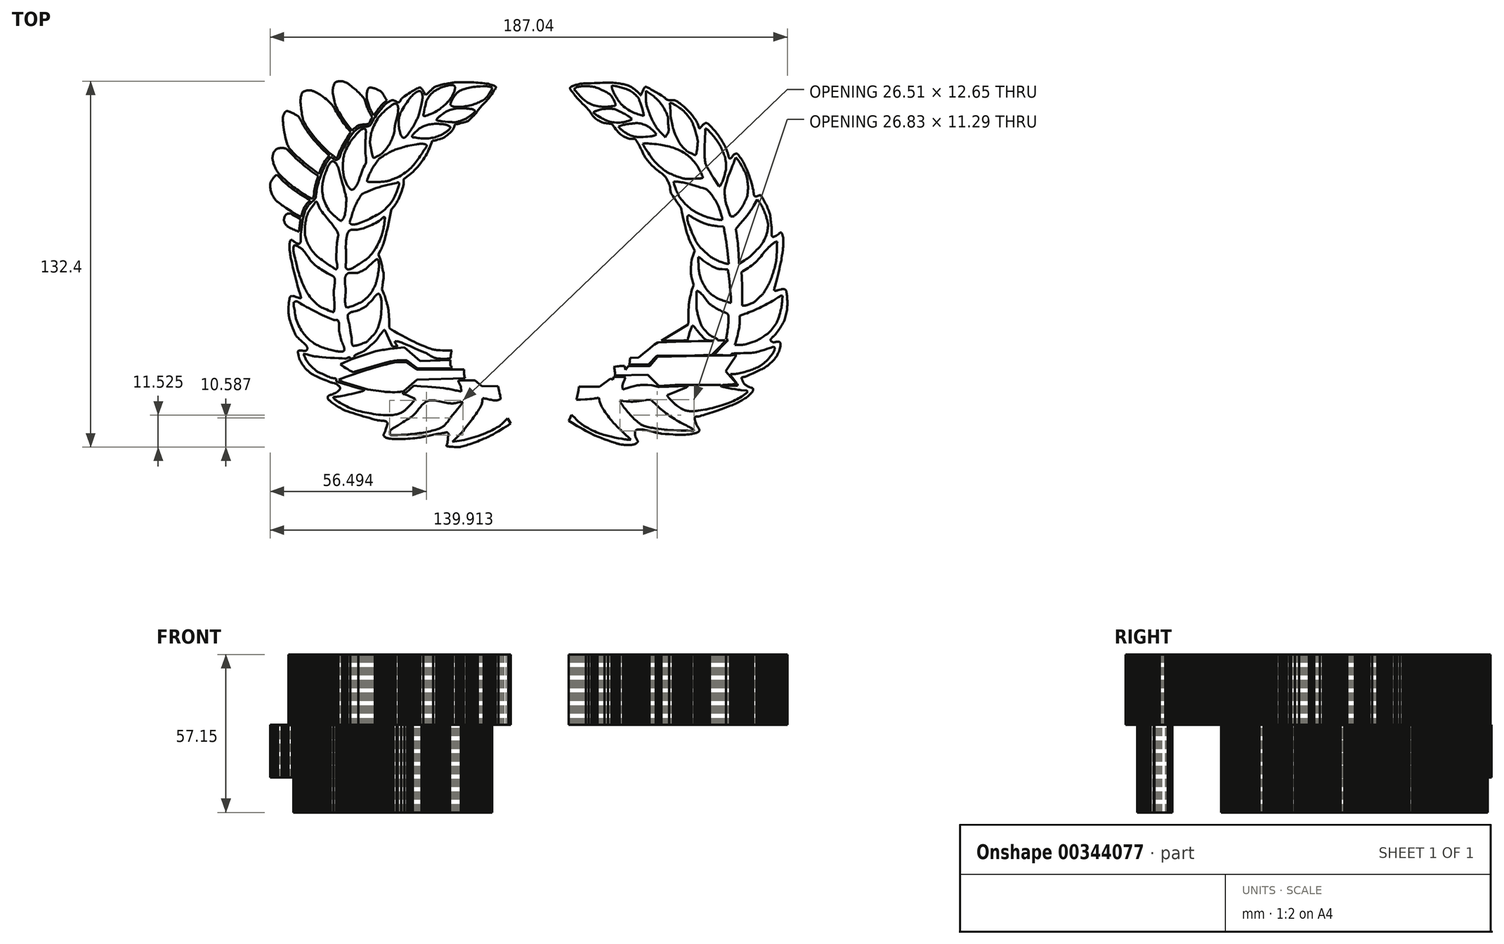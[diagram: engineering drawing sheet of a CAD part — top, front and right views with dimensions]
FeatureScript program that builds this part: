
annotation { "Feature Type Name" : "Feature", "Feature Type Description" : "" }
export const myFeature = defineFeature(function(context is Context, id is Id, definition is map)
    precondition{}
    {
        {
            var Q0;
            Q0=qCreatedBy(makeId("Top.planeOp"),FACE);
            var sketch = newSketch(context, id + "F0", { "sketchPlane" : qUnion([Q0])});
            skLineSegment(sketch, "E0", {"start": v(-39.54, -60.82) * mm, "end": v(-38.96, -60.7) * mm});
            skLineSegment(sketch, "E1", {"start": v(-38.96, -60.7) * mm, "end": v(-38.35, -60.57) * mm});
            skLineSegment(sketch, "E2", {"start": v(-38.35, -60.57) * mm, "end": v(-37.71, -60.43) * mm});
            skLineSegment(sketch, "E3", {"start": v(-37.71, -60.43) * mm, "end": v(-37.06, -60.27) * mm});
            skLineSegment(sketch, "E4", {"start": v(-37.06, -60.27) * mm, "end": v(-36.42, -60.1) * mm});
            skLineSegment(sketch, "E5", {"start": v(-36.42, -60.1) * mm, "end": v(-35.8, -59.92) * mm});
            skLineSegment(sketch, "E6", {"start": v(-35.8, -59.92) * mm, "end": v(-35.2, -59.73) * mm});
            skLineSegment(sketch, "E7", {"start": v(-35.2, -59.73) * mm, "end": v(-34.64, -59.53) * mm});
            skLineSegment(sketch, "E8", {"start": v(-34.64, -59.53) * mm, "end": v(-34.4, -59.43) * mm});
            skLineSegment(sketch, "E9", {"start": v(-34.4, -59.43) * mm, "end": v(-34.14, -59.32) * mm});
            skLineSegment(sketch, "E10", {"start": v(-34.14, -59.32) * mm, "end": v(-33.87, -59.18) * mm});
            skLineSegment(sketch, "E11", {"start": v(-33.87, -59.18) * mm, "end": v(-33.6, -59.04) * mm});
            skLineSegment(sketch, "E12", {"start": v(-33.6, -59.04) * mm, "end": v(-33.35, -58.88) * mm});
            skLineSegment(sketch, "E13", {"start": v(-33.35, -58.88) * mm, "end": v(-33.1, -58.72) * mm});
            skLineSegment(sketch, "E14", {"start": v(-33.1, -58.72) * mm, "end": v(-32.87, -58.56) * mm});
            skLineSegment(sketch, "E15", {"start": v(-32.87, -58.56) * mm, "end": v(-32.66, -58.39) * mm});
            skLineSegment(sketch, "E16", {"start": v(-32.66, -58.39) * mm, "end": v(-32.52, -58.26) * mm});
            skLineSegment(sketch, "E17", {"start": v(-32.52, -58.26) * mm, "end": v(-32.38, -58.12) * mm});
            skLineSegment(sketch, "E18", {"start": v(-32.38, -58.12) * mm, "end": v(-32.1, -57.81) * mm});
            skLineSegment(sketch, "E19", {"start": v(-32.1, -57.81) * mm, "end": v(-31.84, -57.48) * mm});
            skLineSegment(sketch, "E20", {"start": v(-31.84, -57.48) * mm, "end": v(-31.57, -57.13) * mm});
            skLineSegment(sketch, "E21", {"start": v(-31.57, -57.13) * mm, "end": v(-31.07, -56.41) * mm});
            skLineSegment(sketch, "E22", {"start": v(-31.07, -56.41) * mm, "end": v(-30.82, -56.08) * mm});
            skLineSegment(sketch, "E23", {"start": v(-30.82, -56.08) * mm, "end": v(-30.59, -55.76) * mm});
            skLineSegment(sketch, "E24", {"start": v(-30.59, -55.76) * mm, "end": v(-29.68, -54.62) * mm});
            skLineSegment(sketch, "E25", {"start": v(-29.68, -54.62) * mm, "end": v(-28.74, -53.46) * mm});
            skLineSegment(sketch, "E26", {"start": v(-28.74, -53.46) * mm, "end": v(-27.87, -52.4) * mm});
            skLineSegment(sketch, "E27", {"start": v(-27.87, -52.4) * mm, "end": v(-27.2, -51.6) * mm});
            skLineSegment(sketch, "E28", {"start": v(-27.2, -51.6) * mm, "end": v(-26.7, -50.98) * mm});
            skLineSegment(sketch, "E29", {"start": v(-26.7, -50.98) * mm, "end": v(-26.28, -50.46) * mm});
            skLineSegment(sketch, "E30", {"start": v(-26.28, -50.46) * mm, "end": v(-26, -50.09) * mm});
            skLineSegment(sketch, "E31", {"start": v(-26, -50.09) * mm, "end": v(-25.93, -49.97) * mm});
            skLineSegment(sketch, "E32", {"start": v(-25.93, -49.97) * mm, "end": v(-25.9, -49.91) * mm});
            skLineSegment(sketch, "E33", {"start": v(-25.9, -49.91) * mm, "end": v(-25.9, -49.9) * mm});
            skLineSegment(sketch, "E34", {"start": v(-25.9, -49.9) * mm, "end": v(-25.94, -49.9) * mm});
            skLineSegment(sketch, "E35", {"start": v(-25.94, -49.9) * mm, "end": v(-26.05, -49.88) * mm});
            skLineSegment(sketch, "E36", {"start": v(-26.05, -49.88) * mm, "end": v(-26.22, -49.89) * mm});
            skLineSegment(sketch, "E37", {"start": v(-26.22, -49.89) * mm, "end": v(-26.46, -49.9) * mm});
            skLineSegment(sketch, "E38", {"start": v(-26.46, -49.9) * mm, "end": v(-27.06, -49.98) * mm});
            skLineSegment(sketch, "E39", {"start": v(-27.06, -49.98) * mm, "end": v(-27.8, -50.09) * mm});
            skLineSegment(sketch, "E40", {"start": v(-27.8, -50.09) * mm, "end": v(-28.25, -50.17) * mm});
            skLineSegment(sketch, "E41", {"start": v(-28.25, -50.17) * mm, "end": v(-28.74, -50.27) * mm});
            skLineSegment(sketch, "E42", {"start": v(-28.74, -50.27) * mm, "end": v(-29.23, -50.36) * mm});
            skLineSegment(sketch, "E43", {"start": v(-29.23, -50.36) * mm, "end": v(-29.47, -50.38) * mm});
            skLineSegment(sketch, "E44", {"start": v(-29.47, -50.38) * mm, "end": v(-29.7, -50.4) * mm});
            skLineSegment(sketch, "E45", {"start": v(-29.7, -50.4) * mm, "end": v(-29.95, -50.4) * mm});
            skLineSegment(sketch, "E46", {"start": v(-29.95, -50.4) * mm, "end": v(-30.22, -50.4) * mm});
            skLineSegment(sketch, "E47", {"start": v(-30.22, -50.4) * mm, "end": v(-30.5, -50.38) * mm});
            skLineSegment(sketch, "E48", {"start": v(-30.5, -50.38) * mm, "end": v(-30.77, -50.35) * mm});
            skLineSegment(sketch, "E49", {"start": v(-30.77, -50.35) * mm, "end": v(-31.33, -50.28) * mm});
            skLineSegment(sketch, "E50", {"start": v(-31.33, -50.28) * mm, "end": v(-31.92, -50.18) * mm});
            skLineSegment(sketch, "E51", {"start": v(-31.92, -50.18) * mm, "end": v(-33.1, -49.92) * mm});
            skLineSegment(sketch, "E52", {"start": v(-33.1, -49.92) * mm, "end": v(-34.32, -49.66) * mm});
            skLineSegment(sketch, "E53", {"start": v(-34.32, -49.66) * mm, "end": v(-34.92, -49.53) * mm});
            skLineSegment(sketch, "E54", {"start": v(-34.92, -49.53) * mm, "end": v(-35.52, -49.43) * mm});
            skLineSegment(sketch, "E55", {"start": v(-35.52, -49.43) * mm, "end": v(-36.11, -49.35) * mm});
            skLineSegment(sketch, "E56", {"start": v(-36.11, -49.35) * mm, "end": v(-36.4, -49.32) * mm});
            skLineSegment(sketch, "E57", {"start": v(-36.4, -49.32) * mm, "end": v(-36.7, -49.3) * mm});
            skLineSegment(sketch, "E58", {"start": v(-36.7, -49.3) * mm, "end": v(-36.97, -49.3) * mm});
            skLineSegment(sketch, "E59", {"start": v(-36.97, -49.3) * mm, "end": v(-37.25, -49.3) * mm});
            skLineSegment(sketch, "E60", {"start": v(-37.25, -49.3) * mm, "end": v(-37.53, -49.3) * mm});
            skLineSegment(sketch, "E61", {"start": v(-37.53, -49.3) * mm, "end": v(-37.8, -49.33) * mm});
            skLineSegment(sketch, "E62", {"start": v(-37.8, -49.33) * mm, "end": v(-38.06, -49.36) * mm});
            skLineSegment(sketch, "E63", {"start": v(-38.06, -49.36) * mm, "end": v(-38.32, -49.42) * mm});
            skLineSegment(sketch, "E64", {"start": v(-38.32, -49.42) * mm, "end": v(-38.57, -49.48) * mm});
            skLineSegment(sketch, "E65", {"start": v(-38.57, -49.48) * mm, "end": v(-38.81, -49.56) * mm});
            skLineSegment(sketch, "E66", {"start": v(-38.81, -49.56) * mm, "end": v(-38.99, -49.64) * mm});
            skLineSegment(sketch, "E67", {"start": v(-38.99, -49.64) * mm, "end": v(-39.16, -49.72) * mm});
            skLineSegment(sketch, "E68", {"start": v(-39.16, -49.72) * mm, "end": v(-39.33, -49.81) * mm});
            skLineSegment(sketch, "E69", {"start": v(-39.33, -49.81) * mm, "end": v(-39.5, -49.91) * mm});
            skLineSegment(sketch, "E70", {"start": v(-39.5, -49.91) * mm, "end": v(-39.66, -50.03) * mm});
            skLineSegment(sketch, "E71", {"start": v(-39.66, -50.03) * mm, "end": v(-39.82, -50.15) * mm});
            skLineSegment(sketch, "E72", {"start": v(-39.82, -50.15) * mm, "end": v(-40.14, -50.4) * mm});
            skLineSegment(sketch, "E73", {"start": v(-40.14, -50.4) * mm, "end": v(-40.44, -50.7) * mm});
            skLineSegment(sketch, "E74", {"start": v(-40.44, -50.7) * mm, "end": v(-40.74, -51) * mm});
            skLineSegment(sketch, "E75", {"start": v(-40.74, -51) * mm, "end": v(-41.03, -51.34) * mm});
            skLineSegment(sketch, "E76", {"start": v(-41.03, -51.34) * mm, "end": v(-41.32, -51.68) * mm});
            skLineSegment(sketch, "E77", {"start": v(-41.32, -51.68) * mm, "end": v(-41.88, -52.38) * mm});
            skLineSegment(sketch, "E78", {"start": v(-41.88, -52.38) * mm, "end": v(-42.42, -53.08) * mm});
            skLineSegment(sketch, "E79", {"start": v(-42.42, -53.08) * mm, "end": v(-42.7, -53.41) * mm});
            skLineSegment(sketch, "E80", {"start": v(-42.7, -53.41) * mm, "end": v(-42.96, -53.73) * mm});
            skLineSegment(sketch, "E81", {"start": v(-42.96, -53.73) * mm, "end": v(-43.23, -54.03) * mm});
            skLineSegment(sketch, "E82", {"start": v(-43.23, -54.03) * mm, "end": v(-43.5, -54.3) * mm});
            skLineSegment(sketch, "E83", {"start": v(-43.5, -54.3) * mm, "end": v(-43.82, -54.6) * mm});
            skLineSegment(sketch, "E84", {"start": v(-43.82, -54.6) * mm, "end": v(-44.15, -54.87) * mm});
            skLineSegment(sketch, "E85", {"start": v(-44.15, -54.87) * mm, "end": v(-44.48, -55.13) * mm});
            skLineSegment(sketch, "E86", {"start": v(-44.48, -55.13) * mm, "end": v(-44.82, -55.39) * mm});
            skLineSegment(sketch, "E87", {"start": v(-44.82, -55.39) * mm, "end": v(-45.17, -55.63) * mm});
            skLineSegment(sketch, "E88", {"start": v(-45.17, -55.63) * mm, "end": v(-45.52, -55.87) * mm});
            skLineSegment(sketch, "E89", {"start": v(-45.52, -55.87) * mm, "end": v(-46.24, -56.34) * mm});
            skLineSegment(sketch, "E90", {"start": v(-46.24, -56.34) * mm, "end": v(-46.97, -56.78) * mm});
            skLineSegment(sketch, "E91", {"start": v(-46.97, -56.78) * mm, "end": v(-47.7, -57.23) * mm});
            skLineSegment(sketch, "E92", {"start": v(-47.7, -57.23) * mm, "end": v(-48.44, -57.68) * mm});
            skLineSegment(sketch, "E93", {"start": v(-48.44, -57.68) * mm, "end": v(-49.16, -58.15) * mm});
            skLineSegment(sketch, "E94", {"start": v(-49.16, -58.15) * mm, "end": v(-49.56, -58.4) * mm});
            skLineSegment(sketch, "E95", {"start": v(-49.56, -58.4) * mm, "end": v(-50.01, -58.68) * mm});
            skLineSegment(sketch, "E96", {"start": v(-50.01, -58.68) * mm, "end": v(-50.47, -58.95) * mm});
            skLineSegment(sketch, "E97", {"start": v(-50.47, -58.95) * mm, "end": v(-50.9, -59.18) * mm});
            skLineSegment(sketch, "E98", {"start": v(-50.9, -59.18) * mm, "end": v(-51.23, -59.37) * mm});
            skLineSegment(sketch, "E99", {"start": v(-51.23, -59.37) * mm, "end": v(-51.52, -59.55) * mm});
            skLineSegment(sketch, "E100", {"start": v(-51.52, -59.55) * mm, "end": v(-51.76, -59.74) * mm});
            skLineSegment(sketch, "E101", {"start": v(-51.76, -59.74) * mm, "end": v(-51.96, -59.9) * mm});
            skLineSegment(sketch, "E102", {"start": v(-51.96, -59.9) * mm, "end": v(-52.12, -60.07) * mm});
            skLineSegment(sketch, "E103", {"start": v(-52.12, -60.07) * mm, "end": v(-52.23, -60.2) * mm});
            skLineSegment(sketch, "E104", {"start": v(-52.23, -60.2) * mm, "end": v(-52.3, -60.3) * mm});
            skLineSegment(sketch, "E105", {"start": v(-52.3, -60.3) * mm, "end": v(-52.32, -60.35) * mm});
            skLineSegment(sketch, "E106", {"start": v(-52.32, -60.35) * mm, "end": v(-52.32, -60.38) * mm});
            skLineSegment(sketch, "E107", {"start": v(-52.32, -60.38) * mm, "end": v(-52.35, -60.64) * mm});
            skLineSegment(sketch, "E108", {"start": v(-52.35, -60.64) * mm, "end": v(-52.38, -60.82) * mm});
            skLineSegment(sketch, "E109", {"start": v(-52.38, -60.82) * mm, "end": v(-52.4, -61.03) * mm});
            skLineSegment(sketch, "E110", {"start": v(-52.4, -61.03) * mm, "end": v(-52.41, -61.23) * mm});
            skLineSegment(sketch, "E111", {"start": v(-52.41, -61.23) * mm, "end": v(-52.4, -61.42) * mm});
            skLineSegment(sketch, "E112", {"start": v(-52.4, -61.42) * mm, "end": v(-52.39, -61.5) * mm});
            skLineSegment(sketch, "E113", {"start": v(-52.39, -61.5) * mm, "end": v(-52.37, -61.58) * mm});
            skLineSegment(sketch, "E114", {"start": v(-52.37, -61.58) * mm, "end": v(-52.33, -61.64) * mm});
            skLineSegment(sketch, "E115", {"start": v(-52.33, -61.64) * mm, "end": v(-52.3, -61.7) * mm});
            skLineSegment(sketch, "E116", {"start": v(-52.3, -61.7) * mm, "end": v(-52.19, -61.77) * mm});
            skLineSegment(sketch, "E117", {"start": v(-52.19, -61.77) * mm, "end": v(-52.07, -61.83) * mm});
            skLineSegment(sketch, "E118", {"start": v(-52.07, -61.83) * mm, "end": v(-51.93, -61.87) * mm});
            skLineSegment(sketch, "E119", {"start": v(-51.93, -61.87) * mm, "end": v(-51.78, -61.9) * mm});
            skLineSegment(sketch, "E120", {"start": v(-51.78, -61.9) * mm, "end": v(-51.62, -61.92) * mm});
            skLineSegment(sketch, "E121", {"start": v(-51.62, -61.92) * mm, "end": v(-51.45, -61.94) * mm});
            skLineSegment(sketch, "E122", {"start": v(-51.45, -61.94) * mm, "end": v(-51.09, -61.94) * mm});
            skLineSegment(sketch, "E123", {"start": v(-51.09, -61.94) * mm, "end": v(-50.31, -61.88) * mm});
            skLineSegment(sketch, "E124", {"start": v(-50.31, -61.88) * mm, "end": v(-49.93, -61.85) * mm});
            skLineSegment(sketch, "E125", {"start": v(-49.93, -61.85) * mm, "end": v(-49.57, -61.84) * mm});
            skLineSegment(sketch, "E126", {"start": v(-49.57, -61.84) * mm, "end": v(-48.31, -61.8) * mm});
            skLineSegment(sketch, "E127", {"start": v(-48.31, -61.8) * mm, "end": v(-47.13, -61.77) * mm});
            skLineSegment(sketch, "E128", {"start": v(-47.13, -61.77) * mm, "end": v(-46.16, -61.71) * mm});
            skLineSegment(sketch, "E129", {"start": v(-46.16, -61.71) * mm, "end": v(-45.8, -61.68) * mm});
            skLineSegment(sketch, "E130", {"start": v(-45.8, -61.68) * mm, "end": v(-45.53, -61.65) * mm});
            skLineSegment(sketch, "E131", {"start": v(-45.53, -61.65) * mm, "end": v(-44.83, -61.55) * mm});
            skLineSegment(sketch, "E132", {"start": v(-44.83, -61.55) * mm, "end": v(-44.1, -61.45) * mm});
            skLineSegment(sketch, "E133", {"start": v(-44.1, -61.45) * mm, "end": v(-42.53, -61.26) * mm});
            skLineSegment(sketch, "E134", {"start": v(-42.53, -61.26) * mm, "end": v(-41.75, -61.16) * mm});
            skLineSegment(sketch, "E135", {"start": v(-41.75, -61.16) * mm, "end": v(-40.97, -61.05) * mm});
            skLineSegment(sketch, "E136", {"start": v(-40.97, -61.05) * mm, "end": v(-40.23, -60.94) * mm});
            skLineSegment(sketch, "E137", {"start": v(-40.23, -60.94) * mm, "end": v(-39.54, -60.82) * mm});
            skLineSegment(sketch, "E138", {"start": v(54.2, -58.06) * mm, "end": v(53.44, -57.67) * mm});
            skLineSegment(sketch, "E139", {"start": v(53.44, -57.67) * mm, "end": v(52.71, -57.28) * mm});
            skLineSegment(sketch, "E140", {"start": v(52.71, -57.28) * mm, "end": v(52, -56.89) * mm});
            skLineSegment(sketch, "E141", {"start": v(52, -56.89) * mm, "end": v(51.31, -56.49) * mm});
            skLineSegment(sketch, "E142", {"start": v(51.31, -56.49) * mm, "end": v(50.64, -56.09) * mm});
            skLineSegment(sketch, "E143", {"start": v(50.64, -56.09) * mm, "end": v(49.99, -55.68) * mm});
            skLineSegment(sketch, "E144", {"start": v(49.99, -55.68) * mm, "end": v(49.35, -55.27) * mm});
            skLineSegment(sketch, "E145", {"start": v(49.35, -55.27) * mm, "end": v(48.73, -54.85) * mm});
            skLineSegment(sketch, "E146", {"start": v(48.73, -54.85) * mm, "end": v(48.13, -54.42) * mm});
            skLineSegment(sketch, "E147", {"start": v(48.13, -54.42) * mm, "end": v(47.54, -54) * mm});
            skLineSegment(sketch, "E148", {"start": v(47.54, -54) * mm, "end": v(46.96, -53.55) * mm});
            skLineSegment(sketch, "E149", {"start": v(46.96, -53.55) * mm, "end": v(46.4, -53.1) * mm});
            skLineSegment(sketch, "E150", {"start": v(46.4, -53.1) * mm, "end": v(45.84, -52.64) * mm});
            skLineSegment(sketch, "E151", {"start": v(45.84, -52.64) * mm, "end": v(45.3, -52.18) * mm});
            skLineSegment(sketch, "E152", {"start": v(45.3, -52.18) * mm, "end": v(44.77, -51.7) * mm});
            skLineSegment(sketch, "E153", {"start": v(44.77, -51.7) * mm, "end": v(44.25, -51.2) * mm});
            skLineSegment(sketch, "E154", {"start": v(44.25, -51.2) * mm, "end": v(41.97, -49.03) * mm});
            skLineSegment(sketch, "E155", {"start": v(41.97, -49.03) * mm, "end": v(40.39, -49.23) * mm});
            skLineSegment(sketch, "E156", {"start": v(40.39, -49.23) * mm, "end": v(38.69, -49.45) * mm});
            skLineSegment(sketch, "E157", {"start": v(38.69, -49.45) * mm, "end": v(37.83, -49.55) * mm});
            skLineSegment(sketch, "E158", {"start": v(37.83, -49.55) * mm, "end": v(36.98, -49.64) * mm});
            skLineSegment(sketch, "E159", {"start": v(36.98, -49.64) * mm, "end": v(36.17, -49.7) * mm});
            skLineSegment(sketch, "E160", {"start": v(36.17, -49.7) * mm, "end": v(35.77, -49.73) * mm});
            skLineSegment(sketch, "E161", {"start": v(35.77, -49.73) * mm, "end": v(35.4, -49.75) * mm});
            skLineSegment(sketch, "E162", {"start": v(35.4, -49.75) * mm, "end": v(34.86, -49.75) * mm});
            skLineSegment(sketch, "E163", {"start": v(34.86, -49.75) * mm, "end": v(34.3, -49.73) * mm});
            skLineSegment(sketch, "E164", {"start": v(34.3, -49.73) * mm, "end": v(33.72, -49.7) * mm});
            skLineSegment(sketch, "E165", {"start": v(33.72, -49.7) * mm, "end": v(33.12, -49.66) * mm});
            skLineSegment(sketch, "E166", {"start": v(33.12, -49.66) * mm, "end": v(31.94, -49.57) * mm});
            skLineSegment(sketch, "E167", {"start": v(31.94, -49.57) * mm, "end": v(30.85, -49.49) * mm});
            skLineSegment(sketch, "E168", {"start": v(30.85, -49.49) * mm, "end": v(30.93, -49.72) * mm});
            skLineSegment(sketch, "E169", {"start": v(30.93, -49.72) * mm, "end": v(30.97, -49.84) * mm});
            skLineSegment(sketch, "E170", {"start": v(30.97, -49.84) * mm, "end": v(31.02, -49.95) * mm});
            skLineSegment(sketch, "E171", {"start": v(31.02, -49.95) * mm, "end": v(31.33, -50.45) * mm});
            skLineSegment(sketch, "E172", {"start": v(31.33, -50.45) * mm, "end": v(31.67, -50.95) * mm});
            skLineSegment(sketch, "E173", {"start": v(31.67, -50.95) * mm, "end": v(32.03, -51.47) * mm});
            skLineSegment(sketch, "E174", {"start": v(32.03, -51.47) * mm, "end": v(32.42, -51.99) * mm});
            skLineSegment(sketch, "E175", {"start": v(32.42, -51.99) * mm, "end": v(32.82, -52.5) * mm});
            skLineSegment(sketch, "E176", {"start": v(32.82, -52.5) * mm, "end": v(33.24, -53.03) * mm});
            skLineSegment(sketch, "E177", {"start": v(33.24, -53.03) * mm, "end": v(33.67, -53.54) * mm});
            skLineSegment(sketch, "E178", {"start": v(33.67, -53.54) * mm, "end": v(34.12, -54.05) * mm});
            skLineSegment(sketch, "E179", {"start": v(34.12, -54.05) * mm, "end": v(34.57, -54.56) * mm});
            skLineSegment(sketch, "E180", {"start": v(34.57, -54.56) * mm, "end": v(35.03, -55.05) * mm});
            skLineSegment(sketch, "E181", {"start": v(35.03, -55.05) * mm, "end": v(35.5, -55.52) * mm});
            skLineSegment(sketch, "E182", {"start": v(35.5, -55.52) * mm, "end": v(35.97, -55.98) * mm});
            skLineSegment(sketch, "E183", {"start": v(35.97, -55.98) * mm, "end": v(36.44, -56.42) * mm});
            skLineSegment(sketch, "E184", {"start": v(36.44, -56.42) * mm, "end": v(36.91, -56.84) * mm});
            skLineSegment(sketch, "E185", {"start": v(36.91, -56.84) * mm, "end": v(37.38, -57.24) * mm});
            skLineSegment(sketch, "E186", {"start": v(37.38, -57.24) * mm, "end": v(37.84, -57.6) * mm});
            skLineSegment(sketch, "E187", {"start": v(37.84, -57.6) * mm, "end": v(38.03, -57.74) * mm});
            skLineSegment(sketch, "E188", {"start": v(38.03, -57.74) * mm, "end": v(38.23, -57.88) * mm});
            skLineSegment(sketch, "E189", {"start": v(38.23, -57.88) * mm, "end": v(38.45, -58) * mm});
            skLineSegment(sketch, "E190", {"start": v(38.45, -58) * mm, "end": v(38.69, -58.13) * mm});
            skLineSegment(sketch, "E191", {"start": v(38.69, -58.13) * mm, "end": v(38.92, -58.24) * mm});
            skLineSegment(sketch, "E192", {"start": v(38.92, -58.24) * mm, "end": v(39.16, -58.35) * mm});
            skLineSegment(sketch, "E193", {"start": v(39.16, -58.35) * mm, "end": v(39.39, -58.44) * mm});
            skLineSegment(sketch, "E194", {"start": v(39.39, -58.44) * mm, "end": v(39.6, -58.52) * mm});
            skLineSegment(sketch, "E195", {"start": v(39.6, -58.52) * mm, "end": v(40.06, -58.67) * mm});
            skLineSegment(sketch, "E196", {"start": v(40.06, -58.67) * mm, "end": v(40.54, -58.8) * mm});
            skLineSegment(sketch, "E197", {"start": v(40.54, -58.8) * mm, "end": v(41.04, -58.93) * mm});
            skLineSegment(sketch, "E198", {"start": v(41.04, -58.93) * mm, "end": v(41.55, -59.05) * mm});
            skLineSegment(sketch, "E199", {"start": v(41.55, -59.05) * mm, "end": v(42.07, -59.16) * mm});
            skLineSegment(sketch, "E200", {"start": v(42.07, -59.16) * mm, "end": v(42.6, -59.27) * mm});
            skLineSegment(sketch, "E201", {"start": v(42.6, -59.27) * mm, "end": v(43.68, -59.45) * mm});
            skLineSegment(sketch, "E202", {"start": v(43.68, -59.45) * mm, "end": v(44.77, -59.62) * mm});
            skLineSegment(sketch, "E203", {"start": v(44.77, -59.62) * mm, "end": v(45.84, -59.75) * mm});
            skLineSegment(sketch, "E204", {"start": v(45.84, -59.75) * mm, "end": v(47.85, -59.98) * mm});
            skLineSegment(sketch, "E205", {"start": v(47.85, -59.98) * mm, "end": v(48.41, -60.03) * mm});
            skLineSegment(sketch, "E206", {"start": v(48.41, -60.03) * mm, "end": v(49, -60.08) * mm});
            skLineSegment(sketch, "E207", {"start": v(49, -60.08) * mm, "end": v(50.2, -60.15) * mm});
            skLineSegment(sketch, "E208", {"start": v(50.2, -60.15) * mm, "end": v(51.47, -60.2) * mm});
            skLineSegment(sketch, "E209", {"start": v(51.47, -60.2) * mm, "end": v(52.76, -60.23) * mm});
            skLineSegment(sketch, "E210", {"start": v(52.76, -60.23) * mm, "end": v(55.3, -60.27) * mm});
            skLineSegment(sketch, "E211", {"start": v(55.3, -60.27) * mm, "end": v(56.53, -60.29) * mm});
            skLineSegment(sketch, "E212", {"start": v(56.53, -60.29) * mm, "end": v(57.68, -60.32) * mm});
            skLineSegment(sketch, "E213", {"start": v(57.68, -60.32) * mm, "end": v(57.46, -59.97) * mm});
            skLineSegment(sketch, "E214", {"start": v(57.46, -59.97) * mm, "end": v(57.42, -59.92) * mm});
            skLineSegment(sketch, "E215", {"start": v(57.42, -59.92) * mm, "end": v(57.35, -59.86) * mm});
            skLineSegment(sketch, "E216", {"start": v(57.35, -59.86) * mm, "end": v(57.13, -59.7) * mm});
            skLineSegment(sketch, "E217", {"start": v(57.13, -59.7) * mm, "end": v(56.81, -59.5) * mm});
            skLineSegment(sketch, "E218", {"start": v(56.81, -59.5) * mm, "end": v(56.4, -59.26) * mm});
            skLineSegment(sketch, "E219", {"start": v(56.4, -59.26) * mm, "end": v(55.93, -58.99) * mm});
            skLineSegment(sketch, "E220", {"start": v(55.93, -58.99) * mm, "end": v(55.4, -58.7) * mm});
            skLineSegment(sketch, "E221", {"start": v(55.4, -58.7) * mm, "end": v(54.81, -58.38) * mm});
            skLineSegment(sketch, "E222", {"start": v(54.81, -58.38) * mm, "end": v(54.2, -58.06) * mm});
            skLineSegment(sketch, "E223", {"start": v(1.8, -52.65) * mm, "end": v(2.73, -52.65) * mm});
            skLineSegment(sketch, "E224", {"start": v(2.73, -52.65) * mm, "end": v(3.04, -52.23) * mm});
            skLineSegment(sketch, "E225", {"start": v(3.04, -52.23) * mm, "end": v(3.11, -52.12) * mm});
            skLineSegment(sketch, "E226", {"start": v(3.11, -52.12) * mm, "end": v(3.2, -51.94) * mm});
            skLineSegment(sketch, "E227", {"start": v(3.2, -51.94) * mm, "end": v(3.46, -51.43) * mm});
            skLineSegment(sketch, "E228", {"start": v(3.46, -51.43) * mm, "end": v(3.77, -50.72) * mm});
            skLineSegment(sketch, "E229", {"start": v(3.77, -50.72) * mm, "end": v(4.14, -49.85) * mm});
            skLineSegment(sketch, "E230", {"start": v(4.14, -49.85) * mm, "end": v(4.55, -48.84) * mm});
            skLineSegment(sketch, "E231", {"start": v(4.55, -48.84) * mm, "end": v(5, -47.72) * mm});
            skLineSegment(sketch, "E232", {"start": v(5, -47.72) * mm, "end": v(5.46, -46.51) * mm});
            skLineSegment(sketch, "E233", {"start": v(5.46, -46.51) * mm, "end": v(5.94, -45.24) * mm});
            skLineSegment(sketch, "E234", {"start": v(5.94, -45.24) * mm, "end": v(6.16, -44.62) * mm});
            skLineSegment(sketch, "E235", {"start": v(6.16, -44.62) * mm, "end": v(6.4, -43.96) * mm});
            skLineSegment(sketch, "E236", {"start": v(6.4, -43.96) * mm, "end": v(6.86, -42.53) * mm});
            skLineSegment(sketch, "E237", {"start": v(6.86, -42.53) * mm, "end": v(7.34, -41) * mm});
            skLineSegment(sketch, "E238", {"start": v(7.34, -41) * mm, "end": v(7.8, -39.43) * mm});
            skLineSegment(sketch, "E239", {"start": v(7.8, -39.43) * mm, "end": v(8.23, -37.85) * mm});
            skLineSegment(sketch, "E240", {"start": v(8.23, -37.85) * mm, "end": v(8.63, -36.31) * mm});
            skLineSegment(sketch, "E241", {"start": v(8.63, -36.31) * mm, "end": v(8.98, -34.86) * mm});
            skLineSegment(sketch, "E242", {"start": v(8.98, -34.86) * mm, "end": v(9.13, -34.19) * mm});
            skLineSegment(sketch, "E243", {"start": v(9.13, -34.19) * mm, "end": v(9.26, -33.56) * mm});
            skLineSegment(sketch, "E244", {"start": v(9.26, -33.56) * mm, "end": v(9.81, -30.8) * mm});
            skLineSegment(sketch, "E245", {"start": v(9.81, -30.8) * mm, "end": v(9.13, -29.31) * mm});
            skLineSegment(sketch, "E246", {"start": v(9.13, -29.31) * mm, "end": v(6.15, -28.56) * mm});
            skLineSegment(sketch, "E247", {"start": v(6.15, -28.56) * mm, "end": v(-2.3, -28.59) * mm});
            skLineSegment(sketch, "E248", {"start": v(-2.3, -28.59) * mm, "end": v(-3.72, -28.86) * mm});
            skLineSegment(sketch, "E249", {"start": v(-3.72, -28.86) * mm, "end": v(-4.29, -28.98) * mm});
            skLineSegment(sketch, "E250", {"start": v(-4.29, -28.98) * mm, "end": v(-4.78, -29.11) * mm});
            skLineSegment(sketch, "E251", {"start": v(-4.78, -29.11) * mm, "end": v(-4.98, -29.18) * mm});
            skLineSegment(sketch, "E252", {"start": v(-4.98, -29.18) * mm, "end": v(-5.15, -29.24) * mm});
            skLineSegment(sketch, "E253", {"start": v(-5.15, -29.24) * mm, "end": v(-5.27, -29.3) * mm});
            skLineSegment(sketch, "E254", {"start": v(-5.27, -29.3) * mm, "end": v(-5.34, -29.34) * mm});
            skLineSegment(sketch, "E255", {"start": v(-5.34, -29.34) * mm, "end": v(-5.54, -29.54) * mm});
            skLineSegment(sketch, "E256", {"start": v(-5.54, -29.54) * mm, "end": v(-5.46, -36.42) * mm});
            skLineSegment(sketch, "E257", {"start": v(-5.46, -36.42) * mm, "end": v(-5.12, -38.56) * mm});
            skLineSegment(sketch, "E258", {"start": v(-5.12, -38.56) * mm, "end": v(-4.98, -39.33) * mm});
            skLineSegment(sketch, "E259", {"start": v(-4.98, -39.33) * mm, "end": v(-4.81, -40.13) * mm});
            skLineSegment(sketch, "E260", {"start": v(-4.81, -40.13) * mm, "end": v(-4.61, -40.95) * mm});
            skLineSegment(sketch, "E261", {"start": v(-4.61, -40.95) * mm, "end": v(-4.38, -41.78) * mm});
            skLineSegment(sketch, "E262", {"start": v(-4.38, -41.78) * mm, "end": v(-4.12, -42.63) * mm});
            skLineSegment(sketch, "E263", {"start": v(-4.12, -42.63) * mm, "end": v(-3.84, -43.48) * mm});
            skLineSegment(sketch, "E264", {"start": v(-3.84, -43.48) * mm, "end": v(-3.54, -44.33) * mm});
            skLineSegment(sketch, "E265", {"start": v(-3.54, -44.33) * mm, "end": v(-3.21, -45.18) * mm});
            skLineSegment(sketch, "E266", {"start": v(-3.21, -45.18) * mm, "end": v(-2.87, -46.03) * mm});
            skLineSegment(sketch, "E267", {"start": v(-2.87, -46.03) * mm, "end": v(-2.5, -46.85) * mm});
            skLineSegment(sketch, "E268", {"start": v(-2.5, -46.85) * mm, "end": v(-2.13, -47.66) * mm});
            skLineSegment(sketch, "E269", {"start": v(-2.13, -47.66) * mm, "end": v(-1.74, -48.45) * mm});
            skLineSegment(sketch, "E270", {"start": v(-1.74, -48.45) * mm, "end": v(-1.34, -49.2) * mm});
            skLineSegment(sketch, "E271", {"start": v(-1.34, -49.2) * mm, "end": v(-0.94, -49.92) * mm});
            skLineSegment(sketch, "E272", {"start": v(-0.94, -49.92) * mm, "end": v(-0.52, -50.6) * mm});
            skLineSegment(sketch, "E273", {"start": v(-0.52, -50.6) * mm, "end": v(-0.1, -51.24) * mm});
            skLineSegment(sketch, "E274", {"start": v(-0.1, -51.24) * mm, "end": v(0.86, -52.65) * mm});
            skLineSegment(sketch, "E275", {"start": v(0.86, -52.65) * mm, "end": v(1.8, -52.65) * mm});
            skLineSegment(sketch, "E276", {"start": v(-51.43, -46.34) * mm, "end": v(-51, -46.34) * mm});
            skLineSegment(sketch, "E277", {"start": v(-51, -46.34) * mm, "end": v(-50.56, -46.34) * mm});
            skLineSegment(sketch, "E278", {"start": v(-50.56, -46.34) * mm, "end": v(-49.7, -46.3) * mm});
            skLineSegment(sketch, "E279", {"start": v(-49.7, -46.3) * mm, "end": v(-49.3, -46.28) * mm});
            skLineSegment(sketch, "E280", {"start": v(-49.3, -46.28) * mm, "end": v(-48.94, -46.25) * mm});
            skLineSegment(sketch, "E281", {"start": v(-48.94, -46.25) * mm, "end": v(-48.63, -46.21) * mm});
            skLineSegment(sketch, "E282", {"start": v(-48.63, -46.21) * mm, "end": v(-48.38, -46.17) * mm});
            skLineSegment(sketch, "E283", {"start": v(-48.38, -46.17) * mm, "end": v(-47.35, -45.97) * mm});
            skLineSegment(sketch, "E284", {"start": v(-47.35, -45.97) * mm, "end": v(-42.5, -41.83) * mm});
            skLineSegment(sketch, "E285", {"start": v(-42.5, -41.83) * mm, "end": v(-25.18, -41.34) * mm});
            skLineSegment(sketch, "E286", {"start": v(-25.18, -41.34) * mm, "end": v(-25.37, -40.64) * mm});
            skLineSegment(sketch, "E287", {"start": v(-25.37, -40.64) * mm, "end": v(-25.45, -40.3) * mm});
            skLineSegment(sketch, "E288", {"start": v(-25.45, -40.3) * mm, "end": v(-25.5, -39.88) * mm});
            skLineSegment(sketch, "E289", {"start": v(-25.5, -39.88) * mm, "end": v(-25.55, -39.44) * mm});
            skLineSegment(sketch, "E290", {"start": v(-25.55, -39.44) * mm, "end": v(-25.56, -39.03) * mm});
            skLineSegment(sketch, "E291", {"start": v(-25.56, -39.03) * mm, "end": v(-25.57, -38.1) * mm});
            skLineSegment(sketch, "E292", {"start": v(-25.57, -38.1) * mm, "end": v(-42.72, -38.17) * mm});
            skLineSegment(sketch, "E293", {"start": v(-42.72, -38.17) * mm, "end": v(-46.46, -35.49) * mm});
            skLineSegment(sketch, "E294", {"start": v(-46.46, -35.49) * mm, "end": v(-50.3, -35.49) * mm});
            skLineSegment(sketch, "E295", {"start": v(-50.3, -35.49) * mm, "end": v(-53.04, -36.13) * mm});
            skLineSegment(sketch, "E296", {"start": v(-53.04, -36.13) * mm, "end": v(-53.7, -36.29) * mm});
            skLineSegment(sketch, "E297", {"start": v(-53.7, -36.29) * mm, "end": v(-54.5, -36.5) * mm});
            skLineSegment(sketch, "E298", {"start": v(-54.5, -36.5) * mm, "end": v(-56.43, -37.03) * mm});
            skLineSegment(sketch, "E299", {"start": v(-56.43, -37.03) * mm, "end": v(-58.59, -37.66) * mm});
            skLineSegment(sketch, "E300", {"start": v(-58.59, -37.66) * mm, "end": v(-59.67, -37.98) * mm});
            skLineSegment(sketch, "E301", {"start": v(-59.67, -37.98) * mm, "end": v(-60.72, -38.3) * mm});
            skLineSegment(sketch, "E302", {"start": v(-60.72, -38.3) * mm, "end": v(-68.27, -40.84) * mm});
            skLineSegment(sketch, "E303", {"start": v(-68.27, -40.84) * mm, "end": v(-70.88, -41.85) * mm});
            skLineSegment(sketch, "E304", {"start": v(-70.88, -41.85) * mm, "end": v(-69.3, -42.68) * mm});
            skLineSegment(sketch, "E305", {"start": v(-69.3, -42.68) * mm, "end": v(-60.38, -45.3) * mm});
            skLineSegment(sketch, "E306", {"start": v(-60.38, -45.3) * mm, "end": v(-54.44, -46.1) * mm});
            skLineSegment(sketch, "E307", {"start": v(-54.44, -46.1) * mm, "end": v(-53.95, -46.2) * mm});
            skLineSegment(sketch, "E308", {"start": v(-53.95, -46.2) * mm, "end": v(-53.8, -46.22) * mm});
            skLineSegment(sketch, "E309", {"start": v(-53.8, -46.22) * mm, "end": v(-53.6, -46.24) * mm});
            skLineSegment(sketch, "E310", {"start": v(-53.6, -46.24) * mm, "end": v(-53, -46.28) * mm});
            skLineSegment(sketch, "E311", {"start": v(-53, -46.28) * mm, "end": v(-52.25, -46.32) * mm});
            skLineSegment(sketch, "E312", {"start": v(-52.25, -46.32) * mm, "end": v(-51.43, -46.34) * mm});
            skLineSegment(sketch, "E313", {"start": v(73.42, -43.73) * mm, "end": v(73.42, -43.38) * mm});
            skLineSegment(sketch, "E314", {"start": v(73.42, -43.38) * mm, "end": v(68.07, -43.7) * mm});
            skLineSegment(sketch, "E315", {"start": v(68.07, -43.7) * mm, "end": v(67.7, -44.07) * mm});
            skLineSegment(sketch, "E316", {"start": v(67.7, -44.07) * mm, "end": v(72.93, -43.99) * mm});
            skLineSegment(sketch, "E317", {"start": v(72.93, -43.99) * mm, "end": v(73.18, -44.03) * mm});
            skLineSegment(sketch, "E318", {"start": v(73.18, -44.03) * mm, "end": v(73.23, -44.03) * mm});
            skLineSegment(sketch, "E319", {"start": v(73.23, -44.03) * mm, "end": v(73.27, -44.02) * mm});
            skLineSegment(sketch, "E320", {"start": v(73.27, -44.02) * mm, "end": v(73.31, -44) * mm});
            skLineSegment(sketch, "E321", {"start": v(73.31, -44) * mm, "end": v(73.35, -43.95) * mm});
            skLineSegment(sketch, "E322", {"start": v(73.35, -43.95) * mm, "end": v(73.38, -43.9) * mm});
            skLineSegment(sketch, "E323", {"start": v(73.38, -43.9) * mm, "end": v(73.4, -43.85) * mm});
            skLineSegment(sketch, "E324", {"start": v(73.4, -43.85) * mm, "end": v(73.42, -43.8) * mm});
            skLineSegment(sketch, "E325", {"start": v(73.42, -43.8) * mm, "end": v(73.42, -43.73) * mm});
            skLineSegment(sketch, "E326", {"start": v(70.78, -40) * mm, "end": v(70.78, -39.78) * mm});
            skLineSegment(sketch, "E327", {"start": v(70.78, -39.78) * mm, "end": v(71.89, -39.78) * mm});
            skLineSegment(sketch, "E328", {"start": v(71.89, -39.78) * mm, "end": v(72.2, -39.76) * mm});
            skLineSegment(sketch, "E329", {"start": v(72.2, -39.76) * mm, "end": v(72.57, -39.73) * mm});
            skLineSegment(sketch, "E330", {"start": v(72.57, -39.73) * mm, "end": v(72.98, -39.67) * mm});
            skLineSegment(sketch, "E331", {"start": v(72.98, -39.67) * mm, "end": v(73.43, -39.6) * mm});
            skLineSegment(sketch, "E332", {"start": v(73.43, -39.6) * mm, "end": v(73.92, -39.5) * mm});
            skLineSegment(sketch, "E333", {"start": v(73.92, -39.5) * mm, "end": v(74.44, -39.38) * mm});
            skLineSegment(sketch, "E334", {"start": v(74.44, -39.38) * mm, "end": v(74.98, -39.25) * mm});
            skLineSegment(sketch, "E335", {"start": v(74.98, -39.25) * mm, "end": v(75.53, -39.11) * mm});
            skLineSegment(sketch, "E336", {"start": v(75.53, -39.11) * mm, "end": v(76.1, -38.96) * mm});
            skLineSegment(sketch, "E337", {"start": v(76.1, -38.96) * mm, "end": v(76.66, -38.8) * mm});
            skLineSegment(sketch, "E338", {"start": v(76.66, -38.8) * mm, "end": v(77.21, -38.63) * mm});
            skLineSegment(sketch, "E339", {"start": v(77.21, -38.63) * mm, "end": v(77.76, -38.45) * mm});
            skLineSegment(sketch, "E340", {"start": v(77.76, -38.45) * mm, "end": v(78.29, -38.27) * mm});
            skLineSegment(sketch, "E341", {"start": v(78.29, -38.27) * mm, "end": v(78.79, -38.09) * mm});
            skLineSegment(sketch, "E342", {"start": v(78.79, -38.09) * mm, "end": v(79.26, -37.9) * mm});
            skLineSegment(sketch, "E343", {"start": v(79.26, -37.9) * mm, "end": v(79.7, -37.72) * mm});
            skLineSegment(sketch, "E344", {"start": v(79.7, -37.72) * mm, "end": v(80.14, -37.53) * mm});
            skLineSegment(sketch, "E345", {"start": v(80.14, -37.53) * mm, "end": v(80.62, -37.34) * mm});
            skLineSegment(sketch, "E346", {"start": v(80.62, -37.34) * mm, "end": v(80.86, -37.24) * mm});
            skLineSegment(sketch, "E347", {"start": v(80.86, -37.24) * mm, "end": v(81.1, -37.14) * mm});
            skLineSegment(sketch, "E348", {"start": v(81.1, -37.14) * mm, "end": v(81.3, -37.02) * mm});
            skLineSegment(sketch, "E349", {"start": v(81.3, -37.02) * mm, "end": v(81.5, -36.9) * mm});
            skLineSegment(sketch, "E350", {"start": v(81.5, -36.9) * mm, "end": v(81.95, -36.6) * mm});
            skLineSegment(sketch, "E351", {"start": v(81.95, -36.6) * mm, "end": v(82.4, -36.27) * mm});
            skLineSegment(sketch, "E352", {"start": v(82.4, -36.27) * mm, "end": v(82.86, -35.9) * mm});
            skLineSegment(sketch, "E353", {"start": v(82.86, -35.9) * mm, "end": v(83.3, -35.5) * mm});
            skLineSegment(sketch, "E354", {"start": v(83.3, -35.5) * mm, "end": v(83.75, -35.1) * mm});
            skLineSegment(sketch, "E355", {"start": v(83.75, -35.1) * mm, "end": v(84.16, -34.69) * mm});
            skLineSegment(sketch, "E356", {"start": v(84.16, -34.69) * mm, "end": v(84.54, -34.27) * mm});
            skLineSegment(sketch, "E357", {"start": v(84.54, -34.27) * mm, "end": v(84.72, -34.06) * mm});
            skLineSegment(sketch, "E358", {"start": v(84.72, -34.06) * mm, "end": v(84.88, -33.86) * mm});
            skLineSegment(sketch, "E359", {"start": v(84.88, -33.86) * mm, "end": v(85.18, -33.48) * mm});
            skLineSegment(sketch, "E360", {"start": v(85.18, -33.48) * mm, "end": v(85.52, -33.06) * mm});
            skLineSegment(sketch, "E361", {"start": v(85.52, -33.06) * mm, "end": v(85.86, -32.61) * mm});
            skLineSegment(sketch, "E362", {"start": v(85.86, -32.61) * mm, "end": v(86.02, -32.38) * mm});
            skLineSegment(sketch, "E363", {"start": v(86.02, -32.38) * mm, "end": v(86.18, -32.14) * mm});
            skLineSegment(sketch, "E364", {"start": v(86.18, -32.14) * mm, "end": v(86.32, -31.9) * mm});
            skLineSegment(sketch, "E365", {"start": v(86.32, -31.9) * mm, "end": v(86.45, -31.67) * mm});
            skLineSegment(sketch, "E366", {"start": v(86.45, -31.67) * mm, "end": v(86.57, -31.43) * mm});
            skLineSegment(sketch, "E367", {"start": v(86.57, -31.43) * mm, "end": v(86.66, -31.19) * mm});
            skLineSegment(sketch, "E368", {"start": v(86.66, -31.19) * mm, "end": v(86.73, -30.95) * mm});
            skLineSegment(sketch, "E369", {"start": v(86.73, -30.95) * mm, "end": v(86.77, -30.7) * mm});
            skLineSegment(sketch, "E370", {"start": v(86.77, -30.7) * mm, "end": v(86.79, -30.6) * mm});
            skLineSegment(sketch, "E371", {"start": v(86.79, -30.6) * mm, "end": v(86.79, -30.48) * mm});
            skLineSegment(sketch, "E372", {"start": v(86.79, -30.48) * mm, "end": v(86.78, -30.36) * mm});
            skLineSegment(sketch, "E373", {"start": v(86.78, -30.36) * mm, "end": v(86.77, -30.25) * mm});
            skLineSegment(sketch, "E374", {"start": v(86.77, -30.25) * mm, "end": v(86.75, -30.19) * mm});
            skLineSegment(sketch, "E375", {"start": v(86.75, -30.19) * mm, "end": v(86.72, -30.13) * mm});
            skLineSegment(sketch, "E376", {"start": v(86.72, -30.13) * mm, "end": v(86.61, -30.04) * mm});
            skLineSegment(sketch, "E377", {"start": v(86.61, -30.04) * mm, "end": v(86.5, -29.95) * mm});
            skLineSegment(sketch, "E378", {"start": v(86.5, -29.95) * mm, "end": v(86.38, -29.86) * mm});
            skLineSegment(sketch, "E379", {"start": v(86.38, -29.86) * mm, "end": v(85.43, -30.23) * mm});
            skLineSegment(sketch, "E380", {"start": v(85.43, -30.23) * mm, "end": v(84.88, -30.43) * mm});
            skLineSegment(sketch, "E381", {"start": v(84.88, -30.43) * mm, "end": v(84.08, -30.69) * mm});
            skLineSegment(sketch, "E382", {"start": v(84.08, -30.69) * mm, "end": v(83.14, -30.98) * mm});
            skLineSegment(sketch, "E383", {"start": v(83.14, -30.98) * mm, "end": v(82.17, -31.27) * mm});
            skLineSegment(sketch, "E384", {"start": v(82.17, -31.27) * mm, "end": v(81.61, -31.44) * mm});
            skLineSegment(sketch, "E385", {"start": v(81.61, -31.44) * mm, "end": v(81.02, -31.62) * mm});
            skLineSegment(sketch, "E386", {"start": v(81.02, -31.62) * mm, "end": v(80.42, -31.8) * mm});
            skLineSegment(sketch, "E387", {"start": v(80.42, -31.8) * mm, "end": v(80.13, -31.87) * mm});
            skLineSegment(sketch, "E388", {"start": v(80.13, -31.87) * mm, "end": v(79.86, -31.93) * mm});
            skLineSegment(sketch, "E389", {"start": v(79.86, -31.93) * mm, "end": v(79.37, -32) * mm});
            skLineSegment(sketch, "E390", {"start": v(79.37, -32) * mm, "end": v(78.86, -32.06) * mm});
            skLineSegment(sketch, "E391", {"start": v(78.86, -32.06) * mm, "end": v(78.34, -32.1) * mm});
            skLineSegment(sketch, "E392", {"start": v(78.34, -32.1) * mm, "end": v(77.8, -32.14) * mm});
            skLineSegment(sketch, "E393", {"start": v(77.8, -32.14) * mm, "end": v(76.7, -32.18) * mm});
            skLineSegment(sketch, "E394", {"start": v(76.7, -32.18) * mm, "end": v(75.57, -32.2) * mm});
            skLineSegment(sketch, "E395", {"start": v(75.57, -32.2) * mm, "end": v(74.44, -32.22) * mm});
            skLineSegment(sketch, "E396", {"start": v(74.44, -32.22) * mm, "end": v(73.88, -32.24) * mm});
            skLineSegment(sketch, "E397", {"start": v(73.88, -32.24) * mm, "end": v(73.33, -32.26) * mm});
            skLineSegment(sketch, "E398", {"start": v(73.33, -32.26) * mm, "end": v(72.8, -32.3) * mm});
            skLineSegment(sketch, "E399", {"start": v(72.8, -32.3) * mm, "end": v(72.27, -32.34) * mm});
            skLineSegment(sketch, "E400", {"start": v(72.27, -32.34) * mm, "end": v(71.77, -32.4) * mm});
            skLineSegment(sketch, "E401", {"start": v(71.77, -32.4) * mm, "end": v(71.28, -32.47) * mm});
            skLineSegment(sketch, "E402", {"start": v(71.28, -32.47) * mm, "end": v(71.2, -32.5) * mm});
            skLineSegment(sketch, "E403", {"start": v(71.2, -32.5) * mm, "end": v(71.18, -32.5) * mm});
            skLineSegment(sketch, "E404", {"start": v(71.18, -32.5) * mm, "end": v(71.16, -32.53) * mm});
            skLineSegment(sketch, "E405", {"start": v(71.16, -32.53) * mm, "end": v(71.14, -32.6) * mm});
            skLineSegment(sketch, "E406", {"start": v(71.14, -32.6) * mm, "end": v(71.12, -32.69) * mm});
            skLineSegment(sketch, "E407", {"start": v(71.12, -32.69) * mm, "end": v(71.11, -32.8) * mm});
            skLineSegment(sketch, "E408", {"start": v(71.11, -32.8) * mm, "end": v(71.11, -33.09) * mm});
            skLineSegment(sketch, "E409", {"start": v(71.11, -33.09) * mm, "end": v(72.76, -32.77) * mm});
            skLineSegment(sketch, "E410", {"start": v(72.76, -32.77) * mm, "end": v(72.76, -33.05) * mm});
            skLineSegment(sketch, "E411", {"start": v(72.76, -33.05) * mm, "end": v(72.75, -33.09) * mm});
            skLineSegment(sketch, "E412", {"start": v(72.75, -33.09) * mm, "end": v(72.73, -33.16) * mm});
            skLineSegment(sketch, "E413", {"start": v(72.73, -33.16) * mm, "end": v(72.62, -33.37) * mm});
            skLineSegment(sketch, "E414", {"start": v(72.62, -33.37) * mm, "end": v(72.45, -33.67) * mm});
            skLineSegment(sketch, "E415", {"start": v(72.45, -33.67) * mm, "end": v(72.22, -34.04) * mm});
            skLineSegment(sketch, "E416", {"start": v(72.22, -34.04) * mm, "end": v(71.63, -34.96) * mm});
            skLineSegment(sketch, "E417", {"start": v(71.63, -34.96) * mm, "end": v(70.9, -36.03) * mm});
            skLineSegment(sketch, "E418", {"start": v(70.9, -36.03) * mm, "end": v(69.05, -38.74) * mm});
            skLineSegment(sketch, "E419", {"start": v(69.05, -38.74) * mm, "end": v(72.88, -43.08) * mm});
            skLineSegment(sketch, "E420", {"start": v(72.88, -43.08) * mm, "end": v(73, -43.08) * mm});
            skLineSegment(sketch, "E421", {"start": v(73, -43.08) * mm, "end": v(73.02, -43.07) * mm});
            skLineSegment(sketch, "E422", {"start": v(73.02, -43.07) * mm, "end": v(73.01, -43.05) * mm});
            skLineSegment(sketch, "E423", {"start": v(73.01, -43.05) * mm, "end": v(72.97, -42.96) * mm});
            skLineSegment(sketch, "E424", {"start": v(72.97, -42.96) * mm, "end": v(72.75, -42.65) * mm});
            skLineSegment(sketch, "E425", {"start": v(72.75, -42.65) * mm, "end": v(72.4, -42.2) * mm});
            skLineSegment(sketch, "E426", {"start": v(72.4, -42.2) * mm, "end": v(71.96, -41.64) * mm});
            skLineSegment(sketch, "E427", {"start": v(71.96, -41.64) * mm, "end": v(71.5, -41.07) * mm});
            skLineSegment(sketch, "E428", {"start": v(71.5, -41.07) * mm, "end": v(71.13, -40.56) * mm});
            skLineSegment(sketch, "E429", {"start": v(71.13, -40.56) * mm, "end": v(70.99, -40.36) * mm});
            skLineSegment(sketch, "E430", {"start": v(70.99, -40.36) * mm, "end": v(70.88, -40.19) * mm});
            skLineSegment(sketch, "E431", {"start": v(70.88, -40.19) * mm, "end": v(70.8, -40.06) * mm});
            skLineSegment(sketch, "E432", {"start": v(70.8, -40.06) * mm, "end": v(70.78, -40) * mm});
            skLineSegment(sketch, "E433", {"start": v(-20.24, -41.31) * mm, "end": v(-14.96, -41.1) * mm});
            skLineSegment(sketch, "E434", {"start": v(-14.96, -41.1) * mm, "end": v(-13.69, -41.1) * mm});
            skLineSegment(sketch, "E435", {"start": v(-13.69, -41.1) * mm, "end": v(-13.69, -38.59) * mm});
            skLineSegment(sketch, "E436", {"start": v(-13.69, -38.59) * mm, "end": v(-14.48, -37.8) * mm});
            skLineSegment(sketch, "E437", {"start": v(-14.48, -37.8) * mm, "end": v(-19.5, -37.8) * mm});
            skLineSegment(sketch, "E438", {"start": v(-19.5, -37.8) * mm, "end": v(-19.81, -38.07) * mm});
            skLineSegment(sketch, "E439", {"start": v(-19.81, -38.07) * mm, "end": v(-19.9, -38.13) * mm});
            skLineSegment(sketch, "E440", {"start": v(-19.9, -38.13) * mm, "end": v(-20.04, -38.2) * mm});
            skLineSegment(sketch, "E441", {"start": v(-20.04, -38.2) * mm, "end": v(-20.22, -38.3) * mm});
            skLineSegment(sketch, "E442", {"start": v(-20.22, -38.3) * mm, "end": v(-20.44, -38.38) * mm});
            skLineSegment(sketch, "E443", {"start": v(-20.44, -38.38) * mm, "end": v(-20.95, -38.57) * mm});
            skLineSegment(sketch, "E444", {"start": v(-20.95, -38.57) * mm, "end": v(-21.5, -38.74) * mm});
            skLineSegment(sketch, "E445", {"start": v(-21.5, -38.74) * mm, "end": v(-22.74, -39.28) * mm});
            skLineSegment(sketch, "E446", {"start": v(-22.74, -39.28) * mm, "end": v(-23.57, -40) * mm});
            skLineSegment(sketch, "E447", {"start": v(-23.57, -40) * mm, "end": v(-23.7, -40.17) * mm});
            skLineSegment(sketch, "E448", {"start": v(-23.7, -40.17) * mm, "end": v(-23.83, -40.36) * mm});
            skLineSegment(sketch, "E449", {"start": v(-23.83, -40.36) * mm, "end": v(-23.95, -40.53) * mm});
            skLineSegment(sketch, "E450", {"start": v(-23.95, -40.53) * mm, "end": v(-24.05, -40.7) * mm});
            skLineSegment(sketch, "E451", {"start": v(-24.05, -40.7) * mm, "end": v(-24.13, -40.86) * mm});
            skLineSegment(sketch, "E452", {"start": v(-24.13, -40.86) * mm, "end": v(-24.2, -41) * mm});
            skLineSegment(sketch, "E453", {"start": v(-24.2, -41) * mm, "end": v(-24.24, -41.1) * mm});
            skLineSegment(sketch, "E454", {"start": v(-24.24, -41.1) * mm, "end": v(-24.25, -41.2) * mm});
            skLineSegment(sketch, "E455", {"start": v(-24.25, -41.2) * mm, "end": v(-24.25, -41.53) * mm});
            skLineSegment(sketch, "E456", {"start": v(-24.25, -41.53) * mm, "end": v(-20.24, -41.31) * mm});
            skLineSegment(sketch, "E457", {"start": v(28.33, -39.92) * mm, "end": v(28.62, -39.07) * mm});
            skLineSegment(sketch, "E458", {"start": v(28.62, -39.07) * mm, "end": v(27.5, -36.15) * mm});
            skLineSegment(sketch, "E459", {"start": v(27.5, -36.15) * mm, "end": v(27.19, -36.13) * mm});
            skLineSegment(sketch, "E460", {"start": v(27.19, -36.13) * mm, "end": v(26.84, -36.1) * mm});
            skLineSegment(sketch, "E461", {"start": v(26.84, -36.1) * mm, "end": v(26.67, -36.08) * mm});
            skLineSegment(sketch, "E462", {"start": v(26.67, -36.08) * mm, "end": v(26.5, -36.08) * mm});
            skLineSegment(sketch, "E463", {"start": v(26.5, -36.08) * mm, "end": v(26.35, -36.1) * mm});
            skLineSegment(sketch, "E464", {"start": v(26.35, -36.1) * mm, "end": v(26.2, -36.15) * mm});
            skLineSegment(sketch, "E465", {"start": v(26.2, -36.15) * mm, "end": v(26.08, -36.21) * mm});
            skLineSegment(sketch, "E466", {"start": v(26.08, -36.21) * mm, "end": v(25.94, -36.3) * mm});
            skLineSegment(sketch, "E467", {"start": v(25.94, -36.3) * mm, "end": v(25.65, -36.51) * mm});
            skLineSegment(sketch, "E468", {"start": v(25.65, -36.51) * mm, "end": v(25.37, -36.75) * mm});
            skLineSegment(sketch, "E469", {"start": v(25.37, -36.75) * mm, "end": v(25.15, -36.96) * mm});
            skLineSegment(sketch, "E470", {"start": v(25.15, -36.96) * mm, "end": v(25, -37.13) * mm});
            skLineSegment(sketch, "E471", {"start": v(25, -37.13) * mm, "end": v(24.87, -37.3) * mm});
            skLineSegment(sketch, "E472", {"start": v(24.87, -37.3) * mm, "end": v(24.77, -37.47) * mm});
            skLineSegment(sketch, "E473", {"start": v(24.77, -37.47) * mm, "end": v(24.7, -37.62) * mm});
            skLineSegment(sketch, "E474", {"start": v(24.7, -37.62) * mm, "end": v(24.65, -37.77) * mm});
            skLineSegment(sketch, "E475", {"start": v(24.65, -37.77) * mm, "end": v(24.61, -37.9) * mm});
            skLineSegment(sketch, "E476", {"start": v(24.61, -37.9) * mm, "end": v(24.6, -38) * mm});
            skLineSegment(sketch, "E477", {"start": v(24.6, -38) * mm, "end": v(24.59, -38.08) * mm});
            skLineSegment(sketch, "E478", {"start": v(24.59, -38.08) * mm, "end": v(24.59, -38.39) * mm});
            skLineSegment(sketch, "E479", {"start": v(24.59, -38.39) * mm, "end": v(26.18, -38.79) * mm});
            skLineSegment(sketch, "E480", {"start": v(26.18, -38.79) * mm, "end": v(28.05, -40.77) * mm});
            skLineSegment(sketch, "E481", {"start": v(28.05, -40.77) * mm, "end": v(28.33, -39.92) * mm});
            skLineSegment(sketch, "E482", {"start": v(21.78, -40.44) * mm, "end": v(26.9, -40.44) * mm});
            skLineSegment(sketch, "E483", {"start": v(26.9, -40.44) * mm, "end": v(26.9, -40.13) * mm});
            skLineSegment(sketch, "E484", {"start": v(26.9, -40.13) * mm, "end": v(26.9, -40.09) * mm});
            skLineSegment(sketch, "E485", {"start": v(26.9, -40.09) * mm, "end": v(26.87, -40.05) * mm});
            skLineSegment(sketch, "E486", {"start": v(26.87, -40.05) * mm, "end": v(26.81, -39.94) * mm});
            skLineSegment(sketch, "E487", {"start": v(26.81, -39.94) * mm, "end": v(26.72, -39.82) * mm});
            skLineSegment(sketch, "E488", {"start": v(26.72, -39.82) * mm, "end": v(26.6, -39.68) * mm});
            skLineSegment(sketch, "E489", {"start": v(26.6, -39.68) * mm, "end": v(26.45, -39.54) * mm});
            skLineSegment(sketch, "E490", {"start": v(26.45, -39.54) * mm, "end": v(26.3, -39.4) * mm});
            skLineSegment(sketch, "E491", {"start": v(26.3, -39.4) * mm, "end": v(26.14, -39.27) * mm});
            skLineSegment(sketch, "E492", {"start": v(26.14, -39.27) * mm, "end": v(25.99, -39.15) * mm});
            skLineSegment(sketch, "E493", {"start": v(25.99, -39.15) * mm, "end": v(25.12, -38.77) * mm});
            skLineSegment(sketch, "E494", {"start": v(25.12, -38.77) * mm, "end": v(23.38, -38.82) * mm});
            skLineSegment(sketch, "E495", {"start": v(23.38, -38.82) * mm, "end": v(22.02, -37.14) * mm});
            skLineSegment(sketch, "E496", {"start": v(22.02, -37.14) * mm, "end": v(18.46, -37.14) * mm});
            skLineSegment(sketch, "E497", {"start": v(18.46, -37.14) * mm, "end": v(16.67, -39.19) * mm});
            skLineSegment(sketch, "E498", {"start": v(16.67, -39.19) * mm, "end": v(16.67, -40.44) * mm});
            skLineSegment(sketch, "E499", {"start": v(16.67, -40.44) * mm, "end": v(21.78, -40.44) * mm});
            skLineSegment(sketch, "E500", {"start": v(-65.54, -39.1) * mm, "end": v(-65.1, -38.93) * mm});
            skLineSegment(sketch, "E501", {"start": v(-65.1, -38.93) * mm, "end": v(-54.18, -35.69) * mm});
            skLineSegment(sketch, "E502", {"start": v(-54.18, -35.69) * mm, "end": v(-52.6, -35.32) * mm});
            skLineSegment(sketch, "E503", {"start": v(-52.6, -35.32) * mm, "end": v(-52.21, -35.24) * mm});
            skLineSegment(sketch, "E504", {"start": v(-52.21, -35.24) * mm, "end": v(-51.76, -35.16) * mm});
            skLineSegment(sketch, "E505", {"start": v(-51.76, -35.16) * mm, "end": v(-51.26, -35.07) * mm});
            skLineSegment(sketch, "E506", {"start": v(-51.26, -35.07) * mm, "end": v(-50.73, -35) * mm});
            skLineSegment(sketch, "E507", {"start": v(-50.73, -35) * mm, "end": v(-50.19, -34.92) * mm});
            skLineSegment(sketch, "E508", {"start": v(-50.19, -34.92) * mm, "end": v(-49.65, -34.86) * mm});
            skLineSegment(sketch, "E509", {"start": v(-49.65, -34.86) * mm, "end": v(-49.13, -34.82) * mm});
            skLineSegment(sketch, "E510", {"start": v(-49.13, -34.82) * mm, "end": v(-48.66, -34.8) * mm});
            skLineSegment(sketch, "E511", {"start": v(-48.66, -34.8) * mm, "end": v(-46.22, -34.88) * mm});
            skLineSegment(sketch, "E512", {"start": v(-46.22, -34.88) * mm, "end": v(-42.58, -37.65) * mm});
            skLineSegment(sketch, "E513", {"start": v(-42.58, -37.65) * mm, "end": v(-30.24, -37.7) * mm});
            skLineSegment(sketch, "E514", {"start": v(-30.24, -37.7) * mm, "end": v(-29.85, -37.18) * mm});
            skLineSegment(sketch, "E515", {"start": v(-29.85, -37.18) * mm, "end": v(-30.52, -36.77) * mm});
            skLineSegment(sketch, "E516", {"start": v(-30.52, -36.77) * mm, "end": v(-30.52, -34.72) * mm});
            skLineSegment(sketch, "E517", {"start": v(-30.52, -34.72) * mm, "end": v(-41.49, -35.14) * mm});
            skLineSegment(sketch, "E518", {"start": v(-41.49, -35.14) * mm, "end": v(-47.12, -30.12) * mm});
            skLineSegment(sketch, "E519", {"start": v(-47.12, -30.12) * mm, "end": v(-49.72, -30.34) * mm});
            skLineSegment(sketch, "E520", {"start": v(-49.72, -30.34) * mm, "end": v(-50.3, -30.4) * mm});
            skLineSegment(sketch, "E521", {"start": v(-50.3, -30.4) * mm, "end": v(-50.93, -30.46) * mm});
            skLineSegment(sketch, "E522", {"start": v(-50.93, -30.46) * mm, "end": v(-52.33, -30.64) * mm});
            skLineSegment(sketch, "E523", {"start": v(-52.33, -30.64) * mm, "end": v(-53.73, -30.84) * mm});
            skLineSegment(sketch, "E524", {"start": v(-53.73, -30.84) * mm, "end": v(-54.38, -30.95) * mm});
            skLineSegment(sketch, "E525", {"start": v(-54.38, -30.95) * mm, "end": v(-54.96, -31.06) * mm});
            skLineSegment(sketch, "E526", {"start": v(-54.96, -31.06) * mm, "end": v(-57.61, -31.56) * mm});
            skLineSegment(sketch, "E527", {"start": v(-57.61, -31.56) * mm, "end": v(-66.32, -34.44) * mm});
            skLineSegment(sketch, "E528", {"start": v(-66.32, -34.44) * mm, "end": v(-70.21, -36.18) * mm});
            skLineSegment(sketch, "E529", {"start": v(-70.21, -36.18) * mm, "end": v(-69.82, -36.58) * mm});
            skLineSegment(sketch, "E530", {"start": v(-69.82, -36.58) * mm, "end": v(-69.68, -36.7) * mm});
            skLineSegment(sketch, "E531", {"start": v(-69.68, -36.7) * mm, "end": v(-69.48, -36.86) * mm});
            skLineSegment(sketch, "E532", {"start": v(-69.48, -36.86) * mm, "end": v(-69.24, -37.04) * mm});
            skLineSegment(sketch, "E533", {"start": v(-69.24, -37.04) * mm, "end": v(-68.96, -37.23) * mm});
            skLineSegment(sketch, "E534", {"start": v(-68.96, -37.23) * mm, "end": v(-68.32, -37.64) * mm});
            skLineSegment(sketch, "E535", {"start": v(-68.32, -37.64) * mm, "end": v(-67.63, -38.06) * mm});
            skLineSegment(sketch, "E536", {"start": v(-67.63, -38.06) * mm, "end": v(-66.95, -38.45) * mm});
            skLineSegment(sketch, "E537", {"start": v(-66.95, -38.45) * mm, "end": v(-66.33, -38.78) * mm});
            skLineSegment(sketch, "E538", {"start": v(-66.33, -38.78) * mm, "end": v(-66.07, -38.9) * mm});
            skLineSegment(sketch, "E539", {"start": v(-66.07, -38.9) * mm, "end": v(-65.84, -39) * mm});
            skLineSegment(sketch, "E540", {"start": v(-65.84, -39) * mm, "end": v(-65.66, -39.07) * mm});
            skLineSegment(sketch, "E541", {"start": v(-65.66, -39.07) * mm, "end": v(-65.54, -39.1) * mm});
            skLineSegment(sketch, "E542", {"start": v(-9.36, -33.84) * mm, "end": v(-9.3, -33.83) * mm});
            skLineSegment(sketch, "E543", {"start": v(-9.3, -33.83) * mm, "end": v(-9.26, -33.8) * mm});
            skLineSegment(sketch, "E544", {"start": v(-9.26, -33.8) * mm, "end": v(-9.2, -33.77) * mm});
            skLineSegment(sketch, "E545", {"start": v(-9.2, -33.77) * mm, "end": v(-9.16, -33.71) * mm});
            skLineSegment(sketch, "E546", {"start": v(-9.16, -33.71) * mm, "end": v(-9.11, -33.64) * mm});
            skLineSegment(sketch, "E547", {"start": v(-9.11, -33.64) * mm, "end": v(-9.07, -33.55) * mm});
            skLineSegment(sketch, "E548", {"start": v(-9.07, -33.55) * mm, "end": v(-8.97, -33.3) * mm});
            skLineSegment(sketch, "E549", {"start": v(-8.97, -33.3) * mm, "end": v(-8.87, -32.98) * mm});
            skLineSegment(sketch, "E550", {"start": v(-8.87, -32.98) * mm, "end": v(-8.77, -32.57) * mm});
            skLineSegment(sketch, "E551", {"start": v(-8.77, -32.57) * mm, "end": v(-8.67, -32.06) * mm});
            skLineSegment(sketch, "E552", {"start": v(-8.67, -32.06) * mm, "end": v(-8.56, -31.45) * mm});
            skLineSegment(sketch, "E553", {"start": v(-8.56, -31.45) * mm, "end": v(-8.34, -30.2) * mm});
            skLineSegment(sketch, "E554", {"start": v(-8.34, -30.2) * mm, "end": v(-8.72, -30.2) * mm});
            skLineSegment(sketch, "E555", {"start": v(-8.72, -30.2) * mm, "end": v(-8.82, -30.22) * mm});
            skLineSegment(sketch, "E556", {"start": v(-8.82, -30.22) * mm, "end": v(-8.97, -30.26) * mm});
            skLineSegment(sketch, "E557", {"start": v(-8.97, -30.26) * mm, "end": v(-9.15, -30.32) * mm});
            skLineSegment(sketch, "E558", {"start": v(-9.15, -30.32) * mm, "end": v(-9.36, -30.4) * mm});
            skLineSegment(sketch, "E559", {"start": v(-9.36, -30.4) * mm, "end": v(-9.85, -30.6) * mm});
            skLineSegment(sketch, "E560", {"start": v(-9.85, -30.6) * mm, "end": v(-10.38, -30.86) * mm});
            skLineSegment(sketch, "E561", {"start": v(-10.38, -30.86) * mm, "end": v(-11.66, -31.52) * mm});
            skLineSegment(sketch, "E562", {"start": v(-11.66, -31.52) * mm, "end": v(-10.64, -32.68) * mm});
            skLineSegment(sketch, "E563", {"start": v(-10.64, -32.68) * mm, "end": v(-10.22, -33.13) * mm});
            skLineSegment(sketch, "E564", {"start": v(-10.22, -33.13) * mm, "end": v(-9.84, -33.5) * mm});
            skLineSegment(sketch, "E565", {"start": v(-9.84, -33.5) * mm, "end": v(-9.68, -33.64) * mm});
            skLineSegment(sketch, "E566", {"start": v(-9.68, -33.64) * mm, "end": v(-9.54, -33.75) * mm});
            skLineSegment(sketch, "E567", {"start": v(-9.54, -33.75) * mm, "end": v(-9.43, -33.81) * mm});
            skLineSegment(sketch, "E568", {"start": v(-9.43, -33.81) * mm, "end": v(-9.4, -33.83) * mm});
            skLineSegment(sketch, "E569", {"start": v(-9.4, -33.83) * mm, "end": v(-9.36, -33.84) * mm});
            skLineSegment(sketch, "E570", {"start": v(-69.85, -27.8) * mm, "end": v(-70.07, -27) * mm});
            skLineSegment(sketch, "E571", {"start": v(-70.07, -27) * mm, "end": v(-70.29, -26.15) * mm});
            skLineSegment(sketch, "E572", {"start": v(-70.29, -26.15) * mm, "end": v(-70.49, -25.3) * mm});
            skLineSegment(sketch, "E573", {"start": v(-70.49, -25.3) * mm, "end": v(-70.66, -24.48) * mm});
            skLineSegment(sketch, "E574", {"start": v(-70.66, -24.48) * mm, "end": v(-70.7, -24.24) * mm});
            skLineSegment(sketch, "E575", {"start": v(-70.7, -24.24) * mm, "end": v(-70.71, -23.99) * mm});
            skLineSegment(sketch, "E576", {"start": v(-70.71, -23.99) * mm, "end": v(-70.73, -23.45) * mm});
            skLineSegment(sketch, "E577", {"start": v(-70.73, -23.45) * mm, "end": v(-70.73, -22.88) * mm});
            skLineSegment(sketch, "E578", {"start": v(-70.73, -22.88) * mm, "end": v(-70.72, -22.3) * mm});
            skLineSegment(sketch, "E579", {"start": v(-70.72, -22.3) * mm, "end": v(-70.73, -22.01) * mm});
            skLineSegment(sketch, "E580", {"start": v(-70.73, -22.01) * mm, "end": v(-70.75, -21.73) * mm});
            skLineSegment(sketch, "E581", {"start": v(-70.75, -21.73) * mm, "end": v(-70.78, -21.46) * mm});
            skLineSegment(sketch, "E582", {"start": v(-70.78, -21.46) * mm, "end": v(-70.82, -21.2) * mm});
            skLineSegment(sketch, "E583", {"start": v(-70.82, -21.2) * mm, "end": v(-70.88, -20.95) * mm});
            skLineSegment(sketch, "E584", {"start": v(-70.88, -20.95) * mm, "end": v(-70.96, -20.72) * mm});
            skLineSegment(sketch, "E585", {"start": v(-70.96, -20.72) * mm, "end": v(-71.01, -20.6) * mm});
            skLineSegment(sketch, "E586", {"start": v(-71.01, -20.6) * mm, "end": v(-71.07, -20.5) * mm});
            skLineSegment(sketch, "E587", {"start": v(-71.07, -20.5) * mm, "end": v(-71.13, -20.4) * mm});
            skLineSegment(sketch, "E588", {"start": v(-71.13, -20.4) * mm, "end": v(-71.2, -20.3) * mm});
            skLineSegment(sketch, "E589", {"start": v(-71.2, -20.3) * mm, "end": v(-71.22, -20.29) * mm});
            skLineSegment(sketch, "E590", {"start": v(-71.22, -20.29) * mm, "end": v(-71.26, -20.28) * mm});
            skLineSegment(sketch, "E591", {"start": v(-71.26, -20.28) * mm, "end": v(-71.35, -20.26) * mm});
            skLineSegment(sketch, "E592", {"start": v(-71.35, -20.26) * mm, "end": v(-71.6, -20.26) * mm});
            skLineSegment(sketch, "E593", {"start": v(-71.6, -20.26) * mm, "end": v(-71.87, -20.27) * mm});
            skLineSegment(sketch, "E594", {"start": v(-71.87, -20.27) * mm, "end": v(-72.07, -20.28) * mm});
            skLineSegment(sketch, "E595", {"start": v(-72.07, -20.28) * mm, "end": v(-72.23, -20.27) * mm});
            skLineSegment(sketch, "E596", {"start": v(-72.23, -20.27) * mm, "end": v(-72.42, -20.23) * mm});
            skLineSegment(sketch, "E597", {"start": v(-72.42, -20.23) * mm, "end": v(-72.65, -20.16) * mm});
            skLineSegment(sketch, "E598", {"start": v(-72.65, -20.16) * mm, "end": v(-72.91, -20.08) * mm});
            skLineSegment(sketch, "E599", {"start": v(-72.91, -20.08) * mm, "end": v(-73.53, -19.86) * mm});
            skLineSegment(sketch, "E600", {"start": v(-73.53, -19.86) * mm, "end": v(-74.25, -19.57) * mm});
            skLineSegment(sketch, "E601", {"start": v(-74.25, -19.57) * mm, "end": v(-75.05, -19.23) * mm});
            skLineSegment(sketch, "E602", {"start": v(-75.05, -19.23) * mm, "end": v(-75.93, -18.83) * mm});
            skLineSegment(sketch, "E603", {"start": v(-75.93, -18.83) * mm, "end": v(-76.86, -18.4) * mm});
            skLineSegment(sketch, "E604", {"start": v(-76.86, -18.4) * mm, "end": v(-77.83, -17.93) * mm});
            skLineSegment(sketch, "E605", {"start": v(-77.83, -17.93) * mm, "end": v(-78.81, -17.44) * mm});
            skLineSegment(sketch, "E606", {"start": v(-78.81, -17.44) * mm, "end": v(-79.8, -16.94) * mm});
            skLineSegment(sketch, "E607", {"start": v(-79.8, -16.94) * mm, "end": v(-80.76, -16.44) * mm});
            skLineSegment(sketch, "E608", {"start": v(-80.76, -16.44) * mm, "end": v(-81.69, -15.94) * mm});
            skLineSegment(sketch, "E609", {"start": v(-81.69, -15.94) * mm, "end": v(-82.57, -15.46) * mm});
            skLineSegment(sketch, "E610", {"start": v(-82.57, -15.46) * mm, "end": v(-83.37, -15) * mm});
            skLineSegment(sketch, "E611", {"start": v(-83.37, -15) * mm, "end": v(-84.09, -14.58) * mm});
            skLineSegment(sketch, "E612", {"start": v(-84.09, -14.58) * mm, "end": v(-84.7, -14.2) * mm});
            skLineSegment(sketch, "E613", {"start": v(-84.7, -14.2) * mm, "end": v(-85.01, -14) * mm});
            skLineSegment(sketch, "E614", {"start": v(-85.01, -14) * mm, "end": v(-85.3, -13.81) * mm});
            skLineSegment(sketch, "E615", {"start": v(-85.3, -13.81) * mm, "end": v(-85.45, -13.73) * mm});
            skLineSegment(sketch, "E616", {"start": v(-85.45, -13.73) * mm, "end": v(-85.59, -13.65) * mm});
            skLineSegment(sketch, "E617", {"start": v(-85.59, -13.65) * mm, "end": v(-85.73, -13.6) * mm});
            skLineSegment(sketch, "E618", {"start": v(-85.73, -13.6) * mm, "end": v(-85.87, -13.54) * mm});
            skLineSegment(sketch, "E619", {"start": v(-85.87, -13.54) * mm, "end": v(-86.01, -13.5) * mm});
            skLineSegment(sketch, "E620", {"start": v(-86.01, -13.5) * mm, "end": v(-86.15, -13.49) * mm});
            skLineSegment(sketch, "E621", {"start": v(-86.15, -13.49) * mm, "end": v(-86.3, -13.49) * mm});
            skLineSegment(sketch, "E622", {"start": v(-86.3, -13.49) * mm, "end": v(-86.46, -13.5) * mm});
            skLineSegment(sketch, "E623", {"start": v(-86.46, -13.5) * mm, "end": v(-86.62, -13.54) * mm});
            skLineSegment(sketch, "E624", {"start": v(-86.62, -13.54) * mm, "end": v(-86.78, -13.6) * mm});
            skLineSegment(sketch, "E625", {"start": v(-86.78, -13.6) * mm, "end": v(-86.96, -13.69) * mm});
            skLineSegment(sketch, "E626", {"start": v(-86.96, -13.69) * mm, "end": v(-87.14, -13.8) * mm});
            skLineSegment(sketch, "E627", {"start": v(-87.14, -13.8) * mm, "end": v(-87.16, -13.83) * mm});
            skLineSegment(sketch, "E628", {"start": v(-87.16, -13.83) * mm, "end": v(-87.18, -13.89) * mm});
            skLineSegment(sketch, "E629", {"start": v(-87.18, -13.89) * mm, "end": v(-87.18, -14.08) * mm});
            skLineSegment(sketch, "E630", {"start": v(-87.18, -14.08) * mm, "end": v(-87.17, -14.38) * mm});
            skLineSegment(sketch, "E631", {"start": v(-87.17, -14.38) * mm, "end": v(-87.13, -14.76) * mm});
            skLineSegment(sketch, "E632", {"start": v(-87.13, -14.76) * mm, "end": v(-87.08, -15.2) * mm});
            skLineSegment(sketch, "E633", {"start": v(-87.08, -15.2) * mm, "end": v(-87, -15.7) * mm});
            skLineSegment(sketch, "E634", {"start": v(-87, -15.7) * mm, "end": v(-86.83, -16.84) * mm});
            skLineSegment(sketch, "E635", {"start": v(-86.83, -16.84) * mm, "end": v(-86.72, -17.53) * mm});
            skLineSegment(sketch, "E636", {"start": v(-86.72, -17.53) * mm, "end": v(-86.62, -18.28) * mm});
            skLineSegment(sketch, "E637", {"start": v(-86.62, -18.28) * mm, "end": v(-86.57, -18.66) * mm});
            skLineSegment(sketch, "E638", {"start": v(-86.57, -18.66) * mm, "end": v(-86.5, -19.03) * mm});
            skLineSegment(sketch, "E639", {"start": v(-86.5, -19.03) * mm, "end": v(-86.42, -19.38) * mm});
            skLineSegment(sketch, "E640", {"start": v(-86.42, -19.38) * mm, "end": v(-86.33, -19.7) * mm});
            skLineSegment(sketch, "E641", {"start": v(-86.33, -19.7) * mm, "end": v(-86.13, -20.3) * mm});
            skLineSegment(sketch, "E642", {"start": v(-86.13, -20.3) * mm, "end": v(-85.9, -20.92) * mm});
            skLineSegment(sketch, "E643", {"start": v(-85.9, -20.92) * mm, "end": v(-85.63, -21.56) * mm});
            skLineSegment(sketch, "E644", {"start": v(-85.63, -21.56) * mm, "end": v(-85.34, -22.2) * mm});
            skLineSegment(sketch, "E645", {"start": v(-85.34, -22.2) * mm, "end": v(-85.02, -22.84) * mm});
            skLineSegment(sketch, "E646", {"start": v(-85.02, -22.84) * mm, "end": v(-84.7, -23.45) * mm});
            skLineSegment(sketch, "E647", {"start": v(-84.7, -23.45) * mm, "end": v(-84.37, -24.03) * mm});
            skLineSegment(sketch, "E648", {"start": v(-84.37, -24.03) * mm, "end": v(-84.2, -24.3) * mm});
            skLineSegment(sketch, "E649", {"start": v(-84.2, -24.3) * mm, "end": v(-84.03, -24.56) * mm});
            skLineSegment(sketch, "E650", {"start": v(-84.03, -24.56) * mm, "end": v(-83.75, -24.94) * mm});
            skLineSegment(sketch, "E651", {"start": v(-83.75, -24.94) * mm, "end": v(-83.44, -25.34) * mm});
            skLineSegment(sketch, "E652", {"start": v(-83.44, -25.34) * mm, "end": v(-83.1, -25.73) * mm});
            skLineSegment(sketch, "E653", {"start": v(-83.1, -25.73) * mm, "end": v(-82.75, -26.13) * mm});
            skLineSegment(sketch, "E654", {"start": v(-82.75, -26.13) * mm, "end": v(-82.38, -26.51) * mm});
            skLineSegment(sketch, "E655", {"start": v(-82.38, -26.51) * mm, "end": v(-82, -26.88) * mm});
            skLineSegment(sketch, "E656", {"start": v(-82, -26.88) * mm, "end": v(-81.64, -27.22) * mm});
            skLineSegment(sketch, "E657", {"start": v(-81.64, -27.22) * mm, "end": v(-81.28, -27.53) * mm});
            skLineSegment(sketch, "E658", {"start": v(-81.28, -27.53) * mm, "end": v(-80.93, -27.82) * mm});
            skLineSegment(sketch, "E659", {"start": v(-80.93, -27.82) * mm, "end": v(-80.55, -28.1) * mm});
            skLineSegment(sketch, "E660", {"start": v(-80.55, -28.1) * mm, "end": v(-80.14, -28.4) * mm});
            skLineSegment(sketch, "E661", {"start": v(-80.14, -28.4) * mm, "end": v(-79.72, -28.67) * mm});
            skLineSegment(sketch, "E662", {"start": v(-79.72, -28.67) * mm, "end": v(-79.29, -28.94) * mm});
            skLineSegment(sketch, "E663", {"start": v(-79.29, -28.94) * mm, "end": v(-78.86, -29.2) * mm});
            skLineSegment(sketch, "E664", {"start": v(-78.86, -29.2) * mm, "end": v(-78.44, -29.42) * mm});
            skLineSegment(sketch, "E665", {"start": v(-78.44, -29.42) * mm, "end": v(-78.03, -29.62) * mm});
            skLineSegment(sketch, "E666", {"start": v(-78.03, -29.62) * mm, "end": v(-77.5, -29.85) * mm});
            skLineSegment(sketch, "E667", {"start": v(-77.5, -29.85) * mm, "end": v(-76.92, -30.08) * mm});
            skLineSegment(sketch, "E668", {"start": v(-76.92, -30.08) * mm, "end": v(-76.3, -30.3) * mm});
            skLineSegment(sketch, "E669", {"start": v(-76.3, -30.3) * mm, "end": v(-75.68, -30.5) * mm});
            skLineSegment(sketch, "E670", {"start": v(-75.68, -30.5) * mm, "end": v(-75.05, -30.67) * mm});
            skLineSegment(sketch, "E671", {"start": v(-75.05, -30.67) * mm, "end": v(-74.43, -30.84) * mm});
            skLineSegment(sketch, "E672", {"start": v(-74.43, -30.84) * mm, "end": v(-73.82, -30.99) * mm});
            skLineSegment(sketch, "E673", {"start": v(-73.82, -30.99) * mm, "end": v(-73.25, -31.11) * mm});
            skLineSegment(sketch, "E674", {"start": v(-73.25, -31.11) * mm, "end": v(-72.79, -31.22) * mm});
            skLineSegment(sketch, "E675", {"start": v(-72.79, -31.22) * mm, "end": v(-72.29, -31.34) * mm});
            skLineSegment(sketch, "E676", {"start": v(-72.29, -31.34) * mm, "end": v(-71.77, -31.46) * mm});
            skLineSegment(sketch, "E677", {"start": v(-71.77, -31.46) * mm, "end": v(-71.24, -31.57) * mm});
            skLineSegment(sketch, "E678", {"start": v(-71.24, -31.57) * mm, "end": v(-70.97, -31.62) * mm});
            skLineSegment(sketch, "E679", {"start": v(-70.97, -31.62) * mm, "end": v(-70.7, -31.65) * mm});
            skLineSegment(sketch, "E680", {"start": v(-70.7, -31.65) * mm, "end": v(-70.45, -31.67) * mm});
            skLineSegment(sketch, "E681", {"start": v(-70.45, -31.67) * mm, "end": v(-70.2, -31.68) * mm});
            skLineSegment(sketch, "E682", {"start": v(-70.2, -31.68) * mm, "end": v(-69.94, -31.68) * mm});
            skLineSegment(sketch, "E683", {"start": v(-69.94, -31.68) * mm, "end": v(-69.7, -31.65) * mm});
            skLineSegment(sketch, "E684", {"start": v(-69.7, -31.65) * mm, "end": v(-69.47, -31.6) * mm});
            skLineSegment(sketch, "E685", {"start": v(-69.47, -31.6) * mm, "end": v(-69.25, -31.55) * mm});
            skLineSegment(sketch, "E686", {"start": v(-69.25, -31.55) * mm, "end": v(-69.14, -31.49) * mm});
            skLineSegment(sketch, "E687", {"start": v(-69.14, -31.49) * mm, "end": v(-69.03, -31.4) * mm});
            skLineSegment(sketch, "E688", {"start": v(-69.03, -31.4) * mm, "end": v(-68.95, -31.3) * mm});
            skLineSegment(sketch, "E689", {"start": v(-68.95, -31.3) * mm, "end": v(-68.91, -31.24) * mm});
            skLineSegment(sketch, "E690", {"start": v(-68.91, -31.24) * mm, "end": v(-68.9, -31.19) * mm});
            skLineSegment(sketch, "E691", {"start": v(-68.9, -31.19) * mm, "end": v(-68.86, -31) * mm});
            skLineSegment(sketch, "E692", {"start": v(-68.86, -31) * mm, "end": v(-68.85, -30.79) * mm});
            skLineSegment(sketch, "E693", {"start": v(-68.85, -30.79) * mm, "end": v(-68.86, -30.58) * mm});
            skLineSegment(sketch, "E694", {"start": v(-68.86, -30.58) * mm, "end": v(-68.9, -30.37) * mm});
            skLineSegment(sketch, "E695", {"start": v(-68.9, -30.37) * mm, "end": v(-68.94, -30.16) * mm});
            skLineSegment(sketch, "E696", {"start": v(-68.94, -30.16) * mm, "end": v(-69, -29.94) * mm});
            skLineSegment(sketch, "E697", {"start": v(-69, -29.94) * mm, "end": v(-69.16, -29.5) * mm});
            skLineSegment(sketch, "E698", {"start": v(-69.16, -29.5) * mm, "end": v(-69.35, -29.05) * mm});
            skLineSegment(sketch, "E699", {"start": v(-69.35, -29.05) * mm, "end": v(-69.54, -28.62) * mm});
            skLineSegment(sketch, "E700", {"start": v(-69.54, -28.62) * mm, "end": v(-69.71, -28.2) * mm});
            skLineSegment(sketch, "E701", {"start": v(-69.71, -28.2) * mm, "end": v(-69.79, -28) * mm});
            skLineSegment(sketch, "E702", {"start": v(-69.79, -28) * mm, "end": v(-69.85, -27.8) * mm});
            skLineSegment(sketch, "E703", {"start": v(11, -30.85) * mm, "end": v(11.03, -30.84) * mm});
            skLineSegment(sketch, "E704", {"start": v(11.03, -30.84) * mm, "end": v(11.07, -30.8) * mm});
            skLineSegment(sketch, "E705", {"start": v(11.07, -30.8) * mm, "end": v(11.19, -30.63) * mm});
            skLineSegment(sketch, "E706", {"start": v(11.19, -30.63) * mm, "end": v(11.34, -30.37) * mm});
            skLineSegment(sketch, "E707", {"start": v(11.34, -30.37) * mm, "end": v(11.53, -30.03) * mm});
            skLineSegment(sketch, "E708", {"start": v(11.53, -30.03) * mm, "end": v(11.75, -29.62) * mm});
            skLineSegment(sketch, "E709", {"start": v(11.75, -29.62) * mm, "end": v(12, -29.15) * mm});
            skLineSegment(sketch, "E710", {"start": v(12, -29.15) * mm, "end": v(12.24, -28.63) * mm});
            skLineSegment(sketch, "E711", {"start": v(12.24, -28.63) * mm, "end": v(12.5, -28.07) * mm});
            skLineSegment(sketch, "E712", {"start": v(12.5, -28.07) * mm, "end": v(12.81, -27.4) * mm});
            skLineSegment(sketch, "E713", {"start": v(12.81, -27.4) * mm, "end": v(13.15, -26.67) * mm});
            skLineSegment(sketch, "E714", {"start": v(13.15, -26.67) * mm, "end": v(13.33, -26.3) * mm});
            skLineSegment(sketch, "E715", {"start": v(13.33, -26.3) * mm, "end": v(13.5, -25.95) * mm});
            skLineSegment(sketch, "E716", {"start": v(13.5, -25.95) * mm, "end": v(13.7, -25.62) * mm});
            skLineSegment(sketch, "E717", {"start": v(13.7, -25.62) * mm, "end": v(13.88, -25.3) * mm});
            skLineSegment(sketch, "E718", {"start": v(13.88, -25.3) * mm, "end": v(14.28, -24.65) * mm});
            skLineSegment(sketch, "E719", {"start": v(14.28, -24.65) * mm, "end": v(14.5, -24.3) * mm});
            skLineSegment(sketch, "E720", {"start": v(14.5, -24.3) * mm, "end": v(14.74, -23.95) * mm});
            skLineSegment(sketch, "E721", {"start": v(14.74, -23.95) * mm, "end": v(14.99, -23.62) * mm});
            skLineSegment(sketch, "E722", {"start": v(14.99, -23.62) * mm, "end": v(15.11, -23.47) * mm});
            skLineSegment(sketch, "E723", {"start": v(15.11, -23.47) * mm, "end": v(15.23, -23.33) * mm});
            skLineSegment(sketch, "E724", {"start": v(15.23, -23.33) * mm, "end": v(15.36, -23.21) * mm});
            skLineSegment(sketch, "E725", {"start": v(15.36, -23.21) * mm, "end": v(15.48, -23.1) * mm});
            skLineSegment(sketch, "E726", {"start": v(15.48, -23.1) * mm, "end": v(15.6, -23.02) * mm});
            skLineSegment(sketch, "E727", {"start": v(15.6, -23.02) * mm, "end": v(15.73, -22.95) * mm});
            skLineSegment(sketch, "E728", {"start": v(15.73, -22.95) * mm, "end": v(15.83, -22.9) * mm});
            skLineSegment(sketch, "E729", {"start": v(15.83, -22.9) * mm, "end": v(15.94, -22.87) * mm});
            skLineSegment(sketch, "E730", {"start": v(15.94, -22.87) * mm, "end": v(16.17, -22.81) * mm});
            skLineSegment(sketch, "E731", {"start": v(16.17, -22.81) * mm, "end": v(16.43, -22.78) * mm});
            skLineSegment(sketch, "E732", {"start": v(16.43, -22.78) * mm, "end": v(16.7, -22.76) * mm});
            skLineSegment(sketch, "E733", {"start": v(16.7, -22.76) * mm, "end": v(16.97, -22.75) * mm});
            skLineSegment(sketch, "E734", {"start": v(16.97, -22.75) * mm, "end": v(17.24, -22.76) * mm});
            skLineSegment(sketch, "E735", {"start": v(17.24, -22.76) * mm, "end": v(17.49, -22.79) * mm});
            skLineSegment(sketch, "E736", {"start": v(17.49, -22.79) * mm, "end": v(17.7, -22.83) * mm});
            skLineSegment(sketch, "E737", {"start": v(17.7, -22.83) * mm, "end": v(17.89, -22.87) * mm});
            skLineSegment(sketch, "E738", {"start": v(17.89, -22.87) * mm, "end": v(18.07, -22.94) * mm});
            skLineSegment(sketch, "E739", {"start": v(18.07, -22.94) * mm, "end": v(18.46, -23.1) * mm});
            skLineSegment(sketch, "E740", {"start": v(18.46, -23.1) * mm, "end": v(18.85, -23.27) * mm});
            skLineSegment(sketch, "E741", {"start": v(18.85, -23.27) * mm, "end": v(19.2, -23.43) * mm});
            skLineSegment(sketch, "E742", {"start": v(19.2, -23.43) * mm, "end": v(19.53, -23.6) * mm});
            skLineSegment(sketch, "E743", {"start": v(19.53, -23.6) * mm, "end": v(19.94, -23.83) * mm});
            skLineSegment(sketch, "E744", {"start": v(19.94, -23.83) * mm, "end": v(20.42, -24.11) * mm});
            skLineSegment(sketch, "E745", {"start": v(20.42, -24.11) * mm, "end": v(20.94, -24.44) * mm});
            skLineSegment(sketch, "E746", {"start": v(20.94, -24.44) * mm, "end": v(22.07, -25.16) * mm});
            skLineSegment(sketch, "E747", {"start": v(22.07, -25.16) * mm, "end": v(22.66, -25.53) * mm});
            skLineSegment(sketch, "E748", {"start": v(22.66, -25.53) * mm, "end": v(23.24, -25.89) * mm});
            skLineSegment(sketch, "E749", {"start": v(23.24, -25.89) * mm, "end": v(23.56, -26.1) * mm});
            skLineSegment(sketch, "E750", {"start": v(23.56, -26.1) * mm, "end": v(23.88, -26.33) * mm});
            skLineSegment(sketch, "E751", {"start": v(23.88, -26.33) * mm, "end": v(24.55, -26.86) * mm});
            skLineSegment(sketch, "E752", {"start": v(24.55, -26.86) * mm, "end": v(24.89, -27.13) * mm});
            skLineSegment(sketch, "E753", {"start": v(24.89, -27.13) * mm, "end": v(25.22, -27.4) * mm});
            skLineSegment(sketch, "E754", {"start": v(25.22, -27.4) * mm, "end": v(25.54, -27.63) * mm});
            skLineSegment(sketch, "E755", {"start": v(25.54, -27.63) * mm, "end": v(25.86, -27.84) * mm});
            skLineSegment(sketch, "E756", {"start": v(25.86, -27.84) * mm, "end": v(26.2, -27.62) * mm});
            skLineSegment(sketch, "E757", {"start": v(26.2, -27.62) * mm, "end": v(26.21, -27.59) * mm});
            skLineSegment(sketch, "E758", {"start": v(26.21, -27.59) * mm, "end": v(26.22, -27.54) * mm});
            skLineSegment(sketch, "E759", {"start": v(26.22, -27.54) * mm, "end": v(26.23, -27.38) * mm});
            skLineSegment(sketch, "E760", {"start": v(26.23, -27.38) * mm, "end": v(26.21, -27.15) * mm});
            skLineSegment(sketch, "E761", {"start": v(26.21, -27.15) * mm, "end": v(26.19, -26.86) * mm});
            skLineSegment(sketch, "E762", {"start": v(26.19, -26.86) * mm, "end": v(26.14, -26.54) * mm});
            skLineSegment(sketch, "E763", {"start": v(26.14, -26.54) * mm, "end": v(26.09, -26.18) * mm});
            skLineSegment(sketch, "E764", {"start": v(26.09, -26.18) * mm, "end": v(26.02, -25.8) * mm});
            skLineSegment(sketch, "E765", {"start": v(26.02, -25.8) * mm, "end": v(25.94, -25.43) * mm});
            skLineSegment(sketch, "E766", {"start": v(25.94, -25.43) * mm, "end": v(25.83, -25) * mm});
            skLineSegment(sketch, "E767", {"start": v(25.83, -25) * mm, "end": v(25.7, -24.54) * mm});
            skLineSegment(sketch, "E768", {"start": v(25.7, -24.54) * mm, "end": v(25.54, -24.1) * mm});
            skLineSegment(sketch, "E769", {"start": v(25.54, -24.1) * mm, "end": v(25.37, -23.68) * mm});
            skLineSegment(sketch, "E770", {"start": v(25.37, -23.68) * mm, "end": v(25.15, -23.2) * mm});
            skLineSegment(sketch, "E771", {"start": v(25.15, -23.2) * mm, "end": v(24.9, -22.68) * mm});
            skLineSegment(sketch, "E772", {"start": v(24.9, -22.68) * mm, "end": v(24.62, -22.16) * mm});
            skLineSegment(sketch, "E773", {"start": v(24.62, -22.16) * mm, "end": v(24.32, -21.64) * mm});
            skLineSegment(sketch, "E774", {"start": v(24.32, -21.64) * mm, "end": v(24, -21.14) * mm});
            skLineSegment(sketch, "E775", {"start": v(24, -21.14) * mm, "end": v(23.67, -20.65) * mm});
            skLineSegment(sketch, "E776", {"start": v(23.67, -20.65) * mm, "end": v(23.33, -20.2) * mm});
            skLineSegment(sketch, "E777", {"start": v(23.33, -20.2) * mm, "end": v(23.15, -19.99) * mm});
            skLineSegment(sketch, "E778", {"start": v(23.15, -19.99) * mm, "end": v(22.98, -19.8) * mm});
            skLineSegment(sketch, "E779", {"start": v(22.98, -19.8) * mm, "end": v(22.7, -19.5) * mm});
            skLineSegment(sketch, "E780", {"start": v(22.7, -19.5) * mm, "end": v(22.37, -19.2) * mm});
            skLineSegment(sketch, "E781", {"start": v(22.37, -19.2) * mm, "end": v(22.02, -18.92) * mm});
            skLineSegment(sketch, "E782", {"start": v(22.02, -18.92) * mm, "end": v(21.66, -18.64) * mm});
            skLineSegment(sketch, "E783", {"start": v(21.66, -18.64) * mm, "end": v(21.29, -18.37) * mm});
            skLineSegment(sketch, "E784", {"start": v(21.29, -18.37) * mm, "end": v(20.91, -18.12) * mm});
            skLineSegment(sketch, "E785", {"start": v(20.91, -18.12) * mm, "end": v(20.54, -17.88) * mm});
            skLineSegment(sketch, "E786", {"start": v(20.54, -17.88) * mm, "end": v(20.19, -17.67) * mm});
            skLineSegment(sketch, "E787", {"start": v(20.19, -17.67) * mm, "end": v(19.84, -17.49) * mm});
            skLineSegment(sketch, "E788", {"start": v(19.84, -17.49) * mm, "end": v(19.45, -17.3) * mm});
            skLineSegment(sketch, "E789", {"start": v(19.45, -17.3) * mm, "end": v(19.06, -17.14) * mm});
            skLineSegment(sketch, "E790", {"start": v(19.06, -17.14) * mm, "end": v(18.7, -17) * mm});
            skLineSegment(sketch, "E791", {"start": v(18.7, -17) * mm, "end": v(18.35, -16.87) * mm});
            skLineSegment(sketch, "E792", {"start": v(18.35, -16.87) * mm, "end": v(17.97, -16.75) * mm});
            skLineSegment(sketch, "E793", {"start": v(17.97, -16.75) * mm, "end": v(17.57, -16.63) * mm});
            skLineSegment(sketch, "E794", {"start": v(17.57, -16.63) * mm, "end": v(17.15, -16.52) * mm});
            skLineSegment(sketch, "E795", {"start": v(17.15, -16.52) * mm, "end": v(16.73, -16.4) * mm});
            skLineSegment(sketch, "E796", {"start": v(16.73, -16.4) * mm, "end": v(16.32, -16.32) * mm});
            skLineSegment(sketch, "E797", {"start": v(16.32, -16.32) * mm, "end": v(15.94, -16.24) * mm});
            skLineSegment(sketch, "E798", {"start": v(15.94, -16.24) * mm, "end": v(15.6, -16.18) * mm});
            skLineSegment(sketch, "E799", {"start": v(15.6, -16.18) * mm, "end": v(15.22, -16.1) * mm});
            skLineSegment(sketch, "E800", {"start": v(15.22, -16.1) * mm, "end": v(14.8, -16) * mm});
            skLineSegment(sketch, "E801", {"start": v(14.8, -16) * mm, "end": v(14.6, -15.95) * mm});
            skLineSegment(sketch, "E802", {"start": v(14.6, -15.95) * mm, "end": v(14.4, -15.93) * mm});
            skLineSegment(sketch, "E803", {"start": v(14.4, -15.93) * mm, "end": v(14.2, -15.92) * mm});
            skLineSegment(sketch, "E804", {"start": v(14.2, -15.92) * mm, "end": v(14.12, -15.93) * mm});
            skLineSegment(sketch, "E805", {"start": v(14.12, -15.93) * mm, "end": v(14.03, -15.94) * mm});
            skLineSegment(sketch, "E806", {"start": v(14.03, -15.94) * mm, "end": v(13.81, -16) * mm});
            skLineSegment(sketch, "E807", {"start": v(13.81, -16) * mm, "end": v(13.6, -16.1) * mm});
            skLineSegment(sketch, "E808", {"start": v(13.6, -16.1) * mm, "end": v(13.37, -16.22) * mm});
            skLineSegment(sketch, "E809", {"start": v(13.37, -16.22) * mm, "end": v(13.16, -16.35) * mm});
            skLineSegment(sketch, "E810", {"start": v(13.16, -16.35) * mm, "end": v(12.95, -16.5) * mm});
            skLineSegment(sketch, "E811", {"start": v(12.95, -16.5) * mm, "end": v(12.76, -16.67) * mm});
            skLineSegment(sketch, "E812", {"start": v(12.76, -16.67) * mm, "end": v(12.58, -16.83) * mm});
            skLineSegment(sketch, "E813", {"start": v(12.58, -16.83) * mm, "end": v(12.42, -17) * mm});
            skLineSegment(sketch, "E814", {"start": v(12.42, -17) * mm, "end": v(12.12, -17.35) * mm});
            skLineSegment(sketch, "E815", {"start": v(12.12, -17.35) * mm, "end": v(11.82, -17.74) * mm});
            skLineSegment(sketch, "E816", {"start": v(11.82, -17.74) * mm, "end": v(11.53, -18.14) * mm});
            skLineSegment(sketch, "E817", {"start": v(11.53, -18.14) * mm, "end": v(11.24, -18.57) * mm});
            skLineSegment(sketch, "E818", {"start": v(11.24, -18.57) * mm, "end": v(10.96, -19.02) * mm});
            skLineSegment(sketch, "E819", {"start": v(10.96, -19.02) * mm, "end": v(10.7, -19.48) * mm});
            skLineSegment(sketch, "E820", {"start": v(10.7, -19.48) * mm, "end": v(10.43, -19.96) * mm});
            skLineSegment(sketch, "E821", {"start": v(10.43, -19.96) * mm, "end": v(10.19, -20.44) * mm});
            skLineSegment(sketch, "E822", {"start": v(10.19, -20.44) * mm, "end": v(9.95, -20.93) * mm});
            skLineSegment(sketch, "E823", {"start": v(9.95, -20.93) * mm, "end": v(9.73, -21.43) * mm});
            skLineSegment(sketch, "E824", {"start": v(9.73, -21.43) * mm, "end": v(9.52, -21.92) * mm});
            skLineSegment(sketch, "E825", {"start": v(9.52, -21.92) * mm, "end": v(9.33, -22.41) * mm});
            skLineSegment(sketch, "E826", {"start": v(9.33, -22.41) * mm, "end": v(9.16, -22.9) * mm});
            skLineSegment(sketch, "E827", {"start": v(9.16, -22.9) * mm, "end": v(9, -23.38) * mm});
            skLineSegment(sketch, "E828", {"start": v(9, -23.38) * mm, "end": v(8.87, -23.85) * mm});
            skLineSegment(sketch, "E829", {"start": v(8.87, -23.85) * mm, "end": v(8.75, -24.3) * mm});
            skLineSegment(sketch, "E830", {"start": v(8.75, -24.3) * mm, "end": v(8.72, -24.45) * mm});
            skLineSegment(sketch, "E831", {"start": v(8.72, -24.45) * mm, "end": v(8.71, -24.6) * mm});
            skLineSegment(sketch, "E832", {"start": v(8.71, -24.6) * mm, "end": v(8.72, -24.93) * mm});
            skLineSegment(sketch, "E833", {"start": v(8.72, -24.93) * mm, "end": v(8.74, -25.26) * mm});
            skLineSegment(sketch, "E834", {"start": v(8.74, -25.26) * mm, "end": v(8.75, -25.56) * mm});
            skLineSegment(sketch, "E835", {"start": v(8.75, -25.56) * mm, "end": v(8.76, -25.83) * mm});
            skLineSegment(sketch, "E836", {"start": v(8.76, -25.83) * mm, "end": v(8.78, -26.13) * mm});
            skLineSegment(sketch, "E837", {"start": v(8.78, -26.13) * mm, "end": v(8.81, -26.45) * mm});
            skLineSegment(sketch, "E838", {"start": v(8.81, -26.45) * mm, "end": v(8.86, -26.77) * mm});
            skLineSegment(sketch, "E839", {"start": v(8.86, -26.77) * mm, "end": v(8.92, -27.1) * mm});
            skLineSegment(sketch, "E840", {"start": v(8.92, -27.1) * mm, "end": v(8.98, -27.4) * mm});
            skLineSegment(sketch, "E841", {"start": v(8.98, -27.4) * mm, "end": v(9.05, -27.68) * mm});
            skLineSegment(sketch, "E842", {"start": v(9.05, -27.68) * mm, "end": v(9.13, -27.93) * mm});
            skLineSegment(sketch, "E843", {"start": v(9.13, -27.93) * mm, "end": v(9.21, -28.17) * mm});
            skLineSegment(sketch, "E844", {"start": v(9.21, -28.17) * mm, "end": v(9.31, -28.41) * mm});
            skLineSegment(sketch, "E845", {"start": v(9.31, -28.41) * mm, "end": v(9.43, -28.66) * mm});
            skLineSegment(sketch, "E846", {"start": v(9.43, -28.66) * mm, "end": v(9.55, -28.9) * mm});
            skLineSegment(sketch, "E847", {"start": v(9.55, -28.9) * mm, "end": v(9.81, -29.4) * mm});
            skLineSegment(sketch, "E848", {"start": v(9.81, -29.4) * mm, "end": v(10.09, -29.86) * mm});
            skLineSegment(sketch, "E849", {"start": v(10.09, -29.86) * mm, "end": v(10.23, -30.07) * mm});
            skLineSegment(sketch, "E850", {"start": v(10.23, -30.07) * mm, "end": v(10.36, -30.26) * mm});
            skLineSegment(sketch, "E851", {"start": v(10.36, -30.26) * mm, "end": v(10.5, -30.43) * mm});
            skLineSegment(sketch, "E852", {"start": v(10.5, -30.43) * mm, "end": v(10.61, -30.58) * mm});
            skLineSegment(sketch, "E853", {"start": v(10.61, -30.58) * mm, "end": v(10.73, -30.7) * mm});
            skLineSegment(sketch, "E854", {"start": v(10.73, -30.7) * mm, "end": v(10.83, -30.79) * mm});
            skLineSegment(sketch, "E855", {"start": v(10.83, -30.79) * mm, "end": v(10.92, -30.84) * mm});
            skLineSegment(sketch, "E856", {"start": v(10.92, -30.84) * mm, "end": v(10.96, -30.85) * mm});
            skLineSegment(sketch, "E857", {"start": v(10.96, -30.85) * mm, "end": v(11, -30.85) * mm});
            skLineSegment(sketch, "E858", {"start": v(-59.25, -26.59) * mm, "end": v(-58.9, -26.24) * mm});
            skLineSegment(sketch, "E859", {"start": v(-58.9, -26.24) * mm, "end": v(-58.5, -25.87) * mm});
            skLineSegment(sketch, "E860", {"start": v(-58.5, -25.87) * mm, "end": v(-58.3, -25.67) * mm});
            skLineSegment(sketch, "E861", {"start": v(-58.3, -25.67) * mm, "end": v(-58.11, -25.48) * mm});
            skLineSegment(sketch, "E862", {"start": v(-58.11, -25.48) * mm, "end": v(-57.94, -25.29) * mm});
            skLineSegment(sketch, "E863", {"start": v(-57.94, -25.29) * mm, "end": v(-57.8, -25.1) * mm});
            skLineSegment(sketch, "E864", {"start": v(-57.8, -25.1) * mm, "end": v(-57.56, -24.73) * mm});
            skLineSegment(sketch, "E865", {"start": v(-57.56, -24.73) * mm, "end": v(-57.34, -24.33) * mm});
            skLineSegment(sketch, "E866", {"start": v(-57.34, -24.33) * mm, "end": v(-57.12, -23.9) * mm});
            skLineSegment(sketch, "E867", {"start": v(-57.12, -23.9) * mm, "end": v(-56.92, -23.46) * mm});
            skLineSegment(sketch, "E868", {"start": v(-56.92, -23.46) * mm, "end": v(-56.72, -23.01) * mm});
            skLineSegment(sketch, "E869", {"start": v(-56.72, -23.01) * mm, "end": v(-56.55, -22.57) * mm});
            skLineSegment(sketch, "E870", {"start": v(-56.55, -22.57) * mm, "end": v(-56.39, -22.14) * mm});
            skLineSegment(sketch, "E871", {"start": v(-56.39, -22.14) * mm, "end": v(-56.25, -21.72) * mm});
            skLineSegment(sketch, "E872", {"start": v(-56.25, -21.72) * mm, "end": v(-56.12, -21.28) * mm});
            skLineSegment(sketch, "E873", {"start": v(-56.12, -21.28) * mm, "end": v(-56, -20.8) * mm});
            skLineSegment(sketch, "E874", {"start": v(-56, -20.8) * mm, "end": v(-55.88, -20.3) * mm});
            skLineSegment(sketch, "E875", {"start": v(-55.88, -20.3) * mm, "end": v(-55.78, -19.8) * mm});
            skLineSegment(sketch, "E876", {"start": v(-55.78, -19.8) * mm, "end": v(-55.7, -19.29) * mm});
            skLineSegment(sketch, "E877", {"start": v(-55.7, -19.29) * mm, "end": v(-55.62, -18.78) * mm});
            skLineSegment(sketch, "E878", {"start": v(-55.62, -18.78) * mm, "end": v(-55.56, -18.3) * mm});
            skLineSegment(sketch, "E879", {"start": v(-55.56, -18.3) * mm, "end": v(-55.52, -17.83) * mm});
            skLineSegment(sketch, "E880", {"start": v(-55.52, -17.83) * mm, "end": v(-55.47, -17.07) * mm});
            skLineSegment(sketch, "E881", {"start": v(-55.47, -17.07) * mm, "end": v(-55.4, -16.24) * mm});
            skLineSegment(sketch, "E882", {"start": v(-55.4, -16.24) * mm, "end": v(-55.36, -15.39) * mm});
            skLineSegment(sketch, "E883", {"start": v(-55.36, -15.39) * mm, "end": v(-55.35, -14.95) * mm});
            skLineSegment(sketch, "E884", {"start": v(-55.35, -14.95) * mm, "end": v(-55.35, -14.52) * mm});
            skLineSegment(sketch, "E885", {"start": v(-55.35, -14.52) * mm, "end": v(-55.35, -14.08) * mm});
            skLineSegment(sketch, "E886", {"start": v(-55.35, -14.08) * mm, "end": v(-55.37, -13.66) * mm});
            skLineSegment(sketch, "E887", {"start": v(-55.37, -13.66) * mm, "end": v(-55.4, -13.23) * mm});
            skLineSegment(sketch, "E888", {"start": v(-55.4, -13.23) * mm, "end": v(-55.46, -12.82) * mm});
            skLineSegment(sketch, "E889", {"start": v(-55.46, -12.82) * mm, "end": v(-55.53, -12.42) * mm});
            skLineSegment(sketch, "E890", {"start": v(-55.53, -12.42) * mm, "end": v(-55.62, -12.04) * mm});
            skLineSegment(sketch, "E891", {"start": v(-55.62, -12.04) * mm, "end": v(-55.73, -11.67) * mm});
            skLineSegment(sketch, "E892", {"start": v(-55.73, -11.67) * mm, "end": v(-55.8, -11.5) * mm});
            skLineSegment(sketch, "E893", {"start": v(-55.8, -11.5) * mm, "end": v(-55.87, -11.33) * mm});
            skLineSegment(sketch, "E894", {"start": v(-55.87, -11.33) * mm, "end": v(-55.97, -11.13) * mm});
            skLineSegment(sketch, "E895", {"start": v(-55.97, -11.13) * mm, "end": v(-56.04, -11.03) * mm});
            skLineSegment(sketch, "E896", {"start": v(-56.04, -11.03) * mm, "end": v(-56.11, -10.93) * mm});
            skLineSegment(sketch, "E897", {"start": v(-56.11, -10.93) * mm, "end": v(-56.2, -10.85) * mm});
            skLineSegment(sketch, "E898", {"start": v(-56.2, -10.85) * mm, "end": v(-56.28, -10.78) * mm});
            skLineSegment(sketch, "E899", {"start": v(-56.28, -10.78) * mm, "end": v(-56.37, -10.74) * mm});
            skLineSegment(sketch, "E900", {"start": v(-56.37, -10.74) * mm, "end": v(-56.42, -10.73) * mm});
            skLineSegment(sketch, "E901", {"start": v(-56.42, -10.73) * mm, "end": v(-56.47, -10.73) * mm});
            skLineSegment(sketch, "E902", {"start": v(-56.47, -10.73) * mm, "end": v(-56.57, -10.74) * mm});
            skLineSegment(sketch, "E903", {"start": v(-56.57, -10.74) * mm, "end": v(-56.67, -10.77) * mm});
            skLineSegment(sketch, "E904", {"start": v(-56.67, -10.77) * mm, "end": v(-56.77, -10.81) * mm});
            skLineSegment(sketch, "E905", {"start": v(-56.77, -10.81) * mm, "end": v(-56.87, -10.86) * mm});
            skLineSegment(sketch, "E906", {"start": v(-56.87, -10.86) * mm, "end": v(-57.07, -11) * mm});
            skLineSegment(sketch, "E907", {"start": v(-57.07, -11) * mm, "end": v(-57.26, -11.16) * mm});
            skLineSegment(sketch, "E908", {"start": v(-57.26, -11.16) * mm, "end": v(-57.44, -11.34) * mm});
            skLineSegment(sketch, "E909", {"start": v(-57.44, -11.34) * mm, "end": v(-57.6, -11.52) * mm});
            skLineSegment(sketch, "E910", {"start": v(-57.6, -11.52) * mm, "end": v(-57.76, -11.7) * mm});
            skLineSegment(sketch, "E911", {"start": v(-57.76, -11.7) * mm, "end": v(-57.89, -11.88) * mm});
            skLineSegment(sketch, "E912", {"start": v(-57.89, -11.88) * mm, "end": v(-58.13, -12.2) * mm});
            skLineSegment(sketch, "E913", {"start": v(-58.13, -12.2) * mm, "end": v(-58.42, -12.55) * mm});
            skLineSegment(sketch, "E914", {"start": v(-58.42, -12.55) * mm, "end": v(-58.75, -12.93) * mm});
            skLineSegment(sketch, "E915", {"start": v(-58.75, -12.93) * mm, "end": v(-59.1, -13.33) * mm});
            skLineSegment(sketch, "E916", {"start": v(-59.1, -13.33) * mm, "end": v(-59.9, -14.17) * mm});
            skLineSegment(sketch, "E917", {"start": v(-59.9, -14.17) * mm, "end": v(-60.75, -15.02) * mm});
            skLineSegment(sketch, "E918", {"start": v(-60.75, -15.02) * mm, "end": v(-60.87, -15.13) * mm});
            skLineSegment(sketch, "E919", {"start": v(-60.87, -15.13) * mm, "end": v(-61, -15.24) * mm});
            skLineSegment(sketch, "E920", {"start": v(-61, -15.24) * mm, "end": v(-61.29, -15.45) * mm});
            skLineSegment(sketch, "E921", {"start": v(-61.29, -15.45) * mm, "end": v(-61.6, -15.64) * mm});
            skLineSegment(sketch, "E922", {"start": v(-61.6, -15.64) * mm, "end": v(-61.93, -15.83) * mm});
            skLineSegment(sketch, "E923", {"start": v(-61.93, -15.83) * mm, "end": v(-62.6, -16.17) * mm});
            skLineSegment(sketch, "E924", {"start": v(-62.6, -16.17) * mm, "end": v(-62.91, -16.34) * mm});
            skLineSegment(sketch, "E925", {"start": v(-62.91, -16.34) * mm, "end": v(-63.21, -16.5) * mm});
            skLineSegment(sketch, "E926", {"start": v(-63.21, -16.5) * mm, "end": v(-63.44, -16.62) * mm});
            skLineSegment(sketch, "E927", {"start": v(-63.44, -16.62) * mm, "end": v(-63.7, -16.72) * mm});
            skLineSegment(sketch, "E928", {"start": v(-63.7, -16.72) * mm, "end": v(-63.97, -16.8) * mm});
            skLineSegment(sketch, "E929", {"start": v(-63.97, -16.8) * mm, "end": v(-64.27, -16.88) * mm});
            skLineSegment(sketch, "E930", {"start": v(-64.27, -16.88) * mm, "end": v(-64.9, -17.03) * mm});
            skLineSegment(sketch, "E931", {"start": v(-64.9, -17.03) * mm, "end": v(-65.54, -17.18) * mm});
            skLineSegment(sketch, "E932", {"start": v(-65.54, -17.18) * mm, "end": v(-65.86, -17.26) * mm});
            skLineSegment(sketch, "E933", {"start": v(-65.86, -17.26) * mm, "end": v(-66.17, -17.36) * mm});
            skLineSegment(sketch, "E934", {"start": v(-66.17, -17.36) * mm, "end": v(-66.47, -17.47) * mm});
            skLineSegment(sketch, "E935", {"start": v(-66.47, -17.47) * mm, "end": v(-66.75, -17.6) * mm});
            skLineSegment(sketch, "E936", {"start": v(-66.75, -17.6) * mm, "end": v(-66.88, -17.67) * mm});
            skLineSegment(sketch, "E937", {"start": v(-66.88, -17.67) * mm, "end": v(-67, -17.74) * mm});
            skLineSegment(sketch, "E938", {"start": v(-67, -17.74) * mm, "end": v(-67.12, -17.82) * mm});
            skLineSegment(sketch, "E939", {"start": v(-67.12, -17.82) * mm, "end": v(-67.23, -17.91) * mm});
            skLineSegment(sketch, "E940", {"start": v(-67.23, -17.91) * mm, "end": v(-67.33, -18) * mm});
            skLineSegment(sketch, "E941", {"start": v(-67.33, -18) * mm, "end": v(-67.42, -18.11) * mm});
            skLineSegment(sketch, "E942", {"start": v(-67.42, -18.11) * mm, "end": v(-67.5, -18.22) * mm});
            skLineSegment(sketch, "E943", {"start": v(-67.5, -18.22) * mm, "end": v(-67.58, -18.34) * mm});
            skLineSegment(sketch, "E944", {"start": v(-67.58, -18.34) * mm, "end": v(-67.6, -18.4) * mm});
            skLineSegment(sketch, "E945", {"start": v(-67.6, -18.4) * mm, "end": v(-67.63, -18.45) * mm});
            skLineSegment(sketch, "E946", {"start": v(-67.63, -18.45) * mm, "end": v(-67.64, -18.6) * mm});
            skLineSegment(sketch, "E947", {"start": v(-67.64, -18.6) * mm, "end": v(-67.64, -18.8) * mm});
            skLineSegment(sketch, "E948", {"start": v(-67.64, -18.8) * mm, "end": v(-67.62, -19) * mm});
            skLineSegment(sketch, "E949", {"start": v(-67.62, -19) * mm, "end": v(-67.6, -19.24) * mm});
            skLineSegment(sketch, "E950", {"start": v(-67.6, -19.24) * mm, "end": v(-67.54, -19.5) * mm});
            skLineSegment(sketch, "E951", {"start": v(-67.54, -19.5) * mm, "end": v(-67.43, -20.03) * mm});
            skLineSegment(sketch, "E952", {"start": v(-67.43, -20.03) * mm, "end": v(-67.16, -21.07) * mm});
            skLineSegment(sketch, "E953", {"start": v(-67.16, -21.07) * mm, "end": v(-67.06, -21.48) * mm});
            skLineSegment(sketch, "E954", {"start": v(-67.06, -21.48) * mm, "end": v(-67.02, -21.65) * mm});
            skLineSegment(sketch, "E955", {"start": v(-67.02, -21.65) * mm, "end": v(-67, -21.78) * mm});
            skLineSegment(sketch, "E956", {"start": v(-67, -21.78) * mm, "end": v(-66.95, -22.23) * mm});
            skLineSegment(sketch, "E957", {"start": v(-66.95, -22.23) * mm, "end": v(-66.88, -22.77) * mm});
            skLineSegment(sketch, "E958", {"start": v(-66.88, -22.77) * mm, "end": v(-66.7, -24.02) * mm});
            skLineSegment(sketch, "E959", {"start": v(-66.7, -24.02) * mm, "end": v(-66.47, -25.37) * mm});
            skLineSegment(sketch, "E960", {"start": v(-66.47, -25.37) * mm, "end": v(-66.24, -26.65) * mm});
            skLineSegment(sketch, "E961", {"start": v(-66.24, -26.65) * mm, "end": v(-66.2, -26.82) * mm});
            skLineSegment(sketch, "E962", {"start": v(-66.2, -26.82) * mm, "end": v(-66.2, -27) * mm});
            skLineSegment(sketch, "E963", {"start": v(-66.2, -27) * mm, "end": v(-66.17, -27.39) * mm});
            skLineSegment(sketch, "E964", {"start": v(-66.17, -27.39) * mm, "end": v(-66.16, -27.8) * mm});
            skLineSegment(sketch, "E965", {"start": v(-66.16, -27.8) * mm, "end": v(-66.14, -28.22) * mm});
            skLineSegment(sketch, "E966", {"start": v(-66.14, -28.22) * mm, "end": v(-66.13, -28.42) * mm});
            skLineSegment(sketch, "E967", {"start": v(-66.13, -28.42) * mm, "end": v(-66.1, -28.62) * mm});
            skLineSegment(sketch, "E968", {"start": v(-66.1, -28.62) * mm, "end": v(-66.07, -28.8) * mm});
            skLineSegment(sketch, "E969", {"start": v(-66.07, -28.8) * mm, "end": v(-66.02, -28.98) * mm});
            skLineSegment(sketch, "E970", {"start": v(-66.02, -28.98) * mm, "end": v(-65.96, -29.15) * mm});
            skLineSegment(sketch, "E971", {"start": v(-65.96, -29.15) * mm, "end": v(-65.88, -29.3) * mm});
            skLineSegment(sketch, "E972", {"start": v(-65.88, -29.3) * mm, "end": v(-65.78, -29.43) * mm});
            skLineSegment(sketch, "E973", {"start": v(-65.78, -29.43) * mm, "end": v(-65.72, -29.5) * mm});
            skLineSegment(sketch, "E974", {"start": v(-65.72, -29.5) * mm, "end": v(-65.66, -29.55) * mm});
            skLineSegment(sketch, "E975", {"start": v(-65.66, -29.55) * mm, "end": v(-65.6, -29.58) * mm});
            skLineSegment(sketch, "E976", {"start": v(-65.6, -29.58) * mm, "end": v(-65.52, -29.6) * mm});
            skLineSegment(sketch, "E977", {"start": v(-65.52, -29.6) * mm, "end": v(-65.44, -29.6) * mm});
            skLineSegment(sketch, "E978", {"start": v(-65.44, -29.6) * mm, "end": v(-65.35, -29.59) * mm});
            skLineSegment(sketch, "E979", {"start": v(-65.35, -29.59) * mm, "end": v(-65.17, -29.55) * mm});
            skLineSegment(sketch, "E980", {"start": v(-65.17, -29.55) * mm, "end": v(-65.08, -29.53) * mm});
            skLineSegment(sketch, "E981", {"start": v(-65.08, -29.53) * mm, "end": v(-65, -29.53) * mm});
            skLineSegment(sketch, "E982", {"start": v(-65, -29.53) * mm, "end": v(-64.83, -29.5) * mm});
            skLineSegment(sketch, "E983", {"start": v(-64.83, -29.5) * mm, "end": v(-64.6, -29.46) * mm});
            skLineSegment(sketch, "E984", {"start": v(-64.6, -29.46) * mm, "end": v(-64.32, -29.4) * mm});
            skLineSegment(sketch, "E985", {"start": v(-64.32, -29.4) * mm, "end": v(-64, -29.3) * mm});
            skLineSegment(sketch, "E986", {"start": v(-64, -29.3) * mm, "end": v(-63.65, -29.2) * mm});
            skLineSegment(sketch, "E987", {"start": v(-63.65, -29.2) * mm, "end": v(-63.28, -29.07) * mm});
            skLineSegment(sketch, "E988", {"start": v(-63.28, -29.07) * mm, "end": v(-62.9, -28.94) * mm});
            skLineSegment(sketch, "E989", {"start": v(-62.9, -28.94) * mm, "end": v(-62.53, -28.8) * mm});
            skLineSegment(sketch, "E990", {"start": v(-62.53, -28.8) * mm, "end": v(-62.08, -28.64) * mm});
            skLineSegment(sketch, "E991", {"start": v(-62.08, -28.64) * mm, "end": v(-61.6, -28.48) * mm});
            skLineSegment(sketch, "E992", {"start": v(-61.6, -28.48) * mm, "end": v(-61.36, -28.4) * mm});
            skLineSegment(sketch, "E993", {"start": v(-61.36, -28.4) * mm, "end": v(-61.12, -28.3) * mm});
            skLineSegment(sketch, "E994", {"start": v(-61.12, -28.3) * mm, "end": v(-60.9, -28.2) * mm});
            skLineSegment(sketch, "E995", {"start": v(-60.9, -28.2) * mm, "end": v(-60.71, -28.08) * mm});
            skLineSegment(sketch, "E996", {"start": v(-60.71, -28.08) * mm, "end": v(-60.52, -27.93) * mm});
            skLineSegment(sketch, "E997", {"start": v(-60.52, -27.93) * mm, "end": v(-60.33, -27.76) * mm});
            skLineSegment(sketch, "E998", {"start": v(-60.33, -27.76) * mm, "end": v(-60.14, -27.57) * mm});
            skLineSegment(sketch, "E999", {"start": v(-60.14, -27.57) * mm, "end": v(-59.95, -27.37) * mm});
            skLineSegment(sketch, "E1000", {"start": v(-59.95, -27.37) * mm, "end": v(-59.6, -26.96) * mm});
            skLineSegment(sketch, "E1001", {"start": v(-59.6, -26.96) * mm, "end": v(-59.42, -26.76) * mm});
            skLineSegment(sketch, "E1002", {"start": v(-59.42, -26.76) * mm, "end": v(-59.25, -26.59) * mm});
            skLineSegment(sketch, "E1003", {"start": v(80.19, -27.67) * mm, "end": v(80.48, -27.53) * mm});
            skLineSegment(sketch, "E1004", {"start": v(80.48, -27.53) * mm, "end": v(80.82, -27.36) * mm});
            skLineSegment(sketch, "E1005", {"start": v(80.82, -27.36) * mm, "end": v(81.2, -27.16) * mm});
            skLineSegment(sketch, "E1006", {"start": v(81.2, -27.16) * mm, "end": v(81.58, -26.94) * mm});
            skLineSegment(sketch, "E1007", {"start": v(81.58, -26.94) * mm, "end": v(81.97, -26.7) * mm});
            skLineSegment(sketch, "E1008", {"start": v(81.97, -26.7) * mm, "end": v(82.36, -26.46) * mm});
            skLineSegment(sketch, "E1009", {"start": v(82.36, -26.46) * mm, "end": v(82.73, -26.22) * mm});
            skLineSegment(sketch, "E1010", {"start": v(82.73, -26.22) * mm, "end": v(83.07, -25.98) * mm});
            skLineSegment(sketch, "E1011", {"start": v(83.07, -25.98) * mm, "end": v(83.45, -25.73) * mm});
            skLineSegment(sketch, "E1012", {"start": v(83.45, -25.73) * mm, "end": v(83.87, -25.46) * mm});
            skLineSegment(sketch, "E1013", {"start": v(83.87, -25.46) * mm, "end": v(84.07, -25.32) * mm});
            skLineSegment(sketch, "E1014", {"start": v(84.07, -25.32) * mm, "end": v(84.27, -25.18) * mm});
            skLineSegment(sketch, "E1015", {"start": v(84.27, -25.18) * mm, "end": v(84.46, -25.03) * mm});
            skLineSegment(sketch, "E1016", {"start": v(84.46, -25.03) * mm, "end": v(84.62, -24.88) * mm});
            skLineSegment(sketch, "E1017", {"start": v(84.62, -24.88) * mm, "end": v(85.03, -24.47) * mm});
            skLineSegment(sketch, "E1018", {"start": v(85.03, -24.47) * mm, "end": v(85.44, -24.01) * mm});
            skLineSegment(sketch, "E1019", {"start": v(85.44, -24.01) * mm, "end": v(85.85, -23.52) * mm});
            skLineSegment(sketch, "E1020", {"start": v(85.85, -23.52) * mm, "end": v(86.26, -23) * mm});
            skLineSegment(sketch, "E1021", {"start": v(86.26, -23) * mm, "end": v(86.64, -22.48) * mm});
            skLineSegment(sketch, "E1022", {"start": v(86.64, -22.48) * mm, "end": v(87, -21.95) * mm});
            skLineSegment(sketch, "E1023", {"start": v(87, -21.95) * mm, "end": v(87.32, -21.43) * mm});
            skLineSegment(sketch, "E1024", {"start": v(87.32, -21.43) * mm, "end": v(87.47, -21.17) * mm});
            skLineSegment(sketch, "E1025", {"start": v(87.47, -21.17) * mm, "end": v(87.6, -20.92) * mm});
            skLineSegment(sketch, "E1026", {"start": v(87.6, -20.92) * mm, "end": v(87.73, -20.65) * mm});
            skLineSegment(sketch, "E1027", {"start": v(87.73, -20.65) * mm, "end": v(87.86, -20.36) * mm});
            skLineSegment(sketch, "E1028", {"start": v(87.86, -20.36) * mm, "end": v(87.99, -20.06) * mm});
            skLineSegment(sketch, "E1029", {"start": v(87.99, -20.06) * mm, "end": v(88.11, -19.75) * mm});
            skLineSegment(sketch, "E1030", {"start": v(88.11, -19.75) * mm, "end": v(88.34, -19.1) * mm});
            skLineSegment(sketch, "E1031", {"start": v(88.34, -19.1) * mm, "end": v(88.55, -18.44) * mm});
            skLineSegment(sketch, "E1032", {"start": v(88.55, -18.44) * mm, "end": v(88.74, -17.77) * mm});
            skLineSegment(sketch, "E1033", {"start": v(88.74, -17.77) * mm, "end": v(88.91, -17.1) * mm});
            skLineSegment(sketch, "E1034", {"start": v(88.91, -17.1) * mm, "end": v(89.06, -16.46) * mm});
            skLineSegment(sketch, "E1035", {"start": v(89.06, -16.46) * mm, "end": v(89.2, -15.85) * mm});
            skLineSegment(sketch, "E1036", {"start": v(89.2, -15.85) * mm, "end": v(89.29, -15.34) * mm});
            skLineSegment(sketch, "E1037", {"start": v(89.29, -15.34) * mm, "end": v(89.37, -14.8) * mm});
            skLineSegment(sketch, "E1038", {"start": v(89.37, -14.8) * mm, "end": v(89.43, -14.22) * mm});
            skLineSegment(sketch, "E1039", {"start": v(89.43, -14.22) * mm, "end": v(89.48, -13.63) * mm});
            skLineSegment(sketch, "E1040", {"start": v(89.48, -13.63) * mm, "end": v(89.57, -12.47) * mm});
            skLineSegment(sketch, "E1041", {"start": v(89.57, -12.47) * mm, "end": v(89.62, -11.92) * mm});
            skLineSegment(sketch, "E1042", {"start": v(89.62, -11.92) * mm, "end": v(89.67, -11.4) * mm});
            skLineSegment(sketch, "E1043", {"start": v(89.67, -11.4) * mm, "end": v(89.32, -11.4) * mm});
            skLineSegment(sketch, "E1044", {"start": v(89.32, -11.4) * mm, "end": v(89.28, -11.4) * mm});
            skLineSegment(sketch, "E1045", {"start": v(89.28, -11.4) * mm, "end": v(89.21, -11.43) * mm});
            skLineSegment(sketch, "E1046", {"start": v(89.21, -11.43) * mm, "end": v(89.03, -11.5) * mm});
            skLineSegment(sketch, "E1047", {"start": v(89.03, -11.5) * mm, "end": v(88.78, -11.63) * mm});
            skLineSegment(sketch, "E1048", {"start": v(88.78, -11.63) * mm, "end": v(88.47, -11.8) * mm});
            skLineSegment(sketch, "E1049", {"start": v(88.47, -11.8) * mm, "end": v(88.12, -12) * mm});
            skLineSegment(sketch, "E1050", {"start": v(88.12, -12) * mm, "end": v(87.74, -12.24) * mm});
            skLineSegment(sketch, "E1051", {"start": v(87.74, -12.24) * mm, "end": v(87.33, -12.5) * mm});
            skLineSegment(sketch, "E1052", {"start": v(87.33, -12.5) * mm, "end": v(86.91, -12.77) * mm});
            skLineSegment(sketch, "E1053", {"start": v(86.91, -12.77) * mm, "end": v(86.46, -13.06) * mm});
            skLineSegment(sketch, "E1054", {"start": v(86.46, -13.06) * mm, "end": v(85.95, -13.37) * mm});
            skLineSegment(sketch, "E1055", {"start": v(85.95, -13.37) * mm, "end": v(85.38, -13.7) * mm});
            skLineSegment(sketch, "E1056", {"start": v(85.38, -13.7) * mm, "end": v(84.76, -14.04) * mm});
            skLineSegment(sketch, "E1057", {"start": v(84.76, -14.04) * mm, "end": v(84.1, -14.4) * mm});
            skLineSegment(sketch, "E1058", {"start": v(84.1, -14.4) * mm, "end": v(83.4, -14.75) * mm});
            skLineSegment(sketch, "E1059", {"start": v(83.4, -14.75) * mm, "end": v(82.69, -15.11) * mm});
            skLineSegment(sketch, "E1060", {"start": v(82.69, -15.11) * mm, "end": v(81.95, -15.48) * mm});
            skLineSegment(sketch, "E1061", {"start": v(81.95, -15.48) * mm, "end": v(81.2, -15.84) * mm});
            skLineSegment(sketch, "E1062", {"start": v(81.2, -15.84) * mm, "end": v(80.43, -16.2) * mm});
            skLineSegment(sketch, "E1063", {"start": v(80.43, -16.2) * mm, "end": v(79.68, -16.53) * mm});
            skLineSegment(sketch, "E1064", {"start": v(79.68, -16.53) * mm, "end": v(78.93, -16.87) * mm});
            skLineSegment(sketch, "E1065", {"start": v(78.93, -16.87) * mm, "end": v(78.2, -17.18) * mm});
            skLineSegment(sketch, "E1066", {"start": v(78.2, -17.18) * mm, "end": v(77.48, -17.47) * mm});
            skLineSegment(sketch, "E1067", {"start": v(77.48, -17.47) * mm, "end": v(76.8, -17.74) * mm});
            skLineSegment(sketch, "E1068", {"start": v(76.8, -17.74) * mm, "end": v(76.15, -17.99) * mm});
            skLineSegment(sketch, "E1069", {"start": v(76.15, -17.99) * mm, "end": v(74.08, -18.74) * mm});
            skLineSegment(sketch, "E1070", {"start": v(74.08, -18.74) * mm, "end": v(74.1, -19.55) * mm});
            skLineSegment(sketch, "E1071", {"start": v(74.1, -19.55) * mm, "end": v(74.12, -20.43) * mm});
            skLineSegment(sketch, "E1072", {"start": v(74.12, -20.43) * mm, "end": v(74.12, -20.88) * mm});
            skLineSegment(sketch, "E1073", {"start": v(74.12, -20.88) * mm, "end": v(74.12, -21.31) * mm});
            skLineSegment(sketch, "E1074", {"start": v(74.12, -21.31) * mm, "end": v(74.1, -21.73) * mm});
            skLineSegment(sketch, "E1075", {"start": v(74.1, -21.73) * mm, "end": v(74.07, -22.12) * mm});
            skLineSegment(sketch, "E1076", {"start": v(74.07, -22.12) * mm, "end": v(73.97, -22.83) * mm});
            skLineSegment(sketch, "E1077", {"start": v(73.97, -22.83) * mm, "end": v(73.85, -23.57) * mm});
            skLineSegment(sketch, "E1078", {"start": v(73.85, -23.57) * mm, "end": v(73.7, -24.33) * mm});
            skLineSegment(sketch, "E1079", {"start": v(73.7, -24.33) * mm, "end": v(73.52, -25.1) * mm});
            skLineSegment(sketch, "E1080", {"start": v(73.52, -25.1) * mm, "end": v(73.33, -25.88) * mm});
            skLineSegment(sketch, "E1081", {"start": v(73.33, -25.88) * mm, "end": v(73.13, -26.64) * mm});
            skLineSegment(sketch, "E1082", {"start": v(73.13, -26.64) * mm, "end": v(72.76, -28.06) * mm});
            skLineSegment(sketch, "E1083", {"start": v(72.76, -28.06) * mm, "end": v(72.58, -28.64) * mm});
            skLineSegment(sketch, "E1084", {"start": v(72.58, -28.64) * mm, "end": v(72.39, -29.22) * mm});
            skLineSegment(sketch, "E1085", {"start": v(72.39, -29.22) * mm, "end": v(73.16, -29.22) * mm});
            skLineSegment(sketch, "E1086", {"start": v(73.16, -29.22) * mm, "end": v(73.98, -29.23) * mm});
            skLineSegment(sketch, "E1087", {"start": v(73.98, -29.23) * mm, "end": v(74.4, -29.23) * mm});
            skLineSegment(sketch, "E1088", {"start": v(74.4, -29.23) * mm, "end": v(74.8, -29.22) * mm});
            skLineSegment(sketch, "E1089", {"start": v(74.8, -29.22) * mm, "end": v(75.2, -29.2) * mm});
            skLineSegment(sketch, "E1090", {"start": v(75.2, -29.2) * mm, "end": v(75.57, -29.16) * mm});
            skLineSegment(sketch, "E1091", {"start": v(75.57, -29.16) * mm, "end": v(75.76, -29.12) * mm});
            skLineSegment(sketch, "E1092", {"start": v(75.76, -29.12) * mm, "end": v(75.97, -29.08) * mm});
            skLineSegment(sketch, "E1093", {"start": v(75.97, -29.08) * mm, "end": v(76.4, -28.96) * mm});
            skLineSegment(sketch, "E1094", {"start": v(76.4, -28.96) * mm, "end": v(76.82, -28.82) * mm});
            skLineSegment(sketch, "E1095", {"start": v(76.82, -28.82) * mm, "end": v(77.22, -28.7) * mm});
            skLineSegment(sketch, "E1096", {"start": v(77.22, -28.7) * mm, "end": v(77.96, -28.49) * mm});
            skLineSegment(sketch, "E1097", {"start": v(77.96, -28.49) * mm, "end": v(78.77, -28.22) * mm});
            skLineSegment(sketch, "E1098", {"start": v(78.77, -28.22) * mm, "end": v(79.54, -27.93) * mm});
            skLineSegment(sketch, "E1099", {"start": v(79.54, -27.93) * mm, "end": v(79.89, -27.8) * mm});
            skLineSegment(sketch, "E1100", {"start": v(79.89, -27.8) * mm, "end": v(80.19, -27.67) * mm});
            skLineSegment(sketch, "E1101", {"start": v(-37.94, -24.55) * mm, "end": v(-37.7, -24.55) * mm});
            skLineSegment(sketch, "E1102", {"start": v(-37.7, -24.55) * mm, "end": v(-37.39, -24.53) * mm});
            skLineSegment(sketch, "E1103", {"start": v(-37.39, -24.53) * mm, "end": v(-37.02, -24.5) * mm});
            skLineSegment(sketch, "E1104", {"start": v(-37.02, -24.5) * mm, "end": v(-36.6, -24.44) * mm});
            skLineSegment(sketch, "E1105", {"start": v(-36.6, -24.44) * mm, "end": v(-36.16, -24.38) * mm});
            skLineSegment(sketch, "E1106", {"start": v(-36.16, -24.38) * mm, "end": v(-35.7, -24.3) * mm});
            skLineSegment(sketch, "E1107", {"start": v(-35.7, -24.3) * mm, "end": v(-35.23, -24.22) * mm});
            skLineSegment(sketch, "E1108", {"start": v(-35.23, -24.22) * mm, "end": v(-34.77, -24.12) * mm});
            skLineSegment(sketch, "E1109", {"start": v(-34.77, -24.12) * mm, "end": v(-34.24, -24.02) * mm});
            skLineSegment(sketch, "E1110", {"start": v(-34.24, -24.02) * mm, "end": v(-33.67, -23.92) * mm});
            skLineSegment(sketch, "E1111", {"start": v(-33.67, -23.92) * mm, "end": v(-33.38, -23.87) * mm});
            skLineSegment(sketch, "E1112", {"start": v(-33.38, -23.87) * mm, "end": v(-33.1, -23.8) * mm});
            skLineSegment(sketch, "E1113", {"start": v(-33.1, -23.8) * mm, "end": v(-32.83, -23.74) * mm});
            skLineSegment(sketch, "E1114", {"start": v(-32.83, -23.74) * mm, "end": v(-32.58, -23.66) * mm});
            skLineSegment(sketch, "E1115", {"start": v(-32.58, -23.66) * mm, "end": v(-32.1, -23.48) * mm});
            skLineSegment(sketch, "E1116", {"start": v(-32.1, -23.48) * mm, "end": v(-31.58, -23.28) * mm});
            skLineSegment(sketch, "E1117", {"start": v(-31.58, -23.28) * mm, "end": v(-31.06, -23.05) * mm});
            skLineSegment(sketch, "E1118", {"start": v(-31.06, -23.05) * mm, "end": v(-30.53, -22.8) * mm});
            skLineSegment(sketch, "E1119", {"start": v(-30.53, -22.8) * mm, "end": v(-30, -22.54) * mm});
            skLineSegment(sketch, "E1120", {"start": v(-30, -22.54) * mm, "end": v(-29.51, -22.26) * mm});
            skLineSegment(sketch, "E1121", {"start": v(-29.51, -22.26) * mm, "end": v(-29.05, -21.96) * mm});
            skLineSegment(sketch, "E1122", {"start": v(-29.05, -21.96) * mm, "end": v(-28.83, -21.81) * mm});
            skLineSegment(sketch, "E1123", {"start": v(-28.83, -21.81) * mm, "end": v(-28.62, -21.66) * mm});
            skLineSegment(sketch, "E1124", {"start": v(-28.62, -21.66) * mm, "end": v(-28.26, -21.36) * mm});
            skLineSegment(sketch, "E1125", {"start": v(-28.26, -21.36) * mm, "end": v(-27.89, -21.02) * mm});
            skLineSegment(sketch, "E1126", {"start": v(-27.89, -21.02) * mm, "end": v(-27.52, -20.65) * mm});
            skLineSegment(sketch, "E1127", {"start": v(-27.52, -20.65) * mm, "end": v(-27.15, -20.26) * mm});
            skLineSegment(sketch, "E1128", {"start": v(-27.15, -20.26) * mm, "end": v(-26.8, -19.85) * mm});
            skLineSegment(sketch, "E1129", {"start": v(-26.8, -19.85) * mm, "end": v(-26.49, -19.44) * mm});
            skLineSegment(sketch, "E1130", {"start": v(-26.49, -19.44) * mm, "end": v(-26.2, -19.02) * mm});
            skLineSegment(sketch, "E1131", {"start": v(-26.2, -19.02) * mm, "end": v(-25.95, -18.62) * mm});
            skLineSegment(sketch, "E1132", {"start": v(-25.95, -18.62) * mm, "end": v(-25.86, -18.46) * mm});
            skLineSegment(sketch, "E1133", {"start": v(-25.86, -18.46) * mm, "end": v(-25.79, -18.27) * mm});
            skLineSegment(sketch, "E1134", {"start": v(-25.79, -18.27) * mm, "end": v(-25.66, -17.87) * mm});
            skLineSegment(sketch, "E1135", {"start": v(-25.66, -17.87) * mm, "end": v(-25.54, -17.47) * mm});
            skLineSegment(sketch, "E1136", {"start": v(-25.54, -17.47) * mm, "end": v(-25.43, -17.1) * mm});
            skLineSegment(sketch, "E1137", {"start": v(-25.43, -17.1) * mm, "end": v(-25.23, -16.46) * mm});
            skLineSegment(sketch, "E1138", {"start": v(-25.23, -16.46) * mm, "end": v(-25.06, -15.86) * mm});
            skLineSegment(sketch, "E1139", {"start": v(-25.06, -15.86) * mm, "end": v(-25, -15.6) * mm});
            skLineSegment(sketch, "E1140", {"start": v(-25, -15.6) * mm, "end": v(-24.95, -15.37) * mm});
            skLineSegment(sketch, "E1141", {"start": v(-24.95, -15.37) * mm, "end": v(-24.92, -15.18) * mm});
            skLineSegment(sketch, "E1142", {"start": v(-24.92, -15.18) * mm, "end": v(-24.9, -15.04) * mm});
            skLineSegment(sketch, "E1143", {"start": v(-24.9, -15.04) * mm, "end": v(-24.9, -14.51) * mm});
            skLineSegment(sketch, "E1144", {"start": v(-24.9, -14.51) * mm, "end": v(-25.14, -14.39) * mm});
            skLineSegment(sketch, "E1145", {"start": v(-25.14, -14.39) * mm, "end": v(-25.4, -14.26) * mm});
            skLineSegment(sketch, "E1146", {"start": v(-25.4, -14.26) * mm, "end": v(-25.94, -14) * mm});
            skLineSegment(sketch, "E1147", {"start": v(-25.94, -14) * mm, "end": v(-26.2, -13.87) * mm});
            skLineSegment(sketch, "E1148", {"start": v(-26.2, -13.87) * mm, "end": v(-26.45, -13.72) * mm});
            skLineSegment(sketch, "E1149", {"start": v(-26.45, -13.72) * mm, "end": v(-26.56, -13.64) * mm});
            skLineSegment(sketch, "E1150", {"start": v(-26.56, -13.64) * mm, "end": v(-26.67, -13.55) * mm});
            skLineSegment(sketch, "E1151", {"start": v(-26.67, -13.55) * mm, "end": v(-26.76, -13.46) * mm});
            skLineSegment(sketch, "E1152", {"start": v(-26.76, -13.46) * mm, "end": v(-26.85, -13.37) * mm});
            skLineSegment(sketch, "E1153", {"start": v(-26.85, -13.37) * mm, "end": v(-26.94, -13.23) * mm});
            skLineSegment(sketch, "E1154", {"start": v(-26.94, -13.23) * mm, "end": v(-27.01, -13.06) * mm});
            skLineSegment(sketch, "E1155", {"start": v(-27.01, -13.06) * mm, "end": v(-27.07, -12.89) * mm});
            skLineSegment(sketch, "E1156", {"start": v(-27.07, -12.89) * mm, "end": v(-27.12, -12.7) * mm});
            skLineSegment(sketch, "E1157", {"start": v(-27.12, -12.7) * mm, "end": v(-27.2, -12.33) * mm});
            skLineSegment(sketch, "E1158", {"start": v(-27.2, -12.33) * mm, "end": v(-27.24, -12.15) * mm});
            skLineSegment(sketch, "E1159", {"start": v(-27.24, -12.15) * mm, "end": v(-27.29, -11.98) * mm});
            skLineSegment(sketch, "E1160", {"start": v(-27.29, -11.98) * mm, "end": v(-27.64, -12.61) * mm});
            skLineSegment(sketch, "E1161", {"start": v(-27.64, -12.61) * mm, "end": v(-28, -13.3) * mm});
            skLineSegment(sketch, "E1162", {"start": v(-28, -13.3) * mm, "end": v(-28.2, -13.63) * mm});
            skLineSegment(sketch, "E1163", {"start": v(-28.2, -13.63) * mm, "end": v(-28.4, -13.96) * mm});
            skLineSegment(sketch, "E1164", {"start": v(-28.4, -13.96) * mm, "end": v(-28.6, -14.26) * mm});
            skLineSegment(sketch, "E1165", {"start": v(-28.6, -14.26) * mm, "end": v(-28.82, -14.53) * mm});
            skLineSegment(sketch, "E1166", {"start": v(-28.82, -14.53) * mm, "end": v(-29.13, -14.88) * mm});
            skLineSegment(sketch, "E1167", {"start": v(-29.13, -14.88) * mm, "end": v(-29.48, -15.22) * mm});
            skLineSegment(sketch, "E1168", {"start": v(-29.48, -15.22) * mm, "end": v(-29.86, -15.56) * mm});
            skLineSegment(sketch, "E1169", {"start": v(-29.86, -15.56) * mm, "end": v(-30.25, -15.9) * mm});
            skLineSegment(sketch, "E1170", {"start": v(-30.25, -15.9) * mm, "end": v(-30.66, -16.22) * mm});
            skLineSegment(sketch, "E1171", {"start": v(-30.66, -16.22) * mm, "end": v(-31.07, -16.53) * mm});
            skLineSegment(sketch, "E1172", {"start": v(-31.07, -16.53) * mm, "end": v(-31.48, -16.8) * mm});
            skLineSegment(sketch, "E1173", {"start": v(-31.48, -16.8) * mm, "end": v(-31.86, -17.06) * mm});
            skLineSegment(sketch, "E1174", {"start": v(-31.86, -17.06) * mm, "end": v(-32.17, -17.24) * mm});
            skLineSegment(sketch, "E1175", {"start": v(-32.17, -17.24) * mm, "end": v(-32.51, -17.42) * mm});
            skLineSegment(sketch, "E1176", {"start": v(-32.51, -17.42) * mm, "end": v(-32.87, -17.59) * mm});
            skLineSegment(sketch, "E1177", {"start": v(-32.87, -17.59) * mm, "end": v(-33.24, -17.75) * mm});
            skLineSegment(sketch, "E1178", {"start": v(-33.24, -17.75) * mm, "end": v(-33.98, -18.06) * mm});
            skLineSegment(sketch, "E1179", {"start": v(-33.98, -18.06) * mm, "end": v(-34.33, -18.21) * mm});
            skLineSegment(sketch, "E1180", {"start": v(-34.33, -18.21) * mm, "end": v(-34.66, -18.36) * mm});
            skLineSegment(sketch, "E1181", {"start": v(-34.66, -18.36) * mm, "end": v(-35.27, -18.63) * mm});
            skLineSegment(sketch, "E1182", {"start": v(-35.27, -18.63) * mm, "end": v(-35.9, -18.9) * mm});
            skLineSegment(sketch, "E1183", {"start": v(-35.9, -18.9) * mm, "end": v(-36.56, -19.17) * mm});
            skLineSegment(sketch, "E1184", {"start": v(-36.56, -19.17) * mm, "end": v(-37.22, -19.43) * mm});
            skLineSegment(sketch, "E1185", {"start": v(-37.22, -19.43) * mm, "end": v(-37.85, -19.67) * mm});
            skLineSegment(sketch, "E1186", {"start": v(-37.85, -19.67) * mm, "end": v(-38.45, -19.88) * mm});
            skLineSegment(sketch, "E1187", {"start": v(-38.45, -19.88) * mm, "end": v(-38.98, -20.06) * mm});
            skLineSegment(sketch, "E1188", {"start": v(-38.98, -20.06) * mm, "end": v(-39.44, -20.2) * mm});
            skLineSegment(sketch, "E1189", {"start": v(-39.44, -20.2) * mm, "end": v(-39.97, -20.34) * mm});
            skLineSegment(sketch, "E1190", {"start": v(-39.97, -20.34) * mm, "end": v(-40.6, -20.5) * mm});
            skLineSegment(sketch, "E1191", {"start": v(-40.6, -20.5) * mm, "end": v(-41.12, -20.64) * mm});
            skLineSegment(sketch, "E1192", {"start": v(-41.12, -20.64) * mm, "end": v(-41.3, -20.7) * mm});
            skLineSegment(sketch, "E1193", {"start": v(-41.3, -20.7) * mm, "end": v(-41.4, -20.75) * mm});
            skLineSegment(sketch, "E1194", {"start": v(-41.4, -20.75) * mm, "end": v(-41.42, -20.99) * mm});
            skLineSegment(sketch, "E1195", {"start": v(-41.42, -20.99) * mm, "end": v(-41.43, -21.25) * mm});
            skLineSegment(sketch, "E1196", {"start": v(-41.43, -21.25) * mm, "end": v(-41.48, -21.78) * mm});
            skLineSegment(sketch, "E1197", {"start": v(-41.48, -21.78) * mm, "end": v(-41.49, -22.06) * mm});
            skLineSegment(sketch, "E1198", {"start": v(-41.49, -22.06) * mm, "end": v(-41.49, -22.32) * mm});
            skLineSegment(sketch, "E1199", {"start": v(-41.49, -22.32) * mm, "end": v(-41.46, -22.57) * mm});
            skLineSegment(sketch, "E1200", {"start": v(-41.46, -22.57) * mm, "end": v(-41.44, -22.69) * mm});
            skLineSegment(sketch, "E1201", {"start": v(-41.44, -22.69) * mm, "end": v(-41.4, -22.8) * mm});
            skLineSegment(sketch, "E1202", {"start": v(-41.4, -22.8) * mm, "end": v(-41.34, -23) * mm});
            skLineSegment(sketch, "E1203", {"start": v(-41.34, -23) * mm, "end": v(-41.25, -23.2) * mm});
            skLineSegment(sketch, "E1204", {"start": v(-41.25, -23.2) * mm, "end": v(-41.14, -23.4) * mm});
            skLineSegment(sketch, "E1205", {"start": v(-41.14, -23.4) * mm, "end": v(-41.01, -23.6) * mm});
            skLineSegment(sketch, "E1206", {"start": v(-41.01, -23.6) * mm, "end": v(-40.88, -23.78) * mm});
            skLineSegment(sketch, "E1207", {"start": v(-40.88, -23.78) * mm, "end": v(-40.73, -23.95) * mm});
            skLineSegment(sketch, "E1208", {"start": v(-40.73, -23.95) * mm, "end": v(-40.57, -24.1) * mm});
            skLineSegment(sketch, "E1209", {"start": v(-40.57, -24.1) * mm, "end": v(-40.41, -24.22) * mm});
            skLineSegment(sketch, "E1210", {"start": v(-40.41, -24.22) * mm, "end": v(-40.33, -24.26) * mm});
            skLineSegment(sketch, "E1211", {"start": v(-40.33, -24.26) * mm, "end": v(-40.25, -24.3) * mm});
            skLineSegment(sketch, "E1212", {"start": v(-40.25, -24.3) * mm, "end": v(-40.05, -24.32) * mm});
            skLineSegment(sketch, "E1213", {"start": v(-40.05, -24.32) * mm, "end": v(-39.85, -24.34) * mm});
            skLineSegment(sketch, "E1214", {"start": v(-39.85, -24.34) * mm, "end": v(-39.67, -24.37) * mm});
            skLineSegment(sketch, "E1215", {"start": v(-39.67, -24.37) * mm, "end": v(-39.3, -24.42) * mm});
            skLineSegment(sketch, "E1216", {"start": v(-39.3, -24.42) * mm, "end": v(-38.86, -24.48) * mm});
            skLineSegment(sketch, "E1217", {"start": v(-38.86, -24.48) * mm, "end": v(-38.39, -24.52) * mm});
            skLineSegment(sketch, "E1218", {"start": v(-38.39, -24.52) * mm, "end": v(-37.94, -24.55) * mm});
            skLineSegment(sketch, "E1219", {"start": v(-42.1, -20.3) * mm, "end": v(-41.2, -20.3) * mm});
            skLineSegment(sketch, "E1220", {"start": v(-41.2, -20.3) * mm, "end": v(-38.42, -19.37) * mm});
            skLineSegment(sketch, "E1221", {"start": v(-38.42, -19.37) * mm, "end": v(-37.76, -19.14) * mm});
            skLineSegment(sketch, "E1222", {"start": v(-37.76, -19.14) * mm, "end": v(-37.12, -18.9) * mm});
            skLineSegment(sketch, "E1223", {"start": v(-37.12, -18.9) * mm, "end": v(-36.5, -18.67) * mm});
            skLineSegment(sketch, "E1224", {"start": v(-36.5, -18.67) * mm, "end": v(-35.9, -18.43) * mm});
            skLineSegment(sketch, "E1225", {"start": v(-35.9, -18.43) * mm, "end": v(-35.32, -18.18) * mm});
            skLineSegment(sketch, "E1226", {"start": v(-35.32, -18.18) * mm, "end": v(-34.76, -17.93) * mm});
            skLineSegment(sketch, "E1227", {"start": v(-34.76, -17.93) * mm, "end": v(-34.21, -17.67) * mm});
            skLineSegment(sketch, "E1228", {"start": v(-34.21, -17.67) * mm, "end": v(-33.69, -17.41) * mm});
            skLineSegment(sketch, "E1229", {"start": v(-33.69, -17.41) * mm, "end": v(-33.19, -17.15) * mm});
            skLineSegment(sketch, "E1230", {"start": v(-33.19, -17.15) * mm, "end": v(-32.71, -16.89) * mm});
            skLineSegment(sketch, "E1231", {"start": v(-32.71, -16.89) * mm, "end": v(-32.25, -16.62) * mm});
            skLineSegment(sketch, "E1232", {"start": v(-32.25, -16.62) * mm, "end": v(-31.82, -16.35) * mm});
            skLineSegment(sketch, "E1233", {"start": v(-31.82, -16.35) * mm, "end": v(-31.41, -16.08) * mm});
            skLineSegment(sketch, "E1234", {"start": v(-31.41, -16.08) * mm, "end": v(-31.03, -15.8) * mm});
            skLineSegment(sketch, "E1235", {"start": v(-31.03, -15.8) * mm, "end": v(-30.67, -15.53) * mm});
            skLineSegment(sketch, "E1236", {"start": v(-30.67, -15.53) * mm, "end": v(-30.34, -15.26) * mm});
            skLineSegment(sketch, "E1237", {"start": v(-30.34, -15.26) * mm, "end": v(-29, -14.1) * mm});
            skLineSegment(sketch, "E1238", {"start": v(-29, -14.1) * mm, "end": v(-27.8, -11.85) * mm});
            skLineSegment(sketch, "E1239", {"start": v(-27.8, -11.85) * mm, "end": v(-28.66, -10.92) * mm});
            skLineSegment(sketch, "E1240", {"start": v(-28.66, -10.92) * mm, "end": v(-28.84, -10.72) * mm});
            skLineSegment(sketch, "E1241", {"start": v(-28.84, -10.72) * mm, "end": v(-29, -10.53) * mm});
            skLineSegment(sketch, "E1242", {"start": v(-29, -10.53) * mm, "end": v(-29.15, -10.33) * mm});
            skLineSegment(sketch, "E1243", {"start": v(-29.15, -10.33) * mm, "end": v(-29.27, -10.15) * mm});
            skLineSegment(sketch, "E1244", {"start": v(-29.27, -10.15) * mm, "end": v(-29.38, -9.98) * mm});
            skLineSegment(sketch, "E1245", {"start": v(-29.38, -9.98) * mm, "end": v(-29.46, -9.84) * mm});
            skLineSegment(sketch, "E1246", {"start": v(-29.46, -9.84) * mm, "end": v(-29.51, -9.72) * mm});
            skLineSegment(sketch, "E1247", {"start": v(-29.51, -9.72) * mm, "end": v(-29.53, -9.62) * mm});
            skLineSegment(sketch, "E1248", {"start": v(-29.53, -9.62) * mm, "end": v(-29.53, -9.27) * mm});
            skLineSegment(sketch, "E1249", {"start": v(-29.53, -9.27) * mm, "end": v(-32.44, -12.6) * mm});
            skLineSegment(sketch, "E1250", {"start": v(-32.44, -12.6) * mm, "end": v(-37.15, -14.77) * mm});
            skLineSegment(sketch, "E1251", {"start": v(-37.15, -14.77) * mm, "end": v(-44.21, -15.86) * mm});
            skLineSegment(sketch, "E1252", {"start": v(-44.21, -15.86) * mm, "end": v(-44.32, -16.8) * mm});
            skLineSegment(sketch, "E1253", {"start": v(-44.32, -16.8) * mm, "end": v(-44.34, -17.04) * mm});
            skLineSegment(sketch, "E1254", {"start": v(-44.34, -17.04) * mm, "end": v(-44.35, -17.26) * mm});
            skLineSegment(sketch, "E1255", {"start": v(-44.35, -17.26) * mm, "end": v(-44.36, -17.49) * mm});
            skLineSegment(sketch, "E1256", {"start": v(-44.36, -17.49) * mm, "end": v(-44.35, -17.7) * mm});
            skLineSegment(sketch, "E1257", {"start": v(-44.35, -17.7) * mm, "end": v(-44.33, -17.92) * mm});
            skLineSegment(sketch, "E1258", {"start": v(-44.33, -17.92) * mm, "end": v(-44.3, -18.13) * mm});
            skLineSegment(sketch, "E1259", {"start": v(-44.3, -18.13) * mm, "end": v(-44.26, -18.33) * mm});
            skLineSegment(sketch, "E1260", {"start": v(-44.26, -18.33) * mm, "end": v(-44.22, -18.52) * mm});
            skLineSegment(sketch, "E1261", {"start": v(-44.22, -18.52) * mm, "end": v(-44.16, -18.71) * mm});
            skLineSegment(sketch, "E1262", {"start": v(-44.16, -18.71) * mm, "end": v(-44.1, -18.9) * mm});
            skLineSegment(sketch, "E1263", {"start": v(-44.1, -18.9) * mm, "end": v(-44.02, -19.06) * mm});
            skLineSegment(sketch, "E1264", {"start": v(-44.02, -19.06) * mm, "end": v(-43.94, -19.23) * mm});
            skLineSegment(sketch, "E1265", {"start": v(-43.94, -19.23) * mm, "end": v(-43.85, -19.38) * mm});
            skLineSegment(sketch, "E1266", {"start": v(-43.85, -19.38) * mm, "end": v(-43.75, -19.53) * mm});
            skLineSegment(sketch, "E1267", {"start": v(-43.75, -19.53) * mm, "end": v(-43.64, -19.66) * mm});
            skLineSegment(sketch, "E1268", {"start": v(-43.64, -19.66) * mm, "end": v(-43.53, -19.8) * mm});
            skLineSegment(sketch, "E1269", {"start": v(-43.53, -19.8) * mm, "end": v(-43.01, -20.3) * mm});
            skLineSegment(sketch, "E1270", {"start": v(-43.01, -20.3) * mm, "end": v(-42.1, -20.3) * mm});
            skLineSegment(sketch, "E1271", {"start": v(-64.01, -14.34) * mm, "end": v(-63.6, -14.17) * mm});
            skLineSegment(sketch, "E1272", {"start": v(-63.6, -14.17) * mm, "end": v(-63.17, -13.98) * mm});
            skLineSegment(sketch, "E1273", {"start": v(-63.17, -13.98) * mm, "end": v(-62.95, -13.89) * mm});
            skLineSegment(sketch, "E1274", {"start": v(-62.95, -13.89) * mm, "end": v(-62.74, -13.79) * mm});
            skLineSegment(sketch, "E1275", {"start": v(-62.74, -13.79) * mm, "end": v(-62.54, -13.68) * mm});
            skLineSegment(sketch, "E1276", {"start": v(-62.54, -13.68) * mm, "end": v(-62.36, -13.57) * mm});
            skLineSegment(sketch, "E1277", {"start": v(-62.36, -13.57) * mm, "end": v(-61.94, -13.25) * mm});
            skLineSegment(sketch, "E1278", {"start": v(-61.94, -13.25) * mm, "end": v(-61.5, -12.9) * mm});
            skLineSegment(sketch, "E1279", {"start": v(-61.5, -12.9) * mm, "end": v(-61.07, -12.51) * mm});
            skLineSegment(sketch, "E1280", {"start": v(-61.07, -12.51) * mm, "end": v(-60.64, -12.1) * mm});
            skLineSegment(sketch, "E1281", {"start": v(-60.64, -12.1) * mm, "end": v(-60.23, -11.68) * mm});
            skLineSegment(sketch, "E1282", {"start": v(-60.23, -11.68) * mm, "end": v(-59.84, -11.24) * mm});
            skLineSegment(sketch, "E1283", {"start": v(-59.84, -11.24) * mm, "end": v(-59.49, -10.81) * mm});
            skLineSegment(sketch, "E1284", {"start": v(-59.49, -10.81) * mm, "end": v(-59.18, -10.4) * mm});
            skLineSegment(sketch, "E1285", {"start": v(-59.18, -10.4) * mm, "end": v(-58.86, -9.91) * mm});
            skLineSegment(sketch, "E1286", {"start": v(-58.86, -9.91) * mm, "end": v(-58.55, -9.4) * mm});
            skLineSegment(sketch, "E1287", {"start": v(-58.55, -9.4) * mm, "end": v(-58.25, -8.84) * mm});
            skLineSegment(sketch, "E1288", {"start": v(-58.25, -8.84) * mm, "end": v(-57.97, -8.26) * mm});
            skLineSegment(sketch, "E1289", {"start": v(-57.97, -8.26) * mm, "end": v(-57.71, -7.67) * mm});
            skLineSegment(sketch, "E1290", {"start": v(-57.71, -7.67) * mm, "end": v(-57.48, -7.08) * mm});
            skLineSegment(sketch, "E1291", {"start": v(-57.48, -7.08) * mm, "end": v(-57.38, -6.8) * mm});
            skLineSegment(sketch, "E1292", {"start": v(-57.38, -6.8) * mm, "end": v(-57.29, -6.5) * mm});
            skLineSegment(sketch, "E1293", {"start": v(-57.29, -6.5) * mm, "end": v(-57.2, -6.23) * mm});
            skLineSegment(sketch, "E1294", {"start": v(-57.2, -6.23) * mm, "end": v(-57.14, -5.95) * mm});
            skLineSegment(sketch, "E1295", {"start": v(-57.14, -5.95) * mm, "end": v(-56.92, -5.03) * mm});
            skLineSegment(sketch, "E1296", {"start": v(-56.92, -5.03) * mm, "end": v(-56.81, -4.51) * mm});
            skLineSegment(sketch, "E1297", {"start": v(-56.81, -4.51) * mm, "end": v(-56.7, -3.98) * mm});
            skLineSegment(sketch, "E1298", {"start": v(-56.7, -3.98) * mm, "end": v(-56.6, -3.42) * mm});
            skLineSegment(sketch, "E1299", {"start": v(-56.6, -3.42) * mm, "end": v(-56.52, -2.86) * mm});
            skLineSegment(sketch, "E1300", {"start": v(-56.52, -2.86) * mm, "end": v(-56.44, -2.3) * mm});
            skLineSegment(sketch, "E1301", {"start": v(-56.44, -2.3) * mm, "end": v(-56.38, -1.73) * mm});
            skLineSegment(sketch, "E1302", {"start": v(-56.38, -1.73) * mm, "end": v(-56.33, -1.18) * mm});
            skLineSegment(sketch, "E1303", {"start": v(-56.33, -1.18) * mm, "end": v(-56.31, -0.65) * mm});
            skLineSegment(sketch, "E1304", {"start": v(-56.31, -0.65) * mm, "end": v(-56.32, -0.14) * mm});
            skLineSegment(sketch, "E1305", {"start": v(-56.32, -0.14) * mm, "end": v(-56.33, 0.1) * mm});
            skLineSegment(sketch, "E1306", {"start": v(-56.33, 0.1) * mm, "end": v(-56.35, 0.34) * mm});
            skLineSegment(sketch, "E1307", {"start": v(-56.35, 0.34) * mm, "end": v(-56.38, 0.57) * mm});
            skLineSegment(sketch, "E1308", {"start": v(-56.38, 0.57) * mm, "end": v(-56.42, 0.78) * mm});
            skLineSegment(sketch, "E1309", {"start": v(-56.42, 0.78) * mm, "end": v(-56.46, 0.98) * mm});
            skLineSegment(sketch, "E1310", {"start": v(-56.46, 0.98) * mm, "end": v(-56.52, 1.17) * mm});
            skLineSegment(sketch, "E1311", {"start": v(-56.52, 1.17) * mm, "end": v(-56.58, 1.35) * mm});
            skLineSegment(sketch, "E1312", {"start": v(-56.58, 1.35) * mm, "end": v(-56.65, 1.52) * mm});
            skLineSegment(sketch, "E1313", {"start": v(-56.65, 1.52) * mm, "end": v(-56.74, 1.67) * mm});
            skLineSegment(sketch, "E1314", {"start": v(-56.74, 1.67) * mm, "end": v(-56.84, 1.8) * mm});
            skLineSegment(sketch, "E1315", {"start": v(-56.84, 1.8) * mm, "end": v(-56.86, 1.82) * mm});
            skLineSegment(sketch, "E1316", {"start": v(-56.86, 1.82) * mm, "end": v(-56.88, 1.82) * mm});
            skLineSegment(sketch, "E1317", {"start": v(-56.88, 1.82) * mm, "end": v(-56.95, 1.82) * mm});
            skLineSegment(sketch, "E1318", {"start": v(-56.95, 1.82) * mm, "end": v(-57.02, 1.8) * mm});
            skLineSegment(sketch, "E1319", {"start": v(-57.02, 1.8) * mm, "end": v(-57.08, 1.8) * mm});
            skLineSegment(sketch, "E1320", {"start": v(-57.08, 1.8) * mm, "end": v(-57.11, 1.8) * mm});
            skLineSegment(sketch, "E1321", {"start": v(-57.11, 1.8) * mm, "end": v(-57.17, 1.76) * mm});
            skLineSegment(sketch, "E1322", {"start": v(-57.17, 1.76) * mm, "end": v(-57.32, 1.66) * mm});
            skLineSegment(sketch, "E1323", {"start": v(-57.32, 1.66) * mm, "end": v(-57.54, 1.5) * mm});
            skLineSegment(sketch, "E1324", {"start": v(-57.54, 1.5) * mm, "end": v(-57.81, 1.28) * mm});
            skLineSegment(sketch, "E1325", {"start": v(-57.81, 1.28) * mm, "end": v(-58.47, 0.72) * mm});
            skLineSegment(sketch, "E1326", {"start": v(-58.47, 0.72) * mm, "end": v(-59.24, 0.03) * mm});
            skLineSegment(sketch, "E1327", {"start": v(-59.24, 0.03) * mm, "end": v(-59.69, -0.41) * mm});
            skLineSegment(sketch, "E1328", {"start": v(-59.69, -0.41) * mm, "end": v(-60.17, -0.9) * mm});
            skLineSegment(sketch, "E1329", {"start": v(-60.17, -0.9) * mm, "end": v(-60.41, -1.13) * mm});
            skLineSegment(sketch, "E1330", {"start": v(-60.41, -1.13) * mm, "end": v(-60.66, -1.36) * mm});
            skLineSegment(sketch, "E1331", {"start": v(-60.66, -1.36) * mm, "end": v(-60.9, -1.56) * mm});
            skLineSegment(sketch, "E1332", {"start": v(-60.9, -1.56) * mm, "end": v(-61.15, -1.74) * mm});
            skLineSegment(sketch, "E1333", {"start": v(-61.15, -1.74) * mm, "end": v(-61.47, -1.95) * mm});
            skLineSegment(sketch, "E1334", {"start": v(-61.47, -1.95) * mm, "end": v(-61.82, -2.16) * mm});
            skLineSegment(sketch, "E1335", {"start": v(-61.82, -2.16) * mm, "end": v(-62.18, -2.36) * mm});
            skLineSegment(sketch, "E1336", {"start": v(-62.18, -2.36) * mm, "end": v(-62.57, -2.56) * mm});
            skLineSegment(sketch, "E1337", {"start": v(-62.57, -2.56) * mm, "end": v(-62.95, -2.74) * mm});
            skLineSegment(sketch, "E1338", {"start": v(-62.95, -2.74) * mm, "end": v(-63.34, -2.9) * mm});
            skLineSegment(sketch, "E1339", {"start": v(-63.34, -2.9) * mm, "end": v(-63.72, -3.04) * mm});
            skLineSegment(sketch, "E1340", {"start": v(-63.72, -3.04) * mm, "end": v(-64.08, -3.16) * mm});
            skLineSegment(sketch, "E1341", {"start": v(-64.08, -3.16) * mm, "end": v(-64.3, -3.21) * mm});
            skLineSegment(sketch, "E1342", {"start": v(-64.3, -3.21) * mm, "end": v(-64.54, -3.24) * mm});
            skLineSegment(sketch, "E1343", {"start": v(-64.54, -3.24) * mm, "end": v(-64.79, -3.26) * mm});
            skLineSegment(sketch, "E1344", {"start": v(-64.79, -3.26) * mm, "end": v(-65.05, -3.26) * mm});
            skLineSegment(sketch, "E1345", {"start": v(-65.05, -3.26) * mm, "end": v(-65.6, -3.24) * mm});
            skLineSegment(sketch, "E1346", {"start": v(-65.6, -3.24) * mm, "end": v(-66.14, -3.2) * mm});
            skLineSegment(sketch, "E1347", {"start": v(-66.14, -3.2) * mm, "end": v(-66.42, -3.2) * mm});
            skLineSegment(sketch, "E1348", {"start": v(-66.42, -3.2) * mm, "end": v(-66.68, -3.2) * mm});
            skLineSegment(sketch, "E1349", {"start": v(-66.68, -3.2) * mm, "end": v(-66.94, -3.22) * mm});
            skLineSegment(sketch, "E1350", {"start": v(-66.94, -3.22) * mm, "end": v(-67.18, -3.26) * mm});
            skLineSegment(sketch, "E1351", {"start": v(-67.18, -3.26) * mm, "end": v(-67.4, -3.31) * mm});
            skLineSegment(sketch, "E1352", {"start": v(-67.4, -3.31) * mm, "end": v(-67.51, -3.35) * mm});
            skLineSegment(sketch, "E1353", {"start": v(-67.51, -3.35) * mm, "end": v(-67.62, -3.4) * mm});
            skLineSegment(sketch, "E1354", {"start": v(-67.62, -3.4) * mm, "end": v(-67.71, -3.44) * mm});
            skLineSegment(sketch, "E1355", {"start": v(-67.71, -3.44) * mm, "end": v(-67.8, -3.5) * mm});
            skLineSegment(sketch, "E1356", {"start": v(-67.8, -3.5) * mm, "end": v(-67.9, -3.57) * mm});
            skLineSegment(sketch, "E1357", {"start": v(-67.9, -3.57) * mm, "end": v(-67.97, -3.65) * mm});
            skLineSegment(sketch, "E1358", {"start": v(-67.97, -3.65) * mm, "end": v(-68.08, -3.77) * mm});
            skLineSegment(sketch, "E1359", {"start": v(-68.08, -3.77) * mm, "end": v(-68.18, -3.9) * mm});
            skLineSegment(sketch, "E1360", {"start": v(-68.18, -3.9) * mm, "end": v(-68.26, -4.05) * mm});
            skLineSegment(sketch, "E1361", {"start": v(-68.26, -4.05) * mm, "end": v(-68.34, -4.2) * mm});
            skLineSegment(sketch, "E1362", {"start": v(-68.34, -4.2) * mm, "end": v(-68.4, -4.36) * mm});
            skLineSegment(sketch, "E1363", {"start": v(-68.4, -4.36) * mm, "end": v(-68.46, -4.52) * mm});
            skLineSegment(sketch, "E1364", {"start": v(-68.46, -4.52) * mm, "end": v(-68.51, -4.7) * mm});
            skLineSegment(sketch, "E1365", {"start": v(-68.51, -4.7) * mm, "end": v(-68.55, -4.87) * mm});
            skLineSegment(sketch, "E1366", {"start": v(-68.55, -4.87) * mm, "end": v(-68.58, -5.05) * mm});
            skLineSegment(sketch, "E1367", {"start": v(-68.58, -5.05) * mm, "end": v(-68.6, -5.24) * mm});
            skLineSegment(sketch, "E1368", {"start": v(-68.6, -5.24) * mm, "end": v(-68.64, -5.62) * mm});
            skLineSegment(sketch, "E1369", {"start": v(-68.64, -5.62) * mm, "end": v(-68.64, -6.02) * mm});
            skLineSegment(sketch, "E1370", {"start": v(-68.64, -6.02) * mm, "end": v(-68.63, -6.43) * mm});
            skLineSegment(sketch, "E1371", {"start": v(-68.63, -6.43) * mm, "end": v(-68.6, -6.85) * mm});
            skLineSegment(sketch, "E1372", {"start": v(-68.6, -6.85) * mm, "end": v(-68.57, -7.26) * mm});
            skLineSegment(sketch, "E1373", {"start": v(-68.57, -7.26) * mm, "end": v(-68.49, -8.09) * mm});
            skLineSegment(sketch, "E1374", {"start": v(-68.49, -8.09) * mm, "end": v(-68.41, -8.87) * mm});
            skLineSegment(sketch, "E1375", {"start": v(-68.41, -8.87) * mm, "end": v(-68.39, -9.24) * mm});
            skLineSegment(sketch, "E1376", {"start": v(-68.39, -9.24) * mm, "end": v(-68.38, -9.58) * mm});
            skLineSegment(sketch, "E1377", {"start": v(-68.38, -9.58) * mm, "end": v(-68.39, -9.94) * mm});
            skLineSegment(sketch, "E1378", {"start": v(-68.39, -9.94) * mm, "end": v(-68.4, -10.33) * mm});
            skLineSegment(sketch, "E1379", {"start": v(-68.4, -10.33) * mm, "end": v(-68.46, -11.17) * mm});
            skLineSegment(sketch, "E1380", {"start": v(-68.46, -11.17) * mm, "end": v(-68.52, -12.05) * mm});
            skLineSegment(sketch, "E1381", {"start": v(-68.52, -12.05) * mm, "end": v(-68.54, -12.5) * mm});
            skLineSegment(sketch, "E1382", {"start": v(-68.54, -12.5) * mm, "end": v(-68.56, -12.94) * mm});
            skLineSegment(sketch, "E1383", {"start": v(-68.56, -12.94) * mm, "end": v(-68.56, -13.37) * mm});
            skLineSegment(sketch, "E1384", {"start": v(-68.56, -13.37) * mm, "end": v(-68.55, -13.79) * mm});
            skLineSegment(sketch, "E1385", {"start": v(-68.55, -13.79) * mm, "end": v(-68.53, -14.18) * mm});
            skLineSegment(sketch, "E1386", {"start": v(-68.53, -14.18) * mm, "end": v(-68.48, -14.56) * mm});
            skLineSegment(sketch, "E1387", {"start": v(-68.48, -14.56) * mm, "end": v(-68.45, -14.73) * mm});
            skLineSegment(sketch, "E1388", {"start": v(-68.45, -14.73) * mm, "end": v(-68.41, -14.9) * mm});
            skLineSegment(sketch, "E1389", {"start": v(-68.41, -14.9) * mm, "end": v(-68.37, -15.06) * mm});
            skLineSegment(sketch, "E1390", {"start": v(-68.37, -15.06) * mm, "end": v(-68.32, -15.2) * mm});
            skLineSegment(sketch, "E1391", {"start": v(-68.32, -15.2) * mm, "end": v(-68.26, -15.34) * mm});
            skLineSegment(sketch, "E1392", {"start": v(-68.26, -15.34) * mm, "end": v(-68.2, -15.47) * mm});
            skLineSegment(sketch, "E1393", {"start": v(-68.2, -15.47) * mm, "end": v(-68.12, -15.59) * mm});
            skLineSegment(sketch, "E1394", {"start": v(-68.12, -15.59) * mm, "end": v(-68.04, -15.69) * mm});
            skLineSegment(sketch, "E1395", {"start": v(-68.04, -15.69) * mm, "end": v(-68, -15.71) * mm});
            skLineSegment(sketch, "E1396", {"start": v(-68, -15.71) * mm, "end": v(-67.96, -15.72) * mm});
            skLineSegment(sketch, "E1397", {"start": v(-67.96, -15.72) * mm, "end": v(-67.87, -15.7) * mm});
            skLineSegment(sketch, "E1398", {"start": v(-67.87, -15.7) * mm, "end": v(-67.77, -15.68) * mm});
            skLineSegment(sketch, "E1399", {"start": v(-67.77, -15.68) * mm, "end": v(-67.67, -15.66) * mm});
            skLineSegment(sketch, "E1400", {"start": v(-67.67, -15.66) * mm, "end": v(-67.4, -15.62) * mm});
            skLineSegment(sketch, "E1401", {"start": v(-67.4, -15.62) * mm, "end": v(-67.06, -15.54) * mm});
            skLineSegment(sketch, "E1402", {"start": v(-67.06, -15.54) * mm, "end": v(-66.66, -15.43) * mm});
            skLineSegment(sketch, "E1403", {"start": v(-66.66, -15.43) * mm, "end": v(-66.22, -15.28) * mm});
            skLineSegment(sketch, "E1404", {"start": v(-66.22, -15.28) * mm, "end": v(-65.73, -15.1) * mm});
            skLineSegment(sketch, "E1405", {"start": v(-65.73, -15.1) * mm, "end": v(-65.2, -14.87) * mm});
            skLineSegment(sketch, "E1406", {"start": v(-65.2, -14.87) * mm, "end": v(-64.62, -14.62) * mm});
            skLineSegment(sketch, "E1407", {"start": v(-64.62, -14.62) * mm, "end": v(-64.01, -14.34) * mm});
            skLineSegment(sketch, "E1408", {"start": v(-44.21, -15.36) * mm, "end": v(-43.83, -15.32) * mm});
            skLineSegment(sketch, "E1409", {"start": v(-43.83, -15.32) * mm, "end": v(-43.04, -15.21) * mm});
            skLineSegment(sketch, "E1410", {"start": v(-43.04, -15.21) * mm, "end": v(-41.95, -15.06) * mm});
            skLineSegment(sketch, "E1411", {"start": v(-41.95, -15.06) * mm, "end": v(-40.68, -14.87) * mm});
            skLineSegment(sketch, "E1412", {"start": v(-40.68, -14.87) * mm, "end": v(-37.48, -14.39) * mm});
            skLineSegment(sketch, "E1413", {"start": v(-37.48, -14.39) * mm, "end": v(-33, -12.36) * mm});
            skLineSegment(sketch, "E1414", {"start": v(-33, -12.36) * mm, "end": v(-31.9, -11.3) * mm});
            skLineSegment(sketch, "E1415", {"start": v(-31.9, -11.3) * mm, "end": v(-31.66, -11.07) * mm});
            skLineSegment(sketch, "E1416", {"start": v(-31.66, -11.07) * mm, "end": v(-31.43, -10.82) * mm});
            skLineSegment(sketch, "E1417", {"start": v(-31.43, -10.82) * mm, "end": v(-31.2, -10.55) * mm});
            skLineSegment(sketch, "E1418", {"start": v(-31.2, -10.55) * mm, "end": v(-30.97, -10.28) * mm});
            skLineSegment(sketch, "E1419", {"start": v(-30.97, -10.28) * mm, "end": v(-30.76, -10.01) * mm});
            skLineSegment(sketch, "E1420", {"start": v(-30.76, -10.01) * mm, "end": v(-30.58, -9.76) * mm});
            skLineSegment(sketch, "E1421", {"start": v(-30.58, -9.76) * mm, "end": v(-30.42, -9.52) * mm});
            skLineSegment(sketch, "E1422", {"start": v(-30.42, -9.52) * mm, "end": v(-30.3, -9.31) * mm});
            skLineSegment(sketch, "E1423", {"start": v(-30.3, -9.31) * mm, "end": v(-29.82, -8.38) * mm});
            skLineSegment(sketch, "E1424", {"start": v(-29.82, -8.38) * mm, "end": v(-31.5, -6.81) * mm});
            skLineSegment(sketch, "E1425", {"start": v(-31.5, -6.81) * mm, "end": v(-31.5, -5.79) * mm});
            skLineSegment(sketch, "E1426", {"start": v(-31.5, -5.79) * mm, "end": v(-31.85, -5.79) * mm});
            skLineSegment(sketch, "E1427", {"start": v(-31.85, -5.79) * mm, "end": v(-31.94, -5.8) * mm});
            skLineSegment(sketch, "E1428", {"start": v(-31.94, -5.8) * mm, "end": v(-32.06, -5.83) * mm});
            skLineSegment(sketch, "E1429", {"start": v(-32.06, -5.83) * mm, "end": v(-32.36, -5.92) * mm});
            skLineSegment(sketch, "E1430", {"start": v(-32.36, -5.92) * mm, "end": v(-32.72, -6.07) * mm});
            skLineSegment(sketch, "E1431", {"start": v(-32.72, -6.07) * mm, "end": v(-33.1, -6.24) * mm});
            skLineSegment(sketch, "E1432", {"start": v(-33.1, -6.24) * mm, "end": v(-33.32, -6.35) * mm});
            skLineSegment(sketch, "E1433", {"start": v(-33.32, -6.35) * mm, "end": v(-33.62, -6.46) * mm});
            skLineSegment(sketch, "E1434", {"start": v(-33.62, -6.46) * mm, "end": v(-33.99, -6.59) * mm});
            skLineSegment(sketch, "E1435", {"start": v(-33.99, -6.59) * mm, "end": v(-34.4, -6.72) * mm});
            skLineSegment(sketch, "E1436", {"start": v(-34.4, -6.72) * mm, "end": v(-34.86, -6.85) * mm});
            skLineSegment(sketch, "E1437", {"start": v(-34.86, -6.85) * mm, "end": v(-35.34, -6.99) * mm});
            skLineSegment(sketch, "E1438", {"start": v(-35.34, -6.99) * mm, "end": v(-35.83, -7.11) * mm});
            skLineSegment(sketch, "E1439", {"start": v(-35.83, -7.11) * mm, "end": v(-36.32, -7.23) * mm});
            skLineSegment(sketch, "E1440", {"start": v(-36.32, -7.23) * mm, "end": v(-38.66, -7.75) * mm});
            skLineSegment(sketch, "E1441", {"start": v(-38.66, -7.75) * mm, "end": v(-47.96, -8.55) * mm});
            skLineSegment(sketch, "E1442", {"start": v(-47.96, -8.55) * mm, "end": v(-48.14, -9.23) * mm});
            skLineSegment(sketch, "E1443", {"start": v(-48.14, -9.23) * mm, "end": v(-48.18, -9.4) * mm});
            skLineSegment(sketch, "E1444", {"start": v(-48.18, -9.4) * mm, "end": v(-48.22, -9.58) * mm});
            skLineSegment(sketch, "E1445", {"start": v(-48.22, -9.58) * mm, "end": v(-48.28, -10.02) * mm});
            skLineSegment(sketch, "E1446", {"start": v(-48.28, -10.02) * mm, "end": v(-48.32, -10.5) * mm});
            skLineSegment(sketch, "E1447", {"start": v(-48.32, -10.5) * mm, "end": v(-48.33, -10.96) * mm});
            skLineSegment(sketch, "E1448", {"start": v(-48.33, -10.96) * mm, "end": v(-48.34, -12) * mm});
            skLineSegment(sketch, "E1449", {"start": v(-48.34, -12) * mm, "end": v(-47.44, -13.07) * mm});
            skLineSegment(sketch, "E1450", {"start": v(-47.44, -13.07) * mm, "end": v(-47.27, -13.27) * mm});
            skLineSegment(sketch, "E1451", {"start": v(-47.27, -13.27) * mm, "end": v(-47.07, -13.48) * mm});
            skLineSegment(sketch, "E1452", {"start": v(-47.07, -13.48) * mm, "end": v(-46.86, -13.68) * mm});
            skLineSegment(sketch, "E1453", {"start": v(-46.86, -13.68) * mm, "end": v(-46.64, -13.88) * mm});
            skLineSegment(sketch, "E1454", {"start": v(-46.64, -13.88) * mm, "end": v(-46.42, -14.07) * mm});
            skLineSegment(sketch, "E1455", {"start": v(-46.42, -14.07) * mm, "end": v(-46.19, -14.26) * mm});
            skLineSegment(sketch, "E1456", {"start": v(-46.19, -14.26) * mm, "end": v(-45.95, -14.44) * mm});
            skLineSegment(sketch, "E1457", {"start": v(-45.95, -14.44) * mm, "end": v(-45.72, -14.61) * mm});
            skLineSegment(sketch, "E1458", {"start": v(-45.72, -14.61) * mm, "end": v(-45.49, -14.77) * mm});
            skLineSegment(sketch, "E1459", {"start": v(-45.49, -14.77) * mm, "end": v(-45.27, -14.92) * mm});
            skLineSegment(sketch, "E1460", {"start": v(-45.27, -14.92) * mm, "end": v(-45.05, -15.04) * mm});
            skLineSegment(sketch, "E1461", {"start": v(-45.05, -15.04) * mm, "end": v(-44.85, -15.15) * mm});
            skLineSegment(sketch, "E1462", {"start": v(-44.85, -15.15) * mm, "end": v(-44.66, -15.24) * mm});
            skLineSegment(sketch, "E1463", {"start": v(-44.66, -15.24) * mm, "end": v(-44.49, -15.3) * mm});
            skLineSegment(sketch, "E1464", {"start": v(-44.49, -15.3) * mm, "end": v(-44.34, -15.34) * mm});
            skLineSegment(sketch, "E1465", {"start": v(-44.34, -15.34) * mm, "end": v(-44.21, -15.36) * mm});
            skLineSegment(sketch, "E1466", {"start": v(80.88, -12.33) * mm, "end": v(81.26, -12) * mm});
            skLineSegment(sketch, "E1467", {"start": v(81.26, -12) * mm, "end": v(81.68, -11.64) * mm});
            skLineSegment(sketch, "E1468", {"start": v(81.68, -11.64) * mm, "end": v(82.09, -11.27) * mm});
            skLineSegment(sketch, "E1469", {"start": v(82.09, -11.27) * mm, "end": v(82.27, -11.09) * mm});
            skLineSegment(sketch, "E1470", {"start": v(82.27, -11.09) * mm, "end": v(82.44, -10.9) * mm});
            skLineSegment(sketch, "E1471", {"start": v(82.44, -10.9) * mm, "end": v(82.58, -10.72) * mm});
            skLineSegment(sketch, "E1472", {"start": v(82.58, -10.72) * mm, "end": v(82.73, -10.51) * mm});
            skLineSegment(sketch, "E1473", {"start": v(82.73, -10.51) * mm, "end": v(83.01, -10.07) * mm});
            skLineSegment(sketch, "E1474", {"start": v(83.01, -10.07) * mm, "end": v(83.28, -9.61) * mm});
            skLineSegment(sketch, "E1475", {"start": v(83.28, -9.61) * mm, "end": v(83.54, -9.2) * mm});
            skLineSegment(sketch, "E1476", {"start": v(83.54, -9.2) * mm, "end": v(83.78, -8.8) * mm});
            skLineSegment(sketch, "E1477", {"start": v(83.78, -8.8) * mm, "end": v(84.01, -8.41) * mm});
            skLineSegment(sketch, "E1478", {"start": v(84.01, -8.41) * mm, "end": v(84.24, -8) * mm});
            skLineSegment(sketch, "E1479", {"start": v(84.24, -8) * mm, "end": v(84.46, -7.6) * mm});
            skLineSegment(sketch, "E1480", {"start": v(84.46, -7.6) * mm, "end": v(84.68, -7.17) * mm});
            skLineSegment(sketch, "E1481", {"start": v(84.68, -7.17) * mm, "end": v(84.88, -6.74) * mm});
            skLineSegment(sketch, "E1482", {"start": v(84.88, -6.74) * mm, "end": v(85.08, -6.3) * mm});
            skLineSegment(sketch, "E1483", {"start": v(85.08, -6.3) * mm, "end": v(85.28, -5.84) * mm});
            skLineSegment(sketch, "E1484", {"start": v(85.28, -5.84) * mm, "end": v(85.47, -5.37) * mm});
            skLineSegment(sketch, "E1485", {"start": v(85.47, -5.37) * mm, "end": v(85.65, -4.88) * mm});
            skLineSegment(sketch, "E1486", {"start": v(85.65, -4.88) * mm, "end": v(85.83, -4.39) * mm});
            skLineSegment(sketch, "E1487", {"start": v(85.83, -4.39) * mm, "end": v(86, -3.87) * mm});
            skLineSegment(sketch, "E1488", {"start": v(86, -3.87) * mm, "end": v(86.18, -3.35) * mm});
            skLineSegment(sketch, "E1489", {"start": v(86.18, -3.35) * mm, "end": v(86.34, -2.8) * mm});
            skLineSegment(sketch, "E1490", {"start": v(86.34, -2.8) * mm, "end": v(86.5, -2.24) * mm});
            skLineSegment(sketch, "E1491", {"start": v(86.5, -2.24) * mm, "end": v(86.66, -1.66) * mm});
            skLineSegment(sketch, "E1492", {"start": v(86.66, -1.66) * mm, "end": v(86.82, -1.11) * mm});
            skLineSegment(sketch, "E1493", {"start": v(86.82, -1.11) * mm, "end": v(87, -0.52) * mm});
            skLineSegment(sketch, "E1494", {"start": v(87, -0.52) * mm, "end": v(87.16, 0.08) * mm});
            skLineSegment(sketch, "E1495", {"start": v(87.16, 0.08) * mm, "end": v(87.22, 0.37) * mm});
            skLineSegment(sketch, "E1496", {"start": v(87.22, 0.37) * mm, "end": v(87.27, 0.64) * mm});
            skLineSegment(sketch, "E1497", {"start": v(87.27, 0.64) * mm, "end": v(87.34, 1.07) * mm});
            skLineSegment(sketch, "E1498", {"start": v(87.34, 1.07) * mm, "end": v(87.39, 1.5) * mm});
            skLineSegment(sketch, "E1499", {"start": v(87.39, 1.5) * mm, "end": v(87.47, 2.42) * mm});
            skLineSegment(sketch, "E1500", {"start": v(87.47, 2.42) * mm, "end": v(87.53, 3.37) * mm});
            skLineSegment(sketch, "E1501", {"start": v(87.53, 3.37) * mm, "end": v(87.58, 4.35) * mm});
            skLineSegment(sketch, "E1502", {"start": v(87.58, 4.35) * mm, "end": v(87.64, 6.28) * mm});
            skLineSegment(sketch, "E1503", {"start": v(87.64, 6.28) * mm, "end": v(87.67, 7.2) * mm});
            skLineSegment(sketch, "E1504", {"start": v(87.67, 7.2) * mm, "end": v(87.71, 8.07) * mm});
            skLineSegment(sketch, "E1505", {"start": v(87.71, 8.07) * mm, "end": v(87.61, 8.08) * mm});
            skLineSegment(sketch, "E1506", {"start": v(87.61, 8.08) * mm, "end": v(87.5, 8.09) * mm});
            skLineSegment(sketch, "E1507", {"start": v(87.5, 8.09) * mm, "end": v(87.4, 8.09) * mm});
            skLineSegment(sketch, "E1508", {"start": v(87.4, 8.09) * mm, "end": v(87.34, 8.08) * mm});
            skLineSegment(sketch, "E1509", {"start": v(87.34, 8.08) * mm, "end": v(87.3, 8.07) * mm});
            skLineSegment(sketch, "E1510", {"start": v(87.3, 8.07) * mm, "end": v(87.02, 7.94) * mm});
            skLineSegment(sketch, "E1511", {"start": v(87.02, 7.94) * mm, "end": v(86.74, 7.8) * mm});
            skLineSegment(sketch, "E1512", {"start": v(86.74, 7.8) * mm, "end": v(86.46, 7.64) * mm});
            skLineSegment(sketch, "E1513", {"start": v(86.46, 7.64) * mm, "end": v(86.2, 7.46) * mm});
            skLineSegment(sketch, "E1514", {"start": v(86.2, 7.46) * mm, "end": v(85.93, 7.27) * mm});
            skLineSegment(sketch, "E1515", {"start": v(85.93, 7.27) * mm, "end": v(85.67, 7.07) * mm});
            skLineSegment(sketch, "E1516", {"start": v(85.67, 7.07) * mm, "end": v(85.41, 6.85) * mm});
            skLineSegment(sketch, "E1517", {"start": v(85.41, 6.85) * mm, "end": v(85.16, 6.62) * mm});
            skLineSegment(sketch, "E1518", {"start": v(85.16, 6.62) * mm, "end": v(84.9, 6.38) * mm});
            skLineSegment(sketch, "E1519", {"start": v(84.9, 6.38) * mm, "end": v(84.66, 6.14) * mm});
            skLineSegment(sketch, "E1520", {"start": v(84.66, 6.14) * mm, "end": v(84.17, 5.62) * mm});
            skLineSegment(sketch, "E1521", {"start": v(84.17, 5.62) * mm, "end": v(83.7, 5.07) * mm});
            skLineSegment(sketch, "E1522", {"start": v(83.7, 5.07) * mm, "end": v(83.22, 4.5) * mm});
            skLineSegment(sketch, "E1523", {"start": v(83.22, 4.5) * mm, "end": v(82.3, 3.36) * mm});
            skLineSegment(sketch, "E1524", {"start": v(82.3, 3.36) * mm, "end": v(81.84, 2.8) * mm});
            skLineSegment(sketch, "E1525", {"start": v(81.84, 2.8) * mm, "end": v(81.38, 2.24) * mm});
            skLineSegment(sketch, "E1526", {"start": v(81.38, 2.24) * mm, "end": v(80.93, 1.7) * mm});
            skLineSegment(sketch, "E1527", {"start": v(80.93, 1.7) * mm, "end": v(80.46, 1.2) * mm});
            skLineSegment(sketch, "E1528", {"start": v(80.46, 1.2) * mm, "end": v(80.23, 0.96) * mm});
            skLineSegment(sketch, "E1529", {"start": v(80.23, 0.96) * mm, "end": v(80, 0.73) * mm});
            skLineSegment(sketch, "E1530", {"start": v(80, 0.73) * mm, "end": v(79.76, 0.52) * mm});
            skLineSegment(sketch, "E1531", {"start": v(79.76, 0.52) * mm, "end": v(79.53, 0.31) * mm});
            skLineSegment(sketch, "E1532", {"start": v(79.53, 0.31) * mm, "end": v(79, -0.1) * mm});
            skLineSegment(sketch, "E1533", {"start": v(79, -0.1) * mm, "end": v(78.41, -0.53) * mm});
            skLineSegment(sketch, "E1534", {"start": v(78.41, -0.53) * mm, "end": v(77.8, -0.96) * mm});
            skLineSegment(sketch, "E1535", {"start": v(77.8, -0.96) * mm, "end": v(77.16, -1.38) * mm});
            skLineSegment(sketch, "E1536", {"start": v(77.16, -1.38) * mm, "end": v(75.89, -2.2) * mm});
            skLineSegment(sketch, "E1537", {"start": v(75.89, -2.2) * mm, "end": v(75.28, -2.6) * mm});
            skLineSegment(sketch, "E1538", {"start": v(75.28, -2.6) * mm, "end": v(74.72, -2.98) * mm});
            skLineSegment(sketch, "E1539", {"start": v(74.72, -2.98) * mm, "end": v(74.9, -4.63) * mm});
            skLineSegment(sketch, "E1540", {"start": v(74.9, -4.63) * mm, "end": v(74.93, -5.06) * mm});
            skLineSegment(sketch, "E1541", {"start": v(74.93, -5.06) * mm, "end": v(74.96, -5.62) * mm});
            skLineSegment(sketch, "E1542", {"start": v(74.96, -5.62) * mm, "end": v(75.02, -7.08) * mm});
            skLineSegment(sketch, "E1543", {"start": v(75.02, -7.08) * mm, "end": v(75.06, -8.83) * mm});
            skLineSegment(sketch, "E1544", {"start": v(75.06, -8.83) * mm, "end": v(75.07, -10.66) * mm});
            skLineSegment(sketch, "E1545", {"start": v(75.07, -10.66) * mm, "end": v(75.07, -15.03) * mm});
            skLineSegment(sketch, "E1546", {"start": v(75.07, -15.03) * mm, "end": v(75.82, -15.02) * mm});
            skLineSegment(sketch, "E1547", {"start": v(75.82, -15.02) * mm, "end": v(76, -15) * mm});
            skLineSegment(sketch, "E1548", {"start": v(76, -15) * mm, "end": v(76.21, -14.97) * mm});
            skLineSegment(sketch, "E1549", {"start": v(76.21, -14.97) * mm, "end": v(76.47, -14.91) * mm});
            skLineSegment(sketch, "E1550", {"start": v(76.47, -14.91) * mm, "end": v(76.75, -14.83) * mm});
            skLineSegment(sketch, "E1551", {"start": v(76.75, -14.83) * mm, "end": v(77.04, -14.74) * mm});
            skLineSegment(sketch, "E1552", {"start": v(77.04, -14.74) * mm, "end": v(77.35, -14.63) * mm});
            skLineSegment(sketch, "E1553", {"start": v(77.35, -14.63) * mm, "end": v(77.65, -14.51) * mm});
            skLineSegment(sketch, "E1554", {"start": v(77.65, -14.51) * mm, "end": v(77.94, -14.39) * mm});
            skLineSegment(sketch, "E1555", {"start": v(77.94, -14.39) * mm, "end": v(78.28, -14.24) * mm});
            skLineSegment(sketch, "E1556", {"start": v(78.28, -14.24) * mm, "end": v(78.65, -14.1) * mm});
            skLineSegment(sketch, "E1557", {"start": v(78.65, -14.1) * mm, "end": v(79, -13.94) * mm});
            skLineSegment(sketch, "E1558", {"start": v(79, -13.94) * mm, "end": v(79.17, -13.85) * mm});
            skLineSegment(sketch, "E1559", {"start": v(79.17, -13.85) * mm, "end": v(79.32, -13.76) * mm});
            skLineSegment(sketch, "E1560", {"start": v(79.32, -13.76) * mm, "end": v(79.52, -13.61) * mm});
            skLineSegment(sketch, "E1561", {"start": v(79.52, -13.61) * mm, "end": v(79.72, -13.45) * mm});
            skLineSegment(sketch, "E1562", {"start": v(79.72, -13.45) * mm, "end": v(80.13, -13.07) * mm});
            skLineSegment(sketch, "E1563", {"start": v(80.13, -13.07) * mm, "end": v(80.51, -12.69) * mm});
            skLineSegment(sketch, "E1564", {"start": v(80.51, -12.69) * mm, "end": v(80.88, -12.33) * mm});
            skLineSegment(sketch, "E1565", {"start": v(70.43, -6.28) * mm, "end": v(70.32, -5.36) * mm});
            skLineSegment(sketch, "E1566", {"start": v(70.32, -5.36) * mm, "end": v(70.21, -4.36) * mm});
            skLineSegment(sketch, "E1567", {"start": v(70.21, -4.36) * mm, "end": v(70.15, -3.86) * mm});
            skLineSegment(sketch, "E1568", {"start": v(70.15, -3.86) * mm, "end": v(70.09, -3.36) * mm});
            skLineSegment(sketch, "E1569", {"start": v(70.09, -3.36) * mm, "end": v(70.02, -2.9) * mm});
            skLineSegment(sketch, "E1570", {"start": v(70.02, -2.9) * mm, "end": v(69.93, -2.45) * mm});
            skLineSegment(sketch, "E1571", {"start": v(69.93, -2.45) * mm, "end": v(69.86, -2.18) * mm});
            skLineSegment(sketch, "E1572", {"start": v(69.86, -2.18) * mm, "end": v(69.77, -1.9) * mm});
            skLineSegment(sketch, "E1573", {"start": v(69.77, -1.9) * mm, "end": v(69.33, -1.88) * mm});
            skLineSegment(sketch, "E1574", {"start": v(69.33, -1.88) * mm, "end": v(68.85, -1.87) * mm});
            skLineSegment(sketch, "E1575", {"start": v(68.85, -1.87) * mm, "end": v(67.85, -1.85) * mm});
            skLineSegment(sketch, "E1576", {"start": v(67.85, -1.85) * mm, "end": v(67.34, -1.83) * mm});
            skLineSegment(sketch, "E1577", {"start": v(67.34, -1.83) * mm, "end": v(66.85, -1.79) * mm});
            skLineSegment(sketch, "E1578", {"start": v(66.85, -1.79) * mm, "end": v(66.61, -1.76) * mm});
            skLineSegment(sketch, "E1579", {"start": v(66.61, -1.76) * mm, "end": v(66.38, -1.73) * mm});
            skLineSegment(sketch, "E1580", {"start": v(66.38, -1.73) * mm, "end": v(66.16, -1.68) * mm});
            skLineSegment(sketch, "E1581", {"start": v(66.16, -1.68) * mm, "end": v(65.94, -1.63) * mm});
            skLineSegment(sketch, "E1582", {"start": v(65.94, -1.63) * mm, "end": v(65.72, -1.56) * mm});
            skLineSegment(sketch, "E1583", {"start": v(65.72, -1.56) * mm, "end": v(65.5, -1.46) * mm});
            skLineSegment(sketch, "E1584", {"start": v(65.5, -1.46) * mm, "end": v(65.26, -1.35) * mm});
            skLineSegment(sketch, "E1585", {"start": v(65.26, -1.35) * mm, "end": v(65.03, -1.23) * mm});
            skLineSegment(sketch, "E1586", {"start": v(65.03, -1.23) * mm, "end": v(64.57, -0.98) * mm});
            skLineSegment(sketch, "E1587", {"start": v(64.57, -0.98) * mm, "end": v(64.15, -0.75) * mm});
            skLineSegment(sketch, "E1588", {"start": v(64.15, -0.75) * mm, "end": v(63.76, -0.55) * mm});
            skLineSegment(sketch, "E1589", {"start": v(63.76, -0.55) * mm, "end": v(63.34, -0.32) * mm});
            skLineSegment(sketch, "E1590", {"start": v(63.34, -0.32) * mm, "end": v(62.91, -0.06) * mm});
            skLineSegment(sketch, "E1591", {"start": v(62.91, -0.06) * mm, "end": v(62.48, 0.21) * mm});
            skLineSegment(sketch, "E1592", {"start": v(62.48, 0.21) * mm, "end": v(62.06, 0.5) * mm});
            skLineSegment(sketch, "E1593", {"start": v(62.06, 0.5) * mm, "end": v(61.66, 0.77) * mm});
            skLineSegment(sketch, "E1594", {"start": v(61.66, 0.77) * mm, "end": v(61.3, 1.04) * mm});
            skLineSegment(sketch, "E1595", {"start": v(61.3, 1.04) * mm, "end": v(60.99, 1.3) * mm});
            skLineSegment(sketch, "E1596", {"start": v(60.99, 1.3) * mm, "end": v(60.44, 1.75) * mm});
            skLineSegment(sketch, "E1597", {"start": v(60.44, 1.75) * mm, "end": v(59.95, 2.12) * mm});
            skLineSegment(sketch, "E1598", {"start": v(59.95, 2.12) * mm, "end": v(59.75, 2.26) * mm});
            skLineSegment(sketch, "E1599", {"start": v(59.75, 2.26) * mm, "end": v(59.58, 2.37) * mm});
            skLineSegment(sketch, "E1600", {"start": v(59.58, 2.37) * mm, "end": v(59.46, 2.44) * mm});
            skLineSegment(sketch, "E1601", {"start": v(59.46, 2.44) * mm, "end": v(59.38, 2.46) * mm});
            skLineSegment(sketch, "E1602", {"start": v(59.38, 2.46) * mm, "end": v(59.14, 2.46) * mm});
            skLineSegment(sketch, "E1603", {"start": v(59.14, 2.46) * mm, "end": v(59.18, 1.82) * mm});
            skLineSegment(sketch, "E1604", {"start": v(59.18, 1.82) * mm, "end": v(59.2, 1.15) * mm});
            skLineSegment(sketch, "E1605", {"start": v(59.2, 1.15) * mm, "end": v(59.26, -0.27) * mm});
            skLineSegment(sketch, "E1606", {"start": v(59.26, -0.27) * mm, "end": v(59.3, -0.99) * mm});
            skLineSegment(sketch, "E1607", {"start": v(59.3, -0.99) * mm, "end": v(59.35, -1.68) * mm});
            skLineSegment(sketch, "E1608", {"start": v(59.35, -1.68) * mm, "end": v(59.42, -2.36) * mm});
            skLineSegment(sketch, "E1609", {"start": v(59.42, -2.36) * mm, "end": v(59.46, -2.68) * mm});
            skLineSegment(sketch, "E1610", {"start": v(59.46, -2.68) * mm, "end": v(59.52, -2.98) * mm});
            skLineSegment(sketch, "E1611", {"start": v(59.52, -2.98) * mm, "end": v(59.6, -3.4) * mm});
            skLineSegment(sketch, "E1612", {"start": v(59.6, -3.4) * mm, "end": v(59.7, -3.82) * mm});
            skLineSegment(sketch, "E1613", {"start": v(59.7, -3.82) * mm, "end": v(59.81, -4.27) * mm});
            skLineSegment(sketch, "E1614", {"start": v(59.81, -4.27) * mm, "end": v(59.94, -4.72) * mm});
            skLineSegment(sketch, "E1615", {"start": v(59.94, -4.72) * mm, "end": v(60.08, -5.16) * mm});
            skLineSegment(sketch, "E1616", {"start": v(60.08, -5.16) * mm, "end": v(60.23, -5.6) * mm});
            skLineSegment(sketch, "E1617", {"start": v(60.23, -5.6) * mm, "end": v(60.4, -6) * mm});
            skLineSegment(sketch, "E1618", {"start": v(60.4, -6) * mm, "end": v(60.56, -6.38) * mm});
            skLineSegment(sketch, "E1619", {"start": v(60.56, -6.38) * mm, "end": v(60.8, -6.88) * mm});
            skLineSegment(sketch, "E1620", {"start": v(60.8, -6.88) * mm, "end": v(61.1, -7.4) * mm});
            skLineSegment(sketch, "E1621", {"start": v(61.1, -7.4) * mm, "end": v(61.4, -7.94) * mm});
            skLineSegment(sketch, "E1622", {"start": v(61.4, -7.94) * mm, "end": v(61.74, -8.48) * mm});
            skLineSegment(sketch, "E1623", {"start": v(61.74, -8.48) * mm, "end": v(62.1, -9) * mm});
            skLineSegment(sketch, "E1624", {"start": v(62.1, -9) * mm, "end": v(62.46, -9.5) * mm});
            skLineSegment(sketch, "E1625", {"start": v(62.46, -9.5) * mm, "end": v(62.65, -9.73) * mm});
            skLineSegment(sketch, "E1626", {"start": v(62.65, -9.73) * mm, "end": v(62.84, -9.95) * mm});
            skLineSegment(sketch, "E1627", {"start": v(62.84, -9.95) * mm, "end": v(63.03, -10.16) * mm});
            skLineSegment(sketch, "E1628", {"start": v(63.03, -10.16) * mm, "end": v(63.22, -10.36) * mm});
            skLineSegment(sketch, "E1629", {"start": v(63.22, -10.36) * mm, "end": v(63.39, -10.52) * mm});
            skLineSegment(sketch, "E1630", {"start": v(63.39, -10.52) * mm, "end": v(63.57, -10.69) * mm});
            skLineSegment(sketch, "E1631", {"start": v(63.57, -10.69) * mm, "end": v(63.98, -11.02) * mm});
            skLineSegment(sketch, "E1632", {"start": v(63.98, -11.02) * mm, "end": v(64.4, -11.33) * mm});
            skLineSegment(sketch, "E1633", {"start": v(64.4, -11.33) * mm, "end": v(64.87, -11.64) * mm});
            skLineSegment(sketch, "E1634", {"start": v(64.87, -11.64) * mm, "end": v(65.33, -11.93) * mm});
            skLineSegment(sketch, "E1635", {"start": v(65.33, -11.93) * mm, "end": v(65.8, -12.2) * mm});
            skLineSegment(sketch, "E1636", {"start": v(65.8, -12.2) * mm, "end": v(66.26, -12.45) * mm});
            skLineSegment(sketch, "E1637", {"start": v(66.26, -12.45) * mm, "end": v(66.7, -12.67) * mm});
            skLineSegment(sketch, "E1638", {"start": v(66.7, -12.67) * mm, "end": v(66.92, -12.77) * mm});
            skLineSegment(sketch, "E1639", {"start": v(66.92, -12.77) * mm, "end": v(67.17, -12.87) * mm});
            skLineSegment(sketch, "E1640", {"start": v(67.17, -12.87) * mm, "end": v(67.7, -13.04) * mm});
            skLineSegment(sketch, "E1641", {"start": v(67.7, -13.04) * mm, "end": v(68.24, -13.2) * mm});
            skLineSegment(sketch, "E1642", {"start": v(68.24, -13.2) * mm, "end": v(68.73, -13.35) * mm});
            skLineSegment(sketch, "E1643", {"start": v(68.73, -13.35) * mm, "end": v(69.53, -13.62) * mm});
            skLineSegment(sketch, "E1644", {"start": v(69.53, -13.62) * mm, "end": v(70.21, -13.84) * mm});
            skLineSegment(sketch, "E1645", {"start": v(70.21, -13.84) * mm, "end": v(70.7, -13.98) * mm});
            skLineSegment(sketch, "E1646", {"start": v(70.7, -13.98) * mm, "end": v(70.85, -14.03) * mm});
            skLineSegment(sketch, "E1647", {"start": v(70.85, -14.03) * mm, "end": v(70.92, -14.04) * mm});
            skLineSegment(sketch, "E1648", {"start": v(70.92, -14.04) * mm, "end": v(70.94, -14.03) * mm});
            skLineSegment(sketch, "E1649", {"start": v(70.94, -14.03) * mm, "end": v(70.95, -14) * mm});
            skLineSegment(sketch, "E1650", {"start": v(70.95, -14) * mm, "end": v(70.97, -13.9) * mm});
            skLineSegment(sketch, "E1651", {"start": v(70.97, -13.9) * mm, "end": v(70.98, -13.73) * mm});
            skLineSegment(sketch, "E1652", {"start": v(70.98, -13.73) * mm, "end": v(70.99, -13.5) * mm});
            skLineSegment(sketch, "E1653", {"start": v(70.99, -13.5) * mm, "end": v(70.97, -12.85) * mm});
            skLineSegment(sketch, "E1654", {"start": v(70.97, -12.85) * mm, "end": v(70.92, -11.95) * mm});
            skLineSegment(sketch, "E1655", {"start": v(70.92, -11.95) * mm, "end": v(70.84, -10.84) * mm});
            skLineSegment(sketch, "E1656", {"start": v(70.84, -10.84) * mm, "end": v(70.73, -9.51) * mm});
            skLineSegment(sketch, "E1657", {"start": v(70.73, -9.51) * mm, "end": v(70.6, -7.99) * mm});
            skLineSegment(sketch, "E1658", {"start": v(70.6, -7.99) * mm, "end": v(70.43, -6.28) * mm});
            skLineSegment(sketch, "E1659", {"start": v(46.8, -8.4) * mm, "end": v(49.06, -8.43) * mm});
            skLineSegment(sketch, "E1660", {"start": v(49.06, -8.43) * mm, "end": v(50.95, -6.53) * mm});
            skLineSegment(sketch, "E1661", {"start": v(50.95, -6.53) * mm, "end": v(51.39, -4.8) * mm});
            skLineSegment(sketch, "E1662", {"start": v(51.39, -4.8) * mm, "end": v(51.19, -4) * mm});
            skLineSegment(sketch, "E1663", {"start": v(51.19, -4) * mm, "end": v(51.13, -3.83) * mm});
            skLineSegment(sketch, "E1664", {"start": v(51.13, -3.83) * mm, "end": v(51.04, -3.66) * mm});
            skLineSegment(sketch, "E1665", {"start": v(51.04, -3.66) * mm, "end": v(50.93, -3.5) * mm});
            skLineSegment(sketch, "E1666", {"start": v(50.93, -3.5) * mm, "end": v(50.8, -3.34) * mm});
            skLineSegment(sketch, "E1667", {"start": v(50.8, -3.34) * mm, "end": v(50.54, -3.05) * mm});
            skLineSegment(sketch, "E1668", {"start": v(50.54, -3.05) * mm, "end": v(50.31, -2.82) * mm});
            skLineSegment(sketch, "E1669", {"start": v(50.31, -2.82) * mm, "end": v(49.5, -2.55) * mm});
            skLineSegment(sketch, "E1670", {"start": v(49.5, -2.55) * mm, "end": v(44.55, -1.85) * mm});
            skLineSegment(sketch, "E1671", {"start": v(44.55, -1.85) * mm, "end": v(43.03, -1.37) * mm});
            skLineSegment(sketch, "E1672", {"start": v(43.03, -1.37) * mm, "end": v(42.7, -1.27) * mm});
            skLineSegment(sketch, "E1673", {"start": v(42.7, -1.27) * mm, "end": v(42.36, -1.15) * mm});
            skLineSegment(sketch, "E1674", {"start": v(42.36, -1.15) * mm, "end": v(41.67, -0.88) * mm});
            skLineSegment(sketch, "E1675", {"start": v(41.67, -0.88) * mm, "end": v(40.95, -0.58) * mm});
            skLineSegment(sketch, "E1676", {"start": v(40.95, -0.58) * mm, "end": v(40.24, -0.25) * mm});
            skLineSegment(sketch, "E1677", {"start": v(40.24, -0.25) * mm, "end": v(39.54, 0.1) * mm});
            skLineSegment(sketch, "E1678", {"start": v(39.54, 0.1) * mm, "end": v(38.88, 0.46) * mm});
            skLineSegment(sketch, "E1679", {"start": v(38.88, 0.46) * mm, "end": v(38.28, 0.83) * mm});
            skLineSegment(sketch, "E1680", {"start": v(38.28, 0.83) * mm, "end": v(38, 1) * mm});
            skLineSegment(sketch, "E1681", {"start": v(38, 1) * mm, "end": v(37.74, 1.18) * mm});
            skLineSegment(sketch, "E1682", {"start": v(37.74, 1.18) * mm, "end": v(36.87, 1.8) * mm});
            skLineSegment(sketch, "E1683", {"start": v(36.87, 1.8) * mm, "end": v(36.46, 0.16) * mm});
            skLineSegment(sketch, "E1684", {"start": v(36.46, 0.16) * mm, "end": v(34.82, -0.92) * mm});
            skLineSegment(sketch, "E1685", {"start": v(34.82, -0.92) * mm, "end": v(34.82, -4.17) * mm});
            skLineSegment(sketch, "E1686", {"start": v(34.82, -4.17) * mm, "end": v(33.12, -5.74) * mm});
            skLineSegment(sketch, "E1687", {"start": v(33.12, -5.74) * mm, "end": v(33.72, -6.06) * mm});
            skLineSegment(sketch, "E1688", {"start": v(33.72, -6.06) * mm, "end": v(33.92, -6.16) * mm});
            skLineSegment(sketch, "E1689", {"start": v(33.92, -6.16) * mm, "end": v(34.14, -6.26) * mm});
            skLineSegment(sketch, "E1690", {"start": v(34.14, -6.26) * mm, "end": v(34.4, -6.36) * mm});
            skLineSegment(sketch, "E1691", {"start": v(34.4, -6.36) * mm, "end": v(34.67, -6.46) * mm});
            skLineSegment(sketch, "E1692", {"start": v(34.67, -6.46) * mm, "end": v(35.28, -6.66) * mm});
            skLineSegment(sketch, "E1693", {"start": v(35.28, -6.66) * mm, "end": v(35.98, -6.86) * mm});
            skLineSegment(sketch, "E1694", {"start": v(35.98, -6.86) * mm, "end": v(36.75, -7.05) * mm});
            skLineSegment(sketch, "E1695", {"start": v(36.75, -7.05) * mm, "end": v(37.57, -7.24) * mm});
            skLineSegment(sketch, "E1696", {"start": v(37.57, -7.24) * mm, "end": v(38.45, -7.42) * mm});
            skLineSegment(sketch, "E1697", {"start": v(38.45, -7.42) * mm, "end": v(39.36, -7.6) * mm});
            skLineSegment(sketch, "E1698", {"start": v(39.36, -7.6) * mm, "end": v(40.3, -7.75) * mm});
            skLineSegment(sketch, "E1699", {"start": v(40.3, -7.75) * mm, "end": v(41.27, -7.9) * mm});
            skLineSegment(sketch, "E1700", {"start": v(41.27, -7.9) * mm, "end": v(42.23, -8.03) * mm});
            skLineSegment(sketch, "E1701", {"start": v(42.23, -8.03) * mm, "end": v(43.2, -8.14) * mm});
            skLineSegment(sketch, "E1702", {"start": v(43.2, -8.14) * mm, "end": v(44.15, -8.24) * mm});
            skLineSegment(sketch, "E1703", {"start": v(44.15, -8.24) * mm, "end": v(45.07, -8.31) * mm});
            skLineSegment(sketch, "E1704", {"start": v(45.07, -8.31) * mm, "end": v(45.96, -8.36) * mm});
            skLineSegment(sketch, "E1705", {"start": v(45.96, -8.36) * mm, "end": v(46.8, -8.4) * mm});
            skLineSegment(sketch, "E1706", {"start": v(-46.4, -7.95) * mm, "end": v(-45.59, -7.87) * mm});
            skLineSegment(sketch, "E1707", {"start": v(-45.59, -7.87) * mm, "end": v(-44.5, -7.78) * mm});
            skLineSegment(sketch, "E1708", {"start": v(-44.5, -7.78) * mm, "end": v(-42.07, -7.59) * mm});
            skLineSegment(sketch, "E1709", {"start": v(-42.07, -7.59) * mm, "end": v(-41.16, -7.51) * mm});
            skLineSegment(sketch, "E1710", {"start": v(-41.16, -7.51) * mm, "end": v(-40.26, -7.42) * mm});
            skLineSegment(sketch, "E1711", {"start": v(-40.26, -7.42) * mm, "end": v(-39.37, -7.31) * mm});
            skLineSegment(sketch, "E1712", {"start": v(-39.37, -7.31) * mm, "end": v(-38.5, -7.19) * mm});
            skLineSegment(sketch, "E1713", {"start": v(-38.5, -7.19) * mm, "end": v(-37.64, -7.05) * mm});
            skLineSegment(sketch, "E1714", {"start": v(-37.64, -7.05) * mm, "end": v(-36.82, -6.9) * mm});
            skLineSegment(sketch, "E1715", {"start": v(-36.82, -6.9) * mm, "end": v(-36.04, -6.74) * mm});
            skLineSegment(sketch, "E1716", {"start": v(-36.04, -6.74) * mm, "end": v(-35.31, -6.58) * mm});
            skLineSegment(sketch, "E1717", {"start": v(-35.31, -6.58) * mm, "end": v(-34.64, -6.4) * mm});
            skLineSegment(sketch, "E1718", {"start": v(-34.64, -6.4) * mm, "end": v(-34.03, -6.23) * mm});
            skLineSegment(sketch, "E1719", {"start": v(-34.03, -6.23) * mm, "end": v(-33.5, -6.06) * mm});
            skLineSegment(sketch, "E1720", {"start": v(-33.5, -6.06) * mm, "end": v(-33.04, -5.88) * mm});
            skLineSegment(sketch, "E1721", {"start": v(-33.04, -5.88) * mm, "end": v(-32.84, -5.8) * mm});
            skLineSegment(sketch, "E1722", {"start": v(-32.84, -5.8) * mm, "end": v(-32.67, -5.7) * mm});
            skLineSegment(sketch, "E1723", {"start": v(-32.67, -5.7) * mm, "end": v(-32.52, -5.62) * mm});
            skLineSegment(sketch, "E1724", {"start": v(-32.52, -5.62) * mm, "end": v(-32.4, -5.54) * mm});
            skLineSegment(sketch, "E1725", {"start": v(-32.4, -5.54) * mm, "end": v(-32.3, -5.46) * mm});
            skLineSegment(sketch, "E1726", {"start": v(-32.3, -5.46) * mm, "end": v(-32.23, -5.38) * mm});
            skLineSegment(sketch, "E1727", {"start": v(-32.23, -5.38) * mm, "end": v(-32.18, -5.3) * mm});
            skLineSegment(sketch, "E1728", {"start": v(-32.18, -5.3) * mm, "end": v(-32.17, -5.22) * mm});
            skLineSegment(sketch, "E1729", {"start": v(-32.17, -5.22) * mm, "end": v(-32.18, -5.15) * mm});
            skLineSegment(sketch, "E1730", {"start": v(-32.18, -5.15) * mm, "end": v(-32.22, -5.07) * mm});
            skLineSegment(sketch, "E1731", {"start": v(-32.22, -5.07) * mm, "end": v(-32.28, -4.97) * mm});
            skLineSegment(sketch, "E1732", {"start": v(-32.28, -4.97) * mm, "end": v(-32.36, -4.86) * mm});
            skLineSegment(sketch, "E1733", {"start": v(-32.36, -4.86) * mm, "end": v(-32.46, -4.74) * mm});
            skLineSegment(sketch, "E1734", {"start": v(-32.46, -4.74) * mm, "end": v(-32.57, -4.62) * mm});
            skLineSegment(sketch, "E1735", {"start": v(-32.57, -4.62) * mm, "end": v(-32.7, -4.5) * mm});
            skLineSegment(sketch, "E1736", {"start": v(-32.7, -4.5) * mm, "end": v(-32.83, -4.38) * mm});
            skLineSegment(sketch, "E1737", {"start": v(-32.83, -4.38) * mm, "end": v(-33.49, -3.82) * mm});
            skLineSegment(sketch, "E1738", {"start": v(-33.49, -3.82) * mm, "end": v(-33.49, -0.34) * mm});
            skLineSegment(sketch, "E1739", {"start": v(-33.49, -0.34) * mm, "end": v(-34.96, 0.31) * mm});
            skLineSegment(sketch, "E1740", {"start": v(-34.96, 0.31) * mm, "end": v(-35.56, 2.44) * mm});
            skLineSegment(sketch, "E1741", {"start": v(-35.56, 2.44) * mm, "end": v(-36.75, 1.5) * mm});
            skLineSegment(sketch, "E1742", {"start": v(-36.75, 1.5) * mm, "end": v(-37.33, 1.07) * mm});
            skLineSegment(sketch, "E1743", {"start": v(-37.33, 1.07) * mm, "end": v(-37.6, 0.87) * mm});
            skLineSegment(sketch, "E1744", {"start": v(-37.6, 0.87) * mm, "end": v(-37.86, 0.7) * mm});
            skLineSegment(sketch, "E1745", {"start": v(-37.86, 0.7) * mm, "end": v(-38.12, 0.53) * mm});
            skLineSegment(sketch, "E1746", {"start": v(-38.12, 0.53) * mm, "end": v(-38.37, 0.38) * mm});
            skLineSegment(sketch, "E1747", {"start": v(-38.37, 0.38) * mm, "end": v(-38.63, 0.24) * mm});
            skLineSegment(sketch, "E1748", {"start": v(-38.63, 0.24) * mm, "end": v(-38.9, 0.1) * mm});
            skLineSegment(sketch, "E1749", {"start": v(-38.9, 0.1) * mm, "end": v(-39.17, -0.02) * mm});
            skLineSegment(sketch, "E1750", {"start": v(-39.17, -0.02) * mm, "end": v(-39.46, -0.14) * mm});
            skLineSegment(sketch, "E1751", {"start": v(-39.46, -0.14) * mm, "end": v(-39.77, -0.26) * mm});
            skLineSegment(sketch, "E1752", {"start": v(-39.77, -0.26) * mm, "end": v(-40.1, -0.38) * mm});
            skLineSegment(sketch, "E1753", {"start": v(-40.1, -0.38) * mm, "end": v(-40.83, -0.62) * mm});
            skLineSegment(sketch, "E1754", {"start": v(-40.83, -0.62) * mm, "end": v(-41.7, -0.88) * mm});
            skLineSegment(sketch, "E1755", {"start": v(-41.7, -0.88) * mm, "end": v(-43.88, -1.5) * mm});
            skLineSegment(sketch, "E1756", {"start": v(-43.88, -1.5) * mm, "end": v(-49.39, -1.93) * mm});
            skLineSegment(sketch, "E1757", {"start": v(-49.39, -1.93) * mm, "end": v(-50.4, -4.07) * mm});
            skLineSegment(sketch, "E1758", {"start": v(-50.4, -4.07) * mm, "end": v(-49.96, -6.4) * mm});
            skLineSegment(sketch, "E1759", {"start": v(-49.96, -6.4) * mm, "end": v(-47.94, -8.11) * mm});
            skLineSegment(sketch, "E1760", {"start": v(-47.94, -8.11) * mm, "end": v(-46.4, -7.95) * mm});
            skLineSegment(sketch, "E1761", {"start": v(-71.45, 8.32) * mm, "end": v(-71.4, 8.63) * mm});
            skLineSegment(sketch, "E1762", {"start": v(-71.4, 8.63) * mm, "end": v(-71.32, 8.98) * mm});
            skLineSegment(sketch, "E1763", {"start": v(-71.32, 8.98) * mm, "end": v(-71.24, 9.33) * mm});
            skLineSegment(sketch, "E1764", {"start": v(-71.24, 9.33) * mm, "end": v(-71.15, 9.7) * mm});
            skLineSegment(sketch, "E1765", {"start": v(-71.15, 9.7) * mm, "end": v(-71.1, 10.05) * mm});
            skLineSegment(sketch, "E1766", {"start": v(-71.1, 10.05) * mm, "end": v(-71.07, 10.23) * mm});
            skLineSegment(sketch, "E1767", {"start": v(-71.07, 10.23) * mm, "end": v(-71.06, 10.4) * mm});
            skLineSegment(sketch, "E1768", {"start": v(-71.06, 10.4) * mm, "end": v(-71.06, 10.57) * mm});
            skLineSegment(sketch, "E1769", {"start": v(-71.06, 10.57) * mm, "end": v(-71.07, 10.73) * mm});
            skLineSegment(sketch, "E1770", {"start": v(-71.07, 10.73) * mm, "end": v(-71.1, 10.89) * mm});
            skLineSegment(sketch, "E1771", {"start": v(-71.1, 10.89) * mm, "end": v(-71.13, 11.04) * mm});
            skLineSegment(sketch, "E1772", {"start": v(-71.13, 11.04) * mm, "end": v(-71.28, 11.4) * mm});
            skLineSegment(sketch, "E1773", {"start": v(-71.28, 11.4) * mm, "end": v(-71.44, 11.76) * mm});
            skLineSegment(sketch, "E1774", {"start": v(-71.44, 11.76) * mm, "end": v(-71.64, 12.13) * mm});
            skLineSegment(sketch, "E1775", {"start": v(-71.64, 12.13) * mm, "end": v(-71.86, 12.5) * mm});
            skLineSegment(sketch, "E1776", {"start": v(-71.86, 12.5) * mm, "end": v(-72.1, 12.87) * mm});
            skLineSegment(sketch, "E1777", {"start": v(-72.1, 12.87) * mm, "end": v(-72.35, 13.23) * mm});
            skLineSegment(sketch, "E1778", {"start": v(-72.35, 13.23) * mm, "end": v(-72.62, 13.6) * mm});
            skLineSegment(sketch, "E1779", {"start": v(-72.62, 13.6) * mm, "end": v(-72.9, 13.96) * mm});
            skLineSegment(sketch, "E1780", {"start": v(-72.9, 13.96) * mm, "end": v(-73.48, 14.68) * mm});
            skLineSegment(sketch, "E1781", {"start": v(-73.48, 14.68) * mm, "end": v(-74.06, 15.36) * mm});
            skLineSegment(sketch, "E1782", {"start": v(-74.06, 15.36) * mm, "end": v(-74.62, 16.02) * mm});
            skLineSegment(sketch, "E1783", {"start": v(-74.62, 16.02) * mm, "end": v(-75.13, 16.63) * mm});
            skLineSegment(sketch, "E1784", {"start": v(-75.13, 16.63) * mm, "end": v(-76.02, 17.72) * mm});
            skLineSegment(sketch, "E1785", {"start": v(-76.02, 17.72) * mm, "end": v(-76.47, 18.3) * mm});
            skLineSegment(sketch, "E1786", {"start": v(-76.47, 18.3) * mm, "end": v(-76.91, 18.87) * mm});
            skLineSegment(sketch, "E1787", {"start": v(-76.91, 18.87) * mm, "end": v(-77.12, 19.17) * mm});
            skLineSegment(sketch, "E1788", {"start": v(-77.12, 19.17) * mm, "end": v(-77.32, 19.47) * mm});
            skLineSegment(sketch, "E1789", {"start": v(-77.32, 19.47) * mm, "end": v(-77.52, 19.78) * mm});
            skLineSegment(sketch, "E1790", {"start": v(-77.52, 19.78) * mm, "end": v(-77.7, 20.08) * mm});
            skLineSegment(sketch, "E1791", {"start": v(-77.7, 20.08) * mm, "end": v(-77.87, 20.4) * mm});
            skLineSegment(sketch, "E1792", {"start": v(-77.87, 20.4) * mm, "end": v(-78.03, 20.7) * mm});
            skLineSegment(sketch, "E1793", {"start": v(-78.03, 20.7) * mm, "end": v(-78.17, 21.02) * mm});
            skLineSegment(sketch, "E1794", {"start": v(-78.17, 21.02) * mm, "end": v(-78.3, 21.34) * mm});
            skLineSegment(sketch, "E1795", {"start": v(-78.3, 21.34) * mm, "end": v(-78.52, 21.9) * mm});
            skLineSegment(sketch, "E1796", {"start": v(-78.52, 21.9) * mm, "end": v(-78.6, 22.12) * mm});
            skLineSegment(sketch, "E1797", {"start": v(-78.6, 22.12) * mm, "end": v(-78.7, 22.3) * mm});
            skLineSegment(sketch, "E1798", {"start": v(-78.7, 22.3) * mm, "end": v(-78.77, 22.43) * mm});
            skLineSegment(sketch, "E1799", {"start": v(-78.77, 22.43) * mm, "end": v(-78.84, 22.52) * mm});
            skLineSegment(sketch, "E1800", {"start": v(-78.84, 22.52) * mm, "end": v(-78.88, 22.55) * mm});
            skLineSegment(sketch, "E1801", {"start": v(-78.88, 22.55) * mm, "end": v(-78.92, 22.57) * mm});
            skLineSegment(sketch, "E1802", {"start": v(-78.92, 22.57) * mm, "end": v(-78.95, 22.58) * mm});
            skLineSegment(sketch, "E1803", {"start": v(-78.95, 22.58) * mm, "end": v(-79, 22.58) * mm});
            skLineSegment(sketch, "E1804", {"start": v(-79, 22.58) * mm, "end": v(-79.03, 22.57) * mm});
            skLineSegment(sketch, "E1805", {"start": v(-79.03, 22.57) * mm, "end": v(-79.07, 22.56) * mm});
            skLineSegment(sketch, "E1806", {"start": v(-79.07, 22.56) * mm, "end": v(-79.15, 22.5) * mm});
            skLineSegment(sketch, "E1807", {"start": v(-79.15, 22.5) * mm, "end": v(-79.25, 22.4) * mm});
            skLineSegment(sketch, "E1808", {"start": v(-79.25, 22.4) * mm, "end": v(-79.36, 22.28) * mm});
            skLineSegment(sketch, "E1809", {"start": v(-79.36, 22.28) * mm, "end": v(-79.61, 21.94) * mm});
            skLineSegment(sketch, "E1810", {"start": v(-79.61, 21.94) * mm, "end": v(-79.95, 21.47) * mm});
            skLineSegment(sketch, "E1811", {"start": v(-79.95, 21.47) * mm, "end": v(-80.14, 21.23) * mm});
            skLineSegment(sketch, "E1812", {"start": v(-80.14, 21.23) * mm, "end": v(-80.46, 20.84) * mm});
            skLineSegment(sketch, "E1813", {"start": v(-80.46, 20.84) * mm, "end": v(-80.64, 20.6) * mm});
            skLineSegment(sketch, "E1814", {"start": v(-80.64, 20.6) * mm, "end": v(-80.84, 20.32) * mm});
            skLineSegment(sketch, "E1815", {"start": v(-80.84, 20.32) * mm, "end": v(-81.03, 20.04) * mm});
            skLineSegment(sketch, "E1816", {"start": v(-81.03, 20.04) * mm, "end": v(-81.22, 19.73) * mm});
            skLineSegment(sketch, "E1817", {"start": v(-81.22, 19.73) * mm, "end": v(-81.44, 19.38) * mm});
            skLineSegment(sketch, "E1818", {"start": v(-81.44, 19.38) * mm, "end": v(-81.68, 19) * mm});
            skLineSegment(sketch, "E1819", {"start": v(-81.68, 19) * mm, "end": v(-81.91, 18.6) * mm});
            skLineSegment(sketch, "E1820", {"start": v(-81.91, 18.6) * mm, "end": v(-82.01, 18.42) * mm});
            skLineSegment(sketch, "E1821", {"start": v(-82.01, 18.42) * mm, "end": v(-82.1, 18.23) * mm});
            skLineSegment(sketch, "E1822", {"start": v(-82.1, 18.23) * mm, "end": v(-82.25, 17.81) * mm});
            skLineSegment(sketch, "E1823", {"start": v(-82.25, 17.81) * mm, "end": v(-82.4, 17.36) * mm});
            skLineSegment(sketch, "E1824", {"start": v(-82.4, 17.36) * mm, "end": v(-82.53, 16.88) * mm});
            skLineSegment(sketch, "E1825", {"start": v(-82.53, 16.88) * mm, "end": v(-82.65, 16.4) * mm});
            skLineSegment(sketch, "E1826", {"start": v(-82.65, 16.4) * mm, "end": v(-82.75, 15.9) * mm});
            skLineSegment(sketch, "E1827", {"start": v(-82.75, 15.9) * mm, "end": v(-82.84, 15.42) * mm});
            skLineSegment(sketch, "E1828", {"start": v(-82.84, 15.42) * mm, "end": v(-82.92, 14.95) * mm});
            skLineSegment(sketch, "E1829", {"start": v(-82.92, 14.95) * mm, "end": v(-82.97, 14.5) * mm});
            skLineSegment(sketch, "E1830", {"start": v(-82.97, 14.5) * mm, "end": v(-83.03, 14) * mm});
            skLineSegment(sketch, "E1831", {"start": v(-83.03, 14) * mm, "end": v(-83.07, 13.45) * mm});
            skLineSegment(sketch, "E1832", {"start": v(-83.07, 13.45) * mm, "end": v(-83.1, 12.88) * mm});
            skLineSegment(sketch, "E1833", {"start": v(-83.1, 12.88) * mm, "end": v(-83.13, 12.3) * mm});
            skLineSegment(sketch, "E1834", {"start": v(-83.13, 12.3) * mm, "end": v(-83.13, 11.72) * mm});
            skLineSegment(sketch, "E1835", {"start": v(-83.13, 11.72) * mm, "end": v(-83.1, 11.16) * mm});
            skLineSegment(sketch, "E1836", {"start": v(-83.1, 11.16) * mm, "end": v(-83.06, 10.62) * mm});
            skLineSegment(sketch, "E1837", {"start": v(-83.06, 10.62) * mm, "end": v(-83.03, 10.36) * mm});
            skLineSegment(sketch, "E1838", {"start": v(-83.03, 10.36) * mm, "end": v(-82.98, 10.1) * mm});
            skLineSegment(sketch, "E1839", {"start": v(-82.98, 10.1) * mm, "end": v(-82.89, 9.67) * mm});
            skLineSegment(sketch, "E1840", {"start": v(-82.89, 9.67) * mm, "end": v(-82.76, 9.2) * mm});
            skLineSegment(sketch, "E1841", {"start": v(-82.76, 9.2) * mm, "end": v(-82.6, 8.74) * mm});
            skLineSegment(sketch, "E1842", {"start": v(-82.6, 8.74) * mm, "end": v(-82.43, 8.26) * mm});
            skLineSegment(sketch, "E1843", {"start": v(-82.43, 8.26) * mm, "end": v(-82.24, 7.8) * mm});
            skLineSegment(sketch, "E1844", {"start": v(-82.24, 7.8) * mm, "end": v(-82.04, 7.34) * mm});
            skLineSegment(sketch, "E1845", {"start": v(-82.04, 7.34) * mm, "end": v(-81.82, 6.91) * mm});
            skLineSegment(sketch, "E1846", {"start": v(-81.82, 6.91) * mm, "end": v(-81.61, 6.52) * mm});
            skLineSegment(sketch, "E1847", {"start": v(-81.61, 6.52) * mm, "end": v(-81.33, 6.05) * mm});
            skLineSegment(sketch, "E1848", {"start": v(-81.33, 6.05) * mm, "end": v(-81, 5.56) * mm});
            skLineSegment(sketch, "E1849", {"start": v(-81, 5.56) * mm, "end": v(-80.66, 5.07) * mm});
            skLineSegment(sketch, "E1850", {"start": v(-80.66, 5.07) * mm, "end": v(-80.28, 4.58) * mm});
            skLineSegment(sketch, "E1851", {"start": v(-80.28, 4.58) * mm, "end": v(-79.9, 4.1) * mm});
            skLineSegment(sketch, "E1852", {"start": v(-79.9, 4.1) * mm, "end": v(-79.5, 3.65) * mm});
            skLineSegment(sketch, "E1853", {"start": v(-79.5, 3.65) * mm, "end": v(-79.1, 3.22) * mm});
            skLineSegment(sketch, "E1854", {"start": v(-79.1, 3.22) * mm, "end": v(-78.72, 2.83) * mm});
            skLineSegment(sketch, "E1855", {"start": v(-78.72, 2.83) * mm, "end": v(-78.46, 2.6) * mm});
            skLineSegment(sketch, "E1856", {"start": v(-78.46, 2.6) * mm, "end": v(-78.17, 2.36) * mm});
            skLineSegment(sketch, "E1857", {"start": v(-78.17, 2.36) * mm, "end": v(-77.85, 2.13) * mm});
            skLineSegment(sketch, "E1858", {"start": v(-77.85, 2.13) * mm, "end": v(-77.53, 1.9) * mm});
            skLineSegment(sketch, "E1859", {"start": v(-77.53, 1.9) * mm, "end": v(-76.88, 1.45) * mm});
            skLineSegment(sketch, "E1860", {"start": v(-76.88, 1.45) * mm, "end": v(-76.57, 1.24) * mm});
            skLineSegment(sketch, "E1861", {"start": v(-76.57, 1.24) * mm, "end": v(-76.28, 1.03) * mm});
            skLineSegment(sketch, "E1862", {"start": v(-76.28, 1.03) * mm, "end": v(-75.25, 0.29) * mm});
            skLineSegment(sketch, "E1863", {"start": v(-75.25, 0.29) * mm, "end": v(-74.25, -0.4) * mm});
            skLineSegment(sketch, "E1864", {"start": v(-74.25, -0.4) * mm, "end": v(-73.8, -0.7) * mm});
            skLineSegment(sketch, "E1865", {"start": v(-73.8, -0.7) * mm, "end": v(-73.4, -0.96) * mm});
            skLineSegment(sketch, "E1866", {"start": v(-73.4, -0.96) * mm, "end": v(-73.06, -1.17) * mm});
            skLineSegment(sketch, "E1867", {"start": v(-73.06, -1.17) * mm, "end": v(-72.8, -1.3) * mm});
            skLineSegment(sketch, "E1868", {"start": v(-72.8, -1.3) * mm, "end": v(-72.68, -1.39) * mm});
            skLineSegment(sketch, "E1869", {"start": v(-72.68, -1.39) * mm, "end": v(-72.55, -1.49) * mm});
            skLineSegment(sketch, "E1870", {"start": v(-72.55, -1.49) * mm, "end": v(-72.28, -1.7) * mm});
            skLineSegment(sketch, "E1871", {"start": v(-72.28, -1.7) * mm, "end": v(-72.14, -1.8) * mm});
            skLineSegment(sketch, "E1872", {"start": v(-72.14, -1.8) * mm, "end": v(-72.08, -1.84) * mm});
            skLineSegment(sketch, "E1873", {"start": v(-72.08, -1.84) * mm, "end": v(-72.01, -1.86) * mm});
            skLineSegment(sketch, "E1874", {"start": v(-72.01, -1.86) * mm, "end": v(-71.95, -1.88) * mm});
            skLineSegment(sketch, "E1875", {"start": v(-71.95, -1.88) * mm, "end": v(-71.88, -1.88) * mm});
            skLineSegment(sketch, "E1876", {"start": v(-71.88, -1.88) * mm, "end": v(-71.82, -1.87) * mm});
            skLineSegment(sketch, "E1877", {"start": v(-71.82, -1.87) * mm, "end": v(-71.77, -1.85) * mm});
            skLineSegment(sketch, "E1878", {"start": v(-71.77, -1.85) * mm, "end": v(-71.68, -1.79) * mm});
            skLineSegment(sketch, "E1879", {"start": v(-71.68, -1.79) * mm, "end": v(-71.6, -1.72) * mm});
            skLineSegment(sketch, "E1880", {"start": v(-71.6, -1.72) * mm, "end": v(-71.54, -1.65) * mm});
            skLineSegment(sketch, "E1881", {"start": v(-71.54, -1.65) * mm, "end": v(-71.5, -1.57) * mm});
            skLineSegment(sketch, "E1882", {"start": v(-71.5, -1.57) * mm, "end": v(-71.45, -1.48) * mm});
            skLineSegment(sketch, "E1883", {"start": v(-71.45, -1.48) * mm, "end": v(-71.41, -1.38) * mm});
            skLineSegment(sketch, "E1884", {"start": v(-71.41, -1.38) * mm, "end": v(-71.38, -1.28) * mm});
            skLineSegment(sketch, "E1885", {"start": v(-71.38, -1.28) * mm, "end": v(-71.36, -1.18) * mm});
            skLineSegment(sketch, "E1886", {"start": v(-71.36, -1.18) * mm, "end": v(-71.34, -0.95) * mm});
            skLineSegment(sketch, "E1887", {"start": v(-71.34, -0.95) * mm, "end": v(-71.35, -0.7) * mm});
            skLineSegment(sketch, "E1888", {"start": v(-71.35, -0.7) * mm, "end": v(-71.37, -0.45) * mm});
            skLineSegment(sketch, "E1889", {"start": v(-71.37, -0.45) * mm, "end": v(-71.4, -0.19) * mm});
            skLineSegment(sketch, "E1890", {"start": v(-71.4, -0.19) * mm, "end": v(-71.51, 0.36) * mm});
            skLineSegment(sketch, "E1891", {"start": v(-71.51, 0.36) * mm, "end": v(-71.63, 0.9) * mm});
            skLineSegment(sketch, "E1892", {"start": v(-71.63, 0.9) * mm, "end": v(-71.68, 1.17) * mm});
            skLineSegment(sketch, "E1893", {"start": v(-71.68, 1.17) * mm, "end": v(-71.72, 1.42) * mm});
            skLineSegment(sketch, "E1894", {"start": v(-71.72, 1.42) * mm, "end": v(-71.75, 1.65) * mm});
            skLineSegment(sketch, "E1895", {"start": v(-71.75, 1.65) * mm, "end": v(-71.76, 1.87) * mm});
            skLineSegment(sketch, "E1896", {"start": v(-71.76, 1.87) * mm, "end": v(-71.76, 2.68) * mm});
            skLineSegment(sketch, "E1897", {"start": v(-71.76, 2.68) * mm, "end": v(-71.74, 3.53) * mm});
            skLineSegment(sketch, "E1898", {"start": v(-71.74, 3.53) * mm, "end": v(-71.7, 4.42) * mm});
            skLineSegment(sketch, "E1899", {"start": v(-71.7, 4.42) * mm, "end": v(-71.67, 5.3) * mm});
            skLineSegment(sketch, "E1900", {"start": v(-71.67, 5.3) * mm, "end": v(-71.62, 6.16) * mm});
            skLineSegment(sketch, "E1901", {"start": v(-71.62, 6.16) * mm, "end": v(-71.57, 6.97) * mm});
            skLineSegment(sketch, "E1902", {"start": v(-71.57, 6.97) * mm, "end": v(-71.51, 7.7) * mm});
            skLineSegment(sketch, "E1903", {"start": v(-71.51, 7.7) * mm, "end": v(-71.45, 8.32) * mm});
            skLineSegment(sketch, "E1904", {"start": v(-62.3, 0.83) * mm, "end": v(-61.9, 1.1) * mm});
            skLineSegment(sketch, "E1905", {"start": v(-61.9, 1.1) * mm, "end": v(-61.45, 1.37) * mm});
            skLineSegment(sketch, "E1906", {"start": v(-61.45, 1.37) * mm, "end": v(-61.01, 1.66) * mm});
            skLineSegment(sketch, "E1907", {"start": v(-61.01, 1.66) * mm, "end": v(-60.81, 1.81) * mm});
            skLineSegment(sketch, "E1908", {"start": v(-60.81, 1.81) * mm, "end": v(-60.63, 1.96) * mm});
            skLineSegment(sketch, "E1909", {"start": v(-60.63, 1.96) * mm, "end": v(-60.26, 2.31) * mm});
            skLineSegment(sketch, "E1910", {"start": v(-60.26, 2.31) * mm, "end": v(-59.88, 2.7) * mm});
            skLineSegment(sketch, "E1911", {"start": v(-59.88, 2.7) * mm, "end": v(-59.5, 3.1) * mm});
            skLineSegment(sketch, "E1912", {"start": v(-59.5, 3.1) * mm, "end": v(-59.12, 3.53) * mm});
            skLineSegment(sketch, "E1913", {"start": v(-59.12, 3.53) * mm, "end": v(-58.75, 3.97) * mm});
            skLineSegment(sketch, "E1914", {"start": v(-58.75, 3.97) * mm, "end": v(-58.4, 4.4) * mm});
            skLineSegment(sketch, "E1915", {"start": v(-58.4, 4.4) * mm, "end": v(-58.08, 4.84) * mm});
            skLineSegment(sketch, "E1916", {"start": v(-58.08, 4.84) * mm, "end": v(-57.8, 5.26) * mm});
            skLineSegment(sketch, "E1917", {"start": v(-57.8, 5.26) * mm, "end": v(-57.62, 5.55) * mm});
            skLineSegment(sketch, "E1918", {"start": v(-57.62, 5.55) * mm, "end": v(-57.44, 5.85) * mm});
            skLineSegment(sketch, "E1919", {"start": v(-57.44, 5.85) * mm, "end": v(-57.09, 6.48) * mm});
            skLineSegment(sketch, "E1920", {"start": v(-57.09, 6.48) * mm, "end": v(-56.74, 7.15) * mm});
            skLineSegment(sketch, "E1921", {"start": v(-56.74, 7.15) * mm, "end": v(-56.4, 7.84) * mm});
            skLineSegment(sketch, "E1922", {"start": v(-56.4, 7.84) * mm, "end": v(-56.09, 8.54) * mm});
            skLineSegment(sketch, "E1923", {"start": v(-56.09, 8.54) * mm, "end": v(-55.8, 9.23) * mm});
            skLineSegment(sketch, "E1924", {"start": v(-55.8, 9.23) * mm, "end": v(-55.52, 9.9) * mm});
            skLineSegment(sketch, "E1925", {"start": v(-55.52, 9.9) * mm, "end": v(-55.28, 10.54) * mm});
            skLineSegment(sketch, "E1926", {"start": v(-55.28, 10.54) * mm, "end": v(-55.2, 10.77) * mm});
            skLineSegment(sketch, "E1927", {"start": v(-55.2, 10.77) * mm, "end": v(-55.14, 11) * mm});
            skLineSegment(sketch, "E1928", {"start": v(-55.14, 11) * mm, "end": v(-55.01, 11.52) * mm});
            skLineSegment(sketch, "E1929", {"start": v(-55.01, 11.52) * mm, "end": v(-54.9, 12.04) * mm});
            skLineSegment(sketch, "E1930", {"start": v(-54.9, 12.04) * mm, "end": v(-54.78, 12.51) * mm});
            skLineSegment(sketch, "E1931", {"start": v(-54.78, 12.51) * mm, "end": v(-54.68, 12.93) * mm});
            skLineSegment(sketch, "E1932", {"start": v(-54.68, 12.93) * mm, "end": v(-54.58, 13.37) * mm});
            skLineSegment(sketch, "E1933", {"start": v(-54.58, 13.37) * mm, "end": v(-54.5, 13.83) * mm});
            skLineSegment(sketch, "E1934", {"start": v(-54.5, 13.83) * mm, "end": v(-54.42, 14.27) * mm});
            skLineSegment(sketch, "E1935", {"start": v(-54.42, 14.27) * mm, "end": v(-54.36, 14.7) * mm});
            skLineSegment(sketch, "E1936", {"start": v(-54.36, 14.7) * mm, "end": v(-54.32, 15.1) * mm});
            skLineSegment(sketch, "E1937", {"start": v(-54.32, 15.1) * mm, "end": v(-54.29, 15.45) * mm});
            skLineSegment(sketch, "E1938", {"start": v(-54.29, 15.45) * mm, "end": v(-54.28, 15.74) * mm});
            skLineSegment(sketch, "E1939", {"start": v(-54.28, 15.74) * mm, "end": v(-54.26, 15.9) * mm});
            skLineSegment(sketch, "E1940", {"start": v(-54.26, 15.9) * mm, "end": v(-54.23, 16.08) * mm});
            skLineSegment(sketch, "E1941", {"start": v(-54.23, 16.08) * mm, "end": v(-54.15, 16.45) * mm});
            skLineSegment(sketch, "E1942", {"start": v(-54.15, 16.45) * mm, "end": v(-54.13, 16.63) * mm});
            skLineSegment(sketch, "E1943", {"start": v(-54.13, 16.63) * mm, "end": v(-54.13, 16.71) * mm});
            skLineSegment(sketch, "E1944", {"start": v(-54.13, 16.71) * mm, "end": v(-54.13, 16.8) * mm});
            skLineSegment(sketch, "E1945", {"start": v(-54.13, 16.8) * mm, "end": v(-54.15, 16.86) * mm});
            skLineSegment(sketch, "E1946", {"start": v(-54.15, 16.86) * mm, "end": v(-54.18, 16.92) * mm});
            skLineSegment(sketch, "E1947", {"start": v(-54.18, 16.92) * mm, "end": v(-54.22, 16.97) * mm});
            skLineSegment(sketch, "E1948", {"start": v(-54.22, 16.97) * mm, "end": v(-54.28, 17.01) * mm});
            skLineSegment(sketch, "E1949", {"start": v(-54.28, 17.01) * mm, "end": v(-54.36, 17.04) * mm});
            skLineSegment(sketch, "E1950", {"start": v(-54.36, 17.04) * mm, "end": v(-54.45, 17.05) * mm});
            skLineSegment(sketch, "E1951", {"start": v(-54.45, 17.05) * mm, "end": v(-54.54, 17.03) * mm});
            skLineSegment(sketch, "E1952", {"start": v(-54.54, 17.03) * mm, "end": v(-54.63, 17) * mm});
            skLineSegment(sketch, "E1953", {"start": v(-54.63, 17) * mm, "end": v(-54.72, 16.95) * mm});
            skLineSegment(sketch, "E1954", {"start": v(-54.72, 16.95) * mm, "end": v(-54.8, 16.89) * mm});
            skLineSegment(sketch, "E1955", {"start": v(-54.8, 16.89) * mm, "end": v(-54.99, 16.73) * mm});
            skLineSegment(sketch, "E1956", {"start": v(-54.99, 16.73) * mm, "end": v(-55.17, 16.54) * mm});
            skLineSegment(sketch, "E1957", {"start": v(-55.17, 16.54) * mm, "end": v(-55.35, 16.35) * mm});
            skLineSegment(sketch, "E1958", {"start": v(-55.35, 16.35) * mm, "end": v(-55.52, 16.18) * mm});
            skLineSegment(sketch, "E1959", {"start": v(-55.52, 16.18) * mm, "end": v(-55.6, 16.1) * mm});
            skLineSegment(sketch, "E1960", {"start": v(-55.6, 16.1) * mm, "end": v(-55.68, 16.05) * mm});
            skLineSegment(sketch, "E1961", {"start": v(-55.68, 16.05) * mm, "end": v(-56.29, 15.64) * mm});
            skLineSegment(sketch, "E1962", {"start": v(-56.29, 15.64) * mm, "end": v(-56.9, 15.26) * mm});
            skLineSegment(sketch, "E1963", {"start": v(-56.9, 15.26) * mm, "end": v(-57.54, 14.9) * mm});
            skLineSegment(sketch, "E1964", {"start": v(-57.54, 14.9) * mm, "end": v(-58.17, 14.55) * mm});
            skLineSegment(sketch, "E1965", {"start": v(-58.17, 14.55) * mm, "end": v(-58.8, 14.22) * mm});
            skLineSegment(sketch, "E1966", {"start": v(-58.8, 14.22) * mm, "end": v(-59.44, 13.92) * mm});
            skLineSegment(sketch, "E1967", {"start": v(-59.44, 13.92) * mm, "end": v(-60.08, 13.64) * mm});
            skLineSegment(sketch, "E1968", {"start": v(-60.08, 13.64) * mm, "end": v(-60.7, 13.38) * mm});
            skLineSegment(sketch, "E1969", {"start": v(-60.7, 13.38) * mm, "end": v(-61.32, 13.15) * mm});
            skLineSegment(sketch, "E1970", {"start": v(-61.32, 13.15) * mm, "end": v(-61.93, 12.95) * mm});
            skLineSegment(sketch, "E1971", {"start": v(-61.93, 12.95) * mm, "end": v(-62.52, 12.78) * mm});
            skLineSegment(sketch, "E1972", {"start": v(-62.52, 12.78) * mm, "end": v(-63.1, 12.63) * mm});
            skLineSegment(sketch, "E1973", {"start": v(-63.1, 12.63) * mm, "end": v(-63.66, 12.52) * mm});
            skLineSegment(sketch, "E1974", {"start": v(-63.66, 12.52) * mm, "end": v(-64.2, 12.43) * mm});
            skLineSegment(sketch, "E1975", {"start": v(-64.2, 12.43) * mm, "end": v(-64.7, 12.38) * mm});
            skLineSegment(sketch, "E1976", {"start": v(-64.7, 12.38) * mm, "end": v(-64.95, 12.37) * mm});
            skLineSegment(sketch, "E1977", {"start": v(-64.95, 12.37) * mm, "end": v(-65.19, 12.36) * mm});
            skLineSegment(sketch, "E1978", {"start": v(-65.19, 12.36) * mm, "end": v(-65.47, 12.38) * mm});
            skLineSegment(sketch, "E1979", {"start": v(-65.47, 12.38) * mm, "end": v(-65.78, 12.4) * mm});
            skLineSegment(sketch, "E1980", {"start": v(-65.78, 12.4) * mm, "end": v(-65.93, 12.4) * mm});
            skLineSegment(sketch, "E1981", {"start": v(-65.93, 12.4) * mm, "end": v(-66.08, 12.4) * mm});
            skLineSegment(sketch, "E1982", {"start": v(-66.08, 12.4) * mm, "end": v(-66.23, 12.4) * mm});
            skLineSegment(sketch, "E1983", {"start": v(-66.23, 12.4) * mm, "end": v(-66.36, 12.36) * mm});
            skLineSegment(sketch, "E1984", {"start": v(-66.36, 12.36) * mm, "end": v(-66.52, 12.3) * mm});
            skLineSegment(sketch, "E1985", {"start": v(-66.52, 12.3) * mm, "end": v(-66.68, 12.23) * mm});
            skLineSegment(sketch, "E1986", {"start": v(-66.68, 12.23) * mm, "end": v(-66.85, 12.14) * mm});
            skLineSegment(sketch, "E1987", {"start": v(-66.85, 12.14) * mm, "end": v(-67.02, 12.04) * mm});
            skLineSegment(sketch, "E1988", {"start": v(-67.02, 12.04) * mm, "end": v(-67.17, 11.92) * mm});
            skLineSegment(sketch, "E1989", {"start": v(-67.17, 11.92) * mm, "end": v(-67.3, 11.8) * mm});
            skLineSegment(sketch, "E1990", {"start": v(-67.3, 11.8) * mm, "end": v(-67.42, 11.67) * mm});
            skLineSegment(sketch, "E1991", {"start": v(-67.42, 11.67) * mm, "end": v(-67.47, 11.6) * mm});
            skLineSegment(sketch, "E1992", {"start": v(-67.47, 11.6) * mm, "end": v(-67.5, 11.52) * mm});
            skLineSegment(sketch, "E1993", {"start": v(-67.5, 11.52) * mm, "end": v(-67.6, 11.26) * mm});
            skLineSegment(sketch, "E1994", {"start": v(-67.6, 11.26) * mm, "end": v(-67.7, 10.99) * mm});
            skLineSegment(sketch, "E1995", {"start": v(-67.7, 10.99) * mm, "end": v(-67.8, 10.7) * mm});
            skLineSegment(sketch, "E1996", {"start": v(-67.8, 10.7) * mm, "end": v(-67.88, 10.41) * mm});
            skLineSegment(sketch, "E1997", {"start": v(-67.88, 10.41) * mm, "end": v(-67.95, 10.12) * mm});
            skLineSegment(sketch, "E1998", {"start": v(-67.95, 10.12) * mm, "end": v(-68.01, 9.81) * mm});
            skLineSegment(sketch, "E1999", {"start": v(-68.01, 9.81) * mm, "end": v(-68.07, 9.5) * mm});
            skLineSegment(sketch, "E2000", {"start": v(-68.07, 9.5) * mm, "end": v(-68.12, 9.18) * mm});
            skLineSegment(sketch, "E2001", {"start": v(-68.12, 9.18) * mm, "end": v(-68.2, 8.53) * mm});
            skLineSegment(sketch, "E2002", {"start": v(-68.2, 8.53) * mm, "end": v(-68.25, 7.87) * mm});
            skLineSegment(sketch, "E2003", {"start": v(-68.25, 7.87) * mm, "end": v(-68.28, 7.19) * mm});
            skLineSegment(sketch, "E2004", {"start": v(-68.28, 7.19) * mm, "end": v(-68.3, 6.5) * mm});
            skLineSegment(sketch, "E2005", {"start": v(-68.3, 6.5) * mm, "end": v(-68.3, 5.81) * mm});
            skLineSegment(sketch, "E2006", {"start": v(-68.3, 5.81) * mm, "end": v(-68.28, 5.12) * mm});
            skLineSegment(sketch, "E2007", {"start": v(-68.28, 5.12) * mm, "end": v(-68.24, 3.76) * mm});
            skLineSegment(sketch, "E2008", {"start": v(-68.24, 3.76) * mm, "end": v(-68.2, 2.45) * mm});
            skLineSegment(sketch, "E2009", {"start": v(-68.2, 2.45) * mm, "end": v(-68.18, 1.83) * mm});
            skLineSegment(sketch, "E2010", {"start": v(-68.18, 1.83) * mm, "end": v(-68.18, 1.24) * mm});
            skLineSegment(sketch, "E2011", {"start": v(-68.18, 1.24) * mm, "end": v(-68.18, 1.06) * mm});
            skLineSegment(sketch, "E2012", {"start": v(-68.18, 1.06) * mm, "end": v(-68.2, 0.87) * mm});
            skLineSegment(sketch, "E2013", {"start": v(-68.2, 0.87) * mm, "end": v(-68.25, 0.46) * mm});
            skLineSegment(sketch, "E2014", {"start": v(-68.25, 0.46) * mm, "end": v(-68.3, 0.02) * mm});
            skLineSegment(sketch, "E2015", {"start": v(-68.3, 0.02) * mm, "end": v(-68.36, -0.42) * mm});
            skLineSegment(sketch, "E2016", {"start": v(-68.36, -0.42) * mm, "end": v(-68.37, -0.63) * mm});
            skLineSegment(sketch, "E2017", {"start": v(-68.37, -0.63) * mm, "end": v(-68.37, -0.83) * mm});
            skLineSegment(sketch, "E2018", {"start": v(-68.37, -0.83) * mm, "end": v(-68.35, -1.03) * mm});
            skLineSegment(sketch, "E2019", {"start": v(-68.35, -1.03) * mm, "end": v(-68.32, -1.21) * mm});
            skLineSegment(sketch, "E2020", {"start": v(-68.32, -1.21) * mm, "end": v(-68.27, -1.38) * mm});
            skLineSegment(sketch, "E2021", {"start": v(-68.27, -1.38) * mm, "end": v(-68.24, -1.46) * mm});
            skLineSegment(sketch, "E2022", {"start": v(-68.24, -1.46) * mm, "end": v(-68.2, -1.53) * mm});
            skLineSegment(sketch, "E2023", {"start": v(-68.2, -1.53) * mm, "end": v(-68.15, -1.6) * mm});
            skLineSegment(sketch, "E2024", {"start": v(-68.15, -1.6) * mm, "end": v(-68.1, -1.66) * mm});
            skLineSegment(sketch, "E2025", {"start": v(-68.1, -1.66) * mm, "end": v(-68.04, -1.71) * mm});
            skLineSegment(sketch, "E2026", {"start": v(-68.04, -1.71) * mm, "end": v(-67.97, -1.76) * mm});
            skLineSegment(sketch, "E2027", {"start": v(-67.97, -1.76) * mm, "end": v(-67.87, -1.82) * mm});
            skLineSegment(sketch, "E2028", {"start": v(-67.87, -1.82) * mm, "end": v(-67.76, -1.87) * mm});
            skLineSegment(sketch, "E2029", {"start": v(-67.76, -1.87) * mm, "end": v(-67.65, -1.9) * mm});
            skLineSegment(sketch, "E2030", {"start": v(-67.65, -1.9) * mm, "end": v(-67.54, -1.92) * mm});
            skLineSegment(sketch, "E2031", {"start": v(-67.54, -1.92) * mm, "end": v(-67.42, -1.93) * mm});
            skLineSegment(sketch, "E2032", {"start": v(-67.42, -1.93) * mm, "end": v(-67.3, -1.93) * mm});
            skLineSegment(sketch, "E2033", {"start": v(-67.3, -1.93) * mm, "end": v(-67.18, -1.93) * mm});
            skLineSegment(sketch, "E2034", {"start": v(-67.18, -1.93) * mm, "end": v(-67.06, -1.9) * mm});
            skLineSegment(sketch, "E2035", {"start": v(-67.06, -1.9) * mm, "end": v(-66.8, -1.85) * mm});
            skLineSegment(sketch, "E2036", {"start": v(-66.8, -1.85) * mm, "end": v(-66.54, -1.76) * mm});
            skLineSegment(sketch, "E2037", {"start": v(-66.54, -1.76) * mm, "end": v(-66.27, -1.65) * mm});
            skLineSegment(sketch, "E2038", {"start": v(-66.27, -1.65) * mm, "end": v(-66, -1.51) * mm});
            skLineSegment(sketch, "E2039", {"start": v(-66, -1.51) * mm, "end": v(-65.73, -1.37) * mm});
            skLineSegment(sketch, "E2040", {"start": v(-65.73, -1.37) * mm, "end": v(-65.46, -1.2) * mm});
            skLineSegment(sketch, "E2041", {"start": v(-65.46, -1.2) * mm, "end": v(-64.93, -0.88) * mm});
            skLineSegment(sketch, "E2042", {"start": v(-64.93, -0.88) * mm, "end": v(-64.43, -0.57) * mm});
            skLineSegment(sketch, "E2043", {"start": v(-64.43, -0.57) * mm, "end": v(-64.2, -0.43) * mm});
            skLineSegment(sketch, "E2044", {"start": v(-64.2, -0.43) * mm, "end": v(-63.98, -0.31) * mm});
            skLineSegment(sketch, "E2045", {"start": v(-63.98, -0.31) * mm, "end": v(-63.77, -0.2) * mm});
            skLineSegment(sketch, "E2046", {"start": v(-63.77, -0.2) * mm, "end": v(-63.56, -0.06) * mm});
            skLineSegment(sketch, "E2047", {"start": v(-63.56, -0.06) * mm, "end": v(-63.13, 0.23) * mm});
            skLineSegment(sketch, "E2048", {"start": v(-63.13, 0.23) * mm, "end": v(-62.7, 0.54) * mm});
            skLineSegment(sketch, "E2049", {"start": v(-62.7, 0.54) * mm, "end": v(-62.3, 0.83) * mm});
            skLineSegment(sketch, "E2050", {"start": v(69.26, 8.07) * mm, "end": v(69.09, 9.14) * mm});
            skLineSegment(sketch, "E2051", {"start": v(69.09, 9.14) * mm, "end": v(68.9, 10.3) * mm});
            skLineSegment(sketch, "E2052", {"start": v(68.9, 10.3) * mm, "end": v(68.72, 11.46) * mm});
            skLineSegment(sketch, "E2053", {"start": v(68.72, 11.46) * mm, "end": v(68.62, 12) * mm});
            skLineSegment(sketch, "E2054", {"start": v(68.62, 12) * mm, "end": v(68.52, 12.52) * mm});
            skLineSegment(sketch, "E2055", {"start": v(68.52, 12.52) * mm, "end": v(68.4, 13.02) * mm});
            skLineSegment(sketch, "E2056", {"start": v(68.4, 13.02) * mm, "end": v(68.27, 13.51) * mm});
            skLineSegment(sketch, "E2057", {"start": v(68.27, 13.51) * mm, "end": v(66.14, 13.71) * mm});
            skLineSegment(sketch, "E2058", {"start": v(66.14, 13.71) * mm, "end": v(65.69, 13.76) * mm});
            skLineSegment(sketch, "E2059", {"start": v(65.69, 13.76) * mm, "end": v(65.2, 13.82) * mm});
            skLineSegment(sketch, "E2060", {"start": v(65.2, 13.82) * mm, "end": v(64.7, 13.9) * mm});
            skLineSegment(sketch, "E2061", {"start": v(64.7, 13.9) * mm, "end": v(64.2, 13.97) * mm});
            skLineSegment(sketch, "E2062", {"start": v(64.2, 13.97) * mm, "end": v(63.73, 14.06) * mm});
            skLineSegment(sketch, "E2063", {"start": v(63.73, 14.06) * mm, "end": v(63.28, 14.15) * mm});
            skLineSegment(sketch, "E2064", {"start": v(63.28, 14.15) * mm, "end": v(62.88, 14.24) * mm});
            skLineSegment(sketch, "E2065", {"start": v(62.88, 14.24) * mm, "end": v(62.54, 14.32) * mm});
            skLineSegment(sketch, "E2066", {"start": v(62.54, 14.32) * mm, "end": v(62.2, 14.42) * mm});
            skLineSegment(sketch, "E2067", {"start": v(62.2, 14.42) * mm, "end": v(61.84, 14.55) * mm});
            skLineSegment(sketch, "E2068", {"start": v(61.84, 14.55) * mm, "end": v(61.44, 14.7) * mm});
            skLineSegment(sketch, "E2069", {"start": v(61.44, 14.7) * mm, "end": v(61.02, 14.87) * mm});
            skLineSegment(sketch, "E2070", {"start": v(61.02, 14.87) * mm, "end": v(60.58, 15.05) * mm});
            skLineSegment(sketch, "E2071", {"start": v(60.58, 15.05) * mm, "end": v(60.13, 15.25) * mm});
            skLineSegment(sketch, "E2072", {"start": v(60.13, 15.25) * mm, "end": v(59.23, 15.66) * mm});
            skLineSegment(sketch, "E2073", {"start": v(59.23, 15.66) * mm, "end": v(58.36, 16.1) * mm});
            skLineSegment(sketch, "E2074", {"start": v(58.36, 16.1) * mm, "end": v(57.96, 16.3) * mm});
            skLineSegment(sketch, "E2075", {"start": v(57.96, 16.3) * mm, "end": v(57.6, 16.51) * mm});
            skLineSegment(sketch, "E2076", {"start": v(57.6, 16.51) * mm, "end": v(57.26, 16.71) * mm});
            skLineSegment(sketch, "E2077", {"start": v(57.26, 16.71) * mm, "end": v(56.96, 16.9) * mm});
            skLineSegment(sketch, "E2078", {"start": v(56.96, 16.9) * mm, "end": v(56.72, 17.06) * mm});
            skLineSegment(sketch, "E2079", {"start": v(56.72, 17.06) * mm, "end": v(56.53, 17.21) * mm});
            skLineSegment(sketch, "E2080", {"start": v(56.53, 17.21) * mm, "end": v(56.41, 17.31) * mm});
            skLineSegment(sketch, "E2081", {"start": v(56.41, 17.31) * mm, "end": v(56.3, 17.4) * mm});
            skLineSegment(sketch, "E2082", {"start": v(56.3, 17.4) * mm, "end": v(56.17, 17.47) * mm});
            skLineSegment(sketch, "E2083", {"start": v(56.17, 17.47) * mm, "end": v(56.05, 17.53) * mm});
            skLineSegment(sketch, "E2084", {"start": v(56.05, 17.53) * mm, "end": v(55.94, 17.57) * mm});
            skLineSegment(sketch, "E2085", {"start": v(55.94, 17.57) * mm, "end": v(55.83, 17.6) * mm});
            skLineSegment(sketch, "E2086", {"start": v(55.83, 17.6) * mm, "end": v(55.75, 17.6) * mm});
            skLineSegment(sketch, "E2087", {"start": v(55.75, 17.6) * mm, "end": v(55.67, 17.59) * mm});
            skLineSegment(sketch, "E2088", {"start": v(55.67, 17.59) * mm, "end": v(55.6, 17.57) * mm});
            skLineSegment(sketch, "E2089", {"start": v(55.6, 17.57) * mm, "end": v(55.5, 17.55) * mm});
            skLineSegment(sketch, "E2090", {"start": v(55.5, 17.55) * mm, "end": v(55.43, 17.52) * mm});
            skLineSegment(sketch, "E2091", {"start": v(55.43, 17.52) * mm, "end": v(55.4, 17.5) * mm});
            skLineSegment(sketch, "E2092", {"start": v(55.4, 17.5) * mm, "end": v(55.37, 17.47) * mm});
            skLineSegment(sketch, "E2093", {"start": v(55.37, 17.47) * mm, "end": v(55.32, 17.36) * mm});
            skLineSegment(sketch, "E2094", {"start": v(55.32, 17.36) * mm, "end": v(55.27, 17.23) * mm});
            skLineSegment(sketch, "E2095", {"start": v(55.27, 17.23) * mm, "end": v(55.23, 17.1) * mm});
            skLineSegment(sketch, "E2096", {"start": v(55.23, 17.1) * mm, "end": v(55.2, 16.97) * mm});
            skLineSegment(sketch, "E2097", {"start": v(55.2, 16.97) * mm, "end": v(55.18, 16.84) * mm});
            skLineSegment(sketch, "E2098", {"start": v(55.18, 16.84) * mm, "end": v(55.17, 16.7) * mm});
            skLineSegment(sketch, "E2099", {"start": v(55.17, 16.7) * mm, "end": v(55.17, 16.42) * mm});
            skLineSegment(sketch, "E2100", {"start": v(55.17, 16.42) * mm, "end": v(55.2, 16.12) * mm});
            skLineSegment(sketch, "E2101", {"start": v(55.2, 16.12) * mm, "end": v(55.25, 15.82) * mm});
            skLineSegment(sketch, "E2102", {"start": v(55.25, 15.82) * mm, "end": v(55.32, 15.51) * mm});
            skLineSegment(sketch, "E2103", {"start": v(55.32, 15.51) * mm, "end": v(55.41, 15.2) * mm});
            skLineSegment(sketch, "E2104", {"start": v(55.41, 15.2) * mm, "end": v(55.52, 14.89) * mm});
            skLineSegment(sketch, "E2105", {"start": v(55.52, 14.89) * mm, "end": v(55.63, 14.58) * mm});
            skLineSegment(sketch, "E2106", {"start": v(55.63, 14.58) * mm, "end": v(55.87, 13.97) * mm});
            skLineSegment(sketch, "E2107", {"start": v(55.87, 13.97) * mm, "end": v(56.1, 13.39) * mm});
            skLineSegment(sketch, "E2108", {"start": v(56.1, 13.39) * mm, "end": v(56.2, 13.11) * mm});
            skLineSegment(sketch, "E2109", {"start": v(56.2, 13.11) * mm, "end": v(56.3, 12.85) * mm});
            skLineSegment(sketch, "E2110", {"start": v(56.3, 12.85) * mm, "end": v(56.56, 12.1) * mm});
            skLineSegment(sketch, "E2111", {"start": v(56.56, 12.1) * mm, "end": v(56.87, 11.33) * mm});
            skLineSegment(sketch, "E2112", {"start": v(56.87, 11.33) * mm, "end": v(57.2, 10.53) * mm});
            skLineSegment(sketch, "E2113", {"start": v(57.2, 10.53) * mm, "end": v(57.57, 9.72) * mm});
            skLineSegment(sketch, "E2114", {"start": v(57.57, 9.72) * mm, "end": v(57.97, 8.92) * mm});
            skLineSegment(sketch, "E2115", {"start": v(57.97, 8.92) * mm, "end": v(58.17, 8.54) * mm});
            skLineSegment(sketch, "E2116", {"start": v(58.17, 8.54) * mm, "end": v(58.38, 8.16) * mm});
            skLineSegment(sketch, "E2117", {"start": v(58.38, 8.16) * mm, "end": v(58.59, 7.79) * mm});
            skLineSegment(sketch, "E2118", {"start": v(58.59, 7.79) * mm, "end": v(58.8, 7.44) * mm});
            skLineSegment(sketch, "E2119", {"start": v(58.8, 7.44) * mm, "end": v(59.02, 7.1) * mm});
            skLineSegment(sketch, "E2120", {"start": v(59.02, 7.1) * mm, "end": v(59.24, 6.78) * mm});
            skLineSegment(sketch, "E2121", {"start": v(59.24, 6.78) * mm, "end": v(59.41, 6.55) * mm});
            skLineSegment(sketch, "E2122", {"start": v(59.41, 6.55) * mm, "end": v(59.61, 6.32) * mm});
            skLineSegment(sketch, "E2123", {"start": v(59.61, 6.32) * mm, "end": v(59.83, 6.09) * mm});
            skLineSegment(sketch, "E2124", {"start": v(59.83, 6.09) * mm, "end": v(60.07, 5.86) * mm});
            skLineSegment(sketch, "E2125", {"start": v(60.07, 5.86) * mm, "end": v(60.54, 5.42) * mm});
            skLineSegment(sketch, "E2126", {"start": v(60.54, 5.42) * mm, "end": v(60.76, 5.2) * mm});
            skLineSegment(sketch, "E2127", {"start": v(60.76, 5.2) * mm, "end": v(60.97, 5) * mm});
            skLineSegment(sketch, "E2128", {"start": v(60.97, 5) * mm, "end": v(61.34, 4.63) * mm});
            skLineSegment(sketch, "E2129", {"start": v(61.34, 4.63) * mm, "end": v(61.75, 4.25) * mm});
            skLineSegment(sketch, "E2130", {"start": v(61.75, 4.25) * mm, "end": v(62.17, 3.86) * mm});
            skLineSegment(sketch, "E2131", {"start": v(62.17, 3.86) * mm, "end": v(62.6, 3.5) * mm});
            skLineSegment(sketch, "E2132", {"start": v(62.6, 3.5) * mm, "end": v(63.02, 3.15) * mm});
            skLineSegment(sketch, "E2133", {"start": v(63.02, 3.15) * mm, "end": v(63.41, 2.83) * mm});
            skLineSegment(sketch, "E2134", {"start": v(63.41, 2.83) * mm, "end": v(63.78, 2.57) * mm});
            skLineSegment(sketch, "E2135", {"start": v(63.78, 2.57) * mm, "end": v(64.1, 2.35) * mm});
            skLineSegment(sketch, "E2136", {"start": v(64.1, 2.35) * mm, "end": v(64.4, 2.16) * mm});
            skLineSegment(sketch, "E2137", {"start": v(64.4, 2.16) * mm, "end": v(64.75, 1.97) * mm});
            skLineSegment(sketch, "E2138", {"start": v(64.75, 1.97) * mm, "end": v(65.11, 1.78) * mm});
            skLineSegment(sketch, "E2139", {"start": v(65.11, 1.78) * mm, "end": v(65.5, 1.59) * mm});
            skLineSegment(sketch, "E2140", {"start": v(65.5, 1.59) * mm, "end": v(65.89, 1.4) * mm});
            skLineSegment(sketch, "E2141", {"start": v(65.89, 1.4) * mm, "end": v(66.29, 1.22) * mm});
            skLineSegment(sketch, "E2142", {"start": v(66.29, 1.22) * mm, "end": v(66.7, 1.04) * mm});
            skLineSegment(sketch, "E2143", {"start": v(66.7, 1.04) * mm, "end": v(67.1, 0.88) * mm});
            skLineSegment(sketch, "E2144", {"start": v(67.1, 0.88) * mm, "end": v(67.49, 0.72) * mm});
            skLineSegment(sketch, "E2145", {"start": v(67.49, 0.72) * mm, "end": v(67.86, 0.58) * mm});
            skLineSegment(sketch, "E2146", {"start": v(67.86, 0.58) * mm, "end": v(68.23, 0.46) * mm});
            skLineSegment(sketch, "E2147", {"start": v(68.23, 0.46) * mm, "end": v(68.57, 0.35) * mm});
            skLineSegment(sketch, "E2148", {"start": v(68.57, 0.35) * mm, "end": v(68.88, 0.27) * mm});
            skLineSegment(sketch, "E2149", {"start": v(68.88, 0.27) * mm, "end": v(69.15, 0.2) * mm});
            skLineSegment(sketch, "E2150", {"start": v(69.15, 0.2) * mm, "end": v(69.4, 0.16) * mm});
            skLineSegment(sketch, "E2151", {"start": v(69.4, 0.16) * mm, "end": v(69.59, 0.15) * mm});
            skLineSegment(sketch, "E2152", {"start": v(69.59, 0.15) * mm, "end": v(70.2, 0.15) * mm});
            skLineSegment(sketch, "E2153", {"start": v(70.2, 0.15) * mm, "end": v(69.98, 2.38) * mm});
            skLineSegment(sketch, "E2154", {"start": v(69.98, 2.38) * mm, "end": v(69.85, 3.52) * mm});
            skLineSegment(sketch, "E2155", {"start": v(69.85, 3.52) * mm, "end": v(69.67, 4.97) * mm});
            skLineSegment(sketch, "E2156", {"start": v(69.67, 4.97) * mm, "end": v(69.47, 6.55) * mm});
            skLineSegment(sketch, "E2157", {"start": v(69.47, 6.55) * mm, "end": v(69.26, 8.07) * mm});
            skLineSegment(sketch, "E2158", {"start": v(79.8, 4.67) * mm, "end": v(80.27, 5.12) * mm});
            skLineSegment(sketch, "E2159", {"start": v(80.27, 5.12) * mm, "end": v(80.79, 5.6) * mm});
            skLineSegment(sketch, "E2160", {"start": v(80.79, 5.6) * mm, "end": v(81.04, 5.84) * mm});
            skLineSegment(sketch, "E2161", {"start": v(81.04, 5.84) * mm, "end": v(81.28, 6.09) * mm});
            skLineSegment(sketch, "E2162", {"start": v(81.28, 6.09) * mm, "end": v(81.5, 6.34) * mm});
            skLineSegment(sketch, "E2163", {"start": v(81.5, 6.34) * mm, "end": v(81.7, 6.58) * mm});
            skLineSegment(sketch, "E2164", {"start": v(81.7, 6.58) * mm, "end": v(82.03, 7.07) * mm});
            skLineSegment(sketch, "E2165", {"start": v(82.03, 7.07) * mm, "end": v(82.35, 7.59) * mm});
            skLineSegment(sketch, "E2166", {"start": v(82.35, 7.59) * mm, "end": v(82.67, 8.15) * mm});
            skLineSegment(sketch, "E2167", {"start": v(82.67, 8.15) * mm, "end": v(82.98, 8.73) * mm});
            skLineSegment(sketch, "E2168", {"start": v(82.98, 8.73) * mm, "end": v(83.27, 9.32) * mm});
            skLineSegment(sketch, "E2169", {"start": v(83.27, 9.32) * mm, "end": v(83.52, 9.9) * mm});
            skLineSegment(sketch, "E2170", {"start": v(83.52, 9.9) * mm, "end": v(83.75, 10.48) * mm});
            skLineSegment(sketch, "E2171", {"start": v(83.75, 10.48) * mm, "end": v(83.85, 10.76) * mm});
            skLineSegment(sketch, "E2172", {"start": v(83.85, 10.76) * mm, "end": v(83.93, 11.03) * mm});
            skLineSegment(sketch, "E2173", {"start": v(83.93, 11.03) * mm, "end": v(84.05, 11.43) * mm});
            skLineSegment(sketch, "E2174", {"start": v(84.05, 11.43) * mm, "end": v(84.14, 11.87) * mm});
            skLineSegment(sketch, "E2175", {"start": v(84.14, 11.87) * mm, "end": v(84.23, 12.32) * mm});
            skLineSegment(sketch, "E2176", {"start": v(84.23, 12.32) * mm, "end": v(84.3, 12.78) * mm});
            skLineSegment(sketch, "E2177", {"start": v(84.3, 12.78) * mm, "end": v(84.35, 13.25) * mm});
            skLineSegment(sketch, "E2178", {"start": v(84.35, 13.25) * mm, "end": v(84.38, 13.7) * mm});
            skLineSegment(sketch, "E2179", {"start": v(84.38, 13.7) * mm, "end": v(84.39, 14.15) * mm});
            skLineSegment(sketch, "E2180", {"start": v(84.39, 14.15) * mm, "end": v(84.38, 14.57) * mm});
            skLineSegment(sketch, "E2181", {"start": v(84.38, 14.57) * mm, "end": v(84.35, 14.81) * mm});
            skLineSegment(sketch, "E2182", {"start": v(84.35, 14.81) * mm, "end": v(84.3, 15.06) * mm});
            skLineSegment(sketch, "E2183", {"start": v(84.3, 15.06) * mm, "end": v(84.24, 15.32) * mm});
            skLineSegment(sketch, "E2184", {"start": v(84.24, 15.32) * mm, "end": v(84.16, 15.59) * mm});
            skLineSegment(sketch, "E2185", {"start": v(84.16, 15.59) * mm, "end": v(84, 16.1) * mm});
            skLineSegment(sketch, "E2186", {"start": v(84, 16.1) * mm, "end": v(83.92, 16.36) * mm});
            skLineSegment(sketch, "E2187", {"start": v(83.92, 16.36) * mm, "end": v(83.86, 16.6) * mm});
            skLineSegment(sketch, "E2188", {"start": v(83.86, 16.6) * mm, "end": v(83.75, 17) * mm});
            skLineSegment(sketch, "E2189", {"start": v(83.75, 17) * mm, "end": v(83.62, 17.42) * mm});
            skLineSegment(sketch, "E2190", {"start": v(83.62, 17.42) * mm, "end": v(83.49, 17.84) * mm});
            skLineSegment(sketch, "E2191", {"start": v(83.49, 17.84) * mm, "end": v(83.34, 18.26) * mm});
            skLineSegment(sketch, "E2192", {"start": v(83.34, 18.26) * mm, "end": v(83.18, 18.68) * mm});
            skLineSegment(sketch, "E2193", {"start": v(83.18, 18.68) * mm, "end": v(83.01, 19.1) * mm});
            skLineSegment(sketch, "E2194", {"start": v(83.01, 19.1) * mm, "end": v(82.84, 19.5) * mm});
            skLineSegment(sketch, "E2195", {"start": v(82.84, 19.5) * mm, "end": v(82.66, 19.91) * mm});
            skLineSegment(sketch, "E2196", {"start": v(82.66, 19.91) * mm, "end": v(82.47, 20.3) * mm});
            skLineSegment(sketch, "E2197", {"start": v(82.47, 20.3) * mm, "end": v(82.28, 20.68) * mm});
            skLineSegment(sketch, "E2198", {"start": v(82.28, 20.68) * mm, "end": v(82.09, 21.05) * mm});
            skLineSegment(sketch, "E2199", {"start": v(82.09, 21.05) * mm, "end": v(81.9, 21.4) * mm});
            skLineSegment(sketch, "E2200", {"start": v(81.9, 21.4) * mm, "end": v(81.7, 21.72) * mm});
            skLineSegment(sketch, "E2201", {"start": v(81.7, 21.72) * mm, "end": v(81.5, 22.03) * mm});
            skLineSegment(sketch, "E2202", {"start": v(81.5, 22.03) * mm, "end": v(81.3, 22.31) * mm});
            skLineSegment(sketch, "E2203", {"start": v(81.3, 22.31) * mm, "end": v(81.1, 22.57) * mm});
            skLineSegment(sketch, "E2204", {"start": v(81.1, 22.57) * mm, "end": v(80.45, 23.36) * mm});
            skLineSegment(sketch, "E2205", {"start": v(80.45, 23.36) * mm, "end": v(79.24, 21.2) * mm});
            skLineSegment(sketch, "E2206", {"start": v(79.24, 21.2) * mm, "end": v(78.8, 20.41) * mm});
            skLineSegment(sketch, "E2207", {"start": v(78.8, 20.41) * mm, "end": v(78.35, 19.7) * mm});
            skLineSegment(sketch, "E2208", {"start": v(78.35, 19.7) * mm, "end": v(78.12, 19.34) * mm});
            skLineSegment(sketch, "E2209", {"start": v(78.12, 19.34) * mm, "end": v(77.89, 19) * mm});
            skLineSegment(sketch, "E2210", {"start": v(77.89, 19) * mm, "end": v(77.64, 18.64) * mm});
            skLineSegment(sketch, "E2211", {"start": v(77.64, 18.64) * mm, "end": v(77.38, 18.29) * mm});
            skLineSegment(sketch, "E2212", {"start": v(77.38, 18.29) * mm, "end": v(76.8, 17.52) * mm});
            skLineSegment(sketch, "E2213", {"start": v(76.8, 17.52) * mm, "end": v(76.1, 16.67) * mm});
            skLineSegment(sketch, "E2214", {"start": v(76.1, 16.67) * mm, "end": v(75.28, 15.7) * mm});
            skLineSegment(sketch, "E2215", {"start": v(75.28, 15.7) * mm, "end": v(74.3, 14.55) * mm});
            skLineSegment(sketch, "E2216", {"start": v(74.3, 14.55) * mm, "end": v(72.7, 12.7) * mm});
            skLineSegment(sketch, "E2217", {"start": v(72.7, 12.7) * mm, "end": v(73.1, 10.3) * mm});
            skLineSegment(sketch, "E2218", {"start": v(73.1, 10.3) * mm, "end": v(73.2, 9.74) * mm});
            skLineSegment(sketch, "E2219", {"start": v(73.2, 9.74) * mm, "end": v(73.28, 9.07) * mm});
            skLineSegment(sketch, "E2220", {"start": v(73.28, 9.07) * mm, "end": v(73.37, 8.3) * mm});
            skLineSegment(sketch, "E2221", {"start": v(73.37, 8.3) * mm, "end": v(73.45, 7.46) * mm});
            skLineSegment(sketch, "E2222", {"start": v(73.45, 7.46) * mm, "end": v(73.53, 6.59) * mm});
            skLineSegment(sketch, "E2223", {"start": v(73.53, 6.59) * mm, "end": v(73.6, 5.7) * mm});
            skLineSegment(sketch, "E2224", {"start": v(73.6, 5.7) * mm, "end": v(73.67, 4.83) * mm});
            skLineSegment(sketch, "E2225", {"start": v(73.67, 4.83) * mm, "end": v(73.72, 4) * mm});
            skLineSegment(sketch, "E2226", {"start": v(73.72, 4) * mm, "end": v(73.92, 0.09) * mm});
            skLineSegment(sketch, "E2227", {"start": v(73.92, 0.09) * mm, "end": v(74.9, 0.71) * mm});
            skLineSegment(sketch, "E2228", {"start": v(74.9, 0.71) * mm, "end": v(75.95, 1.38) * mm});
            skLineSegment(sketch, "E2229", {"start": v(75.95, 1.38) * mm, "end": v(76.47, 1.72) * mm});
            skLineSegment(sketch, "E2230", {"start": v(76.47, 1.72) * mm, "end": v(76.99, 2.06) * mm});
            skLineSegment(sketch, "E2231", {"start": v(76.99, 2.06) * mm, "end": v(77.47, 2.41) * mm});
            skLineSegment(sketch, "E2232", {"start": v(77.47, 2.41) * mm, "end": v(77.91, 2.76) * mm});
            skLineSegment(sketch, "E2233", {"start": v(77.91, 2.76) * mm, "end": v(78.15, 2.96) * mm});
            skLineSegment(sketch, "E2234", {"start": v(78.15, 2.96) * mm, "end": v(78.39, 3.2) * mm});
            skLineSegment(sketch, "E2235", {"start": v(78.39, 3.2) * mm, "end": v(78.88, 3.7) * mm});
            skLineSegment(sketch, "E2236", {"start": v(78.88, 3.7) * mm, "end": v(79.36, 4.2) * mm});
            skLineSegment(sketch, "E2237", {"start": v(79.36, 4.2) * mm, "end": v(79.8, 4.67) * mm});
            skLineSegment(sketch, "E2238", {"start": v(7.78, 5.12) * mm, "end": v(7.98, 5.1) * mm});
            skLineSegment(sketch, "E2239", {"start": v(7.98, 5.1) * mm, "end": v(8.2, 5.07) * mm});
            skLineSegment(sketch, "E2240", {"start": v(8.2, 5.07) * mm, "end": v(8.31, 5.06) * mm});
            skLineSegment(sketch, "E2241", {"start": v(8.31, 5.06) * mm, "end": v(8.42, 5.06) * mm});
            skLineSegment(sketch, "E2242", {"start": v(8.42, 5.06) * mm, "end": v(8.52, 5.07) * mm});
            skLineSegment(sketch, "E2243", {"start": v(8.52, 5.07) * mm, "end": v(8.62, 5.1) * mm});
            skLineSegment(sketch, "E2244", {"start": v(8.62, 5.1) * mm, "end": v(8.74, 5.16) * mm});
            skLineSegment(sketch, "E2245", {"start": v(8.74, 5.16) * mm, "end": v(8.85, 5.23) * mm});
            skLineSegment(sketch, "E2246", {"start": v(8.85, 5.23) * mm, "end": v(8.97, 5.32) * mm});
            skLineSegment(sketch, "E2247", {"start": v(8.97, 5.32) * mm, "end": v(9.08, 5.43) * mm});
            skLineSegment(sketch, "E2248", {"start": v(9.08, 5.43) * mm, "end": v(9.18, 5.54) * mm});
            skLineSegment(sketch, "E2249", {"start": v(9.18, 5.54) * mm, "end": v(9.27, 5.65) * mm});
            skLineSegment(sketch, "E2250", {"start": v(9.27, 5.65) * mm, "end": v(9.35, 5.77) * mm});
            skLineSegment(sketch, "E2251", {"start": v(9.35, 5.77) * mm, "end": v(9.4, 5.9) * mm});
            skLineSegment(sketch, "E2252", {"start": v(9.4, 5.9) * mm, "end": v(9.44, 6) * mm});
            skLineSegment(sketch, "E2253", {"start": v(9.44, 6) * mm, "end": v(9.47, 6.1) * mm});
            skLineSegment(sketch, "E2254", {"start": v(9.47, 6.1) * mm, "end": v(9.5, 6.33) * mm});
            skLineSegment(sketch, "E2255", {"start": v(9.5, 6.33) * mm, "end": v(9.5, 6.58) * mm});
            skLineSegment(sketch, "E2256", {"start": v(9.5, 6.58) * mm, "end": v(9.5, 6.83) * mm});
            skLineSegment(sketch, "E2257", {"start": v(9.5, 6.83) * mm, "end": v(9.44, 7.34) * mm});
            skLineSegment(sketch, "E2258", {"start": v(9.44, 7.34) * mm, "end": v(9.42, 7.58) * mm});
            skLineSegment(sketch, "E2259", {"start": v(9.42, 7.58) * mm, "end": v(9.4, 7.8) * mm});
            skLineSegment(sketch, "E2260", {"start": v(9.4, 7.8) * mm, "end": v(9.16, 7.7) * mm});
            skLineSegment(sketch, "E2261", {"start": v(9.16, 7.7) * mm, "end": v(8.9, 7.57) * mm});
            skLineSegment(sketch, "E2262", {"start": v(8.9, 7.57) * mm, "end": v(8.77, 7.5) * mm});
            skLineSegment(sketch, "E2263", {"start": v(8.77, 7.5) * mm, "end": v(8.64, 7.46) * mm});
            skLineSegment(sketch, "E2264", {"start": v(8.64, 7.46) * mm, "end": v(8.5, 7.43) * mm});
            skLineSegment(sketch, "E2265", {"start": v(8.5, 7.43) * mm, "end": v(8.38, 7.42) * mm});
            skLineSegment(sketch, "E2266", {"start": v(8.38, 7.42) * mm, "end": v(8.25, 7.42) * mm});
            skLineSegment(sketch, "E2267", {"start": v(8.25, 7.42) * mm, "end": v(8.1, 7.45) * mm});
            skLineSegment(sketch, "E2268", {"start": v(8.1, 7.45) * mm, "end": v(7.97, 7.48) * mm});
            skLineSegment(sketch, "E2269", {"start": v(7.97, 7.48) * mm, "end": v(7.83, 7.53) * mm});
            skLineSegment(sketch, "E2270", {"start": v(7.83, 7.53) * mm, "end": v(7.54, 7.64) * mm});
            skLineSegment(sketch, "E2271", {"start": v(7.54, 7.64) * mm, "end": v(7.26, 7.78) * mm});
            skLineSegment(sketch, "E2272", {"start": v(7.26, 7.78) * mm, "end": v(6.7, 8.08) * mm});
            skLineSegment(sketch, "E2273", {"start": v(6.7, 8.08) * mm, "end": v(6.43, 8.22) * mm});
            skLineSegment(sketch, "E2274", {"start": v(6.43, 8.22) * mm, "end": v(6.17, 8.34) * mm});
            skLineSegment(sketch, "E2275", {"start": v(6.17, 8.34) * mm, "end": v(6.02, 7.63) * mm});
            skLineSegment(sketch, "E2276", {"start": v(6.02, 7.63) * mm, "end": v(5.94, 7.3) * mm});
            skLineSegment(sketch, "E2277", {"start": v(5.94, 7.3) * mm, "end": v(5.84, 6.97) * mm});
            skLineSegment(sketch, "E2278", {"start": v(5.84, 6.97) * mm, "end": v(5.74, 6.65) * mm});
            skLineSegment(sketch, "E2279", {"start": v(5.74, 6.65) * mm, "end": v(5.64, 6.4) * mm});
            skLineSegment(sketch, "E2280", {"start": v(5.64, 6.4) * mm, "end": v(5.42, 5.87) * mm});
            skLineSegment(sketch, "E2281", {"start": v(5.42, 5.87) * mm, "end": v(6.18, 5.5) * mm});
            skLineSegment(sketch, "E2282", {"start": v(6.18, 5.5) * mm, "end": v(6.35, 5.43) * mm});
            skLineSegment(sketch, "E2283", {"start": v(6.35, 5.43) * mm, "end": v(6.54, 5.37) * mm});
            skLineSegment(sketch, "E2284", {"start": v(6.54, 5.37) * mm, "end": v(6.74, 5.3) * mm});
            skLineSegment(sketch, "E2285", {"start": v(6.74, 5.3) * mm, "end": v(6.96, 5.24) * mm});
            skLineSegment(sketch, "E2286", {"start": v(6.96, 5.24) * mm, "end": v(7.18, 5.2) * mm});
            skLineSegment(sketch, "E2287", {"start": v(7.18, 5.2) * mm, "end": v(7.39, 5.16) * mm});
            skLineSegment(sketch, "E2288", {"start": v(7.39, 5.16) * mm, "end": v(7.6, 5.13) * mm});
            skLineSegment(sketch, "E2289", {"start": v(7.6, 5.13) * mm, "end": v(7.78, 5.12) * mm});
            skLineSegment(sketch, "E2290", {"start": v(-2.87, 6.42) * mm, "end": v(-2.76, 6.43) * mm});
            skLineSegment(sketch, "E2291", {"start": v(-2.76, 6.43) * mm, "end": v(-2.61, 6.46) * mm});
            skLineSegment(sketch, "E2292", {"start": v(-2.61, 6.46) * mm, "end": v(-2.45, 6.52) * mm});
            skLineSegment(sketch, "E2293", {"start": v(-2.45, 6.52) * mm, "end": v(-2.26, 6.59) * mm});
            skLineSegment(sketch, "E2294", {"start": v(-2.26, 6.59) * mm, "end": v(-2.06, 6.67) * mm});
            skLineSegment(sketch, "E2295", {"start": v(-2.06, 6.67) * mm, "end": v(-1.86, 6.77) * mm});
            skLineSegment(sketch, "E2296", {"start": v(-1.86, 6.77) * mm, "end": v(-1.65, 6.87) * mm});
            skLineSegment(sketch, "E2297", {"start": v(-1.65, 6.87) * mm, "end": v(-1.45, 6.99) * mm});
            skLineSegment(sketch, "E2298", {"start": v(-1.45, 6.99) * mm, "end": v(-0.5, 7.55) * mm});
            skLineSegment(sketch, "E2299", {"start": v(-0.5, 7.55) * mm, "end": v(-0.72, 8.22) * mm});
            skLineSegment(sketch, "E2300", {"start": v(-0.72, 8.22) * mm, "end": v(-0.81, 8.54) * mm});
            skLineSegment(sketch, "E2301", {"start": v(-0.81, 8.54) * mm, "end": v(-0.9, 8.92) * mm});
            skLineSegment(sketch, "E2302", {"start": v(-0.9, 8.92) * mm, "end": v(-0.94, 9.3) * mm});
            skLineSegment(sketch, "E2303", {"start": v(-0.94, 9.3) * mm, "end": v(-0.96, 9.47) * mm});
            skLineSegment(sketch, "E2304", {"start": v(-0.96, 9.47) * mm, "end": v(-0.97, 9.64) * mm});
            skLineSegment(sketch, "E2305", {"start": v(-0.97, 9.64) * mm, "end": v(-0.98, 9.95) * mm});
            skLineSegment(sketch, "E2306", {"start": v(-0.98, 9.95) * mm, "end": v(-1, 10.07) * mm});
            skLineSegment(sketch, "E2307", {"start": v(-1, 10.07) * mm, "end": v(-1.02, 10.17) * mm});
            skLineSegment(sketch, "E2308", {"start": v(-1.02, 10.17) * mm, "end": v(-1.04, 10.24) * mm});
            skLineSegment(sketch, "E2309", {"start": v(-1.04, 10.24) * mm, "end": v(-1.08, 10.3) * mm});
            skLineSegment(sketch, "E2310", {"start": v(-1.08, 10.3) * mm, "end": v(-1.12, 10.32) * mm});
            skLineSegment(sketch, "E2311", {"start": v(-1.12, 10.32) * mm, "end": v(-1.16, 10.33) * mm});
            skLineSegment(sketch, "E2312", {"start": v(-1.16, 10.33) * mm, "end": v(-1.22, 10.31) * mm});
            skLineSegment(sketch, "E2313", {"start": v(-1.22, 10.31) * mm, "end": v(-1.3, 10.27) * mm});
            skLineSegment(sketch, "E2314", {"start": v(-1.3, 10.27) * mm, "end": v(-1.37, 10.2) * mm});
            skLineSegment(sketch, "E2315", {"start": v(-1.37, 10.2) * mm, "end": v(-1.46, 10.12) * mm});
            skLineSegment(sketch, "E2316", {"start": v(-1.46, 10.12) * mm, "end": v(-1.68, 9.88) * mm});
            skLineSegment(sketch, "E2317", {"start": v(-1.68, 9.88) * mm, "end": v(-1.96, 9.54) * mm});
            skLineSegment(sketch, "E2318", {"start": v(-1.96, 9.54) * mm, "end": v(-2.11, 9.32) * mm});
            skLineSegment(sketch, "E2319", {"start": v(-2.11, 9.32) * mm, "end": v(-2.27, 9.08) * mm});
            skLineSegment(sketch, "E2320", {"start": v(-2.27, 9.08) * mm, "end": v(-2.35, 8.96) * mm});
            skLineSegment(sketch, "E2321", {"start": v(-2.35, 8.96) * mm, "end": v(-2.44, 8.86) * mm});
            skLineSegment(sketch, "E2322", {"start": v(-2.44, 8.86) * mm, "end": v(-2.53, 8.77) * mm});
            skLineSegment(sketch, "E2323", {"start": v(-2.53, 8.77) * mm, "end": v(-2.64, 8.7) * mm});
            skLineSegment(sketch, "E2324", {"start": v(-2.64, 8.7) * mm, "end": v(-2.71, 8.66) * mm});
            skLineSegment(sketch, "E2325", {"start": v(-2.71, 8.66) * mm, "end": v(-2.8, 8.64) * mm});
            skLineSegment(sketch, "E2326", {"start": v(-2.8, 8.64) * mm, "end": v(-2.97, 8.6) * mm});
            skLineSegment(sketch, "E2327", {"start": v(-2.97, 8.6) * mm, "end": v(-3.16, 8.58) * mm});
            skLineSegment(sketch, "E2328", {"start": v(-3.16, 8.58) * mm, "end": v(-3.36, 8.58) * mm});
            skLineSegment(sketch, "E2329", {"start": v(-3.36, 8.58) * mm, "end": v(-3.76, 8.6) * mm});
            skLineSegment(sketch, "E2330", {"start": v(-3.76, 8.6) * mm, "end": v(-3.94, 8.6) * mm});
            skLineSegment(sketch, "E2331", {"start": v(-3.94, 8.6) * mm, "end": v(-4.12, 8.59) * mm});
            skLineSegment(sketch, "E2332", {"start": v(-4.12, 8.59) * mm, "end": v(-4.1, 8.3) * mm});
            skLineSegment(sketch, "E2333", {"start": v(-4.1, 8.3) * mm, "end": v(-4.08, 8.05) * mm});
            skLineSegment(sketch, "E2334", {"start": v(-4.08, 8.05) * mm, "end": v(-4.03, 7.8) * mm});
            skLineSegment(sketch, "E2335", {"start": v(-4.03, 7.8) * mm, "end": v(-3.96, 7.53) * mm});
            skLineSegment(sketch, "E2336", {"start": v(-3.96, 7.53) * mm, "end": v(-3.92, 7.37) * mm});
            skLineSegment(sketch, "E2337", {"start": v(-3.92, 7.37) * mm, "end": v(-3.87, 7.16) * mm});
            skLineSegment(sketch, "E2338", {"start": v(-3.87, 7.16) * mm, "end": v(-3.8, 6.96) * mm});
            skLineSegment(sketch, "E2339", {"start": v(-3.8, 6.96) * mm, "end": v(-3.77, 6.87) * mm});
            skLineSegment(sketch, "E2340", {"start": v(-3.77, 6.87) * mm, "end": v(-3.72, 6.82) * mm});
            skLineSegment(sketch, "E2341", {"start": v(-3.72, 6.82) * mm, "end": v(-3.64, 6.74) * mm});
            skLineSegment(sketch, "E2342", {"start": v(-3.64, 6.74) * mm, "end": v(-3.53, 6.66) * mm});
            skLineSegment(sketch, "E2343", {"start": v(-3.53, 6.66) * mm, "end": v(-3.42, 6.6) * mm});
            skLineSegment(sketch, "E2344", {"start": v(-3.42, 6.6) * mm, "end": v(-3.3, 6.54) * mm});
            skLineSegment(sketch, "E2345", {"start": v(-3.3, 6.54) * mm, "end": v(-3.2, 6.49) * mm});
            skLineSegment(sketch, "E2346", {"start": v(-3.2, 6.49) * mm, "end": v(-3.08, 6.45) * mm});
            skLineSegment(sketch, "E2347", {"start": v(-3.08, 6.45) * mm, "end": v(-2.97, 6.43) * mm});
            skLineSegment(sketch, "E2348", {"start": v(-2.97, 6.43) * mm, "end": v(-2.87, 6.42) * mm});
            skLineSegment(sketch, "E2349", {"start": v(4.34, 6.43) * mm, "end": v(5.05, 6.42) * mm});
            skLineSegment(sketch, "E2350", {"start": v(5.05, 6.42) * mm, "end": v(5.25, 6.94) * mm});
            skLineSegment(sketch, "E2351", {"start": v(5.25, 6.94) * mm, "end": v(5.33, 7.18) * mm});
            skLineSegment(sketch, "E2352", {"start": v(5.33, 7.18) * mm, "end": v(5.4, 7.45) * mm});
            skLineSegment(sketch, "E2353", {"start": v(5.4, 7.45) * mm, "end": v(5.43, 7.7) * mm});
            skLineSegment(sketch, "E2354", {"start": v(5.43, 7.7) * mm, "end": v(5.45, 7.93) * mm});
            skLineSegment(sketch, "E2355", {"start": v(5.45, 7.93) * mm, "end": v(5.45, 8.4) * mm});
            skLineSegment(sketch, "E2356", {"start": v(5.45, 8.4) * mm, "end": v(4.95, 8.4) * mm});
            skLineSegment(sketch, "E2357", {"start": v(4.95, 8.4) * mm, "end": v(4.84, 8.41) * mm});
            skLineSegment(sketch, "E2358", {"start": v(4.84, 8.41) * mm, "end": v(4.71, 8.45) * mm});
            skLineSegment(sketch, "E2359", {"start": v(4.71, 8.45) * mm, "end": v(4.57, 8.5) * mm});
            skLineSegment(sketch, "E2360", {"start": v(4.57, 8.5) * mm, "end": v(4.42, 8.58) * mm});
            skLineSegment(sketch, "E2361", {"start": v(4.42, 8.58) * mm, "end": v(4.27, 8.68) * mm});
            skLineSegment(sketch, "E2362", {"start": v(4.27, 8.68) * mm, "end": v(4.12, 8.78) * mm});
            skLineSegment(sketch, "E2363", {"start": v(4.12, 8.78) * mm, "end": v(3.97, 8.9) * mm});
            skLineSegment(sketch, "E2364", {"start": v(3.97, 8.9) * mm, "end": v(3.83, 9.02) * mm});
            skLineSegment(sketch, "E2365", {"start": v(3.83, 9.02) * mm, "end": v(3.21, 9.65) * mm});
            skLineSegment(sketch, "E2366", {"start": v(3.21, 9.65) * mm, "end": v(2.51, 8.7) * mm});
            skLineSegment(sketch, "E2367", {"start": v(2.51, 8.7) * mm, "end": v(2.24, 8.33) * mm});
            skLineSegment(sketch, "E2368", {"start": v(2.24, 8.33) * mm, "end": v(2.02, 8) * mm});
            skLineSegment(sketch, "E2369", {"start": v(2.02, 8) * mm, "end": v(1.87, 7.74) * mm});
            skLineSegment(sketch, "E2370", {"start": v(1.87, 7.74) * mm, "end": v(1.83, 7.65) * mm});
            skLineSegment(sketch, "E2371", {"start": v(1.83, 7.65) * mm, "end": v(1.82, 7.6) * mm});
            skLineSegment(sketch, "E2372", {"start": v(1.82, 7.6) * mm, "end": v(1.82, 7.57) * mm});
            skLineSegment(sketch, "E2373", {"start": v(1.82, 7.57) * mm, "end": v(1.84, 7.53) * mm});
            skLineSegment(sketch, "E2374", {"start": v(1.84, 7.53) * mm, "end": v(1.9, 7.46) * mm});
            skLineSegment(sketch, "E2375", {"start": v(1.9, 7.46) * mm, "end": v(2, 7.37) * mm});
            skLineSegment(sketch, "E2376", {"start": v(2, 7.37) * mm, "end": v(2.11, 7.29) * mm});
            skLineSegment(sketch, "E2377", {"start": v(2.11, 7.29) * mm, "end": v(2.26, 7.2) * mm});
            skLineSegment(sketch, "E2378", {"start": v(2.26, 7.2) * mm, "end": v(2.43, 7.1) * mm});
            skLineSegment(sketch, "E2379", {"start": v(2.43, 7.1) * mm, "end": v(2.81, 6.9) * mm});
            skLineSegment(sketch, "E2380", {"start": v(2.81, 6.9) * mm, "end": v(3.23, 6.72) * mm});
            skLineSegment(sketch, "E2381", {"start": v(3.23, 6.72) * mm, "end": v(3.65, 6.58) * mm});
            skLineSegment(sketch, "E2382", {"start": v(3.65, 6.58) * mm, "end": v(3.85, 6.52) * mm});
            skLineSegment(sketch, "E2383", {"start": v(3.85, 6.52) * mm, "end": v(4.03, 6.47) * mm});
            skLineSegment(sketch, "E2384", {"start": v(4.03, 6.47) * mm, "end": v(4.2, 6.44) * mm});
            skLineSegment(sketch, "E2385", {"start": v(4.2, 6.44) * mm, "end": v(4.34, 6.43) * mm});
            skLineSegment(sketch, "E2386", {"start": v(37.54, 7.44) * mm, "end": v(39.1, 7.4) * mm});
            skLineSegment(sketch, "E2387", {"start": v(39.1, 7.4) * mm, "end": v(40.43, 8.73) * mm});
            skLineSegment(sketch, "E2388", {"start": v(40.43, 8.73) * mm, "end": v(40.42, 9.64) * mm});
            skLineSegment(sketch, "E2389", {"start": v(40.42, 9.64) * mm, "end": v(40.4, 10.05) * mm});
            skLineSegment(sketch, "E2390", {"start": v(40.4, 10.05) * mm, "end": v(40.36, 10.5) * mm});
            skLineSegment(sketch, "E2391", {"start": v(40.36, 10.5) * mm, "end": v(40.3, 10.93) * mm});
            skLineSegment(sketch, "E2392", {"start": v(40.3, 10.93) * mm, "end": v(40.26, 11.12) * mm});
            skLineSegment(sketch, "E2393", {"start": v(40.26, 11.12) * mm, "end": v(40.22, 11.29) * mm});
            skLineSegment(sketch, "E2394", {"start": v(40.22, 11.29) * mm, "end": v(40.02, 12.03) * mm});
            skLineSegment(sketch, "E2395", {"start": v(40.02, 12.03) * mm, "end": v(38.77, 12.03) * mm});
            skLineSegment(sketch, "E2396", {"start": v(38.77, 12.03) * mm, "end": v(38.47, 12.04) * mm});
            skLineSegment(sketch, "E2397", {"start": v(38.47, 12.04) * mm, "end": v(38.08, 12.07) * mm});
            skLineSegment(sketch, "E2398", {"start": v(38.08, 12.07) * mm, "end": v(37.63, 12.12) * mm});
            skLineSegment(sketch, "E2399", {"start": v(37.63, 12.12) * mm, "end": v(37.13, 12.18) * mm});
            skLineSegment(sketch, "E2400", {"start": v(37.13, 12.18) * mm, "end": v(36.6, 12.26) * mm});
            skLineSegment(sketch, "E2401", {"start": v(36.6, 12.26) * mm, "end": v(36.04, 12.35) * mm});
            skLineSegment(sketch, "E2402", {"start": v(36.04, 12.35) * mm, "end": v(35.48, 12.45) * mm});
            skLineSegment(sketch, "E2403", {"start": v(35.48, 12.45) * mm, "end": v(34.93, 12.56) * mm});
            skLineSegment(sketch, "E2404", {"start": v(34.93, 12.56) * mm, "end": v(34.3, 12.67) * mm});
            skLineSegment(sketch, "E2405", {"start": v(34.3, 12.67) * mm, "end": v(33.63, 12.8) * mm});
            skLineSegment(sketch, "E2406", {"start": v(33.63, 12.8) * mm, "end": v(33.29, 12.85) * mm});
            skLineSegment(sketch, "E2407", {"start": v(33.29, 12.85) * mm, "end": v(32.96, 12.92) * mm});
            skLineSegment(sketch, "E2408", {"start": v(32.96, 12.92) * mm, "end": v(32.64, 13) * mm});
            skLineSegment(sketch, "E2409", {"start": v(32.64, 13) * mm, "end": v(32.34, 13.1) * mm});
            skLineSegment(sketch, "E2410", {"start": v(32.34, 13.1) * mm, "end": v(32.13, 13.17) * mm});
            skLineSegment(sketch, "E2411", {"start": v(32.13, 13.17) * mm, "end": v(31.9, 13.26) * mm});
            skLineSegment(sketch, "E2412", {"start": v(31.9, 13.26) * mm, "end": v(31.46, 13.48) * mm});
            skLineSegment(sketch, "E2413", {"start": v(31.46, 13.48) * mm, "end": v(31, 13.7) * mm});
            skLineSegment(sketch, "E2414", {"start": v(31, 13.7) * mm, "end": v(30.59, 13.91) * mm});
            skLineSegment(sketch, "E2415", {"start": v(30.59, 13.91) * mm, "end": v(29.9, 14.22) * mm});
            skLineSegment(sketch, "E2416", {"start": v(29.9, 14.22) * mm, "end": v(29.33, 14.46) * mm});
            skLineSegment(sketch, "E2417", {"start": v(29.33, 14.46) * mm, "end": v(29.1, 14.54) * mm});
            skLineSegment(sketch, "E2418", {"start": v(29.1, 14.54) * mm, "end": v(28.93, 14.6) * mm});
            skLineSegment(sketch, "E2419", {"start": v(28.93, 14.6) * mm, "end": v(28.81, 14.63) * mm});
            skLineSegment(sketch, "E2420", {"start": v(28.81, 14.63) * mm, "end": v(28.78, 14.63) * mm});
            skLineSegment(sketch, "E2421", {"start": v(28.78, 14.63) * mm, "end": v(28.76, 14.62) * mm});
            skLineSegment(sketch, "E2422", {"start": v(28.76, 14.62) * mm, "end": v(28.48, 14.03) * mm});
            skLineSegment(sketch, "E2423", {"start": v(28.48, 14.03) * mm, "end": v(27.9, 12.78) * mm});
            skLineSegment(sketch, "E2424", {"start": v(27.9, 12.78) * mm, "end": v(27.13, 11.06) * mm});
            skLineSegment(sketch, "E2425", {"start": v(27.13, 11.06) * mm, "end": v(27.54, 10.56) * mm});
            skLineSegment(sketch, "E2426", {"start": v(27.54, 10.56) * mm, "end": v(27.66, 10.45) * mm});
            skLineSegment(sketch, "E2427", {"start": v(27.66, 10.45) * mm, "end": v(27.85, 10.3) * mm});
            skLineSegment(sketch, "E2428", {"start": v(27.85, 10.3) * mm, "end": v(28.1, 10.13) * mm});
            skLineSegment(sketch, "E2429", {"start": v(28.1, 10.13) * mm, "end": v(28.38, 9.94) * mm});
            skLineSegment(sketch, "E2430", {"start": v(28.38, 9.94) * mm, "end": v(28.7, 9.75) * mm});
            skLineSegment(sketch, "E2431", {"start": v(28.7, 9.75) * mm, "end": v(29.06, 9.55) * mm});
            skLineSegment(sketch, "E2432", {"start": v(29.06, 9.55) * mm, "end": v(29.44, 9.35) * mm});
            skLineSegment(sketch, "E2433", {"start": v(29.44, 9.35) * mm, "end": v(29.82, 9.15) * mm});
            skLineSegment(sketch, "E2434", {"start": v(29.82, 9.15) * mm, "end": v(30.26, 8.92) * mm});
            skLineSegment(sketch, "E2435", {"start": v(30.26, 8.92) * mm, "end": v(30.74, 8.67) * mm});
            skLineSegment(sketch, "E2436", {"start": v(30.74, 8.67) * mm, "end": v(30.98, 8.54) * mm});
            skLineSegment(sketch, "E2437", {"start": v(30.98, 8.54) * mm, "end": v(31.22, 8.43) * mm});
            skLineSegment(sketch, "E2438", {"start": v(31.22, 8.43) * mm, "end": v(31.45, 8.32) * mm});
            skLineSegment(sketch, "E2439", {"start": v(31.45, 8.32) * mm, "end": v(31.68, 8.24) * mm});
            skLineSegment(sketch, "E2440", {"start": v(31.68, 8.24) * mm, "end": v(31.93, 8.17) * mm});
            skLineSegment(sketch, "E2441", {"start": v(31.93, 8.17) * mm, "end": v(32.19, 8.11) * mm});
            skLineSegment(sketch, "E2442", {"start": v(32.19, 8.11) * mm, "end": v(32.75, 8.02) * mm});
            skLineSegment(sketch, "E2443", {"start": v(32.75, 8.02) * mm, "end": v(33.3, 7.94) * mm});
            skLineSegment(sketch, "E2444", {"start": v(33.3, 7.94) * mm, "end": v(33.83, 7.86) * mm});
            skLineSegment(sketch, "E2445", {"start": v(33.83, 7.86) * mm, "end": v(34.29, 7.78) * mm});
            skLineSegment(sketch, "E2446", {"start": v(34.29, 7.78) * mm, "end": v(34.78, 7.7) * mm});
            skLineSegment(sketch, "E2447", {"start": v(34.78, 7.7) * mm, "end": v(35.8, 7.58) * mm});
            skLineSegment(sketch, "E2448", {"start": v(35.8, 7.58) * mm, "end": v(36.3, 7.52) * mm});
            skLineSegment(sketch, "E2449", {"start": v(36.3, 7.52) * mm, "end": v(36.76, 7.48) * mm});
            skLineSegment(sketch, "E2450", {"start": v(36.76, 7.48) * mm, "end": v(37.18, 7.46) * mm});
            skLineSegment(sketch, "E2451", {"start": v(37.18, 7.46) * mm, "end": v(37.54, 7.44) * mm});
            skLineSegment(sketch, "E2452", {"start": v(-7.07, 8.07) * mm, "end": v(-6.93, 8.08) * mm});
            skLineSegment(sketch, "E2453", {"start": v(-6.93, 8.08) * mm, "end": v(-6.77, 8.1) * mm});
            skLineSegment(sketch, "E2454", {"start": v(-6.77, 8.1) * mm, "end": v(-6.6, 8.13) * mm});
            skLineSegment(sketch, "E2455", {"start": v(-6.6, 8.13) * mm, "end": v(-6.41, 8.17) * mm});
            skLineSegment(sketch, "E2456", {"start": v(-6.41, 8.17) * mm, "end": v(-6.23, 8.22) * mm});
            skLineSegment(sketch, "E2457", {"start": v(-6.23, 8.22) * mm, "end": v(-6.04, 8.28) * mm});
            skLineSegment(sketch, "E2458", {"start": v(-6.04, 8.28) * mm, "end": v(-5.86, 8.35) * mm});
            skLineSegment(sketch, "E2459", {"start": v(-5.86, 8.35) * mm, "end": v(-5.7, 8.42) * mm});
            skLineSegment(sketch, "E2460", {"start": v(-5.7, 8.42) * mm, "end": v(-4.93, 8.77) * mm});
            skLineSegment(sketch, "E2461", {"start": v(-4.93, 8.77) * mm, "end": v(-4.9, 10.07) * mm});
            skLineSegment(sketch, "E2462", {"start": v(-4.9, 10.07) * mm, "end": v(-4.89, 10.98) * mm});
            skLineSegment(sketch, "E2463", {"start": v(-4.89, 10.98) * mm, "end": v(-4.9, 11.26) * mm});
            skLineSegment(sketch, "E2464", {"start": v(-4.9, 11.26) * mm, "end": v(-4.9, 11.33) * mm});
            skLineSegment(sketch, "E2465", {"start": v(-4.9, 11.33) * mm, "end": v(-4.9, 11.35) * mm});
            skLineSegment(sketch, "E2466", {"start": v(-4.9, 11.35) * mm, "end": v(-6.6, 10.9) * mm});
            skLineSegment(sketch, "E2467", {"start": v(-6.6, 10.9) * mm, "end": v(-6.79, 10.87) * mm});
            skLineSegment(sketch, "E2468", {"start": v(-6.79, 10.87) * mm, "end": v(-7, 10.83) * mm});
            skLineSegment(sketch, "E2469", {"start": v(-7, 10.83) * mm, "end": v(-7.4, 10.77) * mm});
            skLineSegment(sketch, "E2470", {"start": v(-7.4, 10.77) * mm, "end": v(-7.6, 10.73) * mm});
            skLineSegment(sketch, "E2471", {"start": v(-7.6, 10.73) * mm, "end": v(-7.8, 10.66) * mm});
            skLineSegment(sketch, "E2472", {"start": v(-7.8, 10.66) * mm, "end": v(-7.88, 10.62) * mm});
            skLineSegment(sketch, "E2473", {"start": v(-7.88, 10.62) * mm, "end": v(-7.96, 10.57) * mm});
            skLineSegment(sketch, "E2474", {"start": v(-7.96, 10.57) * mm, "end": v(-8.03, 10.52) * mm});
            skLineSegment(sketch, "E2475", {"start": v(-8.03, 10.52) * mm, "end": v(-8.1, 10.45) * mm});
            skLineSegment(sketch, "E2476", {"start": v(-8.1, 10.45) * mm, "end": v(-8.15, 10.39) * mm});
            skLineSegment(sketch, "E2477", {"start": v(-8.15, 10.39) * mm, "end": v(-8.2, 10.32) * mm});
            skLineSegment(sketch, "E2478", {"start": v(-8.2, 10.32) * mm, "end": v(-8.27, 10.16) * mm});
            skLineSegment(sketch, "E2479", {"start": v(-8.27, 10.16) * mm, "end": v(-8.32, 10) * mm});
            skLineSegment(sketch, "E2480", {"start": v(-8.32, 10) * mm, "end": v(-8.34, 9.82) * mm});
            skLineSegment(sketch, "E2481", {"start": v(-8.34, 9.82) * mm, "end": v(-8.35, 9.64) * mm});
            skLineSegment(sketch, "E2482", {"start": v(-8.35, 9.64) * mm, "end": v(-8.34, 9.46) * mm});
            skLineSegment(sketch, "E2483", {"start": v(-8.34, 9.46) * mm, "end": v(-8.3, 9.28) * mm});
            skLineSegment(sketch, "E2484", {"start": v(-8.3, 9.28) * mm, "end": v(-8.27, 9.11) * mm});
            skLineSegment(sketch, "E2485", {"start": v(-8.27, 9.11) * mm, "end": v(-8.18, 8.82) * mm});
            skLineSegment(sketch, "E2486", {"start": v(-8.18, 8.82) * mm, "end": v(-8.13, 8.67) * mm});
            skLineSegment(sketch, "E2487", {"start": v(-8.13, 8.67) * mm, "end": v(-8.06, 8.52) * mm});
            skLineSegment(sketch, "E2488", {"start": v(-8.06, 8.52) * mm, "end": v(-7.98, 8.37) * mm});
            skLineSegment(sketch, "E2489", {"start": v(-7.98, 8.37) * mm, "end": v(-7.9, 8.25) * mm});
            skLineSegment(sketch, "E2490", {"start": v(-7.9, 8.25) * mm, "end": v(-7.79, 8.14) * mm});
            skLineSegment(sketch, "E2491", {"start": v(-7.79, 8.14) * mm, "end": v(-7.73, 8.1) * mm});
            skLineSegment(sketch, "E2492", {"start": v(-7.73, 8.1) * mm, "end": v(-7.67, 8.07) * mm});
            skLineSegment(sketch, "E2493", {"start": v(-7.67, 8.07) * mm, "end": v(-7.6, 8.05) * mm});
            skLineSegment(sketch, "E2494", {"start": v(-7.6, 8.05) * mm, "end": v(-7.53, 8.04) * mm});
            skLineSegment(sketch, "E2495", {"start": v(-7.53, 8.04) * mm, "end": v(-7.37, 8.04) * mm});
            skLineSegment(sketch, "E2496", {"start": v(-7.37, 8.04) * mm, "end": v(-7.21, 8.06) * mm});
            skLineSegment(sketch, "E2497", {"start": v(-7.21, 8.06) * mm, "end": v(-7.07, 8.07) * mm});
            skLineSegment(sketch, "E2498", {"start": v(12.44, 10.43) * mm, "end": v(13, 10.38) * mm});
            skLineSegment(sketch, "E2499", {"start": v(13, 10.38) * mm, "end": v(13.18, 10.64) * mm});
            skLineSegment(sketch, "E2500", {"start": v(13.18, 10.64) * mm, "end": v(13.38, 10.92) * mm});
            skLineSegment(sketch, "E2501", {"start": v(13.38, 10.92) * mm, "end": v(13.48, 11.06) * mm});
            skLineSegment(sketch, "E2502", {"start": v(13.48, 11.06) * mm, "end": v(13.55, 11.2) * mm});
            skLineSegment(sketch, "E2503", {"start": v(13.55, 11.2) * mm, "end": v(13.6, 11.35) * mm});
            skLineSegment(sketch, "E2504", {"start": v(13.6, 11.35) * mm, "end": v(13.62, 11.42) * mm});
            skLineSegment(sketch, "E2505", {"start": v(13.62, 11.42) * mm, "end": v(13.63, 11.5) * mm});
            skLineSegment(sketch, "E2506", {"start": v(13.63, 11.5) * mm, "end": v(13.62, 11.62) * mm});
            skLineSegment(sketch, "E2507", {"start": v(13.62, 11.62) * mm, "end": v(13.6, 11.76) * mm});
            skLineSegment(sketch, "E2508", {"start": v(13.6, 11.76) * mm, "end": v(13.57, 11.9) * mm});
            skLineSegment(sketch, "E2509", {"start": v(13.57, 11.9) * mm, "end": v(13.52, 12.03) * mm});
            skLineSegment(sketch, "E2510", {"start": v(13.52, 12.03) * mm, "end": v(13.47, 12.17) * mm});
            skLineSegment(sketch, "E2511", {"start": v(13.47, 12.17) * mm, "end": v(13.4, 12.3) * mm});
            skLineSegment(sketch, "E2512", {"start": v(13.4, 12.3) * mm, "end": v(13.25, 12.57) * mm});
            skLineSegment(sketch, "E2513", {"start": v(13.25, 12.57) * mm, "end": v(12.91, 13.1) * mm});
            skLineSegment(sketch, "E2514", {"start": v(12.91, 13.1) * mm, "end": v(12.75, 13.36) * mm});
            skLineSegment(sketch, "E2515", {"start": v(12.75, 13.36) * mm, "end": v(12.62, 13.6) * mm});
            skLineSegment(sketch, "E2516", {"start": v(12.62, 13.6) * mm, "end": v(11.1, 13.78) * mm});
            skLineSegment(sketch, "E2517", {"start": v(11.1, 13.78) * mm, "end": v(10.5, 13.83) * mm});
            skLineSegment(sketch, "E2518", {"start": v(10.5, 13.83) * mm, "end": v(9.99, 13.87) * mm});
            skLineSegment(sketch, "E2519", {"start": v(9.99, 13.87) * mm, "end": v(9.63, 13.87) * mm});
            skLineSegment(sketch, "E2520", {"start": v(9.63, 13.87) * mm, "end": v(9.52, 13.86) * mm});
            skLineSegment(sketch, "E2521", {"start": v(9.52, 13.86) * mm, "end": v(9.46, 13.84) * mm});
            skLineSegment(sketch, "E2522", {"start": v(9.46, 13.84) * mm, "end": v(9.46, 13.83) * mm});
            skLineSegment(sketch, "E2523", {"start": v(9.46, 13.83) * mm, "end": v(9.45, 13.8) * mm});
            skLineSegment(sketch, "E2524", {"start": v(9.45, 13.8) * mm, "end": v(9.47, 13.74) * mm});
            skLineSegment(sketch, "E2525", {"start": v(9.47, 13.74) * mm, "end": v(9.5, 13.64) * mm});
            skLineSegment(sketch, "E2526", {"start": v(9.5, 13.64) * mm, "end": v(9.55, 13.52) * mm});
            skLineSegment(sketch, "E2527", {"start": v(9.55, 13.52) * mm, "end": v(9.7, 13.23) * mm});
            skLineSegment(sketch, "E2528", {"start": v(9.7, 13.23) * mm, "end": v(9.9, 12.9) * mm});
            skLineSegment(sketch, "E2529", {"start": v(9.9, 12.9) * mm, "end": v(10.05, 12.7) * mm});
            skLineSegment(sketch, "E2530", {"start": v(10.05, 12.7) * mm, "end": v(10.23, 12.5) * mm});
            skLineSegment(sketch, "E2531", {"start": v(10.23, 12.5) * mm, "end": v(10.3, 12.4) * mm});
            skLineSegment(sketch, "E2532", {"start": v(10.3, 12.4) * mm, "end": v(10.37, 12.28) * mm});
            skLineSegment(sketch, "E2533", {"start": v(10.37, 12.28) * mm, "end": v(10.42, 12.17) * mm});
            skLineSegment(sketch, "E2534", {"start": v(10.42, 12.17) * mm, "end": v(10.45, 12.06) * mm});
            skLineSegment(sketch, "E2535", {"start": v(10.45, 12.06) * mm, "end": v(10.46, 11.98) * mm});
            skLineSegment(sketch, "E2536", {"start": v(10.46, 11.98) * mm, "end": v(10.46, 11.9) * mm});
            skLineSegment(sketch, "E2537", {"start": v(10.46, 11.9) * mm, "end": v(10.43, 11.74) * mm});
            skLineSegment(sketch, "E2538", {"start": v(10.43, 11.74) * mm, "end": v(10.38, 11.57) * mm});
            skLineSegment(sketch, "E2539", {"start": v(10.38, 11.57) * mm, "end": v(10.31, 11.4) * mm});
            skLineSegment(sketch, "E2540", {"start": v(10.31, 11.4) * mm, "end": v(10.16, 11.07) * mm});
            skLineSegment(sketch, "E2541", {"start": v(10.16, 11.07) * mm, "end": v(10.1, 10.9) * mm});
            skLineSegment(sketch, "E2542", {"start": v(10.1, 10.9) * mm, "end": v(10.04, 10.76) * mm});
            skLineSegment(sketch, "E2543", {"start": v(10.04, 10.76) * mm, "end": v(10.96, 10.62) * mm});
            skLineSegment(sketch, "E2544", {"start": v(10.96, 10.62) * mm, "end": v(11.78, 10.5) * mm});
            skLineSegment(sketch, "E2545", {"start": v(11.78, 10.5) * mm, "end": v(12.44, 10.43) * mm});
            skLineSegment(sketch, "E2546", {"start": v(39.22, 12.41) * mm, "end": v(40.16, 12.36) * mm});
            skLineSegment(sketch, "E2547", {"start": v(40.16, 12.36) * mm, "end": v(40.61, 12.6) * mm});
            skLineSegment(sketch, "E2548", {"start": v(40.61, 12.6) * mm, "end": v(41.1, 12.85) * mm});
            skLineSegment(sketch, "E2549", {"start": v(41.1, 12.85) * mm, "end": v(41.36, 12.98) * mm});
            skLineSegment(sketch, "E2550", {"start": v(41.36, 12.98) * mm, "end": v(41.59, 13.13) * mm});
            skLineSegment(sketch, "E2551", {"start": v(41.59, 13.13) * mm, "end": v(41.8, 13.28) * mm});
            skLineSegment(sketch, "E2552", {"start": v(41.8, 13.28) * mm, "end": v(41.9, 13.36) * mm});
            skLineSegment(sketch, "E2553", {"start": v(41.9, 13.36) * mm, "end": v(41.99, 13.44) * mm});
            skLineSegment(sketch, "E2554", {"start": v(41.99, 13.44) * mm, "end": v(42.16, 13.62) * mm});
            skLineSegment(sketch, "E2555", {"start": v(42.16, 13.62) * mm, "end": v(42.32, 13.83) * mm});
            skLineSegment(sketch, "E2556", {"start": v(42.32, 13.83) * mm, "end": v(42.48, 14.05) * mm});
            skLineSegment(sketch, "E2557", {"start": v(42.48, 14.05) * mm, "end": v(42.63, 14.3) * mm});
            skLineSegment(sketch, "E2558", {"start": v(42.63, 14.3) * mm, "end": v(42.77, 14.54) * mm});
            skLineSegment(sketch, "E2559", {"start": v(42.77, 14.54) * mm, "end": v(42.89, 14.78) * mm});
            skLineSegment(sketch, "E2560", {"start": v(42.89, 14.78) * mm, "end": v(42.99, 15.03) * mm});
            skLineSegment(sketch, "E2561", {"start": v(42.99, 15.03) * mm, "end": v(43.07, 15.27) * mm});
            skLineSegment(sketch, "E2562", {"start": v(43.07, 15.27) * mm, "end": v(43.11, 15.5) * mm});
            skLineSegment(sketch, "E2563", {"start": v(43.11, 15.5) * mm, "end": v(43.13, 15.75) * mm});
            skLineSegment(sketch, "E2564", {"start": v(43.13, 15.75) * mm, "end": v(43.14, 16.01) * mm});
            skLineSegment(sketch, "E2565", {"start": v(43.14, 16.01) * mm, "end": v(43.13, 16.28) * mm});
            skLineSegment(sketch, "E2566", {"start": v(43.13, 16.28) * mm, "end": v(43.09, 16.81) * mm});
            skLineSegment(sketch, "E2567", {"start": v(43.09, 16.81) * mm, "end": v(43.07, 17.07) * mm});
            skLineSegment(sketch, "E2568", {"start": v(43.07, 17.07) * mm, "end": v(43.07, 17.3) * mm});
            skLineSegment(sketch, "E2569", {"start": v(43.07, 17.3) * mm, "end": v(41, 17.32) * mm});
            skLineSegment(sketch, "E2570", {"start": v(41, 17.32) * mm, "end": v(40.54, 17.33) * mm});
            skLineSegment(sketch, "E2571", {"start": v(40.54, 17.33) * mm, "end": v(40, 17.36) * mm});
            skLineSegment(sketch, "E2572", {"start": v(40, 17.36) * mm, "end": v(39.42, 17.4) * mm});
            skLineSegment(sketch, "E2573", {"start": v(39.42, 17.4) * mm, "end": v(38.8, 17.46) * mm});
            skLineSegment(sketch, "E2574", {"start": v(38.8, 17.46) * mm, "end": v(38.18, 17.53) * mm});
            skLineSegment(sketch, "E2575", {"start": v(38.18, 17.53) * mm, "end": v(37.57, 17.6) * mm});
            skLineSegment(sketch, "E2576", {"start": v(37.57, 17.6) * mm, "end": v(36.98, 17.69) * mm});
            skLineSegment(sketch, "E2577", {"start": v(36.98, 17.69) * mm, "end": v(36.43, 17.78) * mm});
            skLineSegment(sketch, "E2578", {"start": v(36.43, 17.78) * mm, "end": v(35.82, 17.88) * mm});
            skLineSegment(sketch, "E2579", {"start": v(35.82, 17.88) * mm, "end": v(35.16, 17.97) * mm});
            skLineSegment(sketch, "E2580", {"start": v(35.16, 17.97) * mm, "end": v(34.83, 18.02) * mm});
            skLineSegment(sketch, "E2581", {"start": v(34.83, 18.02) * mm, "end": v(34.51, 18.08) * mm});
            skLineSegment(sketch, "E2582", {"start": v(34.51, 18.08) * mm, "end": v(34.2, 18.15) * mm});
            skLineSegment(sketch, "E2583", {"start": v(34.2, 18.15) * mm, "end": v(33.92, 18.23) * mm});
            skLineSegment(sketch, "E2584", {"start": v(33.92, 18.23) * mm, "end": v(33.73, 18.3) * mm});
            skLineSegment(sketch, "E2585", {"start": v(33.73, 18.3) * mm, "end": v(33.53, 18.37) * mm});
            skLineSegment(sketch, "E2586", {"start": v(33.53, 18.37) * mm, "end": v(33.12, 18.56) * mm});
            skLineSegment(sketch, "E2587", {"start": v(33.12, 18.56) * mm, "end": v(32.71, 18.75) * mm});
            skLineSegment(sketch, "E2588", {"start": v(32.71, 18.75) * mm, "end": v(32.34, 18.93) * mm});
            skLineSegment(sketch, "E2589", {"start": v(32.34, 18.93) * mm, "end": v(31.72, 19.2) * mm});
            skLineSegment(sketch, "E2590", {"start": v(31.72, 19.2) * mm, "end": v(31.2, 19.4) * mm});
            skLineSegment(sketch, "E2591", {"start": v(31.2, 19.4) * mm, "end": v(30.83, 19.52) * mm});
            skLineSegment(sketch, "E2592", {"start": v(30.83, 19.52) * mm, "end": v(30.72, 19.54) * mm});
            skLineSegment(sketch, "E2593", {"start": v(30.72, 19.54) * mm, "end": v(30.69, 19.55) * mm});
            skLineSegment(sketch, "E2594", {"start": v(30.69, 19.55) * mm, "end": v(30.67, 19.54) * mm});
            skLineSegment(sketch, "E2595", {"start": v(30.67, 19.54) * mm, "end": v(30.62, 19.46) * mm});
            skLineSegment(sketch, "E2596", {"start": v(30.62, 19.46) * mm, "end": v(30.55, 19.32) * mm});
            skLineSegment(sketch, "E2597", {"start": v(30.55, 19.32) * mm, "end": v(30.36, 18.86) * mm});
            skLineSegment(sketch, "E2598", {"start": v(30.36, 18.86) * mm, "end": v(30.12, 18.24) * mm});
            skLineSegment(sketch, "E2599", {"start": v(30.12, 18.24) * mm, "end": v(29.86, 17.54) * mm});
            skLineSegment(sketch, "E2600", {"start": v(29.86, 17.54) * mm, "end": v(29.62, 16.83) * mm});
            skLineSegment(sketch, "E2601", {"start": v(29.62, 16.83) * mm, "end": v(29.4, 16.19) * mm});
            skLineSegment(sketch, "E2602", {"start": v(29.4, 16.19) * mm, "end": v(29.26, 15.7) * mm});
            skLineSegment(sketch, "E2603", {"start": v(29.26, 15.7) * mm, "end": v(29.22, 15.52) * mm});
            skLineSegment(sketch, "E2604", {"start": v(29.22, 15.52) * mm, "end": v(29.2, 15.42) * mm});
            skLineSegment(sketch, "E2605", {"start": v(29.2, 15.42) * mm, "end": v(29.2, 15.01) * mm});
            skLineSegment(sketch, "E2606", {"start": v(29.2, 15.01) * mm, "end": v(30.52, 14.34) * mm});
            skLineSegment(sketch, "E2607", {"start": v(30.52, 14.34) * mm, "end": v(30.88, 14.17) * mm});
            skLineSegment(sketch, "E2608", {"start": v(30.88, 14.17) * mm, "end": v(31.29, 14) * mm});
            skLineSegment(sketch, "E2609", {"start": v(31.29, 14) * mm, "end": v(31.73, 13.83) * mm});
            skLineSegment(sketch, "E2610", {"start": v(31.73, 13.83) * mm, "end": v(32.2, 13.67) * mm});
            skLineSegment(sketch, "E2611", {"start": v(32.2, 13.67) * mm, "end": v(32.7, 13.52) * mm});
            skLineSegment(sketch, "E2612", {"start": v(32.7, 13.52) * mm, "end": v(33.24, 13.37) * mm});
            skLineSegment(sketch, "E2613", {"start": v(33.24, 13.37) * mm, "end": v(33.8, 13.23) * mm});
            skLineSegment(sketch, "E2614", {"start": v(33.8, 13.23) * mm, "end": v(34.36, 13.1) * mm});
            skLineSegment(sketch, "E2615", {"start": v(34.36, 13.1) * mm, "end": v(34.95, 12.97) * mm});
            skLineSegment(sketch, "E2616", {"start": v(34.95, 12.97) * mm, "end": v(35.55, 12.86) * mm});
            skLineSegment(sketch, "E2617", {"start": v(35.55, 12.86) * mm, "end": v(36.16, 12.75) * mm});
            skLineSegment(sketch, "E2618", {"start": v(36.16, 12.75) * mm, "end": v(36.78, 12.66) * mm});
            skLineSegment(sketch, "E2619", {"start": v(36.78, 12.66) * mm, "end": v(37.4, 12.58) * mm});
            skLineSegment(sketch, "E2620", {"start": v(37.4, 12.58) * mm, "end": v(38.01, 12.5) * mm});
            skLineSegment(sketch, "E2621", {"start": v(38.01, 12.5) * mm, "end": v(38.62, 12.45) * mm});
            skLineSegment(sketch, "E2622", {"start": v(38.62, 12.45) * mm, "end": v(39.22, 12.41) * mm});
            skLineSegment(sketch, "E2623", {"start": v(15.76, 13.06) * mm, "end": v(17, 13.02) * mm});
            skLineSegment(sketch, "E2624", {"start": v(17, 13.02) * mm, "end": v(17.02, 13.46) * mm});
            skLineSegment(sketch, "E2625", {"start": v(17.02, 13.46) * mm, "end": v(17.05, 13.93) * mm});
            skLineSegment(sketch, "E2626", {"start": v(17.05, 13.93) * mm, "end": v(17.06, 14.17) * mm});
            skLineSegment(sketch, "E2627", {"start": v(17.06, 14.17) * mm, "end": v(17.06, 14.4) * mm});
            skLineSegment(sketch, "E2628", {"start": v(17.06, 14.4) * mm, "end": v(17.04, 14.63) * mm});
            skLineSegment(sketch, "E2629", {"start": v(17.04, 14.63) * mm, "end": v(17, 14.83) * mm});
            skLineSegment(sketch, "E2630", {"start": v(17, 14.83) * mm, "end": v(16.96, 14.95) * mm});
            skLineSegment(sketch, "E2631", {"start": v(16.96, 14.95) * mm, "end": v(16.9, 15.07) * mm});
            skLineSegment(sketch, "E2632", {"start": v(16.9, 15.07) * mm, "end": v(16.79, 15.32) * mm});
            skLineSegment(sketch, "E2633", {"start": v(16.79, 15.32) * mm, "end": v(16.64, 15.56) * mm});
            skLineSegment(sketch, "E2634", {"start": v(16.64, 15.56) * mm, "end": v(16.48, 15.8) * mm});
            skLineSegment(sketch, "E2635", {"start": v(16.48, 15.8) * mm, "end": v(16.14, 16.27) * mm});
            skLineSegment(sketch, "E2636", {"start": v(16.14, 16.27) * mm, "end": v(15.98, 16.5) * mm});
            skLineSegment(sketch, "E2637", {"start": v(15.98, 16.5) * mm, "end": v(15.84, 16.71) * mm});
            skLineSegment(sketch, "E2638", {"start": v(15.84, 16.71) * mm, "end": v(12.5, 16.82) * mm});
            skLineSegment(sketch, "E2639", {"start": v(12.5, 16.82) * mm, "end": v(12.65, 16.58) * mm});
            skLineSegment(sketch, "E2640", {"start": v(12.65, 16.58) * mm, "end": v(12.84, 16.32) * mm});
            skLineSegment(sketch, "E2641", {"start": v(12.84, 16.32) * mm, "end": v(13.23, 15.8) * mm});
            skLineSegment(sketch, "E2642", {"start": v(13.23, 15.8) * mm, "end": v(13.41, 15.52) * mm});
            skLineSegment(sketch, "E2643", {"start": v(13.41, 15.52) * mm, "end": v(13.5, 15.38) * mm});
            skLineSegment(sketch, "E2644", {"start": v(13.5, 15.38) * mm, "end": v(13.57, 15.25) * mm});
            skLineSegment(sketch, "E2645", {"start": v(13.57, 15.25) * mm, "end": v(13.64, 15.1) * mm});
            skLineSegment(sketch, "E2646", {"start": v(13.64, 15.1) * mm, "end": v(13.69, 14.97) * mm});
            skLineSegment(sketch, "E2647", {"start": v(13.69, 14.97) * mm, "end": v(13.73, 14.83) * mm});
            skLineSegment(sketch, "E2648", {"start": v(13.73, 14.83) * mm, "end": v(13.75, 14.7) * mm});
            skLineSegment(sketch, "E2649", {"start": v(13.75, 14.7) * mm, "end": v(13.75, 14.61) * mm});
            skLineSegment(sketch, "E2650", {"start": v(13.75, 14.61) * mm, "end": v(13.75, 14.54) * mm});
            skLineSegment(sketch, "E2651", {"start": v(13.75, 14.54) * mm, "end": v(13.72, 14.37) * mm});
            skLineSegment(sketch, "E2652", {"start": v(13.72, 14.37) * mm, "end": v(13.67, 14.2) * mm});
            skLineSegment(sketch, "E2653", {"start": v(13.67, 14.2) * mm, "end": v(13.6, 14.04) * mm});
            skLineSegment(sketch, "E2654", {"start": v(13.6, 14.04) * mm, "end": v(13.46, 13.71) * mm});
            skLineSegment(sketch, "E2655", {"start": v(13.46, 13.71) * mm, "end": v(13.4, 13.55) * mm});
            skLineSegment(sketch, "E2656", {"start": v(13.4, 13.55) * mm, "end": v(13.34, 13.4) * mm});
            skLineSegment(sketch, "E2657", {"start": v(13.34, 13.4) * mm, "end": v(13.93, 13.25) * mm});
            skLineSegment(sketch, "E2658", {"start": v(13.93, 13.25) * mm, "end": v(14.08, 13.22) * mm});
            skLineSegment(sketch, "E2659", {"start": v(14.08, 13.22) * mm, "end": v(14.26, 13.19) * mm});
            skLineSegment(sketch, "E2660", {"start": v(14.26, 13.19) * mm, "end": v(14.71, 13.13) * mm});
            skLineSegment(sketch, "E2661", {"start": v(14.71, 13.13) * mm, "end": v(15.23, 13.08) * mm});
            skLineSegment(sketch, "E2662", {"start": v(15.23, 13.08) * mm, "end": v(15.76, 13.06) * mm});
            skLineSegment(sketch, "E2663", {"start": v(-58.46, 17.07) * mm, "end": v(-57.81, 17.39) * mm});
            skLineSegment(sketch, "E2664", {"start": v(-57.81, 17.39) * mm, "end": v(-57.11, 17.72) * mm});
            skLineSegment(sketch, "E2665", {"start": v(-57.11, 17.72) * mm, "end": v(-56.76, 17.9) * mm});
            skLineSegment(sketch, "E2666", {"start": v(-56.76, 17.9) * mm, "end": v(-56.42, 18.08) * mm});
            skLineSegment(sketch, "E2667", {"start": v(-56.42, 18.08) * mm, "end": v(-56.1, 18.27) * mm});
            skLineSegment(sketch, "E2668", {"start": v(-56.1, 18.27) * mm, "end": v(-55.82, 18.46) * mm});
            skLineSegment(sketch, "E2669", {"start": v(-55.82, 18.46) * mm, "end": v(-55.28, 18.88) * mm});
            skLineSegment(sketch, "E2670", {"start": v(-55.28, 18.88) * mm, "end": v(-54.72, 19.34) * mm});
            skLineSegment(sketch, "E2671", {"start": v(-54.72, 19.34) * mm, "end": v(-54.16, 19.84) * mm});
            skLineSegment(sketch, "E2672", {"start": v(-54.16, 19.84) * mm, "end": v(-53.6, 20.37) * mm});
            skLineSegment(sketch, "E2673", {"start": v(-53.6, 20.37) * mm, "end": v(-53.07, 20.92) * mm});
            skLineSegment(sketch, "E2674", {"start": v(-53.07, 20.92) * mm, "end": v(-52.57, 21.47) * mm});
            skLineSegment(sketch, "E2675", {"start": v(-52.57, 21.47) * mm, "end": v(-52.33, 21.75) * mm});
            skLineSegment(sketch, "E2676", {"start": v(-52.33, 21.75) * mm, "end": v(-52.1, 22.02) * mm});
            skLineSegment(sketch, "E2677", {"start": v(-52.1, 22.02) * mm, "end": v(-51.9, 22.3) * mm});
            skLineSegment(sketch, "E2678", {"start": v(-51.9, 22.3) * mm, "end": v(-51.7, 22.57) * mm});
            skLineSegment(sketch, "E2679", {"start": v(-51.7, 22.57) * mm, "end": v(-51.54, 22.8) * mm});
            skLineSegment(sketch, "E2680", {"start": v(-51.54, 22.8) * mm, "end": v(-51.39, 23.03) * mm});
            skLineSegment(sketch, "E2681", {"start": v(-51.39, 23.03) * mm, "end": v(-51.1, 23.54) * mm});
            skLineSegment(sketch, "E2682", {"start": v(-51.1, 23.54) * mm, "end": v(-50.8, 24.08) * mm});
            skLineSegment(sketch, "E2683", {"start": v(-50.8, 24.08) * mm, "end": v(-50.53, 24.64) * mm});
            skLineSegment(sketch, "E2684", {"start": v(-50.53, 24.64) * mm, "end": v(-50.28, 25.2) * mm});
            skLineSegment(sketch, "E2685", {"start": v(-50.28, 25.2) * mm, "end": v(-50.05, 25.78) * mm});
            skLineSegment(sketch, "E2686", {"start": v(-50.05, 25.78) * mm, "end": v(-49.84, 26.33) * mm});
            skLineSegment(sketch, "E2687", {"start": v(-49.84, 26.33) * mm, "end": v(-49.67, 26.86) * mm});
            skLineSegment(sketch, "E2688", {"start": v(-49.67, 26.86) * mm, "end": v(-49.56, 27.17) * mm});
            skLineSegment(sketch, "E2689", {"start": v(-49.56, 27.17) * mm, "end": v(-49.41, 27.53) * mm});
            skLineSegment(sketch, "E2690", {"start": v(-49.41, 27.53) * mm, "end": v(-49.27, 27.9) * mm});
            skLineSegment(sketch, "E2691", {"start": v(-49.27, 27.9) * mm, "end": v(-49.14, 28.29) * mm});
            skLineSegment(sketch, "E2692", {"start": v(-49.14, 28.29) * mm, "end": v(-49.09, 28.48) * mm});
            skLineSegment(sketch, "E2693", {"start": v(-49.09, 28.48) * mm, "end": v(-49.05, 28.66) * mm});
            skLineSegment(sketch, "E2694", {"start": v(-49.05, 28.66) * mm, "end": v(-49.02, 28.84) * mm});
            skLineSegment(sketch, "E2695", {"start": v(-49.02, 28.84) * mm, "end": v(-49.02, 29) * mm});
            skLineSegment(sketch, "E2696", {"start": v(-49.02, 29) * mm, "end": v(-49.03, 29.16) * mm});
            skLineSegment(sketch, "E2697", {"start": v(-49.03, 29.16) * mm, "end": v(-49.07, 29.3) * mm});
            skLineSegment(sketch, "E2698", {"start": v(-49.07, 29.3) * mm, "end": v(-49.1, 29.38) * mm});
            skLineSegment(sketch, "E2699", {"start": v(-49.1, 29.38) * mm, "end": v(-49.14, 29.44) * mm});
            skLineSegment(sketch, "E2700", {"start": v(-49.14, 29.44) * mm, "end": v(-49.18, 29.5) * mm});
            skLineSegment(sketch, "E2701", {"start": v(-49.18, 29.5) * mm, "end": v(-49.24, 29.55) * mm});
            skLineSegment(sketch, "E2702", {"start": v(-49.24, 29.55) * mm, "end": v(-49.27, 29.58) * mm});
            skLineSegment(sketch, "E2703", {"start": v(-49.27, 29.58) * mm, "end": v(-49.31, 29.6) * mm});
            skLineSegment(sketch, "E2704", {"start": v(-49.31, 29.6) * mm, "end": v(-49.4, 29.6) * mm});
            skLineSegment(sketch, "E2705", {"start": v(-49.4, 29.6) * mm, "end": v(-49.5, 29.58) * mm});
            skLineSegment(sketch, "E2706", {"start": v(-49.5, 29.58) * mm, "end": v(-49.6, 29.54) * mm});
            skLineSegment(sketch, "E2707", {"start": v(-49.6, 29.54) * mm, "end": v(-49.83, 29.44) * mm});
            skLineSegment(sketch, "E2708", {"start": v(-49.83, 29.44) * mm, "end": v(-49.93, 29.4) * mm});
            skLineSegment(sketch, "E2709", {"start": v(-49.93, 29.4) * mm, "end": v(-50.02, 29.37) * mm});
            skLineSegment(sketch, "E2710", {"start": v(-50.02, 29.37) * mm, "end": v(-53.1, 28.67) * mm});
            skLineSegment(sketch, "E2711", {"start": v(-53.1, 28.67) * mm, "end": v(-54.17, 28.41) * mm});
            skLineSegment(sketch, "E2712", {"start": v(-54.17, 28.41) * mm, "end": v(-55.25, 28.13) * mm});
            skLineSegment(sketch, "E2713", {"start": v(-55.25, 28.13) * mm, "end": v(-56.3, 27.81) * mm});
            skLineSegment(sketch, "E2714", {"start": v(-56.3, 27.81) * mm, "end": v(-57.33, 27.48) * mm});
            skLineSegment(sketch, "E2715", {"start": v(-57.33, 27.48) * mm, "end": v(-58.33, 27.13) * mm});
            skLineSegment(sketch, "E2716", {"start": v(-58.33, 27.13) * mm, "end": v(-58.8, 26.95) * mm});
            skLineSegment(sketch, "E2717", {"start": v(-58.8, 26.95) * mm, "end": v(-59.27, 26.76) * mm});
            skLineSegment(sketch, "E2718", {"start": v(-59.27, 26.76) * mm, "end": v(-59.71, 26.58) * mm});
            skLineSegment(sketch, "E2719", {"start": v(-59.71, 26.58) * mm, "end": v(-60.14, 26.39) * mm});
            skLineSegment(sketch, "E2720", {"start": v(-60.14, 26.39) * mm, "end": v(-60.55, 26.2) * mm});
            skLineSegment(sketch, "E2721", {"start": v(-60.55, 26.2) * mm, "end": v(-60.94, 26.01) * mm});
            skLineSegment(sketch, "E2722", {"start": v(-60.94, 26.01) * mm, "end": v(-61.32, 25.84) * mm});
            skLineSegment(sketch, "E2723", {"start": v(-61.32, 25.84) * mm, "end": v(-61.74, 25.66) * mm});
            skLineSegment(sketch, "E2724", {"start": v(-61.74, 25.66) * mm, "end": v(-61.95, 25.57) * mm});
            skLineSegment(sketch, "E2725", {"start": v(-61.95, 25.57) * mm, "end": v(-62.15, 25.47) * mm});
            skLineSegment(sketch, "E2726", {"start": v(-62.15, 25.47) * mm, "end": v(-62.33, 25.36) * mm});
            skLineSegment(sketch, "E2727", {"start": v(-62.33, 25.36) * mm, "end": v(-62.49, 25.24) * mm});
            skLineSegment(sketch, "E2728", {"start": v(-62.49, 25.24) * mm, "end": v(-62.63, 25.1) * mm});
            skLineSegment(sketch, "E2729", {"start": v(-62.63, 25.1) * mm, "end": v(-62.76, 24.93) * mm});
            skLineSegment(sketch, "E2730", {"start": v(-62.76, 24.93) * mm, "end": v(-62.88, 24.75) * mm});
            skLineSegment(sketch, "E2731", {"start": v(-62.88, 24.75) * mm, "end": v(-63, 24.56) * mm});
            skLineSegment(sketch, "E2732", {"start": v(-63, 24.56) * mm, "end": v(-63.22, 24.18) * mm});
            skLineSegment(sketch, "E2733", {"start": v(-63.22, 24.18) * mm, "end": v(-63.33, 24) * mm});
            skLineSegment(sketch, "E2734", {"start": v(-63.33, 24) * mm, "end": v(-63.44, 23.83) * mm});
            skLineSegment(sketch, "E2735", {"start": v(-63.44, 23.83) * mm, "end": v(-63.65, 23.5) * mm});
            skLineSegment(sketch, "E2736", {"start": v(-63.65, 23.5) * mm, "end": v(-63.86, 23.16) * mm});
            skLineSegment(sketch, "E2737", {"start": v(-63.86, 23.16) * mm, "end": v(-64.07, 22.8) * mm});
            skLineSegment(sketch, "E2738", {"start": v(-64.07, 22.8) * mm, "end": v(-64.27, 22.41) * mm});
            skLineSegment(sketch, "E2739", {"start": v(-64.27, 22.41) * mm, "end": v(-64.47, 22.01) * mm});
            skLineSegment(sketch, "E2740", {"start": v(-64.47, 22.01) * mm, "end": v(-64.67, 21.6) * mm});
            skLineSegment(sketch, "E2741", {"start": v(-64.67, 21.6) * mm, "end": v(-64.87, 21.17) * mm});
            skLineSegment(sketch, "E2742", {"start": v(-64.87, 21.17) * mm, "end": v(-65.06, 20.73) * mm});
            skLineSegment(sketch, "E2743", {"start": v(-65.06, 20.73) * mm, "end": v(-65.24, 20.27) * mm});
            skLineSegment(sketch, "E2744", {"start": v(-65.24, 20.27) * mm, "end": v(-65.42, 19.81) * mm});
            skLineSegment(sketch, "E2745", {"start": v(-65.42, 19.81) * mm, "end": v(-65.6, 19.34) * mm});
            skLineSegment(sketch, "E2746", {"start": v(-65.6, 19.34) * mm, "end": v(-65.76, 18.86) * mm});
            skLineSegment(sketch, "E2747", {"start": v(-65.76, 18.86) * mm, "end": v(-65.92, 18.37) * mm});
            skLineSegment(sketch, "E2748", {"start": v(-65.92, 18.37) * mm, "end": v(-66.07, 17.87) * mm});
            skLineSegment(sketch, "E2749", {"start": v(-66.07, 17.87) * mm, "end": v(-66.21, 17.38) * mm});
            skLineSegment(sketch, "E2750", {"start": v(-66.21, 17.38) * mm, "end": v(-66.35, 16.87) * mm});
            skLineSegment(sketch, "E2751", {"start": v(-66.35, 16.87) * mm, "end": v(-66.42, 16.64) * mm});
            skLineSegment(sketch, "E2752", {"start": v(-66.42, 16.64) * mm, "end": v(-66.52, 16.4) * mm});
            skLineSegment(sketch, "E2753", {"start": v(-66.52, 16.4) * mm, "end": v(-66.72, 15.89) * mm});
            skLineSegment(sketch, "E2754", {"start": v(-66.72, 15.89) * mm, "end": v(-66.81, 15.63) * mm});
            skLineSegment(sketch, "E2755", {"start": v(-66.81, 15.63) * mm, "end": v(-66.85, 15.5) * mm});
            skLineSegment(sketch, "E2756", {"start": v(-66.85, 15.5) * mm, "end": v(-66.87, 15.38) * mm});
            skLineSegment(sketch, "E2757", {"start": v(-66.87, 15.38) * mm, "end": v(-66.89, 15.26) * mm});
            skLineSegment(sketch, "E2758", {"start": v(-66.89, 15.26) * mm, "end": v(-66.9, 15.14) * mm});
            skLineSegment(sketch, "E2759", {"start": v(-66.9, 15.14) * mm, "end": v(-66.88, 15.02) * mm});
            skLineSegment(sketch, "E2760", {"start": v(-66.88, 15.02) * mm, "end": v(-66.86, 14.9) * mm});
            skLineSegment(sketch, "E2761", {"start": v(-66.86, 14.9) * mm, "end": v(-66.83, 14.83) * mm});
            skLineSegment(sketch, "E2762", {"start": v(-66.83, 14.83) * mm, "end": v(-66.78, 14.75) * mm});
            skLineSegment(sketch, "E2763", {"start": v(-66.78, 14.75) * mm, "end": v(-66.72, 14.67) * mm});
            skLineSegment(sketch, "E2764", {"start": v(-66.72, 14.67) * mm, "end": v(-66.65, 14.6) * mm});
            skLineSegment(sketch, "E2765", {"start": v(-66.65, 14.6) * mm, "end": v(-66.57, 14.54) * mm});
            skLineSegment(sketch, "E2766", {"start": v(-66.57, 14.54) * mm, "end": v(-66.49, 14.49) * mm});
            skLineSegment(sketch, "E2767", {"start": v(-66.49, 14.49) * mm, "end": v(-66.4, 14.44) * mm});
            skLineSegment(sketch, "E2768", {"start": v(-66.4, 14.44) * mm, "end": v(-66.32, 14.41) * mm});
            skLineSegment(sketch, "E2769", {"start": v(-66.32, 14.41) * mm, "end": v(-66.17, 14.38) * mm});
            skLineSegment(sketch, "E2770", {"start": v(-66.17, 14.38) * mm, "end": v(-66.02, 14.36) * mm});
            skLineSegment(sketch, "E2771", {"start": v(-66.02, 14.36) * mm, "end": v(-65.87, 14.34) * mm});
            skLineSegment(sketch, "E2772", {"start": v(-65.87, 14.34) * mm, "end": v(-65.71, 14.33) * mm});
            skLineSegment(sketch, "E2773", {"start": v(-65.71, 14.33) * mm, "end": v(-65.39, 14.33) * mm});
            skLineSegment(sketch, "E2774", {"start": v(-65.39, 14.33) * mm, "end": v(-65.06, 14.36) * mm});
            skLineSegment(sketch, "E2775", {"start": v(-65.06, 14.36) * mm, "end": v(-64.72, 14.41) * mm});
            skLineSegment(sketch, "E2776", {"start": v(-64.72, 14.41) * mm, "end": v(-64.38, 14.48) * mm});
            skLineSegment(sketch, "E2777", {"start": v(-64.38, 14.48) * mm, "end": v(-64.04, 14.57) * mm});
            skLineSegment(sketch, "E2778", {"start": v(-64.04, 14.57) * mm, "end": v(-63.7, 14.68) * mm});
            skLineSegment(sketch, "E2779", {"start": v(-63.7, 14.68) * mm, "end": v(-63.35, 14.8) * mm});
            skLineSegment(sketch, "E2780", {"start": v(-63.35, 14.8) * mm, "end": v(-63, 14.92) * mm});
            skLineSegment(sketch, "E2781", {"start": v(-63, 14.92) * mm, "end": v(-62.33, 15.18) * mm});
            skLineSegment(sketch, "E2782", {"start": v(-62.33, 15.18) * mm, "end": v(-61.7, 15.43) * mm});
            skLineSegment(sketch, "E2783", {"start": v(-61.7, 15.43) * mm, "end": v(-61.1, 15.67) * mm});
            skLineSegment(sketch, "E2784", {"start": v(-61.1, 15.67) * mm, "end": v(-60.78, 15.8) * mm});
            skLineSegment(sketch, "E2785", {"start": v(-60.78, 15.8) * mm, "end": v(-60.45, 15.96) * mm});
            skLineSegment(sketch, "E2786", {"start": v(-60.45, 15.96) * mm, "end": v(-60.1, 16.14) * mm});
            skLineSegment(sketch, "E2787", {"start": v(-60.1, 16.14) * mm, "end": v(-59.76, 16.33) * mm});
            skLineSegment(sketch, "E2788", {"start": v(-59.76, 16.33) * mm, "end": v(-59.09, 16.72) * mm});
            skLineSegment(sketch, "E2789", {"start": v(-59.09, 16.72) * mm, "end": v(-58.46, 17.07) * mm});
            skLineSegment(sketch, "E2790", {"start": v(-68.14, 23.63) * mm, "end": v(-68.16, 23.87) * mm});
            skLineSegment(sketch, "E2791", {"start": v(-68.16, 23.87) * mm, "end": v(-68.21, 24.2) * mm});
            skLineSegment(sketch, "E2792", {"start": v(-68.21, 24.2) * mm, "end": v(-68.3, 24.6) * mm});
            skLineSegment(sketch, "E2793", {"start": v(-68.3, 24.6) * mm, "end": v(-68.4, 25.08) * mm});
            skLineSegment(sketch, "E2794", {"start": v(-68.4, 25.08) * mm, "end": v(-68.68, 26.17) * mm});
            skLineSegment(sketch, "E2795", {"start": v(-68.68, 26.17) * mm, "end": v(-68.96, 27.35) * mm});
            skLineSegment(sketch, "E2796", {"start": v(-68.96, 27.35) * mm, "end": v(-69.14, 28.03) * mm});
            skLineSegment(sketch, "E2797", {"start": v(-69.14, 28.03) * mm, "end": v(-69.35, 28.73) * mm});
            skLineSegment(sketch, "E2798", {"start": v(-69.35, 28.73) * mm, "end": v(-69.57, 29.43) * mm});
            skLineSegment(sketch, "E2799", {"start": v(-69.57, 29.43) * mm, "end": v(-69.8, 30.09) * mm});
            skLineSegment(sketch, "E2800", {"start": v(-69.8, 30.09) * mm, "end": v(-69.92, 30.5) * mm});
            skLineSegment(sketch, "E2801", {"start": v(-69.92, 30.5) * mm, "end": v(-70.05, 30.95) * mm});
            skLineSegment(sketch, "E2802", {"start": v(-70.05, 30.95) * mm, "end": v(-70.27, 31.91) * mm});
            skLineSegment(sketch, "E2803", {"start": v(-70.27, 31.91) * mm, "end": v(-70.5, 32.92) * mm});
            skLineSegment(sketch, "E2804", {"start": v(-70.5, 32.92) * mm, "end": v(-70.62, 33.43) * mm});
            skLineSegment(sketch, "E2805", {"start": v(-70.62, 33.43) * mm, "end": v(-70.76, 33.94) * mm});
            skLineSegment(sketch, "E2806", {"start": v(-70.76, 33.94) * mm, "end": v(-70.9, 34.43) * mm});
            skLineSegment(sketch, "E2807", {"start": v(-70.9, 34.43) * mm, "end": v(-71.07, 34.91) * mm});
            skLineSegment(sketch, "E2808", {"start": v(-71.07, 34.91) * mm, "end": v(-71.16, 35.14) * mm});
            skLineSegment(sketch, "E2809", {"start": v(-71.16, 35.14) * mm, "end": v(-71.25, 35.37) * mm});
            skLineSegment(sketch, "E2810", {"start": v(-71.25, 35.37) * mm, "end": v(-71.35, 35.58) * mm});
            skLineSegment(sketch, "E2811", {"start": v(-71.35, 35.58) * mm, "end": v(-71.46, 35.8) * mm});
            skLineSegment(sketch, "E2812", {"start": v(-71.46, 35.8) * mm, "end": v(-71.57, 36) * mm});
            skLineSegment(sketch, "E2813", {"start": v(-71.57, 36) * mm, "end": v(-71.7, 36.19) * mm});
            skLineSegment(sketch, "E2814", {"start": v(-71.7, 36.19) * mm, "end": v(-71.82, 36.37) * mm});
            skLineSegment(sketch, "E2815", {"start": v(-71.82, 36.37) * mm, "end": v(-71.96, 36.54) * mm});
            skLineSegment(sketch, "E2816", {"start": v(-71.96, 36.54) * mm, "end": v(-72.1, 36.7) * mm});
            skLineSegment(sketch, "E2817", {"start": v(-72.1, 36.7) * mm, "end": v(-72.26, 36.85) * mm});
            skLineSegment(sketch, "E2818", {"start": v(-72.26, 36.85) * mm, "end": v(-72.42, 36.98) * mm});
            skLineSegment(sketch, "E2819", {"start": v(-72.42, 36.98) * mm, "end": v(-72.6, 37.1) * mm});
            skLineSegment(sketch, "E2820", {"start": v(-72.6, 37.1) * mm, "end": v(-72.67, 37.15) * mm});
            skLineSegment(sketch, "E2821", {"start": v(-72.67, 37.15) * mm, "end": v(-72.77, 37.18) * mm});
            skLineSegment(sketch, "E2822", {"start": v(-72.77, 37.18) * mm, "end": v(-72.87, 37.2) * mm});
            skLineSegment(sketch, "E2823", {"start": v(-72.87, 37.2) * mm, "end": v(-72.98, 37.2) * mm});
            skLineSegment(sketch, "E2824", {"start": v(-72.98, 37.2) * mm, "end": v(-73.1, 37.2) * mm});
            skLineSegment(sketch, "E2825", {"start": v(-73.1, 37.2) * mm, "end": v(-73.2, 37.18) * mm});
            skLineSegment(sketch, "E2826", {"start": v(-73.2, 37.18) * mm, "end": v(-73.3, 37.15) * mm});
            skLineSegment(sketch, "E2827", {"start": v(-73.3, 37.15) * mm, "end": v(-73.38, 37.1) * mm});
            skLineSegment(sketch, "E2828", {"start": v(-73.38, 37.1) * mm, "end": v(-73.5, 37.04) * mm});
            skLineSegment(sketch, "E2829", {"start": v(-73.5, 37.04) * mm, "end": v(-73.6, 36.96) * mm});
            skLineSegment(sketch, "E2830", {"start": v(-73.6, 36.96) * mm, "end": v(-73.81, 36.78) * mm});
            skLineSegment(sketch, "E2831", {"start": v(-73.81, 36.78) * mm, "end": v(-74, 36.57) * mm});
            skLineSegment(sketch, "E2832", {"start": v(-74, 36.57) * mm, "end": v(-74.18, 36.35) * mm});
            skLineSegment(sketch, "E2833", {"start": v(-74.18, 36.35) * mm, "end": v(-74.35, 36.1) * mm});
            skLineSegment(sketch, "E2834", {"start": v(-74.35, 36.1) * mm, "end": v(-74.5, 35.83) * mm});
            skLineSegment(sketch, "E2835", {"start": v(-74.5, 35.83) * mm, "end": v(-74.65, 35.56) * mm});
            skLineSegment(sketch, "E2836", {"start": v(-74.65, 35.56) * mm, "end": v(-74.79, 35.27) * mm});
            skLineSegment(sketch, "E2837", {"start": v(-74.79, 35.27) * mm, "end": v(-75.04, 34.68) * mm});
            skLineSegment(sketch, "E2838", {"start": v(-75.04, 34.68) * mm, "end": v(-75.27, 34.08) * mm});
            skLineSegment(sketch, "E2839", {"start": v(-75.27, 34.08) * mm, "end": v(-75.48, 33.5) * mm});
            skLineSegment(sketch, "E2840", {"start": v(-75.48, 33.5) * mm, "end": v(-75.68, 32.98) * mm});
            skLineSegment(sketch, "E2841", {"start": v(-75.68, 32.98) * mm, "end": v(-75.86, 32.5) * mm});
            skLineSegment(sketch, "E2842", {"start": v(-75.86, 32.5) * mm, "end": v(-76.04, 31.98) * mm});
            skLineSegment(sketch, "E2843", {"start": v(-76.04, 31.98) * mm, "end": v(-76.21, 31.43) * mm});
            skLineSegment(sketch, "E2844", {"start": v(-76.21, 31.43) * mm, "end": v(-76.37, 30.87) * mm});
            skLineSegment(sketch, "E2845", {"start": v(-76.37, 30.87) * mm, "end": v(-76.51, 30.3) * mm});
            skLineSegment(sketch, "E2846", {"start": v(-76.51, 30.3) * mm, "end": v(-76.63, 29.75) * mm});
            skLineSegment(sketch, "E2847", {"start": v(-76.63, 29.75) * mm, "end": v(-76.73, 29.2) * mm});
            skLineSegment(sketch, "E2848", {"start": v(-76.73, 29.2) * mm, "end": v(-76.79, 28.7) * mm});
            skLineSegment(sketch, "E2849", {"start": v(-76.79, 28.7) * mm, "end": v(-76.83, 28.12) * mm});
            skLineSegment(sketch, "E2850", {"start": v(-76.83, 28.12) * mm, "end": v(-76.84, 27.5) * mm});
            skLineSegment(sketch, "E2851", {"start": v(-76.84, 27.5) * mm, "end": v(-76.83, 26.87) * mm});
            skLineSegment(sketch, "E2852", {"start": v(-76.83, 26.87) * mm, "end": v(-76.8, 26.22) * mm});
            skLineSegment(sketch, "E2853", {"start": v(-76.8, 26.22) * mm, "end": v(-76.75, 25.58) * mm});
            skLineSegment(sketch, "E2854", {"start": v(-76.75, 25.58) * mm, "end": v(-76.67, 24.95) * mm});
            skLineSegment(sketch, "E2855", {"start": v(-76.67, 24.95) * mm, "end": v(-76.62, 24.64) * mm});
            skLineSegment(sketch, "E2856", {"start": v(-76.62, 24.64) * mm, "end": v(-76.56, 24.35) * mm});
            skLineSegment(sketch, "E2857", {"start": v(-76.56, 24.35) * mm, "end": v(-76.5, 24.06) * mm});
            skLineSegment(sketch, "E2858", {"start": v(-76.5, 24.06) * mm, "end": v(-76.43, 23.79) * mm});
            skLineSegment(sketch, "E2859", {"start": v(-76.43, 23.79) * mm, "end": v(-76.34, 23.5) * mm});
            skLineSegment(sketch, "E2860", {"start": v(-76.34, 23.5) * mm, "end": v(-76.25, 23.2) * mm});
            skLineSegment(sketch, "E2861", {"start": v(-76.25, 23.2) * mm, "end": v(-76.14, 22.9) * mm});
            skLineSegment(sketch, "E2862", {"start": v(-76.14, 22.9) * mm, "end": v(-76.02, 22.59) * mm});
            skLineSegment(sketch, "E2863", {"start": v(-76.02, 22.59) * mm, "end": v(-75.75, 21.96) * mm});
            skLineSegment(sketch, "E2864", {"start": v(-75.75, 21.96) * mm, "end": v(-75.46, 21.34) * mm});
            skLineSegment(sketch, "E2865", {"start": v(-75.46, 21.34) * mm, "end": v(-75.14, 20.72) * mm});
            skLineSegment(sketch, "E2866", {"start": v(-75.14, 20.72) * mm, "end": v(-74.8, 20.13) * mm});
            skLineSegment(sketch, "E2867", {"start": v(-74.8, 20.13) * mm, "end": v(-74.45, 19.58) * mm});
            skLineSegment(sketch, "E2868", {"start": v(-74.45, 19.58) * mm, "end": v(-74.27, 19.32) * mm});
            skLineSegment(sketch, "E2869", {"start": v(-74.27, 19.32) * mm, "end": v(-74.1, 19.07) * mm});
            skLineSegment(sketch, "E2870", {"start": v(-74.1, 19.07) * mm, "end": v(-73.91, 18.85) * mm});
            skLineSegment(sketch, "E2871", {"start": v(-73.91, 18.85) * mm, "end": v(-73.7, 18.63) * mm});
            skLineSegment(sketch, "E2872", {"start": v(-73.7, 18.63) * mm, "end": v(-73.47, 18.4) * mm});
            skLineSegment(sketch, "E2873", {"start": v(-73.47, 18.4) * mm, "end": v(-73.23, 18.19) * mm});
            skLineSegment(sketch, "E2874", {"start": v(-73.23, 18.19) * mm, "end": v(-72.74, 17.77) * mm});
            skLineSegment(sketch, "E2875", {"start": v(-72.74, 17.77) * mm, "end": v(-72.5, 17.56) * mm});
            skLineSegment(sketch, "E2876", {"start": v(-72.5, 17.56) * mm, "end": v(-72.3, 17.37) * mm});
            skLineSegment(sketch, "E2877", {"start": v(-72.3, 17.37) * mm, "end": v(-71.92, 17.02) * mm});
            skLineSegment(sketch, "E2878", {"start": v(-71.92, 17.02) * mm, "end": v(-71.57, 16.7) * mm});
            skLineSegment(sketch, "E2879", {"start": v(-71.57, 16.7) * mm, "end": v(-71.23, 16.41) * mm});
            skLineSegment(sketch, "E2880", {"start": v(-71.23, 16.41) * mm, "end": v(-70.93, 16.16) * mm});
            skLineSegment(sketch, "E2881", {"start": v(-70.93, 16.16) * mm, "end": v(-70.66, 15.95) * mm});
            skLineSegment(sketch, "E2882", {"start": v(-70.66, 15.95) * mm, "end": v(-70.44, 15.8) * mm});
            skLineSegment(sketch, "E2883", {"start": v(-70.44, 15.8) * mm, "end": v(-70.28, 15.7) * mm});
            skLineSegment(sketch, "E2884", {"start": v(-70.28, 15.7) * mm, "end": v(-70.23, 15.67) * mm});
            skLineSegment(sketch, "E2885", {"start": v(-70.23, 15.67) * mm, "end": v(-70.19, 15.66) * mm});
            skLineSegment(sketch, "E2886", {"start": v(-70.19, 15.66) * mm, "end": v(-70.11, 15.65) * mm});
            skLineSegment(sketch, "E2887", {"start": v(-70.11, 15.65) * mm, "end": v(-70.03, 15.64) * mm});
            skLineSegment(sketch, "E2888", {"start": v(-70.03, 15.64) * mm, "end": v(-69.95, 15.64) * mm});
            skLineSegment(sketch, "E2889", {"start": v(-69.95, 15.64) * mm, "end": v(-69.92, 15.64) * mm});
            skLineSegment(sketch, "E2890", {"start": v(-69.92, 15.64) * mm, "end": v(-69.89, 15.66) * mm});
            skLineSegment(sketch, "E2891", {"start": v(-69.89, 15.66) * mm, "end": v(-69.73, 15.8) * mm});
            skLineSegment(sketch, "E2892", {"start": v(-69.73, 15.8) * mm, "end": v(-69.59, 15.94) * mm});
            skLineSegment(sketch, "E2893", {"start": v(-69.59, 15.94) * mm, "end": v(-69.45, 16.1) * mm});
            skLineSegment(sketch, "E2894", {"start": v(-69.45, 16.1) * mm, "end": v(-69.33, 16.26) * mm});
            skLineSegment(sketch, "E2895", {"start": v(-69.33, 16.26) * mm, "end": v(-69.21, 16.44) * mm});
            skLineSegment(sketch, "E2896", {"start": v(-69.21, 16.44) * mm, "end": v(-69.1, 16.63) * mm});
            skLineSegment(sketch, "E2897", {"start": v(-69.1, 16.63) * mm, "end": v(-69.01, 16.83) * mm});
            skLineSegment(sketch, "E2898", {"start": v(-69.01, 16.83) * mm, "end": v(-68.92, 17.03) * mm});
            skLineSegment(sketch, "E2899", {"start": v(-68.92, 17.03) * mm, "end": v(-68.84, 17.24) * mm});
            skLineSegment(sketch, "E2900", {"start": v(-68.84, 17.24) * mm, "end": v(-68.77, 17.46) * mm});
            skLineSegment(sketch, "E2901", {"start": v(-68.77, 17.46) * mm, "end": v(-68.64, 17.92) * mm});
            skLineSegment(sketch, "E2902", {"start": v(-68.64, 17.92) * mm, "end": v(-68.54, 18.4) * mm});
            skLineSegment(sketch, "E2903", {"start": v(-68.54, 18.4) * mm, "end": v(-68.46, 18.9) * mm});
            skLineSegment(sketch, "E2904", {"start": v(-68.46, 18.9) * mm, "end": v(-68.4, 19.4) * mm});
            skLineSegment(sketch, "E2905", {"start": v(-68.4, 19.4) * mm, "end": v(-68.35, 19.9) * mm});
            skLineSegment(sketch, "E2906", {"start": v(-68.35, 19.9) * mm, "end": v(-68.28, 20.92) * mm});
            skLineSegment(sketch, "E2907", {"start": v(-68.28, 20.92) * mm, "end": v(-68.22, 21.88) * mm});
            skLineSegment(sketch, "E2908", {"start": v(-68.22, 21.88) * mm, "end": v(-68.18, 22.33) * mm});
            skLineSegment(sketch, "E2909", {"start": v(-68.18, 22.33) * mm, "end": v(-68.13, 22.75) * mm});
            skLineSegment(sketch, "E2910", {"start": v(-68.13, 22.75) * mm, "end": v(-68.12, 22.96) * mm});
            skLineSegment(sketch, "E2911", {"start": v(-68.12, 22.96) * mm, "end": v(-68.12, 23.2) * mm});
            skLineSegment(sketch, "E2912", {"start": v(-68.12, 23.2) * mm, "end": v(-68.14, 23.63) * mm});
            skLineSegment(sketch, "E2913", {"start": v(67, 19.3) * mm, "end": v(66.82, 19.87) * mm});
            skLineSegment(sketch, "E2914", {"start": v(66.82, 19.87) * mm, "end": v(66.63, 20.48) * mm});
            skLineSegment(sketch, "E2915", {"start": v(66.63, 20.48) * mm, "end": v(66.42, 21.08) * mm});
            skLineSegment(sketch, "E2916", {"start": v(66.42, 21.08) * mm, "end": v(66.3, 21.37) * mm});
            skLineSegment(sketch, "E2917", {"start": v(66.3, 21.37) * mm, "end": v(66.2, 21.63) * mm});
            skLineSegment(sketch, "E2918", {"start": v(66.2, 21.63) * mm, "end": v(66.08, 21.86) * mm});
            skLineSegment(sketch, "E2919", {"start": v(66.08, 21.86) * mm, "end": v(65.94, 22.1) * mm});
            skLineSegment(sketch, "E2920", {"start": v(65.94, 22.1) * mm, "end": v(65.65, 22.58) * mm});
            skLineSegment(sketch, "E2921", {"start": v(65.65, 22.58) * mm, "end": v(65.33, 23.06) * mm});
            skLineSegment(sketch, "E2922", {"start": v(65.33, 23.06) * mm, "end": v(65.05, 23.51) * mm});
            skLineSegment(sketch, "E2923", {"start": v(65.05, 23.51) * mm, "end": v(64.8, 23.9) * mm});
            skLineSegment(sketch, "E2924", {"start": v(64.8, 23.9) * mm, "end": v(64.54, 24.3) * mm});
            skLineSegment(sketch, "E2925", {"start": v(64.54, 24.3) * mm, "end": v(64.27, 24.7) * mm});
            skLineSegment(sketch, "E2926", {"start": v(64.27, 24.7) * mm, "end": v(64, 25.07) * mm});
            skLineSegment(sketch, "E2927", {"start": v(64, 25.07) * mm, "end": v(63.74, 25.41) * mm});
            skLineSegment(sketch, "E2928", {"start": v(63.74, 25.41) * mm, "end": v(63.5, 25.71) * mm});
            skLineSegment(sketch, "E2929", {"start": v(63.5, 25.71) * mm, "end": v(63.28, 25.97) * mm});
            skLineSegment(sketch, "E2930", {"start": v(63.28, 25.97) * mm, "end": v(63.1, 26.16) * mm});
            skLineSegment(sketch, "E2931", {"start": v(63.1, 26.16) * mm, "end": v(62.9, 26.35) * mm});
            skLineSegment(sketch, "E2932", {"start": v(62.9, 26.35) * mm, "end": v(62.7, 26.56) * mm});
            skLineSegment(sketch, "E2933", {"start": v(62.7, 26.56) * mm, "end": v(62.5, 26.77) * mm});
            skLineSegment(sketch, "E2934", {"start": v(62.5, 26.77) * mm, "end": v(62.38, 26.85) * mm});
            skLineSegment(sketch, "E2935", {"start": v(62.38, 26.85) * mm, "end": v(62.28, 26.93) * mm});
            skLineSegment(sketch, "E2936", {"start": v(62.28, 26.93) * mm, "end": v(62.12, 27.01) * mm});
            skLineSegment(sketch, "E2937", {"start": v(62.12, 27.01) * mm, "end": v(61.96, 27.1) * mm});
            skLineSegment(sketch, "E2938", {"start": v(61.96, 27.1) * mm, "end": v(61.6, 27.24) * mm});
            skLineSegment(sketch, "E2939", {"start": v(61.6, 27.24) * mm, "end": v(61.23, 27.37) * mm});
            skLineSegment(sketch, "E2940", {"start": v(61.23, 27.37) * mm, "end": v(60.85, 27.49) * mm});
            skLineSegment(sketch, "E2941", {"start": v(60.85, 27.49) * mm, "end": v(60.07, 27.7) * mm});
            skLineSegment(sketch, "E2942", {"start": v(60.07, 27.7) * mm, "end": v(59.7, 27.8) * mm});
            skLineSegment(sketch, "E2943", {"start": v(59.7, 27.8) * mm, "end": v(59.35, 27.91) * mm});
            skLineSegment(sketch, "E2944", {"start": v(59.35, 27.91) * mm, "end": v(58.13, 28.31) * mm});
            skLineSegment(sketch, "E2945", {"start": v(58.13, 28.31) * mm, "end": v(56.9, 28.68) * mm});
            skLineSegment(sketch, "E2946", {"start": v(56.9, 28.68) * mm, "end": v(55.72, 29) * mm});
            skLineSegment(sketch, "E2947", {"start": v(55.72, 29) * mm, "end": v(54.6, 29.29) * mm});
            skLineSegment(sketch, "E2948", {"start": v(54.6, 29.29) * mm, "end": v(54.06, 29.4) * mm});
            skLineSegment(sketch, "E2949", {"start": v(54.06, 29.4) * mm, "end": v(53.55, 29.52) * mm});
            skLineSegment(sketch, "E2950", {"start": v(53.55, 29.52) * mm, "end": v(53.07, 29.61) * mm});
            skLineSegment(sketch, "E2951", {"start": v(53.07, 29.61) * mm, "end": v(52.62, 29.7) * mm});
            skLineSegment(sketch, "E2952", {"start": v(52.62, 29.7) * mm, "end": v(52.2, 29.76) * mm});
            skLineSegment(sketch, "E2953", {"start": v(52.2, 29.76) * mm, "end": v(51.82, 29.8) * mm});
            skLineSegment(sketch, "E2954", {"start": v(51.82, 29.8) * mm, "end": v(51.49, 29.83) * mm});
            skLineSegment(sketch, "E2955", {"start": v(51.49, 29.83) * mm, "end": v(51.2, 29.84) * mm});
            skLineSegment(sketch, "E2956", {"start": v(51.2, 29.84) * mm, "end": v(50.24, 29.85) * mm});
            skLineSegment(sketch, "E2957", {"start": v(50.24, 29.85) * mm, "end": v(50.45, 28.78) * mm});
            skLineSegment(sketch, "E2958", {"start": v(50.45, 28.78) * mm, "end": v(50.52, 28.52) * mm});
            skLineSegment(sketch, "E2959", {"start": v(50.52, 28.52) * mm, "end": v(50.6, 28.22) * mm});
            skLineSegment(sketch, "E2960", {"start": v(50.6, 28.22) * mm, "end": v(50.73, 27.87) * mm});
            skLineSegment(sketch, "E2961", {"start": v(50.73, 27.87) * mm, "end": v(50.87, 27.5) * mm});
            skLineSegment(sketch, "E2962", {"start": v(50.87, 27.5) * mm, "end": v(51.03, 27.1) * mm});
            skLineSegment(sketch, "E2963", {"start": v(51.03, 27.1) * mm, "end": v(51.2, 26.69) * mm});
            skLineSegment(sketch, "E2964", {"start": v(51.2, 26.69) * mm, "end": v(51.38, 26.29) * mm});
            skLineSegment(sketch, "E2965", {"start": v(51.38, 26.29) * mm, "end": v(51.57, 25.9) * mm});
            skLineSegment(sketch, "E2966", {"start": v(51.57, 25.9) * mm, "end": v(51.77, 25.47) * mm});
            skLineSegment(sketch, "E2967", {"start": v(51.77, 25.47) * mm, "end": v(51.99, 24.99) * mm});
            skLineSegment(sketch, "E2968", {"start": v(51.99, 24.99) * mm, "end": v(52.1, 24.75) * mm});
            skLineSegment(sketch, "E2969", {"start": v(52.1, 24.75) * mm, "end": v(52.22, 24.52) * mm});
            skLineSegment(sketch, "E2970", {"start": v(52.22, 24.52) * mm, "end": v(52.34, 24.3) * mm});
            skLineSegment(sketch, "E2971", {"start": v(52.34, 24.3) * mm, "end": v(52.47, 24.1) * mm});
            skLineSegment(sketch, "E2972", {"start": v(52.47, 24.1) * mm, "end": v(52.68, 23.82) * mm});
            skLineSegment(sketch, "E2973", {"start": v(52.68, 23.82) * mm, "end": v(52.9, 23.53) * mm});
            skLineSegment(sketch, "E2974", {"start": v(52.9, 23.53) * mm, "end": v(53.4, 22.94) * mm});
            skLineSegment(sketch, "E2975", {"start": v(53.4, 22.94) * mm, "end": v(53.92, 22.34) * mm});
            skLineSegment(sketch, "E2976", {"start": v(53.92, 22.34) * mm, "end": v(54.48, 21.75) * mm});
            skLineSegment(sketch, "E2977", {"start": v(54.48, 21.75) * mm, "end": v(55.05, 21.18) * mm});
            skLineSegment(sketch, "E2978", {"start": v(55.05, 21.18) * mm, "end": v(55.35, 20.9) * mm});
            skLineSegment(sketch, "E2979", {"start": v(55.35, 20.9) * mm, "end": v(55.64, 20.64) * mm});
            skLineSegment(sketch, "E2980", {"start": v(55.64, 20.64) * mm, "end": v(55.94, 20.4) * mm});
            skLineSegment(sketch, "E2981", {"start": v(55.94, 20.4) * mm, "end": v(56.23, 20.15) * mm});
            skLineSegment(sketch, "E2982", {"start": v(56.23, 20.15) * mm, "end": v(56.52, 19.92) * mm});
            skLineSegment(sketch, "E2983", {"start": v(56.52, 19.92) * mm, "end": v(56.8, 19.71) * mm});
            skLineSegment(sketch, "E2984", {"start": v(56.8, 19.71) * mm, "end": v(57.1, 19.5) * mm});
            skLineSegment(sketch, "E2985", {"start": v(57.1, 19.5) * mm, "end": v(57.4, 19.3) * mm});
            skLineSegment(sketch, "E2986", {"start": v(57.4, 19.3) * mm, "end": v(57.73, 19.11) * mm});
            skLineSegment(sketch, "E2987", {"start": v(57.73, 19.11) * mm, "end": v(58.06, 18.92) * mm});
            skLineSegment(sketch, "E2988", {"start": v(58.06, 18.92) * mm, "end": v(58.77, 18.54) * mm});
            skLineSegment(sketch, "E2989", {"start": v(58.77, 18.54) * mm, "end": v(59.5, 18.18) * mm});
            skLineSegment(sketch, "E2990", {"start": v(59.5, 18.18) * mm, "end": v(60.24, 17.84) * mm});
            skLineSegment(sketch, "E2991", {"start": v(60.24, 17.84) * mm, "end": v(60.98, 17.53) * mm});
            skLineSegment(sketch, "E2992", {"start": v(60.98, 17.53) * mm, "end": v(61.7, 17.24) * mm});
            skLineSegment(sketch, "E2993", {"start": v(61.7, 17.24) * mm, "end": v(62.37, 16.99) * mm});
            skLineSegment(sketch, "E2994", {"start": v(62.37, 16.99) * mm, "end": v(62.6, 16.9) * mm});
            skLineSegment(sketch, "E2995", {"start": v(62.6, 16.9) * mm, "end": v(62.84, 16.84) * mm});
            skLineSegment(sketch, "E2996", {"start": v(62.84, 16.84) * mm, "end": v(63.35, 16.71) * mm});
            skLineSegment(sketch, "E2997", {"start": v(63.35, 16.71) * mm, "end": v(63.86, 16.6) * mm});
            skLineSegment(sketch, "E2998", {"start": v(63.86, 16.6) * mm, "end": v(64.34, 16.49) * mm});
            skLineSegment(sketch, "E2999", {"start": v(64.34, 16.49) * mm, "end": v(65.16, 16.3) * mm});
            skLineSegment(sketch, "E3000", {"start": v(65.16, 16.3) * mm, "end": v(65.95, 16.14) * mm});
            skLineSegment(sketch, "E3001", {"start": v(65.95, 16.14) * mm, "end": v(66.3, 16.07) * mm});
            skLineSegment(sketch, "E3002", {"start": v(66.3, 16.07) * mm, "end": v(66.61, 16.03) * mm});
            skLineSegment(sketch, "E3003", {"start": v(66.61, 16.03) * mm, "end": v(66.87, 16) * mm});
            skLineSegment(sketch, "E3004", {"start": v(66.87, 16) * mm, "end": v(67.06, 15.99) * mm});
            skLineSegment(sketch, "E3005", {"start": v(67.06, 15.99) * mm, "end": v(67.81, 15.99) * mm});
            skLineSegment(sketch, "E3006", {"start": v(67.81, 15.99) * mm, "end": v(67.81, 16.49) * mm});
            skLineSegment(sketch, "E3007", {"start": v(67.81, 16.49) * mm, "end": v(67.8, 16.64) * mm});
            skLineSegment(sketch, "E3008", {"start": v(67.8, 16.64) * mm, "end": v(67.75, 16.87) * mm});
            skLineSegment(sketch, "E3009", {"start": v(67.75, 16.87) * mm, "end": v(67.68, 17.17) * mm});
            skLineSegment(sketch, "E3010", {"start": v(67.68, 17.17) * mm, "end": v(67.58, 17.52) * mm});
            skLineSegment(sketch, "E3011", {"start": v(67.58, 17.52) * mm, "end": v(67.32, 18.37) * mm});
            skLineSegment(sketch, "E3012", {"start": v(67.32, 18.37) * mm, "end": v(67, 19.3) * mm});
            skLineSegment(sketch, "E3013", {"start": v(75.94, 22.53) * mm, "end": v(76.16, 22.96) * mm});
            skLineSegment(sketch, "E3014", {"start": v(76.16, 22.96) * mm, "end": v(76.4, 23.43) * mm});
            skLineSegment(sketch, "E3015", {"start": v(76.4, 23.43) * mm, "end": v(76.52, 23.66) * mm});
            skLineSegment(sketch, "E3016", {"start": v(76.52, 23.66) * mm, "end": v(76.63, 23.9) * mm});
            skLineSegment(sketch, "E3017", {"start": v(76.63, 23.9) * mm, "end": v(76.72, 24.13) * mm});
            skLineSegment(sketch, "E3018", {"start": v(76.72, 24.13) * mm, "end": v(76.8, 24.35) * mm});
            skLineSegment(sketch, "E3019", {"start": v(76.8, 24.35) * mm, "end": v(76.9, 24.78) * mm});
            skLineSegment(sketch, "E3020", {"start": v(76.9, 24.78) * mm, "end": v(76.98, 25.24) * mm});
            skLineSegment(sketch, "E3021", {"start": v(76.98, 25.24) * mm, "end": v(77.05, 25.72) * mm});
            skLineSegment(sketch, "E3022", {"start": v(77.05, 25.72) * mm, "end": v(77.1, 26.21) * mm});
            skLineSegment(sketch, "E3023", {"start": v(77.1, 26.21) * mm, "end": v(77.13, 26.7) * mm});
            skLineSegment(sketch, "E3024", {"start": v(77.13, 26.7) * mm, "end": v(77.15, 27.2) * mm});
            skLineSegment(sketch, "E3025", {"start": v(77.15, 27.2) * mm, "end": v(77.15, 27.67) * mm});
            skLineSegment(sketch, "E3026", {"start": v(77.15, 27.67) * mm, "end": v(77.14, 28.1) * mm});
            skLineSegment(sketch, "E3027", {"start": v(77.14, 28.1) * mm, "end": v(77.1, 28.64) * mm});
            skLineSegment(sketch, "E3028", {"start": v(77.1, 28.64) * mm, "end": v(77.05, 29.2) * mm});
            skLineSegment(sketch, "E3029", {"start": v(77.05, 29.2) * mm, "end": v(76.98, 29.78) * mm});
            skLineSegment(sketch, "E3030", {"start": v(76.98, 29.78) * mm, "end": v(76.89, 30.37) * mm});
            skLineSegment(sketch, "E3031", {"start": v(76.89, 30.37) * mm, "end": v(76.78, 30.95) * mm});
            skLineSegment(sketch, "E3032", {"start": v(76.78, 30.95) * mm, "end": v(76.66, 31.52) * mm});
            skLineSegment(sketch, "E3033", {"start": v(76.66, 31.52) * mm, "end": v(76.52, 32.07) * mm});
            skLineSegment(sketch, "E3034", {"start": v(76.52, 32.07) * mm, "end": v(76.36, 32.57) * mm});
            skLineSegment(sketch, "E3035", {"start": v(76.36, 32.57) * mm, "end": v(76.26, 32.84) * mm});
            skLineSegment(sketch, "E3036", {"start": v(76.26, 32.84) * mm, "end": v(76.13, 33.12) * mm});
            skLineSegment(sketch, "E3037", {"start": v(76.13, 33.12) * mm, "end": v(75.99, 33.4) * mm});
            skLineSegment(sketch, "E3038", {"start": v(75.99, 33.4) * mm, "end": v(75.84, 33.68) * mm});
            skLineSegment(sketch, "E3039", {"start": v(75.84, 33.68) * mm, "end": v(75.52, 34.24) * mm});
            skLineSegment(sketch, "E3040", {"start": v(75.52, 34.24) * mm, "end": v(75.23, 34.76) * mm});
            skLineSegment(sketch, "E3041", {"start": v(75.23, 34.76) * mm, "end": v(75, 35.21) * mm});
            skLineSegment(sketch, "E3042", {"start": v(75, 35.21) * mm, "end": v(74.74, 35.67) * mm});
            skLineSegment(sketch, "E3043", {"start": v(74.74, 35.67) * mm, "end": v(74.24, 36.54) * mm});
            skLineSegment(sketch, "E3044", {"start": v(74.24, 36.54) * mm, "end": v(74, 36.93) * mm});
            skLineSegment(sketch, "E3045", {"start": v(74, 36.93) * mm, "end": v(73.79, 37.27) * mm});
            skLineSegment(sketch, "E3046", {"start": v(73.79, 37.27) * mm, "end": v(73.6, 37.56) * mm});
            skLineSegment(sketch, "E3047", {"start": v(73.6, 37.56) * mm, "end": v(73.44, 37.77) * mm});
            skLineSegment(sketch, "E3048", {"start": v(73.44, 37.77) * mm, "end": v(72.77, 38.6) * mm});
            skLineSegment(sketch, "E3049", {"start": v(72.77, 38.6) * mm, "end": v(72.44, 38.1) * mm});
            skLineSegment(sketch, "E3050", {"start": v(72.44, 38.1) * mm, "end": v(72.37, 37.81) * mm});
            skLineSegment(sketch, "E3051", {"start": v(72.37, 37.81) * mm, "end": v(72.26, 37.46) * mm});
            skLineSegment(sketch, "E3052", {"start": v(72.26, 37.46) * mm, "end": v(72.11, 37.05) * mm});
            skLineSegment(sketch, "E3053", {"start": v(72.11, 37.05) * mm, "end": v(71.94, 36.59) * mm});
            skLineSegment(sketch, "E3054", {"start": v(71.94, 36.59) * mm, "end": v(71.53, 35.54) * mm});
            skLineSegment(sketch, "E3055", {"start": v(71.53, 35.54) * mm, "end": v(71.06, 34.37) * mm});
            skLineSegment(sketch, "E3056", {"start": v(71.06, 34.37) * mm, "end": v(70.57, 33.15) * mm});
            skLineSegment(sketch, "E3057", {"start": v(70.57, 33.15) * mm, "end": v(70.1, 31.92) * mm});
            skLineSegment(sketch, "E3058", {"start": v(70.1, 31.92) * mm, "end": v(69.9, 31.33) * mm});
            skLineSegment(sketch, "E3059", {"start": v(69.9, 31.33) * mm, "end": v(69.7, 30.75) * mm});
            skLineSegment(sketch, "E3060", {"start": v(69.7, 30.75) * mm, "end": v(69.53, 30.2) * mm});
            skLineSegment(sketch, "E3061", {"start": v(69.53, 30.2) * mm, "end": v(69.39, 29.7) * mm});
            skLineSegment(sketch, "E3062", {"start": v(69.39, 29.7) * mm, "end": v(69.2, 29.06) * mm});
            skLineSegment(sketch, "E3063", {"start": v(69.2, 29.06) * mm, "end": v(69, 28.38) * mm});
            skLineSegment(sketch, "E3064", {"start": v(69, 28.38) * mm, "end": v(68.9, 28.04) * mm});
            skLineSegment(sketch, "E3065", {"start": v(68.9, 28.04) * mm, "end": v(68.82, 27.7) * mm});
            skLineSegment(sketch, "E3066", {"start": v(68.82, 27.7) * mm, "end": v(68.76, 27.37) * mm});
            skLineSegment(sketch, "E3067", {"start": v(68.76, 27.37) * mm, "end": v(68.72, 27.06) * mm});
            skLineSegment(sketch, "E3068", {"start": v(68.72, 27.06) * mm, "end": v(68.7, 26.52) * mm});
            skLineSegment(sketch, "E3069", {"start": v(68.7, 26.52) * mm, "end": v(68.69, 25.94) * mm});
            skLineSegment(sketch, "E3070", {"start": v(68.69, 25.94) * mm, "end": v(68.71, 25.34) * mm});
            skLineSegment(sketch, "E3071", {"start": v(68.71, 25.34) * mm, "end": v(68.76, 24.73) * mm});
            skLineSegment(sketch, "E3072", {"start": v(68.76, 24.73) * mm, "end": v(68.82, 24.12) * mm});
            skLineSegment(sketch, "E3073", {"start": v(68.82, 24.12) * mm, "end": v(68.9, 23.53) * mm});
            skLineSegment(sketch, "E3074", {"start": v(68.9, 23.53) * mm, "end": v(69, 22.96) * mm});
            skLineSegment(sketch, "E3075", {"start": v(69, 22.96) * mm, "end": v(69.1, 22.42) * mm});
            skLineSegment(sketch, "E3076", {"start": v(69.1, 22.42) * mm, "end": v(69.16, 22.12) * mm});
            skLineSegment(sketch, "E3077", {"start": v(69.16, 22.12) * mm, "end": v(69.24, 21.81) * mm});
            skLineSegment(sketch, "E3078", {"start": v(69.24, 21.81) * mm, "end": v(69.43, 21.17) * mm});
            skLineSegment(sketch, "E3079", {"start": v(69.43, 21.17) * mm, "end": v(69.66, 20.51) * mm});
            skLineSegment(sketch, "E3080", {"start": v(69.66, 20.51) * mm, "end": v(69.9, 19.85) * mm});
            skLineSegment(sketch, "E3081", {"start": v(69.9, 19.85) * mm, "end": v(70.4, 18.53) * mm});
            skLineSegment(sketch, "E3082", {"start": v(70.4, 18.53) * mm, "end": v(70.63, 17.9) * mm});
            skLineSegment(sketch, "E3083", {"start": v(70.63, 17.9) * mm, "end": v(70.84, 17.3) * mm});
            skLineSegment(sketch, "E3084", {"start": v(70.84, 17.3) * mm, "end": v(71.08, 17.3) * mm});
            skLineSegment(sketch, "E3085", {"start": v(71.08, 17.3) * mm, "end": v(71.34, 17.27) * mm});
            skLineSegment(sketch, "E3086", {"start": v(71.34, 17.27) * mm, "end": v(71.46, 17.26) * mm});
            skLineSegment(sketch, "E3087", {"start": v(71.46, 17.26) * mm, "end": v(71.59, 17.26) * mm});
            skLineSegment(sketch, "E3088", {"start": v(71.59, 17.26) * mm, "end": v(71.7, 17.28) * mm});
            skLineSegment(sketch, "E3089", {"start": v(71.7, 17.28) * mm, "end": v(71.81, 17.3) * mm});
            skLineSegment(sketch, "E3090", {"start": v(71.81, 17.3) * mm, "end": v(72.05, 17.43) * mm});
            skLineSegment(sketch, "E3091", {"start": v(72.05, 17.43) * mm, "end": v(72.3, 17.57) * mm});
            skLineSegment(sketch, "E3092", {"start": v(72.3, 17.57) * mm, "end": v(72.53, 17.73) * mm});
            skLineSegment(sketch, "E3093", {"start": v(72.53, 17.73) * mm, "end": v(72.76, 17.91) * mm});
            skLineSegment(sketch, "E3094", {"start": v(72.76, 17.91) * mm, "end": v(72.98, 18.1) * mm});
            skLineSegment(sketch, "E3095", {"start": v(72.98, 18.1) * mm, "end": v(73.2, 18.32) * mm});
            skLineSegment(sketch, "E3096", {"start": v(73.2, 18.32) * mm, "end": v(73.42, 18.55) * mm});
            skLineSegment(sketch, "E3097", {"start": v(73.42, 18.55) * mm, "end": v(73.63, 18.78) * mm});
            skLineSegment(sketch, "E3098", {"start": v(73.63, 18.78) * mm, "end": v(74.03, 19.27) * mm});
            skLineSegment(sketch, "E3099", {"start": v(74.03, 19.27) * mm, "end": v(74.4, 19.77) * mm});
            skLineSegment(sketch, "E3100", {"start": v(74.4, 19.77) * mm, "end": v(75.08, 20.71) * mm});
            skLineSegment(sketch, "E3101", {"start": v(75.08, 20.71) * mm, "end": v(75.2, 20.91) * mm});
            skLineSegment(sketch, "E3102", {"start": v(75.2, 20.91) * mm, "end": v(75.32, 21.13) * mm});
            skLineSegment(sketch, "E3103", {"start": v(75.32, 21.13) * mm, "end": v(75.54, 21.6) * mm});
            skLineSegment(sketch, "E3104", {"start": v(75.54, 21.6) * mm, "end": v(75.74, 22.09) * mm});
            skLineSegment(sketch, "E3105", {"start": v(75.74, 22.09) * mm, "end": v(75.94, 22.53) * mm});
            skLineSegment(sketch, "E3106", {"start": v(-62.1, 34.47) * mm, "end": v(-62.02, 34.68) * mm});
            skLineSegment(sketch, "E3107", {"start": v(-62.02, 34.68) * mm, "end": v(-61.87, 34.97) * mm});
            skLineSegment(sketch, "E3108", {"start": v(-61.87, 34.97) * mm, "end": v(-61.49, 35.67) * mm});
            skLineSegment(sketch, "E3109", {"start": v(-61.49, 35.67) * mm, "end": v(-61.3, 36.04) * mm});
            skLineSegment(sketch, "E3110", {"start": v(-61.3, 36.04) * mm, "end": v(-61.12, 36.38) * mm});
            skLineSegment(sketch, "E3111", {"start": v(-61.12, 36.38) * mm, "end": v(-61, 36.68) * mm});
            skLineSegment(sketch, "E3112", {"start": v(-61, 36.68) * mm, "end": v(-60.96, 36.8) * mm});
            skLineSegment(sketch, "E3113", {"start": v(-60.96, 36.8) * mm, "end": v(-60.94, 36.9) * mm});
            skLineSegment(sketch, "E3114", {"start": v(-60.94, 36.9) * mm, "end": v(-60.92, 37.29) * mm});
            skLineSegment(sketch, "E3115", {"start": v(-60.92, 37.29) * mm, "end": v(-60.92, 37.67) * mm});
            skLineSegment(sketch, "E3116", {"start": v(-60.92, 37.67) * mm, "end": v(-60.95, 38.05) * mm});
            skLineSegment(sketch, "E3117", {"start": v(-60.95, 38.05) * mm, "end": v(-60.99, 38.43) * mm});
            skLineSegment(sketch, "E3118", {"start": v(-60.99, 38.43) * mm, "end": v(-61.1, 39.18) * mm});
            skLineSegment(sketch, "E3119", {"start": v(-61.1, 39.18) * mm, "end": v(-61.2, 39.95) * mm});
            skLineSegment(sketch, "E3120", {"start": v(-61.2, 39.95) * mm, "end": v(-61.25, 40.32) * mm});
            skLineSegment(sketch, "E3121", {"start": v(-61.25, 40.32) * mm, "end": v(-61.27, 40.7) * mm});
            skLineSegment(sketch, "E3122", {"start": v(-61.27, 40.7) * mm, "end": v(-61.29, 41.1) * mm});
            skLineSegment(sketch, "E3123", {"start": v(-61.29, 41.1) * mm, "end": v(-61.3, 41.5) * mm});
            skLineSegment(sketch, "E3124", {"start": v(-61.3, 41.5) * mm, "end": v(-61.3, 42.33) * mm});
            skLineSegment(sketch, "E3125", {"start": v(-61.3, 42.33) * mm, "end": v(-61.26, 43.17) * mm});
            skLineSegment(sketch, "E3126", {"start": v(-61.26, 43.17) * mm, "end": v(-61.19, 44.77) * mm});
            skLineSegment(sketch, "E3127", {"start": v(-61.19, 44.77) * mm, "end": v(-61.16, 45.5) * mm});
            skLineSegment(sketch, "E3128", {"start": v(-61.16, 45.5) * mm, "end": v(-61.15, 46.14) * mm});
            skLineSegment(sketch, "E3129", {"start": v(-61.15, 46.14) * mm, "end": v(-61.13, 46.5) * mm});
            skLineSegment(sketch, "E3130", {"start": v(-61.13, 46.5) * mm, "end": v(-61.1, 46.88) * mm});
            skLineSegment(sketch, "E3131", {"start": v(-61.1, 46.88) * mm, "end": v(-61.06, 47.28) * mm});
            skLineSegment(sketch, "E3132", {"start": v(-61.06, 47.28) * mm, "end": v(-61.04, 47.7) * mm});
            skLineSegment(sketch, "E3133", {"start": v(-61.04, 47.7) * mm, "end": v(-61.04, 47.9) * mm});
            skLineSegment(sketch, "E3134", {"start": v(-61.04, 47.9) * mm, "end": v(-61.04, 48.1) * mm});
            skLineSegment(sketch, "E3135", {"start": v(-61.04, 48.1) * mm, "end": v(-61.06, 48.29) * mm});
            skLineSegment(sketch, "E3136", {"start": v(-61.06, 48.29) * mm, "end": v(-61.1, 48.47) * mm});
            skLineSegment(sketch, "E3137", {"start": v(-61.1, 48.47) * mm, "end": v(-61.14, 48.64) * mm});
            skLineSegment(sketch, "E3138", {"start": v(-61.14, 48.64) * mm, "end": v(-61.2, 48.8) * mm});
            skLineSegment(sketch, "E3139", {"start": v(-61.2, 48.8) * mm, "end": v(-61.28, 48.93) * mm});
            skLineSegment(sketch, "E3140", {"start": v(-61.28, 48.93) * mm, "end": v(-61.39, 49.06) * mm});
            skLineSegment(sketch, "E3141", {"start": v(-61.39, 49.06) * mm, "end": v(-61.41, 49.07) * mm});
            skLineSegment(sketch, "E3142", {"start": v(-61.41, 49.07) * mm, "end": v(-61.46, 49.07) * mm});
            skLineSegment(sketch, "E3143", {"start": v(-61.46, 49.07) * mm, "end": v(-61.6, 49.05) * mm});
            skLineSegment(sketch, "E3144", {"start": v(-61.6, 49.05) * mm, "end": v(-61.8, 49) * mm});
            skLineSegment(sketch, "E3145", {"start": v(-61.8, 49) * mm, "end": v(-62.04, 48.94) * mm});
            skLineSegment(sketch, "E3146", {"start": v(-62.04, 48.94) * mm, "end": v(-62.28, 48.87) * mm});
            skLineSegment(sketch, "E3147", {"start": v(-62.28, 48.87) * mm, "end": v(-62.5, 48.8) * mm});
            skLineSegment(sketch, "E3148", {"start": v(-62.5, 48.8) * mm, "end": v(-62.7, 48.72) * mm});
            skLineSegment(sketch, "E3149", {"start": v(-62.7, 48.72) * mm, "end": v(-62.85, 48.66) * mm});
            skLineSegment(sketch, "E3150", {"start": v(-62.85, 48.66) * mm, "end": v(-62.94, 48.59) * mm});
            skLineSegment(sketch, "E3151", {"start": v(-62.94, 48.59) * mm, "end": v(-63.1, 48.46) * mm});
            skLineSegment(sketch, "E3152", {"start": v(-63.1, 48.46) * mm, "end": v(-63.3, 48.26) * mm});
            skLineSegment(sketch, "E3153", {"start": v(-63.3, 48.26) * mm, "end": v(-63.55, 48.02) * mm});
            skLineSegment(sketch, "E3154", {"start": v(-63.55, 48.02) * mm, "end": v(-63.84, 47.72) * mm});
            skLineSegment(sketch, "E3155", {"start": v(-63.84, 47.72) * mm, "end": v(-64.15, 47.38) * mm});
            skLineSegment(sketch, "E3156", {"start": v(-64.15, 47.38) * mm, "end": v(-64.48, 47) * mm});
            skLineSegment(sketch, "E3157", {"start": v(-64.48, 47) * mm, "end": v(-64.82, 46.6) * mm});
            skLineSegment(sketch, "E3158", {"start": v(-64.82, 46.6) * mm, "end": v(-65.23, 46.1) * mm});
            skLineSegment(sketch, "E3159", {"start": v(-65.23, 46.1) * mm, "end": v(-65.67, 45.58) * mm});
            skLineSegment(sketch, "E3160", {"start": v(-65.67, 45.58) * mm, "end": v(-65.9, 45.31) * mm});
            skLineSegment(sketch, "E3161", {"start": v(-65.9, 45.31) * mm, "end": v(-66.1, 45.05) * mm});
            skLineSegment(sketch, "E3162", {"start": v(-66.1, 45.05) * mm, "end": v(-66.3, 44.79) * mm});
            skLineSegment(sketch, "E3163", {"start": v(-66.3, 44.79) * mm, "end": v(-66.47, 44.53) * mm});
            skLineSegment(sketch, "E3164", {"start": v(-66.47, 44.53) * mm, "end": v(-66.82, 43.98) * mm});
            skLineSegment(sketch, "E3165", {"start": v(-66.82, 43.98) * mm, "end": v(-67.18, 43.4) * mm});
            skLineSegment(sketch, "E3166", {"start": v(-67.18, 43.4) * mm, "end": v(-67.54, 42.78) * mm});
            skLineSegment(sketch, "E3167", {"start": v(-67.54, 42.78) * mm, "end": v(-67.9, 42.14) * mm});
            skLineSegment(sketch, "E3168", {"start": v(-67.9, 42.14) * mm, "end": v(-68.22, 41.49) * mm});
            skLineSegment(sketch, "E3169", {"start": v(-68.22, 41.49) * mm, "end": v(-68.37, 41.16) * mm});
            skLineSegment(sketch, "E3170", {"start": v(-68.37, 41.16) * mm, "end": v(-68.5, 40.84) * mm});
            skLineSegment(sketch, "E3171", {"start": v(-68.5, 40.84) * mm, "end": v(-68.64, 40.52) * mm});
            skLineSegment(sketch, "E3172", {"start": v(-68.64, 40.52) * mm, "end": v(-68.75, 40.2) * mm});
            skLineSegment(sketch, "E3173", {"start": v(-68.75, 40.2) * mm, "end": v(-68.85, 39.89) * mm});
            skLineSegment(sketch, "E3174", {"start": v(-68.85, 39.89) * mm, "end": v(-68.93, 39.58) * mm});
            skLineSegment(sketch, "E3175", {"start": v(-68.93, 39.58) * mm, "end": v(-69.02, 39.13) * mm});
            skLineSegment(sketch, "E3176", {"start": v(-69.02, 39.13) * mm, "end": v(-69.11, 38.67) * mm});
            skLineSegment(sketch, "E3177", {"start": v(-69.11, 38.67) * mm, "end": v(-69.18, 38.18) * mm});
            skLineSegment(sketch, "E3178", {"start": v(-69.18, 38.18) * mm, "end": v(-69.24, 37.68) * mm});
            skLineSegment(sketch, "E3179", {"start": v(-69.24, 37.68) * mm, "end": v(-69.3, 37.17) * mm});
            skLineSegment(sketch, "E3180", {"start": v(-69.3, 37.17) * mm, "end": v(-69.33, 36.65) * mm});
            skLineSegment(sketch, "E3181", {"start": v(-69.33, 36.65) * mm, "end": v(-69.35, 36.12) * mm});
            skLineSegment(sketch, "E3182", {"start": v(-69.35, 36.12) * mm, "end": v(-69.36, 35.6) * mm});
            skLineSegment(sketch, "E3183", {"start": v(-69.36, 35.6) * mm, "end": v(-69.36, 35.06) * mm});
            skLineSegment(sketch, "E3184", {"start": v(-69.36, 35.06) * mm, "end": v(-69.34, 34.54) * mm});
            skLineSegment(sketch, "E3185", {"start": v(-69.34, 34.54) * mm, "end": v(-69.31, 34.02) * mm});
            skLineSegment(sketch, "E3186", {"start": v(-69.31, 34.02) * mm, "end": v(-69.27, 33.5) * mm});
            skLineSegment(sketch, "E3187", {"start": v(-69.27, 33.5) * mm, "end": v(-69.21, 33) * mm});
            skLineSegment(sketch, "E3188", {"start": v(-69.21, 33) * mm, "end": v(-69.14, 32.52) * mm});
            skLineSegment(sketch, "E3189", {"start": v(-69.14, 32.52) * mm, "end": v(-69.06, 32.05) * mm});
            skLineSegment(sketch, "E3190", {"start": v(-69.06, 32.05) * mm, "end": v(-68.96, 31.6) * mm});
            skLineSegment(sketch, "E3191", {"start": v(-68.96, 31.6) * mm, "end": v(-68.8, 31.02) * mm});
            skLineSegment(sketch, "E3192", {"start": v(-68.8, 31.02) * mm, "end": v(-68.72, 30.72) * mm});
            skLineSegment(sketch, "E3193", {"start": v(-68.72, 30.72) * mm, "end": v(-68.61, 30.41) * mm});
            skLineSegment(sketch, "E3194", {"start": v(-68.61, 30.41) * mm, "end": v(-68.5, 30.1) * mm});
            skLineSegment(sketch, "E3195", {"start": v(-68.5, 30.1) * mm, "end": v(-68.38, 29.78) * mm});
            skLineSegment(sketch, "E3196", {"start": v(-68.38, 29.78) * mm, "end": v(-68.25, 29.47) * mm});
            skLineSegment(sketch, "E3197", {"start": v(-68.25, 29.47) * mm, "end": v(-68.11, 29.16) * mm});
            skLineSegment(sketch, "E3198", {"start": v(-68.11, 29.16) * mm, "end": v(-67.96, 28.85) * mm});
            skLineSegment(sketch, "E3199", {"start": v(-67.96, 28.85) * mm, "end": v(-67.8, 28.56) * mm});
            skLineSegment(sketch, "E3200", {"start": v(-67.8, 28.56) * mm, "end": v(-67.63, 28.27) * mm});
            skLineSegment(sketch, "E3201", {"start": v(-67.63, 28.27) * mm, "end": v(-67.46, 28) * mm});
            skLineSegment(sketch, "E3202", {"start": v(-67.46, 28) * mm, "end": v(-67.27, 27.74) * mm});
            skLineSegment(sketch, "E3203", {"start": v(-67.27, 27.74) * mm, "end": v(-67.07, 27.5) * mm});
            skLineSegment(sketch, "E3204", {"start": v(-67.07, 27.5) * mm, "end": v(-66.87, 27.29) * mm});
            skLineSegment(sketch, "E3205", {"start": v(-66.87, 27.29) * mm, "end": v(-66.65, 27.1) * mm});
            skLineSegment(sketch, "E3206", {"start": v(-66.65, 27.1) * mm, "end": v(-66.58, 27.04) * mm});
            skLineSegment(sketch, "E3207", {"start": v(-66.58, 27.04) * mm, "end": v(-66.5, 27) * mm});
            skLineSegment(sketch, "E3208", {"start": v(-66.5, 27) * mm, "end": v(-66.42, 26.95) * mm});
            skLineSegment(sketch, "E3209", {"start": v(-66.42, 26.95) * mm, "end": v(-66.33, 26.91) * mm});
            skLineSegment(sketch, "E3210", {"start": v(-66.33, 26.91) * mm, "end": v(-66.24, 26.89) * mm});
            skLineSegment(sketch, "E3211", {"start": v(-66.24, 26.89) * mm, "end": v(-66.15, 26.87) * mm});
            skLineSegment(sketch, "E3212", {"start": v(-66.15, 26.87) * mm, "end": v(-66.07, 26.87) * mm});
            skLineSegment(sketch, "E3213", {"start": v(-66.07, 26.87) * mm, "end": v(-66, 26.9) * mm});
            skLineSegment(sketch, "E3214", {"start": v(-66, 26.9) * mm, "end": v(-65.81, 26.97) * mm});
            skLineSegment(sketch, "E3215", {"start": v(-65.81, 26.97) * mm, "end": v(-65.64, 27.07) * mm});
            skLineSegment(sketch, "E3216", {"start": v(-65.64, 27.07) * mm, "end": v(-65.48, 27.18) * mm});
            skLineSegment(sketch, "E3217", {"start": v(-65.48, 27.18) * mm, "end": v(-65.32, 27.3) * mm});
            skLineSegment(sketch, "E3218", {"start": v(-65.32, 27.3) * mm, "end": v(-65.17, 27.44) * mm});
            skLineSegment(sketch, "E3219", {"start": v(-65.17, 27.44) * mm, "end": v(-65.03, 27.58) * mm});
            skLineSegment(sketch, "E3220", {"start": v(-65.03, 27.58) * mm, "end": v(-64.9, 27.74) * mm});
            skLineSegment(sketch, "E3221", {"start": v(-64.9, 27.74) * mm, "end": v(-64.76, 27.9) * mm});
            skLineSegment(sketch, "E3222", {"start": v(-64.76, 27.9) * mm, "end": v(-64.64, 28.08) * mm});
            skLineSegment(sketch, "E3223", {"start": v(-64.64, 28.08) * mm, "end": v(-64.51, 28.27) * mm});
            skLineSegment(sketch, "E3224", {"start": v(-64.51, 28.27) * mm, "end": v(-64.29, 28.66) * mm});
            skLineSegment(sketch, "E3225", {"start": v(-64.29, 28.66) * mm, "end": v(-64.08, 29.08) * mm});
            skLineSegment(sketch, "E3226", {"start": v(-64.08, 29.08) * mm, "end": v(-63.88, 29.52) * mm});
            skLineSegment(sketch, "E3227", {"start": v(-63.88, 29.52) * mm, "end": v(-63.7, 29.97) * mm});
            skLineSegment(sketch, "E3228", {"start": v(-63.7, 29.97) * mm, "end": v(-63.53, 30.42) * mm});
            skLineSegment(sketch, "E3229", {"start": v(-63.53, 30.42) * mm, "end": v(-63.2, 31.33) * mm});
            skLineSegment(sketch, "E3230", {"start": v(-63.2, 31.33) * mm, "end": v(-62.9, 32.2) * mm});
            skLineSegment(sketch, "E3231", {"start": v(-62.9, 32.2) * mm, "end": v(-62.75, 32.6) * mm});
            skLineSegment(sketch, "E3232", {"start": v(-62.75, 32.6) * mm, "end": v(-62.6, 32.98) * mm});
            skLineSegment(sketch, "E3233", {"start": v(-62.6, 32.98) * mm, "end": v(-62.46, 33.33) * mm});
            skLineSegment(sketch, "E3234", {"start": v(-62.46, 33.33) * mm, "end": v(-62.34, 33.72) * mm});
            skLineSegment(sketch, "E3235", {"start": v(-62.34, 33.72) * mm, "end": v(-62.22, 34.1) * mm});
            skLineSegment(sketch, "E3236", {"start": v(-62.22, 34.1) * mm, "end": v(-62.1, 34.47) * mm});
            skLineSegment(sketch, "E3237", {"start": v(68.86, 32.95) * mm, "end": v(68.96, 33.34) * mm});
            skLineSegment(sketch, "E3238", {"start": v(68.96, 33.34) * mm, "end": v(69.07, 33.76) * mm});
            skLineSegment(sketch, "E3239", {"start": v(69.07, 33.76) * mm, "end": v(69.16, 34.18) * mm});
            skLineSegment(sketch, "E3240", {"start": v(69.16, 34.18) * mm, "end": v(69.2, 34.39) * mm});
            skLineSegment(sketch, "E3241", {"start": v(69.2, 34.39) * mm, "end": v(69.21, 34.58) * mm});
            skLineSegment(sketch, "E3242", {"start": v(69.21, 34.58) * mm, "end": v(69.23, 35.08) * mm});
            skLineSegment(sketch, "E3243", {"start": v(69.23, 35.08) * mm, "end": v(69.22, 35.6) * mm});
            skLineSegment(sketch, "E3244", {"start": v(69.22, 35.6) * mm, "end": v(69.18, 36.14) * mm});
            skLineSegment(sketch, "E3245", {"start": v(69.18, 36.14) * mm, "end": v(69.13, 36.7) * mm});
            skLineSegment(sketch, "E3246", {"start": v(69.13, 36.7) * mm, "end": v(69.06, 37.25) * mm});
            skLineSegment(sketch, "E3247", {"start": v(69.06, 37.25) * mm, "end": v(68.98, 37.79) * mm});
            skLineSegment(sketch, "E3248", {"start": v(68.98, 37.79) * mm, "end": v(68.89, 38.3) * mm});
            skLineSegment(sketch, "E3249", {"start": v(68.89, 38.3) * mm, "end": v(68.78, 38.8) * mm});
            skLineSegment(sketch, "E3250", {"start": v(68.78, 38.8) * mm, "end": v(68.73, 39) * mm});
            skLineSegment(sketch, "E3251", {"start": v(68.73, 39) * mm, "end": v(68.66, 39.21) * mm});
            skLineSegment(sketch, "E3252", {"start": v(68.66, 39.21) * mm, "end": v(68.48, 39.66) * mm});
            skLineSegment(sketch, "E3253", {"start": v(68.48, 39.66) * mm, "end": v(68.3, 40.1) * mm});
            skLineSegment(sketch, "E3254", {"start": v(68.3, 40.1) * mm, "end": v(68.14, 40.52) * mm});
            skLineSegment(sketch, "E3255", {"start": v(68.14, 40.52) * mm, "end": v(67.99, 40.9) * mm});
            skLineSegment(sketch, "E3256", {"start": v(67.99, 40.9) * mm, "end": v(67.8, 41.32) * mm});
            skLineSegment(sketch, "E3257", {"start": v(67.8, 41.32) * mm, "end": v(67.6, 41.77) * mm});
            skLineSegment(sketch, "E3258", {"start": v(67.6, 41.77) * mm, "end": v(67.36, 42.23) * mm});
            skLineSegment(sketch, "E3259", {"start": v(67.36, 42.23) * mm, "end": v(67.13, 42.7) * mm});
            skLineSegment(sketch, "E3260", {"start": v(67.13, 42.7) * mm, "end": v(66.88, 43.14) * mm});
            skLineSegment(sketch, "E3261", {"start": v(66.88, 43.14) * mm, "end": v(66.64, 43.55) * mm});
            skLineSegment(sketch, "E3262", {"start": v(66.64, 43.55) * mm, "end": v(66.42, 43.93) * mm});
            skLineSegment(sketch, "E3263", {"start": v(66.42, 43.93) * mm, "end": v(66.18, 44.29) * mm});
            skLineSegment(sketch, "E3264", {"start": v(66.18, 44.29) * mm, "end": v(65.9, 44.67) * mm});
            skLineSegment(sketch, "E3265", {"start": v(65.9, 44.67) * mm, "end": v(65.61, 45.07) * mm});
            skLineSegment(sketch, "E3266", {"start": v(65.61, 45.07) * mm, "end": v(65.3, 45.5) * mm});
            skLineSegment(sketch, "E3267", {"start": v(65.3, 45.5) * mm, "end": v(64.96, 45.91) * mm});
            skLineSegment(sketch, "E3268", {"start": v(64.96, 45.91) * mm, "end": v(64.62, 46.33) * mm});
            skLineSegment(sketch, "E3269", {"start": v(64.62, 46.33) * mm, "end": v(63.92, 47.14) * mm});
            skLineSegment(sketch, "E3270", {"start": v(63.92, 47.14) * mm, "end": v(63.59, 47.52) * mm});
            skLineSegment(sketch, "E3271", {"start": v(63.59, 47.52) * mm, "end": v(63.27, 47.87) * mm});
            skLineSegment(sketch, "E3272", {"start": v(63.27, 47.87) * mm, "end": v(62.97, 48.18) * mm});
            skLineSegment(sketch, "E3273", {"start": v(62.97, 48.18) * mm, "end": v(62.7, 48.45) * mm});
            skLineSegment(sketch, "E3274", {"start": v(62.7, 48.45) * mm, "end": v(62.45, 48.68) * mm});
            skLineSegment(sketch, "E3275", {"start": v(62.45, 48.68) * mm, "end": v(62.25, 48.84) * mm});
            skLineSegment(sketch, "E3276", {"start": v(62.25, 48.84) * mm, "end": v(62.09, 48.95) * mm});
            skLineSegment(sketch, "E3277", {"start": v(62.09, 48.95) * mm, "end": v(62.03, 48.98) * mm});
            skLineSegment(sketch, "E3278", {"start": v(62.03, 48.98) * mm, "end": v(61.98, 48.99) * mm});
            skLineSegment(sketch, "E3279", {"start": v(61.98, 48.99) * mm, "end": v(61.7, 48.99) * mm});
            skLineSegment(sketch, "E3280", {"start": v(61.7, 48.99) * mm, "end": v(61.7, 48.25) * mm});
            skLineSegment(sketch, "E3281", {"start": v(61.7, 48.25) * mm, "end": v(61.69, 47.48) * mm});
            skLineSegment(sketch, "E3282", {"start": v(61.69, 47.48) * mm, "end": v(61.62, 45.88) * mm});
            skLineSegment(sketch, "E3283", {"start": v(61.62, 45.88) * mm, "end": v(61.53, 44.22) * mm});
            skLineSegment(sketch, "E3284", {"start": v(61.53, 44.22) * mm, "end": v(61.48, 43.38) * mm});
            skLineSegment(sketch, "E3285", {"start": v(61.48, 43.38) * mm, "end": v(61.45, 42.53) * mm});
            skLineSegment(sketch, "E3286", {"start": v(61.45, 42.53) * mm, "end": v(61.42, 41.69) * mm});
            skLineSegment(sketch, "E3287", {"start": v(61.42, 41.69) * mm, "end": v(61.4, 40.85) * mm});
            skLineSegment(sketch, "E3288", {"start": v(61.4, 40.85) * mm, "end": v(61.41, 40.02) * mm});
            skLineSegment(sketch, "E3289", {"start": v(61.41, 40.02) * mm, "end": v(61.44, 39.2) * mm});
            skLineSegment(sketch, "E3290", {"start": v(61.44, 39.2) * mm, "end": v(61.49, 38.4) * mm});
            skLineSegment(sketch, "E3291", {"start": v(61.49, 38.4) * mm, "end": v(61.53, 38.01) * mm});
            skLineSegment(sketch, "E3292", {"start": v(61.53, 38.01) * mm, "end": v(61.57, 37.63) * mm});
            skLineSegment(sketch, "E3293", {"start": v(61.57, 37.63) * mm, "end": v(61.62, 37.25) * mm});
            skLineSegment(sketch, "E3294", {"start": v(61.62, 37.25) * mm, "end": v(61.68, 36.88) * mm});
            skLineSegment(sketch, "E3295", {"start": v(61.68, 36.88) * mm, "end": v(61.75, 36.52) * mm});
            skLineSegment(sketch, "E3296", {"start": v(61.75, 36.52) * mm, "end": v(61.83, 36.16) * mm});
            skLineSegment(sketch, "E3297", {"start": v(61.83, 36.16) * mm, "end": v(61.88, 36.03) * mm});
            skLineSegment(sketch, "E3298", {"start": v(61.88, 36.03) * mm, "end": v(61.93, 35.89) * mm});
            skLineSegment(sketch, "E3299", {"start": v(61.93, 35.89) * mm, "end": v(62.08, 35.6) * mm});
            skLineSegment(sketch, "E3300", {"start": v(62.08, 35.6) * mm, "end": v(62.24, 35.33) * mm});
            skLineSegment(sketch, "E3301", {"start": v(62.24, 35.33) * mm, "end": v(62.39, 35.07) * mm});
            skLineSegment(sketch, "E3302", {"start": v(62.39, 35.07) * mm, "end": v(62.54, 34.79) * mm});
            skLineSegment(sketch, "E3303", {"start": v(62.54, 34.79) * mm, "end": v(62.75, 34.41) * mm});
            skLineSegment(sketch, "E3304", {"start": v(62.75, 34.41) * mm, "end": v(63.32, 33.45) * mm});
            skLineSegment(sketch, "E3305", {"start": v(63.32, 33.45) * mm, "end": v(64.02, 32.3) * mm});
            skLineSegment(sketch, "E3306", {"start": v(64.02, 32.3) * mm, "end": v(64.78, 31.09) * mm});
            skLineSegment(sketch, "E3307", {"start": v(64.78, 31.09) * mm, "end": v(66.62, 28.2) * mm});
            skLineSegment(sketch, "E3308", {"start": v(66.62, 28.2) * mm, "end": v(66.9, 28.2) * mm});
            skLineSegment(sketch, "E3309", {"start": v(66.9, 28.2) * mm, "end": v(66.94, 28.2) * mm});
            skLineSegment(sketch, "E3310", {"start": v(66.94, 28.2) * mm, "end": v(66.98, 28.23) * mm});
            skLineSegment(sketch, "E3311", {"start": v(66.98, 28.23) * mm, "end": v(67.03, 28.27) * mm});
            skLineSegment(sketch, "E3312", {"start": v(67.03, 28.27) * mm, "end": v(67.08, 28.32) * mm});
            skLineSegment(sketch, "E3313", {"start": v(67.08, 28.32) * mm, "end": v(67.2, 28.47) * mm});
            skLineSegment(sketch, "E3314", {"start": v(67.2, 28.47) * mm, "end": v(67.31, 28.66) * mm});
            skLineSegment(sketch, "E3315", {"start": v(67.31, 28.66) * mm, "end": v(67.44, 28.9) * mm});
            skLineSegment(sketch, "E3316", {"start": v(67.44, 28.9) * mm, "end": v(67.58, 29.19) * mm});
            skLineSegment(sketch, "E3317", {"start": v(67.58, 29.19) * mm, "end": v(67.72, 29.5) * mm});
            skLineSegment(sketch, "E3318", {"start": v(67.72, 29.5) * mm, "end": v(67.87, 29.84) * mm});
            skLineSegment(sketch, "E3319", {"start": v(67.87, 29.84) * mm, "end": v(68.02, 30.2) * mm});
            skLineSegment(sketch, "E3320", {"start": v(68.02, 30.2) * mm, "end": v(68.16, 30.59) * mm});
            skLineSegment(sketch, "E3321", {"start": v(68.16, 30.59) * mm, "end": v(68.3, 30.98) * mm});
            skLineSegment(sketch, "E3322", {"start": v(68.3, 30.98) * mm, "end": v(68.43, 31.38) * mm});
            skLineSegment(sketch, "E3323", {"start": v(68.43, 31.38) * mm, "end": v(68.56, 31.78) * mm});
            skLineSegment(sketch, "E3324", {"start": v(68.56, 31.78) * mm, "end": v(68.67, 32.18) * mm});
            skLineSegment(sketch, "E3325", {"start": v(68.67, 32.18) * mm, "end": v(68.78, 32.57) * mm});
            skLineSegment(sketch, "E3326", {"start": v(68.78, 32.57) * mm, "end": v(68.86, 32.95) * mm});
            skLineSegment(sketch, "E3327", {"start": v(-50.97, 30.87) * mm, "end": v(-50.48, 31.05) * mm});
            skLineSegment(sketch, "E3328", {"start": v(-50.48, 31.05) * mm, "end": v(-49.96, 31.24) * mm});
            skLineSegment(sketch, "E3329", {"start": v(-49.96, 31.24) * mm, "end": v(-49.7, 31.33) * mm});
            skLineSegment(sketch, "E3330", {"start": v(-49.7, 31.33) * mm, "end": v(-49.44, 31.44) * mm});
            skLineSegment(sketch, "E3331", {"start": v(-49.44, 31.44) * mm, "end": v(-49.2, 31.55) * mm});
            skLineSegment(sketch, "E3332", {"start": v(-49.2, 31.55) * mm, "end": v(-48.98, 31.66) * mm});
            skLineSegment(sketch, "E3333", {"start": v(-48.98, 31.66) * mm, "end": v(-48.45, 31.97) * mm});
            skLineSegment(sketch, "E3334", {"start": v(-48.45, 31.97) * mm, "end": v(-47.9, 32.31) * mm});
            skLineSegment(sketch, "E3335", {"start": v(-47.9, 32.31) * mm, "end": v(-47.34, 32.7) * mm});
            skLineSegment(sketch, "E3336", {"start": v(-47.34, 32.7) * mm, "end": v(-46.78, 33.1) * mm});
            skLineSegment(sketch, "E3337", {"start": v(-46.78, 33.1) * mm, "end": v(-46.23, 33.5) * mm});
            skLineSegment(sketch, "E3338", {"start": v(-46.23, 33.5) * mm, "end": v(-45.7, 33.93) * mm});
            skLineSegment(sketch, "E3339", {"start": v(-45.7, 33.93) * mm, "end": v(-45.2, 34.35) * mm});
            skLineSegment(sketch, "E3340", {"start": v(-45.2, 34.35) * mm, "end": v(-44.75, 34.76) * mm});
            skLineSegment(sketch, "E3341", {"start": v(-44.75, 34.76) * mm, "end": v(-44.52, 35) * mm});
            skLineSegment(sketch, "E3342", {"start": v(-44.52, 35) * mm, "end": v(-44.28, 35.26) * mm});
            skLineSegment(sketch, "E3343", {"start": v(-44.28, 35.26) * mm, "end": v(-43.82, 35.83) * mm});
            skLineSegment(sketch, "E3344", {"start": v(-43.82, 35.83) * mm, "end": v(-43.37, 36.41) * mm});
            skLineSegment(sketch, "E3345", {"start": v(-43.37, 36.41) * mm, "end": v(-42.95, 36.95) * mm});
            skLineSegment(sketch, "E3346", {"start": v(-42.95, 36.95) * mm, "end": v(-42.56, 37.43) * mm});
            skLineSegment(sketch, "E3347", {"start": v(-42.56, 37.43) * mm, "end": v(-42.17, 37.95) * mm});
            skLineSegment(sketch, "E3348", {"start": v(-42.17, 37.95) * mm, "end": v(-41.76, 38.5) * mm});
            skLineSegment(sketch, "E3349", {"start": v(-41.76, 38.5) * mm, "end": v(-41.37, 39.06) * mm});
            skLineSegment(sketch, "E3350", {"start": v(-41.37, 39.06) * mm, "end": v(-41, 39.61) * mm});
            skLineSegment(sketch, "E3351", {"start": v(-41, 39.61) * mm, "end": v(-40.66, 40.14) * mm});
            skLineSegment(sketch, "E3352", {"start": v(-40.66, 40.14) * mm, "end": v(-40.36, 40.63) * mm});
            skLineSegment(sketch, "E3353", {"start": v(-40.36, 40.63) * mm, "end": v(-40.11, 41.07) * mm});
            skLineSegment(sketch, "E3354", {"start": v(-40.11, 41.07) * mm, "end": v(-39.97, 41.3) * mm});
            skLineSegment(sketch, "E3355", {"start": v(-39.97, 41.3) * mm, "end": v(-39.8, 41.52) * mm});
            skLineSegment(sketch, "E3356", {"start": v(-39.8, 41.52) * mm, "end": v(-39.6, 41.77) * mm});
            skLineSegment(sketch, "E3357", {"start": v(-39.6, 41.77) * mm, "end": v(-39.42, 42.01) * mm});
            skLineSegment(sketch, "E3358", {"start": v(-39.42, 42.01) * mm, "end": v(-39.25, 42.26) * mm});
            skLineSegment(sketch, "E3359", {"start": v(-39.25, 42.26) * mm, "end": v(-39.18, 42.39) * mm});
            skLineSegment(sketch, "E3360", {"start": v(-39.18, 42.39) * mm, "end": v(-39.13, 42.51) * mm});
            skLineSegment(sketch, "E3361", {"start": v(-39.13, 42.51) * mm, "end": v(-39.09, 42.64) * mm});
            skLineSegment(sketch, "E3362", {"start": v(-39.09, 42.64) * mm, "end": v(-39.07, 42.76) * mm});
            skLineSegment(sketch, "E3363", {"start": v(-39.07, 42.76) * mm, "end": v(-39.06, 42.88) * mm});
            skLineSegment(sketch, "E3364", {"start": v(-39.06, 42.88) * mm, "end": v(-39.08, 43) * mm});
            skLineSegment(sketch, "E3365", {"start": v(-39.08, 43) * mm, "end": v(-39.12, 43.07) * mm});
            skLineSegment(sketch, "E3366", {"start": v(-39.12, 43.07) * mm, "end": v(-39.17, 43.14) * mm});
            skLineSegment(sketch, "E3367", {"start": v(-39.17, 43.14) * mm, "end": v(-39.25, 43.2) * mm});
            skLineSegment(sketch, "E3368", {"start": v(-39.25, 43.2) * mm, "end": v(-39.33, 43.25) * mm});
            skLineSegment(sketch, "E3369", {"start": v(-39.33, 43.25) * mm, "end": v(-39.52, 43.33) * mm});
            skLineSegment(sketch, "E3370", {"start": v(-39.52, 43.33) * mm, "end": v(-39.7, 43.38) * mm});
            skLineSegment(sketch, "E3371", {"start": v(-39.7, 43.38) * mm, "end": v(-40.04, 43.44) * mm});
            skLineSegment(sketch, "E3372", {"start": v(-40.04, 43.44) * mm, "end": v(-40.4, 43.48) * mm});
            skLineSegment(sketch, "E3373", {"start": v(-40.4, 43.48) * mm, "end": v(-40.78, 43.5) * mm});
            skLineSegment(sketch, "E3374", {"start": v(-40.78, 43.5) * mm, "end": v(-41.17, 43.5) * mm});
            skLineSegment(sketch, "E3375", {"start": v(-41.17, 43.5) * mm, "end": v(-41.56, 43.48) * mm});
            skLineSegment(sketch, "E3376", {"start": v(-41.56, 43.48) * mm, "end": v(-41.96, 43.45) * mm});
            skLineSegment(sketch, "E3377", {"start": v(-41.96, 43.45) * mm, "end": v(-42.37, 43.4) * mm});
            skLineSegment(sketch, "E3378", {"start": v(-42.37, 43.4) * mm, "end": v(-42.77, 43.34) * mm});
            skLineSegment(sketch, "E3379", {"start": v(-42.77, 43.34) * mm, "end": v(-43.59, 43.2) * mm});
            skLineSegment(sketch, "E3380", {"start": v(-43.59, 43.2) * mm, "end": v(-44.38, 43.04) * mm});
            skLineSegment(sketch, "E3381", {"start": v(-44.38, 43.04) * mm, "end": v(-45.15, 42.87) * mm});
            skLineSegment(sketch, "E3382", {"start": v(-45.15, 42.87) * mm, "end": v(-45.86, 42.73) * mm});
            skLineSegment(sketch, "E3383", {"start": v(-45.86, 42.73) * mm, "end": v(-46.15, 42.67) * mm});
            skLineSegment(sketch, "E3384", {"start": v(-46.15, 42.67) * mm, "end": v(-46.45, 42.6) * mm});
            skLineSegment(sketch, "E3385", {"start": v(-46.45, 42.6) * mm, "end": v(-47.08, 42.41) * mm});
            skLineSegment(sketch, "E3386", {"start": v(-47.08, 42.41) * mm, "end": v(-47.7, 42.22) * mm});
            skLineSegment(sketch, "E3387", {"start": v(-47.7, 42.22) * mm, "end": v(-48.29, 42.05) * mm});
            skLineSegment(sketch, "E3388", {"start": v(-48.29, 42.05) * mm, "end": v(-48.78, 41.91) * mm});
            skLineSegment(sketch, "E3389", {"start": v(-48.78, 41.91) * mm, "end": v(-49.24, 41.77) * mm});
            skLineSegment(sketch, "E3390", {"start": v(-49.24, 41.77) * mm, "end": v(-49.7, 41.62) * mm});
            skLineSegment(sketch, "E3391", {"start": v(-49.7, 41.62) * mm, "end": v(-50.13, 41.47) * mm});
            skLineSegment(sketch, "E3392", {"start": v(-50.13, 41.47) * mm, "end": v(-50.55, 41.32) * mm});
            skLineSegment(sketch, "E3393", {"start": v(-50.55, 41.32) * mm, "end": v(-50.96, 41.16) * mm});
            skLineSegment(sketch, "E3394", {"start": v(-50.96, 41.16) * mm, "end": v(-51.36, 41) * mm});
            skLineSegment(sketch, "E3395", {"start": v(-51.36, 41) * mm, "end": v(-51.76, 40.81) * mm});
            skLineSegment(sketch, "E3396", {"start": v(-51.76, 40.81) * mm, "end": v(-52.15, 40.63) * mm});
            skLineSegment(sketch, "E3397", {"start": v(-52.15, 40.63) * mm, "end": v(-52.53, 40.44) * mm});
            skLineSegment(sketch, "E3398", {"start": v(-52.53, 40.44) * mm, "end": v(-52.91, 40.23) * mm});
            skLineSegment(sketch, "E3399", {"start": v(-52.91, 40.23) * mm, "end": v(-53.3, 40.02) * mm});
            skLineSegment(sketch, "E3400", {"start": v(-53.3, 40.02) * mm, "end": v(-53.68, 39.79) * mm});
            skLineSegment(sketch, "E3401", {"start": v(-53.68, 39.79) * mm, "end": v(-54.06, 39.55) * mm});
            skLineSegment(sketch, "E3402", {"start": v(-54.06, 39.55) * mm, "end": v(-54.46, 39.3) * mm});
            skLineSegment(sketch, "E3403", {"start": v(-54.46, 39.3) * mm, "end": v(-54.86, 39.02) * mm});
            skLineSegment(sketch, "E3404", {"start": v(-54.86, 39.02) * mm, "end": v(-55.2, 38.8) * mm});
            skLineSegment(sketch, "E3405", {"start": v(-55.2, 38.8) * mm, "end": v(-55.58, 38.57) * mm});
            skLineSegment(sketch, "E3406", {"start": v(-55.58, 38.57) * mm, "end": v(-55.77, 38.45) * mm});
            skLineSegment(sketch, "E3407", {"start": v(-55.77, 38.45) * mm, "end": v(-55.95, 38.32) * mm});
            skLineSegment(sketch, "E3408", {"start": v(-55.95, 38.32) * mm, "end": v(-56.11, 38.2) * mm});
            skLineSegment(sketch, "E3409", {"start": v(-56.11, 38.2) * mm, "end": v(-56.26, 38.06) * mm});
            skLineSegment(sketch, "E3410", {"start": v(-56.26, 38.06) * mm, "end": v(-56.44, 37.87) * mm});
            skLineSegment(sketch, "E3411", {"start": v(-56.44, 37.87) * mm, "end": v(-56.62, 37.65) * mm});
            skLineSegment(sketch, "E3412", {"start": v(-56.62, 37.65) * mm, "end": v(-56.8, 37.42) * mm});
            skLineSegment(sketch, "E3413", {"start": v(-56.8, 37.42) * mm, "end": v(-56.97, 37.18) * mm});
            skLineSegment(sketch, "E3414", {"start": v(-56.97, 37.18) * mm, "end": v(-57.3, 36.69) * mm});
            skLineSegment(sketch, "E3415", {"start": v(-57.3, 36.69) * mm, "end": v(-57.6, 36.24) * mm});
            skLineSegment(sketch, "E3416", {"start": v(-57.6, 36.24) * mm, "end": v(-57.87, 35.88) * mm});
            skLineSegment(sketch, "E3417", {"start": v(-57.87, 35.88) * mm, "end": v(-58.13, 35.5) * mm});
            skLineSegment(sketch, "E3418", {"start": v(-58.13, 35.5) * mm, "end": v(-58.39, 35.09) * mm});
            skLineSegment(sketch, "E3419", {"start": v(-58.39, 35.09) * mm, "end": v(-58.64, 34.66) * mm});
            skLineSegment(sketch, "E3420", {"start": v(-58.64, 34.66) * mm, "end": v(-58.9, 34.23) * mm});
            skLineSegment(sketch, "E3421", {"start": v(-58.9, 34.23) * mm, "end": v(-59.14, 33.8) * mm});
            skLineSegment(sketch, "E3422", {"start": v(-59.14, 33.8) * mm, "end": v(-59.37, 33.36) * mm});
            skLineSegment(sketch, "E3423", {"start": v(-59.37, 33.36) * mm, "end": v(-59.59, 32.93) * mm});
            skLineSegment(sketch, "E3424", {"start": v(-59.59, 32.93) * mm, "end": v(-59.8, 32.51) * mm});
            skLineSegment(sketch, "E3425", {"start": v(-59.8, 32.51) * mm, "end": v(-59.98, 32.1) * mm});
            skLineSegment(sketch, "E3426", {"start": v(-59.98, 32.1) * mm, "end": v(-60.14, 31.73) * mm});
            skLineSegment(sketch, "E3427", {"start": v(-60.14, 31.73) * mm, "end": v(-60.28, 31.37) * mm});
            skLineSegment(sketch, "E3428", {"start": v(-60.28, 31.37) * mm, "end": v(-60.4, 31.05) * mm});
            skLineSegment(sketch, "E3429", {"start": v(-60.4, 31.05) * mm, "end": v(-60.48, 30.77) * mm});
            skLineSegment(sketch, "E3430", {"start": v(-60.48, 30.77) * mm, "end": v(-60.53, 30.53) * mm});
            skLineSegment(sketch, "E3431", {"start": v(-60.53, 30.53) * mm, "end": v(-60.54, 30.42) * mm});
            skLineSegment(sketch, "E3432", {"start": v(-60.54, 30.42) * mm, "end": v(-60.55, 30.33) * mm});
            skLineSegment(sketch, "E3433", {"start": v(-60.55, 30.33) * mm, "end": v(-60.56, 30.2) * mm});
            skLineSegment(sketch, "E3434", {"start": v(-60.56, 30.2) * mm, "end": v(-60.6, 30.06) * mm});
            skLineSegment(sketch, "E3435", {"start": v(-60.6, 30.06) * mm, "end": v(-60.6, 29.99) * mm});
            skLineSegment(sketch, "E3436", {"start": v(-60.6, 29.99) * mm, "end": v(-60.6, 29.93) * mm});
            skLineSegment(sketch, "E3437", {"start": v(-60.6, 29.93) * mm, "end": v(-60.58, 29.88) * mm});
            skLineSegment(sketch, "E3438", {"start": v(-60.58, 29.88) * mm, "end": v(-60.55, 29.85) * mm});
            skLineSegment(sketch, "E3439", {"start": v(-60.55, 29.85) * mm, "end": v(-60.41, 29.8) * mm});
            skLineSegment(sketch, "E3440", {"start": v(-60.41, 29.8) * mm, "end": v(-60.27, 29.76) * mm});
            skLineSegment(sketch, "E3441", {"start": v(-60.27, 29.76) * mm, "end": v(-60.12, 29.73) * mm});
            skLineSegment(sketch, "E3442", {"start": v(-60.12, 29.73) * mm, "end": v(-59.97, 29.7) * mm});
            skLineSegment(sketch, "E3443", {"start": v(-59.97, 29.7) * mm, "end": v(-59.64, 29.69) * mm});
            skLineSegment(sketch, "E3444", {"start": v(-59.64, 29.69) * mm, "end": v(-59.31, 29.7) * mm});
            skLineSegment(sketch, "E3445", {"start": v(-59.31, 29.7) * mm, "end": v(-58.64, 29.72) * mm});
            skLineSegment(sketch, "E3446", {"start": v(-58.64, 29.72) * mm, "end": v(-58.33, 29.73) * mm});
            skLineSegment(sketch, "E3447", {"start": v(-58.33, 29.73) * mm, "end": v(-58.03, 29.72) * mm});
            skLineSegment(sketch, "E3448", {"start": v(-58.03, 29.72) * mm, "end": v(-57.8, 29.7) * mm});
            skLineSegment(sketch, "E3449", {"start": v(-57.8, 29.7) * mm, "end": v(-57.5, 29.7) * mm});
            skLineSegment(sketch, "E3450", {"start": v(-57.5, 29.7) * mm, "end": v(-57.15, 29.7) * mm});
            skLineSegment(sketch, "E3451", {"start": v(-57.15, 29.7) * mm, "end": v(-56.75, 29.7) * mm});
            skLineSegment(sketch, "E3452", {"start": v(-56.75, 29.7) * mm, "end": v(-56.33, 29.72) * mm});
            skLineSegment(sketch, "E3453", {"start": v(-56.33, 29.72) * mm, "end": v(-55.9, 29.75) * mm});
            skLineSegment(sketch, "E3454", {"start": v(-55.9, 29.75) * mm, "end": v(-55.45, 29.79) * mm});
            skLineSegment(sketch, "E3455", {"start": v(-55.45, 29.79) * mm, "end": v(-55.02, 29.83) * mm});
            skLineSegment(sketch, "E3456", {"start": v(-55.02, 29.83) * mm, "end": v(-54.52, 29.88) * mm});
            skLineSegment(sketch, "E3457", {"start": v(-54.52, 29.88) * mm, "end": v(-53.99, 29.92) * mm});
            skLineSegment(sketch, "E3458", {"start": v(-53.99, 29.92) * mm, "end": v(-53.45, 29.98) * mm});
            skLineSegment(sketch, "E3459", {"start": v(-53.45, 29.98) * mm, "end": v(-53.2, 30.03) * mm});
            skLineSegment(sketch, "E3460", {"start": v(-53.2, 30.03) * mm, "end": v(-52.96, 30.08) * mm});
            skLineSegment(sketch, "E3461", {"start": v(-52.96, 30.08) * mm, "end": v(-52.72, 30.15) * mm});
            skLineSegment(sketch, "E3462", {"start": v(-52.72, 30.15) * mm, "end": v(-52.47, 30.23) * mm});
            skLineSegment(sketch, "E3463", {"start": v(-52.47, 30.23) * mm, "end": v(-51.95, 30.44) * mm});
            skLineSegment(sketch, "E3464", {"start": v(-51.95, 30.44) * mm, "end": v(-51.44, 30.67) * mm});
            skLineSegment(sketch, "E3465", {"start": v(-51.44, 30.67) * mm, "end": v(-50.97, 30.87) * mm});
            skLineSegment(sketch, "E3466", {"start": v(60.88, 31.37) * mm, "end": v(60.86, 31.44) * mm});
            skLineSegment(sketch, "E3467", {"start": v(60.86, 31.44) * mm, "end": v(60.8, 31.58) * mm});
            skLineSegment(sketch, "E3468", {"start": v(60.8, 31.58) * mm, "end": v(60.6, 32.04) * mm});
            skLineSegment(sketch, "E3469", {"start": v(60.6, 32.04) * mm, "end": v(60.29, 32.7) * mm});
            skLineSegment(sketch, "E3470", {"start": v(60.29, 32.7) * mm, "end": v(59.9, 33.46) * mm});
            skLineSegment(sketch, "E3471", {"start": v(59.9, 33.46) * mm, "end": v(59.68, 33.93) * mm});
            skLineSegment(sketch, "E3472", {"start": v(59.68, 33.93) * mm, "end": v(59.44, 34.44) * mm});
            skLineSegment(sketch, "E3473", {"start": v(59.44, 34.44) * mm, "end": v(59.32, 34.7) * mm});
            skLineSegment(sketch, "E3474", {"start": v(59.32, 34.7) * mm, "end": v(59.2, 34.95) * mm});
            skLineSegment(sketch, "E3475", {"start": v(59.2, 34.95) * mm, "end": v(59.06, 35.18) * mm});
            skLineSegment(sketch, "E3476", {"start": v(59.06, 35.18) * mm, "end": v(58.93, 35.4) * mm});
            skLineSegment(sketch, "E3477", {"start": v(58.93, 35.4) * mm, "end": v(58.55, 35.92) * mm});
            skLineSegment(sketch, "E3478", {"start": v(58.55, 35.92) * mm, "end": v(58.13, 36.46) * mm});
            skLineSegment(sketch, "E3479", {"start": v(58.13, 36.46) * mm, "end": v(57.67, 37) * mm});
            skLineSegment(sketch, "E3480", {"start": v(57.67, 37) * mm, "end": v(57.2, 37.54) * mm});
            skLineSegment(sketch, "E3481", {"start": v(57.2, 37.54) * mm, "end": v(56.7, 38.06) * mm});
            skLineSegment(sketch, "E3482", {"start": v(56.7, 38.06) * mm, "end": v(56.19, 38.56) * mm});
            skLineSegment(sketch, "E3483", {"start": v(56.19, 38.56) * mm, "end": v(55.68, 39.02) * mm});
            skLineSegment(sketch, "E3484", {"start": v(55.68, 39.02) * mm, "end": v(55.44, 39.23) * mm});
            skLineSegment(sketch, "E3485", {"start": v(55.44, 39.23) * mm, "end": v(55.19, 39.43) * mm});
            skLineSegment(sketch, "E3486", {"start": v(55.19, 39.43) * mm, "end": v(54.76, 39.75) * mm});
            skLineSegment(sketch, "E3487", {"start": v(54.76, 39.75) * mm, "end": v(54.28, 40.07) * mm});
            skLineSegment(sketch, "E3488", {"start": v(54.28, 40.07) * mm, "end": v(53.77, 40.38) * mm});
            skLineSegment(sketch, "E3489", {"start": v(53.77, 40.38) * mm, "end": v(53.24, 40.68) * mm});
            skLineSegment(sketch, "E3490", {"start": v(53.24, 40.68) * mm, "end": v(52.7, 40.97) * mm});
            skLineSegment(sketch, "E3491", {"start": v(52.7, 40.97) * mm, "end": v(52.17, 41.23) * mm});
            skLineSegment(sketch, "E3492", {"start": v(52.17, 41.23) * mm, "end": v(51.65, 41.47) * mm});
            skLineSegment(sketch, "E3493", {"start": v(51.65, 41.47) * mm, "end": v(51.15, 41.69) * mm});
            skLineSegment(sketch, "E3494", {"start": v(51.15, 41.69) * mm, "end": v(50.6, 41.9) * mm});
            skLineSegment(sketch, "E3495", {"start": v(50.6, 41.9) * mm, "end": v(49.99, 42.1) * mm});
            skLineSegment(sketch, "E3496", {"start": v(49.99, 42.1) * mm, "end": v(49.36, 42.3) * mm});
            skLineSegment(sketch, "E3497", {"start": v(49.36, 42.3) * mm, "end": v(48.7, 42.47) * mm});
            skLineSegment(sketch, "E3498", {"start": v(48.7, 42.47) * mm, "end": v(48.06, 42.64) * mm});
            skLineSegment(sketch, "E3499", {"start": v(48.06, 42.64) * mm, "end": v(47.41, 42.78) * mm});
            skLineSegment(sketch, "E3500", {"start": v(47.41, 42.78) * mm, "end": v(46.79, 42.92) * mm});
            skLineSegment(sketch, "E3501", {"start": v(46.79, 42.92) * mm, "end": v(46.2, 43.03) * mm});
            skLineSegment(sketch, "E3502", {"start": v(46.2, 43.03) * mm, "end": v(45.51, 43.15) * mm});
            skLineSegment(sketch, "E3503", {"start": v(45.51, 43.15) * mm, "end": v(44.78, 43.26) * mm});
            skLineSegment(sketch, "E3504", {"start": v(44.78, 43.26) * mm, "end": v(44.02, 43.35) * mm});
            skLineSegment(sketch, "E3505", {"start": v(44.02, 43.35) * mm, "end": v(43.24, 43.44) * mm});
            skLineSegment(sketch, "E3506", {"start": v(43.24, 43.44) * mm, "end": v(42.46, 43.51) * mm});
            skLineSegment(sketch, "E3507", {"start": v(42.46, 43.51) * mm, "end": v(41.7, 43.57) * mm});
            skLineSegment(sketch, "E3508", {"start": v(41.7, 43.57) * mm, "end": v(40.96, 43.62) * mm});
            skLineSegment(sketch, "E3509", {"start": v(40.96, 43.62) * mm, "end": v(40.26, 43.65) * mm});
            skLineSegment(sketch, "E3510", {"start": v(40.26, 43.65) * mm, "end": v(39.98, 43.64) * mm});
            skLineSegment(sketch, "E3511", {"start": v(39.98, 43.64) * mm, "end": v(39.67, 43.63) * mm});
            skLineSegment(sketch, "E3512", {"start": v(39.67, 43.63) * mm, "end": v(39.08, 43.6) * mm});
            skLineSegment(sketch, "E3513", {"start": v(39.08, 43.6) * mm, "end": v(39.26, 43.13) * mm});
            skLineSegment(sketch, "E3514", {"start": v(39.26, 43.13) * mm, "end": v(39.33, 42.98) * mm});
            skLineSegment(sketch, "E3515", {"start": v(39.33, 42.98) * mm, "end": v(39.46, 42.75) * mm});
            skLineSegment(sketch, "E3516", {"start": v(39.46, 42.75) * mm, "end": v(39.89, 42.07) * mm});
            skLineSegment(sketch, "E3517", {"start": v(39.89, 42.07) * mm, "end": v(40.47, 41.19) * mm});
            skLineSegment(sketch, "E3518", {"start": v(40.47, 41.19) * mm, "end": v(41.14, 40.2) * mm});
            skLineSegment(sketch, "E3519", {"start": v(41.14, 40.2) * mm, "end": v(41.54, 39.59) * mm});
            skLineSegment(sketch, "E3520", {"start": v(41.54, 39.59) * mm, "end": v(41.97, 38.94) * mm});
            skLineSegment(sketch, "E3521", {"start": v(41.97, 38.94) * mm, "end": v(42.18, 38.6) * mm});
            skLineSegment(sketch, "E3522", {"start": v(42.18, 38.6) * mm, "end": v(42.4, 38.3) * mm});
            skLineSegment(sketch, "E3523", {"start": v(42.4, 38.3) * mm, "end": v(42.63, 38) * mm});
            skLineSegment(sketch, "E3524", {"start": v(42.63, 38) * mm, "end": v(42.85, 37.73) * mm});
            skLineSegment(sketch, "E3525", {"start": v(42.85, 37.73) * mm, "end": v(43.32, 37.2) * mm});
            skLineSegment(sketch, "E3526", {"start": v(43.32, 37.2) * mm, "end": v(43.84, 36.64) * mm});
            skLineSegment(sketch, "E3527", {"start": v(43.84, 36.64) * mm, "end": v(44.4, 36.08) * mm});
            skLineSegment(sketch, "E3528", {"start": v(44.4, 36.08) * mm, "end": v(44.97, 35.53) * mm});
            skLineSegment(sketch, "E3529", {"start": v(44.97, 35.53) * mm, "end": v(45.56, 34.99) * mm});
            skLineSegment(sketch, "E3530", {"start": v(45.56, 34.99) * mm, "end": v(46.15, 34.48) * mm});
            skLineSegment(sketch, "E3531", {"start": v(46.15, 34.48) * mm, "end": v(46.45, 34.23) * mm});
            skLineSegment(sketch, "E3532", {"start": v(46.45, 34.23) * mm, "end": v(46.74, 34) * mm});
            skLineSegment(sketch, "E3533", {"start": v(46.74, 34) * mm, "end": v(47.03, 33.79) * mm});
            skLineSegment(sketch, "E3534", {"start": v(47.03, 33.79) * mm, "end": v(47.32, 33.59) * mm});
            skLineSegment(sketch, "E3535", {"start": v(47.32, 33.59) * mm, "end": v(47.55, 33.44) * mm});
            skLineSegment(sketch, "E3536", {"start": v(47.55, 33.44) * mm, "end": v(47.8, 33.3) * mm});
            skLineSegment(sketch, "E3537", {"start": v(47.8, 33.3) * mm, "end": v(48.34, 33.04) * mm});
            skLineSegment(sketch, "E3538", {"start": v(48.34, 33.04) * mm, "end": v(48.9, 32.8) * mm});
            skLineSegment(sketch, "E3539", {"start": v(48.9, 32.8) * mm, "end": v(49.4, 32.56) * mm});
            skLineSegment(sketch, "E3540", {"start": v(49.4, 32.56) * mm, "end": v(49.85, 32.35) * mm});
            skLineSegment(sketch, "E3541", {"start": v(49.85, 32.35) * mm, "end": v(50.32, 32.14) * mm});
            skLineSegment(sketch, "E3542", {"start": v(50.32, 32.14) * mm, "end": v(50.82, 31.93) * mm});
            skLineSegment(sketch, "E3543", {"start": v(50.82, 31.93) * mm, "end": v(51.3, 31.74) * mm});
            skLineSegment(sketch, "E3544", {"start": v(51.3, 31.74) * mm, "end": v(51.78, 31.56) * mm});
            skLineSegment(sketch, "E3545", {"start": v(51.78, 31.56) * mm, "end": v(52.22, 31.4) * mm});
            skLineSegment(sketch, "E3546", {"start": v(52.22, 31.4) * mm, "end": v(52.62, 31.29) * mm});
            skLineSegment(sketch, "E3547", {"start": v(52.62, 31.29) * mm, "end": v(52.97, 31.2) * mm});
            skLineSegment(sketch, "E3548", {"start": v(52.97, 31.2) * mm, "end": v(53.32, 31.1) * mm});
            skLineSegment(sketch, "E3549", {"start": v(53.32, 31.1) * mm, "end": v(53.7, 31) * mm});
            skLineSegment(sketch, "E3550", {"start": v(53.7, 31) * mm, "end": v(54.09, 30.91) * mm});
            skLineSegment(sketch, "E3551", {"start": v(54.09, 30.91) * mm, "end": v(54.27, 30.88) * mm});
            skLineSegment(sketch, "E3552", {"start": v(54.27, 30.88) * mm, "end": v(54.45, 30.85) * mm});
            skLineSegment(sketch, "E3553", {"start": v(54.45, 30.85) * mm, "end": v(54.76, 30.83) * mm});
            skLineSegment(sketch, "E3554", {"start": v(54.76, 30.83) * mm, "end": v(55.08, 30.82) * mm});
            skLineSegment(sketch, "E3555", {"start": v(55.08, 30.82) * mm, "end": v(55.77, 30.83) * mm});
            skLineSegment(sketch, "E3556", {"start": v(55.77, 30.83) * mm, "end": v(56.45, 30.86) * mm});
            skLineSegment(sketch, "E3557", {"start": v(56.45, 30.86) * mm, "end": v(57.1, 30.88) * mm});
            skLineSegment(sketch, "E3558", {"start": v(57.1, 30.88) * mm, "end": v(58, 30.9) * mm});
            skLineSegment(sketch, "E3559", {"start": v(58, 30.9) * mm, "end": v(58.77, 30.93) * mm});
            skLineSegment(sketch, "E3560", {"start": v(58.77, 30.93) * mm, "end": v(59.43, 30.97) * mm});
            skLineSegment(sketch, "E3561", {"start": v(59.43, 30.97) * mm, "end": v(59.96, 31.02) * mm});
            skLineSegment(sketch, "E3562", {"start": v(59.96, 31.02) * mm, "end": v(60.18, 31.06) * mm});
            skLineSegment(sketch, "E3563", {"start": v(60.18, 31.06) * mm, "end": v(60.37, 31.09) * mm});
            skLineSegment(sketch, "E3564", {"start": v(60.37, 31.09) * mm, "end": v(60.53, 31.13) * mm});
            skLineSegment(sketch, "E3565", {"start": v(60.53, 31.13) * mm, "end": v(60.66, 31.17) * mm});
            skLineSegment(sketch, "E3566", {"start": v(60.66, 31.17) * mm, "end": v(60.76, 31.21) * mm});
            skLineSegment(sketch, "E3567", {"start": v(60.76, 31.21) * mm, "end": v(60.83, 31.26) * mm});
            skLineSegment(sketch, "E3568", {"start": v(60.83, 31.26) * mm, "end": v(60.87, 31.31) * mm});
            skLineSegment(sketch, "E3569", {"start": v(60.87, 31.31) * mm, "end": v(60.88, 31.37) * mm});
            skLineSegment(sketch, "E3570", {"start": v(-12.25, 36.25) * mm, "end": v(-12.05, 36.55) * mm});
            skLineSegment(sketch, "E3571", {"start": v(-12.05, 36.55) * mm, "end": v(-11.79, 36.9) * mm});
            skLineSegment(sketch, "E3572", {"start": v(-11.79, 36.9) * mm, "end": v(-11.5, 37.26) * mm});
            skLineSegment(sketch, "E3573", {"start": v(-11.5, 37.26) * mm, "end": v(-11.21, 37.58) * mm});
            skLineSegment(sketch, "E3574", {"start": v(-11.21, 37.58) * mm, "end": v(-11.1, 37.72) * mm});
            skLineSegment(sketch, "E3575", {"start": v(-11.1, 37.72) * mm, "end": v(-11, 37.87) * mm});
            skLineSegment(sketch, "E3576", {"start": v(-11, 37.87) * mm, "end": v(-10.76, 38.18) * mm});
            skLineSegment(sketch, "E3577", {"start": v(-10.76, 38.18) * mm, "end": v(-10.64, 38.34) * mm});
            skLineSegment(sketch, "E3578", {"start": v(-10.64, 38.34) * mm, "end": v(-10.5, 38.48) * mm});
            skLineSegment(sketch, "E3579", {"start": v(-10.5, 38.48) * mm, "end": v(-10.37, 38.6) * mm});
            skLineSegment(sketch, "E3580", {"start": v(-10.37, 38.6) * mm, "end": v(-10.3, 38.64) * mm});
            skLineSegment(sketch, "E3581", {"start": v(-10.3, 38.64) * mm, "end": v(-10.22, 38.68) * mm});
            skLineSegment(sketch, "E3582", {"start": v(-10.22, 38.68) * mm, "end": v(-10.08, 38.74) * mm});
            skLineSegment(sketch, "E3583", {"start": v(-10.08, 38.74) * mm, "end": v(-9.93, 38.78) * mm});
            skLineSegment(sketch, "E3584", {"start": v(-9.93, 38.78) * mm, "end": v(-9.77, 38.82) * mm});
            skLineSegment(sketch, "E3585", {"start": v(-9.77, 38.82) * mm, "end": v(-9.6, 38.85) * mm});
            skLineSegment(sketch, "E3586", {"start": v(-9.6, 38.85) * mm, "end": v(-9.43, 38.87) * mm});
            skLineSegment(sketch, "E3587", {"start": v(-9.43, 38.87) * mm, "end": v(-9.26, 38.88) * mm});
            skLineSegment(sketch, "E3588", {"start": v(-9.26, 38.88) * mm, "end": v(-8.9, 38.89) * mm});
            skLineSegment(sketch, "E3589", {"start": v(-8.9, 38.89) * mm, "end": v(-8.53, 38.87) * mm});
            skLineSegment(sketch, "E3590", {"start": v(-8.53, 38.87) * mm, "end": v(-8.18, 38.84) * mm});
            skLineSegment(sketch, "E3591", {"start": v(-8.18, 38.84) * mm, "end": v(-7.52, 38.76) * mm});
            skLineSegment(sketch, "E3592", {"start": v(-7.52, 38.76) * mm, "end": v(-7.43, 38.74) * mm});
            skLineSegment(sketch, "E3593", {"start": v(-7.43, 38.74) * mm, "end": v(-7.33, 38.7) * mm});
            skLineSegment(sketch, "E3594", {"start": v(-7.33, 38.7) * mm, "end": v(-7.24, 38.67) * mm});
            skLineSegment(sketch, "E3595", {"start": v(-7.24, 38.67) * mm, "end": v(-7.15, 38.62) * mm});
            skLineSegment(sketch, "E3596", {"start": v(-7.15, 38.62) * mm, "end": v(-6.97, 38.5) * mm});
            skLineSegment(sketch, "E3597", {"start": v(-6.97, 38.5) * mm, "end": v(-6.8, 38.35) * mm});
            skLineSegment(sketch, "E3598", {"start": v(-6.8, 38.35) * mm, "end": v(-6.47, 38.04) * mm});
            skLineSegment(sketch, "E3599", {"start": v(-6.47, 38.04) * mm, "end": v(-6.3, 37.9) * mm});
            skLineSegment(sketch, "E3600", {"start": v(-6.3, 37.9) * mm, "end": v(-6.15, 37.77) * mm});
            skLineSegment(sketch, "E3601", {"start": v(-6.15, 37.77) * mm, "end": v(-5.88, 37.57) * mm});
            skLineSegment(sketch, "E3602", {"start": v(-5.88, 37.57) * mm, "end": v(-5.62, 37.4) * mm});
            skLineSegment(sketch, "E3603", {"start": v(-5.62, 37.4) * mm, "end": v(-5.19, 37.15) * mm});
            skLineSegment(sketch, "E3604", {"start": v(-5.19, 37.15) * mm, "end": v(-4.88, 36.99) * mm});
            skLineSegment(sketch, "E3605", {"start": v(-4.88, 36.99) * mm, "end": v(-4.78, 36.95) * mm});
            skLineSegment(sketch, "E3606", {"start": v(-4.78, 36.95) * mm, "end": v(-4.72, 36.93) * mm});
            skLineSegment(sketch, "E3607", {"start": v(-4.72, 36.93) * mm, "end": v(-4.7, 36.94) * mm});
            skLineSegment(sketch, "E3608", {"start": v(-4.7, 36.94) * mm, "end": v(-4.67, 36.96) * mm});
            skLineSegment(sketch, "E3609", {"start": v(-4.67, 36.96) * mm, "end": v(-4.59, 37.04) * mm});
            skLineSegment(sketch, "E3610", {"start": v(-4.59, 37.04) * mm, "end": v(-4.47, 37.18) * mm});
            skLineSegment(sketch, "E3611", {"start": v(-4.47, 37.18) * mm, "end": v(-4.34, 37.35) * mm});
            skLineSegment(sketch, "E3612", {"start": v(-4.34, 37.35) * mm, "end": v(-4.19, 37.57) * mm});
            skLineSegment(sketch, "E3613", {"start": v(-4.19, 37.57) * mm, "end": v(-4.03, 37.83) * mm});
            skLineSegment(sketch, "E3614", {"start": v(-4.03, 37.83) * mm, "end": v(-3.86, 38.13) * mm});
            skLineSegment(sketch, "E3615", {"start": v(-3.86, 38.13) * mm, "end": v(-3.68, 38.45) * mm});
            skLineSegment(sketch, "E3616", {"start": v(-3.68, 38.45) * mm, "end": v(-3.58, 38.64) * mm});
            skLineSegment(sketch, "E3617", {"start": v(-3.58, 38.64) * mm, "end": v(-3.46, 38.83) * mm});
            skLineSegment(sketch, "E3618", {"start": v(-3.46, 38.83) * mm, "end": v(-3.2, 39.24) * mm});
            skLineSegment(sketch, "E3619", {"start": v(-3.2, 39.24) * mm, "end": v(-3.07, 39.44) * mm});
            skLineSegment(sketch, "E3620", {"start": v(-3.07, 39.44) * mm, "end": v(-2.96, 39.65) * mm});
            skLineSegment(sketch, "E3621", {"start": v(-2.96, 39.65) * mm, "end": v(-2.86, 39.85) * mm});
            skLineSegment(sketch, "E3622", {"start": v(-2.86, 39.85) * mm, "end": v(-2.8, 40.05) * mm});
            skLineSegment(sketch, "E3623", {"start": v(-2.8, 40.05) * mm, "end": v(-2.74, 40.36) * mm});
            skLineSegment(sketch, "E3624", {"start": v(-2.74, 40.36) * mm, "end": v(-2.69, 40.68) * mm});
            skLineSegment(sketch, "E3625", {"start": v(-2.69, 40.68) * mm, "end": v(-2.65, 41.02) * mm});
            skLineSegment(sketch, "E3626", {"start": v(-2.65, 41.02) * mm, "end": v(-2.63, 41.37) * mm});
            skLineSegment(sketch, "E3627", {"start": v(-2.63, 41.37) * mm, "end": v(-2.63, 41.72) * mm});
            skLineSegment(sketch, "E3628", {"start": v(-2.63, 41.72) * mm, "end": v(-2.66, 42.05) * mm});
            skLineSegment(sketch, "E3629", {"start": v(-2.66, 42.05) * mm, "end": v(-2.69, 42.22) * mm});
            skLineSegment(sketch, "E3630", {"start": v(-2.69, 42.22) * mm, "end": v(-2.72, 42.37) * mm});
            skLineSegment(sketch, "E3631", {"start": v(-2.72, 42.37) * mm, "end": v(-2.75, 42.52) * mm});
            skLineSegment(sketch, "E3632", {"start": v(-2.75, 42.52) * mm, "end": v(-2.8, 42.67) * mm});
            skLineSegment(sketch, "E3633", {"start": v(-2.8, 42.67) * mm, "end": v(-2.86, 42.81) * mm});
            skLineSegment(sketch, "E3634", {"start": v(-2.86, 42.81) * mm, "end": v(-2.94, 42.95) * mm});
            skLineSegment(sketch, "E3635", {"start": v(-2.94, 42.95) * mm, "end": v(-3.02, 43.1) * mm});
            skLineSegment(sketch, "E3636", {"start": v(-3.02, 43.1) * mm, "end": v(-3.12, 43.23) * mm});
            skLineSegment(sketch, "E3637", {"start": v(-3.12, 43.23) * mm, "end": v(-3.35, 43.5) * mm});
            skLineSegment(sketch, "E3638", {"start": v(-3.35, 43.5) * mm, "end": v(-3.6, 43.78) * mm});
            skLineSegment(sketch, "E3639", {"start": v(-3.6, 43.78) * mm, "end": v(-4.11, 44.29) * mm});
            skLineSegment(sketch, "E3640", {"start": v(-4.11, 44.29) * mm, "end": v(-4.36, 44.54) * mm});
            skLineSegment(sketch, "E3641", {"start": v(-4.36, 44.54) * mm, "end": v(-4.58, 44.78) * mm});
            skLineSegment(sketch, "E3642", {"start": v(-4.58, 44.78) * mm, "end": v(-5.04, 44.74) * mm});
            skLineSegment(sketch, "E3643", {"start": v(-5.04, 44.74) * mm, "end": v(-5.54, 44.7) * mm});
            skLineSegment(sketch, "E3644", {"start": v(-5.54, 44.7) * mm, "end": v(-6.57, 44.65) * mm});
            skLineSegment(sketch, "E3645", {"start": v(-6.57, 44.65) * mm, "end": v(-7.1, 44.6) * mm});
            skLineSegment(sketch, "E3646", {"start": v(-7.1, 44.6) * mm, "end": v(-7.6, 44.55) * mm});
            skLineSegment(sketch, "E3647", {"start": v(-7.6, 44.55) * mm, "end": v(-7.85, 44.51) * mm});
            skLineSegment(sketch, "E3648", {"start": v(-7.85, 44.51) * mm, "end": v(-8.09, 44.47) * mm});
            skLineSegment(sketch, "E3649", {"start": v(-8.09, 44.47) * mm, "end": v(-8.32, 44.42) * mm});
            skLineSegment(sketch, "E3650", {"start": v(-8.32, 44.42) * mm, "end": v(-8.54, 44.36) * mm});
            skLineSegment(sketch, "E3651", {"start": v(-8.54, 44.36) * mm, "end": v(-8.9, 44.25) * mm});
            skLineSegment(sketch, "E3652", {"start": v(-8.9, 44.25) * mm, "end": v(-9.26, 44.13) * mm});
            skLineSegment(sketch, "E3653", {"start": v(-9.26, 44.13) * mm, "end": v(-9.65, 43.98) * mm});
            skLineSegment(sketch, "E3654", {"start": v(-9.65, 43.98) * mm, "end": v(-10.03, 43.8) * mm});
            skLineSegment(sketch, "E3655", {"start": v(-10.03, 43.8) * mm, "end": v(-10.4, 43.62) * mm});
            skLineSegment(sketch, "E3656", {"start": v(-10.4, 43.62) * mm, "end": v(-10.76, 43.43) * mm});
            skLineSegment(sketch, "E3657", {"start": v(-10.76, 43.43) * mm, "end": v(-11.08, 43.21) * mm});
            skLineSegment(sketch, "E3658", {"start": v(-11.08, 43.21) * mm, "end": v(-11.23, 43.1) * mm});
            skLineSegment(sketch, "E3659", {"start": v(-11.23, 43.1) * mm, "end": v(-11.38, 43) * mm});
            skLineSegment(sketch, "E3660", {"start": v(-11.38, 43) * mm, "end": v(-11.58, 42.8) * mm});
            skLineSegment(sketch, "E3661", {"start": v(-11.58, 42.8) * mm, "end": v(-11.78, 42.6) * mm});
            skLineSegment(sketch, "E3662", {"start": v(-11.78, 42.6) * mm, "end": v(-11.97, 42.36) * mm});
            skLineSegment(sketch, "E3663", {"start": v(-11.97, 42.36) * mm, "end": v(-12.16, 42.1) * mm});
            skLineSegment(sketch, "E3664", {"start": v(-12.16, 42.1) * mm, "end": v(-12.33, 41.85) * mm});
            skLineSegment(sketch, "E3665", {"start": v(-12.33, 41.85) * mm, "end": v(-12.49, 41.58) * mm});
            skLineSegment(sketch, "E3666", {"start": v(-12.49, 41.58) * mm, "end": v(-12.63, 41.32) * mm});
            skLineSegment(sketch, "E3667", {"start": v(-12.63, 41.32) * mm, "end": v(-12.74, 41.07) * mm});
            skLineSegment(sketch, "E3668", {"start": v(-12.74, 41.07) * mm, "end": v(-12.83, 40.82) * mm});
            skLineSegment(sketch, "E3669", {"start": v(-12.83, 40.82) * mm, "end": v(-12.9, 40.54) * mm});
            skLineSegment(sketch, "E3670", {"start": v(-12.9, 40.54) * mm, "end": v(-12.97, 40.25) * mm});
            skLineSegment(sketch, "E3671", {"start": v(-12.97, 40.25) * mm, "end": v(-13.02, 39.95) * mm});
            skLineSegment(sketch, "E3672", {"start": v(-13.02, 39.95) * mm, "end": v(-13.06, 39.65) * mm});
            skLineSegment(sketch, "E3673", {"start": v(-13.06, 39.65) * mm, "end": v(-13.09, 39.35) * mm});
            skLineSegment(sketch, "E3674", {"start": v(-13.09, 39.35) * mm, "end": v(-13.1, 39.06) * mm});
            skLineSegment(sketch, "E3675", {"start": v(-13.1, 39.06) * mm, "end": v(-13.11, 38.8) * mm});
            skLineSegment(sketch, "E3676", {"start": v(-13.11, 38.8) * mm, "end": v(-13.1, 38.42) * mm});
            skLineSegment(sketch, "E3677", {"start": v(-13.1, 38.42) * mm, "end": v(-13.06, 38.03) * mm});
            skLineSegment(sketch, "E3678", {"start": v(-13.06, 38.03) * mm, "end": v(-13, 37.62) * mm});
            skLineSegment(sketch, "E3679", {"start": v(-13, 37.62) * mm, "end": v(-12.92, 37.2) * mm});
            skLineSegment(sketch, "E3680", {"start": v(-12.92, 37.2) * mm, "end": v(-12.76, 36.38) * mm});
            skLineSegment(sketch, "E3681", {"start": v(-12.76, 36.38) * mm, "end": v(-12.69, 36) * mm});
            skLineSegment(sketch, "E3682", {"start": v(-12.69, 36) * mm, "end": v(-12.62, 35.62) * mm});
            skLineSegment(sketch, "E3683", {"start": v(-12.62, 35.62) * mm, "end": v(-12.25, 36.25) * mm});
            skLineSegment(sketch, "E3684", {"start": v(-54.16, 41.17) * mm, "end": v(-53.88, 41.48) * mm});
            skLineSegment(sketch, "E3685", {"start": v(-53.88, 41.48) * mm, "end": v(-53.6, 41.81) * mm});
            skLineSegment(sketch, "E3686", {"start": v(-53.6, 41.81) * mm, "end": v(-53.34, 42.15) * mm});
            skLineSegment(sketch, "E3687", {"start": v(-53.34, 42.15) * mm, "end": v(-53.1, 42.5) * mm});
            skLineSegment(sketch, "E3688", {"start": v(-53.1, 42.5) * mm, "end": v(-52.85, 42.85) * mm});
            skLineSegment(sketch, "E3689", {"start": v(-52.85, 42.85) * mm, "end": v(-52.62, 43.22) * mm});
            skLineSegment(sketch, "E3690", {"start": v(-52.62, 43.22) * mm, "end": v(-52.4, 43.6) * mm});
            skLineSegment(sketch, "E3691", {"start": v(-52.4, 43.6) * mm, "end": v(-52.18, 43.98) * mm});
            skLineSegment(sketch, "E3692", {"start": v(-52.18, 43.98) * mm, "end": v(-51.98, 44.38) * mm});
            skLineSegment(sketch, "E3693", {"start": v(-51.98, 44.38) * mm, "end": v(-51.8, 44.8) * mm});
            skLineSegment(sketch, "E3694", {"start": v(-51.8, 44.8) * mm, "end": v(-51.6, 45.22) * mm});
            skLineSegment(sketch, "E3695", {"start": v(-51.6, 45.22) * mm, "end": v(-51.43, 45.65) * mm});
            skLineSegment(sketch, "E3696", {"start": v(-51.43, 45.65) * mm, "end": v(-51.27, 46.1) * mm});
            skLineSegment(sketch, "E3697", {"start": v(-51.27, 46.1) * mm, "end": v(-51.11, 46.56) * mm});
            skLineSegment(sketch, "E3698", {"start": v(-51.11, 46.56) * mm, "end": v(-50.96, 47.03) * mm});
            skLineSegment(sketch, "E3699", {"start": v(-50.96, 47.03) * mm, "end": v(-50.82, 47.52) * mm});
            skLineSegment(sketch, "E3700", {"start": v(-50.82, 47.52) * mm, "end": v(-50.77, 47.75) * mm});
            skLineSegment(sketch, "E3701", {"start": v(-50.77, 47.75) * mm, "end": v(-50.73, 48) * mm});
            skLineSegment(sketch, "E3702", {"start": v(-50.73, 48) * mm, "end": v(-50.7, 48.52) * mm});
            skLineSegment(sketch, "E3703", {"start": v(-50.7, 48.52) * mm, "end": v(-50.66, 49.05) * mm});
            skLineSegment(sketch, "E3704", {"start": v(-50.66, 49.05) * mm, "end": v(-50.64, 49.3) * mm});
            skLineSegment(sketch, "E3705", {"start": v(-50.64, 49.3) * mm, "end": v(-50.6, 49.54) * mm});
            skLineSegment(sketch, "E3706", {"start": v(-50.6, 49.54) * mm, "end": v(-50.52, 50.03) * mm});
            skLineSegment(sketch, "E3707", {"start": v(-50.52, 50.03) * mm, "end": v(-50.4, 50.56) * mm});
            skLineSegment(sketch, "E3708", {"start": v(-50.4, 50.56) * mm, "end": v(-50.14, 51.7) * mm});
            skLineSegment(sketch, "E3709", {"start": v(-50.14, 51.7) * mm, "end": v(-49.84, 52.91) * mm});
            skLineSegment(sketch, "E3710", {"start": v(-49.84, 52.91) * mm, "end": v(-49.7, 53.52) * mm});
            skLineSegment(sketch, "E3711", {"start": v(-49.7, 53.52) * mm, "end": v(-49.58, 54.13) * mm});
            skLineSegment(sketch, "E3712", {"start": v(-49.58, 54.13) * mm, "end": v(-49.48, 54.72) * mm});
            skLineSegment(sketch, "E3713", {"start": v(-49.48, 54.72) * mm, "end": v(-49.4, 55.3) * mm});
            skLineSegment(sketch, "E3714", {"start": v(-49.4, 55.3) * mm, "end": v(-49.38, 55.57) * mm});
            skLineSegment(sketch, "E3715", {"start": v(-49.38, 55.57) * mm, "end": v(-49.36, 55.84) * mm});
            skLineSegment(sketch, "E3716", {"start": v(-49.36, 55.84) * mm, "end": v(-49.36, 56.1) * mm});
            skLineSegment(sketch, "E3717", {"start": v(-49.36, 56.1) * mm, "end": v(-49.36, 56.35) * mm});
            skLineSegment(sketch, "E3718", {"start": v(-49.36, 56.35) * mm, "end": v(-49.38, 56.6) * mm});
            skLineSegment(sketch, "E3719", {"start": v(-49.38, 56.6) * mm, "end": v(-49.4, 56.82) * mm});
            skLineSegment(sketch, "E3720", {"start": v(-49.4, 56.82) * mm, "end": v(-49.45, 57.04) * mm});
            skLineSegment(sketch, "E3721", {"start": v(-49.45, 57.04) * mm, "end": v(-49.5, 57.24) * mm});
            skLineSegment(sketch, "E3722", {"start": v(-49.5, 57.24) * mm, "end": v(-49.58, 57.43) * mm});
            skLineSegment(sketch, "E3723", {"start": v(-49.58, 57.43) * mm, "end": v(-49.67, 57.6) * mm});
            skLineSegment(sketch, "E3724", {"start": v(-49.67, 57.6) * mm, "end": v(-49.77, 57.76) * mm});
            skLineSegment(sketch, "E3725", {"start": v(-49.77, 57.76) * mm, "end": v(-49.9, 57.9) * mm});
            skLineSegment(sketch, "E3726", {"start": v(-49.9, 57.9) * mm, "end": v(-49.94, 57.94) * mm});
            skLineSegment(sketch, "E3727", {"start": v(-49.94, 57.94) * mm, "end": v(-50, 57.97) * mm});
            skLineSegment(sketch, "E3728", {"start": v(-50, 57.97) * mm, "end": v(-50.06, 58) * mm});
            skLineSegment(sketch, "E3729", {"start": v(-50.06, 58) * mm, "end": v(-50.13, 58.01) * mm});
            skLineSegment(sketch, "E3730", {"start": v(-50.13, 58.01) * mm, "end": v(-50.28, 58.03) * mm});
            skLineSegment(sketch, "E3731", {"start": v(-50.28, 58.03) * mm, "end": v(-50.44, 58.03) * mm});
            skLineSegment(sketch, "E3732", {"start": v(-50.44, 58.03) * mm, "end": v(-50.6, 58) * mm});
            skLineSegment(sketch, "E3733", {"start": v(-50.6, 58) * mm, "end": v(-50.77, 57.98) * mm});
            skLineSegment(sketch, "E3734", {"start": v(-50.77, 57.98) * mm, "end": v(-51.05, 57.9) * mm});
            skLineSegment(sketch, "E3735", {"start": v(-51.05, 57.9) * mm, "end": v(-51.16, 57.86) * mm});
            skLineSegment(sketch, "E3736", {"start": v(-51.16, 57.86) * mm, "end": v(-51.26, 57.8) * mm});
            skLineSegment(sketch, "E3737", {"start": v(-51.26, 57.8) * mm, "end": v(-51.47, 57.69) * mm});
            skLineSegment(sketch, "E3738", {"start": v(-51.47, 57.69) * mm, "end": v(-51.67, 57.54) * mm});
            skLineSegment(sketch, "E3739", {"start": v(-51.67, 57.54) * mm, "end": v(-51.87, 57.38) * mm});
            skLineSegment(sketch, "E3740", {"start": v(-51.87, 57.38) * mm, "end": v(-52.26, 57.04) * mm});
            skLineSegment(sketch, "E3741", {"start": v(-52.26, 57.04) * mm, "end": v(-52.45, 56.88) * mm});
            skLineSegment(sketch, "E3742", {"start": v(-52.45, 56.88) * mm, "end": v(-52.63, 56.74) * mm});
            skLineSegment(sketch, "E3743", {"start": v(-52.63, 56.74) * mm, "end": v(-52.97, 56.48) * mm});
            skLineSegment(sketch, "E3744", {"start": v(-52.97, 56.48) * mm, "end": v(-53.33, 56.2) * mm});
            skLineSegment(sketch, "E3745", {"start": v(-53.33, 56.2) * mm, "end": v(-53.7, 55.88) * mm});
            skLineSegment(sketch, "E3746", {"start": v(-53.7, 55.88) * mm, "end": v(-54.08, 55.55) * mm});
            skLineSegment(sketch, "E3747", {"start": v(-54.08, 55.55) * mm, "end": v(-54.44, 55.22) * mm});
            skLineSegment(sketch, "E3748", {"start": v(-54.44, 55.22) * mm, "end": v(-54.78, 54.9) * mm});
            skLineSegment(sketch, "E3749", {"start": v(-54.78, 54.9) * mm, "end": v(-55.1, 54.59) * mm});
            skLineSegment(sketch, "E3750", {"start": v(-55.1, 54.59) * mm, "end": v(-55.35, 54.3) * mm});
            skLineSegment(sketch, "E3751", {"start": v(-55.35, 54.3) * mm, "end": v(-55.64, 54) * mm});
            skLineSegment(sketch, "E3752", {"start": v(-55.64, 54) * mm, "end": v(-55.95, 53.69) * mm});
            skLineSegment(sketch, "E3753", {"start": v(-55.95, 53.69) * mm, "end": v(-56.26, 53.36) * mm});
            skLineSegment(sketch, "E3754", {"start": v(-56.26, 53.36) * mm, "end": v(-56.4, 53.2) * mm});
            skLineSegment(sketch, "E3755", {"start": v(-56.4, 53.2) * mm, "end": v(-56.5, 53.03) * mm});
            skLineSegment(sketch, "E3756", {"start": v(-56.5, 53.03) * mm, "end": v(-56.85, 52.5) * mm});
            skLineSegment(sketch, "E3757", {"start": v(-56.85, 52.5) * mm, "end": v(-57.2, 51.92) * mm});
            skLineSegment(sketch, "E3758", {"start": v(-57.2, 51.92) * mm, "end": v(-57.53, 51.3) * mm});
            skLineSegment(sketch, "E3759", {"start": v(-57.53, 51.3) * mm, "end": v(-57.86, 50.67) * mm});
            skLineSegment(sketch, "E3760", {"start": v(-57.86, 50.67) * mm, "end": v(-58.16, 50.03) * mm});
            skLineSegment(sketch, "E3761", {"start": v(-58.16, 50.03) * mm, "end": v(-58.44, 49.39) * mm});
            skLineSegment(sketch, "E3762", {"start": v(-58.44, 49.39) * mm, "end": v(-58.68, 48.76) * mm});
            skLineSegment(sketch, "E3763", {"start": v(-58.68, 48.76) * mm, "end": v(-58.88, 48.16) * mm});
            skLineSegment(sketch, "E3764", {"start": v(-58.88, 48.16) * mm, "end": v(-59.02, 47.67) * mm});
            skLineSegment(sketch, "E3765", {"start": v(-59.02, 47.67) * mm, "end": v(-59.15, 47.15) * mm});
            skLineSegment(sketch, "E3766", {"start": v(-59.15, 47.15) * mm, "end": v(-59.27, 46.6) * mm});
            skLineSegment(sketch, "E3767", {"start": v(-59.27, 46.6) * mm, "end": v(-59.36, 46.03) * mm});
            skLineSegment(sketch, "E3768", {"start": v(-59.36, 46.03) * mm, "end": v(-59.44, 45.46) * mm});
            skLineSegment(sketch, "E3769", {"start": v(-59.44, 45.46) * mm, "end": v(-59.5, 44.9) * mm});
            skLineSegment(sketch, "E3770", {"start": v(-59.5, 44.9) * mm, "end": v(-59.53, 44.36) * mm});
            skLineSegment(sketch, "E3771", {"start": v(-59.53, 44.36) * mm, "end": v(-59.55, 43.85) * mm});
            skLineSegment(sketch, "E3772", {"start": v(-59.55, 43.85) * mm, "end": v(-59.54, 43.64) * mm});
            skLineSegment(sketch, "E3773", {"start": v(-59.54, 43.64) * mm, "end": v(-59.51, 43.42) * mm});
            skLineSegment(sketch, "E3774", {"start": v(-59.51, 43.42) * mm, "end": v(-59.43, 42.95) * mm});
            skLineSegment(sketch, "E3775", {"start": v(-59.43, 42.95) * mm, "end": v(-59.33, 42.48) * mm});
            skLineSegment(sketch, "E3776", {"start": v(-59.33, 42.48) * mm, "end": v(-59.25, 42.05) * mm});
            skLineSegment(sketch, "E3777", {"start": v(-59.25, 42.05) * mm, "end": v(-59.1, 41.18) * mm});
            skLineSegment(sketch, "E3778", {"start": v(-59.1, 41.18) * mm, "end": v(-58.96, 40.44) * mm});
            skLineSegment(sketch, "E3779", {"start": v(-58.96, 40.44) * mm, "end": v(-58.83, 39.82) * mm});
            skLineSegment(sketch, "E3780", {"start": v(-58.83, 39.82) * mm, "end": v(-58.7, 39.31) * mm});
            skLineSegment(sketch, "E3781", {"start": v(-58.7, 39.31) * mm, "end": v(-58.6, 38.92) * mm});
            skLineSegment(sketch, "E3782", {"start": v(-58.6, 38.92) * mm, "end": v(-58.54, 38.77) * mm});
            skLineSegment(sketch, "E3783", {"start": v(-58.54, 38.77) * mm, "end": v(-58.48, 38.65) * mm});
            skLineSegment(sketch, "E3784", {"start": v(-58.48, 38.65) * mm, "end": v(-58.43, 38.55) * mm});
            skLineSegment(sketch, "E3785", {"start": v(-58.43, 38.55) * mm, "end": v(-58.38, 38.48) * mm});
            skLineSegment(sketch, "E3786", {"start": v(-58.38, 38.48) * mm, "end": v(-58.33, 38.44) * mm});
            skLineSegment(sketch, "E3787", {"start": v(-58.33, 38.44) * mm, "end": v(-58.28, 38.43) * mm});
            skLineSegment(sketch, "E3788", {"start": v(-58.28, 38.43) * mm, "end": v(-58.2, 38.44) * mm});
            skLineSegment(sketch, "E3789", {"start": v(-58.2, 38.44) * mm, "end": v(-58.1, 38.48) * mm});
            skLineSegment(sketch, "E3790", {"start": v(-58.1, 38.48) * mm, "end": v(-57.74, 38.63) * mm});
            skLineSegment(sketch, "E3791", {"start": v(-57.74, 38.63) * mm, "end": v(-57.27, 38.84) * mm});
            skLineSegment(sketch, "E3792", {"start": v(-57.27, 38.84) * mm, "end": v(-56.75, 39.1) * mm});
            skLineSegment(sketch, "E3793", {"start": v(-56.75, 39.1) * mm, "end": v(-56.42, 39.26) * mm});
            skLineSegment(sketch, "E3794", {"start": v(-56.42, 39.26) * mm, "end": v(-56.07, 39.42) * mm});
            skLineSegment(sketch, "E3795", {"start": v(-56.07, 39.42) * mm, "end": v(-55.73, 39.6) * mm});
            skLineSegment(sketch, "E3796", {"start": v(-55.73, 39.6) * mm, "end": v(-55.57, 39.68) * mm});
            skLineSegment(sketch, "E3797", {"start": v(-55.57, 39.68) * mm, "end": v(-55.43, 39.78) * mm});
            skLineSegment(sketch, "E3798", {"start": v(-55.43, 39.78) * mm, "end": v(-55.26, 39.92) * mm});
            skLineSegment(sketch, "E3799", {"start": v(-55.26, 39.92) * mm, "end": v(-55.1, 40.08) * mm});
            skLineSegment(sketch, "E3800", {"start": v(-55.1, 40.08) * mm, "end": v(-54.77, 40.45) * mm});
            skLineSegment(sketch, "E3801", {"start": v(-54.77, 40.45) * mm, "end": v(-54.46, 40.82) * mm});
            skLineSegment(sketch, "E3802", {"start": v(-54.46, 40.82) * mm, "end": v(-54.16, 41.17) * mm});
            skLineSegment(sketch, "E3803", {"start": v(58.8, 42.32) * mm, "end": v(58.86, 42.86) * mm});
            skLineSegment(sketch, "E3804", {"start": v(58.86, 42.86) * mm, "end": v(58.93, 43.44) * mm});
            skLineSegment(sketch, "E3805", {"start": v(58.93, 43.44) * mm, "end": v(58.96, 43.73) * mm});
            skLineSegment(sketch, "E3806", {"start": v(58.96, 43.73) * mm, "end": v(58.99, 44.02) * mm});
            skLineSegment(sketch, "E3807", {"start": v(58.99, 44.02) * mm, "end": v(59, 44.3) * mm});
            skLineSegment(sketch, "E3808", {"start": v(59, 44.3) * mm, "end": v(58.99, 44.56) * mm});
            skLineSegment(sketch, "E3809", {"start": v(58.99, 44.56) * mm, "end": v(58.97, 44.76) * mm});
            skLineSegment(sketch, "E3810", {"start": v(58.97, 44.76) * mm, "end": v(58.93, 44.96) * mm});
            skLineSegment(sketch, "E3811", {"start": v(58.93, 44.96) * mm, "end": v(58.84, 45.4) * mm});
            skLineSegment(sketch, "E3812", {"start": v(58.84, 45.4) * mm, "end": v(58.73, 45.83) * mm});
            skLineSegment(sketch, "E3813", {"start": v(58.73, 45.83) * mm, "end": v(58.63, 46.23) * mm});
            skLineSegment(sketch, "E3814", {"start": v(58.63, 46.23) * mm, "end": v(58.55, 46.6) * mm});
            skLineSegment(sketch, "E3815", {"start": v(58.55, 46.6) * mm, "end": v(58.44, 47.02) * mm});
            skLineSegment(sketch, "E3816", {"start": v(58.44, 47.02) * mm, "end": v(58.18, 47.93) * mm});
            skLineSegment(sketch, "E3817", {"start": v(58.18, 47.93) * mm, "end": v(57.89, 48.85) * mm});
            skLineSegment(sketch, "E3818", {"start": v(57.89, 48.85) * mm, "end": v(57.74, 49.29) * mm});
            skLineSegment(sketch, "E3819", {"start": v(57.74, 49.29) * mm, "end": v(57.6, 49.68) * mm});
            skLineSegment(sketch, "E3820", {"start": v(57.6, 49.68) * mm, "end": v(57.45, 50.11) * mm});
            skLineSegment(sketch, "E3821", {"start": v(57.45, 50.11) * mm, "end": v(57.29, 50.58) * mm});
            skLineSegment(sketch, "E3822", {"start": v(57.29, 50.58) * mm, "end": v(57.2, 50.82) * mm});
            skLineSegment(sketch, "E3823", {"start": v(57.2, 50.82) * mm, "end": v(57.12, 51.05) * mm});
            skLineSegment(sketch, "E3824", {"start": v(57.12, 51.05) * mm, "end": v(57.02, 51.26) * mm});
            skLineSegment(sketch, "E3825", {"start": v(57.02, 51.26) * mm, "end": v(56.92, 51.46) * mm});
            skLineSegment(sketch, "E3826", {"start": v(56.92, 51.46) * mm, "end": v(56.76, 51.73) * mm});
            skLineSegment(sketch, "E3827", {"start": v(56.76, 51.73) * mm, "end": v(56.58, 52.01) * mm});
            skLineSegment(sketch, "E3828", {"start": v(56.58, 52.01) * mm, "end": v(56.2, 52.58) * mm});
            skLineSegment(sketch, "E3829", {"start": v(56.2, 52.58) * mm, "end": v(55.77, 53.15) * mm});
            skLineSegment(sketch, "E3830", {"start": v(55.77, 53.15) * mm, "end": v(55.32, 53.72) * mm});
            skLineSegment(sketch, "E3831", {"start": v(55.32, 53.72) * mm, "end": v(54.85, 54.27) * mm});
            skLineSegment(sketch, "E3832", {"start": v(54.85, 54.27) * mm, "end": v(54.37, 54.8) * mm});
            skLineSegment(sketch, "E3833", {"start": v(54.37, 54.8) * mm, "end": v(53.9, 55.3) * mm});
            skLineSegment(sketch, "E3834", {"start": v(53.9, 55.3) * mm, "end": v(53.43, 55.74) * mm});
            skLineSegment(sketch, "E3835", {"start": v(53.43, 55.74) * mm, "end": v(53.24, 55.9) * mm});
            skLineSegment(sketch, "E3836", {"start": v(53.24, 55.9) * mm, "end": v(53.03, 56.07) * mm});
            skLineSegment(sketch, "E3837", {"start": v(53.03, 56.07) * mm, "end": v(52.57, 56.4) * mm});
            skLineSegment(sketch, "E3838", {"start": v(52.57, 56.4) * mm, "end": v(52.1, 56.7) * mm});
            skLineSegment(sketch, "E3839", {"start": v(52.1, 56.7) * mm, "end": v(51.66, 56.98) * mm});
            skLineSegment(sketch, "E3840", {"start": v(51.66, 56.98) * mm, "end": v(51.3, 57.23) * mm});
            skLineSegment(sketch, "E3841", {"start": v(51.3, 57.23) * mm, "end": v(50.93, 57.47) * mm});
            skLineSegment(sketch, "E3842", {"start": v(50.93, 57.47) * mm, "end": v(50.58, 57.68) * mm});
            skLineSegment(sketch, "E3843", {"start": v(50.58, 57.68) * mm, "end": v(50.26, 57.86) * mm});
            skLineSegment(sketch, "E3844", {"start": v(50.26, 57.86) * mm, "end": v(49.97, 58.01) * mm});
            skLineSegment(sketch, "E3845", {"start": v(49.97, 58.01) * mm, "end": v(49.73, 58.13) * mm});
            skLineSegment(sketch, "E3846", {"start": v(49.73, 58.13) * mm, "end": v(49.53, 58.2) * mm});
            skLineSegment(sketch, "E3847", {"start": v(49.53, 58.2) * mm, "end": v(49.46, 58.22) * mm});
            skLineSegment(sketch, "E3848", {"start": v(49.46, 58.22) * mm, "end": v(49.4, 58.23) * mm});
            skLineSegment(sketch, "E3849", {"start": v(49.4, 58.23) * mm, "end": v(48.91, 58.23) * mm});
            skLineSegment(sketch, "E3850", {"start": v(48.91, 58.23) * mm, "end": v(49, 56.8) * mm});
            skLineSegment(sketch, "E3851", {"start": v(49, 56.8) * mm, "end": v(49.08, 55.26) * mm});
            skLineSegment(sketch, "E3852", {"start": v(49.08, 55.26) * mm, "end": v(49.12, 54.48) * mm});
            skLineSegment(sketch, "E3853", {"start": v(49.12, 54.48) * mm, "end": v(49.19, 53.72) * mm});
            skLineSegment(sketch, "E3854", {"start": v(49.19, 53.72) * mm, "end": v(49.26, 53) * mm});
            skLineSegment(sketch, "E3855", {"start": v(49.26, 53) * mm, "end": v(49.3, 52.64) * mm});
            skLineSegment(sketch, "E3856", {"start": v(49.3, 52.64) * mm, "end": v(49.36, 52.3) * mm});
            skLineSegment(sketch, "E3857", {"start": v(49.36, 52.3) * mm, "end": v(49.46, 51.72) * mm});
            skLineSegment(sketch, "E3858", {"start": v(49.46, 51.72) * mm, "end": v(49.58, 51.1) * mm});
            skLineSegment(sketch, "E3859", {"start": v(49.58, 51.1) * mm, "end": v(49.72, 50.47) * mm});
            skLineSegment(sketch, "E3860", {"start": v(49.72, 50.47) * mm, "end": v(49.88, 49.83) * mm});
            skLineSegment(sketch, "E3861", {"start": v(49.88, 49.83) * mm, "end": v(50.04, 49.19) * mm});
            skLineSegment(sketch, "E3862", {"start": v(50.04, 49.19) * mm, "end": v(50.22, 48.56) * mm});
            skLineSegment(sketch, "E3863", {"start": v(50.22, 48.56) * mm, "end": v(50.41, 47.96) * mm});
            skLineSegment(sketch, "E3864", {"start": v(50.41, 47.96) * mm, "end": v(50.61, 47.4) * mm});
            skLineSegment(sketch, "E3865", {"start": v(50.61, 47.4) * mm, "end": v(50.8, 46.93) * mm});
            skLineSegment(sketch, "E3866", {"start": v(50.8, 46.93) * mm, "end": v(51, 46.43) * mm});
            skLineSegment(sketch, "E3867", {"start": v(51, 46.43) * mm, "end": v(51.23, 45.92) * mm});
            skLineSegment(sketch, "E3868", {"start": v(51.23, 45.92) * mm, "end": v(51.48, 45.4) * mm});
            skLineSegment(sketch, "E3869", {"start": v(51.48, 45.4) * mm, "end": v(51.74, 44.9) * mm});
            skLineSegment(sketch, "E3870", {"start": v(51.74, 44.9) * mm, "end": v(52.01, 44.4) * mm});
            skLineSegment(sketch, "E3871", {"start": v(52.01, 44.4) * mm, "end": v(52.29, 43.94) * mm});
            skLineSegment(sketch, "E3872", {"start": v(52.29, 43.94) * mm, "end": v(52.57, 43.52) * mm});
            skLineSegment(sketch, "E3873", {"start": v(52.57, 43.52) * mm, "end": v(52.84, 43.16) * mm});
            skLineSegment(sketch, "E3874", {"start": v(52.84, 43.16) * mm, "end": v(53.14, 42.8) * mm});
            skLineSegment(sketch, "E3875", {"start": v(53.14, 42.8) * mm, "end": v(53.47, 42.42) * mm});
            skLineSegment(sketch, "E3876", {"start": v(53.47, 42.42) * mm, "end": v(53.81, 42.05) * mm});
            skLineSegment(sketch, "E3877", {"start": v(53.81, 42.05) * mm, "end": v(54.17, 41.7) * mm});
            skLineSegment(sketch, "E3878", {"start": v(54.17, 41.7) * mm, "end": v(54.53, 41.35) * mm});
            skLineSegment(sketch, "E3879", {"start": v(54.53, 41.35) * mm, "end": v(54.9, 41.04) * mm});
            skLineSegment(sketch, "E3880", {"start": v(54.9, 41.04) * mm, "end": v(55.25, 40.76) * mm});
            skLineSegment(sketch, "E3881", {"start": v(55.25, 40.76) * mm, "end": v(55.4, 40.67) * mm});
            skLineSegment(sketch, "E3882", {"start": v(55.4, 40.67) * mm, "end": v(55.55, 40.58) * mm});
            skLineSegment(sketch, "E3883", {"start": v(55.55, 40.58) * mm, "end": v(55.9, 40.4) * mm});
            skLineSegment(sketch, "E3884", {"start": v(55.9, 40.4) * mm, "end": v(56.25, 40.24) * mm});
            skLineSegment(sketch, "E3885", {"start": v(56.25, 40.24) * mm, "end": v(56.57, 40.1) * mm});
            skLineSegment(sketch, "E3886", {"start": v(56.57, 40.1) * mm, "end": v(57.1, 39.83) * mm});
            skLineSegment(sketch, "E3887", {"start": v(57.1, 39.83) * mm, "end": v(57.55, 39.61) * mm});
            skLineSegment(sketch, "E3888", {"start": v(57.55, 39.61) * mm, "end": v(57.88, 39.47) * mm});
            skLineSegment(sketch, "E3889", {"start": v(57.88, 39.47) * mm, "end": v(57.99, 39.43) * mm});
            skLineSegment(sketch, "E3890", {"start": v(57.99, 39.43) * mm, "end": v(58.05, 39.42) * mm});
            skLineSegment(sketch, "E3891", {"start": v(58.05, 39.42) * mm, "end": v(58.11, 39.43) * mm});
            skLineSegment(sketch, "E3892", {"start": v(58.11, 39.43) * mm, "end": v(58.18, 39.46) * mm});
            skLineSegment(sketch, "E3893", {"start": v(58.18, 39.46) * mm, "end": v(58.24, 39.5) * mm});
            skLineSegment(sketch, "E3894", {"start": v(58.24, 39.5) * mm, "end": v(58.3, 39.57) * mm});
            skLineSegment(sketch, "E3895", {"start": v(58.3, 39.57) * mm, "end": v(58.35, 39.67) * mm});
            skLineSegment(sketch, "E3896", {"start": v(58.35, 39.67) * mm, "end": v(58.4, 39.78) * mm});
            skLineSegment(sketch, "E3897", {"start": v(58.4, 39.78) * mm, "end": v(58.45, 39.92) * mm});
            skLineSegment(sketch, "E3898", {"start": v(58.45, 39.92) * mm, "end": v(58.5, 40.08) * mm});
            skLineSegment(sketch, "E3899", {"start": v(58.5, 40.08) * mm, "end": v(58.58, 40.47) * mm});
            skLineSegment(sketch, "E3900", {"start": v(58.58, 40.47) * mm, "end": v(58.66, 40.98) * mm});
            skLineSegment(sketch, "E3901", {"start": v(58.66, 40.98) * mm, "end": v(58.73, 41.59) * mm});
            skLineSegment(sketch, "E3902", {"start": v(58.73, 41.59) * mm, "end": v(58.8, 42.32) * mm});
            skLineSegment(sketch, "E3903", {"start": v(-1.17, 44.4) * mm, "end": v(-1.11, 44.33) * mm});
            skLineSegment(sketch, "E3904", {"start": v(-1.11, 44.33) * mm, "end": v(-1.03, 44.25) * mm});
            skLineSegment(sketch, "E3905", {"start": v(-1.03, 44.25) * mm, "end": v(-0.92, 44.16) * mm});
            skLineSegment(sketch, "E3906", {"start": v(-0.92, 44.16) * mm, "end": v(-0.8, 44.08) * mm});
            skLineSegment(sketch, "E3907", {"start": v(-0.8, 44.08) * mm, "end": v(-0.67, 44) * mm});
            skLineSegment(sketch, "E3908", {"start": v(-0.67, 44) * mm, "end": v(-0.53, 43.95) * mm});
            skLineSegment(sketch, "E3909", {"start": v(-0.53, 43.95) * mm, "end": v(-0.4, 43.9) * mm});
            skLineSegment(sketch, "E3910", {"start": v(-0.4, 43.9) * mm, "end": v(-0.28, 43.9) * mm});
            skLineSegment(sketch, "E3911", {"start": v(-0.28, 43.9) * mm, "end": v(-0.13, 43.93) * mm});
            skLineSegment(sketch, "E3912", {"start": v(-0.13, 43.93) * mm, "end": v(0, 43.96) * mm});
            skLineSegment(sketch, "E3913", {"start": v(0, 43.96) * mm, "end": v(0.13, 44) * mm});
            skLineSegment(sketch, "E3914", {"start": v(0.13, 44) * mm, "end": v(0.23, 44.06) * mm});
            skLineSegment(sketch, "E3915", {"start": v(0.23, 44.06) * mm, "end": v(0.32, 44.12) * mm});
            skLineSegment(sketch, "E3916", {"start": v(0.32, 44.12) * mm, "end": v(0.4, 44.2) * mm});
            skLineSegment(sketch, "E3917", {"start": v(0.4, 44.2) * mm, "end": v(0.46, 44.29) * mm});
            skLineSegment(sketch, "E3918", {"start": v(0.46, 44.29) * mm, "end": v(0.52, 44.4) * mm});
            skLineSegment(sketch, "E3919", {"start": v(0.52, 44.4) * mm, "end": v(0.48, 44.5) * mm});
            skLineSegment(sketch, "E3920", {"start": v(0.48, 44.5) * mm, "end": v(0.42, 44.61) * mm});
            skLineSegment(sketch, "E3921", {"start": v(0.42, 44.61) * mm, "end": v(0.34, 44.7) * mm});
            skLineSegment(sketch, "E3922", {"start": v(0.34, 44.7) * mm, "end": v(0.24, 44.79) * mm});
            skLineSegment(sketch, "E3923", {"start": v(0.24, 44.79) * mm, "end": v(0.13, 44.86) * mm});
            skLineSegment(sketch, "E3924", {"start": v(0.13, 44.86) * mm, "end": v(0, 44.92) * mm});
            skLineSegment(sketch, "E3925", {"start": v(0, 44.92) * mm, "end": v(-0.14, 44.96) * mm});
            skLineSegment(sketch, "E3926", {"start": v(-0.14, 44.96) * mm, "end": v(-0.3, 45) * mm});
            skLineSegment(sketch, "E3927", {"start": v(-0.3, 45) * mm, "end": v(-0.44, 44.97) * mm});
            skLineSegment(sketch, "E3928", {"start": v(-0.44, 44.97) * mm, "end": v(-0.56, 44.93) * mm});
            skLineSegment(sketch, "E3929", {"start": v(-0.56, 44.93) * mm, "end": v(-0.67, 44.87) * mm});
            skLineSegment(sketch, "E3930", {"start": v(-0.67, 44.87) * mm, "end": v(-0.76, 44.8) * mm});
            skLineSegment(sketch, "E3931", {"start": v(-0.76, 44.8) * mm, "end": v(-0.95, 44.64) * mm});
            skLineSegment(sketch, "E3932", {"start": v(-0.95, 44.64) * mm, "end": v(-1.17, 44.4) * mm});
            skLineSegment(sketch, "E3933", {"start": v(-34.07, 46.6) * mm, "end": v(-33.8, 46.74) * mm});
            skLineSegment(sketch, "E3934", {"start": v(-33.8, 46.74) * mm, "end": v(-33.5, 46.89) * mm});
            skLineSegment(sketch, "E3935", {"start": v(-33.5, 46.89) * mm, "end": v(-33.2, 47.06) * mm});
            skLineSegment(sketch, "E3936", {"start": v(-33.2, 47.06) * mm, "end": v(-32.9, 47.24) * mm});
            skLineSegment(sketch, "E3937", {"start": v(-32.9, 47.24) * mm, "end": v(-32.6, 47.43) * mm});
            skLineSegment(sketch, "E3938", {"start": v(-32.6, 47.43) * mm, "end": v(-32.3, 47.62) * mm});
            skLineSegment(sketch, "E3939", {"start": v(-32.3, 47.62) * mm, "end": v(-32.02, 47.83) * mm});
            skLineSegment(sketch, "E3940", {"start": v(-32.02, 47.83) * mm, "end": v(-31.75, 48.03) * mm});
            skLineSegment(sketch, "E3941", {"start": v(-31.75, 48.03) * mm, "end": v(-31.5, 48.23) * mm});
            skLineSegment(sketch, "E3942", {"start": v(-31.5, 48.23) * mm, "end": v(-31.26, 48.42) * mm});
            skLineSegment(sketch, "E3943", {"start": v(-31.26, 48.42) * mm, "end": v(-31.05, 48.6) * mm});
            skLineSegment(sketch, "E3944", {"start": v(-31.05, 48.6) * mm, "end": v(-30.87, 48.78) * mm});
            skLineSegment(sketch, "E3945", {"start": v(-30.87, 48.78) * mm, "end": v(-30.72, 48.94) * mm});
            skLineSegment(sketch, "E3946", {"start": v(-30.72, 48.94) * mm, "end": v(-30.61, 49.09) * mm});
            skLineSegment(sketch, "E3947", {"start": v(-30.61, 49.09) * mm, "end": v(-30.54, 49.2) * mm});
            skLineSegment(sketch, "E3948", {"start": v(-30.54, 49.2) * mm, "end": v(-30.52, 49.26) * mm});
            skLineSegment(sketch, "E3949", {"start": v(-30.52, 49.26) * mm, "end": v(-30.52, 49.3) * mm});
            skLineSegment(sketch, "E3950", {"start": v(-30.52, 49.3) * mm, "end": v(-30.51, 49.37) * mm});
            skLineSegment(sketch, "E3951", {"start": v(-30.51, 49.37) * mm, "end": v(-30.5, 49.45) * mm});
            skLineSegment(sketch, "E3952", {"start": v(-30.5, 49.45) * mm, "end": v(-30.5, 49.52) * mm});
            skLineSegment(sketch, "E3953", {"start": v(-30.5, 49.52) * mm, "end": v(-30.5, 49.55) * mm});
            skLineSegment(sketch, "E3954", {"start": v(-30.5, 49.55) * mm, "end": v(-30.52, 49.57) * mm});
            skLineSegment(sketch, "E3955", {"start": v(-30.52, 49.57) * mm, "end": v(-30.6, 49.67) * mm});
            skLineSegment(sketch, "E3956", {"start": v(-30.6, 49.67) * mm, "end": v(-30.68, 49.76) * mm});
            skLineSegment(sketch, "E3957", {"start": v(-30.68, 49.76) * mm, "end": v(-30.78, 49.84) * mm});
            skLineSegment(sketch, "E3958", {"start": v(-30.78, 49.84) * mm, "end": v(-30.88, 49.92) * mm});
            skLineSegment(sketch, "E3959", {"start": v(-30.88, 49.92) * mm, "end": v(-31.1, 50.06) * mm});
            skLineSegment(sketch, "E3960", {"start": v(-31.1, 50.06) * mm, "end": v(-31.34, 50.18) * mm});
            skLineSegment(sketch, "E3961", {"start": v(-31.34, 50.18) * mm, "end": v(-31.6, 50.29) * mm});
            skLineSegment(sketch, "E3962", {"start": v(-31.6, 50.29) * mm, "end": v(-31.88, 50.37) * mm});
            skLineSegment(sketch, "E3963", {"start": v(-31.88, 50.37) * mm, "end": v(-32.16, 50.44) * mm});
            skLineSegment(sketch, "E3964", {"start": v(-32.16, 50.44) * mm, "end": v(-32.46, 50.5) * mm});
            skLineSegment(sketch, "E3965", {"start": v(-32.46, 50.5) * mm, "end": v(-32.76, 50.55) * mm});
            skLineSegment(sketch, "E3966", {"start": v(-32.76, 50.55) * mm, "end": v(-33.07, 50.6) * mm});
            skLineSegment(sketch, "E3967", {"start": v(-33.07, 50.6) * mm, "end": v(-33.68, 50.65) * mm});
            skLineSegment(sketch, "E3968", {"start": v(-33.68, 50.65) * mm, "end": v(-34.26, 50.69) * mm});
            skLineSegment(sketch, "E3969", {"start": v(-34.26, 50.69) * mm, "end": v(-34.8, 50.73) * mm});
            skLineSegment(sketch, "E3970", {"start": v(-34.8, 50.73) * mm, "end": v(-35.25, 50.76) * mm});
            skLineSegment(sketch, "E3971", {"start": v(-35.25, 50.76) * mm, "end": v(-35.73, 50.76) * mm});
            skLineSegment(sketch, "E3972", {"start": v(-35.73, 50.76) * mm, "end": v(-36.23, 50.74) * mm});
            skLineSegment(sketch, "E3973", {"start": v(-36.23, 50.74) * mm, "end": v(-36.75, 50.7) * mm});
            skLineSegment(sketch, "E3974", {"start": v(-36.75, 50.7) * mm, "end": v(-37.26, 50.64) * mm});
            skLineSegment(sketch, "E3975", {"start": v(-37.26, 50.64) * mm, "end": v(-37.76, 50.57) * mm});
            skLineSegment(sketch, "E3976", {"start": v(-37.76, 50.57) * mm, "end": v(-38.23, 50.48) * mm});
            skLineSegment(sketch, "E3977", {"start": v(-38.23, 50.48) * mm, "end": v(-38.68, 50.38) * mm});
            skLineSegment(sketch, "E3978", {"start": v(-38.68, 50.38) * mm, "end": v(-39.04, 50.27) * mm});
            skLineSegment(sketch, "E3979", {"start": v(-39.04, 50.27) * mm, "end": v(-39.43, 50.14) * mm});
            skLineSegment(sketch, "E3980", {"start": v(-39.43, 50.14) * mm, "end": v(-39.82, 50) * mm});
            skLineSegment(sketch, "E3981", {"start": v(-39.82, 50) * mm, "end": v(-40.21, 49.83) * mm});
            skLineSegment(sketch, "E3982", {"start": v(-40.21, 49.83) * mm, "end": v(-40.6, 49.65) * mm});
            skLineSegment(sketch, "E3983", {"start": v(-40.6, 49.65) * mm, "end": v(-40.98, 49.46) * mm});
            skLineSegment(sketch, "E3984", {"start": v(-40.98, 49.46) * mm, "end": v(-41.33, 49.26) * mm});
            skLineSegment(sketch, "E3985", {"start": v(-41.33, 49.26) * mm, "end": v(-41.65, 49.06) * mm});
            skLineSegment(sketch, "E3986", {"start": v(-41.65, 49.06) * mm, "end": v(-41.83, 48.94) * mm});
            skLineSegment(sketch, "E3987", {"start": v(-41.83, 48.94) * mm, "end": v(-42, 48.8) * mm});
            skLineSegment(sketch, "E3988", {"start": v(-42, 48.8) * mm, "end": v(-42.35, 48.47) * mm});
            skLineSegment(sketch, "E3989", {"start": v(-42.35, 48.47) * mm, "end": v(-42.7, 48.14) * mm});
            skLineSegment(sketch, "E3990", {"start": v(-42.7, 48.14) * mm, "end": v(-43.02, 47.83) * mm});
            skLineSegment(sketch, "E3991", {"start": v(-43.02, 47.83) * mm, "end": v(-43.29, 47.58) * mm});
            skLineSegment(sketch, "E3992", {"start": v(-43.29, 47.58) * mm, "end": v(-43.54, 47.33) * mm});
            skLineSegment(sketch, "E3993", {"start": v(-43.54, 47.33) * mm, "end": v(-43.78, 47.1) * mm});
            skLineSegment(sketch, "E3994", {"start": v(-43.78, 47.1) * mm, "end": v(-43.98, 46.88) * mm});
            skLineSegment(sketch, "E3995", {"start": v(-43.98, 46.88) * mm, "end": v(-44.14, 46.7) * mm});
            skLineSegment(sketch, "E3996", {"start": v(-44.14, 46.7) * mm, "end": v(-44.27, 46.54) * mm});
            skLineSegment(sketch, "E3997", {"start": v(-44.27, 46.54) * mm, "end": v(-44.35, 46.41) * mm});
            skLineSegment(sketch, "E3998", {"start": v(-44.35, 46.41) * mm, "end": v(-44.37, 46.37) * mm});
            skLineSegment(sketch, "E3999", {"start": v(-44.37, 46.37) * mm, "end": v(-44.38, 46.34) * mm});
            skLineSegment(sketch, "E4000", {"start": v(-44.38, 46.34) * mm, "end": v(-44.38, 46.27) * mm});
            skLineSegment(sketch, "E4001", {"start": v(-44.38, 46.27) * mm, "end": v(-44.4, 46.2) * mm});
            skLineSegment(sketch, "E4002", {"start": v(-44.4, 46.2) * mm, "end": v(-44.4, 46.13) * mm});
            skLineSegment(sketch, "E4003", {"start": v(-44.4, 46.13) * mm, "end": v(-44.4, 46.1) * mm});
            skLineSegment(sketch, "E4004", {"start": v(-44.4, 46.1) * mm, "end": v(-44.38, 46.07) * mm});
            skLineSegment(sketch, "E4005", {"start": v(-44.38, 46.07) * mm, "end": v(-44.31, 46) * mm});
            skLineSegment(sketch, "E4006", {"start": v(-44.31, 46) * mm, "end": v(-44.23, 45.95) * mm});
            skLineSegment(sketch, "E4007", {"start": v(-44.23, 45.95) * mm, "end": v(-44.15, 45.9) * mm});
            skLineSegment(sketch, "E4008", {"start": v(-44.15, 45.9) * mm, "end": v(-44.05, 45.86) * mm});
            skLineSegment(sketch, "E4009", {"start": v(-44.05, 45.86) * mm, "end": v(-43.95, 45.83) * mm});
            skLineSegment(sketch, "E4010", {"start": v(-43.95, 45.83) * mm, "end": v(-43.84, 45.81) * mm});
            skLineSegment(sketch, "E4011", {"start": v(-43.84, 45.81) * mm, "end": v(-43.61, 45.78) * mm});
            skLineSegment(sketch, "E4012", {"start": v(-43.61, 45.78) * mm, "end": v(-43.14, 45.76) * mm});
            skLineSegment(sketch, "E4013", {"start": v(-43.14, 45.76) * mm, "end": v(-42.91, 45.74) * mm});
            skLineSegment(sketch, "E4014", {"start": v(-42.91, 45.74) * mm, "end": v(-42.71, 45.71) * mm});
            skLineSegment(sketch, "E4015", {"start": v(-42.71, 45.71) * mm, "end": v(-42.17, 45.6) * mm});
            skLineSegment(sketch, "E4016", {"start": v(-42.17, 45.6) * mm, "end": v(-41.63, 45.53) * mm});
            skLineSegment(sketch, "E4017", {"start": v(-41.63, 45.53) * mm, "end": v(-41.08, 45.47) * mm});
            skLineSegment(sketch, "E4018", {"start": v(-41.08, 45.47) * mm, "end": v(-40.53, 45.43) * mm});
            skLineSegment(sketch, "E4019", {"start": v(-40.53, 45.43) * mm, "end": v(-39.98, 45.41) * mm});
            skLineSegment(sketch, "E4020", {"start": v(-39.98, 45.41) * mm, "end": v(-39.42, 45.41) * mm});
            skLineSegment(sketch, "E4021", {"start": v(-39.42, 45.41) * mm, "end": v(-38.87, 45.44) * mm});
            skLineSegment(sketch, "E4022", {"start": v(-38.87, 45.44) * mm, "end": v(-38.32, 45.49) * mm});
            skLineSegment(sketch, "E4023", {"start": v(-38.32, 45.49) * mm, "end": v(-37.77, 45.55) * mm});
            skLineSegment(sketch, "E4024", {"start": v(-37.77, 45.55) * mm, "end": v(-37.22, 45.64) * mm});
            skLineSegment(sketch, "E4025", {"start": v(-37.22, 45.64) * mm, "end": v(-36.68, 45.75) * mm});
            skLineSegment(sketch, "E4026", {"start": v(-36.68, 45.75) * mm, "end": v(-36.14, 45.88) * mm});
            skLineSegment(sketch, "E4027", {"start": v(-36.14, 45.88) * mm, "end": v(-35.61, 46.03) * mm});
            skLineSegment(sketch, "E4028", {"start": v(-35.61, 46.03) * mm, "end": v(-35.1, 46.2) * mm});
            skLineSegment(sketch, "E4029", {"start": v(-35.1, 46.2) * mm, "end": v(-34.58, 46.4) * mm});
            skLineSegment(sketch, "E4030", {"start": v(-34.58, 46.4) * mm, "end": v(-34.07, 46.6) * mm});
            skLineSegment(sketch, "E4031", {"start": v(-43.24, 51.12) * mm, "end": v(-42.95, 51.67) * mm});
            skLineSegment(sketch, "E4032", {"start": v(-42.95, 51.67) * mm, "end": v(-42.63, 52.27) * mm});
            skLineSegment(sketch, "E4033", {"start": v(-42.63, 52.27) * mm, "end": v(-42.47, 52.57) * mm});
            skLineSegment(sketch, "E4034", {"start": v(-42.47, 52.57) * mm, "end": v(-42.32, 52.87) * mm});
            skLineSegment(sketch, "E4035", {"start": v(-42.32, 52.87) * mm, "end": v(-42.19, 53.16) * mm});
            skLineSegment(sketch, "E4036", {"start": v(-42.19, 53.16) * mm, "end": v(-42.07, 53.44) * mm});
            skLineSegment(sketch, "E4037", {"start": v(-42.07, 53.44) * mm, "end": v(-41.92, 53.89) * mm});
            skLineSegment(sketch, "E4038", {"start": v(-41.92, 53.89) * mm, "end": v(-41.77, 54.37) * mm});
            skLineSegment(sketch, "E4039", {"start": v(-41.77, 54.37) * mm, "end": v(-41.63, 54.87) * mm});
            skLineSegment(sketch, "E4040", {"start": v(-41.63, 54.87) * mm, "end": v(-41.5, 55.39) * mm});
            skLineSegment(sketch, "E4041", {"start": v(-41.5, 55.39) * mm, "end": v(-41.27, 56.42) * mm});
            skLineSegment(sketch, "E4042", {"start": v(-41.27, 56.42) * mm, "end": v(-41.08, 57.37) * mm});
            skLineSegment(sketch, "E4043", {"start": v(-41.08, 57.37) * mm, "end": v(-40.95, 57.98) * mm});
            skLineSegment(sketch, "E4044", {"start": v(-40.95, 57.98) * mm, "end": v(-40.81, 58.62) * mm});
            skLineSegment(sketch, "E4045", {"start": v(-40.81, 58.62) * mm, "end": v(-40.68, 59.29) * mm});
            skLineSegment(sketch, "E4046", {"start": v(-40.68, 59.29) * mm, "end": v(-40.63, 59.62) * mm});
            skLineSegment(sketch, "E4047", {"start": v(-40.63, 59.62) * mm, "end": v(-40.6, 59.95) * mm});
            skLineSegment(sketch, "E4048", {"start": v(-40.6, 59.95) * mm, "end": v(-40.57, 60.28) * mm});
            skLineSegment(sketch, "E4049", {"start": v(-40.57, 60.28) * mm, "end": v(-40.56, 60.61) * mm});
            skLineSegment(sketch, "E4050", {"start": v(-40.56, 60.61) * mm, "end": v(-40.58, 60.93) * mm});
            skLineSegment(sketch, "E4051", {"start": v(-40.58, 60.93) * mm, "end": v(-40.62, 61.24) * mm});
            skLineSegment(sketch, "E4052", {"start": v(-40.62, 61.24) * mm, "end": v(-40.65, 61.39) * mm});
            skLineSegment(sketch, "E4053", {"start": v(-40.65, 61.39) * mm, "end": v(-40.68, 61.54) * mm});
            skLineSegment(sketch, "E4054", {"start": v(-40.68, 61.54) * mm, "end": v(-40.73, 61.68) * mm});
            skLineSegment(sketch, "E4055", {"start": v(-40.73, 61.68) * mm, "end": v(-40.78, 61.82) * mm});
            skLineSegment(sketch, "E4056", {"start": v(-40.78, 61.82) * mm, "end": v(-40.84, 61.96) * mm});
            skLineSegment(sketch, "E4057", {"start": v(-40.84, 61.96) * mm, "end": v(-40.9, 62.1) * mm});
            skLineSegment(sketch, "E4058", {"start": v(-40.9, 62.1) * mm, "end": v(-40.99, 62.22) * mm});
            skLineSegment(sketch, "E4059", {"start": v(-40.99, 62.22) * mm, "end": v(-41.07, 62.34) * mm});
            skLineSegment(sketch, "E4060", {"start": v(-41.07, 62.34) * mm, "end": v(-41.12, 62.4) * mm});
            skLineSegment(sketch, "E4061", {"start": v(-41.12, 62.4) * mm, "end": v(-41.17, 62.44) * mm});
            skLineSegment(sketch, "E4062", {"start": v(-41.17, 62.44) * mm, "end": v(-41.23, 62.47) * mm});
            skLineSegment(sketch, "E4063", {"start": v(-41.23, 62.47) * mm, "end": v(-41.3, 62.5) * mm});
            skLineSegment(sketch, "E4064", {"start": v(-41.3, 62.5) * mm, "end": v(-41.45, 62.55) * mm});
            skLineSegment(sketch, "E4065", {"start": v(-41.45, 62.55) * mm, "end": v(-41.6, 62.58) * mm});
            skLineSegment(sketch, "E4066", {"start": v(-41.6, 62.58) * mm, "end": v(-41.78, 62.6) * mm});
            skLineSegment(sketch, "E4067", {"start": v(-41.78, 62.6) * mm, "end": v(-41.94, 62.58) * mm});
            skLineSegment(sketch, "E4068", {"start": v(-41.94, 62.58) * mm, "end": v(-42.1, 62.56) * mm});
            skLineSegment(sketch, "E4069", {"start": v(-42.1, 62.56) * mm, "end": v(-42.22, 62.52) * mm});
            skLineSegment(sketch, "E4070", {"start": v(-42.22, 62.52) * mm, "end": v(-42.39, 62.44) * mm});
            skLineSegment(sketch, "E4071", {"start": v(-42.39, 62.44) * mm, "end": v(-42.55, 62.36) * mm});
            skLineSegment(sketch, "E4072", {"start": v(-42.55, 62.36) * mm, "end": v(-42.87, 62.17) * mm});
            skLineSegment(sketch, "E4073", {"start": v(-42.87, 62.17) * mm, "end": v(-43.19, 61.95) * mm});
            skLineSegment(sketch, "E4074", {"start": v(-43.19, 61.95) * mm, "end": v(-43.5, 61.7) * mm});
            skLineSegment(sketch, "E4075", {"start": v(-43.5, 61.7) * mm, "end": v(-43.8, 61.44) * mm});
            skLineSegment(sketch, "E4076", {"start": v(-43.8, 61.44) * mm, "end": v(-44.1, 61.15) * mm});
            skLineSegment(sketch, "E4077", {"start": v(-44.1, 61.15) * mm, "end": v(-44.38, 60.85) * mm});
            skLineSegment(sketch, "E4078", {"start": v(-44.38, 60.85) * mm, "end": v(-44.67, 60.53) * mm});
            skLineSegment(sketch, "E4079", {"start": v(-44.67, 60.53) * mm, "end": v(-44.94, 60.2) * mm});
            skLineSegment(sketch, "E4080", {"start": v(-44.94, 60.2) * mm, "end": v(-45.2, 59.88) * mm});
            skLineSegment(sketch, "E4081", {"start": v(-45.2, 59.88) * mm, "end": v(-45.71, 59.2) * mm});
            skLineSegment(sketch, "E4082", {"start": v(-45.71, 59.2) * mm, "end": v(-46.18, 58.56) * mm});
            skLineSegment(sketch, "E4083", {"start": v(-46.18, 58.56) * mm, "end": v(-46.62, 57.95) * mm});
            skLineSegment(sketch, "E4084", {"start": v(-46.62, 57.95) * mm, "end": v(-46.97, 57.43) * mm});
            skLineSegment(sketch, "E4085", {"start": v(-46.97, 57.43) * mm, "end": v(-47.33, 56.87) * mm});
            skLineSegment(sketch, "E4086", {"start": v(-47.33, 56.87) * mm, "end": v(-47.68, 56.28) * mm});
            skLineSegment(sketch, "E4087", {"start": v(-47.68, 56.28) * mm, "end": v(-48.01, 55.66) * mm});
            skLineSegment(sketch, "E4088", {"start": v(-48.01, 55.66) * mm, "end": v(-48.17, 55.35) * mm});
            skLineSegment(sketch, "E4089", {"start": v(-48.17, 55.35) * mm, "end": v(-48.33, 55.03) * mm});
            skLineSegment(sketch, "E4090", {"start": v(-48.33, 55.03) * mm, "end": v(-48.47, 54.72) * mm});
            skLineSegment(sketch, "E4091", {"start": v(-48.47, 54.72) * mm, "end": v(-48.6, 54.4) * mm});
            skLineSegment(sketch, "E4092", {"start": v(-48.6, 54.4) * mm, "end": v(-48.72, 54.1) * mm});
            skLineSegment(sketch, "E4093", {"start": v(-48.72, 54.1) * mm, "end": v(-48.83, 53.78) * mm});
            skLineSegment(sketch, "E4094", {"start": v(-48.83, 53.78) * mm, "end": v(-48.92, 53.48) * mm});
            skLineSegment(sketch, "E4095", {"start": v(-48.92, 53.48) * mm, "end": v(-49, 53.19) * mm});
            skLineSegment(sketch, "E4096", {"start": v(-49, 53.19) * mm, "end": v(-49.05, 52.95) * mm});
            skLineSegment(sketch, "E4097", {"start": v(-49.05, 52.95) * mm, "end": v(-49.1, 52.7) * mm});
            skLineSegment(sketch, "E4098", {"start": v(-49.1, 52.7) * mm, "end": v(-49.13, 52.44) * mm});
            skLineSegment(sketch, "E4099", {"start": v(-49.13, 52.44) * mm, "end": v(-49.16, 52.18) * mm});
            skLineSegment(sketch, "E4100", {"start": v(-49.16, 52.18) * mm, "end": v(-49.2, 51.63) * mm});
            skLineSegment(sketch, "E4101", {"start": v(-49.2, 51.63) * mm, "end": v(-49.2, 51.07) * mm});
            skLineSegment(sketch, "E4102", {"start": v(-49.2, 51.07) * mm, "end": v(-49.19, 50.5) * mm});
            skLineSegment(sketch, "E4103", {"start": v(-49.19, 50.5) * mm, "end": v(-49.15, 49.96) * mm});
            skLineSegment(sketch, "E4104", {"start": v(-49.15, 49.96) * mm, "end": v(-49.08, 49.43) * mm});
            skLineSegment(sketch, "E4105", {"start": v(-49.08, 49.43) * mm, "end": v(-49, 48.94) * mm});
            skLineSegment(sketch, "E4106", {"start": v(-49, 48.94) * mm, "end": v(-48.91, 48.53) * mm});
            skLineSegment(sketch, "E4107", {"start": v(-48.91, 48.53) * mm, "end": v(-48.81, 48.07) * mm});
            skLineSegment(sketch, "E4108", {"start": v(-48.81, 48.07) * mm, "end": v(-48.7, 47.6) * mm});
            skLineSegment(sketch, "E4109", {"start": v(-48.7, 47.6) * mm, "end": v(-48.63, 47.37) * mm});
            skLineSegment(sketch, "E4110", {"start": v(-48.63, 47.37) * mm, "end": v(-48.55, 47.14) * mm});
            skLineSegment(sketch, "E4111", {"start": v(-48.55, 47.14) * mm, "end": v(-48.47, 46.9) * mm});
            skLineSegment(sketch, "E4112", {"start": v(-48.47, 46.9) * mm, "end": v(-48.38, 46.7) * mm});
            skLineSegment(sketch, "E4113", {"start": v(-48.38, 46.7) * mm, "end": v(-48.28, 46.48) * mm});
            skLineSegment(sketch, "E4114", {"start": v(-48.28, 46.48) * mm, "end": v(-48.16, 46.29) * mm});
            skLineSegment(sketch, "E4115", {"start": v(-48.16, 46.29) * mm, "end": v(-48.04, 46.1) * mm});
            skLineSegment(sketch, "E4116", {"start": v(-48.04, 46.1) * mm, "end": v(-47.9, 45.95) * mm});
            skLineSegment(sketch, "E4117", {"start": v(-47.9, 45.95) * mm, "end": v(-47.76, 45.8) * mm});
            skLineSegment(sketch, "E4118", {"start": v(-47.76, 45.8) * mm, "end": v(-47.6, 45.69) * mm});
            skLineSegment(sketch, "E4119", {"start": v(-47.6, 45.69) * mm, "end": v(-47.56, 45.67) * mm});
            skLineSegment(sketch, "E4120", {"start": v(-47.56, 45.67) * mm, "end": v(-47.51, 45.66) * mm});
            skLineSegment(sketch, "E4121", {"start": v(-47.51, 45.66) * mm, "end": v(-47.42, 45.67) * mm});
            skLineSegment(sketch, "E4122", {"start": v(-47.42, 45.67) * mm, "end": v(-47.32, 45.69) * mm});
            skLineSegment(sketch, "E4123", {"start": v(-47.32, 45.69) * mm, "end": v(-47.22, 45.7) * mm});
            skLineSegment(sketch, "E4124", {"start": v(-47.22, 45.7) * mm, "end": v(-47.16, 45.71) * mm});
            skLineSegment(sketch, "E4125", {"start": v(-47.16, 45.71) * mm, "end": v(-47.1, 45.74) * mm});
            skLineSegment(sketch, "E4126", {"start": v(-47.1, 45.74) * mm, "end": v(-47.01, 45.78) * mm});
            skLineSegment(sketch, "E4127", {"start": v(-47.01, 45.78) * mm, "end": v(-46.93, 45.84) * mm});
            skLineSegment(sketch, "E4128", {"start": v(-46.93, 45.84) * mm, "end": v(-46.74, 46) * mm});
            skLineSegment(sketch, "E4129", {"start": v(-46.74, 46) * mm, "end": v(-46.52, 46.2) * mm});
            skLineSegment(sketch, "E4130", {"start": v(-46.52, 46.2) * mm, "end": v(-46.28, 46.47) * mm});
            skLineSegment(sketch, "E4131", {"start": v(-46.28, 46.47) * mm, "end": v(-46.02, 46.77) * mm});
            skLineSegment(sketch, "E4132", {"start": v(-46.02, 46.77) * mm, "end": v(-45.75, 47.11) * mm});
            skLineSegment(sketch, "E4133", {"start": v(-45.75, 47.11) * mm, "end": v(-45.47, 47.48) * mm});
            skLineSegment(sketch, "E4134", {"start": v(-45.47, 47.48) * mm, "end": v(-45.18, 47.89) * mm});
            skLineSegment(sketch, "E4135", {"start": v(-45.18, 47.89) * mm, "end": v(-44.89, 48.32) * mm});
            skLineSegment(sketch, "E4136", {"start": v(-44.89, 48.32) * mm, "end": v(-44.6, 48.76) * mm});
            skLineSegment(sketch, "E4137", {"start": v(-44.6, 48.76) * mm, "end": v(-44.3, 49.22) * mm});
            skLineSegment(sketch, "E4138", {"start": v(-44.3, 49.22) * mm, "end": v(-44.01, 49.7) * mm});
            skLineSegment(sketch, "E4139", {"start": v(-44.01, 49.7) * mm, "end": v(-43.74, 50.17) * mm});
            skLineSegment(sketch, "E4140", {"start": v(-43.74, 50.17) * mm, "end": v(-43.48, 50.65) * mm});
            skLineSegment(sketch, "E4141", {"start": v(-43.48, 50.65) * mm, "end": v(-43.24, 51.12) * mm});
            skLineSegment(sketch, "E4142", {"start": v(43.85, 46.79) * mm, "end": v(44.08, 47.02) * mm});
            skLineSegment(sketch, "E4143", {"start": v(44.08, 47.02) * mm, "end": v(43.72, 47.36) * mm});
            skLineSegment(sketch, "E4144", {"start": v(43.72, 47.36) * mm, "end": v(43.36, 47.73) * mm});
            skLineSegment(sketch, "E4145", {"start": v(43.36, 47.73) * mm, "end": v(42.6, 48.5) * mm});
            skLineSegment(sketch, "E4146", {"start": v(42.6, 48.5) * mm, "end": v(42.2, 48.89) * mm});
            skLineSegment(sketch, "E4147", {"start": v(42.2, 48.89) * mm, "end": v(41.8, 49.24) * mm});
            skLineSegment(sketch, "E4148", {"start": v(41.8, 49.24) * mm, "end": v(41.6, 49.4) * mm});
            skLineSegment(sketch, "E4149", {"start": v(41.6, 49.4) * mm, "end": v(41.4, 49.56) * mm});
            skLineSegment(sketch, "E4150", {"start": v(41.4, 49.56) * mm, "end": v(41.2, 49.7) * mm});
            skLineSegment(sketch, "E4151", {"start": v(41.2, 49.7) * mm, "end": v(41, 49.82) * mm});
            skLineSegment(sketch, "E4152", {"start": v(41, 49.82) * mm, "end": v(40.8, 49.93) * mm});
            skLineSegment(sketch, "E4153", {"start": v(40.8, 49.93) * mm, "end": v(40.6, 50.04) * mm});
            skLineSegment(sketch, "E4154", {"start": v(40.6, 50.04) * mm, "end": v(40.14, 50.24) * mm});
            skLineSegment(sketch, "E4155", {"start": v(40.14, 50.24) * mm, "end": v(39.67, 50.42) * mm});
            skLineSegment(sketch, "E4156", {"start": v(39.67, 50.42) * mm, "end": v(39.17, 50.58) * mm});
            skLineSegment(sketch, "E4157", {"start": v(39.17, 50.58) * mm, "end": v(38.67, 50.73) * mm});
            skLineSegment(sketch, "E4158", {"start": v(38.67, 50.73) * mm, "end": v(38.18, 50.85) * mm});
            skLineSegment(sketch, "E4159", {"start": v(38.18, 50.85) * mm, "end": v(37.7, 50.94) * mm});
            skLineSegment(sketch, "E4160", {"start": v(37.7, 50.94) * mm, "end": v(37.24, 51) * mm});
            skLineSegment(sketch, "E4161", {"start": v(37.24, 51) * mm, "end": v(37, 51.02) * mm});
            skLineSegment(sketch, "E4162", {"start": v(37, 51.02) * mm, "end": v(36.75, 51.01) * mm});
            skLineSegment(sketch, "E4163", {"start": v(36.75, 51.01) * mm, "end": v(36.5, 51) * mm});
            skLineSegment(sketch, "E4164", {"start": v(36.5, 51) * mm, "end": v(36.23, 50.97) * mm});
            skLineSegment(sketch, "E4165", {"start": v(36.23, 50.97) * mm, "end": v(35.7, 50.9) * mm});
            skLineSegment(sketch, "E4166", {"start": v(35.7, 50.9) * mm, "end": v(35.45, 50.86) * mm});
            skLineSegment(sketch, "E4167", {"start": v(35.45, 50.86) * mm, "end": v(35.21, 50.84) * mm});
            skLineSegment(sketch, "E4168", {"start": v(35.21, 50.84) * mm, "end": v(34.78, 50.8) * mm});
            skLineSegment(sketch, "E4169", {"start": v(34.78, 50.8) * mm, "end": v(34.32, 50.74) * mm});
            skLineSegment(sketch, "E4170", {"start": v(34.32, 50.74) * mm, "end": v(33.84, 50.67) * mm});
            skLineSegment(sketch, "E4171", {"start": v(33.84, 50.67) * mm, "end": v(33.37, 50.6) * mm});
            skLineSegment(sketch, "E4172", {"start": v(33.37, 50.6) * mm, "end": v(32.91, 50.51) * mm});
            skLineSegment(sketch, "E4173", {"start": v(32.91, 50.51) * mm, "end": v(32.48, 50.42) * mm});
            skLineSegment(sketch, "E4174", {"start": v(32.48, 50.42) * mm, "end": v(32.1, 50.34) * mm});
            skLineSegment(sketch, "E4175", {"start": v(32.1, 50.34) * mm, "end": v(31.78, 50.25) * mm});
            skLineSegment(sketch, "E4176", {"start": v(31.78, 50.25) * mm, "end": v(30.37, 49.82) * mm});
            skLineSegment(sketch, "E4177", {"start": v(30.37, 49.82) * mm, "end": v(30.48, 49.46) * mm});
            skLineSegment(sketch, "E4178", {"start": v(30.48, 49.46) * mm, "end": v(30.5, 49.42) * mm});
            skLineSegment(sketch, "E4179", {"start": v(30.5, 49.42) * mm, "end": v(30.53, 49.37) * mm});
            skLineSegment(sketch, "E4180", {"start": v(30.53, 49.37) * mm, "end": v(30.65, 49.24) * mm});
            skLineSegment(sketch, "E4181", {"start": v(30.65, 49.24) * mm, "end": v(30.81, 49.08) * mm});
            skLineSegment(sketch, "E4182", {"start": v(30.81, 49.08) * mm, "end": v(31.02, 48.9) * mm});
            skLineSegment(sketch, "E4183", {"start": v(31.02, 48.9) * mm, "end": v(31.27, 48.7) * mm});
            skLineSegment(sketch, "E4184", {"start": v(31.27, 48.7) * mm, "end": v(31.55, 48.48) * mm});
            skLineSegment(sketch, "E4185", {"start": v(31.55, 48.48) * mm, "end": v(31.85, 48.26) * mm});
            skLineSegment(sketch, "E4186", {"start": v(31.85, 48.26) * mm, "end": v(32.17, 48.04) * mm});
            skLineSegment(sketch, "E4187", {"start": v(32.17, 48.04) * mm, "end": v(32.54, 47.77) * mm});
            skLineSegment(sketch, "E4188", {"start": v(32.54, 47.77) * mm, "end": v(32.94, 47.47) * mm});
            skLineSegment(sketch, "E4189", {"start": v(32.94, 47.47) * mm, "end": v(33.15, 47.33) * mm});
            skLineSegment(sketch, "E4190", {"start": v(33.15, 47.33) * mm, "end": v(33.35, 47.2) * mm});
            skLineSegment(sketch, "E4191", {"start": v(33.35, 47.2) * mm, "end": v(33.55, 47.07) * mm});
            skLineSegment(sketch, "E4192", {"start": v(33.55, 47.07) * mm, "end": v(33.75, 46.97) * mm});
            skLineSegment(sketch, "E4193", {"start": v(33.75, 46.97) * mm, "end": v(34.12, 46.8) * mm});
            skLineSegment(sketch, "E4194", {"start": v(34.12, 46.8) * mm, "end": v(34.53, 46.64) * mm});
            skLineSegment(sketch, "E4195", {"start": v(34.53, 46.64) * mm, "end": v(34.95, 46.5) * mm});
            skLineSegment(sketch, "E4196", {"start": v(34.95, 46.5) * mm, "end": v(35.4, 46.35) * mm});
            skLineSegment(sketch, "E4197", {"start": v(35.4, 46.35) * mm, "end": v(35.83, 46.23) * mm});
            skLineSegment(sketch, "E4198", {"start": v(35.83, 46.23) * mm, "end": v(36.27, 46.12) * mm});
            skLineSegment(sketch, "E4199", {"start": v(36.27, 46.12) * mm, "end": v(36.7, 46.04) * mm});
            skLineSegment(sketch, "E4200", {"start": v(36.7, 46.04) * mm, "end": v(37.1, 45.97) * mm});
            skLineSegment(sketch, "E4201", {"start": v(37.1, 45.97) * mm, "end": v(37.35, 45.95) * mm});
            skLineSegment(sketch, "E4202", {"start": v(37.35, 45.95) * mm, "end": v(37.62, 45.94) * mm});
            skLineSegment(sketch, "E4203", {"start": v(37.62, 45.94) * mm, "end": v(38.18, 45.95) * mm});
            skLineSegment(sketch, "E4204", {"start": v(38.18, 45.95) * mm, "end": v(38.75, 45.98) * mm});
            skLineSegment(sketch, "E4205", {"start": v(38.75, 45.98) * mm, "end": v(39.27, 46) * mm});
            skLineSegment(sketch, "E4206", {"start": v(39.27, 46) * mm, "end": v(40.09, 46.03) * mm});
            skLineSegment(sketch, "E4207", {"start": v(40.09, 46.03) * mm, "end": v(40.87, 46.08) * mm});
            skLineSegment(sketch, "E4208", {"start": v(40.87, 46.08) * mm, "end": v(41.59, 46.16) * mm});
            skLineSegment(sketch, "E4209", {"start": v(41.59, 46.16) * mm, "end": v(42.24, 46.25) * mm});
            skLineSegment(sketch, "E4210", {"start": v(42.24, 46.25) * mm, "end": v(42.53, 46.3) * mm});
            skLineSegment(sketch, "E4211", {"start": v(42.53, 46.3) * mm, "end": v(42.8, 46.37) * mm});
            skLineSegment(sketch, "E4212", {"start": v(42.8, 46.37) * mm, "end": v(43.05, 46.43) * mm});
            skLineSegment(sketch, "E4213", {"start": v(43.05, 46.43) * mm, "end": v(43.27, 46.5) * mm});
            skLineSegment(sketch, "E4214", {"start": v(43.27, 46.5) * mm, "end": v(43.46, 46.56) * mm});
            skLineSegment(sketch, "E4215", {"start": v(43.46, 46.56) * mm, "end": v(43.62, 46.64) * mm});
            skLineSegment(sketch, "E4216", {"start": v(43.62, 46.64) * mm, "end": v(43.75, 46.71) * mm});
            skLineSegment(sketch, "E4217", {"start": v(43.75, 46.71) * mm, "end": v(43.85, 46.79) * mm});
            skLineSegment(sketch, "E4218", {"start": v(48.3, 50.6) * mm, "end": v(48.29, 51.22) * mm});
            skLineSegment(sketch, "E4219", {"start": v(48.29, 51.22) * mm, "end": v(48.3, 51.88) * mm});
            skLineSegment(sketch, "E4220", {"start": v(48.3, 51.88) * mm, "end": v(48.3, 52.2) * mm});
            skLineSegment(sketch, "E4221", {"start": v(48.3, 52.2) * mm, "end": v(48.27, 52.53) * mm});
            skLineSegment(sketch, "E4222", {"start": v(48.27, 52.53) * mm, "end": v(48.24, 52.84) * mm});
            skLineSegment(sketch, "E4223", {"start": v(48.24, 52.84) * mm, "end": v(48.21, 52.98) * mm});
            skLineSegment(sketch, "E4224", {"start": v(48.21, 52.98) * mm, "end": v(48.18, 53.13) * mm});
            skLineSegment(sketch, "E4225", {"start": v(48.18, 53.13) * mm, "end": v(48.1, 53.4) * mm});
            skLineSegment(sketch, "E4226", {"start": v(48.1, 53.4) * mm, "end": v(48.02, 53.67) * mm});
            skLineSegment(sketch, "E4227", {"start": v(48.02, 53.67) * mm, "end": v(47.92, 53.95) * mm});
            skLineSegment(sketch, "E4228", {"start": v(47.92, 53.95) * mm, "end": v(47.8, 54.23) * mm});
            skLineSegment(sketch, "E4229", {"start": v(47.8, 54.23) * mm, "end": v(47.56, 54.8) * mm});
            skLineSegment(sketch, "E4230", {"start": v(47.56, 54.8) * mm, "end": v(47.28, 55.38) * mm});
            skLineSegment(sketch, "E4231", {"start": v(47.28, 55.38) * mm, "end": v(46.98, 55.94) * mm});
            skLineSegment(sketch, "E4232", {"start": v(46.98, 55.94) * mm, "end": v(46.67, 56.49) * mm});
            skLineSegment(sketch, "E4233", {"start": v(46.67, 56.49) * mm, "end": v(46.35, 57) * mm});
            skLineSegment(sketch, "E4234", {"start": v(46.35, 57) * mm, "end": v(46.04, 57.47) * mm});
            skLineSegment(sketch, "E4235", {"start": v(46.04, 57.47) * mm, "end": v(45.74, 57.88) * mm});
            skLineSegment(sketch, "E4236", {"start": v(45.74, 57.88) * mm, "end": v(45.4, 58.3) * mm});
            skLineSegment(sketch, "E4237", {"start": v(45.4, 58.3) * mm, "end": v(45.04, 58.73) * mm});
            skLineSegment(sketch, "E4238", {"start": v(45.04, 58.73) * mm, "end": v(44.66, 59.15) * mm});
            skLineSegment(sketch, "E4239", {"start": v(44.66, 59.15) * mm, "end": v(44.26, 59.56) * mm});
            skLineSegment(sketch, "E4240", {"start": v(44.26, 59.56) * mm, "end": v(43.87, 59.96) * mm});
            skLineSegment(sketch, "E4241", {"start": v(43.87, 59.96) * mm, "end": v(43.47, 60.33) * mm});
            skLineSegment(sketch, "E4242", {"start": v(43.47, 60.33) * mm, "end": v(43.1, 60.67) * mm});
            skLineSegment(sketch, "E4243", {"start": v(43.1, 60.67) * mm, "end": v(42.78, 60.93) * mm});
            skLineSegment(sketch, "E4244", {"start": v(42.78, 60.93) * mm, "end": v(42.43, 61.2) * mm});
            skLineSegment(sketch, "E4245", {"start": v(42.43, 61.2) * mm, "end": v(42.07, 61.46) * mm});
            skLineSegment(sketch, "E4246", {"start": v(42.07, 61.46) * mm, "end": v(41.69, 61.72) * mm});
            skLineSegment(sketch, "E4247", {"start": v(41.69, 61.72) * mm, "end": v(40.93, 62.23) * mm});
            skLineSegment(sketch, "E4248", {"start": v(40.93, 62.23) * mm, "end": v(40.23, 62.7) * mm});
            skLineSegment(sketch, "E4249", {"start": v(40.23, 62.7) * mm, "end": v(40.24, 62.13) * mm});
            skLineSegment(sketch, "E4250", {"start": v(40.24, 62.13) * mm, "end": v(40.24, 61.5) * mm});
            skLineSegment(sketch, "E4251", {"start": v(40.24, 61.5) * mm, "end": v(40.24, 60.21) * mm});
            skLineSegment(sketch, "E4252", {"start": v(40.24, 60.21) * mm, "end": v(40.25, 59.56) * mm});
            skLineSegment(sketch, "E4253", {"start": v(40.25, 59.56) * mm, "end": v(40.28, 58.92) * mm});
            skLineSegment(sketch, "E4254", {"start": v(40.28, 58.92) * mm, "end": v(40.3, 58.6) * mm});
            skLineSegment(sketch, "E4255", {"start": v(40.3, 58.6) * mm, "end": v(40.33, 58.3) * mm});
            skLineSegment(sketch, "E4256", {"start": v(40.33, 58.3) * mm, "end": v(40.36, 58.01) * mm});
            skLineSegment(sketch, "E4257", {"start": v(40.36, 58.01) * mm, "end": v(40.4, 57.73) * mm});
            skLineSegment(sketch, "E4258", {"start": v(40.4, 57.73) * mm, "end": v(40.46, 57.47) * mm});
            skLineSegment(sketch, "E4259", {"start": v(40.46, 57.47) * mm, "end": v(40.54, 57.2) * mm});
            skLineSegment(sketch, "E4260", {"start": v(40.54, 57.2) * mm, "end": v(40.72, 56.65) * mm});
            skLineSegment(sketch, "E4261", {"start": v(40.72, 56.65) * mm, "end": v(40.92, 56.1) * mm});
            skLineSegment(sketch, "E4262", {"start": v(40.92, 56.1) * mm, "end": v(41.1, 55.59) * mm});
            skLineSegment(sketch, "E4263", {"start": v(41.1, 55.59) * mm, "end": v(41.27, 55.11) * mm});
            skLineSegment(sketch, "E4264", {"start": v(41.27, 55.11) * mm, "end": v(41.46, 54.6) * mm});
            skLineSegment(sketch, "E4265", {"start": v(41.46, 54.6) * mm, "end": v(41.69, 54.04) * mm});
            skLineSegment(sketch, "E4266", {"start": v(41.69, 54.04) * mm, "end": v(41.93, 53.47) * mm});
            skLineSegment(sketch, "E4267", {"start": v(41.93, 53.47) * mm, "end": v(42.18, 52.9) * mm});
            skLineSegment(sketch, "E4268", {"start": v(42.18, 52.9) * mm, "end": v(42.44, 52.36) * mm});
            skLineSegment(sketch, "E4269", {"start": v(42.44, 52.36) * mm, "end": v(42.7, 51.85) * mm});
            skLineSegment(sketch, "E4270", {"start": v(42.7, 51.85) * mm, "end": v(42.94, 51.4) * mm});
            skLineSegment(sketch, "E4271", {"start": v(42.94, 51.4) * mm, "end": v(43.2, 50.9) * mm});
            skLineSegment(sketch, "E4272", {"start": v(43.2, 50.9) * mm, "end": v(43.48, 50.35) * mm});
            skLineSegment(sketch, "E4273", {"start": v(43.48, 50.35) * mm, "end": v(43.62, 50.08) * mm});
            skLineSegment(sketch, "E4274", {"start": v(43.62, 50.08) * mm, "end": v(43.77, 49.82) * mm});
            skLineSegment(sketch, "E4275", {"start": v(43.77, 49.82) * mm, "end": v(43.92, 49.57) * mm});
            skLineSegment(sketch, "E4276", {"start": v(43.92, 49.57) * mm, "end": v(44.07, 49.34) * mm});
            skLineSegment(sketch, "E4277", {"start": v(44.07, 49.34) * mm, "end": v(44.23, 49.13) * mm});
            skLineSegment(sketch, "E4278", {"start": v(44.23, 49.13) * mm, "end": v(44.4, 48.9) * mm});
            skLineSegment(sketch, "E4279", {"start": v(44.4, 48.9) * mm, "end": v(44.79, 48.46) * mm});
            skLineSegment(sketch, "E4280", {"start": v(44.79, 48.46) * mm, "end": v(45.2, 48.02) * mm});
            skLineSegment(sketch, "E4281", {"start": v(45.2, 48.02) * mm, "end": v(45.62, 47.57) * mm});
            skLineSegment(sketch, "E4282", {"start": v(45.62, 47.57) * mm, "end": v(46.48, 46.7) * mm});
            skLineSegment(sketch, "E4283", {"start": v(46.48, 46.7) * mm, "end": v(46.89, 46.27) * mm});
            skLineSegment(sketch, "E4284", {"start": v(46.89, 46.27) * mm, "end": v(47.26, 45.87) * mm});
            skLineSegment(sketch, "E4285", {"start": v(47.26, 45.87) * mm, "end": v(47.4, 46.13) * mm});
            skLineSegment(sketch, "E4286", {"start": v(47.4, 46.13) * mm, "end": v(47.57, 46.4) * mm});
            skLineSegment(sketch, "E4287", {"start": v(47.57, 46.4) * mm, "end": v(47.9, 46.96) * mm});
            skLineSegment(sketch, "E4288", {"start": v(47.9, 46.96) * mm, "end": v(48.07, 47.24) * mm});
            skLineSegment(sketch, "E4289", {"start": v(48.07, 47.24) * mm, "end": v(48.21, 47.53) * mm});
            skLineSegment(sketch, "E4290", {"start": v(48.21, 47.53) * mm, "end": v(48.33, 47.81) * mm});
            skLineSegment(sketch, "E4291", {"start": v(48.33, 47.81) * mm, "end": v(48.38, 47.95) * mm});
            skLineSegment(sketch, "E4292", {"start": v(48.38, 47.95) * mm, "end": v(48.41, 48.1) * mm});
            skLineSegment(sketch, "E4293", {"start": v(48.41, 48.1) * mm, "end": v(48.44, 48.23) * mm});
            skLineSegment(sketch, "E4294", {"start": v(48.44, 48.23) * mm, "end": v(48.45, 48.38) * mm});
            skLineSegment(sketch, "E4295", {"start": v(48.45, 48.38) * mm, "end": v(48.47, 48.69) * mm});
            skLineSegment(sketch, "E4296", {"start": v(48.47, 48.69) * mm, "end": v(48.46, 49.01) * mm});
            skLineSegment(sketch, "E4297", {"start": v(48.46, 49.01) * mm, "end": v(48.43, 49.34) * mm});
            skLineSegment(sketch, "E4298", {"start": v(48.43, 49.34) * mm, "end": v(48.35, 50) * mm});
            skLineSegment(sketch, "E4299", {"start": v(48.35, 50) * mm, "end": v(48.32, 50.31) * mm});
            skLineSegment(sketch, "E4300", {"start": v(48.32, 50.31) * mm, "end": v(48.3, 50.6) * mm});
            skLineSegment(sketch, "E4301", {"start": v(-24.95, 52.6) * mm, "end": v(-24.68, 52.74) * mm});
            skLineSegment(sketch, "E4302", {"start": v(-24.68, 52.74) * mm, "end": v(-24.4, 52.9) * mm});
            skLineSegment(sketch, "E4303", {"start": v(-24.4, 52.9) * mm, "end": v(-24.11, 53.07) * mm});
            skLineSegment(sketch, "E4304", {"start": v(-24.11, 53.07) * mm, "end": v(-23.83, 53.26) * mm});
            skLineSegment(sketch, "E4305", {"start": v(-23.83, 53.26) * mm, "end": v(-23.27, 53.65) * mm});
            skLineSegment(sketch, "E4306", {"start": v(-23.27, 53.65) * mm, "end": v(-22.75, 54.04) * mm});
            skLineSegment(sketch, "E4307", {"start": v(-22.75, 54.04) * mm, "end": v(-22.5, 54.23) * mm});
            skLineSegment(sketch, "E4308", {"start": v(-22.5, 54.23) * mm, "end": v(-22.3, 54.42) * mm});
            skLineSegment(sketch, "E4309", {"start": v(-22.3, 54.42) * mm, "end": v(-22.1, 54.6) * mm});
            skLineSegment(sketch, "E4310", {"start": v(-22.1, 54.6) * mm, "end": v(-21.93, 54.76) * mm});
            skLineSegment(sketch, "E4311", {"start": v(-21.93, 54.76) * mm, "end": v(-21.8, 54.91) * mm});
            skLineSegment(sketch, "E4312", {"start": v(-21.8, 54.91) * mm, "end": v(-21.7, 55.05) * mm});
            skLineSegment(sketch, "E4313", {"start": v(-21.7, 55.05) * mm, "end": v(-21.63, 55.16) * mm});
            skLineSegment(sketch, "E4314", {"start": v(-21.63, 55.16) * mm, "end": v(-21.61, 55.2) * mm});
            skLineSegment(sketch, "E4315", {"start": v(-21.61, 55.2) * mm, "end": v(-21.6, 55.25) * mm});
            skLineSegment(sketch, "E4316", {"start": v(-21.6, 55.25) * mm, "end": v(-21.6, 55.31) * mm});
            skLineSegment(sketch, "E4317", {"start": v(-21.6, 55.31) * mm, "end": v(-21.6, 55.38) * mm});
            skLineSegment(sketch, "E4318", {"start": v(-21.6, 55.38) * mm, "end": v(-21.59, 55.45) * mm});
            skLineSegment(sketch, "E4319", {"start": v(-21.59, 55.45) * mm, "end": v(-21.6, 55.48) * mm});
            skLineSegment(sketch, "E4320", {"start": v(-21.6, 55.48) * mm, "end": v(-21.6, 55.5) * mm});
            skLineSegment(sketch, "E4321", {"start": v(-21.6, 55.5) * mm, "end": v(-21.72, 55.63) * mm});
            skLineSegment(sketch, "E4322", {"start": v(-21.72, 55.63) * mm, "end": v(-21.86, 55.74) * mm});
            skLineSegment(sketch, "E4323", {"start": v(-21.86, 55.74) * mm, "end": v(-22, 55.83) * mm});
            skLineSegment(sketch, "E4324", {"start": v(-22, 55.83) * mm, "end": v(-22.18, 55.9) * mm});
            skLineSegment(sketch, "E4325", {"start": v(-22.18, 55.9) * mm, "end": v(-22.35, 55.97) * mm});
            skLineSegment(sketch, "E4326", {"start": v(-22.35, 55.97) * mm, "end": v(-22.54, 56.03) * mm});
            skLineSegment(sketch, "E4327", {"start": v(-22.54, 56.03) * mm, "end": v(-22.74, 56.07) * mm});
            skLineSegment(sketch, "E4328", {"start": v(-22.74, 56.07) * mm, "end": v(-22.95, 56.1) * mm});
            skLineSegment(sketch, "E4329", {"start": v(-22.95, 56.1) * mm, "end": v(-23.36, 56.15) * mm});
            skLineSegment(sketch, "E4330", {"start": v(-23.36, 56.15) * mm, "end": v(-23.78, 56.18) * mm});
            skLineSegment(sketch, "E4331", {"start": v(-23.78, 56.18) * mm, "end": v(-24.18, 56.21) * mm});
            skLineSegment(sketch, "E4332", {"start": v(-24.18, 56.21) * mm, "end": v(-24.54, 56.25) * mm});
            skLineSegment(sketch, "E4333", {"start": v(-24.54, 56.25) * mm, "end": v(-25.04, 56.3) * mm});
            skLineSegment(sketch, "E4334", {"start": v(-25.04, 56.3) * mm, "end": v(-25.58, 56.34) * mm});
            skLineSegment(sketch, "E4335", {"start": v(-25.58, 56.34) * mm, "end": v(-26.13, 56.38) * mm});
            skLineSegment(sketch, "E4336", {"start": v(-26.13, 56.38) * mm, "end": v(-26.7, 56.4) * mm});
            skLineSegment(sketch, "E4337", {"start": v(-26.7, 56.4) * mm, "end": v(-27.26, 56.39) * mm});
            skLineSegment(sketch, "E4338", {"start": v(-27.26, 56.39) * mm, "end": v(-27.82, 56.36) * mm});
            skLineSegment(sketch, "E4339", {"start": v(-27.82, 56.36) * mm, "end": v(-28.35, 56.32) * mm});
            skLineSegment(sketch, "E4340", {"start": v(-28.35, 56.32) * mm, "end": v(-28.6, 56.29) * mm});
            skLineSegment(sketch, "E4341", {"start": v(-28.6, 56.29) * mm, "end": v(-28.84, 56.25) * mm});
            skLineSegment(sketch, "E4342", {"start": v(-28.84, 56.25) * mm, "end": v(-29.3, 56.15) * mm});
            skLineSegment(sketch, "E4343", {"start": v(-29.3, 56.15) * mm, "end": v(-29.76, 56.02) * mm});
            skLineSegment(sketch, "E4344", {"start": v(-29.76, 56.02) * mm, "end": v(-30.24, 55.87) * mm});
            skLineSegment(sketch, "E4345", {"start": v(-30.24, 55.87) * mm, "end": v(-30.73, 55.7) * mm});
            skLineSegment(sketch, "E4346", {"start": v(-30.73, 55.7) * mm, "end": v(-31.2, 55.5) * mm});
            skLineSegment(sketch, "E4347", {"start": v(-31.2, 55.5) * mm, "end": v(-31.67, 55.3) * mm});
            skLineSegment(sketch, "E4348", {"start": v(-31.67, 55.3) * mm, "end": v(-32.11, 55.08) * mm});
            skLineSegment(sketch, "E4349", {"start": v(-32.11, 55.08) * mm, "end": v(-32.52, 54.87) * mm});
            skLineSegment(sketch, "E4350", {"start": v(-32.52, 54.87) * mm, "end": v(-32.7, 54.77) * mm});
            skLineSegment(sketch, "E4351", {"start": v(-32.7, 54.77) * mm, "end": v(-32.87, 54.65) * mm});
            skLineSegment(sketch, "E4352", {"start": v(-32.87, 54.65) * mm, "end": v(-33.22, 54.37) * mm});
            skLineSegment(sketch, "E4353", {"start": v(-33.22, 54.37) * mm, "end": v(-33.56, 54.09) * mm});
            skLineSegment(sketch, "E4354", {"start": v(-33.56, 54.09) * mm, "end": v(-33.89, 53.83) * mm});
            skLineSegment(sketch, "E4355", {"start": v(-33.89, 53.83) * mm, "end": v(-34.16, 53.6) * mm});
            skLineSegment(sketch, "E4356", {"start": v(-34.16, 53.6) * mm, "end": v(-34.43, 53.4) * mm});
            skLineSegment(sketch, "E4357", {"start": v(-34.43, 53.4) * mm, "end": v(-34.67, 53.18) * mm});
            skLineSegment(sketch, "E4358", {"start": v(-34.67, 53.18) * mm, "end": v(-34.89, 52.98) * mm});
            skLineSegment(sketch, "E4359", {"start": v(-34.89, 52.98) * mm, "end": v(-35.07, 52.8) * mm});
            skLineSegment(sketch, "E4360", {"start": v(-35.07, 52.8) * mm, "end": v(-35.22, 52.64) * mm});
            skLineSegment(sketch, "E4361", {"start": v(-35.22, 52.64) * mm, "end": v(-35.32, 52.5) * mm});
            skLineSegment(sketch, "E4362", {"start": v(-35.32, 52.5) * mm, "end": v(-35.37, 52.41) * mm});
            skLineSegment(sketch, "E4363", {"start": v(-35.37, 52.41) * mm, "end": v(-35.42, 52.32) * mm});
            skLineSegment(sketch, "E4364", {"start": v(-35.42, 52.32) * mm, "end": v(-35.47, 52.22) * mm});
            skLineSegment(sketch, "E4365", {"start": v(-35.47, 52.22) * mm, "end": v(-35.5, 52.17) * mm});
            skLineSegment(sketch, "E4366", {"start": v(-35.5, 52.17) * mm, "end": v(-35.5, 52.13) * mm});
            skLineSegment(sketch, "E4367", {"start": v(-35.5, 52.13) * mm, "end": v(-35.5, 52.08) * mm});
            skLineSegment(sketch, "E4368", {"start": v(-35.5, 52.08) * mm, "end": v(-35.5, 52.04) * mm});
            skLineSegment(sketch, "E4369", {"start": v(-35.5, 52.04) * mm, "end": v(-35.47, 52) * mm});
            skLineSegment(sketch, "E4370", {"start": v(-35.47, 52) * mm, "end": v(-35.44, 51.97) * mm});
            skLineSegment(sketch, "E4371", {"start": v(-35.44, 51.97) * mm, "end": v(-35.36, 51.93) * mm});
            skLineSegment(sketch, "E4372", {"start": v(-35.36, 51.93) * mm, "end": v(-35.27, 51.9) * mm});
            skLineSegment(sketch, "E4373", {"start": v(-35.27, 51.9) * mm, "end": v(-35.16, 51.88) * mm});
            skLineSegment(sketch, "E4374", {"start": v(-35.16, 51.88) * mm, "end": v(-34.94, 51.86) * mm});
            skLineSegment(sketch, "E4375", {"start": v(-34.94, 51.86) * mm, "end": v(-34.83, 51.85) * mm});
            skLineSegment(sketch, "E4376", {"start": v(-34.83, 51.85) * mm, "end": v(-34.74, 51.83) * mm});
            skLineSegment(sketch, "E4377", {"start": v(-34.74, 51.83) * mm, "end": v(-34.53, 51.78) * mm});
            skLineSegment(sketch, "E4378", {"start": v(-34.53, 51.78) * mm, "end": v(-34.24, 51.73) * mm});
            skLineSegment(sketch, "E4379", {"start": v(-34.24, 51.73) * mm, "end": v(-33.86, 51.68) * mm});
            skLineSegment(sketch, "E4380", {"start": v(-33.86, 51.68) * mm, "end": v(-33.43, 51.63) * mm});
            skLineSegment(sketch, "E4381", {"start": v(-33.43, 51.63) * mm, "end": v(-32.43, 51.54) * mm});
            skLineSegment(sketch, "E4382", {"start": v(-32.43, 51.54) * mm, "end": v(-31.34, 51.47) * mm});
            skLineSegment(sketch, "E4383", {"start": v(-31.34, 51.47) * mm, "end": v(-30.7, 51.41) * mm});
            skLineSegment(sketch, "E4384", {"start": v(-30.7, 51.41) * mm, "end": v(-30.02, 51.35) * mm});
            skLineSegment(sketch, "E4385", {"start": v(-30.02, 51.35) * mm, "end": v(-29.68, 51.32) * mm});
            skLineSegment(sketch, "E4386", {"start": v(-29.68, 51.32) * mm, "end": v(-29.34, 51.3) * mm});
            skLineSegment(sketch, "E4387", {"start": v(-29.34, 51.3) * mm, "end": v(-29.01, 51.3) * mm});
            skLineSegment(sketch, "E4388", {"start": v(-29.01, 51.3) * mm, "end": v(-28.7, 51.32) * mm});
            skLineSegment(sketch, "E4389", {"start": v(-28.7, 51.32) * mm, "end": v(-28.56, 51.34) * mm});
            skLineSegment(sketch, "E4390", {"start": v(-28.56, 51.34) * mm, "end": v(-28.4, 51.37) * mm});
            skLineSegment(sketch, "E4391", {"start": v(-28.4, 51.37) * mm, "end": v(-28.08, 51.45) * mm});
            skLineSegment(sketch, "E4392", {"start": v(-28.08, 51.45) * mm, "end": v(-27.76, 51.55) * mm});
            skLineSegment(sketch, "E4393", {"start": v(-27.76, 51.55) * mm, "end": v(-27.46, 51.63) * mm});
            skLineSegment(sketch, "E4394", {"start": v(-27.46, 51.63) * mm, "end": v(-27.19, 51.7) * mm});
            skLineSegment(sketch, "E4395", {"start": v(-27.19, 51.7) * mm, "end": v(-26.88, 51.8) * mm});
            skLineSegment(sketch, "E4396", {"start": v(-26.88, 51.8) * mm, "end": v(-26.55, 51.92) * mm});
            skLineSegment(sketch, "E4397", {"start": v(-26.55, 51.92) * mm, "end": v(-26.21, 52.05) * mm});
            skLineSegment(sketch, "E4398", {"start": v(-26.21, 52.05) * mm, "end": v(-25.87, 52.18) * mm});
            skLineSegment(sketch, "E4399", {"start": v(-25.87, 52.18) * mm, "end": v(-25.54, 52.32) * mm});
            skLineSegment(sketch, "E4400", {"start": v(-25.54, 52.32) * mm, "end": v(-25.23, 52.46) * mm});
            skLineSegment(sketch, "E4401", {"start": v(-25.23, 52.46) * mm, "end": v(-24.95, 52.6) * mm});
            skLineSegment(sketch, "E4402", {"start": v(34.9, 52.22) * mm, "end": v(35.16, 52.5) * mm});
            skLineSegment(sketch, "E4403", {"start": v(35.16, 52.5) * mm, "end": v(33.99, 53.39) * mm});
            skLineSegment(sketch, "E4404", {"start": v(33.99, 53.39) * mm, "end": v(33.71, 53.58) * mm});
            skLineSegment(sketch, "E4405", {"start": v(33.71, 53.58) * mm, "end": v(33.38, 53.8) * mm});
            skLineSegment(sketch, "E4406", {"start": v(33.38, 53.8) * mm, "end": v(33, 54.04) * mm});
            skLineSegment(sketch, "E4407", {"start": v(33, 54.04) * mm, "end": v(32.6, 54.28) * mm});
            skLineSegment(sketch, "E4408", {"start": v(32.6, 54.28) * mm, "end": v(32.18, 54.51) * mm});
            skLineSegment(sketch, "E4409", {"start": v(32.18, 54.51) * mm, "end": v(31.75, 54.74) * mm});
            skLineSegment(sketch, "E4410", {"start": v(31.75, 54.74) * mm, "end": v(31.33, 54.96) * mm});
            skLineSegment(sketch, "E4411", {"start": v(31.33, 54.96) * mm, "end": v(30.92, 55.15) * mm});
            skLineSegment(sketch, "E4412", {"start": v(30.92, 55.15) * mm, "end": v(30.47, 55.38) * mm});
            skLineSegment(sketch, "E4413", {"start": v(30.47, 55.38) * mm, "end": v(30, 55.64) * mm});
            skLineSegment(sketch, "E4414", {"start": v(30, 55.64) * mm, "end": v(29.75, 55.76) * mm});
            skLineSegment(sketch, "E4415", {"start": v(29.75, 55.76) * mm, "end": v(29.5, 55.87) * mm});
            skLineSegment(sketch, "E4416", {"start": v(29.5, 55.87) * mm, "end": v(29.26, 55.96) * mm});
            skLineSegment(sketch, "E4417", {"start": v(29.26, 55.96) * mm, "end": v(29.03, 56.02) * mm});
            skLineSegment(sketch, "E4418", {"start": v(29.03, 56.02) * mm, "end": v(28.77, 56.08) * mm});
            skLineSegment(sketch, "E4419", {"start": v(28.77, 56.08) * mm, "end": v(28.5, 56.12) * mm});
            skLineSegment(sketch, "E4420", {"start": v(28.5, 56.12) * mm, "end": v(28.22, 56.15) * mm});
            skLineSegment(sketch, "E4421", {"start": v(28.22, 56.15) * mm, "end": v(27.93, 56.18) * mm});
            skLineSegment(sketch, "E4422", {"start": v(27.93, 56.18) * mm, "end": v(27.33, 56.22) * mm});
            skLineSegment(sketch, "E4423", {"start": v(27.33, 56.22) * mm, "end": v(26.73, 56.22) * mm});
            skLineSegment(sketch, "E4424", {"start": v(26.73, 56.22) * mm, "end": v(26.12, 56.2) * mm});
            skLineSegment(sketch, "E4425", {"start": v(26.12, 56.2) * mm, "end": v(25.52, 56.17) * mm});
            skLineSegment(sketch, "E4426", {"start": v(25.52, 56.17) * mm, "end": v(24.95, 56.12) * mm});
            skLineSegment(sketch, "E4427", {"start": v(24.95, 56.12) * mm, "end": v(24.4, 56.05) * mm});
            skLineSegment(sketch, "E4428", {"start": v(24.4, 56.05) * mm, "end": v(24.22, 56.02) * mm});
            skLineSegment(sketch, "E4429", {"start": v(24.22, 56.02) * mm, "end": v(24.03, 55.97) * mm});
            skLineSegment(sketch, "E4430", {"start": v(24.03, 55.97) * mm, "end": v(23.62, 55.85) * mm});
            skLineSegment(sketch, "E4431", {"start": v(23.62, 55.85) * mm, "end": v(23.22, 55.72) * mm});
            skLineSegment(sketch, "E4432", {"start": v(23.22, 55.72) * mm, "end": v(22.84, 55.6) * mm});
            skLineSegment(sketch, "E4433", {"start": v(22.84, 55.6) * mm, "end": v(22.53, 55.5) * mm});
            skLineSegment(sketch, "E4434", {"start": v(22.53, 55.5) * mm, "end": v(22.23, 55.4) * mm});
            skLineSegment(sketch, "E4435", {"start": v(22.23, 55.4) * mm, "end": v(21.97, 55.3) * mm});
            skLineSegment(sketch, "E4436", {"start": v(21.97, 55.3) * mm, "end": v(21.73, 55.2) * mm});
            skLineSegment(sketch, "E4437", {"start": v(21.73, 55.2) * mm, "end": v(21.54, 55.12) * mm});
            skLineSegment(sketch, "E4438", {"start": v(21.54, 55.12) * mm, "end": v(21.4, 55.03) * mm});
            skLineSegment(sketch, "E4439", {"start": v(21.4, 55.03) * mm, "end": v(21.3, 54.96) * mm});
            skLineSegment(sketch, "E4440", {"start": v(21.3, 54.96) * mm, "end": v(21.28, 54.93) * mm});
            skLineSegment(sketch, "E4441", {"start": v(21.28, 54.93) * mm, "end": v(21.27, 54.9) * mm});
            skLineSegment(sketch, "E4442", {"start": v(21.27, 54.9) * mm, "end": v(21.28, 54.86) * mm});
            skLineSegment(sketch, "E4443", {"start": v(21.28, 54.86) * mm, "end": v(21.3, 54.82) * mm});
            skLineSegment(sketch, "E4444", {"start": v(21.3, 54.82) * mm, "end": v(21.38, 54.71) * mm});
            skLineSegment(sketch, "E4445", {"start": v(21.38, 54.71) * mm, "end": v(21.5, 54.59) * mm});
            skLineSegment(sketch, "E4446", {"start": v(21.5, 54.59) * mm, "end": v(21.66, 54.44) * mm});
            skLineSegment(sketch, "E4447", {"start": v(21.66, 54.44) * mm, "end": v(21.86, 54.28) * mm});
            skLineSegment(sketch, "E4448", {"start": v(21.86, 54.28) * mm, "end": v(22.1, 54.1) * mm});
            skLineSegment(sketch, "E4449", {"start": v(22.1, 54.1) * mm, "end": v(22.36, 53.92) * mm});
            skLineSegment(sketch, "E4450", {"start": v(22.36, 53.92) * mm, "end": v(22.65, 53.72) * mm});
            skLineSegment(sketch, "E4451", {"start": v(22.65, 53.72) * mm, "end": v(23.3, 53.33) * mm});
            skLineSegment(sketch, "E4452", {"start": v(23.3, 53.33) * mm, "end": v(23.98, 52.93) * mm});
            skLineSegment(sketch, "E4453", {"start": v(23.98, 52.93) * mm, "end": v(24.34, 52.74) * mm});
            skLineSegment(sketch, "E4454", {"start": v(24.34, 52.74) * mm, "end": v(24.7, 52.55) * mm});
            skLineSegment(sketch, "E4455", {"start": v(24.7, 52.55) * mm, "end": v(25.05, 52.38) * mm});
            skLineSegment(sketch, "E4456", {"start": v(25.05, 52.38) * mm, "end": v(25.4, 52.22) * mm});
            skLineSegment(sketch, "E4457", {"start": v(25.4, 52.22) * mm, "end": v(25.8, 52.03) * mm});
            skLineSegment(sketch, "E4458", {"start": v(25.8, 52.03) * mm, "end": v(26.21, 51.82) * mm});
            skLineSegment(sketch, "E4459", {"start": v(26.21, 51.82) * mm, "end": v(26.43, 51.72) * mm});
            skLineSegment(sketch, "E4460", {"start": v(26.43, 51.72) * mm, "end": v(26.64, 51.62) * mm});
            skLineSegment(sketch, "E4461", {"start": v(26.64, 51.62) * mm, "end": v(26.85, 51.55) * mm});
            skLineSegment(sketch, "E4462", {"start": v(26.85, 51.55) * mm, "end": v(27.05, 51.49) * mm});
            skLineSegment(sketch, "E4463", {"start": v(27.05, 51.49) * mm, "end": v(27.33, 51.43) * mm});
            skLineSegment(sketch, "E4464", {"start": v(27.33, 51.43) * mm, "end": v(27.62, 51.38) * mm});
            skLineSegment(sketch, "E4465", {"start": v(27.62, 51.38) * mm, "end": v(27.92, 51.33) * mm});
            skLineSegment(sketch, "E4466", {"start": v(27.92, 51.33) * mm, "end": v(28.22, 51.3) * mm});
            skLineSegment(sketch, "E4467", {"start": v(28.22, 51.3) * mm, "end": v(28.86, 51.24) * mm});
            skLineSegment(sketch, "E4468", {"start": v(28.86, 51.24) * mm, "end": v(29.51, 51.21) * mm});
            skLineSegment(sketch, "E4469", {"start": v(29.51, 51.21) * mm, "end": v(30.16, 51.2) * mm});
            skLineSegment(sketch, "E4470", {"start": v(30.16, 51.2) * mm, "end": v(30.8, 51.22) * mm});
            skLineSegment(sketch, "E4471", {"start": v(30.8, 51.22) * mm, "end": v(31.42, 51.25) * mm});
            skLineSegment(sketch, "E4472", {"start": v(31.42, 51.25) * mm, "end": v(32, 51.3) * mm});
            skLineSegment(sketch, "E4473", {"start": v(32, 51.3) * mm, "end": v(32.15, 51.32) * mm});
            skLineSegment(sketch, "E4474", {"start": v(32.15, 51.32) * mm, "end": v(32.32, 51.35) * mm});
            skLineSegment(sketch, "E4475", {"start": v(32.32, 51.35) * mm, "end": v(32.66, 51.44) * mm});
            skLineSegment(sketch, "E4476", {"start": v(32.66, 51.44) * mm, "end": v(33, 51.54) * mm});
            skLineSegment(sketch, "E4477", {"start": v(33, 51.54) * mm, "end": v(33.31, 51.63) * mm});
            skLineSegment(sketch, "E4478", {"start": v(33.31, 51.63) * mm, "end": v(33.84, 51.77) * mm});
            skLineSegment(sketch, "E4479", {"start": v(33.84, 51.77) * mm, "end": v(34.32, 51.94) * mm});
            skLineSegment(sketch, "E4480", {"start": v(34.32, 51.94) * mm, "end": v(34.52, 52.02) * mm});
            skLineSegment(sketch, "E4481", {"start": v(34.52, 52.02) * mm, "end": v(34.69, 52.1) * mm});
            skLineSegment(sketch, "E4482", {"start": v(34.69, 52.1) * mm, "end": v(34.81, 52.16) * mm});
            skLineSegment(sketch, "E4483", {"start": v(34.81, 52.16) * mm, "end": v(34.9, 52.22) * mm});
            skLineSegment(sketch, "E4484", {"start": v(-34.88, 55.7) * mm, "end": v(-34.57, 55.9) * mm});
            skLineSegment(sketch, "E4485", {"start": v(-34.57, 55.9) * mm, "end": v(-34.23, 56.16) * mm});
            skLineSegment(sketch, "E4486", {"start": v(-34.23, 56.16) * mm, "end": v(-33.87, 56.43) * mm});
            skLineSegment(sketch, "E4487", {"start": v(-33.87, 56.43) * mm, "end": v(-33.5, 56.73) * mm});
            skLineSegment(sketch, "E4488", {"start": v(-33.5, 56.73) * mm, "end": v(-33.13, 57.04) * mm});
            skLineSegment(sketch, "E4489", {"start": v(-33.13, 57.04) * mm, "end": v(-32.78, 57.35) * mm});
            skLineSegment(sketch, "E4490", {"start": v(-32.78, 57.35) * mm, "end": v(-32.45, 57.66) * mm});
            skLineSegment(sketch, "E4491", {"start": v(-32.45, 57.66) * mm, "end": v(-32.16, 57.94) * mm});
            skLineSegment(sketch, "E4492", {"start": v(-32.16, 57.94) * mm, "end": v(-31.84, 58.26) * mm});
            skLineSegment(sketch, "E4493", {"start": v(-31.84, 58.26) * mm, "end": v(-31.48, 58.6) * mm});
            skLineSegment(sketch, "E4494", {"start": v(-31.48, 58.6) * mm, "end": v(-31.3, 58.77) * mm});
            skLineSegment(sketch, "E4495", {"start": v(-31.3, 58.77) * mm, "end": v(-31.14, 58.94) * mm});
            skLineSegment(sketch, "E4496", {"start": v(-31.14, 58.94) * mm, "end": v(-30.99, 59.12) * mm});
            skLineSegment(sketch, "E4497", {"start": v(-30.99, 59.12) * mm, "end": v(-30.85, 59.3) * mm});
            skLineSegment(sketch, "E4498", {"start": v(-30.85, 59.3) * mm, "end": v(-30.54, 59.74) * mm});
            skLineSegment(sketch, "E4499", {"start": v(-30.54, 59.74) * mm, "end": v(-30.22, 60.22) * mm});
            skLineSegment(sketch, "E4500", {"start": v(-30.22, 60.22) * mm, "end": v(-29.9, 60.74) * mm});
            skLineSegment(sketch, "E4501", {"start": v(-29.9, 60.74) * mm, "end": v(-29.6, 61.28) * mm});
            skLineSegment(sketch, "E4502", {"start": v(-29.6, 61.28) * mm, "end": v(-29.46, 61.55) * mm});
            skLineSegment(sketch, "E4503", {"start": v(-29.46, 61.55) * mm, "end": v(-29.32, 61.82) * mm});
            skLineSegment(sketch, "E4504", {"start": v(-29.32, 61.82) * mm, "end": v(-29.2, 62.1) * mm});
            skLineSegment(sketch, "E4505", {"start": v(-29.2, 62.1) * mm, "end": v(-29.1, 62.37) * mm});
            skLineSegment(sketch, "E4506", {"start": v(-29.1, 62.37) * mm, "end": v(-29, 62.65) * mm});
            skLineSegment(sketch, "E4507", {"start": v(-29, 62.65) * mm, "end": v(-28.92, 62.92) * mm});
            skLineSegment(sketch, "E4508", {"start": v(-28.92, 62.92) * mm, "end": v(-28.85, 63.18) * mm});
            skLineSegment(sketch, "E4509", {"start": v(-28.85, 63.18) * mm, "end": v(-28.8, 63.44) * mm});
            skLineSegment(sketch, "E4510", {"start": v(-28.8, 63.44) * mm, "end": v(-28.8, 63.58) * mm});
            skLineSegment(sketch, "E4511", {"start": v(-28.8, 63.58) * mm, "end": v(-28.78, 63.73) * mm});
            skLineSegment(sketch, "E4512", {"start": v(-28.78, 63.73) * mm, "end": v(-28.78, 63.87) * mm});
            skLineSegment(sketch, "E4513", {"start": v(-28.78, 63.87) * mm, "end": v(-28.8, 64) * mm});
            skLineSegment(sketch, "E4514", {"start": v(-28.8, 64) * mm, "end": v(-28.83, 64.14) * mm});
            skLineSegment(sketch, "E4515", {"start": v(-28.83, 64.14) * mm, "end": v(-28.88, 64.26) * mm});
            skLineSegment(sketch, "E4516", {"start": v(-28.88, 64.26) * mm, "end": v(-28.95, 64.37) * mm});
            skLineSegment(sketch, "E4517", {"start": v(-28.95, 64.37) * mm, "end": v(-29, 64.42) * mm});
            skLineSegment(sketch, "E4518", {"start": v(-29, 64.42) * mm, "end": v(-29.05, 64.46) * mm});
            skLineSegment(sketch, "E4519", {"start": v(-29.05, 64.46) * mm, "end": v(-29.19, 64.55) * mm});
            skLineSegment(sketch, "E4520", {"start": v(-29.19, 64.55) * mm, "end": v(-29.34, 64.63) * mm});
            skLineSegment(sketch, "E4521", {"start": v(-29.34, 64.63) * mm, "end": v(-29.5, 64.68) * mm});
            skLineSegment(sketch, "E4522", {"start": v(-29.5, 64.68) * mm, "end": v(-29.69, 64.72) * mm});
            skLineSegment(sketch, "E4523", {"start": v(-29.69, 64.72) * mm, "end": v(-29.87, 64.75) * mm});
            skLineSegment(sketch, "E4524", {"start": v(-29.87, 64.75) * mm, "end": v(-30.07, 64.76) * mm});
            skLineSegment(sketch, "E4525", {"start": v(-30.07, 64.76) * mm, "end": v(-30.27, 64.76) * mm});
            skLineSegment(sketch, "E4526", {"start": v(-30.27, 64.76) * mm, "end": v(-30.47, 64.75) * mm});
            skLineSegment(sketch, "E4527", {"start": v(-30.47, 64.75) * mm, "end": v(-30.88, 64.7) * mm});
            skLineSegment(sketch, "E4528", {"start": v(-30.88, 64.7) * mm, "end": v(-31.28, 64.64) * mm});
            skLineSegment(sketch, "E4529", {"start": v(-31.28, 64.64) * mm, "end": v(-31.66, 64.55) * mm});
            skLineSegment(sketch, "E4530", {"start": v(-31.66, 64.55) * mm, "end": v(-32, 64.46) * mm});
            skLineSegment(sketch, "E4531", {"start": v(-32, 64.46) * mm, "end": v(-32.3, 64.38) * mm});
            skLineSegment(sketch, "E4532", {"start": v(-32.3, 64.38) * mm, "end": v(-32.6, 64.29) * mm});
            skLineSegment(sketch, "E4533", {"start": v(-32.6, 64.29) * mm, "end": v(-33.23, 64.07) * mm});
            skLineSegment(sketch, "E4534", {"start": v(-33.23, 64.07) * mm, "end": v(-33.87, 63.82) * mm});
            skLineSegment(sketch, "E4535", {"start": v(-33.87, 63.82) * mm, "end": v(-34.19, 63.68) * mm});
            skLineSegment(sketch, "E4536", {"start": v(-34.19, 63.68) * mm, "end": v(-34.5, 63.53) * mm});
            skLineSegment(sketch, "E4537", {"start": v(-34.5, 63.53) * mm, "end": v(-34.82, 63.38) * mm});
            skLineSegment(sketch, "E4538", {"start": v(-34.82, 63.38) * mm, "end": v(-35.13, 63.22) * mm});
            skLineSegment(sketch, "E4539", {"start": v(-35.13, 63.22) * mm, "end": v(-35.44, 63.05) * mm});
            skLineSegment(sketch, "E4540", {"start": v(-35.44, 63.05) * mm, "end": v(-35.73, 62.88) * mm});
            skLineSegment(sketch, "E4541", {"start": v(-35.73, 62.88) * mm, "end": v(-36.02, 62.7) * mm});
            skLineSegment(sketch, "E4542", {"start": v(-36.02, 62.7) * mm, "end": v(-36.29, 62.52) * mm});
            skLineSegment(sketch, "E4543", {"start": v(-36.29, 62.52) * mm, "end": v(-36.54, 62.34) * mm});
            skLineSegment(sketch, "E4544", {"start": v(-36.54, 62.34) * mm, "end": v(-36.78, 62.15) * mm});
            skLineSegment(sketch, "E4545", {"start": v(-36.78, 62.15) * mm, "end": v(-36.95, 62) * mm});
            skLineSegment(sketch, "E4546", {"start": v(-36.95, 62) * mm, "end": v(-37.12, 61.86) * mm});
            skLineSegment(sketch, "E4547", {"start": v(-37.12, 61.86) * mm, "end": v(-37.45, 61.52) * mm});
            skLineSegment(sketch, "E4548", {"start": v(-37.45, 61.52) * mm, "end": v(-37.77, 61.14) * mm});
            skLineSegment(sketch, "E4549", {"start": v(-37.77, 61.14) * mm, "end": v(-38.08, 60.75) * mm});
            skLineSegment(sketch, "E4550", {"start": v(-38.08, 60.75) * mm, "end": v(-38.38, 60.34) * mm});
            skLineSegment(sketch, "E4551", {"start": v(-38.38, 60.34) * mm, "end": v(-38.65, 59.93) * mm});
            skLineSegment(sketch, "E4552", {"start": v(-38.65, 59.93) * mm, "end": v(-38.89, 59.52) * mm});
            skLineSegment(sketch, "E4553", {"start": v(-38.89, 59.52) * mm, "end": v(-39.1, 59.12) * mm});
            skLineSegment(sketch, "E4554", {"start": v(-39.1, 59.12) * mm, "end": v(-39.16, 58.98) * mm});
            skLineSegment(sketch, "E4555", {"start": v(-39.16, 58.98) * mm, "end": v(-39.2, 58.84) * mm});
            skLineSegment(sketch, "E4556", {"start": v(-39.2, 58.84) * mm, "end": v(-39.29, 58.52) * mm});
            skLineSegment(sketch, "E4557", {"start": v(-39.29, 58.52) * mm, "end": v(-39.36, 58.2) * mm});
            skLineSegment(sketch, "E4558", {"start": v(-39.36, 58.2) * mm, "end": v(-39.43, 57.9) * mm});
            skLineSegment(sketch, "E4559", {"start": v(-39.43, 57.9) * mm, "end": v(-39.57, 57.3) * mm});
            skLineSegment(sketch, "E4560", {"start": v(-39.57, 57.3) * mm, "end": v(-39.72, 56.58) * mm});
            skLineSegment(sketch, "E4561", {"start": v(-39.72, 56.58) * mm, "end": v(-39.86, 55.83) * mm});
            skLineSegment(sketch, "E4562", {"start": v(-39.86, 55.83) * mm, "end": v(-39.97, 55.14) * mm});
            skLineSegment(sketch, "E4563", {"start": v(-39.97, 55.14) * mm, "end": v(-40, 54.96) * mm});
            skLineSegment(sketch, "E4564", {"start": v(-40, 54.96) * mm, "end": v(-40.07, 54.75) * mm});
            skLineSegment(sketch, "E4565", {"start": v(-40.07, 54.75) * mm, "end": v(-40.14, 54.54) * mm});
            skLineSegment(sketch, "E4566", {"start": v(-40.14, 54.54) * mm, "end": v(-40.21, 54.33) * mm});
            skLineSegment(sketch, "E4567", {"start": v(-40.21, 54.33) * mm, "end": v(-40.26, 54.12) * mm});
            skLineSegment(sketch, "E4568", {"start": v(-40.26, 54.12) * mm, "end": v(-40.28, 54.02) * mm});
            skLineSegment(sketch, "E4569", {"start": v(-40.28, 54.02) * mm, "end": v(-40.28, 53.93) * mm});
            skLineSegment(sketch, "E4570", {"start": v(-40.28, 53.93) * mm, "end": v(-40.28, 53.84) * mm});
            skLineSegment(sketch, "E4571", {"start": v(-40.28, 53.84) * mm, "end": v(-40.26, 53.75) * mm});
            skLineSegment(sketch, "E4572", {"start": v(-40.26, 53.75) * mm, "end": v(-40.23, 53.67) * mm});
            skLineSegment(sketch, "E4573", {"start": v(-40.23, 53.67) * mm, "end": v(-40.18, 53.6) * mm});
            skLineSegment(sketch, "E4574", {"start": v(-40.18, 53.6) * mm, "end": v(-40.13, 53.57) * mm});
            skLineSegment(sketch, "E4575", {"start": v(-40.13, 53.57) * mm, "end": v(-40.08, 53.55) * mm});
            skLineSegment(sketch, "E4576", {"start": v(-40.08, 53.55) * mm, "end": v(-39.94, 53.54) * mm});
            skLineSegment(sketch, "E4577", {"start": v(-39.94, 53.54) * mm, "end": v(-39.79, 53.55) * mm});
            skLineSegment(sketch, "E4578", {"start": v(-39.79, 53.55) * mm, "end": v(-39.66, 53.57) * mm});
            skLineSegment(sketch, "E4579", {"start": v(-39.66, 53.57) * mm, "end": v(-39.5, 53.6) * mm});
            skLineSegment(sketch, "E4580", {"start": v(-39.5, 53.6) * mm, "end": v(-39.29, 53.66) * mm});
            skLineSegment(sketch, "E4581", {"start": v(-39.29, 53.66) * mm, "end": v(-38.79, 53.83) * mm});
            skLineSegment(sketch, "E4582", {"start": v(-38.79, 53.83) * mm, "end": v(-38.2, 54.05) * mm});
            skLineSegment(sketch, "E4583", {"start": v(-38.2, 54.05) * mm, "end": v(-37.53, 54.33) * mm});
            skLineSegment(sketch, "E4584", {"start": v(-37.53, 54.33) * mm, "end": v(-36.84, 54.65) * mm});
            skLineSegment(sketch, "E4585", {"start": v(-36.84, 54.65) * mm, "end": v(-36.14, 54.99) * mm});
            skLineSegment(sketch, "E4586", {"start": v(-36.14, 54.99) * mm, "end": v(-35.48, 55.34) * mm});
            skLineSegment(sketch, "E4587", {"start": v(-35.48, 55.34) * mm, "end": v(-35.17, 55.52) * mm});
            skLineSegment(sketch, "E4588", {"start": v(-35.17, 55.52) * mm, "end": v(-34.88, 55.7) * mm});
            skLineSegment(sketch, "E4589", {"start": v(38.97, 56.08) * mm, "end": v(38.76, 56.82) * mm});
            skLineSegment(sketch, "E4590", {"start": v(38.76, 56.82) * mm, "end": v(38.5, 57.6) * mm});
            skLineSegment(sketch, "E4591", {"start": v(38.5, 57.6) * mm, "end": v(38.24, 58.33) * mm});
            skLineSegment(sketch, "E4592", {"start": v(38.24, 58.33) * mm, "end": v(38.11, 58.66) * mm});
            skLineSegment(sketch, "E4593", {"start": v(38.11, 58.66) * mm, "end": v(38, 58.93) * mm});
            skLineSegment(sketch, "E4594", {"start": v(38, 58.93) * mm, "end": v(37.88, 59.22) * mm});
            skLineSegment(sketch, "E4595", {"start": v(37.88, 59.22) * mm, "end": v(37.77, 59.55) * mm});
            skLineSegment(sketch, "E4596", {"start": v(37.77, 59.55) * mm, "end": v(37.7, 59.7) * mm});
            skLineSegment(sketch, "E4597", {"start": v(37.7, 59.7) * mm, "end": v(37.64, 59.86) * mm});
            skLineSegment(sketch, "E4598", {"start": v(37.64, 59.86) * mm, "end": v(37.56, 60) * mm});
            skLineSegment(sketch, "E4599", {"start": v(37.56, 60) * mm, "end": v(37.48, 60.13) * mm});
            skLineSegment(sketch, "E4600", {"start": v(37.48, 60.13) * mm, "end": v(37.34, 60.3) * mm});
            skLineSegment(sketch, "E4601", {"start": v(37.34, 60.3) * mm, "end": v(37.2, 60.5) * mm});
            skLineSegment(sketch, "E4602", {"start": v(37.2, 60.5) * mm, "end": v(36.86, 60.86) * mm});
            skLineSegment(sketch, "E4603", {"start": v(36.86, 60.86) * mm, "end": v(36.5, 61.22) * mm});
            skLineSegment(sketch, "E4604", {"start": v(36.5, 61.22) * mm, "end": v(36.11, 61.57) * mm});
            skLineSegment(sketch, "E4605", {"start": v(36.11, 61.57) * mm, "end": v(35.7, 61.9) * mm});
            skLineSegment(sketch, "E4606", {"start": v(35.7, 61.9) * mm, "end": v(35.3, 62.21) * mm});
            skLineSegment(sketch, "E4607", {"start": v(35.3, 62.21) * mm, "end": v(34.9, 62.5) * mm});
            skLineSegment(sketch, "E4608", {"start": v(34.9, 62.5) * mm, "end": v(34.5, 62.75) * mm});
            skLineSegment(sketch, "E4609", {"start": v(34.5, 62.75) * mm, "end": v(34.3, 62.86) * mm});
            skLineSegment(sketch, "E4610", {"start": v(34.3, 62.86) * mm, "end": v(34.07, 62.96) * mm});
            skLineSegment(sketch, "E4611", {"start": v(34.07, 62.96) * mm, "end": v(33.58, 63.15) * mm});
            skLineSegment(sketch, "E4612", {"start": v(33.58, 63.15) * mm, "end": v(33.07, 63.31) * mm});
            skLineSegment(sketch, "E4613", {"start": v(33.07, 63.31) * mm, "end": v(32.61, 63.47) * mm});
            skLineSegment(sketch, "E4614", {"start": v(32.61, 63.47) * mm, "end": v(32.2, 63.62) * mm});
            skLineSegment(sketch, "E4615", {"start": v(32.2, 63.62) * mm, "end": v(31.76, 63.77) * mm});
            skLineSegment(sketch, "E4616", {"start": v(31.76, 63.77) * mm, "end": v(31.3, 63.9) * mm});
            skLineSegment(sketch, "E4617", {"start": v(31.3, 63.9) * mm, "end": v(30.86, 64.04) * mm});
            skLineSegment(sketch, "E4618", {"start": v(30.86, 64.04) * mm, "end": v(30.41, 64.16) * mm});
            skLineSegment(sketch, "E4619", {"start": v(30.41, 64.16) * mm, "end": v(30, 64.26) * mm});
            skLineSegment(sketch, "E4620", {"start": v(30, 64.26) * mm, "end": v(29.62, 64.34) * mm});
            skLineSegment(sketch, "E4621", {"start": v(29.62, 64.34) * mm, "end": v(29.3, 64.4) * mm});
            skLineSegment(sketch, "E4622", {"start": v(29.3, 64.4) * mm, "end": v(27.89, 64.58) * mm});
            skLineSegment(sketch, "E4623", {"start": v(27.89, 64.58) * mm, "end": v(27.89, 64.01) * mm});
            skLineSegment(sketch, "E4624", {"start": v(27.89, 64.01) * mm, "end": v(27.9, 63.84) * mm});
            skLineSegment(sketch, "E4625", {"start": v(27.9, 63.84) * mm, "end": v(27.93, 63.65) * mm});
            skLineSegment(sketch, "E4626", {"start": v(27.93, 63.65) * mm, "end": v(27.98, 63.44) * mm});
            skLineSegment(sketch, "E4627", {"start": v(27.98, 63.44) * mm, "end": v(28.05, 63.2) * mm});
            skLineSegment(sketch, "E4628", {"start": v(28.05, 63.2) * mm, "end": v(28.15, 62.95) * mm});
            skLineSegment(sketch, "E4629", {"start": v(28.15, 62.95) * mm, "end": v(28.25, 62.68) * mm});
            skLineSegment(sketch, "E4630", {"start": v(28.25, 62.68) * mm, "end": v(28.38, 62.4) * mm});
            skLineSegment(sketch, "E4631", {"start": v(28.38, 62.4) * mm, "end": v(28.52, 62.1) * mm});
            skLineSegment(sketch, "E4632", {"start": v(28.52, 62.1) * mm, "end": v(28.68, 61.79) * mm});
            skLineSegment(sketch, "E4633", {"start": v(28.68, 61.79) * mm, "end": v(28.85, 61.47) * mm});
            skLineSegment(sketch, "E4634", {"start": v(28.85, 61.47) * mm, "end": v(29.03, 61.14) * mm});
            skLineSegment(sketch, "E4635", {"start": v(29.03, 61.14) * mm, "end": v(29.23, 60.8) * mm});
            skLineSegment(sketch, "E4636", {"start": v(29.23, 60.8) * mm, "end": v(29.44, 60.47) * mm});
            skLineSegment(sketch, "E4637", {"start": v(29.44, 60.47) * mm, "end": v(29.66, 60.13) * mm});
            skLineSegment(sketch, "E4638", {"start": v(29.66, 60.13) * mm, "end": v(29.88, 59.8) * mm});
            skLineSegment(sketch, "E4639", {"start": v(29.88, 59.8) * mm, "end": v(30.12, 59.46) * mm});
            skLineSegment(sketch, "E4640", {"start": v(30.12, 59.46) * mm, "end": v(30.38, 59.07) * mm});
            skLineSegment(sketch, "E4641", {"start": v(30.38, 59.07) * mm, "end": v(30.66, 58.65) * mm});
            skLineSegment(sketch, "E4642", {"start": v(30.66, 58.65) * mm, "end": v(30.8, 58.44) * mm});
            skLineSegment(sketch, "E4643", {"start": v(30.8, 58.44) * mm, "end": v(30.95, 58.23) * mm});
            skLineSegment(sketch, "E4644", {"start": v(30.95, 58.23) * mm, "end": v(31.1, 58.05) * mm});
            skLineSegment(sketch, "E4645", {"start": v(31.1, 58.05) * mm, "end": v(31.25, 57.88) * mm});
            skLineSegment(sketch, "E4646", {"start": v(31.25, 57.88) * mm, "end": v(31.46, 57.68) * mm});
            skLineSegment(sketch, "E4647", {"start": v(31.46, 57.68) * mm, "end": v(31.69, 57.47) * mm});
            skLineSegment(sketch, "E4648", {"start": v(31.69, 57.47) * mm, "end": v(32.17, 57.06) * mm});
            skLineSegment(sketch, "E4649", {"start": v(32.17, 57.06) * mm, "end": v(32.69, 56.65) * mm});
            skLineSegment(sketch, "E4650", {"start": v(32.69, 56.65) * mm, "end": v(33.23, 56.25) * mm});
            skLineSegment(sketch, "E4651", {"start": v(33.23, 56.25) * mm, "end": v(33.79, 55.87) * mm});
            skLineSegment(sketch, "E4652", {"start": v(33.79, 55.87) * mm, "end": v(34.34, 55.52) * mm});
            skLineSegment(sketch, "E4653", {"start": v(34.34, 55.52) * mm, "end": v(34.9, 55.2) * mm});
            skLineSegment(sketch, "E4654", {"start": v(34.9, 55.2) * mm, "end": v(35.42, 54.91) * mm});
            skLineSegment(sketch, "E4655", {"start": v(35.42, 54.91) * mm, "end": v(35.63, 54.81) * mm});
            skLineSegment(sketch, "E4656", {"start": v(35.63, 54.81) * mm, "end": v(35.86, 54.72) * mm});
            skLineSegment(sketch, "E4657", {"start": v(35.86, 54.72) * mm, "end": v(36.35, 54.55) * mm});
            skLineSegment(sketch, "E4658", {"start": v(36.35, 54.55) * mm, "end": v(36.85, 54.4) * mm});
            skLineSegment(sketch, "E4659", {"start": v(36.85, 54.4) * mm, "end": v(37.31, 54.26) * mm});
            skLineSegment(sketch, "E4660", {"start": v(37.31, 54.26) * mm, "end": v(38.69, 53.8) * mm});
            skLineSegment(sketch, "E4661", {"start": v(38.69, 53.8) * mm, "end": v(39.13, 53.66) * mm});
            skLineSegment(sketch, "E4662", {"start": v(39.13, 53.66) * mm, "end": v(39.32, 53.6) * mm});
            skLineSegment(sketch, "E4663", {"start": v(39.32, 53.6) * mm, "end": v(39.36, 53.62) * mm});
            skLineSegment(sketch, "E4664", {"start": v(39.36, 53.62) * mm, "end": v(39.39, 53.65) * mm});
            skLineSegment(sketch, "E4665", {"start": v(39.39, 53.65) * mm, "end": v(39.41, 53.7) * mm});
            skLineSegment(sketch, "E4666", {"start": v(39.41, 53.7) * mm, "end": v(39.42, 53.76) * mm});
            skLineSegment(sketch, "E4667", {"start": v(39.42, 53.76) * mm, "end": v(39.43, 53.85) * mm});
            skLineSegment(sketch, "E4668", {"start": v(39.43, 53.85) * mm, "end": v(39.43, 53.96) * mm});
            skLineSegment(sketch, "E4669", {"start": v(39.43, 53.96) * mm, "end": v(39.4, 54.23) * mm});
            skLineSegment(sketch, "E4670", {"start": v(39.4, 54.23) * mm, "end": v(39.34, 54.58) * mm});
            skLineSegment(sketch, "E4671", {"start": v(39.34, 54.58) * mm, "end": v(39.25, 55) * mm});
            skLineSegment(sketch, "E4672", {"start": v(39.25, 55) * mm, "end": v(39.13, 55.5) * mm});
            skLineSegment(sketch, "E4673", {"start": v(39.13, 55.5) * mm, "end": v(38.97, 56.08) * mm});
            skLineSegment(sketch, "E4674", {"start": v(-72.69, -10.66) * mm, "end": v(-72.68, -10.29) * mm});
            skLineSegment(sketch, "E4675", {"start": v(-72.68, -10.29) * mm, "end": v(-72.65, -9.88) * mm});
            skLineSegment(sketch, "E4676", {"start": v(-72.65, -9.88) * mm, "end": v(-72.61, -9.44) * mm});
            skLineSegment(sketch, "E4677", {"start": v(-72.61, -9.44) * mm, "end": v(-72.56, -8.98) * mm});
            skLineSegment(sketch, "E4678", {"start": v(-72.56, -8.98) * mm, "end": v(-72.43, -8.01) * mm});
            skLineSegment(sketch, "E4679", {"start": v(-72.43, -8.01) * mm, "end": v(-72.37, -7.53) * mm});
            skLineSegment(sketch, "E4680", {"start": v(-72.37, -7.53) * mm, "end": v(-72.32, -7.05) * mm});
            skLineSegment(sketch, "E4681", {"start": v(-72.32, -7.05) * mm, "end": v(-72.28, -6.6) * mm});
            skLineSegment(sketch, "E4682", {"start": v(-72.28, -6.6) * mm, "end": v(-72.26, -6.16) * mm});
            skLineSegment(sketch, "E4683", {"start": v(-72.26, -6.16) * mm, "end": v(-72.27, -5.75) * mm});
            skLineSegment(sketch, "E4684", {"start": v(-72.27, -5.75) * mm, "end": v(-72.28, -5.56) * mm});
            skLineSegment(sketch, "E4685", {"start": v(-72.28, -5.56) * mm, "end": v(-72.3, -5.38) * mm});
            skLineSegment(sketch, "E4686", {"start": v(-72.3, -5.38) * mm, "end": v(-72.33, -5.22) * mm});
            skLineSegment(sketch, "E4687", {"start": v(-72.33, -5.22) * mm, "end": v(-72.37, -5.07) * mm});
            skLineSegment(sketch, "E4688", {"start": v(-72.37, -5.07) * mm, "end": v(-72.42, -4.93) * mm});
            skLineSegment(sketch, "E4689", {"start": v(-72.42, -4.93) * mm, "end": v(-72.48, -4.8) * mm});
            skLineSegment(sketch, "E4690", {"start": v(-72.48, -4.8) * mm, "end": v(-72.55, -4.7) * mm});
            skLineSegment(sketch, "E4691", {"start": v(-72.55, -4.7) * mm, "end": v(-72.63, -4.6) * mm});
            skLineSegment(sketch, "E4692", {"start": v(-72.63, -4.6) * mm, "end": v(-72.72, -4.53) * mm});
            skLineSegment(sketch, "E4693", {"start": v(-72.72, -4.53) * mm, "end": v(-72.83, -4.47) * mm});
            skLineSegment(sketch, "E4694", {"start": v(-72.83, -4.47) * mm, "end": v(-73.21, -4.28) * mm});
            skLineSegment(sketch, "E4695", {"start": v(-73.21, -4.28) * mm, "end": v(-73.93, -3.88) * mm});
            skLineSegment(sketch, "E4696", {"start": v(-73.93, -3.88) * mm, "end": v(-74.9, -3.32) * mm});
            skLineSegment(sketch, "E4697", {"start": v(-74.9, -3.32) * mm, "end": v(-76.02, -2.65) * mm});
            skLineSegment(sketch, "E4698", {"start": v(-76.02, -2.65) * mm, "end": v(-76.61, -2.29) * mm});
            skLineSegment(sketch, "E4699", {"start": v(-76.61, -2.29) * mm, "end": v(-77.2, -1.9) * mm});
            skLineSegment(sketch, "E4700", {"start": v(-77.2, -1.9) * mm, "end": v(-77.79, -1.52) * mm});
            skLineSegment(sketch, "E4701", {"start": v(-77.79, -1.52) * mm, "end": v(-78.35, -1.14) * mm});
            skLineSegment(sketch, "E4702", {"start": v(-78.35, -1.14) * mm, "end": v(-78.89, -0.75) * mm});
            skLineSegment(sketch, "E4703", {"start": v(-78.89, -0.75) * mm, "end": v(-79.38, -0.38) * mm});
            skLineSegment(sketch, "E4704", {"start": v(-79.38, -0.38) * mm, "end": v(-79.81, -0.02) * mm});
            skLineSegment(sketch, "E4705", {"start": v(-79.81, -0.02) * mm, "end": v(-80, 0.15) * mm});
            skLineSegment(sketch, "E4706", {"start": v(-80, 0.15) * mm, "end": v(-80.18, 0.31) * mm});
            skLineSegment(sketch, "E4707", {"start": v(-80.18, 0.31) * mm, "end": v(-80.47, 0.62) * mm});
            skLineSegment(sketch, "E4708", {"start": v(-80.47, 0.62) * mm, "end": v(-80.75, 0.95) * mm});
            skLineSegment(sketch, "E4709", {"start": v(-80.75, 0.95) * mm, "end": v(-81.03, 1.3) * mm});
            skLineSegment(sketch, "E4710", {"start": v(-81.03, 1.3) * mm, "end": v(-81.3, 1.68) * mm});
            skLineSegment(sketch, "E4711", {"start": v(-81.3, 1.68) * mm, "end": v(-81.84, 2.47) * mm});
            skLineSegment(sketch, "E4712", {"start": v(-81.84, 2.47) * mm, "end": v(-82.39, 3.28) * mm});
            skLineSegment(sketch, "E4713", {"start": v(-82.39, 3.28) * mm, "end": v(-82.67, 3.69) * mm});
            skLineSegment(sketch, "E4714", {"start": v(-82.67, 3.69) * mm, "end": v(-82.95, 4.08) * mm});
            skLineSegment(sketch, "E4715", {"start": v(-82.95, 4.08) * mm, "end": v(-83.24, 4.45) * mm});
            skLineSegment(sketch, "E4716", {"start": v(-83.24, 4.45) * mm, "end": v(-83.53, 4.81) * mm});
            skLineSegment(sketch, "E4717", {"start": v(-83.53, 4.81) * mm, "end": v(-83.84, 5.15) * mm});
            skLineSegment(sketch, "E4718", {"start": v(-83.84, 5.15) * mm, "end": v(-84, 5.3) * mm});
            skLineSegment(sketch, "E4719", {"start": v(-84, 5.3) * mm, "end": v(-84.16, 5.45) * mm});
            skLineSegment(sketch, "E4720", {"start": v(-84.16, 5.45) * mm, "end": v(-84.32, 5.6) * mm});
            skLineSegment(sketch, "E4721", {"start": v(-84.32, 5.6) * mm, "end": v(-84.49, 5.72) * mm});
            skLineSegment(sketch, "E4722", {"start": v(-84.49, 5.72) * mm, "end": v(-84.66, 5.84) * mm});
            skLineSegment(sketch, "E4723", {"start": v(-84.66, 5.84) * mm, "end": v(-84.83, 5.95) * mm});
            skLineSegment(sketch, "E4724", {"start": v(-84.83, 5.95) * mm, "end": v(-85.3, 6.23) * mm});
            skLineSegment(sketch, "E4725", {"start": v(-85.3, 6.23) * mm, "end": v(-85.6, 6.4) * mm});
            skLineSegment(sketch, "E4726", {"start": v(-85.6, 6.4) * mm, "end": v(-85.9, 6.55) * mm});
            skLineSegment(sketch, "E4727", {"start": v(-85.9, 6.55) * mm, "end": v(-86.06, 6.61) * mm});
            skLineSegment(sketch, "E4728", {"start": v(-86.06, 6.61) * mm, "end": v(-86.22, 6.67) * mm});
            skLineSegment(sketch, "E4729", {"start": v(-86.22, 6.67) * mm, "end": v(-86.37, 6.72) * mm});
            skLineSegment(sketch, "E4730", {"start": v(-86.37, 6.72) * mm, "end": v(-86.51, 6.76) * mm});
            skLineSegment(sketch, "E4731", {"start": v(-86.51, 6.76) * mm, "end": v(-86.65, 6.78) * mm});
            skLineSegment(sketch, "E4732", {"start": v(-86.65, 6.78) * mm, "end": v(-86.78, 6.78) * mm});
            skLineSegment(sketch, "E4733", {"start": v(-86.78, 6.78) * mm, "end": v(-86.9, 6.76) * mm});
            skLineSegment(sketch, "E4734", {"start": v(-86.9, 6.76) * mm, "end": v(-87, 6.72) * mm});
            skLineSegment(sketch, "E4735", {"start": v(-87, 6.72) * mm, "end": v(-87.02, 6.7) * mm});
            skLineSegment(sketch, "E4736", {"start": v(-87.02, 6.7) * mm, "end": v(-87.04, 6.67) * mm});
            skLineSegment(sketch, "E4737", {"start": v(-87.04, 6.67) * mm, "end": v(-87.1, 6.57) * mm});
            skLineSegment(sketch, "E4738", {"start": v(-87.1, 6.57) * mm, "end": v(-87.14, 6.44) * mm});
            skLineSegment(sketch, "E4739", {"start": v(-87.14, 6.44) * mm, "end": v(-87.19, 6.3) * mm});
            skLineSegment(sketch, "E4740", {"start": v(-87.19, 6.3) * mm, "end": v(-87.25, 6) * mm});
            skLineSegment(sketch, "E4741", {"start": v(-87.25, 6) * mm, "end": v(-87.29, 5.8) * mm});
            skLineSegment(sketch, "E4742", {"start": v(-87.29, 5.8) * mm, "end": v(-87.3, 5.44) * mm});
            skLineSegment(sketch, "E4743", {"start": v(-87.3, 5.44) * mm, "end": v(-87.29, 5.08) * mm});
            skLineSegment(sketch, "E4744", {"start": v(-87.29, 5.08) * mm, "end": v(-87.25, 4.7) * mm});
            skLineSegment(sketch, "E4745", {"start": v(-87.25, 4.7) * mm, "end": v(-87.2, 4.34) * mm});
            skLineSegment(sketch, "E4746", {"start": v(-87.2, 4.34) * mm, "end": v(-87.14, 3.96) * mm});
            skLineSegment(sketch, "E4747", {"start": v(-87.14, 3.96) * mm, "end": v(-87.06, 3.6) * mm});
            skLineSegment(sketch, "E4748", {"start": v(-87.06, 3.6) * mm, "end": v(-86.88, 2.84) * mm});
            skLineSegment(sketch, "E4749", {"start": v(-86.88, 2.84) * mm, "end": v(-86.68, 2.1) * mm});
            skLineSegment(sketch, "E4750", {"start": v(-86.68, 2.1) * mm, "end": v(-86.48, 1.38) * mm});
            skLineSegment(sketch, "E4751", {"start": v(-86.48, 1.38) * mm, "end": v(-86.3, 0.67) * mm});
            skLineSegment(sketch, "E4752", {"start": v(-86.3, 0.67) * mm, "end": v(-86.22, 0.32) * mm});
            skLineSegment(sketch, "E4753", {"start": v(-86.22, 0.32) * mm, "end": v(-86.15, -0.01) * mm});
            skLineSegment(sketch, "E4754", {"start": v(-86.15, -0.01) * mm, "end": v(-86.03, -0.64) * mm});
            skLineSegment(sketch, "E4755", {"start": v(-86.03, -0.64) * mm, "end": v(-85.87, -1.3) * mm});
            skLineSegment(sketch, "E4756", {"start": v(-85.87, -1.3) * mm, "end": v(-85.7, -1.99) * mm});
            skLineSegment(sketch, "E4757", {"start": v(-85.7, -1.99) * mm, "end": v(-85.5, -2.68) * mm});
            skLineSegment(sketch, "E4758", {"start": v(-85.5, -2.68) * mm, "end": v(-85.3, -3.37) * mm});
            skLineSegment(sketch, "E4759", {"start": v(-85.3, -3.37) * mm, "end": v(-85.08, -4.05) * mm});
            skLineSegment(sketch, "E4760", {"start": v(-85.08, -4.05) * mm, "end": v(-84.86, -4.7) * mm});
            skLineSegment(sketch, "E4761", {"start": v(-84.86, -4.7) * mm, "end": v(-84.64, -5.3) * mm});
            skLineSegment(sketch, "E4762", {"start": v(-84.64, -5.3) * mm, "end": v(-84.36, -6.02) * mm});
            skLineSegment(sketch, "E4763", {"start": v(-84.36, -6.02) * mm, "end": v(-84.05, -6.78) * mm});
            skLineSegment(sketch, "E4764", {"start": v(-84.05, -6.78) * mm, "end": v(-83.71, -7.57) * mm});
            skLineSegment(sketch, "E4765", {"start": v(-83.71, -7.57) * mm, "end": v(-83.35, -8.36) * mm});
            skLineSegment(sketch, "E4766", {"start": v(-83.35, -8.36) * mm, "end": v(-82.96, -9.14) * mm});
            skLineSegment(sketch, "E4767", {"start": v(-82.96, -9.14) * mm, "end": v(-82.76, -9.52) * mm});
            skLineSegment(sketch, "E4768", {"start": v(-82.76, -9.52) * mm, "end": v(-82.56, -9.9) * mm});
            skLineSegment(sketch, "E4769", {"start": v(-82.56, -9.9) * mm, "end": v(-82.35, -10.26) * mm});
            skLineSegment(sketch, "E4770", {"start": v(-82.35, -10.26) * mm, "end": v(-82.14, -10.6) * mm});
            skLineSegment(sketch, "E4771", {"start": v(-82.14, -10.6) * mm, "end": v(-81.93, -10.93) * mm});
            skLineSegment(sketch, "E4772", {"start": v(-81.93, -10.93) * mm, "end": v(-81.71, -11.25) * mm});
            skLineSegment(sketch, "E4773", {"start": v(-81.71, -11.25) * mm, "end": v(-81.32, -11.78) * mm});
            skLineSegment(sketch, "E4774", {"start": v(-81.32, -11.78) * mm, "end": v(-80.88, -12.32) * mm});
            skLineSegment(sketch, "E4775", {"start": v(-80.88, -12.32) * mm, "end": v(-80.4, -12.87) * mm});
            skLineSegment(sketch, "E4776", {"start": v(-80.4, -12.87) * mm, "end": v(-79.9, -13.4) * mm});
            skLineSegment(sketch, "E4777", {"start": v(-79.9, -13.4) * mm, "end": v(-79.38, -13.93) * mm});
            skLineSegment(sketch, "E4778", {"start": v(-79.38, -13.93) * mm, "end": v(-78.84, -14.42) * mm});
            skLineSegment(sketch, "E4779", {"start": v(-78.84, -14.42) * mm, "end": v(-78.58, -14.65) * mm});
            skLineSegment(sketch, "E4780", {"start": v(-78.58, -14.65) * mm, "end": v(-78.31, -14.87) * mm});
            skLineSegment(sketch, "E4781", {"start": v(-78.31, -14.87) * mm, "end": v(-78.05, -15.08) * mm});
            skLineSegment(sketch, "E4782", {"start": v(-78.05, -15.08) * mm, "end": v(-77.79, -15.27) * mm});
            skLineSegment(sketch, "E4783", {"start": v(-77.79, -15.27) * mm, "end": v(-77.6, -15.4) * mm});
            skLineSegment(sketch, "E4784", {"start": v(-77.6, -15.4) * mm, "end": v(-77.38, -15.51) * mm});
            skLineSegment(sketch, "E4785", {"start": v(-77.38, -15.51) * mm, "end": v(-76.92, -15.72) * mm});
            skLineSegment(sketch, "E4786", {"start": v(-76.92, -15.72) * mm, "end": v(-76.45, -15.92) * mm});
            skLineSegment(sketch, "E4787", {"start": v(-76.45, -15.92) * mm, "end": v(-76.01, -16.11) * mm});
            skLineSegment(sketch, "E4788", {"start": v(-76.01, -16.11) * mm, "end": v(-75.27, -16.46) * mm});
            skLineSegment(sketch, "E4789", {"start": v(-75.27, -16.46) * mm, "end": v(-74.55, -16.77) * mm});
            skLineSegment(sketch, "E4790", {"start": v(-74.55, -16.77) * mm, "end": v(-73.94, -17.01) * mm});
            skLineSegment(sketch, "E4791", {"start": v(-73.94, -17.01) * mm, "end": v(-73.7, -17.1) * mm});
            skLineSegment(sketch, "E4792", {"start": v(-73.7, -17.1) * mm, "end": v(-73.53, -17.16) * mm});
            skLineSegment(sketch, "E4793", {"start": v(-73.53, -17.16) * mm, "end": v(-73.35, -17.23) * mm});
            skLineSegment(sketch, "E4794", {"start": v(-73.35, -17.23) * mm, "end": v(-73.16, -17.32) * mm});
            skLineSegment(sketch, "E4795", {"start": v(-73.16, -17.32) * mm, "end": v(-73.07, -17.36) * mm});
            skLineSegment(sketch, "E4796", {"start": v(-73.07, -17.36) * mm, "end": v(-72.98, -17.38) * mm});
            skLineSegment(sketch, "E4797", {"start": v(-72.98, -17.38) * mm, "end": v(-72.9, -17.38) * mm});
            skLineSegment(sketch, "E4798", {"start": v(-72.9, -17.38) * mm, "end": v(-72.81, -17.37) * mm});
            skLineSegment(sketch, "E4799", {"start": v(-72.81, -17.37) * mm, "end": v(-72.75, -17.33) * mm});
            skLineSegment(sketch, "E4800", {"start": v(-72.75, -17.33) * mm, "end": v(-72.7, -17.28) * mm});
            skLineSegment(sketch, "E4801", {"start": v(-72.7, -17.28) * mm, "end": v(-72.67, -17.22) * mm});
            skLineSegment(sketch, "E4802", {"start": v(-72.67, -17.22) * mm, "end": v(-72.63, -17.14) * mm});
            skLineSegment(sketch, "E4803", {"start": v(-72.63, -17.14) * mm, "end": v(-72.58, -16.99) * mm});
            skLineSegment(sketch, "E4804", {"start": v(-72.58, -16.99) * mm, "end": v(-72.54, -16.84) * mm});
            skLineSegment(sketch, "E4805", {"start": v(-72.54, -16.84) * mm, "end": v(-72.48, -16.5) * mm});
            skLineSegment(sketch, "E4806", {"start": v(-72.48, -16.5) * mm, "end": v(-72.43, -16.13) * mm});
            skLineSegment(sketch, "E4807", {"start": v(-72.43, -16.13) * mm, "end": v(-72.4, -15.76) * mm});
            skLineSegment(sketch, "E4808", {"start": v(-72.4, -15.76) * mm, "end": v(-72.38, -15.37) * mm});
            skLineSegment(sketch, "E4809", {"start": v(-72.38, -15.37) * mm, "end": v(-72.38, -14.98) * mm});
            skLineSegment(sketch, "E4810", {"start": v(-72.38, -14.98) * mm, "end": v(-72.4, -14.58) * mm});
            skLineSegment(sketch, "E4811", {"start": v(-72.4, -14.58) * mm, "end": v(-72.44, -13.77) * mm});
            skLineSegment(sketch, "E4812", {"start": v(-72.44, -13.77) * mm, "end": v(-72.51, -12.95) * mm});
            skLineSegment(sketch, "E4813", {"start": v(-72.51, -12.95) * mm, "end": v(-72.59, -12.15) * mm});
            skLineSegment(sketch, "E4814", {"start": v(-72.59, -12.15) * mm, "end": v(-72.65, -11.38) * mm});
            skLineSegment(sketch, "E4815", {"start": v(-72.65, -11.38) * mm, "end": v(-72.67, -11.01) * mm});
            skLineSegment(sketch, "E4816", {"start": v(-72.67, -11.01) * mm, "end": v(-72.69, -10.66) * mm});
            skLineSegment(sketch, "E4817", {"start": v(29.2, 57.67) * mm, "end": v(29.18, 57.82) * mm});
            skLineSegment(sketch, "E4818", {"start": v(29.18, 57.82) * mm, "end": v(29.14, 58) * mm});
            skLineSegment(sketch, "E4819", {"start": v(29.14, 58) * mm, "end": v(29.08, 58.21) * mm});
            skLineSegment(sketch, "E4820", {"start": v(29.08, 58.21) * mm, "end": v(29, 58.45) * mm});
            skLineSegment(sketch, "E4821", {"start": v(29, 58.45) * mm, "end": v(28.9, 58.7) * mm});
            skLineSegment(sketch, "E4822", {"start": v(28.9, 58.7) * mm, "end": v(28.78, 58.96) * mm});
            skLineSegment(sketch, "E4823", {"start": v(28.78, 58.96) * mm, "end": v(28.51, 59.51) * mm});
            skLineSegment(sketch, "E4824", {"start": v(28.51, 59.51) * mm, "end": v(28.22, 60.06) * mm});
            skLineSegment(sketch, "E4825", {"start": v(28.22, 60.06) * mm, "end": v(28.06, 60.31) * mm});
            skLineSegment(sketch, "E4826", {"start": v(28.06, 60.31) * mm, "end": v(27.91, 60.55) * mm});
            skLineSegment(sketch, "E4827", {"start": v(27.91, 60.55) * mm, "end": v(27.76, 60.77) * mm});
            skLineSegment(sketch, "E4828", {"start": v(27.76, 60.77) * mm, "end": v(27.62, 60.96) * mm});
            skLineSegment(sketch, "E4829", {"start": v(27.62, 60.96) * mm, "end": v(27.48, 61.13) * mm});
            skLineSegment(sketch, "E4830", {"start": v(27.48, 61.13) * mm, "end": v(27.36, 61.25) * mm});
            skLineSegment(sketch, "E4831", {"start": v(27.36, 61.25) * mm, "end": v(27.2, 61.38) * mm});
            skLineSegment(sketch, "E4832", {"start": v(27.2, 61.38) * mm, "end": v(26.97, 61.55) * mm});
            skLineSegment(sketch, "E4833", {"start": v(26.97, 61.55) * mm, "end": v(26.7, 61.73) * mm});
            skLineSegment(sketch, "E4834", {"start": v(26.7, 61.73) * mm, "end": v(26.4, 61.94) * mm});
            skLineSegment(sketch, "E4835", {"start": v(26.4, 61.94) * mm, "end": v(26.05, 62.15) * mm});
            skLineSegment(sketch, "E4836", {"start": v(26.05, 62.15) * mm, "end": v(25.68, 62.35) * mm});
            skLineSegment(sketch, "E4837", {"start": v(25.68, 62.35) * mm, "end": v(25.3, 62.55) * mm});
            skLineSegment(sketch, "E4838", {"start": v(25.3, 62.55) * mm, "end": v(24.92, 62.74) * mm});
            skLineSegment(sketch, "E4839", {"start": v(24.92, 62.74) * mm, "end": v(24.04, 63.13) * mm});
            skLineSegment(sketch, "E4840", {"start": v(24.04, 63.13) * mm, "end": v(23.58, 63.34) * mm});
            skLineSegment(sketch, "E4841", {"start": v(23.58, 63.34) * mm, "end": v(23.1, 63.55) * mm});
            skLineSegment(sketch, "E4842", {"start": v(23.1, 63.55) * mm, "end": v(22.61, 63.74) * mm});
            skLineSegment(sketch, "E4843", {"start": v(22.61, 63.74) * mm, "end": v(22.13, 63.91) * mm});
            skLineSegment(sketch, "E4844", {"start": v(22.13, 63.91) * mm, "end": v(21.9, 63.98) * mm});
            skLineSegment(sketch, "E4845", {"start": v(21.9, 63.98) * mm, "end": v(21.66, 64.05) * mm});
            skLineSegment(sketch, "E4846", {"start": v(21.66, 64.05) * mm, "end": v(21.43, 64.1) * mm});
            skLineSegment(sketch, "E4847", {"start": v(21.43, 64.1) * mm, "end": v(21.2, 64.14) * mm});
            skLineSegment(sketch, "E4848", {"start": v(21.2, 64.14) * mm, "end": v(20.86, 64.2) * mm});
            skLineSegment(sketch, "E4849", {"start": v(20.86, 64.2) * mm, "end": v(20.5, 64.25) * mm});
            skLineSegment(sketch, "E4850", {"start": v(20.5, 64.25) * mm, "end": v(20.13, 64.29) * mm});
            skLineSegment(sketch, "E4851", {"start": v(20.13, 64.29) * mm, "end": v(19.75, 64.32) * mm});
            skLineSegment(sketch, "E4852", {"start": v(19.75, 64.32) * mm, "end": v(19.36, 64.35) * mm});
            skLineSegment(sketch, "E4853", {"start": v(19.36, 64.35) * mm, "end": v(18.96, 64.36) * mm});
            skLineSegment(sketch, "E4854", {"start": v(18.96, 64.36) * mm, "end": v(18.56, 64.37) * mm});
            skLineSegment(sketch, "E4855", {"start": v(18.56, 64.37) * mm, "end": v(18.15, 64.37) * mm});
            skLineSegment(sketch, "E4856", {"start": v(18.15, 64.37) * mm, "end": v(17.75, 64.36) * mm});
            skLineSegment(sketch, "E4857", {"start": v(17.75, 64.36) * mm, "end": v(17.35, 64.34) * mm});
            skLineSegment(sketch, "E4858", {"start": v(17.35, 64.34) * mm, "end": v(16.96, 64.3) * mm});
            skLineSegment(sketch, "E4859", {"start": v(16.96, 64.3) * mm, "end": v(16.57, 64.26) * mm});
            skLineSegment(sketch, "E4860", {"start": v(16.57, 64.26) * mm, "end": v(16.2, 64.2) * mm});
            skLineSegment(sketch, "E4861", {"start": v(16.2, 64.2) * mm, "end": v(15.83, 64.13) * mm});
            skLineSegment(sketch, "E4862", {"start": v(15.83, 64.13) * mm, "end": v(15.48, 64.05) * mm});
            skLineSegment(sketch, "E4863", {"start": v(15.48, 64.05) * mm, "end": v(15.15, 63.95) * mm});
            skLineSegment(sketch, "E4864", {"start": v(15.15, 63.95) * mm, "end": v(15.03, 63.9) * mm});
            skLineSegment(sketch, "E4865", {"start": v(15.03, 63.9) * mm, "end": v(14.9, 63.83) * mm});
            skLineSegment(sketch, "E4866", {"start": v(14.9, 63.83) * mm, "end": v(14.65, 63.65) * mm});
            skLineSegment(sketch, "E4867", {"start": v(14.65, 63.65) * mm, "end": v(14.41, 63.46) * mm});
            skLineSegment(sketch, "E4868", {"start": v(14.41, 63.46) * mm, "end": v(14.19, 63.28) * mm});
            skLineSegment(sketch, "E4869", {"start": v(14.19, 63.28) * mm, "end": v(14.85, 62.53) * mm});
            skLineSegment(sketch, "E4870", {"start": v(14.85, 62.53) * mm, "end": v(15.56, 61.7) * mm});
            skLineSegment(sketch, "E4871", {"start": v(15.56, 61.7) * mm, "end": v(15.93, 61.3) * mm});
            skLineSegment(sketch, "E4872", {"start": v(15.93, 61.3) * mm, "end": v(16.29, 60.9) * mm});
            skLineSegment(sketch, "E4873", {"start": v(16.29, 60.9) * mm, "end": v(16.65, 60.53) * mm});
            skLineSegment(sketch, "E4874", {"start": v(16.65, 60.53) * mm, "end": v(17, 60.19) * mm});
            skLineSegment(sketch, "E4875", {"start": v(17, 60.19) * mm, "end": v(17.56, 59.68) * mm});
            skLineSegment(sketch, "E4876", {"start": v(17.56, 59.68) * mm, "end": v(17.87, 59.41) * mm});
            skLineSegment(sketch, "E4877", {"start": v(17.87, 59.41) * mm, "end": v(18.2, 59.15) * mm});
            skLineSegment(sketch, "E4878", {"start": v(18.2, 59.15) * mm, "end": v(18.52, 58.9) * mm});
            skLineSegment(sketch, "E4879", {"start": v(18.52, 58.9) * mm, "end": v(18.85, 58.65) * mm});
            skLineSegment(sketch, "E4880", {"start": v(18.85, 58.65) * mm, "end": v(19.18, 58.43) * mm});
            skLineSegment(sketch, "E4881", {"start": v(19.18, 58.43) * mm, "end": v(19.5, 58.24) * mm});
            skLineSegment(sketch, "E4882", {"start": v(19.5, 58.24) * mm, "end": v(19.76, 58.1) * mm});
            skLineSegment(sketch, "E4883", {"start": v(19.76, 58.1) * mm, "end": v(20.03, 57.96) * mm});
            skLineSegment(sketch, "E4884", {"start": v(20.03, 57.96) * mm, "end": v(20.3, 57.84) * mm});
            skLineSegment(sketch, "E4885", {"start": v(20.3, 57.84) * mm, "end": v(20.58, 57.72) * mm});
            skLineSegment(sketch, "E4886", {"start": v(20.58, 57.72) * mm, "end": v(20.85, 57.61) * mm});
            skLineSegment(sketch, "E4887", {"start": v(20.85, 57.61) * mm, "end": v(21.13, 57.51) * mm});
            skLineSegment(sketch, "E4888", {"start": v(21.13, 57.51) * mm, "end": v(21.4, 57.42) * mm});
            skLineSegment(sketch, "E4889", {"start": v(21.4, 57.42) * mm, "end": v(21.69, 57.34) * mm});
            skLineSegment(sketch, "E4890", {"start": v(21.69, 57.34) * mm, "end": v(22.24, 57.2) * mm});
            skLineSegment(sketch, "E4891", {"start": v(22.24, 57.2) * mm, "end": v(22.8, 57.08) * mm});
            skLineSegment(sketch, "E4892", {"start": v(22.8, 57.08) * mm, "end": v(23.37, 57) * mm});
            skLineSegment(sketch, "E4893", {"start": v(23.37, 57) * mm, "end": v(23.93, 56.94) * mm});
            skLineSegment(sketch, "E4894", {"start": v(23.93, 56.94) * mm, "end": v(24.49, 56.9) * mm});
            skLineSegment(sketch, "E4895", {"start": v(24.49, 56.9) * mm, "end": v(25.05, 56.88) * mm});
            skLineSegment(sketch, "E4896", {"start": v(25.05, 56.88) * mm, "end": v(25.6, 56.89) * mm});
            skLineSegment(sketch, "E4897", {"start": v(25.6, 56.89) * mm, "end": v(26.16, 56.91) * mm});
            skLineSegment(sketch, "E4898", {"start": v(26.16, 56.91) * mm, "end": v(26.7, 56.95) * mm});
            skLineSegment(sketch, "E4899", {"start": v(26.7, 56.95) * mm, "end": v(27.24, 57) * mm});
            skLineSegment(sketch, "E4900", {"start": v(27.24, 57) * mm, "end": v(27.78, 57.07) * mm});
            skLineSegment(sketch, "E4901", {"start": v(27.78, 57.07) * mm, "end": v(28.3, 57.14) * mm});
            skLineSegment(sketch, "E4902", {"start": v(28.3, 57.14) * mm, "end": v(29.2, 57.28) * mm});
            skLineSegment(sketch, "E4903", {"start": v(29.2, 57.28) * mm, "end": v(29.2, 57.67) * mm});
            skLineSegment(sketch, "E4904", {"start": v(-85.3, 11.8) * mm, "end": v(-84.85, 14.97) * mm});
            skLineSegment(sketch, "E4905", {"start": v(-84.85, 14.97) * mm, "end": v(-84.64, 16.3) * mm});
            skLineSegment(sketch, "E4906", {"start": v(-84.64, 16.3) * mm, "end": v(-85.1, 16.5) * mm});
            skLineSegment(sketch, "E4907", {"start": v(-85.1, 16.5) * mm, "end": v(-85.57, 16.73) * mm});
            skLineSegment(sketch, "E4908", {"start": v(-85.57, 16.73) * mm, "end": v(-86.06, 16.97) * mm});
            skLineSegment(sketch, "E4909", {"start": v(-86.06, 16.97) * mm, "end": v(-86.55, 17.23) * mm});
            skLineSegment(sketch, "E4910", {"start": v(-86.55, 17.23) * mm, "end": v(-87.03, 17.5) * mm});
            skLineSegment(sketch, "E4911", {"start": v(-87.03, 17.5) * mm, "end": v(-87.5, 17.79) * mm});
            skLineSegment(sketch, "E4912", {"start": v(-87.5, 17.79) * mm, "end": v(-87.94, 18.07) * mm});
            skLineSegment(sketch, "E4913", {"start": v(-87.94, 18.07) * mm, "end": v(-88.34, 18.35) * mm});
            skLineSegment(sketch, "E4914", {"start": v(-88.34, 18.35) * mm, "end": v(-88.72, 18.32) * mm});
            skLineSegment(sketch, "E4915", {"start": v(-88.72, 18.32) * mm, "end": v(-88.92, 18.3) * mm});
            skLineSegment(sketch, "E4916", {"start": v(-88.92, 18.3) * mm, "end": v(-89.12, 18.26) * mm});
            skLineSegment(sketch, "E4917", {"start": v(-89.12, 18.26) * mm, "end": v(-89.32, 18.22) * mm});
            skLineSegment(sketch, "E4918", {"start": v(-89.32, 18.22) * mm, "end": v(-89.51, 18.16) * mm});
            skLineSegment(sketch, "E4919", {"start": v(-89.51, 18.16) * mm, "end": v(-89.68, 18.08) * mm});
            skLineSegment(sketch, "E4920", {"start": v(-89.68, 18.08) * mm, "end": v(-89.76, 18.03) * mm});
            skLineSegment(sketch, "E4921", {"start": v(-89.76, 18.03) * mm, "end": v(-89.83, 17.98) * mm});
            skLineSegment(sketch, "E4922", {"start": v(-89.83, 17.98) * mm, "end": v(-89.92, 17.9) * mm});
            skLineSegment(sketch, "E4923", {"start": v(-89.92, 17.9) * mm, "end": v(-90, 17.8) * mm});
            skLineSegment(sketch, "E4924", {"start": v(-90, 17.8) * mm, "end": v(-90.09, 17.7) * mm});
            skLineSegment(sketch, "E4925", {"start": v(-90.09, 17.7) * mm, "end": v(-90.17, 17.58) * mm});
            skLineSegment(sketch, "E4926", {"start": v(-90.17, 17.58) * mm, "end": v(-90.3, 17.33) * mm});
            skLineSegment(sketch, "E4927", {"start": v(-90.3, 17.33) * mm, "end": v(-90.43, 17.07) * mm});
            skLineSegment(sketch, "E4928", {"start": v(-90.43, 17.07) * mm, "end": v(-90.52, 16.8) * mm});
            skLineSegment(sketch, "E4929", {"start": v(-90.52, 16.8) * mm, "end": v(-90.6, 16.51) * mm});
            skLineSegment(sketch, "E4930", {"start": v(-90.6, 16.51) * mm, "end": v(-90.64, 16.24) * mm});
            skLineSegment(sketch, "E4931", {"start": v(-90.64, 16.24) * mm, "end": v(-90.65, 15.99) * mm});
            skLineSegment(sketch, "E4932", {"start": v(-90.65, 15.99) * mm, "end": v(-90.65, 15.87) * mm});
            skLineSegment(sketch, "E4933", {"start": v(-90.65, 15.87) * mm, "end": v(-90.64, 15.74) * mm});
            skLineSegment(sketch, "E4934", {"start": v(-90.64, 15.74) * mm, "end": v(-90.59, 15.48) * mm});
            skLineSegment(sketch, "E4935", {"start": v(-90.59, 15.48) * mm, "end": v(-90.5, 15.21) * mm});
            skLineSegment(sketch, "E4936", {"start": v(-90.5, 15.21) * mm, "end": v(-90.4, 14.95) * mm});
            skLineSegment(sketch, "E4937", {"start": v(-90.4, 14.95) * mm, "end": v(-90.28, 14.69) * mm});
            skLineSegment(sketch, "E4938", {"start": v(-90.28, 14.69) * mm, "end": v(-90.14, 14.44) * mm});
            skLineSegment(sketch, "E4939", {"start": v(-90.14, 14.44) * mm, "end": v(-90, 14.22) * mm});
            skLineSegment(sketch, "E4940", {"start": v(-90, 14.22) * mm, "end": v(-89.84, 14.02) * mm});
            skLineSegment(sketch, "E4941", {"start": v(-89.84, 14.02) * mm, "end": v(-89.68, 13.86) * mm});
            skLineSegment(sketch, "E4942", {"start": v(-89.68, 13.86) * mm, "end": v(-89.49, 13.71) * mm});
            skLineSegment(sketch, "E4943", {"start": v(-89.49, 13.71) * mm, "end": v(-89.28, 13.57) * mm});
            skLineSegment(sketch, "E4944", {"start": v(-89.28, 13.57) * mm, "end": v(-89.06, 13.44) * mm});
            skLineSegment(sketch, "E4945", {"start": v(-89.06, 13.44) * mm, "end": v(-88.61, 13.2) * mm});
            skLineSegment(sketch, "E4946", {"start": v(-88.61, 13.2) * mm, "end": v(-88.2, 12.97) * mm});
            skLineSegment(sketch, "E4947", {"start": v(-88.2, 12.97) * mm, "end": v(-87.8, 12.76) * mm});
            skLineSegment(sketch, "E4948", {"start": v(-87.8, 12.76) * mm, "end": v(-87.37, 12.56) * mm});
            skLineSegment(sketch, "E4949", {"start": v(-87.37, 12.56) * mm, "end": v(-86.92, 12.36) * mm});
            skLineSegment(sketch, "E4950", {"start": v(-86.92, 12.36) * mm, "end": v(-86.47, 12.18) * mm});
            skLineSegment(sketch, "E4951", {"start": v(-86.47, 12.18) * mm, "end": v(-86.05, 12.02) * mm});
            skLineSegment(sketch, "E4952", {"start": v(-86.05, 12.02) * mm, "end": v(-85.7, 11.9) * mm});
            skLineSegment(sketch, "E4953", {"start": v(-85.7, 11.9) * mm, "end": v(-85.44, 11.82) * mm});
            skLineSegment(sketch, "E4954", {"start": v(-85.44, 11.82) * mm, "end": v(-85.3, 11.8) * mm});
            skLineSegment(sketch, "E4955", {"start": v(0.77, 8.13) * mm, "end": v(0.98, 8.14) * mm});
            skLineSegment(sketch, "E4956", {"start": v(0.98, 8.14) * mm, "end": v(1.22, 8.14) * mm});
            skLineSegment(sketch, "E4957", {"start": v(1.22, 8.14) * mm, "end": v(1.33, 8.15) * mm});
            skLineSegment(sketch, "E4958", {"start": v(1.33, 8.15) * mm, "end": v(1.44, 8.16) * mm});
            skLineSegment(sketch, "E4959", {"start": v(1.44, 8.16) * mm, "end": v(1.54, 8.19) * mm});
            skLineSegment(sketch, "E4960", {"start": v(1.54, 8.19) * mm, "end": v(1.63, 8.23) * mm});
            skLineSegment(sketch, "E4961", {"start": v(1.63, 8.23) * mm, "end": v(1.72, 8.3) * mm});
            skLineSegment(sketch, "E4962", {"start": v(1.72, 8.3) * mm, "end": v(1.81, 8.38) * mm});
            skLineSegment(sketch, "E4963", {"start": v(1.81, 8.38) * mm, "end": v(1.98, 8.56) * mm});
            skLineSegment(sketch, "E4964", {"start": v(1.98, 8.56) * mm, "end": v(2.14, 8.76) * mm});
            skLineSegment(sketch, "E4965", {"start": v(2.14, 8.76) * mm, "end": v(2.28, 9) * mm});
            skLineSegment(sketch, "E4966", {"start": v(2.28, 9) * mm, "end": v(2.4, 9.23) * mm});
            skLineSegment(sketch, "E4967", {"start": v(2.4, 9.23) * mm, "end": v(2.5, 9.48) * mm});
            skLineSegment(sketch, "E4968", {"start": v(2.5, 9.48) * mm, "end": v(2.56, 9.72) * mm});
            skLineSegment(sketch, "E4969", {"start": v(2.56, 9.72) * mm, "end": v(2.58, 9.83) * mm});
            skLineSegment(sketch, "E4970", {"start": v(2.58, 9.83) * mm, "end": v(2.59, 9.95) * mm});
            skLineSegment(sketch, "E4971", {"start": v(2.59, 9.95) * mm, "end": v(2.6, 10.02) * mm});
            skLineSegment(sketch, "E4972", {"start": v(2.6, 10.02) * mm, "end": v(2.58, 10.1) * mm});
            skLineSegment(sketch, "E4973", {"start": v(2.58, 10.1) * mm, "end": v(2.55, 10.26) * mm});
            skLineSegment(sketch, "E4974", {"start": v(2.55, 10.26) * mm, "end": v(2.49, 10.42) * mm});
            skLineSegment(sketch, "E4975", {"start": v(2.49, 10.42) * mm, "end": v(2.41, 10.58) * mm});
            skLineSegment(sketch, "E4976", {"start": v(2.41, 10.58) * mm, "end": v(2.25, 10.9) * mm});
            skLineSegment(sketch, "E4977", {"start": v(2.25, 10.9) * mm, "end": v(2.17, 11.06) * mm});
            skLineSegment(sketch, "E4978", {"start": v(2.17, 11.06) * mm, "end": v(2.1, 11.2) * mm});
            skLineSegment(sketch, "E4979", {"start": v(2.1, 11.2) * mm, "end": v(1.94, 10.9) * mm});
            skLineSegment(sketch, "E4980", {"start": v(1.94, 10.9) * mm, "end": v(1.73, 10.58) * mm});
            skLineSegment(sketch, "E4981", {"start": v(1.73, 10.58) * mm, "end": v(1.62, 10.42) * mm});
            skLineSegment(sketch, "E4982", {"start": v(1.62, 10.42) * mm, "end": v(1.5, 10.27) * mm});
            skLineSegment(sketch, "E4983", {"start": v(1.5, 10.27) * mm, "end": v(1.38, 10.15) * mm});
            skLineSegment(sketch, "E4984", {"start": v(1.38, 10.15) * mm, "end": v(1.25, 10.06) * mm});
            skLineSegment(sketch, "E4985", {"start": v(1.25, 10.06) * mm, "end": v(1.05, 9.96) * mm});
            skLineSegment(sketch, "E4986", {"start": v(1.05, 9.96) * mm, "end": v(0.94, 9.92) * mm});
            skLineSegment(sketch, "E4987", {"start": v(0.94, 9.92) * mm, "end": v(0.83, 9.89) * mm});
            skLineSegment(sketch, "E4988", {"start": v(0.83, 9.89) * mm, "end": v(0.73, 9.87) * mm});
            skLineSegment(sketch, "E4989", {"start": v(0.73, 9.87) * mm, "end": v(0.62, 9.87) * mm});
            skLineSegment(sketch, "E4990", {"start": v(0.62, 9.87) * mm, "end": v(0.52, 9.89) * mm});
            skLineSegment(sketch, "E4991", {"start": v(0.52, 9.89) * mm, "end": v(0.42, 9.93) * mm});
            skLineSegment(sketch, "E4992", {"start": v(0.42, 9.93) * mm, "end": v(0.33, 10) * mm});
            skLineSegment(sketch, "E4993", {"start": v(0.33, 10) * mm, "end": v(0.24, 10.08) * mm});
            skLineSegment(sketch, "E4994", {"start": v(0.24, 10.08) * mm, "end": v(0.17, 10.18) * mm});
            skLineSegment(sketch, "E4995", {"start": v(0.17, 10.18) * mm, "end": v(0.1, 10.29) * mm});
            skLineSegment(sketch, "E4996", {"start": v(0.1, 10.29) * mm, "end": v(0.04, 10.4) * mm});
            skLineSegment(sketch, "E4997", {"start": v(0.04, 10.4) * mm, "end": v(-0.01, 10.54) * mm});
            skLineSegment(sketch, "E4998", {"start": v(-0.01, 10.54) * mm, "end": v(-0.1, 10.81) * mm});
            skLineSegment(sketch, "E4999", {"start": v(-0.1, 10.81) * mm, "end": v(-0.2, 11.1) * mm});
            skLineSegment(sketch, "E5000", {"start": v(-0.2, 11.1) * mm, "end": v(-0.28, 11.38) * mm});
            skLineSegment(sketch, "E5001", {"start": v(-0.28, 11.38) * mm, "end": v(-0.36, 11.64) * mm});
            skLineSegment(sketch, "E5002", {"start": v(-0.36, 11.64) * mm, "end": v(-0.41, 11.76) * mm});
            skLineSegment(sketch, "E5003", {"start": v(-0.41, 11.76) * mm, "end": v(-0.46, 11.86) * mm});
            skLineSegment(sketch, "E5004", {"start": v(-0.46, 11.86) * mm, "end": v(-0.51, 11.37) * mm});
            skLineSegment(sketch, "E5005", {"start": v(-0.51, 11.37) * mm, "end": v(-0.53, 11) * mm});
            skLineSegment(sketch, "E5006", {"start": v(-0.53, 11) * mm, "end": v(-0.53, 10.57) * mm});
            skLineSegment(sketch, "E5007", {"start": v(-0.53, 10.57) * mm, "end": v(-0.51, 10.1) * mm});
            skLineSegment(sketch, "E5008", {"start": v(-0.51, 10.1) * mm, "end": v(-0.48, 9.62) * mm});
            skLineSegment(sketch, "E5009", {"start": v(-0.48, 9.62) * mm, "end": v(-0.44, 9.17) * mm});
            skLineSegment(sketch, "E5010", {"start": v(-0.44, 9.17) * mm, "end": v(-0.39, 8.78) * mm});
            skLineSegment(sketch, "E5011", {"start": v(-0.39, 8.78) * mm, "end": v(-0.33, 8.47) * mm});
            skLineSegment(sketch, "E5012", {"start": v(-0.33, 8.47) * mm, "end": v(-0.3, 8.37) * mm});
            skLineSegment(sketch, "E5013", {"start": v(-0.3, 8.37) * mm, "end": v(-0.26, 8.3) * mm});
            skLineSegment(sketch, "E5014", {"start": v(-0.26, 8.3) * mm, "end": v(-0.23, 8.23) * mm});
            skLineSegment(sketch, "E5015", {"start": v(-0.23, 8.23) * mm, "end": v(-0.2, 8.15) * mm});
            skLineSegment(sketch, "E5016", {"start": v(-0.2, 8.15) * mm, "end": v(-0.15, 8.08) * mm});
            skLineSegment(sketch, "E5017", {"start": v(-0.15, 8.08) * mm, "end": v(-0.13, 8.05) * mm});
            skLineSegment(sketch, "E5018", {"start": v(-0.13, 8.05) * mm, "end": v(-0.1, 8.03) * mm});
            skLineSegment(sketch, "E5019", {"start": v(-0.1, 8.03) * mm, "end": v(0, 8) * mm});
            skLineSegment(sketch, "E5020", {"start": v(0, 8) * mm, "end": v(0.1, 8) * mm});
            skLineSegment(sketch, "E5021", {"start": v(0.1, 8) * mm, "end": v(0.21, 8) * mm});
            skLineSegment(sketch, "E5022", {"start": v(0.21, 8) * mm, "end": v(0.33, 8.03) * mm});
            skLineSegment(sketch, "E5023", {"start": v(0.33, 8.03) * mm, "end": v(0.56, 8.09) * mm});
            skLineSegment(sketch, "E5024", {"start": v(0.56, 8.09) * mm, "end": v(0.67, 8.12) * mm});
            skLineSegment(sketch, "E5025", {"start": v(0.67, 8.12) * mm, "end": v(0.77, 8.13) * mm});
            skLineSegment(sketch, "E5026", {"start": v(8.5, 8.08) * mm, "end": v(8.74, 8.06) * mm});
            skLineSegment(sketch, "E5027", {"start": v(8.74, 8.06) * mm, "end": v(8.98, 8.02) * mm});
            skLineSegment(sketch, "E5028", {"start": v(8.98, 8.02) * mm, "end": v(9.1, 8) * mm});
            skLineSegment(sketch, "E5029", {"start": v(9.1, 8) * mm, "end": v(9.22, 8) * mm});
            skLineSegment(sketch, "E5030", {"start": v(9.22, 8) * mm, "end": v(9.33, 8.03) * mm});
            skLineSegment(sketch, "E5031", {"start": v(9.33, 8.03) * mm, "end": v(9.38, 8.04) * mm});
            skLineSegment(sketch, "E5032", {"start": v(9.38, 8.04) * mm, "end": v(9.42, 8.07) * mm});
            skLineSegment(sketch, "E5033", {"start": v(9.42, 8.07) * mm, "end": v(9.5, 8.13) * mm});
            skLineSegment(sketch, "E5034", {"start": v(9.5, 8.13) * mm, "end": v(9.58, 8.2) * mm});
            skLineSegment(sketch, "E5035", {"start": v(9.58, 8.2) * mm, "end": v(9.64, 8.29) * mm});
            skLineSegment(sketch, "E5036", {"start": v(9.64, 8.29) * mm, "end": v(9.7, 8.38) * mm});
            skLineSegment(sketch, "E5037", {"start": v(9.7, 8.38) * mm, "end": v(9.81, 8.58) * mm});
            skLineSegment(sketch, "E5038", {"start": v(9.81, 8.58) * mm, "end": v(9.9, 8.8) * mm});
            skLineSegment(sketch, "E5039", {"start": v(9.9, 8.8) * mm, "end": v(9.97, 9.04) * mm});
            skLineSegment(sketch, "E5040", {"start": v(9.97, 9.04) * mm, "end": v(10.01, 9.28) * mm});
            skLineSegment(sketch, "E5041", {"start": v(10.01, 9.28) * mm, "end": v(10.04, 9.5) * mm});
            skLineSegment(sketch, "E5042", {"start": v(10.04, 9.5) * mm, "end": v(10.05, 9.71) * mm});
            skLineSegment(sketch, "E5043", {"start": v(10.05, 9.71) * mm, "end": v(10.04, 9.83) * mm});
            skLineSegment(sketch, "E5044", {"start": v(10.04, 9.83) * mm, "end": v(10, 9.95) * mm});
            skLineSegment(sketch, "E5045", {"start": v(10, 9.95) * mm, "end": v(9.91, 10.19) * mm});
            skLineSegment(sketch, "E5046", {"start": v(9.91, 10.19) * mm, "end": v(9.8, 10.42) * mm});
            skLineSegment(sketch, "E5047", {"start": v(9.8, 10.42) * mm, "end": v(9.7, 10.64) * mm});
            skLineSegment(sketch, "E5048", {"start": v(9.7, 10.64) * mm, "end": v(9.43, 10.66) * mm});
            skLineSegment(sketch, "E5049", {"start": v(9.43, 10.66) * mm, "end": v(9.15, 10.67) * mm});
            skLineSegment(sketch, "E5050", {"start": v(9.15, 10.67) * mm, "end": v(8.86, 10.68) * mm});
            skLineSegment(sketch, "E5051", {"start": v(8.86, 10.68) * mm, "end": v(8.73, 10.68) * mm});
            skLineSegment(sketch, "E5052", {"start": v(8.73, 10.68) * mm, "end": v(8.6, 10.7) * mm});
            skLineSegment(sketch, "E5053", {"start": v(8.6, 10.7) * mm, "end": v(8.38, 10.74) * mm});
            skLineSegment(sketch, "E5054", {"start": v(8.38, 10.74) * mm, "end": v(8.15, 10.8) * mm});
            skLineSegment(sketch, "E5055", {"start": v(8.15, 10.8) * mm, "end": v(7.69, 10.93) * mm});
            skLineSegment(sketch, "E5056", {"start": v(7.69, 10.93) * mm, "end": v(7.27, 11.07) * mm});
            skLineSegment(sketch, "E5057", {"start": v(7.27, 11.07) * mm, "end": v(6.93, 11.19) * mm});
            skLineSegment(sketch, "E5058", {"start": v(6.93, 11.19) * mm, "end": v(6.27, 11.4) * mm});
            skLineSegment(sketch, "E5059", {"start": v(6.27, 11.4) * mm, "end": v(6.28, 11.26) * mm});
            skLineSegment(sketch, "E5060", {"start": v(6.28, 11.26) * mm, "end": v(6.3, 11.1) * mm});
            skLineSegment(sketch, "E5061", {"start": v(6.3, 11.1) * mm, "end": v(6.37, 10.8) * mm});
            skLineSegment(sketch, "E5062", {"start": v(6.37, 10.8) * mm, "end": v(6.46, 10.46) * mm});
            skLineSegment(sketch, "E5063", {"start": v(6.46, 10.46) * mm, "end": v(6.53, 10.13) * mm});
            skLineSegment(sketch, "E5064", {"start": v(6.53, 10.13) * mm, "end": v(6.56, 9.96) * mm});
            skLineSegment(sketch, "E5065", {"start": v(6.56, 9.96) * mm, "end": v(6.58, 9.8) * mm});
            skLineSegment(sketch, "E5066", {"start": v(6.58, 9.8) * mm, "end": v(6.58, 9.63) * mm});
            skLineSegment(sketch, "E5067", {"start": v(6.58, 9.63) * mm, "end": v(6.57, 9.47) * mm});
            skLineSegment(sketch, "E5068", {"start": v(6.57, 9.47) * mm, "end": v(6.53, 9.32) * mm});
            skLineSegment(sketch, "E5069", {"start": v(6.53, 9.32) * mm, "end": v(6.47, 9.17) * mm});
            skLineSegment(sketch, "E5070", {"start": v(6.47, 9.17) * mm, "end": v(6.39, 9.03) * mm});
            skLineSegment(sketch, "E5071", {"start": v(6.39, 9.03) * mm, "end": v(6.27, 8.9) * mm});
            skLineSegment(sketch, "E5072", {"start": v(6.27, 8.9) * mm, "end": v(6.58, 8.69) * mm});
            skLineSegment(sketch, "E5073", {"start": v(6.58, 8.69) * mm, "end": v(6.92, 8.45) * mm});
            skLineSegment(sketch, "E5074", {"start": v(6.92, 8.45) * mm, "end": v(7.08, 8.34) * mm});
            skLineSegment(sketch, "E5075", {"start": v(7.08, 8.34) * mm, "end": v(7.26, 8.24) * mm});
            skLineSegment(sketch, "E5076", {"start": v(7.26, 8.24) * mm, "end": v(7.43, 8.15) * mm});
            skLineSegment(sketch, "E5077", {"start": v(7.43, 8.15) * mm, "end": v(7.6, 8.1) * mm});
            skLineSegment(sketch, "E5078", {"start": v(7.6, 8.1) * mm, "end": v(7.7, 8.07) * mm});
            skLineSegment(sketch, "E5079", {"start": v(7.7, 8.07) * mm, "end": v(7.8, 8.06) * mm});
            skLineSegment(sketch, "E5080", {"start": v(7.8, 8.06) * mm, "end": v(8.05, 8.06) * mm});
            skLineSegment(sketch, "E5081", {"start": v(8.05, 8.06) * mm, "end": v(8.29, 8.07) * mm});
            skLineSegment(sketch, "E5082", {"start": v(8.29, 8.07) * mm, "end": v(8.5, 8.08) * mm});
            skLineSegment(sketch, "E5083", {"start": v(58.73, 52.83) * mm, "end": v(59.03, 53.36) * mm});
            skLineSegment(sketch, "E5084", {"start": v(59.03, 53.36) * mm, "end": v(59.31, 53.87) * mm});
            skLineSegment(sketch, "E5085", {"start": v(59.31, 53.87) * mm, "end": v(59.58, 54.37) * mm});
            skLineSegment(sketch, "E5086", {"start": v(59.58, 54.37) * mm, "end": v(59.83, 54.86) * mm});
            skLineSegment(sketch, "E5087", {"start": v(59.83, 54.86) * mm, "end": v(60.05, 55.31) * mm});
            skLineSegment(sketch, "E5088", {"start": v(60.05, 55.31) * mm, "end": v(60.25, 55.77) * mm});
            skLineSegment(sketch, "E5089", {"start": v(60.25, 55.77) * mm, "end": v(60.34, 56.01) * mm});
            skLineSegment(sketch, "E5090", {"start": v(60.34, 56.01) * mm, "end": v(60.43, 56.26) * mm});
            skLineSegment(sketch, "E5091", {"start": v(60.43, 56.26) * mm, "end": v(60.51, 56.52) * mm});
            skLineSegment(sketch, "E5092", {"start": v(60.51, 56.52) * mm, "end": v(60.59, 56.79) * mm});
            skLineSegment(sketch, "E5093", {"start": v(60.59, 56.79) * mm, "end": v(60.71, 57.29) * mm});
            skLineSegment(sketch, "E5094", {"start": v(60.71, 57.29) * mm, "end": v(60.82, 57.82) * mm});
            skLineSegment(sketch, "E5095", {"start": v(60.82, 57.82) * mm, "end": v(60.93, 58.37) * mm});
            skLineSegment(sketch, "E5096", {"start": v(60.93, 58.37) * mm, "end": v(61.01, 58.93) * mm});
            skLineSegment(sketch, "E5097", {"start": v(61.01, 58.93) * mm, "end": v(61.06, 59.28) * mm});
            skLineSegment(sketch, "E5098", {"start": v(61.06, 59.28) * mm, "end": v(61.1, 59.62) * mm});
            skLineSegment(sketch, "E5099", {"start": v(61.1, 59.62) * mm, "end": v(61.12, 59.96) * mm});
            skLineSegment(sketch, "E5100", {"start": v(61.12, 59.96) * mm, "end": v(61.13, 60.3) * mm});
            skLineSegment(sketch, "E5101", {"start": v(61.13, 60.3) * mm, "end": v(61.12, 60.62) * mm});
            skLineSegment(sketch, "E5102", {"start": v(61.12, 60.62) * mm, "end": v(61.1, 60.94) * mm});
            skLineSegment(sketch, "E5103", {"start": v(61.1, 60.94) * mm, "end": v(61.04, 61.24) * mm});
            skLineSegment(sketch, "E5104", {"start": v(61.04, 61.24) * mm, "end": v(61, 61.4) * mm});
            skLineSegment(sketch, "E5105", {"start": v(61, 61.4) * mm, "end": v(60.96, 61.54) * mm});
            skLineSegment(sketch, "E5106", {"start": v(60.96, 61.54) * mm, "end": v(60.9, 61.67) * mm});
            skLineSegment(sketch, "E5107", {"start": v(60.9, 61.67) * mm, "end": v(60.83, 61.82) * mm});
            skLineSegment(sketch, "E5108", {"start": v(60.83, 61.82) * mm, "end": v(60.74, 61.96) * mm});
            skLineSegment(sketch, "E5109", {"start": v(60.74, 61.96) * mm, "end": v(60.64, 62.1) * mm});
            skLineSegment(sketch, "E5110", {"start": v(60.64, 62.1) * mm, "end": v(60.52, 62.23) * mm});
            skLineSegment(sketch, "E5111", {"start": v(60.52, 62.23) * mm, "end": v(60.4, 62.34) * mm});
            skLineSegment(sketch, "E5112", {"start": v(60.4, 62.34) * mm, "end": v(60.27, 62.44) * mm});
            skLineSegment(sketch, "E5113", {"start": v(60.27, 62.44) * mm, "end": v(60.14, 62.52) * mm});
            skLineSegment(sketch, "E5114", {"start": v(60.14, 62.52) * mm, "end": v(60.06, 62.55) * mm});
            skLineSegment(sketch, "E5115", {"start": v(60.06, 62.55) * mm, "end": v(59.96, 62.56) * mm});
            skLineSegment(sketch, "E5116", {"start": v(59.96, 62.56) * mm, "end": v(59.74, 62.55) * mm});
            skLineSegment(sketch, "E5117", {"start": v(59.74, 62.55) * mm, "end": v(59.53, 62.53) * mm});
            skLineSegment(sketch, "E5118", {"start": v(59.53, 62.53) * mm, "end": v(59.33, 62.52) * mm});
            skLineSegment(sketch, "E5119", {"start": v(59.33, 62.52) * mm, "end": v(59.14, 62.5) * mm});
            skLineSegment(sketch, "E5120", {"start": v(59.14, 62.5) * mm, "end": v(58.92, 62.47) * mm});
            skLineSegment(sketch, "E5121", {"start": v(58.92, 62.47) * mm, "end": v(58.68, 62.42) * mm});
            skLineSegment(sketch, "E5122", {"start": v(58.68, 62.42) * mm, "end": v(58.42, 62.36) * mm});
            skLineSegment(sketch, "E5123", {"start": v(58.42, 62.36) * mm, "end": v(58.16, 62.28) * mm});
            skLineSegment(sketch, "E5124", {"start": v(58.16, 62.28) * mm, "end": v(57.9, 62.2) * mm});
            skLineSegment(sketch, "E5125", {"start": v(57.9, 62.2) * mm, "end": v(57.63, 62.1) * mm});
            skLineSegment(sketch, "E5126", {"start": v(57.63, 62.1) * mm, "end": v(57.4, 61.99) * mm});
            skLineSegment(sketch, "E5127", {"start": v(57.4, 61.99) * mm, "end": v(57.12, 61.87) * mm});
            skLineSegment(sketch, "E5128", {"start": v(57.12, 61.87) * mm, "end": v(56.82, 61.75) * mm});
            skLineSegment(sketch, "E5129", {"start": v(56.82, 61.75) * mm, "end": v(56.67, 61.69) * mm});
            skLineSegment(sketch, "E5130", {"start": v(56.67, 61.69) * mm, "end": v(56.52, 61.62) * mm});
            skLineSegment(sketch, "E5131", {"start": v(56.52, 61.62) * mm, "end": v(56.4, 61.54) * mm});
            skLineSegment(sketch, "E5132", {"start": v(56.4, 61.54) * mm, "end": v(56.28, 61.46) * mm});
            skLineSegment(sketch, "E5133", {"start": v(56.28, 61.46) * mm, "end": v(56.1, 61.3) * mm});
            skLineSegment(sketch, "E5134", {"start": v(56.1, 61.3) * mm, "end": v(55.95, 61.11) * mm});
            skLineSegment(sketch, "E5135", {"start": v(55.95, 61.11) * mm, "end": v(55.8, 60.9) * mm});
            skLineSegment(sketch, "E5136", {"start": v(55.8, 60.9) * mm, "end": v(55.66, 60.69) * mm});
            skLineSegment(sketch, "E5137", {"start": v(55.66, 60.69) * mm, "end": v(55.38, 60.24) * mm});
            skLineSegment(sketch, "E5138", {"start": v(55.38, 60.24) * mm, "end": v(55.25, 60.03) * mm});
            skLineSegment(sketch, "E5139", {"start": v(55.25, 60.03) * mm, "end": v(55.12, 59.84) * mm});
            skLineSegment(sketch, "E5140", {"start": v(55.12, 59.84) * mm, "end": v(54.64, 59.19) * mm});
            skLineSegment(sketch, "E5141", {"start": v(54.64, 59.19) * mm, "end": v(54.21, 58.61) * mm});
            skLineSegment(sketch, "E5142", {"start": v(54.21, 58.61) * mm, "end": v(53.92, 58.2) * mm});
            skLineSegment(sketch, "E5143", {"start": v(53.92, 58.2) * mm, "end": v(53.85, 58.07) * mm});
            skLineSegment(sketch, "E5144", {"start": v(53.85, 58.07) * mm, "end": v(53.83, 58.03) * mm});
            skLineSegment(sketch, "E5145", {"start": v(53.83, 58.03) * mm, "end": v(53.84, 58.01) * mm});
            skLineSegment(sketch, "E5146", {"start": v(53.84, 58.01) * mm, "end": v(54.11, 57.79) * mm});
            skLineSegment(sketch, "E5147", {"start": v(54.11, 57.79) * mm, "end": v(54.39, 57.54) * mm});
            skLineSegment(sketch, "E5148", {"start": v(54.39, 57.54) * mm, "end": v(54.68, 57.28) * mm});
            skLineSegment(sketch, "E5149", {"start": v(54.68, 57.28) * mm, "end": v(54.97, 57.02) * mm});
            skLineSegment(sketch, "E5150", {"start": v(54.97, 57.02) * mm, "end": v(55.2, 56.83) * mm});
            skLineSegment(sketch, "E5151", {"start": v(55.2, 56.83) * mm, "end": v(55.41, 56.63) * mm});
            skLineSegment(sketch, "E5152", {"start": v(55.41, 56.63) * mm, "end": v(55.84, 56.21) * mm});
            skLineSegment(sketch, "E5153", {"start": v(55.84, 56.21) * mm, "end": v(56.27, 55.78) * mm});
            skLineSegment(sketch, "E5154", {"start": v(56.27, 55.78) * mm, "end": v(56.7, 55.37) * mm});
            skLineSegment(sketch, "E5155", {"start": v(56.7, 55.37) * mm, "end": v(56.9, 55.17) * mm});
            skLineSegment(sketch, "E5156", {"start": v(56.9, 55.17) * mm, "end": v(57.1, 54.96) * mm});
            skLineSegment(sketch, "E5157", {"start": v(57.1, 54.96) * mm, "end": v(57.3, 54.73) * mm});
            skLineSegment(sketch, "E5158", {"start": v(57.3, 54.73) * mm, "end": v(57.47, 54.5) * mm});
            skLineSegment(sketch, "E5159", {"start": v(57.47, 54.5) * mm, "end": v(57.8, 54.07) * mm});
            skLineSegment(sketch, "E5160", {"start": v(57.8, 54.07) * mm, "end": v(58.1, 53.67) * mm});
            skLineSegment(sketch, "E5161", {"start": v(58.1, 53.67) * mm, "end": v(58.45, 53.22) * mm});
            skLineSegment(sketch, "E5162", {"start": v(58.45, 53.22) * mm, "end": v(58.6, 53.02) * mm});
            skLineSegment(sketch, "E5163", {"start": v(58.6, 53.02) * mm, "end": v(58.73, 52.83) * mm});
            skLineSegment(sketch, "E5164", {"start": v(66.64, 47.65) * mm, "end": v(67.23, 48.3) * mm});
            skLineSegment(sketch, "E5165", {"start": v(67.23, 48.3) * mm, "end": v(67.79, 48.94) * mm});
            skLineSegment(sketch, "E5166", {"start": v(67.79, 48.94) * mm, "end": v(68.31, 49.57) * mm});
            skLineSegment(sketch, "E5167", {"start": v(68.31, 49.57) * mm, "end": v(68.81, 50.2) * mm});
            skLineSegment(sketch, "E5168", {"start": v(68.81, 50.2) * mm, "end": v(69.57, 51.2) * mm});
            skLineSegment(sketch, "E5169", {"start": v(69.57, 51.2) * mm, "end": v(70.27, 52.17) * mm});
            skLineSegment(sketch, "E5170", {"start": v(70.27, 52.17) * mm, "end": v(70.92, 53.1) * mm});
            skLineSegment(sketch, "E5171", {"start": v(70.92, 53.1) * mm, "end": v(71.5, 53.99) * mm});
            skLineSegment(sketch, "E5172", {"start": v(71.5, 53.99) * mm, "end": v(72.03, 54.75) * mm});
            skLineSegment(sketch, "E5173", {"start": v(72.03, 54.75) * mm, "end": v(72.29, 55.12) * mm});
            skLineSegment(sketch, "E5174", {"start": v(72.29, 55.12) * mm, "end": v(72.52, 55.47) * mm});
            skLineSegment(sketch, "E5175", {"start": v(72.52, 55.47) * mm, "end": v(72.79, 55.92) * mm});
            skLineSegment(sketch, "E5176", {"start": v(72.79, 55.92) * mm, "end": v(72.9, 56.14) * mm});
            skLineSegment(sketch, "E5177", {"start": v(72.9, 56.14) * mm, "end": v(73.02, 56.36) * mm});
            skLineSegment(sketch, "E5178", {"start": v(73.02, 56.36) * mm, "end": v(73.12, 56.58) * mm});
            skLineSegment(sketch, "E5179", {"start": v(73.12, 56.58) * mm, "end": v(73.22, 56.8) * mm});
            skLineSegment(sketch, "E5180", {"start": v(73.22, 56.8) * mm, "end": v(73.3, 57) * mm});
            skLineSegment(sketch, "E5181", {"start": v(73.3, 57) * mm, "end": v(73.36, 57.22) * mm});
            skLineSegment(sketch, "E5182", {"start": v(73.36, 57.22) * mm, "end": v(73.41, 57.45) * mm});
            skLineSegment(sketch, "E5183", {"start": v(73.41, 57.45) * mm, "end": v(73.46, 57.68) * mm});
            skLineSegment(sketch, "E5184", {"start": v(73.46, 57.68) * mm, "end": v(73.5, 57.92) * mm});
            skLineSegment(sketch, "E5185", {"start": v(73.5, 57.92) * mm, "end": v(73.53, 58.16) * mm});
            skLineSegment(sketch, "E5186", {"start": v(73.53, 58.16) * mm, "end": v(73.57, 58.65) * mm});
            skLineSegment(sketch, "E5187", {"start": v(73.57, 58.65) * mm, "end": v(73.6, 59.13) * mm});
            skLineSegment(sketch, "E5188", {"start": v(73.6, 59.13) * mm, "end": v(73.58, 59.61) * mm});
            skLineSegment(sketch, "E5189", {"start": v(73.58, 59.61) * mm, "end": v(73.56, 60.07) * mm});
            skLineSegment(sketch, "E5190", {"start": v(73.56, 60.07) * mm, "end": v(73.5, 60.5) * mm});
            skLineSegment(sketch, "E5191", {"start": v(73.5, 60.5) * mm, "end": v(73.45, 60.9) * mm});
            skLineSegment(sketch, "E5192", {"start": v(73.45, 60.9) * mm, "end": v(73.34, 61.48) * mm});
            skLineSegment(sketch, "E5193", {"start": v(73.34, 61.48) * mm, "end": v(73.27, 61.8) * mm});
            skLineSegment(sketch, "E5194", {"start": v(73.27, 61.8) * mm, "end": v(73.2, 62.11) * mm});
            skLineSegment(sketch, "E5195", {"start": v(73.2, 62.11) * mm, "end": v(73.12, 62.43) * mm});
            skLineSegment(sketch, "E5196", {"start": v(73.12, 62.43) * mm, "end": v(73.03, 62.73) * mm});
            skLineSegment(sketch, "E5197", {"start": v(73.03, 62.73) * mm, "end": v(72.92, 63.01) * mm});
            skLineSegment(sketch, "E5198", {"start": v(72.92, 63.01) * mm, "end": v(72.8, 63.27) * mm});
            skLineSegment(sketch, "E5199", {"start": v(72.8, 63.27) * mm, "end": v(72.66, 63.49) * mm});
            skLineSegment(sketch, "E5200", {"start": v(72.66, 63.49) * mm, "end": v(72.51, 63.71) * mm});
            skLineSegment(sketch, "E5201", {"start": v(72.51, 63.71) * mm, "end": v(72.35, 63.94) * mm});
            skLineSegment(sketch, "E5202", {"start": v(72.35, 63.94) * mm, "end": v(72.16, 64.16) * mm});
            skLineSegment(sketch, "E5203", {"start": v(72.16, 64.16) * mm, "end": v(71.97, 64.37) * mm});
            skLineSegment(sketch, "E5204", {"start": v(71.97, 64.37) * mm, "end": v(71.76, 64.55) * mm});
            skLineSegment(sketch, "E5205", {"start": v(71.76, 64.55) * mm, "end": v(71.66, 64.63) * mm});
            skLineSegment(sketch, "E5206", {"start": v(71.66, 64.63) * mm, "end": v(71.55, 64.7) * mm});
            skLineSegment(sketch, "E5207", {"start": v(71.55, 64.7) * mm, "end": v(71.44, 64.77) * mm});
            skLineSegment(sketch, "E5208", {"start": v(71.44, 64.77) * mm, "end": v(71.33, 64.83) * mm});
            skLineSegment(sketch, "E5209", {"start": v(71.33, 64.83) * mm, "end": v(71.24, 64.86) * mm});
            skLineSegment(sketch, "E5210", {"start": v(71.24, 64.86) * mm, "end": v(71.14, 64.89) * mm});
            skLineSegment(sketch, "E5211", {"start": v(71.14, 64.89) * mm, "end": v(70.93, 64.93) * mm});
            skLineSegment(sketch, "E5212", {"start": v(70.93, 64.93) * mm, "end": v(70.7, 64.95) * mm});
            skLineSegment(sketch, "E5213", {"start": v(70.7, 64.95) * mm, "end": v(70.47, 64.95) * mm});
            skLineSegment(sketch, "E5214", {"start": v(70.47, 64.95) * mm, "end": v(70.24, 64.93) * mm});
            skLineSegment(sketch, "E5215", {"start": v(70.24, 64.93) * mm, "end": v(70.01, 64.9) * mm});
            skLineSegment(sketch, "E5216", {"start": v(70.01, 64.9) * mm, "end": v(69.8, 64.87) * mm});
            skLineSegment(sketch, "E5217", {"start": v(69.8, 64.87) * mm, "end": v(69.6, 64.83) * mm});
            skLineSegment(sketch, "E5218", {"start": v(69.6, 64.83) * mm, "end": v(69.38, 64.77) * mm});
            skLineSegment(sketch, "E5219", {"start": v(69.38, 64.77) * mm, "end": v(69.17, 64.7) * mm});
            skLineSegment(sketch, "E5220", {"start": v(69.17, 64.7) * mm, "end": v(68.95, 64.63) * mm});
            skLineSegment(sketch, "E5221", {"start": v(68.95, 64.63) * mm, "end": v(68.73, 64.54) * mm});
            skLineSegment(sketch, "E5222", {"start": v(68.73, 64.54) * mm, "end": v(68.28, 64.35) * mm});
            skLineSegment(sketch, "E5223", {"start": v(68.28, 64.35) * mm, "end": v(67.83, 64.12) * mm});
            skLineSegment(sketch, "E5224", {"start": v(67.83, 64.12) * mm, "end": v(67.4, 63.88) * mm});
            skLineSegment(sketch, "E5225", {"start": v(67.4, 63.88) * mm, "end": v(66.97, 63.63) * mm});
            skLineSegment(sketch, "E5226", {"start": v(66.97, 63.63) * mm, "end": v(66.57, 63.38) * mm});
            skLineSegment(sketch, "E5227", {"start": v(66.57, 63.38) * mm, "end": v(66.2, 63.13) * mm});
            skLineSegment(sketch, "E5228", {"start": v(66.2, 63.13) * mm, "end": v(65.6, 62.72) * mm});
            skLineSegment(sketch, "E5229", {"start": v(65.6, 62.72) * mm, "end": v(64.98, 62.28) * mm});
            skLineSegment(sketch, "E5230", {"start": v(64.98, 62.28) * mm, "end": v(64.36, 61.8) * mm});
            skLineSegment(sketch, "E5231", {"start": v(64.36, 61.8) * mm, "end": v(64.05, 61.57) * mm});
            skLineSegment(sketch, "E5232", {"start": v(64.05, 61.57) * mm, "end": v(63.75, 61.31) * mm});
            skLineSegment(sketch, "E5233", {"start": v(63.75, 61.31) * mm, "end": v(63.46, 61.06) * mm});
            skLineSegment(sketch, "E5234", {"start": v(63.46, 61.06) * mm, "end": v(63.19, 60.79) * mm});
            skLineSegment(sketch, "E5235", {"start": v(63.19, 60.79) * mm, "end": v(62.93, 60.51) * mm});
            skLineSegment(sketch, "E5236", {"start": v(62.93, 60.51) * mm, "end": v(62.68, 60.23) * mm});
            skLineSegment(sketch, "E5237", {"start": v(62.68, 60.23) * mm, "end": v(62.45, 59.94) * mm});
            skLineSegment(sketch, "E5238", {"start": v(62.45, 59.94) * mm, "end": v(62.25, 59.63) * mm});
            skLineSegment(sketch, "E5239", {"start": v(62.25, 59.63) * mm, "end": v(62.07, 59.32) * mm});
            skLineSegment(sketch, "E5240", {"start": v(62.07, 59.32) * mm, "end": v(61.9, 59) * mm});
            skLineSegment(sketch, "E5241", {"start": v(61.9, 59) * mm, "end": v(61.84, 58.8) * mm});
            skLineSegment(sketch, "E5242", {"start": v(61.84, 58.8) * mm, "end": v(61.77, 58.5) * mm});
            skLineSegment(sketch, "E5243", {"start": v(61.77, 58.5) * mm, "end": v(61.7, 58.21) * mm});
            skLineSegment(sketch, "E5244", {"start": v(61.7, 58.21) * mm, "end": v(61.67, 58) * mm});
            skLineSegment(sketch, "E5245", {"start": v(61.67, 58) * mm, "end": v(61.63, 57.73) * mm});
            skLineSegment(sketch, "E5246", {"start": v(61.63, 57.73) * mm, "end": v(61.58, 57.44) * mm});
            skLineSegment(sketch, "E5247", {"start": v(61.58, 57.44) * mm, "end": v(61.51, 57.12) * mm});
            skLineSegment(sketch, "E5248", {"start": v(61.51, 57.12) * mm, "end": v(61.43, 56.8) * mm});
            skLineSegment(sketch, "E5249", {"start": v(61.43, 56.8) * mm, "end": v(61.33, 56.45) * mm});
            skLineSegment(sketch, "E5250", {"start": v(61.33, 56.45) * mm, "end": v(61.22, 56.1) * mm});
            skLineSegment(sketch, "E5251", {"start": v(61.22, 56.1) * mm, "end": v(61.1, 55.74) * mm});
            skLineSegment(sketch, "E5252", {"start": v(61.1, 55.74) * mm, "end": v(60.96, 55.39) * mm});
            skLineSegment(sketch, "E5253", {"start": v(60.96, 55.39) * mm, "end": v(60.84, 55.1) * mm});
            skLineSegment(sketch, "E5254", {"start": v(60.84, 55.1) * mm, "end": v(60.7, 54.82) * mm});
            skLineSegment(sketch, "E5255", {"start": v(60.7, 54.82) * mm, "end": v(60.44, 54.28) * mm});
            skLineSegment(sketch, "E5256", {"start": v(60.44, 54.28) * mm, "end": v(60.21, 53.84) * mm});
            skLineSegment(sketch, "E5257", {"start": v(60.21, 53.84) * mm, "end": v(59.85, 53.15) * mm});
            skLineSegment(sketch, "E5258", {"start": v(59.85, 53.15) * mm, "end": v(59.46, 52.46) * mm});
            skLineSegment(sketch, "E5259", {"start": v(59.46, 52.46) * mm, "end": v(59.3, 52.2) * mm});
            skLineSegment(sketch, "E5260", {"start": v(59.3, 52.2) * mm, "end": v(59.2, 52.02) * mm});
            skLineSegment(sketch, "E5261", {"start": v(59.2, 52.02) * mm, "end": v(59.26, 51.93) * mm});
            skLineSegment(sketch, "E5262", {"start": v(59.26, 51.93) * mm, "end": v(59.33, 51.81) * mm});
            skLineSegment(sketch, "E5263", {"start": v(59.33, 51.81) * mm, "end": v(59.47, 51.52) * mm});
            skLineSegment(sketch, "E5264", {"start": v(59.47, 51.52) * mm, "end": v(59.6, 51.2) * mm});
            skLineSegment(sketch, "E5265", {"start": v(59.6, 51.2) * mm, "end": v(59.73, 50.9) * mm});
            skLineSegment(sketch, "E5266", {"start": v(59.73, 50.9) * mm, "end": v(59.77, 50.78) * mm});
            skLineSegment(sketch, "E5267", {"start": v(59.77, 50.78) * mm, "end": v(59.8, 50.69) * mm});
            skLineSegment(sketch, "E5268", {"start": v(59.8, 50.69) * mm, "end": v(59.8, 50.65) * mm});
            skLineSegment(sketch, "E5269", {"start": v(59.8, 50.65) * mm, "end": v(59.82, 50.62) * mm});
            skLineSegment(sketch, "E5270", {"start": v(59.82, 50.62) * mm, "end": v(59.85, 50.6) * mm});
            skLineSegment(sketch, "E5271", {"start": v(59.85, 50.6) * mm, "end": v(59.89, 50.59) * mm});
            skLineSegment(sketch, "E5272", {"start": v(59.89, 50.59) * mm, "end": v(59.95, 50.6) * mm});
            skLineSegment(sketch, "E5273", {"start": v(59.95, 50.6) * mm, "end": v(60, 50.62) * mm});
            skLineSegment(sketch, "E5274", {"start": v(60, 50.62) * mm, "end": v(60.07, 50.66) * mm});
            skLineSegment(sketch, "E5275", {"start": v(60.07, 50.66) * mm, "end": v(60.12, 50.72) * mm});
            skLineSegment(sketch, "E5276", {"start": v(60.12, 50.72) * mm, "end": v(60.25, 50.86) * mm});
            skLineSegment(sketch, "E5277", {"start": v(60.25, 50.86) * mm, "end": v(60.39, 51.02) * mm});
            skLineSegment(sketch, "E5278", {"start": v(60.39, 51.02) * mm, "end": v(60.53, 51.17) * mm});
            skLineSegment(sketch, "E5279", {"start": v(60.53, 51.17) * mm, "end": v(60.69, 51.3) * mm});
            skLineSegment(sketch, "E5280", {"start": v(60.69, 51.3) * mm, "end": v(60.85, 51.41) * mm});
            skLineSegment(sketch, "E5281", {"start": v(60.85, 51.41) * mm, "end": v(61, 51.51) * mm});
            skLineSegment(sketch, "E5282", {"start": v(61, 51.51) * mm, "end": v(61.17, 51.6) * mm});
            skLineSegment(sketch, "E5283", {"start": v(61.17, 51.6) * mm, "end": v(61.32, 51.66) * mm});
            skLineSegment(sketch, "E5284", {"start": v(61.32, 51.66) * mm, "end": v(61.46, 51.7) * mm});
            skLineSegment(sketch, "E5285", {"start": v(61.46, 51.7) * mm, "end": v(61.59, 51.74) * mm});
            skLineSegment(sketch, "E5286", {"start": v(61.59, 51.74) * mm, "end": v(61.88, 51.78) * mm});
            skLineSegment(sketch, "E5287", {"start": v(61.88, 51.78) * mm, "end": v(62.02, 51.78) * mm});
            skLineSegment(sketch, "E5288", {"start": v(62.02, 51.78) * mm, "end": v(62.17, 51.78) * mm});
            skLineSegment(sketch, "E5289", {"start": v(62.17, 51.78) * mm, "end": v(62.36, 51.74) * mm});
            skLineSegment(sketch, "E5290", {"start": v(62.36, 51.74) * mm, "end": v(62.55, 51.68) * mm});
            skLineSegment(sketch, "E5291", {"start": v(62.55, 51.68) * mm, "end": v(62.73, 51.6) * mm});
            skLineSegment(sketch, "E5292", {"start": v(62.73, 51.6) * mm, "end": v(62.9, 51.51) * mm});
            skLineSegment(sketch, "E5293", {"start": v(62.9, 51.51) * mm, "end": v(63.08, 51.4) * mm});
            skLineSegment(sketch, "E5294", {"start": v(63.08, 51.4) * mm, "end": v(63.24, 51.27) * mm});
            skLineSegment(sketch, "E5295", {"start": v(63.24, 51.27) * mm, "end": v(63.4, 51.13) * mm});
            skLineSegment(sketch, "E5296", {"start": v(63.4, 51.13) * mm, "end": v(63.57, 50.97) * mm});
            skLineSegment(sketch, "E5297", {"start": v(63.57, 50.97) * mm, "end": v(64.41, 50.11) * mm});
            skLineSegment(sketch, "E5298", {"start": v(64.41, 50.11) * mm, "end": v(65.28, 49.2) * mm});
            skLineSegment(sketch, "E5299", {"start": v(65.28, 49.2) * mm, "end": v(65.62, 48.81) * mm});
            skLineSegment(sketch, "E5300", {"start": v(65.62, 48.81) * mm, "end": v(65.78, 48.62) * mm});
            skLineSegment(sketch, "E5301", {"start": v(65.78, 48.62) * mm, "end": v(65.95, 48.44) * mm});
            skLineSegment(sketch, "E5302", {"start": v(65.95, 48.44) * mm, "end": v(66.15, 48.23) * mm});
            skLineSegment(sketch, "E5303", {"start": v(66.15, 48.23) * mm, "end": v(66.3, 48.03) * mm});
            skLineSegment(sketch, "E5304", {"start": v(66.3, 48.03) * mm, "end": v(66.46, 47.85) * mm});
            skLineSegment(sketch, "E5305", {"start": v(66.46, 47.85) * mm, "end": v(66.64, 47.65) * mm});
            skLineSegment(sketch, "E5306", {"start": v(78.57, 31.64) * mm, "end": v(79.2, 32.1) * mm});
            skLineSegment(sketch, "E5307", {"start": v(79.2, 32.1) * mm, "end": v(80.3, 32.94) * mm});
            skLineSegment(sketch, "E5308", {"start": v(80.3, 32.94) * mm, "end": v(81.74, 34.06) * mm});
            skLineSegment(sketch, "E5309", {"start": v(81.74, 34.06) * mm, "end": v(83.39, 35.37) * mm});
            skLineSegment(sketch, "E5310", {"start": v(83.39, 35.37) * mm, "end": v(84.24, 36.06) * mm});
            skLineSegment(sketch, "E5311", {"start": v(84.24, 36.06) * mm, "end": v(85.09, 36.76) * mm});
            skLineSegment(sketch, "E5312", {"start": v(85.09, 36.76) * mm, "end": v(85.91, 37.46) * mm});
            skLineSegment(sketch, "E5313", {"start": v(85.91, 37.46) * mm, "end": v(86.7, 38.15) * mm});
            skLineSegment(sketch, "E5314", {"start": v(86.7, 38.15) * mm, "end": v(87.43, 38.8) * mm});
            skLineSegment(sketch, "E5315", {"start": v(87.43, 38.8) * mm, "end": v(88.1, 39.42) * mm});
            skLineSegment(sketch, "E5316", {"start": v(88.1, 39.42) * mm, "end": v(88.66, 39.98) * mm});
            skLineSegment(sketch, "E5317", {"start": v(88.66, 39.98) * mm, "end": v(88.9, 40.24) * mm});
            skLineSegment(sketch, "E5318", {"start": v(88.9, 40.24) * mm, "end": v(89.11, 40.48) * mm});
            skLineSegment(sketch, "E5319", {"start": v(89.11, 40.48) * mm, "end": v(89.25, 41) * mm});
            skLineSegment(sketch, "E5320", {"start": v(89.25, 41) * mm, "end": v(89.41, 41.55) * mm});
            skLineSegment(sketch, "E5321", {"start": v(89.41, 41.55) * mm, "end": v(89.57, 42.1) * mm});
            skLineSegment(sketch, "E5322", {"start": v(89.57, 42.1) * mm, "end": v(89.71, 42.62) * mm});
            skLineSegment(sketch, "E5323", {"start": v(89.71, 42.62) * mm, "end": v(90, 43.9) * mm});
            skLineSegment(sketch, "E5324", {"start": v(90, 43.9) * mm, "end": v(90.25, 45.1) * mm});
            skLineSegment(sketch, "E5325", {"start": v(90.25, 45.1) * mm, "end": v(90.46, 46.2) * mm});
            skLineSegment(sketch, "E5326", {"start": v(90.46, 46.2) * mm, "end": v(90.62, 47.22) * mm});
            skLineSegment(sketch, "E5327", {"start": v(90.62, 47.22) * mm, "end": v(90.75, 48.16) * mm});
            skLineSegment(sketch, "E5328", {"start": v(90.75, 48.16) * mm, "end": v(90.8, 48.61) * mm});
            skLineSegment(sketch, "E5329", {"start": v(90.8, 48.61) * mm, "end": v(90.84, 49.04) * mm});
            skLineSegment(sketch, "E5330", {"start": v(90.84, 49.04) * mm, "end": v(90.87, 49.46) * mm});
            skLineSegment(sketch, "E5331", {"start": v(90.87, 49.46) * mm, "end": v(90.9, 49.87) * mm});
            skLineSegment(sketch, "E5332", {"start": v(90.9, 49.87) * mm, "end": v(90.9, 50.26) * mm});
            skLineSegment(sketch, "E5333", {"start": v(90.9, 50.26) * mm, "end": v(90.91, 50.65) * mm});
            skLineSegment(sketch, "E5334", {"start": v(90.91, 50.65) * mm, "end": v(90.92, 50.87) * mm});
            skLineSegment(sketch, "E5335", {"start": v(90.92, 50.87) * mm, "end": v(90.94, 51.1) * mm});
            skLineSegment(sketch, "E5336", {"start": v(90.94, 51.1) * mm, "end": v(91, 51.6) * mm});
            skLineSegment(sketch, "E5337", {"start": v(91, 51.6) * mm, "end": v(91.01, 51.85) * mm});
            skLineSegment(sketch, "E5338", {"start": v(91.01, 51.85) * mm, "end": v(91, 52.08) * mm});
            skLineSegment(sketch, "E5339", {"start": v(91, 52.08) * mm, "end": v(91, 52.2) * mm});
            skLineSegment(sketch, "E5340", {"start": v(91, 52.2) * mm, "end": v(90.98, 52.3) * mm});
            skLineSegment(sketch, "E5341", {"start": v(90.98, 52.3) * mm, "end": v(90.95, 52.41) * mm});
            skLineSegment(sketch, "E5342", {"start": v(90.95, 52.41) * mm, "end": v(90.91, 52.51) * mm});
            skLineSegment(sketch, "E5343", {"start": v(90.91, 52.51) * mm, "end": v(90.82, 52.68) * mm});
            skLineSegment(sketch, "E5344", {"start": v(90.82, 52.68) * mm, "end": v(90.7, 52.85) * mm});
            skLineSegment(sketch, "E5345", {"start": v(90.7, 52.85) * mm, "end": v(90.56, 53) * mm});
            skLineSegment(sketch, "E5346", {"start": v(90.56, 53) * mm, "end": v(90.4, 53.16) * mm});
            skLineSegment(sketch, "E5347", {"start": v(90.4, 53.16) * mm, "end": v(90.24, 53.3) * mm});
            skLineSegment(sketch, "E5348", {"start": v(90.24, 53.3) * mm, "end": v(90.06, 53.42) * mm});
            skLineSegment(sketch, "E5349", {"start": v(90.06, 53.42) * mm, "end": v(89.88, 53.53) * mm});
            skLineSegment(sketch, "E5350", {"start": v(89.88, 53.53) * mm, "end": v(89.7, 53.6) * mm});
            skLineSegment(sketch, "E5351", {"start": v(89.7, 53.6) * mm, "end": v(89.64, 53.62) * mm});
            skLineSegment(sketch, "E5352", {"start": v(89.64, 53.62) * mm, "end": v(89.58, 53.63) * mm});
            skLineSegment(sketch, "E5353", {"start": v(89.58, 53.63) * mm, "end": v(89.43, 53.63) * mm});
            skLineSegment(sketch, "E5354", {"start": v(89.43, 53.63) * mm, "end": v(89.28, 53.61) * mm});
            skLineSegment(sketch, "E5355", {"start": v(89.28, 53.61) * mm, "end": v(89.14, 53.6) * mm});
            skLineSegment(sketch, "E5356", {"start": v(89.14, 53.6) * mm, "end": v(89, 53.59) * mm});
            skLineSegment(sketch, "E5357", {"start": v(89, 53.59) * mm, "end": v(88.8, 53.54) * mm});
            skLineSegment(sketch, "E5358", {"start": v(88.8, 53.54) * mm, "end": v(88.56, 53.47) * mm});
            skLineSegment(sketch, "E5359", {"start": v(88.56, 53.47) * mm, "end": v(88.29, 53.37) * mm});
            skLineSegment(sketch, "E5360", {"start": v(88.29, 53.37) * mm, "end": v(87.99, 53.25) * mm});
            skLineSegment(sketch, "E5361", {"start": v(87.99, 53.25) * mm, "end": v(87.67, 53.12) * mm});
            skLineSegment(sketch, "E5362", {"start": v(87.67, 53.12) * mm, "end": v(87.35, 52.97) * mm});
            skLineSegment(sketch, "E5363", {"start": v(87.35, 52.97) * mm, "end": v(87.02, 52.8) * mm});
            skLineSegment(sketch, "E5364", {"start": v(87.02, 52.8) * mm, "end": v(86.64, 52.64) * mm});
            skLineSegment(sketch, "E5365", {"start": v(86.64, 52.64) * mm, "end": v(86.21, 52.46) * mm});
            skLineSegment(sketch, "E5366", {"start": v(86.21, 52.46) * mm, "end": v(86, 52.36) * mm});
            skLineSegment(sketch, "E5367", {"start": v(86, 52.36) * mm, "end": v(85.8, 52.26) * mm});
            skLineSegment(sketch, "E5368", {"start": v(85.8, 52.26) * mm, "end": v(85.62, 52.14) * mm});
            skLineSegment(sketch, "E5369", {"start": v(85.62, 52.14) * mm, "end": v(85.54, 52.08) * mm});
            skLineSegment(sketch, "E5370", {"start": v(85.54, 52.08) * mm, "end": v(85.47, 52.01) * mm});
            skLineSegment(sketch, "E5371", {"start": v(85.47, 52.01) * mm, "end": v(85.33, 51.86) * mm});
            skLineSegment(sketch, "E5372", {"start": v(85.33, 51.86) * mm, "end": v(85.22, 51.7) * mm});
            skLineSegment(sketch, "E5373", {"start": v(85.22, 51.7) * mm, "end": v(85.1, 51.51) * mm});
            skLineSegment(sketch, "E5374", {"start": v(85.1, 51.51) * mm, "end": v(85.01, 51.32) * mm});
            skLineSegment(sketch, "E5375", {"start": v(85.01, 51.32) * mm, "end": v(84.83, 50.89) * mm});
            skLineSegment(sketch, "E5376", {"start": v(84.83, 50.89) * mm, "end": v(84.64, 50.42) * mm});
            skLineSegment(sketch, "E5377", {"start": v(84.64, 50.42) * mm, "end": v(84.4, 49.85) * mm});
            skLineSegment(sketch, "E5378", {"start": v(84.4, 49.85) * mm, "end": v(84.3, 49.59) * mm});
            skLineSegment(sketch, "E5379", {"start": v(84.3, 49.59) * mm, "end": v(84.17, 49.3) * mm});
            skLineSegment(sketch, "E5380", {"start": v(84.17, 49.3) * mm, "end": v(84.02, 49) * mm});
            skLineSegment(sketch, "E5381", {"start": v(84.02, 49) * mm, "end": v(83.82, 48.62) * mm});
            skLineSegment(sketch, "E5382", {"start": v(83.82, 48.62) * mm, "end": v(83.56, 48.16) * mm});
            skLineSegment(sketch, "E5383", {"start": v(83.56, 48.16) * mm, "end": v(83.24, 47.59) * mm});
            skLineSegment(sketch, "E5384", {"start": v(83.24, 47.59) * mm, "end": v(82.88, 47.04) * mm});
            skLineSegment(sketch, "E5385", {"start": v(82.88, 47.04) * mm, "end": v(82.48, 46.47) * mm});
            skLineSegment(sketch, "E5386", {"start": v(82.48, 46.47) * mm, "end": v(82.06, 45.88) * mm});
            skLineSegment(sketch, "E5387", {"start": v(82.06, 45.88) * mm, "end": v(81.6, 45.29) * mm});
            skLineSegment(sketch, "E5388", {"start": v(81.6, 45.29) * mm, "end": v(81.13, 44.68) * mm});
            skLineSegment(sketch, "E5389", {"start": v(81.13, 44.68) * mm, "end": v(80.63, 44.07) * mm});
            skLineSegment(sketch, "E5390", {"start": v(80.63, 44.07) * mm, "end": v(80.12, 43.46) * mm});
            skLineSegment(sketch, "E5391", {"start": v(80.12, 43.46) * mm, "end": v(79.6, 42.85) * mm});
            skLineSegment(sketch, "E5392", {"start": v(79.6, 42.85) * mm, "end": v(79.06, 42.25) * mm});
            skLineSegment(sketch, "E5393", {"start": v(79.06, 42.25) * mm, "end": v(78.52, 41.66) * mm});
            skLineSegment(sketch, "E5394", {"start": v(78.52, 41.66) * mm, "end": v(77.98, 41.09) * mm});
            skLineSegment(sketch, "E5395", {"start": v(77.98, 41.09) * mm, "end": v(77.44, 40.53) * mm});
            skLineSegment(sketch, "E5396", {"start": v(77.44, 40.53) * mm, "end": v(76.9, 40) * mm});
            skLineSegment(sketch, "E5397", {"start": v(76.9, 40) * mm, "end": v(76.37, 39.5) * mm});
            skLineSegment(sketch, "E5398", {"start": v(76.37, 39.5) * mm, "end": v(75.85, 39.01) * mm});
            skLineSegment(sketch, "E5399", {"start": v(75.85, 39.01) * mm, "end": v(75.35, 38.57) * mm});
            skLineSegment(sketch, "E5400", {"start": v(75.35, 38.57) * mm, "end": v(75.41, 38.47) * mm});
            skLineSegment(sketch, "E5401", {"start": v(75.41, 38.47) * mm, "end": v(75.48, 38.36) * mm});
            skLineSegment(sketch, "E5402", {"start": v(75.48, 38.36) * mm, "end": v(75.62, 38.1) * mm});
            skLineSegment(sketch, "E5403", {"start": v(75.62, 38.1) * mm, "end": v(75.77, 37.8) * mm});
            skLineSegment(sketch, "E5404", {"start": v(75.77, 37.8) * mm, "end": v(75.93, 37.5) * mm});
            skLineSegment(sketch, "E5405", {"start": v(75.93, 37.5) * mm, "end": v(76.23, 36.97) * mm});
            skLineSegment(sketch, "E5406", {"start": v(76.23, 36.97) * mm, "end": v(76.54, 36.36) * mm});
            skLineSegment(sketch, "E5407", {"start": v(76.54, 36.36) * mm, "end": v(76.87, 35.68) * mm});
            skLineSegment(sketch, "E5408", {"start": v(76.87, 35.68) * mm, "end": v(77.22, 34.95) * mm});
            skLineSegment(sketch, "E5409", {"start": v(77.22, 34.95) * mm, "end": v(77.56, 34.17) * mm});
            skLineSegment(sketch, "E5410", {"start": v(77.56, 34.17) * mm, "end": v(77.9, 33.35) * mm});
            skLineSegment(sketch, "E5411", {"start": v(77.9, 33.35) * mm, "end": v(78.24, 32.5) * mm});
            skLineSegment(sketch, "E5412", {"start": v(78.24, 32.5) * mm, "end": v(78.57, 31.64) * mm});
            skLineSegment(sketch, "E5413", {"start": v(83.32, 23.83) * mm, "end": v(83.62, 23.99) * mm});
            skLineSegment(sketch, "E5414", {"start": v(83.62, 23.99) * mm, "end": v(84.16, 24.3) * mm});
            skLineSegment(sketch, "E5415", {"start": v(84.16, 24.3) * mm, "end": v(84.89, 24.75) * mm});
            skLineSegment(sketch, "E5416", {"start": v(84.89, 24.75) * mm, "end": v(85.7, 25.26) * mm});
            skLineSegment(sketch, "E5417", {"start": v(85.7, 25.26) * mm, "end": v(86.56, 25.81) * mm});
            skLineSegment(sketch, "E5418", {"start": v(86.56, 25.81) * mm, "end": v(87.36, 26.35) * mm});
            skLineSegment(sketch, "E5419", {"start": v(87.36, 26.35) * mm, "end": v(87.72, 26.6) * mm});
            skLineSegment(sketch, "E5420", {"start": v(87.72, 26.6) * mm, "end": v(88.04, 26.83) * mm});
            skLineSegment(sketch, "E5421", {"start": v(88.04, 26.83) * mm, "end": v(88.3, 27.03) * mm});
            skLineSegment(sketch, "E5422", {"start": v(88.3, 27.03) * mm, "end": v(88.52, 27.2) * mm});
            skLineSegment(sketch, "E5423", {"start": v(88.52, 27.2) * mm, "end": v(89.1, 27.73) * mm});
            skLineSegment(sketch, "E5424", {"start": v(89.1, 27.73) * mm, "end": v(89.69, 28.3) * mm});
            skLineSegment(sketch, "E5425", {"start": v(89.69, 28.3) * mm, "end": v(90.28, 28.91) * mm});
            skLineSegment(sketch, "E5426", {"start": v(90.28, 28.91) * mm, "end": v(90.88, 29.55) * mm});
            skLineSegment(sketch, "E5427", {"start": v(90.88, 29.55) * mm, "end": v(91.45, 30.2) * mm});
            skLineSegment(sketch, "E5428", {"start": v(91.45, 30.2) * mm, "end": v(92, 30.85) * mm});
            skLineSegment(sketch, "E5429", {"start": v(92, 30.85) * mm, "end": v(92.51, 31.5) * mm});
            skLineSegment(sketch, "E5430", {"start": v(92.51, 31.5) * mm, "end": v(92.75, 31.82) * mm});
            skLineSegment(sketch, "E5431", {"start": v(92.75, 31.82) * mm, "end": v(92.97, 32.13) * mm});
            skLineSegment(sketch, "E5432", {"start": v(92.97, 32.13) * mm, "end": v(93.46, 32.85) * mm});
            skLineSegment(sketch, "E5433", {"start": v(93.46, 32.85) * mm, "end": v(93.72, 33.24) * mm});
            skLineSegment(sketch, "E5434", {"start": v(93.72, 33.24) * mm, "end": v(93.97, 33.65) * mm});
            skLineSegment(sketch, "E5435", {"start": v(93.97, 33.65) * mm, "end": v(94.2, 34.06) * mm});
            skLineSegment(sketch, "E5436", {"start": v(94.2, 34.06) * mm, "end": v(94.4, 34.48) * mm});
            skLineSegment(sketch, "E5437", {"start": v(94.4, 34.48) * mm, "end": v(94.49, 34.68) * mm});
            skLineSegment(sketch, "E5438", {"start": v(94.49, 34.68) * mm, "end": v(94.56, 34.89) * mm});
            skLineSegment(sketch, "E5439", {"start": v(94.56, 34.89) * mm, "end": v(94.63, 35.1) * mm});
            skLineSegment(sketch, "E5440", {"start": v(94.63, 35.1) * mm, "end": v(94.68, 35.3) * mm});
            skLineSegment(sketch, "E5441", {"start": v(94.68, 35.3) * mm, "end": v(94.77, 35.7) * mm});
            skLineSegment(sketch, "E5442", {"start": v(94.77, 35.7) * mm, "end": v(94.85, 36.15) * mm});
            skLineSegment(sketch, "E5443", {"start": v(94.85, 36.15) * mm, "end": v(94.9, 36.61) * mm});
            skLineSegment(sketch, "E5444", {"start": v(94.9, 36.61) * mm, "end": v(94.94, 37.09) * mm});
            skLineSegment(sketch, "E5445", {"start": v(94.94, 37.09) * mm, "end": v(94.94, 37.33) * mm});
            skLineSegment(sketch, "E5446", {"start": v(94.94, 37.33) * mm, "end": v(94.94, 37.56) * mm});
            skLineSegment(sketch, "E5447", {"start": v(94.94, 37.56) * mm, "end": v(94.93, 37.8) * mm});
            skLineSegment(sketch, "E5448", {"start": v(94.93, 37.8) * mm, "end": v(94.9, 38.02) * mm});
            skLineSegment(sketch, "E5449", {"start": v(94.9, 38.02) * mm, "end": v(94.87, 38.24) * mm});
            skLineSegment(sketch, "E5450", {"start": v(94.87, 38.24) * mm, "end": v(94.82, 38.45) * mm});
            skLineSegment(sketch, "E5451", {"start": v(94.82, 38.45) * mm, "end": v(94.76, 38.65) * mm});
            skLineSegment(sketch, "E5452", {"start": v(94.76, 38.65) * mm, "end": v(94.68, 38.83) * mm});
            skLineSegment(sketch, "E5453", {"start": v(94.68, 38.83) * mm, "end": v(94.62, 38.96) * mm});
            skLineSegment(sketch, "E5454", {"start": v(94.62, 38.96) * mm, "end": v(94.55, 39.08) * mm});
            skLineSegment(sketch, "E5455", {"start": v(94.55, 39.08) * mm, "end": v(94.46, 39.2) * mm});
            skLineSegment(sketch, "E5456", {"start": v(94.46, 39.2) * mm, "end": v(94.37, 39.32) * mm});
            skLineSegment(sketch, "E5457", {"start": v(94.37, 39.32) * mm, "end": v(94.15, 39.55) * mm});
            skLineSegment(sketch, "E5458", {"start": v(94.15, 39.55) * mm, "end": v(93.91, 39.77) * mm});
            skLineSegment(sketch, "E5459", {"start": v(93.91, 39.77) * mm, "end": v(93.65, 39.97) * mm});
            skLineSegment(sketch, "E5460", {"start": v(93.65, 39.97) * mm, "end": v(93.38, 40.15) * mm});
            skLineSegment(sketch, "E5461", {"start": v(93.38, 40.15) * mm, "end": v(93.12, 40.3) * mm});
            skLineSegment(sketch, "E5462", {"start": v(93.12, 40.3) * mm, "end": v(92.86, 40.4) * mm});
            skLineSegment(sketch, "E5463", {"start": v(92.86, 40.4) * mm, "end": v(92.53, 40.52) * mm});
            skLineSegment(sketch, "E5464", {"start": v(92.53, 40.52) * mm, "end": v(92.17, 40.63) * mm});
            skLineSegment(sketch, "E5465", {"start": v(92.17, 40.63) * mm, "end": v(91.8, 40.72) * mm});
            skLineSegment(sketch, "E5466", {"start": v(91.8, 40.72) * mm, "end": v(91.6, 40.75) * mm});
            skLineSegment(sketch, "E5467", {"start": v(91.6, 40.75) * mm, "end": v(91.4, 40.78) * mm});
            skLineSegment(sketch, "E5468", {"start": v(91.4, 40.78) * mm, "end": v(91.21, 40.79) * mm});
            skLineSegment(sketch, "E5469", {"start": v(91.21, 40.79) * mm, "end": v(91.03, 40.8) * mm});
            skLineSegment(sketch, "E5470", {"start": v(91.03, 40.8) * mm, "end": v(90.85, 40.78) * mm});
            skLineSegment(sketch, "E5471", {"start": v(90.85, 40.78) * mm, "end": v(90.68, 40.75) * mm});
            skLineSegment(sketch, "E5472", {"start": v(90.68, 40.75) * mm, "end": v(90.53, 40.7) * mm});
            skLineSegment(sketch, "E5473", {"start": v(90.53, 40.7) * mm, "end": v(90.38, 40.63) * mm});
            skLineSegment(sketch, "E5474", {"start": v(90.38, 40.63) * mm, "end": v(90.25, 40.54) * mm});
            skLineSegment(sketch, "E5475", {"start": v(90.25, 40.54) * mm, "end": v(90.14, 40.43) * mm});
            skLineSegment(sketch, "E5476", {"start": v(90.14, 40.43) * mm, "end": v(89.93, 40.18) * mm});
            skLineSegment(sketch, "E5477", {"start": v(89.93, 40.18) * mm, "end": v(89.7, 39.92) * mm});
            skLineSegment(sketch, "E5478", {"start": v(89.7, 39.92) * mm, "end": v(89.17, 39.35) * mm});
            skLineSegment(sketch, "E5479", {"start": v(89.17, 39.35) * mm, "end": v(88.57, 38.76) * mm});
            skLineSegment(sketch, "E5480", {"start": v(88.57, 38.76) * mm, "end": v(87.9, 38.13) * mm});
            skLineSegment(sketch, "E5481", {"start": v(87.9, 38.13) * mm, "end": v(87.2, 37.48) * mm});
            skLineSegment(sketch, "E5482", {"start": v(87.2, 37.48) * mm, "end": v(86.44, 36.82) * mm});
            skLineSegment(sketch, "E5483", {"start": v(86.44, 36.82) * mm, "end": v(85.64, 36.15) * mm});
            skLineSegment(sketch, "E5484", {"start": v(85.64, 36.15) * mm, "end": v(84.81, 35.47) * mm});
            skLineSegment(sketch, "E5485", {"start": v(84.81, 35.47) * mm, "end": v(83.55, 34.46) * mm});
            skLineSegment(sketch, "E5486", {"start": v(83.55, 34.46) * mm, "end": v(81.77, 33.06) * mm});
            skLineSegment(sketch, "E5487", {"start": v(81.77, 33.06) * mm, "end": v(80.02, 31.7) * mm});
            skLineSegment(sketch, "E5488", {"start": v(80.02, 31.7) * mm, "end": v(79.33, 31.17) * mm});
            skLineSegment(sketch, "E5489", {"start": v(79.33, 31.17) * mm, "end": v(78.85, 30.82) * mm});
            skLineSegment(sketch, "E5490", {"start": v(78.85, 30.82) * mm, "end": v(78.99, 30.29) * mm});
            skLineSegment(sketch, "E5491", {"start": v(78.99, 30.29) * mm, "end": v(79.14, 29.74) * mm});
            skLineSegment(sketch, "E5492", {"start": v(79.14, 29.74) * mm, "end": v(79.29, 29.2) * mm});
            skLineSegment(sketch, "E5493", {"start": v(79.29, 29.2) * mm, "end": v(79.35, 28.93) * mm});
            skLineSegment(sketch, "E5494", {"start": v(79.35, 28.93) * mm, "end": v(79.4, 28.66) * mm});
            skLineSegment(sketch, "E5495", {"start": v(79.4, 28.66) * mm, "end": v(79.57, 27.91) * mm});
            skLineSegment(sketch, "E5496", {"start": v(79.57, 27.91) * mm, "end": v(79.75, 27.1) * mm});
            skLineSegment(sketch, "E5497", {"start": v(79.75, 27.1) * mm, "end": v(79.84, 26.64) * mm});
            skLineSegment(sketch, "E5498", {"start": v(79.84, 26.64) * mm, "end": v(79.91, 26.2) * mm});
            skLineSegment(sketch, "E5499", {"start": v(79.91, 26.2) * mm, "end": v(79.93, 26.03) * mm});
            skLineSegment(sketch, "E5500", {"start": v(79.93, 26.03) * mm, "end": v(79.95, 25.73) * mm});
            skLineSegment(sketch, "E5501", {"start": v(79.95, 25.73) * mm, "end": v(79.97, 25.57) * mm});
            skLineSegment(sketch, "E5502", {"start": v(79.97, 25.57) * mm, "end": v(80, 25.43) * mm});
            skLineSegment(sketch, "E5503", {"start": v(80, 25.43) * mm, "end": v(80.04, 25.33) * mm});
            skLineSegment(sketch, "E5504", {"start": v(80.04, 25.33) * mm, "end": v(80.07, 25.29) * mm});
            skLineSegment(sketch, "E5505", {"start": v(80.07, 25.29) * mm, "end": v(80.1, 25.27) * mm});
            skLineSegment(sketch, "E5506", {"start": v(80.1, 25.27) * mm, "end": v(80.15, 25.26) * mm});
            skLineSegment(sketch, "E5507", {"start": v(80.15, 25.26) * mm, "end": v(80.21, 25.26) * mm});
            skLineSegment(sketch, "E5508", {"start": v(80.21, 25.26) * mm, "end": v(80.36, 25.31) * mm});
            skLineSegment(sketch, "E5509", {"start": v(80.36, 25.31) * mm, "end": v(80.54, 25.38) * mm});
            skLineSegment(sketch, "E5510", {"start": v(80.54, 25.38) * mm, "end": v(80.72, 25.46) * mm});
            skLineSegment(sketch, "E5511", {"start": v(80.72, 25.46) * mm, "end": v(80.91, 25.55) * mm});
            skLineSegment(sketch, "E5512", {"start": v(80.91, 25.55) * mm, "end": v(81, 25.58) * mm});
            skLineSegment(sketch, "E5513", {"start": v(81, 25.58) * mm, "end": v(81.06, 25.6) * mm});
            skLineSegment(sketch, "E5514", {"start": v(81.06, 25.6) * mm, "end": v(81.34, 25.66) * mm});
            skLineSegment(sketch, "E5515", {"start": v(81.34, 25.66) * mm, "end": v(81.5, 25.68) * mm});
            skLineSegment(sketch, "E5516", {"start": v(81.5, 25.68) * mm, "end": v(81.65, 25.7) * mm});
            skLineSegment(sketch, "E5517", {"start": v(81.65, 25.7) * mm, "end": v(81.78, 25.69) * mm});
            skLineSegment(sketch, "E5518", {"start": v(81.78, 25.69) * mm, "end": v(81.9, 25.67) * mm});
            skLineSegment(sketch, "E5519", {"start": v(81.9, 25.67) * mm, "end": v(82.02, 25.64) * mm});
            skLineSegment(sketch, "E5520", {"start": v(82.02, 25.64) * mm, "end": v(82.13, 25.6) * mm});
            skLineSegment(sketch, "E5521", {"start": v(82.13, 25.6) * mm, "end": v(82.26, 25.5) * mm});
            skLineSegment(sketch, "E5522", {"start": v(82.26, 25.5) * mm, "end": v(82.35, 25.42) * mm});
            skLineSegment(sketch, "E5523", {"start": v(82.35, 25.42) * mm, "end": v(82.4, 25.36) * mm});
            skLineSegment(sketch, "E5524", {"start": v(82.4, 25.36) * mm, "end": v(82.45, 25.29) * mm});
            skLineSegment(sketch, "E5525", {"start": v(82.45, 25.29) * mm, "end": v(82.58, 25.1) * mm});
            skLineSegment(sketch, "E5526", {"start": v(82.58, 25.1) * mm, "end": v(82.7, 24.9) * mm});
            skLineSegment(sketch, "E5527", {"start": v(82.7, 24.9) * mm, "end": v(82.78, 24.72) * mm});
            skLineSegment(sketch, "E5528", {"start": v(82.78, 24.72) * mm, "end": v(82.92, 24.5) * mm});
            skLineSegment(sketch, "E5529", {"start": v(82.92, 24.5) * mm, "end": v(83.04, 24.31) * mm});
            skLineSegment(sketch, "E5530", {"start": v(83.04, 24.31) * mm, "end": v(83.16, 24.11) * mm});
            skLineSegment(sketch, "E5531", {"start": v(83.16, 24.11) * mm, "end": v(83.32, 23.83) * mm});
            skLineSegment(sketch, "E5532", {"start": v(86, 17.17) * mm, "end": v(86.15, 17.23) * mm});
            skLineSegment(sketch, "E5533", {"start": v(86.15, 17.23) * mm, "end": v(86.4, 17.34) * mm});
            skLineSegment(sketch, "E5534", {"start": v(86.4, 17.34) * mm, "end": v(87.11, 17.7) * mm});
            skLineSegment(sketch, "E5535", {"start": v(87.11, 17.7) * mm, "end": v(88.05, 18.2) * mm});
            skLineSegment(sketch, "E5536", {"start": v(88.05, 18.2) * mm, "end": v(89.11, 18.8) * mm});
            skLineSegment(sketch, "E5537", {"start": v(89.11, 18.8) * mm, "end": v(90.2, 19.42) * mm});
            skLineSegment(sketch, "E5538", {"start": v(90.2, 19.42) * mm, "end": v(90.73, 19.74) * mm});
            skLineSegment(sketch, "E5539", {"start": v(90.73, 19.74) * mm, "end": v(91.23, 20.06) * mm});
            skLineSegment(sketch, "E5540", {"start": v(91.23, 20.06) * mm, "end": v(91.69, 20.36) * mm});
            skLineSegment(sketch, "E5541", {"start": v(91.69, 20.36) * mm, "end": v(92.09, 20.64) * mm});
            skLineSegment(sketch, "E5542", {"start": v(92.09, 20.64) * mm, "end": v(92.43, 20.9) * mm});
            skLineSegment(sketch, "E5543", {"start": v(92.43, 20.9) * mm, "end": v(92.57, 21.02) * mm});
            skLineSegment(sketch, "E5544", {"start": v(92.57, 21.02) * mm, "end": v(92.69, 21.13) * mm});
            skLineSegment(sketch, "E5545", {"start": v(92.69, 21.13) * mm, "end": v(93, 21.42) * mm});
            skLineSegment(sketch, "E5546", {"start": v(93, 21.42) * mm, "end": v(93.35, 21.72) * mm});
            skLineSegment(sketch, "E5547", {"start": v(93.35, 21.72) * mm, "end": v(93.52, 21.88) * mm});
            skLineSegment(sketch, "E5548", {"start": v(93.52, 21.88) * mm, "end": v(93.69, 22.04) * mm});
            skLineSegment(sketch, "E5549", {"start": v(93.69, 22.04) * mm, "end": v(93.84, 22.2) * mm});
            skLineSegment(sketch, "E5550", {"start": v(93.84, 22.2) * mm, "end": v(93.96, 22.37) * mm});
            skLineSegment(sketch, "E5551", {"start": v(93.96, 22.37) * mm, "end": v(94.2, 22.73) * mm});
            skLineSegment(sketch, "E5552", {"start": v(94.2, 22.73) * mm, "end": v(94.45, 23.12) * mm});
            skLineSegment(sketch, "E5553", {"start": v(94.45, 23.12) * mm, "end": v(94.68, 23.54) * mm});
            skLineSegment(sketch, "E5554", {"start": v(94.68, 23.54) * mm, "end": v(94.9, 23.98) * mm});
            skLineSegment(sketch, "E5555", {"start": v(94.9, 23.98) * mm, "end": v(95.1, 24.42) * mm});
            skLineSegment(sketch, "E5556", {"start": v(95.1, 24.42) * mm, "end": v(95.27, 24.87) * mm});
            skLineSegment(sketch, "E5557", {"start": v(95.27, 24.87) * mm, "end": v(95.42, 25.3) * mm});
            skLineSegment(sketch, "E5558", {"start": v(95.42, 25.3) * mm, "end": v(95.48, 25.52) * mm});
            skLineSegment(sketch, "E5559", {"start": v(95.48, 25.52) * mm, "end": v(95.53, 25.72) * mm});
            skLineSegment(sketch, "E5560", {"start": v(95.53, 25.72) * mm, "end": v(95.58, 26) * mm});
            skLineSegment(sketch, "E5561", {"start": v(95.58, 26) * mm, "end": v(95.62, 26.3) * mm});
            skLineSegment(sketch, "E5562", {"start": v(95.62, 26.3) * mm, "end": v(95.64, 26.63) * mm});
            skLineSegment(sketch, "E5563", {"start": v(95.64, 26.63) * mm, "end": v(95.65, 26.95) * mm});
            skLineSegment(sketch, "E5564", {"start": v(95.65, 26.95) * mm, "end": v(95.64, 27.27) * mm});
            skLineSegment(sketch, "E5565", {"start": v(95.64, 27.27) * mm, "end": v(95.62, 27.6) * mm});
            skLineSegment(sketch, "E5566", {"start": v(95.62, 27.6) * mm, "end": v(95.58, 27.9) * mm});
            skLineSegment(sketch, "E5567", {"start": v(95.58, 27.9) * mm, "end": v(95.53, 28.18) * mm});
            skLineSegment(sketch, "E5568", {"start": v(95.53, 28.18) * mm, "end": v(95.46, 28.46) * mm});
            skLineSegment(sketch, "E5569", {"start": v(95.46, 28.46) * mm, "end": v(95.37, 28.76) * mm});
            skLineSegment(sketch, "E5570", {"start": v(95.37, 28.76) * mm, "end": v(95.25, 29.07) * mm});
            skLineSegment(sketch, "E5571", {"start": v(95.25, 29.07) * mm, "end": v(95.12, 29.38) * mm});
            skLineSegment(sketch, "E5572", {"start": v(95.12, 29.38) * mm, "end": v(94.98, 29.68) * mm});
            skLineSegment(sketch, "E5573", {"start": v(94.98, 29.68) * mm, "end": v(94.82, 29.96) * mm});
            skLineSegment(sketch, "E5574", {"start": v(94.82, 29.96) * mm, "end": v(94.64, 30.22) * mm});
            skLineSegment(sketch, "E5575", {"start": v(94.64, 30.22) * mm, "end": v(94.55, 30.34) * mm});
            skLineSegment(sketch, "E5576", {"start": v(94.55, 30.34) * mm, "end": v(94.45, 30.45) * mm});
            skLineSegment(sketch, "E5577", {"start": v(94.45, 30.45) * mm, "end": v(94.32, 30.58) * mm});
            skLineSegment(sketch, "E5578", {"start": v(94.32, 30.58) * mm, "end": v(94.18, 30.7) * mm});
            skLineSegment(sketch, "E5579", {"start": v(94.18, 30.7) * mm, "end": v(94.05, 30.8) * mm});
            skLineSegment(sketch, "E5580", {"start": v(94.05, 30.8) * mm, "end": v(93.91, 30.9) * mm});
            skLineSegment(sketch, "E5581", {"start": v(93.91, 30.9) * mm, "end": v(93.63, 31.06) * mm});
            skLineSegment(sketch, "E5582", {"start": v(93.63, 31.06) * mm, "end": v(93.3, 31.24) * mm});
            skLineSegment(sketch, "E5583", {"start": v(93.3, 31.24) * mm, "end": v(92.97, 30.77) * mm});
            skLineSegment(sketch, "E5584", {"start": v(92.97, 30.77) * mm, "end": v(92.62, 30.3) * mm});
            skLineSegment(sketch, "E5585", {"start": v(92.62, 30.3) * mm, "end": v(92.16, 29.73) * mm});
            skLineSegment(sketch, "E5586", {"start": v(92.16, 29.73) * mm, "end": v(91.9, 29.4) * mm});
            skLineSegment(sketch, "E5587", {"start": v(91.9, 29.4) * mm, "end": v(91.6, 29.07) * mm});
            skLineSegment(sketch, "E5588", {"start": v(91.6, 29.07) * mm, "end": v(91.3, 28.71) * mm});
            skLineSegment(sketch, "E5589", {"start": v(91.3, 28.71) * mm, "end": v(90.96, 28.35) * mm});
            skLineSegment(sketch, "E5590", {"start": v(90.96, 28.35) * mm, "end": v(90.6, 27.98) * mm});
            skLineSegment(sketch, "E5591", {"start": v(90.6, 27.98) * mm, "end": v(90.23, 27.61) * mm});
            skLineSegment(sketch, "E5592", {"start": v(90.23, 27.61) * mm, "end": v(89.84, 27.25) * mm});
            skLineSegment(sketch, "E5593", {"start": v(89.84, 27.25) * mm, "end": v(89.43, 26.89) * mm});
            skLineSegment(sketch, "E5594", {"start": v(89.43, 26.89) * mm, "end": v(88.97, 26.5) * mm});
            skLineSegment(sketch, "E5595", {"start": v(88.97, 26.5) * mm, "end": v(88.5, 26.14) * mm});
            skLineSegment(sketch, "E5596", {"start": v(88.5, 26.14) * mm, "end": v(88.02, 25.78) * mm});
            skLineSegment(sketch, "E5597", {"start": v(88.02, 25.78) * mm, "end": v(87.55, 25.44) * mm});
            skLineSegment(sketch, "E5598", {"start": v(87.55, 25.44) * mm, "end": v(87.07, 25.12) * mm});
            skLineSegment(sketch, "E5599", {"start": v(87.07, 25.12) * mm, "end": v(86.61, 24.81) * mm});
            skLineSegment(sketch, "E5600", {"start": v(86.61, 24.81) * mm, "end": v(85.74, 24.26) * mm});
            skLineSegment(sketch, "E5601", {"start": v(85.74, 24.26) * mm, "end": v(84.97, 23.8) * mm});
            skLineSegment(sketch, "E5602", {"start": v(84.97, 23.8) * mm, "end": v(84.35, 23.44) * mm});
            skLineSegment(sketch, "E5603", {"start": v(84.35, 23.44) * mm, "end": v(83.73, 23.09) * mm});
            skLineSegment(sketch, "E5604", {"start": v(83.73, 23.09) * mm, "end": v(84.12, 22.34) * mm});
            skLineSegment(sketch, "E5605", {"start": v(84.12, 22.34) * mm, "end": v(84.48, 21.6) * mm});
            skLineSegment(sketch, "E5606", {"start": v(84.48, 21.6) * mm, "end": v(84.8, 20.94) * mm});
            skLineSegment(sketch, "E5607", {"start": v(84.8, 20.94) * mm, "end": v(84.96, 20.6) * mm});
            skLineSegment(sketch, "E5608", {"start": v(84.96, 20.6) * mm, "end": v(85.1, 20.27) * mm});
            skLineSegment(sketch, "E5609", {"start": v(85.1, 20.27) * mm, "end": v(85.25, 19.87) * mm});
            skLineSegment(sketch, "E5610", {"start": v(85.25, 19.87) * mm, "end": v(85.4, 19.43) * mm});
            skLineSegment(sketch, "E5611", {"start": v(85.4, 19.43) * mm, "end": v(85.68, 18.59) * mm});
            skLineSegment(sketch, "E5612", {"start": v(85.68, 18.59) * mm, "end": v(85.78, 18.28) * mm});
            skLineSegment(sketch, "E5613", {"start": v(85.78, 18.28) * mm, "end": v(85.85, 18) * mm});
            skLineSegment(sketch, "E5614", {"start": v(85.85, 18) * mm, "end": v(85.92, 17.67) * mm});
            skLineSegment(sketch, "E5615", {"start": v(85.92, 17.67) * mm, "end": v(86, 17.17) * mm});
            skLineSegment(sketch, "E5616", {"start": v(86.52, 11.63) * mm, "end": v(88.32, 12.4) * mm});
            skLineSegment(sketch, "E5617", {"start": v(88.32, 12.4) * mm, "end": v(88.41, 12.43) * mm});
            skLineSegment(sketch, "E5618", {"start": v(88.41, 12.43) * mm, "end": v(88.52, 12.48) * mm});
            skLineSegment(sketch, "E5619", {"start": v(88.52, 12.48) * mm, "end": v(88.78, 12.6) * mm});
            skLineSegment(sketch, "E5620", {"start": v(88.78, 12.6) * mm, "end": v(89.07, 12.77) * mm});
            skLineSegment(sketch, "E5621", {"start": v(89.07, 12.77) * mm, "end": v(89.37, 12.96) * mm});
            skLineSegment(sketch, "E5622", {"start": v(89.37, 12.96) * mm, "end": v(89.66, 13.17) * mm});
            skLineSegment(sketch, "E5623", {"start": v(89.66, 13.17) * mm, "end": v(89.93, 13.4) * mm});
            skLineSegment(sketch, "E5624", {"start": v(89.93, 13.4) * mm, "end": v(90.16, 13.61) * mm});
            skLineSegment(sketch, "E5625", {"start": v(90.16, 13.61) * mm, "end": v(90.25, 13.72) * mm});
            skLineSegment(sketch, "E5626", {"start": v(90.25, 13.72) * mm, "end": v(90.33, 13.82) * mm});
            skLineSegment(sketch, "E5627", {"start": v(90.33, 13.82) * mm, "end": v(90.38, 13.9) * mm});
            skLineSegment(sketch, "E5628", {"start": v(90.38, 13.9) * mm, "end": v(90.44, 14.03) * mm});
            skLineSegment(sketch, "E5629", {"start": v(90.44, 14.03) * mm, "end": v(90.5, 14.17) * mm});
            skLineSegment(sketch, "E5630", {"start": v(90.5, 14.17) * mm, "end": v(90.55, 14.34) * mm});
            skLineSegment(sketch, "E5631", {"start": v(90.55, 14.34) * mm, "end": v(90.6, 14.52) * mm});
            skLineSegment(sketch, "E5632", {"start": v(90.6, 14.52) * mm, "end": v(90.64, 14.71) * mm});
            skLineSegment(sketch, "E5633", {"start": v(90.64, 14.71) * mm, "end": v(90.67, 14.91) * mm});
            skLineSegment(sketch, "E5634", {"start": v(90.67, 14.91) * mm, "end": v(90.68, 15.12) * mm});
            skLineSegment(sketch, "E5635", {"start": v(90.68, 15.12) * mm, "end": v(90.68, 15.37) * mm});
            skLineSegment(sketch, "E5636", {"start": v(90.68, 15.37) * mm, "end": v(90.67, 15.65) * mm});
            skLineSegment(sketch, "E5637", {"start": v(90.67, 15.65) * mm, "end": v(90.64, 15.93) * mm});
            skLineSegment(sketch, "E5638", {"start": v(90.64, 15.93) * mm, "end": v(90.61, 16.06) * mm});
            skLineSegment(sketch, "E5639", {"start": v(90.61, 16.06) * mm, "end": v(90.58, 16.17) * mm});
            skLineSegment(sketch, "E5640", {"start": v(90.58, 16.17) * mm, "end": v(90.51, 16.38) * mm});
            skLineSegment(sketch, "E5641", {"start": v(90.51, 16.38) * mm, "end": v(90.43, 16.6) * mm});
            skLineSegment(sketch, "E5642", {"start": v(90.43, 16.6) * mm, "end": v(90.33, 16.82) * mm});
            skLineSegment(sketch, "E5643", {"start": v(90.33, 16.82) * mm, "end": v(90.27, 16.92) * mm});
            skLineSegment(sketch, "E5644", {"start": v(90.27, 16.92) * mm, "end": v(90.22, 17.01) * mm});
            skLineSegment(sketch, "E5645", {"start": v(90.22, 17.01) * mm, "end": v(90.05, 17.23) * mm});
            skLineSegment(sketch, "E5646", {"start": v(90.05, 17.23) * mm, "end": v(89.87, 17.42) * mm});
            skLineSegment(sketch, "E5647", {"start": v(89.87, 17.42) * mm, "end": v(89.7, 17.56) * mm});
            skLineSegment(sketch, "E5648", {"start": v(89.7, 17.56) * mm, "end": v(89.61, 17.61) * mm});
            skLineSegment(sketch, "E5649", {"start": v(89.61, 17.61) * mm, "end": v(89.54, 17.65) * mm});
            skLineSegment(sketch, "E5650", {"start": v(89.54, 17.65) * mm, "end": v(89.42, 17.7) * mm});
            skLineSegment(sketch, "E5651", {"start": v(89.42, 17.7) * mm, "end": v(89.29, 17.76) * mm});
            skLineSegment(sketch, "E5652", {"start": v(89.29, 17.76) * mm, "end": v(89.22, 17.78) * mm});
            skLineSegment(sketch, "E5653", {"start": v(89.22, 17.78) * mm, "end": v(89.15, 17.8) * mm});
            skLineSegment(sketch, "E5654", {"start": v(89.15, 17.8) * mm, "end": v(89.06, 17.8) * mm});
            skLineSegment(sketch, "E5655", {"start": v(89.06, 17.8) * mm, "end": v(88.98, 17.79) * mm});
            skLineSegment(sketch, "E5656", {"start": v(88.98, 17.79) * mm, "end": v(88.89, 17.76) * mm});
            skLineSegment(sketch, "E5657", {"start": v(88.89, 17.76) * mm, "end": v(88.79, 17.72) * mm});
            skLineSegment(sketch, "E5658", {"start": v(88.79, 17.72) * mm, "end": v(88.57, 17.61) * mm});
            skLineSegment(sketch, "E5659", {"start": v(88.57, 17.61) * mm, "end": v(87.88, 17.22) * mm});
            skLineSegment(sketch, "E5660", {"start": v(87.88, 17.22) * mm, "end": v(87.43, 16.99) * mm});
            skLineSegment(sketch, "E5661", {"start": v(87.43, 16.99) * mm, "end": v(87.2, 16.86) * mm});
            skLineSegment(sketch, "E5662", {"start": v(87.2, 16.86) * mm, "end": v(86.92, 16.7) * mm});
            skLineSegment(sketch, "E5663", {"start": v(86.92, 16.7) * mm, "end": v(86.7, 16.6) * mm});
            skLineSegment(sketch, "E5664", {"start": v(86.7, 16.6) * mm, "end": v(86.47, 16.52) * mm});
            skLineSegment(sketch, "E5665", {"start": v(86.47, 16.52) * mm, "end": v(86.09, 16.38) * mm});
            skLineSegment(sketch, "E5666", {"start": v(86.09, 16.38) * mm, "end": v(86.17, 15.8) * mm});
            skLineSegment(sketch, "E5667", {"start": v(86.17, 15.8) * mm, "end": v(86.2, 15.5) * mm});
            skLineSegment(sketch, "E5668", {"start": v(86.2, 15.5) * mm, "end": v(86.23, 15.23) * mm});
            skLineSegment(sketch, "E5669", {"start": v(86.23, 15.23) * mm, "end": v(86.25, 14.98) * mm});
            skLineSegment(sketch, "E5670", {"start": v(86.25, 14.98) * mm, "end": v(86.27, 14.73) * mm});
            skLineSegment(sketch, "E5671", {"start": v(86.27, 14.73) * mm, "end": v(86.29, 14.52) * mm});
            skLineSegment(sketch, "E5672", {"start": v(86.29, 14.52) * mm, "end": v(86.32, 14.31) * mm});
            skLineSegment(sketch, "E5673", {"start": v(86.32, 14.31) * mm, "end": v(86.38, 13.92) * mm});
            skLineSegment(sketch, "E5674", {"start": v(86.38, 13.92) * mm, "end": v(86.4, 13.68) * mm});
            skLineSegment(sketch, "E5675", {"start": v(86.4, 13.68) * mm, "end": v(86.42, 13.42) * mm});
            skLineSegment(sketch, "E5676", {"start": v(86.42, 13.42) * mm, "end": v(86.44, 12.91) * mm});
            skLineSegment(sketch, "E5677", {"start": v(86.44, 12.91) * mm, "end": v(86.5, 12.27) * mm});
            skLineSegment(sketch, "E5678", {"start": v(86.5, 12.27) * mm, "end": v(86.52, 11.93) * mm});
            skLineSegment(sketch, "E5679", {"start": v(86.52, 11.93) * mm, "end": v(86.52, 11.63) * mm});
            skLineSegment(sketch, "E5680", {"start": v(-15.4, 63.71) * mm, "end": v(-15.43, 63.6) * mm});
            skLineSegment(sketch, "E5681", {"start": v(-15.43, 63.6) * mm, "end": v(-15.48, 63.44) * mm});
            skLineSegment(sketch, "E5682", {"start": v(-15.48, 63.44) * mm, "end": v(-15.57, 63.24) * mm});
            skLineSegment(sketch, "E5683", {"start": v(-15.57, 63.24) * mm, "end": v(-15.68, 63) * mm});
            skLineSegment(sketch, "E5684", {"start": v(-15.68, 63) * mm, "end": v(-15.81, 62.74) * mm});
            skLineSegment(sketch, "E5685", {"start": v(-15.81, 62.74) * mm, "end": v(-15.96, 62.46) * mm});
            skLineSegment(sketch, "E5686", {"start": v(-15.96, 62.46) * mm, "end": v(-16.13, 62.16) * mm});
            skLineSegment(sketch, "E5687", {"start": v(-16.13, 62.16) * mm, "end": v(-16.32, 61.84) * mm});
            skLineSegment(sketch, "E5688", {"start": v(-16.32, 61.84) * mm, "end": v(-16.52, 61.53) * mm});
            skLineSegment(sketch, "E5689", {"start": v(-16.52, 61.53) * mm, "end": v(-16.73, 61.21) * mm});
            skLineSegment(sketch, "E5690", {"start": v(-16.73, 61.21) * mm, "end": v(-16.94, 60.9) * mm});
            skLineSegment(sketch, "E5691", {"start": v(-16.94, 60.9) * mm, "end": v(-17.16, 60.61) * mm});
            skLineSegment(sketch, "E5692", {"start": v(-17.16, 60.61) * mm, "end": v(-17.38, 60.34) * mm});
            skLineSegment(sketch, "E5693", {"start": v(-17.38, 60.34) * mm, "end": v(-17.6, 60.09) * mm});
            skLineSegment(sketch, "E5694", {"start": v(-17.6, 60.09) * mm, "end": v(-17.82, 59.87) * mm});
            skLineSegment(sketch, "E5695", {"start": v(-17.82, 59.87) * mm, "end": v(-18.03, 59.7) * mm});
            skLineSegment(sketch, "E5696", {"start": v(-18.03, 59.7) * mm, "end": v(-18.4, 59.44) * mm});
            skLineSegment(sketch, "E5697", {"start": v(-18.4, 59.44) * mm, "end": v(-18.79, 59.2) * mm});
            skLineSegment(sketch, "E5698", {"start": v(-18.79, 59.2) * mm, "end": v(-19.2, 58.97) * mm});
            skLineSegment(sketch, "E5699", {"start": v(-19.2, 58.97) * mm, "end": v(-19.65, 58.74) * mm});
            skLineSegment(sketch, "E5700", {"start": v(-19.65, 58.74) * mm, "end": v(-20.1, 58.54) * mm});
            skLineSegment(sketch, "E5701", {"start": v(-20.1, 58.54) * mm, "end": v(-20.54, 58.34) * mm});
            skLineSegment(sketch, "E5702", {"start": v(-20.54, 58.34) * mm, "end": v(-20.97, 58.17) * mm});
            skLineSegment(sketch, "E5703", {"start": v(-20.97, 58.17) * mm, "end": v(-21.38, 58.01) * mm});
            skLineSegment(sketch, "E5704", {"start": v(-21.38, 58.01) * mm, "end": v(-21.86, 57.85) * mm});
            skLineSegment(sketch, "E5705", {"start": v(-21.86, 57.85) * mm, "end": v(-22.37, 57.7) * mm});
            skLineSegment(sketch, "E5706", {"start": v(-22.37, 57.7) * mm, "end": v(-22.91, 57.54) * mm});
            skLineSegment(sketch, "E5707", {"start": v(-22.91, 57.54) * mm, "end": v(-23.46, 57.4) * mm});
            skLineSegment(sketch, "E5708", {"start": v(-23.46, 57.4) * mm, "end": v(-24.02, 57.28) * mm});
            skLineSegment(sketch, "E5709", {"start": v(-24.02, 57.28) * mm, "end": v(-24.57, 57.18) * mm});
            skLineSegment(sketch, "E5710", {"start": v(-24.57, 57.18) * mm, "end": v(-25.1, 57.09) * mm});
            skLineSegment(sketch, "E5711", {"start": v(-25.1, 57.09) * mm, "end": v(-25.6, 57.02) * mm});
            skLineSegment(sketch, "E5712", {"start": v(-25.6, 57.02) * mm, "end": v(-26.56, 56.91) * mm});
            skLineSegment(sketch, "E5713", {"start": v(-26.56, 56.91) * mm, "end": v(-27.07, 56.87) * mm});
            skLineSegment(sketch, "E5714", {"start": v(-27.07, 56.87) * mm, "end": v(-27.6, 56.84) * mm});
            skLineSegment(sketch, "E5715", {"start": v(-27.6, 56.84) * mm, "end": v(-28.12, 56.84) * mm});
            skLineSegment(sketch, "E5716", {"start": v(-28.12, 56.84) * mm, "end": v(-28.38, 56.84) * mm});
            skLineSegment(sketch, "E5717", {"start": v(-28.38, 56.84) * mm, "end": v(-28.63, 56.86) * mm});
            skLineSegment(sketch, "E5718", {"start": v(-28.63, 56.86) * mm, "end": v(-28.88, 56.88) * mm});
            skLineSegment(sketch, "E5719", {"start": v(-28.88, 56.88) * mm, "end": v(-29.11, 56.92) * mm});
            skLineSegment(sketch, "E5720", {"start": v(-29.11, 56.92) * mm, "end": v(-29.34, 56.96) * mm});
            skLineSegment(sketch, "E5721", {"start": v(-29.34, 56.96) * mm, "end": v(-29.56, 57.02) * mm});
            skLineSegment(sketch, "E5722", {"start": v(-29.56, 57.02) * mm, "end": v(-29.8, 57.1) * mm});
            skLineSegment(sketch, "E5723", {"start": v(-29.8, 57.1) * mm, "end": v(-29.92, 57.15) * mm});
            skLineSegment(sketch, "E5724", {"start": v(-29.92, 57.15) * mm, "end": v(-30.04, 57.2) * mm});
            skLineSegment(sketch, "E5725", {"start": v(-30.04, 57.2) * mm, "end": v(-30.15, 57.28) * mm});
            skLineSegment(sketch, "E5726", {"start": v(-30.15, 57.28) * mm, "end": v(-30.25, 57.35) * mm});
            skLineSegment(sketch, "E5727", {"start": v(-30.25, 57.35) * mm, "end": v(-30.33, 57.44) * mm});
            skLineSegment(sketch, "E5728", {"start": v(-30.33, 57.44) * mm, "end": v(-30.38, 57.54) * mm});
            skLineSegment(sketch, "E5729", {"start": v(-30.38, 57.54) * mm, "end": v(-30.41, 57.66) * mm});
            skLineSegment(sketch, "E5730", {"start": v(-30.41, 57.66) * mm, "end": v(-30.43, 57.78) * mm});
            skLineSegment(sketch, "E5731", {"start": v(-30.43, 57.78) * mm, "end": v(-30.44, 57.91) * mm});
            skLineSegment(sketch, "E5732", {"start": v(-30.44, 57.91) * mm, "end": v(-30.43, 58.05) * mm});
            skLineSegment(sketch, "E5733", {"start": v(-30.43, 58.05) * mm, "end": v(-30.4, 58.19) * mm});
            skLineSegment(sketch, "E5734", {"start": v(-30.4, 58.19) * mm, "end": v(-30.37, 58.33) * mm});
            skLineSegment(sketch, "E5735", {"start": v(-30.37, 58.33) * mm, "end": v(-30.28, 58.61) * mm});
            skLineSegment(sketch, "E5736", {"start": v(-30.28, 58.61) * mm, "end": v(-30.16, 58.9) * mm});
            skLineSegment(sketch, "E5737", {"start": v(-30.16, 58.9) * mm, "end": v(-30.03, 59.17) * mm});
            skLineSegment(sketch, "E5738", {"start": v(-30.03, 59.17) * mm, "end": v(-29.77, 59.67) * mm});
            skLineSegment(sketch, "E5739", {"start": v(-29.77, 59.67) * mm, "end": v(-29.59, 60) * mm});
            skLineSegment(sketch, "E5740", {"start": v(-29.59, 60) * mm, "end": v(-29.38, 60.34) * mm});
            skLineSegment(sketch, "E5741", {"start": v(-29.38, 60.34) * mm, "end": v(-29.14, 60.7) * mm});
            skLineSegment(sketch, "E5742", {"start": v(-29.14, 60.7) * mm, "end": v(-28.89, 61.04) * mm});
            skLineSegment(sketch, "E5743", {"start": v(-28.89, 61.04) * mm, "end": v(-28.62, 61.37) * mm});
            skLineSegment(sketch, "E5744", {"start": v(-28.62, 61.37) * mm, "end": v(-28.34, 61.68) * mm});
            skLineSegment(sketch, "E5745", {"start": v(-28.34, 61.68) * mm, "end": v(-28.05, 61.96) * mm});
            skLineSegment(sketch, "E5746", {"start": v(-28.05, 61.96) * mm, "end": v(-27.9, 62.09) * mm});
            skLineSegment(sketch, "E5747", {"start": v(-27.9, 62.09) * mm, "end": v(-27.76, 62.2) * mm});
            skLineSegment(sketch, "E5748", {"start": v(-27.76, 62.2) * mm, "end": v(-27.6, 62.32) * mm});
            skLineSegment(sketch, "E5749", {"start": v(-27.6, 62.32) * mm, "end": v(-27.42, 62.44) * mm});
            skLineSegment(sketch, "E5750", {"start": v(-27.42, 62.44) * mm, "end": v(-27.24, 62.55) * mm});
            skLineSegment(sketch, "E5751", {"start": v(-27.24, 62.55) * mm, "end": v(-27.04, 62.65) * mm});
            skLineSegment(sketch, "E5752", {"start": v(-27.04, 62.65) * mm, "end": v(-26.63, 62.85) * mm});
            skLineSegment(sketch, "E5753", {"start": v(-26.63, 62.85) * mm, "end": v(-26.2, 63.04) * mm});
            skLineSegment(sketch, "E5754", {"start": v(-26.2, 63.04) * mm, "end": v(-25.76, 63.2) * mm});
            skLineSegment(sketch, "E5755", {"start": v(-25.76, 63.2) * mm, "end": v(-25.33, 63.35) * mm});
            skLineSegment(sketch, "E5756", {"start": v(-25.33, 63.35) * mm, "end": v(-24.9, 63.49) * mm});
            skLineSegment(sketch, "E5757", {"start": v(-24.9, 63.49) * mm, "end": v(-24.5, 63.6) * mm});
            skLineSegment(sketch, "E5758", {"start": v(-24.5, 63.6) * mm, "end": v(-23.96, 63.74) * mm});
            skLineSegment(sketch, "E5759", {"start": v(-23.96, 63.74) * mm, "end": v(-23.38, 63.87) * mm});
            skLineSegment(sketch, "E5760", {"start": v(-23.38, 63.87) * mm, "end": v(-22.77, 63.98) * mm});
            skLineSegment(sketch, "E5761", {"start": v(-22.77, 63.98) * mm, "end": v(-22.14, 64.07) * mm});
            skLineSegment(sketch, "E5762", {"start": v(-22.14, 64.07) * mm, "end": v(-21.52, 64.15) * mm});
            skLineSegment(sketch, "E5763", {"start": v(-21.52, 64.15) * mm, "end": v(-20.9, 64.21) * mm});
            skLineSegment(sketch, "E5764", {"start": v(-20.9, 64.21) * mm, "end": v(-20.3, 64.26) * mm});
            skLineSegment(sketch, "E5765", {"start": v(-20.3, 64.26) * mm, "end": v(-19.74, 64.28) * mm});
            skLineSegment(sketch, "E5766", {"start": v(-19.74, 64.28) * mm, "end": v(-18.67, 64.31) * mm});
            skLineSegment(sketch, "E5767", {"start": v(-18.67, 64.31) * mm, "end": v(-18.09, 64.32) * mm});
            skLineSegment(sketch, "E5768", {"start": v(-18.09, 64.32) * mm, "end": v(-17.5, 64.32) * mm});
            skLineSegment(sketch, "E5769", {"start": v(-17.5, 64.32) * mm, "end": v(-17.2, 64.3) * mm});
            skLineSegment(sketch, "E5770", {"start": v(-17.2, 64.3) * mm, "end": v(-16.92, 64.28) * mm});
            skLineSegment(sketch, "E5771", {"start": v(-16.92, 64.28) * mm, "end": v(-16.64, 64.24) * mm});
            skLineSegment(sketch, "E5772", {"start": v(-16.64, 64.24) * mm, "end": v(-16.36, 64.2) * mm});
            skLineSegment(sketch, "E5773", {"start": v(-16.36, 64.2) * mm, "end": v(-16.1, 64.13) * mm});
            skLineSegment(sketch, "E5774", {"start": v(-16.1, 64.13) * mm, "end": v(-15.84, 64.06) * mm});
            skLineSegment(sketch, "E5775", {"start": v(-15.84, 64.06) * mm, "end": v(-15.6, 63.97) * mm});
            skLineSegment(sketch, "E5776", {"start": v(-15.6, 63.97) * mm, "end": v(-15.37, 63.86) * mm});
            skLineSegment(sketch, "E5777", {"start": v(-15.37, 63.86) * mm, "end": v(-15.4, 63.71) * mm});
            skLineSegment(sketch, "E5778", {"start": v(-6.04, -20) * mm, "end": v(-5.82, -20.23) * mm});
            skLineSegment(sketch, "E5779", {"start": v(-5.82, -20.23) * mm, "end": v(-5.62, -20.5) * mm});
            skLineSegment(sketch, "E5780", {"start": v(-5.62, -20.5) * mm, "end": v(-5.42, -20.78) * mm});
            skLineSegment(sketch, "E5781", {"start": v(-5.42, -20.78) * mm, "end": v(-5.24, -21.07) * mm});
            skLineSegment(sketch, "E5782", {"start": v(-5.24, -21.07) * mm, "end": v(-5.07, -21.37) * mm});
            skLineSegment(sketch, "E5783", {"start": v(-5.07, -21.37) * mm, "end": v(-4.92, -21.66) * mm});
            skLineSegment(sketch, "E5784", {"start": v(-4.92, -21.66) * mm, "end": v(-4.8, -21.95) * mm});
            skLineSegment(sketch, "E5785", {"start": v(-4.8, -21.95) * mm, "end": v(-4.68, -22.2) * mm});
            skLineSegment(sketch, "E5786", {"start": v(-4.68, -22.2) * mm, "end": v(-4.36, -23.03) * mm});
            skLineSegment(sketch, "E5787", {"start": v(-4.36, -23.03) * mm, "end": v(-4.1, -23.68) * mm});
            skLineSegment(sketch, "E5788", {"start": v(-4.1, -23.68) * mm, "end": v(-4, -23.92) * mm});
            skLineSegment(sketch, "E5789", {"start": v(-4, -23.92) * mm, "end": v(-3.9, -24.1) * mm});
            skLineSegment(sketch, "E5790", {"start": v(-3.9, -24.1) * mm, "end": v(-3.84, -24.22) * mm});
            skLineSegment(sketch, "E5791", {"start": v(-3.84, -24.22) * mm, "end": v(-3.81, -24.25) * mm});
            skLineSegment(sketch, "E5792", {"start": v(-3.81, -24.25) * mm, "end": v(-3.8, -24.26) * mm});
            skLineSegment(sketch, "E5793", {"start": v(-3.8, -24.26) * mm, "end": v(-3.77, -24.26) * mm});
            skLineSegment(sketch, "E5794", {"start": v(-3.77, -24.26) * mm, "end": v(-3.73, -24.23) * mm});
            skLineSegment(sketch, "E5795", {"start": v(-3.73, -24.23) * mm, "end": v(-3.64, -24.14) * mm});
            skLineSegment(sketch, "E5796", {"start": v(-3.64, -24.14) * mm, "end": v(-3.5, -23.99) * mm});
            skLineSegment(sketch, "E5797", {"start": v(-3.5, -23.99) * mm, "end": v(-3.35, -23.8) * mm});
            skLineSegment(sketch, "E5798", {"start": v(-3.35, -23.8) * mm, "end": v(-2.97, -23.28) * mm});
            skLineSegment(sketch, "E5799", {"start": v(-2.97, -23.28) * mm, "end": v(-2.52, -22.65) * mm});
            skLineSegment(sketch, "E5800", {"start": v(-2.52, -22.65) * mm, "end": v(-2.24, -22.27) * mm});
            skLineSegment(sketch, "E5801", {"start": v(-2.24, -22.27) * mm, "end": v(-1.92, -21.87) * mm});
            skLineSegment(sketch, "E5802", {"start": v(-1.92, -21.87) * mm, "end": v(-1.77, -21.66) * mm});
            skLineSegment(sketch, "E5803", {"start": v(-1.77, -21.66) * mm, "end": v(-1.63, -21.45) * mm});
            skLineSegment(sketch, "E5804", {"start": v(-1.63, -21.45) * mm, "end": v(-1.51, -21.25) * mm});
            skLineSegment(sketch, "E5805", {"start": v(-1.51, -21.25) * mm, "end": v(-1.42, -21.04) * mm});
            skLineSegment(sketch, "E5806", {"start": v(-1.42, -21.04) * mm, "end": v(-1.35, -20.82) * mm});
            skLineSegment(sketch, "E5807", {"start": v(-1.35, -20.82) * mm, "end": v(-1.29, -20.6) * mm});
            skLineSegment(sketch, "E5808", {"start": v(-1.29, -20.6) * mm, "end": v(-1.23, -20.36) * mm});
            skLineSegment(sketch, "E5809", {"start": v(-1.23, -20.36) * mm, "end": v(-1.18, -20.12) * mm});
            skLineSegment(sketch, "E5810", {"start": v(-1.18, -20.12) * mm, "end": v(-1.1, -19.61) * mm});
            skLineSegment(sketch, "E5811", {"start": v(-1.1, -19.61) * mm, "end": v(-1.04, -19.1) * mm});
            skLineSegment(sketch, "E5812", {"start": v(-1.04, -19.1) * mm, "end": v(-1.01, -18.57) * mm});
            skLineSegment(sketch, "E5813", {"start": v(-1.01, -18.57) * mm, "end": v(-1, -18.05) * mm});
            skLineSegment(sketch, "E5814", {"start": v(-1, -18.05) * mm, "end": v(-1.03, -17.56) * mm});
            skLineSegment(sketch, "E5815", {"start": v(-1.03, -17.56) * mm, "end": v(-1.07, -17.1) * mm});
            skLineSegment(sketch, "E5816", {"start": v(-1.07, -17.1) * mm, "end": v(-1.1, -16.84) * mm});
            skLineSegment(sketch, "E5817", {"start": v(-1.1, -16.84) * mm, "end": v(-1.15, -16.56) * mm});
            skLineSegment(sketch, "E5818", {"start": v(-1.15, -16.56) * mm, "end": v(-1.2, -16.29) * mm});
            skLineSegment(sketch, "E5819", {"start": v(-1.2, -16.29) * mm, "end": v(-1.28, -16) * mm});
            skLineSegment(sketch, "E5820", {"start": v(-1.28, -16) * mm, "end": v(-1.44, -15.43) * mm});
            skLineSegment(sketch, "E5821", {"start": v(-1.44, -15.43) * mm, "end": v(-1.63, -14.85) * mm});
            skLineSegment(sketch, "E5822", {"start": v(-1.63, -14.85) * mm, "end": v(-1.84, -14.28) * mm});
            skLineSegment(sketch, "E5823", {"start": v(-1.84, -14.28) * mm, "end": v(-2.06, -13.73) * mm});
            skLineSegment(sketch, "E5824", {"start": v(-2.06, -13.73) * mm, "end": v(-2.3, -13.2) * mm});
            skLineSegment(sketch, "E5825", {"start": v(-2.3, -13.2) * mm, "end": v(-2.53, -12.7) * mm});
            skLineSegment(sketch, "E5826", {"start": v(-2.53, -12.7) * mm, "end": v(-2.66, -12.46) * mm});
            skLineSegment(sketch, "E5827", {"start": v(-2.66, -12.46) * mm, "end": v(-2.81, -12.21) * mm});
            skLineSegment(sketch, "E5828", {"start": v(-2.81, -12.21) * mm, "end": v(-3.16, -11.7) * mm});
            skLineSegment(sketch, "E5829", {"start": v(-3.16, -11.7) * mm, "end": v(-3.52, -11.2) * mm});
            skLineSegment(sketch, "E5830", {"start": v(-3.52, -11.2) * mm, "end": v(-3.85, -10.73) * mm});
            skLineSegment(sketch, "E5831", {"start": v(-3.85, -10.73) * mm, "end": v(-4.13, -10.33) * mm});
            skLineSegment(sketch, "E5832", {"start": v(-4.13, -10.33) * mm, "end": v(-4.41, -9.93) * mm});
            skLineSegment(sketch, "E5833", {"start": v(-4.41, -9.93) * mm, "end": v(-4.7, -9.55) * mm});
            skLineSegment(sketch, "E5834", {"start": v(-4.7, -9.55) * mm, "end": v(-4.99, -9.2) * mm});
            skLineSegment(sketch, "E5835", {"start": v(-4.99, -9.2) * mm, "end": v(-5.25, -8.88) * mm});
            skLineSegment(sketch, "E5836", {"start": v(-5.25, -8.88) * mm, "end": v(-5.5, -8.61) * mm});
            skLineSegment(sketch, "E5837", {"start": v(-5.5, -8.61) * mm, "end": v(-5.7, -8.4) * mm});
            skLineSegment(sketch, "E5838", {"start": v(-5.7, -8.4) * mm, "end": v(-5.87, -8.26) * mm});
            skLineSegment(sketch, "E5839", {"start": v(-5.87, -8.26) * mm, "end": v(-6.04, -8.13) * mm});
            skLineSegment(sketch, "E5840", {"start": v(-6.04, -8.13) * mm, "end": v(-6.21, -8) * mm});
            skLineSegment(sketch, "E5841", {"start": v(-6.21, -8) * mm, "end": v(-6.4, -7.86) * mm});
            skLineSegment(sketch, "E5842", {"start": v(-6.4, -7.86) * mm, "end": v(-6.48, -7.8) * mm});
            skLineSegment(sketch, "E5843", {"start": v(-6.48, -7.8) * mm, "end": v(-6.58, -7.77) * mm});
            skLineSegment(sketch, "E5844", {"start": v(-6.58, -7.77) * mm, "end": v(-6.74, -7.72) * mm});
            skLineSegment(sketch, "E5845", {"start": v(-6.74, -7.72) * mm, "end": v(-6.9, -7.69) * mm});
            skLineSegment(sketch, "E5846", {"start": v(-6.9, -7.69) * mm, "end": v(-7.08, -7.66) * mm});
            skLineSegment(sketch, "E5847", {"start": v(-7.08, -7.66) * mm, "end": v(-7.25, -7.64) * mm});
            skLineSegment(sketch, "E5848", {"start": v(-7.25, -7.64) * mm, "end": v(-7.63, -7.61) * mm});
            skLineSegment(sketch, "E5849", {"start": v(-7.63, -7.61) * mm, "end": v(-8, -7.61) * mm});
            skLineSegment(sketch, "E5850", {"start": v(-8, -7.61) * mm, "end": v(-8.39, -7.63) * mm});
            skLineSegment(sketch, "E5851", {"start": v(-8.39, -7.63) * mm, "end": v(-8.76, -7.66) * mm});
            skLineSegment(sketch, "E5852", {"start": v(-8.76, -7.66) * mm, "end": v(-9.12, -7.71) * mm});
            skLineSegment(sketch, "E5853", {"start": v(-9.12, -7.71) * mm, "end": v(-9.45, -7.77) * mm});
            skLineSegment(sketch, "E5854", {"start": v(-9.45, -7.77) * mm, "end": v(-9.7, -7.83) * mm});
            skLineSegment(sketch, "E5855", {"start": v(-9.7, -7.83) * mm, "end": v(-9.98, -7.92) * mm});
            skLineSegment(sketch, "E5856", {"start": v(-9.98, -7.92) * mm, "end": v(-10.25, -8.03) * mm});
            skLineSegment(sketch, "E5857", {"start": v(-10.25, -8.03) * mm, "end": v(-10.52, -8.15) * mm});
            skLineSegment(sketch, "E5858", {"start": v(-10.52, -8.15) * mm, "end": v(-11.06, -8.4) * mm});
            skLineSegment(sketch, "E5859", {"start": v(-11.06, -8.4) * mm, "end": v(-11.32, -8.51) * mm});
            skLineSegment(sketch, "E5860", {"start": v(-11.32, -8.51) * mm, "end": v(-11.57, -8.62) * mm});
            skLineSegment(sketch, "E5861", {"start": v(-11.57, -8.62) * mm, "end": v(-12.1, -8.83) * mm});
            skLineSegment(sketch, "E5862", {"start": v(-12.1, -8.83) * mm, "end": v(-12.61, -9.05) * mm});
            skLineSegment(sketch, "E5863", {"start": v(-12.61, -9.05) * mm, "end": v(-13.1, -9.27) * mm});
            skLineSegment(sketch, "E5864", {"start": v(-13.1, -9.27) * mm, "end": v(-13.57, -9.48) * mm});
            skLineSegment(sketch, "E5865", {"start": v(-13.57, -9.48) * mm, "end": v(-14.02, -9.7) * mm});
            skLineSegment(sketch, "E5866", {"start": v(-14.02, -9.7) * mm, "end": v(-14.45, -9.92) * mm});
            skLineSegment(sketch, "E5867", {"start": v(-14.45, -9.92) * mm, "end": v(-14.85, -10.14) * mm});
            skLineSegment(sketch, "E5868", {"start": v(-14.85, -10.14) * mm, "end": v(-15.24, -10.35) * mm});
            skLineSegment(sketch, "E5869", {"start": v(-15.24, -10.35) * mm, "end": v(-15.6, -10.57) * mm});
            skLineSegment(sketch, "E5870", {"start": v(-15.6, -10.57) * mm, "end": v(-15.95, -10.8) * mm});
            skLineSegment(sketch, "E5871", {"start": v(-15.95, -10.8) * mm, "end": v(-16.28, -11.02) * mm});
            skLineSegment(sketch, "E5872", {"start": v(-16.28, -11.02) * mm, "end": v(-16.6, -11.24) * mm});
            skLineSegment(sketch, "E5873", {"start": v(-16.6, -11.24) * mm, "end": v(-16.89, -11.46) * mm});
            skLineSegment(sketch, "E5874", {"start": v(-16.89, -11.46) * mm, "end": v(-17.16, -11.7) * mm});
            skLineSegment(sketch, "E5875", {"start": v(-17.16, -11.7) * mm, "end": v(-17.42, -11.92) * mm});
            skLineSegment(sketch, "E5876", {"start": v(-17.42, -11.92) * mm, "end": v(-17.67, -12.16) * mm});
            skLineSegment(sketch, "E5877", {"start": v(-17.67, -12.16) * mm, "end": v(-17.93, -12.4) * mm});
            skLineSegment(sketch, "E5878", {"start": v(-17.93, -12.4) * mm, "end": v(-18.22, -12.67) * mm});
            skLineSegment(sketch, "E5879", {"start": v(-18.22, -12.67) * mm, "end": v(-18.5, -12.94) * mm});
            skLineSegment(sketch, "E5880", {"start": v(-18.5, -12.94) * mm, "end": v(-18.62, -13.08) * mm});
            skLineSegment(sketch, "E5881", {"start": v(-18.62, -13.08) * mm, "end": v(-18.72, -13.21) * mm});
            skLineSegment(sketch, "E5882", {"start": v(-18.72, -13.21) * mm, "end": v(-18.84, -13.4) * mm});
            skLineSegment(sketch, "E5883", {"start": v(-18.84, -13.4) * mm, "end": v(-18.95, -13.6) * mm});
            skLineSegment(sketch, "E5884", {"start": v(-18.95, -13.6) * mm, "end": v(-19.16, -14.06) * mm});
            skLineSegment(sketch, "E5885", {"start": v(-19.16, -14.06) * mm, "end": v(-19.34, -14.51) * mm});
            skLineSegment(sketch, "E5886", {"start": v(-19.34, -14.51) * mm, "end": v(-19.53, -14.93) * mm});
            skLineSegment(sketch, "E5887", {"start": v(-19.53, -14.93) * mm, "end": v(-19.7, -15.3) * mm});
            skLineSegment(sketch, "E5888", {"start": v(-19.7, -15.3) * mm, "end": v(-19.85, -15.7) * mm});
            skLineSegment(sketch, "E5889", {"start": v(-19.85, -15.7) * mm, "end": v(-20, -16.1) * mm});
            skLineSegment(sketch, "E5890", {"start": v(-20, -16.1) * mm, "end": v(-20.15, -16.5) * mm});
            skLineSegment(sketch, "E5891", {"start": v(-20.15, -16.5) * mm, "end": v(-20.27, -16.88) * mm});
            skLineSegment(sketch, "E5892", {"start": v(-20.27, -16.88) * mm, "end": v(-20.38, -17.24) * mm});
            skLineSegment(sketch, "E5893", {"start": v(-20.38, -17.24) * mm, "end": v(-20.46, -17.56) * mm});
            skLineSegment(sketch, "E5894", {"start": v(-20.46, -17.56) * mm, "end": v(-20.52, -17.84) * mm});
            skLineSegment(sketch, "E5895", {"start": v(-20.52, -17.84) * mm, "end": v(-20.71, -19.02) * mm});
            skLineSegment(sketch, "E5896", {"start": v(-20.71, -19.02) * mm, "end": v(-20.3, -18.93) * mm});
            skLineSegment(sketch, "E5897", {"start": v(-20.3, -18.93) * mm, "end": v(-19.91, -18.82) * mm});
            skLineSegment(sketch, "E5898", {"start": v(-19.91, -18.82) * mm, "end": v(-19.45, -18.67) * mm});
            skLineSegment(sketch, "E5899", {"start": v(-19.45, -18.67) * mm, "end": v(-18.97, -18.5) * mm});
            skLineSegment(sketch, "E5900", {"start": v(-18.97, -18.5) * mm, "end": v(-18.48, -18.32) * mm});
            skLineSegment(sketch, "E5901", {"start": v(-18.48, -18.32) * mm, "end": v(-18.25, -18.24) * mm});
            skLineSegment(sketch, "E5902", {"start": v(-18.25, -18.24) * mm, "end": v(-18.02, -18.18) * mm});
            skLineSegment(sketch, "E5903", {"start": v(-18.02, -18.18) * mm, "end": v(-17.76, -18.1) * mm});
            skLineSegment(sketch, "E5904", {"start": v(-17.76, -18.1) * mm, "end": v(-17.47, -18) * mm});
            skLineSegment(sketch, "E5905", {"start": v(-17.47, -18) * mm, "end": v(-16.84, -17.75) * mm});
            skLineSegment(sketch, "E5906", {"start": v(-16.84, -17.75) * mm, "end": v(-16.51, -17.63) * mm});
            skLineSegment(sketch, "E5907", {"start": v(-16.51, -17.63) * mm, "end": v(-16.2, -17.52) * mm});
            skLineSegment(sketch, "E5908", {"start": v(-16.2, -17.52) * mm, "end": v(-15.9, -17.43) * mm});
            skLineSegment(sketch, "E5909", {"start": v(-15.9, -17.43) * mm, "end": v(-15.77, -17.4) * mm});
            skLineSegment(sketch, "E5910", {"start": v(-15.77, -17.4) * mm, "end": v(-15.64, -17.38) * mm});
            skLineSegment(sketch, "E5911", {"start": v(-15.64, -17.38) * mm, "end": v(-15.46, -17.35) * mm});
            skLineSegment(sketch, "E5912", {"start": v(-15.46, -17.35) * mm, "end": v(-15.25, -17.3) * mm});
            skLineSegment(sketch, "E5913", {"start": v(-15.25, -17.3) * mm, "end": v(-14.8, -17.2) * mm});
            skLineSegment(sketch, "E5914", {"start": v(-14.8, -17.2) * mm, "end": v(-14.36, -17.1) * mm});
            skLineSegment(sketch, "E5915", {"start": v(-14.36, -17.1) * mm, "end": v(-14.15, -17.07) * mm});
            skLineSegment(sketch, "E5916", {"start": v(-14.15, -17.07) * mm, "end": v(-13.96, -17.05) * mm});
            skLineSegment(sketch, "E5917", {"start": v(-13.96, -17.05) * mm, "end": v(-13.57, -17.04) * mm});
            skLineSegment(sketch, "E5918", {"start": v(-13.57, -17.04) * mm, "end": v(-13.19, -17.03) * mm});
            skLineSegment(sketch, "E5919", {"start": v(-13.19, -17.03) * mm, "end": v(-12.8, -17.03) * mm});
            skLineSegment(sketch, "E5920", {"start": v(-12.8, -17.03) * mm, "end": v(-12.41, -17.05) * mm});
            skLineSegment(sketch, "E5921", {"start": v(-12.41, -17.05) * mm, "end": v(-12.06, -17.08) * mm});
            skLineSegment(sketch, "E5922", {"start": v(-12.06, -17.08) * mm, "end": v(-11.69, -17.13) * mm});
            skLineSegment(sketch, "E5923", {"start": v(-11.69, -17.13) * mm, "end": v(-11.3, -17.2) * mm});
            skLineSegment(sketch, "E5924", {"start": v(-11.3, -17.2) * mm, "end": v(-10.92, -17.26) * mm});
            skLineSegment(sketch, "E5925", {"start": v(-10.92, -17.26) * mm, "end": v(-10.54, -17.34) * mm});
            skLineSegment(sketch, "E5926", {"start": v(-10.54, -17.34) * mm, "end": v(-10.17, -17.43) * mm});
            skLineSegment(sketch, "E5927", {"start": v(-10.17, -17.43) * mm, "end": v(-9.46, -17.61) * mm});
            skLineSegment(sketch, "E5928", {"start": v(-9.46, -17.61) * mm, "end": v(-9.24, -17.69) * mm});
            skLineSegment(sketch, "E5929", {"start": v(-9.24, -17.69) * mm, "end": v(-9, -17.78) * mm});
            skLineSegment(sketch, "E5930", {"start": v(-9, -17.78) * mm, "end": v(-8.73, -17.88) * mm});
            skLineSegment(sketch, "E5931", {"start": v(-8.73, -17.88) * mm, "end": v(-8.47, -18) * mm});
            skLineSegment(sketch, "E5932", {"start": v(-8.47, -18) * mm, "end": v(-8.21, -18.12) * mm});
            skLineSegment(sketch, "E5933", {"start": v(-8.21, -18.12) * mm, "end": v(-7.97, -18.25) * mm});
            skLineSegment(sketch, "E5934", {"start": v(-7.97, -18.25) * mm, "end": v(-7.74, -18.38) * mm});
            skLineSegment(sketch, "E5935", {"start": v(-7.74, -18.38) * mm, "end": v(-7.54, -18.5) * mm});
            skLineSegment(sketch, "E5936", {"start": v(-7.54, -18.5) * mm, "end": v(-7.35, -18.64) * mm});
            skLineSegment(sketch, "E5937", {"start": v(-7.35, -18.64) * mm, "end": v(-7.16, -18.82) * mm});
            skLineSegment(sketch, "E5938", {"start": v(-7.16, -18.82) * mm, "end": v(-6.96, -19.01) * mm});
            skLineSegment(sketch, "E5939", {"start": v(-6.96, -19.01) * mm, "end": v(-6.77, -19.22) * mm});
            skLineSegment(sketch, "E5940", {"start": v(-6.77, -19.22) * mm, "end": v(-6.38, -19.65) * mm});
            skLineSegment(sketch, "E5941", {"start": v(-6.38, -19.65) * mm, "end": v(-6.2, -19.84) * mm});
            skLineSegment(sketch, "E5942", {"start": v(-6.2, -19.84) * mm, "end": v(-6.04, -20) * mm});
            skLineSegment(sketch, "E5943", {"start": v(-24.24, -16.02) * mm, "end": v(-24.27, -16.03) * mm});
            skLineSegment(sketch, "E5944", {"start": v(-24.27, -16.03) * mm, "end": v(-24.3, -16.05) * mm});
            skLineSegment(sketch, "E5945", {"start": v(-24.3, -16.05) * mm, "end": v(-24.37, -16.13) * mm});
            skLineSegment(sketch, "E5946", {"start": v(-24.37, -16.13) * mm, "end": v(-24.44, -16.25) * mm});
            skLineSegment(sketch, "E5947", {"start": v(-24.44, -16.25) * mm, "end": v(-24.53, -16.42) * mm});
            skLineSegment(sketch, "E5948", {"start": v(-24.53, -16.42) * mm, "end": v(-24.62, -16.63) * mm});
            skLineSegment(sketch, "E5949", {"start": v(-24.62, -16.63) * mm, "end": v(-24.7, -16.86) * mm});
            skLineSegment(sketch, "E5950", {"start": v(-24.7, -16.86) * mm, "end": v(-24.8, -17.12) * mm});
            skLineSegment(sketch, "E5951", {"start": v(-24.8, -17.12) * mm, "end": v(-24.89, -17.4) * mm});
            skLineSegment(sketch, "E5952", {"start": v(-24.89, -17.4) * mm, "end": v(-24.97, -17.73) * mm});
            skLineSegment(sketch, "E5953", {"start": v(-24.97, -17.73) * mm, "end": v(-25.06, -18.1) * mm});
            skLineSegment(sketch, "E5954", {"start": v(-25.06, -18.1) * mm, "end": v(-25.1, -18.28) * mm});
            skLineSegment(sketch, "E5955", {"start": v(-25.1, -18.28) * mm, "end": v(-25.16, -18.46) * mm});
            skLineSegment(sketch, "E5956", {"start": v(-25.16, -18.46) * mm, "end": v(-25.22, -18.62) * mm});
            skLineSegment(sketch, "E5957", {"start": v(-25.22, -18.62) * mm, "end": v(-25.3, -18.77) * mm});
            skLineSegment(sketch, "E5958", {"start": v(-25.3, -18.77) * mm, "end": v(-25.46, -19.03) * mm});
            skLineSegment(sketch, "E5959", {"start": v(-25.46, -19.03) * mm, "end": v(-25.64, -19.28) * mm});
            skLineSegment(sketch, "E5960", {"start": v(-25.64, -19.28) * mm, "end": v(-25.83, -19.54) * mm});
            skLineSegment(sketch, "E5961", {"start": v(-25.83, -19.54) * mm, "end": v(-26.04, -19.8) * mm});
            skLineSegment(sketch, "E5962", {"start": v(-26.04, -19.8) * mm, "end": v(-26.26, -20.05) * mm});
            skLineSegment(sketch, "E5963", {"start": v(-26.26, -20.05) * mm, "end": v(-26.5, -20.3) * mm});
            skLineSegment(sketch, "E5964", {"start": v(-26.5, -20.3) * mm, "end": v(-26.74, -20.56) * mm});
            skLineSegment(sketch, "E5965", {"start": v(-26.74, -20.56) * mm, "end": v(-26.99, -20.8) * mm});
            skLineSegment(sketch, "E5966", {"start": v(-26.99, -20.8) * mm, "end": v(-27.5, -21.28) * mm});
            skLineSegment(sketch, "E5967", {"start": v(-27.5, -21.28) * mm, "end": v(-28.02, -21.72) * mm});
            skLineSegment(sketch, "E5968", {"start": v(-28.02, -21.72) * mm, "end": v(-28.53, -22.13) * mm});
            skLineSegment(sketch, "E5969", {"start": v(-28.53, -22.13) * mm, "end": v(-29.03, -22.5) * mm});
            skLineSegment(sketch, "E5970", {"start": v(-29.03, -22.5) * mm, "end": v(-29.43, -22.76) * mm});
            skLineSegment(sketch, "E5971", {"start": v(-29.43, -22.76) * mm, "end": v(-29.87, -23.02) * mm});
            skLineSegment(sketch, "E5972", {"start": v(-29.87, -23.02) * mm, "end": v(-30.34, -23.26) * mm});
            skLineSegment(sketch, "E5973", {"start": v(-30.34, -23.26) * mm, "end": v(-30.83, -23.5) * mm});
            skLineSegment(sketch, "E5974", {"start": v(-30.83, -23.5) * mm, "end": v(-31.32, -23.71) * mm});
            skLineSegment(sketch, "E5975", {"start": v(-31.32, -23.71) * mm, "end": v(-31.82, -23.92) * mm});
            skLineSegment(sketch, "E5976", {"start": v(-31.82, -23.92) * mm, "end": v(-32.3, -24.1) * mm});
            skLineSegment(sketch, "E5977", {"start": v(-32.3, -24.1) * mm, "end": v(-32.75, -24.25) * mm});
            skLineSegment(sketch, "E5978", {"start": v(-32.75, -24.25) * mm, "end": v(-33, -24.33) * mm});
            skLineSegment(sketch, "E5979", {"start": v(-33, -24.33) * mm, "end": v(-33.25, -24.4) * mm});
            skLineSegment(sketch, "E5980", {"start": v(-33.25, -24.4) * mm, "end": v(-33.8, -24.52) * mm});
            skLineSegment(sketch, "E5981", {"start": v(-33.8, -24.52) * mm, "end": v(-34.36, -24.63) * mm});
            skLineSegment(sketch, "E5982", {"start": v(-34.36, -24.63) * mm, "end": v(-34.95, -24.73) * mm});
            skLineSegment(sketch, "E5983", {"start": v(-34.95, -24.73) * mm, "end": v(-36.1, -24.91) * mm});
            skLineSegment(sketch, "E5984", {"start": v(-36.1, -24.91) * mm, "end": v(-36.66, -25) * mm});
            skLineSegment(sketch, "E5985", {"start": v(-36.66, -25) * mm, "end": v(-37.18, -25.1) * mm});
            skLineSegment(sketch, "E5986", {"start": v(-37.18, -25.1) * mm, "end": v(-37.14, -25.36) * mm});
            skLineSegment(sketch, "E5987", {"start": v(-37.14, -25.36) * mm, "end": v(-37.12, -25.66) * mm});
            skLineSegment(sketch, "E5988", {"start": v(-37.12, -25.66) * mm, "end": v(-37.08, -26.28) * mm});
            skLineSegment(sketch, "E5989", {"start": v(-37.08, -26.28) * mm, "end": v(-37.05, -26.58) * mm});
            skLineSegment(sketch, "E5990", {"start": v(-37.05, -26.58) * mm, "end": v(-37, -26.88) * mm});
            skLineSegment(sketch, "E5991", {"start": v(-37, -26.88) * mm, "end": v(-36.96, -27.02) * mm});
            skLineSegment(sketch, "E5992", {"start": v(-36.96, -27.02) * mm, "end": v(-36.92, -27.16) * mm});
            skLineSegment(sketch, "E5993", {"start": v(-36.92, -27.16) * mm, "end": v(-36.87, -27.28) * mm});
            skLineSegment(sketch, "E5994", {"start": v(-36.87, -27.28) * mm, "end": v(-36.81, -27.4) * mm});
            skLineSegment(sketch, "E5995", {"start": v(-36.81, -27.4) * mm, "end": v(-36.67, -27.63) * mm});
            skLineSegment(sketch, "E5996", {"start": v(-36.67, -27.63) * mm, "end": v(-36.5, -27.85) * mm});
            skLineSegment(sketch, "E5997", {"start": v(-36.5, -27.85) * mm, "end": v(-36.3, -28.07) * mm});
            skLineSegment(sketch, "E5998", {"start": v(-36.3, -28.07) * mm, "end": v(-36.07, -28.28) * mm});
            skLineSegment(sketch, "E5999", {"start": v(-36.07, -28.28) * mm, "end": v(-35.83, -28.47) * mm});
            skLineSegment(sketch, "E6000", {"start": v(-35.83, -28.47) * mm, "end": v(-35.6, -28.64) * mm});
            skLineSegment(sketch, "E6001", {"start": v(-35.6, -28.64) * mm, "end": v(-35.34, -28.78) * mm});
            skLineSegment(sketch, "E6002", {"start": v(-35.34, -28.78) * mm, "end": v(-35.22, -28.84) * mm});
            skLineSegment(sketch, "E6003", {"start": v(-35.22, -28.84) * mm, "end": v(-35.1, -28.89) * mm});
            skLineSegment(sketch, "E6004", {"start": v(-35.1, -28.89) * mm, "end": v(-34.96, -28.94) * mm});
            skLineSegment(sketch, "E6005", {"start": v(-34.96, -28.94) * mm, "end": v(-34.8, -28.97) * mm});
            skLineSegment(sketch, "E6006", {"start": v(-34.8, -28.97) * mm, "end": v(-34.65, -29) * mm});
            skLineSegment(sketch, "E6007", {"start": v(-34.65, -29) * mm, "end": v(-34.49, -29.03) * mm});
            skLineSegment(sketch, "E6008", {"start": v(-34.49, -29.03) * mm, "end": v(-34.15, -29.06) * mm});
            skLineSegment(sketch, "E6009", {"start": v(-34.15, -29.06) * mm, "end": v(-33.8, -29.06) * mm});
            skLineSegment(sketch, "E6010", {"start": v(-33.8, -29.06) * mm, "end": v(-33.45, -29.04) * mm});
            skLineSegment(sketch, "E6011", {"start": v(-33.45, -29.04) * mm, "end": v(-33.1, -29) * mm});
            skLineSegment(sketch, "E6012", {"start": v(-33.1, -29) * mm, "end": v(-32.78, -28.95) * mm});
            skLineSegment(sketch, "E6013", {"start": v(-32.78, -28.95) * mm, "end": v(-32.48, -28.89) * mm});
            skLineSegment(sketch, "E6014", {"start": v(-32.48, -28.89) * mm, "end": v(-32.23, -28.82) * mm});
            skLineSegment(sketch, "E6015", {"start": v(-32.23, -28.82) * mm, "end": v(-31.97, -28.74) * mm});
            skLineSegment(sketch, "E6016", {"start": v(-31.97, -28.74) * mm, "end": v(-31.7, -28.65) * mm});
            skLineSegment(sketch, "E6017", {"start": v(-31.7, -28.65) * mm, "end": v(-31.43, -28.55) * mm});
            skLineSegment(sketch, "E6018", {"start": v(-31.43, -28.55) * mm, "end": v(-31.16, -28.43) * mm});
            skLineSegment(sketch, "E6019", {"start": v(-31.16, -28.43) * mm, "end": v(-30.9, -28.3) * mm});
            skLineSegment(sketch, "E6020", {"start": v(-30.9, -28.3) * mm, "end": v(-30.35, -28.04) * mm});
            skLineSegment(sketch, "E6021", {"start": v(-30.35, -28.04) * mm, "end": v(-29.82, -27.75) * mm});
            skLineSegment(sketch, "E6022", {"start": v(-29.82, -27.75) * mm, "end": v(-29.31, -27.44) * mm});
            skLineSegment(sketch, "E6023", {"start": v(-29.31, -27.44) * mm, "end": v(-28.84, -27.13) * mm});
            skLineSegment(sketch, "E6024", {"start": v(-28.84, -27.13) * mm, "end": v(-28.4, -26.83) * mm});
            skLineSegment(sketch, "E6025", {"start": v(-28.4, -26.83) * mm, "end": v(-28.13, -26.63) * mm});
            skLineSegment(sketch, "E6026", {"start": v(-28.13, -26.63) * mm, "end": v(-27.87, -26.42) * mm});
            skLineSegment(sketch, "E6027", {"start": v(-27.87, -26.42) * mm, "end": v(-27.33, -25.96) * mm});
            skLineSegment(sketch, "E6028", {"start": v(-27.33, -25.96) * mm, "end": v(-26.8, -25.47) * mm});
            skLineSegment(sketch, "E6029", {"start": v(-26.8, -25.47) * mm, "end": v(-26.26, -24.94) * mm});
            skLineSegment(sketch, "E6030", {"start": v(-26.26, -24.94) * mm, "end": v(-25.74, -24.4) * mm});
            skLineSegment(sketch, "E6031", {"start": v(-25.74, -24.4) * mm, "end": v(-25.25, -23.85) * mm});
            skLineSegment(sketch, "E6032", {"start": v(-25.25, -23.85) * mm, "end": v(-24.8, -23.31) * mm});
            skLineSegment(sketch, "E6033", {"start": v(-24.8, -23.31) * mm, "end": v(-24.4, -22.78) * mm});
            skLineSegment(sketch, "E6034", {"start": v(-24.4, -22.78) * mm, "end": v(-24.25, -22.56) * mm});
            skLineSegment(sketch, "E6035", {"start": v(-24.25, -22.56) * mm, "end": v(-24.1, -22.32) * mm});
            skLineSegment(sketch, "E6036", {"start": v(-24.1, -22.32) * mm, "end": v(-23.83, -21.8) * mm});
            skLineSegment(sketch, "E6037", {"start": v(-23.83, -21.8) * mm, "end": v(-23.58, -21.25) * mm});
            skLineSegment(sketch, "E6038", {"start": v(-23.58, -21.25) * mm, "end": v(-23.33, -20.76) * mm});
            skLineSegment(sketch, "E6039", {"start": v(-23.33, -20.76) * mm, "end": v(-22.92, -19.94) * mm});
            skLineSegment(sketch, "E6040", {"start": v(-22.92, -19.94) * mm, "end": v(-22.58, -19.21) * mm});
            skLineSegment(sketch, "E6041", {"start": v(-22.58, -19.21) * mm, "end": v(-22.45, -18.9) * mm});
            skLineSegment(sketch, "E6042", {"start": v(-22.45, -18.9) * mm, "end": v(-22.35, -18.66) * mm});
            skLineSegment(sketch, "E6043", {"start": v(-22.35, -18.66) * mm, "end": v(-22.3, -18.47) * mm});
            skLineSegment(sketch, "E6044", {"start": v(-22.3, -18.47) * mm, "end": v(-22.27, -18.35) * mm});
            skLineSegment(sketch, "E6045", {"start": v(-22.27, -18.35) * mm, "end": v(-22.29, -18.26) * mm});
            skLineSegment(sketch, "E6046", {"start": v(-22.29, -18.26) * mm, "end": v(-22.34, -18.14) * mm});
            skLineSegment(sketch, "E6047", {"start": v(-22.34, -18.14) * mm, "end": v(-22.42, -18) * mm});
            skLineSegment(sketch, "E6048", {"start": v(-22.42, -18) * mm, "end": v(-22.54, -17.84) * mm});
            skLineSegment(sketch, "E6049", {"start": v(-22.54, -17.84) * mm, "end": v(-22.67, -17.67) * mm});
            skLineSegment(sketch, "E6050", {"start": v(-22.67, -17.67) * mm, "end": v(-22.82, -17.5) * mm});
            skLineSegment(sketch, "E6051", {"start": v(-22.82, -17.5) * mm, "end": v(-23, -17.32) * mm});
            skLineSegment(sketch, "E6052", {"start": v(-23, -17.32) * mm, "end": v(-23.18, -17.15) * mm});
            skLineSegment(sketch, "E6053", {"start": v(-23.18, -17.15) * mm, "end": v(-23.4, -16.96) * mm});
            skLineSegment(sketch, "E6054", {"start": v(-23.4, -16.96) * mm, "end": v(-23.65, -16.76) * mm});
            skLineSegment(sketch, "E6055", {"start": v(-23.65, -16.76) * mm, "end": v(-23.89, -16.55) * mm});
            skLineSegment(sketch, "E6056", {"start": v(-23.89, -16.55) * mm, "end": v(-24, -16.44) * mm});
            skLineSegment(sketch, "E6057", {"start": v(-24, -16.44) * mm, "end": v(-24.08, -16.33) * mm});
            skLineSegment(sketch, "E6058", {"start": v(-24.08, -16.33) * mm, "end": v(-24.17, -16.18) * mm});
            skLineSegment(sketch, "E6059", {"start": v(-24.17, -16.18) * mm, "end": v(-24.24, -16.02) * mm});
            skLineSegment(sketch, "E6060", {"start": v(-21.44, -18.51) * mm, "end": v(-21.4, -18.46) * mm});
            skLineSegment(sketch, "E6061", {"start": v(-21.4, -18.46) * mm, "end": v(-21.36, -18.4) * mm});
            skLineSegment(sketch, "E6062", {"start": v(-21.36, -18.4) * mm, "end": v(-21.29, -18.25) * mm});
            skLineSegment(sketch, "E6063", {"start": v(-21.29, -18.25) * mm, "end": v(-21.23, -18.06) * mm});
            skLineSegment(sketch, "E6064", {"start": v(-21.23, -18.06) * mm, "end": v(-21.17, -17.86) * mm});
            skLineSegment(sketch, "E6065", {"start": v(-21.17, -17.86) * mm, "end": v(-21.07, -17.43) * mm});
            skLineSegment(sketch, "E6066", {"start": v(-21.07, -17.43) * mm, "end": v(-20.98, -17.04) * mm});
            skLineSegment(sketch, "E6067", {"start": v(-20.98, -17.04) * mm, "end": v(-20.89, -16.7) * mm});
            skLineSegment(sketch, "E6068", {"start": v(-20.89, -16.7) * mm, "end": v(-20.77, -16.35) * mm});
            skLineSegment(sketch, "E6069", {"start": v(-20.77, -16.35) * mm, "end": v(-20.65, -16) * mm});
            skLineSegment(sketch, "E6070", {"start": v(-20.65, -16) * mm, "end": v(-20.5, -15.65) * mm});
            skLineSegment(sketch, "E6071", {"start": v(-20.5, -15.65) * mm, "end": v(-20.35, -15.3) * mm});
            skLineSegment(sketch, "E6072", {"start": v(-20.35, -15.3) * mm, "end": v(-20.2, -14.96) * mm});
            skLineSegment(sketch, "E6073", {"start": v(-20.2, -14.96) * mm, "end": v(-20.02, -14.61) * mm});
            skLineSegment(sketch, "E6074", {"start": v(-20.02, -14.61) * mm, "end": v(-19.83, -14.27) * mm});
            skLineSegment(sketch, "E6075", {"start": v(-19.83, -14.27) * mm, "end": v(-19.63, -13.94) * mm});
            skLineSegment(sketch, "E6076", {"start": v(-19.63, -13.94) * mm, "end": v(-19.43, -13.61) * mm});
            skLineSegment(sketch, "E6077", {"start": v(-19.43, -13.61) * mm, "end": v(-19.21, -13.3) * mm});
            skLineSegment(sketch, "E6078", {"start": v(-19.21, -13.3) * mm, "end": v(-18.99, -12.98) * mm});
            skLineSegment(sketch, "E6079", {"start": v(-18.99, -12.98) * mm, "end": v(-18.75, -12.67) * mm});
            skLineSegment(sketch, "E6080", {"start": v(-18.75, -12.67) * mm, "end": v(-18.51, -12.37) * mm});
            skLineSegment(sketch, "E6081", {"start": v(-18.51, -12.37) * mm, "end": v(-18.26, -12.09) * mm});
            skLineSegment(sketch, "E6082", {"start": v(-18.26, -12.09) * mm, "end": v(-18, -11.81) * mm});
            skLineSegment(sketch, "E6083", {"start": v(-18, -11.81) * mm, "end": v(-17.75, -11.56) * mm});
            skLineSegment(sketch, "E6084", {"start": v(-17.75, -11.56) * mm, "end": v(-17.48, -11.31) * mm});
            skLineSegment(sketch, "E6085", {"start": v(-17.48, -11.31) * mm, "end": v(-17.37, -11.2) * mm});
            skLineSegment(sketch, "E6086", {"start": v(-17.37, -11.2) * mm, "end": v(-17.28, -11.1) * mm});
            skLineSegment(sketch, "E6087", {"start": v(-17.28, -11.1) * mm, "end": v(-17.23, -11) * mm});
            skLineSegment(sketch, "E6088", {"start": v(-17.23, -11) * mm, "end": v(-17.22, -10.97) * mm});
            skLineSegment(sketch, "E6089", {"start": v(-17.22, -10.97) * mm, "end": v(-17.22, -10.94) * mm});
            skLineSegment(sketch, "E6090", {"start": v(-17.22, -10.94) * mm, "end": v(-17.24, -10.91) * mm});
            skLineSegment(sketch, "E6091", {"start": v(-17.24, -10.91) * mm, "end": v(-17.27, -10.9) * mm});
            skLineSegment(sketch, "E6092", {"start": v(-17.27, -10.9) * mm, "end": v(-17.39, -10.86) * mm});
            skLineSegment(sketch, "E6093", {"start": v(-17.39, -10.86) * mm, "end": v(-17.54, -10.84) * mm});
            skLineSegment(sketch, "E6094", {"start": v(-17.54, -10.84) * mm, "end": v(-17.71, -10.83) * mm});
            skLineSegment(sketch, "E6095", {"start": v(-17.71, -10.83) * mm, "end": v(-18.06, -10.83) * mm});
            skLineSegment(sketch, "E6096", {"start": v(-18.06, -10.83) * mm, "end": v(-18.2, -10.84) * mm});
            skLineSegment(sketch, "E6097", {"start": v(-18.2, -10.84) * mm, "end": v(-18.27, -10.85) * mm});
            skLineSegment(sketch, "E6098", {"start": v(-18.27, -10.85) * mm, "end": v(-18.33, -10.87) * mm});
            skLineSegment(sketch, "E6099", {"start": v(-18.33, -10.87) * mm, "end": v(-18.4, -10.9) * mm});
            skLineSegment(sketch, "E6100", {"start": v(-18.4, -10.9) * mm, "end": v(-18.5, -11) * mm});
            skLineSegment(sketch, "E6101", {"start": v(-18.5, -11) * mm, "end": v(-18.61, -11.13) * mm});
            skLineSegment(sketch, "E6102", {"start": v(-18.61, -11.13) * mm, "end": v(-18.72, -11.29) * mm});
            skLineSegment(sketch, "E6103", {"start": v(-18.72, -11.29) * mm, "end": v(-18.93, -11.62) * mm});
            skLineSegment(sketch, "E6104", {"start": v(-18.93, -11.62) * mm, "end": v(-19.03, -11.78) * mm});
            skLineSegment(sketch, "E6105", {"start": v(-19.03, -11.78) * mm, "end": v(-19.13, -11.92) * mm});
            skLineSegment(sketch, "E6106", {"start": v(-19.13, -11.92) * mm, "end": v(-19.34, -12.17) * mm});
            skLineSegment(sketch, "E6107", {"start": v(-19.34, -12.17) * mm, "end": v(-19.57, -12.43) * mm});
            skLineSegment(sketch, "E6108", {"start": v(-19.57, -12.43) * mm, "end": v(-19.81, -12.7) * mm});
            skLineSegment(sketch, "E6109", {"start": v(-19.81, -12.7) * mm, "end": v(-20.07, -12.94) * mm});
            skLineSegment(sketch, "E6110", {"start": v(-20.07, -12.94) * mm, "end": v(-20.34, -13.18) * mm});
            skLineSegment(sketch, "E6111", {"start": v(-20.34, -13.18) * mm, "end": v(-20.6, -13.4) * mm});
            skLineSegment(sketch, "E6112", {"start": v(-20.6, -13.4) * mm, "end": v(-20.84, -13.59) * mm});
            skLineSegment(sketch, "E6113", {"start": v(-20.84, -13.59) * mm, "end": v(-21.07, -13.74) * mm});
            skLineSegment(sketch, "E6114", {"start": v(-21.07, -13.74) * mm, "end": v(-21.31, -13.9) * mm});
            skLineSegment(sketch, "E6115", {"start": v(-21.31, -13.9) * mm, "end": v(-21.57, -14.09) * mm});
            skLineSegment(sketch, "E6116", {"start": v(-21.57, -14.09) * mm, "end": v(-21.7, -14.17) * mm});
            skLineSegment(sketch, "E6117", {"start": v(-21.7, -14.17) * mm, "end": v(-21.84, -14.25) * mm});
            skLineSegment(sketch, "E6118", {"start": v(-21.84, -14.25) * mm, "end": v(-21.97, -14.32) * mm});
            skLineSegment(sketch, "E6119", {"start": v(-21.97, -14.32) * mm, "end": v(-22.1, -14.37) * mm});
            skLineSegment(sketch, "E6120", {"start": v(-22.1, -14.37) * mm, "end": v(-22.23, -14.4) * mm});
            skLineSegment(sketch, "E6121", {"start": v(-22.23, -14.4) * mm, "end": v(-22.36, -14.42) * mm});
            skLineSegment(sketch, "E6122", {"start": v(-22.36, -14.42) * mm, "end": v(-22.63, -14.44) * mm});
            skLineSegment(sketch, "E6123", {"start": v(-22.63, -14.44) * mm, "end": v(-22.91, -14.45) * mm});
            skLineSegment(sketch, "E6124", {"start": v(-22.91, -14.45) * mm, "end": v(-23.2, -14.44) * mm});
            skLineSegment(sketch, "E6125", {"start": v(-23.2, -14.44) * mm, "end": v(-23.79, -14.4) * mm});
            skLineSegment(sketch, "E6126", {"start": v(-23.79, -14.4) * mm, "end": v(-24.07, -14.38) * mm});
            skLineSegment(sketch, "E6127", {"start": v(-24.07, -14.38) * mm, "end": v(-24.33, -14.37) * mm});
            skLineSegment(sketch, "E6128", {"start": v(-24.33, -14.37) * mm, "end": v(-24.23, -14.76) * mm});
            skLineSegment(sketch, "E6129", {"start": v(-24.23, -14.76) * mm, "end": v(-24.15, -15.2) * mm});
            skLineSegment(sketch, "E6130", {"start": v(-24.15, -15.2) * mm, "end": v(-24.1, -15.4) * mm});
            skLineSegment(sketch, "E6131", {"start": v(-24.1, -15.4) * mm, "end": v(-24.03, -15.61) * mm});
            skLineSegment(sketch, "E6132", {"start": v(-24.03, -15.61) * mm, "end": v(-23.96, -15.8) * mm});
            skLineSegment(sketch, "E6133", {"start": v(-23.96, -15.8) * mm, "end": v(-23.88, -15.98) * mm});
            skLineSegment(sketch, "E6134", {"start": v(-23.88, -15.98) * mm, "end": v(-23.82, -16.07) * mm});
            skLineSegment(sketch, "E6135", {"start": v(-23.82, -16.07) * mm, "end": v(-23.75, -16.16) * mm});
            skLineSegment(sketch, "E6136", {"start": v(-23.75, -16.16) * mm, "end": v(-23.58, -16.33) * mm});
            skLineSegment(sketch, "E6137", {"start": v(-23.58, -16.33) * mm, "end": v(-23.4, -16.5) * mm});
            skLineSegment(sketch, "E6138", {"start": v(-23.4, -16.5) * mm, "end": v(-23.22, -16.64) * mm});
            skLineSegment(sketch, "E6139", {"start": v(-23.22, -16.64) * mm, "end": v(-23.02, -16.8) * mm});
            skLineSegment(sketch, "E6140", {"start": v(-23.02, -16.8) * mm, "end": v(-22.82, -16.97) * mm});
            skLineSegment(sketch, "E6141", {"start": v(-22.82, -16.97) * mm, "end": v(-22.43, -17.32) * mm});
            skLineSegment(sketch, "E6142", {"start": v(-22.43, -17.32) * mm, "end": v(-22.24, -17.5) * mm});
            skLineSegment(sketch, "E6143", {"start": v(-22.24, -17.5) * mm, "end": v(-22.07, -17.69) * mm});
            skLineSegment(sketch, "E6144", {"start": v(-22.07, -17.69) * mm, "end": v(-21.91, -17.88) * mm});
            skLineSegment(sketch, "E6145", {"start": v(-21.91, -17.88) * mm, "end": v(-21.75, -18.1) * mm});
            skLineSegment(sketch, "E6146", {"start": v(-21.75, -18.1) * mm, "end": v(-21.44, -18.51) * mm});
            skLineSegment(sketch, "E6147", {"start": v(-9.77, -25.48) * mm, "end": v(-9.5, -26.1) * mm});
            skLineSegment(sketch, "E6148", {"start": v(-9.5, -26.1) * mm, "end": v(-9.21, -26.75) * mm});
            skLineSegment(sketch, "E6149", {"start": v(-9.21, -26.75) * mm, "end": v(-8.92, -27.44) * mm});
            skLineSegment(sketch, "E6150", {"start": v(-8.92, -27.44) * mm, "end": v(-8.64, -28.15) * mm});
            skLineSegment(sketch, "E6151", {"start": v(-8.64, -28.15) * mm, "end": v(-8.36, -28.87) * mm});
            skLineSegment(sketch, "E6152", {"start": v(-8.36, -28.87) * mm, "end": v(-8.1, -29.57) * mm});
            skLineSegment(sketch, "E6153", {"start": v(-8.1, -29.57) * mm, "end": v(-7.85, -30.24) * mm});
            skLineSegment(sketch, "E6154", {"start": v(-7.85, -30.24) * mm, "end": v(-7.63, -30.87) * mm});
            skLineSegment(sketch, "E6155", {"start": v(-7.63, -30.87) * mm, "end": v(-7.28, -30.57) * mm});
            skLineSegment(sketch, "E6156", {"start": v(-7.28, -30.57) * mm, "end": v(-6.88, -30.25) * mm});
            skLineSegment(sketch, "E6157", {"start": v(-6.88, -30.25) * mm, "end": v(-6.7, -30.08) * mm});
            skLineSegment(sketch, "E6158", {"start": v(-6.7, -30.08) * mm, "end": v(-6.51, -29.9) * mm});
            skLineSegment(sketch, "E6159", {"start": v(-6.51, -29.9) * mm, "end": v(-6.35, -29.73) * mm});
            skLineSegment(sketch, "E6160", {"start": v(-6.35, -29.73) * mm, "end": v(-6.22, -29.55) * mm});
            skLineSegment(sketch, "E6161", {"start": v(-6.22, -29.55) * mm, "end": v(-6.11, -29.36) * mm});
            skLineSegment(sketch, "E6162", {"start": v(-6.11, -29.36) * mm, "end": v(-6, -29.17) * mm});
            skLineSegment(sketch, "E6163", {"start": v(-6, -29.17) * mm, "end": v(-5.91, -28.97) * mm});
            skLineSegment(sketch, "E6164", {"start": v(-5.91, -28.97) * mm, "end": v(-5.82, -28.75) * mm});
            skLineSegment(sketch, "E6165", {"start": v(-5.82, -28.75) * mm, "end": v(-5.65, -28.3) * mm});
            skLineSegment(sketch, "E6166", {"start": v(-5.65, -28.3) * mm, "end": v(-5.5, -27.84) * mm});
            skLineSegment(sketch, "E6167", {"start": v(-5.5, -27.84) * mm, "end": v(-5.38, -27.37) * mm});
            skLineSegment(sketch, "E6168", {"start": v(-5.38, -27.37) * mm, "end": v(-5.27, -26.9) * mm});
            skLineSegment(sketch, "E6169", {"start": v(-5.27, -26.9) * mm, "end": v(-5.18, -26.45) * mm});
            skLineSegment(sketch, "E6170", {"start": v(-5.18, -26.45) * mm, "end": v(-5.11, -26.03) * mm});
            skLineSegment(sketch, "E6171", {"start": v(-5.11, -26.03) * mm, "end": v(-5.02, -25.33) * mm});
            skLineSegment(sketch, "E6172", {"start": v(-5.02, -25.33) * mm, "end": v(-5, -25.01) * mm});
            skLineSegment(sketch, "E6173", {"start": v(-5, -25.01) * mm, "end": v(-4.97, -24.71) * mm});
            skLineSegment(sketch, "E6174", {"start": v(-4.97, -24.71) * mm, "end": v(-4.96, -24.43) * mm});
            skLineSegment(sketch, "E6175", {"start": v(-4.96, -24.43) * mm, "end": v(-4.96, -24.16) * mm});
            skLineSegment(sketch, "E6176", {"start": v(-4.96, -24.16) * mm, "end": v(-4.97, -23.9) * mm});
            skLineSegment(sketch, "E6177", {"start": v(-4.97, -23.9) * mm, "end": v(-5, -23.67) * mm});
            skLineSegment(sketch, "E6178", {"start": v(-5, -23.67) * mm, "end": v(-5.02, -23.44) * mm});
            skLineSegment(sketch, "E6179", {"start": v(-5.02, -23.44) * mm, "end": v(-5.06, -23.23) * mm});
            skLineSegment(sketch, "E6180", {"start": v(-5.06, -23.23) * mm, "end": v(-5.1, -23.03) * mm});
            skLineSegment(sketch, "E6181", {"start": v(-5.1, -23.03) * mm, "end": v(-5.16, -22.85) * mm});
            skLineSegment(sketch, "E6182", {"start": v(-5.16, -22.85) * mm, "end": v(-5.23, -22.67) * mm});
            skLineSegment(sketch, "E6183", {"start": v(-5.23, -22.67) * mm, "end": v(-5.3, -22.5) * mm});
            skLineSegment(sketch, "E6184", {"start": v(-5.3, -22.5) * mm, "end": v(-5.39, -22.35) * mm});
            skLineSegment(sketch, "E6185", {"start": v(-5.39, -22.35) * mm, "end": v(-5.48, -22.2) * mm});
            skLineSegment(sketch, "E6186", {"start": v(-5.48, -22.2) * mm, "end": v(-5.73, -21.82) * mm});
            skLineSegment(sketch, "E6187", {"start": v(-5.73, -21.82) * mm, "end": v(-6, -21.43) * mm});
            skLineSegment(sketch, "E6188", {"start": v(-6, -21.43) * mm, "end": v(-6.25, -21.05) * mm});
            skLineSegment(sketch, "E6189", {"start": v(-6.25, -21.05) * mm, "end": v(-6.38, -20.88) * mm});
            skLineSegment(sketch, "E6190", {"start": v(-6.38, -20.88) * mm, "end": v(-6.5, -20.7) * mm});
            skLineSegment(sketch, "E6191", {"start": v(-6.5, -20.7) * mm, "end": v(-6.8, -20.35) * mm});
            skLineSegment(sketch, "E6192", {"start": v(-6.8, -20.35) * mm, "end": v(-7.1, -19.97) * mm});
            skLineSegment(sketch, "E6193", {"start": v(-7.1, -19.97) * mm, "end": v(-7.42, -19.61) * mm});
            skLineSegment(sketch, "E6194", {"start": v(-7.42, -19.61) * mm, "end": v(-7.57, -19.45) * mm});
            skLineSegment(sketch, "E6195", {"start": v(-7.57, -19.45) * mm, "end": v(-7.73, -19.3) * mm});
            skLineSegment(sketch, "E6196", {"start": v(-7.73, -19.3) * mm, "end": v(-7.82, -19.22) * mm});
            skLineSegment(sketch, "E6197", {"start": v(-7.82, -19.22) * mm, "end": v(-7.93, -19.14) * mm});
            skLineSegment(sketch, "E6198", {"start": v(-7.93, -19.14) * mm, "end": v(-8.15, -19) * mm});
            skLineSegment(sketch, "E6199", {"start": v(-8.15, -19) * mm, "end": v(-8.4, -18.88) * mm});
            skLineSegment(sketch, "E6200", {"start": v(-8.4, -18.88) * mm, "end": v(-8.64, -18.77) * mm});
            skLineSegment(sketch, "E6201", {"start": v(-8.64, -18.77) * mm, "end": v(-9.15, -18.57) * mm});
            skLineSegment(sketch, "E6202", {"start": v(-9.15, -18.57) * mm, "end": v(-9.4, -18.47) * mm});
            skLineSegment(sketch, "E6203", {"start": v(-9.4, -18.47) * mm, "end": v(-9.63, -18.36) * mm});
            skLineSegment(sketch, "E6204", {"start": v(-9.63, -18.36) * mm, "end": v(-9.97, -18.21) * mm});
            skLineSegment(sketch, "E6205", {"start": v(-9.97, -18.21) * mm, "end": v(-10.32, -18.08) * mm});
            skLineSegment(sketch, "E6206", {"start": v(-10.32, -18.08) * mm, "end": v(-10.7, -17.97) * mm});
            skLineSegment(sketch, "E6207", {"start": v(-10.7, -17.97) * mm, "end": v(-11.08, -17.88) * mm});
            skLineSegment(sketch, "E6208", {"start": v(-11.08, -17.88) * mm, "end": v(-11.48, -17.82) * mm});
            skLineSegment(sketch, "E6209", {"start": v(-11.48, -17.82) * mm, "end": v(-11.9, -17.77) * mm});
            skLineSegment(sketch, "E6210", {"start": v(-11.9, -17.77) * mm, "end": v(-12.33, -17.75) * mm});
            skLineSegment(sketch, "E6211", {"start": v(-12.33, -17.75) * mm, "end": v(-12.79, -17.75) * mm});
            skLineSegment(sketch, "E6212", {"start": v(-12.79, -17.75) * mm, "end": v(-13.22, -17.77) * mm});
            skLineSegment(sketch, "E6213", {"start": v(-13.22, -17.77) * mm, "end": v(-13.72, -17.8) * mm});
            skLineSegment(sketch, "E6214", {"start": v(-13.72, -17.8) * mm, "end": v(-14.26, -17.85) * mm});
            skLineSegment(sketch, "E6215", {"start": v(-14.26, -17.85) * mm, "end": v(-14.82, -17.91) * mm});
            skLineSegment(sketch, "E6216", {"start": v(-14.82, -17.91) * mm, "end": v(-15.38, -18) * mm});
            skLineSegment(sketch, "E6217", {"start": v(-15.38, -18) * mm, "end": v(-15.64, -18.05) * mm});
            skLineSegment(sketch, "E6218", {"start": v(-15.64, -18.05) * mm, "end": v(-15.9, -18.1) * mm});
            skLineSegment(sketch, "E6219", {"start": v(-15.9, -18.1) * mm, "end": v(-16.13, -18.17) * mm});
            skLineSegment(sketch, "E6220", {"start": v(-16.13, -18.17) * mm, "end": v(-16.35, -18.24) * mm});
            skLineSegment(sketch, "E6221", {"start": v(-16.35, -18.24) * mm, "end": v(-16.55, -18.32) * mm});
            skLineSegment(sketch, "E6222", {"start": v(-16.55, -18.32) * mm, "end": v(-16.72, -18.41) * mm});
            skLineSegment(sketch, "E6223", {"start": v(-16.72, -18.41) * mm, "end": v(-17.12, -18.63) * mm});
            skLineSegment(sketch, "E6224", {"start": v(-17.12, -18.63) * mm, "end": v(-17.59, -18.85) * mm});
            skLineSegment(sketch, "E6225", {"start": v(-17.59, -18.85) * mm, "end": v(-18.63, -19.35) * mm});
            skLineSegment(sketch, "E6226", {"start": v(-18.63, -19.35) * mm, "end": v(-19.17, -19.61) * mm});
            skLineSegment(sketch, "E6227", {"start": v(-19.17, -19.61) * mm, "end": v(-19.69, -19.9) * mm});
            skLineSegment(sketch, "E6228", {"start": v(-19.69, -19.9) * mm, "end": v(-19.94, -20.03) * mm});
            skLineSegment(sketch, "E6229", {"start": v(-19.94, -20.03) * mm, "end": v(-20.18, -20.18) * mm});
            skLineSegment(sketch, "E6230", {"start": v(-20.18, -20.18) * mm, "end": v(-20.4, -20.32) * mm});
            skLineSegment(sketch, "E6231", {"start": v(-20.4, -20.32) * mm, "end": v(-20.61, -20.47) * mm});
            skLineSegment(sketch, "E6232", {"start": v(-20.61, -20.47) * mm, "end": v(-20.63, -20.52) * mm});
            skLineSegment(sketch, "E6233", {"start": v(-20.63, -20.52) * mm, "end": v(-20.66, -20.58) * mm});
            skLineSegment(sketch, "E6234", {"start": v(-20.66, -20.58) * mm, "end": v(-20.8, -20.7) * mm});
            skLineSegment(sketch, "E6235", {"start": v(-20.8, -20.7) * mm, "end": v(-20.98, -20.87) * mm});
            skLineSegment(sketch, "E6236", {"start": v(-20.98, -20.87) * mm, "end": v(-21.2, -21.07) * mm});
            skLineSegment(sketch, "E6237", {"start": v(-21.2, -21.07) * mm, "end": v(-21.45, -21.3) * mm});
            skLineSegment(sketch, "E6238", {"start": v(-21.45, -21.3) * mm, "end": v(-21.57, -21.42) * mm});
            skLineSegment(sketch, "E6239", {"start": v(-21.57, -21.42) * mm, "end": v(-21.69, -21.55) * mm});
            skLineSegment(sketch, "E6240", {"start": v(-21.69, -21.55) * mm, "end": v(-21.8, -21.69) * mm});
            skLineSegment(sketch, "E6241", {"start": v(-21.8, -21.69) * mm, "end": v(-21.9, -21.83) * mm});
            skLineSegment(sketch, "E6242", {"start": v(-21.9, -21.83) * mm, "end": v(-22, -21.99) * mm});
            skLineSegment(sketch, "E6243", {"start": v(-22, -21.99) * mm, "end": v(-22.07, -22.15) * mm});
            skLineSegment(sketch, "E6244", {"start": v(-22.07, -22.15) * mm, "end": v(-22.2, -22.45) * mm});
            skLineSegment(sketch, "E6245", {"start": v(-22.2, -22.45) * mm, "end": v(-22.37, -22.74) * mm});
            skLineSegment(sketch, "E6246", {"start": v(-22.37, -22.74) * mm, "end": v(-22.72, -23.35) * mm});
            skLineSegment(sketch, "E6247", {"start": v(-22.72, -23.35) * mm, "end": v(-22.9, -23.66) * mm});
            skLineSegment(sketch, "E6248", {"start": v(-22.9, -23.66) * mm, "end": v(-23.07, -23.98) * mm});
            skLineSegment(sketch, "E6249", {"start": v(-23.07, -23.98) * mm, "end": v(-23.22, -24.32) * mm});
            skLineSegment(sketch, "E6250", {"start": v(-23.22, -24.32) * mm, "end": v(-23.28, -24.49) * mm});
            skLineSegment(sketch, "E6251", {"start": v(-23.28, -24.49) * mm, "end": v(-23.34, -24.66) * mm});
            skLineSegment(sketch, "E6252", {"start": v(-23.34, -24.66) * mm, "end": v(-23.51, -25.26) * mm});
            skLineSegment(sketch, "E6253", {"start": v(-23.51, -25.26) * mm, "end": v(-23.66, -25.85) * mm});
            skLineSegment(sketch, "E6254", {"start": v(-23.66, -25.85) * mm, "end": v(-23.88, -26.94) * mm});
            skLineSegment(sketch, "E6255", {"start": v(-23.88, -26.94) * mm, "end": v(-23.97, -27.41) * mm});
            skLineSegment(sketch, "E6256", {"start": v(-23.97, -27.41) * mm, "end": v(-24.07, -27.81) * mm});
            skLineSegment(sketch, "E6257", {"start": v(-24.07, -27.81) * mm, "end": v(-24.12, -27.98) * mm});
            skLineSegment(sketch, "E6258", {"start": v(-24.12, -27.98) * mm, "end": v(-24.17, -28.12) * mm});
            skLineSegment(sketch, "E6259", {"start": v(-24.17, -28.12) * mm, "end": v(-24.22, -28.24) * mm});
            skLineSegment(sketch, "E6260", {"start": v(-24.22, -28.24) * mm, "end": v(-24.28, -28.33) * mm});
            skLineSegment(sketch, "E6261", {"start": v(-24.28, -28.33) * mm, "end": v(-22.7, -27.78) * mm});
            skLineSegment(sketch, "E6262", {"start": v(-22.7, -27.78) * mm, "end": v(-22.5, -27.64) * mm});
            skLineSegment(sketch, "E6263", {"start": v(-22.5, -27.64) * mm, "end": v(-22.28, -27.5) * mm});
            skLineSegment(sketch, "E6264", {"start": v(-22.28, -27.5) * mm, "end": v(-21.8, -27.2) * mm});
            skLineSegment(sketch, "E6265", {"start": v(-21.8, -27.2) * mm, "end": v(-21.3, -26.89) * mm});
            skLineSegment(sketch, "E6266", {"start": v(-21.3, -26.89) * mm, "end": v(-21.09, -26.74) * mm});
            skLineSegment(sketch, "E6267", {"start": v(-21.09, -26.74) * mm, "end": v(-20.9, -26.6) * mm});
            skLineSegment(sketch, "E6268", {"start": v(-20.9, -26.6) * mm, "end": v(-20.53, -26.27) * mm});
            skLineSegment(sketch, "E6269", {"start": v(-20.53, -26.27) * mm, "end": v(-20.19, -25.93) * mm});
            skLineSegment(sketch, "E6270", {"start": v(-20.19, -25.93) * mm, "end": v(-20.02, -25.76) * mm});
            skLineSegment(sketch, "E6271", {"start": v(-20.02, -25.76) * mm, "end": v(-19.86, -25.57) * mm});
            skLineSegment(sketch, "E6272", {"start": v(-19.86, -25.57) * mm, "end": v(-19.7, -25.38) * mm});
            skLineSegment(sketch, "E6273", {"start": v(-19.7, -25.38) * mm, "end": v(-19.55, -25.18) * mm});
            skLineSegment(sketch, "E6274", {"start": v(-19.55, -25.18) * mm, "end": v(-19.43, -25.04) * mm});
            skLineSegment(sketch, "E6275", {"start": v(-19.43, -25.04) * mm, "end": v(-19.29, -24.9) * mm});
            skLineSegment(sketch, "E6276", {"start": v(-19.29, -24.9) * mm, "end": v(-19.14, -24.76) * mm});
            skLineSegment(sketch, "E6277", {"start": v(-19.14, -24.76) * mm, "end": v(-18.98, -24.62) * mm});
            skLineSegment(sketch, "E6278", {"start": v(-18.98, -24.62) * mm, "end": v(-18.65, -24.38) * mm});
            skLineSegment(sketch, "E6279", {"start": v(-18.65, -24.38) * mm, "end": v(-18.31, -24.17) * mm});
            skLineSegment(sketch, "E6280", {"start": v(-18.31, -24.17) * mm, "end": v(-17.83, -23.88) * mm});
            skLineSegment(sketch, "E6281", {"start": v(-17.83, -23.88) * mm, "end": v(-17.37, -23.62) * mm});
            skLineSegment(sketch, "E6282", {"start": v(-17.37, -23.62) * mm, "end": v(-16.92, -23.37) * mm});
            skLineSegment(sketch, "E6283", {"start": v(-16.92, -23.37) * mm, "end": v(-16.47, -23.15) * mm});
            skLineSegment(sketch, "E6284", {"start": v(-16.47, -23.15) * mm, "end": v(-16.24, -23.05) * mm});
            skLineSegment(sketch, "E6285", {"start": v(-16.24, -23.05) * mm, "end": v(-16.01, -22.95) * mm});
            skLineSegment(sketch, "E6286", {"start": v(-16.01, -22.95) * mm, "end": v(-15.77, -22.87) * mm});
            skLineSegment(sketch, "E6287", {"start": v(-15.77, -22.87) * mm, "end": v(-15.53, -22.79) * mm});
            skLineSegment(sketch, "E6288", {"start": v(-15.53, -22.79) * mm, "end": v(-15.28, -22.71) * mm});
            skLineSegment(sketch, "E6289", {"start": v(-15.28, -22.71) * mm, "end": v(-15.02, -22.65) * mm});
            skLineSegment(sketch, "E6290", {"start": v(-15.02, -22.65) * mm, "end": v(-14.75, -22.59) * mm});
            skLineSegment(sketch, "E6291", {"start": v(-14.75, -22.59) * mm, "end": v(-14.47, -22.54) * mm});
            skLineSegment(sketch, "E6292", {"start": v(-14.47, -22.54) * mm, "end": v(-14.25, -22.51) * mm});
            skLineSegment(sketch, "E6293", {"start": v(-14.25, -22.51) * mm, "end": v(-14, -22.5) * mm});
            skLineSegment(sketch, "E6294", {"start": v(-14, -22.5) * mm, "end": v(-13.7, -22.5) * mm});
            skLineSegment(sketch, "E6295", {"start": v(-13.7, -22.5) * mm, "end": v(-13.4, -22.52) * mm});
            skLineSegment(sketch, "E6296", {"start": v(-13.4, -22.52) * mm, "end": v(-13.11, -22.55) * mm});
            skLineSegment(sketch, "E6297", {"start": v(-13.11, -22.55) * mm, "end": v(-12.83, -22.6) * mm});
            skLineSegment(sketch, "E6298", {"start": v(-12.83, -22.6) * mm, "end": v(-12.58, -22.65) * mm});
            skLineSegment(sketch, "E6299", {"start": v(-12.58, -22.65) * mm, "end": v(-12.37, -22.72) * mm});
            skLineSegment(sketch, "E6300", {"start": v(-12.37, -22.72) * mm, "end": v(-12.13, -22.83) * mm});
            skLineSegment(sketch, "E6301", {"start": v(-12.13, -22.83) * mm, "end": v(-11.92, -22.94) * mm});
            skLineSegment(sketch, "E6302", {"start": v(-11.92, -22.94) * mm, "end": v(-11.72, -23.07) * mm});
            skLineSegment(sketch, "E6303", {"start": v(-11.72, -23.07) * mm, "end": v(-11.54, -23.2) * mm});
            skLineSegment(sketch, "E6304", {"start": v(-11.54, -23.2) * mm, "end": v(-11.36, -23.36) * mm});
            skLineSegment(sketch, "E6305", {"start": v(-11.36, -23.36) * mm, "end": v(-11.19, -23.52) * mm});
            skLineSegment(sketch, "E6306", {"start": v(-11.19, -23.52) * mm, "end": v(-11.02, -23.7) * mm});
            skLineSegment(sketch, "E6307", {"start": v(-11.02, -23.7) * mm, "end": v(-10.85, -23.9) * mm});
            skLineSegment(sketch, "E6308", {"start": v(-10.85, -23.9) * mm, "end": v(-10.55, -24.27) * mm});
            skLineSegment(sketch, "E6309", {"start": v(-10.55, -24.27) * mm, "end": v(-10.25, -24.66) * mm});
            skLineSegment(sketch, "E6310", {"start": v(-10.25, -24.66) * mm, "end": v(-10.12, -24.86) * mm});
            skLineSegment(sketch, "E6311", {"start": v(-10.12, -24.86) * mm, "end": v(-9.99, -25.06) * mm});
            skLineSegment(sketch, "E6312", {"start": v(-9.99, -25.06) * mm, "end": v(-9.87, -25.27) * mm});
            skLineSegment(sketch, "E6313", {"start": v(-9.87, -25.27) * mm, "end": v(-9.77, -25.48) * mm});
            skLineSegment(sketch, "E6314", {"start": v(27.4, -28.34) * mm, "end": v(27.52, -28.44) * mm});
            skLineSegment(sketch, "E6315", {"start": v(27.52, -28.44) * mm, "end": v(27.66, -28.52) * mm});
            skLineSegment(sketch, "E6316", {"start": v(27.66, -28.52) * mm, "end": v(27.96, -28.69) * mm});
            skLineSegment(sketch, "E6317", {"start": v(27.96, -28.69) * mm, "end": v(28.27, -28.84) * mm});
            skLineSegment(sketch, "E6318", {"start": v(28.27, -28.84) * mm, "end": v(28.6, -28.98) * mm});
            skLineSegment(sketch, "E6319", {"start": v(28.6, -28.98) * mm, "end": v(29.28, -29.24) * mm});
            skLineSegment(sketch, "E6320", {"start": v(29.28, -29.24) * mm, "end": v(29.6, -29.37) * mm});
            skLineSegment(sketch, "E6321", {"start": v(29.6, -29.37) * mm, "end": v(29.9, -29.5) * mm});
            skLineSegment(sketch, "E6322", {"start": v(29.9, -29.5) * mm, "end": v(32.85, -30.93) * mm});
            skLineSegment(sketch, "E6323", {"start": v(32.85, -30.93) * mm, "end": v(33.83, -30.56) * mm});
            skLineSegment(sketch, "E6324", {"start": v(33.83, -30.56) * mm, "end": v(33.83, -29.36) * mm});
            skLineSegment(sketch, "E6325", {"start": v(33.83, -29.36) * mm, "end": v(33.26, -29.08) * mm});
            skLineSegment(sketch, "E6326", {"start": v(33.26, -29.08) * mm, "end": v(32.66, -28.8) * mm});
            skLineSegment(sketch, "E6327", {"start": v(32.66, -28.8) * mm, "end": v(31.4, -28.2) * mm});
            skLineSegment(sketch, "E6328", {"start": v(31.4, -28.2) * mm, "end": v(30.77, -27.9) * mm});
            skLineSegment(sketch, "E6329", {"start": v(30.77, -27.9) * mm, "end": v(30.15, -27.58) * mm});
            skLineSegment(sketch, "E6330", {"start": v(30.15, -27.58) * mm, "end": v(29.57, -27.26) * mm});
            skLineSegment(sketch, "E6331", {"start": v(29.57, -27.26) * mm, "end": v(29.3, -27.1) * mm});
            skLineSegment(sketch, "E6332", {"start": v(29.3, -27.1) * mm, "end": v(29.04, -26.92) * mm});
            skLineSegment(sketch, "E6333", {"start": v(29.04, -26.92) * mm, "end": v(28.7, -26.68) * mm});
            skLineSegment(sketch, "E6334", {"start": v(28.7, -26.68) * mm, "end": v(28.34, -26.4) * mm});
            skLineSegment(sketch, "E6335", {"start": v(28.34, -26.4) * mm, "end": v(27.99, -26.1) * mm});
            skLineSegment(sketch, "E6336", {"start": v(27.99, -26.1) * mm, "end": v(27.63, -25.78) * mm});
            skLineSegment(sketch, "E6337", {"start": v(27.63, -25.78) * mm, "end": v(26.93, -25.13) * mm});
            skLineSegment(sketch, "E6338", {"start": v(26.93, -25.13) * mm, "end": v(26.6, -24.83) * mm});
            skLineSegment(sketch, "E6339", {"start": v(26.6, -24.83) * mm, "end": v(26.28, -24.55) * mm});
            skLineSegment(sketch, "E6340", {"start": v(26.28, -24.55) * mm, "end": v(26.32, -24.9) * mm});
            skLineSegment(sketch, "E6341", {"start": v(26.32, -24.9) * mm, "end": v(26.36, -25.28) * mm});
            skLineSegment(sketch, "E6342", {"start": v(26.36, -25.28) * mm, "end": v(26.42, -26.08) * mm});
            skLineSegment(sketch, "E6343", {"start": v(26.42, -26.08) * mm, "end": v(26.46, -26.48) * mm});
            skLineSegment(sketch, "E6344", {"start": v(26.46, -26.48) * mm, "end": v(26.52, -26.87) * mm});
            skLineSegment(sketch, "E6345", {"start": v(26.52, -26.87) * mm, "end": v(26.56, -27.05) * mm});
            skLineSegment(sketch, "E6346", {"start": v(26.56, -27.05) * mm, "end": v(26.61, -27.23) * mm});
            skLineSegment(sketch, "E6347", {"start": v(26.61, -27.23) * mm, "end": v(26.67, -27.4) * mm});
            skLineSegment(sketch, "E6348", {"start": v(26.67, -27.4) * mm, "end": v(26.73, -27.57) * mm});
            skLineSegment(sketch, "E6349", {"start": v(26.73, -27.57) * mm, "end": v(26.79, -27.67) * mm});
            skLineSegment(sketch, "E6350", {"start": v(26.79, -27.67) * mm, "end": v(26.86, -27.78) * mm});
            skLineSegment(sketch, "E6351", {"start": v(26.86, -27.78) * mm, "end": v(27.02, -27.99) * mm});
            skLineSegment(sketch, "E6352", {"start": v(27.02, -27.99) * mm, "end": v(27.2, -28.18) * mm});
            skLineSegment(sketch, "E6353", {"start": v(27.2, -28.18) * mm, "end": v(27.4, -28.34) * mm});
            skLineSegment(sketch, "E6354", {"start": v(21.44, -12.55) * mm, "end": v(20.44, -11.65) * mm});
            skLineSegment(sketch, "E6355", {"start": v(20.44, -11.65) * mm, "end": v(20.24, -11.47) * mm});
            skLineSegment(sketch, "E6356", {"start": v(20.24, -11.47) * mm, "end": v(20.04, -11.3) * mm});
            skLineSegment(sketch, "E6357", {"start": v(20.04, -11.3) * mm, "end": v(19.85, -11.16) * mm});
            skLineSegment(sketch, "E6358", {"start": v(19.85, -11.16) * mm, "end": v(19.67, -11.04) * mm});
            skLineSegment(sketch, "E6359", {"start": v(19.67, -11.04) * mm, "end": v(19.5, -10.93) * mm});
            skLineSegment(sketch, "E6360", {"start": v(19.5, -10.93) * mm, "end": v(19.35, -10.85) * mm});
            skLineSegment(sketch, "E6361", {"start": v(19.35, -10.85) * mm, "end": v(19.2, -10.78) * mm});
            skLineSegment(sketch, "E6362", {"start": v(19.2, -10.78) * mm, "end": v(19.08, -10.74) * mm});
            skLineSegment(sketch, "E6363", {"start": v(19.08, -10.74) * mm, "end": v(18.92, -10.68) * mm});
            skLineSegment(sketch, "E6364", {"start": v(18.92, -10.68) * mm, "end": v(18.71, -10.58) * mm});
            skLineSegment(sketch, "E6365", {"start": v(18.71, -10.58) * mm, "end": v(18.47, -10.44) * mm});
            skLineSegment(sketch, "E6366", {"start": v(18.47, -10.44) * mm, "end": v(18.21, -10.26) * mm});
            skLineSegment(sketch, "E6367", {"start": v(18.21, -10.26) * mm, "end": v(15.58, -8.91) * mm});
            skLineSegment(sketch, "E6368", {"start": v(15.58, -8.91) * mm, "end": v(15.14, -8.7) * mm});
            skLineSegment(sketch, "E6369", {"start": v(15.14, -8.7) * mm, "end": v(14.68, -8.46) * mm});
            skLineSegment(sketch, "E6370", {"start": v(14.68, -8.46) * mm, "end": v(14.44, -8.34) * mm});
            skLineSegment(sketch, "E6371", {"start": v(14.44, -8.34) * mm, "end": v(14.2, -8.24) * mm});
            skLineSegment(sketch, "E6372", {"start": v(14.2, -8.24) * mm, "end": v(13.97, -8.15) * mm});
            skLineSegment(sketch, "E6373", {"start": v(13.97, -8.15) * mm, "end": v(13.75, -8.07) * mm});
            skLineSegment(sketch, "E6374", {"start": v(13.75, -8.07) * mm, "end": v(13.36, -7.98) * mm});
            skLineSegment(sketch, "E6375", {"start": v(13.36, -7.98) * mm, "end": v(12.93, -7.9) * mm});
            skLineSegment(sketch, "E6376", {"start": v(12.93, -7.9) * mm, "end": v(12.48, -7.83) * mm});
            skLineSegment(sketch, "E6377", {"start": v(12.48, -7.83) * mm, "end": v(12.02, -7.8) * mm});
            skLineSegment(sketch, "E6378", {"start": v(12.02, -7.8) * mm, "end": v(11.8, -7.79) * mm});
            skLineSegment(sketch, "E6379", {"start": v(11.8, -7.79) * mm, "end": v(11.57, -7.79) * mm});
            skLineSegment(sketch, "E6380", {"start": v(11.57, -7.79) * mm, "end": v(11.34, -7.8) * mm});
            skLineSegment(sketch, "E6381", {"start": v(11.34, -7.8) * mm, "end": v(11.12, -7.82) * mm});
            skLineSegment(sketch, "E6382", {"start": v(11.12, -7.82) * mm, "end": v(10.9, -7.84) * mm});
            skLineSegment(sketch, "E6383", {"start": v(10.9, -7.84) * mm, "end": v(10.7, -7.88) * mm});
            skLineSegment(sketch, "E6384", {"start": v(10.7, -7.88) * mm, "end": v(10.5, -7.93) * mm});
            skLineSegment(sketch, "E6385", {"start": v(10.5, -7.93) * mm, "end": v(10.32, -7.99) * mm});
            skLineSegment(sketch, "E6386", {"start": v(10.32, -7.99) * mm, "end": v(10.06, -8.1) * mm});
            skLineSegment(sketch, "E6387", {"start": v(10.06, -8.1) * mm, "end": v(9.8, -8.22) * mm});
            skLineSegment(sketch, "E6388", {"start": v(9.8, -8.22) * mm, "end": v(9.55, -8.37) * mm});
            skLineSegment(sketch, "E6389", {"start": v(9.55, -8.37) * mm, "end": v(9.3, -8.53) * mm});
            skLineSegment(sketch, "E6390", {"start": v(9.3, -8.53) * mm, "end": v(9.07, -8.72) * mm});
            skLineSegment(sketch, "E6391", {"start": v(9.07, -8.72) * mm, "end": v(8.84, -8.92) * mm});
            skLineSegment(sketch, "E6392", {"start": v(8.84, -8.92) * mm, "end": v(8.62, -9.13) * mm});
            skLineSegment(sketch, "E6393", {"start": v(8.62, -9.13) * mm, "end": v(8.4, -9.35) * mm});
            skLineSegment(sketch, "E6394", {"start": v(8.4, -9.35) * mm, "end": v(8.2, -9.58) * mm});
            skLineSegment(sketch, "E6395", {"start": v(8.2, -9.58) * mm, "end": v(7.99, -9.81) * mm});
            skLineSegment(sketch, "E6396", {"start": v(7.99, -9.81) * mm, "end": v(7.6, -10.3) * mm});
            skLineSegment(sketch, "E6397", {"start": v(7.6, -10.3) * mm, "end": v(7.23, -10.78) * mm});
            skLineSegment(sketch, "E6398", {"start": v(7.23, -10.78) * mm, "end": v(6.9, -11.25) * mm});
            skLineSegment(sketch, "E6399", {"start": v(6.9, -11.25) * mm, "end": v(6.68, -11.58) * mm});
            skLineSegment(sketch, "E6400", {"start": v(6.68, -11.58) * mm, "end": v(6.45, -11.95) * mm});
            skLineSegment(sketch, "E6401", {"start": v(6.45, -11.95) * mm, "end": v(6.23, -12.33) * mm});
            skLineSegment(sketch, "E6402", {"start": v(6.23, -12.33) * mm, "end": v(6.02, -12.74) * mm});
            skLineSegment(sketch, "E6403", {"start": v(6.02, -12.74) * mm, "end": v(5.83, -13.14) * mm});
            skLineSegment(sketch, "E6404", {"start": v(5.83, -13.14) * mm, "end": v(5.66, -13.55) * mm});
            skLineSegment(sketch, "E6405", {"start": v(5.66, -13.55) * mm, "end": v(5.51, -13.95) * mm});
            skLineSegment(sketch, "E6406", {"start": v(5.51, -13.95) * mm, "end": v(5.4, -14.34) * mm});
            skLineSegment(sketch, "E6407", {"start": v(5.4, -14.34) * mm, "end": v(5.32, -14.74) * mm});
            skLineSegment(sketch, "E6408", {"start": v(5.32, -14.74) * mm, "end": v(5.27, -15.17) * mm});
            skLineSegment(sketch, "E6409", {"start": v(5.27, -15.17) * mm, "end": v(5.23, -15.62) * mm});
            skLineSegment(sketch, "E6410", {"start": v(5.23, -15.62) * mm, "end": v(5.21, -16.08) * mm});
            skLineSegment(sketch, "E6411", {"start": v(5.21, -16.08) * mm, "end": v(5.21, -16.54) * mm});
            skLineSegment(sketch, "E6412", {"start": v(5.21, -16.54) * mm, "end": v(5.23, -17) * mm});
            skLineSegment(sketch, "E6413", {"start": v(5.23, -17) * mm, "end": v(5.26, -17.43) * mm});
            skLineSegment(sketch, "E6414", {"start": v(5.26, -17.43) * mm, "end": v(5.3, -17.84) * mm});
            skLineSegment(sketch, "E6415", {"start": v(5.3, -17.84) * mm, "end": v(5.34, -18.07) * mm});
            skLineSegment(sketch, "E6416", {"start": v(5.34, -18.07) * mm, "end": v(5.38, -18.3) * mm});
            skLineSegment(sketch, "E6417", {"start": v(5.38, -18.3) * mm, "end": v(5.5, -18.8) * mm});
            skLineSegment(sketch, "E6418", {"start": v(5.5, -18.8) * mm, "end": v(5.64, -19.3) * mm});
            skLineSegment(sketch, "E6419", {"start": v(5.64, -19.3) * mm, "end": v(5.81, -19.8) * mm});
            skLineSegment(sketch, "E6420", {"start": v(5.81, -19.8) * mm, "end": v(6, -20.3) * mm});
            skLineSegment(sketch, "E6421", {"start": v(6, -20.3) * mm, "end": v(6.22, -20.77) * mm});
            skLineSegment(sketch, "E6422", {"start": v(6.22, -20.77) * mm, "end": v(6.44, -21.23) * mm});
            skLineSegment(sketch, "E6423", {"start": v(6.44, -21.23) * mm, "end": v(6.66, -21.64) * mm});
            skLineSegment(sketch, "E6424", {"start": v(6.66, -21.64) * mm, "end": v(6.81, -21.9) * mm});
            skLineSegment(sketch, "E6425", {"start": v(6.81, -21.9) * mm, "end": v(6.97, -22.18) * mm});
            skLineSegment(sketch, "E6426", {"start": v(6.97, -22.18) * mm, "end": v(7.13, -22.45) * mm});
            skLineSegment(sketch, "E6427", {"start": v(7.13, -22.45) * mm, "end": v(7.22, -22.57) * mm});
            skLineSegment(sketch, "E6428", {"start": v(7.22, -22.57) * mm, "end": v(7.32, -22.68) * mm});
            skLineSegment(sketch, "E6429", {"start": v(7.32, -22.68) * mm, "end": v(7.68, -23.04) * mm});
            skLineSegment(sketch, "E6430", {"start": v(7.68, -23.04) * mm, "end": v(8, -23.34) * mm});
            skLineSegment(sketch, "E6431", {"start": v(8, -23.34) * mm, "end": v(8.14, -23.45) * mm});
            skLineSegment(sketch, "E6432", {"start": v(8.14, -23.45) * mm, "end": v(8.26, -23.54) * mm});
            skLineSegment(sketch, "E6433", {"start": v(8.26, -23.54) * mm, "end": v(8.35, -23.59) * mm});
            skLineSegment(sketch, "E6434", {"start": v(8.35, -23.59) * mm, "end": v(8.4, -23.6) * mm});
            skLineSegment(sketch, "E6435", {"start": v(8.4, -23.6) * mm, "end": v(8.43, -23.6) * mm});
            skLineSegment(sketch, "E6436", {"start": v(8.43, -23.6) * mm, "end": v(8.45, -23.54) * mm});
            skLineSegment(sketch, "E6437", {"start": v(8.45, -23.54) * mm, "end": v(8.51, -23.36) * mm});
            skLineSegment(sketch, "E6438", {"start": v(8.51, -23.36) * mm, "end": v(8.7, -22.7) * mm});
            skLineSegment(sketch, "E6439", {"start": v(8.7, -22.7) * mm, "end": v(8.84, -22.25) * mm});
            skLineSegment(sketch, "E6440", {"start": v(8.84, -22.25) * mm, "end": v(9, -21.76) * mm});
            skLineSegment(sketch, "E6441", {"start": v(9, -21.76) * mm, "end": v(9.2, -21.24) * mm});
            skLineSegment(sketch, "E6442", {"start": v(9.2, -21.24) * mm, "end": v(9.32, -20.97) * mm});
            skLineSegment(sketch, "E6443", {"start": v(9.32, -20.97) * mm, "end": v(9.45, -20.7) * mm});
            skLineSegment(sketch, "E6444", {"start": v(9.45, -20.7) * mm, "end": v(9.88, -19.8) * mm});
            skLineSegment(sketch, "E6445", {"start": v(9.88, -19.8) * mm, "end": v(10.11, -19.33) * mm});
            skLineSegment(sketch, "E6446", {"start": v(10.11, -19.33) * mm, "end": v(10.35, -18.9) * mm});
            skLineSegment(sketch, "E6447", {"start": v(10.35, -18.9) * mm, "end": v(10.55, -18.56) * mm});
            skLineSegment(sketch, "E6448", {"start": v(10.55, -18.56) * mm, "end": v(10.78, -18.24) * mm});
            skLineSegment(sketch, "E6449", {"start": v(10.78, -18.24) * mm, "end": v(11, -17.94) * mm});
            skLineSegment(sketch, "E6450", {"start": v(11, -17.94) * mm, "end": v(11.23, -17.66) * mm});
            skLineSegment(sketch, "E6451", {"start": v(11.23, -17.66) * mm, "end": v(11.66, -17.17) * mm});
            skLineSegment(sketch, "E6452", {"start": v(11.66, -17.17) * mm, "end": v(11.84, -16.96) * mm});
            skLineSegment(sketch, "E6453", {"start": v(11.84, -16.96) * mm, "end": v(11.98, -16.77) * mm});
            skLineSegment(sketch, "E6454", {"start": v(11.98, -16.77) * mm, "end": v(12.22, -16.45) * mm});
            skLineSegment(sketch, "E6455", {"start": v(12.22, -16.45) * mm, "end": v(12.35, -16.28) * mm});
            skLineSegment(sketch, "E6456", {"start": v(12.35, -16.28) * mm, "end": v(12.48, -16.11) * mm});
            skLineSegment(sketch, "E6457", {"start": v(12.48, -16.11) * mm, "end": v(12.63, -15.96) * mm});
            skLineSegment(sketch, "E6458", {"start": v(12.63, -15.96) * mm, "end": v(12.78, -15.82) * mm});
            skLineSegment(sketch, "E6459", {"start": v(12.78, -15.82) * mm, "end": v(12.94, -15.7) * mm});
            skLineSegment(sketch, "E6460", {"start": v(12.94, -15.7) * mm, "end": v(13.1, -15.6) * mm});
            skLineSegment(sketch, "E6461", {"start": v(13.1, -15.6) * mm, "end": v(13.32, -15.52) * mm});
            skLineSegment(sketch, "E6462", {"start": v(13.32, -15.52) * mm, "end": v(13.55, -15.46) * mm});
            skLineSegment(sketch, "E6463", {"start": v(13.55, -15.46) * mm, "end": v(13.79, -15.42) * mm});
            skLineSegment(sketch, "E6464", {"start": v(13.79, -15.42) * mm, "end": v(14.04, -15.4) * mm});
            skLineSegment(sketch, "E6465", {"start": v(14.04, -15.4) * mm, "end": v(14.3, -15.4) * mm});
            skLineSegment(sketch, "E6466", {"start": v(14.3, -15.4) * mm, "end": v(14.56, -15.41) * mm});
            skLineSegment(sketch, "E6467", {"start": v(14.56, -15.41) * mm, "end": v(14.83, -15.44) * mm});
            skLineSegment(sketch, "E6468", {"start": v(14.83, -15.44) * mm, "end": v(15.1, -15.47) * mm});
            skLineSegment(sketch, "E6469", {"start": v(15.1, -15.47) * mm, "end": v(15.65, -15.57) * mm});
            skLineSegment(sketch, "E6470", {"start": v(15.65, -15.57) * mm, "end": v(16.19, -15.7) * mm});
            skLineSegment(sketch, "E6471", {"start": v(16.19, -15.7) * mm, "end": v(17.16, -15.95) * mm});
            skLineSegment(sketch, "E6472", {"start": v(17.16, -15.95) * mm, "end": v(17.42, -16.02) * mm});
            skLineSegment(sketch, "E6473", {"start": v(17.42, -16.02) * mm, "end": v(17.7, -16.12) * mm});
            skLineSegment(sketch, "E6474", {"start": v(17.7, -16.12) * mm, "end": v(17.97, -16.24) * mm});
            skLineSegment(sketch, "E6475", {"start": v(17.97, -16.24) * mm, "end": v(18.25, -16.37) * mm});
            skLineSegment(sketch, "E6476", {"start": v(18.25, -16.37) * mm, "end": v(18.8, -16.63) * mm});
            skLineSegment(sketch, "E6477", {"start": v(18.8, -16.63) * mm, "end": v(19.3, -16.87) * mm});
            skLineSegment(sketch, "E6478", {"start": v(19.3, -16.87) * mm, "end": v(20.24, -17.3) * mm});
            skLineSegment(sketch, "E6479", {"start": v(20.24, -17.3) * mm, "end": v(21.18, -17.75) * mm});
            skLineSegment(sketch, "E6480", {"start": v(21.18, -17.75) * mm, "end": v(22.04, -18.2) * mm});
            skLineSegment(sketch, "E6481", {"start": v(22.04, -18.2) * mm, "end": v(22.4, -18.39) * mm});
            skLineSegment(sketch, "E6482", {"start": v(22.4, -18.39) * mm, "end": v(22.68, -18.56) * mm});
            skLineSegment(sketch, "E6483", {"start": v(22.68, -18.56) * mm, "end": v(23.19, -18.87) * mm});
            skLineSegment(sketch, "E6484", {"start": v(23.19, -18.87) * mm, "end": v(23.57, -19.09) * mm});
            skLineSegment(sketch, "E6485", {"start": v(23.57, -19.09) * mm, "end": v(23.72, -19.16) * mm});
            skLineSegment(sketch, "E6486", {"start": v(23.72, -19.16) * mm, "end": v(23.85, -19.22) * mm});
            skLineSegment(sketch, "E6487", {"start": v(23.85, -19.22) * mm, "end": v(23.96, -19.25) * mm});
            skLineSegment(sketch, "E6488", {"start": v(23.96, -19.25) * mm, "end": v(24.04, -19.26) * mm});
            skLineSegment(sketch, "E6489", {"start": v(24.04, -19.26) * mm, "end": v(24.1, -19.25) * mm});
            skLineSegment(sketch, "E6490", {"start": v(24.1, -19.25) * mm, "end": v(24.16, -19.21) * mm});
            skLineSegment(sketch, "E6491", {"start": v(24.16, -19.21) * mm, "end": v(24.2, -19.16) * mm});
            skLineSegment(sketch, "E6492", {"start": v(24.2, -19.16) * mm, "end": v(24.23, -19.08) * mm});
            skLineSegment(sketch, "E6493", {"start": v(24.23, -19.08) * mm, "end": v(24.24, -18.98) * mm});
            skLineSegment(sketch, "E6494", {"start": v(24.24, -18.98) * mm, "end": v(24.25, -18.85) * mm});
            skLineSegment(sketch, "E6495", {"start": v(24.25, -18.85) * mm, "end": v(24.26, -18.53) * mm});
            skLineSegment(sketch, "E6496", {"start": v(24.26, -18.53) * mm, "end": v(24.26, -17.75) * mm});
            skLineSegment(sketch, "E6497", {"start": v(24.26, -17.75) * mm, "end": v(22.07, -13.4) * mm});
            skLineSegment(sketch, "E6498", {"start": v(22.07, -13.4) * mm, "end": v(21.44, -12.55) * mm});
            skLineSegment(sketch, "E6499", {"start": v(22.87, -14.06) * mm, "end": v(23.87, -15.68) * mm});
            skLineSegment(sketch, "E6500", {"start": v(23.87, -15.68) * mm, "end": v(25.04, -16.28) * mm});
            skLineSegment(sketch, "E6501", {"start": v(25.04, -16.28) * mm, "end": v(26.07, -14.4) * mm});
            skLineSegment(sketch, "E6502", {"start": v(26.07, -14.4) * mm, "end": v(28.26, -13.03) * mm});
            skLineSegment(sketch, "E6503", {"start": v(28.26, -13.03) * mm, "end": v(28.04, -11.9) * mm});
            skLineSegment(sketch, "E6504", {"start": v(28.04, -11.9) * mm, "end": v(26.5, -12.14) * mm});
            skLineSegment(sketch, "E6505", {"start": v(26.5, -12.14) * mm, "end": v(25.83, -12.06) * mm});
            skLineSegment(sketch, "E6506", {"start": v(25.83, -12.06) * mm, "end": v(25.18, -11.97) * mm});
            skLineSegment(sketch, "E6507", {"start": v(25.18, -11.97) * mm, "end": v(24.87, -11.92) * mm});
            skLineSegment(sketch, "E6508", {"start": v(24.87, -11.92) * mm, "end": v(24.57, -11.86) * mm});
            skLineSegment(sketch, "E6509", {"start": v(24.57, -11.86) * mm, "end": v(24.3, -11.78) * mm});
            skLineSegment(sketch, "E6510", {"start": v(24.3, -11.78) * mm, "end": v(24.18, -11.73) * mm});
            skLineSegment(sketch, "E6511", {"start": v(24.18, -11.73) * mm, "end": v(24.07, -11.68) * mm});
            skLineSegment(sketch, "E6512", {"start": v(24.07, -11.68) * mm, "end": v(22.55, -11.07) * mm});
            skLineSegment(sketch, "E6513", {"start": v(22.55, -11.07) * mm, "end": v(21.06, -11.26) * mm});
            skLineSegment(sketch, "E6514", {"start": v(21.06, -11.26) * mm, "end": v(21.52, -11.98) * mm});
            skLineSegment(sketch, "E6515", {"start": v(21.52, -11.98) * mm, "end": v(22.43, -12.98) * mm});
            skLineSegment(sketch, "E6516", {"start": v(22.43, -12.98) * mm, "end": v(22.87, -14.06) * mm});
            skLineSegment(sketch, "E6517", {"start": v(-26.78, -33.68) * mm, "end": v(-26.86, -32.93) * mm});
            skLineSegment(sketch, "E6518", {"start": v(-26.86, -32.93) * mm, "end": v(-27.12, -32.54) * mm});
            skLineSegment(sketch, "E6519", {"start": v(-27.12, -32.54) * mm, "end": v(-27.33, -32.24) * mm});
            skLineSegment(sketch, "E6520", {"start": v(-27.33, -32.24) * mm, "end": v(-27.43, -32.12) * mm});
            skLineSegment(sketch, "E6521", {"start": v(-27.43, -32.12) * mm, "end": v(-27.52, -32.03) * mm});
            skLineSegment(sketch, "E6522", {"start": v(-27.52, -32.03) * mm, "end": v(-27.62, -31.96) * mm});
            skLineSegment(sketch, "E6523", {"start": v(-27.62, -31.96) * mm, "end": v(-27.7, -31.9) * mm});
            skLineSegment(sketch, "E6524", {"start": v(-27.7, -31.9) * mm, "end": v(-27.8, -31.87) * mm});
            skLineSegment(sketch, "E6525", {"start": v(-27.8, -31.87) * mm, "end": v(-27.9, -31.85) * mm});
            skLineSegment(sketch, "E6526", {"start": v(-27.9, -31.85) * mm, "end": v(-28, -31.84) * mm});
            skLineSegment(sketch, "E6527", {"start": v(-28, -31.84) * mm, "end": v(-28.11, -31.86) * mm});
            skLineSegment(sketch, "E6528", {"start": v(-28.11, -31.86) * mm, "end": v(-28.23, -31.88) * mm});
            skLineSegment(sketch, "E6529", {"start": v(-28.23, -31.88) * mm, "end": v(-28.36, -31.92) * mm});
            skLineSegment(sketch, "E6530", {"start": v(-28.36, -31.92) * mm, "end": v(-28.67, -32.03) * mm});
            skLineSegment(sketch, "E6531", {"start": v(-28.67, -32.03) * mm, "end": v(-29.22, -32.7) * mm});
            skLineSegment(sketch, "E6532", {"start": v(-29.22, -32.7) * mm, "end": v(-30.09, -35.2) * mm});
            skLineSegment(sketch, "E6533", {"start": v(-30.09, -35.2) * mm, "end": v(-29.93, -36) * mm});
            skLineSegment(sketch, "E6534", {"start": v(-29.93, -36) * mm, "end": v(-29.9, -36.18) * mm});
            skLineSegment(sketch, "E6535", {"start": v(-29.9, -36.18) * mm, "end": v(-29.85, -36.33) * mm});
            skLineSegment(sketch, "E6536", {"start": v(-29.85, -36.33) * mm, "end": v(-29.8, -36.46) * mm});
            skLineSegment(sketch, "E6537", {"start": v(-29.8, -36.46) * mm, "end": v(-29.76, -36.56) * mm});
            skLineSegment(sketch, "E6538", {"start": v(-29.76, -36.56) * mm, "end": v(-29.7, -36.65) * mm});
            skLineSegment(sketch, "E6539", {"start": v(-29.7, -36.65) * mm, "end": v(-29.64, -36.71) * mm});
            skLineSegment(sketch, "E6540", {"start": v(-29.64, -36.71) * mm, "end": v(-29.58, -36.76) * mm});
            skLineSegment(sketch, "E6541", {"start": v(-29.58, -36.76) * mm, "end": v(-29.52, -36.78) * mm});
            skLineSegment(sketch, "E6542", {"start": v(-29.52, -36.78) * mm, "end": v(-29.46, -36.78) * mm});
            skLineSegment(sketch, "E6543", {"start": v(-29.46, -36.78) * mm, "end": v(-29.4, -36.76) * mm});
            skLineSegment(sketch, "E6544", {"start": v(-29.4, -36.76) * mm, "end": v(-29.33, -36.71) * mm});
            skLineSegment(sketch, "E6545", {"start": v(-29.33, -36.71) * mm, "end": v(-29.27, -36.64) * mm});
            skLineSegment(sketch, "E6546", {"start": v(-29.27, -36.64) * mm, "end": v(-29.2, -36.56) * mm});
            skLineSegment(sketch, "E6547", {"start": v(-29.2, -36.56) * mm, "end": v(-29.15, -36.44) * mm});
            skLineSegment(sketch, "E6548", {"start": v(-29.15, -36.44) * mm, "end": v(-29.1, -36.31) * mm});
            skLineSegment(sketch, "E6549", {"start": v(-29.1, -36.31) * mm, "end": v(-29.04, -36.16) * mm});
            skLineSegment(sketch, "E6550", {"start": v(-29.04, -36.16) * mm, "end": v(-28.98, -36.01) * mm});
            skLineSegment(sketch, "E6551", {"start": v(-28.98, -36.01) * mm, "end": v(-28.89, -35.85) * mm});
            skLineSegment(sketch, "E6552", {"start": v(-28.89, -35.85) * mm, "end": v(-28.77, -35.67) * mm});
            skLineSegment(sketch, "E6553", {"start": v(-28.77, -35.67) * mm, "end": v(-28.63, -35.5) * mm});
            skLineSegment(sketch, "E6554", {"start": v(-28.63, -35.5) * mm, "end": v(-28.48, -35.31) * mm});
            skLineSegment(sketch, "E6555", {"start": v(-28.48, -35.31) * mm, "end": v(-28.31, -35.14) * mm});
            skLineSegment(sketch, "E6556", {"start": v(-28.31, -35.14) * mm, "end": v(-28.14, -34.97) * mm});
            skLineSegment(sketch, "E6557", {"start": v(-28.14, -34.97) * mm, "end": v(-27.96, -34.82) * mm});
            skLineSegment(sketch, "E6558", {"start": v(-27.96, -34.82) * mm, "end": v(-27.08, -34.13) * mm});
            skLineSegment(sketch, "E6559", {"start": v(-27.08, -34.13) * mm, "end": v(-26.78, -33.68) * mm});
            skLineSegment(sketch, "E6560", {"start": v(-22.75, -36.15) * mm, "end": v(-23.48, -35.95) * mm});
            skLineSegment(sketch, "E6561", {"start": v(-23.48, -35.95) * mm, "end": v(-24.18, -36.15) * mm});
            skLineSegment(sketch, "E6562", {"start": v(-24.18, -36.15) * mm, "end": v(-24.55, -37.19) * mm});
            skLineSegment(sketch, "E6563", {"start": v(-24.55, -37.19) * mm, "end": v(-24.62, -37.41) * mm});
            skLineSegment(sketch, "E6564", {"start": v(-24.62, -37.41) * mm, "end": v(-24.69, -37.66) * mm});
            skLineSegment(sketch, "E6565", {"start": v(-24.69, -37.66) * mm, "end": v(-24.75, -37.93) * mm});
            skLineSegment(sketch, "E6566", {"start": v(-24.75, -37.93) * mm, "end": v(-24.8, -38.2) * mm});
            skLineSegment(sketch, "E6567", {"start": v(-24.8, -38.2) * mm, "end": v(-24.85, -38.46) * mm});
            skLineSegment(sketch, "E6568", {"start": v(-24.85, -38.46) * mm, "end": v(-24.88, -38.72) * mm});
            skLineSegment(sketch, "E6569", {"start": v(-24.88, -38.72) * mm, "end": v(-24.9, -38.96) * mm});
            skLineSegment(sketch, "E6570", {"start": v(-24.9, -38.96) * mm, "end": v(-24.9, -39.17) * mm});
            skLineSegment(sketch, "E6571", {"start": v(-24.9, -39.17) * mm, "end": v(-24.9, -40.1) * mm});
            skLineSegment(sketch, "E6572", {"start": v(-24.9, -40.1) * mm, "end": v(-24.63, -40.1) * mm});
            skLineSegment(sketch, "E6573", {"start": v(-24.63, -40.1) * mm, "end": v(-24.56, -40.1) * mm});
            skLineSegment(sketch, "E6574", {"start": v(-24.56, -40.1) * mm, "end": v(-24.48, -40.06) * mm});
            skLineSegment(sketch, "E6575", {"start": v(-24.48, -40.06) * mm, "end": v(-24.38, -40) * mm});
            skLineSegment(sketch, "E6576", {"start": v(-24.38, -40) * mm, "end": v(-24.27, -39.92) * mm});
            skLineSegment(sketch, "E6577", {"start": v(-24.27, -39.92) * mm, "end": v(-24.15, -39.83) * mm});
            skLineSegment(sketch, "E6578", {"start": v(-24.15, -39.83) * mm, "end": v(-24.02, -39.72) * mm});
            skLineSegment(sketch, "E6579", {"start": v(-24.02, -39.72) * mm, "end": v(-23.9, -39.6) * mm});
            skLineSegment(sketch, "E6580", {"start": v(-23.9, -39.6) * mm, "end": v(-23.78, -39.48) * mm});
            skLineSegment(sketch, "E6581", {"start": v(-23.78, -39.48) * mm, "end": v(-23.65, -39.34) * mm});
            skLineSegment(sketch, "E6582", {"start": v(-23.65, -39.34) * mm, "end": v(-23.48, -39.2) * mm});
            skLineSegment(sketch, "E6583", {"start": v(-23.48, -39.2) * mm, "end": v(-23.3, -39.06) * mm});
            skLineSegment(sketch, "E6584", {"start": v(-23.3, -39.06) * mm, "end": v(-23.1, -38.91) * mm});
            skLineSegment(sketch, "E6585", {"start": v(-23.1, -38.91) * mm, "end": v(-22.88, -38.78) * mm});
            skLineSegment(sketch, "E6586", {"start": v(-22.88, -38.78) * mm, "end": v(-22.67, -38.65) * mm});
            skLineSegment(sketch, "E6587", {"start": v(-22.67, -38.65) * mm, "end": v(-22.45, -38.54) * mm});
            skLineSegment(sketch, "E6588", {"start": v(-22.45, -38.54) * mm, "end": v(-22.25, -38.45) * mm});
            skLineSegment(sketch, "E6589", {"start": v(-22.25, -38.45) * mm, "end": v(-22.05, -38.36) * mm});
            skLineSegment(sketch, "E6590", {"start": v(-22.05, -38.36) * mm, "end": v(-21.87, -38.27) * mm});
            skLineSegment(sketch, "E6591", {"start": v(-21.87, -38.27) * mm, "end": v(-21.7, -38.18) * mm});
            skLineSegment(sketch, "E6592", {"start": v(-21.7, -38.18) * mm, "end": v(-21.56, -38.09) * mm});
            skLineSegment(sketch, "E6593", {"start": v(-21.56, -38.09) * mm, "end": v(-21.44, -38) * mm});
            skLineSegment(sketch, "E6594", {"start": v(-21.44, -38) * mm, "end": v(-21.36, -37.92) * mm});
            skLineSegment(sketch, "E6595", {"start": v(-21.36, -37.92) * mm, "end": v(-21.3, -37.85) * mm});
            skLineSegment(sketch, "E6596", {"start": v(-21.3, -37.85) * mm, "end": v(-21.28, -37.82) * mm});
            skLineSegment(sketch, "E6597", {"start": v(-21.28, -37.82) * mm, "end": v(-21.28, -37.79) * mm});
            skLineSegment(sketch, "E6598", {"start": v(-21.28, -37.79) * mm, "end": v(-21.28, -37.53) * mm});
            skLineSegment(sketch, "E6599", {"start": v(-21.28, -37.53) * mm, "end": v(-21.97, -36.72) * mm});
            skLineSegment(sketch, "E6600", {"start": v(-21.97, -36.72) * mm, "end": v(-22.75, -36.15) * mm});
            skLineSegment(sketch, "E6601", {"start": v(-11.6, -38.95) * mm, "end": v(-11.34, -41.1) * mm});
            skLineSegment(sketch, "E6602", {"start": v(-11.34, -41.1) * mm, "end": v(-11.07, -41.1) * mm});
            skLineSegment(sketch, "E6603", {"start": v(-11.07, -41.1) * mm, "end": v(-11.04, -41.1) * mm});
            skLineSegment(sketch, "E6604", {"start": v(-11.04, -41.1) * mm, "end": v(-11, -41.07) * mm});
            skLineSegment(sketch, "E6605", {"start": v(-11, -41.07) * mm, "end": v(-10.92, -41) * mm});
            skLineSegment(sketch, "E6606", {"start": v(-10.92, -41) * mm, "end": v(-10.82, -40.9) * mm});
            skLineSegment(sketch, "E6607", {"start": v(-10.82, -40.9) * mm, "end": v(-10.72, -40.77) * mm});
            skLineSegment(sketch, "E6608", {"start": v(-10.72, -40.77) * mm, "end": v(-10.6, -40.6) * mm});
            skLineSegment(sketch, "E6609", {"start": v(-10.6, -40.6) * mm, "end": v(-10.5, -40.41) * mm});
            skLineSegment(sketch, "E6610", {"start": v(-10.5, -40.41) * mm, "end": v(-10.38, -40.2) * mm});
            skLineSegment(sketch, "E6611", {"start": v(-10.38, -40.2) * mm, "end": v(-10.26, -39.97) * mm});
            skLineSegment(sketch, "E6612", {"start": v(-10.26, -39.97) * mm, "end": v(-9.73, -38.85) * mm});
            skLineSegment(sketch, "E6613", {"start": v(-9.73, -38.85) * mm, "end": v(-9.73, -36.59) * mm});
            skLineSegment(sketch, "E6614", {"start": v(-9.73, -36.59) * mm, "end": v(-10.5, -35.98) * mm});
            skLineSegment(sketch, "E6615", {"start": v(-10.5, -35.98) * mm, "end": v(-11.4, -35.7) * mm});
            skLineSegment(sketch, "E6616", {"start": v(-11.4, -35.7) * mm, "end": v(-12.16, -36.03) * mm});
            skLineSegment(sketch, "E6617", {"start": v(-12.16, -36.03) * mm, "end": v(-12.86, -37.16) * mm});
            skLineSegment(sketch, "E6618", {"start": v(-12.86, -37.16) * mm, "end": v(-11.6, -38.95) * mm});
            skLineSegment(sketch, "E6619", {"start": v(-12.77, -43.24) * mm, "end": v(-12.22, -46.38) * mm});
            skLineSegment(sketch, "E6620", {"start": v(-12.22, -46.38) * mm, "end": v(-12.1, -47.05) * mm});
            skLineSegment(sketch, "E6621", {"start": v(-12.1, -47.05) * mm, "end": v(-11.95, -47.73) * mm});
            skLineSegment(sketch, "E6622", {"start": v(-11.95, -47.73) * mm, "end": v(-11.8, -48.4) * mm});
            skLineSegment(sketch, "E6623", {"start": v(-11.8, -48.4) * mm, "end": v(-11.64, -49.09) * mm});
            skLineSegment(sketch, "E6624", {"start": v(-11.64, -49.09) * mm, "end": v(-11.47, -49.76) * mm});
            skLineSegment(sketch, "E6625", {"start": v(-11.47, -49.76) * mm, "end": v(-11.3, -50.42) * mm});
            skLineSegment(sketch, "E6626", {"start": v(-11.3, -50.42) * mm, "end": v(-11.1, -51.07) * mm});
            skLineSegment(sketch, "E6627", {"start": v(-11.1, -51.07) * mm, "end": v(-10.92, -51.7) * mm});
            skLineSegment(sketch, "E6628", {"start": v(-10.92, -51.7) * mm, "end": v(-10.72, -52.32) * mm});
            skLineSegment(sketch, "E6629", {"start": v(-10.72, -52.32) * mm, "end": v(-10.52, -52.91) * mm});
            skLineSegment(sketch, "E6630", {"start": v(-10.52, -52.91) * mm, "end": v(-10.32, -53.48) * mm});
            skLineSegment(sketch, "E6631", {"start": v(-10.32, -53.48) * mm, "end": v(-10.1, -54.01) * mm});
            skLineSegment(sketch, "E6632", {"start": v(-10.1, -54.01) * mm, "end": v(-9.9, -54.51) * mm});
            skLineSegment(sketch, "E6633", {"start": v(-9.9, -54.51) * mm, "end": v(-9.7, -54.97) * mm});
            skLineSegment(sketch, "E6634", {"start": v(-9.7, -54.97) * mm, "end": v(-9.5, -55.4) * mm});
            skLineSegment(sketch, "E6635", {"start": v(-9.5, -55.4) * mm, "end": v(-9.3, -55.77) * mm});
            skLineSegment(sketch, "E6636", {"start": v(-9.3, -55.77) * mm, "end": v(-8.58, -57.04) * mm});
            skLineSegment(sketch, "E6637", {"start": v(-8.58, -57.04) * mm, "end": v(-6.77, -58.38) * mm});
            skLineSegment(sketch, "E6638", {"start": v(-6.77, -58.38) * mm, "end": v(-6.39, -58) * mm});
            skLineSegment(sketch, "E6639", {"start": v(-6.39, -58) * mm, "end": v(-6.9, -56.25) * mm});
            skLineSegment(sketch, "E6640", {"start": v(-6.9, -56.25) * mm, "end": v(-7.15, -55.38) * mm});
            skLineSegment(sketch, "E6641", {"start": v(-7.15, -55.38) * mm, "end": v(-7.3, -54.75) * mm});
            skLineSegment(sketch, "E6642", {"start": v(-7.3, -54.75) * mm, "end": v(-7.36, -54.52) * mm});
            skLineSegment(sketch, "E6643", {"start": v(-7.36, -54.52) * mm, "end": v(-7.38, -54.36) * mm});
            skLineSegment(sketch, "E6644", {"start": v(-7.38, -54.36) * mm, "end": v(-7.4, -54.25) * mm});
            skLineSegment(sketch, "E6645", {"start": v(-7.4, -54.25) * mm, "end": v(-7.39, -54.22) * mm});
            skLineSegment(sketch, "E6646", {"start": v(-7.39, -54.22) * mm, "end": v(-7.38, -54.2) * mm});
            skLineSegment(sketch, "E6647", {"start": v(-7.38, -54.2) * mm, "end": v(-7.36, -54.2) * mm});
            skLineSegment(sketch, "E6648", {"start": v(-7.36, -54.2) * mm, "end": v(-7.34, -54.22) * mm});
            skLineSegment(sketch, "E6649", {"start": v(-7.34, -54.22) * mm, "end": v(-7.3, -54.3) * mm});
            skLineSegment(sketch, "E6650", {"start": v(-7.3, -54.3) * mm, "end": v(-7.22, -54.44) * mm});
            skLineSegment(sketch, "E6651", {"start": v(-7.22, -54.44) * mm, "end": v(-7.13, -54.64) * mm});
            skLineSegment(sketch, "E6652", {"start": v(-7.13, -54.64) * mm, "end": v(-6.9, -55.22) * mm});
            skLineSegment(sketch, "E6653", {"start": v(-6.9, -55.22) * mm, "end": v(-6.6, -56.06) * mm});
            skLineSegment(sketch, "E6654", {"start": v(-6.6, -56.06) * mm, "end": v(-6.28, -56.95) * mm});
            skLineSegment(sketch, "E6655", {"start": v(-6.28, -56.95) * mm, "end": v(-6, -57.7) * mm});
            skLineSegment(sketch, "E6656", {"start": v(-6, -57.7) * mm, "end": v(-5.78, -58.24) * mm});
            skLineSegment(sketch, "E6657", {"start": v(-5.78, -58.24) * mm, "end": v(-5.7, -58.4) * mm});
            skLineSegment(sketch, "E6658", {"start": v(-5.7, -58.4) * mm, "end": v(-5.66, -58.48) * mm});
            skLineSegment(sketch, "E6659", {"start": v(-5.66, -58.48) * mm, "end": v(-5.58, -58.51) * mm});
            skLineSegment(sketch, "E6660", {"start": v(-5.58, -58.51) * mm, "end": v(-5.42, -58.56) * mm});
            skLineSegment(sketch, "E6661", {"start": v(-5.42, -58.56) * mm, "end": v(-5.18, -58.61) * mm});
            skLineSegment(sketch, "E6662", {"start": v(-5.18, -58.61) * mm, "end": v(-4.88, -58.67) * mm});
            skLineSegment(sketch, "E6663", {"start": v(-4.88, -58.67) * mm, "end": v(-4.13, -58.8) * mm});
            skLineSegment(sketch, "E6664", {"start": v(-4.13, -58.8) * mm, "end": v(-3.24, -58.92) * mm});
            skLineSegment(sketch, "E6665", {"start": v(-3.24, -58.92) * mm, "end": v(-0.99, -59.2) * mm});
            skLineSegment(sketch, "E6666", {"start": v(-0.99, -59.2) * mm, "end": v(2.48, -59.03) * mm});
            skLineSegment(sketch, "E6667", {"start": v(2.48, -59.03) * mm, "end": v(7.25, -58.64) * mm});
            skLineSegment(sketch, "E6668", {"start": v(7.25, -58.64) * mm, "end": v(8.56, -58.41) * mm});
            skLineSegment(sketch, "E6669", {"start": v(8.56, -58.41) * mm, "end": v(9, -56.93) * mm});
            skLineSegment(sketch, "E6670", {"start": v(9, -56.93) * mm, "end": v(9.1, -56.57) * mm});
            skLineSegment(sketch, "E6671", {"start": v(9.1, -56.57) * mm, "end": v(9.21, -56.1) * mm});
            skLineSegment(sketch, "E6672", {"start": v(9.21, -56.1) * mm, "end": v(9.5, -54.92) * mm});
            skLineSegment(sketch, "E6673", {"start": v(9.5, -54.92) * mm, "end": v(9.8, -53.55) * mm});
            skLineSegment(sketch, "E6674", {"start": v(9.8, -53.55) * mm, "end": v(10.09, -52.15) * mm});
            skLineSegment(sketch, "E6675", {"start": v(10.09, -52.15) * mm, "end": v(10.75, -48.85) * mm});
            skLineSegment(sketch, "E6676", {"start": v(10.75, -48.85) * mm, "end": v(11.5, -37.96) * mm});
            skLineSegment(sketch, "E6677", {"start": v(11.5, -37.96) * mm, "end": v(10.65, -31.2) * mm});
            skLineSegment(sketch, "E6678", {"start": v(10.65, -31.2) * mm, "end": v(10.2, -31.2) * mm});
            skLineSegment(sketch, "E6679", {"start": v(10.2, -31.2) * mm, "end": v(9.8, -33.6) * mm});
            skLineSegment(sketch, "E6680", {"start": v(9.8, -33.6) * mm, "end": v(9.68, -34.21) * mm});
            skLineSegment(sketch, "E6681", {"start": v(9.68, -34.21) * mm, "end": v(9.55, -34.88) * mm});
            skLineSegment(sketch, "E6682", {"start": v(9.55, -34.88) * mm, "end": v(9.4, -35.6) * mm});
            skLineSegment(sketch, "E6683", {"start": v(9.4, -35.6) * mm, "end": v(9.21, -36.35) * mm});
            skLineSegment(sketch, "E6684", {"start": v(9.21, -36.35) * mm, "end": v(9.02, -37.14) * mm});
            skLineSegment(sketch, "E6685", {"start": v(9.02, -37.14) * mm, "end": v(8.8, -37.96) * mm});
            skLineSegment(sketch, "E6686", {"start": v(8.8, -37.96) * mm, "end": v(8.58, -38.8) * mm});
            skLineSegment(sketch, "E6687", {"start": v(8.58, -38.8) * mm, "end": v(8.34, -39.66) * mm});
            skLineSegment(sketch, "E6688", {"start": v(8.34, -39.66) * mm, "end": v(8.09, -40.53) * mm});
            skLineSegment(sketch, "E6689", {"start": v(8.09, -40.53) * mm, "end": v(7.83, -41.4) * mm});
            skLineSegment(sketch, "E6690", {"start": v(7.83, -41.4) * mm, "end": v(7.56, -42.28) * mm});
            skLineSegment(sketch, "E6691", {"start": v(7.56, -42.28) * mm, "end": v(7.28, -43.16) * mm});
            skLineSegment(sketch, "E6692", {"start": v(7.28, -43.16) * mm, "end": v(7, -44.02) * mm});
            skLineSegment(sketch, "E6693", {"start": v(7, -44.02) * mm, "end": v(6.7, -44.86) * mm});
            skLineSegment(sketch, "E6694", {"start": v(6.7, -44.86) * mm, "end": v(6.42, -45.68) * mm});
            skLineSegment(sketch, "E6695", {"start": v(6.42, -45.68) * mm, "end": v(6.13, -46.48) * mm});
            skLineSegment(sketch, "E6696", {"start": v(6.13, -46.48) * mm, "end": v(4.14, -51.4) * mm});
            skLineSegment(sketch, "E6697", {"start": v(4.14, -51.4) * mm, "end": v(3.4, -52.98) * mm});
            skLineSegment(sketch, "E6698", {"start": v(3.4, -52.98) * mm, "end": v(0.88, -52.98) * mm});
            skLineSegment(sketch, "E6699", {"start": v(0.88, -52.98) * mm, "end": v(-0.06, -51.84) * mm});
            skLineSegment(sketch, "E6700", {"start": v(-0.06, -51.84) * mm, "end": v(-0.28, -51.55) * mm});
            skLineSegment(sketch, "E6701", {"start": v(-0.28, -51.55) * mm, "end": v(-0.54, -51.17) * mm});
            skLineSegment(sketch, "E6702", {"start": v(-0.54, -51.17) * mm, "end": v(-0.82, -50.72) * mm});
            skLineSegment(sketch, "E6703", {"start": v(-0.82, -50.72) * mm, "end": v(-1.13, -50.22) * mm});
            skLineSegment(sketch, "E6704", {"start": v(-1.13, -50.22) * mm, "end": v(-1.45, -49.66) * mm});
            skLineSegment(sketch, "E6705", {"start": v(-1.45, -49.66) * mm, "end": v(-1.77, -49.09) * mm});
            skLineSegment(sketch, "E6706", {"start": v(-1.77, -49.09) * mm, "end": v(-2.09, -48.5) * mm});
            skLineSegment(sketch, "E6707", {"start": v(-2.09, -48.5) * mm, "end": v(-2.39, -47.92) * mm});
            skLineSegment(sketch, "E6708", {"start": v(-2.39, -47.92) * mm, "end": v(-3.77, -45.14) * mm});
            skLineSegment(sketch, "E6709", {"start": v(-3.77, -45.14) * mm, "end": v(-5.43, -39.4) * mm});
            skLineSegment(sketch, "E6710", {"start": v(-5.43, -39.4) * mm, "end": v(-6.23, -30.55) * mm});
            skLineSegment(sketch, "E6711", {"start": v(-6.23, -30.55) * mm, "end": v(-6.77, -31.04) * mm});
            skLineSegment(sketch, "E6712", {"start": v(-6.77, -31.04) * mm, "end": v(-6.88, -31.14) * mm});
            skLineSegment(sketch, "E6713", {"start": v(-6.88, -31.14) * mm, "end": v(-7, -31.23) * mm});
            skLineSegment(sketch, "E6714", {"start": v(-7, -31.23) * mm, "end": v(-7.13, -31.31) * mm});
            skLineSegment(sketch, "E6715", {"start": v(-7.13, -31.31) * mm, "end": v(-7.25, -31.38) * mm});
            skLineSegment(sketch, "E6716", {"start": v(-7.25, -31.38) * mm, "end": v(-7.36, -31.44) * mm});
            skLineSegment(sketch, "E6717", {"start": v(-7.36, -31.44) * mm, "end": v(-7.47, -31.49) * mm});
            skLineSegment(sketch, "E6718", {"start": v(-7.47, -31.49) * mm, "end": v(-7.57, -31.52) * mm});
            skLineSegment(sketch, "E6719", {"start": v(-7.57, -31.52) * mm, "end": v(-7.65, -31.53) * mm});
            skLineSegment(sketch, "E6720", {"start": v(-7.65, -31.53) * mm, "end": v(-7.98, -31.53) * mm});
            skLineSegment(sketch, "E6721", {"start": v(-7.98, -31.53) * mm, "end": v(-8.74, -36.1) * mm});
            skLineSegment(sketch, "E6722", {"start": v(-8.74, -36.1) * mm, "end": v(-8.87, -45.55) * mm});
            skLineSegment(sketch, "E6723", {"start": v(-8.87, -45.55) * mm, "end": v(-9.27, -39.28) * mm});
            skLineSegment(sketch, "E6724", {"start": v(-9.27, -39.28) * mm, "end": v(-9.34, -39.67) * mm});
            skLineSegment(sketch, "E6725", {"start": v(-9.34, -39.67) * mm, "end": v(-9.37, -39.78) * mm});
            skLineSegment(sketch, "E6726", {"start": v(-9.37, -39.78) * mm, "end": v(-9.44, -39.93) * mm});
            skLineSegment(sketch, "E6727", {"start": v(-9.44, -39.93) * mm, "end": v(-9.53, -40.1) * mm});
            skLineSegment(sketch, "E6728", {"start": v(-9.53, -40.1) * mm, "end": v(-9.65, -40.27) * mm});
            skLineSegment(sketch, "E6729", {"start": v(-9.65, -40.27) * mm, "end": v(-9.78, -40.47) * mm});
            skLineSegment(sketch, "E6730", {"start": v(-9.78, -40.47) * mm, "end": v(-9.93, -40.67) * mm});
            skLineSegment(sketch, "E6731", {"start": v(-9.93, -40.67) * mm, "end": v(-10.27, -41.08) * mm});
            skLineSegment(sketch, "E6732", {"start": v(-10.27, -41.08) * mm, "end": v(-10.61, -41.46) * mm});
            skLineSegment(sketch, "E6733", {"start": v(-10.61, -41.46) * mm, "end": v(-10.78, -41.63) * mm});
            skLineSegment(sketch, "E6734", {"start": v(-10.78, -41.63) * mm, "end": v(-10.94, -41.78) * mm});
            skLineSegment(sketch, "E6735", {"start": v(-10.94, -41.78) * mm, "end": v(-11.09, -41.9) * mm});
            skLineSegment(sketch, "E6736", {"start": v(-11.09, -41.9) * mm, "end": v(-11.22, -42) * mm});
            skLineSegment(sketch, "E6737", {"start": v(-11.22, -42) * mm, "end": v(-11.33, -42.07) * mm});
            skLineSegment(sketch, "E6738", {"start": v(-11.33, -42.07) * mm, "end": v(-11.37, -42.08) * mm});
            skLineSegment(sketch, "E6739", {"start": v(-11.37, -42.08) * mm, "end": v(-11.4, -42.09) * mm});
            skLineSegment(sketch, "E6740", {"start": v(-11.4, -42.09) * mm, "end": v(-11.7, -42.09) * mm});
            skLineSegment(sketch, "E6741", {"start": v(-11.7, -42.09) * mm, "end": v(-12.77, -43.24) * mm});
            skLineSegment(sketch, "E6742", {"start": v(15.01, -39.3) * mm, "end": v(15.33, -38.46) * mm});
            skLineSegment(sketch, "E6743", {"start": v(15.33, -38.46) * mm, "end": v(16, -38.46) * mm});
            skLineSegment(sketch, "E6744", {"start": v(16, -38.46) * mm, "end": v(16.26, -38.44) * mm});
            skLineSegment(sketch, "E6745", {"start": v(16.26, -38.44) * mm, "end": v(16.37, -38.43) * mm});
            skLineSegment(sketch, "E6746", {"start": v(16.37, -38.43) * mm, "end": v(16.47, -38.4) * mm});
            skLineSegment(sketch, "E6747", {"start": v(16.47, -38.4) * mm, "end": v(16.55, -38.38) * mm});
            skLineSegment(sketch, "E6748", {"start": v(16.55, -38.38) * mm, "end": v(16.62, -38.35) * mm});
            skLineSegment(sketch, "E6749", {"start": v(16.62, -38.35) * mm, "end": v(16.65, -38.31) * mm});
            skLineSegment(sketch, "E6750", {"start": v(16.65, -38.31) * mm, "end": v(16.67, -38.28) * mm});
            skLineSegment(sketch, "E6751", {"start": v(16.67, -38.28) * mm, "end": v(16.66, -38.18) * mm});
            skLineSegment(sketch, "E6752", {"start": v(16.66, -38.18) * mm, "end": v(16.62, -38.05) * mm});
            skLineSegment(sketch, "E6753", {"start": v(16.62, -38.05) * mm, "end": v(16.57, -37.91) * mm});
            skLineSegment(sketch, "E6754", {"start": v(16.57, -37.91) * mm, "end": v(16.5, -37.76) * mm});
            skLineSegment(sketch, "E6755", {"start": v(16.5, -37.76) * mm, "end": v(16.33, -37.41) * mm});
            skLineSegment(sketch, "E6756", {"start": v(16.33, -37.41) * mm, "end": v(16.12, -37.05) * mm});
            skLineSegment(sketch, "E6757", {"start": v(16.12, -37.05) * mm, "end": v(15.88, -36.7) * mm});
            skLineSegment(sketch, "E6758", {"start": v(15.88, -36.7) * mm, "end": v(15.66, -36.4) * mm});
            skLineSegment(sketch, "E6759", {"start": v(15.66, -36.4) * mm, "end": v(15.55, -36.28) * mm});
            skLineSegment(sketch, "E6760", {"start": v(15.55, -36.28) * mm, "end": v(15.45, -36.18) * mm});
            skLineSegment(sketch, "E6761", {"start": v(15.45, -36.18) * mm, "end": v(15.36, -36.1) * mm});
            skLineSegment(sketch, "E6762", {"start": v(15.36, -36.1) * mm, "end": v(15.28, -36.07) * mm});
            skLineSegment(sketch, "E6763", {"start": v(15.28, -36.07) * mm, "end": v(15.18, -36.02) * mm});
            skLineSegment(sketch, "E6764", {"start": v(15.18, -36.02) * mm, "end": v(15.07, -35.97) * mm});
            skLineSegment(sketch, "E6765", {"start": v(15.07, -35.97) * mm, "end": v(14.96, -35.92) * mm});
            skLineSegment(sketch, "E6766", {"start": v(14.96, -35.92) * mm, "end": v(14.9, -35.9) * mm});
            skLineSegment(sketch, "E6767", {"start": v(14.9, -35.9) * mm, "end": v(14.85, -35.9) * mm});
            skLineSegment(sketch, "E6768", {"start": v(14.85, -35.9) * mm, "end": v(14.76, -35.9) * mm});
            skLineSegment(sketch, "E6769", {"start": v(14.76, -35.9) * mm, "end": v(14.67, -35.92) * mm});
            skLineSegment(sketch, "E6770", {"start": v(14.67, -35.92) * mm, "end": v(14.48, -35.97) * mm});
            skLineSegment(sketch, "E6771", {"start": v(14.48, -35.97) * mm, "end": v(14.29, -36.04) * mm});
            skLineSegment(sketch, "E6772", {"start": v(14.29, -36.04) * mm, "end": v(14.1, -36.12) * mm});
            skLineSegment(sketch, "E6773", {"start": v(14.1, -36.12) * mm, "end": v(13.7, -36.3) * mm});
            skLineSegment(sketch, "E6774", {"start": v(13.7, -36.3) * mm, "end": v(13.53, -36.39) * mm});
            skLineSegment(sketch, "E6775", {"start": v(13.53, -36.39) * mm, "end": v(13.35, -36.46) * mm});
            skLineSegment(sketch, "E6776", {"start": v(13.35, -36.46) * mm, "end": v(12.8, -37.96) * mm});
            skLineSegment(sketch, "E6777", {"start": v(12.8, -37.96) * mm, "end": v(13.36, -39.9) * mm});
            skLineSegment(sketch, "E6778", {"start": v(13.36, -39.9) * mm, "end": v(14.57, -41.16) * mm});
            skLineSegment(sketch, "E6779", {"start": v(14.57, -41.16) * mm, "end": v(15.01, -39.3) * mm});
            skLineSegment(sketch, "E6780", {"start": v(15.24, -41.68) * mm, "end": v(14.95, -42.05) * mm});
            skLineSegment(sketch, "E6781", {"start": v(14.95, -42.05) * mm, "end": v(14.4, -41.94) * mm});
            skLineSegment(sketch, "E6782", {"start": v(14.4, -41.94) * mm, "end": v(14.35, -41.89) * mm});
            skLineSegment(sketch, "E6783", {"start": v(14.35, -41.89) * mm, "end": v(14.28, -41.82) * mm});
            skLineSegment(sketch, "E6784", {"start": v(14.28, -41.82) * mm, "end": v(14.1, -41.6) * mm});
            skLineSegment(sketch, "E6785", {"start": v(14.1, -41.6) * mm, "end": v(13.86, -41.24) * mm});
            skLineSegment(sketch, "E6786", {"start": v(13.86, -41.24) * mm, "end": v(13.53, -40.76) * mm});
            skLineSegment(sketch, "E6787", {"start": v(13.53, -40.76) * mm, "end": v(12.59, -39.4) * mm});
            skLineSegment(sketch, "E6788", {"start": v(12.59, -39.4) * mm, "end": v(12.44, -34.4) * mm});
            skLineSegment(sketch, "E6789", {"start": v(12.44, -34.4) * mm, "end": v(15.4, -31.23) * mm});
            skLineSegment(sketch, "E6790", {"start": v(15.4, -31.23) * mm, "end": v(14.18, -30.72) * mm});
            skLineSegment(sketch, "E6791", {"start": v(14.18, -30.72) * mm, "end": v(13.93, -30.62) * mm});
            skLineSegment(sketch, "E6792", {"start": v(13.93, -30.62) * mm, "end": v(13.66, -30.52) * mm});
            skLineSegment(sketch, "E6793", {"start": v(13.66, -30.52) * mm, "end": v(13.15, -30.36) * mm});
            skLineSegment(sketch, "E6794", {"start": v(13.15, -30.36) * mm, "end": v(12.92, -30.3) * mm});
            skLineSegment(sketch, "E6795", {"start": v(12.92, -30.3) * mm, "end": v(12.71, -30.25) * mm});
            skLineSegment(sketch, "E6796", {"start": v(12.71, -30.25) * mm, "end": v(12.54, -30.22) * mm});
            skLineSegment(sketch, "E6797", {"start": v(12.54, -30.22) * mm, "end": v(12.4, -30.2) * mm});
            skLineSegment(sketch, "E6798", {"start": v(12.4, -30.2) * mm, "end": v(11.85, -30.2) * mm});
            skLineSegment(sketch, "E6799", {"start": v(11.85, -30.2) * mm, "end": v(11.2, -32.02) * mm});
            skLineSegment(sketch, "E6800", {"start": v(11.2, -32.02) * mm, "end": v(11.78, -35.65) * mm});
            skLineSegment(sketch, "E6801", {"start": v(11.78, -35.65) * mm, "end": v(11.42, -47.86) * mm});
            skLineSegment(sketch, "E6802", {"start": v(11.42, -47.86) * mm, "end": v(10.1, -55.5) * mm});
            skLineSegment(sketch, "E6803", {"start": v(10.1, -55.5) * mm, "end": v(9.75, -56.4) * mm});
            skLineSegment(sketch, "E6804", {"start": v(9.75, -56.4) * mm, "end": v(9.62, -56.8) * mm});
            skLineSegment(sketch, "E6805", {"start": v(9.62, -56.8) * mm, "end": v(9.5, -57.19) * mm});
            skLineSegment(sketch, "E6806", {"start": v(9.5, -57.19) * mm, "end": v(9.44, -57.54) * mm});
            skLineSegment(sketch, "E6807", {"start": v(9.44, -57.54) * mm, "end": v(9.42, -57.69) * mm});
            skLineSegment(sketch, "E6808", {"start": v(9.42, -57.69) * mm, "end": v(9.4, -57.8) * mm});
            skLineSegment(sketch, "E6809", {"start": v(9.4, -57.8) * mm, "end": v(9.4, -58.3) * mm});
            skLineSegment(sketch, "E6810", {"start": v(9.4, -58.3) * mm, "end": v(10.15, -58.08) * mm});
            skLineSegment(sketch, "E6811", {"start": v(10.15, -58.08) * mm, "end": v(10.35, -58) * mm});
            skLineSegment(sketch, "E6812", {"start": v(10.35, -58) * mm, "end": v(10.54, -57.92) * mm});
            skLineSegment(sketch, "E6813", {"start": v(10.54, -57.92) * mm, "end": v(10.73, -57.82) * mm});
            skLineSegment(sketch, "E6814", {"start": v(10.73, -57.82) * mm, "end": v(10.9, -57.69) * mm});
            skLineSegment(sketch, "E6815", {"start": v(10.9, -57.69) * mm, "end": v(11.08, -57.54) * mm});
            skLineSegment(sketch, "E6816", {"start": v(11.08, -57.54) * mm, "end": v(11.25, -57.36) * mm});
            skLineSegment(sketch, "E6817", {"start": v(11.25, -57.36) * mm, "end": v(11.42, -57.16) * mm});
            skLineSegment(sketch, "E6818", {"start": v(11.42, -57.16) * mm, "end": v(11.59, -56.93) * mm});
            skLineSegment(sketch, "E6819", {"start": v(11.59, -56.93) * mm, "end": v(11.76, -56.66) * mm});
            skLineSegment(sketch, "E6820", {"start": v(11.76, -56.66) * mm, "end": v(11.93, -56.37) * mm});
            skLineSegment(sketch, "E6821", {"start": v(11.93, -56.37) * mm, "end": v(12.1, -56.04) * mm});
            skLineSegment(sketch, "E6822", {"start": v(12.1, -56.04) * mm, "end": v(12.28, -55.67) * mm});
            skLineSegment(sketch, "E6823", {"start": v(12.28, -55.67) * mm, "end": v(12.47, -55.27) * mm});
            skLineSegment(sketch, "E6824", {"start": v(12.47, -55.27) * mm, "end": v(12.66, -54.82) * mm});
            skLineSegment(sketch, "E6825", {"start": v(12.66, -54.82) * mm, "end": v(13.07, -53.8) * mm});
            skLineSegment(sketch, "E6826", {"start": v(13.07, -53.8) * mm, "end": v(14.1, -51.16) * mm});
            skLineSegment(sketch, "E6827", {"start": v(14.1, -51.16) * mm, "end": v(15.74, -43.9) * mm});
            skLineSegment(sketch, "E6828", {"start": v(15.74, -43.9) * mm, "end": v(16.42, -38.82) * mm});
            skLineSegment(sketch, "E6829", {"start": v(16.42, -38.82) * mm, "end": v(15.7, -39.31) * mm});
            skLineSegment(sketch, "E6830", {"start": v(15.7, -39.31) * mm, "end": v(15.24, -41.68) * mm});
            skLineSegment(sketch, "E6831", {"start": v(32.67, -32.5) * mm, "end": v(32.48, -32.45) * mm});
            skLineSegment(sketch, "E6832", {"start": v(32.48, -32.45) * mm, "end": v(32.27, -32.37) * mm});
            skLineSegment(sketch, "E6833", {"start": v(32.27, -32.37) * mm, "end": v(31.83, -32.21) * mm});
            skLineSegment(sketch, "E6834", {"start": v(31.83, -32.21) * mm, "end": v(31.61, -32.15) * mm});
            skLineSegment(sketch, "E6835", {"start": v(31.61, -32.15) * mm, "end": v(31.5, -32.12) * mm});
            skLineSegment(sketch, "E6836", {"start": v(31.5, -32.12) * mm, "end": v(31.4, -32.1) * mm});
            skLineSegment(sketch, "E6837", {"start": v(31.4, -32.1) * mm, "end": v(31.3, -32.1) * mm});
            skLineSegment(sketch, "E6838", {"start": v(31.3, -32.1) * mm, "end": v(31.2, -32.1) * mm});
            skLineSegment(sketch, "E6839", {"start": v(31.2, -32.1) * mm, "end": v(31.1, -32.13) * mm});
            skLineSegment(sketch, "E6840", {"start": v(31.1, -32.13) * mm, "end": v(31.02, -32.16) * mm});
            skLineSegment(sketch, "E6841", {"start": v(31.02, -32.16) * mm, "end": v(30.96, -32.19) * mm});
            skLineSegment(sketch, "E6842", {"start": v(30.96, -32.19) * mm, "end": v(30.91, -32.23) * mm});
            skLineSegment(sketch, "E6843", {"start": v(30.91, -32.23) * mm, "end": v(30.82, -32.33) * mm});
            skLineSegment(sketch, "E6844", {"start": v(30.82, -32.33) * mm, "end": v(30.74, -32.45) * mm});
            skLineSegment(sketch, "E6845", {"start": v(30.74, -32.45) * mm, "end": v(30.68, -32.59) * mm});
            skLineSegment(sketch, "E6846", {"start": v(30.68, -32.59) * mm, "end": v(30.56, -32.87) * mm});
            skLineSegment(sketch, "E6847", {"start": v(30.56, -32.87) * mm, "end": v(30.5, -33.01) * mm});
            skLineSegment(sketch, "E6848", {"start": v(30.5, -33.01) * mm, "end": v(30.44, -33.13) * mm});
            skLineSegment(sketch, "E6849", {"start": v(30.44, -33.13) * mm, "end": v(30.2, -33.54) * mm});
            skLineSegment(sketch, "E6850", {"start": v(30.2, -33.54) * mm, "end": v(30.03, -33.86) * mm});
            skLineSegment(sketch, "E6851", {"start": v(30.03, -33.86) * mm, "end": v(29.98, -33.98) * mm});
            skLineSegment(sketch, "E6852", {"start": v(29.98, -33.98) * mm, "end": v(29.94, -34.1) * mm});
            skLineSegment(sketch, "E6853", {"start": v(29.94, -34.1) * mm, "end": v(29.92, -34.18) * mm});
            skLineSegment(sketch, "E6854", {"start": v(29.92, -34.18) * mm, "end": v(29.92, -34.26) * mm});
            skLineSegment(sketch, "E6855", {"start": v(29.92, -34.26) * mm, "end": v(29.93, -34.32) * mm});
            skLineSegment(sketch, "E6856", {"start": v(29.93, -34.32) * mm, "end": v(29.97, -34.38) * mm});
            skLineSegment(sketch, "E6857", {"start": v(29.97, -34.38) * mm, "end": v(30.02, -34.42) * mm});
            skLineSegment(sketch, "E6858", {"start": v(30.02, -34.42) * mm, "end": v(30.1, -34.45) * mm});
            skLineSegment(sketch, "E6859", {"start": v(30.1, -34.45) * mm, "end": v(30.2, -34.48) * mm});
            skLineSegment(sketch, "E6860", {"start": v(30.2, -34.48) * mm, "end": v(30.3, -34.51) * mm});
            skLineSegment(sketch, "E6861", {"start": v(30.3, -34.51) * mm, "end": v(30.6, -34.56) * mm});
            skLineSegment(sketch, "E6862", {"start": v(30.6, -34.56) * mm, "end": v(31.33, -34.66) * mm});
            skLineSegment(sketch, "E6863", {"start": v(31.33, -34.66) * mm, "end": v(32.1, -35.82) * mm});
            skLineSegment(sketch, "E6864", {"start": v(32.1, -35.82) * mm, "end": v(32.42, -36.28) * mm});
            skLineSegment(sketch, "E6865", {"start": v(32.42, -36.28) * mm, "end": v(32.56, -36.46) * mm});
            skLineSegment(sketch, "E6866", {"start": v(32.56, -36.46) * mm, "end": v(32.69, -36.6) * mm});
            skLineSegment(sketch, "E6867", {"start": v(32.69, -36.6) * mm, "end": v(32.8, -36.72) * mm});
            skLineSegment(sketch, "E6868", {"start": v(32.8, -36.72) * mm, "end": v(32.9, -36.8) * mm});
            skLineSegment(sketch, "E6869", {"start": v(32.9, -36.8) * mm, "end": v(32.99, -36.86) * mm});
            skLineSegment(sketch, "E6870", {"start": v(32.99, -36.86) * mm, "end": v(33.07, -36.89) * mm});
            skLineSegment(sketch, "E6871", {"start": v(33.07, -36.89) * mm, "end": v(33.1, -36.89) * mm});
            skLineSegment(sketch, "E6872", {"start": v(33.1, -36.89) * mm, "end": v(33.15, -36.88) * mm});
            skLineSegment(sketch, "E6873", {"start": v(33.15, -36.88) * mm, "end": v(33.21, -36.84) * mm});
            skLineSegment(sketch, "E6874", {"start": v(33.21, -36.84) * mm, "end": v(33.28, -36.77) * mm});
            skLineSegment(sketch, "E6875", {"start": v(33.28, -36.77) * mm, "end": v(33.33, -36.67) * mm});
            skLineSegment(sketch, "E6876", {"start": v(33.33, -36.67) * mm, "end": v(33.39, -36.54) * mm});
            skLineSegment(sketch, "E6877", {"start": v(33.39, -36.54) * mm, "end": v(33.44, -36.38) * mm});
            skLineSegment(sketch, "E6878", {"start": v(33.44, -36.38) * mm, "end": v(33.54, -35.96) * mm});
            skLineSegment(sketch, "E6879", {"start": v(33.54, -35.96) * mm, "end": v(33.75, -35) * mm});
            skLineSegment(sketch, "E6880", {"start": v(33.75, -35) * mm, "end": v(32.67, -32.5) * mm});
            skLineSegment(sketch, "E6881", {"start": v(32.83, -31.5) * mm, "end": v(29.47, -29.82) * mm});
            skLineSegment(sketch, "E6882", {"start": v(29.47, -29.82) * mm, "end": v(23.76, -28.9) * mm});
            skLineSegment(sketch, "E6883", {"start": v(23.76, -28.9) * mm, "end": v(23.52, -28.89) * mm});
            skLineSegment(sketch, "E6884", {"start": v(23.52, -28.89) * mm, "end": v(23.47, -28.88) * mm});
            skLineSegment(sketch, "E6885", {"start": v(23.47, -28.88) * mm, "end": v(23.42, -28.87) * mm});
            skLineSegment(sketch, "E6886", {"start": v(23.42, -28.87) * mm, "end": v(23.38, -28.84) * mm});
            skLineSegment(sketch, "E6887", {"start": v(23.38, -28.84) * mm, "end": v(23.34, -28.8) * mm});
            skLineSegment(sketch, "E6888", {"start": v(23.34, -28.8) * mm, "end": v(23.3, -28.76) * mm});
            skLineSegment(sketch, "E6889", {"start": v(23.3, -28.76) * mm, "end": v(23.29, -28.71) * mm});
            skLineSegment(sketch, "E6890", {"start": v(23.29, -28.71) * mm, "end": v(23.27, -28.66) * mm});
            skLineSegment(sketch, "E6891", {"start": v(23.27, -28.66) * mm, "end": v(23.27, -28.6) * mm});
            skLineSegment(sketch, "E6892", {"start": v(23.27, -28.6) * mm, "end": v(22.99, -27.07) * mm});
            skLineSegment(sketch, "E6893", {"start": v(22.99, -27.07) * mm, "end": v(22.74, -25.99) * mm});
            skLineSegment(sketch, "E6894", {"start": v(22.74, -25.99) * mm, "end": v(22.35, -25.78) * mm});
            skLineSegment(sketch, "E6895", {"start": v(22.35, -25.78) * mm, "end": v(21.96, -25.56) * mm});
            skLineSegment(sketch, "E6896", {"start": v(21.96, -25.56) * mm, "end": v(21.15, -25.1) * mm});
            skLineSegment(sketch, "E6897", {"start": v(21.15, -25.1) * mm, "end": v(20.31, -24.61) * mm});
            skLineSegment(sketch, "E6898", {"start": v(20.31, -24.61) * mm, "end": v(19.88, -24.37) * mm});
            skLineSegment(sketch, "E6899", {"start": v(19.88, -24.37) * mm, "end": v(19.44, -24.14) * mm});
            skLineSegment(sketch, "E6900", {"start": v(19.44, -24.14) * mm, "end": v(18.95, -23.87) * mm});
            skLineSegment(sketch, "E6901", {"start": v(18.95, -23.87) * mm, "end": v(18.47, -23.6) * mm});
            skLineSegment(sketch, "E6902", {"start": v(18.47, -23.6) * mm, "end": v(18.24, -23.49) * mm});
            skLineSegment(sketch, "E6903", {"start": v(18.24, -23.49) * mm, "end": v(18, -23.39) * mm});
            skLineSegment(sketch, "E6904", {"start": v(18, -23.39) * mm, "end": v(17.76, -23.3) * mm});
            skLineSegment(sketch, "E6905", {"start": v(17.76, -23.3) * mm, "end": v(17.52, -23.25) * mm});
            skLineSegment(sketch, "E6906", {"start": v(17.52, -23.25) * mm, "end": v(17.33, -23.22) * mm});
            skLineSegment(sketch, "E6907", {"start": v(17.33, -23.22) * mm, "end": v(17.12, -23.2) * mm});
            skLineSegment(sketch, "E6908", {"start": v(17.12, -23.2) * mm, "end": v(16.9, -23.2) * mm});
            skLineSegment(sketch, "E6909", {"start": v(16.9, -23.2) * mm, "end": v(16.67, -23.22) * mm});
            skLineSegment(sketch, "E6910", {"start": v(16.67, -23.22) * mm, "end": v(16.45, -23.25) * mm});
            skLineSegment(sketch, "E6911", {"start": v(16.45, -23.25) * mm, "end": v(16.24, -23.3) * mm});
            skLineSegment(sketch, "E6912", {"start": v(16.24, -23.3) * mm, "end": v(16.05, -23.36) * mm});
            skLineSegment(sketch, "E6913", {"start": v(16.05, -23.36) * mm, "end": v(15.87, -23.44) * mm});
            skLineSegment(sketch, "E6914", {"start": v(15.87, -23.44) * mm, "end": v(15.79, -23.5) * mm});
            skLineSegment(sketch, "E6915", {"start": v(15.79, -23.5) * mm, "end": v(15.7, -23.56) * mm});
            skLineSegment(sketch, "E6916", {"start": v(15.7, -23.56) * mm, "end": v(15.55, -23.7) * mm});
            skLineSegment(sketch, "E6917", {"start": v(15.55, -23.7) * mm, "end": v(15.4, -23.88) * mm});
            skLineSegment(sketch, "E6918", {"start": v(15.4, -23.88) * mm, "end": v(15.26, -24.06) * mm});
            skLineSegment(sketch, "E6919", {"start": v(15.26, -24.06) * mm, "end": v(15, -24.44) * mm});
            skLineSegment(sketch, "E6920", {"start": v(15, -24.44) * mm, "end": v(14.88, -24.63) * mm});
            skLineSegment(sketch, "E6921", {"start": v(14.88, -24.63) * mm, "end": v(14.76, -24.8) * mm});
            skLineSegment(sketch, "E6922", {"start": v(14.76, -24.8) * mm, "end": v(14.54, -25.1) * mm});
            skLineSegment(sketch, "E6923", {"start": v(14.54, -25.1) * mm, "end": v(14.34, -25.4) * mm});
            skLineSegment(sketch, "E6924", {"start": v(14.34, -25.4) * mm, "end": v(14.16, -25.68) * mm});
            skLineSegment(sketch, "E6925", {"start": v(14.16, -25.68) * mm, "end": v(14, -25.96) * mm});
            skLineSegment(sketch, "E6926", {"start": v(14, -25.96) * mm, "end": v(13.88, -26.2) * mm});
            skLineSegment(sketch, "E6927", {"start": v(13.88, -26.2) * mm, "end": v(13.78, -26.41) * mm});
            skLineSegment(sketch, "E6928", {"start": v(13.78, -26.41) * mm, "end": v(13.72, -26.58) * mm});
            skLineSegment(sketch, "E6929", {"start": v(13.72, -26.58) * mm, "end": v(13.7, -26.69) * mm});
            skLineSegment(sketch, "E6930", {"start": v(13.7, -26.69) * mm, "end": v(13.7, -27.08) * mm});
            skLineSegment(sketch, "E6931", {"start": v(13.7, -27.08) * mm, "end": v(17.34, -29.98) * mm});
            skLineSegment(sketch, "E6932", {"start": v(17.34, -29.98) * mm, "end": v(12.7, -34.76) * mm});
            skLineSegment(sketch, "E6933", {"start": v(12.7, -34.76) * mm, "end": v(12.71, -35.04) * mm});
            skLineSegment(sketch, "E6934", {"start": v(12.71, -35.04) * mm, "end": v(12.72, -35.1) * mm});
            skLineSegment(sketch, "E6935", {"start": v(12.72, -35.1) * mm, "end": v(12.74, -35.18) * mm});
            skLineSegment(sketch, "E6936", {"start": v(12.74, -35.18) * mm, "end": v(12.8, -35.37) * mm});
            skLineSegment(sketch, "E6937", {"start": v(12.8, -35.37) * mm, "end": v(12.88, -35.56) * mm});
            skLineSegment(sketch, "E6938", {"start": v(12.88, -35.56) * mm, "end": v(13, -35.75) * mm});
            skLineSegment(sketch, "E6939", {"start": v(13, -35.75) * mm, "end": v(13.26, -36.18) * mm});
            skLineSegment(sketch, "E6940", {"start": v(13.26, -36.18) * mm, "end": v(13.46, -36.08) * mm});
            skLineSegment(sketch, "E6941", {"start": v(13.46, -36.08) * mm, "end": v(13.67, -35.96) * mm});
            skLineSegment(sketch, "E6942", {"start": v(13.67, -35.96) * mm, "end": v(14.1, -35.7) * mm});
            skLineSegment(sketch, "E6943", {"start": v(14.1, -35.7) * mm, "end": v(14.32, -35.6) * mm});
            skLineSegment(sketch, "E6944", {"start": v(14.32, -35.6) * mm, "end": v(14.54, -35.5) * mm});
            skLineSegment(sketch, "E6945", {"start": v(14.54, -35.5) * mm, "end": v(14.65, -35.46) * mm});
            skLineSegment(sketch, "E6946", {"start": v(14.65, -35.46) * mm, "end": v(14.76, -35.43) * mm});
            skLineSegment(sketch, "E6947", {"start": v(14.76, -35.43) * mm, "end": v(14.87, -35.4) * mm});
            skLineSegment(sketch, "E6948", {"start": v(14.87, -35.4) * mm, "end": v(14.98, -35.4) * mm});
            skLineSegment(sketch, "E6949", {"start": v(14.98, -35.4) * mm, "end": v(15.1, -35.4) * mm});
            skLineSegment(sketch, "E6950", {"start": v(15.1, -35.4) * mm, "end": v(15.25, -35.43) * mm});
            skLineSegment(sketch, "E6951", {"start": v(15.25, -35.43) * mm, "end": v(15.4, -35.46) * mm});
            skLineSegment(sketch, "E6952", {"start": v(15.4, -35.46) * mm, "end": v(15.54, -35.51) * mm});
            skLineSegment(sketch, "E6953", {"start": v(15.54, -35.51) * mm, "end": v(15.68, -35.57) * mm});
            skLineSegment(sketch, "E6954", {"start": v(15.68, -35.57) * mm, "end": v(15.82, -35.64) * mm});
            skLineSegment(sketch, "E6955", {"start": v(15.82, -35.64) * mm, "end": v(15.94, -35.72) * mm});
            skLineSegment(sketch, "E6956", {"start": v(15.94, -35.72) * mm, "end": v(16.04, -35.8) * mm});
            skLineSegment(sketch, "E6957", {"start": v(16.04, -35.8) * mm, "end": v(16.14, -35.92) * mm});
            skLineSegment(sketch, "E6958", {"start": v(16.14, -35.92) * mm, "end": v(16.23, -36.04) * mm});
            skLineSegment(sketch, "E6959", {"start": v(16.23, -36.04) * mm, "end": v(16.3, -36.17) * mm});
            skLineSegment(sketch, "E6960", {"start": v(16.3, -36.17) * mm, "end": v(16.38, -36.3) * mm});
            skLineSegment(sketch, "E6961", {"start": v(16.38, -36.3) * mm, "end": v(16.52, -36.6) * mm});
            skLineSegment(sketch, "E6962", {"start": v(16.52, -36.6) * mm, "end": v(16.63, -36.93) * mm});
            skLineSegment(sketch, "E6963", {"start": v(16.63, -36.93) * mm, "end": v(16.83, -37.58) * mm});
            skLineSegment(sketch, "E6964", {"start": v(16.83, -37.58) * mm, "end": v(16.92, -37.9) * mm});
            skLineSegment(sketch, "E6965", {"start": v(16.92, -37.9) * mm, "end": v(17.03, -38.18) * mm});
            skLineSegment(sketch, "E6966", {"start": v(17.03, -38.18) * mm, "end": v(17.92, -37) * mm});
            skLineSegment(sketch, "E6967", {"start": v(17.92, -37) * mm, "end": v(18.7, -35.96) * mm});
            skLineSegment(sketch, "E6968", {"start": v(18.7, -35.96) * mm, "end": v(19.34, -35.1) * mm});
            skLineSegment(sketch, "E6969", {"start": v(19.34, -35.1) * mm, "end": v(19.88, -34.35) * mm});
            skLineSegment(sketch, "E6970", {"start": v(19.88, -34.35) * mm, "end": v(23.57, -38.29) * mm});
            skLineSegment(sketch, "E6971", {"start": v(23.57, -38.29) * mm, "end": v(23.82, -37.99) * mm});
            skLineSegment(sketch, "E6972", {"start": v(23.82, -37.99) * mm, "end": v(24.08, -37.65) * mm});
            skLineSegment(sketch, "E6973", {"start": v(24.08, -37.65) * mm, "end": v(24.34, -37.29) * mm});
            skLineSegment(sketch, "E6974", {"start": v(24.34, -37.29) * mm, "end": v(24.6, -36.93) * mm});
            skLineSegment(sketch, "E6975", {"start": v(24.6, -36.93) * mm, "end": v(24.89, -36.58) * mm});
            skLineSegment(sketch, "E6976", {"start": v(24.89, -36.58) * mm, "end": v(25.04, -36.42) * mm});
            skLineSegment(sketch, "E6977", {"start": v(25.04, -36.42) * mm, "end": v(25.18, -36.27) * mm});
            skLineSegment(sketch, "E6978", {"start": v(25.18, -36.27) * mm, "end": v(25.34, -36.13) * mm});
            skLineSegment(sketch, "E6979", {"start": v(25.34, -36.13) * mm, "end": v(25.5, -36) * mm});
            skLineSegment(sketch, "E6980", {"start": v(25.5, -36) * mm, "end": v(25.66, -35.9) * mm});
            skLineSegment(sketch, "E6981", {"start": v(25.66, -35.9) * mm, "end": v(25.83, -35.82) * mm});
            skLineSegment(sketch, "E6982", {"start": v(25.83, -35.82) * mm, "end": v(25.89, -35.8) * mm});
            skLineSegment(sketch, "E6983", {"start": v(25.89, -35.8) * mm, "end": v(25.95, -35.8) * mm});
            skLineSegment(sketch, "E6984", {"start": v(25.95, -35.8) * mm, "end": v(26.1, -35.8) * mm});
            skLineSegment(sketch, "E6985", {"start": v(26.1, -35.8) * mm, "end": v(26.23, -35.8) * mm});
            skLineSegment(sketch, "E6986", {"start": v(26.23, -35.8) * mm, "end": v(26.36, -35.82) * mm});
            skLineSegment(sketch, "E6987", {"start": v(26.36, -35.82) * mm, "end": v(26.5, -35.81) * mm});
            skLineSegment(sketch, "E6988", {"start": v(26.5, -35.81) * mm, "end": v(26.62, -35.8) * mm});
            skLineSegment(sketch, "E6989", {"start": v(26.62, -35.8) * mm, "end": v(26.72, -35.77) * mm});
            skLineSegment(sketch, "E6990", {"start": v(26.72, -35.77) * mm, "end": v(26.79, -35.73) * mm});
            skLineSegment(sketch, "E6991", {"start": v(26.79, -35.73) * mm, "end": v(26.83, -35.68) * mm});
            skLineSegment(sketch, "E6992", {"start": v(26.83, -35.68) * mm, "end": v(26.86, -35.62) * mm});
            skLineSegment(sketch, "E6993", {"start": v(26.86, -35.62) * mm, "end": v(26.86, -35.54) * mm});
            skLineSegment(sketch, "E6994", {"start": v(26.86, -35.54) * mm, "end": v(26.83, -35.45) * mm});
            skLineSegment(sketch, "E6995", {"start": v(26.83, -35.45) * mm, "end": v(26.78, -35.35) * mm});
            skLineSegment(sketch, "E6996", {"start": v(26.78, -35.35) * mm, "end": v(26.71, -35.23) * mm});
            skLineSegment(sketch, "E6997", {"start": v(26.71, -35.23) * mm, "end": v(26.61, -35.1) * mm});
            skLineSegment(sketch, "E6998", {"start": v(26.61, -35.1) * mm, "end": v(26.49, -34.95) * mm});
            skLineSegment(sketch, "E6999", {"start": v(26.49, -34.95) * mm, "end": v(26.17, -34.6) * mm});
            skLineSegment(sketch, "E7000", {"start": v(26.17, -34.6) * mm, "end": v(25.74, -34.17) * mm});
            skLineSegment(sketch, "E7001", {"start": v(25.74, -34.17) * mm, "end": v(25.51, -33.94) * mm});
            skLineSegment(sketch, "E7002", {"start": v(25.51, -33.94) * mm, "end": v(25.3, -33.71) * mm});
            skLineSegment(sketch, "E7003", {"start": v(25.3, -33.71) * mm, "end": v(25.1, -33.5) * mm});
            skLineSegment(sketch, "E7004", {"start": v(25.1, -33.5) * mm, "end": v(24.93, -33.3) * mm});
            skLineSegment(sketch, "E7005", {"start": v(24.93, -33.3) * mm, "end": v(24.79, -33.11) * mm});
            skLineSegment(sketch, "E7006", {"start": v(24.79, -33.11) * mm, "end": v(24.68, -32.96) * mm});
            skLineSegment(sketch, "E7007", {"start": v(24.68, -32.96) * mm, "end": v(24.61, -32.84) * mm});
            skLineSegment(sketch, "E7008", {"start": v(24.61, -32.84) * mm, "end": v(24.6, -32.8) * mm});
            skLineSegment(sketch, "E7009", {"start": v(24.6, -32.8) * mm, "end": v(24.59, -32.76) * mm});
            skLineSegment(sketch, "E7010", {"start": v(24.59, -32.76) * mm, "end": v(24.59, -32.47) * mm});
            skLineSegment(sketch, "E7011", {"start": v(24.59, -32.47) * mm, "end": v(26.46, -33.48) * mm});
            skLineSegment(sketch, "E7012", {"start": v(26.46, -33.48) * mm, "end": v(27.22, -33.88) * mm});
            skLineSegment(sketch, "E7013", {"start": v(27.22, -33.88) * mm, "end": v(27.9, -34.2) * mm});
            skLineSegment(sketch, "E7014", {"start": v(27.9, -34.2) * mm, "end": v(28.18, -34.32) * mm});
            skLineSegment(sketch, "E7015", {"start": v(28.18, -34.32) * mm, "end": v(28.42, -34.42) * mm});
            skLineSegment(sketch, "E7016", {"start": v(28.42, -34.42) * mm, "end": v(28.6, -34.48) * mm});
            skLineSegment(sketch, "E7017", {"start": v(28.6, -34.48) * mm, "end": v(28.7, -34.5) * mm});
            skLineSegment(sketch, "E7018", {"start": v(28.7, -34.5) * mm, "end": v(29.08, -34.5) * mm});
            skLineSegment(sketch, "E7019", {"start": v(29.08, -34.5) * mm, "end": v(29.34, -33.93) * mm});
            skLineSegment(sketch, "E7020", {"start": v(29.34, -33.93) * mm, "end": v(29.6, -33.3) * mm});
            skLineSegment(sketch, "E7021", {"start": v(29.6, -33.3) * mm, "end": v(29.73, -33) * mm});
            skLineSegment(sketch, "E7022", {"start": v(29.73, -33) * mm, "end": v(29.88, -32.7) * mm});
            skLineSegment(sketch, "E7023", {"start": v(29.88, -32.7) * mm, "end": v(30.03, -32.42) * mm});
            skLineSegment(sketch, "E7024", {"start": v(30.03, -32.42) * mm, "end": v(30.2, -32.17) * mm});
            skLineSegment(sketch, "E7025", {"start": v(30.2, -32.17) * mm, "end": v(30.26, -32.1) * mm});
            skLineSegment(sketch, "E7026", {"start": v(30.26, -32.1) * mm, "end": v(30.34, -32.02) * mm});
            skLineSegment(sketch, "E7027", {"start": v(30.34, -32.02) * mm, "end": v(30.43, -31.95) * mm});
            skLineSegment(sketch, "E7028", {"start": v(30.43, -31.95) * mm, "end": v(30.54, -31.9) * mm});
            skLineSegment(sketch, "E7029", {"start": v(30.54, -31.9) * mm, "end": v(30.65, -31.83) * mm});
            skLineSegment(sketch, "E7030", {"start": v(30.65, -31.83) * mm, "end": v(30.78, -31.77) * mm});
            skLineSegment(sketch, "E7031", {"start": v(30.78, -31.77) * mm, "end": v(31.04, -31.68) * mm});
            skLineSegment(sketch, "E7032", {"start": v(31.04, -31.68) * mm, "end": v(31.32, -31.61) * mm});
            skLineSegment(sketch, "E7033", {"start": v(31.32, -31.61) * mm, "end": v(31.45, -31.6) * mm});
            skLineSegment(sketch, "E7034", {"start": v(31.45, -31.6) * mm, "end": v(31.58, -31.58) * mm});
            skLineSegment(sketch, "E7035", {"start": v(31.58, -31.58) * mm, "end": v(31.7, -31.58) * mm});
            skLineSegment(sketch, "E7036", {"start": v(31.7, -31.58) * mm, "end": v(31.82, -31.59) * mm});
            skLineSegment(sketch, "E7037", {"start": v(31.82, -31.59) * mm, "end": v(31.93, -31.6) * mm});
            skLineSegment(sketch, "E7038", {"start": v(31.93, -31.6) * mm, "end": v(32.03, -31.64) * mm});
            skLineSegment(sketch, "E7039", {"start": v(32.03, -31.64) * mm, "end": v(32.83, -31.5) * mm});
            skLineSegment(sketch, "E7040", {"start": v(32.8, -11.2) * mm, "end": v(33.08, -11.46) * mm});
            skLineSegment(sketch, "E7041", {"start": v(33.08, -11.46) * mm, "end": v(33.39, -11.73) * mm});
            skLineSegment(sketch, "E7042", {"start": v(33.39, -11.73) * mm, "end": v(33.71, -12.01) * mm});
            skLineSegment(sketch, "E7043", {"start": v(33.71, -12.01) * mm, "end": v(34.05, -12.28) * mm});
            skLineSegment(sketch, "E7044", {"start": v(34.05, -12.28) * mm, "end": v(34.4, -12.55) * mm});
            skLineSegment(sketch, "E7045", {"start": v(34.4, -12.55) * mm, "end": v(34.75, -12.8) * mm});
            skLineSegment(sketch, "E7046", {"start": v(34.75, -12.8) * mm, "end": v(35.1, -13.02) * mm});
            skLineSegment(sketch, "E7047", {"start": v(35.1, -13.02) * mm, "end": v(35.43, -13.21) * mm});
            skLineSegment(sketch, "E7048", {"start": v(35.43, -13.21) * mm, "end": v(35.68, -13.34) * mm});
            skLineSegment(sketch, "E7049", {"start": v(35.68, -13.34) * mm, "end": v(35.95, -13.47) * mm});
            skLineSegment(sketch, "E7050", {"start": v(35.95, -13.47) * mm, "end": v(36.52, -13.7) * mm});
            skLineSegment(sketch, "E7051", {"start": v(36.52, -13.7) * mm, "end": v(37.12, -13.93) * mm});
            skLineSegment(sketch, "E7052", {"start": v(37.12, -13.93) * mm, "end": v(37.74, -14.14) * mm});
            skLineSegment(sketch, "E7053", {"start": v(37.74, -14.14) * mm, "end": v(38.37, -14.33) * mm});
            skLineSegment(sketch, "E7054", {"start": v(38.37, -14.33) * mm, "end": v(39, -14.5) * mm});
            skLineSegment(sketch, "E7055", {"start": v(39, -14.5) * mm, "end": v(40.16, -14.8) * mm});
            skLineSegment(sketch, "E7056", {"start": v(40.16, -14.8) * mm, "end": v(40.8, -14.95) * mm});
            skLineSegment(sketch, "E7057", {"start": v(40.8, -14.95) * mm, "end": v(41.49, -15.08) * mm});
            skLineSegment(sketch, "E7058", {"start": v(41.49, -15.08) * mm, "end": v(42.2, -15.2) * mm});
            skLineSegment(sketch, "E7059", {"start": v(42.2, -15.2) * mm, "end": v(42.94, -15.3) * mm});
            skLineSegment(sketch, "E7060", {"start": v(42.94, -15.3) * mm, "end": v(44.4, -15.51) * mm});
            skLineSegment(sketch, "E7061", {"start": v(44.4, -15.51) * mm, "end": v(45.09, -15.61) * mm});
            skLineSegment(sketch, "E7062", {"start": v(45.09, -15.61) * mm, "end": v(45.74, -15.71) * mm});
            skLineSegment(sketch, "E7063", {"start": v(45.74, -15.71) * mm, "end": v(48.3, -14.28) * mm});
            skLineSegment(sketch, "E7064", {"start": v(48.3, -14.28) * mm, "end": v(49.39, -12.22) * mm});
            skLineSegment(sketch, "E7065", {"start": v(49.39, -12.22) * mm, "end": v(49.17, -8.92) * mm});
            skLineSegment(sketch, "E7066", {"start": v(49.17, -8.92) * mm, "end": v(47.2, -8.85) * mm});
            skLineSegment(sketch, "E7067", {"start": v(47.2, -8.85) * mm, "end": v(46.3, -8.8) * mm});
            skLineSegment(sketch, "E7068", {"start": v(46.3, -8.8) * mm, "end": v(45.37, -8.74) * mm});
            skLineSegment(sketch, "E7069", {"start": v(45.37, -8.74) * mm, "end": v(44.42, -8.66) * mm});
            skLineSegment(sketch, "E7070", {"start": v(44.42, -8.66) * mm, "end": v(43.45, -8.56) * mm});
            skLineSegment(sketch, "E7071", {"start": v(43.45, -8.56) * mm, "end": v(42.48, -8.44) * mm});
            skLineSegment(sketch, "E7072", {"start": v(42.48, -8.44) * mm, "end": v(41.51, -8.3) * mm});
            skLineSegment(sketch, "E7073", {"start": v(41.51, -8.3) * mm, "end": v(40.56, -8.16) * mm});
            skLineSegment(sketch, "E7074", {"start": v(40.56, -8.16) * mm, "end": v(39.62, -8) * mm});
            skLineSegment(sketch, "E7075", {"start": v(39.62, -8) * mm, "end": v(38.72, -7.84) * mm});
            skLineSegment(sketch, "E7076", {"start": v(38.72, -7.84) * mm, "end": v(37.86, -7.67) * mm});
            skLineSegment(sketch, "E7077", {"start": v(37.86, -7.67) * mm, "end": v(37.05, -7.5) * mm});
            skLineSegment(sketch, "E7078", {"start": v(37.05, -7.5) * mm, "end": v(36.3, -7.3) * mm});
            skLineSegment(sketch, "E7079", {"start": v(36.3, -7.3) * mm, "end": v(35.62, -7.12) * mm});
            skLineSegment(sketch, "E7080", {"start": v(35.62, -7.12) * mm, "end": v(35.02, -6.94) * mm});
            skLineSegment(sketch, "E7081", {"start": v(35.02, -6.94) * mm, "end": v(34.75, -6.84) * mm});
            skLineSegment(sketch, "E7082", {"start": v(34.75, -6.84) * mm, "end": v(34.5, -6.75) * mm});
            skLineSegment(sketch, "E7083", {"start": v(34.5, -6.75) * mm, "end": v(34.28, -6.66) * mm});
            skLineSegment(sketch, "E7084", {"start": v(34.28, -6.66) * mm, "end": v(34.09, -6.56) * mm});
            skLineSegment(sketch, "E7085", {"start": v(34.09, -6.56) * mm, "end": v(33.2, -6.12) * mm});
            skLineSegment(sketch, "E7086", {"start": v(33.2, -6.12) * mm, "end": v(32.8, -6.86) * mm});
            skLineSegment(sketch, "E7087", {"start": v(32.8, -6.86) * mm, "end": v(32.7, -7.02) * mm});
            skLineSegment(sketch, "E7088", {"start": v(32.7, -7.02) * mm, "end": v(32.6, -7.18) * mm});
            skLineSegment(sketch, "E7089", {"start": v(32.6, -7.18) * mm, "end": v(32.47, -7.35) * mm});
            skLineSegment(sketch, "E7090", {"start": v(32.47, -7.35) * mm, "end": v(32.34, -7.51) * mm});
            skLineSegment(sketch, "E7091", {"start": v(32.34, -7.51) * mm, "end": v(32.2, -7.66) * mm});
            skLineSegment(sketch, "E7092", {"start": v(32.2, -7.66) * mm, "end": v(32.07, -7.8) * mm});
            skLineSegment(sketch, "E7093", {"start": v(32.07, -7.8) * mm, "end": v(31.93, -7.93) * mm});
            skLineSegment(sketch, "E7094", {"start": v(31.93, -7.93) * mm, "end": v(31.8, -8.03) * mm});
            skLineSegment(sketch, "E7095", {"start": v(31.8, -8.03) * mm, "end": v(31.21, -8.45) * mm});
            skLineSegment(sketch, "E7096", {"start": v(31.21, -8.45) * mm, "end": v(31.35, -8.85) * mm});
            skLineSegment(sketch, "E7097", {"start": v(31.35, -8.85) * mm, "end": v(31.5, -9.3) * mm});
            skLineSegment(sketch, "E7098", {"start": v(31.5, -9.3) * mm, "end": v(31.57, -9.51) * mm});
            skLineSegment(sketch, "E7099", {"start": v(31.57, -9.51) * mm, "end": v(31.65, -9.73) * mm});
            skLineSegment(sketch, "E7100", {"start": v(31.65, -9.73) * mm, "end": v(31.74, -9.93) * mm});
            skLineSegment(sketch, "E7101", {"start": v(31.74, -9.93) * mm, "end": v(31.84, -10.1) * mm});
            skLineSegment(sketch, "E7102", {"start": v(31.84, -10.1) * mm, "end": v(31.93, -10.25) * mm});
            skLineSegment(sketch, "E7103", {"start": v(31.93, -10.25) * mm, "end": v(32.04, -10.4) * mm});
            skLineSegment(sketch, "E7104", {"start": v(32.04, -10.4) * mm, "end": v(32.28, -10.68) * mm});
            skLineSegment(sketch, "E7105", {"start": v(32.28, -10.68) * mm, "end": v(32.54, -10.95) * mm});
            skLineSegment(sketch, "E7106", {"start": v(32.54, -10.95) * mm, "end": v(32.8, -11.2) * mm});
            skLineSegment(sketch, "E7107", {"start": v(33.5, -16.99) * mm, "end": v(33.92, -17.25) * mm});
            skLineSegment(sketch, "E7108", {"start": v(33.92, -17.25) * mm, "end": v(34.34, -17.5) * mm});
            skLineSegment(sketch, "E7109", {"start": v(34.34, -17.5) * mm, "end": v(34.76, -17.74) * mm});
            skLineSegment(sketch, "E7110", {"start": v(34.76, -17.74) * mm, "end": v(35.2, -17.97) * mm});
            skLineSegment(sketch, "E7111", {"start": v(35.2, -17.97) * mm, "end": v(35.63, -18.2) * mm});
            skLineSegment(sketch, "E7112", {"start": v(35.63, -18.2) * mm, "end": v(36.08, -18.41) * mm});
            skLineSegment(sketch, "E7113", {"start": v(36.08, -18.41) * mm, "end": v(36.54, -18.62) * mm});
            skLineSegment(sketch, "E7114", {"start": v(36.54, -18.62) * mm, "end": v(37.01, -18.83) * mm});
            skLineSegment(sketch, "E7115", {"start": v(37.01, -18.83) * mm, "end": v(37.5, -19.02) * mm});
            skLineSegment(sketch, "E7116", {"start": v(37.5, -19.02) * mm, "end": v(38, -19.21) * mm});
            skLineSegment(sketch, "E7117", {"start": v(38, -19.21) * mm, "end": v(38.5, -19.4) * mm});
            skLineSegment(sketch, "E7118", {"start": v(38.5, -19.4) * mm, "end": v(39.04, -19.57) * mm});
            skLineSegment(sketch, "E7119", {"start": v(39.04, -19.57) * mm, "end": v(39.58, -19.75) * mm});
            skLineSegment(sketch, "E7120", {"start": v(39.58, -19.75) * mm, "end": v(40.15, -19.92) * mm});
            skLineSegment(sketch, "E7121", {"start": v(40.15, -19.92) * mm, "end": v(40.74, -20.09) * mm});
            skLineSegment(sketch, "E7122", {"start": v(40.74, -20.09) * mm, "end": v(41.34, -20.25) * mm});
            skLineSegment(sketch, "E7123", {"start": v(41.34, -20.25) * mm, "end": v(43.41, -20.8) * mm});
            skLineSegment(sketch, "E7124", {"start": v(43.41, -20.8) * mm, "end": v(45.19, -19.8) * mm});
            skLineSegment(sketch, "E7125", {"start": v(45.19, -19.8) * mm, "end": v(45.4, -18.75) * mm});
            skLineSegment(sketch, "E7126", {"start": v(45.4, -18.75) * mm, "end": v(45.44, -18.52) * mm});
            skLineSegment(sketch, "E7127", {"start": v(45.44, -18.52) * mm, "end": v(45.47, -18.28) * mm});
            skLineSegment(sketch, "E7128", {"start": v(45.47, -18.28) * mm, "end": v(45.5, -18.03) * mm});
            skLineSegment(sketch, "E7129", {"start": v(45.5, -18.03) * mm, "end": v(45.51, -17.78) * mm});
            skLineSegment(sketch, "E7130", {"start": v(45.51, -17.78) * mm, "end": v(45.52, -17.54) * mm});
            skLineSegment(sketch, "E7131", {"start": v(45.52, -17.54) * mm, "end": v(45.51, -17.31) * mm});
            skLineSegment(sketch, "E7132", {"start": v(45.51, -17.31) * mm, "end": v(45.5, -17.1) * mm});
            skLineSegment(sketch, "E7133", {"start": v(45.5, -17.1) * mm, "end": v(45.47, -16.94) * mm});
            skLineSegment(sketch, "E7134", {"start": v(45.47, -16.94) * mm, "end": v(45.33, -16.18) * mm});
            skLineSegment(sketch, "E7135", {"start": v(45.33, -16.18) * mm, "end": v(44.52, -16.06) * mm});
            skLineSegment(sketch, "E7136", {"start": v(44.52, -16.06) * mm, "end": v(43.65, -15.95) * mm});
            skLineSegment(sketch, "E7137", {"start": v(43.65, -15.95) * mm, "end": v(41.83, -15.73) * mm});
            skLineSegment(sketch, "E7138", {"start": v(41.83, -15.73) * mm, "end": v(40.92, -15.6) * mm});
            skLineSegment(sketch, "E7139", {"start": v(40.92, -15.6) * mm, "end": v(40.47, -15.52) * mm});
            skLineSegment(sketch, "E7140", {"start": v(40.47, -15.52) * mm, "end": v(40.03, -15.44) * mm});
            skLineSegment(sketch, "E7141", {"start": v(40.03, -15.44) * mm, "end": v(39.6, -15.36) * mm});
            skLineSegment(sketch, "E7142", {"start": v(39.6, -15.36) * mm, "end": v(39.18, -15.26) * mm});
            skLineSegment(sketch, "E7143", {"start": v(39.18, -15.26) * mm, "end": v(38.78, -15.16) * mm});
            skLineSegment(sketch, "E7144", {"start": v(38.78, -15.16) * mm, "end": v(38.39, -15.05) * mm});
            skLineSegment(sketch, "E7145", {"start": v(38.39, -15.05) * mm, "end": v(37.8, -14.85) * mm});
            skLineSegment(sketch, "E7146", {"start": v(37.8, -14.85) * mm, "end": v(37.19, -14.62) * mm});
            skLineSegment(sketch, "E7147", {"start": v(37.19, -14.62) * mm, "end": v(36.56, -14.36) * mm});
            skLineSegment(sketch, "E7148", {"start": v(36.56, -14.36) * mm, "end": v(35.93, -14.08) * mm});
            skLineSegment(sketch, "E7149", {"start": v(35.93, -14.08) * mm, "end": v(35.3, -13.77) * mm});
            skLineSegment(sketch, "E7150", {"start": v(35.3, -13.77) * mm, "end": v(34.7, -13.45) * mm});
            skLineSegment(sketch, "E7151", {"start": v(34.7, -13.45) * mm, "end": v(34.42, -13.28) * mm});
            skLineSegment(sketch, "E7152", {"start": v(34.42, -13.28) * mm, "end": v(34.15, -13.1) * mm});
            skLineSegment(sketch, "E7153", {"start": v(34.15, -13.1) * mm, "end": v(33.89, -12.94) * mm});
            skLineSegment(sketch, "E7154", {"start": v(33.89, -12.94) * mm, "end": v(33.64, -12.76) * mm});
            skLineSegment(sketch, "E7155", {"start": v(33.64, -12.76) * mm, "end": v(33.46, -12.63) * mm});
            skLineSegment(sketch, "E7156", {"start": v(33.46, -12.63) * mm, "end": v(33.28, -12.48) * mm});
            skLineSegment(sketch, "E7157", {"start": v(33.28, -12.48) * mm, "end": v(32.93, -12.15) * mm});
            skLineSegment(sketch, "E7158", {"start": v(32.93, -12.15) * mm, "end": v(32.59, -11.78) * mm});
            skLineSegment(sketch, "E7159", {"start": v(32.59, -11.78) * mm, "end": v(32.24, -11.4) * mm});
            skLineSegment(sketch, "E7160", {"start": v(32.24, -11.4) * mm, "end": v(31.58, -10.62) * mm});
            skLineSegment(sketch, "E7161", {"start": v(31.58, -10.62) * mm, "end": v(31.26, -10.25) * mm});
            skLineSegment(sketch, "E7162", {"start": v(31.26, -10.25) * mm, "end": v(30.96, -9.91) * mm});
            skLineSegment(sketch, "E7163", {"start": v(30.96, -9.91) * mm, "end": v(29.12, -12.1) * mm});
            skLineSegment(sketch, "E7164", {"start": v(29.12, -12.1) * mm, "end": v(29.55, -12.72) * mm});
            skLineSegment(sketch, "E7165", {"start": v(29.55, -12.72) * mm, "end": v(29.78, -13.04) * mm});
            skLineSegment(sketch, "E7166", {"start": v(29.78, -13.04) * mm, "end": v(30, -13.33) * mm});
            skLineSegment(sketch, "E7167", {"start": v(30, -13.33) * mm, "end": v(30.4, -13.81) * mm});
            skLineSegment(sketch, "E7168", {"start": v(30.4, -13.81) * mm, "end": v(30.84, -14.32) * mm});
            skLineSegment(sketch, "E7169", {"start": v(30.84, -14.32) * mm, "end": v(31.3, -14.81) * mm});
            skLineSegment(sketch, "E7170", {"start": v(31.3, -14.81) * mm, "end": v(31.73, -15.26) * mm});
            skLineSegment(sketch, "E7171", {"start": v(31.73, -15.26) * mm, "end": v(32.15, -15.69) * mm});
            skLineSegment(sketch, "E7172", {"start": v(32.15, -15.69) * mm, "end": v(32.6, -16.13) * mm});
            skLineSegment(sketch, "E7173", {"start": v(32.6, -16.13) * mm, "end": v(33.5, -16.99) * mm});
            skLineSegment(sketch, "E7174", {"start": v(29.15, -20.9) * mm, "end": v(29.44, -21.18) * mm});
            skLineSegment(sketch, "E7175", {"start": v(29.44, -21.18) * mm, "end": v(29.73, -21.44) * mm});
            skLineSegment(sketch, "E7176", {"start": v(29.73, -21.44) * mm, "end": v(30.03, -21.68) * mm});
            skLineSegment(sketch, "E7177", {"start": v(30.03, -21.68) * mm, "end": v(30.33, -21.92) * mm});
            skLineSegment(sketch, "E7178", {"start": v(30.33, -21.92) * mm, "end": v(30.64, -22.15) * mm});
            skLineSegment(sketch, "E7179", {"start": v(30.64, -22.15) * mm, "end": v(30.96, -22.36) * mm});
            skLineSegment(sketch, "E7180", {"start": v(30.96, -22.36) * mm, "end": v(31.28, -22.57) * mm});
            skLineSegment(sketch, "E7181", {"start": v(31.28, -22.57) * mm, "end": v(31.62, -22.77) * mm});
            skLineSegment(sketch, "E7182", {"start": v(31.62, -22.77) * mm, "end": v(31.97, -22.96) * mm});
            skLineSegment(sketch, "E7183", {"start": v(31.97, -22.96) * mm, "end": v(32.33, -23.14) * mm});
            skLineSegment(sketch, "E7184", {"start": v(32.33, -23.14) * mm, "end": v(32.7, -23.3) * mm});
            skLineSegment(sketch, "E7185", {"start": v(32.7, -23.3) * mm, "end": v(33.09, -23.47) * mm});
            skLineSegment(sketch, "E7186", {"start": v(33.09, -23.47) * mm, "end": v(33.49, -23.63) * mm});
            skLineSegment(sketch, "E7187", {"start": v(33.49, -23.63) * mm, "end": v(33.9, -23.78) * mm});
            skLineSegment(sketch, "E7188", {"start": v(33.9, -23.78) * mm, "end": v(34.34, -23.93) * mm});
            skLineSegment(sketch, "E7189", {"start": v(34.34, -23.93) * mm, "end": v(34.8, -24.07) * mm});
            skLineSegment(sketch, "E7190", {"start": v(34.8, -24.07) * mm, "end": v(36.59, -24.6) * mm});
            skLineSegment(sketch, "E7191", {"start": v(36.59, -24.6) * mm, "end": v(41.7, -24.6) * mm});
            skLineSegment(sketch, "E7192", {"start": v(41.7, -24.6) * mm, "end": v(42.74, -23.13) * mm});
            skLineSegment(sketch, "E7193", {"start": v(42.74, -23.13) * mm, "end": v(42.74, -21.1) * mm});
            skLineSegment(sketch, "E7194", {"start": v(42.74, -21.1) * mm, "end": v(41.18, -20.69) * mm});
            skLineSegment(sketch, "E7195", {"start": v(41.18, -20.69) * mm, "end": v(40.68, -20.55) * mm});
            skLineSegment(sketch, "E7196", {"start": v(40.68, -20.55) * mm, "end": v(40.15, -20.4) * mm});
            skLineSegment(sketch, "E7197", {"start": v(40.15, -20.4) * mm, "end": v(39.61, -20.23) * mm});
            skLineSegment(sketch, "E7198", {"start": v(39.61, -20.23) * mm, "end": v(39.06, -20.05) * mm});
            skLineSegment(sketch, "E7199", {"start": v(39.06, -20.05) * mm, "end": v(38.5, -19.86) * mm});
            skLineSegment(sketch, "E7200", {"start": v(38.5, -19.86) * mm, "end": v(37.93, -19.66) * mm});
            skLineSegment(sketch, "E7201", {"start": v(37.93, -19.66) * mm, "end": v(37.36, -19.45) * mm});
            skLineSegment(sketch, "E7202", {"start": v(37.36, -19.45) * mm, "end": v(36.8, -19.24) * mm});
            skLineSegment(sketch, "E7203", {"start": v(36.8, -19.24) * mm, "end": v(36.25, -19.02) * mm});
            skLineSegment(sketch, "E7204", {"start": v(36.25, -19.02) * mm, "end": v(35.7, -18.8) * mm});
            skLineSegment(sketch, "E7205", {"start": v(35.7, -18.8) * mm, "end": v(35.18, -18.57) * mm});
            skLineSegment(sketch, "E7206", {"start": v(35.18, -18.57) * mm, "end": v(34.67, -18.33) * mm});
            skLineSegment(sketch, "E7207", {"start": v(34.67, -18.33) * mm, "end": v(34.18, -18.1) * mm});
            skLineSegment(sketch, "E7208", {"start": v(34.18, -18.1) * mm, "end": v(33.73, -17.87) * mm});
            skLineSegment(sketch, "E7209", {"start": v(33.73, -17.87) * mm, "end": v(33.3, -17.64) * mm});
            skLineSegment(sketch, "E7210", {"start": v(33.3, -17.64) * mm, "end": v(32.9, -17.42) * mm});
            skLineSegment(sketch, "E7211", {"start": v(32.9, -17.42) * mm, "end": v(32.8, -17.34) * mm});
            skLineSegment(sketch, "E7212", {"start": v(32.8, -17.34) * mm, "end": v(32.68, -17.25) * mm});
            skLineSegment(sketch, "E7213", {"start": v(32.68, -17.25) * mm, "end": v(32.46, -17.07) * mm});
            skLineSegment(sketch, "E7214", {"start": v(32.46, -17.07) * mm, "end": v(32.27, -16.87) * mm});
            skLineSegment(sketch, "E7215", {"start": v(32.27, -16.87) * mm, "end": v(32.09, -16.66) * mm});
            skLineSegment(sketch, "E7216", {"start": v(32.09, -16.66) * mm, "end": v(31.8, -16.3) * mm});
            skLineSegment(sketch, "E7217", {"start": v(31.8, -16.3) * mm, "end": v(31.68, -16.16) * mm});
            skLineSegment(sketch, "E7218", {"start": v(31.68, -16.16) * mm, "end": v(31.59, -16.06) * mm});
            skLineSegment(sketch, "E7219", {"start": v(31.59, -16.06) * mm, "end": v(31.24, -15.74) * mm});
            skLineSegment(sketch, "E7220", {"start": v(31.24, -15.74) * mm, "end": v(30.89, -15.38) * mm});
            skLineSegment(sketch, "E7221", {"start": v(30.89, -15.38) * mm, "end": v(30.22, -14.67) * mm});
            skLineSegment(sketch, "E7222", {"start": v(30.22, -14.67) * mm, "end": v(29.88, -14.27) * mm});
            skLineSegment(sketch, "E7223", {"start": v(29.88, -14.27) * mm, "end": v(29.53, -13.82) * mm});
            skLineSegment(sketch, "E7224", {"start": v(29.53, -13.82) * mm, "end": v(29.18, -13.37) * mm});
            skLineSegment(sketch, "E7225", {"start": v(29.18, -13.37) * mm, "end": v(28.86, -12.95) * mm});
            skLineSegment(sketch, "E7226", {"start": v(28.86, -12.95) * mm, "end": v(28.5, -13.3) * mm});
            skLineSegment(sketch, "E7227", {"start": v(28.5, -13.3) * mm, "end": v(28.14, -13.7) * mm});
            skLineSegment(sketch, "E7228", {"start": v(28.14, -13.7) * mm, "end": v(27.94, -13.9) * mm});
            skLineSegment(sketch, "E7229", {"start": v(27.94, -13.9) * mm, "end": v(27.75, -14.08) * mm});
            skLineSegment(sketch, "E7230", {"start": v(27.75, -14.08) * mm, "end": v(27.55, -14.24) * mm});
            skLineSegment(sketch, "E7231", {"start": v(27.55, -14.24) * mm, "end": v(27.35, -14.37) * mm});
            skLineSegment(sketch, "E7232", {"start": v(27.35, -14.37) * mm, "end": v(27.25, -14.42) * mm});
            skLineSegment(sketch, "E7233", {"start": v(27.25, -14.42) * mm, "end": v(27.14, -14.45) * mm});
            skLineSegment(sketch, "E7234", {"start": v(27.14, -14.45) * mm, "end": v(26.94, -14.48) * mm});
            skLineSegment(sketch, "E7235", {"start": v(26.94, -14.48) * mm, "end": v(26.84, -14.5) * mm});
            skLineSegment(sketch, "E7236", {"start": v(26.84, -14.5) * mm, "end": v(26.74, -14.54) * mm});
            skLineSegment(sketch, "E7237", {"start": v(26.74, -14.54) * mm, "end": v(26.66, -14.59) * mm});
            skLineSegment(sketch, "E7238", {"start": v(26.66, -14.59) * mm, "end": v(26.58, -14.66) * mm});
            skLineSegment(sketch, "E7239", {"start": v(26.58, -14.66) * mm, "end": v(26.55, -14.72) * mm});
            skLineSegment(sketch, "E7240", {"start": v(26.55, -14.72) * mm, "end": v(26.52, -14.78) * mm});
            skLineSegment(sketch, "E7241", {"start": v(26.52, -14.78) * mm, "end": v(26.5, -14.91) * mm});
            skLineSegment(sketch, "E7242", {"start": v(26.5, -14.91) * mm, "end": v(26.49, -15.06) * mm});
            skLineSegment(sketch, "E7243", {"start": v(26.49, -15.06) * mm, "end": v(26.5, -15.22) * mm});
            skLineSegment(sketch, "E7244", {"start": v(26.5, -15.22) * mm, "end": v(26.55, -15.55) * mm});
            skLineSegment(sketch, "E7245", {"start": v(26.55, -15.55) * mm, "end": v(26.57, -15.7) * mm});
            skLineSegment(sketch, "E7246", {"start": v(26.57, -15.7) * mm, "end": v(26.58, -15.83) * mm});
            skLineSegment(sketch, "E7247", {"start": v(26.58, -15.83) * mm, "end": v(26.6, -16.15) * mm});
            skLineSegment(sketch, "E7248", {"start": v(26.6, -16.15) * mm, "end": v(26.64, -16.47) * mm});
            skLineSegment(sketch, "E7249", {"start": v(26.64, -16.47) * mm, "end": v(26.7, -16.8) * mm});
            skLineSegment(sketch, "E7250", {"start": v(26.7, -16.8) * mm, "end": v(26.75, -17.14) * mm});
            skLineSegment(sketch, "E7251", {"start": v(26.75, -17.14) * mm, "end": v(26.82, -17.46) * mm});
            skLineSegment(sketch, "E7252", {"start": v(26.82, -17.46) * mm, "end": v(26.9, -17.77) * mm});
            skLineSegment(sketch, "E7253", {"start": v(26.9, -17.77) * mm, "end": v(27, -18.04) * mm});
            skLineSegment(sketch, "E7254", {"start": v(27, -18.04) * mm, "end": v(27.1, -18.27) * mm});
            skLineSegment(sketch, "E7255", {"start": v(27.1, -18.27) * mm, "end": v(27.26, -18.58) * mm});
            skLineSegment(sketch, "E7256", {"start": v(27.26, -18.58) * mm, "end": v(27.44, -18.9) * mm});
            skLineSegment(sketch, "E7257", {"start": v(27.44, -18.9) * mm, "end": v(27.63, -19.2) * mm});
            skLineSegment(sketch, "E7258", {"start": v(27.63, -19.2) * mm, "end": v(27.83, -19.48) * mm});
            skLineSegment(sketch, "E7259", {"start": v(27.83, -19.48) * mm, "end": v(27.97, -19.66) * mm});
            skLineSegment(sketch, "E7260", {"start": v(27.97, -19.66) * mm, "end": v(28.13, -19.84) * mm});
            skLineSegment(sketch, "E7261", {"start": v(28.13, -19.84) * mm, "end": v(28.47, -20.22) * mm});
            skLineSegment(sketch, "E7262", {"start": v(28.47, -20.22) * mm, "end": v(29.15, -20.9) * mm});
            skLineSegment(sketch, "E7263", {"start": v(27.4, -19.38) * mm, "end": v(27.1, -18.88) * mm});
            skLineSegment(sketch, "E7264", {"start": v(27.1, -18.88) * mm, "end": v(26.81, -18.38) * mm});
            skLineSegment(sketch, "E7265", {"start": v(26.81, -18.38) * mm, "end": v(26.7, -18.16) * mm});
            skLineSegment(sketch, "E7266", {"start": v(26.7, -18.16) * mm, "end": v(26.6, -17.95) * mm});
            skLineSegment(sketch, "E7267", {"start": v(26.6, -17.95) * mm, "end": v(26.5, -17.73) * mm});
            skLineSegment(sketch, "E7268", {"start": v(26.5, -17.73) * mm, "end": v(26.4, -17.52) * mm});
            skLineSegment(sketch, "E7269", {"start": v(26.4, -17.52) * mm, "end": v(26.34, -17.32) * mm});
            skLineSegment(sketch, "E7270", {"start": v(26.34, -17.32) * mm, "end": v(26.28, -17.14) * mm});
            skLineSegment(sketch, "E7271", {"start": v(26.28, -17.14) * mm, "end": v(26.25, -16.98) * mm});
            skLineSegment(sketch, "E7272", {"start": v(26.25, -16.98) * mm, "end": v(26.24, -16.86) * mm});
            skLineSegment(sketch, "E7273", {"start": v(26.24, -16.86) * mm, "end": v(26.24, -16.35) * mm});
            skLineSegment(sketch, "E7274", {"start": v(26.24, -16.35) * mm, "end": v(25.96, -16.35) * mm});
            skLineSegment(sketch, "E7275", {"start": v(25.96, -16.35) * mm, "end": v(25.9, -16.36) * mm});
            skLineSegment(sketch, "E7276", {"start": v(25.9, -16.36) * mm, "end": v(25.81, -16.4) * mm});
            skLineSegment(sketch, "E7277", {"start": v(25.81, -16.4) * mm, "end": v(25.72, -16.45) * mm});
            skLineSegment(sketch, "E7278", {"start": v(25.72, -16.45) * mm, "end": v(25.61, -16.52) * mm});
            skLineSegment(sketch, "E7279", {"start": v(25.61, -16.52) * mm, "end": v(25.5, -16.6) * mm});
            skLineSegment(sketch, "E7280", {"start": v(25.5, -16.6) * mm, "end": v(25.4, -16.7) * mm});
            skLineSegment(sketch, "E7281", {"start": v(25.4, -16.7) * mm, "end": v(25.28, -16.81) * mm});
            skLineSegment(sketch, "E7282", {"start": v(25.28, -16.81) * mm, "end": v(25.18, -16.93) * mm});
            skLineSegment(sketch, "E7283", {"start": v(25.18, -16.93) * mm, "end": v(24.67, -17.5) * mm});
            skLineSegment(sketch, "E7284", {"start": v(24.67, -17.5) * mm, "end": v(24.33, -20.75) * mm});
            skLineSegment(sketch, "E7285", {"start": v(24.33, -20.75) * mm, "end": v(24.59, -21.19) * mm});
            skLineSegment(sketch, "E7286", {"start": v(24.59, -21.19) * mm, "end": v(24.86, -21.66) * mm});
            skLineSegment(sketch, "E7287", {"start": v(24.86, -21.66) * mm, "end": v(25.42, -22.64) * mm});
            skLineSegment(sketch, "E7288", {"start": v(25.42, -22.64) * mm, "end": v(25.71, -23.13) * mm});
            skLineSegment(sketch, "E7289", {"start": v(25.71, -23.13) * mm, "end": v(26.01, -23.6) * mm});
            skLineSegment(sketch, "E7290", {"start": v(26.01, -23.6) * mm, "end": v(26.17, -23.83) * mm});
            skLineSegment(sketch, "E7291", {"start": v(26.17, -23.83) * mm, "end": v(26.32, -24.04) * mm});
            skLineSegment(sketch, "E7292", {"start": v(26.32, -24.04) * mm, "end": v(26.48, -24.24) * mm});
            skLineSegment(sketch, "E7293", {"start": v(26.48, -24.24) * mm, "end": v(26.64, -24.43) * mm});
            skLineSegment(sketch, "E7294", {"start": v(26.64, -24.43) * mm, "end": v(26.82, -24.62) * mm});
            skLineSegment(sketch, "E7295", {"start": v(26.82, -24.62) * mm, "end": v(27, -24.8) * mm});
            skLineSegment(sketch, "E7296", {"start": v(27, -24.8) * mm, "end": v(27.41, -25.17) * mm});
            skLineSegment(sketch, "E7297", {"start": v(27.41, -25.17) * mm, "end": v(27.86, -25.54) * mm});
            skLineSegment(sketch, "E7298", {"start": v(27.86, -25.54) * mm, "end": v(28.32, -25.9) * mm});
            skLineSegment(sketch, "E7299", {"start": v(28.32, -25.9) * mm, "end": v(29.25, -26.58) * mm});
            skLineSegment(sketch, "E7300", {"start": v(29.25, -26.58) * mm, "end": v(29.7, -26.92) * mm});
            skLineSegment(sketch, "E7301", {"start": v(29.7, -26.92) * mm, "end": v(30.1, -27.24) * mm});
            skLineSegment(sketch, "E7302", {"start": v(30.1, -27.24) * mm, "end": v(34.32, -29.16) * mm});
            skLineSegment(sketch, "E7303", {"start": v(34.32, -29.16) * mm, "end": v(35.31, -28.98) * mm});
            skLineSegment(sketch, "E7304", {"start": v(35.31, -28.98) * mm, "end": v(35.53, -28.94) * mm});
            skLineSegment(sketch, "E7305", {"start": v(35.53, -28.94) * mm, "end": v(35.76, -28.88) * mm});
            skLineSegment(sketch, "E7306", {"start": v(35.76, -28.88) * mm, "end": v(36, -28.8) * mm});
            skLineSegment(sketch, "E7307", {"start": v(36, -28.8) * mm, "end": v(36.23, -28.72) * mm});
            skLineSegment(sketch, "E7308", {"start": v(36.23, -28.72) * mm, "end": v(36.47, -28.63) * mm});
            skLineSegment(sketch, "E7309", {"start": v(36.47, -28.63) * mm, "end": v(36.69, -28.53) * mm});
            skLineSegment(sketch, "E7310", {"start": v(36.69, -28.53) * mm, "end": v(36.89, -28.43) * mm});
            skLineSegment(sketch, "E7311", {"start": v(36.89, -28.43) * mm, "end": v(37.06, -28.34) * mm});
            skLineSegment(sketch, "E7312", {"start": v(37.06, -28.34) * mm, "end": v(37.82, -27.86) * mm});
            skLineSegment(sketch, "E7313", {"start": v(37.82, -27.86) * mm, "end": v(38.13, -27.03) * mm});
            skLineSegment(sketch, "E7314", {"start": v(38.13, -27.03) * mm, "end": v(38.25, -26.68) * mm});
            skLineSegment(sketch, "E7315", {"start": v(38.25, -26.68) * mm, "end": v(38.35, -26.32) * mm});
            skLineSegment(sketch, "E7316", {"start": v(38.35, -26.32) * mm, "end": v(38.42, -26) * mm});
            skLineSegment(sketch, "E7317", {"start": v(38.42, -26) * mm, "end": v(38.44, -25.87) * mm});
            skLineSegment(sketch, "E7318", {"start": v(38.44, -25.87) * mm, "end": v(38.45, -25.76) * mm});
            skLineSegment(sketch, "E7319", {"start": v(38.45, -25.76) * mm, "end": v(38.45, -25.32) * mm});
            skLineSegment(sketch, "E7320", {"start": v(38.45, -25.32) * mm, "end": v(37.29, -25.09) * mm});
            skLineSegment(sketch, "E7321", {"start": v(37.29, -25.09) * mm, "end": v(36.04, -24.85) * mm});
            skLineSegment(sketch, "E7322", {"start": v(36.04, -24.85) * mm, "end": v(35.4, -24.72) * mm});
            skLineSegment(sketch, "E7323", {"start": v(35.4, -24.72) * mm, "end": v(34.8, -24.58) * mm});
            skLineSegment(sketch, "E7324", {"start": v(34.8, -24.58) * mm, "end": v(34.2, -24.43) * mm});
            skLineSegment(sketch, "E7325", {"start": v(34.2, -24.43) * mm, "end": v(33.93, -24.34) * mm});
            skLineSegment(sketch, "E7326", {"start": v(33.93, -24.34) * mm, "end": v(33.66, -24.26) * mm});
            skLineSegment(sketch, "E7327", {"start": v(33.66, -24.26) * mm, "end": v(33.26, -24.12) * mm});
            skLineSegment(sketch, "E7328", {"start": v(33.26, -24.12) * mm, "end": v(32.83, -23.96) * mm});
            skLineSegment(sketch, "E7329", {"start": v(32.83, -23.96) * mm, "end": v(32.4, -23.79) * mm});
            skLineSegment(sketch, "E7330", {"start": v(32.4, -23.79) * mm, "end": v(31.96, -23.6) * mm});
            skLineSegment(sketch, "E7331", {"start": v(31.96, -23.6) * mm, "end": v(31.52, -23.4) * mm});
            skLineSegment(sketch, "E7332", {"start": v(31.52, -23.4) * mm, "end": v(31.1, -23.18) * mm});
            skLineSegment(sketch, "E7333", {"start": v(31.1, -23.18) * mm, "end": v(30.71, -22.96) * mm});
            skLineSegment(sketch, "E7334", {"start": v(30.71, -22.96) * mm, "end": v(30.53, -22.84) * mm});
            skLineSegment(sketch, "E7335", {"start": v(30.53, -22.84) * mm, "end": v(30.36, -22.72) * mm});
            skLineSegment(sketch, "E7336", {"start": v(30.36, -22.72) * mm, "end": v(30.18, -22.58) * mm});
            skLineSegment(sketch, "E7337", {"start": v(30.18, -22.58) * mm, "end": v(30, -22.43) * mm});
            skLineSegment(sketch, "E7338", {"start": v(30, -22.43) * mm, "end": v(29.64, -22.1) * mm});
            skLineSegment(sketch, "E7339", {"start": v(29.64, -22.1) * mm, "end": v(29.28, -21.74) * mm});
            skLineSegment(sketch, "E7340", {"start": v(29.28, -21.74) * mm, "end": v(28.93, -21.36) * mm});
            skLineSegment(sketch, "E7341", {"start": v(28.93, -21.36) * mm, "end": v(28.59, -20.96) * mm});
            skLineSegment(sketch, "E7342", {"start": v(28.59, -20.96) * mm, "end": v(28.26, -20.57) * mm});
            skLineSegment(sketch, "E7343", {"start": v(28.26, -20.57) * mm, "end": v(27.67, -19.81) * mm});
            skLineSegment(sketch, "E7344", {"start": v(27.67, -19.81) * mm, "end": v(27.52, -19.6) * mm});
            skLineSegment(sketch, "E7345", {"start": v(27.52, -19.6) * mm, "end": v(27.4, -19.38) * mm});
            skLineSegment(sketch, "E7346", {"start": v(-26.89, -11.44) * mm, "end": v(-26.89, -11.86) * mm});
            skLineSegment(sketch, "E7347", {"start": v(-26.89, -11.86) * mm, "end": v(-26.87, -11.97) * mm});
            skLineSegment(sketch, "E7348", {"start": v(-26.87, -11.97) * mm, "end": v(-26.83, -12.09) * mm});
            skLineSegment(sketch, "E7349", {"start": v(-26.83, -12.09) * mm, "end": v(-26.76, -12.22) * mm});
            skLineSegment(sketch, "E7350", {"start": v(-26.76, -12.22) * mm, "end": v(-26.67, -12.36) * mm});
            skLineSegment(sketch, "E7351", {"start": v(-26.67, -12.36) * mm, "end": v(-26.56, -12.5) * mm});
            skLineSegment(sketch, "E7352", {"start": v(-26.56, -12.5) * mm, "end": v(-26.43, -12.66) * mm});
            skLineSegment(sketch, "E7353", {"start": v(-26.43, -12.66) * mm, "end": v(-26.29, -12.81) * mm});
            skLineSegment(sketch, "E7354", {"start": v(-26.29, -12.81) * mm, "end": v(-26.13, -12.96) * mm});
            skLineSegment(sketch, "E7355", {"start": v(-26.13, -12.96) * mm, "end": v(-25.96, -13.1) * mm});
            skLineSegment(sketch, "E7356", {"start": v(-25.96, -13.1) * mm, "end": v(-25.8, -13.24) * mm});
            skLineSegment(sketch, "E7357", {"start": v(-25.8, -13.24) * mm, "end": v(-25.61, -13.37) * mm});
            skLineSegment(sketch, "E7358", {"start": v(-25.61, -13.37) * mm, "end": v(-25.43, -13.5) * mm});
            skLineSegment(sketch, "E7359", {"start": v(-25.43, -13.5) * mm, "end": v(-25.25, -13.6) * mm});
            skLineSegment(sketch, "E7360", {"start": v(-25.25, -13.6) * mm, "end": v(-25.08, -13.69) * mm});
            skLineSegment(sketch, "E7361", {"start": v(-25.08, -13.69) * mm, "end": v(-24.9, -13.76) * mm});
            skLineSegment(sketch, "E7362", {"start": v(-24.9, -13.76) * mm, "end": v(-24.74, -13.81) * mm});
            skLineSegment(sketch, "E7363", {"start": v(-24.74, -13.81) * mm, "end": v(-24.59, -13.84) * mm});
            skLineSegment(sketch, "E7364", {"start": v(-24.59, -13.84) * mm, "end": v(-24.4, -13.87) * mm});
            skLineSegment(sketch, "E7365", {"start": v(-24.4, -13.87) * mm, "end": v(-24.18, -13.88) * mm});
            skLineSegment(sketch, "E7366", {"start": v(-24.18, -13.88) * mm, "end": v(-23.94, -13.89) * mm});
            skLineSegment(sketch, "E7367", {"start": v(-23.94, -13.89) * mm, "end": v(-23.69, -13.88) * mm});
            skLineSegment(sketch, "E7368", {"start": v(-23.69, -13.88) * mm, "end": v(-23.43, -13.87) * mm});
            skLineSegment(sketch, "E7369", {"start": v(-23.43, -13.87) * mm, "end": v(-23.17, -13.85) * mm});
            skLineSegment(sketch, "E7370", {"start": v(-23.17, -13.85) * mm, "end": v(-22.93, -13.82) * mm});
            skLineSegment(sketch, "E7371", {"start": v(-22.93, -13.82) * mm, "end": v(-22.65, -13.8) * mm});
            skLineSegment(sketch, "E7372", {"start": v(-22.65, -13.8) * mm, "end": v(-22.34, -13.78) * mm});
            skLineSegment(sketch, "E7373", {"start": v(-22.34, -13.78) * mm, "end": v(-22.19, -13.76) * mm});
            skLineSegment(sketch, "E7374", {"start": v(-22.19, -13.76) * mm, "end": v(-22.04, -13.74) * mm});
            skLineSegment(sketch, "E7375", {"start": v(-22.04, -13.74) * mm, "end": v(-21.9, -13.7) * mm});
            skLineSegment(sketch, "E7376", {"start": v(-21.9, -13.7) * mm, "end": v(-21.77, -13.66) * mm});
            skLineSegment(sketch, "E7377", {"start": v(-21.77, -13.66) * mm, "end": v(-21.46, -13.52) * mm});
            skLineSegment(sketch, "E7378", {"start": v(-21.46, -13.52) * mm, "end": v(-21.14, -13.34) * mm});
            skLineSegment(sketch, "E7379", {"start": v(-21.14, -13.34) * mm, "end": v(-20.81, -13.13) * mm});
            skLineSegment(sketch, "E7380", {"start": v(-20.81, -13.13) * mm, "end": v(-20.5, -12.9) * mm});
            skLineSegment(sketch, "E7381", {"start": v(-20.5, -12.9) * mm, "end": v(-20.2, -12.65) * mm});
            skLineSegment(sketch, "E7382", {"start": v(-20.2, -12.65) * mm, "end": v(-19.92, -12.39) * mm});
            skLineSegment(sketch, "E7383", {"start": v(-19.92, -12.39) * mm, "end": v(-19.8, -12.25) * mm});
            skLineSegment(sketch, "E7384", {"start": v(-19.8, -12.25) * mm, "end": v(-19.68, -12.11) * mm});
            skLineSegment(sketch, "E7385", {"start": v(-19.68, -12.11) * mm, "end": v(-19.57, -11.97) * mm});
            skLineSegment(sketch, "E7386", {"start": v(-19.57, -11.97) * mm, "end": v(-19.48, -11.83) * mm});
            skLineSegment(sketch, "E7387", {"start": v(-19.48, -11.83) * mm, "end": v(-19.43, -11.73) * mm});
            skLineSegment(sketch, "E7388", {"start": v(-19.43, -11.73) * mm, "end": v(-19.4, -11.62) * mm});
            skLineSegment(sketch, "E7389", {"start": v(-19.4, -11.62) * mm, "end": v(-19.34, -11.37) * mm});
            skLineSegment(sketch, "E7390", {"start": v(-19.34, -11.37) * mm, "end": v(-19.31, -11.1) * mm});
            skLineSegment(sketch, "E7391", {"start": v(-19.31, -11.1) * mm, "end": v(-19.28, -10.87) * mm});
            skLineSegment(sketch, "E7392", {"start": v(-19.28, -10.87) * mm, "end": v(-19.22, -10.64) * mm});
            skLineSegment(sketch, "E7393", {"start": v(-19.22, -10.64) * mm, "end": v(-19.12, -10.36) * mm});
            skLineSegment(sketch, "E7394", {"start": v(-19.12, -10.36) * mm, "end": v(-19, -10.03) * mm});
            skLineSegment(sketch, "E7395", {"start": v(-19, -10.03) * mm, "end": v(-18.85, -9.66) * mm});
            skLineSegment(sketch, "E7396", {"start": v(-18.85, -9.66) * mm, "end": v(-18.69, -9.28) * mm});
            skLineSegment(sketch, "E7397", {"start": v(-18.69, -9.28) * mm, "end": v(-18.5, -8.88) * mm});
            skLineSegment(sketch, "E7398", {"start": v(-18.5, -8.88) * mm, "end": v(-18.31, -8.48) * mm});
            skLineSegment(sketch, "E7399", {"start": v(-18.31, -8.48) * mm, "end": v(-18.12, -8.1) * mm});
            skLineSegment(sketch, "E7400", {"start": v(-18.12, -8.1) * mm, "end": v(-17.66, -7.24) * mm});
            skLineSegment(sketch, "E7401", {"start": v(-17.66, -7.24) * mm, "end": v(-17.35, -6.6) * mm});
            skLineSegment(sketch, "E7402", {"start": v(-17.35, -6.6) * mm, "end": v(-17.24, -6.38) * mm});
            skLineSegment(sketch, "E7403", {"start": v(-17.24, -6.38) * mm, "end": v(-17.17, -6.2) * mm});
            skLineSegment(sketch, "E7404", {"start": v(-17.17, -6.2) * mm, "end": v(-17.13, -6.1) * mm});
            skLineSegment(sketch, "E7405", {"start": v(-17.13, -6.1) * mm, "end": v(-17.13, -6.05) * mm});
            skLineSegment(sketch, "E7406", {"start": v(-17.13, -6.05) * mm, "end": v(-17.13, -6.03) * mm});
            skLineSegment(sketch, "E7407", {"start": v(-17.13, -6.03) * mm, "end": v(-17.15, -6.02) * mm});
            skLineSegment(sketch, "E7408", {"start": v(-17.15, -6.02) * mm, "end": v(-17.17, -6.02) * mm});
            skLineSegment(sketch, "E7409", {"start": v(-17.17, -6.02) * mm, "end": v(-17.24, -6.06) * mm});
            skLineSegment(sketch, "E7410", {"start": v(-17.24, -6.06) * mm, "end": v(-17.35, -6.16) * mm});
            skLineSegment(sketch, "E7411", {"start": v(-17.35, -6.16) * mm, "end": v(-17.5, -6.3) * mm});
            skLineSegment(sketch, "E7412", {"start": v(-17.5, -6.3) * mm, "end": v(-17.91, -6.74) * mm});
            skLineSegment(sketch, "E7413", {"start": v(-17.91, -6.74) * mm, "end": v(-18.48, -7.37) * mm});
            skLineSegment(sketch, "E7414", {"start": v(-18.48, -7.37) * mm, "end": v(-18.84, -7.8) * mm});
            skLineSegment(sketch, "E7415", {"start": v(-18.84, -7.8) * mm, "end": v(-19.23, -8.28) * mm});
            skLineSegment(sketch, "E7416", {"start": v(-19.23, -8.28) * mm, "end": v(-19.43, -8.51) * mm});
            skLineSegment(sketch, "E7417", {"start": v(-19.43, -8.51) * mm, "end": v(-19.63, -8.73) * mm});
            skLineSegment(sketch, "E7418", {"start": v(-19.63, -8.73) * mm, "end": v(-19.83, -8.94) * mm});
            skLineSegment(sketch, "E7419", {"start": v(-19.83, -8.94) * mm, "end": v(-20.04, -9.12) * mm});
            skLineSegment(sketch, "E7420", {"start": v(-20.04, -9.12) * mm, "end": v(-20.21, -9.26) * mm});
            skLineSegment(sketch, "E7421", {"start": v(-20.21, -9.26) * mm, "end": v(-20.4, -9.4) * mm});
            skLineSegment(sketch, "E7422", {"start": v(-20.4, -9.4) * mm, "end": v(-20.79, -9.65) * mm});
            skLineSegment(sketch, "E7423", {"start": v(-20.79, -9.65) * mm, "end": v(-21.58, -10.12) * mm});
            skLineSegment(sketch, "E7424", {"start": v(-21.58, -10.12) * mm, "end": v(-21.93, -10.3) * mm});
            skLineSegment(sketch, "E7425", {"start": v(-21.93, -10.3) * mm, "end": v(-22.3, -10.48) * mm});
            skLineSegment(sketch, "E7426", {"start": v(-22.3, -10.48) * mm, "end": v(-22.65, -10.63) * mm});
            skLineSegment(sketch, "E7427", {"start": v(-22.65, -10.63) * mm, "end": v(-22.99, -10.76) * mm});
            skLineSegment(sketch, "E7428", {"start": v(-22.99, -10.76) * mm, "end": v(-23.56, -10.96) * mm});
            skLineSegment(sketch, "E7429", {"start": v(-23.56, -10.96) * mm, "end": v(-23.92, -11.06) * mm});
            skLineSegment(sketch, "E7430", {"start": v(-23.92, -11.06) * mm, "end": v(-24.27, -11.15) * mm});
            skLineSegment(sketch, "E7431", {"start": v(-24.27, -11.15) * mm, "end": v(-24.62, -11.22) * mm});
            skLineSegment(sketch, "E7432", {"start": v(-24.62, -11.22) * mm, "end": v(-24.97, -11.27) * mm});
            skLineSegment(sketch, "E7433", {"start": v(-24.97, -11.27) * mm, "end": v(-25.32, -11.3) * mm});
            skLineSegment(sketch, "E7434", {"start": v(-25.32, -11.3) * mm, "end": v(-26.07, -11.37) * mm});
            skLineSegment(sketch, "E7435", {"start": v(-26.07, -11.37) * mm, "end": v(-26.89, -11.44) * mm});
            skLineSegment(sketch, "E7436", {"start": v(74.86, 39.27) * mm, "end": v(75.4, 39.77) * mm});
            skLineSegment(sketch, "E7437", {"start": v(75.4, 39.77) * mm, "end": v(75.93, 40.25) * mm});
            skLineSegment(sketch, "E7438", {"start": v(75.93, 40.25) * mm, "end": v(76.42, 40.72) * mm});
            skLineSegment(sketch, "E7439", {"start": v(76.42, 40.72) * mm, "end": v(76.88, 41.18) * mm});
            skLineSegment(sketch, "E7440", {"start": v(76.88, 41.18) * mm, "end": v(77.31, 41.61) * mm});
            skLineSegment(sketch, "E7441", {"start": v(77.31, 41.61) * mm, "end": v(77.72, 42.04) * mm});
            skLineSegment(sketch, "E7442", {"start": v(77.72, 42.04) * mm, "end": v(78.46, 42.83) * mm});
            skLineSegment(sketch, "E7443", {"start": v(78.46, 42.83) * mm, "end": v(79.1, 43.56) * mm});
            skLineSegment(sketch, "E7444", {"start": v(79.1, 43.56) * mm, "end": v(79.67, 44.22) * mm});
            skLineSegment(sketch, "E7445", {"start": v(79.67, 44.22) * mm, "end": v(80.6, 45.35) * mm});
            skLineSegment(sketch, "E7446", {"start": v(80.6, 45.35) * mm, "end": v(81.09, 45.96) * mm});
            skLineSegment(sketch, "E7447", {"start": v(81.09, 45.96) * mm, "end": v(81.62, 46.66) * mm});
            skLineSegment(sketch, "E7448", {"start": v(81.62, 46.66) * mm, "end": v(82.1, 47.33) * mm});
            skLineSegment(sketch, "E7449", {"start": v(82.1, 47.33) * mm, "end": v(82.3, 47.62) * mm});
            skLineSegment(sketch, "E7450", {"start": v(82.3, 47.62) * mm, "end": v(82.44, 47.87) * mm});
            skLineSegment(sketch, "E7451", {"start": v(82.44, 47.87) * mm, "end": v(82.75, 48.42) * mm});
            skLineSegment(sketch, "E7452", {"start": v(82.75, 48.42) * mm, "end": v(83.02, 48.93) * mm});
            skLineSegment(sketch, "E7453", {"start": v(83.02, 48.93) * mm, "end": v(83.26, 49.41) * mm});
            skLineSegment(sketch, "E7454", {"start": v(83.26, 49.41) * mm, "end": v(83.46, 49.87) * mm});
            skLineSegment(sketch, "E7455", {"start": v(83.46, 49.87) * mm, "end": v(83.63, 50.3) * mm});
            skLineSegment(sketch, "E7456", {"start": v(83.63, 50.3) * mm, "end": v(83.77, 50.7) * mm});
            skLineSegment(sketch, "E7457", {"start": v(83.77, 50.7) * mm, "end": v(83.89, 51.08) * mm});
            skLineSegment(sketch, "E7458", {"start": v(83.89, 51.08) * mm, "end": v(83.99, 51.44) * mm});
            skLineSegment(sketch, "E7459", {"start": v(83.99, 51.44) * mm, "end": v(84.06, 51.8) * mm});
            skLineSegment(sketch, "E7460", {"start": v(84.06, 51.8) * mm, "end": v(84.12, 52.14) * mm});
            skLineSegment(sketch, "E7461", {"start": v(84.12, 52.14) * mm, "end": v(84.17, 52.48) * mm});
            skLineSegment(sketch, "E7462", {"start": v(84.17, 52.48) * mm, "end": v(84.2, 52.8) * mm});
            skLineSegment(sketch, "E7463", {"start": v(84.2, 52.8) * mm, "end": v(84.26, 53.48) * mm});
            skLineSegment(sketch, "E7464", {"start": v(84.26, 53.48) * mm, "end": v(84.3, 54.18) * mm});
            skLineSegment(sketch, "E7465", {"start": v(84.3, 54.18) * mm, "end": v(84.32, 54.75) * mm});
            skLineSegment(sketch, "E7466", {"start": v(84.32, 54.75) * mm, "end": v(84.33, 55.34) * mm});
            skLineSegment(sketch, "E7467", {"start": v(84.33, 55.34) * mm, "end": v(84.33, 55.95) * mm});
            skLineSegment(sketch, "E7468", {"start": v(84.33, 55.95) * mm, "end": v(84.3, 56.57) * mm});
            skLineSegment(sketch, "E7469", {"start": v(84.3, 56.57) * mm, "end": v(84.26, 57.19) * mm});
            skLineSegment(sketch, "E7470", {"start": v(84.26, 57.19) * mm, "end": v(84.19, 57.8) * mm});
            skLineSegment(sketch, "E7471", {"start": v(84.19, 57.8) * mm, "end": v(84.1, 58.37) * mm});
            skLineSegment(sketch, "E7472", {"start": v(84.1, 58.37) * mm, "end": v(84.04, 58.65) * mm});
            skLineSegment(sketch, "E7473", {"start": v(84.04, 58.65) * mm, "end": v(83.98, 58.92) * mm});
            skLineSegment(sketch, "E7474", {"start": v(83.98, 58.92) * mm, "end": v(83.92, 59.16) * mm});
            skLineSegment(sketch, "E7475", {"start": v(83.92, 59.16) * mm, "end": v(83.84, 59.4) * mm});
            skLineSegment(sketch, "E7476", {"start": v(83.84, 59.4) * mm, "end": v(83.74, 59.67) * mm});
            skLineSegment(sketch, "E7477", {"start": v(83.74, 59.67) * mm, "end": v(83.62, 59.92) * mm});
            skLineSegment(sketch, "E7478", {"start": v(83.62, 59.92) * mm, "end": v(83.5, 60.17) * mm});
            skLineSegment(sketch, "E7479", {"start": v(83.5, 60.17) * mm, "end": v(83.35, 60.4) * mm});
            skLineSegment(sketch, "E7480", {"start": v(83.35, 60.4) * mm, "end": v(83.19, 60.6) * mm});
            skLineSegment(sketch, "E7481", {"start": v(83.19, 60.6) * mm, "end": v(83.1, 60.7) * mm});
            skLineSegment(sketch, "E7482", {"start": v(83.1, 60.7) * mm, "end": v(83.02, 60.79) * mm});
            skLineSegment(sketch, "E7483", {"start": v(83.02, 60.79) * mm, "end": v(82.96, 60.82) * mm});
            skLineSegment(sketch, "E7484", {"start": v(82.96, 60.82) * mm, "end": v(82.9, 60.86) * mm});
            skLineSegment(sketch, "E7485", {"start": v(82.9, 60.86) * mm, "end": v(82.76, 60.9) * mm});
            skLineSegment(sketch, "E7486", {"start": v(82.76, 60.9) * mm, "end": v(82.62, 60.95) * mm});
            skLineSegment(sketch, "E7487", {"start": v(82.62, 60.95) * mm, "end": v(82.48, 61) * mm});
            skLineSegment(sketch, "E7488", {"start": v(82.48, 61) * mm, "end": v(82.36, 61.03) * mm});
            skLineSegment(sketch, "E7489", {"start": v(82.36, 61.03) * mm, "end": v(82.2, 61.07) * mm});
            skLineSegment(sketch, "E7490", {"start": v(82.2, 61.07) * mm, "end": v(81.86, 61.14) * mm});
            skLineSegment(sketch, "E7491", {"start": v(81.86, 61.14) * mm, "end": v(81.48, 61.18) * mm});
            skLineSegment(sketch, "E7492", {"start": v(81.48, 61.18) * mm, "end": v(81.1, 61.2) * mm});
            skLineSegment(sketch, "E7493", {"start": v(81.1, 61.2) * mm, "end": v(80.9, 61.2) * mm});
            skLineSegment(sketch, "E7494", {"start": v(80.9, 61.2) * mm, "end": v(80.69, 61.22) * mm});
            skLineSegment(sketch, "E7495", {"start": v(80.69, 61.22) * mm, "end": v(80.47, 61.22) * mm});
            skLineSegment(sketch, "E7496", {"start": v(80.47, 61.22) * mm, "end": v(80.36, 61.21) * mm});
            skLineSegment(sketch, "E7497", {"start": v(80.36, 61.21) * mm, "end": v(80.27, 61.2) * mm});
            skLineSegment(sketch, "E7498", {"start": v(80.27, 61.2) * mm, "end": v(79.37, 60.96) * mm});
            skLineSegment(sketch, "E7499", {"start": v(79.37, 60.96) * mm, "end": v(78.9, 60.83) * mm});
            skLineSegment(sketch, "E7500", {"start": v(78.9, 60.83) * mm, "end": v(78.44, 60.67) * mm});
            skLineSegment(sketch, "E7501", {"start": v(78.44, 60.67) * mm, "end": v(78.21, 60.59) * mm});
            skLineSegment(sketch, "E7502", {"start": v(78.21, 60.59) * mm, "end": v(77.99, 60.5) * mm});
            skLineSegment(sketch, "E7503", {"start": v(77.99, 60.5) * mm, "end": v(77.77, 60.4) * mm});
            skLineSegment(sketch, "E7504", {"start": v(77.77, 60.4) * mm, "end": v(77.57, 60.29) * mm});
            skLineSegment(sketch, "E7505", {"start": v(77.57, 60.29) * mm, "end": v(77.37, 60.17) * mm});
            skLineSegment(sketch, "E7506", {"start": v(77.37, 60.17) * mm, "end": v(77.18, 60.04) * mm});
            skLineSegment(sketch, "E7507", {"start": v(77.18, 60.04) * mm, "end": v(77, 59.9) * mm});
            skLineSegment(sketch, "E7508", {"start": v(77, 59.9) * mm, "end": v(76.84, 59.75) * mm});
            skLineSegment(sketch, "E7509", {"start": v(76.84, 59.75) * mm, "end": v(76.02, 58.94) * mm});
            skLineSegment(sketch, "E7510", {"start": v(76.02, 58.94) * mm, "end": v(75.64, 58.53) * mm});
            skLineSegment(sketch, "E7511", {"start": v(75.64, 58.53) * mm, "end": v(75.27, 58.11) * mm});
            skLineSegment(sketch, "E7512", {"start": v(75.27, 58.11) * mm, "end": v(74.91, 57.69) * mm});
            skLineSegment(sketch, "E7513", {"start": v(74.91, 57.69) * mm, "end": v(74.58, 57.24) * mm});
            skLineSegment(sketch, "E7514", {"start": v(74.58, 57.24) * mm, "end": v(74.42, 57) * mm});
            skLineSegment(sketch, "E7515", {"start": v(74.42, 57) * mm, "end": v(74.26, 56.77) * mm});
            skLineSegment(sketch, "E7516", {"start": v(74.26, 56.77) * mm, "end": v(74.11, 56.52) * mm});
            skLineSegment(sketch, "E7517", {"start": v(74.11, 56.52) * mm, "end": v(73.97, 56.26) * mm});
            skLineSegment(sketch, "E7518", {"start": v(73.97, 56.26) * mm, "end": v(73.7, 55.79) * mm});
            skLineSegment(sketch, "E7519", {"start": v(73.7, 55.79) * mm, "end": v(73.38, 55.26) * mm});
            skLineSegment(sketch, "E7520", {"start": v(73.38, 55.26) * mm, "end": v(73.02, 54.68) * mm});
            skLineSegment(sketch, "E7521", {"start": v(73.02, 54.68) * mm, "end": v(72.62, 54.06) * mm});
            skLineSegment(sketch, "E7522", {"start": v(72.62, 54.06) * mm, "end": v(72.2, 53.4) * mm});
            skLineSegment(sketch, "E7523", {"start": v(72.2, 53.4) * mm, "end": v(71.73, 52.74) * mm});
            skLineSegment(sketch, "E7524", {"start": v(71.73, 52.74) * mm, "end": v(71.26, 52.06) * mm});
            skLineSegment(sketch, "E7525", {"start": v(71.26, 52.06) * mm, "end": v(70.77, 51.38) * mm});
            skLineSegment(sketch, "E7526", {"start": v(70.77, 51.38) * mm, "end": v(70.27, 50.7) * mm});
            skLineSegment(sketch, "E7527", {"start": v(70.27, 50.7) * mm, "end": v(69.78, 50.05) * mm});
            skLineSegment(sketch, "E7528", {"start": v(69.78, 50.05) * mm, "end": v(69.28, 49.43) * mm});
            skLineSegment(sketch, "E7529", {"start": v(69.28, 49.43) * mm, "end": v(68.8, 48.83) * mm});
            skLineSegment(sketch, "E7530", {"start": v(68.8, 48.83) * mm, "end": v(68.34, 48.29) * mm});
            skLineSegment(sketch, "E7531", {"start": v(68.34, 48.29) * mm, "end": v(67.9, 47.8) * mm});
            skLineSegment(sketch, "E7532", {"start": v(67.9, 47.8) * mm, "end": v(67.5, 47.37) * mm});
            skLineSegment(sketch, "E7533", {"start": v(67.5, 47.37) * mm, "end": v(67.12, 47.01) * mm});
            skLineSegment(sketch, "E7534", {"start": v(67.12, 47.01) * mm, "end": v(67.51, 46.42) * mm});
            skLineSegment(sketch, "E7535", {"start": v(67.51, 46.42) * mm, "end": v(67.92, 45.77) * mm});
            skLineSegment(sketch, "E7536", {"start": v(67.92, 45.77) * mm, "end": v(68.87, 44.2) * mm});
            skLineSegment(sketch, "E7537", {"start": v(68.87, 44.2) * mm, "end": v(68.98, 44) * mm});
            skLineSegment(sketch, "E7538", {"start": v(68.98, 44) * mm, "end": v(69.08, 43.8) * mm});
            skLineSegment(sketch, "E7539", {"start": v(69.08, 43.8) * mm, "end": v(69.36, 43.25) * mm});
            skLineSegment(sketch, "E7540", {"start": v(69.36, 43.25) * mm, "end": v(69.65, 42.64) * mm});
            skLineSegment(sketch, "E7541", {"start": v(69.65, 42.64) * mm, "end": v(69.93, 42.04) * mm});
            skLineSegment(sketch, "E7542", {"start": v(69.93, 42.04) * mm, "end": v(70.18, 41.47) * mm});
            skLineSegment(sketch, "E7543", {"start": v(70.18, 41.47) * mm, "end": v(70.32, 41.12) * mm});
            skLineSegment(sketch, "E7544", {"start": v(70.32, 41.12) * mm, "end": v(70.4, 40.91) * mm});
            skLineSegment(sketch, "E7545", {"start": v(70.4, 40.91) * mm, "end": v(70.47, 40.7) * mm});
            skLineSegment(sketch, "E7546", {"start": v(70.47, 40.7) * mm, "end": v(70.58, 40.32) * mm});
            skLineSegment(sketch, "E7547", {"start": v(70.58, 40.32) * mm, "end": v(70.67, 39.96) * mm});
            skLineSegment(sketch, "E7548", {"start": v(70.67, 39.96) * mm, "end": v(70.7, 39.8) * mm});
            skLineSegment(sketch, "E7549", {"start": v(70.7, 39.8) * mm, "end": v(70.75, 39.69) * mm});
            skLineSegment(sketch, "E7550", {"start": v(70.75, 39.69) * mm, "end": v(70.8, 39.6) * mm});
            skLineSegment(sketch, "E7551", {"start": v(70.8, 39.6) * mm, "end": v(70.82, 39.57) * mm});
            skLineSegment(sketch, "E7552", {"start": v(70.82, 39.57) * mm, "end": v(70.84, 39.56) * mm});
            skLineSegment(sketch, "E7553", {"start": v(70.84, 39.56) * mm, "end": v(70.86, 39.55) * mm});
            skLineSegment(sketch, "E7554", {"start": v(70.86, 39.55) * mm, "end": v(70.89, 39.55) * mm});
            skLineSegment(sketch, "E7555", {"start": v(70.89, 39.55) * mm, "end": v(70.93, 39.58) * mm});
            skLineSegment(sketch, "E7556", {"start": v(70.93, 39.58) * mm, "end": v(70.98, 39.63) * mm});
            skLineSegment(sketch, "E7557", {"start": v(70.98, 39.63) * mm, "end": v(71.03, 39.7) * mm});
            skLineSegment(sketch, "E7558", {"start": v(71.03, 39.7) * mm, "end": v(71.13, 39.86) * mm});
            skLineSegment(sketch, "E7559", {"start": v(71.13, 39.86) * mm, "end": v(71.18, 39.94) * mm});
            skLineSegment(sketch, "E7560", {"start": v(71.18, 39.94) * mm, "end": v(71.24, 40) * mm});
            skLineSegment(sketch, "E7561", {"start": v(71.24, 40) * mm, "end": v(71.34, 40.1) * mm});
            skLineSegment(sketch, "E7562", {"start": v(71.34, 40.1) * mm, "end": v(71.45, 40.18) * mm});
            skLineSegment(sketch, "E7563", {"start": v(71.45, 40.18) * mm, "end": v(71.69, 40.33) * mm});
            skLineSegment(sketch, "E7564", {"start": v(71.69, 40.33) * mm, "end": v(71.93, 40.47) * mm});
            skLineSegment(sketch, "E7565", {"start": v(71.93, 40.47) * mm, "end": v(72.14, 40.57) * mm});
            skLineSegment(sketch, "E7566", {"start": v(72.14, 40.57) * mm, "end": v(72.33, 40.63) * mm});
            skLineSegment(sketch, "E7567", {"start": v(72.33, 40.63) * mm, "end": v(72.55, 40.69) * mm});
            skLineSegment(sketch, "E7568", {"start": v(72.55, 40.69) * mm, "end": v(72.78, 40.72) * mm});
            skLineSegment(sketch, "E7569", {"start": v(72.78, 40.72) * mm, "end": v(72.88, 40.73) * mm});
            skLineSegment(sketch, "E7570", {"start": v(72.88, 40.73) * mm, "end": v(72.98, 40.72) * mm});
            skLineSegment(sketch, "E7571", {"start": v(72.98, 40.72) * mm, "end": v(73.18, 40.7) * mm});
            skLineSegment(sketch, "E7572", {"start": v(73.18, 40.7) * mm, "end": v(73.3, 40.68) * mm});
            skLineSegment(sketch, "E7573", {"start": v(73.3, 40.68) * mm, "end": v(73.4, 40.65) * mm});
            skLineSegment(sketch, "E7574", {"start": v(73.4, 40.65) * mm, "end": v(73.5, 40.62) * mm});
            skLineSegment(sketch, "E7575", {"start": v(73.5, 40.62) * mm, "end": v(73.58, 40.57) * mm});
            skLineSegment(sketch, "E7576", {"start": v(73.58, 40.57) * mm, "end": v(73.74, 40.48) * mm});
            skLineSegment(sketch, "E7577", {"start": v(73.74, 40.48) * mm, "end": v(73.9, 40.36) * mm});
            skLineSegment(sketch, "E7578", {"start": v(73.9, 40.36) * mm, "end": v(74.05, 40.23) * mm});
            skLineSegment(sketch, "E7579", {"start": v(74.05, 40.23) * mm, "end": v(74.2, 40.08) * mm});
            skLineSegment(sketch, "E7580", {"start": v(74.2, 40.08) * mm, "end": v(74.35, 39.92) * mm});
            skLineSegment(sketch, "E7581", {"start": v(74.35, 39.92) * mm, "end": v(74.63, 39.59) * mm});
            skLineSegment(sketch, "E7582", {"start": v(74.63, 39.59) * mm, "end": v(74.86, 39.27) * mm});
            skLineSegment(sketch, "E7583", {"start": v(-84.43, 17.2) * mm, "end": v(-84.38, 17.47) * mm});
            skLineSegment(sketch, "E7584", {"start": v(-84.38, 17.47) * mm, "end": v(-84.15, 18.36) * mm});
            skLineSegment(sketch, "E7585", {"start": v(-84.15, 18.36) * mm, "end": v(-83.87, 19.26) * mm});
            skLineSegment(sketch, "E7586", {"start": v(-83.87, 19.26) * mm, "end": v(-83.76, 19.55) * mm});
            skLineSegment(sketch, "E7587", {"start": v(-83.76, 19.55) * mm, "end": v(-83.59, 19.88) * mm});
            skLineSegment(sketch, "E7588", {"start": v(-83.59, 19.88) * mm, "end": v(-83.2, 20.6) * mm});
            skLineSegment(sketch, "E7589", {"start": v(-83.2, 20.6) * mm, "end": v(-82.77, 21.29) * mm});
            skLineSegment(sketch, "E7590", {"start": v(-82.77, 21.29) * mm, "end": v(-82.42, 21.8) * mm});
            skLineSegment(sketch, "E7591", {"start": v(-82.42, 21.8) * mm, "end": v(-82.25, 22.02) * mm});
            skLineSegment(sketch, "E7592", {"start": v(-82.25, 22.02) * mm, "end": v(-82.08, 22.22) * mm});
            skLineSegment(sketch, "E7593", {"start": v(-82.08, 22.22) * mm, "end": v(-81.72, 22.58) * mm});
            skLineSegment(sketch, "E7594", {"start": v(-81.72, 22.58) * mm, "end": v(-81.36, 22.9) * mm});
            skLineSegment(sketch, "E7595", {"start": v(-81.36, 22.9) * mm, "end": v(-81.16, 23.07) * mm});
            skLineSegment(sketch, "E7596", {"start": v(-81.16, 23.07) * mm, "end": v(-82.16, 23.62) * mm});
            skLineSegment(sketch, "E7597", {"start": v(-82.16, 23.62) * mm, "end": v(-83.12, 24.18) * mm});
            skLineSegment(sketch, "E7598", {"start": v(-83.12, 24.18) * mm, "end": v(-84.03, 24.73) * mm});
            skLineSegment(sketch, "E7599", {"start": v(-84.03, 24.73) * mm, "end": v(-84.9, 25.28) * mm});
            skLineSegment(sketch, "E7600", {"start": v(-84.9, 25.28) * mm, "end": v(-85.74, 25.83) * mm});
            skLineSegment(sketch, "E7601", {"start": v(-85.74, 25.83) * mm, "end": v(-86.54, 26.4) * mm});
            skLineSegment(sketch, "E7602", {"start": v(-86.54, 26.4) * mm, "end": v(-87.31, 26.95) * mm});
            skLineSegment(sketch, "E7603", {"start": v(-87.31, 26.95) * mm, "end": v(-88.05, 27.52) * mm});
            skLineSegment(sketch, "E7604", {"start": v(-88.05, 27.52) * mm, "end": v(-88.77, 28.09) * mm});
            skLineSegment(sketch, "E7605", {"start": v(-88.77, 28.09) * mm, "end": v(-89.46, 28.66) * mm});
            skLineSegment(sketch, "E7606", {"start": v(-89.46, 28.66) * mm, "end": v(-90.12, 29.25) * mm});
            skLineSegment(sketch, "E7607", {"start": v(-90.12, 29.25) * mm, "end": v(-90.77, 29.84) * mm});
            skLineSegment(sketch, "E7608", {"start": v(-90.77, 29.84) * mm, "end": v(-91.4, 30.44) * mm});
            skLineSegment(sketch, "E7609", {"start": v(-91.4, 30.44) * mm, "end": v(-92.02, 31.05) * mm});
            skLineSegment(sketch, "E7610", {"start": v(-92.02, 31.05) * mm, "end": v(-92.63, 31.67) * mm});
            skLineSegment(sketch, "E7611", {"start": v(-92.63, 31.67) * mm, "end": v(-93.23, 32.3) * mm});
            skLineSegment(sketch, "E7612", {"start": v(-93.23, 32.3) * mm, "end": v(-93.8, 31.96) * mm});
            skLineSegment(sketch, "E7613", {"start": v(-93.8, 31.96) * mm, "end": v(-93.93, 31.87) * mm});
            skLineSegment(sketch, "E7614", {"start": v(-93.93, 31.87) * mm, "end": v(-94.06, 31.73) * mm});
            skLineSegment(sketch, "E7615", {"start": v(-94.06, 31.73) * mm, "end": v(-94.21, 31.57) * mm});
            skLineSegment(sketch, "E7616", {"start": v(-94.21, 31.57) * mm, "end": v(-94.36, 31.38) * mm});
            skLineSegment(sketch, "E7617", {"start": v(-94.36, 31.38) * mm, "end": v(-94.68, 30.94) * mm});
            skLineSegment(sketch, "E7618", {"start": v(-94.68, 30.94) * mm, "end": v(-94.98, 30.5) * mm});
            skLineSegment(sketch, "E7619", {"start": v(-94.98, 30.5) * mm, "end": v(-95.15, 30.23) * mm});
            skLineSegment(sketch, "E7620", {"start": v(-95.15, 30.23) * mm, "end": v(-95.32, 29.94) * mm});
            skLineSegment(sketch, "E7621", {"start": v(-95.32, 29.94) * mm, "end": v(-95.4, 29.79) * mm});
            skLineSegment(sketch, "E7622", {"start": v(-95.4, 29.79) * mm, "end": v(-95.47, 29.64) * mm});
            skLineSegment(sketch, "E7623", {"start": v(-95.47, 29.64) * mm, "end": v(-95.52, 29.5) * mm});
            skLineSegment(sketch, "E7624", {"start": v(-95.52, 29.5) * mm, "end": v(-95.56, 29.35) * mm});
            skLineSegment(sketch, "E7625", {"start": v(-95.56, 29.35) * mm, "end": v(-95.6, 29.16) * mm});
            skLineSegment(sketch, "E7626", {"start": v(-95.6, 29.16) * mm, "end": v(-95.62, 28.97) * mm});
            skLineSegment(sketch, "E7627", {"start": v(-95.62, 28.97) * mm, "end": v(-95.64, 28.76) * mm});
            skLineSegment(sketch, "E7628", {"start": v(-95.64, 28.76) * mm, "end": v(-95.65, 28.55) * mm});
            skLineSegment(sketch, "E7629", {"start": v(-95.65, 28.55) * mm, "end": v(-95.65, 28.12) * mm});
            skLineSegment(sketch, "E7630", {"start": v(-95.65, 28.12) * mm, "end": v(-95.62, 27.68) * mm});
            skLineSegment(sketch, "E7631", {"start": v(-95.62, 27.68) * mm, "end": v(-95.57, 27.24) * mm});
            skLineSegment(sketch, "E7632", {"start": v(-95.57, 27.24) * mm, "end": v(-95.5, 26.8) * mm});
            skLineSegment(sketch, "E7633", {"start": v(-95.5, 26.8) * mm, "end": v(-95.42, 26.4) * mm});
            skLineSegment(sketch, "E7634", {"start": v(-95.42, 26.4) * mm, "end": v(-95.31, 26.02) * mm});
            skLineSegment(sketch, "E7635", {"start": v(-95.31, 26.02) * mm, "end": v(-95.2, 25.67) * mm});
            skLineSegment(sketch, "E7636", {"start": v(-95.2, 25.67) * mm, "end": v(-95.04, 25.3) * mm});
            skLineSegment(sketch, "E7637", {"start": v(-95.04, 25.3) * mm, "end": v(-94.86, 24.93) * mm});
            skLineSegment(sketch, "E7638", {"start": v(-94.86, 24.93) * mm, "end": v(-94.66, 24.57) * mm});
            skLineSegment(sketch, "E7639", {"start": v(-94.66, 24.57) * mm, "end": v(-94.44, 24.2) * mm});
            skLineSegment(sketch, "E7640", {"start": v(-94.44, 24.2) * mm, "end": v(-94.2, 23.86) * mm});
            skLineSegment(sketch, "E7641", {"start": v(-94.2, 23.86) * mm, "end": v(-93.98, 23.54) * mm});
            skLineSegment(sketch, "E7642", {"start": v(-93.98, 23.54) * mm, "end": v(-93.75, 23.25) * mm});
            skLineSegment(sketch, "E7643", {"start": v(-93.75, 23.25) * mm, "end": v(-93.56, 23.04) * mm});
            skLineSegment(sketch, "E7644", {"start": v(-93.56, 23.04) * mm, "end": v(-93.34, 22.83) * mm});
            skLineSegment(sketch, "E7645", {"start": v(-93.34, 22.83) * mm, "end": v(-93.1, 22.62) * mm});
            skLineSegment(sketch, "E7646", {"start": v(-93.1, 22.62) * mm, "end": v(-92.85, 22.42) * mm});
            skLineSegment(sketch, "E7647", {"start": v(-92.85, 22.42) * mm, "end": v(-92.35, 22.03) * mm});
            skLineSegment(sketch, "E7648", {"start": v(-92.35, 22.03) * mm, "end": v(-91.87, 21.68) * mm});
            skLineSegment(sketch, "E7649", {"start": v(-91.87, 21.68) * mm, "end": v(-91.42, 21.34) * mm});
            skLineSegment(sketch, "E7650", {"start": v(-91.42, 21.34) * mm, "end": v(-90.94, 21) * mm});
            skLineSegment(sketch, "E7651", {"start": v(-90.94, 21) * mm, "end": v(-89.9, 20.3) * mm});
            skLineSegment(sketch, "E7652", {"start": v(-89.9, 20.3) * mm, "end": v(-88.86, 19.62) * mm});
            skLineSegment(sketch, "E7653", {"start": v(-88.86, 19.62) * mm, "end": v(-87.88, 19) * mm});
            skLineSegment(sketch, "E7654", {"start": v(-87.88, 19) * mm, "end": v(-87.43, 18.7) * mm});
            skLineSegment(sketch, "E7655", {"start": v(-87.43, 18.7) * mm, "end": v(-87.13, 18.5) * mm});
            skLineSegment(sketch, "E7656", {"start": v(-87.13, 18.5) * mm, "end": v(-86.82, 18.3) * mm});
            skLineSegment(sketch, "E7657", {"start": v(-86.82, 18.3) * mm, "end": v(-86.47, 18.11) * mm});
            skLineSegment(sketch, "E7658", {"start": v(-86.47, 18.11) * mm, "end": v(-86.12, 17.92) * mm});
            skLineSegment(sketch, "E7659", {"start": v(-86.12, 17.92) * mm, "end": v(-85.7, 17.7) * mm});
            skLineSegment(sketch, "E7660", {"start": v(-85.7, 17.7) * mm, "end": v(-85.3, 17.49) * mm});
            skLineSegment(sketch, "E7661", {"start": v(-85.3, 17.49) * mm, "end": v(-84.96, 17.32) * mm});
            skLineSegment(sketch, "E7662", {"start": v(-84.96, 17.32) * mm, "end": v(-84.68, 17.2) * mm});
            skLineSegment(sketch, "E7663", {"start": v(-84.68, 17.2) * mm, "end": v(-84.53, 17.16) * mm});
            skLineSegment(sketch, "E7664", {"start": v(-84.53, 17.16) * mm, "end": v(-84.47, 17.16) * mm});
            skLineSegment(sketch, "E7665", {"start": v(-84.47, 17.16) * mm, "end": v(-84.45, 17.18) * mm});
            skLineSegment(sketch, "E7666", {"start": v(-84.45, 17.18) * mm, "end": v(-84.43, 17.2) * mm});
            skLineSegment(sketch, "E7667", {"start": v(-74.25, 39.19) * mm, "end": v(-74.3, 39.15) * mm});
            skLineSegment(sketch, "E7668", {"start": v(-74.3, 39.15) * mm, "end": v(-74.5, 38.98) * mm});
            skLineSegment(sketch, "E7669", {"start": v(-74.5, 38.98) * mm, "end": v(-74.67, 38.8) * mm});
            skLineSegment(sketch, "E7670", {"start": v(-74.67, 38.8) * mm, "end": v(-74.95, 38.48) * mm});
            skLineSegment(sketch, "E7671", {"start": v(-74.95, 38.48) * mm, "end": v(-75.2, 38.2) * mm});
            skLineSegment(sketch, "E7672", {"start": v(-75.2, 38.2) * mm, "end": v(-75.35, 38) * mm});
            skLineSegment(sketch, "E7673", {"start": v(-75.35, 38) * mm, "end": v(-75.51, 37.77) * mm});
            skLineSegment(sketch, "E7674", {"start": v(-75.51, 37.77) * mm, "end": v(-75.84, 37.28) * mm});
            skLineSegment(sketch, "E7675", {"start": v(-75.84, 37.28) * mm, "end": v(-76.16, 36.7) * mm});
            skLineSegment(sketch, "E7676", {"start": v(-76.16, 36.7) * mm, "end": v(-76.5, 36.07) * mm});
            skLineSegment(sketch, "E7677", {"start": v(-76.5, 36.07) * mm, "end": v(-76.53, 36) * mm});
            skLineSegment(sketch, "E7678", {"start": v(-76.53, 36) * mm, "end": v(-76.85, 35.43) * mm});
            skLineSegment(sketch, "E7679", {"start": v(-76.85, 35.43) * mm, "end": v(-76.98, 35.16) * mm});
            skLineSegment(sketch, "E7680", {"start": v(-76.98, 35.16) * mm, "end": v(-77.1, 34.9) * mm});
            skLineSegment(sketch, "E7681", {"start": v(-77.1, 34.9) * mm, "end": v(-77.46, 34) * mm});
            skLineSegment(sketch, "E7682", {"start": v(-77.46, 34) * mm, "end": v(-77.74, 33.29) * mm});
            skLineSegment(sketch, "E7683", {"start": v(-77.74, 33.29) * mm, "end": v(-77.92, 32.82) * mm});
            skLineSegment(sketch, "E7684", {"start": v(-77.92, 32.82) * mm, "end": v(-77.98, 32.7) * mm});
            skLineSegment(sketch, "E7685", {"start": v(-77.98, 32.7) * mm, "end": v(-78, 32.66) * mm});
            skLineSegment(sketch, "E7686", {"start": v(-78, 32.66) * mm, "end": v(-78.01, 32.65) * mm});
            skLineSegment(sketch, "E7687", {"start": v(-78.01, 32.65) * mm, "end": v(-79.39, 33.63) * mm});
            skLineSegment(sketch, "E7688", {"start": v(-79.39, 33.63) * mm, "end": v(-80.06, 34.12) * mm});
            skLineSegment(sketch, "E7689", {"start": v(-80.06, 34.12) * mm, "end": v(-80.72, 34.62) * mm});
            skLineSegment(sketch, "E7690", {"start": v(-80.72, 34.62) * mm, "end": v(-81.38, 35.13) * mm});
            skLineSegment(sketch, "E7691", {"start": v(-81.38, 35.13) * mm, "end": v(-82.04, 35.64) * mm});
            skLineSegment(sketch, "E7692", {"start": v(-82.04, 35.64) * mm, "end": v(-82.7, 36.17) * mm});
            skLineSegment(sketch, "E7693", {"start": v(-82.7, 36.17) * mm, "end": v(-83.34, 36.7) * mm});
            skLineSegment(sketch, "E7694", {"start": v(-83.34, 36.7) * mm, "end": v(-84, 37.26) * mm});
            skLineSegment(sketch, "E7695", {"start": v(-84, 37.26) * mm, "end": v(-84.64, 37.83) * mm});
            skLineSegment(sketch, "E7696", {"start": v(-84.64, 37.83) * mm, "end": v(-85.3, 38.4) * mm});
            skLineSegment(sketch, "E7697", {"start": v(-85.3, 38.4) * mm, "end": v(-85.94, 39.01) * mm});
            skLineSegment(sketch, "E7698", {"start": v(-85.94, 39.01) * mm, "end": v(-86.6, 39.63) * mm});
            skLineSegment(sketch, "E7699", {"start": v(-86.6, 39.63) * mm, "end": v(-87.26, 40.27) * mm});
            skLineSegment(sketch, "E7700", {"start": v(-87.26, 40.27) * mm, "end": v(-87.92, 40.94) * mm});
            skLineSegment(sketch, "E7701", {"start": v(-87.92, 40.94) * mm, "end": v(-88.59, 41.63) * mm});
            skLineSegment(sketch, "E7702", {"start": v(-88.59, 41.63) * mm, "end": v(-88.7, 41.8) * mm});
            skLineSegment(sketch, "E7703", {"start": v(-88.7, 41.8) * mm, "end": v(-88.8, 41.99) * mm});
            skLineSegment(sketch, "E7704", {"start": v(-88.8, 41.99) * mm, "end": v(-89.02, 42.42) * mm});
            skLineSegment(sketch, "E7705", {"start": v(-89.02, 42.42) * mm, "end": v(-89.24, 42.82) * mm});
            skLineSegment(sketch, "E7706", {"start": v(-89.24, 42.82) * mm, "end": v(-89.33, 43.01) * mm});
            skLineSegment(sketch, "E7707", {"start": v(-89.33, 43.01) * mm, "end": v(-89.4, 43.2) * mm});
            skLineSegment(sketch, "E7708", {"start": v(-89.4, 43.2) * mm, "end": v(-89.67, 44.03) * mm});
            skLineSegment(sketch, "E7709", {"start": v(-89.67, 44.03) * mm, "end": v(-89.91, 44.92) * mm});
            skLineSegment(sketch, "E7710", {"start": v(-89.91, 44.92) * mm, "end": v(-90.14, 45.83) * mm});
            skLineSegment(sketch, "E7711", {"start": v(-90.14, 45.83) * mm, "end": v(-90.35, 46.77) * mm});
            skLineSegment(sketch, "E7712", {"start": v(-90.35, 46.77) * mm, "end": v(-90.53, 47.7) * mm});
            skLineSegment(sketch, "E7713", {"start": v(-90.53, 47.7) * mm, "end": v(-90.69, 48.63) * mm});
            skLineSegment(sketch, "E7714", {"start": v(-90.69, 48.63) * mm, "end": v(-90.81, 49.54) * mm});
            skLineSegment(sketch, "E7715", {"start": v(-90.81, 49.54) * mm, "end": v(-90.9, 50.42) * mm});
            skLineSegment(sketch, "E7716", {"start": v(-90.9, 50.42) * mm, "end": v(-90.98, 51.24) * mm});
            skLineSegment(sketch, "E7717", {"start": v(-90.98, 51.24) * mm, "end": v(-91.02, 51.68) * mm});
            skLineSegment(sketch, "E7718", {"start": v(-91.02, 51.68) * mm, "end": v(-91.05, 52.12) * mm});
            skLineSegment(sketch, "E7719", {"start": v(-91.05, 52.12) * mm, "end": v(-91.06, 52.57) * mm});
            skLineSegment(sketch, "E7720", {"start": v(-91.06, 52.57) * mm, "end": v(-91.06, 52.78) * mm});
            skLineSegment(sketch, "E7721", {"start": v(-91.06, 52.78) * mm, "end": v(-91.04, 53) * mm});
            skLineSegment(sketch, "E7722", {"start": v(-91.04, 53) * mm, "end": v(-91.02, 53.2) * mm});
            skLineSegment(sketch, "E7723", {"start": v(-91.02, 53.2) * mm, "end": v(-91, 53.4) * mm});
            skLineSegment(sketch, "E7724", {"start": v(-91, 53.4) * mm, "end": v(-90.95, 53.6) * mm});
            skLineSegment(sketch, "E7725", {"start": v(-90.95, 53.6) * mm, "end": v(-90.9, 53.79) * mm});
            skLineSegment(sketch, "E7726", {"start": v(-90.9, 53.79) * mm, "end": v(-90.83, 54) * mm});
            skLineSegment(sketch, "E7727", {"start": v(-90.83, 54) * mm, "end": v(-90.74, 54.22) * mm});
            skLineSegment(sketch, "E7728", {"start": v(-90.74, 54.22) * mm, "end": v(-90.63, 54.45) * mm});
            skLineSegment(sketch, "E7729", {"start": v(-90.63, 54.45) * mm, "end": v(-90.5, 54.68) * mm});
            skLineSegment(sketch, "E7730", {"start": v(-90.5, 54.68) * mm, "end": v(-90.35, 54.89) * mm});
            skLineSegment(sketch, "E7731", {"start": v(-90.35, 54.89) * mm, "end": v(-90.28, 54.98) * mm});
            skLineSegment(sketch, "E7732", {"start": v(-90.28, 54.98) * mm, "end": v(-90.2, 55.07) * mm});
            skLineSegment(sketch, "E7733", {"start": v(-90.2, 55.07) * mm, "end": v(-90.1, 55.15) * mm});
            skLineSegment(sketch, "E7734", {"start": v(-90.1, 55.15) * mm, "end": v(-90.02, 55.22) * mm});
            skLineSegment(sketch, "E7735", {"start": v(-90.02, 55.22) * mm, "end": v(-89.93, 55.28) * mm});
            skLineSegment(sketch, "E7736", {"start": v(-89.93, 55.28) * mm, "end": v(-89.83, 55.32) * mm});
            skLineSegment(sketch, "E7737", {"start": v(-89.83, 55.32) * mm, "end": v(-89.77, 55.34) * mm});
            skLineSegment(sketch, "E7738", {"start": v(-89.77, 55.34) * mm, "end": v(-89.72, 55.35) * mm});
            skLineSegment(sketch, "E7739", {"start": v(-89.72, 55.35) * mm, "end": v(-89.6, 55.35) * mm});
            skLineSegment(sketch, "E7740", {"start": v(-89.6, 55.35) * mm, "end": v(-89.46, 55.32) * mm});
            skLineSegment(sketch, "E7741", {"start": v(-89.46, 55.32) * mm, "end": v(-89.32, 55.29) * mm});
            skLineSegment(sketch, "E7742", {"start": v(-89.32, 55.29) * mm, "end": v(-89.05, 55.2) * mm});
            skLineSegment(sketch, "E7743", {"start": v(-89.05, 55.2) * mm, "end": v(-88.93, 55.15) * mm});
            skLineSegment(sketch, "E7744", {"start": v(-88.93, 55.15) * mm, "end": v(-88.8, 55.12) * mm});
            skLineSegment(sketch, "E7745", {"start": v(-88.8, 55.12) * mm, "end": v(-88.57, 55.06) * mm});
            skLineSegment(sketch, "E7746", {"start": v(-88.57, 55.06) * mm, "end": v(-88.31, 54.97) * mm});
            skLineSegment(sketch, "E7747", {"start": v(-88.31, 54.97) * mm, "end": v(-88.03, 54.86) * mm});
            skLineSegment(sketch, "E7748", {"start": v(-88.03, 54.86) * mm, "end": v(-87.73, 54.74) * mm});
            skLineSegment(sketch, "E7749", {"start": v(-87.73, 54.74) * mm, "end": v(-87.42, 54.6) * mm});
            skLineSegment(sketch, "E7750", {"start": v(-87.42, 54.6) * mm, "end": v(-87.12, 54.44) * mm});
            skLineSegment(sketch, "E7751", {"start": v(-87.12, 54.44) * mm, "end": v(-86.84, 54.28) * mm});
            skLineSegment(sketch, "E7752", {"start": v(-86.84, 54.28) * mm, "end": v(-86.57, 54.11) * mm});
            skLineSegment(sketch, "E7753", {"start": v(-86.57, 54.11) * mm, "end": v(-86.27, 53.93) * mm});
            skLineSegment(sketch, "E7754", {"start": v(-86.27, 53.93) * mm, "end": v(-85.94, 53.74) * mm});
            skLineSegment(sketch, "E7755", {"start": v(-85.94, 53.74) * mm, "end": v(-85.78, 53.64) * mm});
            skLineSegment(sketch, "E7756", {"start": v(-85.78, 53.64) * mm, "end": v(-85.63, 53.54) * mm});
            skLineSegment(sketch, "E7757", {"start": v(-85.63, 53.54) * mm, "end": v(-85.49, 53.43) * mm});
            skLineSegment(sketch, "E7758", {"start": v(-85.49, 53.43) * mm, "end": v(-85.36, 53.31) * mm});
            skLineSegment(sketch, "E7759", {"start": v(-85.36, 53.31) * mm, "end": v(-85.21, 53.13) * mm});
            skLineSegment(sketch, "E7760", {"start": v(-85.21, 53.13) * mm, "end": v(-85.07, 52.93) * mm});
            skLineSegment(sketch, "E7761", {"start": v(-85.07, 52.93) * mm, "end": v(-84.94, 52.7) * mm});
            skLineSegment(sketch, "E7762", {"start": v(-84.94, 52.7) * mm, "end": v(-84.82, 52.47) * mm});
            skLineSegment(sketch, "E7763", {"start": v(-84.82, 52.47) * mm, "end": v(-84.58, 52) * mm});
            skLineSegment(sketch, "E7764", {"start": v(-84.58, 52) * mm, "end": v(-84.47, 51.77) * mm});
            skLineSegment(sketch, "E7765", {"start": v(-84.47, 51.77) * mm, "end": v(-84.36, 51.56) * mm});
            skLineSegment(sketch, "E7766", {"start": v(-84.36, 51.56) * mm, "end": v(-84.15, 51.15) * mm});
            skLineSegment(sketch, "E7767", {"start": v(-84.15, 51.15) * mm, "end": v(-83.92, 50.73) * mm});
            skLineSegment(sketch, "E7768", {"start": v(-83.92, 50.73) * mm, "end": v(-83.69, 50.3) * mm});
            skLineSegment(sketch, "E7769", {"start": v(-83.69, 50.3) * mm, "end": v(-83.44, 49.9) * mm});
            skLineSegment(sketch, "E7770", {"start": v(-83.44, 49.9) * mm, "end": v(-83.2, 49.47) * mm});
            skLineSegment(sketch, "E7771", {"start": v(-83.2, 49.47) * mm, "end": v(-82.93, 49.05) * mm});
            skLineSegment(sketch, "E7772", {"start": v(-82.93, 49.05) * mm, "end": v(-82.37, 48.22) * mm});
            skLineSegment(sketch, "E7773", {"start": v(-82.37, 48.22) * mm, "end": v(-81.79, 47.38) * mm});
            skLineSegment(sketch, "E7774", {"start": v(-81.79, 47.38) * mm, "end": v(-81.17, 46.56) * mm});
            skLineSegment(sketch, "E7775", {"start": v(-81.17, 46.56) * mm, "end": v(-80.53, 45.74) * mm});
            skLineSegment(sketch, "E7776", {"start": v(-80.53, 45.74) * mm, "end": v(-79.87, 44.93) * mm});
            skLineSegment(sketch, "E7777", {"start": v(-79.87, 44.93) * mm, "end": v(-79.2, 44.14) * mm});
            skLineSegment(sketch, "E7778", {"start": v(-79.2, 44.14) * mm, "end": v(-78.5, 43.37) * mm});
            skLineSegment(sketch, "E7779", {"start": v(-78.5, 43.37) * mm, "end": v(-77.8, 42.6) * mm});
            skLineSegment(sketch, "E7780", {"start": v(-77.8, 42.6) * mm, "end": v(-77.08, 41.88) * mm});
            skLineSegment(sketch, "E7781", {"start": v(-77.08, 41.88) * mm, "end": v(-76.37, 41.16) * mm});
            skLineSegment(sketch, "E7782", {"start": v(-76.37, 41.16) * mm, "end": v(-75.65, 40.48) * mm});
            skLineSegment(sketch, "E7783", {"start": v(-75.65, 40.48) * mm, "end": v(-74.94, 39.83) * mm});
            skLineSegment(sketch, "E7784", {"start": v(-74.94, 39.83) * mm, "end": v(-74.23, 39.2) * mm});
            skLineSegment(sketch, "E7785", {"start": v(-74.23, 39.2) * mm, "end": v(-74.25, 39.19) * mm});
            skLineSegment(sketch, "E7786", {"start": v(-83.77, 52.14) * mm, "end": v(-83.8, 52.22) * mm});
            skLineSegment(sketch, "E7787", {"start": v(-83.8, 52.22) * mm, "end": v(-83.81, 52.29) * mm});
            skLineSegment(sketch, "E7788", {"start": v(-83.81, 52.29) * mm, "end": v(-83.9, 52.68) * mm});
            skLineSegment(sketch, "E7789", {"start": v(-83.9, 52.68) * mm, "end": v(-84, 53.15) * mm});
            skLineSegment(sketch, "E7790", {"start": v(-84, 53.15) * mm, "end": v(-84.1, 53.68) * mm});
            skLineSegment(sketch, "E7791", {"start": v(-84.1, 53.68) * mm, "end": v(-84.18, 54.26) * mm});
            skLineSegment(sketch, "E7792", {"start": v(-84.18, 54.26) * mm, "end": v(-84.27, 54.86) * mm});
            skLineSegment(sketch, "E7793", {"start": v(-84.27, 54.86) * mm, "end": v(-84.35, 55.48) * mm});
            skLineSegment(sketch, "E7794", {"start": v(-84.35, 55.48) * mm, "end": v(-84.42, 56.09) * mm});
            skLineSegment(sketch, "E7795", {"start": v(-84.42, 56.09) * mm, "end": v(-84.47, 56.67) * mm});
            skLineSegment(sketch, "E7796", {"start": v(-84.47, 56.67) * mm, "end": v(-84.55, 57.32) * mm});
            skLineSegment(sketch, "E7797", {"start": v(-84.55, 57.32) * mm, "end": v(-84.64, 58.03) * mm});
            skLineSegment(sketch, "E7798", {"start": v(-84.64, 58.03) * mm, "end": v(-84.68, 58.39) * mm});
            skLineSegment(sketch, "E7799", {"start": v(-84.68, 58.39) * mm, "end": v(-84.7, 58.74) * mm});
            skLineSegment(sketch, "E7800", {"start": v(-84.7, 58.74) * mm, "end": v(-84.71, 59.08) * mm});
            skLineSegment(sketch, "E7801", {"start": v(-84.71, 59.08) * mm, "end": v(-84.7, 59.4) * mm});
            skLineSegment(sketch, "E7802", {"start": v(-84.7, 59.4) * mm, "end": v(-84.67, 59.73) * mm});
            skLineSegment(sketch, "E7803", {"start": v(-84.67, 59.73) * mm, "end": v(-84.63, 60.1) * mm});
            skLineSegment(sketch, "E7804", {"start": v(-84.63, 60.1) * mm, "end": v(-84.57, 60.47) * mm});
            skLineSegment(sketch, "E7805", {"start": v(-84.57, 60.47) * mm, "end": v(-84.5, 60.85) * mm});
            skLineSegment(sketch, "E7806", {"start": v(-84.5, 60.85) * mm, "end": v(-84.4, 61.22) * mm});
            skLineSegment(sketch, "E7807", {"start": v(-84.4, 61.22) * mm, "end": v(-84.35, 61.4) * mm});
            skLineSegment(sketch, "E7808", {"start": v(-84.35, 61.4) * mm, "end": v(-84.28, 61.58) * mm});
            skLineSegment(sketch, "E7809", {"start": v(-84.28, 61.58) * mm, "end": v(-84.21, 61.74) * mm});
            skLineSegment(sketch, "E7810", {"start": v(-84.21, 61.74) * mm, "end": v(-84.14, 61.9) * mm});
            skLineSegment(sketch, "E7811", {"start": v(-84.14, 61.9) * mm, "end": v(-84.05, 62.04) * mm});
            skLineSegment(sketch, "E7812", {"start": v(-84.05, 62.04) * mm, "end": v(-83.95, 62.17) * mm});
            skLineSegment(sketch, "E7813", {"start": v(-83.95, 62.17) * mm, "end": v(-83.9, 62.23) * mm});
            skLineSegment(sketch, "E7814", {"start": v(-83.9, 62.23) * mm, "end": v(-83.82, 62.28) * mm});
            skLineSegment(sketch, "E7815", {"start": v(-83.82, 62.28) * mm, "end": v(-83.66, 62.37) * mm});
            skLineSegment(sketch, "E7816", {"start": v(-83.66, 62.37) * mm, "end": v(-83.48, 62.44) * mm});
            skLineSegment(sketch, "E7817", {"start": v(-83.48, 62.44) * mm, "end": v(-83.32, 62.5) * mm});
            skLineSegment(sketch, "E7818", {"start": v(-83.32, 62.5) * mm, "end": v(-83.18, 62.58) * mm});
            skLineSegment(sketch, "E7819", {"start": v(-83.18, 62.58) * mm, "end": v(-83.01, 62.64) * mm});
            skLineSegment(sketch, "E7820", {"start": v(-83.01, 62.64) * mm, "end": v(-82.83, 62.7) * mm});
            skLineSegment(sketch, "E7821", {"start": v(-82.83, 62.7) * mm, "end": v(-82.63, 62.75) * mm});
            skLineSegment(sketch, "E7822", {"start": v(-82.63, 62.75) * mm, "end": v(-82.42, 62.79) * mm});
            skLineSegment(sketch, "E7823", {"start": v(-82.42, 62.79) * mm, "end": v(-82.22, 62.82) * mm});
            skLineSegment(sketch, "E7824", {"start": v(-82.22, 62.82) * mm, "end": v(-82.02, 62.84) * mm});
            skLineSegment(sketch, "E7825", {"start": v(-82.02, 62.84) * mm, "end": v(-81.83, 62.85) * mm});
            skLineSegment(sketch, "E7826", {"start": v(-81.83, 62.85) * mm, "end": v(-81.62, 62.85) * mm});
            skLineSegment(sketch, "E7827", {"start": v(-81.62, 62.85) * mm, "end": v(-81.4, 62.87) * mm});
            skLineSegment(sketch, "E7828", {"start": v(-81.4, 62.87) * mm, "end": v(-81.17, 62.87) * mm});
            skLineSegment(sketch, "E7829", {"start": v(-81.17, 62.87) * mm, "end": v(-81.06, 62.86) * mm});
            skLineSegment(sketch, "E7830", {"start": v(-81.06, 62.86) * mm, "end": v(-80.96, 62.85) * mm});
            skLineSegment(sketch, "E7831", {"start": v(-80.96, 62.85) * mm, "end": v(-80.73, 62.79) * mm});
            skLineSegment(sketch, "E7832", {"start": v(-80.73, 62.79) * mm, "end": v(-80.5, 62.72) * mm});
            skLineSegment(sketch, "E7833", {"start": v(-80.5, 62.72) * mm, "end": v(-80.26, 62.63) * mm});
            skLineSegment(sketch, "E7834", {"start": v(-80.26, 62.63) * mm, "end": v(-80.01, 62.54) * mm});
            skLineSegment(sketch, "E7835", {"start": v(-80.01, 62.54) * mm, "end": v(-79.52, 62.33) * mm});
            skLineSegment(sketch, "E7836", {"start": v(-79.52, 62.33) * mm, "end": v(-79.03, 62.1) * mm});
            skLineSegment(sketch, "E7837", {"start": v(-79.03, 62.1) * mm, "end": v(-78.55, 61.84) * mm});
            skLineSegment(sketch, "E7838", {"start": v(-78.55, 61.84) * mm, "end": v(-78.08, 61.57) * mm});
            skLineSegment(sketch, "E7839", {"start": v(-78.08, 61.57) * mm, "end": v(-77.64, 61.3) * mm});
            skLineSegment(sketch, "E7840", {"start": v(-77.64, 61.3) * mm, "end": v(-77.24, 61.03) * mm});
            skLineSegment(sketch, "E7841", {"start": v(-77.24, 61.03) * mm, "end": v(-76.54, 60.54) * mm});
            skLineSegment(sketch, "E7842", {"start": v(-76.54, 60.54) * mm, "end": v(-75.92, 60.07) * mm});
            skLineSegment(sketch, "E7843", {"start": v(-75.92, 60.07) * mm, "end": v(-75.35, 59.63) * mm});
            skLineSegment(sketch, "E7844", {"start": v(-75.35, 59.63) * mm, "end": v(-75.08, 59.4) * mm});
            skLineSegment(sketch, "E7845", {"start": v(-75.08, 59.4) * mm, "end": v(-74.82, 59.17) * mm});
            skLineSegment(sketch, "E7846", {"start": v(-74.82, 59.17) * mm, "end": v(-74.57, 58.94) * mm});
            skLineSegment(sketch, "E7847", {"start": v(-74.57, 58.94) * mm, "end": v(-74.32, 58.7) * mm});
            skLineSegment(sketch, "E7848", {"start": v(-74.32, 58.7) * mm, "end": v(-74.07, 58.44) * mm});
            skLineSegment(sketch, "E7849", {"start": v(-74.07, 58.44) * mm, "end": v(-73.82, 58.17) * mm});
            skLineSegment(sketch, "E7850", {"start": v(-73.82, 58.17) * mm, "end": v(-73.57, 57.9) * mm});
            skLineSegment(sketch, "E7851", {"start": v(-73.57, 57.9) * mm, "end": v(-73.31, 57.6) * mm});
            skLineSegment(sketch, "E7852", {"start": v(-73.31, 57.6) * mm, "end": v(-72.77, 56.93) * mm});
            skLineSegment(sketch, "E7853", {"start": v(-72.77, 56.93) * mm, "end": v(-72.46, 56.33) * mm});
            skLineSegment(sketch, "E7854", {"start": v(-72.46, 56.33) * mm, "end": v(-72.14, 55.73) * mm});
            skLineSegment(sketch, "E7855", {"start": v(-72.14, 55.73) * mm, "end": v(-71.8, 55.13) * mm});
            skLineSegment(sketch, "E7856", {"start": v(-71.8, 55.13) * mm, "end": v(-71.44, 54.53) * mm});
            skLineSegment(sketch, "E7857", {"start": v(-71.44, 54.53) * mm, "end": v(-71.07, 53.92) * mm});
            skLineSegment(sketch, "E7858", {"start": v(-71.07, 53.92) * mm, "end": v(-70.7, 53.32) * mm});
            skLineSegment(sketch, "E7859", {"start": v(-70.7, 53.32) * mm, "end": v(-70.3, 52.72) * mm});
            skLineSegment(sketch, "E7860", {"start": v(-70.3, 52.72) * mm, "end": v(-69.9, 52.13) * mm});
            skLineSegment(sketch, "E7861", {"start": v(-69.9, 52.13) * mm, "end": v(-69.5, 51.54) * mm});
            skLineSegment(sketch, "E7862", {"start": v(-69.5, 51.54) * mm, "end": v(-69.08, 50.96) * mm});
            skLineSegment(sketch, "E7863", {"start": v(-69.08, 50.96) * mm, "end": v(-68.66, 50.39) * mm});
            skLineSegment(sketch, "E7864", {"start": v(-68.66, 50.39) * mm, "end": v(-68.23, 49.82) * mm});
            skLineSegment(sketch, "E7865", {"start": v(-68.23, 49.82) * mm, "end": v(-67.8, 49.27) * mm});
            skLineSegment(sketch, "E7866", {"start": v(-67.8, 49.27) * mm, "end": v(-67.38, 48.73) * mm});
            skLineSegment(sketch, "E7867", {"start": v(-67.38, 48.73) * mm, "end": v(-66.95, 48.2) * mm});
            skLineSegment(sketch, "E7868", {"start": v(-66.95, 48.2) * mm, "end": v(-66.53, 47.7) * mm});
            skLineSegment(sketch, "E7869", {"start": v(-66.53, 47.7) * mm, "end": v(-66.75, 47.44) * mm});
            skLineSegment(sketch, "E7870", {"start": v(-66.75, 47.44) * mm, "end": v(-66.96, 47.16) * mm});
            skLineSegment(sketch, "E7871", {"start": v(-66.96, 47.16) * mm, "end": v(-67.17, 46.86) * mm});
            skLineSegment(sketch, "E7872", {"start": v(-67.17, 46.86) * mm, "end": v(-67.36, 46.54) * mm});
            skLineSegment(sketch, "E7873", {"start": v(-67.36, 46.54) * mm, "end": v(-67.83, 45.72) * mm});
            skLineSegment(sketch, "E7874", {"start": v(-67.83, 45.72) * mm, "end": v(-68.06, 45.33) * mm});
            skLineSegment(sketch, "E7875", {"start": v(-68.06, 45.33) * mm, "end": v(-68.28, 44.96) * mm});
            skLineSegment(sketch, "E7876", {"start": v(-68.28, 44.96) * mm, "end": v(-68.65, 44.35) * mm});
            skLineSegment(sketch, "E7877", {"start": v(-68.65, 44.35) * mm, "end": v(-69.02, 43.72) * mm});
            skLineSegment(sketch, "E7878", {"start": v(-69.02, 43.72) * mm, "end": v(-69.39, 43.06) * mm});
            skLineSegment(sketch, "E7879", {"start": v(-69.39, 43.06) * mm, "end": v(-69.73, 42.42) * mm});
            skLineSegment(sketch, "E7880", {"start": v(-69.73, 42.42) * mm, "end": v(-70.05, 41.8) * mm});
            skLineSegment(sketch, "E7881", {"start": v(-70.05, 41.8) * mm, "end": v(-70.34, 41.21) * mm});
            skLineSegment(sketch, "E7882", {"start": v(-70.34, 41.21) * mm, "end": v(-70.58, 40.7) * mm});
            skLineSegment(sketch, "E7883", {"start": v(-70.58, 40.7) * mm, "end": v(-70.76, 40.27) * mm});
            skLineSegment(sketch, "E7884", {"start": v(-70.76, 40.27) * mm, "end": v(-70.87, 39.95) * mm});
            skLineSegment(sketch, "E7885", {"start": v(-70.87, 39.95) * mm, "end": v(-70.92, 39.8) * mm});
            skLineSegment(sketch, "E7886", {"start": v(-70.92, 39.8) * mm, "end": v(-70.98, 39.64) * mm});
            skLineSegment(sketch, "E7887", {"start": v(-70.98, 39.64) * mm, "end": v(-71.04, 39.5) * mm});
            skLineSegment(sketch, "E7888", {"start": v(-71.04, 39.5) * mm, "end": v(-71.1, 39.35) * mm});
            skLineSegment(sketch, "E7889", {"start": v(-71.1, 39.35) * mm, "end": v(-71.14, 39.2) * mm});
            skLineSegment(sketch, "E7890", {"start": v(-71.14, 39.2) * mm, "end": v(-71.2, 39.07) * mm});
            skLineSegment(sketch, "E7891", {"start": v(-71.2, 39.07) * mm, "end": v(-71.28, 38.9) * mm});
            skLineSegment(sketch, "E7892", {"start": v(-71.28, 38.9) * mm, "end": v(-71.37, 38.74) * mm});
            skLineSegment(sketch, "E7893", {"start": v(-71.37, 38.74) * mm, "end": v(-71.44, 38.66) * mm});
            skLineSegment(sketch, "E7894", {"start": v(-71.44, 38.66) * mm, "end": v(-71.49, 38.63) * mm});
            skLineSegment(sketch, "E7895", {"start": v(-71.49, 38.63) * mm, "end": v(-71.58, 38.59) * mm});
            skLineSegment(sketch, "E7896", {"start": v(-71.58, 38.59) * mm, "end": v(-71.69, 38.55) * mm});
            skLineSegment(sketch, "E7897", {"start": v(-71.69, 38.55) * mm, "end": v(-71.8, 38.52) * mm});
            skLineSegment(sketch, "E7898", {"start": v(-71.8, 38.52) * mm, "end": v(-71.9, 38.5) * mm});
            skLineSegment(sketch, "E7899", {"start": v(-71.9, 38.5) * mm, "end": v(-71.94, 38.5) * mm});
            skLineSegment(sketch, "E7900", {"start": v(-71.94, 38.5) * mm, "end": v(-72.03, 38.5) * mm});
            skLineSegment(sketch, "E7901", {"start": v(-72.03, 38.5) * mm, "end": v(-72.05, 38.52) * mm});
            skLineSegment(sketch, "E7902", {"start": v(-72.05, 38.52) * mm, "end": v(-72.1, 38.55) * mm});
            skLineSegment(sketch, "E7903", {"start": v(-72.1, 38.55) * mm, "end": v(-72.25, 38.66) * mm});
            skLineSegment(sketch, "E7904", {"start": v(-72.25, 38.66) * mm, "end": v(-72.43, 38.82) * mm});
            skLineSegment(sketch, "E7905", {"start": v(-72.43, 38.82) * mm, "end": v(-72.64, 39) * mm});
            skLineSegment(sketch, "E7906", {"start": v(-72.64, 39) * mm, "end": v(-72.85, 39.17) * mm});
            skLineSegment(sketch, "E7907", {"start": v(-72.85, 39.17) * mm, "end": v(-73.28, 39.48) * mm});
            skLineSegment(sketch, "E7908", {"start": v(-73.28, 39.48) * mm, "end": v(-73.5, 39.64) * mm});
            skLineSegment(sketch, "E7909", {"start": v(-73.5, 39.64) * mm, "end": v(-73.7, 39.8) * mm});
            skLineSegment(sketch, "E7910", {"start": v(-73.7, 39.8) * mm, "end": v(-74.06, 40.1) * mm});
            skLineSegment(sketch, "E7911", {"start": v(-74.06, 40.1) * mm, "end": v(-74.4, 40.41) * mm});
            skLineSegment(sketch, "E7912", {"start": v(-74.4, 40.41) * mm, "end": v(-75.1, 41.06) * mm});
            skLineSegment(sketch, "E7913", {"start": v(-75.1, 41.06) * mm, "end": v(-75.81, 41.73) * mm});
            skLineSegment(sketch, "E7914", {"start": v(-75.81, 41.73) * mm, "end": v(-76.52, 42.43) * mm});
            skLineSegment(sketch, "E7915", {"start": v(-76.52, 42.43) * mm, "end": v(-77.22, 43.15) * mm});
            skLineSegment(sketch, "E7916", {"start": v(-77.22, 43.15) * mm, "end": v(-77.91, 43.9) * mm});
            skLineSegment(sketch, "E7917", {"start": v(-77.91, 43.9) * mm, "end": v(-78.6, 44.66) * mm});
            skLineSegment(sketch, "E7918", {"start": v(-78.6, 44.66) * mm, "end": v(-79.27, 45.44) * mm});
            skLineSegment(sketch, "E7919", {"start": v(-79.27, 45.44) * mm, "end": v(-79.92, 46.23) * mm});
            skLineSegment(sketch, "E7920", {"start": v(-79.92, 46.23) * mm, "end": v(-80.54, 47.04) * mm});
            skLineSegment(sketch, "E7921", {"start": v(-80.54, 47.04) * mm, "end": v(-81.15, 47.85) * mm});
            skLineSegment(sketch, "E7922", {"start": v(-81.15, 47.85) * mm, "end": v(-81.72, 48.66) * mm});
            skLineSegment(sketch, "E7923", {"start": v(-81.72, 48.66) * mm, "end": v(-82.26, 49.48) * mm});
            skLineSegment(sketch, "E7924", {"start": v(-82.26, 49.48) * mm, "end": v(-82.76, 50.3) * mm});
            skLineSegment(sketch, "E7925", {"start": v(-82.76, 50.3) * mm, "end": v(-83, 50.7) * mm});
            skLineSegment(sketch, "E7926", {"start": v(-83, 50.7) * mm, "end": v(-83.23, 51.1) * mm});
            skLineSegment(sketch, "E7927", {"start": v(-83.23, 51.1) * mm, "end": v(-83.44, 51.52) * mm});
            skLineSegment(sketch, "E7928", {"start": v(-83.44, 51.52) * mm, "end": v(-83.66, 51.93) * mm});
            skLineSegment(sketch, "E7929", {"start": v(-83.66, 51.93) * mm, "end": v(-83.72, 52.03) * mm});
            skLineSegment(sketch, "E7930", {"start": v(-83.72, 52.03) * mm, "end": v(-83.77, 52.14) * mm});
            skLineSegment(sketch, "E7931", {"start": v(-71.85, 56.86) * mm, "end": v(-71.77, 56.7) * mm});
            skLineSegment(sketch, "E7932", {"start": v(-71.77, 56.7) * mm, "end": v(-71.45, 56.12) * mm});
            skLineSegment(sketch, "E7933", {"start": v(-71.45, 56.12) * mm, "end": v(-71.11, 55.53) * mm});
            skLineSegment(sketch, "E7934", {"start": v(-71.11, 55.53) * mm, "end": v(-70.76, 54.93) * mm});
            skLineSegment(sketch, "E7935", {"start": v(-70.76, 54.93) * mm, "end": v(-70.4, 54.34) * mm});
            skLineSegment(sketch, "E7936", {"start": v(-70.4, 54.34) * mm, "end": v(-70.03, 53.75) * mm});
            skLineSegment(sketch, "E7937", {"start": v(-70.03, 53.75) * mm, "end": v(-69.25, 52.58) * mm});
            skLineSegment(sketch, "E7938", {"start": v(-69.25, 52.58) * mm, "end": v(-68.44, 51.42) * mm});
            skLineSegment(sketch, "E7939", {"start": v(-68.44, 51.42) * mm, "end": v(-67.6, 50.3) * mm});
            skLineSegment(sketch, "E7940", {"start": v(-67.6, 50.3) * mm, "end": v(-66.76, 49.23) * mm});
            skLineSegment(sketch, "E7941", {"start": v(-66.76, 49.23) * mm, "end": v(-66, 48.3) * mm});
            skLineSegment(sketch, "E7942", {"start": v(-66, 48.3) * mm, "end": v(-65.86, 48.48) * mm});
            skLineSegment(sketch, "E7943", {"start": v(-65.86, 48.48) * mm, "end": v(-65.5, 48.86) * mm});
            skLineSegment(sketch, "E7944", {"start": v(-65.5, 48.86) * mm, "end": v(-65.1, 49.22) * mm});
            skLineSegment(sketch, "E7945", {"start": v(-65.1, 49.22) * mm, "end": v(-64.69, 49.55) * mm});
            skLineSegment(sketch, "E7946", {"start": v(-64.69, 49.55) * mm, "end": v(-64.46, 49.71) * mm});
            skLineSegment(sketch, "E7947", {"start": v(-64.46, 49.71) * mm, "end": v(-64.22, 49.86) * mm});
            skLineSegment(sketch, "E7948", {"start": v(-64.22, 49.86) * mm, "end": v(-63.98, 50) * mm});
            skLineSegment(sketch, "E7949", {"start": v(-63.98, 50) * mm, "end": v(-63.72, 50.12) * mm});
            skLineSegment(sketch, "E7950", {"start": v(-63.72, 50.12) * mm, "end": v(-63.47, 50.22) * mm});
            skLineSegment(sketch, "E7951", {"start": v(-63.47, 50.22) * mm, "end": v(-63.2, 50.3) * mm});
            skLineSegment(sketch, "E7952", {"start": v(-63.2, 50.3) * mm, "end": v(-62.93, 50.36) * mm});
            skLineSegment(sketch, "E7953", {"start": v(-62.93, 50.36) * mm, "end": v(-62.65, 50.4) * mm});
            skLineSegment(sketch, "E7954", {"start": v(-62.65, 50.4) * mm, "end": v(-62.12, 50.46) * mm});
            skLineSegment(sketch, "E7955", {"start": v(-62.12, 50.46) * mm, "end": v(-61.59, 50.5) * mm});
            skLineSegment(sketch, "E7956", {"start": v(-61.59, 50.5) * mm, "end": v(-61.1, 50.54) * mm});
            skLineSegment(sketch, "E7957", {"start": v(-61.1, 50.54) * mm, "end": v(-60.65, 50.6) * mm});
            skLineSegment(sketch, "E7958", {"start": v(-60.65, 50.6) * mm, "end": v(-60.47, 50.63) * mm});
            skLineSegment(sketch, "E7959", {"start": v(-60.47, 50.63) * mm, "end": v(-60.31, 50.67) * mm});
            skLineSegment(sketch, "E7960", {"start": v(-60.31, 50.67) * mm, "end": v(-60.19, 50.7) * mm});
            skLineSegment(sketch, "E7961", {"start": v(-60.19, 50.7) * mm, "end": v(-60.1, 50.75) * mm});
            skLineSegment(sketch, "E7962", {"start": v(-60.1, 50.75) * mm, "end": v(-60.07, 50.77) * mm});
            skLineSegment(sketch, "E7963", {"start": v(-60.07, 50.77) * mm, "end": v(-60.02, 50.81) * mm});
            skLineSegment(sketch, "E7964", {"start": v(-60.02, 50.81) * mm, "end": v(-59.97, 50.87) * mm});
            skLineSegment(sketch, "E7965", {"start": v(-59.97, 50.87) * mm, "end": v(-59.91, 50.94) * mm});
            skLineSegment(sketch, "E7966", {"start": v(-59.91, 50.94) * mm, "end": v(-59.77, 51.15) * mm});
            skLineSegment(sketch, "E7967", {"start": v(-59.77, 51.15) * mm, "end": v(-59.63, 51.4) * mm});
            skLineSegment(sketch, "E7968", {"start": v(-59.63, 51.4) * mm, "end": v(-59.34, 52.03) * mm});
            skLineSegment(sketch, "E7969", {"start": v(-59.34, 52.03) * mm, "end": v(-59.18, 52.36) * mm});
            skLineSegment(sketch, "E7970", {"start": v(-59.18, 52.36) * mm, "end": v(-59, 52.68) * mm});
            skLineSegment(sketch, "E7971", {"start": v(-59, 52.68) * mm, "end": v(-58.7, 53.15) * mm});
            skLineSegment(sketch, "E7972", {"start": v(-58.7, 53.15) * mm, "end": v(-58.94, 53.49) * mm});
            skLineSegment(sketch, "E7973", {"start": v(-58.94, 53.49) * mm, "end": v(-59.17, 53.84) * mm});
            skLineSegment(sketch, "E7974", {"start": v(-59.17, 53.84) * mm, "end": v(-59.4, 54.2) * mm});
            skLineSegment(sketch, "E7975", {"start": v(-59.4, 54.2) * mm, "end": v(-59.6, 54.59) * mm});
            skLineSegment(sketch, "E7976", {"start": v(-59.6, 54.59) * mm, "end": v(-59.82, 54.98) * mm});
            skLineSegment(sketch, "E7977", {"start": v(-59.82, 54.98) * mm, "end": v(-60.02, 55.38) * mm});
            skLineSegment(sketch, "E7978", {"start": v(-60.02, 55.38) * mm, "end": v(-60.21, 55.8) * mm});
            skLineSegment(sketch, "E7979", {"start": v(-60.21, 55.8) * mm, "end": v(-60.4, 56.2) * mm});
            skLineSegment(sketch, "E7980", {"start": v(-60.4, 56.2) * mm, "end": v(-60.57, 56.63) * mm});
            skLineSegment(sketch, "E7981", {"start": v(-60.57, 56.63) * mm, "end": v(-60.73, 57.05) * mm});
            skLineSegment(sketch, "E7982", {"start": v(-60.73, 57.05) * mm, "end": v(-60.88, 57.48) * mm});
            skLineSegment(sketch, "E7983", {"start": v(-60.88, 57.48) * mm, "end": v(-61.02, 57.9) * mm});
            skLineSegment(sketch, "E7984", {"start": v(-61.02, 57.9) * mm, "end": v(-61.15, 58.33) * mm});
            skLineSegment(sketch, "E7985", {"start": v(-61.15, 58.33) * mm, "end": v(-61.27, 58.75) * mm});
            skLineSegment(sketch, "E7986", {"start": v(-61.27, 58.75) * mm, "end": v(-61.37, 59.17) * mm});
            skLineSegment(sketch, "E7987", {"start": v(-61.37, 59.17) * mm, "end": v(-61.46, 59.58) * mm});
            skLineSegment(sketch, "E7988", {"start": v(-61.46, 59.58) * mm, "end": v(-61.58, 59.77) * mm});
            skLineSegment(sketch, "E7989", {"start": v(-61.58, 59.77) * mm, "end": v(-61.72, 59.96) * mm});
            skLineSegment(sketch, "E7990", {"start": v(-61.72, 59.96) * mm, "end": v(-62.04, 60.33) * mm});
            skLineSegment(sketch, "E7991", {"start": v(-62.04, 60.33) * mm, "end": v(-62.38, 60.7) * mm});
            skLineSegment(sketch, "E7992", {"start": v(-62.38, 60.7) * mm, "end": v(-62.68, 61.04) * mm});
            skLineSegment(sketch, "E7993", {"start": v(-62.68, 61.04) * mm, "end": v(-62.97, 61.37) * mm});
            skLineSegment(sketch, "E7994", {"start": v(-62.97, 61.37) * mm, "end": v(-63.31, 61.73) * mm});
            skLineSegment(sketch, "E7995", {"start": v(-63.31, 61.73) * mm, "end": v(-63.7, 62.11) * mm});
            skLineSegment(sketch, "E7996", {"start": v(-63.7, 62.11) * mm, "end": v(-64.13, 62.5) * mm});
            skLineSegment(sketch, "E7997", {"start": v(-64.13, 62.5) * mm, "end": v(-64.57, 62.9) * mm});
            skLineSegment(sketch, "E7998", {"start": v(-64.57, 62.9) * mm, "end": v(-65.02, 63.3) * mm});
            skLineSegment(sketch, "E7999", {"start": v(-65.02, 63.3) * mm, "end": v(-65.46, 63.66) * mm});
            skLineSegment(sketch, "E8000", {"start": v(-65.46, 63.66) * mm, "end": v(-65.88, 63.99) * mm});
            skLineSegment(sketch, "E8001", {"start": v(-65.88, 63.99) * mm, "end": v(-66.34, 64.36) * mm});
            skLineSegment(sketch, "E8002", {"start": v(-66.34, 64.36) * mm, "end": v(-66.84, 64.78) * mm});
            skLineSegment(sketch, "E8003", {"start": v(-66.84, 64.78) * mm, "end": v(-67.1, 64.98) * mm});
            skLineSegment(sketch, "E8004", {"start": v(-67.1, 64.98) * mm, "end": v(-67.35, 65.17) * mm});
            skLineSegment(sketch, "E8005", {"start": v(-67.35, 65.17) * mm, "end": v(-67.6, 65.33) * mm});
            skLineSegment(sketch, "E8006", {"start": v(-67.6, 65.33) * mm, "end": v(-67.85, 65.47) * mm});
            skLineSegment(sketch, "E8007", {"start": v(-67.85, 65.47) * mm, "end": v(-68.15, 65.61) * mm});
            skLineSegment(sketch, "E8008", {"start": v(-68.15, 65.61) * mm, "end": v(-68.47, 65.75) * mm});
            skLineSegment(sketch, "E8009", {"start": v(-68.47, 65.75) * mm, "end": v(-68.8, 65.87) * mm});
            skLineSegment(sketch, "E8010", {"start": v(-68.8, 65.87) * mm, "end": v(-69.16, 65.99) * mm});
            skLineSegment(sketch, "E8011", {"start": v(-69.16, 65.99) * mm, "end": v(-69.51, 66.08) * mm});
            skLineSegment(sketch, "E8012", {"start": v(-69.51, 66.08) * mm, "end": v(-69.86, 66.15) * mm});
            skLineSegment(sketch, "E8013", {"start": v(-69.86, 66.15) * mm, "end": v(-70.04, 66.18) * mm});
            skLineSegment(sketch, "E8014", {"start": v(-70.04, 66.18) * mm, "end": v(-70.2, 66.2) * mm});
            skLineSegment(sketch, "E8015", {"start": v(-70.2, 66.2) * mm, "end": v(-70.37, 66.2) * mm});
            skLineSegment(sketch, "E8016", {"start": v(-70.37, 66.2) * mm, "end": v(-70.53, 66.2) * mm});
            skLineSegment(sketch, "E8017", {"start": v(-70.53, 66.2) * mm, "end": v(-70.76, 66.17) * mm});
            skLineSegment(sketch, "E8018", {"start": v(-70.76, 66.17) * mm, "end": v(-71.01, 66.12) * mm});
            skLineSegment(sketch, "E8019", {"start": v(-71.01, 66.12) * mm, "end": v(-71.27, 66.05) * mm});
            skLineSegment(sketch, "E8020", {"start": v(-71.27, 66.05) * mm, "end": v(-71.52, 65.96) * mm});
            skLineSegment(sketch, "E8021", {"start": v(-71.52, 65.96) * mm, "end": v(-71.77, 65.85) * mm});
            skLineSegment(sketch, "E8022", {"start": v(-71.77, 65.85) * mm, "end": v(-72, 65.72) * mm});
            skLineSegment(sketch, "E8023", {"start": v(-72, 65.72) * mm, "end": v(-72.2, 65.58) * mm});
            skLineSegment(sketch, "E8024", {"start": v(-72.2, 65.58) * mm, "end": v(-72.3, 65.5) * mm});
            skLineSegment(sketch, "E8025", {"start": v(-72.3, 65.5) * mm, "end": v(-72.38, 65.42) * mm});
            skLineSegment(sketch, "E8026", {"start": v(-72.38, 65.42) * mm, "end": v(-72.46, 65.32) * mm});
            skLineSegment(sketch, "E8027", {"start": v(-72.46, 65.32) * mm, "end": v(-72.52, 65.2) * mm});
            skLineSegment(sketch, "E8028", {"start": v(-72.52, 65.2) * mm, "end": v(-72.56, 65.08) * mm});
            skLineSegment(sketch, "E8029", {"start": v(-72.56, 65.08) * mm, "end": v(-72.6, 64.94) * mm});
            skLineSegment(sketch, "E8030", {"start": v(-72.6, 64.94) * mm, "end": v(-72.67, 64.67) * mm});
            skLineSegment(sketch, "E8031", {"start": v(-72.67, 64.67) * mm, "end": v(-72.7, 64.54) * mm});
            skLineSegment(sketch, "E8032", {"start": v(-72.7, 64.54) * mm, "end": v(-72.73, 64.41) * mm});
            skLineSegment(sketch, "E8033", {"start": v(-72.73, 64.41) * mm, "end": v(-72.8, 64.2) * mm});
            skLineSegment(sketch, "E8034", {"start": v(-72.8, 64.2) * mm, "end": v(-72.87, 63.96) * mm});
            skLineSegment(sketch, "E8035", {"start": v(-72.87, 63.96) * mm, "end": v(-72.98, 63.48) * mm});
            skLineSegment(sketch, "E8036", {"start": v(-72.98, 63.48) * mm, "end": v(-73.02, 63.25) * mm});
            skLineSegment(sketch, "E8037", {"start": v(-73.02, 63.25) * mm, "end": v(-73.06, 63.03) * mm});
            skLineSegment(sketch, "E8038", {"start": v(-73.06, 63.03) * mm, "end": v(-73.08, 62.83) * mm});
            skLineSegment(sketch, "E8039", {"start": v(-73.08, 62.83) * mm, "end": v(-73.09, 62.65) * mm});
            skLineSegment(sketch, "E8040", {"start": v(-73.09, 62.65) * mm, "end": v(-73.1, 62.28) * mm});
            skLineSegment(sketch, "E8041", {"start": v(-73.1, 62.28) * mm, "end": v(-73.1, 62.08) * mm});
            skLineSegment(sketch, "E8042", {"start": v(-73.1, 62.08) * mm, "end": v(-73.09, 61.9) * mm});
            skLineSegment(sketch, "E8043", {"start": v(-73.09, 61.9) * mm, "end": v(-72.98, 61.34) * mm});
            skLineSegment(sketch, "E8044", {"start": v(-72.98, 61.34) * mm, "end": v(-72.85, 60.75) * mm});
            skLineSegment(sketch, "E8045", {"start": v(-72.85, 60.75) * mm, "end": v(-72.71, 60.13) * mm});
            skLineSegment(sketch, "E8046", {"start": v(-72.71, 60.13) * mm, "end": v(-72.56, 59.5) * mm});
            skLineSegment(sketch, "E8047", {"start": v(-72.56, 59.5) * mm, "end": v(-72.4, 58.85) * mm});
            skLineSegment(sketch, "E8048", {"start": v(-72.4, 58.85) * mm, "end": v(-72.23, 58.19) * mm});
            skLineSegment(sketch, "E8049", {"start": v(-72.23, 58.19) * mm, "end": v(-72.04, 57.52) * mm});
            skLineSegment(sketch, "E8050", {"start": v(-72.04, 57.52) * mm, "end": v(-71.85, 56.86) * mm});
            skLineSegment(sketch, "E8051", {"start": v(-60.73, 59.9) * mm, "end": v(-60.72, 59.88) * mm});
            skLineSegment(sketch, "E8052", {"start": v(-60.72, 59.88) * mm, "end": v(-60.6, 59.35) * mm});
            skLineSegment(sketch, "E8053", {"start": v(-60.6, 59.35) * mm, "end": v(-60.5, 58.95) * mm});
            skLineSegment(sketch, "E8054", {"start": v(-60.5, 58.95) * mm, "end": v(-60.4, 58.55) * mm});
            skLineSegment(sketch, "E8055", {"start": v(-60.4, 58.55) * mm, "end": v(-60.27, 58.14) * mm});
            skLineSegment(sketch, "E8056", {"start": v(-60.27, 58.14) * mm, "end": v(-60.14, 57.73) * mm});
            skLineSegment(sketch, "E8057", {"start": v(-60.14, 57.73) * mm, "end": v(-59.99, 57.33) * mm});
            skLineSegment(sketch, "E8058", {"start": v(-59.99, 57.33) * mm, "end": v(-59.83, 56.92) * mm});
            skLineSegment(sketch, "E8059", {"start": v(-59.83, 56.92) * mm, "end": v(-59.67, 56.52) * mm});
            skLineSegment(sketch, "E8060", {"start": v(-59.67, 56.52) * mm, "end": v(-59.5, 56.12) * mm});
            skLineSegment(sketch, "E8061", {"start": v(-59.5, 56.12) * mm, "end": v(-59.3, 55.73) * mm});
            skLineSegment(sketch, "E8062", {"start": v(-59.3, 55.73) * mm, "end": v(-59.12, 55.34) * mm});
            skLineSegment(sketch, "E8063", {"start": v(-59.12, 55.34) * mm, "end": v(-58.92, 54.97) * mm});
            skLineSegment(sketch, "E8064", {"start": v(-58.92, 54.97) * mm, "end": v(-58.71, 54.6) * mm});
            skLineSegment(sketch, "E8065", {"start": v(-58.71, 54.6) * mm, "end": v(-58.5, 54.26) * mm});
            skLineSegment(sketch, "E8066", {"start": v(-58.5, 54.26) * mm, "end": v(-58.28, 53.93) * mm});
            skLineSegment(sketch, "E8067", {"start": v(-58.28, 53.93) * mm, "end": v(-58.25, 53.88) * mm});
            skLineSegment(sketch, "E8068", {"start": v(-58.25, 53.88) * mm, "end": v(-58.2, 53.9) * mm});
            skLineSegment(sketch, "E8069", {"start": v(-58.2, 53.9) * mm, "end": v(-58.14, 53.96) * mm});
            skLineSegment(sketch, "E8070", {"start": v(-58.14, 53.96) * mm, "end": v(-57.58, 54.75) * mm});
            skLineSegment(sketch, "E8071", {"start": v(-57.58, 54.75) * mm, "end": v(-56.84, 55.74) * mm});
            skLineSegment(sketch, "E8072", {"start": v(-56.84, 55.74) * mm, "end": v(-56.48, 56.18) * mm});
            skLineSegment(sketch, "E8073", {"start": v(-56.48, 56.18) * mm, "end": v(-56.18, 56.54) * mm});
            skLineSegment(sketch, "E8074", {"start": v(-56.18, 56.54) * mm, "end": v(-55.87, 56.91) * mm});
            skLineSegment(sketch, "E8075", {"start": v(-55.87, 56.91) * mm, "end": v(-55.52, 57.34) * mm});
            skLineSegment(sketch, "E8076", {"start": v(-55.52, 57.34) * mm, "end": v(-55.15, 57.77) * mm});
            skLineSegment(sketch, "E8077", {"start": v(-55.15, 57.77) * mm, "end": v(-54.94, 57.99) * mm});
            skLineSegment(sketch, "E8078", {"start": v(-54.94, 57.99) * mm, "end": v(-54.73, 58.18) * mm});
            skLineSegment(sketch, "E8079", {"start": v(-54.73, 58.18) * mm, "end": v(-54.06, 58.73) * mm});
            skLineSegment(sketch, "E8080", {"start": v(-54.06, 58.73) * mm, "end": v(-53.68, 59.03) * mm});
            skLineSegment(sketch, "E8081", {"start": v(-53.68, 59.03) * mm, "end": v(-53.45, 59.2) * mm});
            skLineSegment(sketch, "E8082", {"start": v(-53.45, 59.2) * mm, "end": v(-53.7, 59.6) * mm});
            skLineSegment(sketch, "E8083", {"start": v(-53.7, 59.6) * mm, "end": v(-53.96, 60.04) * mm});
            skLineSegment(sketch, "E8084", {"start": v(-53.96, 60.04) * mm, "end": v(-54.2, 60.49) * mm});
            skLineSegment(sketch, "E8085", {"start": v(-54.2, 60.49) * mm, "end": v(-54.46, 60.93) * mm});
            skLineSegment(sketch, "E8086", {"start": v(-54.46, 60.93) * mm, "end": v(-54.73, 61.36) * mm});
            skLineSegment(sketch, "E8087", {"start": v(-54.73, 61.36) * mm, "end": v(-54.87, 61.57) * mm});
            skLineSegment(sketch, "E8088", {"start": v(-54.87, 61.57) * mm, "end": v(-55.02, 61.77) * mm});
            skLineSegment(sketch, "E8089", {"start": v(-55.02, 61.77) * mm, "end": v(-55.17, 61.97) * mm});
            skLineSegment(sketch, "E8090", {"start": v(-55.17, 61.97) * mm, "end": v(-55.33, 62.16) * mm});
            skLineSegment(sketch, "E8091", {"start": v(-55.33, 62.16) * mm, "end": v(-55.5, 62.33) * mm});
            skLineSegment(sketch, "E8092", {"start": v(-55.5, 62.33) * mm, "end": v(-55.68, 62.5) * mm});
            skLineSegment(sketch, "E8093", {"start": v(-55.68, 62.5) * mm, "end": v(-55.82, 62.6) * mm});
            skLineSegment(sketch, "E8094", {"start": v(-55.82, 62.6) * mm, "end": v(-55.98, 62.7) * mm});
            skLineSegment(sketch, "E8095", {"start": v(-55.98, 62.7) * mm, "end": v(-56.16, 62.79) * mm});
            skLineSegment(sketch, "E8096", {"start": v(-56.16, 62.79) * mm, "end": v(-56.34, 62.87) * mm});
            skLineSegment(sketch, "E8097", {"start": v(-56.34, 62.87) * mm, "end": v(-56.72, 63.02) * mm});
            skLineSegment(sketch, "E8098", {"start": v(-56.72, 63.02) * mm, "end": v(-56.9, 63.1) * mm});
            skLineSegment(sketch, "E8099", {"start": v(-56.9, 63.1) * mm, "end": v(-57.06, 63.17) * mm});
            skLineSegment(sketch, "E8100", {"start": v(-57.06, 63.17) * mm, "end": v(-57.35, 63.3) * mm});
            skLineSegment(sketch, "E8101", {"start": v(-57.35, 63.3) * mm, "end": v(-57.65, 63.43) * mm});
            skLineSegment(sketch, "E8102", {"start": v(-57.65, 63.43) * mm, "end": v(-57.95, 63.54) * mm});
            skLineSegment(sketch, "E8103", {"start": v(-57.95, 63.54) * mm, "end": v(-58.25, 63.64) * mm});
            skLineSegment(sketch, "E8104", {"start": v(-58.25, 63.64) * mm, "end": v(-58.52, 63.72) * mm});
            skLineSegment(sketch, "E8105", {"start": v(-58.52, 63.72) * mm, "end": v(-58.77, 63.78) * mm});
            skLineSegment(sketch, "E8106", {"start": v(-58.77, 63.78) * mm, "end": v(-58.98, 63.82) * mm});
            skLineSegment(sketch, "E8107", {"start": v(-58.98, 63.82) * mm, "end": v(-59.15, 63.84) * mm});
            skLineSegment(sketch, "E8108", {"start": v(-59.15, 63.84) * mm, "end": v(-59.33, 63.85) * mm});
            skLineSegment(sketch, "E8109", {"start": v(-59.33, 63.85) * mm, "end": v(-59.52, 63.88) * mm});
            skLineSegment(sketch, "E8110", {"start": v(-59.52, 63.88) * mm, "end": v(-59.61, 63.88) * mm});
            skLineSegment(sketch, "E8111", {"start": v(-59.61, 63.88) * mm, "end": v(-59.7, 63.88) * mm});
            skLineSegment(sketch, "E8112", {"start": v(-59.7, 63.88) * mm, "end": v(-59.79, 63.87) * mm});
            skLineSegment(sketch, "E8113", {"start": v(-59.79, 63.87) * mm, "end": v(-59.86, 63.84) * mm});
            skLineSegment(sketch, "E8114", {"start": v(-59.86, 63.84) * mm, "end": v(-59.94, 63.79) * mm});
            skLineSegment(sketch, "E8115", {"start": v(-59.94, 63.79) * mm, "end": v(-60, 63.73) * mm});
            skLineSegment(sketch, "E8116", {"start": v(-60, 63.73) * mm, "end": v(-60.13, 63.58) * mm});
            skLineSegment(sketch, "E8117", {"start": v(-60.13, 63.58) * mm, "end": v(-60.24, 63.42) * mm});
            skLineSegment(sketch, "E8118", {"start": v(-60.24, 63.42) * mm, "end": v(-60.34, 63.23) * mm});
            skLineSegment(sketch, "E8119", {"start": v(-60.34, 63.23) * mm, "end": v(-60.42, 63.04) * mm});
            skLineSegment(sketch, "E8120", {"start": v(-60.42, 63.04) * mm, "end": v(-60.49, 62.84) * mm});
            skLineSegment(sketch, "E8121", {"start": v(-60.49, 62.84) * mm, "end": v(-60.6, 62.47) * mm});
            skLineSegment(sketch, "E8122", {"start": v(-60.6, 62.47) * mm, "end": v(-60.66, 62.18) * mm});
            skLineSegment(sketch, "E8123", {"start": v(-60.66, 62.18) * mm, "end": v(-60.7, 61.88) * mm});
            skLineSegment(sketch, "E8124", {"start": v(-60.7, 61.88) * mm, "end": v(-60.74, 61.56) * mm});
            skLineSegment(sketch, "E8125", {"start": v(-60.74, 61.56) * mm, "end": v(-60.76, 61.23) * mm});
            skLineSegment(sketch, "E8126", {"start": v(-60.76, 61.23) * mm, "end": v(-60.77, 60.9) * mm});
            skLineSegment(sketch, "E8127", {"start": v(-60.77, 60.9) * mm, "end": v(-60.76, 60.56) * mm});
            skLineSegment(sketch, "E8128", {"start": v(-60.76, 60.56) * mm, "end": v(-60.75, 60.23) * mm});
            skLineSegment(sketch, "E8129", {"start": v(-60.75, 60.23) * mm, "end": v(-60.73, 59.9) * mm});
            skLineSegment(sketch, "E8130", {"start": v(-52.4, 13.1) * mm, "end": v(-52.78, 11.42) * mm});
            skLineSegment(sketch, "E8131", {"start": v(-52.78, 11.42) * mm, "end": v(-53.17, 9.85) * mm});
            skLineSegment(sketch, "E8132", {"start": v(-53.17, 9.85) * mm, "end": v(-53.36, 9.13) * mm});
            skLineSegment(sketch, "E8133", {"start": v(-53.36, 9.13) * mm, "end": v(-53.47, 8.73) * mm});
            skLineSegment(sketch, "E8134", {"start": v(-53.47, 8.73) * mm, "end": v(-52.75, 8.73) * mm});
            skLineSegment(sketch, "E8135", {"start": v(-52.75, 8.73) * mm, "end": v(-52.5, 8.73) * mm});
            skLineSegment(sketch, "E8136", {"start": v(-52.5, 8.73) * mm, "end": v(-52.23, 8.75) * mm});
            skLineSegment(sketch, "E8137", {"start": v(-52.23, 8.75) * mm, "end": v(-51.6, 8.81) * mm});
            skLineSegment(sketch, "E8138", {"start": v(-51.6, 8.81) * mm, "end": v(-50.9, 8.91) * mm});
            skLineSegment(sketch, "E8139", {"start": v(-50.9, 8.91) * mm, "end": v(-50.11, 9.04) * mm});
            skLineSegment(sketch, "E8140", {"start": v(-50.11, 9.04) * mm, "end": v(-49.27, 9.2) * mm});
            skLineSegment(sketch, "E8141", {"start": v(-49.27, 9.2) * mm, "end": v(-48.4, 9.4) * mm});
            skLineSegment(sketch, "E8142", {"start": v(-48.4, 9.4) * mm, "end": v(-47.48, 9.6) * mm});
            skLineSegment(sketch, "E8143", {"start": v(-47.48, 9.6) * mm, "end": v(-46.56, 9.83) * mm});
            skLineSegment(sketch, "E8144", {"start": v(-46.56, 9.83) * mm, "end": v(-45.63, 10.07) * mm});
            skLineSegment(sketch, "E8145", {"start": v(-45.63, 10.07) * mm, "end": v(-44.73, 10.32) * mm});
            skLineSegment(sketch, "E8146", {"start": v(-44.73, 10.32) * mm, "end": v(-43.85, 10.58) * mm});
            skLineSegment(sketch, "E8147", {"start": v(-43.85, 10.58) * mm, "end": v(-43.02, 10.84) * mm});
            skLineSegment(sketch, "E8148", {"start": v(-43.02, 10.84) * mm, "end": v(-42.25, 11.1) * mm});
            skLineSegment(sketch, "E8149", {"start": v(-42.25, 11.1) * mm, "end": v(-41.55, 11.37) * mm});
            skLineSegment(sketch, "E8150", {"start": v(-41.55, 11.37) * mm, "end": v(-40.94, 11.62) * mm});
            skLineSegment(sketch, "E8151", {"start": v(-40.94, 11.62) * mm, "end": v(-40.67, 11.74) * mm});
            skLineSegment(sketch, "E8152", {"start": v(-40.67, 11.74) * mm, "end": v(-40.43, 11.86) * mm});
            skLineSegment(sketch, "E8153", {"start": v(-40.43, 11.86) * mm, "end": v(-39.35, 12.42) * mm});
            skLineSegment(sketch, "E8154", {"start": v(-39.35, 12.42) * mm, "end": v(-41.72, 14.37) * mm});
            skLineSegment(sketch, "E8155", {"start": v(-41.72, 14.37) * mm, "end": v(-42.5, 16.95) * mm});
            skLineSegment(sketch, "E8156", {"start": v(-42.5, 16.95) * mm, "end": v(-43.35, 16.35) * mm});
            skLineSegment(sketch, "E8157", {"start": v(-43.35, 16.35) * mm, "end": v(-43.66, 16.14) * mm});
            skLineSegment(sketch, "E8158", {"start": v(-43.66, 16.14) * mm, "end": v(-43.96, 15.95) * mm});
            skLineSegment(sketch, "E8159", {"start": v(-43.96, 15.95) * mm, "end": v(-44.26, 15.76) * mm});
            skLineSegment(sketch, "E8160", {"start": v(-44.26, 15.76) * mm, "end": v(-44.57, 15.59) * mm});
            skLineSegment(sketch, "E8161", {"start": v(-44.57, 15.59) * mm, "end": v(-44.88, 15.42) * mm});
            skLineSegment(sketch, "E8162", {"start": v(-44.88, 15.42) * mm, "end": v(-45.2, 15.26) * mm});
            skLineSegment(sketch, "E8163", {"start": v(-45.2, 15.26) * mm, "end": v(-45.53, 15.1) * mm});
            skLineSegment(sketch, "E8164", {"start": v(-45.53, 15.1) * mm, "end": v(-45.88, 14.96) * mm});
            skLineSegment(sketch, "E8165", {"start": v(-45.88, 14.96) * mm, "end": v(-46.24, 14.81) * mm});
            skLineSegment(sketch, "E8166", {"start": v(-46.24, 14.81) * mm, "end": v(-46.62, 14.67) * mm});
            skLineSegment(sketch, "E8167", {"start": v(-46.62, 14.67) * mm, "end": v(-47.02, 14.54) * mm});
            skLineSegment(sketch, "E8168", {"start": v(-47.02, 14.54) * mm, "end": v(-47.45, 14.4) * mm});
            skLineSegment(sketch, "E8169", {"start": v(-47.45, 14.4) * mm, "end": v(-48.37, 14.13) * mm});
            skLineSegment(sketch, "E8170", {"start": v(-48.37, 14.13) * mm, "end": v(-49.42, 13.85) * mm});
            skLineSegment(sketch, "E8171", {"start": v(-49.42, 13.85) * mm, "end": v(-52.4, 13.1) * mm});
            skLineSegment(sketch, "E8172", {"start": v(-52.26, 13.76) * mm, "end": v(-51.98, 15.17) * mm});
            skLineSegment(sketch, "E8173", {"start": v(-51.98, 15.17) * mm, "end": v(-51.14, 19.42) * mm});
            skLineSegment(sketch, "E8174", {"start": v(-51.14, 19.42) * mm, "end": v(-50.27, 20.42) * mm});
            skLineSegment(sketch, "E8175", {"start": v(-50.27, 20.42) * mm, "end": v(-50.15, 20.57) * mm});
            skLineSegment(sketch, "E8176", {"start": v(-50.15, 20.57) * mm, "end": v(-50, 20.74) * mm});
            skLineSegment(sketch, "E8177", {"start": v(-50, 20.74) * mm, "end": v(-47.29, 22.47) * mm});
            skLineSegment(sketch, "E8178", {"start": v(-47.29, 22.47) * mm, "end": v(-43.88, 21.31) * mm});
            skLineSegment(sketch, "E8179", {"start": v(-43.88, 21.31) * mm, "end": v(-44.08, 19.42) * mm});
            skLineSegment(sketch, "E8180", {"start": v(-44.08, 19.42) * mm, "end": v(-42.71, 17.68) * mm});
            skLineSegment(sketch, "E8181", {"start": v(-42.71, 17.68) * mm, "end": v(-43.46, 16.97) * mm});
            skLineSegment(sketch, "E8182", {"start": v(-43.46, 16.97) * mm, "end": v(-43.74, 16.73) * mm});
            skLineSegment(sketch, "E8183", {"start": v(-43.74, 16.73) * mm, "end": v(-44.06, 16.48) * mm});
            skLineSegment(sketch, "E8184", {"start": v(-44.06, 16.48) * mm, "end": v(-44.4, 16.25) * mm});
            skLineSegment(sketch, "E8185", {"start": v(-44.4, 16.25) * mm, "end": v(-44.78, 16.02) * mm});
            skLineSegment(sketch, "E8186", {"start": v(-44.78, 16.02) * mm, "end": v(-45.2, 15.8) * mm});
            skLineSegment(sketch, "E8187", {"start": v(-45.2, 15.8) * mm, "end": v(-45.63, 15.57) * mm});
            skLineSegment(sketch, "E8188", {"start": v(-45.63, 15.57) * mm, "end": v(-46.1, 15.36) * mm});
            skLineSegment(sketch, "E8189", {"start": v(-46.1, 15.36) * mm, "end": v(-46.6, 15.15) * mm});
            skLineSegment(sketch, "E8190", {"start": v(-46.6, 15.15) * mm, "end": v(-47.1, 14.96) * mm});
            skLineSegment(sketch, "E8191", {"start": v(-47.1, 14.96) * mm, "end": v(-47.64, 14.77) * mm});
            skLineSegment(sketch, "E8192", {"start": v(-47.64, 14.77) * mm, "end": v(-48.2, 14.6) * mm});
            skLineSegment(sketch, "E8193", {"start": v(-48.2, 14.6) * mm, "end": v(-48.77, 14.43) * mm});
            skLineSegment(sketch, "E8194", {"start": v(-48.77, 14.43) * mm, "end": v(-49.37, 14.27) * mm});
            skLineSegment(sketch, "E8195", {"start": v(-49.37, 14.27) * mm, "end": v(-49.97, 14.13) * mm});
            skLineSegment(sketch, "E8196", {"start": v(-49.97, 14.13) * mm, "end": v(-50.6, 14) * mm});
            skLineSegment(sketch, "E8197", {"start": v(-50.6, 14) * mm, "end": v(-51.22, 13.88) * mm});
            skLineSegment(sketch, "E8198", {"start": v(-51.22, 13.88) * mm, "end": v(-51.57, 13.83) * mm});
            skLineSegment(sketch, "E8199", {"start": v(-51.57, 13.83) * mm, "end": v(-51.87, 13.79) * mm});
            skLineSegment(sketch, "E8200", {"start": v(-51.87, 13.79) * mm, "end": v(-52.1, 13.76) * mm});
            skLineSegment(sketch, "E8201", {"start": v(-52.1, 13.76) * mm, "end": v(-52.26, 13.76) * mm});
            skLineSegment(sketch, "E8202", {"start": v(-55.69, 3.43) * mm, "end": v(-55.7, 3.45) * mm});
            skLineSegment(sketch, "E8203", {"start": v(-55.7, 3.45) * mm, "end": v(-55.1, 4.5) * mm});
            skLineSegment(sketch, "E8204", {"start": v(-55.1, 4.5) * mm, "end": v(-54.9, 4.86) * mm});
            skLineSegment(sketch, "E8205", {"start": v(-54.9, 4.86) * mm, "end": v(-54.7, 5.27) * mm});
            skLineSegment(sketch, "E8206", {"start": v(-54.7, 5.27) * mm, "end": v(-54.5, 5.71) * mm});
            skLineSegment(sketch, "E8207", {"start": v(-54.5, 5.71) * mm, "end": v(-54.3, 6.19) * mm});
            skLineSegment(sketch, "E8208", {"start": v(-54.3, 6.19) * mm, "end": v(-54.11, 6.7) * mm});
            skLineSegment(sketch, "E8209", {"start": v(-54.11, 6.7) * mm, "end": v(-53.92, 7.25) * mm});
            skLineSegment(sketch, "E8210", {"start": v(-53.92, 7.25) * mm, "end": v(-53.73, 7.83) * mm});
            skLineSegment(sketch, "E8211", {"start": v(-53.73, 7.83) * mm, "end": v(-53.68, 8.01) * mm});
            skLineSegment(sketch, "E8212", {"start": v(-53.68, 8.01) * mm, "end": v(-50.56, 8.56) * mm});
            skLineSegment(sketch, "E8213", {"start": v(-50.56, 8.56) * mm, "end": v(-49.83, 8.7) * mm});
            skLineSegment(sketch, "E8214", {"start": v(-49.83, 8.7) * mm, "end": v(-49.04, 8.85) * mm});
            skLineSegment(sketch, "E8215", {"start": v(-49.04, 8.85) * mm, "end": v(-47.37, 9.2) * mm});
            skLineSegment(sketch, "E8216", {"start": v(-47.37, 9.2) * mm, "end": v(-46.56, 9.38) * mm});
            skLineSegment(sketch, "E8217", {"start": v(-46.56, 9.38) * mm, "end": v(-45.78, 9.56) * mm});
            skLineSegment(sketch, "E8218", {"start": v(-45.78, 9.56) * mm, "end": v(-45.07, 9.74) * mm});
            skLineSegment(sketch, "E8219", {"start": v(-45.07, 9.74) * mm, "end": v(-44.46, 9.9) * mm});
            skLineSegment(sketch, "E8220", {"start": v(-44.46, 9.9) * mm, "end": v(-41.73, 10.65) * mm});
            skLineSegment(sketch, "E8221", {"start": v(-41.73, 10.65) * mm, "end": v(-39.42, 12) * mm});
            skLineSegment(sketch, "E8222", {"start": v(-39.42, 12) * mm, "end": v(-39.54, 9.05) * mm});
            skLineSegment(sketch, "E8223", {"start": v(-39.54, 9.05) * mm, "end": v(-38.04, 7.46) * mm});
            skLineSegment(sketch, "E8224", {"start": v(-38.04, 7.46) * mm, "end": v(-41.75, 6.26) * mm});
            skLineSegment(sketch, "E8225", {"start": v(-41.75, 6.26) * mm, "end": v(-42.52, 6.02) * mm});
            skLineSegment(sketch, "E8226", {"start": v(-42.52, 6.02) * mm, "end": v(-43.3, 5.79) * mm});
            skLineSegment(sketch, "E8227", {"start": v(-43.3, 5.79) * mm, "end": v(-44.08, 5.56) * mm});
            skLineSegment(sketch, "E8228", {"start": v(-44.08, 5.56) * mm, "end": v(-44.87, 5.34) * mm});
            skLineSegment(sketch, "E8229", {"start": v(-44.87, 5.34) * mm, "end": v(-45.66, 5.13) * mm});
            skLineSegment(sketch, "E8230", {"start": v(-45.66, 5.13) * mm, "end": v(-46.45, 4.93) * mm});
            skLineSegment(sketch, "E8231", {"start": v(-46.45, 4.93) * mm, "end": v(-47.24, 4.74) * mm});
            skLineSegment(sketch, "E8232", {"start": v(-47.24, 4.74) * mm, "end": v(-48.02, 4.56) * mm});
            skLineSegment(sketch, "E8233", {"start": v(-48.02, 4.56) * mm, "end": v(-48.79, 4.4) * mm});
            skLineSegment(sketch, "E8234", {"start": v(-48.79, 4.4) * mm, "end": v(-49.55, 4.24) * mm});
            skLineSegment(sketch, "E8235", {"start": v(-49.55, 4.24) * mm, "end": v(-50.3, 4.1) * mm});
            skLineSegment(sketch, "E8236", {"start": v(-50.3, 4.1) * mm, "end": v(-51.03, 3.96) * mm});
            skLineSegment(sketch, "E8237", {"start": v(-51.03, 3.96) * mm, "end": v(-51.74, 3.84) * mm});
            skLineSegment(sketch, "E8238", {"start": v(-51.74, 3.84) * mm, "end": v(-52.43, 3.74) * mm});
            skLineSegment(sketch, "E8239", {"start": v(-52.43, 3.74) * mm, "end": v(-53.1, 3.65) * mm});
            skLineSegment(sketch, "E8240", {"start": v(-53.1, 3.65) * mm, "end": v(-53.74, 3.58) * mm});
            skLineSegment(sketch, "E8241", {"start": v(-53.74, 3.58) * mm, "end": v(-55.69, 3.43) * mm});
            skLineSegment(sketch, "E8242", {"start": v(-54.18, -1.82) * mm, "end": v(-54.2, -1.76) * mm});
            skLineSegment(sketch, "E8243", {"start": v(-54.2, -1.76) * mm, "end": v(-54.31, -1.2) * mm});
            skLineSegment(sketch, "E8244", {"start": v(-54.31, -1.2) * mm, "end": v(-54.42, -0.69) * mm});
            skLineSegment(sketch, "E8245", {"start": v(-54.42, -0.69) * mm, "end": v(-54.54, -0.15) * mm});
            skLineSegment(sketch, "E8246", {"start": v(-54.54, -0.15) * mm, "end": v(-54.8, 0.9) * mm});
            skLineSegment(sketch, "E8247", {"start": v(-54.8, 0.9) * mm, "end": v(-55.07, 1.84) * mm});
            skLineSegment(sketch, "E8248", {"start": v(-55.07, 1.84) * mm, "end": v(-55.2, 2.24) * mm});
            skLineSegment(sketch, "E8249", {"start": v(-55.2, 2.24) * mm, "end": v(-55.33, 2.57) * mm});
            skLineSegment(sketch, "E8250", {"start": v(-55.33, 2.57) * mm, "end": v(-55.39, 2.7) * mm});
            skLineSegment(sketch, "E8251", {"start": v(-55.39, 2.7) * mm, "end": v(-55.39, 2.8) * mm});
            skLineSegment(sketch, "E8252", {"start": v(-55.39, 2.8) * mm, "end": v(-55.38, 2.84) * mm});
            skLineSegment(sketch, "E8253", {"start": v(-55.38, 2.84) * mm, "end": v(-55.36, 2.87) * mm});
            skLineSegment(sketch, "E8254", {"start": v(-55.36, 2.87) * mm, "end": v(-55.23, 3.12) * mm});
            skLineSegment(sketch, "E8255", {"start": v(-55.23, 3.12) * mm, "end": v(-52.87, 3.12) * mm});
            skLineSegment(sketch, "E8256", {"start": v(-52.87, 3.12) * mm, "end": v(-44.7, 4.77) * mm});
            skLineSegment(sketch, "E8257", {"start": v(-44.7, 4.77) * mm, "end": v(-41.32, 5.92) * mm});
            skLineSegment(sketch, "E8258", {"start": v(-41.32, 5.92) * mm, "end": v(-40, 6.37) * mm});
            skLineSegment(sketch, "E8259", {"start": v(-40, 6.37) * mm, "end": v(-38.86, 6.74) * mm});
            skLineSegment(sketch, "E8260", {"start": v(-38.86, 6.74) * mm, "end": v(-38.06, 6.99) * mm});
            skLineSegment(sketch, "E8261", {"start": v(-38.06, 6.99) * mm, "end": v(-37.81, 7.05) * mm});
            skLineSegment(sketch, "E8262", {"start": v(-37.81, 7.05) * mm, "end": v(-37.7, 7.08) * mm});
            skLineSegment(sketch, "E8263", {"start": v(-37.7, 7.08) * mm, "end": v(-37.45, 7.08) * mm});
            skLineSegment(sketch, "E8264", {"start": v(-37.45, 7.08) * mm, "end": v(-37.45, 4.74) * mm});
            skLineSegment(sketch, "E8265", {"start": v(-37.45, 4.74) * mm, "end": v(-36.74, 3.75) * mm});
            skLineSegment(sketch, "E8266", {"start": v(-36.74, 3.75) * mm, "end": v(-36.57, 3.59) * mm});
            skLineSegment(sketch, "E8267", {"start": v(-36.57, 3.59) * mm, "end": v(-36.4, 3.44) * mm});
            skLineSegment(sketch, "E8268", {"start": v(-36.4, 3.44) * mm, "end": v(-36.1, 3.21) * mm});
            skLineSegment(sketch, "E8269", {"start": v(-36.1, 3.21) * mm, "end": v(-35.88, 3.05) * mm});
            skLineSegment(sketch, "E8270", {"start": v(-35.88, 3.05) * mm, "end": v(-35.82, 3) * mm});
            skLineSegment(sketch, "E8271", {"start": v(-35.82, 3) * mm, "end": v(-35.8, 2.97) * mm});
            skLineSegment(sketch, "E8272", {"start": v(-35.8, 2.97) * mm, "end": v(-35.83, 2.92) * mm});
            skLineSegment(sketch, "E8273", {"start": v(-35.83, 2.92) * mm, "end": v(-35.93, 2.83) * mm});
            skLineSegment(sketch, "E8274", {"start": v(-35.93, 2.83) * mm, "end": v(-36.28, 2.53) * mm});
            skLineSegment(sketch, "E8275", {"start": v(-36.28, 2.53) * mm, "end": v(-36.8, 2.12) * mm});
            skLineSegment(sketch, "E8276", {"start": v(-36.8, 2.12) * mm, "end": v(-37.44, 1.64) * mm});
            skLineSegment(sketch, "E8277", {"start": v(-37.44, 1.64) * mm, "end": v(-39.08, 0.44) * mm});
            skLineSegment(sketch, "E8278", {"start": v(-39.08, 0.44) * mm, "end": v(-42.83, -0.88) * mm});
            skLineSegment(sketch, "E8279", {"start": v(-42.83, -0.88) * mm, "end": v(-46.82, -1.35) * mm});
            skLineSegment(sketch, "E8280", {"start": v(-46.82, -1.35) * mm, "end": v(-47.66, -1.45) * mm});
            skLineSegment(sketch, "E8281", {"start": v(-47.66, -1.45) * mm, "end": v(-48.52, -1.54) * mm});
            skLineSegment(sketch, "E8282", {"start": v(-48.52, -1.54) * mm, "end": v(-50.18, -1.69) * mm});
            skLineSegment(sketch, "E8283", {"start": v(-50.18, -1.69) * mm, "end": v(-50.95, -1.74) * mm});
            skLineSegment(sketch, "E8284", {"start": v(-50.95, -1.74) * mm, "end": v(-51.63, -1.79) * mm});
            skLineSegment(sketch, "E8285", {"start": v(-51.63, -1.79) * mm, "end": v(-52.2, -1.82) * mm});
            skLineSegment(sketch, "E8286", {"start": v(-52.2, -1.82) * mm, "end": v(-52.66, -1.83) * mm});
            skLineSegment(sketch, "E8287", {"start": v(-52.66, -1.83) * mm, "end": v(-54.18, -1.82) * mm});
            skLineSegment(sketch, "E8288", {"start": v(-31.8, -30.45) * mm, "end": v(-31.5, -30.45) * mm});
            skLineSegment(sketch, "E8289", {"start": v(-31.5, -30.45) * mm, "end": v(-30.64, -30.46) * mm});
            skLineSegment(sketch, "E8290", {"start": v(-30.64, -30.46) * mm, "end": v(-29.84, -30.5) * mm});
            skLineSegment(sketch, "E8291", {"start": v(-29.84, -30.5) * mm, "end": v(-29.74, -30.5) * mm});
            skLineSegment(sketch, "E8292", {"start": v(-29.74, -30.5) * mm, "end": v(-29.63, -30.53) * mm});
            skLineSegment(sketch, "E8293", {"start": v(-29.63, -30.53) * mm, "end": v(-29.53, -30.57) * mm});
            skLineSegment(sketch, "E8294", {"start": v(-29.53, -30.57) * mm, "end": v(-29.44, -30.62) * mm});
            skLineSegment(sketch, "E8295", {"start": v(-29.44, -30.62) * mm, "end": v(-29.41, -30.61) * mm});
            skLineSegment(sketch, "E8296", {"start": v(-29.41, -30.61) * mm, "end": v(-29.23, -30.55) * mm});
            skLineSegment(sketch, "E8297", {"start": v(-29.23, -30.55) * mm, "end": v(-29.04, -30.46) * mm});
            skLineSegment(sketch, "E8298", {"start": v(-29.04, -30.46) * mm, "end": v(-28.86, -30.35) * mm});
            skLineSegment(sketch, "E8299", {"start": v(-28.86, -30.35) * mm, "end": v(-28.67, -30.23) * mm});
            skLineSegment(sketch, "E8300", {"start": v(-28.67, -30.23) * mm, "end": v(-28.3, -29.97) * mm});
            skLineSegment(sketch, "E8301", {"start": v(-28.3, -29.97) * mm, "end": v(-28.12, -29.85) * mm});
            skLineSegment(sketch, "E8302", {"start": v(-28.12, -29.85) * mm, "end": v(-27.95, -29.75) * mm});
            skLineSegment(sketch, "E8303", {"start": v(-27.95, -29.75) * mm, "end": v(-27.31, -29.4) * mm});
            skLineSegment(sketch, "E8304", {"start": v(-27.31, -29.4) * mm, "end": v(-26.64, -29) * mm});
            skLineSegment(sketch, "E8305", {"start": v(-26.64, -29) * mm, "end": v(-26.31, -28.81) * mm});
            skLineSegment(sketch, "E8306", {"start": v(-26.31, -28.81) * mm, "end": v(-26, -28.62) * mm});
            skLineSegment(sketch, "E8307", {"start": v(-26, -28.62) * mm, "end": v(-25.72, -28.43) * mm});
            skLineSegment(sketch, "E8308", {"start": v(-25.72, -28.43) * mm, "end": v(-25.48, -28.25) * mm});
            skLineSegment(sketch, "E8309", {"start": v(-25.48, -28.25) * mm, "end": v(-24.88, -26.71) * mm});
            skLineSegment(sketch, "E8310", {"start": v(-24.88, -26.71) * mm, "end": v(-24.43, -25.5) * mm});
            skLineSegment(sketch, "E8311", {"start": v(-24.43, -25.5) * mm, "end": v(-24.26, -25) * mm});
            skLineSegment(sketch, "E8312", {"start": v(-24.26, -25) * mm, "end": v(-24.12, -24.56) * mm});
            skLineSegment(sketch, "E8313", {"start": v(-24.12, -24.56) * mm, "end": v(-24, -24.2) * mm});
            skLineSegment(sketch, "E8314", {"start": v(-24, -24.2) * mm, "end": v(-23.93, -23.9) * mm});
            skLineSegment(sketch, "E8315", {"start": v(-23.93, -23.9) * mm, "end": v(-23.87, -23.66) * mm});
            skLineSegment(sketch, "E8316", {"start": v(-23.87, -23.66) * mm, "end": v(-23.84, -23.48) * mm});
            skLineSegment(sketch, "E8317", {"start": v(-23.84, -23.48) * mm, "end": v(-23.83, -23.36) * mm});
            skLineSegment(sketch, "E8318", {"start": v(-23.83, -23.36) * mm, "end": v(-23.85, -23.28) * mm});
            skLineSegment(sketch, "E8319", {"start": v(-23.85, -23.28) * mm, "end": v(-23.86, -23.26) * mm});
            skLineSegment(sketch, "E8320", {"start": v(-23.86, -23.26) * mm, "end": v(-23.88, -23.26) * mm});
            skLineSegment(sketch, "E8321", {"start": v(-23.88, -23.26) * mm, "end": v(-23.9, -23.26) * mm});
            skLineSegment(sketch, "E8322", {"start": v(-23.9, -23.26) * mm, "end": v(-23.93, -23.28) * mm});
            skLineSegment(sketch, "E8323", {"start": v(-23.93, -23.28) * mm, "end": v(-24, -23.34) * mm});
            skLineSegment(sketch, "E8324", {"start": v(-24, -23.34) * mm, "end": v(-24.08, -23.44) * mm});
            skLineSegment(sketch, "E8325", {"start": v(-24.08, -23.44) * mm, "end": v(-24.46, -23.93) * mm});
            skLineSegment(sketch, "E8326", {"start": v(-24.46, -23.93) * mm, "end": v(-24.88, -24.43) * mm});
            skLineSegment(sketch, "E8327", {"start": v(-24.88, -24.43) * mm, "end": v(-25.34, -24.94) * mm});
            skLineSegment(sketch, "E8328", {"start": v(-25.34, -24.94) * mm, "end": v(-25.82, -25.44) * mm});
            skLineSegment(sketch, "E8329", {"start": v(-25.82, -25.44) * mm, "end": v(-26.31, -25.93) * mm});
            skLineSegment(sketch, "E8330", {"start": v(-26.31, -25.93) * mm, "end": v(-26.82, -26.38) * mm});
            skLineSegment(sketch, "E8331", {"start": v(-26.82, -26.38) * mm, "end": v(-27.32, -26.8) * mm});
            skLineSegment(sketch, "E8332", {"start": v(-27.32, -26.8) * mm, "end": v(-27.57, -27) * mm});
            skLineSegment(sketch, "E8333", {"start": v(-27.57, -27) * mm, "end": v(-27.81, -27.17) * mm});
            skLineSegment(sketch, "E8334", {"start": v(-27.81, -27.17) * mm, "end": v(-28.04, -27.33) * mm});
            skLineSegment(sketch, "E8335", {"start": v(-28.04, -27.33) * mm, "end": v(-28.29, -27.48) * mm});
            skLineSegment(sketch, "E8336", {"start": v(-28.29, -27.48) * mm, "end": v(-28.54, -27.62) * mm});
            skLineSegment(sketch, "E8337", {"start": v(-28.54, -27.62) * mm, "end": v(-28.8, -27.76) * mm});
            skLineSegment(sketch, "E8338", {"start": v(-28.8, -27.76) * mm, "end": v(-29.37, -28.03) * mm});
            skLineSegment(sketch, "E8339", {"start": v(-29.37, -28.03) * mm, "end": v(-29.94, -28.3) * mm});
            skLineSegment(sketch, "E8340", {"start": v(-29.94, -28.3) * mm, "end": v(-31.1, -28.78) * mm});
            skLineSegment(sketch, "E8341", {"start": v(-31.1, -28.78) * mm, "end": v(-31.65, -29.02) * mm});
            skLineSegment(sketch, "E8342", {"start": v(-31.65, -29.02) * mm, "end": v(-32.17, -29.25) * mm});
            skLineSegment(sketch, "E8343", {"start": v(-32.17, -29.25) * mm, "end": v(-32.17, -29.66) * mm});
            skLineSegment(sketch, "E8344", {"start": v(-32.17, -29.66) * mm, "end": v(-32.16, -29.75) * mm});
            skLineSegment(sketch, "E8345", {"start": v(-32.16, -29.75) * mm, "end": v(-32.14, -29.85) * mm});
            skLineSegment(sketch, "E8346", {"start": v(-32.14, -29.85) * mm, "end": v(-32.1, -29.95) * mm});
            skLineSegment(sketch, "E8347", {"start": v(-32.1, -29.95) * mm, "end": v(-32.06, -30.06) * mm});
            skLineSegment(sketch, "E8348", {"start": v(-32.06, -30.06) * mm, "end": v(-32, -30.16) * mm});
            skLineSegment(sketch, "E8349", {"start": v(-32, -30.16) * mm, "end": v(-31.94, -30.26) * mm});
            skLineSegment(sketch, "E8350", {"start": v(-31.94, -30.26) * mm, "end": v(-31.87, -30.36) * mm});
            skLineSegment(sketch, "E8351", {"start": v(-31.87, -30.36) * mm, "end": v(-31.8, -30.45) * mm});
            skLineSegment(sketch, "E8352", {"start": v(-29.46, -32.24) * mm, "end": v(-29.42, -32.07) * mm});
            skLineSegment(sketch, "E8353", {"start": v(-29.42, -32.07) * mm, "end": v(-29.4, -32.03) * mm});
            skLineSegment(sketch, "E8354", {"start": v(-29.4, -32.03) * mm, "end": v(-29.4, -32.02) * mm});
            skLineSegment(sketch, "E8355", {"start": v(-29.4, -32.02) * mm, "end": v(-29.2, -31.7) * mm});
            skLineSegment(sketch, "E8356", {"start": v(-29.2, -31.7) * mm, "end": v(-29.15, -31.6) * mm});
            skLineSegment(sketch, "E8357", {"start": v(-29.15, -31.6) * mm, "end": v(-29.11, -31.5) * mm});
            skLineSegment(sketch, "E8358", {"start": v(-29.11, -31.5) * mm, "end": v(-29.09, -31.39) * mm});
            skLineSegment(sketch, "E8359", {"start": v(-29.09, -31.39) * mm, "end": v(-29.08, -31.28) * mm});
            skLineSegment(sketch, "E8360", {"start": v(-29.08, -31.28) * mm, "end": v(-28.88, -31.08) * mm});
            skLineSegment(sketch, "E8361", {"start": v(-28.88, -31.08) * mm, "end": v(-28.66, -30.9) * mm});
            skLineSegment(sketch, "E8362", {"start": v(-28.66, -30.9) * mm, "end": v(-28.45, -30.72) * mm});
            skLineSegment(sketch, "E8363", {"start": v(-28.45, -30.72) * mm, "end": v(-28.24, -30.53) * mm});
            skLineSegment(sketch, "E8364", {"start": v(-28.24, -30.53) * mm, "end": v(-28.01, -30.35) * mm});
            skLineSegment(sketch, "E8365", {"start": v(-28.01, -30.35) * mm, "end": v(-27.9, -30.27) * mm});
            skLineSegment(sketch, "E8366", {"start": v(-27.9, -30.27) * mm, "end": v(-27.79, -30.2) * mm});
            skLineSegment(sketch, "E8367", {"start": v(-27.79, -30.2) * mm, "end": v(-27.61, -30.13) * mm});
            skLineSegment(sketch, "E8368", {"start": v(-27.61, -30.13) * mm, "end": v(-27.42, -30.06) * mm});
            skLineSegment(sketch, "E8369", {"start": v(-27.42, -30.06) * mm, "end": v(-27, -29.94) * mm});
            skLineSegment(sketch, "E8370", {"start": v(-27, -29.94) * mm, "end": v(-26.58, -29.83) * mm});
            skLineSegment(sketch, "E8371", {"start": v(-26.58, -29.83) * mm, "end": v(-26.2, -29.73) * mm});
            skLineSegment(sketch, "E8372", {"start": v(-26.2, -29.73) * mm, "end": v(-25.83, -29.63) * mm});
            skLineSegment(sketch, "E8373", {"start": v(-25.83, -29.63) * mm, "end": v(-25.4, -29.53) * mm});
            skLineSegment(sketch, "E8374", {"start": v(-25.4, -29.53) * mm, "end": v(-24.9, -29.43) * mm});
            skLineSegment(sketch, "E8375", {"start": v(-24.9, -29.43) * mm, "end": v(-24.38, -29.33) * mm});
            skLineSegment(sketch, "E8376", {"start": v(-24.38, -29.33) * mm, "end": v(-23.84, -29.24) * mm});
            skLineSegment(sketch, "E8377", {"start": v(-23.84, -29.24) * mm, "end": v(-23.3, -29.16) * mm});
            skLineSegment(sketch, "E8378", {"start": v(-23.3, -29.16) * mm, "end": v(-22.77, -29.09) * mm});
            skLineSegment(sketch, "E8379", {"start": v(-22.77, -29.09) * mm, "end": v(-22.27, -29.03) * mm});
            skLineSegment(sketch, "E8380", {"start": v(-22.27, -29.03) * mm, "end": v(-19.94, -28.8) * mm});
            skLineSegment(sketch, "E8381", {"start": v(-19.94, -28.8) * mm, "end": v(-19.62, -28.2) * mm});
            skLineSegment(sketch, "E8382", {"start": v(-19.62, -28.2) * mm, "end": v(-19.55, -28.07) * mm});
            skLineSegment(sketch, "E8383", {"start": v(-19.55, -28.07) * mm, "end": v(-19.5, -27.9) * mm});
            skLineSegment(sketch, "E8384", {"start": v(-19.5, -27.9) * mm, "end": v(-19.44, -27.7) * mm});
            skLineSegment(sketch, "E8385", {"start": v(-19.44, -27.7) * mm, "end": v(-19.4, -27.5) * mm});
            skLineSegment(sketch, "E8386", {"start": v(-19.4, -27.5) * mm, "end": v(-19.35, -27.29) * mm});
            skLineSegment(sketch, "E8387", {"start": v(-19.35, -27.29) * mm, "end": v(-19.32, -27.07) * mm});
            skLineSegment(sketch, "E8388", {"start": v(-19.32, -27.07) * mm, "end": v(-19.3, -26.86) * mm});
            skLineSegment(sketch, "E8389", {"start": v(-19.3, -26.86) * mm, "end": v(-19.3, -26.65) * mm});
            skLineSegment(sketch, "E8390", {"start": v(-19.3, -26.65) * mm, "end": v(-19.32, -26.42) * mm});
            skLineSegment(sketch, "E8391", {"start": v(-19.32, -26.42) * mm, "end": v(-19.35, -26.16) * mm});
            skLineSegment(sketch, "E8392", {"start": v(-19.35, -26.16) * mm, "end": v(-19.36, -26.03) * mm});
            skLineSegment(sketch, "E8393", {"start": v(-19.36, -26.03) * mm, "end": v(-19.36, -25.9) * mm});
            skLineSegment(sketch, "E8394", {"start": v(-19.36, -25.9) * mm, "end": v(-19.34, -25.8) * mm});
            skLineSegment(sketch, "E8395", {"start": v(-19.34, -25.8) * mm, "end": v(-19.3, -25.7) * mm});
            skLineSegment(sketch, "E8396", {"start": v(-19.3, -25.7) * mm, "end": v(-19.18, -25.52) * mm});
            skLineSegment(sketch, "E8397", {"start": v(-19.18, -25.52) * mm, "end": v(-19.04, -25.36) * mm});
            skLineSegment(sketch, "E8398", {"start": v(-19.04, -25.36) * mm, "end": v(-18.87, -25.22) * mm});
            skLineSegment(sketch, "E8399", {"start": v(-18.87, -25.22) * mm, "end": v(-18.7, -25.08) * mm});
            skLineSegment(sketch, "E8400", {"start": v(-18.7, -25.08) * mm, "end": v(-18.5, -24.96) * mm});
            skLineSegment(sketch, "E8401", {"start": v(-18.5, -24.96) * mm, "end": v(-18.32, -24.84) * mm});
            skLineSegment(sketch, "E8402", {"start": v(-18.32, -24.84) * mm, "end": v(-17.94, -24.63) * mm});
            skLineSegment(sketch, "E8403", {"start": v(-17.94, -24.63) * mm, "end": v(-17.35, -24.33) * mm});
            skLineSegment(sketch, "E8404", {"start": v(-17.35, -24.33) * mm, "end": v(-16.88, -24.1) * mm});
            skLineSegment(sketch, "E8405", {"start": v(-16.88, -24.1) * mm, "end": v(-16.42, -23.93) * mm});
            skLineSegment(sketch, "E8406", {"start": v(-16.42, -23.93) * mm, "end": v(-15.9, -23.75) * mm});
            skLineSegment(sketch, "E8407", {"start": v(-15.9, -23.75) * mm, "end": v(-15.4, -23.58) * mm});
            skLineSegment(sketch, "E8408", {"start": v(-15.4, -23.58) * mm, "end": v(-15.05, -23.48) * mm});
            skLineSegment(sketch, "E8409", {"start": v(-15.05, -23.48) * mm, "end": v(-14.67, -23.37) * mm});
            skLineSegment(sketch, "E8410", {"start": v(-14.67, -23.37) * mm, "end": v(-14.3, -23.27) * mm});
            skLineSegment(sketch, "E8411", {"start": v(-14.3, -23.27) * mm, "end": v(-13.94, -23.2) * mm});
            skLineSegment(sketch, "E8412", {"start": v(-13.94, -23.2) * mm, "end": v(-13.65, -23.15) * mm});
            skLineSegment(sketch, "E8413", {"start": v(-13.65, -23.15) * mm, "end": v(-13.53, -23.14) * mm});
            skLineSegment(sketch, "E8414", {"start": v(-13.53, -23.14) * mm, "end": v(-13.43, -23.15) * mm});
            skLineSegment(sketch, "E8415", {"start": v(-13.43, -23.15) * mm, "end": v(-13.19, -23.18) * mm});
            skLineSegment(sketch, "E8416", {"start": v(-13.19, -23.18) * mm, "end": v(-12.92, -23.25) * mm});
            skLineSegment(sketch, "E8417", {"start": v(-12.92, -23.25) * mm, "end": v(-12.78, -23.3) * mm});
            skLineSegment(sketch, "E8418", {"start": v(-12.78, -23.3) * mm, "end": v(-12.66, -23.34) * mm});
            skLineSegment(sketch, "E8419", {"start": v(-12.66, -23.34) * mm, "end": v(-12.55, -23.4) * mm});
            skLineSegment(sketch, "E8420", {"start": v(-12.55, -23.4) * mm, "end": v(-12.45, -23.47) * mm});
            skLineSegment(sketch, "E8421", {"start": v(-12.45, -23.47) * mm, "end": v(-11.83, -23.98) * mm});
            skLineSegment(sketch, "E8422", {"start": v(-11.83, -23.98) * mm, "end": v(-11.5, -24.27) * mm});
            skLineSegment(sketch, "E8423", {"start": v(-11.5, -24.27) * mm, "end": v(-11.18, -24.57) * mm});
            skLineSegment(sketch, "E8424", {"start": v(-11.18, -24.57) * mm, "end": v(-10.87, -24.88) * mm});
            skLineSegment(sketch, "E8425", {"start": v(-10.87, -24.88) * mm, "end": v(-10.73, -25.04) * mm});
            skLineSegment(sketch, "E8426", {"start": v(-10.73, -25.04) * mm, "end": v(-10.6, -25.2) * mm});
            skLineSegment(sketch, "E8427", {"start": v(-10.6, -25.2) * mm, "end": v(-10.47, -25.36) * mm});
            skLineSegment(sketch, "E8428", {"start": v(-10.47, -25.36) * mm, "end": v(-10.36, -25.53) * mm});
            skLineSegment(sketch, "E8429", {"start": v(-10.36, -25.53) * mm, "end": v(-10.26, -25.7) * mm});
            skLineSegment(sketch, "E8430", {"start": v(-10.26, -25.7) * mm, "end": v(-10.18, -25.87) * mm});
            skLineSegment(sketch, "E8431", {"start": v(-10.18, -25.87) * mm, "end": v(-10.13, -26) * mm});
            skLineSegment(sketch, "E8432", {"start": v(-10.13, -26) * mm, "end": v(-10.1, -26.15) * mm});
            skLineSegment(sketch, "E8433", {"start": v(-10.1, -26.15) * mm, "end": v(-10.1, -26.3) * mm});
            skLineSegment(sketch, "E8434", {"start": v(-10.1, -26.3) * mm, "end": v(-10.09, -26.46) * mm});
            skLineSegment(sketch, "E8435", {"start": v(-10.09, -26.46) * mm, "end": v(-10.1, -26.78) * mm});
            skLineSegment(sketch, "E8436", {"start": v(-10.1, -26.78) * mm, "end": v(-10.1, -26.93) * mm});
            skLineSegment(sketch, "E8437", {"start": v(-10.1, -26.93) * mm, "end": v(-10.09, -27.07) * mm});
            skLineSegment(sketch, "E8438", {"start": v(-10.09, -27.07) * mm, "end": v(-11.72, -28.33) * mm});
            skLineSegment(sketch, "E8439", {"start": v(-11.72, -28.33) * mm, "end": v(-12.05, -28.6) * mm});
            skLineSegment(sketch, "E8440", {"start": v(-12.05, -28.6) * mm, "end": v(-12.36, -28.85) * mm});
            skLineSegment(sketch, "E8441", {"start": v(-12.36, -28.85) * mm, "end": v(-12.64, -29.1) * mm});
            skLineSegment(sketch, "E8442", {"start": v(-12.64, -29.1) * mm, "end": v(-12.88, -29.33) * mm});
            skLineSegment(sketch, "E8443", {"start": v(-12.88, -29.33) * mm, "end": v(-13.08, -29.53) * mm});
            skLineSegment(sketch, "E8444", {"start": v(-13.08, -29.53) * mm, "end": v(-13.23, -29.7) * mm});
            skLineSegment(sketch, "E8445", {"start": v(-13.23, -29.7) * mm, "end": v(-13.33, -29.85) * mm});
            skLineSegment(sketch, "E8446", {"start": v(-13.33, -29.85) * mm, "end": v(-13.35, -29.9) * mm});
            skLineSegment(sketch, "E8447", {"start": v(-13.35, -29.9) * mm, "end": v(-13.36, -29.94) * mm});
            skLineSegment(sketch, "E8448", {"start": v(-13.36, -29.94) * mm, "end": v(-13.36, -30.3) * mm});
            skLineSegment(sketch, "E8449", {"start": v(-13.36, -30.3) * mm, "end": v(-9.12, -34.79) * mm});
            skLineSegment(sketch, "E8450", {"start": v(-9.12, -34.79) * mm, "end": v(-9.3, -35.47) * mm});
            skLineSegment(sketch, "E8451", {"start": v(-9.3, -35.47) * mm, "end": v(-9.37, -35.72) * mm});
            skLineSegment(sketch, "E8452", {"start": v(-9.37, -35.72) * mm, "end": v(-9.45, -35.91) * mm});
            skLineSegment(sketch, "E8453", {"start": v(-9.45, -35.91) * mm, "end": v(-9.5, -35.99) * mm});
            skLineSegment(sketch, "E8454", {"start": v(-9.5, -35.99) * mm, "end": v(-9.54, -36.05) * mm});
            skLineSegment(sketch, "E8455", {"start": v(-9.54, -36.05) * mm, "end": v(-9.59, -36.1) * mm});
            skLineSegment(sketch, "E8456", {"start": v(-9.59, -36.1) * mm, "end": v(-9.63, -36.14) * mm});
            skLineSegment(sketch, "E8457", {"start": v(-9.63, -36.14) * mm, "end": v(-9.68, -36.16) * mm});
            skLineSegment(sketch, "E8458", {"start": v(-9.68, -36.16) * mm, "end": v(-9.73, -36.16) * mm});
            skLineSegment(sketch, "E8459", {"start": v(-9.73, -36.16) * mm, "end": v(-9.79, -36.15) * mm});
            skLineSegment(sketch, "E8460", {"start": v(-9.79, -36.15) * mm, "end": v(-9.84, -36.13) * mm});
            skLineSegment(sketch, "E8461", {"start": v(-9.84, -36.13) * mm, "end": v(-9.9, -36.09) * mm});
            skLineSegment(sketch, "E8462", {"start": v(-9.9, -36.09) * mm, "end": v(-9.95, -36.03) * mm});
            skLineSegment(sketch, "E8463", {"start": v(-9.95, -36.03) * mm, "end": v(-10.01, -35.95) * mm});
            skLineSegment(sketch, "E8464", {"start": v(-10.01, -35.95) * mm, "end": v(-10.07, -35.86) * mm});
            skLineSegment(sketch, "E8465", {"start": v(-10.07, -35.86) * mm, "end": v(-10.14, -35.77) * mm});
            skLineSegment(sketch, "E8466", {"start": v(-10.14, -35.77) * mm, "end": v(-10.24, -35.66) * mm});
            skLineSegment(sketch, "E8467", {"start": v(-10.24, -35.66) * mm, "end": v(-10.34, -35.56) * mm});
            skLineSegment(sketch, "E8468", {"start": v(-10.34, -35.56) * mm, "end": v(-10.43, -35.49) * mm});
            skLineSegment(sketch, "E8469", {"start": v(-10.43, -35.49) * mm, "end": v(-10.53, -35.44) * mm});
            skLineSegment(sketch, "E8470", {"start": v(-10.53, -35.44) * mm, "end": v(-10.64, -35.4) * mm});
            skLineSegment(sketch, "E8471", {"start": v(-10.64, -35.4) * mm, "end": v(-10.76, -35.35) * mm});
            skLineSegment(sketch, "E8472", {"start": v(-10.76, -35.35) * mm, "end": v(-10.88, -35.32) * mm});
            skLineSegment(sketch, "E8473", {"start": v(-10.88, -35.32) * mm, "end": v(-11.14, -35.28) * mm});
            skLineSegment(sketch, "E8474", {"start": v(-11.14, -35.28) * mm, "end": v(-11.41, -35.26) * mm});
            skLineSegment(sketch, "E8475", {"start": v(-11.41, -35.26) * mm, "end": v(-11.68, -35.27) * mm});
            skLineSegment(sketch, "E8476", {"start": v(-11.68, -35.27) * mm, "end": v(-11.81, -35.3) * mm});
            skLineSegment(sketch, "E8477", {"start": v(-11.81, -35.3) * mm, "end": v(-11.94, -35.32) * mm});
            skLineSegment(sketch, "E8478", {"start": v(-11.94, -35.32) * mm, "end": v(-12.06, -35.35) * mm});
            skLineSegment(sketch, "E8479", {"start": v(-12.06, -35.35) * mm, "end": v(-12.18, -35.39) * mm});
            skLineSegment(sketch, "E8480", {"start": v(-12.18, -35.39) * mm, "end": v(-12.28, -35.43) * mm});
            skLineSegment(sketch, "E8481", {"start": v(-12.28, -35.43) * mm, "end": v(-12.38, -35.49) * mm});
            skLineSegment(sketch, "E8482", {"start": v(-12.38, -35.49) * mm, "end": v(-12.44, -35.53) * mm});
            skLineSegment(sketch, "E8483", {"start": v(-12.44, -35.53) * mm, "end": v(-12.5, -35.58) * mm});
            skLineSegment(sketch, "E8484", {"start": v(-12.5, -35.58) * mm, "end": v(-12.58, -35.7) * mm});
            skLineSegment(sketch, "E8485", {"start": v(-12.58, -35.7) * mm, "end": v(-12.65, -35.85) * mm});
            skLineSegment(sketch, "E8486", {"start": v(-12.65, -35.85) * mm, "end": v(-12.72, -36.01) * mm});
            skLineSegment(sketch, "E8487", {"start": v(-12.72, -36.01) * mm, "end": v(-12.82, -36.34) * mm});
            skLineSegment(sketch, "E8488", {"start": v(-12.82, -36.34) * mm, "end": v(-12.87, -36.5) * mm});
            skLineSegment(sketch, "E8489", {"start": v(-12.87, -36.5) * mm, "end": v(-12.93, -36.64) * mm});
            skLineSegment(sketch, "E8490", {"start": v(-12.93, -36.64) * mm, "end": v(-13.05, -36.87) * mm});
            skLineSegment(sketch, "E8491", {"start": v(-13.05, -36.87) * mm, "end": v(-13.16, -37.1) * mm});
            skLineSegment(sketch, "E8492", {"start": v(-13.16, -37.1) * mm, "end": v(-13.28, -37.29) * mm});
            skLineSegment(sketch, "E8493", {"start": v(-13.28, -37.29) * mm, "end": v(-13.39, -37.46) * mm});
            skLineSegment(sketch, "E8494", {"start": v(-13.39, -37.46) * mm, "end": v(-13.5, -37.6) * mm});
            skLineSegment(sketch, "E8495", {"start": v(-13.5, -37.6) * mm, "end": v(-13.58, -37.7) * mm});
            skLineSegment(sketch, "E8496", {"start": v(-13.58, -37.7) * mm, "end": v(-13.66, -37.77) * mm});
            skLineSegment(sketch, "E8497", {"start": v(-13.66, -37.77) * mm, "end": v(-13.69, -37.8) * mm});
            skLineSegment(sketch, "E8498", {"start": v(-13.69, -37.8) * mm, "end": v(-13.72, -37.8) * mm});
            skLineSegment(sketch, "E8499", {"start": v(-13.72, -37.8) * mm, "end": v(-13.75, -37.79) * mm});
            skLineSegment(sketch, "E8500", {"start": v(-13.75, -37.79) * mm, "end": v(-13.79, -37.76) * mm});
            skLineSegment(sketch, "E8501", {"start": v(-13.79, -37.76) * mm, "end": v(-13.9, -37.67) * mm});
            skLineSegment(sketch, "E8502", {"start": v(-13.9, -37.67) * mm, "end": v(-14.06, -37.51) * mm});
            skLineSegment(sketch, "E8503", {"start": v(-14.06, -37.51) * mm, "end": v(-14.25, -37.31) * mm});
            skLineSegment(sketch, "E8504", {"start": v(-14.25, -37.31) * mm, "end": v(-14.46, -37.07) * mm});
            skLineSegment(sketch, "E8505", {"start": v(-14.46, -37.07) * mm, "end": v(-14.7, -36.79) * mm});
            skLineSegment(sketch, "E8506", {"start": v(-14.7, -36.79) * mm, "end": v(-14.95, -36.48) * mm});
            skLineSegment(sketch, "E8507", {"start": v(-14.95, -36.48) * mm, "end": v(-15.2, -36.15) * mm});
            skLineSegment(sketch, "E8508", {"start": v(-15.2, -36.15) * mm, "end": v(-15.71, -35.5) * mm});
            skLineSegment(sketch, "E8509", {"start": v(-15.71, -35.5) * mm, "end": v(-16.15, -34.98) * mm});
            skLineSegment(sketch, "E8510", {"start": v(-16.15, -34.98) * mm, "end": v(-16.33, -34.78) * mm});
            skLineSegment(sketch, "E8511", {"start": v(-16.33, -34.78) * mm, "end": v(-16.48, -34.63) * mm});
            skLineSegment(sketch, "E8512", {"start": v(-16.48, -34.63) * mm, "end": v(-16.6, -34.53) * mm});
            skLineSegment(sketch, "E8513", {"start": v(-16.6, -34.53) * mm, "end": v(-16.63, -34.5) * mm});
            skLineSegment(sketch, "E8514", {"start": v(-16.63, -34.5) * mm, "end": v(-16.66, -34.5) * mm});
            skLineSegment(sketch, "E8515", {"start": v(-16.66, -34.5) * mm, "end": v(-16.69, -34.5) * mm});
            skLineSegment(sketch, "E8516", {"start": v(-16.69, -34.5) * mm, "end": v(-16.73, -34.53) * mm});
            skLineSegment(sketch, "E8517", {"start": v(-16.73, -34.53) * mm, "end": v(-16.86, -34.63) * mm});
            skLineSegment(sketch, "E8518", {"start": v(-16.86, -34.63) * mm, "end": v(-17.04, -34.78) * mm});
            skLineSegment(sketch, "E8519", {"start": v(-17.04, -34.78) * mm, "end": v(-17.27, -34.99) * mm});
            skLineSegment(sketch, "E8520", {"start": v(-17.27, -34.99) * mm, "end": v(-17.84, -35.52) * mm});
            skLineSegment(sketch, "E8521", {"start": v(-17.84, -35.52) * mm, "end": v(-18.49, -36.16) * mm});
            skLineSegment(sketch, "E8522", {"start": v(-18.49, -36.16) * mm, "end": v(-20.12, -37.83) * mm});
            skLineSegment(sketch, "E8523", {"start": v(-20.12, -37.83) * mm, "end": v(-21.11, -37.26) * mm});
            skLineSegment(sketch, "E8524", {"start": v(-21.11, -37.26) * mm, "end": v(-21.74, -36.55) * mm});
            skLineSegment(sketch, "E8525", {"start": v(-21.74, -36.55) * mm, "end": v(-21.87, -36.4) * mm});
            skLineSegment(sketch, "E8526", {"start": v(-21.87, -36.4) * mm, "end": v(-22.03, -36.25) * mm});
            skLineSegment(sketch, "E8527", {"start": v(-22.03, -36.25) * mm, "end": v(-22.2, -36.11) * mm});
            skLineSegment(sketch, "E8528", {"start": v(-22.2, -36.11) * mm, "end": v(-22.36, -35.98) * mm});
            skLineSegment(sketch, "E8529", {"start": v(-22.36, -35.98) * mm, "end": v(-22.54, -35.86) * mm});
            skLineSegment(sketch, "E8530", {"start": v(-22.54, -35.86) * mm, "end": v(-22.7, -35.76) * mm});
            skLineSegment(sketch, "E8531", {"start": v(-22.7, -35.76) * mm, "end": v(-22.86, -35.68) * mm});
            skLineSegment(sketch, "E8532", {"start": v(-22.86, -35.68) * mm, "end": v(-23, -35.63) * mm});
            skLineSegment(sketch, "E8533", {"start": v(-23, -35.63) * mm, "end": v(-23.66, -35.42) * mm});
            skLineSegment(sketch, "E8534", {"start": v(-23.66, -35.42) * mm, "end": v(-21.16, -32.86) * mm});
            skLineSegment(sketch, "E8535", {"start": v(-21.16, -32.86) * mm, "end": v(-21.54, -32.47) * mm});
            skLineSegment(sketch, "E8536", {"start": v(-21.54, -32.47) * mm, "end": v(-25.57, -34.5) * mm});
            skLineSegment(sketch, "E8537", {"start": v(-25.57, -34.5) * mm, "end": v(-26.4, -33.18) * mm});
            skLineSegment(sketch, "E8538", {"start": v(-26.4, -33.18) * mm, "end": v(-26.52, -32.82) * mm});
            skLineSegment(sketch, "E8539", {"start": v(-26.52, -32.82) * mm, "end": v(-26.67, -32.47) * mm});
            skLineSegment(sketch, "E8540", {"start": v(-26.67, -32.47) * mm, "end": v(-26.82, -32.17) * mm});
            skLineSegment(sketch, "E8541", {"start": v(-26.82, -32.17) * mm, "end": v(-26.9, -32.04) * mm});
            skLineSegment(sketch, "E8542", {"start": v(-26.9, -32.04) * mm, "end": v(-26.97, -31.94) * mm});
            skLineSegment(sketch, "E8543", {"start": v(-26.97, -31.94) * mm, "end": v(-27.04, -31.83) * mm});
            skLineSegment(sketch, "E8544", {"start": v(-27.04, -31.83) * mm, "end": v(-27.12, -31.71) * mm});
            skLineSegment(sketch, "E8545", {"start": v(-27.12, -31.71) * mm, "end": v(-27.2, -31.6) * mm});
            skLineSegment(sketch, "E8546", {"start": v(-27.2, -31.6) * mm, "end": v(-27.25, -31.56) * mm});
            skLineSegment(sketch, "E8547", {"start": v(-27.25, -31.56) * mm, "end": v(-27.3, -31.53) * mm});
            skLineSegment(sketch, "E8548", {"start": v(-27.3, -31.53) * mm, "end": v(-27.46, -31.47) * mm});
            skLineSegment(sketch, "E8549", {"start": v(-27.46, -31.47) * mm, "end": v(-27.63, -31.43) * mm});
            skLineSegment(sketch, "E8550", {"start": v(-27.63, -31.43) * mm, "end": v(-27.82, -31.4) * mm});
            skLineSegment(sketch, "E8551", {"start": v(-27.82, -31.4) * mm, "end": v(-28.01, -31.4) * mm});
            skLineSegment(sketch, "E8552", {"start": v(-28.01, -31.4) * mm, "end": v(-28.2, -31.4) * mm});
            skLineSegment(sketch, "E8553", {"start": v(-28.2, -31.4) * mm, "end": v(-28.4, -31.43) * mm});
            skLineSegment(sketch, "E8554", {"start": v(-28.4, -31.43) * mm, "end": v(-28.58, -31.47) * mm});
            skLineSegment(sketch, "E8555", {"start": v(-28.58, -31.47) * mm, "end": v(-28.74, -31.53) * mm});
            skLineSegment(sketch, "E8556", {"start": v(-28.74, -31.53) * mm, "end": v(-28.84, -31.58) * mm});
            skLineSegment(sketch, "E8557", {"start": v(-28.84, -31.58) * mm, "end": v(-28.94, -31.65) * mm});
            skLineSegment(sketch, "E8558", {"start": v(-28.94, -31.65) * mm, "end": v(-29.03, -31.74) * mm});
            skLineSegment(sketch, "E8559", {"start": v(-29.03, -31.74) * mm, "end": v(-29.12, -31.84) * mm});
            skLineSegment(sketch, "E8560", {"start": v(-29.12, -31.84) * mm, "end": v(-29.3, -32.04) * mm});
            skLineSegment(sketch, "E8561", {"start": v(-29.3, -32.04) * mm, "end": v(-29.46, -32.24) * mm});
            skLineSegment(sketch, "E8562", {"start": v(47.45, 29.6) * mm, "end": v(47.43, 29.65) * mm});
            skLineSegment(sketch, "E8563", {"start": v(47.43, 29.65) * mm, "end": v(47.16, 30.2) * mm});
            skLineSegment(sketch, "E8564", {"start": v(47.16, 30.2) * mm, "end": v(46.89, 30.7) * mm});
            skLineSegment(sketch, "E8565", {"start": v(46.89, 30.7) * mm, "end": v(46.67, 31.06) * mm});
            skLineSegment(sketch, "E8566", {"start": v(46.67, 31.06) * mm, "end": v(46.58, 31.18) * mm});
            skLineSegment(sketch, "E8567", {"start": v(46.58, 31.18) * mm, "end": v(46.46, 31.32) * mm});
            skLineSegment(sketch, "E8568", {"start": v(46.46, 31.32) * mm, "end": v(46.1, 31.67) * mm});
            skLineSegment(sketch, "E8569", {"start": v(46.1, 31.67) * mm, "end": v(45.86, 31.89) * mm});
            skLineSegment(sketch, "E8570", {"start": v(45.86, 31.89) * mm, "end": v(45.58, 32.12) * mm});
            skLineSegment(sketch, "E8571", {"start": v(45.58, 32.12) * mm, "end": v(45.27, 32.36) * mm});
            skLineSegment(sketch, "E8572", {"start": v(45.27, 32.36) * mm, "end": v(45.16, 32.43) * mm});
            skLineSegment(sketch, "E8573", {"start": v(45.16, 32.43) * mm, "end": v(34.9, 32.9) * mm});
            skLineSegment(sketch, "E8574", {"start": v(34.9, 32.9) * mm, "end": v(34.37, 31.32) * mm});
            skLineSegment(sketch, "E8575", {"start": v(34.37, 31.32) * mm, "end": v(34.17, 30.7) * mm});
            skLineSegment(sketch, "E8576", {"start": v(34.17, 30.7) * mm, "end": v(34.02, 30.17) * mm});
            skLineSegment(sketch, "E8577", {"start": v(34.02, 30.17) * mm, "end": v(33.97, 29.95) * mm});
            skLineSegment(sketch, "E8578", {"start": v(33.97, 29.95) * mm, "end": v(33.94, 29.79) * mm});
            skLineSegment(sketch, "E8579", {"start": v(33.94, 29.79) * mm, "end": v(33.93, 29.67) * mm});
            skLineSegment(sketch, "E8580", {"start": v(33.93, 29.67) * mm, "end": v(33.94, 29.64) * mm});
            skLineSegment(sketch, "E8581", {"start": v(33.94, 29.64) * mm, "end": v(33.95, 29.62) * mm});
            skLineSegment(sketch, "E8582", {"start": v(33.95, 29.62) * mm, "end": v(33.99, 29.6) * mm});
            skLineSegment(sketch, "E8583", {"start": v(33.99, 29.6) * mm, "end": v(34.05, 29.57) * mm});
            skLineSegment(sketch, "E8584", {"start": v(34.05, 29.57) * mm, "end": v(34.27, 29.52) * mm});
            skLineSegment(sketch, "E8585", {"start": v(34.27, 29.52) * mm, "end": v(34.6, 29.46) * mm});
            skLineSegment(sketch, "E8586", {"start": v(34.6, 29.46) * mm, "end": v(35.01, 29.4) * mm});
            skLineSegment(sketch, "E8587", {"start": v(35.01, 29.4) * mm, "end": v(36.09, 29.28) * mm});
            skLineSegment(sketch, "E8588", {"start": v(36.09, 29.28) * mm, "end": v(37.41, 29.15) * mm});
            skLineSegment(sketch, "E8589", {"start": v(37.41, 29.15) * mm, "end": v(38.9, 29.04) * mm});
            skLineSegment(sketch, "E8590", {"start": v(38.9, 29.04) * mm, "end": v(40.48, 28.94) * mm});
            skLineSegment(sketch, "E8591", {"start": v(40.48, 28.94) * mm, "end": v(42.06, 28.85) * mm});
            skLineSegment(sketch, "E8592", {"start": v(42.06, 28.85) * mm, "end": v(43.56, 28.8) * mm});
            skLineSegment(sketch, "E8593", {"start": v(43.56, 28.8) * mm, "end": v(47.52, 28.7) * mm});
            skLineSegment(sketch, "E8594", {"start": v(47.52, 28.7) * mm, "end": v(47.45, 29.6) * mm});
            skLineSegment(sketch, "E8595", {"start": v(48.6, 25.35) * mm, "end": v(48.6, 25.29) * mm});
            skLineSegment(sketch, "E8596", {"start": v(48.6, 25.29) * mm, "end": v(48.52, 25.19) * mm});
            skLineSegment(sketch, "E8597", {"start": v(48.52, 25.19) * mm, "end": v(48.42, 25.07) * mm});
            skLineSegment(sketch, "E8598", {"start": v(48.42, 25.07) * mm, "end": v(48.32, 24.97) * mm});
            skLineSegment(sketch, "E8599", {"start": v(48.32, 24.97) * mm, "end": v(48.27, 24.93) * mm});
            skLineSegment(sketch, "E8600", {"start": v(48.27, 24.93) * mm, "end": v(48.21, 24.9) * mm});
            skLineSegment(sketch, "E8601", {"start": v(48.21, 24.9) * mm, "end": v(48.1, 24.86) * mm});
            skLineSegment(sketch, "E8602", {"start": v(48.1, 24.86) * mm, "end": v(47.98, 24.83) * mm});
            skLineSegment(sketch, "E8603", {"start": v(47.98, 24.83) * mm, "end": v(47.85, 24.8) * mm});
            skLineSegment(sketch, "E8604", {"start": v(47.85, 24.8) * mm, "end": v(47.72, 24.8) * mm});
            skLineSegment(sketch, "E8605", {"start": v(47.72, 24.8) * mm, "end": v(47.44, 24.79) * mm});
            skLineSegment(sketch, "E8606", {"start": v(47.44, 24.79) * mm, "end": v(47.16, 24.8) * mm});
            skLineSegment(sketch, "E8607", {"start": v(47.16, 24.8) * mm, "end": v(46.6, 24.86) * mm});
            skLineSegment(sketch, "E8608", {"start": v(46.6, 24.86) * mm, "end": v(46.32, 24.89) * mm});
            skLineSegment(sketch, "E8609", {"start": v(46.32, 24.89) * mm, "end": v(46.07, 24.9) * mm});
            skLineSegment(sketch, "E8610", {"start": v(46.07, 24.9) * mm, "end": v(45.48, 24.9) * mm});
            skLineSegment(sketch, "E8611", {"start": v(45.48, 24.9) * mm, "end": v(44.83, 24.93) * mm});
            skLineSegment(sketch, "E8612", {"start": v(44.83, 24.93) * mm, "end": v(44.12, 24.96) * mm});
            skLineSegment(sketch, "E8613", {"start": v(44.12, 24.96) * mm, "end": v(43.36, 25) * mm});
            skLineSegment(sketch, "E8614", {"start": v(43.36, 25) * mm, "end": v(41.76, 25.13) * mm});
            skLineSegment(sketch, "E8615", {"start": v(41.76, 25.13) * mm, "end": v(40.1, 25.28) * mm});
            skLineSegment(sketch, "E8616", {"start": v(40.1, 25.28) * mm, "end": v(38.5, 25.45) * mm});
            skLineSegment(sketch, "E8617", {"start": v(38.5, 25.45) * mm, "end": v(37.75, 25.55) * mm});
            skLineSegment(sketch, "E8618", {"start": v(37.75, 25.55) * mm, "end": v(37.04, 25.64) * mm});
            skLineSegment(sketch, "E8619", {"start": v(37.04, 25.64) * mm, "end": v(36.4, 25.74) * mm});
            skLineSegment(sketch, "E8620", {"start": v(36.4, 25.74) * mm, "end": v(35.8, 25.84) * mm});
            skLineSegment(sketch, "E8621", {"start": v(35.8, 25.84) * mm, "end": v(35.3, 25.93) * mm});
            skLineSegment(sketch, "E8622", {"start": v(35.3, 25.93) * mm, "end": v(34.9, 26.03) * mm});
            skLineSegment(sketch, "E8623", {"start": v(34.9, 26.03) * mm, "end": v(33.33, 26.43) * mm});
            skLineSegment(sketch, "E8624", {"start": v(33.33, 26.43) * mm, "end": v(33.24, 26.93) * mm});
            skLineSegment(sketch, "E8625", {"start": v(33.24, 26.93) * mm, "end": v(33.22, 27.04) * mm});
            skLineSegment(sketch, "E8626", {"start": v(33.22, 27.04) * mm, "end": v(33.22, 27.18) * mm});
            skLineSegment(sketch, "E8627", {"start": v(33.22, 27.18) * mm, "end": v(33.24, 27.35) * mm});
            skLineSegment(sketch, "E8628", {"start": v(33.24, 27.35) * mm, "end": v(33.26, 27.52) * mm});
            skLineSegment(sketch, "E8629", {"start": v(33.26, 27.52) * mm, "end": v(33.3, 27.7) * mm});
            skLineSegment(sketch, "E8630", {"start": v(33.3, 27.7) * mm, "end": v(33.34, 27.89) * mm});
            skLineSegment(sketch, "E8631", {"start": v(33.34, 27.89) * mm, "end": v(33.4, 28.07) * mm});
            skLineSegment(sketch, "E8632", {"start": v(33.4, 28.07) * mm, "end": v(33.45, 28.25) * mm});
            skLineSegment(sketch, "E8633", {"start": v(33.45, 28.25) * mm, "end": v(33.77, 29.07) * mm});
            skLineSegment(sketch, "E8634", {"start": v(33.77, 29.07) * mm, "end": v(34.77, 28.95) * mm});
            skLineSegment(sketch, "E8635", {"start": v(34.77, 28.95) * mm, "end": v(35.86, 28.8) * mm});
            skLineSegment(sketch, "E8636", {"start": v(35.86, 28.8) * mm, "end": v(36.94, 28.67) * mm});
            skLineSegment(sketch, "E8637", {"start": v(36.94, 28.67) * mm, "end": v(37.46, 28.61) * mm});
            skLineSegment(sketch, "E8638", {"start": v(37.46, 28.61) * mm, "end": v(37.95, 28.57) * mm});
            skLineSegment(sketch, "E8639", {"start": v(37.95, 28.57) * mm, "end": v(39.13, 28.48) * mm});
            skLineSegment(sketch, "E8640", {"start": v(39.13, 28.48) * mm, "end": v(40.38, 28.41) * mm});
            skLineSegment(sketch, "E8641", {"start": v(40.38, 28.41) * mm, "end": v(41.68, 28.35) * mm});
            skLineSegment(sketch, "E8642", {"start": v(41.68, 28.35) * mm, "end": v(43, 28.3) * mm});
            skLineSegment(sketch, "E8643", {"start": v(43, 28.3) * mm, "end": v(45.63, 28.2) * mm});
            skLineSegment(sketch, "E8644", {"start": v(45.63, 28.2) * mm, "end": v(48.1, 28.11) * mm});
            skLineSegment(sketch, "E8645", {"start": v(48.1, 28.11) * mm, "end": v(48.1, 28.1) * mm});
            skLineSegment(sketch, "E8646", {"start": v(48.1, 28.1) * mm, "end": v(48.16, 27.71) * mm});
            skLineSegment(sketch, "E8647", {"start": v(48.16, 27.71) * mm, "end": v(48.21, 27.3) * mm});
            skLineSegment(sketch, "E8648", {"start": v(48.21, 27.3) * mm, "end": v(48.27, 26.9) * mm});
            skLineSegment(sketch, "E8649", {"start": v(48.27, 26.9) * mm, "end": v(48.54, 25.44) * mm});
            skLineSegment(sketch, "E8650", {"start": v(48.54, 25.44) * mm, "end": v(48.6, 25.35) * mm});
            skLineSegment(sketch, "E8651", {"start": v(53.75, 13.03) * mm, "end": v(53.18, 13.04) * mm});
            skLineSegment(sketch, "E8652", {"start": v(53.18, 13.04) * mm, "end": v(52.88, 13.06) * mm});
            skLineSegment(sketch, "E8653", {"start": v(52.88, 13.06) * mm, "end": v(52.53, 13.1) * mm});
            skLineSegment(sketch, "E8654", {"start": v(52.53, 13.1) * mm, "end": v(52.11, 13.18) * mm});
            skLineSegment(sketch, "E8655", {"start": v(52.11, 13.18) * mm, "end": v(51.66, 13.27) * mm});
            skLineSegment(sketch, "E8656", {"start": v(51.66, 13.27) * mm, "end": v(51.17, 13.39) * mm});
            skLineSegment(sketch, "E8657", {"start": v(51.17, 13.39) * mm, "end": v(50.65, 13.52) * mm});
            skLineSegment(sketch, "E8658", {"start": v(50.65, 13.52) * mm, "end": v(50.12, 13.66) * mm});
            skLineSegment(sketch, "E8659", {"start": v(50.12, 13.66) * mm, "end": v(49.58, 13.82) * mm});
            skLineSegment(sketch, "E8660", {"start": v(49.58, 13.82) * mm, "end": v(49.05, 13.99) * mm});
            skLineSegment(sketch, "E8661", {"start": v(49.05, 13.99) * mm, "end": v(48.52, 14.16) * mm});
            skLineSegment(sketch, "E8662", {"start": v(48.52, 14.16) * mm, "end": v(48.02, 14.33) * mm});
            skLineSegment(sketch, "E8663", {"start": v(48.02, 14.33) * mm, "end": v(47.55, 14.5) * mm});
            skLineSegment(sketch, "E8664", {"start": v(47.55, 14.5) * mm, "end": v(47.12, 14.68) * mm});
            skLineSegment(sketch, "E8665", {"start": v(47.12, 14.68) * mm, "end": v(46.73, 14.84) * mm});
            skLineSegment(sketch, "E8666", {"start": v(46.73, 14.84) * mm, "end": v(46.4, 15) * mm});
            skLineSegment(sketch, "E8667", {"start": v(46.4, 15) * mm, "end": v(46.15, 15.15) * mm});
            skLineSegment(sketch, "E8668", {"start": v(46.15, 15.15) * mm, "end": v(45.73, 15.43) * mm});
            skLineSegment(sketch, "E8669", {"start": v(45.73, 15.43) * mm, "end": v(45.27, 15.77) * mm});
            skLineSegment(sketch, "E8670", {"start": v(45.27, 15.77) * mm, "end": v(44.84, 16.1) * mm});
            skLineSegment(sketch, "E8671", {"start": v(44.84, 16.1) * mm, "end": v(44.48, 16.4) * mm});
            skLineSegment(sketch, "E8672", {"start": v(44.48, 16.4) * mm, "end": v(43.75, 17.07) * mm});
            skLineSegment(sketch, "E8673", {"start": v(43.75, 17.07) * mm, "end": v(43.96, 17.3) * mm});
            skLineSegment(sketch, "E8674", {"start": v(43.96, 17.3) * mm, "end": v(44.2, 17.53) * mm});
            skLineSegment(sketch, "E8675", {"start": v(44.2, 17.53) * mm, "end": v(44.45, 17.77) * mm});
            skLineSegment(sketch, "E8676", {"start": v(44.45, 17.77) * mm, "end": v(44.7, 18.02) * mm});
            skLineSegment(sketch, "E8677", {"start": v(44.7, 18.02) * mm, "end": v(44.95, 18.27) * mm});
            skLineSegment(sketch, "E8678", {"start": v(44.95, 18.27) * mm, "end": v(45.06, 18.4) * mm});
            skLineSegment(sketch, "E8679", {"start": v(45.06, 18.4) * mm, "end": v(45.16, 18.53) * mm});
            skLineSegment(sketch, "E8680", {"start": v(45.16, 18.53) * mm, "end": v(45.25, 18.66) * mm});
            skLineSegment(sketch, "E8681", {"start": v(45.25, 18.66) * mm, "end": v(45.33, 18.8) * mm});
            skLineSegment(sketch, "E8682", {"start": v(45.33, 18.8) * mm, "end": v(45.39, 18.94) * mm});
            skLineSegment(sketch, "E8683", {"start": v(45.39, 18.94) * mm, "end": v(45.43, 19.08) * mm});
            skLineSegment(sketch, "E8684", {"start": v(45.43, 19.08) * mm, "end": v(45.45, 19.17) * mm});
            skLineSegment(sketch, "E8685", {"start": v(45.45, 19.17) * mm, "end": v(45.46, 19.27) * mm});
            skLineSegment(sketch, "E8686", {"start": v(45.46, 19.27) * mm, "end": v(45.46, 19.38) * mm});
            skLineSegment(sketch, "E8687", {"start": v(45.46, 19.38) * mm, "end": v(45.45, 19.48) * mm});
            skLineSegment(sketch, "E8688", {"start": v(45.45, 19.48) * mm, "end": v(45.41, 19.7) * mm});
            skLineSegment(sketch, "E8689", {"start": v(45.41, 19.7) * mm, "end": v(45.35, 19.92) * mm});
            skLineSegment(sketch, "E8690", {"start": v(45.35, 19.92) * mm, "end": v(45.2, 20.37) * mm});
            skLineSegment(sketch, "E8691", {"start": v(45.2, 20.37) * mm, "end": v(45.14, 20.58) * mm});
            skLineSegment(sketch, "E8692", {"start": v(45.14, 20.58) * mm, "end": v(45.1, 20.78) * mm});
            skLineSegment(sketch, "E8693", {"start": v(45.1, 20.78) * mm, "end": v(45.6, 20.87) * mm});
            skLineSegment(sketch, "E8694", {"start": v(45.6, 20.87) * mm, "end": v(45.85, 20.91) * mm});
            skLineSegment(sketch, "E8695", {"start": v(45.85, 20.91) * mm, "end": v(46.09, 20.97) * mm});
            skLineSegment(sketch, "E8696", {"start": v(46.09, 20.97) * mm, "end": v(46.38, 21.05) * mm});
            skLineSegment(sketch, "E8697", {"start": v(46.38, 21.05) * mm, "end": v(46.7, 21.15) * mm});
            skLineSegment(sketch, "E8698", {"start": v(46.7, 21.15) * mm, "end": v(47, 21.25) * mm});
            skLineSegment(sketch, "E8699", {"start": v(47, 21.25) * mm, "end": v(47.3, 21.36) * mm});
            skLineSegment(sketch, "E8700", {"start": v(47.3, 21.36) * mm, "end": v(47.74, 21.55) * mm});
            skLineSegment(sketch, "E8701", {"start": v(47.74, 21.55) * mm, "end": v(48.17, 21.76) * mm});
            skLineSegment(sketch, "E8702", {"start": v(48.17, 21.76) * mm, "end": v(48.8, 21.38) * mm});
            skLineSegment(sketch, "E8703", {"start": v(48.8, 21.38) * mm, "end": v(49.44, 21) * mm});
            skLineSegment(sketch, "E8704", {"start": v(49.44, 21) * mm, "end": v(50.09, 20.62) * mm});
            skLineSegment(sketch, "E8705", {"start": v(50.09, 20.62) * mm, "end": v(50.43, 20.43) * mm});
            skLineSegment(sketch, "E8706", {"start": v(50.43, 20.43) * mm, "end": v(50.75, 20.26) * mm});
            skLineSegment(sketch, "E8707", {"start": v(50.75, 20.26) * mm, "end": v(51.1, 20.1) * mm});
            skLineSegment(sketch, "E8708", {"start": v(51.1, 20.1) * mm, "end": v(51.48, 19.95) * mm});
            skLineSegment(sketch, "E8709", {"start": v(51.48, 19.95) * mm, "end": v(52.26, 19.65) * mm});
            skLineSegment(sketch, "E8710", {"start": v(52.26, 19.65) * mm, "end": v(52.42, 18.79) * mm});
            skLineSegment(sketch, "E8711", {"start": v(52.42, 18.79) * mm, "end": v(52.67, 17.6) * mm});
            skLineSegment(sketch, "E8712", {"start": v(52.67, 17.6) * mm, "end": v(52.97, 16.26) * mm});
            skLineSegment(sketch, "E8713", {"start": v(52.97, 16.26) * mm, "end": v(53.3, 14.84) * mm});
            skLineSegment(sketch, "E8714", {"start": v(53.3, 14.84) * mm, "end": v(53.64, 13.47) * mm});
            skLineSegment(sketch, "E8715", {"start": v(53.64, 13.47) * mm, "end": v(53.75, 13.03) * mm});
            skLineSegment(sketch, "E8716", {"start": v(56.27, 2.8) * mm, "end": v(55.67, 2.81) * mm});
            skLineSegment(sketch, "E8717", {"start": v(55.67, 2.81) * mm, "end": v(54.45, 2.83) * mm});
            skLineSegment(sketch, "E8718", {"start": v(54.45, 2.83) * mm, "end": v(50.78, 3.6) * mm});
            skLineSegment(sketch, "E8719", {"start": v(50.78, 3.6) * mm, "end": v(49.97, 3.77) * mm});
            skLineSegment(sketch, "E8720", {"start": v(49.97, 3.77) * mm, "end": v(49.06, 3.99) * mm});
            skLineSegment(sketch, "E8721", {"start": v(49.06, 3.99) * mm, "end": v(48.08, 4.23) * mm});
            skLineSegment(sketch, "E8722", {"start": v(48.08, 4.23) * mm, "end": v(47.06, 4.5) * mm});
            skLineSegment(sketch, "E8723", {"start": v(47.06, 4.5) * mm, "end": v(46.05, 4.77) * mm});
            skLineSegment(sketch, "E8724", {"start": v(46.05, 4.77) * mm, "end": v(45.06, 5.05) * mm});
            skLineSegment(sketch, "E8725", {"start": v(45.06, 5.05) * mm, "end": v(44.12, 5.32) * mm});
            skLineSegment(sketch, "E8726", {"start": v(44.12, 5.32) * mm, "end": v(43.28, 5.59) * mm});
            skLineSegment(sketch, "E8727", {"start": v(43.28, 5.59) * mm, "end": v(39.44, 6.82) * mm});
            skLineSegment(sketch, "E8728", {"start": v(39.44, 6.82) * mm, "end": v(39.44, 6.93) * mm});
            skLineSegment(sketch, "E8729", {"start": v(39.44, 6.93) * mm, "end": v(39.45, 6.97) * mm});
            skLineSegment(sketch, "E8730", {"start": v(39.45, 6.97) * mm, "end": v(39.5, 7.05) * mm});
            skLineSegment(sketch, "E8731", {"start": v(39.5, 7.05) * mm, "end": v(39.69, 7.27) * mm});
            skLineSegment(sketch, "E8732", {"start": v(39.69, 7.27) * mm, "end": v(39.96, 7.57) * mm});
            skLineSegment(sketch, "E8733", {"start": v(39.96, 7.57) * mm, "end": v(40.3, 7.9) * mm});
            skLineSegment(sketch, "E8734", {"start": v(40.3, 7.9) * mm, "end": v(41.15, 8.77) * mm});
            skLineSegment(sketch, "E8735", {"start": v(41.15, 8.77) * mm, "end": v(40.89, 11.06) * mm});
            skLineSegment(sketch, "E8736", {"start": v(40.89, 11.06) * mm, "end": v(41.91, 10.62) * mm});
            skLineSegment(sketch, "E8737", {"start": v(41.91, 10.62) * mm, "end": v(47.41, 8.72) * mm});
            skLineSegment(sketch, "E8738", {"start": v(47.41, 8.72) * mm, "end": v(51.43, 8.02) * mm});
            skLineSegment(sketch, "E8739", {"start": v(51.43, 8.02) * mm, "end": v(55.8, 7.23) * mm});
            skLineSegment(sketch, "E8740", {"start": v(55.8, 7.23) * mm, "end": v(55.81, 7.19) * mm});
            skLineSegment(sketch, "E8741", {"start": v(55.81, 7.19) * mm, "end": v(56.06, 6.68) * mm});
            skLineSegment(sketch, "E8742", {"start": v(56.06, 6.68) * mm, "end": v(57, 4.8) * mm});
            skLineSegment(sketch, "E8743", {"start": v(57, 4.8) * mm, "end": v(56.87, 4.44) * mm});
            skLineSegment(sketch, "E8744", {"start": v(56.87, 4.44) * mm, "end": v(56.59, 3.7) * mm});
            skLineSegment(sketch, "E8745", {"start": v(56.59, 3.7) * mm, "end": v(56.32, 2.94) * mm});
            skLineSegment(sketch, "E8746", {"start": v(56.32, 2.94) * mm, "end": v(56.27, 2.8) * mm});
            skLineSegment(sketch, "E8747", {"start": v(55.54, 7.8) * mm, "end": v(55.5, 7.78) * mm});
            skLineSegment(sketch, "E8748", {"start": v(55.5, 7.78) * mm, "end": v(55.46, 7.77) * mm});
            skLineSegment(sketch, "E8749", {"start": v(55.46, 7.77) * mm, "end": v(55.36, 7.78) * mm});
            skLineSegment(sketch, "E8750", {"start": v(55.36, 7.78) * mm, "end": v(52.97, 8.1) * mm});
            skLineSegment(sketch, "E8751", {"start": v(52.97, 8.1) * mm, "end": v(52.38, 8.18) * mm});
            skLineSegment(sketch, "E8752", {"start": v(52.38, 8.18) * mm, "end": v(51.75, 8.29) * mm});
            skLineSegment(sketch, "E8753", {"start": v(51.75, 8.29) * mm, "end": v(51.08, 8.41) * mm});
            skLineSegment(sketch, "E8754", {"start": v(51.08, 8.41) * mm, "end": v(50.4, 8.55) * mm});
            skLineSegment(sketch, "E8755", {"start": v(50.4, 8.55) * mm, "end": v(49.69, 8.7) * mm});
            skLineSegment(sketch, "E8756", {"start": v(49.69, 8.7) * mm, "end": v(48.97, 8.87) * mm});
            skLineSegment(sketch, "E8757", {"start": v(48.97, 8.87) * mm, "end": v(48.24, 9.05) * mm});
            skLineSegment(sketch, "E8758", {"start": v(48.24, 9.05) * mm, "end": v(47.52, 9.23) * mm});
            skLineSegment(sketch, "E8759", {"start": v(47.52, 9.23) * mm, "end": v(46.8, 9.43) * mm});
            skLineSegment(sketch, "E8760", {"start": v(46.8, 9.43) * mm, "end": v(46.1, 9.62) * mm});
            skLineSegment(sketch, "E8761", {"start": v(46.1, 9.62) * mm, "end": v(45.43, 9.83) * mm});
            skLineSegment(sketch, "E8762", {"start": v(45.43, 9.83) * mm, "end": v(44.79, 10.03) * mm});
            skLineSegment(sketch, "E8763", {"start": v(44.79, 10.03) * mm, "end": v(44.18, 10.23) * mm});
            skLineSegment(sketch, "E8764", {"start": v(44.18, 10.23) * mm, "end": v(43.62, 10.43) * mm});
            skLineSegment(sketch, "E8765", {"start": v(43.62, 10.43) * mm, "end": v(43.1, 10.63) * mm});
            skLineSegment(sketch, "E8766", {"start": v(43.1, 10.63) * mm, "end": v(42.65, 10.82) * mm});
            skLineSegment(sketch, "E8767", {"start": v(42.65, 10.82) * mm, "end": v(40.76, 11.66) * mm});
            skLineSegment(sketch, "E8768", {"start": v(40.76, 11.66) * mm, "end": v(40.76, 12.31) * mm});
            skLineSegment(sketch, "E8769", {"start": v(40.76, 12.31) * mm, "end": v(42.06, 12.73) * mm});
            skLineSegment(sketch, "E8770", {"start": v(42.06, 12.73) * mm, "end": v(42.68, 13.62) * mm});
            skLineSegment(sketch, "E8771", {"start": v(42.68, 13.62) * mm, "end": v(42.81, 13.81) * mm});
            skLineSegment(sketch, "E8772", {"start": v(42.81, 13.81) * mm, "end": v(42.95, 14.03) * mm});
            skLineSegment(sketch, "E8773", {"start": v(42.95, 14.03) * mm, "end": v(43.08, 14.26) * mm});
            skLineSegment(sketch, "E8774", {"start": v(43.08, 14.26) * mm, "end": v(43.2, 14.5) * mm});
            skLineSegment(sketch, "E8775", {"start": v(43.2, 14.5) * mm, "end": v(43.33, 14.75) * mm});
            skLineSegment(sketch, "E8776", {"start": v(43.33, 14.75) * mm, "end": v(43.43, 14.98) * mm});
            skLineSegment(sketch, "E8777", {"start": v(43.43, 14.98) * mm, "end": v(43.52, 15.2) * mm});
            skLineSegment(sketch, "E8778", {"start": v(43.52, 15.2) * mm, "end": v(43.6, 15.4) * mm});
            skLineSegment(sketch, "E8779", {"start": v(43.6, 15.4) * mm, "end": v(43.9, 16.3) * mm});
            skLineSegment(sketch, "E8780", {"start": v(43.9, 16.3) * mm, "end": v(45.33, 15.33) * mm});
            skLineSegment(sketch, "E8781", {"start": v(45.33, 15.33) * mm, "end": v(45.67, 15.1) * mm});
            skLineSegment(sketch, "E8782", {"start": v(45.67, 15.1) * mm, "end": v(46.02, 14.9) * mm});
            skLineSegment(sketch, "E8783", {"start": v(46.02, 14.9) * mm, "end": v(46.4, 14.68) * mm});
            skLineSegment(sketch, "E8784", {"start": v(46.4, 14.68) * mm, "end": v(46.78, 14.48) * mm});
            skLineSegment(sketch, "E8785", {"start": v(46.78, 14.48) * mm, "end": v(47.18, 14.29) * mm});
            skLineSegment(sketch, "E8786", {"start": v(47.18, 14.29) * mm, "end": v(47.59, 14.1) * mm});
            skLineSegment(sketch, "E8787", {"start": v(47.59, 14.1) * mm, "end": v(48, 13.92) * mm});
            skLineSegment(sketch, "E8788", {"start": v(48, 13.92) * mm, "end": v(48.43, 13.76) * mm});
            skLineSegment(sketch, "E8789", {"start": v(48.43, 13.76) * mm, "end": v(48.85, 13.6) * mm});
            skLineSegment(sketch, "E8790", {"start": v(48.85, 13.6) * mm, "end": v(49.28, 13.45) * mm});
            skLineSegment(sketch, "E8791", {"start": v(49.28, 13.45) * mm, "end": v(49.71, 13.32) * mm});
            skLineSegment(sketch, "E8792", {"start": v(49.71, 13.32) * mm, "end": v(50.14, 13.2) * mm});
            skLineSegment(sketch, "E8793", {"start": v(50.14, 13.2) * mm, "end": v(50.57, 13.09) * mm});
            skLineSegment(sketch, "E8794", {"start": v(50.57, 13.09) * mm, "end": v(51, 13) * mm});
            skLineSegment(sketch, "E8795", {"start": v(51, 13) * mm, "end": v(51.41, 12.9) * mm});
            skLineSegment(sketch, "E8796", {"start": v(51.41, 12.9) * mm, "end": v(51.82, 12.84) * mm});
            skLineSegment(sketch, "E8797", {"start": v(51.82, 12.84) * mm, "end": v(52.46, 12.74) * mm});
            skLineSegment(sketch, "E8798", {"start": v(52.46, 12.74) * mm, "end": v(53.06, 12.61) * mm});
            skLineSegment(sketch, "E8799", {"start": v(53.06, 12.61) * mm, "end": v(53.57, 12.48) * mm});
            skLineSegment(sketch, "E8800", {"start": v(53.57, 12.48) * mm, "end": v(53.77, 12.42) * mm});
            skLineSegment(sketch, "E8801", {"start": v(53.77, 12.42) * mm, "end": v(53.93, 12.36) * mm});
            skLineSegment(sketch, "E8802", {"start": v(53.93, 12.36) * mm, "end": v(53.95, 12.26) * mm});
            skLineSegment(sketch, "E8803", {"start": v(53.95, 12.26) * mm, "end": v(54.22, 11.3) * mm});
            skLineSegment(sketch, "E8804", {"start": v(54.22, 11.3) * mm, "end": v(54.39, 10.78) * mm});
            skLineSegment(sketch, "E8805", {"start": v(54.39, 10.78) * mm, "end": v(54.59, 10.2) * mm});
            skLineSegment(sketch, "E8806", {"start": v(54.59, 10.2) * mm, "end": v(54.81, 9.59) * mm});
            skLineSegment(sketch, "E8807", {"start": v(54.81, 9.59) * mm, "end": v(55.05, 8.97) * mm});
            skLineSegment(sketch, "E8808", {"start": v(55.05, 8.97) * mm, "end": v(55.3, 8.35) * mm});
            skLineSegment(sketch, "E8809", {"start": v(55.3, 8.35) * mm, "end": v(55.54, 7.8) * mm});
            skLineSegment(sketch, "E8810", {"start": v(-39.43, 37.69) * mm, "end": v(-39.64, 37.37) * mm});
            skLineSegment(sketch, "E8811", {"start": v(-39.64, 37.37) * mm, "end": v(-40.12, 36.67) * mm});
            skLineSegment(sketch, "E8812", {"start": v(-40.12, 36.67) * mm, "end": v(-40.63, 36) * mm});
            skLineSegment(sketch, "E8813", {"start": v(-40.63, 36) * mm, "end": v(-41.16, 35.33) * mm});
            skLineSegment(sketch, "E8814", {"start": v(-41.16, 35.33) * mm, "end": v(-41.71, 34.68) * mm});
            skLineSegment(sketch, "E8815", {"start": v(-41.71, 34.68) * mm, "end": v(-42.28, 34.05) * mm});
            skLineSegment(sketch, "E8816", {"start": v(-42.28, 34.05) * mm, "end": v(-42.68, 33.64) * mm});
            skLineSegment(sketch, "E8817", {"start": v(-42.68, 33.64) * mm, "end": v(-40.65, 33.58) * mm});
            skLineSegment(sketch, "E8818", {"start": v(-40.65, 33.58) * mm, "end": v(-39.93, 33.54) * mm});
            skLineSegment(sketch, "E8819", {"start": v(-39.93, 33.54) * mm, "end": v(-39.56, 33.52) * mm});
            skLineSegment(sketch, "E8820", {"start": v(-39.56, 33.52) * mm, "end": v(-39.21, 33.52) * mm});
            skLineSegment(sketch, "E8821", {"start": v(-39.21, 33.52) * mm, "end": v(-38.72, 33.55) * mm});
            skLineSegment(sketch, "E8822", {"start": v(-38.72, 33.55) * mm, "end": v(-38.19, 33.6) * mm});
            skLineSegment(sketch, "E8823", {"start": v(-38.19, 33.6) * mm, "end": v(-37.17, 33.74) * mm});
            skLineSegment(sketch, "E8824", {"start": v(-37.17, 33.74) * mm, "end": v(-36.2, 33.86) * mm});
            skLineSegment(sketch, "E8825", {"start": v(-36.2, 33.86) * mm, "end": v(-35.24, 33.99) * mm});
            skLineSegment(sketch, "E8826", {"start": v(-35.24, 33.99) * mm, "end": v(-35.82, 34.8) * mm});
            skLineSegment(sketch, "E8827", {"start": v(-35.82, 34.8) * mm, "end": v(-35.94, 34.99) * mm});
            skLineSegment(sketch, "E8828", {"start": v(-35.94, 34.99) * mm, "end": v(-36.06, 35.19) * mm});
            skLineSegment(sketch, "E8829", {"start": v(-36.06, 35.19) * mm, "end": v(-36.18, 35.4) * mm});
            skLineSegment(sketch, "E8830", {"start": v(-36.18, 35.4) * mm, "end": v(-36.3, 35.62) * mm});
            skLineSegment(sketch, "E8831", {"start": v(-36.3, 35.62) * mm, "end": v(-36.4, 35.85) * mm});
            skLineSegment(sketch, "E8832", {"start": v(-36.4, 35.85) * mm, "end": v(-36.48, 36.06) * mm});
            skLineSegment(sketch, "E8833", {"start": v(-36.48, 36.06) * mm, "end": v(-36.55, 36.26) * mm});
            skLineSegment(sketch, "E8834", {"start": v(-36.55, 36.26) * mm, "end": v(-36.6, 36.45) * mm});
            skLineSegment(sketch, "E8835", {"start": v(-36.6, 36.45) * mm, "end": v(-36.8, 37.27) * mm});
            skLineSegment(sketch, "E8836", {"start": v(-36.8, 37.27) * mm, "end": v(-36.79, 38.1) * mm});
            skLineSegment(sketch, "E8837", {"start": v(-36.79, 38.1) * mm, "end": v(-39.43, 37.69) * mm});
            skLineSegment(sketch, "E8838", {"start": v(-30.88, 24.1) * mm, "end": v(-31.22, 25.12) * mm});
            skLineSegment(sketch, "E8839", {"start": v(-31.22, 25.12) * mm, "end": v(-31.62, 26.37) * mm});
            skLineSegment(sketch, "E8840", {"start": v(-31.62, 26.37) * mm, "end": v(-31.66, 26.46) * mm});
            skLineSegment(sketch, "E8841", {"start": v(-31.66, 26.46) * mm, "end": v(-31.72, 26.47) * mm});
            skLineSegment(sketch, "E8842", {"start": v(-31.72, 26.47) * mm, "end": v(-31.86, 26.45) * mm});
            skLineSegment(sketch, "E8843", {"start": v(-31.86, 26.45) * mm, "end": v(-32.37, 26.38) * mm});
            skLineSegment(sketch, "E8844", {"start": v(-32.37, 26.38) * mm, "end": v(-33.11, 26.24) * mm});
            skLineSegment(sketch, "E8845", {"start": v(-33.11, 26.24) * mm, "end": v(-34, 26.07) * mm});
            skLineSegment(sketch, "E8846", {"start": v(-34, 26.07) * mm, "end": v(-36.3, 25.6) * mm});
            skLineSegment(sketch, "E8847", {"start": v(-36.3, 25.6) * mm, "end": v(-46.83, 24.87) * mm});
            skLineSegment(sketch, "E8848", {"start": v(-46.83, 24.87) * mm, "end": v(-47.08, 24.47) * mm});
            skLineSegment(sketch, "E8849", {"start": v(-47.08, 24.47) * mm, "end": v(-47.2, 24.27) * mm});
            skLineSegment(sketch, "E8850", {"start": v(-47.2, 24.27) * mm, "end": v(-47.25, 24.18) * mm});
            skLineSegment(sketch, "E8851", {"start": v(-47.25, 24.18) * mm, "end": v(-47.28, 24.1) * mm});
            skLineSegment(sketch, "E8852", {"start": v(-47.28, 24.1) * mm, "end": v(-47.3, 24.02) * mm});
            skLineSegment(sketch, "E8853", {"start": v(-47.3, 24.02) * mm, "end": v(-47.31, 23.95) * mm});
            skLineSegment(sketch, "E8854", {"start": v(-47.31, 23.95) * mm, "end": v(-47.3, 23.87) * mm});
            skLineSegment(sketch, "E8855", {"start": v(-47.3, 23.87) * mm, "end": v(-47.29, 23.8) * mm});
            skLineSegment(sketch, "E8856", {"start": v(-47.29, 23.8) * mm, "end": v(-47.26, 23.72) * mm});
            skLineSegment(sketch, "E8857", {"start": v(-47.26, 23.72) * mm, "end": v(-47.21, 23.65) * mm});
            skLineSegment(sketch, "E8858", {"start": v(-47.21, 23.65) * mm, "end": v(-47.15, 23.56) * mm});
            skLineSegment(sketch, "E8859", {"start": v(-47.15, 23.56) * mm, "end": v(-47.08, 23.47) * mm});
            skLineSegment(sketch, "E8860", {"start": v(-47.08, 23.47) * mm, "end": v(-46.87, 23.26) * mm});
            skLineSegment(sketch, "E8861", {"start": v(-46.87, 23.26) * mm, "end": v(-46.6, 23) * mm});
            skLineSegment(sketch, "E8862", {"start": v(-46.6, 23) * mm, "end": v(-46.4, 22.83) * mm});
            skLineSegment(sketch, "E8863", {"start": v(-46.4, 22.83) * mm, "end": v(-46.22, 22.68) * mm});
            skLineSegment(sketch, "E8864", {"start": v(-46.22, 22.68) * mm, "end": v(-46.03, 22.54) * mm});
            skLineSegment(sketch, "E8865", {"start": v(-46.03, 22.54) * mm, "end": v(-45.83, 22.43) * mm});
            skLineSegment(sketch, "E8866", {"start": v(-45.83, 22.43) * mm, "end": v(-45.62, 22.33) * mm});
            skLineSegment(sketch, "E8867", {"start": v(-45.62, 22.33) * mm, "end": v(-45.38, 22.24) * mm});
            skLineSegment(sketch, "E8868", {"start": v(-45.38, 22.24) * mm, "end": v(-45.12, 22.18) * mm});
            skLineSegment(sketch, "E8869", {"start": v(-45.12, 22.18) * mm, "end": v(-44.82, 22.12) * mm});
            skLineSegment(sketch, "E8870", {"start": v(-44.82, 22.12) * mm, "end": v(-44.48, 22.08) * mm});
            skLineSegment(sketch, "E8871", {"start": v(-44.48, 22.08) * mm, "end": v(-44.1, 22.06) * mm});
            skLineSegment(sketch, "E8872", {"start": v(-44.1, 22.06) * mm, "end": v(-43.65, 22.04) * mm});
            skLineSegment(sketch, "E8873", {"start": v(-43.65, 22.04) * mm, "end": v(-43.15, 22.03) * mm});
            skLineSegment(sketch, "E8874", {"start": v(-43.15, 22.03) * mm, "end": v(-41.92, 22.05) * mm});
            skLineSegment(sketch, "E8875", {"start": v(-41.92, 22.05) * mm, "end": v(-40.37, 22.1) * mm});
            skLineSegment(sketch, "E8876", {"start": v(-40.37, 22.1) * mm, "end": v(-36.2, 22.23) * mm});
            skLineSegment(sketch, "E8877", {"start": v(-36.2, 22.23) * mm, "end": v(-31.55, 23.3) * mm});
            skLineSegment(sketch, "E8878", {"start": v(-31.55, 23.3) * mm, "end": v(-30.88, 24.1) * mm});
            skLineSegment(sketch, "E8879", {"start": v(-27.92, 15.53) * mm, "end": v(-28.41, 15.17) * mm});
            skLineSegment(sketch, "E8880", {"start": v(-28.41, 15.17) * mm, "end": v(-28.58, 15.07) * mm});
            skLineSegment(sketch, "E8881", {"start": v(-28.58, 15.07) * mm, "end": v(-28.83, 14.94) * mm});
            skLineSegment(sketch, "E8882", {"start": v(-28.83, 14.94) * mm, "end": v(-29.15, 14.79) * mm});
            skLineSegment(sketch, "E8883", {"start": v(-29.15, 14.79) * mm, "end": v(-29.53, 14.63) * mm});
            skLineSegment(sketch, "E8884", {"start": v(-29.53, 14.63) * mm, "end": v(-29.95, 14.46) * mm});
            skLineSegment(sketch, "E8885", {"start": v(-29.95, 14.46) * mm, "end": v(-30.4, 14.3) * mm});
            skLineSegment(sketch, "E8886", {"start": v(-30.4, 14.3) * mm, "end": v(-30.87, 14.13) * mm});
            skLineSegment(sketch, "E8887", {"start": v(-30.87, 14.13) * mm, "end": v(-31.34, 13.97) * mm});
            skLineSegment(sketch, "E8888", {"start": v(-31.34, 13.97) * mm, "end": v(-33.65, 13.23) * mm});
            skLineSegment(sketch, "E8889", {"start": v(-33.65, 13.23) * mm, "end": v(-36.62, 13.1) * mm});
            skLineSegment(sketch, "E8890", {"start": v(-36.62, 13.1) * mm, "end": v(-39.6, 12.98) * mm});
            skLineSegment(sketch, "E8891", {"start": v(-39.6, 12.98) * mm, "end": v(-41.37, 14.5) * mm});
            skLineSegment(sketch, "E8892", {"start": v(-41.37, 14.5) * mm, "end": v(-41.74, 15.94) * mm});
            skLineSegment(sketch, "E8893", {"start": v(-41.74, 15.94) * mm, "end": v(-41.88, 16.5) * mm});
            skLineSegment(sketch, "E8894", {"start": v(-41.88, 16.5) * mm, "end": v(-41.97, 16.98) * mm});
            skLineSegment(sketch, "E8895", {"start": v(-41.97, 16.98) * mm, "end": v(-42, 17.18) * mm});
            skLineSegment(sketch, "E8896", {"start": v(-42, 17.18) * mm, "end": v(-42.02, 17.33) * mm});
            skLineSegment(sketch, "E8897", {"start": v(-42.02, 17.33) * mm, "end": v(-42.02, 17.43) * mm});
            skLineSegment(sketch, "E8898", {"start": v(-42.02, 17.43) * mm, "end": v(-42.01, 17.46) * mm});
            skLineSegment(sketch, "E8899", {"start": v(-42.01, 17.46) * mm, "end": v(-42, 17.48) * mm});
            skLineSegment(sketch, "E8900", {"start": v(-42, 17.48) * mm, "end": v(-41.9, 17.59) * mm});
            skLineSegment(sketch, "E8901", {"start": v(-41.9, 17.59) * mm, "end": v(-39.1, 17.8) * mm});
            skLineSegment(sketch, "E8902", {"start": v(-39.1, 17.8) * mm, "end": v(-37.77, 17.91) * mm});
            skLineSegment(sketch, "E8903", {"start": v(-37.77, 17.91) * mm, "end": v(-37.16, 17.98) * mm});
            skLineSegment(sketch, "E8904", {"start": v(-37.16, 17.98) * mm, "end": v(-36.56, 18.04) * mm});
            skLineSegment(sketch, "E8905", {"start": v(-36.56, 18.04) * mm, "end": v(-36, 18.12) * mm});
            skLineSegment(sketch, "E8906", {"start": v(-36, 18.12) * mm, "end": v(-35.45, 18.2) * mm});
            skLineSegment(sketch, "E8907", {"start": v(-35.45, 18.2) * mm, "end": v(-34.93, 18.29) * mm});
            skLineSegment(sketch, "E8908", {"start": v(-34.93, 18.29) * mm, "end": v(-34.44, 18.38) * mm});
            skLineSegment(sketch, "E8909", {"start": v(-34.44, 18.38) * mm, "end": v(-33.96, 18.48) * mm});
            skLineSegment(sketch, "E8910", {"start": v(-33.96, 18.48) * mm, "end": v(-33.5, 18.58) * mm});
            skLineSegment(sketch, "E8911", {"start": v(-33.5, 18.58) * mm, "end": v(-33.06, 18.7) * mm});
            skLineSegment(sketch, "E8912", {"start": v(-33.06, 18.7) * mm, "end": v(-32.64, 18.81) * mm});
            skLineSegment(sketch, "E8913", {"start": v(-32.64, 18.81) * mm, "end": v(-32.23, 18.94) * mm});
            skLineSegment(sketch, "E8914", {"start": v(-32.23, 18.94) * mm, "end": v(-31.83, 19.08) * mm});
            skLineSegment(sketch, "E8915", {"start": v(-31.83, 19.08) * mm, "end": v(-31.45, 19.22) * mm});
            skLineSegment(sketch, "E8916", {"start": v(-31.45, 19.22) * mm, "end": v(-31.09, 19.37) * mm});
            skLineSegment(sketch, "E8917", {"start": v(-31.09, 19.37) * mm, "end": v(-30.54, 19.6) * mm});
            skLineSegment(sketch, "E8918", {"start": v(-30.54, 19.6) * mm, "end": v(-30.06, 19.77) * mm});
            skLineSegment(sketch, "E8919", {"start": v(-30.06, 19.77) * mm, "end": v(-29.68, 19.88) * mm});
            skLineSegment(sketch, "E8920", {"start": v(-29.68, 19.88) * mm, "end": v(-29.55, 19.91) * mm});
            skLineSegment(sketch, "E8921", {"start": v(-29.55, 19.91) * mm, "end": v(-29.46, 19.92) * mm});
            skLineSegment(sketch, "E8922", {"start": v(-29.46, 19.92) * mm, "end": v(-29.12, 18.94) * mm});
            skLineSegment(sketch, "E8923", {"start": v(-29.12, 18.94) * mm, "end": v(-28.66, 17.58) * mm});
            skLineSegment(sketch, "E8924", {"start": v(-28.66, 17.58) * mm, "end": v(-28.18, 16.21) * mm});
            skLineSegment(sketch, "E8925", {"start": v(-28.18, 16.21) * mm, "end": v(-27.93, 15.56) * mm});
            skLineSegment(sketch, "E8926", {"start": v(-27.93, 15.56) * mm, "end": v(-27.92, 15.53) * mm});
            skLineSegment(sketch, "E8927", {"start": v(-24.22, 7.62) * mm, "end": v(-24.36, 7.28) * mm});
            skLineSegment(sketch, "E8928", {"start": v(-24.36, 7.28) * mm, "end": v(-24.42, 7.15) * mm});
            skLineSegment(sketch, "E8929", {"start": v(-24.42, 7.15) * mm, "end": v(-24.54, 7) * mm});
            skLineSegment(sketch, "E8930", {"start": v(-24.54, 7) * mm, "end": v(-24.7, 6.82) * mm});
            skLineSegment(sketch, "E8931", {"start": v(-24.7, 6.82) * mm, "end": v(-24.9, 6.63) * mm});
            skLineSegment(sketch, "E8932", {"start": v(-24.9, 6.63) * mm, "end": v(-25.13, 6.42) * mm});
            skLineSegment(sketch, "E8933", {"start": v(-25.13, 6.42) * mm, "end": v(-25.38, 6.2) * mm});
            skLineSegment(sketch, "E8934", {"start": v(-25.38, 6.2) * mm, "end": v(-25.65, 5.98) * mm});
            skLineSegment(sketch, "E8935", {"start": v(-25.65, 5.98) * mm, "end": v(-25.94, 5.77) * mm});
            skLineSegment(sketch, "E8936", {"start": v(-25.94, 5.77) * mm, "end": v(-27.33, 4.76) * mm});
            skLineSegment(sketch, "E8937", {"start": v(-27.33, 4.76) * mm, "end": v(-30.68, 3.76) * mm});
            skLineSegment(sketch, "E8938", {"start": v(-30.68, 3.76) * mm, "end": v(-33, 3.6) * mm});
            skLineSegment(sketch, "E8939", {"start": v(-33, 3.6) * mm, "end": v(-35.3, 3.45) * mm});
            skLineSegment(sketch, "E8940", {"start": v(-35.3, 3.45) * mm, "end": v(-36.45, 4.11) * mm});
            skLineSegment(sketch, "E8941", {"start": v(-36.45, 4.11) * mm, "end": v(-36.97, 4.89) * mm});
            skLineSegment(sketch, "E8942", {"start": v(-36.97, 4.89) * mm, "end": v(-37, 5.06) * mm});
            skLineSegment(sketch, "E8943", {"start": v(-37, 5.06) * mm, "end": v(-37.04, 5.26) * mm});
            skLineSegment(sketch, "E8944", {"start": v(-37.04, 5.26) * mm, "end": v(-37.06, 5.47) * mm});
            skLineSegment(sketch, "E8945", {"start": v(-37.06, 5.47) * mm, "end": v(-37.08, 5.68) * mm});
            skLineSegment(sketch, "E8946", {"start": v(-37.08, 5.68) * mm, "end": v(-37.09, 5.9) * mm});
            skLineSegment(sketch, "E8947", {"start": v(-37.09, 5.9) * mm, "end": v(-37.09, 6.1) * mm});
            skLineSegment(sketch, "E8948", {"start": v(-37.09, 6.1) * mm, "end": v(-37.08, 6.3) * mm});
            skLineSegment(sketch, "E8949", {"start": v(-37.08, 6.3) * mm, "end": v(-37.06, 6.47) * mm});
            skLineSegment(sketch, "E8950", {"start": v(-37.06, 6.47) * mm, "end": v(-36.95, 7.24) * mm});
            skLineSegment(sketch, "E8951", {"start": v(-36.95, 7.24) * mm, "end": v(-34.97, 7.51) * mm});
            skLineSegment(sketch, "E8952", {"start": v(-34.97, 7.51) * mm, "end": v(-34.04, 7.66) * mm});
            skLineSegment(sketch, "E8953", {"start": v(-34.04, 7.66) * mm, "end": v(-32.97, 7.85) * mm});
            skLineSegment(sketch, "E8954", {"start": v(-32.97, 7.85) * mm, "end": v(-31.9, 8.07) * mm});
            skLineSegment(sketch, "E8955", {"start": v(-31.9, 8.07) * mm, "end": v(-30.94, 8.29) * mm});
            skLineSegment(sketch, "E8956", {"start": v(-30.94, 8.29) * mm, "end": v(-28.9, 8.8) * mm});
            skLineSegment(sketch, "E8957", {"start": v(-28.9, 8.8) * mm, "end": v(-25.86, 10.72) * mm});
            skLineSegment(sketch, "E8958", {"start": v(-25.86, 10.72) * mm, "end": v(-25.69, 10.62) * mm});
            skLineSegment(sketch, "E8959", {"start": v(-25.69, 10.62) * mm, "end": v(-24.84, 8.9) * mm});
            skLineSegment(sketch, "E8960", {"start": v(-24.84, 8.9) * mm, "end": v(-24.22, 7.62) * mm});
            skLineSegment(sketch, "E8961", {"start": v(-19.66, 1.25) * mm, "end": v(-20.2, 0.47) * mm});
            skLineSegment(sketch, "E8962", {"start": v(-20.2, 0.47) * mm, "end": v(-20.34, 0.28) * mm});
            skLineSegment(sketch, "E8963", {"start": v(-20.34, 0.28) * mm, "end": v(-20.53, 0.03) * mm});
            skLineSegment(sketch, "E8964", {"start": v(-20.53, 0.03) * mm, "end": v(-21.01, -0.56) * mm});
            skLineSegment(sketch, "E8965", {"start": v(-21.01, -0.56) * mm, "end": v(-21.59, -1.22) * mm});
            skLineSegment(sketch, "E8966", {"start": v(-21.59, -1.22) * mm, "end": v(-22.19, -1.88) * mm});
            skLineSegment(sketch, "E8967", {"start": v(-22.19, -1.88) * mm, "end": v(-22.52, -2.26) * mm});
            skLineSegment(sketch, "E8968", {"start": v(-22.52, -2.26) * mm, "end": v(-22.87, -2.68) * mm});
            skLineSegment(sketch, "E8969", {"start": v(-22.87, -2.68) * mm, "end": v(-23.05, -2.89) * mm});
            skLineSegment(sketch, "E8970", {"start": v(-23.05, -2.89) * mm, "end": v(-23.23, -3.08) * mm});
            skLineSegment(sketch, "E8971", {"start": v(-23.23, -3.08) * mm, "end": v(-23.42, -3.26) * mm});
            skLineSegment(sketch, "E8972", {"start": v(-23.42, -3.26) * mm, "end": v(-23.61, -3.4) * mm});
            skLineSegment(sketch, "E8973", {"start": v(-23.61, -3.4) * mm, "end": v(-23.79, -3.53) * mm});
            skLineSegment(sketch, "E8974", {"start": v(-23.79, -3.53) * mm, "end": v(-23.97, -3.64) * mm});
            skLineSegment(sketch, "E8975", {"start": v(-23.97, -3.64) * mm, "end": v(-24.36, -3.86) * mm});
            skLineSegment(sketch, "E8976", {"start": v(-24.36, -3.86) * mm, "end": v(-24.78, -4.07) * mm});
            skLineSegment(sketch, "E8977", {"start": v(-24.78, -4.07) * mm, "end": v(-25.22, -4.26) * mm});
            skLineSegment(sketch, "E8978", {"start": v(-25.22, -4.26) * mm, "end": v(-25.67, -4.43) * mm});
            skLineSegment(sketch, "E8979", {"start": v(-25.67, -4.43) * mm, "end": v(-26.11, -4.6) * mm});
            skLineSegment(sketch, "E8980", {"start": v(-26.11, -4.6) * mm, "end": v(-26.55, -4.73) * mm});
            skLineSegment(sketch, "E8981", {"start": v(-26.55, -4.73) * mm, "end": v(-26.96, -4.85) * mm});
            skLineSegment(sketch, "E8982", {"start": v(-26.96, -4.85) * mm, "end": v(-27.18, -4.9) * mm});
            skLineSegment(sketch, "E8983", {"start": v(-27.18, -4.9) * mm, "end": v(-27.42, -4.95) * mm});
            skLineSegment(sketch, "E8984", {"start": v(-27.42, -4.95) * mm, "end": v(-27.92, -5.03) * mm});
            skLineSegment(sketch, "E8985", {"start": v(-27.92, -5.03) * mm, "end": v(-28.44, -5.1) * mm});
            skLineSegment(sketch, "E8986", {"start": v(-28.44, -5.1) * mm, "end": v(-28.97, -5.14) * mm});
            skLineSegment(sketch, "E8987", {"start": v(-28.97, -5.14) * mm, "end": v(-30.03, -5.22) * mm});
            skLineSegment(sketch, "E8988", {"start": v(-30.03, -5.22) * mm, "end": v(-30.54, -5.26) * mm});
            skLineSegment(sketch, "E8989", {"start": v(-30.54, -5.26) * mm, "end": v(-31.01, -5.3) * mm});
            skLineSegment(sketch, "E8990", {"start": v(-31.01, -5.3) * mm, "end": v(-30.81, -6.61) * mm});
            skLineSegment(sketch, "E8991", {"start": v(-30.81, -6.61) * mm, "end": v(-30.48, -6.9) * mm});
            skLineSegment(sketch, "E8992", {"start": v(-30.48, -6.9) * mm, "end": v(-30.3, -7.03) * mm});
            skLineSegment(sketch, "E8993", {"start": v(-30.3, -7.03) * mm, "end": v(-30.12, -7.17) * mm});
            skLineSegment(sketch, "E8994", {"start": v(-30.12, -7.17) * mm, "end": v(-29.93, -7.29) * mm});
            skLineSegment(sketch, "E8995", {"start": v(-29.93, -7.29) * mm, "end": v(-29.74, -7.4) * mm});
            skLineSegment(sketch, "E8996", {"start": v(-29.74, -7.4) * mm, "end": v(-29.55, -7.5) * mm});
            skLineSegment(sketch, "E8997", {"start": v(-29.55, -7.5) * mm, "end": v(-29.35, -7.57) * mm});
            skLineSegment(sketch, "E8998", {"start": v(-29.35, -7.57) * mm, "end": v(-29.13, -7.64) * mm});
            skLineSegment(sketch, "E8999", {"start": v(-29.13, -7.64) * mm, "end": v(-28.89, -7.68) * mm});
            skLineSegment(sketch, "E9000", {"start": v(-28.89, -7.68) * mm, "end": v(-28.64, -7.7) * mm});
            skLineSegment(sketch, "E9001", {"start": v(-28.64, -7.7) * mm, "end": v(-28.38, -7.73) * mm});
            skLineSegment(sketch, "E9002", {"start": v(-28.38, -7.73) * mm, "end": v(-28.12, -7.73) * mm});
            skLineSegment(sketch, "E9003", {"start": v(-28.12, -7.73) * mm, "end": v(-27.87, -7.73) * mm});
            skLineSegment(sketch, "E9004", {"start": v(-27.87, -7.73) * mm, "end": v(-27.39, -7.7) * mm});
            skLineSegment(sketch, "E9005", {"start": v(-27.39, -7.7) * mm, "end": v(-26.9, -7.66) * mm});
            skLineSegment(sketch, "E9006", {"start": v(-26.9, -7.66) * mm, "end": v(-26.35, -7.58) * mm});
            skLineSegment(sketch, "E9007", {"start": v(-26.35, -7.58) * mm, "end": v(-25.8, -7.47) * mm});
            skLineSegment(sketch, "E9008", {"start": v(-25.8, -7.47) * mm, "end": v(-25.32, -7.36) * mm});
            skLineSegment(sketch, "E9009", {"start": v(-25.32, -7.36) * mm, "end": v(-24.92, -7.24) * mm});
            skLineSegment(sketch, "E9010", {"start": v(-24.92, -7.24) * mm, "end": v(-24.51, -7.11) * mm});
            skLineSegment(sketch, "E9011", {"start": v(-24.51, -7.11) * mm, "end": v(-24.1, -6.96) * mm});
            skLineSegment(sketch, "E9012", {"start": v(-24.1, -6.96) * mm, "end": v(-23.69, -6.8) * mm});
            skLineSegment(sketch, "E9013", {"start": v(-23.69, -6.8) * mm, "end": v(-23.29, -6.62) * mm});
            skLineSegment(sketch, "E9014", {"start": v(-23.29, -6.62) * mm, "end": v(-22.9, -6.42) * mm});
            skLineSegment(sketch, "E9015", {"start": v(-22.9, -6.42) * mm, "end": v(-22.53, -6.2) * mm});
            skLineSegment(sketch, "E9016", {"start": v(-22.53, -6.2) * mm, "end": v(-22.36, -6.08) * mm});
            skLineSegment(sketch, "E9017", {"start": v(-22.36, -6.08) * mm, "end": v(-22.2, -5.97) * mm});
            skLineSegment(sketch, "E9018", {"start": v(-22.2, -5.97) * mm, "end": v(-21.98, -5.79) * mm});
            skLineSegment(sketch, "E9019", {"start": v(-21.98, -5.79) * mm, "end": v(-21.77, -5.58) * mm});
            skLineSegment(sketch, "E9020", {"start": v(-21.77, -5.58) * mm, "end": v(-21.56, -5.35) * mm});
            skLineSegment(sketch, "E9021", {"start": v(-21.56, -5.35) * mm, "end": v(-21.35, -5.11) * mm});
            skLineSegment(sketch, "E9022", {"start": v(-21.35, -5.11) * mm, "end": v(-20.95, -4.63) * mm});
            skLineSegment(sketch, "E9023", {"start": v(-20.95, -4.63) * mm, "end": v(-20.76, -4.4) * mm});
            skLineSegment(sketch, "E9024", {"start": v(-20.76, -4.4) * mm, "end": v(-20.57, -4.19) * mm});
            skLineSegment(sketch, "E9025", {"start": v(-20.57, -4.19) * mm, "end": v(-20.23, -3.81) * mm});
            skLineSegment(sketch, "E9026", {"start": v(-20.23, -3.81) * mm, "end": v(-19.9, -3.42) * mm});
            skLineSegment(sketch, "E9027", {"start": v(-19.9, -3.42) * mm, "end": v(-19.57, -3.03) * mm});
            skLineSegment(sketch, "E9028", {"start": v(-19.57, -3.03) * mm, "end": v(-19.27, -2.64) * mm});
            skLineSegment(sketch, "E9029", {"start": v(-19.27, -2.64) * mm, "end": v(-19, -2.28) * mm});
            skLineSegment(sketch, "E9030", {"start": v(-19, -2.28) * mm, "end": v(-18.76, -1.94) * mm});
            skLineSegment(sketch, "E9031", {"start": v(-18.76, -1.94) * mm, "end": v(-18.57, -1.65) * mm});
            skLineSegment(sketch, "E9032", {"start": v(-18.57, -1.65) * mm, "end": v(-18.43, -1.42) * mm});
            skLineSegment(sketch, "E9033", {"start": v(-18.43, -1.42) * mm, "end": v(-17.95, -0.48) * mm});
            skLineSegment(sketch, "E9034", {"start": v(-17.95, -0.48) * mm, "end": v(-18.32, -0.12) * mm});
            skLineSegment(sketch, "E9035", {"start": v(-18.32, -0.12) * mm, "end": v(-18.8, 0.35) * mm});
            skLineSegment(sketch, "E9036", {"start": v(-18.8, 0.35) * mm, "end": v(-19.66, 1.25) * mm});
            skLineSegment(sketch, "E9037", {"start": v(-20.05, 1.67) * mm, "end": v(-20.18, 1.81) * mm});
            skLineSegment(sketch, "E9038", {"start": v(-20.18, 1.81) * mm, "end": v(-20.59, 2.27) * mm});
            skLineSegment(sketch, "E9039", {"start": v(-20.59, 2.27) * mm, "end": v(-20.95, 2.7) * mm});
            skLineSegment(sketch, "E9040", {"start": v(-20.95, 2.7) * mm, "end": v(-21.24, 3.07) * mm});
            skLineSegment(sketch, "E9041", {"start": v(-21.24, 3.07) * mm, "end": v(-22, 4.05) * mm});
            skLineSegment(sketch, "E9042", {"start": v(-22, 4.05) * mm, "end": v(-22.62, 3.37) * mm});
            skLineSegment(sketch, "E9043", {"start": v(-22.62, 3.37) * mm, "end": v(-23.28, 2.65) * mm});
            skLineSegment(sketch, "E9044", {"start": v(-23.28, 2.65) * mm, "end": v(-23.61, 2.3) * mm});
            skLineSegment(sketch, "E9045", {"start": v(-23.61, 2.3) * mm, "end": v(-23.95, 1.97) * mm});
            skLineSegment(sketch, "E9046", {"start": v(-23.95, 1.97) * mm, "end": v(-24.3, 1.66) * mm});
            skLineSegment(sketch, "E9047", {"start": v(-24.3, 1.66) * mm, "end": v(-24.47, 1.53) * mm});
            skLineSegment(sketch, "E9048", {"start": v(-24.47, 1.53) * mm, "end": v(-24.65, 1.4) * mm});
            skLineSegment(sketch, "E9049", {"start": v(-24.65, 1.4) * mm, "end": v(-24.94, 1.22) * mm});
            skLineSegment(sketch, "E9050", {"start": v(-24.94, 1.22) * mm, "end": v(-25.26, 1.04) * mm});
            skLineSegment(sketch, "E9051", {"start": v(-25.26, 1.04) * mm, "end": v(-25.6, 0.86) * mm});
            skLineSegment(sketch, "E9052", {"start": v(-25.6, 0.86) * mm, "end": v(-25.97, 0.7) * mm});
            skLineSegment(sketch, "E9053", {"start": v(-25.97, 0.7) * mm, "end": v(-26.33, 0.55) * mm});
            skLineSegment(sketch, "E9054", {"start": v(-26.33, 0.55) * mm, "end": v(-26.7, 0.42) * mm});
            skLineSegment(sketch, "E9055", {"start": v(-26.7, 0.42) * mm, "end": v(-27.05, 0.3) * mm});
            skLineSegment(sketch, "E9056", {"start": v(-27.05, 0.3) * mm, "end": v(-27.38, 0.2) * mm});
            skLineSegment(sketch, "E9057", {"start": v(-27.38, 0.2) * mm, "end": v(-28, 0.02) * mm});
            skLineSegment(sketch, "E9058", {"start": v(-28, 0.02) * mm, "end": v(-28.66, -0.17) * mm});
            skLineSegment(sketch, "E9059", {"start": v(-28.66, -0.17) * mm, "end": v(-29, -0.26) * mm});
            skLineSegment(sketch, "E9060", {"start": v(-29, -0.26) * mm, "end": v(-29.35, -0.34) * mm});
            skLineSegment(sketch, "E9061", {"start": v(-29.35, -0.34) * mm, "end": v(-29.7, -0.4) * mm});
            skLineSegment(sketch, "E9062", {"start": v(-29.7, -0.4) * mm, "end": v(-30.05, -0.46) * mm});
            skLineSegment(sketch, "E9063", {"start": v(-30.05, -0.46) * mm, "end": v(-30.39, -0.48) * mm});
            skLineSegment(sketch, "E9064", {"start": v(-30.39, -0.48) * mm, "end": v(-30.73, -0.5) * mm});
            skLineSegment(sketch, "E9065", {"start": v(-30.73, -0.5) * mm, "end": v(-31.4, -0.49) * mm});
            skLineSegment(sketch, "E9066", {"start": v(-31.4, -0.49) * mm, "end": v(-31.71, -0.48) * mm});
            skLineSegment(sketch, "E9067", {"start": v(-31.71, -0.48) * mm, "end": v(-32.03, -0.48) * mm});
            skLineSegment(sketch, "E9068", {"start": v(-32.03, -0.48) * mm, "end": v(-32.34, -0.5) * mm});
            skLineSegment(sketch, "E9069", {"start": v(-32.34, -0.5) * mm, "end": v(-32.63, -0.52) * mm});
            skLineSegment(sketch, "E9070", {"start": v(-32.63, -0.52) * mm, "end": v(-32.89, -0.93) * mm});
            skLineSegment(sketch, "E9071", {"start": v(-32.89, -0.93) * mm, "end": v(-32.94, -1.03) * mm});
            skLineSegment(sketch, "E9072", {"start": v(-32.94, -1.03) * mm, "end": v(-33, -1.16) * mm});
            skLineSegment(sketch, "E9073", {"start": v(-33, -1.16) * mm, "end": v(-33.03, -1.31) * mm});
            skLineSegment(sketch, "E9074", {"start": v(-33.03, -1.31) * mm, "end": v(-33.07, -1.49) * mm});
            skLineSegment(sketch, "E9075", {"start": v(-33.07, -1.49) * mm, "end": v(-33.1, -1.67) * mm});
            skLineSegment(sketch, "E9076", {"start": v(-33.1, -1.67) * mm, "end": v(-33.13, -1.87) * mm});
            skLineSegment(sketch, "E9077", {"start": v(-33.13, -1.87) * mm, "end": v(-33.15, -2.06) * mm});
            skLineSegment(sketch, "E9078", {"start": v(-33.15, -2.06) * mm, "end": v(-33.15, -2.26) * mm});
            skLineSegment(sketch, "E9079", {"start": v(-33.15, -2.26) * mm, "end": v(-33.16, -3.18) * mm});
            skLineSegment(sketch, "E9080", {"start": v(-33.16, -3.18) * mm, "end": v(-32.98, -3.38) * mm});
            skLineSegment(sketch, "E9081", {"start": v(-32.98, -3.38) * mm, "end": v(-32.79, -3.6) * mm});
            skLineSegment(sketch, "E9082", {"start": v(-32.79, -3.6) * mm, "end": v(-32.4, -4.07) * mm});
            skLineSegment(sketch, "E9083", {"start": v(-32.4, -4.07) * mm, "end": v(-32.2, -4.3) * mm});
            skLineSegment(sketch, "E9084", {"start": v(-32.2, -4.3) * mm, "end": v(-32, -4.5) * mm});
            skLineSegment(sketch, "E9085", {"start": v(-32, -4.5) * mm, "end": v(-31.88, -4.6) * mm});
            skLineSegment(sketch, "E9086", {"start": v(-31.88, -4.6) * mm, "end": v(-31.77, -4.67) * mm});
            skLineSegment(sketch, "E9087", {"start": v(-31.77, -4.67) * mm, "end": v(-31.66, -4.74) * mm});
            skLineSegment(sketch, "E9088", {"start": v(-31.66, -4.74) * mm, "end": v(-31.54, -4.8) * mm});
            skLineSegment(sketch, "E9089", {"start": v(-31.54, -4.8) * mm, "end": v(-31.45, -4.83) * mm});
            skLineSegment(sketch, "E9090", {"start": v(-31.45, -4.83) * mm, "end": v(-31.36, -4.85) * mm});
            skLineSegment(sketch, "E9091", {"start": v(-31.36, -4.85) * mm, "end": v(-31.17, -4.88) * mm});
            skLineSegment(sketch, "E9092", {"start": v(-31.17, -4.88) * mm, "end": v(-30.97, -4.88) * mm});
            skLineSegment(sketch, "E9093", {"start": v(-30.97, -4.88) * mm, "end": v(-30.76, -4.87) * mm});
            skLineSegment(sketch, "E9094", {"start": v(-30.76, -4.87) * mm, "end": v(-30.34, -4.82) * mm});
            skLineSegment(sketch, "E9095", {"start": v(-30.34, -4.82) * mm, "end": v(-30.14, -4.8) * mm});
            skLineSegment(sketch, "E9096", {"start": v(-30.14, -4.8) * mm, "end": v(-29.96, -4.8) * mm});
            skLineSegment(sketch, "E9097", {"start": v(-29.96, -4.8) * mm, "end": v(-29.61, -4.8) * mm});
            skLineSegment(sketch, "E9098", {"start": v(-29.61, -4.8) * mm, "end": v(-29.25, -4.77) * mm});
            skLineSegment(sketch, "E9099", {"start": v(-29.25, -4.77) * mm, "end": v(-28.86, -4.74) * mm});
            skLineSegment(sketch, "E9100", {"start": v(-28.86, -4.74) * mm, "end": v(-28.48, -4.7) * mm});
            skLineSegment(sketch, "E9101", {"start": v(-28.48, -4.7) * mm, "end": v(-28.1, -4.65) * mm});
            skLineSegment(sketch, "E9102", {"start": v(-28.1, -4.65) * mm, "end": v(-27.76, -4.6) * mm});
            skLineSegment(sketch, "E9103", {"start": v(-27.76, -4.6) * mm, "end": v(-27.44, -4.53) * mm});
            skLineSegment(sketch, "E9104", {"start": v(-27.44, -4.53) * mm, "end": v(-27.16, -4.46) * mm});
            skLineSegment(sketch, "E9105", {"start": v(-27.16, -4.46) * mm, "end": v(-26.87, -4.39) * mm});
            skLineSegment(sketch, "E9106", {"start": v(-26.87, -4.39) * mm, "end": v(-26.55, -4.31) * mm});
            skLineSegment(sketch, "E9107", {"start": v(-26.55, -4.31) * mm, "end": v(-26.23, -4.23) * mm});
            skLineSegment(sketch, "E9108", {"start": v(-26.23, -4.23) * mm, "end": v(-26.08, -4.18) * mm});
            skLineSegment(sketch, "E9109", {"start": v(-26.08, -4.18) * mm, "end": v(-25.95, -4.12) * mm});
            skLineSegment(sketch, "E9110", {"start": v(-25.95, -4.12) * mm, "end": v(-25.55, -3.92) * mm});
            skLineSegment(sketch, "E9111", {"start": v(-25.55, -3.92) * mm, "end": v(-25.13, -3.7) * mm});
            skLineSegment(sketch, "E9112", {"start": v(-25.13, -3.7) * mm, "end": v(-24.71, -3.44) * mm});
            skLineSegment(sketch, "E9113", {"start": v(-24.71, -3.44) * mm, "end": v(-24.3, -3.17) * mm});
            skLineSegment(sketch, "E9114", {"start": v(-24.3, -3.17) * mm, "end": v(-23.89, -2.88) * mm});
            skLineSegment(sketch, "E9115", {"start": v(-23.89, -2.88) * mm, "end": v(-23.5, -2.59) * mm});
            skLineSegment(sketch, "E9116", {"start": v(-23.5, -2.59) * mm, "end": v(-23.12, -2.29) * mm});
            skLineSegment(sketch, "E9117", {"start": v(-23.12, -2.29) * mm, "end": v(-22.79, -2) * mm});
            skLineSegment(sketch, "E9118", {"start": v(-22.79, -2) * mm, "end": v(-22.6, -1.82) * mm});
            skLineSegment(sketch, "E9119", {"start": v(-22.6, -1.82) * mm, "end": v(-22.42, -1.63) * mm});
            skLineSegment(sketch, "E9120", {"start": v(-22.42, -1.63) * mm, "end": v(-22.05, -1.21) * mm});
            skLineSegment(sketch, "E9121", {"start": v(-22.05, -1.21) * mm, "end": v(-21.68, -0.76) * mm});
            skLineSegment(sketch, "E9122", {"start": v(-21.68, -0.76) * mm, "end": v(-21.32, -0.3) * mm});
            skLineSegment(sketch, "E9123", {"start": v(-21.32, -0.3) * mm, "end": v(-20.62, 0.64) * mm});
            skLineSegment(sketch, "E9124", {"start": v(-20.62, 0.64) * mm, "end": v(-20.28, 1.09) * mm});
            skLineSegment(sketch, "E9125", {"start": v(-20.28, 1.09) * mm, "end": v(-19.95, 1.5) * mm});
            skLineSegment(sketch, "E9126", {"start": v(-19.95, 1.5) * mm, "end": v(-20.05, 1.67) * mm});
            skLineSegment(sketch, "E9127", {"start": v(-32.94, 30.66) * mm, "end": v(-32.92, 30.52) * mm});
            skLineSegment(sketch, "E9128", {"start": v(-32.92, 30.52) * mm, "end": v(-32.91, 30.41) * mm});
            skLineSegment(sketch, "E9129", {"start": v(-32.91, 30.41) * mm, "end": v(-32.92, 30.34) * mm});
            skLineSegment(sketch, "E9130", {"start": v(-32.92, 30.34) * mm, "end": v(-32.93, 30.3) * mm});
            skLineSegment(sketch, "E9131", {"start": v(-32.93, 30.3) * mm, "end": v(-33.1, 30.13) * mm});
            skLineSegment(sketch, "E9132", {"start": v(-33.1, 30.13) * mm, "end": v(-36.34, 29.85) * mm});
            skLineSegment(sketch, "E9133", {"start": v(-36.34, 29.85) * mm, "end": v(-37.88, 29.73) * mm});
            skLineSegment(sketch, "E9134", {"start": v(-37.88, 29.73) * mm, "end": v(-39.68, 29.6) * mm});
            skLineSegment(sketch, "E9135", {"start": v(-39.68, 29.6) * mm, "end": v(-41.5, 29.48) * mm});
            skLineSegment(sketch, "E9136", {"start": v(-41.5, 29.48) * mm, "end": v(-43.14, 29.38) * mm});
            skLineSegment(sketch, "E9137", {"start": v(-43.14, 29.38) * mm, "end": v(-46.6, 29.2) * mm});
            skLineSegment(sketch, "E9138", {"start": v(-46.6, 29.2) * mm, "end": v(-46.58, 29.31) * mm});
            skLineSegment(sketch, "E9139", {"start": v(-46.58, 29.31) * mm, "end": v(-46.55, 29.82) * mm});
            skLineSegment(sketch, "E9140", {"start": v(-46.55, 29.82) * mm, "end": v(-46.55, 30.3) * mm});
            skLineSegment(sketch, "E9141", {"start": v(-46.55, 30.3) * mm, "end": v(-44.75, 31.75) * mm});
            skLineSegment(sketch, "E9142", {"start": v(-44.75, 31.75) * mm, "end": v(-44.11, 32.29) * mm});
            skLineSegment(sketch, "E9143", {"start": v(-44.11, 32.29) * mm, "end": v(-43.49, 32.85) * mm});
            skLineSegment(sketch, "E9144", {"start": v(-43.49, 32.85) * mm, "end": v(-43.12, 33.2) * mm});
            skLineSegment(sketch, "E9145", {"start": v(-43.12, 33.2) * mm, "end": v(-43.12, 33.2) * mm});
            skLineSegment(sketch, "E9146", {"start": v(-43.12, 33.2) * mm, "end": v(-42.13, 33.18) * mm});
            skLineSegment(sketch, "E9147", {"start": v(-42.13, 33.18) * mm, "end": v(-41.08, 33.15) * mm});
            skLineSegment(sketch, "E9148", {"start": v(-41.08, 33.15) * mm, "end": v(-40.04, 33.13) * mm});
            skLineSegment(sketch, "E9149", {"start": v(-40.04, 33.13) * mm, "end": v(-39.54, 33.13) * mm});
            skLineSegment(sketch, "E9150", {"start": v(-39.54, 33.13) * mm, "end": v(-39.07, 33.14) * mm});
            skLineSegment(sketch, "E9151", {"start": v(-39.07, 33.14) * mm, "end": v(-38.65, 33.16) * mm});
            skLineSegment(sketch, "E9152", {"start": v(-38.65, 33.16) * mm, "end": v(-38.2, 33.19) * mm});
            skLineSegment(sketch, "E9153", {"start": v(-38.2, 33.19) * mm, "end": v(-37.28, 33.27) * mm});
            skLineSegment(sketch, "E9154", {"start": v(-37.28, 33.27) * mm, "end": v(-36.35, 33.37) * mm});
            skLineSegment(sketch, "E9155", {"start": v(-36.35, 33.37) * mm, "end": v(-35.5, 33.45) * mm});
            skLineSegment(sketch, "E9156", {"start": v(-35.5, 33.45) * mm, "end": v(-35.07, 33.48) * mm});
            skLineSegment(sketch, "E9157", {"start": v(-35.07, 33.48) * mm, "end": v(-34.65, 33.49) * mm});
            skLineSegment(sketch, "E9158", {"start": v(-34.65, 33.49) * mm, "end": v(-33.81, 33.49) * mm});
            skLineSegment(sketch, "E9159", {"start": v(-33.81, 33.49) * mm, "end": v(-33.82, 33.49) * mm});
            skLineSegment(sketch, "E9160", {"start": v(-33.82, 33.49) * mm, "end": v(-33.77, 33.46) * mm});
            skLineSegment(sketch, "E9161", {"start": v(-33.77, 33.46) * mm, "end": v(-32.94, 30.66) * mm});
            skLineSegment(sketch, "E9162", {"start": v(-31.87, 27.12) * mm, "end": v(-32, 27.56) * mm});
            skLineSegment(sketch, "E9163", {"start": v(-32, 27.56) * mm, "end": v(-32.62, 29.55) * mm});
            skLineSegment(sketch, "E9164", {"start": v(-32.62, 29.55) * mm, "end": v(-35.92, 29.34) * mm});
            skLineSegment(sketch, "E9165", {"start": v(-35.92, 29.34) * mm, "end": v(-39.39, 29.12) * mm});
            skLineSegment(sketch, "E9166", {"start": v(-39.39, 29.12) * mm, "end": v(-43.04, 28.9) * mm});
            skLineSegment(sketch, "E9167", {"start": v(-43.04, 28.9) * mm, "end": v(-46.67, 28.7) * mm});
            skLineSegment(sketch, "E9168", {"start": v(-46.67, 28.7) * mm, "end": v(-46.77, 28.16) * mm});
            skLineSegment(sketch, "E9169", {"start": v(-46.77, 28.16) * mm, "end": v(-46.91, 27.54) * mm});
            skLineSegment(sketch, "E9170", {"start": v(-46.91, 27.54) * mm, "end": v(-47.1, 26.9) * mm});
            skLineSegment(sketch, "E9171", {"start": v(-47.1, 26.9) * mm, "end": v(-47.3, 26.25) * mm});
            skLineSegment(sketch, "E9172", {"start": v(-47.3, 26.25) * mm, "end": v(-47.3, 26.24) * mm});
            skLineSegment(sketch, "E9173", {"start": v(-47.3, 26.24) * mm, "end": v(-47.04, 25.56) * mm});
            skLineSegment(sketch, "E9174", {"start": v(-47.04, 25.56) * mm, "end": v(-43.98, 25.56) * mm});
            skLineSegment(sketch, "E9175", {"start": v(-43.98, 25.56) * mm, "end": v(-43.06, 25.57) * mm});
            skLineSegment(sketch, "E9176", {"start": v(-43.06, 25.57) * mm, "end": v(-42.1, 25.6) * mm});
            skLineSegment(sketch, "E9177", {"start": v(-42.1, 25.6) * mm, "end": v(-41.13, 25.65) * mm});
            skLineSegment(sketch, "E9178", {"start": v(-41.13, 25.65) * mm, "end": v(-40.14, 25.71) * mm});
            skLineSegment(sketch, "E9179", {"start": v(-40.14, 25.71) * mm, "end": v(-39.15, 25.8) * mm});
            skLineSegment(sketch, "E9180", {"start": v(-39.15, 25.8) * mm, "end": v(-38.18, 25.88) * mm});
            skLineSegment(sketch, "E9181", {"start": v(-38.18, 25.88) * mm, "end": v(-37.23, 25.98) * mm});
            skLineSegment(sketch, "E9182", {"start": v(-37.23, 25.98) * mm, "end": v(-36.32, 26.1) * mm});
            skLineSegment(sketch, "E9183", {"start": v(-36.32, 26.1) * mm, "end": v(-35.45, 26.21) * mm});
            skLineSegment(sketch, "E9184", {"start": v(-35.45, 26.21) * mm, "end": v(-34.65, 26.34) * mm});
            skLineSegment(sketch, "E9185", {"start": v(-34.65, 26.34) * mm, "end": v(-33.93, 26.47) * mm});
            skLineSegment(sketch, "E9186", {"start": v(-33.93, 26.47) * mm, "end": v(-33.3, 26.6) * mm});
            skLineSegment(sketch, "E9187", {"start": v(-33.3, 26.6) * mm, "end": v(-32.76, 26.73) * mm});
            skLineSegment(sketch, "E9188", {"start": v(-32.76, 26.73) * mm, "end": v(-32.53, 26.8) * mm});
            skLineSegment(sketch, "E9189", {"start": v(-32.53, 26.8) * mm, "end": v(-32.33, 26.86) * mm});
            skLineSegment(sketch, "E9190", {"start": v(-32.33, 26.86) * mm, "end": v(-32.16, 26.93) * mm});
            skLineSegment(sketch, "E9191", {"start": v(-32.16, 26.93) * mm, "end": v(-32.03, 27) * mm});
            skLineSegment(sketch, "E9192", {"start": v(-32.03, 27) * mm, "end": v(-31.93, 27.06) * mm});
            skLineSegment(sketch, "E9193", {"start": v(-31.93, 27.06) * mm, "end": v(-31.87, 27.12) * mm});
            skLineSegment(sketch, "E9194", {"start": v(-29.9, 21.2) * mm, "end": v(-30.37, 22.56) * mm});
            skLineSegment(sketch, "E9195", {"start": v(-30.37, 22.56) * mm, "end": v(-30.69, 23.5) * mm});
            skLineSegment(sketch, "E9196", {"start": v(-30.69, 23.5) * mm, "end": v(-31.5, 23.09) * mm});
            skLineSegment(sketch, "E9197", {"start": v(-31.5, 23.09) * mm, "end": v(-31.74, 22.97) * mm});
            skLineSegment(sketch, "E9198", {"start": v(-31.74, 22.97) * mm, "end": v(-32.04, 22.86) * mm});
            skLineSegment(sketch, "E9199", {"start": v(-32.04, 22.86) * mm, "end": v(-32.38, 22.75) * mm});
            skLineSegment(sketch, "E9200", {"start": v(-32.38, 22.75) * mm, "end": v(-32.76, 22.64) * mm});
            skLineSegment(sketch, "E9201", {"start": v(-32.76, 22.64) * mm, "end": v(-33.18, 22.54) * mm});
            skLineSegment(sketch, "E9202", {"start": v(-33.18, 22.54) * mm, "end": v(-33.64, 22.43) * mm});
            skLineSegment(sketch, "E9203", {"start": v(-33.64, 22.43) * mm, "end": v(-34.14, 22.33) * mm});
            skLineSegment(sketch, "E9204", {"start": v(-34.14, 22.33) * mm, "end": v(-34.67, 22.24) * mm});
            skLineSegment(sketch, "E9205", {"start": v(-34.67, 22.24) * mm, "end": v(-35.23, 22.15) * mm});
            skLineSegment(sketch, "E9206", {"start": v(-35.23, 22.15) * mm, "end": v(-35.83, 22.06) * mm});
            skLineSegment(sketch, "E9207", {"start": v(-35.83, 22.06) * mm, "end": v(-36.45, 21.98) * mm});
            skLineSegment(sketch, "E9208", {"start": v(-36.45, 21.98) * mm, "end": v(-37.1, 21.9) * mm});
            skLineSegment(sketch, "E9209", {"start": v(-37.1, 21.9) * mm, "end": v(-37.77, 21.83) * mm});
            skLineSegment(sketch, "E9210", {"start": v(-37.77, 21.83) * mm, "end": v(-38.47, 21.76) * mm});
            skLineSegment(sketch, "E9211", {"start": v(-38.47, 21.76) * mm, "end": v(-39.18, 21.7) * mm});
            skLineSegment(sketch, "E9212", {"start": v(-39.18, 21.7) * mm, "end": v(-39.91, 21.65) * mm});
            skLineSegment(sketch, "E9213", {"start": v(-39.91, 21.65) * mm, "end": v(-43.22, 21.43) * mm});
            skLineSegment(sketch, "E9214", {"start": v(-43.22, 21.43) * mm, "end": v(-43.43, 19.25) * mm});
            skLineSegment(sketch, "E9215", {"start": v(-43.43, 19.25) * mm, "end": v(-42.65, 18.3) * mm});
            skLineSegment(sketch, "E9216", {"start": v(-42.65, 18.3) * mm, "end": v(-39.91, 18.3) * mm});
            skLineSegment(sketch, "E9217", {"start": v(-39.91, 18.3) * mm, "end": v(-37.18, 18.3) * mm});
            skLineSegment(sketch, "E9218", {"start": v(-37.18, 18.3) * mm, "end": v(-34.67, 18.78) * mm});
            skLineSegment(sketch, "E9219", {"start": v(-34.67, 18.78) * mm, "end": v(-34.15, 18.88) * mm});
            skLineSegment(sketch, "E9220", {"start": v(-34.15, 18.88) * mm, "end": v(-33.61, 19) * mm});
            skLineSegment(sketch, "E9221", {"start": v(-33.61, 19) * mm, "end": v(-33.08, 19.14) * mm});
            skLineSegment(sketch, "E9222", {"start": v(-33.08, 19.14) * mm, "end": v(-32.57, 19.28) * mm});
            skLineSegment(sketch, "E9223", {"start": v(-32.57, 19.28) * mm, "end": v(-32.09, 19.42) * mm});
            skLineSegment(sketch, "E9224", {"start": v(-32.09, 19.42) * mm, "end": v(-31.66, 19.55) * mm});
            skLineSegment(sketch, "E9225", {"start": v(-31.66, 19.55) * mm, "end": v(-31.3, 19.68) * mm});
            skLineSegment(sketch, "E9226", {"start": v(-31.3, 19.68) * mm, "end": v(-31.01, 19.8) * mm});
            skLineSegment(sketch, "E9227", {"start": v(-31.01, 19.8) * mm, "end": v(-29.86, 20.35) * mm});
            skLineSegment(sketch, "E9228", {"start": v(-29.86, 20.35) * mm, "end": v(-29.86, 20.87) * mm});
            skLineSegment(sketch, "E9229", {"start": v(-29.86, 20.87) * mm, "end": v(-29.87, 21.01) * mm});
            skLineSegment(sketch, "E9230", {"start": v(-29.87, 21.01) * mm, "end": v(-29.9, 21.2) * mm});
            skLineSegment(sketch, "E9231", {"start": v(-26.01, 11.29) * mm, "end": v(-26.34, 11.97) * mm});
            skLineSegment(sketch, "E9232", {"start": v(-26.34, 11.97) * mm, "end": v(-26.83, 13) * mm});
            skLineSegment(sketch, "E9233", {"start": v(-26.83, 13) * mm, "end": v(-27.28, 14) * mm});
            skLineSegment(sketch, "E9234", {"start": v(-27.28, 14) * mm, "end": v(-27.68, 14.93) * mm});
            skLineSegment(sketch, "E9235", {"start": v(-27.68, 14.93) * mm, "end": v(-27.87, 14.88) * mm});
            skLineSegment(sketch, "E9236", {"start": v(-27.87, 14.88) * mm, "end": v(-28.88, 14.51) * mm});
            skLineSegment(sketch, "E9237", {"start": v(-28.88, 14.51) * mm, "end": v(-30.6, 13.87) * mm});
            skLineSegment(sketch, "E9238", {"start": v(-30.6, 13.87) * mm, "end": v(-32.84, 13.02) * mm});
            skLineSegment(sketch, "E9239", {"start": v(-32.84, 13.02) * mm, "end": v(-38.53, 12.38) * mm});
            skLineSegment(sketch, "E9240", {"start": v(-38.53, 12.38) * mm, "end": v(-38.69, 12.22) * mm});
            skLineSegment(sketch, "E9241", {"start": v(-38.69, 12.22) * mm, "end": v(-38.72, 12.16) * mm});
            skLineSegment(sketch, "E9242", {"start": v(-38.72, 12.16) * mm, "end": v(-38.76, 12.04) * mm});
            skLineSegment(sketch, "E9243", {"start": v(-38.76, 12.04) * mm, "end": v(-38.8, 11.88) * mm});
            skLineSegment(sketch, "E9244", {"start": v(-38.8, 11.88) * mm, "end": v(-38.85, 11.68) * mm});
            skLineSegment(sketch, "E9245", {"start": v(-38.85, 11.68) * mm, "end": v(-38.93, 11.2) * mm});
            skLineSegment(sketch, "E9246", {"start": v(-38.93, 11.2) * mm, "end": v(-39, 10.62) * mm});
            skLineSegment(sketch, "E9247", {"start": v(-39, 10.62) * mm, "end": v(-39.17, 9.18) * mm});
            skLineSegment(sketch, "E9248", {"start": v(-39.17, 9.18) * mm, "end": v(-38.06, 8.07) * mm});
            skLineSegment(sketch, "E9249", {"start": v(-38.06, 8.07) * mm, "end": v(-35.53, 8.07) * mm});
            skLineSegment(sketch, "E9250", {"start": v(-35.53, 8.07) * mm, "end": v(-33, 8.08) * mm});
            skLineSegment(sketch, "E9251", {"start": v(-33, 8.08) * mm, "end": v(-29.47, 9.02) * mm});
            skLineSegment(sketch, "E9252", {"start": v(-29.47, 9.02) * mm, "end": v(-27.68, 10.1) * mm});
            skLineSegment(sketch, "E9253", {"start": v(-27.68, 10.1) * mm, "end": v(-27.1, 10.47) * mm});
            skLineSegment(sketch, "E9254", {"start": v(-27.1, 10.47) * mm, "end": v(-26.6, 10.8) * mm});
            skLineSegment(sketch, "E9255", {"start": v(-26.6, 10.8) * mm, "end": v(-26.4, 10.96) * mm});
            skLineSegment(sketch, "E9256", {"start": v(-26.4, 10.96) * mm, "end": v(-26.22, 11.09) * mm});
            skLineSegment(sketch, "E9257", {"start": v(-26.22, 11.09) * mm, "end": v(-26.1, 11.2) * mm});
            skLineSegment(sketch, "E9258", {"start": v(-26.1, 11.2) * mm, "end": v(-26.01, 11.29) * mm});
            skLineSegment(sketch, "E9259", {"start": v(-22.38, 4.56) * mm, "end": v(-22.46, 4.66) * mm});
            skLineSegment(sketch, "E9260", {"start": v(-22.46, 4.66) * mm, "end": v(-22.86, 5.21) * mm});
            skLineSegment(sketch, "E9261", {"start": v(-22.86, 5.21) * mm, "end": v(-23.24, 5.78) * mm});
            skLineSegment(sketch, "E9262", {"start": v(-23.24, 5.78) * mm, "end": v(-23.6, 6.38) * mm});
            skLineSegment(sketch, "E9263", {"start": v(-23.6, 6.38) * mm, "end": v(-23.76, 6.69) * mm});
            skLineSegment(sketch, "E9264", {"start": v(-23.76, 6.69) * mm, "end": v(-23.88, 6.91) * mm});
            skLineSegment(sketch, "E9265", {"start": v(-23.88, 6.91) * mm, "end": v(-24.22, 6.57) * mm});
            skLineSegment(sketch, "E9266", {"start": v(-24.22, 6.57) * mm, "end": v(-24.4, 6.38) * mm});
            skLineSegment(sketch, "E9267", {"start": v(-24.4, 6.38) * mm, "end": v(-24.57, 6.22) * mm});
            skLineSegment(sketch, "E9268", {"start": v(-24.57, 6.22) * mm, "end": v(-24.82, 6) * mm});
            skLineSegment(sketch, "E9269", {"start": v(-24.82, 6) * mm, "end": v(-25.1, 5.77) * mm});
            skLineSegment(sketch, "E9270", {"start": v(-25.1, 5.77) * mm, "end": v(-25.4, 5.55) * mm});
            skLineSegment(sketch, "E9271", {"start": v(-25.4, 5.55) * mm, "end": v(-25.71, 5.33) * mm});
            skLineSegment(sketch, "E9272", {"start": v(-25.71, 5.33) * mm, "end": v(-26.02, 5.12) * mm});
            skLineSegment(sketch, "E9273", {"start": v(-26.02, 5.12) * mm, "end": v(-26.32, 4.93) * mm});
            skLineSegment(sketch, "E9274", {"start": v(-26.32, 4.93) * mm, "end": v(-26.59, 4.76) * mm});
            skLineSegment(sketch, "E9275", {"start": v(-26.59, 4.76) * mm, "end": v(-26.83, 4.63) * mm});
            skLineSegment(sketch, "E9276", {"start": v(-26.83, 4.63) * mm, "end": v(-27.1, 4.5) * mm});
            skLineSegment(sketch, "E9277", {"start": v(-27.1, 4.5) * mm, "end": v(-27.43, 4.37) * mm});
            skLineSegment(sketch, "E9278", {"start": v(-27.43, 4.37) * mm, "end": v(-27.8, 4.24) * mm});
            skLineSegment(sketch, "E9279", {"start": v(-27.8, 4.24) * mm, "end": v(-28.2, 4.11) * mm});
            skLineSegment(sketch, "E9280", {"start": v(-28.2, 4.11) * mm, "end": v(-28.63, 3.98) * mm});
            skLineSegment(sketch, "E9281", {"start": v(-28.63, 3.98) * mm, "end": v(-29.08, 3.86) * mm});
            skLineSegment(sketch, "E9282", {"start": v(-29.08, 3.86) * mm, "end": v(-29.56, 3.74) * mm});
            skLineSegment(sketch, "E9283", {"start": v(-29.56, 3.74) * mm, "end": v(-30.04, 3.63) * mm});
            skLineSegment(sketch, "E9284", {"start": v(-30.04, 3.63) * mm, "end": v(-30.53, 3.52) * mm});
            skLineSegment(sketch, "E9285", {"start": v(-30.53, 3.52) * mm, "end": v(-31.02, 3.43) * mm});
            skLineSegment(sketch, "E9286", {"start": v(-31.02, 3.43) * mm, "end": v(-31.5, 3.34) * mm});
            skLineSegment(sketch, "E9287", {"start": v(-31.5, 3.34) * mm, "end": v(-31.97, 3.27) * mm});
            skLineSegment(sketch, "E9288", {"start": v(-31.97, 3.27) * mm, "end": v(-32.42, 3.2) * mm});
            skLineSegment(sketch, "E9289", {"start": v(-32.42, 3.2) * mm, "end": v(-32.84, 3.16) * mm});
            skLineSegment(sketch, "E9290", {"start": v(-32.84, 3.16) * mm, "end": v(-33.22, 3.14) * mm});
            skLineSegment(sketch, "E9291", {"start": v(-33.22, 3.14) * mm, "end": v(-33.57, 3.13) * mm});
            skLineSegment(sketch, "E9292", {"start": v(-33.57, 3.13) * mm, "end": v(-34.8, 3.12) * mm});
            skLineSegment(sketch, "E9293", {"start": v(-34.8, 3.12) * mm, "end": v(-34.8, 0.83) * mm});
            skLineSegment(sketch, "E9294", {"start": v(-34.8, 0.83) * mm, "end": v(-34.47, 0.63) * mm});
            skLineSegment(sketch, "E9295", {"start": v(-34.47, 0.63) * mm, "end": v(-34.1, 0.4) * mm});
            skLineSegment(sketch, "E9296", {"start": v(-34.1, 0.4) * mm, "end": v(-33.92, 0.3) * mm});
            skLineSegment(sketch, "E9297", {"start": v(-33.92, 0.3) * mm, "end": v(-33.74, 0.2) * mm});
            skLineSegment(sketch, "E9298", {"start": v(-33.74, 0.2) * mm, "end": v(-33.55, 0.12) * mm});
            skLineSegment(sketch, "E9299", {"start": v(-33.55, 0.12) * mm, "end": v(-33.37, 0.06) * mm});
            skLineSegment(sketch, "E9300", {"start": v(-33.37, 0.06) * mm, "end": v(-33.07, 0) * mm});
            skLineSegment(sketch, "E9301", {"start": v(-33.07, 0) * mm, "end": v(-32.75, -0.04) * mm});
            skLineSegment(sketch, "E9302", {"start": v(-32.75, -0.04) * mm, "end": v(-32.42, -0.07) * mm});
            skLineSegment(sketch, "E9303", {"start": v(-32.42, -0.07) * mm, "end": v(-32.08, -0.08) * mm});
            skLineSegment(sketch, "E9304", {"start": v(-32.08, -0.08) * mm, "end": v(-31.74, -0.09) * mm});
            skLineSegment(sketch, "E9305", {"start": v(-31.74, -0.09) * mm, "end": v(-31.39, -0.08) * mm});
            skLineSegment(sketch, "E9306", {"start": v(-31.39, -0.08) * mm, "end": v(-31.03, -0.07) * mm});
            skLineSegment(sketch, "E9307", {"start": v(-31.03, -0.07) * mm, "end": v(-30.68, -0.04) * mm});
            skLineSegment(sketch, "E9308", {"start": v(-30.68, -0.04) * mm, "end": v(-30.32, 0) * mm});
            skLineSegment(sketch, "E9309", {"start": v(-30.32, 0) * mm, "end": v(-29.97, 0.03) * mm});
            skLineSegment(sketch, "E9310", {"start": v(-29.97, 0.03) * mm, "end": v(-29.27, 0.14) * mm});
            skLineSegment(sketch, "E9311", {"start": v(-29.27, 0.14) * mm, "end": v(-28.6, 0.26) * mm});
            skLineSegment(sketch, "E9312", {"start": v(-28.6, 0.26) * mm, "end": v(-27.99, 0.4) * mm});
            skLineSegment(sketch, "E9313", {"start": v(-27.99, 0.4) * mm, "end": v(-27.63, 0.5) * mm});
            skLineSegment(sketch, "E9314", {"start": v(-27.63, 0.5) * mm, "end": v(-27.25, 0.62) * mm});
            skLineSegment(sketch, "E9315", {"start": v(-27.25, 0.62) * mm, "end": v(-26.86, 0.76) * mm});
            skLineSegment(sketch, "E9316", {"start": v(-26.86, 0.76) * mm, "end": v(-26.48, 0.93) * mm});
            skLineSegment(sketch, "E9317", {"start": v(-26.48, 0.93) * mm, "end": v(-26.1, 1.1) * mm});
            skLineSegment(sketch, "E9318", {"start": v(-26.1, 1.1) * mm, "end": v(-25.73, 1.3) * mm});
            skLineSegment(sketch, "E9319", {"start": v(-25.73, 1.3) * mm, "end": v(-25.38, 1.5) * mm});
            skLineSegment(sketch, "E9320", {"start": v(-25.38, 1.5) * mm, "end": v(-25.07, 1.7) * mm});
            skLineSegment(sketch, "E9321", {"start": v(-25.07, 1.7) * mm, "end": v(-24.89, 1.84) * mm});
            skLineSegment(sketch, "E9322", {"start": v(-24.89, 1.84) * mm, "end": v(-24.7, 1.99) * mm});
            skLineSegment(sketch, "E9323", {"start": v(-24.7, 1.99) * mm, "end": v(-24.35, 2.32) * mm});
            skLineSegment(sketch, "E9324", {"start": v(-24.35, 2.32) * mm, "end": v(-24, 2.68) * mm});
            skLineSegment(sketch, "E9325", {"start": v(-24, 2.68) * mm, "end": v(-23.66, 3.05) * mm});
            skLineSegment(sketch, "E9326", {"start": v(-23.66, 3.05) * mm, "end": v(-23, 3.83) * mm});
            skLineSegment(sketch, "E9327", {"start": v(-23, 3.83) * mm, "end": v(-22.69, 4.2) * mm});
            skLineSegment(sketch, "E9328", {"start": v(-22.69, 4.2) * mm, "end": v(-22.38, 4.56) * mm});
            skLineSegment(sketch, "E9329", {"start": v(-15.62, -2.62) * mm, "end": v(-15.66, -2.6) * mm});
            skLineSegment(sketch, "E9330", {"start": v(-15.66, -2.6) * mm, "end": v(-16, -2.38) * mm});
            skLineSegment(sketch, "E9331", {"start": v(-16, -2.38) * mm, "end": v(-16.3, -2.13) * mm});
            skLineSegment(sketch, "E9332", {"start": v(-16.3, -2.13) * mm, "end": v(-16.6, -1.86) * mm});
            skLineSegment(sketch, "E9333", {"start": v(-16.6, -1.86) * mm, "end": v(-16.88, -1.58) * mm});
            skLineSegment(sketch, "E9334", {"start": v(-16.88, -1.58) * mm, "end": v(-17.4, -1.03) * mm});
            skLineSegment(sketch, "E9335", {"start": v(-17.4, -1.03) * mm, "end": v(-17.48, -0.94) * mm});
            skLineSegment(sketch, "E9336", {"start": v(-17.48, -0.94) * mm, "end": v(-17.9, -1.55) * mm});
            skLineSegment(sketch, "E9337", {"start": v(-17.9, -1.55) * mm, "end": v(-18.57, -2.53) * mm});
            skLineSegment(sketch, "E9338", {"start": v(-18.57, -2.53) * mm, "end": v(-18.81, -2.87) * mm});
            skLineSegment(sketch, "E9339", {"start": v(-18.81, -2.87) * mm, "end": v(-19.1, -3.24) * mm});
            skLineSegment(sketch, "E9340", {"start": v(-19.1, -3.24) * mm, "end": v(-19.43, -3.64) * mm});
            skLineSegment(sketch, "E9341", {"start": v(-19.43, -3.64) * mm, "end": v(-19.79, -4.05) * mm});
            skLineSegment(sketch, "E9342", {"start": v(-19.79, -4.05) * mm, "end": v(-20.16, -4.45) * mm});
            skLineSegment(sketch, "E9343", {"start": v(-20.16, -4.45) * mm, "end": v(-20.54, -4.85) * mm});
            skLineSegment(sketch, "E9344", {"start": v(-20.54, -4.85) * mm, "end": v(-20.91, -5.22) * mm});
            skLineSegment(sketch, "E9345", {"start": v(-20.91, -5.22) * mm, "end": v(-21.27, -5.55) * mm});
            skLineSegment(sketch, "E9346", {"start": v(-21.27, -5.55) * mm, "end": v(-21.66, -5.93) * mm});
            skLineSegment(sketch, "E9347", {"start": v(-21.66, -5.93) * mm, "end": v(-22.07, -6.34) * mm});
            skLineSegment(sketch, "E9348", {"start": v(-22.07, -6.34) * mm, "end": v(-22.28, -6.54) * mm});
            skLineSegment(sketch, "E9349", {"start": v(-22.28, -6.54) * mm, "end": v(-22.5, -6.73) * mm});
            skLineSegment(sketch, "E9350", {"start": v(-22.5, -6.73) * mm, "end": v(-22.72, -6.9) * mm});
            skLineSegment(sketch, "E9351", {"start": v(-22.72, -6.9) * mm, "end": v(-22.93, -7.05) * mm});
            skLineSegment(sketch, "E9352", {"start": v(-22.93, -7.05) * mm, "end": v(-23.27, -7.23) * mm});
            skLineSegment(sketch, "E9353", {"start": v(-23.27, -7.23) * mm, "end": v(-23.63, -7.4) * mm});
            skLineSegment(sketch, "E9354", {"start": v(-23.63, -7.4) * mm, "end": v(-24.02, -7.56) * mm});
            skLineSegment(sketch, "E9355", {"start": v(-24.02, -7.56) * mm, "end": v(-24.43, -7.7) * mm});
            skLineSegment(sketch, "E9356", {"start": v(-24.43, -7.7) * mm, "end": v(-24.84, -7.83) * mm});
            skLineSegment(sketch, "E9357", {"start": v(-24.84, -7.83) * mm, "end": v(-25.25, -7.94) * mm});
            skLineSegment(sketch, "E9358", {"start": v(-25.25, -7.94) * mm, "end": v(-25.64, -8.03) * mm});
            skLineSegment(sketch, "E9359", {"start": v(-25.64, -8.03) * mm, "end": v(-26.02, -8.1) * mm});
            skLineSegment(sketch, "E9360", {"start": v(-26.02, -8.1) * mm, "end": v(-26.38, -8.14) * mm});
            skLineSegment(sketch, "E9361", {"start": v(-26.38, -8.14) * mm, "end": v(-26.78, -8.17) * mm});
            skLineSegment(sketch, "E9362", {"start": v(-26.78, -8.17) * mm, "end": v(-27.19, -8.17) * mm});
            skLineSegment(sketch, "E9363", {"start": v(-27.19, -8.17) * mm, "end": v(-27.6, -8.16) * mm});
            skLineSegment(sketch, "E9364", {"start": v(-27.6, -8.16) * mm, "end": v(-28.43, -8.12) * mm});
            skLineSegment(sketch, "E9365", {"start": v(-28.43, -8.12) * mm, "end": v(-28.83, -8.1) * mm});
            skLineSegment(sketch, "E9366", {"start": v(-28.83, -8.1) * mm, "end": v(-29.2, -8.1) * mm});
            skLineSegment(sketch, "E9367", {"start": v(-29.2, -8.1) * mm, "end": v(-29.22, -8.4) * mm});
            skLineSegment(sketch, "E9368", {"start": v(-29.22, -8.4) * mm, "end": v(-29.24, -8.72) * mm});
            skLineSegment(sketch, "E9369", {"start": v(-29.24, -8.72) * mm, "end": v(-29.25, -8.88) * mm});
            skLineSegment(sketch, "E9370", {"start": v(-29.25, -8.88) * mm, "end": v(-29.25, -9.04) * mm});
            skLineSegment(sketch, "E9371", {"start": v(-29.25, -9.04) * mm, "end": v(-29.23, -9.2) * mm});
            skLineSegment(sketch, "E9372", {"start": v(-29.23, -9.2) * mm, "end": v(-29.2, -9.33) * mm});
            skLineSegment(sketch, "E9373", {"start": v(-29.2, -9.33) * mm, "end": v(-29.1, -9.57) * mm});
            skLineSegment(sketch, "E9374", {"start": v(-29.1, -9.57) * mm, "end": v(-29, -9.8) * mm});
            skLineSegment(sketch, "E9375", {"start": v(-29, -9.8) * mm, "end": v(-28.85, -10.03) * mm});
            skLineSegment(sketch, "E9376", {"start": v(-28.85, -10.03) * mm, "end": v(-28.7, -10.25) * mm});
            skLineSegment(sketch, "E9377", {"start": v(-28.7, -10.25) * mm, "end": v(-28.53, -10.45) * mm});
            skLineSegment(sketch, "E9378", {"start": v(-28.53, -10.45) * mm, "end": v(-28.34, -10.63) * mm});
            skLineSegment(sketch, "E9379", {"start": v(-28.34, -10.63) * mm, "end": v(-28.23, -10.71) * mm});
            skLineSegment(sketch, "E9380", {"start": v(-28.23, -10.71) * mm, "end": v(-28.13, -10.79) * mm});
            skLineSegment(sketch, "E9381", {"start": v(-28.13, -10.79) * mm, "end": v(-28.02, -10.85) * mm});
            skLineSegment(sketch, "E9382", {"start": v(-28.02, -10.85) * mm, "end": v(-27.9, -10.9) * mm});
            skLineSegment(sketch, "E9383", {"start": v(-27.9, -10.9) * mm, "end": v(-27.79, -10.96) * mm});
            skLineSegment(sketch, "E9384", {"start": v(-27.79, -10.96) * mm, "end": v(-27.65, -11) * mm});
            skLineSegment(sketch, "E9385", {"start": v(-27.65, -11) * mm, "end": v(-27.36, -11.06) * mm});
            skLineSegment(sketch, "E9386", {"start": v(-27.36, -11.06) * mm, "end": v(-27.03, -11.1) * mm});
            skLineSegment(sketch, "E9387", {"start": v(-27.03, -11.1) * mm, "end": v(-26.68, -11.13) * mm});
            skLineSegment(sketch, "E9388", {"start": v(-26.68, -11.13) * mm, "end": v(-26.33, -11.13) * mm});
            skLineSegment(sketch, "E9389", {"start": v(-26.33, -11.13) * mm, "end": v(-26, -11.12) * mm});
            skLineSegment(sketch, "E9390", {"start": v(-26, -11.12) * mm, "end": v(-25.69, -11.1) * mm});
            skLineSegment(sketch, "E9391", {"start": v(-25.69, -11.1) * mm, "end": v(-25.41, -11.05) * mm});
            skLineSegment(sketch, "E9392", {"start": v(-25.41, -11.05) * mm, "end": v(-24.9, -10.96) * mm});
            skLineSegment(sketch, "E9393", {"start": v(-24.9, -10.96) * mm, "end": v(-24.45, -10.87) * mm});
            skLineSegment(sketch, "E9394", {"start": v(-24.45, -10.87) * mm, "end": v(-24, -10.76) * mm});
            skLineSegment(sketch, "E9395", {"start": v(-24, -10.76) * mm, "end": v(-23.55, -10.63) * mm});
            skLineSegment(sketch, "E9396", {"start": v(-23.55, -10.63) * mm, "end": v(-23.3, -10.54) * mm});
            skLineSegment(sketch, "E9397", {"start": v(-23.3, -10.54) * mm, "end": v(-23.05, -10.44) * mm});
            skLineSegment(sketch, "E9398", {"start": v(-23.05, -10.44) * mm, "end": v(-22.47, -10.2) * mm});
            skLineSegment(sketch, "E9399", {"start": v(-22.47, -10.2) * mm, "end": v(-21.78, -9.87) * mm});
            skLineSegment(sketch, "E9400", {"start": v(-21.78, -9.87) * mm, "end": v(-20.95, -9.45) * mm});
            skLineSegment(sketch, "E9401", {"start": v(-20.95, -9.45) * mm, "end": v(-20.73, -9.32) * mm});
            skLineSegment(sketch, "E9402", {"start": v(-20.73, -9.32) * mm, "end": v(-20.52, -9.17) * mm});
            skLineSegment(sketch, "E9403", {"start": v(-20.52, -9.17) * mm, "end": v(-20.3, -9) * mm});
            skLineSegment(sketch, "E9404", {"start": v(-20.3, -9) * mm, "end": v(-20.1, -8.82) * mm});
            skLineSegment(sketch, "E9405", {"start": v(-20.1, -8.82) * mm, "end": v(-19.91, -8.62) * mm});
            skLineSegment(sketch, "E9406", {"start": v(-19.91, -8.62) * mm, "end": v(-19.72, -8.4) * mm});
            skLineSegment(sketch, "E9407", {"start": v(-19.72, -8.4) * mm, "end": v(-19.34, -7.95) * mm});
            skLineSegment(sketch, "E9408", {"start": v(-19.34, -7.95) * mm, "end": v(-18.98, -7.48) * mm});
            skLineSegment(sketch, "E9409", {"start": v(-18.98, -7.48) * mm, "end": v(-18.63, -7.02) * mm});
            skLineSegment(sketch, "E9410", {"start": v(-18.63, -7.02) * mm, "end": v(-18.29, -6.58) * mm});
            skLineSegment(sketch, "E9411", {"start": v(-18.29, -6.58) * mm, "end": v(-18.12, -6.37) * mm});
            skLineSegment(sketch, "E9412", {"start": v(-18.12, -6.37) * mm, "end": v(-17.95, -6.18) * mm});
            skLineSegment(sketch, "E9413", {"start": v(-17.95, -6.18) * mm, "end": v(-15.43, -3.6) * mm});
            skLineSegment(sketch, "E9414", {"start": v(-15.43, -3.6) * mm, "end": v(-15.62, -2.62) * mm});
            skLineSegment(sketch, "E9415", {"start": v(0.83, -3.86) * mm, "end": v(0.84, -9.4) * mm});
            skLineSegment(sketch, "E9416", {"start": v(0.84, -9.4) * mm, "end": v(-0.5, -11.97) * mm});
            skLineSegment(sketch, "E9417", {"start": v(-0.5, -11.97) * mm, "end": v(-1.73, -13.08) * mm});
            skLineSegment(sketch, "E9418", {"start": v(-1.73, -13.08) * mm, "end": v(-0.5, -17.07) * mm});
            skLineSegment(sketch, "E9419", {"start": v(-0.5, -17.07) * mm, "end": v(-0.52, -19.48) * mm});
            skLineSegment(sketch, "E9420", {"start": v(-0.52, -19.48) * mm, "end": v(-0.97, -20.74) * mm});
            skLineSegment(sketch, "E9421", {"start": v(-0.97, -20.74) * mm, "end": v(-1.08, -21.02) * mm});
            skLineSegment(sketch, "E9422", {"start": v(-1.08, -21.02) * mm, "end": v(-1.21, -21.33) * mm});
            skLineSegment(sketch, "E9423", {"start": v(-1.21, -21.33) * mm, "end": v(-1.37, -21.67) * mm});
            skLineSegment(sketch, "E9424", {"start": v(-1.37, -21.67) * mm, "end": v(-1.55, -22.01) * mm});
            skLineSegment(sketch, "E9425", {"start": v(-1.55, -22.01) * mm, "end": v(-1.74, -22.36) * mm});
            skLineSegment(sketch, "E9426", {"start": v(-1.74, -22.36) * mm, "end": v(-1.94, -22.7) * mm});
            skLineSegment(sketch, "E9427", {"start": v(-1.94, -22.7) * mm, "end": v(-2.14, -23.03) * mm});
            skLineSegment(sketch, "E9428", {"start": v(-2.14, -23.03) * mm, "end": v(-2.33, -23.32) * mm});
            skLineSegment(sketch, "E9429", {"start": v(-2.33, -23.32) * mm, "end": v(-3.25, -24.64) * mm});
            skLineSegment(sketch, "E9430", {"start": v(-3.25, -24.64) * mm, "end": v(-4.43, -24.33) * mm});
            skLineSegment(sketch, "E9431", {"start": v(-4.43, -24.33) * mm, "end": v(-4.63, -25.54) * mm});
            skLineSegment(sketch, "E9432", {"start": v(-4.63, -25.54) * mm, "end": v(-4.73, -26.08) * mm});
            skLineSegment(sketch, "E9433", {"start": v(-4.73, -26.08) * mm, "end": v(-4.86, -26.66) * mm});
            skLineSegment(sketch, "E9434", {"start": v(-4.86, -26.66) * mm, "end": v(-5, -27.22) * mm});
            skLineSegment(sketch, "E9435", {"start": v(-5, -27.22) * mm, "end": v(-5.13, -27.68) * mm});
            skLineSegment(sketch, "E9436", {"start": v(-5.13, -27.68) * mm, "end": v(-5.43, -28.61) * mm});
            skLineSegment(sketch, "E9437", {"start": v(-5.43, -28.61) * mm, "end": v(-0.33, -28.06) * mm});
            skLineSegment(sketch, "E9438", {"start": v(-0.33, -28.06) * mm, "end": v(6.6, -28.2) * mm});
            skLineSegment(sketch, "E9439", {"start": v(6.6, -28.2) * mm, "end": v(8.58, -28.77) * mm});
            skLineSegment(sketch, "E9440", {"start": v(8.58, -28.77) * mm, "end": v(8.46, -26.44) * mm});
            skLineSegment(sketch, "E9441", {"start": v(8.46, -26.44) * mm, "end": v(8.34, -24.1) * mm});
            skLineSegment(sketch, "E9442", {"start": v(8.34, -24.1) * mm, "end": v(8.22, -24) * mm});
            skLineSegment(sketch, "E9443", {"start": v(8.22, -24) * mm, "end": v(8.1, -23.9) * mm});
            skLineSegment(sketch, "E9444", {"start": v(8.1, -23.9) * mm, "end": v(7.8, -23.68) * mm});
            skLineSegment(sketch, "E9445", {"start": v(7.8, -23.68) * mm, "end": v(7.53, -23.47) * mm});
            skLineSegment(sketch, "E9446", {"start": v(7.53, -23.47) * mm, "end": v(7.4, -23.36) * mm});
            skLineSegment(sketch, "E9447", {"start": v(7.4, -23.36) * mm, "end": v(7.28, -23.25) * mm});
            skLineSegment(sketch, "E9448", {"start": v(7.28, -23.25) * mm, "end": v(7.06, -23.02) * mm});
            skLineSegment(sketch, "E9449", {"start": v(7.06, -23.02) * mm, "end": v(6.84, -22.76) * mm});
            skLineSegment(sketch, "E9450", {"start": v(6.84, -22.76) * mm, "end": v(6.6, -22.46) * mm});
            skLineSegment(sketch, "E9451", {"start": v(6.6, -22.46) * mm, "end": v(6.36, -22.15) * mm});
            skLineSegment(sketch, "E9452", {"start": v(6.36, -22.15) * mm, "end": v(6.13, -21.82) * mm});
            skLineSegment(sketch, "E9453", {"start": v(6.13, -21.82) * mm, "end": v(5.92, -21.5) * mm});
            skLineSegment(sketch, "E9454", {"start": v(5.92, -21.5) * mm, "end": v(5.73, -21.2) * mm});
            skLineSegment(sketch, "E9455", {"start": v(5.73, -21.2) * mm, "end": v(5.57, -20.9) * mm});
            skLineSegment(sketch, "E9456", {"start": v(5.57, -20.9) * mm, "end": v(5.4, -20.58) * mm});
            skLineSegment(sketch, "E9457", {"start": v(5.4, -20.58) * mm, "end": v(5.24, -20.2) * mm});
            skLineSegment(sketch, "E9458", {"start": v(5.24, -20.2) * mm, "end": v(5.1, -19.83) * mm});
            skLineSegment(sketch, "E9459", {"start": v(5.1, -19.83) * mm, "end": v(5.04, -19.65) * mm});
            skLineSegment(sketch, "E9460", {"start": v(5.04, -19.65) * mm, "end": v(4.99, -19.48) * mm});
            skLineSegment(sketch, "E9461", {"start": v(4.99, -19.48) * mm, "end": v(4.93, -19.22) * mm});
            skLineSegment(sketch, "E9462", {"start": v(4.93, -19.22) * mm, "end": v(4.88, -18.93) * mm});
            skLineSegment(sketch, "E9463", {"start": v(4.88, -18.93) * mm, "end": v(4.85, -18.62) * mm});
            skLineSegment(sketch, "E9464", {"start": v(4.85, -18.62) * mm, "end": v(4.82, -18.31) * mm});
            skLineSegment(sketch, "E9465", {"start": v(4.82, -18.31) * mm, "end": v(4.79, -17.7) * mm});
            skLineSegment(sketch, "E9466", {"start": v(4.79, -17.7) * mm, "end": v(4.78, -17.13) * mm});
            skLineSegment(sketch, "E9467", {"start": v(4.78, -17.13) * mm, "end": v(4.79, -16.64) * mm});
            skLineSegment(sketch, "E9468", {"start": v(4.79, -16.64) * mm, "end": v(4.82, -16.16) * mm});
            skLineSegment(sketch, "E9469", {"start": v(4.82, -16.16) * mm, "end": v(4.86, -15.68) * mm});
            skLineSegment(sketch, "E9470", {"start": v(4.86, -15.68) * mm, "end": v(4.91, -15.23) * mm});
            skLineSegment(sketch, "E9471", {"start": v(4.91, -15.23) * mm, "end": v(5.03, -14.43) * mm});
            skLineSegment(sketch, "E9472", {"start": v(5.03, -14.43) * mm, "end": v(5.11, -13.87) * mm});
            skLineSegment(sketch, "E9473", {"start": v(5.11, -13.87) * mm, "end": v(4.62, -12.22) * mm});
            skLineSegment(sketch, "E9474", {"start": v(4.62, -12.22) * mm, "end": v(4.3, -11.56) * mm});
            skLineSegment(sketch, "E9475", {"start": v(4.3, -11.56) * mm, "end": v(3, -8.92) * mm});
            skLineSegment(sketch, "E9476", {"start": v(3, -8.92) * mm, "end": v(2.97, -3.81) * mm});
            skLineSegment(sketch, "E9477", {"start": v(2.97, -3.81) * mm, "end": v(2.97, -3.81) * mm});
            skLineSegment(sketch, "E9478", {"start": v(2.97, -3.81) * mm, "end": v(2.87, -3.84) * mm});
            skLineSegment(sketch, "E9479", {"start": v(2.87, -3.84) * mm, "end": v(2.77, -3.85) * mm});
            skLineSegment(sketch, "E9480", {"start": v(2.77, -3.85) * mm, "end": v(0.83, -3.86) * mm});
            skLineSegment(sketch, "E9481", {"start": v(0.04, -3.43) * mm, "end": v(-0.06, -3.04) * mm});
            skLineSegment(sketch, "E9482", {"start": v(-0.06, -3.04) * mm, "end": v(-0.12, -2.86) * mm});
            skLineSegment(sketch, "E9483", {"start": v(-0.12, -2.86) * mm, "end": v(-0.17, -2.72) * mm});
            skLineSegment(sketch, "E9484", {"start": v(-0.17, -2.72) * mm, "end": v(-0.23, -2.57) * mm});
            skLineSegment(sketch, "E9485", {"start": v(-0.23, -2.57) * mm, "end": v(-0.32, -2.41) * mm});
            skLineSegment(sketch, "E9486", {"start": v(-0.32, -2.41) * mm, "end": v(-0.51, -2.1) * mm});
            skLineSegment(sketch, "E9487", {"start": v(-0.51, -2.1) * mm, "end": v(-0.7, -1.85) * mm});
            skLineSegment(sketch, "E9488", {"start": v(-0.7, -1.85) * mm, "end": v(-0.91, -1.6) * mm});
            skLineSegment(sketch, "E9489", {"start": v(-0.91, -1.6) * mm, "end": v(-1.03, -1.48) * mm});
            skLineSegment(sketch, "E9490", {"start": v(-1.03, -1.48) * mm, "end": v(-1.26, -1.28) * mm});
            skLineSegment(sketch, "E9491", {"start": v(-1.26, -1.28) * mm, "end": v(-1.4, -1.17) * mm});
            skLineSegment(sketch, "E9492", {"start": v(-1.4, -1.17) * mm, "end": v(-1.58, -1.05) * mm});
            skLineSegment(sketch, "E9493", {"start": v(-1.58, -1.05) * mm, "end": v(-1.77, -0.93) * mm});
            skLineSegment(sketch, "E9494", {"start": v(-1.77, -0.93) * mm, "end": v(-2, -0.8) * mm});
            skLineSegment(sketch, "E9495", {"start": v(-2, -0.8) * mm, "end": v(-2.3, -0.65) * mm});
            skLineSegment(sketch, "E9496", {"start": v(-2.3, -0.65) * mm, "end": v(-2.6, -0.47) * mm});
            skLineSegment(sketch, "E9497", {"start": v(-2.6, -0.47) * mm, "end": v(-2.9, -0.33) * mm});
            skLineSegment(sketch, "E9498", {"start": v(-2.9, -0.33) * mm, "end": v(-3, -0.28) * mm});
            skLineSegment(sketch, "E9499", {"start": v(-3, -0.28) * mm, "end": v(-3.1, -0.25) * mm});
            skLineSegment(sketch, "E9500", {"start": v(-3.1, -0.25) * mm, "end": v(-3.35, -0.2) * mm});
            skLineSegment(sketch, "E9501", {"start": v(-3.35, -0.2) * mm, "end": v(-3.61, -0.16) * mm});
            skLineSegment(sketch, "E9502", {"start": v(-3.61, -0.16) * mm, "end": v(-4.19, -0.1) * mm});
            skLineSegment(sketch, "E9503", {"start": v(-4.19, -0.1) * mm, "end": v(-4.8, -0.06) * mm});
            skLineSegment(sketch, "E9504", {"start": v(-4.8, -0.06) * mm, "end": v(-5.42, -0.06) * mm});
            skLineSegment(sketch, "E9505", {"start": v(-5.42, -0.06) * mm, "end": v(-6.05, -0.09) * mm});
            skLineSegment(sketch, "E9506", {"start": v(-6.05, -0.09) * mm, "end": v(-6.68, -0.13) * mm});
            skLineSegment(sketch, "E9507", {"start": v(-6.68, -0.13) * mm, "end": v(-7.27, -0.2) * mm});
            skLineSegment(sketch, "E9508", {"start": v(-7.27, -0.2) * mm, "end": v(-7.83, -0.27) * mm});
            skLineSegment(sketch, "E9509", {"start": v(-7.83, -0.27) * mm, "end": v(-8.25, -0.34) * mm});
            skLineSegment(sketch, "E9510", {"start": v(-8.25, -0.34) * mm, "end": v(-8.7, -0.44) * mm});
            skLineSegment(sketch, "E9511", {"start": v(-8.7, -0.44) * mm, "end": v(-9.16, -0.56) * mm});
            skLineSegment(sketch, "E9512", {"start": v(-9.16, -0.56) * mm, "end": v(-9.63, -0.69) * mm});
            skLineSegment(sketch, "E9513", {"start": v(-9.63, -0.69) * mm, "end": v(-10.1, -0.84) * mm});
            skLineSegment(sketch, "E9514", {"start": v(-10.1, -0.84) * mm, "end": v(-10.54, -1) * mm});
            skLineSegment(sketch, "E9515", {"start": v(-10.54, -1) * mm, "end": v(-10.96, -1.17) * mm});
            skLineSegment(sketch, "E9516", {"start": v(-10.96, -1.17) * mm, "end": v(-11.35, -1.34) * mm});
            skLineSegment(sketch, "E9517", {"start": v(-11.35, -1.34) * mm, "end": v(-11.62, -1.49) * mm});
            skLineSegment(sketch, "E9518", {"start": v(-11.62, -1.49) * mm, "end": v(-11.91, -1.66) * mm});
            skLineSegment(sketch, "E9519", {"start": v(-11.91, -1.66) * mm, "end": v(-12.53, -2.1) * mm});
            skLineSegment(sketch, "E9520", {"start": v(-12.53, -2.1) * mm, "end": v(-13.16, -2.55) * mm});
            skLineSegment(sketch, "E9521", {"start": v(-13.16, -2.55) * mm, "end": v(-13.75, -2.98) * mm});
            skLineSegment(sketch, "E9522", {"start": v(-13.75, -2.98) * mm, "end": v(-13.8, -3.01) * mm});
            skLineSegment(sketch, "E9523", {"start": v(-13.8, -3.01) * mm, "end": v(-14.2, -3.51) * mm});
            skLineSegment(sketch, "E9524", {"start": v(-14.2, -3.51) * mm, "end": v(-14.4, -3.75) * mm});
            skLineSegment(sketch, "E9525", {"start": v(-14.4, -3.75) * mm, "end": v(-14.59, -3.97) * mm});
            skLineSegment(sketch, "E9526", {"start": v(-14.59, -3.97) * mm, "end": v(-14.88, -4.3) * mm});
            skLineSegment(sketch, "E9527", {"start": v(-14.88, -4.3) * mm, "end": v(-15.17, -4.66) * mm});
            skLineSegment(sketch, "E9528", {"start": v(-15.17, -4.66) * mm, "end": v(-15.47, -5.03) * mm});
            skLineSegment(sketch, "E9529", {"start": v(-15.47, -5.03) * mm, "end": v(-15.77, -5.42) * mm});
            skLineSegment(sketch, "E9530", {"start": v(-15.77, -5.42) * mm, "end": v(-16.36, -6.24) * mm});
            skLineSegment(sketch, "E9531", {"start": v(-16.36, -6.24) * mm, "end": v(-16.93, -7.06) * mm});
            skLineSegment(sketch, "E9532", {"start": v(-16.93, -7.06) * mm, "end": v(-17.2, -7.47) * mm});
            skLineSegment(sketch, "E9533", {"start": v(-17.2, -7.47) * mm, "end": v(-17.45, -7.87) * mm});
            skLineSegment(sketch, "E9534", {"start": v(-17.45, -7.87) * mm, "end": v(-17.69, -8.26) * mm});
            skLineSegment(sketch, "E9535", {"start": v(-17.69, -8.26) * mm, "end": v(-17.9, -8.64) * mm});
            skLineSegment(sketch, "E9536", {"start": v(-17.9, -8.64) * mm, "end": v(-18.1, -8.99) * mm});
            skLineSegment(sketch, "E9537", {"start": v(-18.1, -8.99) * mm, "end": v(-18.26, -9.32) * mm});
            skLineSegment(sketch, "E9538", {"start": v(-18.26, -9.32) * mm, "end": v(-18.4, -9.62) * mm});
            skLineSegment(sketch, "E9539", {"start": v(-18.4, -9.62) * mm, "end": v(-18.51, -9.88) * mm});
            skLineSegment(sketch, "E9540", {"start": v(-18.51, -9.88) * mm, "end": v(-18.75, -10.51) * mm});
            skLineSegment(sketch, "E9541", {"start": v(-18.75, -10.51) * mm, "end": v(-18.1, -10.42) * mm});
            skLineSegment(sketch, "E9542", {"start": v(-18.1, -10.42) * mm, "end": v(-17.42, -10.34) * mm});
            skLineSegment(sketch, "E9543", {"start": v(-17.42, -10.34) * mm, "end": v(-17.07, -10.3) * mm});
            skLineSegment(sketch, "E9544", {"start": v(-17.07, -10.3) * mm, "end": v(-16.73, -10.23) * mm});
            skLineSegment(sketch, "E9545", {"start": v(-16.73, -10.23) * mm, "end": v(-16.4, -10.17) * mm});
            skLineSegment(sketch, "E9546", {"start": v(-16.4, -10.17) * mm, "end": v(-16.1, -10.09) * mm});
            skLineSegment(sketch, "E9547", {"start": v(-16.1, -10.09) * mm, "end": v(-15.79, -9.98) * mm});
            skLineSegment(sketch, "E9548", {"start": v(-15.79, -9.98) * mm, "end": v(-15.47, -9.86) * mm});
            skLineSegment(sketch, "E9549", {"start": v(-15.47, -9.86) * mm, "end": v(-15.15, -9.72) * mm});
            skLineSegment(sketch, "E9550", {"start": v(-15.15, -9.72) * mm, "end": v(-14.82, -9.56) * mm});
            skLineSegment(sketch, "E9551", {"start": v(-14.82, -9.56) * mm, "end": v(-14.17, -9.22) * mm});
            skLineSegment(sketch, "E9552", {"start": v(-14.17, -9.22) * mm, "end": v(-13.5, -8.86) * mm});
            skLineSegment(sketch, "E9553", {"start": v(-13.5, -8.86) * mm, "end": v(-12.83, -8.5) * mm});
            skLineSegment(sketch, "E9554", {"start": v(-12.83, -8.5) * mm, "end": v(-12.5, -8.34) * mm});
            skLineSegment(sketch, "E9555", {"start": v(-12.5, -8.34) * mm, "end": v(-12.17, -8.18) * mm});
            skLineSegment(sketch, "E9556", {"start": v(-12.17, -8.18) * mm, "end": v(-11.84, -8.03) * mm});
            skLineSegment(sketch, "E9557", {"start": v(-11.84, -8.03) * mm, "end": v(-11.52, -7.9) * mm});
            skLineSegment(sketch, "E9558", {"start": v(-11.52, -7.9) * mm, "end": v(-11.2, -7.78) * mm});
            skLineSegment(sketch, "E9559", {"start": v(-11.2, -7.78) * mm, "end": v(-10.88, -7.69) * mm});
            skLineSegment(sketch, "E9560", {"start": v(-10.88, -7.69) * mm, "end": v(-10.39, -7.56) * mm});
            skLineSegment(sketch, "E9561", {"start": v(-10.39, -7.56) * mm, "end": v(-9.86, -7.44) * mm});
            skLineSegment(sketch, "E9562", {"start": v(-9.86, -7.44) * mm, "end": v(-9.3, -7.34) * mm});
            skLineSegment(sketch, "E9563", {"start": v(-9.3, -7.34) * mm, "end": v(-9, -7.3) * mm});
            skLineSegment(sketch, "E9564", {"start": v(-9, -7.3) * mm, "end": v(-8.72, -7.25) * mm});
            skLineSegment(sketch, "E9565", {"start": v(-8.72, -7.25) * mm, "end": v(-8.43, -7.22) * mm});
            skLineSegment(sketch, "E9566", {"start": v(-8.43, -7.22) * mm, "end": v(-8.15, -7.2) * mm});
            skLineSegment(sketch, "E9567", {"start": v(-8.15, -7.2) * mm, "end": v(-7.87, -7.2) * mm});
            skLineSegment(sketch, "E9568", {"start": v(-7.87, -7.2) * mm, "end": v(-7.6, -7.2) * mm});
            skLineSegment(sketch, "E9569", {"start": v(-7.6, -7.2) * mm, "end": v(-7.32, -7.22) * mm});
            skLineSegment(sketch, "E9570", {"start": v(-7.32, -7.22) * mm, "end": v(-7.06, -7.25) * mm});
            skLineSegment(sketch, "E9571", {"start": v(-7.06, -7.25) * mm, "end": v(-6.81, -7.3) * mm});
            skLineSegment(sketch, "E9572", {"start": v(-6.81, -7.3) * mm, "end": v(-6.57, -7.36) * mm});
            skLineSegment(sketch, "E9573", {"start": v(-6.57, -7.36) * mm, "end": v(-6.42, -7.42) * mm});
            skLineSegment(sketch, "E9574", {"start": v(-6.42, -7.42) * mm, "end": v(-6.26, -7.5) * mm});
            skLineSegment(sketch, "E9575", {"start": v(-6.26, -7.5) * mm, "end": v(-6.11, -7.58) * mm});
            skLineSegment(sketch, "E9576", {"start": v(-6.11, -7.58) * mm, "end": v(-5.96, -7.67) * mm});
            skLineSegment(sketch, "E9577", {"start": v(-5.96, -7.67) * mm, "end": v(-5.8, -7.78) * mm});
            skLineSegment(sketch, "E9578", {"start": v(-5.8, -7.78) * mm, "end": v(-5.66, -7.9) * mm});
            skLineSegment(sketch, "E9579", {"start": v(-5.66, -7.9) * mm, "end": v(-5.37, -8.15) * mm});
            skLineSegment(sketch, "E9580", {"start": v(-5.37, -8.15) * mm, "end": v(-5.09, -8.42) * mm});
            skLineSegment(sketch, "E9581", {"start": v(-5.09, -8.42) * mm, "end": v(-4.82, -8.7) * mm});
            skLineSegment(sketch, "E9582", {"start": v(-4.82, -8.7) * mm, "end": v(-4.35, -9.23) * mm});
            skLineSegment(sketch, "E9583", {"start": v(-4.35, -9.23) * mm, "end": v(-4.2, -9.42) * mm});
            skLineSegment(sketch, "E9584", {"start": v(-4.2, -9.42) * mm, "end": v(-4.04, -9.61) * mm});
            skLineSegment(sketch, "E9585", {"start": v(-4.04, -9.61) * mm, "end": v(-3.74, -10.03) * mm});
            skLineSegment(sketch, "E9586", {"start": v(-3.74, -10.03) * mm, "end": v(-3.45, -10.48) * mm});
            skLineSegment(sketch, "E9587", {"start": v(-3.45, -10.48) * mm, "end": v(-3.17, -10.95) * mm});
            skLineSegment(sketch, "E9588", {"start": v(-3.17, -10.95) * mm, "end": v(-2.62, -11.9) * mm});
            skLineSegment(sketch, "E9589", {"start": v(-2.62, -11.9) * mm, "end": v(-2.35, -12.34) * mm});
            skLineSegment(sketch, "E9590", {"start": v(-2.35, -12.34) * mm, "end": v(-2.1, -12.76) * mm});
            skLineSegment(sketch, "E9591", {"start": v(-2.1, -12.76) * mm, "end": v(-1.6, -12.35) * mm});
            skLineSegment(sketch, "E9592", {"start": v(-1.6, -12.35) * mm, "end": v(-1.48, -12.24) * mm});
            skLineSegment(sketch, "E9593", {"start": v(-1.48, -12.24) * mm, "end": v(-1.35, -12.08) * mm});
            skLineSegment(sketch, "E9594", {"start": v(-1.35, -12.08) * mm, "end": v(-1.2, -11.9) * mm});
            skLineSegment(sketch, "E9595", {"start": v(-1.2, -11.9) * mm, "end": v(-1.04, -11.66) * mm});
            skLineSegment(sketch, "E9596", {"start": v(-1.04, -11.66) * mm, "end": v(-0.87, -11.42) * mm});
            skLineSegment(sketch, "E9597", {"start": v(-0.87, -11.42) * mm, "end": v(-0.7, -11.15) * mm});
            skLineSegment(sketch, "E9598", {"start": v(-0.7, -11.15) * mm, "end": v(-0.54, -10.87) * mm});
            skLineSegment(sketch, "E9599", {"start": v(-0.54, -10.87) * mm, "end": v(-0.39, -10.6) * mm});
            skLineSegment(sketch, "E9600", {"start": v(-0.39, -10.6) * mm, "end": v(0.33, -9.25) * mm});
            skLineSegment(sketch, "E9601", {"start": v(0.33, -9.25) * mm, "end": v(0.32, -8.54) * mm});
            skLineSegment(sketch, "E9602", {"start": v(0.32, -8.54) * mm, "end": v(0.3, -7.68) * mm});
            skLineSegment(sketch, "E9603", {"start": v(0.3, -7.68) * mm, "end": v(0.2, -5.8) * mm});
            skLineSegment(sketch, "E9604", {"start": v(0.2, -5.8) * mm, "end": v(0.1, -4.19) * mm});
            skLineSegment(sketch, "E9605", {"start": v(0.1, -4.19) * mm, "end": v(0.07, -3.67) * mm});
            skLineSegment(sketch, "E9606", {"start": v(0.07, -3.67) * mm, "end": v(0.04, -3.43) * mm});
            skLineSegment(sketch, "E9607", {"start": v(30.76, 20.17) * mm, "end": v(31.38, 19.72) * mm});
            skLineSegment(sketch, "E9608", {"start": v(31.38, 19.72) * mm, "end": v(31.52, 19.63) * mm});
            skLineSegment(sketch, "E9609", {"start": v(31.52, 19.63) * mm, "end": v(31.68, 19.53) * mm});
            skLineSegment(sketch, "E9610", {"start": v(31.68, 19.53) * mm, "end": v(31.85, 19.44) * mm});
            skLineSegment(sketch, "E9611", {"start": v(31.85, 19.44) * mm, "end": v(32.05, 19.35) * mm});
            skLineSegment(sketch, "E9612", {"start": v(32.05, 19.35) * mm, "end": v(32.49, 19.16) * mm});
            skLineSegment(sketch, "E9613", {"start": v(32.49, 19.16) * mm, "end": v(32.99, 18.98) * mm});
            skLineSegment(sketch, "E9614", {"start": v(32.99, 18.98) * mm, "end": v(33.54, 18.81) * mm});
            skLineSegment(sketch, "E9615", {"start": v(33.54, 18.81) * mm, "end": v(34.14, 18.65) * mm});
            skLineSegment(sketch, "E9616", {"start": v(34.14, 18.65) * mm, "end": v(34.79, 18.5) * mm});
            skLineSegment(sketch, "E9617", {"start": v(34.79, 18.5) * mm, "end": v(35.47, 18.35) * mm});
            skLineSegment(sketch, "E9618", {"start": v(35.47, 18.35) * mm, "end": v(36.19, 18.22) * mm});
            skLineSegment(sketch, "E9619", {"start": v(36.19, 18.22) * mm, "end": v(36.93, 18.1) * mm});
            skLineSegment(sketch, "E9620", {"start": v(36.93, 18.1) * mm, "end": v(37.7, 17.99) * mm});
            skLineSegment(sketch, "E9621", {"start": v(37.7, 17.99) * mm, "end": v(38.48, 17.9) * mm});
            skLineSegment(sketch, "E9622", {"start": v(38.48, 17.9) * mm, "end": v(39.27, 17.81) * mm});
            skLineSegment(sketch, "E9623", {"start": v(39.27, 17.81) * mm, "end": v(40.07, 17.75) * mm});
            skLineSegment(sketch, "E9624", {"start": v(40.07, 17.75) * mm, "end": v(40.87, 17.7) * mm});
            skLineSegment(sketch, "E9625", {"start": v(40.87, 17.7) * mm, "end": v(41.66, 17.68) * mm});
            skLineSegment(sketch, "E9626", {"start": v(41.66, 17.68) * mm, "end": v(43.71, 17.64) * mm});
            skLineSegment(sketch, "E9627", {"start": v(43.71, 17.64) * mm, "end": v(43.85, 17.83) * mm});
            skLineSegment(sketch, "E9628", {"start": v(43.85, 17.83) * mm, "end": v(44, 18.02) * mm});
            skLineSegment(sketch, "E9629", {"start": v(44, 18.02) * mm, "end": v(44.33, 18.43) * mm});
            skLineSegment(sketch, "E9630", {"start": v(44.33, 18.43) * mm, "end": v(44.49, 18.64) * mm});
            skLineSegment(sketch, "E9631", {"start": v(44.49, 18.64) * mm, "end": v(44.62, 18.85) * mm});
            skLineSegment(sketch, "E9632", {"start": v(44.62, 18.85) * mm, "end": v(44.68, 18.96) * mm});
            skLineSegment(sketch, "E9633", {"start": v(44.68, 18.96) * mm, "end": v(44.73, 19.07) * mm});
            skLineSegment(sketch, "E9634", {"start": v(44.73, 19.07) * mm, "end": v(44.76, 19.17) * mm});
            skLineSegment(sketch, "E9635", {"start": v(44.76, 19.17) * mm, "end": v(44.79, 19.28) * mm});
            skLineSegment(sketch, "E9636", {"start": v(44.79, 19.28) * mm, "end": v(44.8, 19.37) * mm});
            skLineSegment(sketch, "E9637", {"start": v(44.8, 19.37) * mm, "end": v(44.8, 19.46) * mm});
            skLineSegment(sketch, "E9638", {"start": v(44.8, 19.46) * mm, "end": v(44.78, 19.65) * mm});
            skLineSegment(sketch, "E9639", {"start": v(44.78, 19.65) * mm, "end": v(44.73, 19.84) * mm});
            skLineSegment(sketch, "E9640", {"start": v(44.73, 19.84) * mm, "end": v(44.67, 20.04) * mm});
            skLineSegment(sketch, "E9641", {"start": v(44.67, 20.04) * mm, "end": v(44.53, 20.43) * mm});
            skLineSegment(sketch, "E9642", {"start": v(44.53, 20.43) * mm, "end": v(44.46, 20.62) * mm});
            skLineSegment(sketch, "E9643", {"start": v(44.46, 20.62) * mm, "end": v(44.4, 20.8) * mm});
            skLineSegment(sketch, "E9644", {"start": v(44.4, 20.8) * mm, "end": v(43.38, 20.87) * mm});
            skLineSegment(sketch, "E9645", {"start": v(43.38, 20.87) * mm, "end": v(42.28, 20.93) * mm});
            skLineSegment(sketch, "E9646", {"start": v(42.28, 20.93) * mm, "end": v(41.13, 20.98) * mm});
            skLineSegment(sketch, "E9647", {"start": v(41.13, 20.98) * mm, "end": v(39.97, 21.04) * mm});
            skLineSegment(sketch, "E9648", {"start": v(39.97, 21.04) * mm, "end": v(38.81, 21.12) * mm});
            skLineSegment(sketch, "E9649", {"start": v(38.81, 21.12) * mm, "end": v(38.24, 21.17) * mm});
            skLineSegment(sketch, "E9650", {"start": v(38.24, 21.17) * mm, "end": v(37.68, 21.23) * mm});
            skLineSegment(sketch, "E9651", {"start": v(37.68, 21.23) * mm, "end": v(37.13, 21.3) * mm});
            skLineSegment(sketch, "E9652", {"start": v(37.13, 21.3) * mm, "end": v(36.59, 21.37) * mm});
            skLineSegment(sketch, "E9653", {"start": v(36.59, 21.37) * mm, "end": v(36.07, 21.46) * mm});
            skLineSegment(sketch, "E9654", {"start": v(36.07, 21.46) * mm, "end": v(35.57, 21.56) * mm});
            skLineSegment(sketch, "E9655", {"start": v(35.57, 21.56) * mm, "end": v(35.15, 21.68) * mm});
            skLineSegment(sketch, "E9656", {"start": v(35.15, 21.68) * mm, "end": v(34.7, 21.82) * mm});
            skLineSegment(sketch, "E9657", {"start": v(34.7, 21.82) * mm, "end": v(34.25, 22) * mm});
            skLineSegment(sketch, "E9658", {"start": v(34.25, 22) * mm, "end": v(33.79, 22.18) * mm});
            skLineSegment(sketch, "E9659", {"start": v(33.79, 22.18) * mm, "end": v(32.88, 22.56) * mm});
            skLineSegment(sketch, "E9660", {"start": v(32.88, 22.56) * mm, "end": v(32.45, 22.75) * mm});
            skLineSegment(sketch, "E9661", {"start": v(32.45, 22.75) * mm, "end": v(32.04, 22.9) * mm});
            skLineSegment(sketch, "E9662", {"start": v(32.04, 22.9) * mm, "end": v(31.83, 22.67) * mm});
            skLineSegment(sketch, "E9663", {"start": v(31.83, 22.67) * mm, "end": v(31.78, 22.6) * mm});
            skLineSegment(sketch, "E9664", {"start": v(31.78, 22.6) * mm, "end": v(31.71, 22.48) * mm});
            skLineSegment(sketch, "E9665", {"start": v(31.71, 22.48) * mm, "end": v(31.55, 22.17) * mm});
            skLineSegment(sketch, "E9666", {"start": v(31.55, 22.17) * mm, "end": v(31.37, 21.76) * mm});
            skLineSegment(sketch, "E9667", {"start": v(31.37, 21.76) * mm, "end": v(31.18, 21.3) * mm});
            skLineSegment(sketch, "E9668", {"start": v(31.18, 21.3) * mm, "end": v(30.97, 20.77) * mm});
            skLineSegment(sketch, "E9669", {"start": v(30.97, 20.77) * mm, "end": v(30.76, 20.17) * mm});
            skLineSegment(sketch, "E9670", {"start": v(19.3, -0.88) * mm, "end": v(19.64, -1.44) * mm});
            skLineSegment(sketch, "E9671", {"start": v(19.64, -1.44) * mm, "end": v(20.26, -2.45) * mm});
            skLineSegment(sketch, "E9672", {"start": v(20.26, -2.45) * mm, "end": v(20.59, -2.95) * mm});
            skLineSegment(sketch, "E9673", {"start": v(20.59, -2.95) * mm, "end": v(20.92, -3.44) * mm});
            skLineSegment(sketch, "E9674", {"start": v(20.92, -3.44) * mm, "end": v(21.27, -3.92) * mm});
            skLineSegment(sketch, "E9675", {"start": v(21.27, -3.92) * mm, "end": v(21.45, -4.15) * mm});
            skLineSegment(sketch, "E9676", {"start": v(21.45, -4.15) * mm, "end": v(21.64, -4.38) * mm});
            skLineSegment(sketch, "E9677", {"start": v(21.64, -4.38) * mm, "end": v(21.84, -4.6) * mm});
            skLineSegment(sketch, "E9678", {"start": v(21.84, -4.6) * mm, "end": v(22.04, -4.82) * mm});
            skLineSegment(sketch, "E9679", {"start": v(22.04, -4.82) * mm, "end": v(22.24, -5.03) * mm});
            skLineSegment(sketch, "E9680", {"start": v(22.24, -5.03) * mm, "end": v(22.46, -5.23) * mm});
            skLineSegment(sketch, "E9681", {"start": v(22.46, -5.23) * mm, "end": v(22.76, -5.5) * mm});
            skLineSegment(sketch, "E9682", {"start": v(22.76, -5.5) * mm, "end": v(23.1, -5.76) * mm});
            skLineSegment(sketch, "E9683", {"start": v(23.1, -5.76) * mm, "end": v(23.45, -6.03) * mm});
            skLineSegment(sketch, "E9684", {"start": v(23.45, -6.03) * mm, "end": v(23.8, -6.3) * mm});
            skLineSegment(sketch, "E9685", {"start": v(23.8, -6.3) * mm, "end": v(24.15, -6.54) * mm});
            skLineSegment(sketch, "E9686", {"start": v(24.15, -6.54) * mm, "end": v(24.49, -6.76) * mm});
            skLineSegment(sketch, "E9687", {"start": v(24.49, -6.76) * mm, "end": v(24.8, -6.95) * mm});
            skLineSegment(sketch, "E9688", {"start": v(24.8, -6.95) * mm, "end": v(25.07, -7.1) * mm});
            skLineSegment(sketch, "E9689", {"start": v(25.07, -7.1) * mm, "end": v(25.37, -7.27) * mm});
            skLineSegment(sketch, "E9690", {"start": v(25.37, -7.27) * mm, "end": v(25.68, -7.44) * mm});
            skLineSegment(sketch, "E9691", {"start": v(25.68, -7.44) * mm, "end": v(26, -7.6) * mm});
            skLineSegment(sketch, "E9692", {"start": v(26, -7.6) * mm, "end": v(26.15, -7.68) * mm});
            skLineSegment(sketch, "E9693", {"start": v(26.15, -7.68) * mm, "end": v(26.3, -7.73) * mm});
            skLineSegment(sketch, "E9694", {"start": v(26.3, -7.73) * mm, "end": v(26.7, -7.84) * mm});
            skLineSegment(sketch, "E9695", {"start": v(26.7, -7.84) * mm, "end": v(27.14, -7.94) * mm});
            skLineSegment(sketch, "E9696", {"start": v(27.14, -7.94) * mm, "end": v(27.6, -8.03) * mm});
            skLineSegment(sketch, "E9697", {"start": v(27.6, -8.03) * mm, "end": v(28.06, -8.1) * mm});
            skLineSegment(sketch, "E9698", {"start": v(28.06, -8.1) * mm, "end": v(28.53, -8.15) * mm});
            skLineSegment(sketch, "E9699", {"start": v(28.53, -8.15) * mm, "end": v(29, -8.18) * mm});
            skLineSegment(sketch, "E9700", {"start": v(29, -8.18) * mm, "end": v(29.44, -8.19) * mm});
            skLineSegment(sketch, "E9701", {"start": v(29.44, -8.19) * mm, "end": v(29.86, -8.17) * mm});
            skLineSegment(sketch, "E9702", {"start": v(29.86, -8.17) * mm, "end": v(30.05, -8.15) * mm});
            skLineSegment(sketch, "E9703", {"start": v(30.05, -8.15) * mm, "end": v(30.26, -8.11) * mm});
            skLineSegment(sketch, "E9704", {"start": v(30.26, -8.11) * mm, "end": v(30.69, -8) * mm});
            skLineSegment(sketch, "E9705", {"start": v(30.69, -8) * mm, "end": v(31.11, -7.87) * mm});
            skLineSegment(sketch, "E9706", {"start": v(31.11, -7.87) * mm, "end": v(31.5, -7.76) * mm});
            skLineSegment(sketch, "E9707", {"start": v(31.5, -7.76) * mm, "end": v(32.05, -6.93) * mm});
            skLineSegment(sketch, "E9708", {"start": v(32.05, -6.93) * mm, "end": v(32.16, -6.76) * mm});
            skLineSegment(sketch, "E9709", {"start": v(32.16, -6.76) * mm, "end": v(32.25, -6.6) * mm});
            skLineSegment(sketch, "E9710", {"start": v(32.25, -6.6) * mm, "end": v(32.33, -6.44) * mm});
            skLineSegment(sketch, "E9711", {"start": v(32.33, -6.44) * mm, "end": v(32.39, -6.3) * mm});
            skLineSegment(sketch, "E9712", {"start": v(32.39, -6.3) * mm, "end": v(32.43, -6.16) * mm});
            skLineSegment(sketch, "E9713", {"start": v(32.43, -6.16) * mm, "end": v(32.45, -6.06) * mm});
            skLineSegment(sketch, "E9714", {"start": v(32.45, -6.06) * mm, "end": v(32.45, -5.98) * mm});
            skLineSegment(sketch, "E9715", {"start": v(32.45, -5.98) * mm, "end": v(32.44, -5.95) * mm});
            skLineSegment(sketch, "E9716", {"start": v(32.44, -5.95) * mm, "end": v(32.42, -5.92) * mm});
            skLineSegment(sketch, "E9717", {"start": v(32.42, -5.92) * mm, "end": v(32.34, -5.88) * mm});
            skLineSegment(sketch, "E9718", {"start": v(32.34, -5.88) * mm, "end": v(32.2, -5.83) * mm});
            skLineSegment(sketch, "E9719", {"start": v(32.2, -5.83) * mm, "end": v(31.97, -5.78) * mm});
            skLineSegment(sketch, "E9720", {"start": v(31.97, -5.78) * mm, "end": v(31.7, -5.72) * mm});
            skLineSegment(sketch, "E9721", {"start": v(31.7, -5.72) * mm, "end": v(31, -5.59) * mm});
            skLineSegment(sketch, "E9722", {"start": v(31, -5.59) * mm, "end": v(30.2, -5.46) * mm});
            skLineSegment(sketch, "E9723", {"start": v(30.2, -5.46) * mm, "end": v(29.7, -5.4) * mm});
            skLineSegment(sketch, "E9724", {"start": v(29.7, -5.4) * mm, "end": v(29.16, -5.35) * mm});
            skLineSegment(sketch, "E9725", {"start": v(29.16, -5.35) * mm, "end": v(28.89, -5.32) * mm});
            skLineSegment(sketch, "E9726", {"start": v(28.89, -5.32) * mm, "end": v(28.62, -5.28) * mm});
            skLineSegment(sketch, "E9727", {"start": v(28.62, -5.28) * mm, "end": v(28.37, -5.23) * mm});
            skLineSegment(sketch, "E9728", {"start": v(28.37, -5.23) * mm, "end": v(28.14, -5.17) * mm});
            skLineSegment(sketch, "E9729", {"start": v(28.14, -5.17) * mm, "end": v(27.69, -5.02) * mm});
            skLineSegment(sketch, "E9730", {"start": v(27.69, -5.02) * mm, "end": v(27.22, -4.83) * mm});
            skLineSegment(sketch, "E9731", {"start": v(27.22, -4.83) * mm, "end": v(26.74, -4.63) * mm});
            skLineSegment(sketch, "E9732", {"start": v(26.74, -4.63) * mm, "end": v(26.25, -4.4) * mm});
            skLineSegment(sketch, "E9733", {"start": v(26.25, -4.4) * mm, "end": v(25.78, -4.15) * mm});
            skLineSegment(sketch, "E9734", {"start": v(25.78, -4.15) * mm, "end": v(25.33, -3.89) * mm});
            skLineSegment(sketch, "E9735", {"start": v(25.33, -3.89) * mm, "end": v(24.9, -3.62) * mm});
            skLineSegment(sketch, "E9736", {"start": v(24.9, -3.62) * mm, "end": v(24.7, -3.48) * mm});
            skLineSegment(sketch, "E9737", {"start": v(24.7, -3.48) * mm, "end": v(24.52, -3.34) * mm});
            skLineSegment(sketch, "E9738", {"start": v(24.52, -3.34) * mm, "end": v(24.33, -3.18) * mm});
            skLineSegment(sketch, "E9739", {"start": v(24.33, -3.18) * mm, "end": v(24.13, -3) * mm});
            skLineSegment(sketch, "E9740", {"start": v(24.13, -3) * mm, "end": v(23.73, -2.63) * mm});
            skLineSegment(sketch, "E9741", {"start": v(23.73, -2.63) * mm, "end": v(23.34, -2.22) * mm});
            skLineSegment(sketch, "E9742", {"start": v(23.34, -2.22) * mm, "end": v(22.95, -1.8) * mm});
            skLineSegment(sketch, "E9743", {"start": v(22.95, -1.8) * mm, "end": v(22.2, -0.92) * mm});
            skLineSegment(sketch, "E9744", {"start": v(22.2, -0.92) * mm, "end": v(21.51, -0.1) * mm});
            skLineSegment(sketch, "E9745", {"start": v(21.51, -0.1) * mm, "end": v(20.87, 0.7) * mm});
            skLineSegment(sketch, "E9746", {"start": v(20.87, 0.7) * mm, "end": v(20.6, 0.37) * mm});
            skLineSegment(sketch, "E9747", {"start": v(20.6, 0.37) * mm, "end": v(20, -0.26) * mm});
            skLineSegment(sketch, "E9748", {"start": v(20, -0.26) * mm, "end": v(19.65, -0.58) * mm});
            skLineSegment(sketch, "E9749", {"start": v(19.65, -0.58) * mm, "end": v(19.3, -0.88) * mm});
            skLineSegment(sketch, "E9750", {"start": v(31.9, 23.56) * mm, "end": v(32.25, 23.3) * mm});
            skLineSegment(sketch, "E9751", {"start": v(32.25, 23.3) * mm, "end": v(32.63, 23.03) * mm});
            skLineSegment(sketch, "E9752", {"start": v(32.63, 23.03) * mm, "end": v(32.83, 22.9) * mm});
            skLineSegment(sketch, "E9753", {"start": v(32.83, 22.9) * mm, "end": v(33.02, 22.77) * mm});
            skLineSegment(sketch, "E9754", {"start": v(33.02, 22.77) * mm, "end": v(33.21, 22.66) * mm});
            skLineSegment(sketch, "E9755", {"start": v(33.21, 22.66) * mm, "end": v(33.4, 22.57) * mm});
            skLineSegment(sketch, "E9756", {"start": v(33.4, 22.57) * mm, "end": v(33.67, 22.48) * mm});
            skLineSegment(sketch, "E9757", {"start": v(33.67, 22.48) * mm, "end": v(33.97, 22.4) * mm});
            skLineSegment(sketch, "E9758", {"start": v(33.97, 22.4) * mm, "end": v(34.28, 22.34) * mm});
            skLineSegment(sketch, "E9759", {"start": v(34.28, 22.34) * mm, "end": v(34.6, 22.3) * mm});
            skLineSegment(sketch, "E9760", {"start": v(34.6, 22.3) * mm, "end": v(35.25, 22.2) * mm});
            skLineSegment(sketch, "E9761", {"start": v(35.25, 22.2) * mm, "end": v(35.55, 22.16) * mm});
            skLineSegment(sketch, "E9762", {"start": v(35.55, 22.16) * mm, "end": v(35.84, 22.12) * mm});
            skLineSegment(sketch, "E9763", {"start": v(35.84, 22.12) * mm, "end": v(36.4, 22.02) * mm});
            skLineSegment(sketch, "E9764", {"start": v(36.4, 22.02) * mm, "end": v(37.09, 21.92) * mm});
            skLineSegment(sketch, "E9765", {"start": v(37.09, 21.92) * mm, "end": v(37.85, 21.82) * mm});
            skLineSegment(sketch, "E9766", {"start": v(37.85, 21.82) * mm, "end": v(38.68, 21.73) * mm});
            skLineSegment(sketch, "E9767", {"start": v(38.68, 21.73) * mm, "end": v(39.54, 21.64) * mm});
            skLineSegment(sketch, "E9768", {"start": v(39.54, 21.64) * mm, "end": v(40.41, 21.56) * mm});
            skLineSegment(sketch, "E9769", {"start": v(40.41, 21.56) * mm, "end": v(41.26, 21.5) * mm});
            skLineSegment(sketch, "E9770", {"start": v(41.26, 21.5) * mm, "end": v(42.08, 21.44) * mm});
            skLineSegment(sketch, "E9771", {"start": v(42.08, 21.44) * mm, "end": v(42.52, 21.4) * mm});
            skLineSegment(sketch, "E9772", {"start": v(42.52, 21.4) * mm, "end": v(43, 21.35) * mm});
            skLineSegment(sketch, "E9773", {"start": v(43, 21.35) * mm, "end": v(43.48, 21.28) * mm});
            skLineSegment(sketch, "E9774", {"start": v(43.48, 21.28) * mm, "end": v(43.98, 21.22) * mm});
            skLineSegment(sketch, "E9775", {"start": v(43.98, 21.22) * mm, "end": v(44.48, 21.17) * mm});
            skLineSegment(sketch, "E9776", {"start": v(44.48, 21.17) * mm, "end": v(44.73, 21.15) * mm});
            skLineSegment(sketch, "E9777", {"start": v(44.73, 21.15) * mm, "end": v(44.97, 21.14) * mm});
            skLineSegment(sketch, "E9778", {"start": v(44.97, 21.14) * mm, "end": v(45.2, 21.15) * mm});
            skLineSegment(sketch, "E9779", {"start": v(45.2, 21.15) * mm, "end": v(45.44, 21.16) * mm});
            skLineSegment(sketch, "E9780", {"start": v(45.44, 21.16) * mm, "end": v(45.66, 21.19) * mm});
            skLineSegment(sketch, "E9781", {"start": v(45.66, 21.19) * mm, "end": v(45.87, 21.23) * mm});
            skLineSegment(sketch, "E9782", {"start": v(45.87, 21.23) * mm, "end": v(46.17, 21.3) * mm});
            skLineSegment(sketch, "E9783", {"start": v(46.17, 21.3) * mm, "end": v(46.49, 21.41) * mm});
            skLineSegment(sketch, "E9784", {"start": v(46.49, 21.41) * mm, "end": v(46.8, 21.54) * mm});
            skLineSegment(sketch, "E9785", {"start": v(46.8, 21.54) * mm, "end": v(47.13, 21.7) * mm});
            skLineSegment(sketch, "E9786", {"start": v(47.13, 21.7) * mm, "end": v(47.43, 21.86) * mm});
            skLineSegment(sketch, "E9787", {"start": v(47.43, 21.86) * mm, "end": v(47.58, 21.96) * mm});
            skLineSegment(sketch, "E9788", {"start": v(47.58, 21.96) * mm, "end": v(47.72, 22.06) * mm});
            skLineSegment(sketch, "E9789", {"start": v(47.72, 22.06) * mm, "end": v(47.84, 22.16) * mm});
            skLineSegment(sketch, "E9790", {"start": v(47.84, 22.16) * mm, "end": v(47.96, 22.27) * mm});
            skLineSegment(sketch, "E9791", {"start": v(47.96, 22.27) * mm, "end": v(48.07, 22.38) * mm});
            skLineSegment(sketch, "E9792", {"start": v(48.07, 22.38) * mm, "end": v(48.17, 22.5) * mm});
            skLineSegment(sketch, "E9793", {"start": v(48.17, 22.5) * mm, "end": v(48.22, 22.57) * mm});
            skLineSegment(sketch, "E9794", {"start": v(48.22, 22.57) * mm, "end": v(48.26, 22.65) * mm});
            skLineSegment(sketch, "E9795", {"start": v(48.26, 22.65) * mm, "end": v(48.29, 22.73) * mm});
            skLineSegment(sketch, "E9796", {"start": v(48.29, 22.73) * mm, "end": v(48.31, 22.8) * mm});
            skLineSegment(sketch, "E9797", {"start": v(48.31, 22.8) * mm, "end": v(48.34, 22.98) * mm});
            skLineSegment(sketch, "E9798", {"start": v(48.34, 22.98) * mm, "end": v(48.33, 23.16) * mm});
            skLineSegment(sketch, "E9799", {"start": v(48.33, 23.16) * mm, "end": v(48.31, 23.34) * mm});
            skLineSegment(sketch, "E9800", {"start": v(48.31, 23.34) * mm, "end": v(48.28, 23.52) * mm});
            skLineSegment(sketch, "E9801", {"start": v(48.28, 23.52) * mm, "end": v(48.18, 23.88) * mm});
            skLineSegment(sketch, "E9802", {"start": v(48.18, 23.88) * mm, "end": v(48.11, 24.2) * mm});
            skLineSegment(sketch, "E9803", {"start": v(48.11, 24.2) * mm, "end": v(45.75, 24.36) * mm});
            skLineSegment(sketch, "E9804", {"start": v(45.75, 24.36) * mm, "end": v(43.2, 24.5) * mm});
            skLineSegment(sketch, "E9805", {"start": v(43.2, 24.5) * mm, "end": v(41.92, 24.6) * mm});
            skLineSegment(sketch, "E9806", {"start": v(41.92, 24.6) * mm, "end": v(40.66, 24.69) * mm});
            skLineSegment(sketch, "E9807", {"start": v(40.66, 24.69) * mm, "end": v(39.45, 24.8) * mm});
            skLineSegment(sketch, "E9808", {"start": v(39.45, 24.8) * mm, "end": v(38.87, 24.87) * mm});
            skLineSegment(sketch, "E9809", {"start": v(38.87, 24.87) * mm, "end": v(38.3, 24.94) * mm});
            skLineSegment(sketch, "E9810", {"start": v(38.3, 24.94) * mm, "end": v(37.75, 25.03) * mm});
            skLineSegment(sketch, "E9811", {"start": v(37.75, 25.03) * mm, "end": v(37.14, 25.14) * mm});
            skLineSegment(sketch, "E9812", {"start": v(37.14, 25.14) * mm, "end": v(35.98, 25.38) * mm});
            skLineSegment(sketch, "E9813", {"start": v(35.98, 25.38) * mm, "end": v(34.21, 25.73) * mm});
            skLineSegment(sketch, "E9814", {"start": v(34.21, 25.73) * mm, "end": v(33.21, 25.94) * mm});
            skLineSegment(sketch, "E9815", {"start": v(33.21, 25.94) * mm, "end": v(32.76, 26.05) * mm});
            skLineSegment(sketch, "E9816", {"start": v(32.76, 26.05) * mm, "end": v(32.12, 24.26) * mm});
            skLineSegment(sketch, "E9817", {"start": v(32.12, 24.26) * mm, "end": v(31.9, 23.56) * mm});
            skLineSegment(sketch, "E9818", {"start": v(25.32, 7.26) * mm, "end": v(25.64, 6.8) * mm});
            skLineSegment(sketch, "E9819", {"start": v(25.64, 6.8) * mm, "end": v(25.99, 6.3) * mm});
            skLineSegment(sketch, "E9820", {"start": v(25.99, 6.3) * mm, "end": v(26.16, 6.07) * mm});
            skLineSegment(sketch, "E9821", {"start": v(26.16, 6.07) * mm, "end": v(26.35, 5.84) * mm});
            skLineSegment(sketch, "E9822", {"start": v(26.35, 5.84) * mm, "end": v(26.54, 5.64) * mm});
            skLineSegment(sketch, "E9823", {"start": v(26.54, 5.64) * mm, "end": v(26.73, 5.46) * mm});
            skLineSegment(sketch, "E9824", {"start": v(26.73, 5.46) * mm, "end": v(26.89, 5.34) * mm});
            skLineSegment(sketch, "E9825", {"start": v(26.89, 5.34) * mm, "end": v(27.06, 5.24) * mm});
            skLineSegment(sketch, "E9826", {"start": v(27.06, 5.24) * mm, "end": v(27.45, 5.05) * mm});
            skLineSegment(sketch, "E9827", {"start": v(27.45, 5.05) * mm, "end": v(27.85, 4.88) * mm});
            skLineSegment(sketch, "E9828", {"start": v(27.85, 4.88) * mm, "end": v(28.22, 4.71) * mm});
            skLineSegment(sketch, "E9829", {"start": v(28.22, 4.71) * mm, "end": v(28.57, 4.54) * mm});
            skLineSegment(sketch, "E9830", {"start": v(28.57, 4.54) * mm, "end": v(28.94, 4.38) * mm});
            skLineSegment(sketch, "E9831", {"start": v(28.94, 4.38) * mm, "end": v(29.33, 4.23) * mm});
            skLineSegment(sketch, "E9832", {"start": v(29.33, 4.23) * mm, "end": v(29.74, 4.08) * mm});
            skLineSegment(sketch, "E9833", {"start": v(29.74, 4.08) * mm, "end": v(30.16, 3.95) * mm});
            skLineSegment(sketch, "E9834", {"start": v(30.16, 3.95) * mm, "end": v(30.59, 3.82) * mm});
            skLineSegment(sketch, "E9835", {"start": v(30.59, 3.82) * mm, "end": v(31.03, 3.7) * mm});
            skLineSegment(sketch, "E9836", {"start": v(31.03, 3.7) * mm, "end": v(31.48, 3.6) * mm});
            skLineSegment(sketch, "E9837", {"start": v(31.48, 3.6) * mm, "end": v(31.93, 3.5) * mm});
            skLineSegment(sketch, "E9838", {"start": v(31.93, 3.5) * mm, "end": v(32.39, 3.42) * mm});
            skLineSegment(sketch, "E9839", {"start": v(32.39, 3.42) * mm, "end": v(32.85, 3.34) * mm});
            skLineSegment(sketch, "E9840", {"start": v(32.85, 3.34) * mm, "end": v(33.31, 3.28) * mm});
            skLineSegment(sketch, "E9841", {"start": v(33.31, 3.28) * mm, "end": v(33.78, 3.23) * mm});
            skLineSegment(sketch, "E9842", {"start": v(33.78, 3.23) * mm, "end": v(34.24, 3.2) * mm});
            skLineSegment(sketch, "E9843", {"start": v(34.24, 3.2) * mm, "end": v(34.7, 3.17) * mm});
            skLineSegment(sketch, "E9844", {"start": v(34.7, 3.17) * mm, "end": v(35.15, 3.16) * mm});
            skLineSegment(sketch, "E9845", {"start": v(35.15, 3.16) * mm, "end": v(36.96, 3.14) * mm});
            skLineSegment(sketch, "E9846", {"start": v(36.96, 3.14) * mm, "end": v(38.07, 3.99) * mm});
            skLineSegment(sketch, "E9847", {"start": v(38.07, 3.99) * mm, "end": v(38.5, 5.71) * mm});
            skLineSegment(sketch, "E9848", {"start": v(38.5, 5.71) * mm, "end": v(38.07, 7.08) * mm});
            skLineSegment(sketch, "E9849", {"start": v(38.07, 7.08) * mm, "end": v(36.7, 7.08) * mm});
            skLineSegment(sketch, "E9850", {"start": v(36.7, 7.08) * mm, "end": v(36.37, 7.1) * mm});
            skLineSegment(sketch, "E9851", {"start": v(36.37, 7.1) * mm, "end": v(36, 7.12) * mm});
            skLineSegment(sketch, "E9852", {"start": v(36, 7.12) * mm, "end": v(35.57, 7.17) * mm});
            skLineSegment(sketch, "E9853", {"start": v(35.57, 7.17) * mm, "end": v(35.1, 7.23) * mm});
            skLineSegment(sketch, "E9854", {"start": v(35.1, 7.23) * mm, "end": v(34.63, 7.3) * mm});
            skLineSegment(sketch, "E9855", {"start": v(34.63, 7.3) * mm, "end": v(34.16, 7.39) * mm});
            skLineSegment(sketch, "E9856", {"start": v(34.16, 7.39) * mm, "end": v(33.69, 7.48) * mm});
            skLineSegment(sketch, "E9857", {"start": v(33.69, 7.48) * mm, "end": v(33.24, 7.58) * mm});
            skLineSegment(sketch, "E9858", {"start": v(33.24, 7.58) * mm, "end": v(32.74, 7.68) * mm});
            skLineSegment(sketch, "E9859", {"start": v(32.74, 7.68) * mm, "end": v(32.2, 7.8) * mm});
            skLineSegment(sketch, "E9860", {"start": v(32.2, 7.8) * mm, "end": v(31.66, 7.92) * mm});
            skLineSegment(sketch, "E9861", {"start": v(31.66, 7.92) * mm, "end": v(31.4, 7.99) * mm});
            skLineSegment(sketch, "E9862", {"start": v(31.4, 7.99) * mm, "end": v(31.17, 8.06) * mm});
            skLineSegment(sketch, "E9863", {"start": v(31.17, 8.06) * mm, "end": v(30.98, 8.14) * mm});
            skLineSegment(sketch, "E9864", {"start": v(30.98, 8.14) * mm, "end": v(30.77, 8.24) * mm});
            skLineSegment(sketch, "E9865", {"start": v(30.77, 8.24) * mm, "end": v(30.35, 8.45) * mm});
            skLineSegment(sketch, "E9866", {"start": v(30.35, 8.45) * mm, "end": v(29.94, 8.68) * mm});
            skLineSegment(sketch, "E9867", {"start": v(29.94, 8.68) * mm, "end": v(29.55, 8.89) * mm});
            skLineSegment(sketch, "E9868", {"start": v(29.55, 8.89) * mm, "end": v(29.22, 9.06) * mm});
            skLineSegment(sketch, "E9869", {"start": v(29.22, 9.06) * mm, "end": v(28.9, 9.23) * mm});
            skLineSegment(sketch, "E9870", {"start": v(28.9, 9.23) * mm, "end": v(28.61, 9.4) * mm});
            skLineSegment(sketch, "E9871", {"start": v(28.61, 9.4) * mm, "end": v(28.35, 9.56) * mm});
            skLineSegment(sketch, "E9872", {"start": v(28.35, 9.56) * mm, "end": v(28.12, 9.71) * mm});
            skLineSegment(sketch, "E9873", {"start": v(28.12, 9.71) * mm, "end": v(27.93, 9.85) * mm});
            skLineSegment(sketch, "E9874", {"start": v(27.93, 9.85) * mm, "end": v(27.8, 9.96) * mm});
            skLineSegment(sketch, "E9875", {"start": v(27.8, 9.96) * mm, "end": v(27.73, 10.04) * mm});
            skLineSegment(sketch, "E9876", {"start": v(27.73, 10.04) * mm, "end": v(27.65, 10.15) * mm});
            skLineSegment(sketch, "E9877", {"start": v(27.65, 10.15) * mm, "end": v(27.58, 10.23) * mm});
            skLineSegment(sketch, "E9878", {"start": v(27.58, 10.23) * mm, "end": v(27.5, 10.3) * mm});
            skLineSegment(sketch, "E9879", {"start": v(27.5, 10.3) * mm, "end": v(27.43, 10.34) * mm});
            skLineSegment(sketch, "E9880", {"start": v(27.43, 10.34) * mm, "end": v(27.35, 10.35) * mm});
            skLineSegment(sketch, "E9881", {"start": v(27.35, 10.35) * mm, "end": v(27.27, 10.34) * mm});
            skLineSegment(sketch, "E9882", {"start": v(27.27, 10.34) * mm, "end": v(27.18, 10.31) * mm});
            skLineSegment(sketch, "E9883", {"start": v(27.18, 10.31) * mm, "end": v(27.1, 10.26) * mm});
            skLineSegment(sketch, "E9884", {"start": v(27.1, 10.26) * mm, "end": v(27, 10.18) * mm});
            skLineSegment(sketch, "E9885", {"start": v(27, 10.18) * mm, "end": v(26.9, 10.07) * mm});
            skLineSegment(sketch, "E9886", {"start": v(26.9, 10.07) * mm, "end": v(26.78, 9.94) * mm});
            skLineSegment(sketch, "E9887", {"start": v(26.78, 9.94) * mm, "end": v(26.66, 9.78) * mm});
            skLineSegment(sketch, "E9888", {"start": v(26.66, 9.78) * mm, "end": v(26.4, 9.37) * mm});
            skLineSegment(sketch, "E9889", {"start": v(26.4, 9.37) * mm, "end": v(26.1, 8.86) * mm});
            skLineSegment(sketch, "E9890", {"start": v(26.1, 8.86) * mm, "end": v(25.83, 8.37) * mm});
            skLineSegment(sketch, "E9891", {"start": v(25.83, 8.37) * mm, "end": v(25.5, 7.65) * mm});
            skLineSegment(sketch, "E9892", {"start": v(25.5, 7.65) * mm, "end": v(25.32, 7.26) * mm});
            skLineSegment(sketch, "E9893", {"start": v(23.6, 4.3) * mm, "end": v(23.96, 3.9) * mm});
            skLineSegment(sketch, "E9894", {"start": v(23.96, 3.9) * mm, "end": v(24.32, 3.5) * mm});
            skLineSegment(sketch, "E9895", {"start": v(24.32, 3.5) * mm, "end": v(24.7, 3.06) * mm});
            skLineSegment(sketch, "E9896", {"start": v(24.7, 3.06) * mm, "end": v(25.09, 2.62) * mm});
            skLineSegment(sketch, "E9897", {"start": v(25.09, 2.62) * mm, "end": v(25.48, 2.2) * mm});
            skLineSegment(sketch, "E9898", {"start": v(25.48, 2.2) * mm, "end": v(25.88, 1.8) * mm});
            skLineSegment(sketch, "E9899", {"start": v(25.88, 1.8) * mm, "end": v(26.09, 1.62) * mm});
            skLineSegment(sketch, "E9900", {"start": v(26.09, 1.62) * mm, "end": v(26.3, 1.44) * mm});
            skLineSegment(sketch, "E9901", {"start": v(26.3, 1.44) * mm, "end": v(26.5, 1.29) * mm});
            skLineSegment(sketch, "E9902", {"start": v(26.5, 1.29) * mm, "end": v(26.7, 1.14) * mm});
            skLineSegment(sketch, "E9903", {"start": v(26.7, 1.14) * mm, "end": v(26.85, 1.06) * mm});
            skLineSegment(sketch, "E9904", {"start": v(26.85, 1.06) * mm, "end": v(27.02, 0.98) * mm});
            skLineSegment(sketch, "E9905", {"start": v(27.02, 0.98) * mm, "end": v(27.38, 0.85) * mm});
            skLineSegment(sketch, "E9906", {"start": v(27.38, 0.85) * mm, "end": v(27.75, 0.73) * mm});
            skLineSegment(sketch, "E9907", {"start": v(27.75, 0.73) * mm, "end": v(28.09, 0.61) * mm});
            skLineSegment(sketch, "E9908", {"start": v(28.09, 0.61) * mm, "end": v(28.36, 0.52) * mm});
            skLineSegment(sketch, "E9909", {"start": v(28.36, 0.52) * mm, "end": v(28.66, 0.42) * mm});
            skLineSegment(sketch, "E9910", {"start": v(28.66, 0.42) * mm, "end": v(28.98, 0.33) * mm});
            skLineSegment(sketch, "E9911", {"start": v(28.98, 0.33) * mm, "end": v(29.32, 0.23) * mm});
            skLineSegment(sketch, "E9912", {"start": v(29.32, 0.23) * mm, "end": v(30.06, 0.06) * mm});
            skLineSegment(sketch, "E9913", {"start": v(30.06, 0.06) * mm, "end": v(30.85, -0.1) * mm});
            skLineSegment(sketch, "E9914", {"start": v(30.85, -0.1) * mm, "end": v(31.66, -0.23) * mm});
            skLineSegment(sketch, "E9915", {"start": v(31.66, -0.23) * mm, "end": v(32.47, -0.34) * mm});
            skLineSegment(sketch, "E9916", {"start": v(32.47, -0.34) * mm, "end": v(33.27, -0.42) * mm});
            skLineSegment(sketch, "E9917", {"start": v(33.27, -0.42) * mm, "end": v(33.65, -0.45) * mm});
            skLineSegment(sketch, "E9918", {"start": v(33.65, -0.45) * mm, "end": v(34.02, -0.47) * mm});
            skLineSegment(sketch, "E9919", {"start": v(34.02, -0.47) * mm, "end": v(35.04, -0.51) * mm});
            skLineSegment(sketch, "E9920", {"start": v(35.04, -0.51) * mm, "end": v(36.14, 0.7) * mm});
            skLineSegment(sketch, "E9921", {"start": v(36.14, 0.7) * mm, "end": v(36.14, 2.7) * mm});
            skLineSegment(sketch, "E9922", {"start": v(36.14, 2.7) * mm, "end": v(35.58, 2.73) * mm});
            skLineSegment(sketch, "E9923", {"start": v(35.58, 2.73) * mm, "end": v(34.98, 2.75) * mm});
            skLineSegment(sketch, "E9924", {"start": v(34.98, 2.75) * mm, "end": v(33.73, 2.8) * mm});
            skLineSegment(sketch, "E9925", {"start": v(33.73, 2.8) * mm, "end": v(33.1, 2.84) * mm});
            skLineSegment(sketch, "E9926", {"start": v(33.1, 2.84) * mm, "end": v(32.5, 2.89) * mm});
            skLineSegment(sketch, "E9927", {"start": v(32.5, 2.89) * mm, "end": v(31.9, 2.96) * mm});
            skLineSegment(sketch, "E9928", {"start": v(31.9, 2.96) * mm, "end": v(31.62, 3) * mm});
            skLineSegment(sketch, "E9929", {"start": v(31.62, 3) * mm, "end": v(31.35, 3.06) * mm});
            skLineSegment(sketch, "E9930", {"start": v(31.35, 3.06) * mm, "end": v(30.9, 3.17) * mm});
            skLineSegment(sketch, "E9931", {"start": v(30.9, 3.17) * mm, "end": v(30.43, 3.3) * mm});
            skLineSegment(sketch, "E9932", {"start": v(30.43, 3.3) * mm, "end": v(29.95, 3.45) * mm});
            skLineSegment(sketch, "E9933", {"start": v(29.95, 3.45) * mm, "end": v(29.46, 3.62) * mm});
            skLineSegment(sketch, "E9934", {"start": v(29.46, 3.62) * mm, "end": v(28.98, 3.81) * mm});
            skLineSegment(sketch, "E9935", {"start": v(28.98, 3.81) * mm, "end": v(28.51, 4.01) * mm});
            skLineSegment(sketch, "E9936", {"start": v(28.51, 4.01) * mm, "end": v(28.07, 4.22) * mm});
            skLineSegment(sketch, "E9937", {"start": v(28.07, 4.22) * mm, "end": v(27.67, 4.44) * mm});
            skLineSegment(sketch, "E9938", {"start": v(27.67, 4.44) * mm, "end": v(27.5, 4.55) * mm});
            skLineSegment(sketch, "E9939", {"start": v(27.5, 4.55) * mm, "end": v(27.33, 4.66) * mm});
            skLineSegment(sketch, "E9940", {"start": v(27.33, 4.66) * mm, "end": v(27, 4.92) * mm});
            skLineSegment(sketch, "E9941", {"start": v(27, 4.92) * mm, "end": v(26.66, 5.2) * mm});
            skLineSegment(sketch, "E9942", {"start": v(26.66, 5.2) * mm, "end": v(26.32, 5.5) * mm});
            skLineSegment(sketch, "E9943", {"start": v(26.32, 5.5) * mm, "end": v(25.66, 6.12) * mm});
            skLineSegment(sketch, "E9944", {"start": v(25.66, 6.12) * mm, "end": v(25.35, 6.42) * mm});
            skLineSegment(sketch, "E9945", {"start": v(25.35, 6.42) * mm, "end": v(25.04, 6.7) * mm});
            skLineSegment(sketch, "E9946", {"start": v(25.04, 6.7) * mm, "end": v(25, 6.6) * mm});
            skLineSegment(sketch, "E9947", {"start": v(25, 6.6) * mm, "end": v(24.73, 6.1) * mm});
            skLineSegment(sketch, "E9948", {"start": v(24.73, 6.1) * mm, "end": v(24.46, 5.63) * mm});
            skLineSegment(sketch, "E9949", {"start": v(24.46, 5.63) * mm, "end": v(24, 4.9) * mm});
            skLineSegment(sketch, "E9950", {"start": v(24, 4.9) * mm, "end": v(23.6, 4.3) * mm});
            skLineSegment(sketch, "E9951", {"start": v(21.25, 1.13) * mm, "end": v(21.45, 0.8) * mm});
            skLineSegment(sketch, "E9952", {"start": v(21.45, 0.8) * mm, "end": v(21.55, 0.64) * mm});
            skLineSegment(sketch, "E9953", {"start": v(21.55, 0.64) * mm, "end": v(21.65, 0.49) * mm});
            skLineSegment(sketch, "E9954", {"start": v(21.65, 0.49) * mm, "end": v(22, 0.04) * mm});
            skLineSegment(sketch, "E9955", {"start": v(22, 0.04) * mm, "end": v(22.38, -0.43) * mm});
            skLineSegment(sketch, "E9956", {"start": v(22.38, -0.43) * mm, "end": v(22.78, -0.9) * mm});
            skLineSegment(sketch, "E9957", {"start": v(22.78, -0.9) * mm, "end": v(23.2, -1.39) * mm});
            skLineSegment(sketch, "E9958", {"start": v(23.2, -1.39) * mm, "end": v(23.64, -1.85) * mm});
            skLineSegment(sketch, "E9959", {"start": v(23.64, -1.85) * mm, "end": v(24.08, -2.3) * mm});
            skLineSegment(sketch, "E9960", {"start": v(24.08, -2.3) * mm, "end": v(24.5, -2.72) * mm});
            skLineSegment(sketch, "E9961", {"start": v(24.5, -2.72) * mm, "end": v(24.93, -3.1) * mm});
            skLineSegment(sketch, "E9962", {"start": v(24.93, -3.1) * mm, "end": v(25.11, -3.26) * mm});
            skLineSegment(sketch, "E9963", {"start": v(25.11, -3.26) * mm, "end": v(25.31, -3.41) * mm});
            skLineSegment(sketch, "E9964", {"start": v(25.31, -3.41) * mm, "end": v(25.52, -3.56) * mm});
            skLineSegment(sketch, "E9965", {"start": v(25.52, -3.56) * mm, "end": v(25.74, -3.7) * mm});
            skLineSegment(sketch, "E9966", {"start": v(25.74, -3.7) * mm, "end": v(25.98, -3.84) * mm});
            skLineSegment(sketch, "E9967", {"start": v(25.98, -3.84) * mm, "end": v(26.22, -3.97) * mm});
            skLineSegment(sketch, "E9968", {"start": v(26.22, -3.97) * mm, "end": v(26.71, -4.22) * mm});
            skLineSegment(sketch, "E9969", {"start": v(26.71, -4.22) * mm, "end": v(27.22, -4.45) * mm});
            skLineSegment(sketch, "E9970", {"start": v(27.22, -4.45) * mm, "end": v(27.73, -4.65) * mm});
            skLineSegment(sketch, "E9971", {"start": v(27.73, -4.65) * mm, "end": v(28.23, -4.82) * mm});
            skLineSegment(sketch, "E9972", {"start": v(28.23, -4.82) * mm, "end": v(28.7, -4.95) * mm});
            skLineSegment(sketch, "E9973", {"start": v(28.7, -4.95) * mm, "end": v(28.94, -5) * mm});
            skLineSegment(sketch, "E9974", {"start": v(28.94, -5) * mm, "end": v(29.2, -5.05) * mm});
            skLineSegment(sketch, "E9975", {"start": v(29.2, -5.05) * mm, "end": v(29.45, -5.09) * mm});
            skLineSegment(sketch, "E9976", {"start": v(29.45, -5.09) * mm, "end": v(29.72, -5.11) * mm});
            skLineSegment(sketch, "E9977", {"start": v(29.72, -5.11) * mm, "end": v(30.27, -5.15) * mm});
            skLineSegment(sketch, "E9978", {"start": v(30.27, -5.15) * mm, "end": v(30.84, -5.16) * mm});
            skLineSegment(sketch, "E9979", {"start": v(30.84, -5.16) * mm, "end": v(31.96, -5.16) * mm});
            skLineSegment(sketch, "E9980", {"start": v(31.96, -5.16) * mm, "end": v(32.5, -5.16) * mm});
            skLineSegment(sketch, "E9981", {"start": v(32.5, -5.16) * mm, "end": v(33, -5.18) * mm});
            skLineSegment(sketch, "E9982", {"start": v(33, -5.18) * mm, "end": v(34.24, -4.25) * mm});
            skLineSegment(sketch, "E9983", {"start": v(34.24, -4.25) * mm, "end": v(34.56, -0.97) * mm});
            skLineSegment(sketch, "E9984", {"start": v(34.56, -0.97) * mm, "end": v(33.9, -0.9) * mm});
            skLineSegment(sketch, "E9985", {"start": v(33.9, -0.9) * mm, "end": v(33.2, -0.83) * mm});
            skLineSegment(sketch, "E9986", {"start": v(33.2, -0.83) * mm, "end": v(31.72, -0.7) * mm});
            skLineSegment(sketch, "E9987", {"start": v(31.72, -0.7) * mm, "end": v(30.98, -0.62) * mm});
            skLineSegment(sketch, "E9988", {"start": v(30.98, -0.62) * mm, "end": v(30.61, -0.57) * mm});
            skLineSegment(sketch, "E9989", {"start": v(30.61, -0.57) * mm, "end": v(30.26, -0.52) * mm});
            skLineSegment(sketch, "E9990", {"start": v(30.26, -0.52) * mm, "end": v(29.9, -0.46) * mm});
            skLineSegment(sketch, "E9991", {"start": v(29.9, -0.46) * mm, "end": v(29.57, -0.39) * mm});
            skLineSegment(sketch, "E9992", {"start": v(29.57, -0.39) * mm, "end": v(29.24, -0.3) * mm});
            skLineSegment(sketch, "E9993", {"start": v(29.24, -0.3) * mm, "end": v(28.93, -0.22) * mm});
            skLineSegment(sketch, "E9994", {"start": v(28.93, -0.22) * mm, "end": v(28.53, -0.08) * mm});
            skLineSegment(sketch, "E9995", {"start": v(28.53, -0.08) * mm, "end": v(28.12, 0.08) * mm});
            skLineSegment(sketch, "E9996", {"start": v(28.12, 0.08) * mm, "end": v(27.7, 0.27) * mm});
            skLineSegment(sketch, "E9997", {"start": v(27.7, 0.27) * mm, "end": v(27.27, 0.48) * mm});
            skLineSegment(sketch, "E9998", {"start": v(27.27, 0.48) * mm, "end": v(26.86, 0.7) * mm});
            skLineSegment(sketch, "E9999", {"start": v(26.86, 0.7) * mm, "end": v(26.46, 0.93) * mm});
            skLineSegment(sketch, "E10000", {"start": v(26.46, 0.93) * mm, "end": v(26.08, 1.17) * mm});
            skLineSegment(sketch, "E10001", {"start": v(26.08, 1.17) * mm, "end": v(25.74, 1.41) * mm});
            skLineSegment(sketch, "E10002", {"start": v(25.74, 1.41) * mm, "end": v(25.6, 1.53) * mm});
            skLineSegment(sketch, "E10003", {"start": v(25.6, 1.53) * mm, "end": v(25.45, 1.67) * mm});
            skLineSegment(sketch, "E10004", {"start": v(25.45, 1.67) * mm, "end": v(25.15, 1.98) * mm});
            skLineSegment(sketch, "E10005", {"start": v(25.15, 1.98) * mm, "end": v(24.87, 2.3) * mm});
            skLineSegment(sketch, "E10006", {"start": v(24.87, 2.3) * mm, "end": v(24.6, 2.6) * mm});
            skLineSegment(sketch, "E10007", {"start": v(24.6, 2.6) * mm, "end": v(24.15, 3.06) * mm});
            skLineSegment(sketch, "E10008", {"start": v(24.15, 3.06) * mm, "end": v(23.74, 3.43) * mm});
            skLineSegment(sketch, "E10009", {"start": v(23.74, 3.43) * mm, "end": v(23.57, 3.58) * mm});
            skLineSegment(sketch, "E10010", {"start": v(23.57, 3.58) * mm, "end": v(23.42, 3.69) * mm});
            skLineSegment(sketch, "E10011", {"start": v(23.42, 3.69) * mm, "end": v(23.32, 3.76) * mm});
            skLineSegment(sketch, "E10012", {"start": v(23.32, 3.76) * mm, "end": v(23.28, 3.77) * mm});
            skLineSegment(sketch, "E10013", {"start": v(23.28, 3.77) * mm, "end": v(23.25, 3.78) * mm});
            skLineSegment(sketch, "E10014", {"start": v(23.25, 3.78) * mm, "end": v(23.25, 3.78) * mm});
            skLineSegment(sketch, "E10015", {"start": v(23.25, 3.78) * mm, "end": v(22.95, 3.36) * mm});
            skLineSegment(sketch, "E10016", {"start": v(22.95, 3.36) * mm, "end": v(22.39, 2.57) * mm});
            skLineSegment(sketch, "E10017", {"start": v(22.39, 2.57) * mm, "end": v(21.8, 1.8) * mm});
            skLineSegment(sketch, "E10018", {"start": v(21.8, 1.8) * mm, "end": v(21.25, 1.13) * mm});
            skLineSegment(sketch, "E10019", {"start": v(38, 36.67) * mm, "end": v(37.89, 36.13) * mm});
            skLineSegment(sketch, "E10020", {"start": v(37.89, 36.13) * mm, "end": v(37.73, 35.57) * mm});
            skLineSegment(sketch, "E10021", {"start": v(37.73, 35.57) * mm, "end": v(37.55, 35.05) * mm});
            skLineSegment(sketch, "E10022", {"start": v(37.55, 35.05) * mm, "end": v(37.45, 34.82) * mm});
            skLineSegment(sketch, "E10023", {"start": v(37.45, 34.82) * mm, "end": v(37.35, 34.62) * mm});
            skLineSegment(sketch, "E10024", {"start": v(37.35, 34.62) * mm, "end": v(36.94, 33.86) * mm});
            skArc(sketch, "E10025", {"start": v(36.94, 33.86) * mm, "mid": v(36.82, 33.7) * mm, "end": v(36.64, 33.6) * mm});
            skLineSegment(sketch, "E10026", {"start": v(36.64, 33.6) * mm, "end": v(36.56, 33.57) * mm});
            skLineSegment(sketch, "E10027", {"start": v(36.56, 33.57) * mm, "end": v(36.5, 33.44) * mm});
            skLineSegment(sketch, "E10028", {"start": v(36.5, 33.44) * mm, "end": v(36.47, 33.39) * mm});
            skLineSegment(sketch, "E10029", {"start": v(36.47, 33.39) * mm, "end": v(36.47, 33.36) * mm});
            skLineSegment(sketch, "E10030", {"start": v(36.47, 33.36) * mm, "end": v(36.48, 33.34) * mm});
            skLineSegment(sketch, "E10031", {"start": v(36.48, 33.34) * mm, "end": v(36.53, 33.32) * mm});
            skLineSegment(sketch, "E10032", {"start": v(36.53, 33.32) * mm, "end": v(36.7, 33.28) * mm});
            skLineSegment(sketch, "E10033", {"start": v(36.7, 33.28) * mm, "end": v(36.96, 33.23) * mm});
            skLineSegment(sketch, "E10034", {"start": v(36.96, 33.23) * mm, "end": v(37.31, 33.2) * mm});
            skLineSegment(sketch, "E10035", {"start": v(37.31, 33.2) * mm, "end": v(37.74, 33.16) * mm});
            skLineSegment(sketch, "E10036", {"start": v(37.74, 33.16) * mm, "end": v(38.23, 33.12) * mm});
            skLineSegment(sketch, "E10037", {"start": v(38.23, 33.12) * mm, "end": v(38.77, 33.09) * mm});
            skLineSegment(sketch, "E10038", {"start": v(38.77, 33.09) * mm, "end": v(39.35, 33.06) * mm});
            skLineSegment(sketch, "E10039", {"start": v(39.35, 33.06) * mm, "end": v(41.54, 32.97) * mm});
            skLineSegment(sketch, "E10040", {"start": v(41.54, 32.97) * mm, "end": v(42.41, 32.93) * mm});
            skLineSegment(sketch, "E10041", {"start": v(42.41, 32.93) * mm, "end": v(43.08, 32.91) * mm});
            skLineSegment(sketch, "E10042", {"start": v(43.08, 32.91) * mm, "end": v(43.33, 32.88) * mm});
            skLineSegment(sketch, "E10043", {"start": v(43.33, 32.88) * mm, "end": v(43.79, 32.8) * mm});
            skLineSegment(sketch, "E10044", {"start": v(43.79, 32.8) * mm, "end": v(44.05, 32.77) * mm});
            skLineSegment(sketch, "E10045", {"start": v(44.05, 32.77) * mm, "end": v(44.3, 32.74) * mm});
            skLineSegment(sketch, "E10046", {"start": v(44.3, 32.74) * mm, "end": v(44.53, 32.73) * mm});
            skLineSegment(sketch, "E10047", {"start": v(44.53, 32.73) * mm, "end": v(44.71, 32.74) * mm});
            skLineSegment(sketch, "E10048", {"start": v(44.71, 32.74) * mm, "end": v(44.4, 32.95) * mm});
            skLineSegment(sketch, "E10049", {"start": v(44.4, 32.95) * mm, "end": v(43.85, 33.36) * mm});
            skLineSegment(sketch, "E10050", {"start": v(43.85, 33.36) * mm, "end": v(43.33, 33.78) * mm});
            skLineSegment(sketch, "E10051", {"start": v(43.33, 33.78) * mm, "end": v(42.86, 34.18) * mm});
            skLineSegment(sketch, "E10052", {"start": v(42.86, 34.18) * mm, "end": v(42.43, 34.57) * mm});
            skLineSegment(sketch, "E10053", {"start": v(42.43, 34.57) * mm, "end": v(42.01, 35) * mm});
            skLineSegment(sketch, "E10054", {"start": v(42.01, 35) * mm, "end": v(41.6, 35.43) * mm});
            skLineSegment(sketch, "E10055", {"start": v(41.6, 35.43) * mm, "end": v(41.19, 35.9) * mm});
            skLineSegment(sketch, "E10056", {"start": v(41.19, 35.9) * mm, "end": v(40.4, 36.82) * mm});
            skLineSegment(sketch, "E10057", {"start": v(40.4, 36.82) * mm, "end": v(39.64, 37.78) * mm});
            skLineSegment(sketch, "E10058", {"start": v(39.64, 37.78) * mm, "end": v(39.43, 38.05) * mm});
            skLineSegment(sketch, "E10059", {"start": v(39.43, 38.05) * mm, "end": v(39.24, 38.34) * mm});
            skLineSegment(sketch, "E10060", {"start": v(39.24, 38.34) * mm, "end": v(39.15, 38.48) * mm});
            skLineSegment(sketch, "E10061", {"start": v(39.15, 38.48) * mm, "end": v(39.08, 38.48) * mm});
            skLineSegment(sketch, "E10062", {"start": v(39.08, 38.48) * mm, "end": v(39, 38.47) * mm});
            skLineSegment(sketch, "E10063", {"start": v(39, 38.47) * mm, "end": v(38.92, 38.44) * mm});
            skLineSegment(sketch, "E10064", {"start": v(38.92, 38.44) * mm, "end": v(38.85, 38.4) * mm});
            skLineSegment(sketch, "E10065", {"start": v(38.85, 38.4) * mm, "end": v(38.78, 38.35) * mm});
            skLineSegment(sketch, "E10066", {"start": v(38.78, 38.35) * mm, "end": v(38.72, 38.3) * mm});
            skLineSegment(sketch, "E10067", {"start": v(38.72, 38.3) * mm, "end": v(38.65, 38.22) * mm});
            skLineSegment(sketch, "E10068", {"start": v(38.65, 38.22) * mm, "end": v(38.54, 38.07) * mm});
            skLineSegment(sketch, "E10069", {"start": v(38.54, 38.07) * mm, "end": v(38.43, 37.9) * mm});
            skLineSegment(sketch, "E10070", {"start": v(38.43, 37.9) * mm, "end": v(38.34, 37.72) * mm});
            skLineSegment(sketch, "E10071", {"start": v(38.34, 37.72) * mm, "end": v(38.18, 37.39) * mm});
            skLineSegment(sketch, "E10072", {"start": v(38.18, 37.39) * mm, "end": v(38.12, 37.23) * mm});
            skLineSegment(sketch, "E10073", {"start": v(38.12, 37.23) * mm, "end": v(38.07, 37.07) * mm});
            skLineSegment(sketch, "E10074", {"start": v(38.07, 37.07) * mm, "end": v(38.04, 36.9) * mm});
            skLineSegment(sketch, "E10075", {"start": v(38.04, 36.9) * mm, "end": v(38, 36.73) * mm});
            skLineSegment(sketch, "E10076", {"start": v(38, 36.73) * mm, "end": v(38, 36.67) * mm});
            skLineSegment(sketch, "E10077", {"start": v(-80.36, 23.75) * mm, "end": v(-80.15, 23.96) * mm});
            skLineSegment(sketch, "E10078", {"start": v(-80.15, 23.96) * mm, "end": v(-80.07, 24.04) * mm});
            skLineSegment(sketch, "E10079", {"start": v(-80.07, 24.04) * mm, "end": v(-80.01, 24.12) * mm});
            skLineSegment(sketch, "E10080", {"start": v(-80.01, 24.12) * mm, "end": v(-80, 24.13) * mm});
            skLineSegment(sketch, "E10081", {"start": v(-80, 24.13) * mm, "end": v(-80, 24.13) * mm});
            skLineSegment(sketch, "E10082", {"start": v(-80, 24.13) * mm, "end": v(-79.97, 24.23) * mm});
            skLineSegment(sketch, "E10083", {"start": v(-79.97, 24.23) * mm, "end": v(-79.92, 24.6) * mm});
            skLineSegment(sketch, "E10084", {"start": v(-79.92, 24.6) * mm, "end": v(-79.81, 25.6) * mm});
            skLineSegment(sketch, "E10085", {"start": v(-79.81, 25.6) * mm, "end": v(-79.73, 26.23) * mm});
            skLineSegment(sketch, "E10086", {"start": v(-79.73, 26.23) * mm, "end": v(-79.65, 26.84) * mm});
            skLineSegment(sketch, "E10087", {"start": v(-79.65, 26.84) * mm, "end": v(-79.52, 27.52) * mm});
            skLineSegment(sketch, "E10088", {"start": v(-79.52, 27.52) * mm, "end": v(-79.36, 28.25) * mm});
            skLineSegment(sketch, "E10089", {"start": v(-79.36, 28.25) * mm, "end": v(-79.17, 29.01) * mm});
            skLineSegment(sketch, "E10090", {"start": v(-79.17, 29.01) * mm, "end": v(-79.03, 29.5) * mm});
            skLineSegment(sketch, "E10091", {"start": v(-79.03, 29.5) * mm, "end": v(-78.96, 29.8) * mm});
            skLineSegment(sketch, "E10092", {"start": v(-78.96, 29.8) * mm, "end": v(-78.88, 30.1) * mm});
            skLineSegment(sketch, "E10093", {"start": v(-78.88, 30.1) * mm, "end": v(-78.54, 31.14) * mm});
            skLineSegment(sketch, "E10094", {"start": v(-78.54, 31.14) * mm, "end": v(-78.42, 31.5) * mm});
            skLineSegment(sketch, "E10095", {"start": v(-78.42, 31.5) * mm, "end": v(-78.36, 31.69) * mm});
            skLineSegment(sketch, "E10096", {"start": v(-78.36, 31.69) * mm, "end": v(-78.27, 31.86) * mm});
            skLineSegment(sketch, "E10097", {"start": v(-78.27, 31.86) * mm, "end": v(-79, 32.36) * mm});
            skLineSegment(sketch, "E10098", {"start": v(-79, 32.36) * mm, "end": v(-79.75, 32.89) * mm});
            skLineSegment(sketch, "E10099", {"start": v(-79.75, 32.89) * mm, "end": v(-80.5, 33.44) * mm});
            skLineSegment(sketch, "E10100", {"start": v(-80.5, 33.44) * mm, "end": v(-81.25, 34) * mm});
            skLineSegment(sketch, "E10101", {"start": v(-81.25, 34) * mm, "end": v(-82.01, 34.6) * mm});
            skLineSegment(sketch, "E10102", {"start": v(-82.01, 34.6) * mm, "end": v(-82.77, 35.2) * mm});
            skLineSegment(sketch, "E10103", {"start": v(-82.77, 35.2) * mm, "end": v(-83.53, 35.82) * mm});
            skLineSegment(sketch, "E10104", {"start": v(-83.53, 35.82) * mm, "end": v(-84.27, 36.45) * mm});
            skLineSegment(sketch, "E10105", {"start": v(-84.27, 36.45) * mm, "end": v(-85.01, 37.09) * mm});
            skLineSegment(sketch, "E10106", {"start": v(-85.01, 37.09) * mm, "end": v(-85.74, 37.73) * mm});
            skLineSegment(sketch, "E10107", {"start": v(-85.74, 37.73) * mm, "end": v(-86.45, 38.38) * mm});
            skLineSegment(sketch, "E10108", {"start": v(-86.45, 38.38) * mm, "end": v(-87.14, 39.03) * mm});
            skLineSegment(sketch, "E10109", {"start": v(-87.14, 39.03) * mm, "end": v(-87.81, 39.68) * mm});
            skLineSegment(sketch, "E10110", {"start": v(-87.81, 39.68) * mm, "end": v(-88.46, 40.33) * mm});
            skLineSegment(sketch, "E10111", {"start": v(-88.46, 40.33) * mm, "end": v(-89.08, 40.97) * mm});
            skLineSegment(sketch, "E10112", {"start": v(-89.08, 40.97) * mm, "end": v(-89.66, 41.6) * mm});
            skLineSegment(sketch, "E10113", {"start": v(-89.66, 41.6) * mm, "end": v(-89.78, 41.69) * mm});
            skLineSegment(sketch, "E10114", {"start": v(-89.78, 41.69) * mm, "end": v(-89.84, 41.73) * mm});
            skLineSegment(sketch, "E10115", {"start": v(-89.84, 41.73) * mm, "end": v(-90.02, 41.79) * mm});
            skLineSegment(sketch, "E10116", {"start": v(-90.02, 41.79) * mm, "end": v(-90.21, 41.84) * mm});
            skLineSegment(sketch, "E10117", {"start": v(-90.21, 41.84) * mm, "end": v(-90.4, 41.88) * mm});
            skLineSegment(sketch, "E10118", {"start": v(-90.4, 41.88) * mm, "end": v(-90.61, 41.92) * mm});
            skLineSegment(sketch, "E10119", {"start": v(-90.61, 41.92) * mm, "end": v(-90.83, 41.95) * mm});
            skLineSegment(sketch, "E10120", {"start": v(-90.83, 41.95) * mm, "end": v(-91.04, 41.98) * mm});
            skLineSegment(sketch, "E10121", {"start": v(-91.04, 41.98) * mm, "end": v(-91.26, 42) * mm});
            skLineSegment(sketch, "E10122", {"start": v(-91.26, 42) * mm, "end": v(-91.48, 42) * mm});
            skLineSegment(sketch, "E10123", {"start": v(-91.48, 42) * mm, "end": v(-91.7, 42) * mm});
            skLineSegment(sketch, "E10124", {"start": v(-91.7, 42) * mm, "end": v(-91.92, 41.99) * mm});
            skLineSegment(sketch, "E10125", {"start": v(-91.92, 41.99) * mm, "end": v(-92.13, 41.97) * mm});
            skLineSegment(sketch, "E10126", {"start": v(-92.13, 41.97) * mm, "end": v(-92.34, 41.94) * mm});
            skLineSegment(sketch, "E10127", {"start": v(-92.34, 41.94) * mm, "end": v(-92.55, 41.9) * mm});
            skLineSegment(sketch, "E10128", {"start": v(-92.55, 41.9) * mm, "end": v(-92.74, 41.85) * mm});
            skLineSegment(sketch, "E10129", {"start": v(-92.74, 41.85) * mm, "end": v(-92.93, 41.8) * mm});
            skLineSegment(sketch, "E10130", {"start": v(-92.93, 41.8) * mm, "end": v(-93.1, 41.73) * mm});
            skLineSegment(sketch, "E10131", {"start": v(-93.1, 41.73) * mm, "end": v(-93.2, 41.68) * mm});
            skLineSegment(sketch, "E10132", {"start": v(-93.2, 41.68) * mm, "end": v(-93.3, 41.62) * mm});
            skLineSegment(sketch, "E10133", {"start": v(-93.3, 41.62) * mm, "end": v(-93.5, 41.47) * mm});
            skLineSegment(sketch, "E10134", {"start": v(-93.5, 41.47) * mm, "end": v(-93.7, 41.3) * mm});
            skLineSegment(sketch, "E10135", {"start": v(-93.7, 41.3) * mm, "end": v(-93.88, 41.1) * mm});
            skLineSegment(sketch, "E10136", {"start": v(-93.88, 41.1) * mm, "end": v(-94.05, 40.88) * mm});
            skLineSegment(sketch, "E10137", {"start": v(-94.05, 40.88) * mm, "end": v(-94.2, 40.67) * mm});
            skLineSegment(sketch, "E10138", {"start": v(-94.2, 40.67) * mm, "end": v(-94.33, 40.45) * mm});
            skLineSegment(sketch, "E10139", {"start": v(-94.33, 40.45) * mm, "end": v(-94.44, 40.24) * mm});
            skLineSegment(sketch, "E10140", {"start": v(-94.44, 40.24) * mm, "end": v(-94.54, 40.02) * mm});
            skLineSegment(sketch, "E10141", {"start": v(-94.54, 40.02) * mm, "end": v(-94.63, 39.77) * mm});
            skLineSegment(sketch, "E10142", {"start": v(-94.63, 39.77) * mm, "end": v(-94.7, 39.51) * mm});
            skLineSegment(sketch, "E10143", {"start": v(-94.7, 39.51) * mm, "end": v(-94.75, 39.24) * mm});
            skLineSegment(sketch, "E10144", {"start": v(-94.75, 39.24) * mm, "end": v(-94.8, 38.97) * mm});
            skLineSegment(sketch, "E10145", {"start": v(-94.8, 38.97) * mm, "end": v(-94.82, 38.7) * mm});
            skLineSegment(sketch, "E10146", {"start": v(-94.82, 38.7) * mm, "end": v(-94.83, 38.44) * mm});
            skLineSegment(sketch, "E10147", {"start": v(-94.83, 38.44) * mm, "end": v(-94.83, 38.2) * mm});
            skLineSegment(sketch, "E10148", {"start": v(-94.83, 38.2) * mm, "end": v(-94.81, 37.98) * mm});
            skLineSegment(sketch, "E10149", {"start": v(-94.81, 37.98) * mm, "end": v(-94.78, 37.76) * mm});
            skLineSegment(sketch, "E10150", {"start": v(-94.78, 37.76) * mm, "end": v(-94.74, 37.54) * mm});
            skLineSegment(sketch, "E10151", {"start": v(-94.74, 37.54) * mm, "end": v(-94.7, 37.3) * mm});
            skLineSegment(sketch, "E10152", {"start": v(-94.7, 37.3) * mm, "end": v(-94.57, 36.86) * mm});
            skLineSegment(sketch, "E10153", {"start": v(-94.57, 36.86) * mm, "end": v(-94.44, 36.46) * mm});
            skLineSegment(sketch, "E10154", {"start": v(-94.44, 36.46) * mm, "end": v(-94.08, 35.48) * mm});
            skLineSegment(sketch, "E10155", {"start": v(-94.08, 35.48) * mm, "end": v(-93.9, 35.03) * mm});
            skLineSegment(sketch, "E10156", {"start": v(-93.9, 35.03) * mm, "end": v(-93.7, 34.6) * mm});
            skLineSegment(sketch, "E10157", {"start": v(-93.7, 34.6) * mm, "end": v(-93.5, 34.17) * mm});
            skLineSegment(sketch, "E10158", {"start": v(-93.5, 34.17) * mm, "end": v(-93.25, 33.75) * mm});
            skLineSegment(sketch, "E10159", {"start": v(-93.25, 33.75) * mm, "end": v(-93.12, 33.53) * mm});
            skLineSegment(sketch, "E10160", {"start": v(-93.12, 33.53) * mm, "end": v(-92.97, 33.32) * mm});
            skLineSegment(sketch, "E10161", {"start": v(-92.97, 33.32) * mm, "end": v(-92.81, 33.1) * mm});
            skLineSegment(sketch, "E10162", {"start": v(-92.81, 33.1) * mm, "end": v(-92.64, 32.88) * mm});
            skLineSegment(sketch, "E10163", {"start": v(-92.64, 32.88) * mm, "end": v(-92.48, 32.68) * mm});
            skLineSegment(sketch, "E10164", {"start": v(-92.48, 32.68) * mm, "end": v(-92.32, 32.5) * mm});
            skLineSegment(sketch, "E10165", {"start": v(-92.32, 32.5) * mm, "end": v(-91.92, 32.11) * mm});
            skLineSegment(sketch, "E10166", {"start": v(-91.92, 32.11) * mm, "end": v(-91.53, 31.7) * mm});
            skLineSegment(sketch, "E10167", {"start": v(-91.53, 31.7) * mm, "end": v(-91.31, 31.47) * mm});
            skLineSegment(sketch, "E10168", {"start": v(-91.31, 31.47) * mm, "end": v(-91.11, 31.27) * mm});
            skLineSegment(sketch, "E10169", {"start": v(-91.11, 31.27) * mm, "end": v(-90.33, 30.54) * mm});
            skLineSegment(sketch, "E10170", {"start": v(-90.33, 30.54) * mm, "end": v(-89.95, 30.18) * mm});
            skLineSegment(sketch, "E10171", {"start": v(-89.95, 30.18) * mm, "end": v(-89.56, 29.84) * mm});
            skLineSegment(sketch, "E10172", {"start": v(-89.56, 29.84) * mm, "end": v(-88.85, 29.22) * mm});
            skLineSegment(sketch, "E10173", {"start": v(-88.85, 29.22) * mm, "end": v(-88.14, 28.62) * mm});
            skLineSegment(sketch, "E10174", {"start": v(-88.14, 28.62) * mm, "end": v(-87.61, 28.2) * mm});
            skLineSegment(sketch, "E10175", {"start": v(-87.61, 28.2) * mm, "end": v(-87.08, 27.8) * mm});
            skLineSegment(sketch, "E10176", {"start": v(-87.08, 27.8) * mm, "end": v(-86.54, 27.4) * mm});
            skLineSegment(sketch, "E10177", {"start": v(-86.54, 27.4) * mm, "end": v(-86, 27) * mm});
            skLineSegment(sketch, "E10178", {"start": v(-86, 27) * mm, "end": v(-85.43, 26.61) * mm});
            skLineSegment(sketch, "E10179", {"start": v(-85.43, 26.61) * mm, "end": v(-84.83, 26.22) * mm});
            skLineSegment(sketch, "E10180", {"start": v(-84.83, 26.22) * mm, "end": v(-83.57, 25.4) * mm});
            skLineSegment(sketch, "E10181", {"start": v(-83.57, 25.4) * mm, "end": v(-82.89, 24.98) * mm});
            skLineSegment(sketch, "E10182", {"start": v(-82.89, 24.98) * mm, "end": v(-82.13, 24.53) * mm});
            skLineSegment(sketch, "E10183", {"start": v(-82.13, 24.53) * mm, "end": v(-81.37, 24.1) * mm});
            skLineSegment(sketch, "E10184", {"start": v(-81.37, 24.1) * mm, "end": v(-80.66, 23.73) * mm});
            skLineSegment(sketch, "E10185", {"start": v(-80.66, 23.73) * mm, "end": v(-80.61, 23.71) * mm});
            skLineSegment(sketch, "E10186", {"start": v(-80.61, 23.71) * mm, "end": v(-80.54, 23.7) * mm});
            skLineSegment(sketch, "E10187", {"start": v(-80.54, 23.7) * mm, "end": v(-80.47, 23.71) * mm});
            skLineSegment(sketch, "E10188", {"start": v(-80.47, 23.71) * mm, "end": v(-80.41, 23.73) * mm});
            skLineSegment(sketch, "E10189", {"start": v(-80.41, 23.73) * mm, "end": v(-80.34, 23.76) * mm});
            skLineSegment(sketch, "E10190", {"start": v(-80.34, 23.76) * mm, "end": v(-80.3, 23.8) * mm});
            skLineSegment(sketch, "E10191", {"start": v(-80.3, 23.8) * mm, "end": v(-80.2, 23.88) * mm});
            skLineSegment(sketch, "E10192", {"start": v(-80.2, 23.88) * mm, "end": v(-80.15, 23.94) * mm});
            skLineSegment(sketch, "E10193", {"start": v(-80.15, 23.94) * mm, "end": v(-80.1, 24) * mm});
            skLineSegment(sketch, "E10194", {"start": v(-80.1, 24) * mm, "end": v(-80.1, 24.02) * mm});
            skLineSegment(sketch, "E10195", {"start": v(-80.1, 24.02) * mm, "end": v(-80.13, 24) * mm});
            skLineSegment(sketch, "E10196", {"start": v(-80.13, 24) * mm, "end": v(-80.24, 23.88) * mm});
            skLineSegment(sketch, "E10197", {"start": v(-80.24, 23.88) * mm, "end": v(-80.36, 23.75) * mm});
            skLineSegment(sketch, "E10198", {"start": v(16.22, -2.56) * mm, "end": v(15.77, -2.33) * mm});
            skLineSegment(sketch, "E10199", {"start": v(15.77, -2.33) * mm, "end": v(15.14, -1.99) * mm});
            skLineSegment(sketch, "E10200", {"start": v(15.14, -1.99) * mm, "end": v(14.53, -1.66) * mm});
            skLineSegment(sketch, "E10201", {"start": v(14.53, -1.66) * mm, "end": v(13.95, -1.37) * mm});
            skLineSegment(sketch, "E10202", {"start": v(13.95, -1.37) * mm, "end": v(13.16, -0.97) * mm});
            skLineSegment(sketch, "E10203", {"start": v(13.16, -0.97) * mm, "end": v(12.76, -0.78) * mm});
            skLineSegment(sketch, "E10204", {"start": v(12.76, -0.78) * mm, "end": v(12.38, -0.62) * mm});
            skLineSegment(sketch, "E10205", {"start": v(12.38, -0.62) * mm, "end": v(12.07, -0.5) * mm});
            skLineSegment(sketch, "E10206", {"start": v(12.07, -0.5) * mm, "end": v(11.77, -0.4) * mm});
            skLineSegment(sketch, "E10207", {"start": v(11.77, -0.4) * mm, "end": v(11.2, -0.23) * mm});
            skLineSegment(sketch, "E10208", {"start": v(11.2, -0.23) * mm, "end": v(10.71, -0.11) * mm});
            skLineSegment(sketch, "E10209", {"start": v(10.71, -0.11) * mm, "end": v(10.34, -0.03) * mm});
            skLineSegment(sketch, "E10210", {"start": v(10.34, -0.03) * mm, "end": v(9.68, 0.09) * mm});
            skLineSegment(sketch, "E10211", {"start": v(9.68, 0.09) * mm, "end": v(9.34, 0.13) * mm});
            skLineSegment(sketch, "E10212", {"start": v(9.34, 0.13) * mm, "end": v(9.07, 0.15) * mm});
            skLineSegment(sketch, "E10213", {"start": v(9.07, 0.15) * mm, "end": v(8.8, 0.14) * mm});
            skLineSegment(sketch, "E10214", {"start": v(8.8, 0.14) * mm, "end": v(8.47, 0.1) * mm});
            skLineSegment(sketch, "E10215", {"start": v(8.47, 0.1) * mm, "end": v(7.81, 0) * mm});
            skLineSegment(sketch, "E10216", {"start": v(7.81, 0) * mm, "end": v(7.54, -0.05) * mm});
            skLineSegment(sketch, "E10217", {"start": v(7.54, -0.05) * mm, "end": v(7.28, -0.12) * mm});
            skLineSegment(sketch, "E10218", {"start": v(7.28, -0.12) * mm, "end": v(7.04, -0.2) * mm});
            skLineSegment(sketch, "E10219", {"start": v(7.04, -0.2) * mm, "end": v(6.8, -0.28) * mm});
            skLineSegment(sketch, "E10220", {"start": v(6.8, -0.28) * mm, "end": v(6.59, -0.38) * mm});
            skLineSegment(sketch, "E10221", {"start": v(6.59, -0.38) * mm, "end": v(6.38, -0.5) * mm});
            skLineSegment(sketch, "E10222", {"start": v(6.38, -0.5) * mm, "end": v(6.17, -0.62) * mm});
            skLineSegment(sketch, "E10223", {"start": v(6.17, -0.62) * mm, "end": v(5.97, -0.76) * mm});
            skLineSegment(sketch, "E10224", {"start": v(5.97, -0.76) * mm, "end": v(5.76, -0.92) * mm});
            skLineSegment(sketch, "E10225", {"start": v(5.76, -0.92) * mm, "end": v(5.55, -1.09) * mm});
            skLineSegment(sketch, "E10226", {"start": v(5.55, -1.09) * mm, "end": v(5.34, -1.28) * mm});
            skLineSegment(sketch, "E10227", {"start": v(5.34, -1.28) * mm, "end": v(5.13, -1.49) * mm});
            skLineSegment(sketch, "E10228", {"start": v(5.13, -1.49) * mm, "end": v(4.68, -1.97) * mm});
            skLineSegment(sketch, "E10229", {"start": v(4.68, -1.97) * mm, "end": v(4.37, -2.33) * mm});
            skLineSegment(sketch, "E10230", {"start": v(4.37, -2.33) * mm, "end": v(4.23, -2.63) * mm});
            skLineSegment(sketch, "E10231", {"start": v(4.23, -2.63) * mm, "end": v(4.09, -2.91) * mm});
            skLineSegment(sketch, "E10232", {"start": v(4.09, -2.91) * mm, "end": v(3.95, -3.18) * mm});
            skLineSegment(sketch, "E10233", {"start": v(3.95, -3.18) * mm, "end": v(3.8, -3.48) * mm});
            skLineSegment(sketch, "E10234", {"start": v(3.8, -3.48) * mm, "end": v(3.66, -3.78) * mm});
            skLineSegment(sketch, "E10235", {"start": v(3.66, -3.78) * mm, "end": v(3.6, -3.93) * mm});
            skLineSegment(sketch, "E10236", {"start": v(3.6, -3.93) * mm, "end": v(3.57, -4.07) * mm});
            skLineSegment(sketch, "E10237", {"start": v(3.57, -4.07) * mm, "end": v(3.5, -4.34) * mm});
            skLineSegment(sketch, "E10238", {"start": v(3.5, -4.34) * mm, "end": v(3.45, -4.63) * mm});
            skLineSegment(sketch, "E10239", {"start": v(3.45, -4.63) * mm, "end": v(3.4, -4.94) * mm});
            skLineSegment(sketch, "E10240", {"start": v(3.4, -4.94) * mm, "end": v(3.37, -5.26) * mm});
            skLineSegment(sketch, "E10241", {"start": v(3.37, -5.26) * mm, "end": v(3.33, -5.9) * mm});
            skLineSegment(sketch, "E10242", {"start": v(3.33, -5.9) * mm, "end": v(3.32, -6.43) * mm});
            skLineSegment(sketch, "E10243", {"start": v(3.32, -6.43) * mm, "end": v(3.3, -6.72) * mm});
            skLineSegment(sketch, "E10244", {"start": v(3.3, -6.72) * mm, "end": v(3.3, -7.06) * mm});
            skLineSegment(sketch, "E10245", {"start": v(3.3, -7.06) * mm, "end": v(3.3, -7.38) * mm});
            skLineSegment(sketch, "E10246", {"start": v(3.3, -7.38) * mm, "end": v(3.3, -7.54) * mm});
            skLineSegment(sketch, "E10247", {"start": v(3.3, -7.54) * mm, "end": v(3.32, -7.67) * mm});
            skLineSegment(sketch, "E10248", {"start": v(3.32, -7.67) * mm, "end": v(3.59, -9.01) * mm});
            skLineSegment(sketch, "E10249", {"start": v(3.59, -9.01) * mm, "end": v(4.9, -11.87) * mm});
            skLineSegment(sketch, "E10250", {"start": v(4.9, -11.87) * mm, "end": v(5.25, -12.88) * mm});
            skLineSegment(sketch, "E10251", {"start": v(5.25, -12.88) * mm, "end": v(5.35, -12.66) * mm});
            skLineSegment(sketch, "E10252", {"start": v(5.35, -12.66) * mm, "end": v(5.48, -12.43) * mm});
            skLineSegment(sketch, "E10253", {"start": v(5.48, -12.43) * mm, "end": v(5.62, -12.2) * mm});
            skLineSegment(sketch, "E10254", {"start": v(5.62, -12.2) * mm, "end": v(5.77, -11.97) * mm});
            skLineSegment(sketch, "E10255", {"start": v(5.77, -11.97) * mm, "end": v(6.09, -11.5) * mm});
            skLineSegment(sketch, "E10256", {"start": v(6.09, -11.5) * mm, "end": v(6.38, -11.1) * mm});
            skLineSegment(sketch, "E10257", {"start": v(6.38, -11.1) * mm, "end": v(6.93, -10.37) * mm});
            skLineSegment(sketch, "E10258", {"start": v(6.93, -10.37) * mm, "end": v(7.23, -9.99) * mm});
            skLineSegment(sketch, "E10259", {"start": v(7.23, -9.99) * mm, "end": v(7.53, -9.61) * mm});
            skLineSegment(sketch, "E10260", {"start": v(7.53, -9.61) * mm, "end": v(7.84, -9.25) * mm});
            skLineSegment(sketch, "E10261", {"start": v(7.84, -9.25) * mm, "end": v(8.14, -8.91) * mm});
            skLineSegment(sketch, "E10262", {"start": v(8.14, -8.91) * mm, "end": v(8.42, -8.62) * mm});
            skLineSegment(sketch, "E10263", {"start": v(8.42, -8.62) * mm, "end": v(8.68, -8.37) * mm});
            skLineSegment(sketch, "E10264", {"start": v(8.68, -8.37) * mm, "end": v(9, -8.11) * mm});
            skLineSegment(sketch, "E10265", {"start": v(9, -8.11) * mm, "end": v(9.35, -7.85) * mm});
            skLineSegment(sketch, "E10266", {"start": v(9.35, -7.85) * mm, "end": v(9.54, -7.72) * mm});
            skLineSegment(sketch, "E10267", {"start": v(9.54, -7.72) * mm, "end": v(9.73, -7.61) * mm});
            skLineSegment(sketch, "E10268", {"start": v(9.73, -7.61) * mm, "end": v(9.92, -7.52) * mm});
            skLineSegment(sketch, "E10269", {"start": v(9.92, -7.52) * mm, "end": v(10.1, -7.44) * mm});
            skLineSegment(sketch, "E10270", {"start": v(10.1, -7.44) * mm, "end": v(10.23, -7.4) * mm});
            skLineSegment(sketch, "E10271", {"start": v(10.23, -7.4) * mm, "end": v(10.38, -7.36) * mm});
            skLineSegment(sketch, "E10272", {"start": v(10.38, -7.36) * mm, "end": v(10.54, -7.33) * mm});
            skLineSegment(sketch, "E10273", {"start": v(10.54, -7.33) * mm, "end": v(10.7, -7.3) * mm});
            skLineSegment(sketch, "E10274", {"start": v(10.7, -7.3) * mm, "end": v(11.03, -7.28) * mm});
            skLineSegment(sketch, "E10275", {"start": v(11.03, -7.28) * mm, "end": v(11.37, -7.29) * mm});
            skLineSegment(sketch, "E10276", {"start": v(11.37, -7.29) * mm, "end": v(11.72, -7.3) * mm});
            skLineSegment(sketch, "E10277", {"start": v(11.72, -7.3) * mm, "end": v(12.06, -7.34) * mm});
            skLineSegment(sketch, "E10278", {"start": v(12.06, -7.34) * mm, "end": v(12.68, -7.44) * mm});
            skLineSegment(sketch, "E10279", {"start": v(12.68, -7.44) * mm, "end": v(12.92, -7.49) * mm});
            skLineSegment(sketch, "E10280", {"start": v(12.92, -7.49) * mm, "end": v(13.17, -7.56) * mm});
            skLineSegment(sketch, "E10281", {"start": v(13.17, -7.56) * mm, "end": v(13.7, -7.72) * mm});
            skLineSegment(sketch, "E10282", {"start": v(13.7, -7.72) * mm, "end": v(14.21, -7.91) * mm});
            skLineSegment(sketch, "E10283", {"start": v(14.21, -7.91) * mm, "end": v(14.68, -8.09) * mm});
            skLineSegment(sketch, "E10284", {"start": v(14.68, -8.09) * mm, "end": v(17.88, -9.5) * mm});
            skLineSegment(sketch, "E10285", {"start": v(17.88, -9.5) * mm, "end": v(18, -9.6) * mm});
            skLineSegment(sketch, "E10286", {"start": v(18, -9.6) * mm, "end": v(18.16, -9.73) * mm});
            skLineSegment(sketch, "E10287", {"start": v(18.16, -9.73) * mm, "end": v(18.32, -9.87) * mm});
            skLineSegment(sketch, "E10288", {"start": v(18.32, -9.87) * mm, "end": v(18.4, -9.93) * mm});
            skLineSegment(sketch, "E10289", {"start": v(18.4, -9.93) * mm, "end": v(18.48, -9.98) * mm});
            skLineSegment(sketch, "E10290", {"start": v(18.48, -9.98) * mm, "end": v(18.64, -10.05) * mm});
            skLineSegment(sketch, "E10291", {"start": v(18.64, -10.05) * mm, "end": v(18.85, -10.13) * mm});
            skLineSegment(sketch, "E10292", {"start": v(18.85, -10.13) * mm, "end": v(19.1, -10.2) * mm});
            skLineSegment(sketch, "E10293", {"start": v(19.1, -10.2) * mm, "end": v(19.36, -10.27) * mm});
            skLineSegment(sketch, "E10294", {"start": v(19.36, -10.27) * mm, "end": v(19.65, -10.34) * mm});
            skLineSegment(sketch, "E10295", {"start": v(19.65, -10.34) * mm, "end": v(19.95, -10.4) * mm});
            skLineSegment(sketch, "E10296", {"start": v(19.95, -10.4) * mm, "end": v(20.25, -10.46) * mm});
            skLineSegment(sketch, "E10297", {"start": v(20.25, -10.46) * mm, "end": v(20.55, -10.5) * mm});
            skLineSegment(sketch, "E10298", {"start": v(20.55, -10.5) * mm, "end": v(21.95, -10.68) * mm});
            skLineSegment(sketch, "E10299", {"start": v(21.95, -10.68) * mm, "end": v(18.3, -4.46) * mm});
            skLineSegment(sketch, "E10300", {"start": v(18.3, -4.46) * mm, "end": v(17.81, -4.02) * mm});
            skLineSegment(sketch, "E10301", {"start": v(17.81, -4.02) * mm, "end": v(17.3, -3.53) * mm});
            skLineSegment(sketch, "E10302", {"start": v(17.3, -3.53) * mm, "end": v(16.76, -3.03) * mm});
            skLineSegment(sketch, "E10303", {"start": v(16.76, -3.03) * mm, "end": v(16.5, -2.79) * mm});
            skLineSegment(sketch, "E10304", {"start": v(16.5, -2.79) * mm, "end": v(16.22, -2.56) * mm});
            skLineSegment(sketch, "E10305", {"start": v(18.65, -1.37) * mm, "end": v(18.48, -1.5) * mm});
            skLineSegment(sketch, "E10306", {"start": v(18.48, -1.5) * mm, "end": v(17.68, -2.06) * mm});
            skLineSegment(sketch, "E10307", {"start": v(17.68, -2.06) * mm, "end": v(17.5, -2.2) * mm});
            skLineSegment(sketch, "E10308", {"start": v(17.5, -2.2) * mm, "end": v(17.24, -2.47) * mm});
            skLineSegment(sketch, "E10309", {"start": v(17.24, -2.47) * mm, "end": v(19.52, -5.06) * mm});
            skLineSegment(sketch, "E10310", {"start": v(19.52, -5.06) * mm, "end": v(22.06, -9.04) * mm});
            skLineSegment(sketch, "E10311", {"start": v(22.06, -9.04) * mm, "end": v(24.1, -10.57) * mm});
            skLineSegment(sketch, "E10312", {"start": v(24.1, -10.57) * mm, "end": v(24.56, -10.78) * mm});
            skLineSegment(sketch, "E10313", {"start": v(24.56, -10.78) * mm, "end": v(25.07, -11.02) * mm});
            skLineSegment(sketch, "E10314", {"start": v(25.07, -11.02) * mm, "end": v(25.33, -11.13) * mm});
            skLineSegment(sketch, "E10315", {"start": v(25.33, -11.13) * mm, "end": v(25.58, -11.24) * mm});
            skLineSegment(sketch, "E10316", {"start": v(25.58, -11.24) * mm, "end": v(25.83, -11.32) * mm});
            skLineSegment(sketch, "E10317", {"start": v(25.83, -11.32) * mm, "end": v(26.07, -11.38) * mm});
            skLineSegment(sketch, "E10318", {"start": v(26.07, -11.38) * mm, "end": v(26.24, -11.41) * mm});
            skLineSegment(sketch, "E10319", {"start": v(26.24, -11.41) * mm, "end": v(26.42, -11.44) * mm});
            skLineSegment(sketch, "E10320", {"start": v(26.42, -11.44) * mm, "end": v(26.8, -11.46) * mm});
            skLineSegment(sketch, "E10321", {"start": v(26.8, -11.46) * mm, "end": v(27.18, -11.47) * mm});
            skLineSegment(sketch, "E10322", {"start": v(27.18, -11.47) * mm, "end": v(27.58, -11.46) * mm});
            skLineSegment(sketch, "E10323", {"start": v(27.58, -11.46) * mm, "end": v(28.37, -11.42) * mm});
            skLineSegment(sketch, "E10324", {"start": v(28.37, -11.42) * mm, "end": v(28.75, -11.4) * mm});
            skLineSegment(sketch, "E10325", {"start": v(28.75, -11.4) * mm, "end": v(29.1, -11.4) * mm});
            skLineSegment(sketch, "E10326", {"start": v(29.1, -11.4) * mm, "end": v(29.63, -10.82) * mm});
            skLineSegment(sketch, "E10327", {"start": v(29.63, -10.82) * mm, "end": v(29.74, -10.69) * mm});
            skLineSegment(sketch, "E10328", {"start": v(29.74, -10.69) * mm, "end": v(29.86, -10.53) * mm});
            skLineSegment(sketch, "E10329", {"start": v(29.86, -10.53) * mm, "end": v(29.98, -10.35) * mm});
            skLineSegment(sketch, "E10330", {"start": v(29.98, -10.35) * mm, "end": v(30.1, -10.16) * mm});
            skLineSegment(sketch, "E10331", {"start": v(30.1, -10.16) * mm, "end": v(30.2, -9.96) * mm});
            skLineSegment(sketch, "E10332", {"start": v(30.2, -9.96) * mm, "end": v(30.31, -9.76) * mm});
            skLineSegment(sketch, "E10333", {"start": v(30.31, -9.76) * mm, "end": v(30.4, -9.56) * mm});
            skLineSegment(sketch, "E10334", {"start": v(30.4, -9.56) * mm, "end": v(30.48, -9.38) * mm});
            skLineSegment(sketch, "E10335", {"start": v(30.48, -9.38) * mm, "end": v(30.8, -8.51) * mm});
            skLineSegment(sketch, "E10336", {"start": v(30.8, -8.51) * mm, "end": v(30.3, -8.49) * mm});
            skLineSegment(sketch, "E10337", {"start": v(30.3, -8.49) * mm, "end": v(29.74, -8.48) * mm});
            skLineSegment(sketch, "E10338", {"start": v(29.74, -8.48) * mm, "end": v(28.59, -8.45) * mm});
            skLineSegment(sketch, "E10339", {"start": v(28.59, -8.45) * mm, "end": v(28, -8.43) * mm});
            skLineSegment(sketch, "E10340", {"start": v(28, -8.43) * mm, "end": v(27.44, -8.38) * mm});
            skLineSegment(sketch, "E10341", {"start": v(27.44, -8.38) * mm, "end": v(27.17, -8.35) * mm});
            skLineSegment(sketch, "E10342", {"start": v(27.17, -8.35) * mm, "end": v(26.9, -8.31) * mm});
            skLineSegment(sketch, "E10343", {"start": v(26.9, -8.31) * mm, "end": v(26.65, -8.26) * mm});
            skLineSegment(sketch, "E10344", {"start": v(26.65, -8.26) * mm, "end": v(26.4, -8.2) * mm});
            skLineSegment(sketch, "E10345", {"start": v(26.4, -8.2) * mm, "end": v(26.05, -8.09) * mm});
            skLineSegment(sketch, "E10346", {"start": v(26.05, -8.09) * mm, "end": v(25.68, -7.95) * mm});
            skLineSegment(sketch, "E10347", {"start": v(25.68, -7.95) * mm, "end": v(25.3, -7.78) * mm});
            skLineSegment(sketch, "E10348", {"start": v(25.3, -7.78) * mm, "end": v(24.93, -7.6) * mm});
            skLineSegment(sketch, "E10349", {"start": v(24.93, -7.6) * mm, "end": v(24.56, -7.4) * mm});
            skLineSegment(sketch, "E10350", {"start": v(24.56, -7.4) * mm, "end": v(24.2, -7.19) * mm});
            skLineSegment(sketch, "E10351", {"start": v(24.2, -7.19) * mm, "end": v(23.87, -6.97) * mm});
            skLineSegment(sketch, "E10352", {"start": v(23.87, -6.97) * mm, "end": v(23.57, -6.75) * mm});
            skLineSegment(sketch, "E10353", {"start": v(23.57, -6.75) * mm, "end": v(23.23, -6.47) * mm});
            skLineSegment(sketch, "E10354", {"start": v(23.23, -6.47) * mm, "end": v(22.88, -6.15) * mm});
            skLineSegment(sketch, "E10355", {"start": v(22.88, -6.15) * mm, "end": v(22.52, -5.8) * mm});
            skLineSegment(sketch, "E10356", {"start": v(22.52, -5.8) * mm, "end": v(22.16, -5.43) * mm});
            skLineSegment(sketch, "E10357", {"start": v(22.16, -5.43) * mm, "end": v(21.47, -4.68) * mm});
            skLineSegment(sketch, "E10358", {"start": v(21.47, -4.68) * mm, "end": v(20.86, -3.99) * mm});
            skLineSegment(sketch, "E10359", {"start": v(20.86, -3.99) * mm, "end": v(18.65, -1.37) * mm});
            skLineSegment(sketch, "E10360", {"start": v(-15.37, 15.22) * mm, "end": v(-15.27, 15.41) * mm});
            skLineSegment(sketch, "E10361", {"start": v(-15.27, 15.41) * mm, "end": v(-15.13, 15.67) * mm});
            skLineSegment(sketch, "E10362", {"start": v(-15.13, 15.67) * mm, "end": v(-14.96, 15.93) * mm});
            skLineSegment(sketch, "E10363", {"start": v(-14.96, 15.93) * mm, "end": v(-14.56, 16.5) * mm});
            skLineSegment(sketch, "E10364", {"start": v(-14.56, 16.5) * mm, "end": v(-14.46, 16.65) * mm});
            skLineSegment(sketch, "E10365", {"start": v(-14.46, 16.65) * mm, "end": v(-14.31, 16.76) * mm});
            skLineSegment(sketch, "E10366", {"start": v(-14.31, 16.76) * mm, "end": v(-14.17, 16.84) * mm});
            skLineSegment(sketch, "E10367", {"start": v(-14.17, 16.84) * mm, "end": v(-14.09, 16.87) * mm});
            skLineSegment(sketch, "E10368", {"start": v(-14.09, 16.87) * mm, "end": v(-14.01, 16.9) * mm});
            skLineSegment(sketch, "E10369", {"start": v(-14.01, 16.9) * mm, "end": v(-13.93, 16.9) * mm});
            skLineSegment(sketch, "E10370", {"start": v(-13.93, 16.9) * mm, "end": v(-13.85, 16.91) * mm});
            skLineSegment(sketch, "E10371", {"start": v(-13.85, 16.91) * mm, "end": v(-13.49, 16.92) * mm});
            skLineSegment(sketch, "E10372", {"start": v(-13.49, 16.92) * mm, "end": v(-13.12, 16.95) * mm});
            skLineSegment(sketch, "E10373", {"start": v(-13.12, 16.95) * mm, "end": v(-12.76, 17) * mm});
            skLineSegment(sketch, "E10374", {"start": v(-12.76, 17) * mm, "end": v(-12.4, 17.04) * mm});
            skLineSegment(sketch, "E10375", {"start": v(-12.4, 17.04) * mm, "end": v(-11.72, 17.15) * mm});
            skLineSegment(sketch, "E10376", {"start": v(-11.72, 17.15) * mm, "end": v(-11.39, 17.2) * mm});
            skLineSegment(sketch, "E10377", {"start": v(-11.39, 17.2) * mm, "end": v(-11.07, 17.24) * mm});
            skLineSegment(sketch, "E10378", {"start": v(-11.07, 17.24) * mm, "end": v(-11.55, 16.3) * mm});
            skLineSegment(sketch, "E10379", {"start": v(-11.55, 16.3) * mm, "end": v(-11.65, 16.1) * mm});
            skLineSegment(sketch, "E10380", {"start": v(-11.65, 16.1) * mm, "end": v(-11.74, 15.89) * mm});
            skLineSegment(sketch, "E10381", {"start": v(-11.74, 15.89) * mm, "end": v(-11.82, 15.67) * mm});
            skLineSegment(sketch, "E10382", {"start": v(-11.82, 15.67) * mm, "end": v(-11.9, 15.46) * mm});
            skLineSegment(sketch, "E10383", {"start": v(-11.9, 15.46) * mm, "end": v(-11.96, 15.25) * mm});
            skLineSegment(sketch, "E10384", {"start": v(-11.96, 15.25) * mm, "end": v(-12, 15.06) * mm});
            skLineSegment(sketch, "E10385", {"start": v(-12, 15.06) * mm, "end": v(-12.03, 14.89) * mm});
            skLineSegment(sketch, "E10386", {"start": v(-12.03, 14.89) * mm, "end": v(-12.04, 14.75) * mm});
            skLineSegment(sketch, "E10387", {"start": v(-12.04, 14.75) * mm, "end": v(-12.04, 14.13) * mm});
            skLineSegment(sketch, "E10388", {"start": v(-12.04, 14.13) * mm, "end": v(-13.2, 13.57) * mm});
            skLineSegment(sketch, "E10389", {"start": v(-13.2, 13.57) * mm, "end": v(-13.45, 13.46) * mm});
            skLineSegment(sketch, "E10390", {"start": v(-13.45, 13.46) * mm, "end": v(-13.7, 13.36) * mm});
            skLineSegment(sketch, "E10391", {"start": v(-13.7, 13.36) * mm, "end": v(-14.17, 13.18) * mm});
            skLineSegment(sketch, "E10392", {"start": v(-14.17, 13.18) * mm, "end": v(-14.39, 13.11) * mm});
            skLineSegment(sketch, "E10393", {"start": v(-14.39, 13.11) * mm, "end": v(-14.58, 13.06) * mm});
            skLineSegment(sketch, "E10394", {"start": v(-14.58, 13.06) * mm, "end": v(-14.73, 13.03) * mm});
            skLineSegment(sketch, "E10395", {"start": v(-14.73, 13.03) * mm, "end": v(-14.86, 13.02) * mm});
            skLineSegment(sketch, "E10396", {"start": v(-14.86, 13.02) * mm, "end": v(-15.34, 13.02) * mm});
            skLineSegment(sketch, "E10397", {"start": v(-15.34, 13.02) * mm, "end": v(-15.35, 13.28) * mm});
            skLineSegment(sketch, "E10398", {"start": v(-15.35, 13.28) * mm, "end": v(-15.37, 13.55) * mm});
            skLineSegment(sketch, "E10399", {"start": v(-15.37, 13.55) * mm, "end": v(-15.43, 14.13) * mm});
            skLineSegment(sketch, "E10400", {"start": v(-15.43, 14.13) * mm, "end": v(-15.45, 14.42) * mm});
            skLineSegment(sketch, "E10401", {"start": v(-15.45, 14.42) * mm, "end": v(-15.45, 14.7) * mm});
            skLineSegment(sketch, "E10402", {"start": v(-15.45, 14.7) * mm, "end": v(-15.44, 14.84) * mm});
            skLineSegment(sketch, "E10403", {"start": v(-15.44, 14.84) * mm, "end": v(-15.42, 14.98) * mm});
            skLineSegment(sketch, "E10404", {"start": v(-15.42, 14.98) * mm, "end": v(-15.4, 15.1) * mm});
            skLineSegment(sketch, "E10405", {"start": v(-15.4, 15.1) * mm, "end": v(-15.36, 15.23) * mm});
            skLineSegment(sketch, "E10406", {"start": v(-15.36, 15.23) * mm, "end": v(-15.37, 15.22) * mm});
            skLineSegment(sketch, "E10407", {"start": v(-11.64, 7.67) * mm, "end": v(-11.72, 7.83) * mm});
            skLineSegment(sketch, "E10408", {"start": v(-11.72, 7.83) * mm, "end": v(-11.8, 7.99) * mm});
            skLineSegment(sketch, "E10409", {"start": v(-11.8, 7.99) * mm, "end": v(-11.84, 8.13) * mm});
            skLineSegment(sketch, "E10410", {"start": v(-11.84, 8.13) * mm, "end": v(-11.87, 8.25) * mm});
            skLineSegment(sketch, "E10411", {"start": v(-11.87, 8.25) * mm, "end": v(-11.89, 8.41) * mm});
            skLineSegment(sketch, "E10412", {"start": v(-11.89, 8.41) * mm, "end": v(-11.89, 8.6) * mm});
            skLineSegment(sketch, "E10413", {"start": v(-11.89, 8.6) * mm, "end": v(-11.87, 8.78) * mm});
            skLineSegment(sketch, "E10414", {"start": v(-11.87, 8.78) * mm, "end": v(-11.82, 8.99) * mm});
            skLineSegment(sketch, "E10415", {"start": v(-11.82, 8.99) * mm, "end": v(-11.77, 9.2) * mm});
            skLineSegment(sketch, "E10416", {"start": v(-11.77, 9.2) * mm, "end": v(-11.7, 9.42) * mm});
            skLineSegment(sketch, "E10417", {"start": v(-11.7, 9.42) * mm, "end": v(-11.52, 9.87) * mm});
            skLineSegment(sketch, "E10418", {"start": v(-11.52, 9.87) * mm, "end": v(-11.49, 9.97) * mm});
            skLineSegment(sketch, "E10419", {"start": v(-11.49, 9.97) * mm, "end": v(-11.48, 10.08) * mm});
            skLineSegment(sketch, "E10420", {"start": v(-11.48, 10.08) * mm, "end": v(-11.48, 10.1) * mm});
            skLineSegment(sketch, "E10421", {"start": v(-11.48, 10.1) * mm, "end": v(-11.3, 10.32) * mm});
            skLineSegment(sketch, "E10422", {"start": v(-11.3, 10.32) * mm, "end": v(-11.01, 10.28) * mm});
            skLineSegment(sketch, "E10423", {"start": v(-11.01, 10.28) * mm, "end": v(-10.7, 10.27) * mm});
            skLineSegment(sketch, "E10424", {"start": v(-10.7, 10.27) * mm, "end": v(-10.38, 10.27) * mm});
            skLineSegment(sketch, "E10425", {"start": v(-10.38, 10.27) * mm, "end": v(-10.06, 10.3) * mm});
            skLineSegment(sketch, "E10426", {"start": v(-10.06, 10.3) * mm, "end": v(-9.73, 10.34) * mm});
            skLineSegment(sketch, "E10427", {"start": v(-9.73, 10.34) * mm, "end": v(-9.4, 10.4) * mm});
            skLineSegment(sketch, "E10428", {"start": v(-9.4, 10.4) * mm, "end": v(-9.1, 10.47) * mm});
            skLineSegment(sketch, "E10429", {"start": v(-9.1, 10.47) * mm, "end": v(-8.8, 10.56) * mm});
            skLineSegment(sketch, "E10430", {"start": v(-8.8, 10.56) * mm, "end": v(-8.5, 8.23) * mm});
            skLineSegment(sketch, "E10431", {"start": v(-8.5, 8.23) * mm, "end": v(-8.74, 7.96) * mm});
            skLineSegment(sketch, "E10432", {"start": v(-8.74, 7.96) * mm, "end": v(-8.82, 7.9) * mm});
            skLineSegment(sketch, "E10433", {"start": v(-8.82, 7.9) * mm, "end": v(-8.94, 7.84) * mm});
            skLineSegment(sketch, "E10434", {"start": v(-8.94, 7.84) * mm, "end": v(-9.1, 7.77) * mm});
            skLineSegment(sketch, "E10435", {"start": v(-9.1, 7.77) * mm, "end": v(-9.3, 7.7) * mm});
            skLineSegment(sketch, "E10436", {"start": v(-9.3, 7.7) * mm, "end": v(-9.53, 7.64) * mm});
            skLineSegment(sketch, "E10437", {"start": v(-9.53, 7.64) * mm, "end": v(-9.78, 7.59) * mm});
            skLineSegment(sketch, "E10438", {"start": v(-9.78, 7.59) * mm, "end": v(-10.04, 7.54) * mm});
            skLineSegment(sketch, "E10439", {"start": v(-10.04, 7.54) * mm, "end": v(-10.32, 7.5) * mm});
            skLineSegment(sketch, "E10440", {"start": v(-10.32, 7.5) * mm, "end": v(-10.9, 7.48) * mm});
            skLineSegment(sketch, "E10441", {"start": v(-10.9, 7.48) * mm, "end": v(-11.5, 7.46) * mm});
            skLineSegment(sketch, "E10442", {"start": v(-11.5, 7.46) * mm, "end": v(-11.53, 7.46) * mm});
            skLineSegment(sketch, "E10443", {"start": v(-11.53, 7.46) * mm, "end": v(-11.55, 7.48) * mm});
            skLineSegment(sketch, "E10444", {"start": v(-11.55, 7.48) * mm, "end": v(-11.59, 7.54) * mm});
            skLineSegment(sketch, "E10445", {"start": v(-11.59, 7.54) * mm, "end": v(-11.61, 7.6) * mm});
            skLineSegment(sketch, "E10446", {"start": v(-11.61, 7.6) * mm, "end": v(-11.64, 7.67) * mm});
            skLineSegment(sketch, "E10447", {"start": v(65.17, -32.6) * mm, "end": v(65.19, -32.56) * mm});
            skLineSegment(sketch, "E10448", {"start": v(65.19, -32.56) * mm, "end": v(65.22, -32.5) * mm});
            skLineSegment(sketch, "E10449", {"start": v(65.22, -32.5) * mm, "end": v(65.36, -32.31) * mm});
            skLineSegment(sketch, "E10450", {"start": v(65.36, -32.31) * mm, "end": v(65.58, -32.05) * mm});
            skLineSegment(sketch, "E10451", {"start": v(65.58, -32.05) * mm, "end": v(65.88, -31.72) * mm});
            skLineSegment(sketch, "E10452", {"start": v(65.88, -31.72) * mm, "end": v(66.64, -30.9) * mm});
            skLineSegment(sketch, "E10453", {"start": v(66.64, -30.9) * mm, "end": v(67.57, -29.93) * mm});
            skLineSegment(sketch, "E10454", {"start": v(67.57, -29.93) * mm, "end": v(69.96, -27.5) * mm});
            skLineSegment(sketch, "E10455", {"start": v(69.96, -27.5) * mm, "end": v(69.23, -27.21) * mm});
            skLineSegment(sketch, "E10456", {"start": v(69.23, -27.21) * mm, "end": v(69.67, -24.5) * mm});
            skLineSegment(sketch, "E10457", {"start": v(69.67, -24.5) * mm, "end": v(69.76, -23.95) * mm});
            skLineSegment(sketch, "E10458", {"start": v(69.76, -23.95) * mm, "end": v(69.83, -23.4) * mm});
            skLineSegment(sketch, "E10459", {"start": v(69.83, -23.4) * mm, "end": v(69.9, -22.85) * mm});
            skLineSegment(sketch, "E10460", {"start": v(69.9, -22.85) * mm, "end": v(69.96, -22.32) * mm});
            skLineSegment(sketch, "E10461", {"start": v(69.96, -22.32) * mm, "end": v(70, -21.81) * mm});
            skLineSegment(sketch, "E10462", {"start": v(70, -21.81) * mm, "end": v(70.05, -21.32) * mm});
            skLineSegment(sketch, "E10463", {"start": v(70.05, -21.32) * mm, "end": v(70.07, -20.85) * mm});
            skLineSegment(sketch, "E10464", {"start": v(70.07, -20.85) * mm, "end": v(70.1, -20.4) * mm});
            skLineSegment(sketch, "E10465", {"start": v(70.1, -20.4) * mm, "end": v(70.1, -19.99) * mm});
            skLineSegment(sketch, "E10466", {"start": v(70.1, -19.99) * mm, "end": v(70.1, -19.6) * mm});
            skLineSegment(sketch, "E10467", {"start": v(70.1, -19.6) * mm, "end": v(70.09, -19.25) * mm});
            skLineSegment(sketch, "E10468", {"start": v(70.09, -19.25) * mm, "end": v(70.07, -18.94) * mm});
            skLineSegment(sketch, "E10469", {"start": v(70.07, -18.94) * mm, "end": v(70.03, -18.67) * mm});
            skLineSegment(sketch, "E10470", {"start": v(70.03, -18.67) * mm, "end": v(70, -18.44) * mm});
            skLineSegment(sketch, "E10471", {"start": v(70, -18.44) * mm, "end": v(69.94, -18.26) * mm});
            skLineSegment(sketch, "E10472", {"start": v(69.94, -18.26) * mm, "end": v(69.9, -18.19) * mm});
            skLineSegment(sketch, "E10473", {"start": v(69.9, -18.19) * mm, "end": v(69.87, -18.13) * mm});
            skLineSegment(sketch, "E10474", {"start": v(69.87, -18.13) * mm, "end": v(69.8, -18.05) * mm});
            skLineSegment(sketch, "E10475", {"start": v(69.8, -18.05) * mm, "end": v(69.68, -17.96) * mm});
            skLineSegment(sketch, "E10476", {"start": v(69.68, -17.96) * mm, "end": v(69.53, -17.86) * mm});
            skLineSegment(sketch, "E10477", {"start": v(69.53, -17.86) * mm, "end": v(69.34, -17.76) * mm});
            skLineSegment(sketch, "E10478", {"start": v(69.34, -17.76) * mm, "end": v(69.13, -17.65) * mm});
            skLineSegment(sketch, "E10479", {"start": v(69.13, -17.65) * mm, "end": v(68.9, -17.55) * mm});
            skLineSegment(sketch, "E10480", {"start": v(68.9, -17.55) * mm, "end": v(68.66, -17.46) * mm});
            skLineSegment(sketch, "E10481", {"start": v(68.66, -17.46) * mm, "end": v(68.42, -17.37) * mm});
            skLineSegment(sketch, "E10482", {"start": v(68.42, -17.37) * mm, "end": v(68.13, -17.26) * mm});
            skLineSegment(sketch, "E10483", {"start": v(68.13, -17.26) * mm, "end": v(67.8, -17.12) * mm});
            skLineSegment(sketch, "E10484", {"start": v(67.8, -17.12) * mm, "end": v(67.4, -16.93) * mm});
            skLineSegment(sketch, "E10485", {"start": v(67.4, -16.93) * mm, "end": v(67, -16.72) * mm});
            skLineSegment(sketch, "E10486", {"start": v(67, -16.72) * mm, "end": v(66.56, -16.5) * mm});
            skLineSegment(sketch, "E10487", {"start": v(66.56, -16.5) * mm, "end": v(66.12, -16.24) * mm});
            skLineSegment(sketch, "E10488", {"start": v(66.12, -16.24) * mm, "end": v(65.7, -15.99) * mm});
            skLineSegment(sketch, "E10489", {"start": v(65.7, -15.99) * mm, "end": v(65.28, -15.73) * mm});
            skLineSegment(sketch, "E10490", {"start": v(65.28, -15.73) * mm, "end": v(64.81, -15.44) * mm});
            skLineSegment(sketch, "E10491", {"start": v(64.81, -15.44) * mm, "end": v(64.3, -15.13) * mm});
            skLineSegment(sketch, "E10492", {"start": v(64.3, -15.13) * mm, "end": v(64.05, -14.98) * mm});
            skLineSegment(sketch, "E10493", {"start": v(64.05, -14.98) * mm, "end": v(63.8, -14.81) * mm});
            skLineSegment(sketch, "E10494", {"start": v(63.8, -14.81) * mm, "end": v(63.57, -14.65) * mm});
            skLineSegment(sketch, "E10495", {"start": v(63.57, -14.65) * mm, "end": v(63.36, -14.49) * mm});
            skLineSegment(sketch, "E10496", {"start": v(63.36, -14.49) * mm, "end": v(63.09, -14.24) * mm});
            skLineSegment(sketch, "E10497", {"start": v(63.09, -14.24) * mm, "end": v(62.82, -13.96) * mm});
            skLineSegment(sketch, "E10498", {"start": v(62.82, -13.96) * mm, "end": v(62.56, -13.65) * mm});
            skLineSegment(sketch, "E10499", {"start": v(62.56, -13.65) * mm, "end": v(62.3, -13.33) * mm});
            skLineSegment(sketch, "E10500", {"start": v(62.3, -13.33) * mm, "end": v(61.8, -12.64) * mm});
            skLineSegment(sketch, "E10501", {"start": v(61.8, -12.64) * mm, "end": v(61.28, -11.94) * mm});
            skLineSegment(sketch, "E10502", {"start": v(61.28, -11.94) * mm, "end": v(61.02, -11.6) * mm});
            skLineSegment(sketch, "E10503", {"start": v(61.02, -11.6) * mm, "end": v(60.75, -11.26) * mm});
            skLineSegment(sketch, "E10504", {"start": v(60.75, -11.26) * mm, "end": v(60.48, -10.94) * mm});
            skLineSegment(sketch, "E10505", {"start": v(60.48, -10.94) * mm, "end": v(60.2, -10.64) * mm});
            skLineSegment(sketch, "E10506", {"start": v(60.2, -10.64) * mm, "end": v(59.92, -10.37) * mm});
            skLineSegment(sketch, "E10507", {"start": v(59.92, -10.37) * mm, "end": v(59.77, -10.24) * mm});
            skLineSegment(sketch, "E10508", {"start": v(59.77, -10.24) * mm, "end": v(59.62, -10.12) * mm});
            skLineSegment(sketch, "E10509", {"start": v(59.62, -10.12) * mm, "end": v(59.46, -10.02) * mm});
            skLineSegment(sketch, "E10510", {"start": v(59.46, -10.02) * mm, "end": v(59.3, -9.92) * mm});
            skLineSegment(sketch, "E10511", {"start": v(59.3, -9.92) * mm, "end": v(59.14, -9.83) * mm});
            skLineSegment(sketch, "E10512", {"start": v(59.14, -9.83) * mm, "end": v(58.98, -9.75) * mm});
            skLineSegment(sketch, "E10513", {"start": v(58.98, -9.75) * mm, "end": v(58.89, -9.73) * mm});
            skLineSegment(sketch, "E10514", {"start": v(58.89, -9.73) * mm, "end": v(58.78, -9.73) * mm});
            skLineSegment(sketch, "E10515", {"start": v(58.78, -9.73) * mm, "end": v(58.67, -9.74) * mm});
            skLineSegment(sketch, "E10516", {"start": v(58.67, -9.74) * mm, "end": v(58.57, -9.75) * mm});
            skLineSegment(sketch, "E10517", {"start": v(58.57, -9.75) * mm, "end": v(58.57, -10.52) * mm});
            skLineSegment(sketch, "E10518", {"start": v(58.57, -10.52) * mm, "end": v(58.55, -11.33) * mm});
            skLineSegment(sketch, "E10519", {"start": v(58.55, -11.33) * mm, "end": v(58.5, -13.04) * mm});
            skLineSegment(sketch, "E10520", {"start": v(58.5, -13.04) * mm, "end": v(58.48, -13.9) * mm});
            skLineSegment(sketch, "E10521", {"start": v(58.48, -13.9) * mm, "end": v(58.49, -14.74) * mm});
            skLineSegment(sketch, "E10522", {"start": v(58.49, -14.74) * mm, "end": v(58.5, -15.15) * mm});
            skLineSegment(sketch, "E10523", {"start": v(58.5, -15.15) * mm, "end": v(58.52, -15.55) * mm});
            skLineSegment(sketch, "E10524", {"start": v(58.52, -15.55) * mm, "end": v(58.54, -15.94) * mm});
            skLineSegment(sketch, "E10525", {"start": v(58.54, -15.94) * mm, "end": v(58.57, -16.32) * mm});
            skLineSegment(sketch, "E10526", {"start": v(58.57, -16.32) * mm, "end": v(58.6, -16.52) * mm});
            skLineSegment(sketch, "E10527", {"start": v(58.6, -16.52) * mm, "end": v(58.64, -16.74) * mm});
            skLineSegment(sketch, "E10528", {"start": v(58.64, -16.74) * mm, "end": v(58.74, -17.19) * mm});
            skLineSegment(sketch, "E10529", {"start": v(58.74, -17.19) * mm, "end": v(58.85, -17.64) * mm});
            skLineSegment(sketch, "E10530", {"start": v(58.85, -17.64) * mm, "end": v(58.95, -18.06) * mm});
            skLineSegment(sketch, "E10531", {"start": v(58.95, -18.06) * mm, "end": v(59.04, -18.43) * mm});
            skLineSegment(sketch, "E10532", {"start": v(59.04, -18.43) * mm, "end": v(59.14, -18.84) * mm});
            skLineSegment(sketch, "E10533", {"start": v(59.14, -18.84) * mm, "end": v(59.26, -19.27) * mm});
            skLineSegment(sketch, "E10534", {"start": v(59.26, -19.27) * mm, "end": v(59.39, -19.7) * mm});
            skLineSegment(sketch, "E10535", {"start": v(59.39, -19.7) * mm, "end": v(59.52, -20.12) * mm});
            skLineSegment(sketch, "E10536", {"start": v(59.52, -20.12) * mm, "end": v(59.66, -20.52) * mm});
            skLineSegment(sketch, "E10537", {"start": v(59.66, -20.52) * mm, "end": v(59.8, -20.89) * mm});
            skLineSegment(sketch, "E10538", {"start": v(59.8, -20.89) * mm, "end": v(59.93, -21.2) * mm});
            skLineSegment(sketch, "E10539", {"start": v(59.93, -21.2) * mm, "end": v(60.06, -21.56) * mm});
            skLineSegment(sketch, "E10540", {"start": v(60.06, -21.56) * mm, "end": v(60.2, -21.93) * mm});
            skLineSegment(sketch, "E10541", {"start": v(60.2, -21.93) * mm, "end": v(60.36, -22.3) * mm});
            skLineSegment(sketch, "E10542", {"start": v(60.36, -22.3) * mm, "end": v(60.44, -22.47) * mm});
            skLineSegment(sketch, "E10543", {"start": v(60.44, -22.47) * mm, "end": v(60.53, -22.62) * mm});
            skLineSegment(sketch, "E10544", {"start": v(60.53, -22.62) * mm, "end": v(60.82, -23.05) * mm});
            skLineSegment(sketch, "E10545", {"start": v(60.82, -23.05) * mm, "end": v(61.15, -23.48) * mm});
            skLineSegment(sketch, "E10546", {"start": v(61.15, -23.48) * mm, "end": v(61.51, -23.92) * mm});
            skLineSegment(sketch, "E10547", {"start": v(61.51, -23.92) * mm, "end": v(61.9, -24.35) * mm});
            skLineSegment(sketch, "E10548", {"start": v(61.9, -24.35) * mm, "end": v(62.3, -24.76) * mm});
            skLineSegment(sketch, "E10549", {"start": v(62.3, -24.76) * mm, "end": v(62.7, -25.15) * mm});
            skLineSegment(sketch, "E10550", {"start": v(62.7, -25.15) * mm, "end": v(63.11, -25.5) * mm});
            skLineSegment(sketch, "E10551", {"start": v(63.11, -25.5) * mm, "end": v(63.32, -25.67) * mm});
            skLineSegment(sketch, "E10552", {"start": v(63.32, -25.67) * mm, "end": v(63.52, -25.82) * mm});
            skLineSegment(sketch, "E10553", {"start": v(63.52, -25.82) * mm, "end": v(63.66, -25.9) * mm});
            skLineSegment(sketch, "E10554", {"start": v(63.66, -25.9) * mm, "end": v(63.82, -26) * mm});
            skLineSegment(sketch, "E10555", {"start": v(63.82, -26) * mm, "end": v(64.16, -26.14) * mm});
            skLineSegment(sketch, "E10556", {"start": v(64.16, -26.14) * mm, "end": v(64.52, -26.28) * mm});
            skLineSegment(sketch, "E10557", {"start": v(64.52, -26.28) * mm, "end": v(64.84, -26.41) * mm});
            skLineSegment(sketch, "E10558", {"start": v(64.84, -26.41) * mm, "end": v(65.1, -26.54) * mm});
            skLineSegment(sketch, "E10559", {"start": v(65.1, -26.54) * mm, "end": v(65.36, -26.67) * mm});
            skLineSegment(sketch, "E10560", {"start": v(65.36, -26.67) * mm, "end": v(65.58, -26.8) * mm});
            skLineSegment(sketch, "E10561", {"start": v(65.58, -26.8) * mm, "end": v(65.78, -26.92) * mm});
            skLineSegment(sketch, "E10562", {"start": v(65.78, -26.92) * mm, "end": v(65.94, -27.03) * mm});
            skLineSegment(sketch, "E10563", {"start": v(65.94, -27.03) * mm, "end": v(66.06, -27.13) * mm});
            skLineSegment(sketch, "E10564", {"start": v(66.06, -27.13) * mm, "end": v(66.14, -27.22) * mm});
            skLineSegment(sketch, "E10565", {"start": v(66.14, -27.22) * mm, "end": v(66.16, -27.26) * mm});
            skLineSegment(sketch, "E10566", {"start": v(66.16, -27.26) * mm, "end": v(66.16, -27.29) * mm});
            skLineSegment(sketch, "E10567", {"start": v(66.16, -27.29) * mm, "end": v(66.16, -27.57) * mm});
            skLineSegment(sketch, "E10568", {"start": v(66.16, -27.57) * mm, "end": v(68.86, -27.57) * mm});
            skLineSegment(sketch, "E10569", {"start": v(68.86, -27.57) * mm, "end": v(68.75, -27.87) * mm});
            skLineSegment(sketch, "E10570", {"start": v(68.75, -27.87) * mm, "end": v(68.68, -27.98) * mm});
            skLineSegment(sketch, "E10571", {"start": v(68.68, -27.98) * mm, "end": v(68.53, -28.18) * mm});
            skLineSegment(sketch, "E10572", {"start": v(68.53, -28.18) * mm, "end": v(68.3, -28.44) * mm});
            skLineSegment(sketch, "E10573", {"start": v(68.3, -28.44) * mm, "end": v(68.01, -28.77) * mm});
            skLineSegment(sketch, "E10574", {"start": v(68.01, -28.77) * mm, "end": v(67.27, -29.58) * mm});
            skLineSegment(sketch, "E10575", {"start": v(67.27, -29.58) * mm, "end": v(66.39, -30.5) * mm});
            skLineSegment(sketch, "E10576", {"start": v(66.39, -30.5) * mm, "end": v(64.14, -32.83) * mm});
            skLineSegment(sketch, "E10577", {"start": v(64.14, -32.83) * mm, "end": v(54.8, -33.22) * mm});
            skLineSegment(sketch, "E10578", {"start": v(54.8, -33.22) * mm, "end": v(54.78, -33.28) * mm});
            skLineSegment(sketch, "E10579", {"start": v(54.78, -33.28) * mm, "end": v(70.95, -33.04) * mm});
            skLineSegment(sketch, "E10580", {"start": v(70.95, -33.04) * mm, "end": v(65.17, -32.82) * mm});
            skLineSegment(sketch, "E10581", {"start": v(65.17, -32.82) * mm, "end": v(65.17, -32.6) * mm});
            skLineSegment(sketch, "E10582", {"start": v(55.7, -2.49) * mm, "end": v(53.43, -2.49) * mm});
            skLineSegment(sketch, "E10583", {"start": v(53.43, -2.49) * mm, "end": v(50.7, -2.49) * mm});
            skLineSegment(sketch, "E10584", {"start": v(50.7, -2.49) * mm, "end": v(50.29, -1.83) * mm});
            skLineSegment(sketch, "E10585", {"start": v(50.29, -1.83) * mm, "end": v(46.99, -1.5) * mm});
            skLineSegment(sketch, "E10586", {"start": v(46.99, -1.5) * mm, "end": v(42.52, -0.6) * mm});
            skLineSegment(sketch, "E10587", {"start": v(42.52, -0.6) * mm, "end": v(40.47, 0.3) * mm});
            skLineSegment(sketch, "E10588", {"start": v(40.47, 0.3) * mm, "end": v(39.62, 0.72) * mm});
            skLineSegment(sketch, "E10589", {"start": v(39.62, 0.72) * mm, "end": v(38.78, 1.17) * mm});
            skLineSegment(sketch, "E10590", {"start": v(38.78, 1.17) * mm, "end": v(38.4, 1.39) * mm});
            skLineSegment(sketch, "E10591", {"start": v(38.4, 1.39) * mm, "end": v(38.06, 1.59) * mm});
            skLineSegment(sketch, "E10592", {"start": v(38.06, 1.59) * mm, "end": v(37.78, 1.77) * mm});
            skLineSegment(sketch, "E10593", {"start": v(37.78, 1.77) * mm, "end": v(37.57, 1.92) * mm});
            skLineSegment(sketch, "E10594", {"start": v(37.57, 1.92) * mm, "end": v(36.8, 2.51) * mm});
            skLineSegment(sketch, "E10595", {"start": v(36.8, 2.51) * mm, "end": v(37.09, 2.7) * mm});
            skLineSegment(sketch, "E10596", {"start": v(37.09, 2.7) * mm, "end": v(37.19, 2.74) * mm});
            skLineSegment(sketch, "E10597", {"start": v(37.19, 2.74) * mm, "end": v(37.31, 2.8) * mm});
            skLineSegment(sketch, "E10598", {"start": v(37.31, 2.8) * mm, "end": v(37.59, 3) * mm});
            skLineSegment(sketch, "E10599", {"start": v(37.59, 3) * mm, "end": v(37.88, 3.24) * mm});
            skLineSegment(sketch, "E10600", {"start": v(37.88, 3.24) * mm, "end": v(38.16, 3.5) * mm});
            skLineSegment(sketch, "E10601", {"start": v(38.16, 3.5) * mm, "end": v(38.78, 4.1) * mm});
            skLineSegment(sketch, "E10602", {"start": v(38.78, 4.1) * mm, "end": v(38.78, 6.67) * mm});
            skLineSegment(sketch, "E10603", {"start": v(38.78, 6.67) * mm, "end": v(43.26, 5.23) * mm});
            skLineSegment(sketch, "E10604", {"start": v(43.26, 5.23) * mm, "end": v(44.08, 4.97) * mm});
            skLineSegment(sketch, "E10605", {"start": v(44.08, 4.97) * mm, "end": v(44.93, 4.7) * mm});
            skLineSegment(sketch, "E10606", {"start": v(44.93, 4.7) * mm, "end": v(45.8, 4.46) * mm});
            skLineSegment(sketch, "E10607", {"start": v(45.8, 4.46) * mm, "end": v(46.68, 4.2) * mm});
            skLineSegment(sketch, "E10608", {"start": v(46.68, 4.2) * mm, "end": v(47.56, 3.97) * mm});
            skLineSegment(sketch, "E10609", {"start": v(47.56, 3.97) * mm, "end": v(48.44, 3.74) * mm});
            skLineSegment(sketch, "E10610", {"start": v(48.44, 3.74) * mm, "end": v(49.3, 3.53) * mm});
            skLineSegment(sketch, "E10611", {"start": v(49.3, 3.53) * mm, "end": v(50.13, 3.32) * mm});
            skLineSegment(sketch, "E10612", {"start": v(50.13, 3.32) * mm, "end": v(50.94, 3.14) * mm});
            skLineSegment(sketch, "E10613", {"start": v(50.94, 3.14) * mm, "end": v(51.7, 2.97) * mm});
            skLineSegment(sketch, "E10614", {"start": v(51.7, 2.97) * mm, "end": v(52.42, 2.82) * mm});
            skLineSegment(sketch, "E10615", {"start": v(52.42, 2.82) * mm, "end": v(53.09, 2.7) * mm});
            skLineSegment(sketch, "E10616", {"start": v(53.09, 2.7) * mm, "end": v(53.68, 2.6) * mm});
            skLineSegment(sketch, "E10617", {"start": v(53.68, 2.6) * mm, "end": v(54.2, 2.52) * mm});
            skLineSegment(sketch, "E10618", {"start": v(54.2, 2.52) * mm, "end": v(54.65, 2.47) * mm});
            skLineSegment(sketch, "E10619", {"start": v(54.65, 2.47) * mm, "end": v(55, 2.45) * mm});
            skLineSegment(sketch, "E10620", {"start": v(55, 2.45) * mm, "end": v(55.15, 2.45) * mm});
            skLineSegment(sketch, "E10621", {"start": v(55.15, 2.45) * mm, "end": v(55.3, 2.44) * mm});
            skLineSegment(sketch, "E10622", {"start": v(55.3, 2.44) * mm, "end": v(55.62, 2.39) * mm});
            skLineSegment(sketch, "E10623", {"start": v(55.62, 2.39) * mm, "end": v(55.76, 2.35) * mm});
            skLineSegment(sketch, "E10624", {"start": v(55.76, 2.35) * mm, "end": v(55.9, 2.31) * mm});
            skLineSegment(sketch, "E10625", {"start": v(55.9, 2.31) * mm, "end": v(56.02, 2.27) * mm});
            skLineSegment(sketch, "E10626", {"start": v(56.02, 2.27) * mm, "end": v(56.12, 2.22) * mm});
            skLineSegment(sketch, "E10627", {"start": v(56.12, 2.22) * mm, "end": v(56.1, 2.16) * mm});
            skLineSegment(sketch, "E10628", {"start": v(56.1, 2.16) * mm, "end": v(55.98, 1.43) * mm});
            skLineSegment(sketch, "E10629", {"start": v(55.98, 1.43) * mm, "end": v(55.88, 0.67) * mm});
            skLineSegment(sketch, "E10630", {"start": v(55.88, 0.67) * mm, "end": v(55.8, -0.12) * mm});
            skLineSegment(sketch, "E10631", {"start": v(55.8, -0.12) * mm, "end": v(55.73, -0.93) * mm});
            skLineSegment(sketch, "E10632", {"start": v(55.73, -0.93) * mm, "end": v(55.7, -1.74) * mm});
            skLineSegment(sketch, "E10633", {"start": v(55.7, -1.74) * mm, "end": v(55.7, -2.49) * mm});
            skLineSegment(sketch, "E10634", {"start": v(49.3, 25.73) * mm, "end": v(49.42, 25.54) * mm});
            skLineSegment(sketch, "E10635", {"start": v(49.42, 25.54) * mm, "end": v(49.67, 25.12) * mm});
            skLineSegment(sketch, "E10636", {"start": v(49.67, 25.12) * mm, "end": v(50.01, 24.57) * mm});
            skLineSegment(sketch, "E10637", {"start": v(50.01, 24.57) * mm, "end": v(50.42, 23.96) * mm});
            skLineSegment(sketch, "E10638", {"start": v(50.42, 23.96) * mm, "end": v(50.86, 23.3) * mm});
            skLineSegment(sketch, "E10639", {"start": v(50.86, 23.3) * mm, "end": v(51.3, 22.6) * mm});
            skLineSegment(sketch, "E10640", {"start": v(51.3, 22.6) * mm, "end": v(51.52, 22.27) * mm});
            skLineSegment(sketch, "E10641", {"start": v(51.52, 22.27) * mm, "end": v(51.74, 21.96) * mm});
            skLineSegment(sketch, "E10642", {"start": v(51.74, 21.96) * mm, "end": v(51.94, 21.69) * mm});
            skLineSegment(sketch, "E10643", {"start": v(51.94, 21.69) * mm, "end": v(52.12, 21.46) * mm});
            skLineSegment(sketch, "E10644", {"start": v(52.12, 21.46) * mm, "end": v(52.45, 21.07) * mm});
            skLineSegment(sketch, "E10645", {"start": v(52.45, 21.07) * mm, "end": v(52.72, 20.72) * mm});
            skLineSegment(sketch, "E10646", {"start": v(52.72, 20.72) * mm, "end": v(52.82, 20.57) * mm});
            skLineSegment(sketch, "E10647", {"start": v(52.82, 20.57) * mm, "end": v(52.9, 20.45) * mm});
            skLineSegment(sketch, "E10648", {"start": v(52.9, 20.45) * mm, "end": v(52.95, 20.35) * mm});
            skLineSegment(sketch, "E10649", {"start": v(52.95, 20.35) * mm, "end": v(52.97, 20.29) * mm});
            skLineSegment(sketch, "E10650", {"start": v(52.97, 20.29) * mm, "end": v(52.98, 20.1) * mm});
            skLineSegment(sketch, "E10651", {"start": v(52.98, 20.1) * mm, "end": v(53.03, 19.82) * mm});
            skLineSegment(sketch, "E10652", {"start": v(53.03, 19.82) * mm, "end": v(53.2, 18.94) * mm});
            skLineSegment(sketch, "E10653", {"start": v(53.2, 18.94) * mm, "end": v(53.44, 17.78) * mm});
            skLineSegment(sketch, "E10654", {"start": v(53.44, 17.78) * mm, "end": v(53.74, 16.44) * mm});
            skLineSegment(sketch, "E10655", {"start": v(53.74, 16.44) * mm, "end": v(54.07, 15.03) * mm});
            skLineSegment(sketch, "E10656", {"start": v(54.07, 15.03) * mm, "end": v(54.4, 13.67) * mm});
            skLineSegment(sketch, "E10657", {"start": v(54.4, 13.67) * mm, "end": v(54.72, 12.46) * mm});
            skLineSegment(sketch, "E10658", {"start": v(54.72, 12.46) * mm, "end": v(54.98, 11.53) * mm});
            skLineSegment(sketch, "E10659", {"start": v(54.98, 11.53) * mm, "end": v(55.14, 11.03) * mm});
            skLineSegment(sketch, "E10660", {"start": v(55.14, 11.03) * mm, "end": v(55.33, 10.46) * mm});
            skLineSegment(sketch, "E10661", {"start": v(55.33, 10.46) * mm, "end": v(55.55, 9.87) * mm});
            skLineSegment(sketch, "E10662", {"start": v(55.55, 9.87) * mm, "end": v(55.79, 9.26) * mm});
            skLineSegment(sketch, "E10663", {"start": v(55.79, 9.26) * mm, "end": v(56.03, 8.65) * mm});
            skLineSegment(sketch, "E10664", {"start": v(56.03, 8.65) * mm, "end": v(56.28, 8.07) * mm});
            skLineSegment(sketch, "E10665", {"start": v(56.28, 8.07) * mm, "end": v(56.53, 7.52) * mm});
            skLineSegment(sketch, "E10666", {"start": v(56.53, 7.52) * mm, "end": v(56.76, 7.03) * mm});
            skLineSegment(sketch, "E10667", {"start": v(56.76, 7.03) * mm, "end": v(57.86, 4.84) * mm});
            skLineSegment(sketch, "E10668", {"start": v(57.86, 4.84) * mm, "end": v(57.6, 4.16) * mm});
            skLineSegment(sketch, "E10669", {"start": v(57.6, 4.16) * mm, "end": v(57.33, 3.43) * mm});
            skLineSegment(sketch, "E10670", {"start": v(57.33, 3.43) * mm, "end": v(57.2, 3.06) * mm});
            skLineSegment(sketch, "E10671", {"start": v(57.2, 3.06) * mm, "end": v(57.07, 2.7) * mm});
            skLineSegment(sketch, "E10672", {"start": v(57.07, 2.7) * mm, "end": v(56.96, 2.34) * mm});
            skLineSegment(sketch, "E10673", {"start": v(56.96, 2.34) * mm, "end": v(56.88, 2) * mm});
            skLineSegment(sketch, "E10674", {"start": v(56.88, 2) * mm, "end": v(56.76, 1.31) * mm});
            skLineSegment(sketch, "E10675", {"start": v(56.76, 1.31) * mm, "end": v(56.66, 0.58) * mm});
            skLineSegment(sketch, "E10676", {"start": v(56.66, 0.58) * mm, "end": v(56.58, -0.2) * mm});
            skLineSegment(sketch, "E10677", {"start": v(56.58, -0.2) * mm, "end": v(56.52, -0.98) * mm});
            skLineSegment(sketch, "E10678", {"start": v(56.52, -0.98) * mm, "end": v(56.49, -1.76) * mm});
            skLineSegment(sketch, "E10679", {"start": v(56.49, -1.76) * mm, "end": v(56.48, -2.54) * mm});
            skLineSegment(sketch, "E10680", {"start": v(56.48, -2.54) * mm, "end": v(56.5, -2.91) * mm});
            skLineSegment(sketch, "E10681", {"start": v(56.5, -2.91) * mm, "end": v(56.5, -3.28) * mm});
            skLineSegment(sketch, "E10682", {"start": v(56.5, -3.28) * mm, "end": v(56.53, -3.63) * mm});
            skLineSegment(sketch, "E10683", {"start": v(56.53, -3.63) * mm, "end": v(56.56, -3.97) * mm});
            skLineSegment(sketch, "E10684", {"start": v(56.56, -3.97) * mm, "end": v(56.59, -4.19) * mm});
            skLineSegment(sketch, "E10685", {"start": v(56.59, -4.19) * mm, "end": v(56.62, -4.4) * mm});
            skLineSegment(sketch, "E10686", {"start": v(56.62, -4.4) * mm, "end": v(56.72, -4.86) * mm});
            skLineSegment(sketch, "E10687", {"start": v(56.72, -4.86) * mm, "end": v(56.84, -5.32) * mm});
            skLineSegment(sketch, "E10688", {"start": v(56.84, -5.32) * mm, "end": v(56.98, -5.8) * mm});
            skLineSegment(sketch, "E10689", {"start": v(56.98, -5.8) * mm, "end": v(57.27, -6.72) * mm});
            skLineSegment(sketch, "E10690", {"start": v(57.27, -6.72) * mm, "end": v(57.4, -7.17) * mm});
            skLineSegment(sketch, "E10691", {"start": v(57.4, -7.17) * mm, "end": v(57.53, -7.6) * mm});
            skLineSegment(sketch, "E10692", {"start": v(57.53, -7.6) * mm, "end": v(57.27, -8.1) * mm});
            skLineSegment(sketch, "E10693", {"start": v(57.27, -8.1) * mm, "end": v(57.2, -8.24) * mm});
            skLineSegment(sketch, "E10694", {"start": v(57.2, -8.24) * mm, "end": v(57.12, -8.48) * mm});
            skLineSegment(sketch, "E10695", {"start": v(57.12, -8.48) * mm, "end": v(56.92, -9.17) * mm});
            skLineSegment(sketch, "E10696", {"start": v(56.92, -9.17) * mm, "end": v(56.68, -10.07) * mm});
            skLineSegment(sketch, "E10697", {"start": v(56.68, -10.07) * mm, "end": v(56.44, -11.07) * mm});
            skLineSegment(sketch, "E10698", {"start": v(56.44, -11.07) * mm, "end": v(56.3, -11.66) * mm});
            skLineSegment(sketch, "E10699", {"start": v(56.3, -11.66) * mm, "end": v(56.14, -12.3) * mm});
            skLineSegment(sketch, "E10700", {"start": v(56.14, -12.3) * mm, "end": v(56, -12.94) * mm});
            skLineSegment(sketch, "E10701", {"start": v(56, -12.94) * mm, "end": v(55.93, -13.25) * mm});
            skLineSegment(sketch, "E10702", {"start": v(55.93, -13.25) * mm, "end": v(55.88, -13.54) * mm});
            skLineSegment(sketch, "E10703", {"start": v(55.88, -13.54) * mm, "end": v(55.83, -14.02) * mm});
            skLineSegment(sketch, "E10704", {"start": v(55.83, -14.02) * mm, "end": v(55.78, -14.5) * mm});
            skLineSegment(sketch, "E10705", {"start": v(55.78, -14.5) * mm, "end": v(55.7, -15.54) * mm});
            skLineSegment(sketch, "E10706", {"start": v(55.7, -15.54) * mm, "end": v(55.65, -16.6) * mm});
            skLineSegment(sketch, "E10707", {"start": v(55.65, -16.6) * mm, "end": v(55.61, -17.7) * mm});
            skLineSegment(sketch, "E10708", {"start": v(55.61, -17.7) * mm, "end": v(55.57, -19.85) * mm});
            skLineSegment(sketch, "E10709", {"start": v(55.57, -19.85) * mm, "end": v(55.54, -20.89) * mm});
            skLineSegment(sketch, "E10710", {"start": v(55.54, -20.89) * mm, "end": v(55.5, -21.86) * mm});
            skLineSegment(sketch, "E10711", {"start": v(55.5, -21.86) * mm, "end": v(45.87, -27.73) * mm});
            skLineSegment(sketch, "E10712", {"start": v(45.87, -27.73) * mm, "end": v(49.48, -27.69) * mm});
            skLineSegment(sketch, "E10713", {"start": v(49.48, -27.69) * mm, "end": v(53.94, -27.53) * mm});
            skLineSegment(sketch, "E10714", {"start": v(53.94, -27.53) * mm, "end": v(55.4, -27.4) * mm});
            skLineSegment(sketch, "E10715", {"start": v(55.4, -27.4) * mm, "end": v(55.52, -26.76) * mm});
            skLineSegment(sketch, "E10716", {"start": v(55.52, -26.76) * mm, "end": v(55.67, -26.1) * mm});
            skLineSegment(sketch, "E10717", {"start": v(55.67, -26.1) * mm, "end": v(55.85, -25.44) * mm});
            skLineSegment(sketch, "E10718", {"start": v(55.85, -25.44) * mm, "end": v(56.05, -24.79) * mm});
            skLineSegment(sketch, "E10719", {"start": v(56.05, -24.79) * mm, "end": v(56.26, -24.14) * mm});
            skLineSegment(sketch, "E10720", {"start": v(56.26, -24.14) * mm, "end": v(56.49, -23.5) * mm});
            skLineSegment(sketch, "E10721", {"start": v(56.49, -23.5) * mm, "end": v(56.72, -22.87) * mm});
            skLineSegment(sketch, "E10722", {"start": v(56.72, -22.87) * mm, "end": v(56.95, -22.27) * mm});
            skLineSegment(sketch, "E10723", {"start": v(56.95, -22.27) * mm, "end": v(57.08, -22.3) * mm});
            skLineSegment(sketch, "E10724", {"start": v(57.08, -22.3) * mm, "end": v(57.2, -22.34) * mm});
            skLineSegment(sketch, "E10725", {"start": v(57.2, -22.34) * mm, "end": v(57.33, -22.4) * mm});
            skLineSegment(sketch, "E10726", {"start": v(57.33, -22.4) * mm, "end": v(57.45, -22.45) * mm});
            skLineSegment(sketch, "E10727", {"start": v(57.45, -22.45) * mm, "end": v(57.5, -22.5) * mm});
            skLineSegment(sketch, "E10728", {"start": v(57.5, -22.5) * mm, "end": v(57.6, -22.59) * mm});
            skLineSegment(sketch, "E10729", {"start": v(57.6, -22.59) * mm, "end": v(57.85, -22.87) * mm});
            skLineSegment(sketch, "E10730", {"start": v(57.85, -22.87) * mm, "end": v(58.17, -23.26) * mm});
            skLineSegment(sketch, "E10731", {"start": v(58.17, -23.26) * mm, "end": v(58.33, -23.48) * mm});
            skLineSegment(sketch, "E10732", {"start": v(58.33, -23.48) * mm, "end": v(58.48, -23.7) * mm});
            skLineSegment(sketch, "E10733", {"start": v(58.48, -23.7) * mm, "end": v(58.66, -23.94) * mm});
            skLineSegment(sketch, "E10734", {"start": v(58.66, -23.94) * mm, "end": v(58.87, -24.22) * mm});
            skLineSegment(sketch, "E10735", {"start": v(58.87, -24.22) * mm, "end": v(59.12, -24.52) * mm});
            skLineSegment(sketch, "E10736", {"start": v(59.12, -24.52) * mm, "end": v(59.39, -24.84) * mm});
            skLineSegment(sketch, "E10737", {"start": v(59.39, -24.84) * mm, "end": v(59.67, -25.16) * mm});
            skLineSegment(sketch, "E10738", {"start": v(59.67, -25.16) * mm, "end": v(59.97, -25.48) * mm});
            skLineSegment(sketch, "E10739", {"start": v(59.97, -25.48) * mm, "end": v(60.26, -25.78) * mm});
            skLineSegment(sketch, "E10740", {"start": v(60.26, -25.78) * mm, "end": v(60.54, -26.07) * mm});
            skLineSegment(sketch, "E10741", {"start": v(60.54, -26.07) * mm, "end": v(60.84, -26.4) * mm});
            skLineSegment(sketch, "E10742", {"start": v(60.84, -26.4) * mm, "end": v(61.16, -26.76) * mm});
            skLineSegment(sketch, "E10743", {"start": v(61.16, -26.76) * mm, "end": v(61.33, -26.94) * mm});
            skLineSegment(sketch, "E10744", {"start": v(61.33, -26.94) * mm, "end": v(61.5, -27.1) * mm});
            skLineSegment(sketch, "E10745", {"start": v(61.5, -27.1) * mm, "end": v(61.68, -27.25) * mm});
            skLineSegment(sketch, "E10746", {"start": v(61.68, -27.25) * mm, "end": v(61.77, -27.3) * mm});
            skLineSegment(sketch, "E10747", {"start": v(61.77, -27.3) * mm, "end": v(61.86, -27.36) * mm});
            skLineSegment(sketch, "E10748", {"start": v(61.86, -27.36) * mm, "end": v(62, -27.42) * mm});
            skLineSegment(sketch, "E10749", {"start": v(62, -27.42) * mm, "end": v(62.17, -27.48) * mm});
            skLineSegment(sketch, "E10750", {"start": v(62.17, -27.48) * mm, "end": v(62.33, -27.53) * mm});
            skLineSegment(sketch, "E10751", {"start": v(62.33, -27.53) * mm, "end": v(62.5, -27.57) * mm});
            skLineSegment(sketch, "E10752", {"start": v(62.5, -27.57) * mm, "end": v(62.86, -27.64) * mm});
            skLineSegment(sketch, "E10753", {"start": v(62.86, -27.64) * mm, "end": v(63.24, -27.68) * mm});
            skLineSegment(sketch, "E10754", {"start": v(63.24, -27.68) * mm, "end": v(63.99, -27.74) * mm});
            skLineSegment(sketch, "E10755", {"start": v(63.99, -27.74) * mm, "end": v(64.35, -27.77) * mm});
            skLineSegment(sketch, "E10756", {"start": v(64.35, -27.77) * mm, "end": v(64.68, -27.82) * mm});
            skLineSegment(sketch, "E10757", {"start": v(64.68, -27.82) * mm, "end": v(61.05, -27.86) * mm});
            skLineSegment(sketch, "E10758", {"start": v(61.05, -27.86) * mm, "end": v(59.13, -27.9) * mm});
            skLineSegment(sketch, "E10759", {"start": v(59.13, -27.9) * mm, "end": v(56.6, -27.95) * mm});
            skLineSegment(sketch, "E10760", {"start": v(56.6, -27.95) * mm, "end": v(53.77, -28.02) * mm});
            skLineSegment(sketch, "E10761", {"start": v(53.77, -28.02) * mm, "end": v(50.99, -28.1) * mm});
            skLineSegment(sketch, "E10762", {"start": v(50.99, -28.1) * mm, "end": v(44.55, -28.3) * mm});
            skLineSegment(sketch, "E10763", {"start": v(44.55, -28.3) * mm, "end": v(43.34, -29.17) * mm});
            skLineSegment(sketch, "E10764", {"start": v(43.34, -29.17) * mm, "end": v(42.69, -29.66) * mm});
            skLineSegment(sketch, "E10765", {"start": v(42.69, -29.66) * mm, "end": v(41.82, -30.34) * mm});
            skLineSegment(sketch, "E10766", {"start": v(41.82, -30.34) * mm, "end": v(40.84, -31.12) * mm});
            skLineSegment(sketch, "E10767", {"start": v(40.84, -31.12) * mm, "end": v(39.87, -31.91) * mm});
            skLineSegment(sketch, "E10768", {"start": v(39.87, -31.91) * mm, "end": v(37.61, -33.78) * mm});
            skLineSegment(sketch, "E10769", {"start": v(37.61, -33.78) * mm, "end": v(34.55, -33.94) * mm});
            skLineSegment(sketch, "E10770", {"start": v(34.55, -33.94) * mm, "end": v(34.33, -36.33) * mm});
            skLineSegment(sketch, "E10771", {"start": v(34.33, -36.33) * mm, "end": v(41.19, -36.4) * mm});
            skLineSegment(sketch, "E10772", {"start": v(41.19, -36.4) * mm, "end": v(44.15, -33.18) * mm});
            skLineSegment(sketch, "E10773", {"start": v(44.15, -33.18) * mm, "end": v(54.76, -33.22) * mm});
            skLineSegment(sketch, "E10774", {"start": v(54.76, -33.22) * mm, "end": v(54.77, -33.28) * mm});
            skLineSegment(sketch, "E10775", {"start": v(54.77, -33.28) * mm, "end": v(44.4, -33.52) * mm});
            skLineSegment(sketch, "E10776", {"start": v(44.4, -33.52) * mm, "end": v(41.58, -36.8) * mm});
            skLineSegment(sketch, "E10777", {"start": v(41.58, -36.8) * mm, "end": v(33.9, -36.8) * mm});
            skLineSegment(sketch, "E10778", {"start": v(33.9, -36.8) * mm, "end": v(32.86, -38.3) * mm});
            skLineSegment(sketch, "E10779", {"start": v(32.86, -38.3) * mm, "end": v(32.43, -36.8) * mm});
            skLineSegment(sketch, "E10780", {"start": v(32.43, -36.8) * mm, "end": v(31.73, -36.81) * mm});
            skLineSegment(sketch, "E10781", {"start": v(31.73, -36.81) * mm, "end": v(31.36, -36.83) * mm});
            skLineSegment(sketch, "E10782", {"start": v(31.36, -36.83) * mm, "end": v(30.87, -36.87) * mm});
            skLineSegment(sketch, "E10783", {"start": v(30.87, -36.87) * mm, "end": v(30.34, -36.94) * mm});
            skLineSegment(sketch, "E10784", {"start": v(30.34, -36.94) * mm, "end": v(29.8, -37.02) * mm});
            skLineSegment(sketch, "E10785", {"start": v(29.8, -37.02) * mm, "end": v(28.6, -37.22) * mm});
            skLineSegment(sketch, "E10786", {"start": v(28.6, -37.22) * mm, "end": v(28.76, -37.64) * mm});
            skLineSegment(sketch, "E10787", {"start": v(28.76, -37.64) * mm, "end": v(28.8, -37.75) * mm});
            skLineSegment(sketch, "E10788", {"start": v(28.8, -37.75) * mm, "end": v(28.83, -37.9) * mm});
            skLineSegment(sketch, "E10789", {"start": v(28.83, -37.9) * mm, "end": v(28.9, -38.26) * mm});
            skLineSegment(sketch, "E10790", {"start": v(28.9, -38.26) * mm, "end": v(28.96, -38.7) * mm});
            skLineSegment(sketch, "E10791", {"start": v(28.96, -38.7) * mm, "end": v(29, -39.17) * mm});
            skLineSegment(sketch, "E10792", {"start": v(29, -39.17) * mm, "end": v(29.1, -40.27) * mm});
            skLineSegment(sketch, "E10793", {"start": v(29.1, -40.27) * mm, "end": v(40.83, -40.03) * mm});
            skLineSegment(sketch, "E10794", {"start": v(40.83, -40.03) * mm, "end": v(45, -44.13) * mm});
            skLineSegment(sketch, "E10795", {"start": v(45, -44.13) * mm, "end": v(50.82, -43.74) * mm});
            skLineSegment(sketch, "E10796", {"start": v(50.82, -43.74) * mm, "end": v(67.26, -43.7) * mm});
            skLineSegment(sketch, "E10797", {"start": v(67.26, -43.7) * mm, "end": v(67.65, -44.3) * mm});
            skLineSegment(sketch, "E10798", {"start": v(67.65, -44.3) * mm, "end": v(70.12, -44.83) * mm});
            skLineSegment(sketch, "E10799", {"start": v(70.12, -44.83) * mm, "end": v(71.25, -45.06) * mm});
            skLineSegment(sketch, "E10800", {"start": v(71.25, -45.06) * mm, "end": v(72.48, -45.27) * mm});
            skLineSegment(sketch, "E10801", {"start": v(72.48, -45.27) * mm, "end": v(73.67, -45.46) * mm});
            skLineSegment(sketch, "E10802", {"start": v(73.67, -45.46) * mm, "end": v(74.2, -45.53) * mm});
            skLineSegment(sketch, "E10803", {"start": v(74.2, -45.53) * mm, "end": v(74.67, -45.58) * mm});
            skLineSegment(sketch, "E10804", {"start": v(74.67, -45.58) * mm, "end": v(76.74, -45.8) * mm});
            skLineSegment(sketch, "E10805", {"start": v(76.74, -45.8) * mm, "end": v(77.05, -46.3) * mm});
            skLineSegment(sketch, "E10806", {"start": v(77.05, -46.3) * mm, "end": v(75.98, -47.1) * mm});
            skLineSegment(sketch, "E10807", {"start": v(75.98, -47.1) * mm, "end": v(75.43, -47.5) * mm});
            skLineSegment(sketch, "E10808", {"start": v(75.43, -47.5) * mm, "end": v(74.87, -47.88) * mm});
            skLineSegment(sketch, "E10809", {"start": v(74.87, -47.88) * mm, "end": v(74.3, -48.25) * mm});
            skLineSegment(sketch, "E10810", {"start": v(74.3, -48.25) * mm, "end": v(73.73, -48.6) * mm});
            skLineSegment(sketch, "E10811", {"start": v(73.73, -48.6) * mm, "end": v(73.14, -48.92) * mm});
            skLineSegment(sketch, "E10812", {"start": v(73.14, -48.92) * mm, "end": v(72.54, -49.24) * mm});
            skLineSegment(sketch, "E10813", {"start": v(72.54, -49.24) * mm, "end": v(71.91, -49.54) * mm});
            skLineSegment(sketch, "E10814", {"start": v(71.91, -49.54) * mm, "end": v(71.27, -49.83) * mm});
            skLineSegment(sketch, "E10815", {"start": v(71.27, -49.83) * mm, "end": v(70.6, -50.1) * mm});
            skLineSegment(sketch, "E10816", {"start": v(70.6, -50.1) * mm, "end": v(69.9, -50.37) * mm});
            skLineSegment(sketch, "E10817", {"start": v(69.9, -50.37) * mm, "end": v(69.18, -50.63) * mm});
            skLineSegment(sketch, "E10818", {"start": v(69.18, -50.63) * mm, "end": v(68.42, -50.88) * mm});
            skLineSegment(sketch, "E10819", {"start": v(68.42, -50.88) * mm, "end": v(67.63, -51.13) * mm});
            skLineSegment(sketch, "E10820", {"start": v(67.63, -51.13) * mm, "end": v(66.8, -51.37) * mm});
            skLineSegment(sketch, "E10821", {"start": v(66.8, -51.37) * mm, "end": v(65.92, -51.6) * mm});
            skLineSegment(sketch, "E10822", {"start": v(65.92, -51.6) * mm, "end": v(65, -51.84) * mm});
            skLineSegment(sketch, "E10823", {"start": v(65, -51.84) * mm, "end": v(64.22, -52.05) * mm});
            skLineSegment(sketch, "E10824", {"start": v(64.22, -52.05) * mm, "end": v(63.37, -52.28) * mm});
            skLineSegment(sketch, "E10825", {"start": v(63.37, -52.28) * mm, "end": v(62.94, -52.4) * mm});
            skLineSegment(sketch, "E10826", {"start": v(62.94, -52.4) * mm, "end": v(62.51, -52.5) * mm});
            skLineSegment(sketch, "E10827", {"start": v(62.51, -52.5) * mm, "end": v(62.1, -52.59) * mm});
            skLineSegment(sketch, "E10828", {"start": v(62.1, -52.59) * mm, "end": v(61.7, -52.66) * mm});
            skLineSegment(sketch, "E10829", {"start": v(61.7, -52.66) * mm, "end": v(60.04, -52.91) * mm});
            skLineSegment(sketch, "E10830", {"start": v(60.04, -52.91) * mm, "end": v(59.15, -53.04) * mm});
            skLineSegment(sketch, "E10831", {"start": v(59.15, -53.04) * mm, "end": v(58.7, -53.1) * mm});
            skLineSegment(sketch, "E10832", {"start": v(58.7, -53.1) * mm, "end": v(58.23, -53.14) * mm});
            skLineSegment(sketch, "E10833", {"start": v(58.23, -53.14) * mm, "end": v(57.78, -53.18) * mm});
            skLineSegment(sketch, "E10834", {"start": v(57.78, -53.18) * mm, "end": v(57.32, -53.2) * mm});
            skLineSegment(sketch, "E10835", {"start": v(57.32, -53.2) * mm, "end": v(56.87, -53.22) * mm});
            skLineSegment(sketch, "E10836", {"start": v(56.87, -53.22) * mm, "end": v(56.43, -53.22) * mm});
            skLineSegment(sketch, "E10837", {"start": v(56.43, -53.22) * mm, "end": v(56, -53.2) * mm});
            skLineSegment(sketch, "E10838", {"start": v(56, -53.2) * mm, "end": v(55.58, -53.17) * mm});
            skLineSegment(sketch, "E10839", {"start": v(55.58, -53.17) * mm, "end": v(55.17, -53.12) * mm});
            skLineSegment(sketch, "E10840", {"start": v(55.17, -53.12) * mm, "end": v(54.78, -53.04) * mm});
            skLineSegment(sketch, "E10841", {"start": v(54.78, -53.04) * mm, "end": v(54.56, -52.99) * mm});
            skLineSegment(sketch, "E10842", {"start": v(54.56, -52.99) * mm, "end": v(54.34, -52.92) * mm});
            skLineSegment(sketch, "E10843", {"start": v(54.34, -52.92) * mm, "end": v(54.12, -52.83) * mm});
            skLineSegment(sketch, "E10844", {"start": v(54.12, -52.83) * mm, "end": v(53.9, -52.74) * mm});
            skLineSegment(sketch, "E10845", {"start": v(53.9, -52.74) * mm, "end": v(53.67, -52.63) * mm});
            skLineSegment(sketch, "E10846", {"start": v(53.67, -52.63) * mm, "end": v(53.44, -52.52) * mm});
            skLineSegment(sketch, "E10847", {"start": v(53.44, -52.52) * mm, "end": v(53, -52.27) * mm});
            skLineSegment(sketch, "E10848", {"start": v(53, -52.27) * mm, "end": v(52.55, -52) * mm});
            skLineSegment(sketch, "E10849", {"start": v(52.55, -52) * mm, "end": v(52.13, -51.71) * mm});
            skLineSegment(sketch, "E10850", {"start": v(52.13, -51.71) * mm, "end": v(51.35, -51.16) * mm});
            skLineSegment(sketch, "E10851", {"start": v(51.35, -51.16) * mm, "end": v(51.14, -51) * mm});
            skLineSegment(sketch, "E10852", {"start": v(51.14, -51) * mm, "end": v(50.93, -50.8) * mm});
            skLineSegment(sketch, "E10853", {"start": v(50.93, -50.8) * mm, "end": v(50.5, -50.4) * mm});
            skLineSegment(sketch, "E10854", {"start": v(50.5, -50.4) * mm, "end": v(50.08, -49.96) * mm});
            skLineSegment(sketch, "E10855", {"start": v(50.08, -49.96) * mm, "end": v(49.68, -49.57) * mm});
            skLineSegment(sketch, "E10856", {"start": v(49.68, -49.57) * mm, "end": v(49.35, -49.25) * mm});
            skLineSegment(sketch, "E10857", {"start": v(49.35, -49.25) * mm, "end": v(49.04, -48.93) * mm});
            skLineSegment(sketch, "E10858", {"start": v(49.04, -48.93) * mm, "end": v(48.75, -48.64) * mm});
            skLineSegment(sketch, "E10859", {"start": v(48.75, -48.64) * mm, "end": v(48.5, -48.37) * mm});
            skLineSegment(sketch, "E10860", {"start": v(48.5, -48.37) * mm, "end": v(48.3, -48.13) * mm});
            skLineSegment(sketch, "E10861", {"start": v(48.3, -48.13) * mm, "end": v(48.15, -47.94) * mm});
            skLineSegment(sketch, "E10862", {"start": v(48.15, -47.94) * mm, "end": v(48.05, -47.8) * mm});
            skLineSegment(sketch, "E10863", {"start": v(48.05, -47.8) * mm, "end": v(48.02, -47.75) * mm});
            skLineSegment(sketch, "E10864", {"start": v(48.02, -47.75) * mm, "end": v(48.02, -47.71) * mm});
            skLineSegment(sketch, "E10865", {"start": v(48.02, -47.71) * mm, "end": v(48.02, -47.44) * mm});
            skLineSegment(sketch, "E10866", {"start": v(48.02, -47.44) * mm, "end": v(54.78, -44.6) * mm});
            skLineSegment(sketch, "E10867", {"start": v(54.78, -44.6) * mm, "end": v(55.42, -44.06) * mm});
            skLineSegment(sketch, "E10868", {"start": v(55.42, -44.06) * mm, "end": v(44.88, -44.45) * mm});
            skLineSegment(sketch, "E10869", {"start": v(44.88, -44.45) * mm, "end": v(42.4, -43.85) * mm});
            skLineSegment(sketch, "E10870", {"start": v(42.4, -43.85) * mm, "end": v(40.86, -43.71) * mm});
            skLineSegment(sketch, "E10871", {"start": v(40.86, -43.71) * mm, "end": v(40.28, -43.7) * mm});
            skLineSegment(sketch, "E10872", {"start": v(40.28, -43.7) * mm, "end": v(39.66, -43.7) * mm});
            skLineSegment(sketch, "E10873", {"start": v(39.66, -43.7) * mm, "end": v(39, -43.7) * mm});
            skLineSegment(sketch, "E10874", {"start": v(39, -43.7) * mm, "end": v(38.64, -43.72) * mm});
            skLineSegment(sketch, "E10875", {"start": v(38.64, -43.72) * mm, "end": v(38.28, -43.74) * mm});
            skLineSegment(sketch, "E10876", {"start": v(38.28, -43.74) * mm, "end": v(37.9, -43.78) * mm});
            skLineSegment(sketch, "E10877", {"start": v(37.9, -43.78) * mm, "end": v(37.5, -43.82) * mm});
            skLineSegment(sketch, "E10878", {"start": v(37.5, -43.82) * mm, "end": v(37.08, -43.88) * mm});
            skLineSegment(sketch, "E10879", {"start": v(37.08, -43.88) * mm, "end": v(36.64, -43.96) * mm});
            skLineSegment(sketch, "E10880", {"start": v(36.64, -43.96) * mm, "end": v(36.19, -44.06) * mm});
            skLineSegment(sketch, "E10881", {"start": v(36.19, -44.06) * mm, "end": v(35.71, -44.17) * mm});
            skLineSegment(sketch, "E10882", {"start": v(35.71, -44.17) * mm, "end": v(35.22, -44.31) * mm});
            skLineSegment(sketch, "E10883", {"start": v(35.22, -44.31) * mm, "end": v(34.7, -44.47) * mm});
            skLineSegment(sketch, "E10884", {"start": v(34.7, -44.47) * mm, "end": v(31.86, -45.41) * mm});
            skLineSegment(sketch, "E10885", {"start": v(31.86, -45.41) * mm, "end": v(31.72, -44.26) * mm});
            skLineSegment(sketch, "E10886", {"start": v(31.72, -44.26) * mm, "end": v(31.73, -44.15) * mm});
            skLineSegment(sketch, "E10887", {"start": v(31.73, -44.15) * mm, "end": v(31.75, -43.99) * mm});
            skLineSegment(sketch, "E10888", {"start": v(31.75, -43.99) * mm, "end": v(31.78, -43.79) * mm});
            skLineSegment(sketch, "E10889", {"start": v(31.78, -43.79) * mm, "end": v(31.83, -43.56) * mm});
            skLineSegment(sketch, "E10890", {"start": v(31.83, -43.56) * mm, "end": v(31.9, -43.3) * mm});
            skLineSegment(sketch, "E10891", {"start": v(31.9, -43.3) * mm, "end": v(31.98, -43.03) * mm});
            skLineSegment(sketch, "E10892", {"start": v(31.98, -43.03) * mm, "end": v(32.08, -42.74) * mm});
            skLineSegment(sketch, "E10893", {"start": v(32.08, -42.74) * mm, "end": v(32.2, -42.45) * mm});
            skLineSegment(sketch, "E10894", {"start": v(32.2, -42.45) * mm, "end": v(32.45, -41.89) * mm});
            skLineSegment(sketch, "E10895", {"start": v(32.45, -41.89) * mm, "end": v(32.65, -41.4) * mm});
            skLineSegment(sketch, "E10896", {"start": v(32.65, -41.4) * mm, "end": v(32.79, -41.06) * mm});
            skLineSegment(sketch, "E10897", {"start": v(32.79, -41.06) * mm, "end": v(32.82, -40.95) * mm});
            skLineSegment(sketch, "E10898", {"start": v(32.82, -40.95) * mm, "end": v(32.84, -40.9) * mm});
            skLineSegment(sketch, "E10899", {"start": v(32.84, -40.9) * mm, "end": v(32.83, -40.88) * mm});
            skLineSegment(sketch, "E10900", {"start": v(32.83, -40.88) * mm, "end": v(32.8, -40.87) * mm});
            skLineSegment(sketch, "E10901", {"start": v(32.8, -40.87) * mm, "end": v(32.67, -40.85) * mm});
            skLineSegment(sketch, "E10902", {"start": v(32.67, -40.85) * mm, "end": v(32.48, -40.82) * mm});
            skLineSegment(sketch, "E10903", {"start": v(32.48, -40.82) * mm, "end": v(32.22, -40.8) * mm});
            skLineSegment(sketch, "E10904", {"start": v(32.22, -40.8) * mm, "end": v(31.55, -40.78) * mm});
            skLineSegment(sketch, "E10905", {"start": v(31.55, -40.78) * mm, "end": v(30.73, -40.77) * mm});
            skLineSegment(sketch, "E10906", {"start": v(30.73, -40.77) * mm, "end": v(28.62, -40.77) * mm});
            skLineSegment(sketch, "E10907", {"start": v(28.62, -40.77) * mm, "end": v(28.24, -41.75) * mm});
            skLineSegment(sketch, "E10908", {"start": v(28.24, -41.75) * mm, "end": v(27.37, -41.4) * mm});
            skLineSegment(sketch, "E10909", {"start": v(27.37, -41.4) * mm, "end": v(23.52, -44.4) * mm});
            skLineSegment(sketch, "E10910", {"start": v(23.52, -44.4) * mm, "end": v(16.04, -44.4) * mm});
            skLineSegment(sketch, "E10911", {"start": v(16.04, -44.4) * mm, "end": v(15.83, -45.63) * mm});
            skLineSegment(sketch, "E10912", {"start": v(15.83, -45.63) * mm, "end": v(15.72, -46.2) * mm});
            skLineSegment(sketch, "E10913", {"start": v(15.72, -46.2) * mm, "end": v(15.6, -46.83) * mm});
            skLineSegment(sketch, "E10914", {"start": v(15.6, -46.83) * mm, "end": v(15.46, -47.45) * mm});
            skLineSegment(sketch, "E10915", {"start": v(15.46, -47.45) * mm, "end": v(15.33, -47.98) * mm});
            skLineSegment(sketch, "E10916", {"start": v(15.33, -47.98) * mm, "end": v(15.05, -49.1) * mm});
            skLineSegment(sketch, "E10917", {"start": v(15.05, -49.1) * mm, "end": v(16.6, -49) * mm});
            skLineSegment(sketch, "E10918", {"start": v(16.6, -49) * mm, "end": v(18.26, -48.92) * mm});
            skLineSegment(sketch, "E10919", {"start": v(18.26, -48.92) * mm, "end": v(19.1, -48.87) * mm});
            skLineSegment(sketch, "E10920", {"start": v(19.1, -48.87) * mm, "end": v(19.92, -48.81) * mm});
            skLineSegment(sketch, "E10921", {"start": v(19.92, -48.81) * mm, "end": v(20.7, -48.74) * mm});
            skLineSegment(sketch, "E10922", {"start": v(20.7, -48.74) * mm, "end": v(21.45, -48.66) * mm});
            skLineSegment(sketch, "E10923", {"start": v(21.45, -48.66) * mm, "end": v(21.86, -48.6) * mm});
            skLineSegment(sketch, "E10924", {"start": v(21.86, -48.6) * mm, "end": v(22.3, -48.5) * mm});
            skLineSegment(sketch, "E10925", {"start": v(22.3, -48.5) * mm, "end": v(23.15, -48.33) * mm});
            skLineSegment(sketch, "E10926", {"start": v(23.15, -48.33) * mm, "end": v(23.33, -48.97) * mm});
            skLineSegment(sketch, "E10927", {"start": v(23.33, -48.97) * mm, "end": v(23.5, -49.66) * mm});
            skLineSegment(sketch, "E10928", {"start": v(23.5, -49.66) * mm, "end": v(23.6, -50) * mm});
            skLineSegment(sketch, "E10929", {"start": v(23.6, -50) * mm, "end": v(23.7, -50.34) * mm});
            skLineSegment(sketch, "E10930", {"start": v(23.7, -50.34) * mm, "end": v(23.82, -50.66) * mm});
            skLineSegment(sketch, "E10931", {"start": v(23.82, -50.66) * mm, "end": v(23.94, -50.96) * mm});
            skLineSegment(sketch, "E10932", {"start": v(23.94, -50.96) * mm, "end": v(24.1, -51.28) * mm});
            skLineSegment(sketch, "E10933", {"start": v(24.1, -51.28) * mm, "end": v(24.27, -51.6) * mm});
            skLineSegment(sketch, "E10934", {"start": v(24.27, -51.6) * mm, "end": v(24.45, -51.93) * mm});
            skLineSegment(sketch, "E10935", {"start": v(24.45, -51.93) * mm, "end": v(24.65, -52.27) * mm});
            skLineSegment(sketch, "E10936", {"start": v(24.65, -52.27) * mm, "end": v(25.07, -52.95) * mm});
            skLineSegment(sketch, "E10937", {"start": v(25.07, -52.95) * mm, "end": v(25.52, -53.62) * mm});
            skLineSegment(sketch, "E10938", {"start": v(25.52, -53.62) * mm, "end": v(26, -54.3) * mm});
            skLineSegment(sketch, "E10939", {"start": v(26, -54.3) * mm, "end": v(26.47, -54.93) * mm});
            skLineSegment(sketch, "E10940", {"start": v(26.47, -54.93) * mm, "end": v(26.94, -55.54) * mm});
            skLineSegment(sketch, "E10941", {"start": v(26.94, -55.54) * mm, "end": v(27.4, -56.11) * mm});
            skLineSegment(sketch, "E10942", {"start": v(27.4, -56.11) * mm, "end": v(27.78, -56.57) * mm});
            skLineSegment(sketch, "E10943", {"start": v(27.78, -56.57) * mm, "end": v(28.19, -57.03) * mm});
            skLineSegment(sketch, "E10944", {"start": v(28.19, -57.03) * mm, "end": v(28.62, -57.5) * mm});
            skLineSegment(sketch, "E10945", {"start": v(28.62, -57.5) * mm, "end": v(29.06, -57.98) * mm});
            skLineSegment(sketch, "E10946", {"start": v(29.06, -57.98) * mm, "end": v(30, -58.94) * mm});
            skLineSegment(sketch, "E10947", {"start": v(30, -58.94) * mm, "end": v(30.98, -59.9) * mm});
            skLineSegment(sketch, "E10948", {"start": v(30.98, -59.9) * mm, "end": v(32.93, -61.78) * mm});
            skLineSegment(sketch, "E10949", {"start": v(32.93, -61.78) * mm, "end": v(33.86, -62.68) * mm});
            skLineSegment(sketch, "E10950", {"start": v(33.86, -62.68) * mm, "end": v(34.73, -63.54) * mm});
            skLineSegment(sketch, "E10951", {"start": v(34.73, -63.54) * mm, "end": v(34.03, -63.53) * mm});
            skLineSegment(sketch, "E10952", {"start": v(34.03, -63.53) * mm, "end": v(33.75, -63.52) * mm});
            skLineSegment(sketch, "E10953", {"start": v(33.75, -63.52) * mm, "end": v(33.4, -63.5) * mm});
            skLineSegment(sketch, "E10954", {"start": v(33.4, -63.5) * mm, "end": v(32.99, -63.44) * mm});
            skLineSegment(sketch, "E10955", {"start": v(32.99, -63.44) * mm, "end": v(32.51, -63.38) * mm});
            skLineSegment(sketch, "E10956", {"start": v(32.51, -63.38) * mm, "end": v(31.43, -63.2) * mm});
            skLineSegment(sketch, "E10957", {"start": v(31.43, -63.2) * mm, "end": v(30.22, -62.97) * mm});
            skLineSegment(sketch, "E10958", {"start": v(30.22, -62.97) * mm, "end": v(28.95, -62.72) * mm});
            skLineSegment(sketch, "E10959", {"start": v(28.95, -62.72) * mm, "end": v(27.7, -62.44) * mm});
            skLineSegment(sketch, "E10960", {"start": v(27.7, -62.44) * mm, "end": v(26.53, -62.15) * mm});
            skLineSegment(sketch, "E10961", {"start": v(26.53, -62.15) * mm, "end": v(26, -62.01) * mm});
            skLineSegment(sketch, "E10962", {"start": v(26, -62.01) * mm, "end": v(25.5, -61.87) * mm});
            skLineSegment(sketch, "E10963", {"start": v(25.5, -61.87) * mm, "end": v(24.92, -61.71) * mm});
            skLineSegment(sketch, "E10964", {"start": v(24.92, -61.71) * mm, "end": v(24.3, -61.54) * mm});
            skLineSegment(sketch, "E10965", {"start": v(24.3, -61.54) * mm, "end": v(23.67, -61.36) * mm});
            skLineSegment(sketch, "E10966", {"start": v(23.67, -61.36) * mm, "end": v(23.38, -61.27) * mm});
            skLineSegment(sketch, "E10967", {"start": v(23.38, -61.27) * mm, "end": v(23.1, -61.16) * mm});
            skLineSegment(sketch, "E10968", {"start": v(23.1, -61.16) * mm, "end": v(22.4, -60.87) * mm});
            skLineSegment(sketch, "E10969", {"start": v(22.4, -60.87) * mm, "end": v(21.65, -60.54) * mm});
            skLineSegment(sketch, "E10970", {"start": v(21.65, -60.54) * mm, "end": v(20.89, -60.17) * mm});
            skLineSegment(sketch, "E10971", {"start": v(20.89, -60.17) * mm, "end": v(20.12, -59.79) * mm});
            skLineSegment(sketch, "E10972", {"start": v(20.12, -59.79) * mm, "end": v(19.36, -59.38) * mm});
            skLineSegment(sketch, "E10973", {"start": v(19.36, -59.38) * mm, "end": v(18.62, -58.97) * mm});
            skLineSegment(sketch, "E10974", {"start": v(18.62, -58.97) * mm, "end": v(17.93, -58.54) * mm});
            skLineSegment(sketch, "E10975", {"start": v(17.93, -58.54) * mm, "end": v(17.6, -58.33) * mm});
            skLineSegment(sketch, "E10976", {"start": v(17.6, -58.33) * mm, "end": v(17.29, -58.12) * mm});
            skLineSegment(sketch, "E10977", {"start": v(17.29, -58.12) * mm, "end": v(17.04, -57.94) * mm});
            skLineSegment(sketch, "E10978", {"start": v(17.04, -57.94) * mm, "end": v(16.8, -57.75) * mm});
            skLineSegment(sketch, "E10979", {"start": v(16.8, -57.75) * mm, "end": v(16.28, -57.32) * mm});
            skLineSegment(sketch, "E10980", {"start": v(16.28, -57.32) * mm, "end": v(15.78, -56.87) * mm});
            skLineSegment(sketch, "E10981", {"start": v(15.78, -56.87) * mm, "end": v(15.27, -56.4) * mm});
            skLineSegment(sketch, "E10982", {"start": v(15.27, -56.4) * mm, "end": v(14.27, -55.43) * mm});
            skLineSegment(sketch, "E10983", {"start": v(14.27, -55.43) * mm, "end": v(13.8, -54.97) * mm});
            skLineSegment(sketch, "E10984", {"start": v(13.8, -54.97) * mm, "end": v(13.34, -54.54) * mm});
            skLineSegment(sketch, "E10985", {"start": v(13.34, -54.54) * mm, "end": v(13.26, -54.67) * mm});
            skLineSegment(sketch, "E10986", {"start": v(13.26, -54.67) * mm, "end": v(13.2, -54.8) * mm});
            skLineSegment(sketch, "E10987", {"start": v(13.2, -54.8) * mm, "end": v(13.07, -55.04) * mm});
            skLineSegment(sketch, "E10988", {"start": v(13.07, -55.04) * mm, "end": v(12.76, -55.76) * mm});
            skLineSegment(sketch, "E10989", {"start": v(12.76, -55.76) * mm, "end": v(12.34, -56.72) * mm});
            skLineSegment(sketch, "E10990", {"start": v(12.34, -56.72) * mm, "end": v(12.92, -57.08) * mm});
            skLineSegment(sketch, "E10991", {"start": v(12.92, -57.08) * mm, "end": v(13.51, -57.43) * mm});
            skLineSegment(sketch, "E10992", {"start": v(13.51, -57.43) * mm, "end": v(15.4, -58.54) * mm});
            skLineSegment(sketch, "E10993", {"start": v(15.4, -58.54) * mm, "end": v(16.41, -59.14) * mm});
            skLineSegment(sketch, "E10994", {"start": v(16.41, -59.14) * mm, "end": v(17.44, -59.74) * mm});
            skLineSegment(sketch, "E10995", {"start": v(17.44, -59.74) * mm, "end": v(18.48, -60.33) * mm});
            skLineSegment(sketch, "E10996", {"start": v(18.48, -60.33) * mm, "end": v(19.5, -60.9) * mm});
            skLineSegment(sketch, "E10997", {"start": v(19.5, -60.9) * mm, "end": v(20.5, -61.42) * mm});
            skLineSegment(sketch, "E10998", {"start": v(20.5, -61.42) * mm, "end": v(20.98, -61.67) * mm});
            skLineSegment(sketch, "E10999", {"start": v(20.98, -61.67) * mm, "end": v(21.45, -61.9) * mm});
            skLineSegment(sketch, "E11000", {"start": v(21.45, -61.9) * mm, "end": v(21.75, -62.03) * mm});
            skLineSegment(sketch, "E11001", {"start": v(21.75, -62.03) * mm, "end": v(22.08, -62.17) * mm});
            skLineSegment(sketch, "E11002", {"start": v(22.08, -62.17) * mm, "end": v(22.76, -62.44) * mm});
            skLineSegment(sketch, "E11003", {"start": v(22.76, -62.44) * mm, "end": v(23.45, -62.7) * mm});
            skLineSegment(sketch, "E11004", {"start": v(23.45, -62.7) * mm, "end": v(24.1, -62.93) * mm});
            skLineSegment(sketch, "E11005", {"start": v(24.1, -62.93) * mm, "end": v(25.27, -63.38) * mm});
            skLineSegment(sketch, "E11006", {"start": v(25.27, -63.38) * mm, "end": v(26.54, -63.84) * mm});
            skLineSegment(sketch, "E11007", {"start": v(26.54, -63.84) * mm, "end": v(27.74, -64.25) * mm});
            skLineSegment(sketch, "E11008", {"start": v(27.74, -64.25) * mm, "end": v(28.26, -64.42) * mm});
            skLineSegment(sketch, "E11009", {"start": v(28.26, -64.42) * mm, "end": v(28.71, -64.55) * mm});
            skLineSegment(sketch, "E11010", {"start": v(28.71, -64.55) * mm, "end": v(29.19, -64.7) * mm});
            skLineSegment(sketch, "E11011", {"start": v(29.19, -64.7) * mm, "end": v(29.7, -64.88) * mm});
            skLineSegment(sketch, "E11012", {"start": v(29.7, -64.88) * mm, "end": v(29.95, -64.96) * mm});
            skLineSegment(sketch, "E11013", {"start": v(29.95, -64.96) * mm, "end": v(30.2, -65.03) * mm});
            skLineSegment(sketch, "E11014", {"start": v(30.2, -65.03) * mm, "end": v(30.46, -65.1) * mm});
            skLineSegment(sketch, "E11015", {"start": v(30.46, -65.1) * mm, "end": v(30.7, -65.14) * mm});
            skLineSegment(sketch, "E11016", {"start": v(30.7, -65.14) * mm, "end": v(31.34, -65.24) * mm});
            skLineSegment(sketch, "E11017", {"start": v(31.34, -65.24) * mm, "end": v(32.04, -65.36) * mm});
            skLineSegment(sketch, "E11018", {"start": v(32.04, -65.36) * mm, "end": v(32.4, -65.4) * mm});
            skLineSegment(sketch, "E11019", {"start": v(32.4, -65.4) * mm, "end": v(32.75, -65.45) * mm});
            skLineSegment(sketch, "E11020", {"start": v(32.75, -65.45) * mm, "end": v(33.08, -65.48) * mm});
            skLineSegment(sketch, "E11021", {"start": v(33.08, -65.48) * mm, "end": v(33.4, -65.5) * mm});
            skLineSegment(sketch, "E11022", {"start": v(33.4, -65.5) * mm, "end": v(33.7, -65.5) * mm});
            skLineSegment(sketch, "E11023", {"start": v(33.7, -65.5) * mm, "end": v(34.03, -65.48) * mm});
            skLineSegment(sketch, "E11024", {"start": v(34.03, -65.48) * mm, "end": v(34.37, -65.46) * mm});
            skLineSegment(sketch, "E11025", {"start": v(34.37, -65.46) * mm, "end": v(34.72, -65.43) * mm});
            skLineSegment(sketch, "E11026", {"start": v(34.72, -65.43) * mm, "end": v(35.06, -65.4) * mm});
            skLineSegment(sketch, "E11027", {"start": v(35.06, -65.4) * mm, "end": v(35.4, -65.34) * mm});
            skLineSegment(sketch, "E11028", {"start": v(35.4, -65.34) * mm, "end": v(35.71, -65.27) * mm});
            skLineSegment(sketch, "E11029", {"start": v(35.71, -65.27) * mm, "end": v(36.01, -65.19) * mm});
            skLineSegment(sketch, "E11030", {"start": v(36.01, -65.19) * mm, "end": v(36.19, -65.12) * mm});
            skLineSegment(sketch, "E11031", {"start": v(36.19, -65.12) * mm, "end": v(36.38, -65.05) * mm});
            skLineSegment(sketch, "E11032", {"start": v(36.38, -65.05) * mm, "end": v(36.57, -64.95) * mm});
            skLineSegment(sketch, "E11033", {"start": v(36.57, -64.95) * mm, "end": v(36.76, -64.84) * mm});
            skLineSegment(sketch, "E11034", {"start": v(36.76, -64.84) * mm, "end": v(36.93, -64.72) * mm});
            skLineSegment(sketch, "E11035", {"start": v(36.93, -64.72) * mm, "end": v(37.01, -64.65) * mm});
            skLineSegment(sketch, "E11036", {"start": v(37.01, -64.65) * mm, "end": v(37.08, -64.58) * mm});
            skLineSegment(sketch, "E11037", {"start": v(37.08, -64.58) * mm, "end": v(37.14, -64.5) * mm});
            skLineSegment(sketch, "E11038", {"start": v(37.14, -64.5) * mm, "end": v(37.2, -64.43) * mm});
            skLineSegment(sketch, "E11039", {"start": v(37.2, -64.43) * mm, "end": v(37.24, -64.35) * mm});
            skLineSegment(sketch, "E11040", {"start": v(37.24, -64.35) * mm, "end": v(37.27, -64.27) * mm});
            skLineSegment(sketch, "E11041", {"start": v(37.27, -64.27) * mm, "end": v(37.28, -64.16) * mm});
            skLineSegment(sketch, "E11042", {"start": v(37.28, -64.16) * mm, "end": v(37.28, -64.05) * mm});
            skLineSegment(sketch, "E11043", {"start": v(37.28, -64.05) * mm, "end": v(37.26, -63.95) * mm});
            skLineSegment(sketch, "E11044", {"start": v(37.26, -63.95) * mm, "end": v(37.22, -63.84) * mm});
            skLineSegment(sketch, "E11045", {"start": v(37.22, -63.84) * mm, "end": v(37.17, -63.73) * mm});
            skLineSegment(sketch, "E11046", {"start": v(37.17, -63.73) * mm, "end": v(37.1, -63.62) * mm});
            skLineSegment(sketch, "E11047", {"start": v(37.1, -63.62) * mm, "end": v(36.97, -63.4) * mm});
            skLineSegment(sketch, "E11048", {"start": v(36.97, -63.4) * mm, "end": v(36.81, -63.17) * mm});
            skLineSegment(sketch, "E11049", {"start": v(36.81, -63.17) * mm, "end": v(36.66, -62.95) * mm});
            skLineSegment(sketch, "E11050", {"start": v(36.66, -62.95) * mm, "end": v(36.6, -62.84) * mm});
            skLineSegment(sketch, "E11051", {"start": v(36.6, -62.84) * mm, "end": v(36.54, -62.73) * mm});
            skLineSegment(sketch, "E11052", {"start": v(36.54, -62.73) * mm, "end": v(36.5, -62.62) * mm});
            skLineSegment(sketch, "E11053", {"start": v(36.5, -62.62) * mm, "end": v(36.47, -62.51) * mm});
            skLineSegment(sketch, "E11054", {"start": v(36.47, -62.51) * mm, "end": v(36.41, -62.25) * mm});
            skLineSegment(sketch, "E11055", {"start": v(36.41, -62.25) * mm, "end": v(36.36, -61.97) * mm});
            skLineSegment(sketch, "E11056", {"start": v(36.36, -61.97) * mm, "end": v(36.32, -61.67) * mm});
            skLineSegment(sketch, "E11057", {"start": v(36.32, -61.67) * mm, "end": v(36.3, -61.37) * mm});
            skLineSegment(sketch, "E11058", {"start": v(36.3, -61.37) * mm, "end": v(36.29, -61.07) * mm});
            skLineSegment(sketch, "E11059", {"start": v(36.29, -61.07) * mm, "end": v(36.3, -60.92) * mm});
            skLineSegment(sketch, "E11060", {"start": v(36.3, -60.92) * mm, "end": v(36.3, -60.78) * mm});
            skLineSegment(sketch, "E11061", {"start": v(36.3, -60.78) * mm, "end": v(36.33, -60.64) * mm});
            skLineSegment(sketch, "E11062", {"start": v(36.33, -60.64) * mm, "end": v(36.37, -60.51) * mm});
            skLineSegment(sketch, "E11063", {"start": v(36.37, -60.51) * mm, "end": v(36.41, -60.39) * mm});
            skLineSegment(sketch, "E11064", {"start": v(36.41, -60.39) * mm, "end": v(36.47, -60.27) * mm});
            skLineSegment(sketch, "E11065", {"start": v(36.47, -60.27) * mm, "end": v(36.51, -60.2) * mm});
            skLineSegment(sketch, "E11066", {"start": v(36.51, -60.2) * mm, "end": v(36.58, -60.14) * mm});
            skLineSegment(sketch, "E11067", {"start": v(36.58, -60.14) * mm, "end": v(36.65, -60.08) * mm});
            skLineSegment(sketch, "E11068", {"start": v(36.65, -60.08) * mm, "end": v(36.74, -60.03) * mm});
            skLineSegment(sketch, "E11069", {"start": v(36.74, -60.03) * mm, "end": v(36.91, -59.94) * mm});
            skLineSegment(sketch, "E11070", {"start": v(36.91, -59.94) * mm, "end": v(37.09, -59.9) * mm});
            skLineSegment(sketch, "E11071", {"start": v(37.09, -59.9) * mm, "end": v(37.33, -59.85) * mm});
            skLineSegment(sketch, "E11072", {"start": v(37.33, -59.85) * mm, "end": v(37.59, -59.82) * mm});
            skLineSegment(sketch, "E11073", {"start": v(37.59, -59.82) * mm, "end": v(37.84, -59.8) * mm});
            skLineSegment(sketch, "E11074", {"start": v(37.84, -59.8) * mm, "end": v(38.1, -59.8) * mm});
            skLineSegment(sketch, "E11075", {"start": v(38.1, -59.8) * mm, "end": v(38.37, -59.8) * mm});
            skLineSegment(sketch, "E11076", {"start": v(38.37, -59.8) * mm, "end": v(38.64, -59.81) * mm});
            skLineSegment(sketch, "E11077", {"start": v(38.64, -59.81) * mm, "end": v(38.91, -59.83) * mm});
            skLineSegment(sketch, "E11078", {"start": v(38.91, -59.83) * mm, "end": v(39.19, -59.86) * mm});
            skLineSegment(sketch, "E11079", {"start": v(39.19, -59.86) * mm, "end": v(39.75, -59.95) * mm});
            skLineSegment(sketch, "E11080", {"start": v(39.75, -59.95) * mm, "end": v(40.31, -60.06) * mm});
            skLineSegment(sketch, "E11081", {"start": v(40.31, -60.06) * mm, "end": v(40.89, -60.18) * mm});
            skLineSegment(sketch, "E11082", {"start": v(40.89, -60.18) * mm, "end": v(41.46, -60.33) * mm});
            skLineSegment(sketch, "E11083", {"start": v(41.46, -60.33) * mm, "end": v(42.61, -60.63) * mm});
            skLineSegment(sketch, "E11084", {"start": v(42.61, -60.63) * mm, "end": v(43.74, -60.93) * mm});
            skLineSegment(sketch, "E11085", {"start": v(43.74, -60.93) * mm, "end": v(44.3, -61.06) * mm});
            skLineSegment(sketch, "E11086", {"start": v(44.3, -61.06) * mm, "end": v(44.84, -61.17) * mm});
            skLineSegment(sketch, "E11087", {"start": v(44.84, -61.17) * mm, "end": v(45.36, -61.26) * mm});
            skLineSegment(sketch, "E11088", {"start": v(45.36, -61.26) * mm, "end": v(45.62, -61.3) * mm});
            skLineSegment(sketch, "E11089", {"start": v(45.62, -61.3) * mm, "end": v(45.87, -61.32) * mm});
            skLineSegment(sketch, "E11090", {"start": v(45.87, -61.32) * mm, "end": v(47.18, -61.43) * mm});
            skLineSegment(sketch, "E11091", {"start": v(47.18, -61.43) * mm, "end": v(48.58, -61.55) * mm});
            skLineSegment(sketch, "E11092", {"start": v(48.58, -61.55) * mm, "end": v(50.03, -61.65) * mm});
            skLineSegment(sketch, "E11093", {"start": v(50.03, -61.65) * mm, "end": v(50.76, -61.7) * mm});
            skLineSegment(sketch, "E11094", {"start": v(50.76, -61.7) * mm, "end": v(51.5, -61.72) * mm});
            skLineSegment(sketch, "E11095", {"start": v(51.5, -61.72) * mm, "end": v(52.24, -61.74) * mm});
            skLineSegment(sketch, "E11096", {"start": v(52.24, -61.74) * mm, "end": v(52.98, -61.75) * mm});
            skLineSegment(sketch, "E11097", {"start": v(52.98, -61.75) * mm, "end": v(53.7, -61.74) * mm});
            skLineSegment(sketch, "E11098", {"start": v(53.7, -61.74) * mm, "end": v(54.42, -61.71) * mm});
            skLineSegment(sketch, "E11099", {"start": v(54.42, -61.71) * mm, "end": v(55.12, -61.67) * mm});
            skLineSegment(sketch, "E11100", {"start": v(55.12, -61.67) * mm, "end": v(55.8, -61.6) * mm});
            skLineSegment(sketch, "E11101", {"start": v(55.8, -61.6) * mm, "end": v(56.46, -61.5) * mm});
            skLineSegment(sketch, "E11102", {"start": v(56.46, -61.5) * mm, "end": v(56.78, -61.45) * mm});
            skLineSegment(sketch, "E11103", {"start": v(56.78, -61.45) * mm, "end": v(57.1, -61.4) * mm});
            skLineSegment(sketch, "E11104", {"start": v(57.1, -61.4) * mm, "end": v(57.77, -61.25) * mm});
            skLineSegment(sketch, "E11105", {"start": v(57.77, -61.25) * mm, "end": v(58.14, -61.16) * mm});
            skLineSegment(sketch, "E11106", {"start": v(58.14, -61.16) * mm, "end": v(58.51, -61.05) * mm});
            skLineSegment(sketch, "E11107", {"start": v(58.51, -61.05) * mm, "end": v(58.7, -60.99) * mm});
            skLineSegment(sketch, "E11108", {"start": v(58.7, -60.99) * mm, "end": v(58.86, -60.92) * mm});
            skLineSegment(sketch, "E11109", {"start": v(58.86, -60.92) * mm, "end": v(59.02, -60.84) * mm});
            skLineSegment(sketch, "E11110", {"start": v(59.02, -60.84) * mm, "end": v(59.16, -60.75) * mm});
            skLineSegment(sketch, "E11111", {"start": v(59.16, -60.75) * mm, "end": v(59.29, -60.65) * mm});
            skLineSegment(sketch, "E11112", {"start": v(59.29, -60.65) * mm, "end": v(59.4, -60.53) * mm});
            skLineSegment(sketch, "E11113", {"start": v(59.4, -60.53) * mm, "end": v(59.49, -60.41) * mm});
            skLineSegment(sketch, "E11114", {"start": v(59.49, -60.41) * mm, "end": v(59.55, -60.27) * mm});
            skLineSegment(sketch, "E11115", {"start": v(59.55, -60.27) * mm, "end": v(59.58, -60.17) * mm});
            skLineSegment(sketch, "E11116", {"start": v(59.58, -60.17) * mm, "end": v(59.59, -60.06) * mm});
            skLineSegment(sketch, "E11117", {"start": v(59.59, -60.06) * mm, "end": v(59.57, -59.96) * mm});
            skLineSegment(sketch, "E11118", {"start": v(59.57, -59.96) * mm, "end": v(59.54, -59.85) * mm});
            skLineSegment(sketch, "E11119", {"start": v(59.54, -59.85) * mm, "end": v(59.5, -59.73) * mm});
            skLineSegment(sketch, "E11120", {"start": v(59.5, -59.73) * mm, "end": v(59.45, -59.62) * mm});
            skLineSegment(sketch, "E11121", {"start": v(59.45, -59.62) * mm, "end": v(59.31, -59.4) * mm});
            skLineSegment(sketch, "E11122", {"start": v(59.31, -59.4) * mm, "end": v(59.16, -59.16) * mm});
            skLineSegment(sketch, "E11123", {"start": v(59.16, -59.16) * mm, "end": v(59, -58.94) * mm});
            skLineSegment(sketch, "E11124", {"start": v(59, -58.94) * mm, "end": v(58.85, -58.73) * mm});
            skLineSegment(sketch, "E11125", {"start": v(58.85, -58.73) * mm, "end": v(58.79, -58.62) * mm});
            skLineSegment(sketch, "E11126", {"start": v(58.79, -58.62) * mm, "end": v(58.74, -58.52) * mm});
            skLineSegment(sketch, "E11127", {"start": v(58.74, -58.52) * mm, "end": v(58.57, -58.16) * mm});
            skLineSegment(sketch, "E11128", {"start": v(58.57, -58.16) * mm, "end": v(58.42, -57.79) * mm});
            skLineSegment(sketch, "E11129", {"start": v(58.42, -57.79) * mm, "end": v(58.28, -57.42) * mm});
            skLineSegment(sketch, "E11130", {"start": v(58.28, -57.42) * mm, "end": v(58.16, -57.08) * mm});
            skLineSegment(sketch, "E11131", {"start": v(58.16, -57.08) * mm, "end": v(58.06, -56.76) * mm});
            skLineSegment(sketch, "E11132", {"start": v(58.06, -56.76) * mm, "end": v(57.98, -56.48) * mm});
            skLineSegment(sketch, "E11133", {"start": v(57.98, -56.48) * mm, "end": v(57.94, -56.24) * mm});
            skLineSegment(sketch, "E11134", {"start": v(57.94, -56.24) * mm, "end": v(57.92, -56.07) * mm});
            skLineSegment(sketch, "E11135", {"start": v(57.92, -56.07) * mm, "end": v(57.9, -55.89) * mm});
            skLineSegment(sketch, "E11136", {"start": v(57.9, -55.89) * mm, "end": v(57.87, -55.7) * mm});
            skLineSegment(sketch, "E11137", {"start": v(57.87, -55.7) * mm, "end": v(57.86, -55.6) * mm});
            skLineSegment(sketch, "E11138", {"start": v(57.86, -55.6) * mm, "end": v(57.86, -55.5) * mm});
            skLineSegment(sketch, "E11139", {"start": v(57.86, -55.5) * mm, "end": v(57.88, -55.43) * mm});
            skLineSegment(sketch, "E11140", {"start": v(57.88, -55.43) * mm, "end": v(57.91, -55.36) * mm});
            skLineSegment(sketch, "E11141", {"start": v(57.91, -55.36) * mm, "end": v(57.96, -55.31) * mm});
            skLineSegment(sketch, "E11142", {"start": v(57.96, -55.31) * mm, "end": v(58.01, -55.28) * mm});
            skLineSegment(sketch, "E11143", {"start": v(58.01, -55.28) * mm, "end": v(58.07, -55.25) * mm});
            skLineSegment(sketch, "E11144", {"start": v(58.07, -55.25) * mm, "end": v(58.13, -55.22) * mm});
            skLineSegment(sketch, "E11145", {"start": v(58.13, -55.22) * mm, "end": v(58.27, -55.2) * mm});
            skLineSegment(sketch, "E11146", {"start": v(58.27, -55.2) * mm, "end": v(58.43, -55.18) * mm});
            skLineSegment(sketch, "E11147", {"start": v(58.43, -55.18) * mm, "end": v(58.74, -55.17) * mm});
            skLineSegment(sketch, "E11148", {"start": v(58.74, -55.17) * mm, "end": v(58.9, -55.17) * mm});
            skLineSegment(sketch, "E11149", {"start": v(58.9, -55.17) * mm, "end": v(59.03, -55.15) * mm});
            skLineSegment(sketch, "E11150", {"start": v(59.03, -55.15) * mm, "end": v(59.34, -55.08) * mm});
            skLineSegment(sketch, "E11151", {"start": v(59.34, -55.08) * mm, "end": v(59.79, -54.97) * mm});
            skLineSegment(sketch, "E11152", {"start": v(59.79, -54.97) * mm, "end": v(60.35, -54.81) * mm});
            skLineSegment(sketch, "E11153", {"start": v(60.35, -54.81) * mm, "end": v(61.02, -54.62) * mm});
            skLineSegment(sketch, "E11154", {"start": v(61.02, -54.62) * mm, "end": v(61.76, -54.4) * mm});
            skLineSegment(sketch, "E11155", {"start": v(61.76, -54.4) * mm, "end": v(62.56, -54.15) * mm});
            skLineSegment(sketch, "E11156", {"start": v(62.56, -54.15) * mm, "end": v(63.39, -53.88) * mm});
            skLineSegment(sketch, "E11157", {"start": v(63.39, -53.88) * mm, "end": v(64.23, -53.6) * mm});
            skLineSegment(sketch, "E11158", {"start": v(64.23, -53.6) * mm, "end": v(65.8, -53.05) * mm});
            skLineSegment(sketch, "E11159", {"start": v(65.8, -53.05) * mm, "end": v(67.48, -52.46) * mm});
            skLineSegment(sketch, "E11160", {"start": v(67.48, -52.46) * mm, "end": v(69.16, -51.85) * mm});
            skLineSegment(sketch, "E11161", {"start": v(69.16, -51.85) * mm, "end": v(70.72, -51.26) * mm});
            skLineSegment(sketch, "E11162", {"start": v(70.72, -51.26) * mm, "end": v(71.33, -51.02) * mm});
            skLineSegment(sketch, "E11163", {"start": v(71.33, -51.02) * mm, "end": v(71.91, -50.78) * mm});
            skLineSegment(sketch, "E11164", {"start": v(71.91, -50.78) * mm, "end": v(72.47, -50.53) * mm});
            skLineSegment(sketch, "E11165", {"start": v(72.47, -50.53) * mm, "end": v(73, -50.29) * mm});
            skLineSegment(sketch, "E11166", {"start": v(73, -50.29) * mm, "end": v(73.51, -50.04) * mm});
            skLineSegment(sketch, "E11167", {"start": v(73.51, -50.04) * mm, "end": v(74, -49.8) * mm});
            skLineSegment(sketch, "E11168", {"start": v(74, -49.8) * mm, "end": v(74.46, -49.55) * mm});
            skLineSegment(sketch, "E11169", {"start": v(74.46, -49.55) * mm, "end": v(74.9, -49.31) * mm});
            skLineSegment(sketch, "E11170", {"start": v(74.9, -49.31) * mm, "end": v(75.3, -49.07) * mm});
            skLineSegment(sketch, "E11171", {"start": v(75.3, -49.07) * mm, "end": v(75.7, -48.83) * mm});
            skLineSegment(sketch, "E11172", {"start": v(75.7, -48.83) * mm, "end": v(76.06, -48.59) * mm});
            skLineSegment(sketch, "E11173", {"start": v(76.06, -48.59) * mm, "end": v(76.4, -48.35) * mm});
            skLineSegment(sketch, "E11174", {"start": v(76.4, -48.35) * mm, "end": v(76.72, -48.11) * mm});
            skLineSegment(sketch, "E11175", {"start": v(76.72, -48.11) * mm, "end": v(77.02, -47.88) * mm});
            skLineSegment(sketch, "E11176", {"start": v(77.02, -47.88) * mm, "end": v(77.29, -47.65) * mm});
            skLineSegment(sketch, "E11177", {"start": v(77.29, -47.65) * mm, "end": v(77.54, -47.42) * mm});
            skLineSegment(sketch, "E11178", {"start": v(77.54, -47.42) * mm, "end": v(77.81, -47.19) * mm});
            skLineSegment(sketch, "E11179", {"start": v(77.81, -47.19) * mm, "end": v(78.12, -46.94) * mm});
            skLineSegment(sketch, "E11180", {"start": v(78.12, -46.94) * mm, "end": v(78.26, -46.81) * mm});
            skLineSegment(sketch, "E11181", {"start": v(78.26, -46.81) * mm, "end": v(78.4, -46.68) * mm});
            skLineSegment(sketch, "E11182", {"start": v(78.4, -46.68) * mm, "end": v(78.52, -46.54) * mm});
            skLineSegment(sketch, "E11183", {"start": v(78.52, -46.54) * mm, "end": v(78.62, -46.4) * mm});
            skLineSegment(sketch, "E11184", {"start": v(78.62, -46.4) * mm, "end": v(78.79, -46.1) * mm});
            skLineSegment(sketch, "E11185", {"start": v(78.79, -46.1) * mm, "end": v(78.87, -45.92) * mm});
            skLineSegment(sketch, "E11186", {"start": v(78.87, -45.92) * mm, "end": v(78.94, -45.74) * mm});
            skLineSegment(sketch, "E11187", {"start": v(78.94, -45.74) * mm, "end": v(79, -45.55) * mm});
            skLineSegment(sketch, "E11188", {"start": v(79, -45.55) * mm, "end": v(79.02, -45.38) * mm});
            skLineSegment(sketch, "E11189", {"start": v(79.02, -45.38) * mm, "end": v(79.02, -45.3) * mm});
            skLineSegment(sketch, "E11190", {"start": v(79.02, -45.3) * mm, "end": v(79.02, -45.21) * mm});
            skLineSegment(sketch, "E11191", {"start": v(79.02, -45.21) * mm, "end": v(79, -45.13) * mm});
            skLineSegment(sketch, "E11192", {"start": v(79, -45.13) * mm, "end": v(78.97, -45.06) * mm});
            skLineSegment(sketch, "E11193", {"start": v(78.97, -45.06) * mm, "end": v(78.93, -44.99) * mm});
            skLineSegment(sketch, "E11194", {"start": v(78.93, -44.99) * mm, "end": v(78.87, -44.92) * mm});
            skLineSegment(sketch, "E11195", {"start": v(78.87, -44.92) * mm, "end": v(78.8, -44.87) * mm});
            skLineSegment(sketch, "E11196", {"start": v(78.8, -44.87) * mm, "end": v(78.73, -44.82) * mm});
            skLineSegment(sketch, "E11197", {"start": v(78.73, -44.82) * mm, "end": v(78.56, -44.74) * mm});
            skLineSegment(sketch, "E11198", {"start": v(78.56, -44.74) * mm, "end": v(78.37, -44.67) * mm});
            skLineSegment(sketch, "E11199", {"start": v(78.37, -44.67) * mm, "end": v(77.96, -44.57) * mm});
            skLineSegment(sketch, "E11200", {"start": v(77.96, -44.57) * mm, "end": v(77.77, -44.51) * mm});
            skLineSegment(sketch, "E11201", {"start": v(77.77, -44.51) * mm, "end": v(77.6, -44.45) * mm});
            skLineSegment(sketch, "E11202", {"start": v(77.6, -44.45) * mm, "end": v(77.08, -44.2) * mm});
            skLineSegment(sketch, "E11203", {"start": v(77.08, -44.2) * mm, "end": v(76.85, -44.09) * mm});
            skLineSegment(sketch, "E11204", {"start": v(76.85, -44.09) * mm, "end": v(76.64, -43.97) * mm});
            skLineSegment(sketch, "E11205", {"start": v(76.64, -43.97) * mm, "end": v(76.45, -43.85) * mm});
            skLineSegment(sketch, "E11206", {"start": v(76.45, -43.85) * mm, "end": v(76.27, -43.73) * mm});
            skLineSegment(sketch, "E11207", {"start": v(76.27, -43.73) * mm, "end": v(76.11, -43.6) * mm});
            skLineSegment(sketch, "E11208", {"start": v(76.11, -43.6) * mm, "end": v(75.97, -43.47) * mm});
            skLineSegment(sketch, "E11209", {"start": v(75.97, -43.47) * mm, "end": v(75.84, -43.33) * mm});
            skLineSegment(sketch, "E11210", {"start": v(75.84, -43.33) * mm, "end": v(75.71, -43.18) * mm});
            skLineSegment(sketch, "E11211", {"start": v(75.71, -43.18) * mm, "end": v(75.6, -43.02) * mm});
            skLineSegment(sketch, "E11212", {"start": v(75.6, -43.02) * mm, "end": v(75.5, -42.85) * mm});
            skLineSegment(sketch, "E11213", {"start": v(75.5, -42.85) * mm, "end": v(75.4, -42.66) * mm});
            skLineSegment(sketch, "E11214", {"start": v(75.4, -42.66) * mm, "end": v(75.3, -42.46) * mm});
            skLineSegment(sketch, "E11215", {"start": v(75.3, -42.46) * mm, "end": v(75.2, -42.25) * mm});
            skLineSegment(sketch, "E11216", {"start": v(75.2, -42.25) * mm, "end": v(75.1, -42.01) * mm});
            skLineSegment(sketch, "E11217", {"start": v(75.1, -42.01) * mm, "end": v(75.06, -41.91) * mm});
            skLineSegment(sketch, "E11218", {"start": v(75.06, -41.91) * mm, "end": v(75, -41.8) * mm});
            skLineSegment(sketch, "E11219", {"start": v(75, -41.8) * mm, "end": v(74.86, -41.57) * mm});
            skLineSegment(sketch, "E11220", {"start": v(74.86, -41.57) * mm, "end": v(74.8, -41.46) * mm});
            skLineSegment(sketch, "E11221", {"start": v(74.8, -41.46) * mm, "end": v(74.76, -41.34) * mm});
            skLineSegment(sketch, "E11222", {"start": v(74.76, -41.34) * mm, "end": v(74.75, -41.3) * mm});
            skLineSegment(sketch, "E11223", {"start": v(74.75, -41.3) * mm, "end": v(74.75, -41.24) * mm});
            skLineSegment(sketch, "E11224", {"start": v(74.75, -41.24) * mm, "end": v(74.76, -41.19) * mm});
            skLineSegment(sketch, "E11225", {"start": v(74.76, -41.19) * mm, "end": v(74.78, -41.14) * mm});
            skLineSegment(sketch, "E11226", {"start": v(74.78, -41.14) * mm, "end": v(74.81, -41.08) * mm});
            skLineSegment(sketch, "E11227", {"start": v(74.81, -41.08) * mm, "end": v(74.86, -41.03) * mm});
            skLineSegment(sketch, "E11228", {"start": v(74.86, -41.03) * mm, "end": v(74.92, -40.98) * mm});
            skLineSegment(sketch, "E11229", {"start": v(74.92, -40.98) * mm, "end": v(74.99, -40.95) * mm});
            skLineSegment(sketch, "E11230", {"start": v(74.99, -40.95) * mm, "end": v(75.14, -40.9) * mm});
            skLineSegment(sketch, "E11231", {"start": v(75.14, -40.9) * mm, "end": v(75.31, -40.86) * mm});
            skLineSegment(sketch, "E11232", {"start": v(75.31, -40.86) * mm, "end": v(75.68, -40.8) * mm});
            skLineSegment(sketch, "E11233", {"start": v(75.68, -40.8) * mm, "end": v(75.85, -40.78) * mm});
            skLineSegment(sketch, "E11234", {"start": v(75.85, -40.78) * mm, "end": v(76, -40.75) * mm});
            skLineSegment(sketch, "E11235", {"start": v(76, -40.75) * mm, "end": v(76.3, -40.64) * mm});
            skLineSegment(sketch, "E11236", {"start": v(76.3, -40.64) * mm, "end": v(76.71, -40.48) * mm});
            skLineSegment(sketch, "E11237", {"start": v(76.71, -40.48) * mm, "end": v(77.2, -40.27) * mm});
            skLineSegment(sketch, "E11238", {"start": v(77.2, -40.27) * mm, "end": v(77.75, -40.03) * mm});
            skLineSegment(sketch, "E11239", {"start": v(77.75, -40.03) * mm, "end": v(78.99, -39.47) * mm});
            skLineSegment(sketch, "E11240", {"start": v(78.99, -39.47) * mm, "end": v(80.27, -38.86) * mm});
            skLineSegment(sketch, "E11241", {"start": v(80.27, -38.86) * mm, "end": v(81, -38.51) * mm});
            skLineSegment(sketch, "E11242", {"start": v(81, -38.51) * mm, "end": v(81.82, -38.15) * mm});
            skLineSegment(sketch, "E11243", {"start": v(81.82, -38.15) * mm, "end": v(82.22, -37.96) * mm});
            skLineSegment(sketch, "E11244", {"start": v(82.22, -37.96) * mm, "end": v(82.6, -37.77) * mm});
            skLineSegment(sketch, "E11245", {"start": v(82.6, -37.77) * mm, "end": v(82.98, -37.57) * mm});
            skLineSegment(sketch, "E11246", {"start": v(82.98, -37.57) * mm, "end": v(83.31, -37.36) * mm});
            skLineSegment(sketch, "E11247", {"start": v(83.31, -37.36) * mm, "end": v(83.77, -37.04) * mm});
            skLineSegment(sketch, "E11248", {"start": v(83.77, -37.04) * mm, "end": v(84.25, -36.68) * mm});
            skLineSegment(sketch, "E11249", {"start": v(84.25, -36.68) * mm, "end": v(84.74, -36.3) * mm});
            skLineSegment(sketch, "E11250", {"start": v(84.74, -36.3) * mm, "end": v(85.22, -35.89) * mm});
            skLineSegment(sketch, "E11251", {"start": v(85.22, -35.89) * mm, "end": v(85.7, -35.47) * mm});
            skLineSegment(sketch, "E11252", {"start": v(85.7, -35.47) * mm, "end": v(86.13, -35.04) * mm});
            skLineSegment(sketch, "E11253", {"start": v(86.13, -35.04) * mm, "end": v(86.34, -34.82) * mm});
            skLineSegment(sketch, "E11254", {"start": v(86.34, -34.82) * mm, "end": v(86.54, -34.6) * mm});
            skLineSegment(sketch, "E11255", {"start": v(86.54, -34.6) * mm, "end": v(86.72, -34.38) * mm});
            skLineSegment(sketch, "E11256", {"start": v(86.72, -34.38) * mm, "end": v(86.9, -34.17) * mm});
            skLineSegment(sketch, "E11257", {"start": v(86.9, -34.17) * mm, "end": v(87.16, -33.8) * mm});
            skLineSegment(sketch, "E11258", {"start": v(87.16, -33.8) * mm, "end": v(87.42, -33.4) * mm});
            skLineSegment(sketch, "E11259", {"start": v(87.42, -33.4) * mm, "end": v(87.67, -32.98) * mm});
            skLineSegment(sketch, "E11260", {"start": v(87.67, -32.98) * mm, "end": v(87.91, -32.53) * mm});
            skLineSegment(sketch, "E11261", {"start": v(87.91, -32.53) * mm, "end": v(88.13, -32.07) * mm});
            skLineSegment(sketch, "E11262", {"start": v(88.13, -32.07) * mm, "end": v(88.32, -31.62) * mm});
            skLineSegment(sketch, "E11263", {"start": v(88.32, -31.62) * mm, "end": v(88.48, -31.17) * mm});
            skLineSegment(sketch, "E11264", {"start": v(88.48, -31.17) * mm, "end": v(88.55, -30.95) * mm});
            skLineSegment(sketch, "E11265", {"start": v(88.55, -30.95) * mm, "end": v(88.6, -30.74) * mm});
            skLineSegment(sketch, "E11266", {"start": v(88.6, -30.74) * mm, "end": v(88.75, -30.11) * mm});
            skLineSegment(sketch, "E11267", {"start": v(88.75, -30.11) * mm, "end": v(88.82, -29.76) * mm});
            skLineSegment(sketch, "E11268", {"start": v(88.82, -29.76) * mm, "end": v(88.87, -29.4) * mm});
            skLineSegment(sketch, "E11269", {"start": v(88.87, -29.4) * mm, "end": v(88.88, -29.23) * mm});
            skLineSegment(sketch, "E11270", {"start": v(88.88, -29.23) * mm, "end": v(88.88, -29.06) * mm});
            skLineSegment(sketch, "E11271", {"start": v(88.88, -29.06) * mm, "end": v(88.87, -28.9) * mm});
            skLineSegment(sketch, "E11272", {"start": v(88.87, -28.9) * mm, "end": v(88.85, -28.74) * mm});
            skLineSegment(sketch, "E11273", {"start": v(88.85, -28.74) * mm, "end": v(88.82, -28.6) * mm});
            skLineSegment(sketch, "E11274", {"start": v(88.82, -28.6) * mm, "end": v(88.76, -28.46) * mm});
            skLineSegment(sketch, "E11275", {"start": v(88.76, -28.46) * mm, "end": v(88.7, -28.34) * mm});
            skLineSegment(sketch, "E11276", {"start": v(88.7, -28.34) * mm, "end": v(88.6, -28.23) * mm});
            skLineSegment(sketch, "E11277", {"start": v(88.6, -28.23) * mm, "end": v(88.55, -28.18) * mm});
            skLineSegment(sketch, "E11278", {"start": v(88.55, -28.18) * mm, "end": v(88.5, -28.14) * mm});
            skLineSegment(sketch, "E11279", {"start": v(88.5, -28.14) * mm, "end": v(88.37, -28.09) * mm});
            skLineSegment(sketch, "E11280", {"start": v(88.37, -28.09) * mm, "end": v(88.23, -28.06) * mm});
            skLineSegment(sketch, "E11281", {"start": v(88.23, -28.06) * mm, "end": v(88.08, -28.04) * mm});
            skLineSegment(sketch, "E11282", {"start": v(88.08, -28.04) * mm, "end": v(87.93, -28.05) * mm});
            skLineSegment(sketch, "E11283", {"start": v(87.93, -28.05) * mm, "end": v(87.76, -28.07) * mm});
            skLineSegment(sketch, "E11284", {"start": v(87.76, -28.07) * mm, "end": v(87.4, -28.14) * mm});
            skLineSegment(sketch, "E11285", {"start": v(87.4, -28.14) * mm, "end": v(87.05, -28.21) * mm});
            skLineSegment(sketch, "E11286", {"start": v(87.05, -28.21) * mm, "end": v(86.88, -28.25) * mm});
            skLineSegment(sketch, "E11287", {"start": v(86.88, -28.25) * mm, "end": v(86.7, -28.27) * mm});
            skLineSegment(sketch, "E11288", {"start": v(86.7, -28.27) * mm, "end": v(86.54, -28.29) * mm});
            skLineSegment(sketch, "E11289", {"start": v(86.54, -28.29) * mm, "end": v(86.38, -28.29) * mm});
            skLineSegment(sketch, "E11290", {"start": v(86.38, -28.29) * mm, "end": v(86.23, -28.27) * mm});
            skLineSegment(sketch, "E11291", {"start": v(86.23, -28.27) * mm, "end": v(86.1, -28.23) * mm});
            skLineSegment(sketch, "E11292", {"start": v(86.1, -28.23) * mm, "end": v(85.98, -28.17) * mm});
            skLineSegment(sketch, "E11293", {"start": v(85.98, -28.17) * mm, "end": v(85.85, -28.1) * mm});
            skLineSegment(sketch, "E11294", {"start": v(85.85, -28.1) * mm, "end": v(85.73, -28.02) * mm});
            skLineSegment(sketch, "E11295", {"start": v(85.73, -28.02) * mm, "end": v(85.6, -27.92) * mm});
            skLineSegment(sketch, "E11296", {"start": v(85.6, -27.92) * mm, "end": v(85.5, -27.82) * mm});
            skLineSegment(sketch, "E11297", {"start": v(85.5, -27.82) * mm, "end": v(85.42, -27.7) * mm});
            skLineSegment(sketch, "E11298", {"start": v(85.42, -27.7) * mm, "end": v(85.36, -27.59) * mm});
            skLineSegment(sketch, "E11299", {"start": v(85.36, -27.59) * mm, "end": v(85.34, -27.53) * mm});
            skLineSegment(sketch, "E11300", {"start": v(85.34, -27.53) * mm, "end": v(85.34, -27.47) * mm});
            skLineSegment(sketch, "E11301", {"start": v(85.34, -27.47) * mm, "end": v(85.34, -27.35) * mm});
            skLineSegment(sketch, "E11302", {"start": v(85.34, -27.35) * mm, "end": v(85.37, -27.23) * mm});
            skLineSegment(sketch, "E11303", {"start": v(85.37, -27.23) * mm, "end": v(85.42, -27.11) * mm});
            skLineSegment(sketch, "E11304", {"start": v(85.42, -27.11) * mm, "end": v(85.49, -27) * mm});
            skLineSegment(sketch, "E11305", {"start": v(85.49, -27) * mm, "end": v(85.57, -26.89) * mm});
            skLineSegment(sketch, "E11306", {"start": v(85.57, -26.89) * mm, "end": v(85.66, -26.78) * mm});
            skLineSegment(sketch, "E11307", {"start": v(85.66, -26.78) * mm, "end": v(85.88, -26.57) * mm});
            skLineSegment(sketch, "E11308", {"start": v(85.88, -26.57) * mm, "end": v(86.12, -26.37) * mm});
            skLineSegment(sketch, "E11309", {"start": v(86.12, -26.37) * mm, "end": v(86.36, -26.17) * mm});
            skLineSegment(sketch, "E11310", {"start": v(86.36, -26.17) * mm, "end": v(86.58, -25.98) * mm});
            skLineSegment(sketch, "E11311", {"start": v(86.58, -25.98) * mm, "end": v(86.68, -25.88) * mm});
            skLineSegment(sketch, "E11312", {"start": v(86.68, -25.88) * mm, "end": v(86.76, -25.79) * mm});
            skLineSegment(sketch, "E11313", {"start": v(86.76, -25.79) * mm, "end": v(87.07, -25.41) * mm});
            skLineSegment(sketch, "E11314", {"start": v(87.07, -25.41) * mm, "end": v(87.4, -24.99) * mm});
            skLineSegment(sketch, "E11315", {"start": v(87.4, -24.99) * mm, "end": v(87.73, -24.54) * mm});
            skLineSegment(sketch, "E11316", {"start": v(87.73, -24.54) * mm, "end": v(88.07, -24.06) * mm});
            skLineSegment(sketch, "E11317", {"start": v(88.07, -24.06) * mm, "end": v(88.4, -23.59) * mm});
            skLineSegment(sketch, "E11318", {"start": v(88.4, -23.59) * mm, "end": v(88.7, -23.13) * mm});
            skLineSegment(sketch, "E11319", {"start": v(88.7, -23.13) * mm, "end": v(88.97, -22.69) * mm});
            skLineSegment(sketch, "E11320", {"start": v(88.97, -22.69) * mm, "end": v(89.2, -22.29) * mm});
            skLineSegment(sketch, "E11321", {"start": v(89.2, -22.29) * mm, "end": v(89.46, -21.86) * mm});
            skLineSegment(sketch, "E11322", {"start": v(89.46, -21.86) * mm, "end": v(89.74, -21.4) * mm});
            skLineSegment(sketch, "E11323", {"start": v(89.74, -21.4) * mm, "end": v(90, -20.92) * mm});
            skLineSegment(sketch, "E11324", {"start": v(90, -20.92) * mm, "end": v(90.12, -20.7) * mm});
            skLineSegment(sketch, "E11325", {"start": v(90.12, -20.7) * mm, "end": v(90.22, -20.47) * mm});
            skLineSegment(sketch, "E11326", {"start": v(90.22, -20.47) * mm, "end": v(90.39, -20.03) * mm});
            skLineSegment(sketch, "E11327", {"start": v(90.39, -20.03) * mm, "end": v(90.55, -19.55) * mm});
            skLineSegment(sketch, "E11328", {"start": v(90.55, -19.55) * mm, "end": v(90.7, -19.05) * mm});
            skLineSegment(sketch, "E11329", {"start": v(90.7, -19.05) * mm, "end": v(90.84, -18.54) * mm});
            skLineSegment(sketch, "E11330", {"start": v(90.84, -18.54) * mm, "end": v(90.97, -18.02) * mm});
            skLineSegment(sketch, "E11331", {"start": v(90.97, -18.02) * mm, "end": v(91.08, -17.5) * mm});
            skLineSegment(sketch, "E11332", {"start": v(91.08, -17.5) * mm, "end": v(91.17, -17.01) * mm});
            skLineSegment(sketch, "E11333", {"start": v(91.17, -17.01) * mm, "end": v(91.24, -16.54) * mm});
            skLineSegment(sketch, "E11334", {"start": v(91.24, -16.54) * mm, "end": v(91.3, -15.96) * mm});
            skLineSegment(sketch, "E11335", {"start": v(91.3, -15.96) * mm, "end": v(91.35, -15.35) * mm});
            skLineSegment(sketch, "E11336", {"start": v(91.35, -15.35) * mm, "end": v(91.38, -14.7) * mm});
            skLineSegment(sketch, "E11337", {"start": v(91.38, -14.7) * mm, "end": v(91.39, -14.05) * mm});
            skLineSegment(sketch, "E11338", {"start": v(91.39, -14.05) * mm, "end": v(91.38, -13.4) * mm});
            skLineSegment(sketch, "E11339", {"start": v(91.38, -13.4) * mm, "end": v(91.35, -12.76) * mm});
            skLineSegment(sketch, "E11340", {"start": v(91.35, -12.76) * mm, "end": v(91.3, -12.14) * mm});
            skLineSegment(sketch, "E11341", {"start": v(91.3, -12.14) * mm, "end": v(91.24, -11.56) * mm});
            skLineSegment(sketch, "E11342", {"start": v(91.24, -11.56) * mm, "end": v(91.18, -10.95) * mm});
            skLineSegment(sketch, "E11343", {"start": v(91.18, -10.95) * mm, "end": v(91.15, -10.61) * mm});
            skLineSegment(sketch, "E11344", {"start": v(91.15, -10.61) * mm, "end": v(91.1, -10.27) * mm});
            skLineSegment(sketch, "E11345", {"start": v(91.1, -10.27) * mm, "end": v(91.07, -10.1) * mm});
            skLineSegment(sketch, "E11346", {"start": v(91.07, -10.1) * mm, "end": v(91.03, -9.95) * mm});
            skLineSegment(sketch, "E11347", {"start": v(91.03, -9.95) * mm, "end": v(90.98, -9.8) * mm});
            skLineSegment(sketch, "E11348", {"start": v(90.98, -9.8) * mm, "end": v(90.93, -9.66) * mm});
            skLineSegment(sketch, "E11349", {"start": v(90.93, -9.66) * mm, "end": v(90.86, -9.52) * mm});
            skLineSegment(sketch, "E11350", {"start": v(90.86, -9.52) * mm, "end": v(90.78, -9.4) * mm});
            skLineSegment(sketch, "E11351", {"start": v(90.78, -9.4) * mm, "end": v(90.7, -9.3) * mm});
            skLineSegment(sketch, "E11352", {"start": v(90.7, -9.3) * mm, "end": v(90.59, -9.21) * mm});
            skLineSegment(sketch, "E11353", {"start": v(90.59, -9.21) * mm, "end": v(90.5, -9.15) * mm});
            skLineSegment(sketch, "E11354", {"start": v(90.5, -9.15) * mm, "end": v(90.39, -9.1) * mm});
            skLineSegment(sketch, "E11355", {"start": v(90.39, -9.1) * mm, "end": v(90.28, -9.07) * mm});
            skLineSegment(sketch, "E11356", {"start": v(90.28, -9.07) * mm, "end": v(90.17, -9.05) * mm});
            skLineSegment(sketch, "E11357", {"start": v(90.17, -9.05) * mm, "end": v(90.05, -9.04) * mm});
            skLineSegment(sketch, "E11358", {"start": v(90.05, -9.04) * mm, "end": v(89.93, -9.03) * mm});
            skLineSegment(sketch, "E11359", {"start": v(89.93, -9.03) * mm, "end": v(89.67, -9.05) * mm});
            skLineSegment(sketch, "E11360", {"start": v(89.67, -9.05) * mm, "end": v(89.4, -9.09) * mm});
            skLineSegment(sketch, "E11361", {"start": v(89.4, -9.09) * mm, "end": v(89.11, -9.15) * mm});
            skLineSegment(sketch, "E11362", {"start": v(89.11, -9.15) * mm, "end": v(88.54, -9.3) * mm});
            skLineSegment(sketch, "E11363", {"start": v(88.54, -9.3) * mm, "end": v(87.97, -9.47) * mm});
            skLineSegment(sketch, "E11364", {"start": v(87.97, -9.47) * mm, "end": v(87.7, -9.54) * mm});
            skLineSegment(sketch, "E11365", {"start": v(87.7, -9.54) * mm, "end": v(87.44, -9.6) * mm});
            skLineSegment(sketch, "E11366", {"start": v(87.44, -9.6) * mm, "end": v(87.2, -9.62) * mm});
            skLineSegment(sketch, "E11367", {"start": v(87.2, -9.62) * mm, "end": v(87.09, -9.62) * mm});
            skLineSegment(sketch, "E11368", {"start": v(87.09, -9.62) * mm, "end": v(86.98, -9.62) * mm});
            skLineSegment(sketch, "E11369", {"start": v(86.98, -9.62) * mm, "end": v(86.88, -9.6) * mm});
            skLineSegment(sketch, "E11370", {"start": v(86.88, -9.6) * mm, "end": v(86.79, -9.58) * mm});
            skLineSegment(sketch, "E11371", {"start": v(86.79, -9.58) * mm, "end": v(86.7, -9.55) * mm});
            skLineSegment(sketch, "E11372", {"start": v(86.7, -9.55) * mm, "end": v(86.62, -9.5) * mm});
            skLineSegment(sketch, "E11373", {"start": v(86.62, -9.5) * mm, "end": v(86.6, -9.48) * mm});
            skLineSegment(sketch, "E11374", {"start": v(86.6, -9.48) * mm, "end": v(86.6, -9.45) * mm});
            skLineSegment(sketch, "E11375", {"start": v(86.6, -9.45) * mm, "end": v(86.6, -9.37) * mm});
            skLineSegment(sketch, "E11376", {"start": v(86.6, -9.37) * mm, "end": v(86.62, -9.29) * mm});
            skLineSegment(sketch, "E11377", {"start": v(86.62, -9.29) * mm, "end": v(86.63, -9.21) * mm});
            skLineSegment(sketch, "E11378", {"start": v(86.63, -9.21) * mm, "end": v(86.64, -9.12) * mm});
            skLineSegment(sketch, "E11379", {"start": v(86.64, -9.12) * mm, "end": v(86.67, -8.97) * mm});
            skLineSegment(sketch, "E11380", {"start": v(86.67, -8.97) * mm, "end": v(86.78, -8.52) * mm});
            skLineSegment(sketch, "E11381", {"start": v(86.78, -8.52) * mm, "end": v(86.94, -7.94) * mm});
            skLineSegment(sketch, "E11382", {"start": v(86.94, -7.94) * mm, "end": v(87.14, -7.27) * mm});
            skLineSegment(sketch, "E11383", {"start": v(87.14, -7.27) * mm, "end": v(87.26, -6.87) * mm});
            skLineSegment(sketch, "E11384", {"start": v(87.26, -6.87) * mm, "end": v(87.4, -6.33) * mm});
            skLineSegment(sketch, "E11385", {"start": v(87.4, -6.33) * mm, "end": v(87.74, -5) * mm});
            skLineSegment(sketch, "E11386", {"start": v(87.74, -5) * mm, "end": v(88.11, -3.43) * mm});
            skLineSegment(sketch, "E11387", {"start": v(88.11, -3.43) * mm, "end": v(88.47, -1.83) * mm});
            skLineSegment(sketch, "E11388", {"start": v(88.47, -1.83) * mm, "end": v(88.68, -0.92) * mm});
            skLineSegment(sketch, "E11389", {"start": v(88.68, -0.92) * mm, "end": v(88.92, 0.06) * mm});
            skLineSegment(sketch, "E11390", {"start": v(88.92, 0.06) * mm, "end": v(89.04, 0.56) * mm});
            skLineSegment(sketch, "E11391", {"start": v(89.04, 0.56) * mm, "end": v(89.14, 1.04) * mm});
            skLineSegment(sketch, "E11392", {"start": v(89.14, 1.04) * mm, "end": v(89.23, 1.52) * mm});
            skLineSegment(sketch, "E11393", {"start": v(89.23, 1.52) * mm, "end": v(89.3, 1.96) * mm});
            skLineSegment(sketch, "E11394", {"start": v(89.3, 1.96) * mm, "end": v(89.43, 2.97) * mm});
            skLineSegment(sketch, "E11395", {"start": v(89.43, 2.97) * mm, "end": v(89.59, 4.04) * mm});
            skLineSegment(sketch, "E11396", {"start": v(89.59, 4.04) * mm, "end": v(89.73, 5.15) * mm});
            skLineSegment(sketch, "E11397", {"start": v(89.73, 5.15) * mm, "end": v(89.8, 5.72) * mm});
            skLineSegment(sketch, "E11398", {"start": v(89.8, 5.72) * mm, "end": v(89.86, 6.28) * mm});
            skLineSegment(sketch, "E11399", {"start": v(89.86, 6.28) * mm, "end": v(89.9, 6.85) * mm});
            skLineSegment(sketch, "E11400", {"start": v(89.9, 6.85) * mm, "end": v(89.93, 7.42) * mm});
            skLineSegment(sketch, "E11401", {"start": v(89.93, 7.42) * mm, "end": v(89.94, 7.97) * mm});
            skLineSegment(sketch, "E11402", {"start": v(89.94, 7.97) * mm, "end": v(89.93, 8.52) * mm});
            skLineSegment(sketch, "E11403", {"start": v(89.93, 8.52) * mm, "end": v(89.9, 9.05) * mm});
            skLineSegment(sketch, "E11404", {"start": v(89.9, 9.05) * mm, "end": v(89.84, 9.57) * mm});
            skLineSegment(sketch, "E11405", {"start": v(89.84, 9.57) * mm, "end": v(89.8, 9.82) * mm});
            skLineSegment(sketch, "E11406", {"start": v(89.8, 9.82) * mm, "end": v(89.75, 10.07) * mm});
            skLineSegment(sketch, "E11407", {"start": v(89.75, 10.07) * mm, "end": v(89.7, 10.3) * mm});
            skLineSegment(sketch, "E11408", {"start": v(89.7, 10.3) * mm, "end": v(89.63, 10.54) * mm});
            skLineSegment(sketch, "E11409", {"start": v(89.63, 10.54) * mm, "end": v(89.54, 10.82) * mm});
            skLineSegment(sketch, "E11410", {"start": v(89.54, 10.82) * mm, "end": v(89.48, 10.97) * mm});
            skLineSegment(sketch, "E11411", {"start": v(89.48, 10.97) * mm, "end": v(89.4, 11.1) * mm});
            skLineSegment(sketch, "E11412", {"start": v(89.4, 11.1) * mm, "end": v(89.32, 11.24) * mm});
            skLineSegment(sketch, "E11413", {"start": v(89.32, 11.24) * mm, "end": v(89.22, 11.35) * mm});
            skLineSegment(sketch, "E11414", {"start": v(89.22, 11.35) * mm, "end": v(89.17, 11.4) * mm});
            skLineSegment(sketch, "E11415", {"start": v(89.17, 11.4) * mm, "end": v(89.12, 11.43) * mm});
            skLineSegment(sketch, "E11416", {"start": v(89.12, 11.43) * mm, "end": v(89.06, 11.45) * mm});
            skLineSegment(sketch, "E11417", {"start": v(89.06, 11.45) * mm, "end": v(89, 11.47) * mm});
            skLineSegment(sketch, "E11418", {"start": v(89, 11.47) * mm, "end": v(88.93, 11.47) * mm});
            skLineSegment(sketch, "E11419", {"start": v(88.93, 11.47) * mm, "end": v(88.87, 11.46) * mm});
            skLineSegment(sketch, "E11420", {"start": v(88.87, 11.46) * mm, "end": v(88.81, 11.44) * mm});
            skLineSegment(sketch, "E11421", {"start": v(88.81, 11.44) * mm, "end": v(88.75, 11.4) * mm});
            skLineSegment(sketch, "E11422", {"start": v(88.75, 11.4) * mm, "end": v(88.63, 11.32) * mm});
            skLineSegment(sketch, "E11423", {"start": v(88.63, 11.32) * mm, "end": v(88.52, 11.21) * mm});
            skLineSegment(sketch, "E11424", {"start": v(88.52, 11.21) * mm, "end": v(88.3, 10.97) * mm});
            skLineSegment(sketch, "E11425", {"start": v(88.3, 10.97) * mm, "end": v(88.2, 10.85) * mm});
            skLineSegment(sketch, "E11426", {"start": v(88.2, 10.85) * mm, "end": v(88.1, 10.76) * mm});
            skLineSegment(sketch, "E11427", {"start": v(88.1, 10.76) * mm, "end": v(87.73, 10.49) * mm});
            skLineSegment(sketch, "E11428", {"start": v(87.73, 10.49) * mm, "end": v(87.38, 10.26) * mm});
            skLineSegment(sketch, "E11429", {"start": v(87.38, 10.26) * mm, "end": v(87.1, 10.11) * mm});
            skLineSegment(sketch, "E11430", {"start": v(87.1, 10.11) * mm, "end": v(87, 10.07) * mm});
            skLineSegment(sketch, "E11431", {"start": v(87, 10.07) * mm, "end": v(86.94, 10.05) * mm});
            skLineSegment(sketch, "E11432", {"start": v(86.94, 10.05) * mm, "end": v(86.83, 10.03) * mm});
            skLineSegment(sketch, "E11433", {"start": v(86.83, 10.03) * mm, "end": v(86.71, 9.98) * mm});
            skLineSegment(sketch, "E11434", {"start": v(86.71, 9.98) * mm, "end": v(86.47, 9.88) * mm});
            skLineSegment(sketch, "E11435", {"start": v(86.47, 9.88) * mm, "end": v(86.34, 9.84) * mm});
            skLineSegment(sketch, "E11436", {"start": v(86.34, 9.84) * mm, "end": v(86.23, 9.81) * mm});
            skLineSegment(sketch, "E11437", {"start": v(86.23, 9.81) * mm, "end": v(86.18, 9.81) * mm});
            skLineSegment(sketch, "E11438", {"start": v(86.18, 9.81) * mm, "end": v(86.13, 9.82) * mm});
            skLineSegment(sketch, "E11439", {"start": v(86.13, 9.82) * mm, "end": v(86.08, 9.83) * mm});
            skLineSegment(sketch, "E11440", {"start": v(86.08, 9.83) * mm, "end": v(86.04, 9.86) * mm});
            skLineSegment(sketch, "E11441", {"start": v(86.04, 9.86) * mm, "end": v(85.94, 9.95) * mm});
            skLineSegment(sketch, "E11442", {"start": v(85.94, 9.95) * mm, "end": v(85.86, 10.05) * mm});
            skLineSegment(sketch, "E11443", {"start": v(85.86, 10.05) * mm, "end": v(85.8, 10.14) * mm});
            skLineSegment(sketch, "E11444", {"start": v(85.8, 10.14) * mm, "end": v(85.75, 10.24) * mm});
            skLineSegment(sketch, "E11445", {"start": v(85.75, 10.24) * mm, "end": v(85.72, 10.34) * mm});
            skLineSegment(sketch, "E11446", {"start": v(85.72, 10.34) * mm, "end": v(85.7, 10.44) * mm});
            skLineSegment(sketch, "E11447", {"start": v(85.7, 10.44) * mm, "end": v(85.68, 10.54) * mm});
            skLineSegment(sketch, "E11448", {"start": v(85.68, 10.54) * mm, "end": v(85.67, 10.65) * mm});
            skLineSegment(sketch, "E11449", {"start": v(85.67, 10.65) * mm, "end": v(85.68, 10.86) * mm});
            skLineSegment(sketch, "E11450", {"start": v(85.68, 10.86) * mm, "end": v(85.7, 11.09) * mm});
            skLineSegment(sketch, "E11451", {"start": v(85.7, 11.09) * mm, "end": v(85.72, 11.32) * mm});
            skLineSegment(sketch, "E11452", {"start": v(85.72, 11.32) * mm, "end": v(85.73, 11.57) * mm});
            skLineSegment(sketch, "E11453", {"start": v(85.73, 11.57) * mm, "end": v(85.72, 12.14) * mm});
            skLineSegment(sketch, "E11454", {"start": v(85.72, 12.14) * mm, "end": v(85.69, 12.73) * mm});
            skLineSegment(sketch, "E11455", {"start": v(85.69, 12.73) * mm, "end": v(85.64, 13.33) * mm});
            skLineSegment(sketch, "E11456", {"start": v(85.64, 13.33) * mm, "end": v(85.58, 13.95) * mm});
            skLineSegment(sketch, "E11457", {"start": v(85.58, 13.95) * mm, "end": v(85.44, 15.2) * mm});
            skLineSegment(sketch, "E11458", {"start": v(85.44, 15.2) * mm, "end": v(85.37, 15.85) * mm});
            skLineSegment(sketch, "E11459", {"start": v(85.37, 15.85) * mm, "end": v(85.31, 16.5) * mm});
            skLineSegment(sketch, "E11460", {"start": v(85.31, 16.5) * mm, "end": v(85.28, 16.78) * mm});
            skLineSegment(sketch, "E11461", {"start": v(85.28, 16.78) * mm, "end": v(85.24, 17.05) * mm});
            skLineSegment(sketch, "E11462", {"start": v(85.24, 17.05) * mm, "end": v(85.2, 17.33) * mm});
            skLineSegment(sketch, "E11463", {"start": v(85.2, 17.33) * mm, "end": v(85.14, 17.61) * mm});
            skLineSegment(sketch, "E11464", {"start": v(85.14, 17.61) * mm, "end": v(85, 18.16) * mm});
            skLineSegment(sketch, "E11465", {"start": v(85, 18.16) * mm, "end": v(84.85, 18.72) * mm});
            skLineSegment(sketch, "E11466", {"start": v(84.85, 18.72) * mm, "end": v(84.66, 19.27) * mm});
            skLineSegment(sketch, "E11467", {"start": v(84.66, 19.27) * mm, "end": v(84.46, 19.8) * mm});
            skLineSegment(sketch, "E11468", {"start": v(84.46, 19.8) * mm, "end": v(84.23, 20.35) * mm});
            skLineSegment(sketch, "E11469", {"start": v(84.23, 20.35) * mm, "end": v(84, 20.88) * mm});
            skLineSegment(sketch, "E11470", {"start": v(84, 20.88) * mm, "end": v(83.74, 21.4) * mm});
            skLineSegment(sketch, "E11471", {"start": v(83.74, 21.4) * mm, "end": v(83.47, 21.93) * mm});
            skLineSegment(sketch, "E11472", {"start": v(83.47, 21.93) * mm, "end": v(82.92, 22.94) * mm});
            skLineSegment(sketch, "E11473", {"start": v(82.92, 22.94) * mm, "end": v(82.36, 23.92) * mm});
            skLineSegment(sketch, "E11474", {"start": v(82.36, 23.92) * mm, "end": v(81.82, 24.85) * mm});
            skLineSegment(sketch, "E11475", {"start": v(81.82, 24.85) * mm, "end": v(81.79, 24.9) * mm});
            skLineSegment(sketch, "E11476", {"start": v(81.79, 24.9) * mm, "end": v(81.74, 24.93) * mm});
            skLineSegment(sketch, "E11477", {"start": v(81.74, 24.93) * mm, "end": v(81.69, 24.94) * mm});
            skLineSegment(sketch, "E11478", {"start": v(81.69, 24.94) * mm, "end": v(81.63, 24.95) * mm});
            skLineSegment(sketch, "E11479", {"start": v(81.63, 24.95) * mm, "end": v(81.56, 24.94) * mm});
            skLineSegment(sketch, "E11480", {"start": v(81.56, 24.94) * mm, "end": v(81.48, 24.92) * mm});
            skLineSegment(sketch, "E11481", {"start": v(81.48, 24.92) * mm, "end": v(81.3, 24.87) * mm});
            skLineSegment(sketch, "E11482", {"start": v(81.3, 24.87) * mm, "end": v(80.9, 24.7) * mm});
            skLineSegment(sketch, "E11483", {"start": v(80.9, 24.7) * mm, "end": v(80.68, 24.61) * mm});
            skLineSegment(sketch, "E11484", {"start": v(80.68, 24.61) * mm, "end": v(80.45, 24.53) * mm});
            skLineSegment(sketch, "E11485", {"start": v(80.45, 24.53) * mm, "end": v(80.23, 24.47) * mm});
            skLineSegment(sketch, "E11486", {"start": v(80.23, 24.47) * mm, "end": v(80.12, 24.45) * mm});
            skLineSegment(sketch, "E11487", {"start": v(80.12, 24.45) * mm, "end": v(80.02, 24.44) * mm});
            skLineSegment(sketch, "E11488", {"start": v(80.02, 24.44) * mm, "end": v(79.92, 24.44) * mm});
            skLineSegment(sketch, "E11489", {"start": v(79.92, 24.44) * mm, "end": v(79.82, 24.45) * mm});
            skLineSegment(sketch, "E11490", {"start": v(79.82, 24.45) * mm, "end": v(79.72, 24.47) * mm});
            skLineSegment(sketch, "E11491", {"start": v(79.72, 24.47) * mm, "end": v(79.64, 24.5) * mm});
            skLineSegment(sketch, "E11492", {"start": v(79.64, 24.5) * mm, "end": v(79.55, 24.56) * mm});
            skLineSegment(sketch, "E11493", {"start": v(79.55, 24.56) * mm, "end": v(79.48, 24.63) * mm});
            skLineSegment(sketch, "E11494", {"start": v(79.48, 24.63) * mm, "end": v(79.4, 24.71) * mm});
            skLineSegment(sketch, "E11495", {"start": v(79.4, 24.71) * mm, "end": v(79.35, 24.82) * mm});
            skLineSegment(sketch, "E11496", {"start": v(79.35, 24.82) * mm, "end": v(79.3, 24.94) * mm});
            skLineSegment(sketch, "E11497", {"start": v(79.3, 24.94) * mm, "end": v(79.26, 25.1) * mm});
            skLineSegment(sketch, "E11498", {"start": v(79.26, 25.1) * mm, "end": v(79.23, 25.26) * mm});
            skLineSegment(sketch, "E11499", {"start": v(79.23, 25.26) * mm, "end": v(79.2, 25.46) * mm});
            skLineSegment(sketch, "E11500", {"start": v(79.2, 25.46) * mm, "end": v(79.18, 25.74) * mm});
            skLineSegment(sketch, "E11501", {"start": v(79.18, 25.74) * mm, "end": v(79.15, 26.04) * mm});
            skLineSegment(sketch, "E11502", {"start": v(79.15, 26.04) * mm, "end": v(79.1, 26.37) * mm});
            skLineSegment(sketch, "E11503", {"start": v(79.1, 26.37) * mm, "end": v(79.04, 26.71) * mm});
            skLineSegment(sketch, "E11504", {"start": v(79.04, 26.71) * mm, "end": v(78.9, 27.47) * mm});
            skLineSegment(sketch, "E11505", {"start": v(78.9, 27.47) * mm, "end": v(78.7, 28.29) * mm});
            skLineSegment(sketch, "E11506", {"start": v(78.7, 28.29) * mm, "end": v(78.47, 29.17) * mm});
            skLineSegment(sketch, "E11507", {"start": v(78.47, 29.17) * mm, "end": v(78.2, 30.1) * mm});
            skLineSegment(sketch, "E11508", {"start": v(78.2, 30.1) * mm, "end": v(77.89, 31.06) * mm});
            skLineSegment(sketch, "E11509", {"start": v(77.89, 31.06) * mm, "end": v(77.54, 32.04) * mm});
            skLineSegment(sketch, "E11510", {"start": v(77.54, 32.04) * mm, "end": v(77.17, 33.03) * mm});
            skLineSegment(sketch, "E11511", {"start": v(77.17, 33.03) * mm, "end": v(76.76, 34.03) * mm});
            skLineSegment(sketch, "E11512", {"start": v(76.76, 34.03) * mm, "end": v(76.55, 34.52) * mm});
            skLineSegment(sketch, "E11513", {"start": v(76.55, 34.52) * mm, "end": v(76.33, 35.01) * mm});
            skLineSegment(sketch, "E11514", {"start": v(76.33, 35.01) * mm, "end": v(76.1, 35.5) * mm});
            skLineSegment(sketch, "E11515", {"start": v(76.1, 35.5) * mm, "end": v(75.86, 35.98) * mm});
            skLineSegment(sketch, "E11516", {"start": v(75.86, 35.98) * mm, "end": v(75.62, 36.44) * mm});
            skLineSegment(sketch, "E11517", {"start": v(75.62, 36.44) * mm, "end": v(75.37, 36.9) * mm});
            skLineSegment(sketch, "E11518", {"start": v(75.37, 36.9) * mm, "end": v(75.12, 37.35) * mm});
            skLineSegment(sketch, "E11519", {"start": v(75.12, 37.35) * mm, "end": v(74.86, 37.79) * mm});
            skLineSegment(sketch, "E11520", {"start": v(74.86, 37.79) * mm, "end": v(74.6, 38.2) * mm});
            skLineSegment(sketch, "E11521", {"start": v(74.6, 38.2) * mm, "end": v(74.33, 38.6) * mm});
            skLineSegment(sketch, "E11522", {"start": v(74.33, 38.6) * mm, "end": v(74.06, 39) * mm});
            skLineSegment(sketch, "E11523", {"start": v(74.06, 39) * mm, "end": v(73.78, 39.37) * mm});
            skLineSegment(sketch, "E11524", {"start": v(73.78, 39.37) * mm, "end": v(73.64, 39.55) * mm});
            skLineSegment(sketch, "E11525", {"start": v(73.64, 39.55) * mm, "end": v(73.49, 39.71) * mm});
            skLineSegment(sketch, "E11526", {"start": v(73.49, 39.71) * mm, "end": v(73.4, 39.79) * mm});
            skLineSegment(sketch, "E11527", {"start": v(73.4, 39.79) * mm, "end": v(73.32, 39.85) * mm});
            skLineSegment(sketch, "E11528", {"start": v(73.32, 39.85) * mm, "end": v(73.23, 39.9) * mm});
            skLineSegment(sketch, "E11529", {"start": v(73.23, 39.9) * mm, "end": v(73.13, 39.94) * mm});
            skLineSegment(sketch, "E11530", {"start": v(73.13, 39.94) * mm, "end": v(73.02, 39.96) * mm});
            skLineSegment(sketch, "E11531", {"start": v(73.02, 39.96) * mm, "end": v(72.9, 39.96) * mm});
            skLineSegment(sketch, "E11532", {"start": v(72.9, 39.96) * mm, "end": v(72.75, 39.94) * mm});
            skLineSegment(sketch, "E11533", {"start": v(72.75, 39.94) * mm, "end": v(72.6, 39.9) * mm});
            skLineSegment(sketch, "E11534", {"start": v(72.6, 39.9) * mm, "end": v(72.44, 39.84) * mm});
            skLineSegment(sketch, "E11535", {"start": v(72.44, 39.84) * mm, "end": v(72.25, 39.74) * mm});
            skLineSegment(sketch, "E11536", {"start": v(72.25, 39.74) * mm, "end": v(72.05, 39.62) * mm});
            skLineSegment(sketch, "E11537", {"start": v(72.05, 39.62) * mm, "end": v(71.82, 39.47) * mm});
            skLineSegment(sketch, "E11538", {"start": v(71.82, 39.47) * mm, "end": v(71.76, 39.4) * mm});
            skLineSegment(sketch, "E11539", {"start": v(71.76, 39.4) * mm, "end": v(71.69, 39.32) * mm});
            skLineSegment(sketch, "E11540", {"start": v(71.69, 39.32) * mm, "end": v(71.55, 39.12) * mm});
            skLineSegment(sketch, "E11541", {"start": v(71.55, 39.12) * mm, "end": v(71.42, 38.88) * mm});
            skLineSegment(sketch, "E11542", {"start": v(71.42, 38.88) * mm, "end": v(71.27, 38.63) * mm});
            skLineSegment(sketch, "E11543", {"start": v(71.27, 38.63) * mm, "end": v(71.19, 38.52) * mm});
            skLineSegment(sketch, "E11544", {"start": v(71.19, 38.52) * mm, "end": v(71.1, 38.42) * mm});
            skLineSegment(sketch, "E11545", {"start": v(71.1, 38.42) * mm, "end": v(71.01, 38.33) * mm});
            skLineSegment(sketch, "E11546", {"start": v(71.01, 38.33) * mm, "end": v(70.92, 38.27) * mm});
            skLineSegment(sketch, "E11547", {"start": v(70.92, 38.27) * mm, "end": v(70.82, 38.22) * mm});
            skLineSegment(sketch, "E11548", {"start": v(70.82, 38.22) * mm, "end": v(70.7, 38.2) * mm});
            skLineSegment(sketch, "E11549", {"start": v(70.7, 38.2) * mm, "end": v(70.65, 38.2) * mm});
            skLineSegment(sketch, "E11550", {"start": v(70.65, 38.2) * mm, "end": v(70.6, 38.22) * mm});
            skLineSegment(sketch, "E11551", {"start": v(70.6, 38.22) * mm, "end": v(70.53, 38.24) * mm});
            skLineSegment(sketch, "E11552", {"start": v(70.53, 38.24) * mm, "end": v(70.47, 38.26) * mm});
            skLineSegment(sketch, "E11553", {"start": v(70.47, 38.26) * mm, "end": v(70.4, 38.31) * mm});
            skLineSegment(sketch, "E11554", {"start": v(70.4, 38.31) * mm, "end": v(70.33, 38.39) * mm});
            skLineSegment(sketch, "E11555", {"start": v(70.33, 38.39) * mm, "end": v(70.27, 38.47) * mm});
            skLineSegment(sketch, "E11556", {"start": v(70.27, 38.47) * mm, "end": v(70.22, 38.58) * mm});
            skLineSegment(sketch, "E11557", {"start": v(70.22, 38.58) * mm, "end": v(70.17, 38.7) * mm});
            skLineSegment(sketch, "E11558", {"start": v(70.17, 38.7) * mm, "end": v(70.13, 38.83) * mm});
            skLineSegment(sketch, "E11559", {"start": v(70.13, 38.83) * mm, "end": v(70.07, 39.11) * mm});
            skLineSegment(sketch, "E11560", {"start": v(70.07, 39.11) * mm, "end": v(69.95, 39.73) * mm});
            skLineSegment(sketch, "E11561", {"start": v(69.95, 39.73) * mm, "end": v(69.88, 40.02) * mm});
            skLineSegment(sketch, "E11562", {"start": v(69.88, 40.02) * mm, "end": v(69.85, 40.16) * mm});
            skLineSegment(sketch, "E11563", {"start": v(69.85, 40.16) * mm, "end": v(69.8, 40.29) * mm});
            skLineSegment(sketch, "E11564", {"start": v(69.8, 40.29) * mm, "end": v(69.63, 40.74) * mm});
            skLineSegment(sketch, "E11565", {"start": v(69.63, 40.74) * mm, "end": v(69.45, 41.18) * mm});
            skLineSegment(sketch, "E11566", {"start": v(69.45, 41.18) * mm, "end": v(69.27, 41.62) * mm});
            skLineSegment(sketch, "E11567", {"start": v(69.27, 41.62) * mm, "end": v(69.08, 42.05) * mm});
            skLineSegment(sketch, "E11568", {"start": v(69.08, 42.05) * mm, "end": v(68.88, 42.47) * mm});
            skLineSegment(sketch, "E11569", {"start": v(68.88, 42.47) * mm, "end": v(68.68, 42.89) * mm});
            skLineSegment(sketch, "E11570", {"start": v(68.68, 42.89) * mm, "end": v(68.47, 43.3) * mm});
            skLineSegment(sketch, "E11571", {"start": v(68.47, 43.3) * mm, "end": v(68.26, 43.7) * mm});
            skLineSegment(sketch, "E11572", {"start": v(68.26, 43.7) * mm, "end": v(67.98, 44.2) * mm});
            skLineSegment(sketch, "E11573", {"start": v(67.98, 44.2) * mm, "end": v(67.7, 44.68) * mm});
            skLineSegment(sketch, "E11574", {"start": v(67.7, 44.68) * mm, "end": v(67.4, 45.15) * mm});
            skLineSegment(sketch, "E11575", {"start": v(67.4, 45.15) * mm, "end": v(67.1, 45.62) * mm});
            skLineSegment(sketch, "E11576", {"start": v(67.1, 45.62) * mm, "end": v(66.79, 46.07) * mm});
            skLineSegment(sketch, "E11577", {"start": v(66.79, 46.07) * mm, "end": v(66.47, 46.52) * mm});
            skLineSegment(sketch, "E11578", {"start": v(66.47, 46.52) * mm, "end": v(66.14, 46.96) * mm});
            skLineSegment(sketch, "E11579", {"start": v(66.14, 46.96) * mm, "end": v(65.81, 47.38) * mm});
            skLineSegment(sketch, "E11580", {"start": v(65.81, 47.38) * mm, "end": v(65.47, 47.8) * mm});
            skLineSegment(sketch, "E11581", {"start": v(65.47, 47.8) * mm, "end": v(65.13, 48.2) * mm});
            skLineSegment(sketch, "E11582", {"start": v(65.13, 48.2) * mm, "end": v(64.77, 48.61) * mm});
            skLineSegment(sketch, "E11583", {"start": v(64.77, 48.61) * mm, "end": v(64.42, 49) * mm});
            skLineSegment(sketch, "E11584", {"start": v(64.42, 49) * mm, "end": v(64.05, 49.39) * mm});
            skLineSegment(sketch, "E11585", {"start": v(64.05, 49.39) * mm, "end": v(63.68, 49.77) * mm});
            skLineSegment(sketch, "E11586", {"start": v(63.68, 49.77) * mm, "end": v(63.3, 50.14) * mm});
            skLineSegment(sketch, "E11587", {"start": v(63.3, 50.14) * mm, "end": v(62.93, 50.5) * mm});
            skLineSegment(sketch, "E11588", {"start": v(62.93, 50.5) * mm, "end": v(62.7, 50.72) * mm});
            skLineSegment(sketch, "E11589", {"start": v(62.7, 50.72) * mm, "end": v(62.57, 50.81) * mm});
            skLineSegment(sketch, "E11590", {"start": v(62.57, 50.81) * mm, "end": v(62.44, 50.9) * mm});
            skLineSegment(sketch, "E11591", {"start": v(62.44, 50.9) * mm, "end": v(62.3, 50.96) * mm});
            skLineSegment(sketch, "E11592", {"start": v(62.3, 50.96) * mm, "end": v(62.16, 51) * mm});
            skLineSegment(sketch, "E11593", {"start": v(62.16, 51) * mm, "end": v(62.01, 51.02) * mm});
            skLineSegment(sketch, "E11594", {"start": v(62.01, 51.02) * mm, "end": v(61.93, 51.01) * mm});
            skLineSegment(sketch, "E11595", {"start": v(61.93, 51.01) * mm, "end": v(61.85, 51) * mm});
            skLineSegment(sketch, "E11596", {"start": v(61.85, 51) * mm, "end": v(61.76, 50.98) * mm});
            skLineSegment(sketch, "E11597", {"start": v(61.76, 50.98) * mm, "end": v(61.67, 50.96) * mm});
            skLineSegment(sketch, "E11598", {"start": v(61.67, 50.96) * mm, "end": v(61.58, 50.92) * mm});
            skLineSegment(sketch, "E11599", {"start": v(61.58, 50.92) * mm, "end": v(61.48, 50.87) * mm});
            skLineSegment(sketch, "E11600", {"start": v(61.48, 50.87) * mm, "end": v(61.27, 50.74) * mm});
            skLineSegment(sketch, "E11601", {"start": v(61.27, 50.74) * mm, "end": v(61.04, 50.57) * mm});
            skLineSegment(sketch, "E11602", {"start": v(61.04, 50.57) * mm, "end": v(60.8, 50.34) * mm});
            skLineSegment(sketch, "E11603", {"start": v(60.8, 50.34) * mm, "end": v(60.53, 50.06) * mm});
            skLineSegment(sketch, "E11604", {"start": v(60.53, 50.06) * mm, "end": v(60.25, 49.72) * mm});
            skLineSegment(sketch, "E11605", {"start": v(60.25, 49.72) * mm, "end": v(59.93, 49.32) * mm});
            skLineSegment(sketch, "E11606", {"start": v(59.93, 49.32) * mm, "end": v(59.86, 49.21) * mm});
            skLineSegment(sketch, "E11607", {"start": v(59.86, 49.21) * mm, "end": v(59.79, 49.13) * mm});
            skLineSegment(sketch, "E11608", {"start": v(59.79, 49.13) * mm, "end": v(59.75, 49.1) * mm});
            skLineSegment(sketch, "E11609", {"start": v(59.75, 49.1) * mm, "end": v(59.7, 49.08) * mm});
            skLineSegment(sketch, "E11610", {"start": v(59.7, 49.08) * mm, "end": v(59.65, 49.08) * mm});
            skLineSegment(sketch, "E11611", {"start": v(59.65, 49.08) * mm, "end": v(59.58, 49.1) * mm});
            skLineSegment(sketch, "E11612", {"start": v(59.58, 49.1) * mm, "end": v(59.53, 49.12) * mm});
            skLineSegment(sketch, "E11613", {"start": v(59.53, 49.12) * mm, "end": v(59.5, 49.15) * mm});
            skLineSegment(sketch, "E11614", {"start": v(59.5, 49.15) * mm, "end": v(59.46, 49.19) * mm});
            skLineSegment(sketch, "E11615", {"start": v(59.46, 49.19) * mm, "end": v(59.42, 49.24) * mm});
            skLineSegment(sketch, "E11616", {"start": v(59.42, 49.24) * mm, "end": v(59.37, 49.35) * mm});
            skLineSegment(sketch, "E11617", {"start": v(59.37, 49.35) * mm, "end": v(59.34, 49.48) * mm});
            skLineSegment(sketch, "E11618", {"start": v(59.34, 49.48) * mm, "end": v(59.28, 49.78) * mm});
            skLineSegment(sketch, "E11619", {"start": v(59.28, 49.78) * mm, "end": v(59.24, 49.94) * mm});
            skLineSegment(sketch, "E11620", {"start": v(59.24, 49.94) * mm, "end": v(59.2, 50.09) * mm});
            skLineSegment(sketch, "E11621", {"start": v(59.2, 50.09) * mm, "end": v(59.05, 50.48) * mm});
            skLineSegment(sketch, "E11622", {"start": v(59.05, 50.48) * mm, "end": v(58.89, 50.86) * mm});
            skLineSegment(sketch, "E11623", {"start": v(58.89, 50.86) * mm, "end": v(58.7, 51.25) * mm});
            skLineSegment(sketch, "E11624", {"start": v(58.7, 51.25) * mm, "end": v(58.5, 51.62) * mm});
            skLineSegment(sketch, "E11625", {"start": v(58.5, 51.62) * mm, "end": v(58.28, 52) * mm});
            skLineSegment(sketch, "E11626", {"start": v(58.28, 52) * mm, "end": v(58.05, 52.37) * mm});
            skLineSegment(sketch, "E11627", {"start": v(58.05, 52.37) * mm, "end": v(57.81, 52.73) * mm});
            skLineSegment(sketch, "E11628", {"start": v(57.81, 52.73) * mm, "end": v(57.56, 53.09) * mm});
            skLineSegment(sketch, "E11629", {"start": v(57.56, 53.09) * mm, "end": v(57.3, 53.44) * mm});
            skLineSegment(sketch, "E11630", {"start": v(57.3, 53.44) * mm, "end": v(57.02, 53.78) * mm});
            skLineSegment(sketch, "E11631", {"start": v(57.02, 53.78) * mm, "end": v(56.74, 54.12) * mm});
            skLineSegment(sketch, "E11632", {"start": v(56.74, 54.12) * mm, "end": v(56.45, 54.45) * mm});
            skLineSegment(sketch, "E11633", {"start": v(56.45, 54.45) * mm, "end": v(55.87, 55.09) * mm});
            skLineSegment(sketch, "E11634", {"start": v(55.87, 55.09) * mm, "end": v(55.28, 55.7) * mm});
            skLineSegment(sketch, "E11635", {"start": v(55.28, 55.7) * mm, "end": v(54.87, 56.08) * mm});
            skLineSegment(sketch, "E11636", {"start": v(54.87, 56.08) * mm, "end": v(54.15, 56.72) * mm});
            skLineSegment(sketch, "E11637", {"start": v(54.15, 56.72) * mm, "end": v(53.3, 57.45) * mm});
            skLineSegment(sketch, "E11638", {"start": v(53.3, 57.45) * mm, "end": v(52.89, 57.8) * mm});
            skLineSegment(sketch, "E11639", {"start": v(52.89, 57.8) * mm, "end": v(52.5, 58.1) * mm});
            skLineSegment(sketch, "E11640", {"start": v(52.5, 58.1) * mm, "end": v(52.1, 58.4) * mm});
            skLineSegment(sketch, "E11641", {"start": v(52.1, 58.4) * mm, "end": v(51.9, 58.56) * mm});
            skLineSegment(sketch, "E11642", {"start": v(51.9, 58.56) * mm, "end": v(51.67, 58.72) * mm});
            skLineSegment(sketch, "E11643", {"start": v(51.67, 58.72) * mm, "end": v(51.44, 58.86) * mm});
            skLineSegment(sketch, "E11644", {"start": v(51.44, 58.86) * mm, "end": v(51.21, 58.99) * mm});
            skLineSegment(sketch, "E11645", {"start": v(51.21, 58.99) * mm, "end": v(50.98, 59.1) * mm});
            skLineSegment(sketch, "E11646", {"start": v(50.98, 59.1) * mm, "end": v(50.75, 59.18) * mm});
            skLineSegment(sketch, "E11647", {"start": v(50.75, 59.18) * mm, "end": v(50.6, 59.22) * mm});
            skLineSegment(sketch, "E11648", {"start": v(50.6, 59.22) * mm, "end": v(50.44, 59.25) * mm});
            skLineSegment(sketch, "E11649", {"start": v(50.44, 59.25) * mm, "end": v(50.12, 59.28) * mm});
            skLineSegment(sketch, "E11650", {"start": v(50.12, 59.28) * mm, "end": v(49.8, 59.3) * mm});
            skLineSegment(sketch, "E11651", {"start": v(49.8, 59.3) * mm, "end": v(49.47, 59.29) * mm});
            skLineSegment(sketch, "E11652", {"start": v(49.47, 59.29) * mm, "end": v(49.14, 59.29) * mm});
            skLineSegment(sketch, "E11653", {"start": v(49.14, 59.29) * mm, "end": v(48.81, 59.3) * mm});
            skLineSegment(sketch, "E11654", {"start": v(48.81, 59.3) * mm, "end": v(48.5, 59.32) * mm});
            skLineSegment(sketch, "E11655", {"start": v(48.5, 59.32) * mm, "end": v(48.34, 59.35) * mm});
            skLineSegment(sketch, "E11656", {"start": v(48.34, 59.35) * mm, "end": v(48.18, 59.38) * mm});
            skLineSegment(sketch, "E11657", {"start": v(48.18, 59.38) * mm, "end": v(48.08, 59.41) * mm});
            skLineSegment(sketch, "E11658", {"start": v(48.08, 59.41) * mm, "end": v(47.99, 59.45) * mm});
            skLineSegment(sketch, "E11659", {"start": v(47.99, 59.45) * mm, "end": v(47.8, 59.56) * mm});
            skLineSegment(sketch, "E11660", {"start": v(47.8, 59.56) * mm, "end": v(47.6, 59.68) * mm});
            skLineSegment(sketch, "E11661", {"start": v(47.6, 59.68) * mm, "end": v(47.4, 59.83) * mm});
            skLineSegment(sketch, "E11662", {"start": v(47.4, 59.83) * mm, "end": v(47.04, 60.13) * mm});
            skLineSegment(sketch, "E11663", {"start": v(47.04, 60.13) * mm, "end": v(46.87, 60.27) * mm});
            skLineSegment(sketch, "E11664", {"start": v(46.87, 60.27) * mm, "end": v(46.7, 60.4) * mm});
            skLineSegment(sketch, "E11665", {"start": v(46.7, 60.4) * mm, "end": v(46.35, 60.63) * mm});
            skLineSegment(sketch, "E11666", {"start": v(46.35, 60.63) * mm, "end": v(45.92, 60.9) * mm});
            skLineSegment(sketch, "E11667", {"start": v(45.92, 60.9) * mm, "end": v(44.9, 61.52) * mm});
            skLineSegment(sketch, "E11668", {"start": v(44.9, 61.52) * mm, "end": v(43.79, 62.18) * mm});
            skLineSegment(sketch, "E11669", {"start": v(43.79, 62.18) * mm, "end": v(42.7, 62.79) * mm});
            skLineSegment(sketch, "E11670", {"start": v(42.7, 62.79) * mm, "end": v(42.4, 62.96) * mm});
            skLineSegment(sketch, "E11671", {"start": v(42.4, 62.96) * mm, "end": v(42.1, 63.15) * mm});
            skLineSegment(sketch, "E11672", {"start": v(42.1, 63.15) * mm, "end": v(41.47, 63.55) * mm});
            skLineSegment(sketch, "E11673", {"start": v(41.47, 63.55) * mm, "end": v(41.14, 63.75) * mm});
            skLineSegment(sketch, "E11674", {"start": v(41.14, 63.75) * mm, "end": v(40.82, 63.92) * mm});
            skLineSegment(sketch, "E11675", {"start": v(40.82, 63.92) * mm, "end": v(40.66, 64) * mm});
            skLineSegment(sketch, "E11676", {"start": v(40.66, 64) * mm, "end": v(40.5, 64.06) * mm});
            skLineSegment(sketch, "E11677", {"start": v(40.5, 64.06) * mm, "end": v(40.34, 64.12) * mm});
            skLineSegment(sketch, "E11678", {"start": v(40.34, 64.12) * mm, "end": v(40.18, 64.17) * mm});
            skLineSegment(sketch, "E11679", {"start": v(40.18, 64.17) * mm, "end": v(40.07, 64.17) * mm});
            skLineSegment(sketch, "E11680", {"start": v(40.07, 64.17) * mm, "end": v(39.95, 64.17) * mm});
            skLineSegment(sketch, "E11681", {"start": v(39.95, 64.17) * mm, "end": v(39.93, 64.16) * mm});
            skLineSegment(sketch, "E11682", {"start": v(39.93, 64.16) * mm, "end": v(39.9, 64.13) * mm});
            skLineSegment(sketch, "E11683", {"start": v(39.9, 64.13) * mm, "end": v(39.81, 64.04) * mm});
            skLineSegment(sketch, "E11684", {"start": v(39.81, 64.04) * mm, "end": v(39.71, 63.9) * mm});
            skLineSegment(sketch, "E11685", {"start": v(39.71, 63.9) * mm, "end": v(39.6, 63.7) * mm});
            skLineSegment(sketch, "E11686", {"start": v(39.6, 63.7) * mm, "end": v(39.46, 63.48) * mm});
            skLineSegment(sketch, "E11687", {"start": v(39.46, 63.48) * mm, "end": v(39.33, 63.22) * mm});
            skLineSegment(sketch, "E11688", {"start": v(39.33, 63.22) * mm, "end": v(39.19, 62.93) * mm});
            skLineSegment(sketch, "E11689", {"start": v(39.19, 62.93) * mm, "end": v(39.04, 62.62) * mm});
            skLineSegment(sketch, "E11690", {"start": v(39.04, 62.62) * mm, "end": v(38.46, 61.3) * mm});
            skLineSegment(sketch, "E11691", {"start": v(38.46, 61.3) * mm, "end": v(38.44, 61.23) * mm});
            skLineSegment(sketch, "E11692", {"start": v(38.44, 61.23) * mm, "end": v(38.43, 61.16) * mm});
            skLineSegment(sketch, "E11693", {"start": v(38.43, 61.16) * mm, "end": v(38.4, 61.1) * mm});
            skLineSegment(sketch, "E11694", {"start": v(38.4, 61.1) * mm, "end": v(38.38, 61.08) * mm});
            skLineSegment(sketch, "E11695", {"start": v(38.38, 61.08) * mm, "end": v(38.36, 61.07) * mm});
            skLineSegment(sketch, "E11696", {"start": v(38.36, 61.07) * mm, "end": v(38.31, 61.07) * mm});
            skLineSegment(sketch, "E11697", {"start": v(38.31, 61.07) * mm, "end": v(38.27, 61.1) * mm});
            skLineSegment(sketch, "E11698", {"start": v(38.27, 61.1) * mm, "end": v(38.23, 61.13) * mm});
            skLineSegment(sketch, "E11699", {"start": v(38.23, 61.13) * mm, "end": v(38.2, 61.18) * mm});
            skLineSegment(sketch, "E11700", {"start": v(38.2, 61.18) * mm, "end": v(38.14, 61.3) * mm});
            skLineSegment(sketch, "E11701", {"start": v(38.14, 61.3) * mm, "end": v(38.07, 61.4) * mm});
            skLineSegment(sketch, "E11702", {"start": v(38.07, 61.4) * mm, "end": v(37.62, 61.92) * mm});
            skLineSegment(sketch, "E11703", {"start": v(37.62, 61.92) * mm, "end": v(37.44, 62.11) * mm});
            skLineSegment(sketch, "E11704", {"start": v(37.44, 62.11) * mm, "end": v(37.23, 62.32) * mm});
            skLineSegment(sketch, "E11705", {"start": v(37.23, 62.32) * mm, "end": v(36.98, 62.55) * mm});
            skLineSegment(sketch, "E11706", {"start": v(36.98, 62.55) * mm, "end": v(36.7, 62.78) * mm});
            skLineSegment(sketch, "E11707", {"start": v(36.7, 62.78) * mm, "end": v(36.42, 63) * mm});
            skLineSegment(sketch, "E11708", {"start": v(36.42, 63) * mm, "end": v(36.13, 63.23) * mm});
            skLineSegment(sketch, "E11709", {"start": v(36.13, 63.23) * mm, "end": v(35.84, 63.43) * mm});
            skLineSegment(sketch, "E11710", {"start": v(35.84, 63.43) * mm, "end": v(35.56, 63.62) * mm});
            skLineSegment(sketch, "E11711", {"start": v(35.56, 63.62) * mm, "end": v(35.24, 63.83) * mm});
            skLineSegment(sketch, "E11712", {"start": v(35.24, 63.83) * mm, "end": v(34.9, 64.06) * mm});
            skLineSegment(sketch, "E11713", {"start": v(34.9, 64.06) * mm, "end": v(34.57, 64.28) * mm});
            skLineSegment(sketch, "E11714", {"start": v(34.57, 64.28) * mm, "end": v(34.4, 64.37) * mm});
            skLineSegment(sketch, "E11715", {"start": v(34.4, 64.37) * mm, "end": v(34.24, 64.45) * mm});
            skLineSegment(sketch, "E11716", {"start": v(34.24, 64.45) * mm, "end": v(34.04, 64.53) * mm});
            skLineSegment(sketch, "E11717", {"start": v(34.04, 64.53) * mm, "end": v(33.82, 64.6) * mm});
            skLineSegment(sketch, "E11718", {"start": v(33.82, 64.6) * mm, "end": v(33.36, 64.73) * mm});
            skLineSegment(sketch, "E11719", {"start": v(33.36, 64.73) * mm, "end": v(32.9, 64.84) * mm});
            skLineSegment(sketch, "E11720", {"start": v(32.9, 64.84) * mm, "end": v(32.46, 64.95) * mm});
            skLineSegment(sketch, "E11721", {"start": v(32.46, 64.95) * mm, "end": v(32, 65.07) * mm});
            skLineSegment(sketch, "E11722", {"start": v(32, 65.07) * mm, "end": v(31.52, 65.18) * mm});
            skLineSegment(sketch, "E11723", {"start": v(31.52, 65.18) * mm, "end": v(31.03, 65.28) * mm});
            skLineSegment(sketch, "E11724", {"start": v(31.03, 65.28) * mm, "end": v(30.53, 65.37) * mm});
            skLineSegment(sketch, "E11725", {"start": v(30.53, 65.37) * mm, "end": v(30.01, 65.44) * mm});
            skLineSegment(sketch, "E11726", {"start": v(30.01, 65.44) * mm, "end": v(29.47, 65.5) * mm});
            skLineSegment(sketch, "E11727", {"start": v(29.47, 65.5) * mm, "end": v(28.9, 65.55) * mm});
            skLineSegment(sketch, "E11728", {"start": v(28.9, 65.55) * mm, "end": v(28.3, 65.58) * mm});
            skLineSegment(sketch, "E11729", {"start": v(28.3, 65.58) * mm, "end": v(27.65, 65.6) * mm});
            skLineSegment(sketch, "E11730", {"start": v(27.65, 65.6) * mm, "end": v(26.96, 65.62) * mm});
            skLineSegment(sketch, "E11731", {"start": v(26.96, 65.62) * mm, "end": v(26.22, 65.62) * mm});
            skLineSegment(sketch, "E11732", {"start": v(26.22, 65.62) * mm, "end": v(25.42, 65.6) * mm});
            skLineSegment(sketch, "E11733", {"start": v(25.42, 65.6) * mm, "end": v(24.57, 65.59) * mm});
            skLineSegment(sketch, "E11734", {"start": v(24.57, 65.59) * mm, "end": v(23.65, 65.56) * mm});
            skLineSegment(sketch, "E11735", {"start": v(23.65, 65.56) * mm, "end": v(21.6, 65.46) * mm});
            skLineSegment(sketch, "E11736", {"start": v(21.6, 65.46) * mm, "end": v(20.37, 65.42) * mm});
            skLineSegment(sketch, "E11737", {"start": v(20.37, 65.42) * mm, "end": v(19.04, 65.39) * mm});
            skLineSegment(sketch, "E11738", {"start": v(19.04, 65.39) * mm, "end": v(18.36, 65.36) * mm});
            skLineSegment(sketch, "E11739", {"start": v(18.36, 65.36) * mm, "end": v(17.7, 65.33) * mm});
            skLineSegment(sketch, "E11740", {"start": v(17.7, 65.33) * mm, "end": v(17.07, 65.27) * mm});
            skLineSegment(sketch, "E11741", {"start": v(17.07, 65.27) * mm, "end": v(16.48, 65.2) * mm});
            skLineSegment(sketch, "E11742", {"start": v(16.48, 65.2) * mm, "end": v(16.1, 65.13) * mm});
            skLineSegment(sketch, "E11743", {"start": v(16.1, 65.13) * mm, "end": v(15.7, 65.02) * mm});
            skLineSegment(sketch, "E11744", {"start": v(15.7, 65.02) * mm, "end": v(15.3, 64.91) * mm});
            skLineSegment(sketch, "E11745", {"start": v(15.3, 64.91) * mm, "end": v(14.93, 64.81) * mm});
            skLineSegment(sketch, "E11746", {"start": v(14.93, 64.81) * mm, "end": v(14.62, 64.72) * mm});
            skLineSegment(sketch, "E11747", {"start": v(14.62, 64.72) * mm, "end": v(14.3, 64.63) * mm});
            skLineSegment(sketch, "E11748", {"start": v(14.3, 64.63) * mm, "end": v(14.02, 64.53) * mm});
            skLineSegment(sketch, "E11749", {"start": v(14.02, 64.53) * mm, "end": v(13.75, 64.43) * mm});
            skLineSegment(sketch, "E11750", {"start": v(13.75, 64.43) * mm, "end": v(13.52, 64.32) * mm});
            skLineSegment(sketch, "E11751", {"start": v(13.52, 64.32) * mm, "end": v(13.32, 64.22) * mm});
            skLineSegment(sketch, "E11752", {"start": v(13.32, 64.22) * mm, "end": v(13.17, 64.13) * mm});
            skLineSegment(sketch, "E11753", {"start": v(13.17, 64.13) * mm, "end": v(13.12, 64.09) * mm});
            skLineSegment(sketch, "E11754", {"start": v(13.12, 64.09) * mm, "end": v(13.08, 64.05) * mm});
            skLineSegment(sketch, "E11755", {"start": v(13.08, 64.05) * mm, "end": v(13, 63.96) * mm});
            skLineSegment(sketch, "E11756", {"start": v(13, 63.96) * mm, "end": v(12.9, 63.87) * mm});
            skLineSegment(sketch, "E11757", {"start": v(12.9, 63.87) * mm, "end": v(12.85, 63.82) * mm});
            skLineSegment(sketch, "E11758", {"start": v(12.85, 63.82) * mm, "end": v(12.8, 63.77) * mm});
            skLineSegment(sketch, "E11759", {"start": v(12.8, 63.77) * mm, "end": v(12.78, 63.72) * mm});
            skLineSegment(sketch, "E11760", {"start": v(12.78, 63.72) * mm, "end": v(12.77, 63.67) * mm});
            skLineSegment(sketch, "E11761", {"start": v(12.77, 63.67) * mm, "end": v(12.77, 63.55) * mm});
            skLineSegment(sketch, "E11762", {"start": v(12.77, 63.55) * mm, "end": v(12.8, 63.43) * mm});
            skLineSegment(sketch, "E11763", {"start": v(12.8, 63.43) * mm, "end": v(12.84, 63.3) * mm});
            skLineSegment(sketch, "E11764", {"start": v(12.84, 63.3) * mm, "end": v(12.9, 63.19) * mm});
            skLineSegment(sketch, "E11765", {"start": v(12.9, 63.19) * mm, "end": v(12.96, 63.07) * mm});
            skLineSegment(sketch, "E11766", {"start": v(12.96, 63.07) * mm, "end": v(13.04, 62.95) * mm});
            skLineSegment(sketch, "E11767", {"start": v(13.04, 62.95) * mm, "end": v(13.22, 62.72) * mm});
            skLineSegment(sketch, "E11768", {"start": v(13.22, 62.72) * mm, "end": v(13.42, 62.5) * mm});
            skLineSegment(sketch, "E11769", {"start": v(13.42, 62.5) * mm, "end": v(13.63, 62.28) * mm});
            skLineSegment(sketch, "E11770", {"start": v(13.63, 62.28) * mm, "end": v(13.82, 62.06) * mm});
            skLineSegment(sketch, "E11771", {"start": v(13.82, 62.06) * mm, "end": v(13.97, 61.86) * mm});
            skLineSegment(sketch, "E11772", {"start": v(13.97, 61.86) * mm, "end": v(14.16, 61.57) * mm});
            skLineSegment(sketch, "E11773", {"start": v(14.16, 61.57) * mm, "end": v(14.37, 61.28) * mm});
            skLineSegment(sketch, "E11774", {"start": v(14.37, 61.28) * mm, "end": v(14.6, 60.99) * mm});
            skLineSegment(sketch, "E11775", {"start": v(14.6, 60.99) * mm, "end": v(14.84, 60.68) * mm});
            skLineSegment(sketch, "E11776", {"start": v(14.84, 60.68) * mm, "end": v(15.36, 60.05) * mm});
            skLineSegment(sketch, "E11777", {"start": v(15.36, 60.05) * mm, "end": v(15.94, 59.4) * mm});
            skLineSegment(sketch, "E11778", {"start": v(15.94, 59.4) * mm, "end": v(16.58, 58.73) * mm});
            skLineSegment(sketch, "E11779", {"start": v(16.58, 58.73) * mm, "end": v(17.26, 58.05) * mm});
            skLineSegment(sketch, "E11780", {"start": v(17.26, 58.05) * mm, "end": v(17.99, 57.35) * mm});
            skLineSegment(sketch, "E11781", {"start": v(17.99, 57.35) * mm, "end": v(18.75, 56.65) * mm});
            skLineSegment(sketch, "E11782", {"start": v(18.75, 56.65) * mm, "end": v(18.83, 56.57) * mm});
            skLineSegment(sketch, "E11783", {"start": v(18.83, 56.57) * mm, "end": v(18.96, 56.43) * mm});
            skLineSegment(sketch, "E11784", {"start": v(18.96, 56.43) * mm, "end": v(19.3, 56) * mm});
            skLineSegment(sketch, "E11785", {"start": v(19.3, 56) * mm, "end": v(19.75, 55.43) * mm});
            skLineSegment(sketch, "E11786", {"start": v(19.75, 55.43) * mm, "end": v(20.25, 54.77) * mm});
            skLineSegment(sketch, "E11787", {"start": v(20.25, 54.77) * mm, "end": v(20.53, 54.37) * mm});
            skLineSegment(sketch, "E11788", {"start": v(20.53, 54.37) * mm, "end": v(20.82, 53.92) * mm});
            skLineSegment(sketch, "E11789", {"start": v(20.82, 53.92) * mm, "end": v(20.98, 53.7) * mm});
            skLineSegment(sketch, "E11790", {"start": v(20.98, 53.7) * mm, "end": v(21.13, 53.5) * mm});
            skLineSegment(sketch, "E11791", {"start": v(21.13, 53.5) * mm, "end": v(21.3, 53.3) * mm});
            skLineSegment(sketch, "E11792", {"start": v(21.3, 53.3) * mm, "end": v(21.46, 53.13) * mm});
            skLineSegment(sketch, "E11793", {"start": v(21.46, 53.13) * mm, "end": v(21.77, 52.87) * mm});
            skLineSegment(sketch, "E11794", {"start": v(21.77, 52.87) * mm, "end": v(22.11, 52.6) * mm});
            skLineSegment(sketch, "E11795", {"start": v(22.11, 52.6) * mm, "end": v(22.48, 52.34) * mm});
            skLineSegment(sketch, "E11796", {"start": v(22.48, 52.34) * mm, "end": v(22.87, 52.1) * mm});
            skLineSegment(sketch, "E11797", {"start": v(22.87, 52.1) * mm, "end": v(23.26, 51.86) * mm});
            skLineSegment(sketch, "E11798", {"start": v(23.26, 51.86) * mm, "end": v(23.66, 51.65) * mm});
            skLineSegment(sketch, "E11799", {"start": v(23.66, 51.65) * mm, "end": v(24.05, 51.46) * mm});
            skLineSegment(sketch, "E11800", {"start": v(24.05, 51.46) * mm, "end": v(24.42, 51.3) * mm});
            skLineSegment(sketch, "E11801", {"start": v(24.42, 51.3) * mm, "end": v(24.79, 51.18) * mm});
            skLineSegment(sketch, "E11802", {"start": v(24.79, 51.18) * mm, "end": v(25.18, 51.08) * mm});
            skLineSegment(sketch, "E11803", {"start": v(25.18, 51.08) * mm, "end": v(25.59, 51) * mm});
            skLineSegment(sketch, "E11804", {"start": v(25.59, 51) * mm, "end": v(26.01, 50.92) * mm});
            skLineSegment(sketch, "E11805", {"start": v(26.01, 50.92) * mm, "end": v(26.87, 50.8) * mm});
            skLineSegment(sketch, "E11806", {"start": v(26.87, 50.8) * mm, "end": v(27.7, 50.68) * mm});
            skLineSegment(sketch, "E11807", {"start": v(27.7, 50.68) * mm, "end": v(27.78, 50.68) * mm});
            skLineSegment(sketch, "E11808", {"start": v(27.78, 50.68) * mm, "end": v(27.87, 50.67) * mm});
            skLineSegment(sketch, "E11809", {"start": v(27.87, 50.67) * mm, "end": v(27.96, 50.66) * mm});
            skLineSegment(sketch, "E11810", {"start": v(27.96, 50.66) * mm, "end": v(28, 50.65) * mm});
            skLineSegment(sketch, "E11811", {"start": v(28, 50.65) * mm, "end": v(28.03, 50.63) * mm});
            skLineSegment(sketch, "E11812", {"start": v(28.03, 50.63) * mm, "end": v(28.08, 50.58) * mm});
            skLineSegment(sketch, "E11813", {"start": v(28.08, 50.58) * mm, "end": v(28.13, 50.52) * mm});
            skLineSegment(sketch, "E11814", {"start": v(28.13, 50.52) * mm, "end": v(28.2, 50.38) * mm});
            skLineSegment(sketch, "E11815", {"start": v(28.2, 50.38) * mm, "end": v(28.27, 50.23) * mm});
            skLineSegment(sketch, "E11816", {"start": v(28.27, 50.23) * mm, "end": v(28.33, 50.1) * mm});
            skLineSegment(sketch, "E11817", {"start": v(28.33, 50.1) * mm, "end": v(28.42, 49.96) * mm});
            skLineSegment(sketch, "E11818", {"start": v(28.42, 49.96) * mm, "end": v(28.54, 49.78) * mm});
            skLineSegment(sketch, "E11819", {"start": v(28.54, 49.78) * mm, "end": v(28.9, 49.32) * mm});
            skLineSegment(sketch, "E11820", {"start": v(28.9, 49.32) * mm, "end": v(29.34, 48.79) * mm});
            skLineSegment(sketch, "E11821", {"start": v(29.34, 48.79) * mm, "end": v(29.83, 48.23) * mm});
            skLineSegment(sketch, "E11822", {"start": v(29.83, 48.23) * mm, "end": v(30.1, 47.9) * mm});
            skLineSegment(sketch, "E11823", {"start": v(30.1, 47.9) * mm, "end": v(30.4, 47.54) * mm});
            skLineSegment(sketch, "E11824", {"start": v(30.4, 47.54) * mm, "end": v(30.55, 47.36) * mm});
            skLineSegment(sketch, "E11825", {"start": v(30.55, 47.36) * mm, "end": v(30.7, 47.19) * mm});
            skLineSegment(sketch, "E11826", {"start": v(30.7, 47.19) * mm, "end": v(30.86, 47.03) * mm});
            skLineSegment(sketch, "E11827", {"start": v(30.86, 47.03) * mm, "end": v(31.02, 46.9) * mm});
            skLineSegment(sketch, "E11828", {"start": v(31.02, 46.9) * mm, "end": v(31.37, 46.66) * mm});
            skLineSegment(sketch, "E11829", {"start": v(31.37, 46.66) * mm, "end": v(31.76, 46.42) * mm});
            skLineSegment(sketch, "E11830", {"start": v(31.76, 46.42) * mm, "end": v(32.17, 46.2) * mm});
            skLineSegment(sketch, "E11831", {"start": v(32.17, 46.2) * mm, "end": v(32.6, 45.98) * mm});
            skLineSegment(sketch, "E11832", {"start": v(32.6, 45.98) * mm, "end": v(33.04, 45.78) * mm});
            skLineSegment(sketch, "E11833", {"start": v(33.04, 45.78) * mm, "end": v(33.48, 45.61) * mm});
            skLineSegment(sketch, "E11834", {"start": v(33.48, 45.61) * mm, "end": v(33.9, 45.47) * mm});
            skLineSegment(sketch, "E11835", {"start": v(33.9, 45.47) * mm, "end": v(34.32, 45.36) * mm});
            skLineSegment(sketch, "E11836", {"start": v(34.32, 45.36) * mm, "end": v(34.52, 45.33) * mm});
            skLineSegment(sketch, "E11837", {"start": v(34.52, 45.33) * mm, "end": v(34.73, 45.3) * mm});
            skLineSegment(sketch, "E11838", {"start": v(34.73, 45.3) * mm, "end": v(34.95, 45.3) * mm});
            skLineSegment(sketch, "E11839", {"start": v(34.95, 45.3) * mm, "end": v(35.18, 45.3) * mm});
            skLineSegment(sketch, "E11840", {"start": v(35.18, 45.3) * mm, "end": v(35.64, 45.33) * mm});
            skLineSegment(sketch, "E11841", {"start": v(35.64, 45.33) * mm, "end": v(36.08, 45.35) * mm});
            skLineSegment(sketch, "E11842", {"start": v(36.08, 45.35) * mm, "end": v(36.22, 45.37) * mm});
            skLineSegment(sketch, "E11843", {"start": v(36.22, 45.37) * mm, "end": v(36.28, 45.37) * mm});
            skLineSegment(sketch, "E11844", {"start": v(36.28, 45.37) * mm, "end": v(36.34, 45.36) * mm});
            skLineSegment(sketch, "E11845", {"start": v(36.34, 45.36) * mm, "end": v(36.39, 45.32) * mm});
            skLineSegment(sketch, "E11846", {"start": v(36.39, 45.32) * mm, "end": v(36.42, 45.27) * mm});
            skLineSegment(sketch, "E11847", {"start": v(36.42, 45.27) * mm, "end": v(36.48, 45.16) * mm});
            skLineSegment(sketch, "E11848", {"start": v(36.48, 45.16) * mm, "end": v(36.53, 45.03) * mm});
            skLineSegment(sketch, "E11849", {"start": v(36.53, 45.03) * mm, "end": v(36.59, 44.92) * mm});
            skLineSegment(sketch, "E11850", {"start": v(36.59, 44.92) * mm, "end": v(36.88, 44.44) * mm});
            skLineSegment(sketch, "E11851", {"start": v(36.88, 44.44) * mm, "end": v(37.2, 43.94) * mm});
            skLineSegment(sketch, "E11852", {"start": v(37.2, 43.94) * mm, "end": v(37.52, 43.44) * mm});
            skLineSegment(sketch, "E11853", {"start": v(37.52, 43.44) * mm, "end": v(37.8, 42.96) * mm});
            skLineSegment(sketch, "E11854", {"start": v(37.8, 42.96) * mm, "end": v(37.95, 42.7) * mm});
            skLineSegment(sketch, "E11855", {"start": v(37.95, 42.7) * mm, "end": v(38.1, 42.41) * mm});
            skLineSegment(sketch, "E11856", {"start": v(38.1, 42.41) * mm, "end": v(38.38, 41.82) * mm});
            skLineSegment(sketch, "E11857", {"start": v(38.38, 41.82) * mm, "end": v(38.67, 41.2) * mm});
            skLineSegment(sketch, "E11858", {"start": v(38.67, 41.2) * mm, "end": v(38.96, 40.56) * mm});
            skLineSegment(sketch, "E11859", {"start": v(38.96, 40.56) * mm, "end": v(39.26, 39.93) * mm});
            skLineSegment(sketch, "E11860", {"start": v(39.26, 39.93) * mm, "end": v(39.41, 39.63) * mm});
            skLineSegment(sketch, "E11861", {"start": v(39.41, 39.63) * mm, "end": v(39.57, 39.33) * mm});
            skLineSegment(sketch, "E11862", {"start": v(39.57, 39.33) * mm, "end": v(39.74, 39.04) * mm});
            skLineSegment(sketch, "E11863", {"start": v(39.74, 39.04) * mm, "end": v(39.9, 38.77) * mm});
            skLineSegment(sketch, "E11864", {"start": v(39.9, 38.77) * mm, "end": v(40.08, 38.5) * mm});
            skLineSegment(sketch, "E11865", {"start": v(40.08, 38.5) * mm, "end": v(40.26, 38.26) * mm});
            skLineSegment(sketch, "E11866", {"start": v(40.26, 38.26) * mm, "end": v(41.01, 37.33) * mm});
            skLineSegment(sketch, "E11867", {"start": v(41.01, 37.33) * mm, "end": v(41.4, 36.86) * mm});
            skLineSegment(sketch, "E11868", {"start": v(41.4, 36.86) * mm, "end": v(41.79, 36.4) * mm});
            skLineSegment(sketch, "E11869", {"start": v(41.79, 36.4) * mm, "end": v(42.18, 35.97) * mm});
            skLineSegment(sketch, "E11870", {"start": v(42.18, 35.97) * mm, "end": v(42.58, 35.55) * mm});
            skLineSegment(sketch, "E11871", {"start": v(42.58, 35.55) * mm, "end": v(42.98, 35.15) * mm});
            skLineSegment(sketch, "E11872", {"start": v(42.98, 35.15) * mm, "end": v(43.39, 34.77) * mm});
            skLineSegment(sketch, "E11873", {"start": v(43.39, 34.77) * mm, "end": v(43.83, 34.4) * mm});
            skLineSegment(sketch, "E11874", {"start": v(43.83, 34.4) * mm, "end": v(44.34, 33.99) * mm});
            skLineSegment(sketch, "E11875", {"start": v(44.34, 33.99) * mm, "end": v(44.86, 33.6) * mm});
            skLineSegment(sketch, "E11876", {"start": v(44.86, 33.6) * mm, "end": v(45.1, 33.42) * mm});
            skLineSegment(sketch, "E11877", {"start": v(45.1, 33.42) * mm, "end": v(45.34, 33.27) * mm});
            skLineSegment(sketch, "E11878", {"start": v(45.34, 33.27) * mm, "end": v(45.73, 33) * mm});
            skLineSegment(sketch, "E11879", {"start": v(45.73, 33) * mm, "end": v(46.08, 32.74) * mm});
            skLineSegment(sketch, "E11880", {"start": v(46.08, 32.74) * mm, "end": v(46.38, 32.48) * mm});
            skLineSegment(sketch, "E11881", {"start": v(46.38, 32.48) * mm, "end": v(46.64, 32.25) * mm});
            skLineSegment(sketch, "E11882", {"start": v(46.64, 32.25) * mm, "end": v(47.02, 31.87) * mm});
            skLineSegment(sketch, "E11883", {"start": v(47.02, 31.87) * mm, "end": v(47.2, 31.68) * mm});
            skLineSegment(sketch, "E11884", {"start": v(47.2, 31.68) * mm, "end": v(47.25, 31.62) * mm});
            skLineSegment(sketch, "E11885", {"start": v(47.25, 31.62) * mm, "end": v(47.34, 31.49) * mm});
            skLineSegment(sketch, "E11886", {"start": v(47.34, 31.49) * mm, "end": v(47.58, 31.09) * mm});
            skLineSegment(sketch, "E11887", {"start": v(47.58, 31.09) * mm, "end": v(47.86, 30.56) * mm});
            skLineSegment(sketch, "E11888", {"start": v(47.86, 30.56) * mm, "end": v(48, 30.28) * mm});
            skLineSegment(sketch, "E11889", {"start": v(48, 30.28) * mm, "end": v(48.14, 30) * mm});
            skLineSegment(sketch, "E11890", {"start": v(48.14, 30) * mm, "end": v(48.3, 29.67) * mm});
            skLineSegment(sketch, "E11891", {"start": v(48.3, 29.67) * mm, "end": v(48.49, 29.32) * mm});
            skLineSegment(sketch, "E11892", {"start": v(48.49, 29.32) * mm, "end": v(48.66, 28.96) * mm});
            skLineSegment(sketch, "E11893", {"start": v(48.66, 28.96) * mm, "end": v(48.73, 28.78) * mm});
            skLineSegment(sketch, "E11894", {"start": v(48.73, 28.78) * mm, "end": v(48.79, 28.61) * mm});
            skLineSegment(sketch, "E11895", {"start": v(48.79, 28.61) * mm, "end": v(48.84, 28.43) * mm});
            skLineSegment(sketch, "E11896", {"start": v(48.84, 28.43) * mm, "end": v(48.88, 28.24) * mm});
            skLineSegment(sketch, "E11897", {"start": v(48.88, 28.24) * mm, "end": v(48.94, 27.83) * mm});
            skLineSegment(sketch, "E11898", {"start": v(48.94, 27.83) * mm, "end": v(49, 27.41) * mm});
            skLineSegment(sketch, "E11899", {"start": v(49, 27.41) * mm, "end": v(49.05, 27.03) * mm});
            skLineSegment(sketch, "E11900", {"start": v(49.05, 27.03) * mm, "end": v(49.3, 25.73) * mm});
            skLineSegment(sketch, "E11901", {"start": v(-14.43, 63.16) * mm, "end": v(-14.28, 63.38) * mm});
            skLineSegment(sketch, "E11902", {"start": v(-14.28, 63.38) * mm, "end": v(-14.2, 63.5) * mm});
            skLineSegment(sketch, "E11903", {"start": v(-14.2, 63.5) * mm, "end": v(-14.14, 63.64) * mm});
            skLineSegment(sketch, "E11904", {"start": v(-14.14, 63.64) * mm, "end": v(-14.08, 63.77) * mm});
            skLineSegment(sketch, "E11905", {"start": v(-14.08, 63.77) * mm, "end": v(-14.04, 63.9) * mm});
            skLineSegment(sketch, "E11906", {"start": v(-14.04, 63.9) * mm, "end": v(-14.03, 64.03) * mm});
            skLineSegment(sketch, "E11907", {"start": v(-14.03, 64.03) * mm, "end": v(-14.03, 64.09) * mm});
            skLineSegment(sketch, "E11908", {"start": v(-14.03, 64.09) * mm, "end": v(-14.05, 64.14) * mm});
            skLineSegment(sketch, "E11909", {"start": v(-14.05, 64.14) * mm, "end": v(-14.07, 64.18) * mm});
            skLineSegment(sketch, "E11910", {"start": v(-14.07, 64.18) * mm, "end": v(-14.1, 64.21) * mm});
            skLineSegment(sketch, "E11911", {"start": v(-14.1, 64.21) * mm, "end": v(-14.19, 64.26) * mm});
            skLineSegment(sketch, "E11912", {"start": v(-14.19, 64.26) * mm, "end": v(-14.29, 64.3) * mm});
            skLineSegment(sketch, "E11913", {"start": v(-14.29, 64.3) * mm, "end": v(-14.37, 64.35) * mm});
            skLineSegment(sketch, "E11914", {"start": v(-14.37, 64.35) * mm, "end": v(-14.59, 64.45) * mm});
            skLineSegment(sketch, "E11915", {"start": v(-14.59, 64.45) * mm, "end": v(-14.92, 64.58) * mm});
            skLineSegment(sketch, "E11916", {"start": v(-14.92, 64.58) * mm, "end": v(-15.32, 64.73) * mm});
            skLineSegment(sketch, "E11917", {"start": v(-15.32, 64.73) * mm, "end": v(-15.76, 64.87) * mm});
            skLineSegment(sketch, "E11918", {"start": v(-15.76, 64.87) * mm, "end": v(-16.29, 65.05) * mm});
            skLineSegment(sketch, "E11919", {"start": v(-16.29, 65.05) * mm, "end": v(-16.56, 65.14) * mm});
            skLineSegment(sketch, "E11920", {"start": v(-16.56, 65.14) * mm, "end": v(-16.82, 65.2) * mm});
            skLineSegment(sketch, "E11921", {"start": v(-16.82, 65.2) * mm, "end": v(-17.5, 65.3) * mm});
            skLineSegment(sketch, "E11922", {"start": v(-17.5, 65.3) * mm, "end": v(-18.2, 65.4) * mm});
            skLineSegment(sketch, "E11923", {"start": v(-18.2, 65.4) * mm, "end": v(-18.92, 65.48) * mm});
            skLineSegment(sketch, "E11924", {"start": v(-18.92, 65.48) * mm, "end": v(-19.66, 65.56) * mm});
            skLineSegment(sketch, "E11925", {"start": v(-19.66, 65.56) * mm, "end": v(-20.42, 65.62) * mm});
            skLineSegment(sketch, "E11926", {"start": v(-20.42, 65.62) * mm, "end": v(-21.19, 65.67) * mm});
            skLineSegment(sketch, "E11927", {"start": v(-21.19, 65.67) * mm, "end": v(-21.96, 65.72) * mm});
            skLineSegment(sketch, "E11928", {"start": v(-21.96, 65.72) * mm, "end": v(-22.75, 65.75) * mm});
            skLineSegment(sketch, "E11929", {"start": v(-22.75, 65.75) * mm, "end": v(-23.53, 65.77) * mm});
            skLineSegment(sketch, "E11930", {"start": v(-23.53, 65.77) * mm, "end": v(-24.3, 65.8) * mm});
            skLineSegment(sketch, "E11931", {"start": v(-24.3, 65.8) * mm, "end": v(-25.08, 65.8) * mm});
            skLineSegment(sketch, "E11932", {"start": v(-25.08, 65.8) * mm, "end": v(-25.84, 65.8) * mm});
            skLineSegment(sketch, "E11933", {"start": v(-25.84, 65.8) * mm, "end": v(-27.31, 65.78) * mm});
            skLineSegment(sketch, "E11934", {"start": v(-27.31, 65.78) * mm, "end": v(-28.7, 65.73) * mm});
            skLineSegment(sketch, "E11935", {"start": v(-28.7, 65.73) * mm, "end": v(-28.96, 65.71) * mm});
            skLineSegment(sketch, "E11936", {"start": v(-28.96, 65.71) * mm, "end": v(-29.22, 65.68) * mm});
            skLineSegment(sketch, "E11937", {"start": v(-29.22, 65.68) * mm, "end": v(-29.78, 65.6) * mm});
            skLineSegment(sketch, "E11938", {"start": v(-29.78, 65.6) * mm, "end": v(-30.33, 65.51) * mm});
            skLineSegment(sketch, "E11939", {"start": v(-30.33, 65.51) * mm, "end": v(-30.85, 65.44) * mm});
            skLineSegment(sketch, "E11940", {"start": v(-30.85, 65.44) * mm, "end": v(-31.31, 65.37) * mm});
            skLineSegment(sketch, "E11941", {"start": v(-31.31, 65.37) * mm, "end": v(-31.8, 65.28) * mm});
            skLineSegment(sketch, "E11942", {"start": v(-31.8, 65.28) * mm, "end": v(-32.31, 65.18) * mm});
            skLineSegment(sketch, "E11943", {"start": v(-32.31, 65.18) * mm, "end": v(-32.82, 65.08) * mm});
            skLineSegment(sketch, "E11944", {"start": v(-32.82, 65.08) * mm, "end": v(-33.31, 64.97) * mm});
            skLineSegment(sketch, "E11945", {"start": v(-33.31, 64.97) * mm, "end": v(-33.78, 64.85) * mm});
            skLineSegment(sketch, "E11946", {"start": v(-33.78, 64.85) * mm, "end": v(-34.2, 64.74) * mm});
            skLineSegment(sketch, "E11947", {"start": v(-34.2, 64.74) * mm, "end": v(-34.55, 64.63) * mm});
            skLineSegment(sketch, "E11948", {"start": v(-34.55, 64.63) * mm, "end": v(-34.93, 64.52) * mm});
            skLineSegment(sketch, "E11949", {"start": v(-34.93, 64.52) * mm, "end": v(-35.35, 64.4) * mm});
            skLineSegment(sketch, "E11950", {"start": v(-35.35, 64.4) * mm, "end": v(-35.55, 64.35) * mm});
            skLineSegment(sketch, "E11951", {"start": v(-35.55, 64.35) * mm, "end": v(-35.75, 64.28) * mm});
            skLineSegment(sketch, "E11952", {"start": v(-35.75, 64.28) * mm, "end": v(-35.94, 64.2) * mm});
            skLineSegment(sketch, "E11953", {"start": v(-35.94, 64.2) * mm, "end": v(-36.1, 64.12) * mm});
            skLineSegment(sketch, "E11954", {"start": v(-36.1, 64.12) * mm, "end": v(-36.32, 63.98) * mm});
            skLineSegment(sketch, "E11955", {"start": v(-36.32, 63.98) * mm, "end": v(-36.53, 63.81) * mm});
            skLineSegment(sketch, "E11956", {"start": v(-36.53, 63.81) * mm, "end": v(-36.74, 63.63) * mm});
            skLineSegment(sketch, "E11957", {"start": v(-36.74, 63.63) * mm, "end": v(-36.95, 63.43) * mm});
            skLineSegment(sketch, "E11958", {"start": v(-36.95, 63.43) * mm, "end": v(-37.35, 63.02) * mm});
            skLineSegment(sketch, "E11959", {"start": v(-37.35, 63.02) * mm, "end": v(-37.55, 62.83) * mm});
            skLineSegment(sketch, "E11960", {"start": v(-37.55, 62.83) * mm, "end": v(-37.73, 62.66) * mm});
            skLineSegment(sketch, "E11961", {"start": v(-37.73, 62.66) * mm, "end": v(-38.38, 62.09) * mm});
            skLineSegment(sketch, "E11962", {"start": v(-38.38, 62.09) * mm, "end": v(-38.93, 61.62) * mm});
            skLineSegment(sketch, "E11963", {"start": v(-38.93, 61.62) * mm, "end": v(-39.33, 61.31) * mm});
            skLineSegment(sketch, "E11964", {"start": v(-39.33, 61.31) * mm, "end": v(-39.45, 61.23) * mm});
            skLineSegment(sketch, "E11965", {"start": v(-39.45, 61.23) * mm, "end": v(-39.52, 61.2) * mm});
            skLineSegment(sketch, "E11966", {"start": v(-39.52, 61.2) * mm, "end": v(-39.56, 61.22) * mm});
            skLineSegment(sketch, "E11967", {"start": v(-39.56, 61.22) * mm, "end": v(-39.61, 61.27) * mm});
            skLineSegment(sketch, "E11968", {"start": v(-39.61, 61.27) * mm, "end": v(-39.68, 61.36) * mm});
            skLineSegment(sketch, "E11969", {"start": v(-39.68, 61.36) * mm, "end": v(-39.75, 61.48) * mm});
            skLineSegment(sketch, "E11970", {"start": v(-39.75, 61.48) * mm, "end": v(-39.91, 61.8) * mm});
            skLineSegment(sketch, "E11971", {"start": v(-39.91, 61.8) * mm, "end": v(-40.08, 62.17) * mm});
            skLineSegment(sketch, "E11972", {"start": v(-40.08, 62.17) * mm, "end": v(-40.17, 62.38) * mm});
            skLineSegment(sketch, "E11973", {"start": v(-40.17, 62.38) * mm, "end": v(-40.27, 62.58) * mm});
            skLineSegment(sketch, "E11974", {"start": v(-40.27, 62.58) * mm, "end": v(-40.38, 62.78) * mm});
            skLineSegment(sketch, "E11975", {"start": v(-40.38, 62.78) * mm, "end": v(-40.5, 62.97) * mm});
            skLineSegment(sketch, "E11976", {"start": v(-40.5, 62.97) * mm, "end": v(-40.6, 63.14) * mm});
            skLineSegment(sketch, "E11977", {"start": v(-40.6, 63.14) * mm, "end": v(-40.7, 63.29) * mm});
            skLineSegment(sketch, "E11978", {"start": v(-40.7, 63.29) * mm, "end": v(-40.8, 63.4) * mm});
            skLineSegment(sketch, "E11979", {"start": v(-40.8, 63.4) * mm, "end": v(-40.9, 63.5) * mm});
            skLineSegment(sketch, "E11980", {"start": v(-40.9, 63.5) * mm, "end": v(-41, 63.59) * mm});
            skLineSegment(sketch, "E11981", {"start": v(-41, 63.59) * mm, "end": v(-41.1, 63.7) * mm});
            skLineSegment(sketch, "E11982", {"start": v(-41.1, 63.7) * mm, "end": v(-41.14, 63.75) * mm});
            skLineSegment(sketch, "E11983", {"start": v(-41.14, 63.75) * mm, "end": v(-41.2, 63.8) * mm});
            skLineSegment(sketch, "E11984", {"start": v(-41.2, 63.8) * mm, "end": v(-41.25, 63.82) * mm});
            skLineSegment(sketch, "E11985", {"start": v(-41.25, 63.82) * mm, "end": v(-41.31, 63.84) * mm});
            skLineSegment(sketch, "E11986", {"start": v(-41.31, 63.84) * mm, "end": v(-41.47, 63.84) * mm});
            skLineSegment(sketch, "E11987", {"start": v(-41.47, 63.84) * mm, "end": v(-41.63, 63.83) * mm});
            skLineSegment(sketch, "E11988", {"start": v(-41.63, 63.83) * mm, "end": v(-41.8, 63.8) * mm});
            skLineSegment(sketch, "E11989", {"start": v(-41.8, 63.8) * mm, "end": v(-41.97, 63.75) * mm});
            skLineSegment(sketch, "E11990", {"start": v(-41.97, 63.75) * mm, "end": v(-42.15, 63.69) * mm});
            skLineSegment(sketch, "E11991", {"start": v(-42.15, 63.69) * mm, "end": v(-42.32, 63.62) * mm});
            skLineSegment(sketch, "E11992", {"start": v(-42.32, 63.62) * mm, "end": v(-42.68, 63.45) * mm});
            skLineSegment(sketch, "E11993", {"start": v(-42.68, 63.45) * mm, "end": v(-43.03, 63.25) * mm});
            skLineSegment(sketch, "E11994", {"start": v(-43.03, 63.25) * mm, "end": v(-43.36, 63.05) * mm});
            skLineSegment(sketch, "E11995", {"start": v(-43.36, 63.05) * mm, "end": v(-43.68, 62.86) * mm});
            skLineSegment(sketch, "E11996", {"start": v(-43.68, 62.86) * mm, "end": v(-43.97, 62.7) * mm});
            skLineSegment(sketch, "E11997", {"start": v(-43.97, 62.7) * mm, "end": v(-44.48, 62.4) * mm});
            skLineSegment(sketch, "E11998", {"start": v(-44.48, 62.4) * mm, "end": v(-45.02, 62.07) * mm});
            skLineSegment(sketch, "E11999", {"start": v(-45.02, 62.07) * mm, "end": v(-45.55, 61.73) * mm});
            skLineSegment(sketch, "E12000", {"start": v(-45.55, 61.73) * mm, "end": v(-46.09, 61.37) * mm});
            skLineSegment(sketch, "E12001", {"start": v(-46.09, 61.37) * mm, "end": v(-47.08, 60.67) * mm});
            skLineSegment(sketch, "E12002", {"start": v(-47.08, 60.67) * mm, "end": v(-47.91, 60.06) * mm});
            skLineSegment(sketch, "E12003", {"start": v(-47.91, 60.06) * mm, "end": v(-48, 59.97) * mm});
            skLineSegment(sketch, "E12004", {"start": v(-48, 59.97) * mm, "end": v(-48.1, 59.88) * mm});
            skLineSegment(sketch, "E12005", {"start": v(-48.1, 59.88) * mm, "end": v(-48.17, 59.77) * mm});
            skLineSegment(sketch, "E12006", {"start": v(-48.17, 59.77) * mm, "end": v(-48.24, 59.65) * mm});
            skLineSegment(sketch, "E12007", {"start": v(-48.24, 59.65) * mm, "end": v(-48.38, 59.4) * mm});
            skLineSegment(sketch, "E12008", {"start": v(-48.38, 59.4) * mm, "end": v(-48.52, 59.14) * mm});
            skLineSegment(sketch, "E12009", {"start": v(-48.52, 59.14) * mm, "end": v(-48.66, 58.9) * mm});
            skLineSegment(sketch, "E12010", {"start": v(-48.66, 58.9) * mm, "end": v(-48.73, 58.79) * mm});
            skLineSegment(sketch, "E12011", {"start": v(-48.73, 58.79) * mm, "end": v(-48.81, 58.69) * mm});
            skLineSegment(sketch, "E12012", {"start": v(-48.81, 58.69) * mm, "end": v(-48.9, 58.6) * mm});
            skLineSegment(sketch, "E12013", {"start": v(-48.9, 58.6) * mm, "end": v(-49, 58.54) * mm});
            skLineSegment(sketch, "E12014", {"start": v(-49, 58.54) * mm, "end": v(-49.1, 58.5) * mm});
            skLineSegment(sketch, "E12015", {"start": v(-49.1, 58.5) * mm, "end": v(-49.22, 58.47) * mm});
            skLineSegment(sketch, "E12016", {"start": v(-49.22, 58.47) * mm, "end": v(-49.32, 58.47) * mm});
            skLineSegment(sketch, "E12017", {"start": v(-49.32, 58.47) * mm, "end": v(-49.44, 58.49) * mm});
            skLineSegment(sketch, "E12018", {"start": v(-49.44, 58.49) * mm, "end": v(-49.56, 58.52) * mm});
            skLineSegment(sketch, "E12019", {"start": v(-49.56, 58.52) * mm, "end": v(-49.69, 58.58) * mm});
            skLineSegment(sketch, "E12020", {"start": v(-49.69, 58.58) * mm, "end": v(-49.96, 58.71) * mm});
            skLineSegment(sketch, "E12021", {"start": v(-49.96, 58.71) * mm, "end": v(-50.24, 58.87) * mm});
            skLineSegment(sketch, "E12022", {"start": v(-50.24, 58.87) * mm, "end": v(-50.52, 59.03) * mm});
            skLineSegment(sketch, "E12023", {"start": v(-50.52, 59.03) * mm, "end": v(-50.8, 59.18) * mm});
            skLineSegment(sketch, "E12024", {"start": v(-50.8, 59.18) * mm, "end": v(-50.92, 59.23) * mm});
            skLineSegment(sketch, "E12025", {"start": v(-50.92, 59.23) * mm, "end": v(-51.04, 59.27) * mm});
            skLineSegment(sketch, "E12026", {"start": v(-51.04, 59.27) * mm, "end": v(-51.16, 59.3) * mm});
            skLineSegment(sketch, "E12027", {"start": v(-51.16, 59.3) * mm, "end": v(-51.27, 59.3) * mm});
            skLineSegment(sketch, "E12028", {"start": v(-51.27, 59.3) * mm, "end": v(-51.46, 59.28) * mm});
            skLineSegment(sketch, "E12029", {"start": v(-51.46, 59.28) * mm, "end": v(-51.65, 59.24) * mm});
            skLineSegment(sketch, "E12030", {"start": v(-51.65, 59.24) * mm, "end": v(-51.85, 59.18) * mm});
            skLineSegment(sketch, "E12031", {"start": v(-51.85, 59.18) * mm, "end": v(-52.05, 59.1) * mm});
            skLineSegment(sketch, "E12032", {"start": v(-52.05, 59.1) * mm, "end": v(-52.24, 59.01) * mm});
            skLineSegment(sketch, "E12033", {"start": v(-52.24, 59.01) * mm, "end": v(-52.44, 58.9) * mm});
            skLineSegment(sketch, "E12034", {"start": v(-52.44, 58.9) * mm, "end": v(-52.63, 58.79) * mm});
            skLineSegment(sketch, "E12035", {"start": v(-52.63, 58.79) * mm, "end": v(-52.83, 58.66) * mm});
            skLineSegment(sketch, "E12036", {"start": v(-52.83, 58.66) * mm, "end": v(-53.2, 58.4) * mm});
            skLineSegment(sketch, "E12037", {"start": v(-53.2, 58.4) * mm, "end": v(-53.56, 58.11) * mm});
            skLineSegment(sketch, "E12038", {"start": v(-53.56, 58.11) * mm, "end": v(-54.21, 57.58) * mm});
            skLineSegment(sketch, "E12039", {"start": v(-54.21, 57.58) * mm, "end": v(-54.4, 57.42) * mm});
            skLineSegment(sketch, "E12040", {"start": v(-54.4, 57.42) * mm, "end": v(-54.57, 57.23) * mm});
            skLineSegment(sketch, "E12041", {"start": v(-54.57, 57.23) * mm, "end": v(-54.92, 56.83) * mm});
            skLineSegment(sketch, "E12042", {"start": v(-54.92, 56.83) * mm, "end": v(-55.26, 56.41) * mm});
            skLineSegment(sketch, "E12043", {"start": v(-55.26, 56.41) * mm, "end": v(-55.57, 56.03) * mm});
            skLineSegment(sketch, "E12044", {"start": v(-55.57, 56.03) * mm, "end": v(-55.88, 55.67) * mm});
            skLineSegment(sketch, "E12045", {"start": v(-55.88, 55.67) * mm, "end": v(-56.21, 55.25) * mm});
            skLineSegment(sketch, "E12046", {"start": v(-56.21, 55.25) * mm, "end": v(-56.57, 54.79) * mm});
            skLineSegment(sketch, "E12047", {"start": v(-56.57, 54.79) * mm, "end": v(-56.94, 54.29) * mm});
            skLineSegment(sketch, "E12048", {"start": v(-56.94, 54.29) * mm, "end": v(-57.32, 53.77) * mm});
            skLineSegment(sketch, "E12049", {"start": v(-57.32, 53.77) * mm, "end": v(-57.68, 53.25) * mm});
            skLineSegment(sketch, "E12050", {"start": v(-57.68, 53.25) * mm, "end": v(-58.02, 52.75) * mm});
            skLineSegment(sketch, "E12051", {"start": v(-58.02, 52.75) * mm, "end": v(-58.33, 52.27) * mm});
            skLineSegment(sketch, "E12052", {"start": v(-58.33, 52.27) * mm, "end": v(-58.48, 52) * mm});
            skLineSegment(sketch, "E12053", {"start": v(-58.48, 52) * mm, "end": v(-58.63, 51.7) * mm});
            skLineSegment(sketch, "E12054", {"start": v(-58.63, 51.7) * mm, "end": v(-58.77, 51.38) * mm});
            skLineSegment(sketch, "E12055", {"start": v(-58.77, 51.38) * mm, "end": v(-58.92, 51.06) * mm});
            skLineSegment(sketch, "E12056", {"start": v(-58.92, 51.06) * mm, "end": v(-59.09, 50.75) * mm});
            skLineSegment(sketch, "E12057", {"start": v(-59.09, 50.75) * mm, "end": v(-59.18, 50.6) * mm});
            skLineSegment(sketch, "E12058", {"start": v(-59.18, 50.6) * mm, "end": v(-59.27, 50.47) * mm});
            skLineSegment(sketch, "E12059", {"start": v(-59.27, 50.47) * mm, "end": v(-59.37, 50.34) * mm});
            skLineSegment(sketch, "E12060", {"start": v(-59.37, 50.34) * mm, "end": v(-59.48, 50.23) * mm});
            skLineSegment(sketch, "E12061", {"start": v(-59.48, 50.23) * mm, "end": v(-59.6, 50.14) * mm});
            skLineSegment(sketch, "E12062", {"start": v(-59.6, 50.14) * mm, "end": v(-59.72, 50.06) * mm});
            skLineSegment(sketch, "E12063", {"start": v(-59.72, 50.06) * mm, "end": v(-59.9, 49.98) * mm});
            skLineSegment(sketch, "E12064", {"start": v(-59.9, 49.98) * mm, "end": v(-60.09, 49.9) * mm});
            skLineSegment(sketch, "E12065", {"start": v(-60.09, 49.9) * mm, "end": v(-60.3, 49.86) * mm});
            skLineSegment(sketch, "E12066", {"start": v(-60.3, 49.86) * mm, "end": v(-60.53, 49.81) * mm});
            skLineSegment(sketch, "E12067", {"start": v(-60.53, 49.81) * mm, "end": v(-61.01, 49.76) * mm});
            skLineSegment(sketch, "E12068", {"start": v(-61.01, 49.76) * mm, "end": v(-61.53, 49.71) * mm});
            skLineSegment(sketch, "E12069", {"start": v(-61.53, 49.71) * mm, "end": v(-62.04, 49.68) * mm});
            skLineSegment(sketch, "E12070", {"start": v(-62.04, 49.68) * mm, "end": v(-62.55, 49.62) * mm});
            skLineSegment(sketch, "E12071", {"start": v(-62.55, 49.62) * mm, "end": v(-62.78, 49.58) * mm});
            skLineSegment(sketch, "E12072", {"start": v(-62.78, 49.58) * mm, "end": v(-63, 49.54) * mm});
            skLineSegment(sketch, "E12073", {"start": v(-63, 49.54) * mm, "end": v(-63.21, 49.48) * mm});
            skLineSegment(sketch, "E12074", {"start": v(-63.21, 49.48) * mm, "end": v(-63.4, 49.4) * mm});
            skLineSegment(sketch, "E12075", {"start": v(-63.4, 49.4) * mm, "end": v(-63.61, 49.3) * mm});
            skLineSegment(sketch, "E12076", {"start": v(-63.61, 49.3) * mm, "end": v(-63.82, 49.18) * mm});
            skLineSegment(sketch, "E12077", {"start": v(-63.82, 49.18) * mm, "end": v(-64.02, 49.05) * mm});
            skLineSegment(sketch, "E12078", {"start": v(-64.02, 49.05) * mm, "end": v(-64.21, 48.92) * mm});
            skLineSegment(sketch, "E12079", {"start": v(-64.21, 48.92) * mm, "end": v(-64.4, 48.77) * mm});
            skLineSegment(sketch, "E12080", {"start": v(-64.4, 48.77) * mm, "end": v(-64.58, 48.62) * mm});
            skLineSegment(sketch, "E12081", {"start": v(-64.58, 48.62) * mm, "end": v(-64.94, 48.3) * mm});
            skLineSegment(sketch, "E12082", {"start": v(-64.94, 48.3) * mm, "end": v(-65.28, 47.94) * mm});
            skLineSegment(sketch, "E12083", {"start": v(-65.28, 47.94) * mm, "end": v(-65.6, 47.58) * mm});
            skLineSegment(sketch, "E12084", {"start": v(-65.6, 47.58) * mm, "end": v(-66.2, 46.84) * mm});
            skLineSegment(sketch, "E12085", {"start": v(-66.2, 46.84) * mm, "end": v(-66.42, 46.56) * mm});
            skLineSegment(sketch, "E12086", {"start": v(-66.42, 46.56) * mm, "end": v(-66.63, 46.25) * mm});
            skLineSegment(sketch, "E12087", {"start": v(-66.63, 46.25) * mm, "end": v(-66.84, 45.92) * mm});
            skLineSegment(sketch, "E12088", {"start": v(-66.84, 45.92) * mm, "end": v(-67.04, 45.58) * mm});
            skLineSegment(sketch, "E12089", {"start": v(-67.04, 45.58) * mm, "end": v(-67.43, 44.9) * mm});
            skLineSegment(sketch, "E12090", {"start": v(-67.43, 44.9) * mm, "end": v(-67.8, 44.27) * mm});
            skLineSegment(sketch, "E12091", {"start": v(-67.8, 44.27) * mm, "end": v(-68.14, 43.71) * mm});
            skLineSegment(sketch, "E12092", {"start": v(-68.14, 43.71) * mm, "end": v(-68.48, 43.12) * mm});
            skLineSegment(sketch, "E12093", {"start": v(-68.48, 43.12) * mm, "end": v(-68.81, 42.52) * mm});
            skLineSegment(sketch, "E12094", {"start": v(-68.81, 42.52) * mm, "end": v(-69.14, 41.92) * mm});
            skLineSegment(sketch, "E12095", {"start": v(-69.14, 41.92) * mm, "end": v(-69.44, 41.34) * mm});
            skLineSegment(sketch, "E12096", {"start": v(-69.44, 41.34) * mm, "end": v(-69.71, 40.8) * mm});
            skLineSegment(sketch, "E12097", {"start": v(-69.71, 40.8) * mm, "end": v(-69.94, 40.32) * mm});
            skLineSegment(sketch, "E12098", {"start": v(-69.94, 40.32) * mm, "end": v(-70.12, 39.9) * mm});
            skLineSegment(sketch, "E12099", {"start": v(-70.12, 39.9) * mm, "end": v(-70.2, 39.7) * mm});
            skLineSegment(sketch, "E12100", {"start": v(-70.2, 39.7) * mm, "end": v(-70.26, 39.46) * mm});
            skLineSegment(sketch, "E12101", {"start": v(-70.26, 39.46) * mm, "end": v(-70.4, 38.96) * mm});
            skLineSegment(sketch, "E12102", {"start": v(-70.4, 38.96) * mm, "end": v(-70.48, 38.72) * mm});
            skLineSegment(sketch, "E12103", {"start": v(-70.48, 38.72) * mm, "end": v(-70.58, 38.49) * mm});
            skLineSegment(sketch, "E12104", {"start": v(-70.58, 38.49) * mm, "end": v(-70.64, 38.38) * mm});
            skLineSegment(sketch, "E12105", {"start": v(-70.64, 38.38) * mm, "end": v(-70.7, 38.29) * mm});
            skLineSegment(sketch, "E12106", {"start": v(-70.7, 38.29) * mm, "end": v(-70.77, 38.2) * mm});
            skLineSegment(sketch, "E12107", {"start": v(-70.77, 38.2) * mm, "end": v(-70.84, 38.12) * mm});
            skLineSegment(sketch, "E12108", {"start": v(-70.84, 38.12) * mm, "end": v(-70.97, 38.02) * mm});
            skLineSegment(sketch, "E12109", {"start": v(-70.97, 38.02) * mm, "end": v(-71.11, 37.93) * mm});
            skLineSegment(sketch, "E12110", {"start": v(-71.11, 37.93) * mm, "end": v(-71.27, 37.86) * mm});
            skLineSegment(sketch, "E12111", {"start": v(-71.27, 37.86) * mm, "end": v(-71.45, 37.8) * mm});
            skLineSegment(sketch, "E12112", {"start": v(-71.45, 37.8) * mm, "end": v(-71.62, 37.74) * mm});
            skLineSegment(sketch, "E12113", {"start": v(-71.62, 37.74) * mm, "end": v(-71.8, 37.71) * mm});
            skLineSegment(sketch, "E12114", {"start": v(-71.8, 37.71) * mm, "end": v(-71.97, 37.7) * mm});
            skLineSegment(sketch, "E12115", {"start": v(-71.97, 37.7) * mm, "end": v(-72.13, 37.71) * mm});
            skLineSegment(sketch, "E12116", {"start": v(-72.13, 37.71) * mm, "end": v(-72.23, 37.74) * mm});
            skLineSegment(sketch, "E12117", {"start": v(-72.23, 37.74) * mm, "end": v(-72.34, 37.78) * mm});
            skLineSegment(sketch, "E12118", {"start": v(-72.34, 37.78) * mm, "end": v(-72.44, 37.83) * mm});
            skLineSegment(sketch, "E12119", {"start": v(-72.44, 37.83) * mm, "end": v(-72.55, 37.9) * mm});
            skLineSegment(sketch, "E12120", {"start": v(-72.55, 37.9) * mm, "end": v(-72.75, 38.05) * mm});
            skLineSegment(sketch, "E12121", {"start": v(-72.75, 38.05) * mm, "end": v(-72.95, 38.22) * mm});
            skLineSegment(sketch, "E12122", {"start": v(-72.95, 38.22) * mm, "end": v(-73.13, 38.38) * mm});
            skLineSegment(sketch, "E12123", {"start": v(-73.13, 38.38) * mm, "end": v(-73.3, 38.52) * mm});
            skLineSegment(sketch, "E12124", {"start": v(-73.3, 38.52) * mm, "end": v(-73.38, 38.57) * mm});
            skLineSegment(sketch, "E12125", {"start": v(-73.38, 38.57) * mm, "end": v(-73.46, 38.61) * mm});
            skLineSegment(sketch, "E12126", {"start": v(-73.46, 38.61) * mm, "end": v(-73.53, 38.63) * mm});
            skLineSegment(sketch, "E12127", {"start": v(-73.53, 38.63) * mm, "end": v(-73.6, 38.64) * mm});
            skLineSegment(sketch, "E12128", {"start": v(-73.6, 38.64) * mm, "end": v(-73.65, 38.62) * mm});
            skLineSegment(sketch, "E12129", {"start": v(-73.65, 38.62) * mm, "end": v(-73.7, 38.6) * mm});
            skLineSegment(sketch, "E12130", {"start": v(-73.7, 38.6) * mm, "end": v(-73.83, 38.52) * mm});
            skLineSegment(sketch, "E12131", {"start": v(-73.83, 38.52) * mm, "end": v(-73.96, 38.4) * mm});
            skLineSegment(sketch, "E12132", {"start": v(-73.96, 38.4) * mm, "end": v(-74.1, 38.27) * mm});
            skLineSegment(sketch, "E12133", {"start": v(-74.1, 38.27) * mm, "end": v(-74.35, 37.97) * mm});
            skLineSegment(sketch, "E12134", {"start": v(-74.35, 37.97) * mm, "end": v(-74.58, 37.7) * mm});
            skLineSegment(sketch, "E12135", {"start": v(-74.58, 37.7) * mm, "end": v(-74.72, 37.52) * mm});
            skLineSegment(sketch, "E12136", {"start": v(-74.72, 37.52) * mm, "end": v(-74.86, 37.32) * mm});
            skLineSegment(sketch, "E12137", {"start": v(-74.86, 37.32) * mm, "end": v(-75, 37.1) * mm});
            skLineSegment(sketch, "E12138", {"start": v(-75, 37.1) * mm, "end": v(-75.16, 36.86) * mm});
            skLineSegment(sketch, "E12139", {"start": v(-75.16, 36.86) * mm, "end": v(-75.47, 36.32) * mm});
            skLineSegment(sketch, "E12140", {"start": v(-75.47, 36.32) * mm, "end": v(-75.8, 35.72) * mm});
            skLineSegment(sketch, "E12141", {"start": v(-75.8, 35.72) * mm, "end": v(-76.12, 35.05) * mm});
            skLineSegment(sketch, "E12142", {"start": v(-76.12, 35.05) * mm, "end": v(-76.44, 34.33) * mm});
            skLineSegment(sketch, "E12143", {"start": v(-76.44, 34.33) * mm, "end": v(-76.76, 33.58) * mm});
            skLineSegment(sketch, "E12144", {"start": v(-76.76, 33.58) * mm, "end": v(-77.08, 32.8) * mm});
            skLineSegment(sketch, "E12145", {"start": v(-77.08, 32.8) * mm, "end": v(-77.38, 32) * mm});
            skLineSegment(sketch, "E12146", {"start": v(-77.38, 32) * mm, "end": v(-77.67, 31.19) * mm});
            skLineSegment(sketch, "E12147", {"start": v(-77.67, 31.19) * mm, "end": v(-77.94, 30.38) * mm});
            skLineSegment(sketch, "E12148", {"start": v(-77.94, 30.38) * mm, "end": v(-78.18, 29.58) * mm});
            skLineSegment(sketch, "E12149", {"start": v(-78.18, 29.58) * mm, "end": v(-78.4, 28.8) * mm});
            skLineSegment(sketch, "E12150", {"start": v(-78.4, 28.8) * mm, "end": v(-78.6, 28.07) * mm});
            skLineSegment(sketch, "E12151", {"start": v(-78.6, 28.07) * mm, "end": v(-78.75, 27.36) * mm});
            skLineSegment(sketch, "E12152", {"start": v(-78.75, 27.36) * mm, "end": v(-78.87, 26.71) * mm});
            skLineSegment(sketch, "E12153", {"start": v(-78.87, 26.71) * mm, "end": v(-78.95, 26.13) * mm});
            skLineSegment(sketch, "E12154", {"start": v(-78.95, 26.13) * mm, "end": v(-79.03, 25.51) * mm});
            skLineSegment(sketch, "E12155", {"start": v(-79.03, 25.51) * mm, "end": v(-79.14, 24.49) * mm});
            skLineSegment(sketch, "E12156", {"start": v(-79.14, 24.49) * mm, "end": v(-79.16, 24.28) * mm});
            skLineSegment(sketch, "E12157", {"start": v(-79.16, 24.28) * mm, "end": v(-79.2, 24.06) * mm});
            skLineSegment(sketch, "E12158", {"start": v(-79.2, 24.06) * mm, "end": v(-79.23, 23.95) * mm});
            skLineSegment(sketch, "E12159", {"start": v(-79.23, 23.95) * mm, "end": v(-79.26, 23.85) * mm});
            skLineSegment(sketch, "E12160", {"start": v(-79.26, 23.85) * mm, "end": v(-79.3, 23.75) * mm});
            skLineSegment(sketch, "E12161", {"start": v(-79.3, 23.75) * mm, "end": v(-79.36, 23.67) * mm});
            skLineSegment(sketch, "E12162", {"start": v(-79.36, 23.67) * mm, "end": v(-79.46, 23.54) * mm});
            skLineSegment(sketch, "E12163", {"start": v(-79.46, 23.54) * mm, "end": v(-79.58, 23.4) * mm});
            skLineSegment(sketch, "E12164", {"start": v(-79.58, 23.4) * mm, "end": v(-79.85, 23.15) * mm});
            skLineSegment(sketch, "E12165", {"start": v(-79.85, 23.15) * mm, "end": v(-80.16, 22.88) * mm});
            skLineSegment(sketch, "E12166", {"start": v(-80.16, 22.88) * mm, "end": v(-80.5, 22.6) * mm});
            skLineSegment(sketch, "E12167", {"start": v(-80.5, 22.6) * mm, "end": v(-80.84, 22.31) * mm});
            skLineSegment(sketch, "E12168", {"start": v(-80.84, 22.31) * mm, "end": v(-81.18, 22) * mm});
            skLineSegment(sketch, "E12169", {"start": v(-81.18, 22) * mm, "end": v(-81.34, 21.85) * mm});
            skLineSegment(sketch, "E12170", {"start": v(-81.34, 21.85) * mm, "end": v(-81.5, 21.68) * mm});
            skLineSegment(sketch, "E12171", {"start": v(-81.5, 21.68) * mm, "end": v(-81.64, 21.51) * mm});
            skLineSegment(sketch, "E12172", {"start": v(-81.64, 21.51) * mm, "end": v(-81.78, 21.34) * mm});
            skLineSegment(sketch, "E12173", {"start": v(-81.78, 21.34) * mm, "end": v(-81.92, 21.13) * mm});
            skLineSegment(sketch, "E12174", {"start": v(-81.92, 21.13) * mm, "end": v(-82.1, 20.86) * mm});
            skLineSegment(sketch, "E12175", {"start": v(-82.1, 20.86) * mm, "end": v(-82.5, 20.2) * mm});
            skLineSegment(sketch, "E12176", {"start": v(-82.5, 20.2) * mm, "end": v(-82.71, 19.85) * mm});
            skLineSegment(sketch, "E12177", {"start": v(-82.71, 19.85) * mm, "end": v(-82.89, 19.51) * mm});
            skLineSegment(sketch, "E12178", {"start": v(-82.89, 19.51) * mm, "end": v(-83.03, 19.22) * mm});
            skLineSegment(sketch, "E12179", {"start": v(-83.03, 19.22) * mm, "end": v(-83.13, 19) * mm});
            skLineSegment(sketch, "E12180", {"start": v(-83.13, 19) * mm, "end": v(-83.26, 18.57) * mm});
            skLineSegment(sketch, "E12181", {"start": v(-83.26, 18.57) * mm, "end": v(-83.39, 18.14) * mm});
            skLineSegment(sketch, "E12182", {"start": v(-83.39, 18.14) * mm, "end": v(-83.5, 17.72) * mm});
            skLineSegment(sketch, "E12183", {"start": v(-83.5, 17.72) * mm, "end": v(-83.6, 17.3) * mm});
            skLineSegment(sketch, "E12184", {"start": v(-83.6, 17.3) * mm, "end": v(-83.7, 16.86) * mm});
            skLineSegment(sketch, "E12185", {"start": v(-83.7, 16.86) * mm, "end": v(-83.8, 16.41) * mm});
            skLineSegment(sketch, "E12186", {"start": v(-83.8, 16.41) * mm, "end": v(-83.96, 15.49) * mm});
            skLineSegment(sketch, "E12187", {"start": v(-83.96, 15.49) * mm, "end": v(-84.11, 14.48) * mm});
            skLineSegment(sketch, "E12188", {"start": v(-84.11, 14.48) * mm, "end": v(-84.26, 13.38) * mm});
            skLineSegment(sketch, "E12189", {"start": v(-84.26, 13.38) * mm, "end": v(-84.6, 10.8) * mm});
            skLineSegment(sketch, "E12190", {"start": v(-84.6, 10.8) * mm, "end": v(-84.6, 10.6) * mm});
            skLineSegment(sketch, "E12191", {"start": v(-84.6, 10.6) * mm, "end": v(-84.61, 10.4) * mm});
            skLineSegment(sketch, "E12192", {"start": v(-84.61, 10.4) * mm, "end": v(-84.6, 9.95) * mm});
            skLineSegment(sketch, "E12193", {"start": v(-84.6, 9.95) * mm, "end": v(-84.58, 9.47) * mm});
            skLineSegment(sketch, "E12194", {"start": v(-84.58, 9.47) * mm, "end": v(-84.57, 8.98) * mm});
            skLineSegment(sketch, "E12195", {"start": v(-84.57, 8.98) * mm, "end": v(-84.57, 8.74) * mm});
            skLineSegment(sketch, "E12196", {"start": v(-84.57, 8.74) * mm, "end": v(-84.58, 8.5) * mm});
            skLineSegment(sketch, "E12197", {"start": v(-84.58, 8.5) * mm, "end": v(-84.6, 8.28) * mm});
            skLineSegment(sketch, "E12198", {"start": v(-84.6, 8.28) * mm, "end": v(-84.65, 8.07) * mm});
            skLineSegment(sketch, "E12199", {"start": v(-84.65, 8.07) * mm, "end": v(-84.7, 7.87) * mm});
            skLineSegment(sketch, "E12200", {"start": v(-84.7, 7.87) * mm, "end": v(-84.78, 7.7) * mm});
            skLineSegment(sketch, "E12201", {"start": v(-84.78, 7.7) * mm, "end": v(-84.83, 7.6) * mm});
            skLineSegment(sketch, "E12202", {"start": v(-84.83, 7.6) * mm, "end": v(-84.88, 7.53) * mm});
            skLineSegment(sketch, "E12203", {"start": v(-84.88, 7.53) * mm, "end": v(-84.94, 7.46) * mm});
            skLineSegment(sketch, "E12204", {"start": v(-84.94, 7.46) * mm, "end": v(-85, 7.4) * mm});
            skLineSegment(sketch, "E12205", {"start": v(-85, 7.4) * mm, "end": v(-85.05, 7.38) * mm});
            skLineSegment(sketch, "E12206", {"start": v(-85.05, 7.38) * mm, "end": v(-85.13, 7.37) * mm});
            skLineSegment(sketch, "E12207", {"start": v(-85.13, 7.37) * mm, "end": v(-85.34, 7.37) * mm});
            skLineSegment(sketch, "E12208", {"start": v(-85.34, 7.37) * mm, "end": v(-85.56, 7.39) * mm});
            skLineSegment(sketch, "E12209", {"start": v(-85.56, 7.39) * mm, "end": v(-85.7, 7.4) * mm});
            skLineSegment(sketch, "E12210", {"start": v(-85.7, 7.4) * mm, "end": v(-85.95, 7.5) * mm});
            skLineSegment(sketch, "E12211", {"start": v(-85.95, 7.5) * mm, "end": v(-86.26, 7.65) * mm});
            skLineSegment(sketch, "E12212", {"start": v(-86.26, 7.65) * mm, "end": v(-86.6, 7.85) * mm});
            skLineSegment(sketch, "E12213", {"start": v(-86.6, 7.85) * mm, "end": v(-86.8, 7.97) * mm});
            skLineSegment(sketch, "E12214", {"start": v(-86.8, 7.97) * mm, "end": v(-87, 8.1) * mm});
            skLineSegment(sketch, "E12215", {"start": v(-87, 8.1) * mm, "end": v(-87.1, 8.2) * mm});
            skLineSegment(sketch, "E12216", {"start": v(-87.1, 8.2) * mm, "end": v(-87.22, 8.3) * mm});
            skLineSegment(sketch, "E12217", {"start": v(-87.22, 8.3) * mm, "end": v(-87.46, 8.54) * mm});
            skLineSegment(sketch, "E12218", {"start": v(-87.46, 8.54) * mm, "end": v(-87.58, 8.65) * mm});
            skLineSegment(sketch, "E12219", {"start": v(-87.58, 8.65) * mm, "end": v(-87.7, 8.73) * mm});
            skLineSegment(sketch, "E12220", {"start": v(-87.7, 8.73) * mm, "end": v(-87.77, 8.77) * mm});
            skLineSegment(sketch, "E12221", {"start": v(-87.77, 8.77) * mm, "end": v(-87.84, 8.79) * mm});
            skLineSegment(sketch, "E12222", {"start": v(-87.84, 8.79) * mm, "end": v(-87.9, 8.8) * mm});
            skLineSegment(sketch, "E12223", {"start": v(-87.9, 8.8) * mm, "end": v(-87.97, 8.8) * mm});
            skLineSegment(sketch, "E12224", {"start": v(-87.97, 8.8) * mm, "end": v(-88.04, 8.78) * mm});
            skLineSegment(sketch, "E12225", {"start": v(-88.04, 8.78) * mm, "end": v(-88.11, 8.75) * mm});
            skLineSegment(sketch, "E12226", {"start": v(-88.11, 8.75) * mm, "end": v(-88.18, 8.7) * mm});
            skLineSegment(sketch, "E12227", {"start": v(-88.18, 8.7) * mm, "end": v(-88.25, 8.63) * mm});
            skLineSegment(sketch, "E12228", {"start": v(-88.25, 8.63) * mm, "end": v(-88.35, 8.49) * mm});
            skLineSegment(sketch, "E12229", {"start": v(-88.35, 8.49) * mm, "end": v(-88.43, 8.34) * mm});
            skLineSegment(sketch, "E12230", {"start": v(-88.43, 8.34) * mm, "end": v(-88.52, 8.07) * mm});
            skLineSegment(sketch, "E12231", {"start": v(-88.52, 8.07) * mm, "end": v(-88.6, 7.78) * mm});
            skLineSegment(sketch, "E12232", {"start": v(-88.6, 7.78) * mm, "end": v(-88.65, 7.48) * mm});
            skLineSegment(sketch, "E12233", {"start": v(-88.65, 7.48) * mm, "end": v(-88.68, 7.17) * mm});
            skLineSegment(sketch, "E12234", {"start": v(-88.68, 7.17) * mm, "end": v(-88.7, 6.85) * mm});
            skLineSegment(sketch, "E12235", {"start": v(-88.7, 6.85) * mm, "end": v(-88.7, 6.52) * mm});
            skLineSegment(sketch, "E12236", {"start": v(-88.7, 6.52) * mm, "end": v(-88.69, 6.19) * mm});
            skLineSegment(sketch, "E12237", {"start": v(-88.69, 6.19) * mm, "end": v(-88.67, 5.85) * mm});
            skLineSegment(sketch, "E12238", {"start": v(-88.67, 5.85) * mm, "end": v(-88.6, 5.18) * mm});
            skLineSegment(sketch, "E12239", {"start": v(-88.6, 5.18) * mm, "end": v(-88.52, 4.51) * mm});
            skLineSegment(sketch, "E12240", {"start": v(-88.52, 4.51) * mm, "end": v(-88.43, 3.88) * mm});
            skLineSegment(sketch, "E12241", {"start": v(-88.43, 3.88) * mm, "end": v(-88.36, 3.28) * mm});
            skLineSegment(sketch, "E12242", {"start": v(-88.36, 3.28) * mm, "end": v(-88.3, 2.87) * mm});
            skLineSegment(sketch, "E12243", {"start": v(-88.3, 2.87) * mm, "end": v(-88.22, 2.42) * mm});
            skLineSegment(sketch, "E12244", {"start": v(-88.22, 2.42) * mm, "end": v(-88.03, 1.5) * mm});
            skLineSegment(sketch, "E12245", {"start": v(-88.03, 1.5) * mm, "end": v(-87.82, 0.59) * mm});
            skLineSegment(sketch, "E12246", {"start": v(-87.82, 0.59) * mm, "end": v(-87.63, -0.27) * mm});
            skLineSegment(sketch, "E12247", {"start": v(-87.63, -0.27) * mm, "end": v(-87.46, -1.06) * mm});
            skLineSegment(sketch, "E12248", {"start": v(-87.46, -1.06) * mm, "end": v(-87.26, -1.94) * mm});
            skLineSegment(sketch, "E12249", {"start": v(-87.26, -1.94) * mm, "end": v(-87.04, -2.88) * mm});
            skLineSegment(sketch, "E12250", {"start": v(-87.04, -2.88) * mm, "end": v(-86.8, -3.86) * mm});
            skLineSegment(sketch, "E12251", {"start": v(-86.8, -3.86) * mm, "end": v(-86.54, -4.85) * mm});
            skLineSegment(sketch, "E12252", {"start": v(-86.54, -4.85) * mm, "end": v(-86.3, -5.8) * mm});
            skLineSegment(sketch, "E12253", {"start": v(-86.3, -5.8) * mm, "end": v(-86.05, -6.7) * mm});
            skLineSegment(sketch, "E12254", {"start": v(-86.05, -6.7) * mm, "end": v(-85.81, -7.53) * mm});
            skLineSegment(sketch, "E12255", {"start": v(-85.81, -7.53) * mm, "end": v(-85.2, -9.63) * mm});
            skLineSegment(sketch, "E12256", {"start": v(-85.2, -9.63) * mm, "end": v(-84.88, -10.72) * mm});
            skLineSegment(sketch, "E12257", {"start": v(-84.88, -10.72) * mm, "end": v(-84.6, -11.73) * mm});
            skLineSegment(sketch, "E12258", {"start": v(-84.6, -11.73) * mm, "end": v(-84.55, -11.85) * mm});
            skLineSegment(sketch, "E12259", {"start": v(-84.55, -11.85) * mm, "end": v(-84.48, -11.99) * mm});
            skLineSegment(sketch, "E12260", {"start": v(-84.48, -11.99) * mm, "end": v(-84.45, -12.06) * mm});
            skLineSegment(sketch, "E12261", {"start": v(-84.45, -12.06) * mm, "end": v(-84.44, -12.12) * mm});
            skLineSegment(sketch, "E12262", {"start": v(-84.44, -12.12) * mm, "end": v(-84.44, -12.18) * mm});
            skLineSegment(sketch, "E12263", {"start": v(-84.44, -12.18) * mm, "end": v(-84.47, -12.22) * mm});
            skLineSegment(sketch, "E12264", {"start": v(-84.47, -12.22) * mm, "end": v(-84.52, -12.27) * mm});
            skLineSegment(sketch, "E12265", {"start": v(-84.52, -12.27) * mm, "end": v(-84.58, -12.3) * mm});
            skLineSegment(sketch, "E12266", {"start": v(-84.58, -12.3) * mm, "end": v(-84.65, -12.31) * mm});
            skLineSegment(sketch, "E12267", {"start": v(-84.65, -12.31) * mm, "end": v(-84.72, -12.32) * mm});
            skLineSegment(sketch, "E12268", {"start": v(-84.72, -12.32) * mm, "end": v(-84.81, -12.32) * mm});
            skLineSegment(sketch, "E12269", {"start": v(-84.81, -12.32) * mm, "end": v(-84.9, -12.3) * mm});
            skLineSegment(sketch, "E12270", {"start": v(-84.9, -12.3) * mm, "end": v(-85.12, -12.26) * mm});
            skLineSegment(sketch, "E12271", {"start": v(-85.12, -12.26) * mm, "end": v(-85.36, -12.2) * mm});
            skLineSegment(sketch, "E12272", {"start": v(-85.36, -12.2) * mm, "end": v(-85.61, -12.1) * mm});
            skLineSegment(sketch, "E12273", {"start": v(-85.61, -12.1) * mm, "end": v(-86.17, -11.9) * mm});
            skLineSegment(sketch, "E12274", {"start": v(-86.17, -11.9) * mm, "end": v(-86.46, -11.8) * mm});
            skLineSegment(sketch, "E12275", {"start": v(-86.46, -11.8) * mm, "end": v(-86.76, -11.7) * mm});
            skLineSegment(sketch, "E12276", {"start": v(-86.76, -11.7) * mm, "end": v(-87.05, -11.62) * mm});
            skLineSegment(sketch, "E12277", {"start": v(-87.05, -11.62) * mm, "end": v(-87.33, -11.55) * mm});
            skLineSegment(sketch, "E12278", {"start": v(-87.33, -11.55) * mm, "end": v(-87.6, -11.52) * mm});
            skLineSegment(sketch, "E12279", {"start": v(-87.6, -11.52) * mm, "end": v(-87.72, -11.51) * mm});
            skLineSegment(sketch, "E12280", {"start": v(-87.72, -11.51) * mm, "end": v(-87.84, -11.52) * mm});
            skLineSegment(sketch, "E12281", {"start": v(-87.84, -11.52) * mm, "end": v(-87.96, -11.53) * mm});
            skLineSegment(sketch, "E12282", {"start": v(-87.96, -11.53) * mm, "end": v(-88.07, -11.56) * mm});
            skLineSegment(sketch, "E12283", {"start": v(-88.07, -11.56) * mm, "end": v(-88.18, -11.6) * mm});
            skLineSegment(sketch, "E12284", {"start": v(-88.18, -11.6) * mm, "end": v(-88.27, -11.65) * mm});
            skLineSegment(sketch, "E12285", {"start": v(-88.27, -11.65) * mm, "end": v(-88.34, -11.7) * mm});
            skLineSegment(sketch, "E12286", {"start": v(-88.34, -11.7) * mm, "end": v(-88.4, -11.76) * mm});
            skLineSegment(sketch, "E12287", {"start": v(-88.4, -11.76) * mm, "end": v(-88.47, -11.84) * mm});
            skLineSegment(sketch, "E12288", {"start": v(-88.47, -11.84) * mm, "end": v(-88.52, -11.92) * mm});
            skLineSegment(sketch, "E12289", {"start": v(-88.52, -11.92) * mm, "end": v(-88.56, -12.01) * mm});
            skLineSegment(sketch, "E12290", {"start": v(-88.56, -12.01) * mm, "end": v(-88.6, -12.11) * mm});
            skLineSegment(sketch, "E12291", {"start": v(-88.6, -12.11) * mm, "end": v(-88.65, -12.32) * mm});
            skLineSegment(sketch, "E12292", {"start": v(-88.65, -12.32) * mm, "end": v(-88.7, -12.54) * mm});
            skLineSegment(sketch, "E12293", {"start": v(-88.7, -12.54) * mm, "end": v(-88.73, -12.77) * mm});
            skLineSegment(sketch, "E12294", {"start": v(-88.73, -12.77) * mm, "end": v(-88.79, -13.19) * mm});
            skLineSegment(sketch, "E12295", {"start": v(-88.79, -13.19) * mm, "end": v(-88.83, -13.43) * mm});
            skLineSegment(sketch, "E12296", {"start": v(-88.83, -13.43) * mm, "end": v(-88.86, -13.75) * mm});
            skLineSegment(sketch, "E12297", {"start": v(-88.86, -13.75) * mm, "end": v(-88.93, -14.55) * mm});
            skLineSegment(sketch, "E12298", {"start": v(-88.93, -14.55) * mm, "end": v(-88.99, -15.5) * mm});
            skLineSegment(sketch, "E12299", {"start": v(-88.99, -15.5) * mm, "end": v(-89, -16) * mm});
            skLineSegment(sketch, "E12300", {"start": v(-89, -16) * mm, "end": v(-89.02, -16.49) * mm});
            skLineSegment(sketch, "E12301", {"start": v(-89.02, -16.49) * mm, "end": v(-89.01, -17.05) * mm});
            skLineSegment(sketch, "E12302", {"start": v(-89.01, -17.05) * mm, "end": v(-89, -17.65) * mm});
            skLineSegment(sketch, "E12303", {"start": v(-89, -17.65) * mm, "end": v(-88.96, -18.26) * mm});
            skLineSegment(sketch, "E12304", {"start": v(-88.96, -18.26) * mm, "end": v(-88.94, -18.54) * mm});
            skLineSegment(sketch, "E12305", {"start": v(-88.94, -18.54) * mm, "end": v(-88.9, -18.81) * mm});
            skLineSegment(sketch, "E12306", {"start": v(-88.9, -18.81) * mm, "end": v(-88.85, -19.1) * mm});
            skLineSegment(sketch, "E12307", {"start": v(-88.85, -19.1) * mm, "end": v(-88.79, -19.38) * mm});
            skLineSegment(sketch, "E12308", {"start": v(-88.79, -19.38) * mm, "end": v(-88.63, -19.99) * mm});
            skLineSegment(sketch, "E12309", {"start": v(-88.63, -19.99) * mm, "end": v(-88.45, -20.58) * mm});
            skLineSegment(sketch, "E12310", {"start": v(-88.45, -20.58) * mm, "end": v(-88.27, -21.14) * mm});
            skLineSegment(sketch, "E12311", {"start": v(-88.27, -21.14) * mm, "end": v(-87.93, -22.13) * mm});
            skLineSegment(sketch, "E12312", {"start": v(-87.93, -22.13) * mm, "end": v(-87.56, -23.13) * mm});
            skLineSegment(sketch, "E12313", {"start": v(-87.56, -23.13) * mm, "end": v(-87.2, -24.01) * mm});
            skLineSegment(sketch, "E12314", {"start": v(-87.2, -24.01) * mm, "end": v(-87.04, -24.38) * mm});
            skLineSegment(sketch, "E12315", {"start": v(-87.04, -24.38) * mm, "end": v(-86.9, -24.67) * mm});
            skLineSegment(sketch, "E12316", {"start": v(-86.9, -24.67) * mm, "end": v(-86.76, -24.97) * mm});
            skLineSegment(sketch, "E12317", {"start": v(-86.76, -24.97) * mm, "end": v(-86.6, -25.3) * mm});
            skLineSegment(sketch, "E12318", {"start": v(-86.6, -25.3) * mm, "end": v(-86.45, -25.61) * mm});
            skLineSegment(sketch, "E12319", {"start": v(-86.45, -25.61) * mm, "end": v(-86.37, -25.76) * mm});
            skLineSegment(sketch, "E12320", {"start": v(-86.37, -25.76) * mm, "end": v(-86.28, -25.9) * mm});
            skLineSegment(sketch, "E12321", {"start": v(-86.28, -25.9) * mm, "end": v(-86.07, -26.17) * mm});
            skLineSegment(sketch, "E12322", {"start": v(-86.07, -26.17) * mm, "end": v(-85.83, -26.45) * mm});
            skLineSegment(sketch, "E12323", {"start": v(-85.83, -26.45) * mm, "end": v(-85.55, -26.74) * mm});
            skLineSegment(sketch, "E12324", {"start": v(-85.55, -26.74) * mm, "end": v(-85.25, -27.03) * mm});
            skLineSegment(sketch, "E12325", {"start": v(-85.25, -27.03) * mm, "end": v(-84.62, -27.6) * mm});
            skLineSegment(sketch, "E12326", {"start": v(-84.62, -27.6) * mm, "end": v(-83.96, -28.18) * mm});
            skLineSegment(sketch, "E12327", {"start": v(-83.96, -28.18) * mm, "end": v(-83.65, -28.47) * mm});
            skLineSegment(sketch, "E12328", {"start": v(-83.65, -28.47) * mm, "end": v(-83.35, -28.74) * mm});
            skLineSegment(sketch, "E12329", {"start": v(-83.35, -28.74) * mm, "end": v(-83.07, -29.01) * mm});
            skLineSegment(sketch, "E12330", {"start": v(-83.07, -29.01) * mm, "end": v(-82.83, -29.28) * mm});
            skLineSegment(sketch, "E12331", {"start": v(-82.83, -29.28) * mm, "end": v(-82.61, -29.53) * mm});
            skLineSegment(sketch, "E12332", {"start": v(-82.61, -29.53) * mm, "end": v(-82.44, -29.77) * mm});
            skLineSegment(sketch, "E12333", {"start": v(-82.44, -29.77) * mm, "end": v(-82.37, -29.88) * mm});
            skLineSegment(sketch, "E12334", {"start": v(-82.37, -29.88) * mm, "end": v(-82.32, -30) * mm});
            skLineSegment(sketch, "E12335", {"start": v(-82.32, -30) * mm, "end": v(-82.27, -30.1) * mm});
            skLineSegment(sketch, "E12336", {"start": v(-82.27, -30.1) * mm, "end": v(-82.25, -30.21) * mm});
            skLineSegment(sketch, "E12337", {"start": v(-82.25, -30.21) * mm, "end": v(-82.23, -30.35) * mm});
            skLineSegment(sketch, "E12338", {"start": v(-82.23, -30.35) * mm, "end": v(-82.22, -30.5) * mm});
            skLineSegment(sketch, "E12339", {"start": v(-82.22, -30.5) * mm, "end": v(-82.23, -30.64) * mm});
            skLineSegment(sketch, "E12340", {"start": v(-82.23, -30.64) * mm, "end": v(-82.26, -30.8) * mm});
            skLineSegment(sketch, "E12341", {"start": v(-82.26, -30.8) * mm, "end": v(-82.3, -30.93) * mm});
            skLineSegment(sketch, "E12342", {"start": v(-82.3, -30.93) * mm, "end": v(-82.37, -31.06) * mm});
            skLineSegment(sketch, "E12343", {"start": v(-82.37, -31.06) * mm, "end": v(-82.4, -31.11) * mm});
            skLineSegment(sketch, "E12344", {"start": v(-82.4, -31.11) * mm, "end": v(-82.45, -31.16) * mm});
            skLineSegment(sketch, "E12345", {"start": v(-82.45, -31.16) * mm, "end": v(-82.5, -31.2) * mm});
            skLineSegment(sketch, "E12346", {"start": v(-82.5, -31.2) * mm, "end": v(-82.56, -31.24) * mm});
            skLineSegment(sketch, "E12347", {"start": v(-82.56, -31.24) * mm, "end": v(-82.62, -31.28) * mm});
            skLineSegment(sketch, "E12348", {"start": v(-82.62, -31.28) * mm, "end": v(-82.7, -31.3) * mm});
            skLineSegment(sketch, "E12349", {"start": v(-82.7, -31.3) * mm, "end": v(-82.87, -31.34) * mm});
            skLineSegment(sketch, "E12350", {"start": v(-82.87, -31.34) * mm, "end": v(-83.05, -31.36) * mm});
            skLineSegment(sketch, "E12351", {"start": v(-83.05, -31.36) * mm, "end": v(-83.26, -31.37) * mm});
            skLineSegment(sketch, "E12352", {"start": v(-83.26, -31.37) * mm, "end": v(-83.7, -31.35) * mm});
            skLineSegment(sketch, "E12353", {"start": v(-83.7, -31.35) * mm, "end": v(-84.16, -31.3) * mm});
            skLineSegment(sketch, "E12354", {"start": v(-84.16, -31.3) * mm, "end": v(-84.6, -31.28) * mm});
            skLineSegment(sketch, "E12355", {"start": v(-84.6, -31.28) * mm, "end": v(-84.82, -31.28) * mm});
            skLineSegment(sketch, "E12356", {"start": v(-84.82, -31.28) * mm, "end": v(-85.02, -31.29) * mm});
            skLineSegment(sketch, "E12357", {"start": v(-85.02, -31.29) * mm, "end": v(-85.2, -31.32) * mm});
            skLineSegment(sketch, "E12358", {"start": v(-85.2, -31.32) * mm, "end": v(-85.37, -31.36) * mm});
            skLineSegment(sketch, "E12359", {"start": v(-85.37, -31.36) * mm, "end": v(-85.45, -31.4) * mm});
            skLineSegment(sketch, "E12360", {"start": v(-85.45, -31.4) * mm, "end": v(-85.51, -31.44) * mm});
            skLineSegment(sketch, "E12361", {"start": v(-85.51, -31.44) * mm, "end": v(-85.57, -31.48) * mm});
            skLineSegment(sketch, "E12362", {"start": v(-85.57, -31.48) * mm, "end": v(-85.62, -31.54) * mm});
            skLineSegment(sketch, "E12363", {"start": v(-85.62, -31.54) * mm, "end": v(-85.64, -31.56) * mm});
            skLineSegment(sketch, "E12364", {"start": v(-85.64, -31.56) * mm, "end": v(-85.65, -31.6) * mm});
            skLineSegment(sketch, "E12365", {"start": v(-85.65, -31.6) * mm, "end": v(-85.65, -31.68) * mm});
            skLineSegment(sketch, "E12366", {"start": v(-85.65, -31.68) * mm, "end": v(-85.63, -31.76) * mm});
            skLineSegment(sketch, "E12367", {"start": v(-85.63, -31.76) * mm, "end": v(-85.62, -31.84) * mm});
            skLineSegment(sketch, "E12368", {"start": v(-85.62, -31.84) * mm, "end": v(-85.6, -32.1) * mm});
            skLineSegment(sketch, "E12369", {"start": v(-85.6, -32.1) * mm, "end": v(-85.5, -32.57) * mm});
            skLineSegment(sketch, "E12370", {"start": v(-85.5, -32.57) * mm, "end": v(-85.38, -33.19) * mm});
            skLineSegment(sketch, "E12371", {"start": v(-85.38, -33.19) * mm, "end": v(-85.23, -33.9) * mm});
            skLineSegment(sketch, "E12372", {"start": v(-85.23, -33.9) * mm, "end": v(-85.17, -34.1) * mm});
            skLineSegment(sketch, "E12373", {"start": v(-85.17, -34.1) * mm, "end": v(-85.08, -34.33) * mm});
            skLineSegment(sketch, "E12374", {"start": v(-85.08, -34.33) * mm, "end": v(-84.98, -34.56) * mm});
            skLineSegment(sketch, "E12375", {"start": v(-84.98, -34.56) * mm, "end": v(-84.86, -34.8) * mm});
            skLineSegment(sketch, "E12376", {"start": v(-84.86, -34.8) * mm, "end": v(-84.6, -35.27) * mm});
            skLineSegment(sketch, "E12377", {"start": v(-84.6, -35.27) * mm, "end": v(-84.38, -35.67) * mm});
            skLineSegment(sketch, "E12378", {"start": v(-84.38, -35.67) * mm, "end": v(-84.22, -35.95) * mm});
            skLineSegment(sketch, "E12379", {"start": v(-84.22, -35.95) * mm, "end": v(-84.04, -36.22) * mm});
            skLineSegment(sketch, "E12380", {"start": v(-84.04, -36.22) * mm, "end": v(-83.86, -36.5) * mm});
            skLineSegment(sketch, "E12381", {"start": v(-83.86, -36.5) * mm, "end": v(-83.67, -36.77) * mm});
            skLineSegment(sketch, "E12382", {"start": v(-83.67, -36.77) * mm, "end": v(-83.46, -37.04) * mm});
            skLineSegment(sketch, "E12383", {"start": v(-83.46, -37.04) * mm, "end": v(-83.25, -37.3) * mm});
            skLineSegment(sketch, "E12384", {"start": v(-83.25, -37.3) * mm, "end": v(-83.03, -37.57) * mm});
            skLineSegment(sketch, "E12385", {"start": v(-83.03, -37.57) * mm, "end": v(-82.8, -37.83) * mm});
            skLineSegment(sketch, "E12386", {"start": v(-82.8, -37.83) * mm, "end": v(-82.57, -38.08) * mm});
            skLineSegment(sketch, "E12387", {"start": v(-82.57, -38.08) * mm, "end": v(-82.33, -38.32) * mm});
            skLineSegment(sketch, "E12388", {"start": v(-82.33, -38.32) * mm, "end": v(-82.08, -38.56) * mm});
            skLineSegment(sketch, "E12389", {"start": v(-82.08, -38.56) * mm, "end": v(-81.84, -38.79) * mm});
            skLineSegment(sketch, "E12390", {"start": v(-81.84, -38.79) * mm, "end": v(-81.58, -39.01) * mm});
            skLineSegment(sketch, "E12391", {"start": v(-81.58, -39.01) * mm, "end": v(-81.33, -39.22) * mm});
            skLineSegment(sketch, "E12392", {"start": v(-81.33, -39.22) * mm, "end": v(-81.07, -39.42) * mm});
            skLineSegment(sketch, "E12393", {"start": v(-81.07, -39.42) * mm, "end": v(-80.81, -39.61) * mm});
            skLineSegment(sketch, "E12394", {"start": v(-80.81, -39.61) * mm, "end": v(-80.56, -39.78) * mm});
            skLineSegment(sketch, "E12395", {"start": v(-80.56, -39.78) * mm, "end": v(-80.29, -39.93) * mm});
            skLineSegment(sketch, "E12396", {"start": v(-80.29, -39.93) * mm, "end": v(-80, -40.08) * mm});
            skLineSegment(sketch, "E12397", {"start": v(-80, -40.08) * mm, "end": v(-79.69, -40.22) * mm});
            skLineSegment(sketch, "E12398", {"start": v(-79.69, -40.22) * mm, "end": v(-79.08, -40.5) * mm});
            skLineSegment(sketch, "E12399", {"start": v(-79.08, -40.5) * mm, "end": v(-78.79, -40.62) * mm});
            skLineSegment(sketch, "E12400", {"start": v(-78.79, -40.62) * mm, "end": v(-78.52, -40.75) * mm});
            skLineSegment(sketch, "E12401", {"start": v(-78.52, -40.75) * mm, "end": v(-78, -41) * mm});
            skLineSegment(sketch, "E12402", {"start": v(-78, -41) * mm, "end": v(-77.43, -41.26) * mm});
            skLineSegment(sketch, "E12403", {"start": v(-77.43, -41.26) * mm, "end": v(-76.81, -41.54) * mm});
            skLineSegment(sketch, "E12404", {"start": v(-76.81, -41.54) * mm, "end": v(-76.17, -41.81) * mm});
            skLineSegment(sketch, "E12405", {"start": v(-76.17, -41.81) * mm, "end": v(-75.52, -42.08) * mm});
            skLineSegment(sketch, "E12406", {"start": v(-75.52, -42.08) * mm, "end": v(-74.89, -42.34) * mm});
            skLineSegment(sketch, "E12407", {"start": v(-74.89, -42.34) * mm, "end": v(-74.29, -42.57) * mm});
            skLineSegment(sketch, "E12408", {"start": v(-74.29, -42.57) * mm, "end": v(-73.75, -42.77) * mm});
            skLineSegment(sketch, "E12409", {"start": v(-73.75, -42.77) * mm, "end": v(-73.45, -42.87) * mm});
            skLineSegment(sketch, "E12410", {"start": v(-73.45, -42.87) * mm, "end": v(-73.13, -42.95) * mm});
            skLineSegment(sketch, "E12411", {"start": v(-73.13, -42.95) * mm, "end": v(-72.46, -43.13) * mm});
            skLineSegment(sketch, "E12412", {"start": v(-72.46, -43.13) * mm, "end": v(-72.13, -43.23) * mm});
            skLineSegment(sketch, "E12413", {"start": v(-72.13, -43.23) * mm, "end": v(-71.81, -43.35) * mm});
            skLineSegment(sketch, "E12414", {"start": v(-71.81, -43.35) * mm, "end": v(-71.67, -43.41) * mm});
            skLineSegment(sketch, "E12415", {"start": v(-71.67, -43.41) * mm, "end": v(-71.52, -43.49) * mm});
            skLineSegment(sketch, "E12416", {"start": v(-71.52, -43.49) * mm, "end": v(-71.4, -43.57) * mm});
            skLineSegment(sketch, "E12417", {"start": v(-71.4, -43.57) * mm, "end": v(-71.27, -43.65) * mm});
            skLineSegment(sketch, "E12418", {"start": v(-71.27, -43.65) * mm, "end": v(-71.12, -43.78) * mm});
            skLineSegment(sketch, "E12419", {"start": v(-71.12, -43.78) * mm, "end": v(-70.96, -43.93) * mm});
            skLineSegment(sketch, "E12420", {"start": v(-70.96, -43.93) * mm, "end": v(-70.8, -44.1) * mm});
            skLineSegment(sketch, "E12421", {"start": v(-70.8, -44.1) * mm, "end": v(-70.65, -44.27) * mm});
            skLineSegment(sketch, "E12422", {"start": v(-70.65, -44.27) * mm, "end": v(-70.52, -44.46) * mm});
            skLineSegment(sketch, "E12423", {"start": v(-70.52, -44.46) * mm, "end": v(-70.47, -44.56) * mm});
            skLineSegment(sketch, "E12424", {"start": v(-70.47, -44.56) * mm, "end": v(-70.43, -44.65) * mm});
            skLineSegment(sketch, "E12425", {"start": v(-70.43, -44.65) * mm, "end": v(-70.4, -44.75) * mm});
            skLineSegment(sketch, "E12426", {"start": v(-70.4, -44.75) * mm, "end": v(-70.37, -44.84) * mm});
            skLineSegment(sketch, "E12427", {"start": v(-70.37, -44.84) * mm, "end": v(-70.36, -44.94) * mm});
            skLineSegment(sketch, "E12428", {"start": v(-70.36, -44.94) * mm, "end": v(-70.37, -45.03) * mm});
            skLineSegment(sketch, "E12429", {"start": v(-70.37, -45.03) * mm, "end": v(-70.41, -45.2) * mm});
            skLineSegment(sketch, "E12430", {"start": v(-70.41, -45.2) * mm, "end": v(-70.48, -45.35) * mm});
            skLineSegment(sketch, "E12431", {"start": v(-70.48, -45.35) * mm, "end": v(-70.57, -45.5) * mm});
            skLineSegment(sketch, "E12432", {"start": v(-70.57, -45.5) * mm, "end": v(-70.7, -45.64) * mm});
            skLineSegment(sketch, "E12433", {"start": v(-70.7, -45.64) * mm, "end": v(-70.83, -45.78) * mm});
            skLineSegment(sketch, "E12434", {"start": v(-70.83, -45.78) * mm, "end": v(-70.98, -45.91) * mm});
            skLineSegment(sketch, "E12435", {"start": v(-70.98, -45.91) * mm, "end": v(-71.14, -46.03) * mm});
            skLineSegment(sketch, "E12436", {"start": v(-71.14, -46.03) * mm, "end": v(-71.31, -46.15) * mm});
            skLineSegment(sketch, "E12437", {"start": v(-71.31, -46.15) * mm, "end": v(-71.68, -46.38) * mm});
            skLineSegment(sketch, "E12438", {"start": v(-71.68, -46.38) * mm, "end": v(-72.06, -46.58) * mm});
            skLineSegment(sketch, "E12439", {"start": v(-72.06, -46.58) * mm, "end": v(-72.42, -46.77) * mm});
            skLineSegment(sketch, "E12440", {"start": v(-72.42, -46.77) * mm, "end": v(-72.74, -46.95) * mm});
            skLineSegment(sketch, "E12441", {"start": v(-72.74, -46.95) * mm, "end": v(-72.85, -47) * mm});
            skLineSegment(sketch, "E12442", {"start": v(-72.85, -47) * mm, "end": v(-72.97, -47.06) * mm});
            skLineSegment(sketch, "E12443", {"start": v(-72.97, -47.06) * mm, "end": v(-73.24, -47.14) * mm});
            skLineSegment(sketch, "E12444", {"start": v(-73.24, -47.14) * mm, "end": v(-73.52, -47.22) * mm});
            skLineSegment(sketch, "E12445", {"start": v(-73.52, -47.22) * mm, "end": v(-73.81, -47.29) * mm});
            skLineSegment(sketch, "E12446", {"start": v(-73.81, -47.29) * mm, "end": v(-74.1, -47.37) * mm});
            skLineSegment(sketch, "E12447", {"start": v(-74.1, -47.37) * mm, "end": v(-74.23, -47.41) * mm});
            skLineSegment(sketch, "E12448", {"start": v(-74.23, -47.41) * mm, "end": v(-74.35, -47.47) * mm});
            skLineSegment(sketch, "E12449", {"start": v(-74.35, -47.47) * mm, "end": v(-74.47, -47.53) * mm});
            skLineSegment(sketch, "E12450", {"start": v(-74.47, -47.53) * mm, "end": v(-74.57, -47.6) * mm});
            skLineSegment(sketch, "E12451", {"start": v(-74.57, -47.6) * mm, "end": v(-74.66, -47.68) * mm});
            skLineSegment(sketch, "E12452", {"start": v(-74.66, -47.68) * mm, "end": v(-74.74, -47.78) * mm});
            skLineSegment(sketch, "E12453", {"start": v(-74.74, -47.78) * mm, "end": v(-74.79, -47.88) * mm});
            skLineSegment(sketch, "E12454", {"start": v(-74.79, -47.88) * mm, "end": v(-74.82, -48) * mm});
            skLineSegment(sketch, "E12455", {"start": v(-74.82, -48) * mm, "end": v(-74.84, -48.13) * mm});
            skLineSegment(sketch, "E12456", {"start": v(-74.84, -48.13) * mm, "end": v(-74.84, -48.27) * mm});
            skLineSegment(sketch, "E12457", {"start": v(-74.84, -48.27) * mm, "end": v(-74.83, -48.4) * mm});
            skLineSegment(sketch, "E12458", {"start": v(-74.83, -48.4) * mm, "end": v(-74.8, -48.54) * mm});
            skLineSegment(sketch, "E12459", {"start": v(-74.8, -48.54) * mm, "end": v(-74.78, -48.66) * mm});
            skLineSegment(sketch, "E12460", {"start": v(-74.78, -48.66) * mm, "end": v(-74.74, -48.77) * mm});
            skLineSegment(sketch, "E12461", {"start": v(-74.74, -48.77) * mm, "end": v(-74.7, -48.85) * mm});
            skLineSegment(sketch, "E12462", {"start": v(-74.7, -48.85) * mm, "end": v(-74.65, -48.92) * mm});
            skLineSegment(sketch, "E12463", {"start": v(-74.65, -48.92) * mm, "end": v(-74.53, -49.07) * mm});
            skLineSegment(sketch, "E12464", {"start": v(-74.53, -49.07) * mm, "end": v(-74.4, -49.2) * mm});
            skLineSegment(sketch, "E12465", {"start": v(-74.4, -49.2) * mm, "end": v(-74.24, -49.33) * mm});
            skLineSegment(sketch, "E12466", {"start": v(-74.24, -49.33) * mm, "end": v(-73.92, -49.57) * mm});
            skLineSegment(sketch, "E12467", {"start": v(-73.92, -49.57) * mm, "end": v(-73.77, -49.7) * mm});
            skLineSegment(sketch, "E12468", {"start": v(-73.77, -49.7) * mm, "end": v(-73.64, -49.8) * mm});
            skLineSegment(sketch, "E12469", {"start": v(-73.64, -49.8) * mm, "end": v(-73.38, -50.04) * mm});
            skLineSegment(sketch, "E12470", {"start": v(-73.38, -50.04) * mm, "end": v(-73.06, -50.3) * mm});
            skLineSegment(sketch, "E12471", {"start": v(-73.06, -50.3) * mm, "end": v(-72.7, -50.56) * mm});
            skLineSegment(sketch, "E12472", {"start": v(-72.7, -50.56) * mm, "end": v(-72.29, -50.84) * mm});
            skLineSegment(sketch, "E12473", {"start": v(-72.29, -50.84) * mm, "end": v(-71.87, -51.12) * mm});
            skLineSegment(sketch, "E12474", {"start": v(-71.87, -51.12) * mm, "end": v(-71.43, -51.4) * mm});
            skLineSegment(sketch, "E12475", {"start": v(-71.43, -51.4) * mm, "end": v(-71, -51.65) * mm});
            skLineSegment(sketch, "E12476", {"start": v(-71, -51.65) * mm, "end": v(-70.59, -51.88) * mm});
            skLineSegment(sketch, "E12477", {"start": v(-70.59, -51.88) * mm, "end": v(-70.12, -52.14) * mm});
            skLineSegment(sketch, "E12478", {"start": v(-70.12, -52.14) * mm, "end": v(-69.62, -52.42) * mm});
            skLineSegment(sketch, "E12479", {"start": v(-69.62, -52.42) * mm, "end": v(-69.11, -52.7) * mm});
            skLineSegment(sketch, "E12480", {"start": v(-69.11, -52.7) * mm, "end": v(-68.87, -52.82) * mm});
            skLineSegment(sketch, "E12481", {"start": v(-68.87, -52.82) * mm, "end": v(-68.63, -52.92) * mm});
            skLineSegment(sketch, "E12482", {"start": v(-68.63, -52.92) * mm, "end": v(-68.18, -53.1) * mm});
            skLineSegment(sketch, "E12483", {"start": v(-68.18, -53.1) * mm, "end": v(-67.7, -53.28) * mm});
            skLineSegment(sketch, "E12484", {"start": v(-67.7, -53.28) * mm, "end": v(-66.66, -53.61) * mm});
            skLineSegment(sketch, "E12485", {"start": v(-66.66, -53.61) * mm, "end": v(-65.63, -53.93) * mm});
            skLineSegment(sketch, "E12486", {"start": v(-65.63, -53.93) * mm, "end": v(-64.67, -54.23) * mm});
            skLineSegment(sketch, "E12487", {"start": v(-64.67, -54.23) * mm, "end": v(-63.8, -54.5) * mm});
            skLineSegment(sketch, "E12488", {"start": v(-63.8, -54.5) * mm, "end": v(-62.84, -54.8) * mm});
            skLineSegment(sketch, "E12489", {"start": v(-62.84, -54.8) * mm, "end": v(-61.82, -55.11) * mm});
            skLineSegment(sketch, "E12490", {"start": v(-61.82, -55.11) * mm, "end": v(-60.78, -55.42) * mm});
            skLineSegment(sketch, "E12491", {"start": v(-60.78, -55.42) * mm, "end": v(-59.75, -55.7) * mm});
            skLineSegment(sketch, "E12492", {"start": v(-59.75, -55.7) * mm, "end": v(-58.75, -55.98) * mm});
            skLineSegment(sketch, "E12493", {"start": v(-58.75, -55.98) * mm, "end": v(-57.83, -56.23) * mm});
            skLineSegment(sketch, "E12494", {"start": v(-57.83, -56.23) * mm, "end": v(-57, -56.44) * mm});
            skLineSegment(sketch, "E12495", {"start": v(-57, -56.44) * mm, "end": v(-56.78, -56.48) * mm});
            skLineSegment(sketch, "E12496", {"start": v(-56.78, -56.48) * mm, "end": v(-56.55, -56.52) * mm});
            skLineSegment(sketch, "E12497", {"start": v(-56.55, -56.52) * mm, "end": v(-56.05, -56.57) * mm});
            skLineSegment(sketch, "E12498", {"start": v(-56.05, -56.57) * mm, "end": v(-55.52, -56.6) * mm});
            skLineSegment(sketch, "E12499", {"start": v(-55.52, -56.6) * mm, "end": v(-55, -56.65) * mm});
            skLineSegment(sketch, "E12500", {"start": v(-55, -56.65) * mm, "end": v(-54.73, -56.69) * mm});
            skLineSegment(sketch, "E12501", {"start": v(-54.73, -56.69) * mm, "end": v(-54.48, -56.73) * mm});
            skLineSegment(sketch, "E12502", {"start": v(-54.48, -56.73) * mm, "end": v(-54.24, -56.78) * mm});
            skLineSegment(sketch, "E12503", {"start": v(-54.24, -56.78) * mm, "end": v(-54, -56.86) * mm});
            skLineSegment(sketch, "E12504", {"start": v(-54, -56.86) * mm, "end": v(-53.8, -56.94) * mm});
            skLineSegment(sketch, "E12505", {"start": v(-53.8, -56.94) * mm, "end": v(-53.6, -57.05) * mm});
            skLineSegment(sketch, "E12506", {"start": v(-53.6, -57.05) * mm, "end": v(-53.52, -57.11) * mm});
            skLineSegment(sketch, "E12507", {"start": v(-53.52, -57.11) * mm, "end": v(-53.43, -57.18) * mm});
            skLineSegment(sketch, "E12508", {"start": v(-53.43, -57.18) * mm, "end": v(-53.36, -57.26) * mm});
            skLineSegment(sketch, "E12509", {"start": v(-53.36, -57.26) * mm, "end": v(-53.29, -57.34) * mm});
            skLineSegment(sketch, "E12510", {"start": v(-53.29, -57.34) * mm, "end": v(-53.26, -57.38) * mm});
            skLineSegment(sketch, "E12511", {"start": v(-53.26, -57.38) * mm, "end": v(-53.25, -57.44) * mm});
            skLineSegment(sketch, "E12512", {"start": v(-53.25, -57.44) * mm, "end": v(-53.24, -57.56) * mm});
            skLineSegment(sketch, "E12513", {"start": v(-53.24, -57.56) * mm, "end": v(-53.26, -57.69) * mm});
            skLineSegment(sketch, "E12514", {"start": v(-53.26, -57.69) * mm, "end": v(-53.29, -57.8) * mm});
            skLineSegment(sketch, "E12515", {"start": v(-53.29, -57.8) * mm, "end": v(-53.36, -58.13) * mm});
            skLineSegment(sketch, "E12516", {"start": v(-53.36, -58.13) * mm, "end": v(-53.5, -58.69) * mm});
            skLineSegment(sketch, "E12517", {"start": v(-53.5, -58.69) * mm, "end": v(-53.7, -59.4) * mm});
            skLineSegment(sketch, "E12518", {"start": v(-53.7, -59.4) * mm, "end": v(-53.82, -59.77) * mm});
            skLineSegment(sketch, "E12519", {"start": v(-53.82, -59.77) * mm, "end": v(-53.95, -60.16) * mm});
            skLineSegment(sketch, "E12520", {"start": v(-53.95, -60.16) * mm, "end": v(-54.04, -60.38) * mm});
            skLineSegment(sketch, "E12521", {"start": v(-54.04, -60.38) * mm, "end": v(-54.16, -60.61) * mm});
            skLineSegment(sketch, "E12522", {"start": v(-54.16, -60.61) * mm, "end": v(-54.3, -60.86) * mm});
            skLineSegment(sketch, "E12523", {"start": v(-54.3, -60.86) * mm, "end": v(-54.42, -61.1) * mm});
            skLineSegment(sketch, "E12524", {"start": v(-54.42, -61.1) * mm, "end": v(-54.54, -61.35) * mm});
            skLineSegment(sketch, "E12525", {"start": v(-54.54, -61.35) * mm, "end": v(-54.58, -61.47) * mm});
            skLineSegment(sketch, "E12526", {"start": v(-54.58, -61.47) * mm, "end": v(-54.61, -61.6) * mm});
            skLineSegment(sketch, "E12527", {"start": v(-54.61, -61.6) * mm, "end": v(-54.64, -61.71) * mm});
            skLineSegment(sketch, "E12528", {"start": v(-54.64, -61.71) * mm, "end": v(-54.65, -61.83) * mm});
            skLineSegment(sketch, "E12529", {"start": v(-54.65, -61.83) * mm, "end": v(-54.64, -61.94) * mm});
            skLineSegment(sketch, "E12530", {"start": v(-54.64, -61.94) * mm, "end": v(-54.62, -62.05) * mm});
            skLineSegment(sketch, "E12531", {"start": v(-54.62, -62.05) * mm, "end": v(-54.59, -62.12) * mm});
            skLineSegment(sketch, "E12532", {"start": v(-54.59, -62.12) * mm, "end": v(-54.55, -62.19) * mm});
            skLineSegment(sketch, "E12533", {"start": v(-54.55, -62.19) * mm, "end": v(-54.45, -62.31) * mm});
            skLineSegment(sketch, "E12534", {"start": v(-54.45, -62.31) * mm, "end": v(-54.33, -62.43) * mm});
            skLineSegment(sketch, "E12535", {"start": v(-54.33, -62.43) * mm, "end": v(-54.18, -62.53) * mm});
            skLineSegment(sketch, "E12536", {"start": v(-54.18, -62.53) * mm, "end": v(-54.02, -62.62) * mm});
            skLineSegment(sketch, "E12537", {"start": v(-54.02, -62.62) * mm, "end": v(-53.86, -62.7) * mm});
            skLineSegment(sketch, "E12538", {"start": v(-53.86, -62.7) * mm, "end": v(-53.55, -62.83) * mm});
            skLineSegment(sketch, "E12539", {"start": v(-53.55, -62.83) * mm, "end": v(-53.32, -62.91) * mm});
            skLineSegment(sketch, "E12540", {"start": v(-53.32, -62.91) * mm, "end": v(-53.07, -62.99) * mm});
            skLineSegment(sketch, "E12541", {"start": v(-53.07, -62.99) * mm, "end": v(-52.8, -63.05) * mm});
            skLineSegment(sketch, "E12542", {"start": v(-52.8, -63.05) * mm, "end": v(-52.54, -63.1) * mm});
            skLineSegment(sketch, "E12543", {"start": v(-52.54, -63.1) * mm, "end": v(-52.26, -63.14) * mm});
            skLineSegment(sketch, "E12544", {"start": v(-52.26, -63.14) * mm, "end": v(-51.98, -63.18) * mm});
            skLineSegment(sketch, "E12545", {"start": v(-51.98, -63.18) * mm, "end": v(-51.4, -63.23) * mm});
            skLineSegment(sketch, "E12546", {"start": v(-51.4, -63.23) * mm, "end": v(-50.82, -63.26) * mm});
            skLineSegment(sketch, "E12547", {"start": v(-50.82, -63.26) * mm, "end": v(-50.25, -63.28) * mm});
            skLineSegment(sketch, "E12548", {"start": v(-50.25, -63.28) * mm, "end": v(-49.19, -63.3) * mm});
            skLineSegment(sketch, "E12549", {"start": v(-49.19, -63.3) * mm, "end": v(-48.4, -63.3) * mm});
            skLineSegment(sketch, "E12550", {"start": v(-48.4, -63.3) * mm, "end": v(-47.58, -63.29) * mm});
            skLineSegment(sketch, "E12551", {"start": v(-47.58, -63.29) * mm, "end": v(-46.72, -63.25) * mm});
            skLineSegment(sketch, "E12552", {"start": v(-46.72, -63.25) * mm, "end": v(-45.85, -63.2) * mm});
            skLineSegment(sketch, "E12553", {"start": v(-45.85, -63.2) * mm, "end": v(-44.97, -63.14) * mm});
            skLineSegment(sketch, "E12554", {"start": v(-44.97, -63.14) * mm, "end": v(-44.11, -63.06) * mm});
            skLineSegment(sketch, "E12555", {"start": v(-44.11, -63.06) * mm, "end": v(-43.3, -62.98) * mm});
            skLineSegment(sketch, "E12556", {"start": v(-43.3, -62.98) * mm, "end": v(-42.51, -62.89) * mm});
            skLineSegment(sketch, "E12557", {"start": v(-42.51, -62.89) * mm, "end": v(-41.98, -62.82) * mm});
            skLineSegment(sketch, "E12558", {"start": v(-41.98, -62.82) * mm, "end": v(-41.43, -62.73) * mm});
            skLineSegment(sketch, "E12559", {"start": v(-41.43, -62.73) * mm, "end": v(-40.3, -62.52) * mm});
            skLineSegment(sketch, "E12560", {"start": v(-40.3, -62.52) * mm, "end": v(-39.12, -62.28) * mm});
            skLineSegment(sketch, "E12561", {"start": v(-39.12, -62.28) * mm, "end": v(-37.92, -62.02) * mm});
            skLineSegment(sketch, "E12562", {"start": v(-37.92, -62.02) * mm, "end": v(-36.72, -61.77) * mm});
            skLineSegment(sketch, "E12563", {"start": v(-36.72, -61.77) * mm, "end": v(-35.54, -61.53) * mm});
            skLineSegment(sketch, "E12564", {"start": v(-35.54, -61.53) * mm, "end": v(-34.97, -61.42) * mm});
            skLineSegment(sketch, "E12565", {"start": v(-34.97, -61.42) * mm, "end": v(-34.4, -61.32) * mm});
            skLineSegment(sketch, "E12566", {"start": v(-34.4, -61.32) * mm, "end": v(-33.85, -61.24) * mm});
            skLineSegment(sketch, "E12567", {"start": v(-33.85, -61.24) * mm, "end": v(-33.32, -61.17) * mm});
            skLineSegment(sketch, "E12568", {"start": v(-33.32, -61.17) * mm, "end": v(-33.09, -61.12) * mm});
            skLineSegment(sketch, "E12569", {"start": v(-33.09, -61.12) * mm, "end": v(-32.82, -61.06) * mm});
            skLineSegment(sketch, "E12570", {"start": v(-32.82, -61.06) * mm, "end": v(-32.55, -61) * mm});
            skLineSegment(sketch, "E12571", {"start": v(-32.55, -61) * mm, "end": v(-32.27, -60.93) * mm});
            skLineSegment(sketch, "E12572", {"start": v(-32.27, -60.93) * mm, "end": v(-32, -60.9) * mm});
            skLineSegment(sketch, "E12573", {"start": v(-32, -60.9) * mm, "end": v(-31.87, -60.89) * mm});
            skLineSegment(sketch, "E12574", {"start": v(-31.87, -60.89) * mm, "end": v(-31.75, -60.9) * mm});
            skLineSegment(sketch, "E12575", {"start": v(-31.75, -60.9) * mm, "end": v(-31.63, -60.91) * mm});
            skLineSegment(sketch, "E12576", {"start": v(-31.63, -60.91) * mm, "end": v(-31.53, -60.94) * mm});
            skLineSegment(sketch, "E12577", {"start": v(-31.53, -60.94) * mm, "end": v(-31.43, -61) * mm});
            skLineSegment(sketch, "E12578", {"start": v(-31.43, -61) * mm, "end": v(-31.34, -61.06) * mm});
            skLineSegment(sketch, "E12579", {"start": v(-31.34, -61.06) * mm, "end": v(-31.28, -61.13) * mm});
            skLineSegment(sketch, "E12580", {"start": v(-31.28, -61.13) * mm, "end": v(-31.24, -61.2) * mm});
            skLineSegment(sketch, "E12581", {"start": v(-31.24, -61.2) * mm, "end": v(-31.21, -61.3) * mm});
            skLineSegment(sketch, "E12582", {"start": v(-31.21, -61.3) * mm, "end": v(-31.2, -61.4) * mm});
            skLineSegment(sketch, "E12583", {"start": v(-31.2, -61.4) * mm, "end": v(-31.2, -61.5) * mm});
            skLineSegment(sketch, "E12584", {"start": v(-31.2, -61.5) * mm, "end": v(-31.2, -61.6) * mm});
            skLineSegment(sketch, "E12585", {"start": v(-31.2, -61.6) * mm, "end": v(-31.22, -61.83) * mm});
            skLineSegment(sketch, "E12586", {"start": v(-31.22, -61.83) * mm, "end": v(-31.32, -62.3) * mm});
            skLineSegment(sketch, "E12587", {"start": v(-31.32, -62.3) * mm, "end": v(-31.36, -62.51) * mm});
            skLineSegment(sketch, "E12588", {"start": v(-31.36, -62.51) * mm, "end": v(-31.38, -62.71) * mm});
            skLineSegment(sketch, "E12589", {"start": v(-31.38, -62.71) * mm, "end": v(-31.39, -63.06) * mm});
            skLineSegment(sketch, "E12590", {"start": v(-31.39, -63.06) * mm, "end": v(-31.4, -63.4) * mm});
            skLineSegment(sketch, "E12591", {"start": v(-31.4, -63.4) * mm, "end": v(-31.44, -63.75) * mm});
            skLineSegment(sketch, "E12592", {"start": v(-31.44, -63.75) * mm, "end": v(-31.47, -64.08) * mm});
            skLineSegment(sketch, "E12593", {"start": v(-31.47, -64.08) * mm, "end": v(-31.51, -64.4) * mm});
            skLineSegment(sketch, "E12594", {"start": v(-31.51, -64.4) * mm, "end": v(-31.56, -64.67) * mm});
            skLineSegment(sketch, "E12595", {"start": v(-31.56, -64.67) * mm, "end": v(-31.6, -64.9) * mm});
            skLineSegment(sketch, "E12596", {"start": v(-31.6, -64.9) * mm, "end": v(-31.65, -65.07) * mm});
            skLineSegment(sketch, "E12597", {"start": v(-31.65, -65.07) * mm, "end": v(-31.74, -65.25) * mm});
            skLineSegment(sketch, "E12598", {"start": v(-31.74, -65.25) * mm, "end": v(-31.84, -65.43) * mm});
            skLineSegment(sketch, "E12599", {"start": v(-31.84, -65.43) * mm, "end": v(-31.89, -65.53) * mm});
            skLineSegment(sketch, "E12600", {"start": v(-31.89, -65.53) * mm, "end": v(-31.92, -65.62) * mm});
            skLineSegment(sketch, "E12601", {"start": v(-31.92, -65.62) * mm, "end": v(-31.92, -65.7) * mm});
            skLineSegment(sketch, "E12602", {"start": v(-31.92, -65.7) * mm, "end": v(-31.92, -65.75) * mm});
            skLineSegment(sketch, "E12603", {"start": v(-31.92, -65.75) * mm, "end": v(-31.9, -65.78) * mm});
            skLineSegment(sketch, "E12604", {"start": v(-31.9, -65.78) * mm, "end": v(-31.86, -65.84) * mm});
            skLineSegment(sketch, "E12605", {"start": v(-31.86, -65.84) * mm, "end": v(-31.8, -65.87) * mm});
            skLineSegment(sketch, "E12606", {"start": v(-31.8, -65.87) * mm, "end": v(-31.72, -65.9) * mm});
            skLineSegment(sketch, "E12607", {"start": v(-31.72, -65.9) * mm, "end": v(-31.63, -65.9) * mm});
            skLineSegment(sketch, "E12608", {"start": v(-31.63, -65.9) * mm, "end": v(-31.45, -65.92) * mm});
            skLineSegment(sketch, "E12609", {"start": v(-31.45, -65.92) * mm, "end": v(-31.37, -65.93) * mm});
            skLineSegment(sketch, "E12610", {"start": v(-31.37, -65.93) * mm, "end": v(-31.3, -65.94) * mm});
            skLineSegment(sketch, "E12611", {"start": v(-31.3, -65.94) * mm, "end": v(-31.13, -65.97) * mm});
            skLineSegment(sketch, "E12612", {"start": v(-31.13, -65.97) * mm, "end": v(-30.92, -66) * mm});
            skLineSegment(sketch, "E12613", {"start": v(-30.92, -66) * mm, "end": v(-30.34, -66.06) * mm});
            skLineSegment(sketch, "E12614", {"start": v(-30.34, -66.06) * mm, "end": v(-29.65, -66.1) * mm});
            skLineSegment(sketch, "E12615", {"start": v(-29.65, -66.1) * mm, "end": v(-28.92, -66.14) * mm});
            skLineSegment(sketch, "E12616", {"start": v(-28.92, -66.14) * mm, "end": v(-28.5, -66.16) * mm});
            skLineSegment(sketch, "E12617", {"start": v(-28.5, -66.16) * mm, "end": v(-28.03, -66.18) * mm});
            skLineSegment(sketch, "E12618", {"start": v(-28.03, -66.18) * mm, "end": v(-27.57, -66.2) * mm});
            skLineSegment(sketch, "E12619", {"start": v(-27.57, -66.2) * mm, "end": v(-27.35, -66.2) * mm});
            skLineSegment(sketch, "E12620", {"start": v(-27.35, -66.2) * mm, "end": v(-27.15, -66.18) * mm});
            skLineSegment(sketch, "E12621", {"start": v(-27.15, -66.18) * mm, "end": v(-26.9, -66.14) * mm});
            skLineSegment(sketch, "E12622", {"start": v(-26.9, -66.14) * mm, "end": v(-26.66, -66.09) * mm});
            skLineSegment(sketch, "E12623", {"start": v(-26.66, -66.09) * mm, "end": v(-26.14, -65.95) * mm});
            skLineSegment(sketch, "E12624", {"start": v(-26.14, -65.95) * mm, "end": v(-25.62, -65.8) * mm});
            skLineSegment(sketch, "E12625", {"start": v(-25.62, -65.8) * mm, "end": v(-25.14, -65.66) * mm});
            skLineSegment(sketch, "E12626", {"start": v(-25.14, -65.66) * mm, "end": v(-24.67, -65.52) * mm});
            skLineSegment(sketch, "E12627", {"start": v(-24.67, -65.52) * mm, "end": v(-24.11, -65.35) * mm});
            skLineSegment(sketch, "E12628", {"start": v(-24.11, -65.35) * mm, "end": v(-23.48, -65.14) * mm});
            skLineSegment(sketch, "E12629", {"start": v(-23.48, -65.14) * mm, "end": v(-22.8, -64.9) * mm});
            skLineSegment(sketch, "E12630", {"start": v(-22.8, -64.9) * mm, "end": v(-22.08, -64.64) * mm});
            skLineSegment(sketch, "E12631", {"start": v(-22.08, -64.64) * mm, "end": v(-21.36, -64.37) * mm});
            skLineSegment(sketch, "E12632", {"start": v(-21.36, -64.37) * mm, "end": v(-20.65, -64.1) * mm});
            skLineSegment(sketch, "E12633", {"start": v(-20.65, -64.1) * mm, "end": v(-19.98, -63.82) * mm});
            skLineSegment(sketch, "E12634", {"start": v(-19.98, -63.82) * mm, "end": v(-19.22, -63.52) * mm});
            skLineSegment(sketch, "E12635", {"start": v(-19.22, -63.52) * mm, "end": v(-18.4, -63.2) * mm});
            skLineSegment(sketch, "E12636", {"start": v(-18.4, -63.2) * mm, "end": v(-17.57, -62.85) * mm});
            skLineSegment(sketch, "E12637", {"start": v(-17.57, -62.85) * mm, "end": v(-17.18, -62.68) * mm});
            skLineSegment(sketch, "E12638", {"start": v(-17.18, -62.68) * mm, "end": v(-16.82, -62.51) * mm});
            skLineSegment(sketch, "E12639", {"start": v(-16.82, -62.51) * mm, "end": v(-15.95, -62.06) * mm});
            skLineSegment(sketch, "E12640", {"start": v(-15.95, -62.06) * mm, "end": v(-15.04, -61.56) * mm});
            skLineSegment(sketch, "E12641", {"start": v(-15.04, -61.56) * mm, "end": v(-14.1, -61.03) * mm});
            skLineSegment(sketch, "E12642", {"start": v(-14.1, -61.03) * mm, "end": v(-13.15, -60.47) * mm});
            skLineSegment(sketch, "E12643", {"start": v(-13.15, -60.47) * mm, "end": v(-11.29, -59.33) * mm});
            skLineSegment(sketch, "E12644", {"start": v(-11.29, -59.33) * mm, "end": v(-9.56, -58.27) * mm});
            skLineSegment(sketch, "E12645", {"start": v(-9.56, -58.27) * mm, "end": v(-9.1, -57.97) * mm});
            skLineSegment(sketch, "E12646", {"start": v(-9.1, -57.97) * mm, "end": v(-8.66, -57.67) * mm});
            skLineSegment(sketch, "E12647", {"start": v(-8.66, -57.67) * mm, "end": v(-9.78, -55.78) * mm});
            skLineSegment(sketch, "E12648", {"start": v(-9.78, -55.78) * mm, "end": v(-10.45, -56.45) * mm});
            skLineSegment(sketch, "E12649", {"start": v(-10.45, -56.45) * mm, "end": v(-11.18, -57.2) * mm});
            skLineSegment(sketch, "E12650", {"start": v(-11.18, -57.2) * mm, "end": v(-11.54, -57.56) * mm});
            skLineSegment(sketch, "E12651", {"start": v(-11.54, -57.56) * mm, "end": v(-11.92, -57.91) * mm});
            skLineSegment(sketch, "E12652", {"start": v(-11.92, -57.91) * mm, "end": v(-12.28, -58.24) * mm});
            skLineSegment(sketch, "E12653", {"start": v(-12.28, -58.24) * mm, "end": v(-12.65, -58.52) * mm});
            skLineSegment(sketch, "E12654", {"start": v(-12.65, -58.52) * mm, "end": v(-12.88, -58.68) * mm});
            skLineSegment(sketch, "E12655", {"start": v(-12.88, -58.68) * mm, "end": v(-13.13, -58.84) * mm});
            skLineSegment(sketch, "E12656", {"start": v(-13.13, -58.84) * mm, "end": v(-13.68, -59.14) * mm});
            skLineSegment(sketch, "E12657", {"start": v(-13.68, -59.14) * mm, "end": v(-14.23, -59.43) * mm});
            skLineSegment(sketch, "E12658", {"start": v(-14.23, -59.43) * mm, "end": v(-14.74, -59.7) * mm});
            skLineSegment(sketch, "E12659", {"start": v(-14.74, -59.7) * mm, "end": v(-15.43, -60.06) * mm});
            skLineSegment(sketch, "E12660", {"start": v(-15.43, -60.06) * mm, "end": v(-16.15, -60.43) * mm});
            skLineSegment(sketch, "E12661", {"start": v(-16.15, -60.43) * mm, "end": v(-16.92, -60.78) * mm});
            skLineSegment(sketch, "E12662", {"start": v(-16.92, -60.78) * mm, "end": v(-17.7, -61.13) * mm});
            skLineSegment(sketch, "E12663", {"start": v(-17.7, -61.13) * mm, "end": v(-18.53, -61.46) * mm});
            skLineSegment(sketch, "E12664", {"start": v(-18.53, -61.46) * mm, "end": v(-19.38, -61.79) * mm});
            skLineSegment(sketch, "E12665", {"start": v(-19.38, -61.79) * mm, "end": v(-20.24, -62.1) * mm});
            skLineSegment(sketch, "E12666", {"start": v(-20.24, -62.1) * mm, "end": v(-21.11, -62.4) * mm});
            skLineSegment(sketch, "E12667", {"start": v(-21.11, -62.4) * mm, "end": v(-22, -62.67) * mm});
            skLineSegment(sketch, "E12668", {"start": v(-22, -62.67) * mm, "end": v(-22.89, -62.93) * mm});
            skLineSegment(sketch, "E12669", {"start": v(-22.89, -62.93) * mm, "end": v(-23.78, -63.18) * mm});
            skLineSegment(sketch, "E12670", {"start": v(-23.78, -63.18) * mm, "end": v(-24.66, -63.4) * mm});
            skLineSegment(sketch, "E12671", {"start": v(-24.66, -63.4) * mm, "end": v(-25.53, -63.6) * mm});
            skLineSegment(sketch, "E12672", {"start": v(-25.53, -63.6) * mm, "end": v(-26.4, -63.77) * mm});
            skLineSegment(sketch, "E12673", {"start": v(-26.4, -63.77) * mm, "end": v(-27.23, -63.92) * mm});
            skLineSegment(sketch, "E12674", {"start": v(-27.23, -63.92) * mm, "end": v(-28.04, -64.04) * mm});
            skLineSegment(sketch, "E12675", {"start": v(-28.04, -64.04) * mm, "end": v(-29.7, -64.26) * mm});
            skLineSegment(sketch, "E12676", {"start": v(-29.7, -64.26) * mm, "end": v(-27.84, -62.44) * mm});
            skLineSegment(sketch, "E12677", {"start": v(-27.84, -62.44) * mm, "end": v(-27.4, -62) * mm});
            skLineSegment(sketch, "E12678", {"start": v(-27.4, -62) * mm, "end": v(-26.95, -61.52) * mm});
            skLineSegment(sketch, "E12679", {"start": v(-26.95, -61.52) * mm, "end": v(-26.48, -61) * mm});
            skLineSegment(sketch, "E12680", {"start": v(-26.48, -61) * mm, "end": v(-25.99, -60.44) * mm});
            skLineSegment(sketch, "E12681", {"start": v(-25.99, -60.44) * mm, "end": v(-25.49, -59.85) * mm});
            skLineSegment(sketch, "E12682", {"start": v(-25.49, -59.85) * mm, "end": v(-24.98, -59.25) * mm});
            skLineSegment(sketch, "E12683", {"start": v(-24.98, -59.25) * mm, "end": v(-24.47, -58.62) * mm});
            skLineSegment(sketch, "E12684", {"start": v(-24.47, -58.62) * mm, "end": v(-23.97, -57.98) * mm});
            skLineSegment(sketch, "E12685", {"start": v(-23.97, -57.98) * mm, "end": v(-23.47, -57.34) * mm});
            skLineSegment(sketch, "E12686", {"start": v(-23.47, -57.34) * mm, "end": v(-22.98, -56.7) * mm});
            skLineSegment(sketch, "E12687", {"start": v(-22.98, -56.7) * mm, "end": v(-22.5, -56.05) * mm});
            skLineSegment(sketch, "E12688", {"start": v(-22.5, -56.05) * mm, "end": v(-22.05, -55.42) * mm});
            skLineSegment(sketch, "E12689", {"start": v(-22.05, -55.42) * mm, "end": v(-21.62, -54.8) * mm});
            skLineSegment(sketch, "E12690", {"start": v(-21.62, -54.8) * mm, "end": v(-21.22, -54.2) * mm});
            skLineSegment(sketch, "E12691", {"start": v(-21.22, -54.2) * mm, "end": v(-20.85, -53.64) * mm});
            skLineSegment(sketch, "E12692", {"start": v(-20.85, -53.64) * mm, "end": v(-20.52, -53.1) * mm});
            skLineSegment(sketch, "E12693", {"start": v(-20.52, -53.1) * mm, "end": v(-20.21, -52.63) * mm});
            skLineSegment(sketch, "E12694", {"start": v(-20.21, -52.63) * mm, "end": v(-19.87, -52.12) * mm});
            skLineSegment(sketch, "E12695", {"start": v(-19.87, -52.12) * mm, "end": v(-19.7, -51.86) * mm});
            skLineSegment(sketch, "E12696", {"start": v(-19.7, -51.86) * mm, "end": v(-19.56, -51.6) * mm});
            skLineSegment(sketch, "E12697", {"start": v(-19.56, -51.6) * mm, "end": v(-19.42, -51.34) * mm});
            skLineSegment(sketch, "E12698", {"start": v(-19.42, -51.34) * mm, "end": v(-19.3, -51.1) * mm});
            skLineSegment(sketch, "E12699", {"start": v(-19.3, -51.1) * mm, "end": v(-19.21, -50.8) * mm});
            skLineSegment(sketch, "E12700", {"start": v(-19.21, -50.8) * mm, "end": v(-19.13, -50.5) * mm});
            skLineSegment(sketch, "E12701", {"start": v(-19.13, -50.5) * mm, "end": v(-19.06, -50.17) * mm});
            skLineSegment(sketch, "E12702", {"start": v(-19.06, -50.17) * mm, "end": v(-19, -49.84) * mm});
            skLineSegment(sketch, "E12703", {"start": v(-19, -49.84) * mm, "end": v(-18.9, -49.17) * mm});
            skLineSegment(sketch, "E12704", {"start": v(-18.9, -49.17) * mm, "end": v(-18.84, -48.85) * mm});
            skLineSegment(sketch, "E12705", {"start": v(-18.84, -48.85) * mm, "end": v(-18.78, -48.55) * mm});
            skLineSegment(sketch, "E12706", {"start": v(-18.78, -48.55) * mm, "end": v(-18.4, -48.58) * mm});
            skLineSegment(sketch, "E12707", {"start": v(-18.4, -48.58) * mm, "end": v(-18, -48.63) * mm});
            skLineSegment(sketch, "E12708", {"start": v(-18, -48.63) * mm, "end": v(-17.6, -48.7) * mm});
            skLineSegment(sketch, "E12709", {"start": v(-17.6, -48.7) * mm, "end": v(-17.16, -48.8) * mm});
            skLineSegment(sketch, "E12710", {"start": v(-17.16, -48.8) * mm, "end": v(-16.27, -49) * mm});
            skLineSegment(sketch, "E12711", {"start": v(-16.27, -49) * mm, "end": v(-15.81, -49.1) * mm});
            skLineSegment(sketch, "E12712", {"start": v(-15.81, -49.1) * mm, "end": v(-15.36, -49.18) * mm});
            skLineSegment(sketch, "E12713", {"start": v(-15.36, -49.18) * mm, "end": v(-14.92, -49.25) * mm});
            skLineSegment(sketch, "E12714", {"start": v(-14.92, -49.25) * mm, "end": v(-14.49, -49.3) * mm});
            skLineSegment(sketch, "E12715", {"start": v(-14.49, -49.3) * mm, "end": v(-14.28, -49.3) * mm});
            skLineSegment(sketch, "E12716", {"start": v(-14.28, -49.3) * mm, "end": v(-14.07, -49.31) * mm});
            skLineSegment(sketch, "E12717", {"start": v(-14.07, -49.31) * mm, "end": v(-13.87, -49.3) * mm});
            skLineSegment(sketch, "E12718", {"start": v(-13.87, -49.3) * mm, "end": v(-13.67, -49.3) * mm});
            skLineSegment(sketch, "E12719", {"start": v(-13.67, -49.3) * mm, "end": v(-13.48, -49.27) * mm});
            skLineSegment(sketch, "E12720", {"start": v(-13.48, -49.27) * mm, "end": v(-13.3, -49.23) * mm});
            skLineSegment(sketch, "E12721", {"start": v(-13.3, -49.23) * mm, "end": v(-13.13, -49.19) * mm});
            skLineSegment(sketch, "E12722", {"start": v(-13.13, -49.19) * mm, "end": v(-12.96, -49.13) * mm});
            skLineSegment(sketch, "E12723", {"start": v(-12.96, -49.13) * mm, "end": v(-12.8, -49.05) * mm});
            skLineSegment(sketch, "E12724", {"start": v(-12.8, -49.05) * mm, "end": v(-12.64, -48.96) * mm});
            skLineSegment(sketch, "E12725", {"start": v(-12.64, -48.96) * mm, "end": v(-12.5, -48.86) * mm});
            skLineSegment(sketch, "E12726", {"start": v(-12.5, -48.86) * mm, "end": v(-12.37, -48.74) * mm});
            skLineSegment(sketch, "E12727", {"start": v(-12.37, -48.74) * mm, "end": v(-12.34, -48.7) * mm});
            skLineSegment(sketch, "E12728", {"start": v(-12.34, -48.7) * mm, "end": v(-12.33, -48.65) * mm});
            skLineSegment(sketch, "E12729", {"start": v(-12.33, -48.65) * mm, "end": v(-12.34, -48.53) * mm});
            skLineSegment(sketch, "E12730", {"start": v(-12.34, -48.53) * mm, "end": v(-12.37, -48.41) * mm});
            skLineSegment(sketch, "E12731", {"start": v(-12.37, -48.41) * mm, "end": v(-12.38, -48.3) * mm});
            skLineSegment(sketch, "E12732", {"start": v(-12.38, -48.3) * mm, "end": v(-12.4, -48.18) * mm});
            skLineSegment(sketch, "E12733", {"start": v(-12.4, -48.18) * mm, "end": v(-12.42, -47.99) * mm});
            skLineSegment(sketch, "E12734", {"start": v(-12.42, -47.99) * mm, "end": v(-12.52, -47.46) * mm});
            skLineSegment(sketch, "E12735", {"start": v(-12.52, -47.46) * mm, "end": v(-12.66, -46.79) * mm});
            skLineSegment(sketch, "E12736", {"start": v(-12.66, -46.79) * mm, "end": v(-12.82, -46.05) * mm});
            skLineSegment(sketch, "E12737", {"start": v(-12.82, -46.05) * mm, "end": v(-13.24, -44.23) * mm});
            skLineSegment(sketch, "E12738", {"start": v(-13.24, -44.23) * mm, "end": v(-19.2, -44.04) * mm});
            skLineSegment(sketch, "E12739", {"start": v(-19.2, -44.04) * mm, "end": v(-21.63, -42.02) * mm});
            skLineSegment(sketch, "E12740", {"start": v(-21.63, -42.02) * mm, "end": v(-27.55, -42) * mm});
            skLineSegment(sketch, "E12741", {"start": v(-27.55, -42) * mm, "end": v(-27.55, -42.26) * mm});
            skLineSegment(sketch, "E12742", {"start": v(-27.55, -42.26) * mm, "end": v(-27.54, -42.37) * mm});
            skLineSegment(sketch, "E12743", {"start": v(-27.54, -42.37) * mm, "end": v(-27.52, -42.5) * mm});
            skLineSegment(sketch, "E12744", {"start": v(-27.52, -42.5) * mm, "end": v(-27.48, -42.64) * mm});
            skLineSegment(sketch, "E12745", {"start": v(-27.48, -42.64) * mm, "end": v(-27.43, -42.8) * mm});
            skLineSegment(sketch, "E12746", {"start": v(-27.43, -42.8) * mm, "end": v(-27.37, -42.95) * mm});
            skLineSegment(sketch, "E12747", {"start": v(-27.37, -42.95) * mm, "end": v(-27.3, -43.1) * mm});
            skLineSegment(sketch, "E12748", {"start": v(-27.3, -43.1) * mm, "end": v(-27.23, -43.26) * mm});
            skLineSegment(sketch, "E12749", {"start": v(-27.23, -43.26) * mm, "end": v(-27.15, -43.4) * mm});
            skLineSegment(sketch, "E12750", {"start": v(-27.15, -43.4) * mm, "end": v(-26.75, -44.04) * mm});
            skLineSegment(sketch, "E12751", {"start": v(-26.75, -44.04) * mm, "end": v(-26.55, -46.07) * mm});
            skLineSegment(sketch, "E12752", {"start": v(-26.55, -46.07) * mm, "end": v(-26.77, -46.01) * mm});
            skLineSegment(sketch, "E12753", {"start": v(-26.77, -46.01) * mm, "end": v(-27.02, -45.97) * mm});
            skLineSegment(sketch, "E12754", {"start": v(-27.02, -45.97) * mm, "end": v(-27.57, -45.88) * mm});
            skLineSegment(sketch, "E12755", {"start": v(-27.57, -45.88) * mm, "end": v(-28.12, -45.8) * mm});
            skLineSegment(sketch, "E12756", {"start": v(-28.12, -45.8) * mm, "end": v(-28.37, -45.76) * mm});
            skLineSegment(sketch, "E12757", {"start": v(-28.37, -45.76) * mm, "end": v(-28.58, -45.7) * mm});
            skLineSegment(sketch, "E12758", {"start": v(-28.58, -45.7) * mm, "end": v(-29.04, -45.58) * mm});
            skLineSegment(sketch, "E12759", {"start": v(-29.04, -45.58) * mm, "end": v(-29.53, -45.47) * mm});
            skLineSegment(sketch, "E12760", {"start": v(-29.53, -45.47) * mm, "end": v(-30.04, -45.36) * mm});
            skLineSegment(sketch, "E12761", {"start": v(-30.04, -45.36) * mm, "end": v(-30.57, -45.25) * mm});
            skLineSegment(sketch, "E12762", {"start": v(-30.57, -45.25) * mm, "end": v(-31.14, -45.16) * mm});
            skLineSegment(sketch, "E12763", {"start": v(-31.14, -45.16) * mm, "end": v(-31.72, -45.07) * mm});
            skLineSegment(sketch, "E12764", {"start": v(-31.72, -45.07) * mm, "end": v(-32.33, -44.98) * mm});
            skLineSegment(sketch, "E12765", {"start": v(-32.33, -44.98) * mm, "end": v(-32.96, -44.9) * mm});
            skLineSegment(sketch, "E12766", {"start": v(-32.96, -44.9) * mm, "end": v(-34.3, -44.75) * mm});
            skLineSegment(sketch, "E12767", {"start": v(-34.3, -44.75) * mm, "end": v(-35.7, -44.62) * mm});
            skLineSegment(sketch, "E12768", {"start": v(-35.7, -44.62) * mm, "end": v(-37.2, -44.5) * mm});
            skLineSegment(sketch, "E12769", {"start": v(-37.2, -44.5) * mm, "end": v(-38.75, -44.4) * mm});
            skLineSegment(sketch, "E12770", {"start": v(-38.75, -44.4) * mm, "end": v(-41.22, -44.2) * mm});
            skLineSegment(sketch, "E12771", {"start": v(-41.22, -44.2) * mm, "end": v(-42.62, -44.08) * mm});
            skLineSegment(sketch, "E12772", {"start": v(-42.62, -44.08) * mm, "end": v(-43.68, -44) * mm});
            skLineSegment(sketch, "E12773", {"start": v(-43.68, -44) * mm, "end": v(-46.5, -46.47) * mm});
            skLineSegment(sketch, "E12774", {"start": v(-46.5, -46.47) * mm, "end": v(-47.4, -46.47) * mm});
            skLineSegment(sketch, "E12775", {"start": v(-47.4, -46.47) * mm, "end": v(-47.46, -46.47) * mm});
            skLineSegment(sketch, "E12776", {"start": v(-47.46, -46.47) * mm, "end": v(-47.51, -46.49) * mm});
            skLineSegment(sketch, "E12777", {"start": v(-47.51, -46.49) * mm, "end": v(-47.56, -46.5) * mm});
            skLineSegment(sketch, "E12778", {"start": v(-47.56, -46.5) * mm, "end": v(-47.6, -46.53) * mm});
            skLineSegment(sketch, "E12779", {"start": v(-47.6, -46.53) * mm, "end": v(-47.62, -46.57) * mm});
            skLineSegment(sketch, "E12780", {"start": v(-47.62, -46.57) * mm, "end": v(-47.63, -46.62) * mm});
            skLineSegment(sketch, "E12781", {"start": v(-47.63, -46.62) * mm, "end": v(-47.65, -46.67) * mm});
            skLineSegment(sketch, "E12782", {"start": v(-47.65, -46.67) * mm, "end": v(-47.65, -46.74) * mm});
            skLineSegment(sketch, "E12783", {"start": v(-47.65, -46.74) * mm, "end": v(-47.68, -47.04) * mm});
            skLineSegment(sketch, "E12784", {"start": v(-47.68, -47.04) * mm, "end": v(-47.26, -47.04) * mm});
            skLineSegment(sketch, "E12785", {"start": v(-47.26, -47.04) * mm, "end": v(-47.15, -47.06) * mm});
            skLineSegment(sketch, "E12786", {"start": v(-47.15, -47.06) * mm, "end": v(-46.97, -47.1) * mm});
            skLineSegment(sketch, "E12787", {"start": v(-46.97, -47.1) * mm, "end": v(-46.74, -47.18) * mm});
            skLineSegment(sketch, "E12788", {"start": v(-46.74, -47.18) * mm, "end": v(-46.46, -47.28) * mm});
            skLineSegment(sketch, "E12789", {"start": v(-46.46, -47.28) * mm, "end": v(-45.82, -47.54) * mm});
            skLineSegment(sketch, "E12790", {"start": v(-45.82, -47.54) * mm, "end": v(-45.12, -47.85) * mm});
            skLineSegment(sketch, "E12791", {"start": v(-45.12, -47.85) * mm, "end": v(-43.39, -48.66) * mm});
            skLineSegment(sketch, "E12792", {"start": v(-43.39, -48.66) * mm, "end": v(-43.39, -49) * mm});
            skLineSegment(sketch, "E12793", {"start": v(-43.39, -49) * mm, "end": v(-43.4, -49.04) * mm});
            skLineSegment(sketch, "E12794", {"start": v(-43.4, -49.04) * mm, "end": v(-43.42, -49.1) * mm});
            skLineSegment(sketch, "E12795", {"start": v(-43.42, -49.1) * mm, "end": v(-43.53, -49.27) * mm});
            skLineSegment(sketch, "E12796", {"start": v(-43.53, -49.27) * mm, "end": v(-43.7, -49.5) * mm});
            skLineSegment(sketch, "E12797", {"start": v(-43.7, -49.5) * mm, "end": v(-43.92, -49.77) * mm});
            skLineSegment(sketch, "E12798", {"start": v(-43.92, -49.77) * mm, "end": v(-44.19, -50.08) * mm});
            skLineSegment(sketch, "E12799", {"start": v(-44.19, -50.08) * mm, "end": v(-44.5, -50.42) * mm});
            skLineSegment(sketch, "E12800", {"start": v(-44.5, -50.42) * mm, "end": v(-44.84, -50.78) * mm});
            skLineSegment(sketch, "E12801", {"start": v(-44.84, -50.78) * mm, "end": v(-45.2, -51.15) * mm});
            skLineSegment(sketch, "E12802", {"start": v(-45.2, -51.15) * mm, "end": v(-45.63, -51.6) * mm});
            skLineSegment(sketch, "E12803", {"start": v(-45.63, -51.6) * mm, "end": v(-46.08, -52.1) * mm});
            skLineSegment(sketch, "E12804", {"start": v(-46.08, -52.1) * mm, "end": v(-46.31, -52.33) * mm});
            skLineSegment(sketch, "E12805", {"start": v(-46.31, -52.33) * mm, "end": v(-46.55, -52.57) * mm});
            skLineSegment(sketch, "E12806", {"start": v(-46.55, -52.57) * mm, "end": v(-46.78, -52.78) * mm});
            skLineSegment(sketch, "E12807", {"start": v(-46.78, -52.78) * mm, "end": v(-47.02, -52.96) * mm});
            skLineSegment(sketch, "E12808", {"start": v(-47.02, -52.96) * mm, "end": v(-47.29, -53.15) * mm});
            skLineSegment(sketch, "E12809", {"start": v(-47.29, -53.15) * mm, "end": v(-47.58, -53.33) * mm});
            skLineSegment(sketch, "E12810", {"start": v(-47.58, -53.33) * mm, "end": v(-47.9, -53.52) * mm});
            skLineSegment(sketch, "E12811", {"start": v(-47.9, -53.52) * mm, "end": v(-48.21, -53.69) * mm});
            skLineSegment(sketch, "E12812", {"start": v(-48.21, -53.69) * mm, "end": v(-48.54, -53.85) * mm});
            skLineSegment(sketch, "E12813", {"start": v(-48.54, -53.85) * mm, "end": v(-48.87, -54) * mm});
            skLineSegment(sketch, "E12814", {"start": v(-48.87, -54) * mm, "end": v(-49.2, -54.12) * mm});
            skLineSegment(sketch, "E12815", {"start": v(-49.2, -54.12) * mm, "end": v(-49.5, -54.23) * mm});
            skLineSegment(sketch, "E12816", {"start": v(-49.5, -54.23) * mm, "end": v(-49.91, -54.34) * mm});
            skLineSegment(sketch, "E12817", {"start": v(-49.91, -54.34) * mm, "end": v(-50.35, -54.43) * mm});
            skLineSegment(sketch, "E12818", {"start": v(-50.35, -54.43) * mm, "end": v(-50.82, -54.51) * mm});
            skLineSegment(sketch, "E12819", {"start": v(-50.82, -54.51) * mm, "end": v(-51.3, -54.57) * mm});
            skLineSegment(sketch, "E12820", {"start": v(-51.3, -54.57) * mm, "end": v(-51.77, -54.62) * mm});
            skLineSegment(sketch, "E12821", {"start": v(-51.77, -54.62) * mm, "end": v(-52.24, -54.65) * mm});
            skLineSegment(sketch, "E12822", {"start": v(-52.24, -54.65) * mm, "end": v(-52.7, -54.67) * mm});
            skLineSegment(sketch, "E12823", {"start": v(-52.7, -54.67) * mm, "end": v(-53.12, -54.68) * mm});
            skLineSegment(sketch, "E12824", {"start": v(-53.12, -54.68) * mm, "end": v(-53.52, -54.68) * mm});
            skLineSegment(sketch, "E12825", {"start": v(-53.52, -54.68) * mm, "end": v(-53.93, -54.67) * mm});
            skLineSegment(sketch, "E12826", {"start": v(-53.93, -54.67) * mm, "end": v(-54.78, -54.62) * mm});
            skLineSegment(sketch, "E12827", {"start": v(-54.78, -54.62) * mm, "end": v(-55.66, -54.54) * mm});
            skLineSegment(sketch, "E12828", {"start": v(-55.66, -54.54) * mm, "end": v(-56.56, -54.45) * mm});
            skLineSegment(sketch, "E12829", {"start": v(-56.56, -54.45) * mm, "end": v(-57.45, -54.33) * mm});
            skLineSegment(sketch, "E12830", {"start": v(-57.45, -54.33) * mm, "end": v(-58.33, -54.2) * mm});
            skLineSegment(sketch, "E12831", {"start": v(-58.33, -54.2) * mm, "end": v(-59.17, -54.06) * mm});
            skLineSegment(sketch, "E12832", {"start": v(-59.17, -54.06) * mm, "end": v(-59.97, -53.92) * mm});
            skLineSegment(sketch, "E12833", {"start": v(-59.97, -53.92) * mm, "end": v(-60.69, -53.79) * mm});
            skLineSegment(sketch, "E12834", {"start": v(-60.69, -53.79) * mm, "end": v(-61.45, -53.63) * mm});
            skLineSegment(sketch, "E12835", {"start": v(-61.45, -53.63) * mm, "end": v(-62.24, -53.46) * mm});
            skLineSegment(sketch, "E12836", {"start": v(-62.24, -53.46) * mm, "end": v(-63.04, -53.27) * mm});
            skLineSegment(sketch, "E12837", {"start": v(-63.04, -53.27) * mm, "end": v(-63.83, -53.07) * mm});
            skLineSegment(sketch, "E12838", {"start": v(-63.83, -53.07) * mm, "end": v(-64.6, -52.85) * mm});
            skLineSegment(sketch, "E12839", {"start": v(-64.6, -52.85) * mm, "end": v(-65.35, -52.63) * mm});
            skLineSegment(sketch, "E12840", {"start": v(-65.35, -52.63) * mm, "end": v(-66.04, -52.38) * mm});
            skLineSegment(sketch, "E12841", {"start": v(-66.04, -52.38) * mm, "end": v(-66.33, -52.26) * mm});
            skLineSegment(sketch, "E12842", {"start": v(-66.33, -52.26) * mm, "end": v(-66.64, -52.12) * mm});
            skLineSegment(sketch, "E12843", {"start": v(-66.64, -52.12) * mm, "end": v(-67.28, -51.8) * mm});
            skLineSegment(sketch, "E12844", {"start": v(-67.28, -51.8) * mm, "end": v(-67.9, -51.46) * mm});
            skLineSegment(sketch, "E12845", {"start": v(-67.9, -51.46) * mm, "end": v(-68.49, -51.15) * mm});
            skLineSegment(sketch, "E12846", {"start": v(-68.49, -51.15) * mm, "end": v(-69.48, -50.65) * mm});
            skLineSegment(sketch, "E12847", {"start": v(-69.48, -50.65) * mm, "end": v(-70.34, -50.18) * mm});
            skLineSegment(sketch, "E12848", {"start": v(-70.34, -50.18) * mm, "end": v(-71.07, -49.76) * mm});
            skLineSegment(sketch, "E12849", {"start": v(-71.07, -49.76) * mm, "end": v(-71.39, -49.57) * mm});
            skLineSegment(sketch, "E12850", {"start": v(-71.39, -49.57) * mm, "end": v(-71.67, -49.38) * mm});
            skLineSegment(sketch, "E12851", {"start": v(-71.67, -49.38) * mm, "end": v(-71.92, -49.21) * mm});
            skLineSegment(sketch, "E12852", {"start": v(-71.92, -49.21) * mm, "end": v(-72.14, -49.05) * mm});
            skLineSegment(sketch, "E12853", {"start": v(-72.14, -49.05) * mm, "end": v(-72.33, -48.9) * mm});
            skLineSegment(sketch, "E12854", {"start": v(-72.33, -48.9) * mm, "end": v(-72.48, -48.76) * mm});
            skLineSegment(sketch, "E12855", {"start": v(-72.48, -48.76) * mm, "end": v(-72.6, -48.64) * mm});
            skLineSegment(sketch, "E12856", {"start": v(-72.6, -48.64) * mm, "end": v(-72.69, -48.53) * mm});
            skLineSegment(sketch, "E12857", {"start": v(-72.69, -48.53) * mm, "end": v(-72.74, -48.42) * mm});
            skLineSegment(sketch, "E12858", {"start": v(-72.74, -48.42) * mm, "end": v(-72.75, -48.38) * mm});
            skLineSegment(sketch, "E12859", {"start": v(-72.75, -48.38) * mm, "end": v(-72.76, -48.33) * mm});
            skLineSegment(sketch, "E12860", {"start": v(-72.76, -48.33) * mm, "end": v(-72.76, -48.03) * mm});
            skLineSegment(sketch, "E12861", {"start": v(-72.76, -48.03) * mm, "end": v(-71.89, -48.03) * mm});
            skLineSegment(sketch, "E12862", {"start": v(-71.89, -48.03) * mm, "end": v(-71.63, -48) * mm});
            skLineSegment(sketch, "E12863", {"start": v(-71.63, -48) * mm, "end": v(-71.25, -47.96) * mm});
            skLineSegment(sketch, "E12864", {"start": v(-71.25, -47.96) * mm, "end": v(-70.75, -47.88) * mm});
            skLineSegment(sketch, "E12865", {"start": v(-70.75, -47.88) * mm, "end": v(-70.15, -47.77) * mm});
            skLineSegment(sketch, "E12866", {"start": v(-70.15, -47.77) * mm, "end": v(-68.74, -47.5) * mm});
            skLineSegment(sketch, "E12867", {"start": v(-68.74, -47.5) * mm, "end": v(-67.19, -47.17) * mm});
            skLineSegment(sketch, "E12868", {"start": v(-67.19, -47.17) * mm, "end": v(-66.26, -46.97) * mm});
            skLineSegment(sketch, "E12869", {"start": v(-66.26, -46.97) * mm, "end": v(-65.26, -46.77) * mm});
            skLineSegment(sketch, "E12870", {"start": v(-65.26, -46.77) * mm, "end": v(-64.76, -46.67) * mm});
            skLineSegment(sketch, "E12871", {"start": v(-64.76, -46.67) * mm, "end": v(-64.26, -46.56) * mm});
            skLineSegment(sketch, "E12872", {"start": v(-64.26, -46.56) * mm, "end": v(-63.8, -46.44) * mm});
            skLineSegment(sketch, "E12873", {"start": v(-63.8, -46.44) * mm, "end": v(-63.35, -46.3) * mm});
            skLineSegment(sketch, "E12874", {"start": v(-63.35, -46.3) * mm, "end": v(-63.12, -46.23) * mm});
            skLineSegment(sketch, "E12875", {"start": v(-63.12, -46.23) * mm, "end": v(-62.89, -46.14) * mm});
            skLineSegment(sketch, "E12876", {"start": v(-62.89, -46.14) * mm, "end": v(-62.4, -45.94) * mm});
            skLineSegment(sketch, "E12877", {"start": v(-62.4, -45.94) * mm, "end": v(-61.9, -45.73) * mm});
            skLineSegment(sketch, "E12878", {"start": v(-61.9, -45.73) * mm, "end": v(-61.45, -45.53) * mm});
            skLineSegment(sketch, "E12879", {"start": v(-61.45, -45.53) * mm, "end": v(-61.91, -45.4) * mm});
            skLineSegment(sketch, "E12880", {"start": v(-61.91, -45.4) * mm, "end": v(-62.4, -45.28) * mm});
            skLineSegment(sketch, "E12881", {"start": v(-62.4, -45.28) * mm, "end": v(-62.9, -45.16) * mm});
            skLineSegment(sketch, "E12882", {"start": v(-62.9, -45.16) * mm, "end": v(-63.36, -45.03) * mm});
            skLineSegment(sketch, "E12883", {"start": v(-63.36, -45.03) * mm, "end": v(-65.72, -44.32) * mm});
            skLineSegment(sketch, "E12884", {"start": v(-65.72, -44.32) * mm, "end": v(-67.19, -43.87) * mm});
            skLineSegment(sketch, "E12885", {"start": v(-67.19, -43.87) * mm, "end": v(-68.6, -43.43) * mm});
            skLineSegment(sketch, "E12886", {"start": v(-68.6, -43.43) * mm, "end": v(-68.98, -43.33) * mm});
            skLineSegment(sketch, "E12887", {"start": v(-68.98, -43.33) * mm, "end": v(-69.38, -43.22) * mm});
            skLineSegment(sketch, "E12888", {"start": v(-69.38, -43.22) * mm, "end": v(-69.8, -43.12) * mm});
            skLineSegment(sketch, "E12889", {"start": v(-69.8, -43.12) * mm, "end": v(-70.23, -43) * mm});
            skLineSegment(sketch, "E12890", {"start": v(-70.23, -43) * mm, "end": v(-70.65, -42.88) * mm});
            skLineSegment(sketch, "E12891", {"start": v(-70.65, -42.88) * mm, "end": v(-70.85, -42.8) * mm});
            skLineSegment(sketch, "E12892", {"start": v(-70.85, -42.8) * mm, "end": v(-71.05, -42.73) * mm});
            skLineSegment(sketch, "E12893", {"start": v(-71.05, -42.73) * mm, "end": v(-71.24, -42.64) * mm});
            skLineSegment(sketch, "E12894", {"start": v(-71.24, -42.64) * mm, "end": v(-71.43, -42.55) * mm});
            skLineSegment(sketch, "E12895", {"start": v(-71.43, -42.55) * mm, "end": v(-71.6, -42.44) * mm});
            skLineSegment(sketch, "E12896", {"start": v(-71.6, -42.44) * mm, "end": v(-71.77, -42.33) * mm});
            skLineSegment(sketch, "E12897", {"start": v(-71.77, -42.33) * mm, "end": v(-71.8, -42.3) * mm});
            skLineSegment(sketch, "E12898", {"start": v(-71.8, -42.3) * mm, "end": v(-71.82, -42.26) * mm});
            skLineSegment(sketch, "E12899", {"start": v(-71.82, -42.26) * mm, "end": v(-71.83, -42.21) * mm});
            skLineSegment(sketch, "E12900", {"start": v(-71.83, -42.21) * mm, "end": v(-71.83, -42.16) * mm});
            skLineSegment(sketch, "E12901", {"start": v(-71.83, -42.16) * mm, "end": v(-71.81, -42.05) * mm});
            skLineSegment(sketch, "E12902", {"start": v(-71.81, -42.05) * mm, "end": v(-71.78, -41.93) * mm});
            skLineSegment(sketch, "E12903", {"start": v(-71.78, -41.93) * mm, "end": v(-71.75, -41.8) * mm});
            skLineSegment(sketch, "E12904", {"start": v(-71.75, -41.8) * mm, "end": v(-71.73, -41.69) * mm});
            skLineSegment(sketch, "E12905", {"start": v(-71.73, -41.69) * mm, "end": v(-71.72, -41.64) * mm});
            skLineSegment(sketch, "E12906", {"start": v(-71.72, -41.64) * mm, "end": v(-71.73, -41.58) * mm});
            skLineSegment(sketch, "E12907", {"start": v(-71.73, -41.58) * mm, "end": v(-71.74, -41.54) * mm});
            skLineSegment(sketch, "E12908", {"start": v(-71.74, -41.54) * mm, "end": v(-71.77, -41.5) * mm});
            skLineSegment(sketch, "E12909", {"start": v(-71.77, -41.5) * mm, "end": v(-71.8, -41.46) * mm});
            skLineSegment(sketch, "E12910", {"start": v(-71.8, -41.46) * mm, "end": v(-71.86, -41.42) * mm});
            skLineSegment(sketch, "E12911", {"start": v(-71.86, -41.42) * mm, "end": v(-71.98, -41.37) * mm});
            skLineSegment(sketch, "E12912", {"start": v(-71.98, -41.37) * mm, "end": v(-72.12, -41.34) * mm});
            skLineSegment(sketch, "E12913", {"start": v(-72.12, -41.34) * mm, "end": v(-72.27, -41.33) * mm});
            skLineSegment(sketch, "E12914", {"start": v(-72.27, -41.33) * mm, "end": v(-72.57, -41.32) * mm});
            skLineSegment(sketch, "E12915", {"start": v(-72.57, -41.32) * mm, "end": v(-72.72, -41.31) * mm});
            skLineSegment(sketch, "E12916", {"start": v(-72.72, -41.31) * mm, "end": v(-72.85, -41.3) * mm});
            skLineSegment(sketch, "E12917", {"start": v(-72.85, -41.3) * mm, "end": v(-73.12, -41.23) * mm});
            skLineSegment(sketch, "E12918", {"start": v(-73.12, -41.23) * mm, "end": v(-73.46, -41.13) * mm});
            skLineSegment(sketch, "E12919", {"start": v(-73.46, -41.13) * mm, "end": v(-73.87, -40.99) * mm});
            skLineSegment(sketch, "E12920", {"start": v(-73.87, -40.99) * mm, "end": v(-74.32, -40.82) * mm});
            skLineSegment(sketch, "E12921", {"start": v(-74.32, -40.82) * mm, "end": v(-74.8, -40.62) * mm});
            skLineSegment(sketch, "E12922", {"start": v(-74.8, -40.62) * mm, "end": v(-75.32, -40.4) * mm});
            skLineSegment(sketch, "E12923", {"start": v(-75.32, -40.4) * mm, "end": v(-75.83, -40.18) * mm});
            skLineSegment(sketch, "E12924", {"start": v(-75.83, -40.18) * mm, "end": v(-76.33, -39.95) * mm});
            skLineSegment(sketch, "E12925", {"start": v(-76.33, -39.95) * mm, "end": v(-76.92, -39.69) * mm});
            skLineSegment(sketch, "E12926", {"start": v(-76.92, -39.69) * mm, "end": v(-77.56, -39.41) * mm});
            skLineSegment(sketch, "E12927", {"start": v(-77.56, -39.41) * mm, "end": v(-77.87, -39.27) * mm});
            skLineSegment(sketch, "E12928", {"start": v(-77.87, -39.27) * mm, "end": v(-78.18, -39.12) * mm});
            skLineSegment(sketch, "E12929", {"start": v(-78.18, -39.12) * mm, "end": v(-78.47, -38.96) * mm});
            skLineSegment(sketch, "E12930", {"start": v(-78.47, -38.96) * mm, "end": v(-78.73, -38.8) * mm});
            skLineSegment(sketch, "E12931", {"start": v(-78.73, -38.8) * mm, "end": v(-78.96, -38.63) * mm});
            skLineSegment(sketch, "E12932", {"start": v(-78.96, -38.63) * mm, "end": v(-79.2, -38.45) * mm});
            skLineSegment(sketch, "E12933", {"start": v(-79.2, -38.45) * mm, "end": v(-79.67, -38.05) * mm});
            skLineSegment(sketch, "E12934", {"start": v(-79.67, -38.05) * mm, "end": v(-80.15, -37.62) * mm});
            skLineSegment(sketch, "E12935", {"start": v(-80.15, -37.62) * mm, "end": v(-80.62, -37.16) * mm});
            skLineSegment(sketch, "E12936", {"start": v(-80.62, -37.16) * mm, "end": v(-81.07, -36.7) * mm});
            skLineSegment(sketch, "E12937", {"start": v(-81.07, -36.7) * mm, "end": v(-81.5, -36.21) * mm});
            skLineSegment(sketch, "E12938", {"start": v(-81.5, -36.21) * mm, "end": v(-81.9, -35.74) * mm});
            skLineSegment(sketch, "E12939", {"start": v(-81.9, -35.74) * mm, "end": v(-82.25, -35.27) * mm});
            skLineSegment(sketch, "E12940", {"start": v(-82.25, -35.27) * mm, "end": v(-82.45, -34.97) * mm});
            skLineSegment(sketch, "E12941", {"start": v(-82.45, -34.97) * mm, "end": v(-82.64, -34.64) * mm});
            skLineSegment(sketch, "E12942", {"start": v(-82.64, -34.64) * mm, "end": v(-82.83, -34.29) * mm});
            skLineSegment(sketch, "E12943", {"start": v(-82.83, -34.29) * mm, "end": v(-83, -33.92) * mm});
            skLineSegment(sketch, "E12944", {"start": v(-83, -33.92) * mm, "end": v(-83.34, -33.2) * mm});
            skLineSegment(sketch, "E12945", {"start": v(-83.34, -33.2) * mm, "end": v(-83.5, -32.84) * mm});
            skLineSegment(sketch, "E12946", {"start": v(-83.5, -32.84) * mm, "end": v(-83.66, -32.52) * mm});
            skLineSegment(sketch, "E12947", {"start": v(-83.66, -32.52) * mm, "end": v(-83.32, -32.52) * mm});
            skLineSegment(sketch, "E12948", {"start": v(-83.32, -32.52) * mm, "end": v(-83.2, -32.53) * mm});
            skLineSegment(sketch, "E12949", {"start": v(-83.2, -32.53) * mm, "end": v(-83, -32.57) * mm});
            skLineSegment(sketch, "E12950", {"start": v(-83, -32.57) * mm, "end": v(-82.37, -32.72) * mm});
            skLineSegment(sketch, "E12951", {"start": v(-82.37, -32.72) * mm, "end": v(-81.54, -32.94) * mm});
            skLineSegment(sketch, "E12952", {"start": v(-81.54, -32.94) * mm, "end": v(-80.59, -33.21) * mm});
            skLineSegment(sketch, "E12953", {"start": v(-80.59, -33.21) * mm, "end": v(-80.3, -33.28) * mm});
            skLineSegment(sketch, "E12954", {"start": v(-80.3, -33.28) * mm, "end": v(-79.98, -33.34) * mm});
            skLineSegment(sketch, "E12955", {"start": v(-79.98, -33.34) * mm, "end": v(-79.64, -33.38) * mm});
            skLineSegment(sketch, "E12956", {"start": v(-79.64, -33.38) * mm, "end": v(-79.28, -33.42) * mm});
            skLineSegment(sketch, "E12957", {"start": v(-79.28, -33.42) * mm, "end": v(-78.58, -33.47) * mm});
            skLineSegment(sketch, "E12958", {"start": v(-78.58, -33.47) * mm, "end": v(-77.96, -33.53) * mm});
            skLineSegment(sketch, "E12959", {"start": v(-77.96, -33.53) * mm, "end": v(-76.84, -33.64) * mm});
            skLineSegment(sketch, "E12960", {"start": v(-76.84, -33.64) * mm, "end": v(-75.45, -33.76) * mm});
            skLineSegment(sketch, "E12961", {"start": v(-75.45, -33.76) * mm, "end": v(-73.92, -33.87) * mm});
            skLineSegment(sketch, "E12962", {"start": v(-73.92, -33.87) * mm, "end": v(-72.35, -33.98) * mm});
            skLineSegment(sketch, "E12963", {"start": v(-72.35, -33.98) * mm, "end": v(-70.89, -34.06) * mm});
            skLineSegment(sketch, "E12964", {"start": v(-70.89, -34.06) * mm, "end": v(-69.63, -34.12) * mm});
            skLineSegment(sketch, "E12965", {"start": v(-69.63, -34.12) * mm, "end": v(-68.72, -34.15) * mm});
            skLineSegment(sketch, "E12966", {"start": v(-68.72, -34.15) * mm, "end": v(-68.43, -34.15) * mm});
            skLineSegment(sketch, "E12967", {"start": v(-68.43, -34.15) * mm, "end": v(-68.27, -34.13) * mm});
            skLineSegment(sketch, "E12968", {"start": v(-68.27, -34.13) * mm, "end": v(-68.1, -34.1) * mm});
            skLineSegment(sketch, "E12969", {"start": v(-68.1, -34.1) * mm, "end": v(-67.9, -34.02) * mm});
            skLineSegment(sketch, "E12970", {"start": v(-67.9, -34.02) * mm, "end": v(-67.5, -33.87) * mm});
            skLineSegment(sketch, "E12971", {"start": v(-67.5, -33.87) * mm, "end": v(-67.3, -33.8) * mm});
            skLineSegment(sketch, "E12972", {"start": v(-67.3, -33.8) * mm, "end": v(-67.12, -33.73) * mm});
            skLineSegment(sketch, "E12973", {"start": v(-67.12, -33.73) * mm, "end": v(-66.99, -33.7) * mm});
            skLineSegment(sketch, "E12974", {"start": v(-66.99, -33.7) * mm, "end": v(-66.94, -33.7) * mm});
            skLineSegment(sketch, "E12975", {"start": v(-66.94, -33.7) * mm, "end": v(-66.9, -33.7) * mm});
            skLineSegment(sketch, "E12976", {"start": v(-66.9, -33.7) * mm, "end": v(-66.84, -33.74) * mm});
            skLineSegment(sketch, "E12977", {"start": v(-66.84, -33.74) * mm, "end": v(-66.78, -33.8) * mm});
            skLineSegment(sketch, "E12978", {"start": v(-66.78, -33.8) * mm, "end": v(-66.74, -33.88) * mm});
            skLineSegment(sketch, "E12979", {"start": v(-66.74, -33.88) * mm, "end": v(-66.7, -33.97) * mm});
            skLineSegment(sketch, "E12980", {"start": v(-66.7, -33.97) * mm, "end": v(-66.64, -34.15) * mm});
            skLineSegment(sketch, "E12981", {"start": v(-66.64, -34.15) * mm, "end": v(-66.6, -34.23) * mm});
            skLineSegment(sketch, "E12982", {"start": v(-66.6, -34.23) * mm, "end": v(-66.57, -34.3) * mm});
            skLineSegment(sketch, "E12983", {"start": v(-66.57, -34.3) * mm, "end": v(-65, -33.77) * mm});
            skLineSegment(sketch, "E12984", {"start": v(-65, -33.77) * mm, "end": v(-65.07, -33.62) * mm});
            skLineSegment(sketch, "E12985", {"start": v(-65.07, -33.62) * mm, "end": v(-65.16, -33.46) * mm});
            skLineSegment(sketch, "E12986", {"start": v(-65.16, -33.46) * mm, "end": v(-65.19, -33.37) * mm});
            skLineSegment(sketch, "E12987", {"start": v(-65.19, -33.37) * mm, "end": v(-65.21, -33.3) * mm});
            skLineSegment(sketch, "E12988", {"start": v(-65.21, -33.3) * mm, "end": v(-65.22, -33.22) * mm});
            skLineSegment(sketch, "E12989", {"start": v(-65.22, -33.22) * mm, "end": v(-65.2, -33.14) * mm});
            skLineSegment(sketch, "E12990", {"start": v(-65.2, -33.14) * mm, "end": v(-65.16, -33.08) * mm});
            skLineSegment(sketch, "E12991", {"start": v(-65.16, -33.08) * mm, "end": v(-65.1, -33.01) * mm});
            skLineSegment(sketch, "E12992", {"start": v(-65.1, -33.01) * mm, "end": v(-65.03, -32.95) * mm});
            skLineSegment(sketch, "E12993", {"start": v(-65.03, -32.95) * mm, "end": v(-64.94, -32.89) * mm});
            skLineSegment(sketch, "E12994", {"start": v(-64.94, -32.89) * mm, "end": v(-64.72, -32.77) * mm});
            skLineSegment(sketch, "E12995", {"start": v(-64.72, -32.77) * mm, "end": v(-64.46, -32.65) * mm});
            skLineSegment(sketch, "E12996", {"start": v(-64.46, -32.65) * mm, "end": v(-63.9, -32.43) * mm});
            skLineSegment(sketch, "E12997", {"start": v(-63.9, -32.43) * mm, "end": v(-63.61, -32.32) * mm});
            skLineSegment(sketch, "E12998", {"start": v(-63.61, -32.32) * mm, "end": v(-63.36, -32.22) * mm});
            skLineSegment(sketch, "E12999", {"start": v(-63.36, -32.22) * mm, "end": v(-62.99, -32.06) * mm});
            skLineSegment(sketch, "E13000", {"start": v(-62.99, -32.06) * mm, "end": v(-62.59, -31.88) * mm});
            skLineSegment(sketch, "E13001", {"start": v(-62.59, -31.88) * mm, "end": v(-62.2, -31.69) * mm});
            skLineSegment(sketch, "E13002", {"start": v(-62.2, -31.69) * mm, "end": v(-62, -31.59) * mm});
            skLineSegment(sketch, "E13003", {"start": v(-62, -31.59) * mm, "end": v(-61.84, -31.48) * mm});
            skLineSegment(sketch, "E13004", {"start": v(-61.84, -31.48) * mm, "end": v(-61.62, -31.34) * mm});
            skLineSegment(sketch, "E13005", {"start": v(-61.62, -31.34) * mm, "end": v(-61.38, -31.16) * mm});
            skLineSegment(sketch, "E13006", {"start": v(-61.38, -31.16) * mm, "end": v(-61.12, -30.95) * mm});
            skLineSegment(sketch, "E13007", {"start": v(-61.12, -30.95) * mm, "end": v(-60.82, -30.71) * mm});
            skLineSegment(sketch, "E13008", {"start": v(-60.82, -30.71) * mm, "end": v(-60.14, -30.13) * mm});
            skLineSegment(sketch, "E13009", {"start": v(-60.14, -30.13) * mm, "end": v(-59.33, -29.4) * mm});
            skLineSegment(sketch, "E13010", {"start": v(-59.33, -29.4) * mm, "end": v(-58.8, -28.93) * mm});
            skLineSegment(sketch, "E13011", {"start": v(-58.8, -28.93) * mm, "end": v(-58.24, -28.44) * mm});
            skLineSegment(sketch, "E13012", {"start": v(-58.24, -28.44) * mm, "end": v(-57.95, -28.18) * mm});
            skLineSegment(sketch, "E13013", {"start": v(-57.95, -28.18) * mm, "end": v(-57.68, -27.93) * mm});
            skLineSegment(sketch, "E13014", {"start": v(-57.68, -27.93) * mm, "end": v(-57.42, -27.68) * mm});
            skLineSegment(sketch, "E13015", {"start": v(-57.42, -27.68) * mm, "end": v(-57.2, -27.43) * mm});
            skLineSegment(sketch, "E13016", {"start": v(-57.2, -27.43) * mm, "end": v(-57.02, -27.22) * mm});
            skLineSegment(sketch, "E13017", {"start": v(-57.02, -27.22) * mm, "end": v(-56.84, -27) * mm});
            skLineSegment(sketch, "E13018", {"start": v(-56.84, -27) * mm, "end": v(-56.5, -26.5) * mm});
            skLineSegment(sketch, "E13019", {"start": v(-56.5, -26.5) * mm, "end": v(-56.17, -26) * mm});
            skLineSegment(sketch, "E13020", {"start": v(-56.17, -26) * mm, "end": v(-55.86, -25.53) * mm});
            skLineSegment(sketch, "E13021", {"start": v(-55.86, -25.53) * mm, "end": v(-55.58, -25.15) * mm});
            skLineSegment(sketch, "E13022", {"start": v(-55.58, -25.15) * mm, "end": v(-55.32, -24.8) * mm});
            skLineSegment(sketch, "E13023", {"start": v(-55.32, -24.8) * mm, "end": v(-55.08, -24.49) * mm});
            skLineSegment(sketch, "E13024", {"start": v(-55.08, -24.49) * mm, "end": v(-54.85, -24.22) * mm});
            skLineSegment(sketch, "E13025", {"start": v(-54.85, -24.22) * mm, "end": v(-54.66, -24) * mm});
            skLineSegment(sketch, "E13026", {"start": v(-54.66, -24) * mm, "end": v(-54.5, -23.85) * mm});
            skLineSegment(sketch, "E13027", {"start": v(-54.5, -23.85) * mm, "end": v(-54.38, -23.77) * mm});
            skLineSegment(sketch, "E13028", {"start": v(-54.38, -23.77) * mm, "end": v(-54.34, -23.75) * mm});
            skLineSegment(sketch, "E13029", {"start": v(-54.34, -23.75) * mm, "end": v(-54.32, -23.75) * mm});
            skLineSegment(sketch, "E13030", {"start": v(-54.32, -23.75) * mm, "end": v(-54.29, -23.78) * mm});
            skLineSegment(sketch, "E13031", {"start": v(-54.29, -23.78) * mm, "end": v(-54.25, -23.84) * mm});
            skLineSegment(sketch, "E13032", {"start": v(-54.25, -23.84) * mm, "end": v(-54.13, -24.04) * mm});
            skLineSegment(sketch, "E13033", {"start": v(-54.13, -24.04) * mm, "end": v(-53.98, -24.34) * mm});
            skLineSegment(sketch, "E13034", {"start": v(-53.98, -24.34) * mm, "end": v(-53.78, -24.73) * mm});
            skLineSegment(sketch, "E13035", {"start": v(-53.78, -24.73) * mm, "end": v(-53.32, -25.7) * mm});
            skLineSegment(sketch, "E13036", {"start": v(-53.32, -25.7) * mm, "end": v(-52.8, -26.88) * mm});
            skLineSegment(sketch, "E13037", {"start": v(-52.8, -26.88) * mm, "end": v(-51.47, -29.87) * mm});
            skLineSegment(sketch, "E13038", {"start": v(-51.47, -29.87) * mm, "end": v(-49.58, -29.88) * mm});
            skLineSegment(sketch, "E13039", {"start": v(-49.58, -29.88) * mm, "end": v(-50.11, -29.06) * mm});
            skLineSegment(sketch, "E13040", {"start": v(-50.11, -29.06) * mm, "end": v(-50.34, -28.71) * mm});
            skLineSegment(sketch, "E13041", {"start": v(-50.34, -28.71) * mm, "end": v(-50.5, -28.44) * mm});
            skLineSegment(sketch, "E13042", {"start": v(-50.5, -28.44) * mm, "end": v(-50.55, -28.33) * mm});
            skLineSegment(sketch, "E13043", {"start": v(-50.55, -28.33) * mm, "end": v(-50.59, -28.24) * mm});
            skLineSegment(sketch, "E13044", {"start": v(-50.59, -28.24) * mm, "end": v(-50.6, -28.16) * mm});
            skLineSegment(sketch, "E13045", {"start": v(-50.6, -28.16) * mm, "end": v(-50.6, -28.09) * mm});
            skLineSegment(sketch, "E13046", {"start": v(-50.6, -28.09) * mm, "end": v(-50.6, -28.03) * mm});
            skLineSegment(sketch, "E13047", {"start": v(-50.6, -28.03) * mm, "end": v(-50.56, -28) * mm});
            skLineSegment(sketch, "E13048", {"start": v(-50.56, -28) * mm, "end": v(-50.5, -27.96) * mm});
            skLineSegment(sketch, "E13049", {"start": v(-50.5, -27.96) * mm, "end": v(-50.44, -27.93) * mm});
            skLineSegment(sketch, "E13050", {"start": v(-50.44, -27.93) * mm, "end": v(-50.35, -27.92) * mm});
            skLineSegment(sketch, "E13051", {"start": v(-50.35, -27.92) * mm, "end": v(-50.24, -27.9) * mm});
            skLineSegment(sketch, "E13052", {"start": v(-50.24, -27.9) * mm, "end": v(-49.98, -27.9) * mm});
            skLineSegment(sketch, "E13053", {"start": v(-49.98, -27.9) * mm, "end": v(-49.85, -27.9) * mm});
            skLineSegment(sketch, "E13054", {"start": v(-49.85, -27.9) * mm, "end": v(-49.7, -27.92) * mm});
            skLineSegment(sketch, "E13055", {"start": v(-49.7, -27.92) * mm, "end": v(-49.39, -27.98) * mm});
            skLineSegment(sketch, "E13056", {"start": v(-49.39, -27.98) * mm, "end": v(-49.02, -28.08) * mm});
            skLineSegment(sketch, "E13057", {"start": v(-49.02, -28.08) * mm, "end": v(-48.6, -28.22) * mm});
            skLineSegment(sketch, "E13058", {"start": v(-48.6, -28.22) * mm, "end": v(-48.15, -28.39) * mm});
            skLineSegment(sketch, "E13059", {"start": v(-48.15, -28.39) * mm, "end": v(-47.64, -28.59) * mm});
            skLineSegment(sketch, "E13060", {"start": v(-47.64, -28.59) * mm, "end": v(-46.49, -29.08) * mm});
            skLineSegment(sketch, "E13061", {"start": v(-46.49, -29.08) * mm, "end": v(-45.14, -29.67) * mm});
            skLineSegment(sketch, "E13062", {"start": v(-45.14, -29.67) * mm, "end": v(-43.62, -30.35) * mm});
            skLineSegment(sketch, "E13063", {"start": v(-43.62, -30.35) * mm, "end": v(-41.9, -31.1) * mm});
            skLineSegment(sketch, "E13064", {"start": v(-41.9, -31.1) * mm, "end": v(-40.97, -31.48) * mm});
            skLineSegment(sketch, "E13065", {"start": v(-40.97, -31.48) * mm, "end": v(-40, -31.89) * mm});
            skLineSegment(sketch, "E13066", {"start": v(-40, -31.89) * mm, "end": v(-39.65, -32.03) * mm});
            skLineSegment(sketch, "E13067", {"start": v(-39.65, -32.03) * mm, "end": v(-39.33, -32.19) * mm});
            skLineSegment(sketch, "E13068", {"start": v(-39.33, -32.19) * mm, "end": v(-39.02, -32.34) * mm});
            skLineSegment(sketch, "E13069", {"start": v(-39.02, -32.34) * mm, "end": v(-38.74, -32.5) * mm});
            skLineSegment(sketch, "E13070", {"start": v(-38.74, -32.5) * mm, "end": v(-38.21, -32.8) * mm});
            skLineSegment(sketch, "E13071", {"start": v(-38.21, -32.8) * mm, "end": v(-37.72, -33.11) * mm});
            skLineSegment(sketch, "E13072", {"start": v(-37.72, -33.11) * mm, "end": v(-37.25, -33.4) * mm});
            skLineSegment(sketch, "E13073", {"start": v(-37.25, -33.4) * mm, "end": v(-37.01, -33.53) * mm});
            skLineSegment(sketch, "E13074", {"start": v(-37.01, -33.53) * mm, "end": v(-36.77, -33.66) * mm});
            skLineSegment(sketch, "E13075", {"start": v(-36.77, -33.66) * mm, "end": v(-36.52, -33.77) * mm});
            skLineSegment(sketch, "E13076", {"start": v(-36.52, -33.77) * mm, "end": v(-36.26, -33.88) * mm});
            skLineSegment(sketch, "E13077", {"start": v(-36.26, -33.88) * mm, "end": v(-35.99, -33.98) * mm});
            skLineSegment(sketch, "E13078", {"start": v(-35.99, -33.98) * mm, "end": v(-35.7, -34.07) * mm});
            skLineSegment(sketch, "E13079", {"start": v(-35.7, -34.07) * mm, "end": v(-35.53, -34.1) * mm});
            skLineSegment(sketch, "E13080", {"start": v(-35.53, -34.1) * mm, "end": v(-35.3, -34.13) * mm});
            skLineSegment(sketch, "E13081", {"start": v(-35.3, -34.13) * mm, "end": v(-34.74, -34.19) * mm});
            skLineSegment(sketch, "E13082", {"start": v(-34.74, -34.19) * mm, "end": v(-34.06, -34.23) * mm});
            skLineSegment(sketch, "E13083", {"start": v(-34.06, -34.23) * mm, "end": v(-33.33, -34.26) * mm});
            skLineSegment(sketch, "E13084", {"start": v(-33.33, -34.26) * mm, "end": v(-32.61, -34.27) * mm});
            skLineSegment(sketch, "E13085", {"start": v(-32.61, -34.27) * mm, "end": v(-31.97, -34.26) * mm});
            skLineSegment(sketch, "E13086", {"start": v(-31.97, -34.26) * mm, "end": v(-31.47, -34.24) * mm});
            skLineSegment(sketch, "E13087", {"start": v(-31.47, -34.24) * mm, "end": v(-31.3, -34.22) * mm});
            skLineSegment(sketch, "E13088", {"start": v(-31.3, -34.22) * mm, "end": v(-31.18, -34.2) * mm});
            skLineSegment(sketch, "E13089", {"start": v(-31.18, -34.2) * mm, "end": v(-30.35, -33.97) * mm});
            skLineSegment(sketch, "E13090", {"start": v(-30.35, -33.97) * mm, "end": v(-30.33, -32.98) * mm});
            skLineSegment(sketch, "E13091", {"start": v(-30.33, -32.98) * mm, "end": v(-30.32, -32.78) * mm});
            skLineSegment(sketch, "E13092", {"start": v(-30.32, -32.78) * mm, "end": v(-30.3, -32.57) * mm});
            skLineSegment(sketch, "E13093", {"start": v(-30.3, -32.57) * mm, "end": v(-30.25, -32.18) * mm});
            skLineSegment(sketch, "E13094", {"start": v(-30.25, -32.18) * mm, "end": v(-30.22, -32) * mm});
            skLineSegment(sketch, "E13095", {"start": v(-30.22, -32) * mm, "end": v(-30.18, -31.86) * mm});
            skLineSegment(sketch, "E13096", {"start": v(-30.18, -31.86) * mm, "end": v(-30.14, -31.73) * mm});
            skLineSegment(sketch, "E13097", {"start": v(-30.14, -31.73) * mm, "end": v(-30.1, -31.64) * mm});
            skLineSegment(sketch, "E13098", {"start": v(-30.1, -31.64) * mm, "end": v(-29.87, -31.28) * mm});
            skLineSegment(sketch, "E13099", {"start": v(-29.87, -31.28) * mm, "end": v(-30.66, -31.25) * mm});
            skLineSegment(sketch, "E13100", {"start": v(-30.66, -31.25) * mm, "end": v(-31.5, -31.24) * mm});
            skLineSegment(sketch, "E13101", {"start": v(-31.5, -31.24) * mm, "end": v(-33.26, -31.22) * mm});
            skLineSegment(sketch, "E13102", {"start": v(-33.26, -31.22) * mm, "end": v(-34.15, -31.2) * mm});
            skLineSegment(sketch, "E13103", {"start": v(-34.15, -31.2) * mm, "end": v(-34.58, -31.17) * mm});
            skLineSegment(sketch, "E13104", {"start": v(-34.58, -31.17) * mm, "end": v(-35.01, -31.14) * mm});
            skLineSegment(sketch, "E13105", {"start": v(-35.01, -31.14) * mm, "end": v(-35.43, -31.1) * mm});
            skLineSegment(sketch, "E13106", {"start": v(-35.43, -31.1) * mm, "end": v(-35.84, -31.06) * mm});
            skLineSegment(sketch, "E13107", {"start": v(-35.84, -31.06) * mm, "end": v(-36.24, -31) * mm});
            skLineSegment(sketch, "E13108", {"start": v(-36.24, -31) * mm, "end": v(-36.62, -30.94) * mm});
            skLineSegment(sketch, "E13109", {"start": v(-36.62, -30.94) * mm, "end": v(-36.9, -30.87) * mm});
            skLineSegment(sketch, "E13110", {"start": v(-36.9, -30.87) * mm, "end": v(-37.2, -30.78) * mm});
            skLineSegment(sketch, "E13111", {"start": v(-37.2, -30.78) * mm, "end": v(-37.8, -30.56) * mm});
            skLineSegment(sketch, "E13112", {"start": v(-37.8, -30.56) * mm, "end": v(-38.41, -30.32) * mm});
            skLineSegment(sketch, "E13113", {"start": v(-38.41, -30.32) * mm, "end": v(-38.97, -30.11) * mm});
            skLineSegment(sketch, "E13114", {"start": v(-38.97, -30.11) * mm, "end": v(-39.53, -29.9) * mm});
            skLineSegment(sketch, "E13115", {"start": v(-39.53, -29.9) * mm, "end": v(-40.2, -29.63) * mm});
            skLineSegment(sketch, "E13116", {"start": v(-40.2, -29.63) * mm, "end": v(-40.96, -29.3) * mm});
            skLineSegment(sketch, "E13117", {"start": v(-40.96, -29.3) * mm, "end": v(-41.79, -28.94) * mm});
            skLineSegment(sketch, "E13118", {"start": v(-41.79, -28.94) * mm, "end": v(-42.65, -28.54) * mm});
            skLineSegment(sketch, "E13119", {"start": v(-42.65, -28.54) * mm, "end": v(-43.54, -28.12) * mm});
            skLineSegment(sketch, "E13120", {"start": v(-43.54, -28.12) * mm, "end": v(-44.4, -27.7) * mm});
            skLineSegment(sketch, "E13121", {"start": v(-44.4, -27.7) * mm, "end": v(-45.24, -27.28) * mm});
            skLineSegment(sketch, "E13122", {"start": v(-45.24, -27.28) * mm, "end": v(-48.05, -25.8) * mm});
            skLineSegment(sketch, "E13123", {"start": v(-48.05, -25.8) * mm, "end": v(-49.5, -25.02) * mm});
            skLineSegment(sketch, "E13124", {"start": v(-49.5, -25.02) * mm, "end": v(-50.85, -24.3) * mm});
            skLineSegment(sketch, "E13125", {"start": v(-50.85, -24.3) * mm, "end": v(-51.69, -23.81) * mm});
            skLineSegment(sketch, "E13126", {"start": v(-51.69, -23.81) * mm, "end": v(-52.53, -23.32) * mm});
            skLineSegment(sketch, "E13127", {"start": v(-52.53, -23.32) * mm, "end": v(-52.57, -22.52) * mm});
            skLineSegment(sketch, "E13128", {"start": v(-52.57, -22.52) * mm, "end": v(-52.6, -21.68) * mm});
            skLineSegment(sketch, "E13129", {"start": v(-52.6, -21.68) * mm, "end": v(-52.65, -19.91) * mm});
            skLineSegment(sketch, "E13130", {"start": v(-52.65, -19.91) * mm, "end": v(-52.68, -19.02) * mm});
            skLineSegment(sketch, "E13131", {"start": v(-52.68, -19.02) * mm, "end": v(-52.74, -18.14) * mm});
            skLineSegment(sketch, "E13132", {"start": v(-52.74, -18.14) * mm, "end": v(-52.8, -17.3) * mm});
            skLineSegment(sketch, "E13133", {"start": v(-52.8, -17.3) * mm, "end": v(-52.85, -16.9) * mm});
            skLineSegment(sketch, "E13134", {"start": v(-52.85, -16.9) * mm, "end": v(-52.9, -16.51) * mm});
            skLineSegment(sketch, "E13135", {"start": v(-52.9, -16.51) * mm, "end": v(-52.95, -16.25) * mm});
            skLineSegment(sketch, "E13136", {"start": v(-52.95, -16.25) * mm, "end": v(-53, -15.98) * mm});
            skLineSegment(sketch, "E13137", {"start": v(-53, -15.98) * mm, "end": v(-53.14, -15.4) * mm});
            skLineSegment(sketch, "E13138", {"start": v(-53.14, -15.4) * mm, "end": v(-53.3, -14.84) * mm});
            skLineSegment(sketch, "E13139", {"start": v(-53.3, -14.84) * mm, "end": v(-53.43, -14.3) * mm});
            skLineSegment(sketch, "E13140", {"start": v(-53.43, -14.3) * mm, "end": v(-53.54, -13.84) * mm});
            skLineSegment(sketch, "E13141", {"start": v(-53.54, -13.84) * mm, "end": v(-53.68, -13.34) * mm});
            skLineSegment(sketch, "E13142", {"start": v(-53.68, -13.34) * mm, "end": v(-53.83, -12.82) * mm});
            skLineSegment(sketch, "E13143", {"start": v(-53.83, -12.82) * mm, "end": v(-53.99, -12.31) * mm});
            skLineSegment(sketch, "E13144", {"start": v(-53.99, -12.31) * mm, "end": v(-54.15, -11.82) * mm});
            skLineSegment(sketch, "E13145", {"start": v(-54.15, -11.82) * mm, "end": v(-54.3, -11.36) * mm});
            skLineSegment(sketch, "E13146", {"start": v(-54.3, -11.36) * mm, "end": v(-54.45, -10.95) * mm});
            skLineSegment(sketch, "E13147", {"start": v(-54.45, -10.95) * mm, "end": v(-54.6, -10.6) * mm});
            skLineSegment(sketch, "E13148", {"start": v(-54.6, -10.6) * mm, "end": v(-55.24, -9.1) * mm});
            skLineSegment(sketch, "E13149", {"start": v(-55.24, -9.1) * mm, "end": v(-55.16, -8.48) * mm});
            skLineSegment(sketch, "E13150", {"start": v(-55.16, -8.48) * mm, "end": v(-55.06, -7.81) * mm});
            skLineSegment(sketch, "E13151", {"start": v(-55.06, -7.81) * mm, "end": v(-54.84, -6.43) * mm});
            skLineSegment(sketch, "E13152", {"start": v(-54.84, -6.43) * mm, "end": v(-54.75, -5.73) * mm});
            skLineSegment(sketch, "E13153", {"start": v(-54.75, -5.73) * mm, "end": v(-54.67, -5.04) * mm});
            skLineSegment(sketch, "E13154", {"start": v(-54.67, -5.04) * mm, "end": v(-54.65, -4.7) * mm});
            skLineSegment(sketch, "E13155", {"start": v(-54.65, -4.7) * mm, "end": v(-54.63, -4.38) * mm});
            skLineSegment(sketch, "E13156", {"start": v(-54.63, -4.38) * mm, "end": v(-54.62, -4.06) * mm});
            skLineSegment(sketch, "E13157", {"start": v(-54.62, -4.06) * mm, "end": v(-54.63, -3.75) * mm});
            skLineSegment(sketch, "E13158", {"start": v(-54.63, -3.75) * mm, "end": v(-54.65, -3.47) * mm});
            skLineSegment(sketch, "E13159", {"start": v(-54.65, -3.47) * mm, "end": v(-54.7, -3.17) * mm});
            skLineSegment(sketch, "E13160", {"start": v(-54.7, -3.17) * mm, "end": v(-54.75, -2.86) * mm});
            skLineSegment(sketch, "E13161", {"start": v(-54.75, -2.86) * mm, "end": v(-54.82, -2.55) * mm});
            skLineSegment(sketch, "E13162", {"start": v(-54.82, -2.55) * mm, "end": v(-54.96, -1.93) * mm});
            skLineSegment(sketch, "E13163", {"start": v(-54.96, -1.93) * mm, "end": v(-55.09, -1.36) * mm});
            skLineSegment(sketch, "E13164", {"start": v(-55.09, -1.36) * mm, "end": v(-55.19, -0.85) * mm});
            skLineSegment(sketch, "E13165", {"start": v(-55.19, -0.85) * mm, "end": v(-55.3, -0.33) * mm});
            skLineSegment(sketch, "E13166", {"start": v(-55.3, -0.33) * mm, "end": v(-55.43, 0.2) * mm});
            skLineSegment(sketch, "E13167", {"start": v(-55.43, 0.2) * mm, "end": v(-55.56, 0.7) * mm});
            skLineSegment(sketch, "E13168", {"start": v(-55.56, 0.7) * mm, "end": v(-55.7, 1.17) * mm});
            skLineSegment(sketch, "E13169", {"start": v(-55.7, 1.17) * mm, "end": v(-55.83, 1.6) * mm});
            skLineSegment(sketch, "E13170", {"start": v(-55.83, 1.6) * mm, "end": v(-55.95, 1.98) * mm});
            skLineSegment(sketch, "E13171", {"start": v(-55.95, 1.98) * mm, "end": v(-56.06, 2.27) * mm});
            skLineSegment(sketch, "E13172", {"start": v(-56.06, 2.27) * mm, "end": v(-56.58, 3.51) * mm});
            skLineSegment(sketch, "E13173", {"start": v(-56.58, 3.51) * mm, "end": v(-55.79, 4.88) * mm});
            skLineSegment(sketch, "E13174", {"start": v(-55.79, 4.88) * mm, "end": v(-55.6, 5.23) * mm});
            skLineSegment(sketch, "E13175", {"start": v(-55.6, 5.23) * mm, "end": v(-55.4, 5.6) * mm});
            skLineSegment(sketch, "E13176", {"start": v(-55.4, 5.6) * mm, "end": v(-55.22, 6.02) * mm});
            skLineSegment(sketch, "E13177", {"start": v(-55.22, 6.02) * mm, "end": v(-55.04, 6.48) * mm});
            skLineSegment(sketch, "E13178", {"start": v(-55.04, 6.48) * mm, "end": v(-54.86, 6.97) * mm});
            skLineSegment(sketch, "E13179", {"start": v(-54.86, 6.97) * mm, "end": v(-54.67, 7.5) * mm});
            skLineSegment(sketch, "E13180", {"start": v(-54.67, 7.5) * mm, "end": v(-54.49, 8.07) * mm});
            skLineSegment(sketch, "E13181", {"start": v(-54.49, 8.07) * mm, "end": v(-54.3, 8.68) * mm});
            skLineSegment(sketch, "E13182", {"start": v(-54.3, 8.68) * mm, "end": v(-54.12, 9.34) * mm});
            skLineSegment(sketch, "E13183", {"start": v(-54.12, 9.34) * mm, "end": v(-53.93, 10.04) * mm});
            skLineSegment(sketch, "E13184", {"start": v(-53.93, 10.04) * mm, "end": v(-53.75, 10.8) * mm});
            skLineSegment(sketch, "E13185", {"start": v(-53.75, 10.8) * mm, "end": v(-53.55, 11.6) * mm});
            skLineSegment(sketch, "E13186", {"start": v(-53.55, 11.6) * mm, "end": v(-53.36, 12.45) * mm});
            skLineSegment(sketch, "E13187", {"start": v(-53.36, 12.45) * mm, "end": v(-53.16, 13.35) * mm});
            skLineSegment(sketch, "E13188", {"start": v(-53.16, 13.35) * mm, "end": v(-52.76, 15.33) * mm});
            skLineSegment(sketch, "E13189", {"start": v(-52.76, 15.33) * mm, "end": v(-51.87, 19.78) * mm});
            skLineSegment(sketch, "E13190", {"start": v(-51.87, 19.78) * mm, "end": v(-50.88, 20.92) * mm});
            skLineSegment(sketch, "E13191", {"start": v(-50.88, 20.92) * mm, "end": v(-50.73, 21.1) * mm});
            skLineSegment(sketch, "E13192", {"start": v(-50.73, 21.1) * mm, "end": v(-50.57, 21.3) * mm});
            skLineSegment(sketch, "E13193", {"start": v(-50.57, 21.3) * mm, "end": v(-50.42, 21.52) * mm});
            skLineSegment(sketch, "E13194", {"start": v(-50.42, 21.52) * mm, "end": v(-50.26, 21.75) * mm});
            skLineSegment(sketch, "E13195", {"start": v(-50.26, 21.75) * mm, "end": v(-49.95, 22.24) * mm});
            skLineSegment(sketch, "E13196", {"start": v(-49.95, 22.24) * mm, "end": v(-49.64, 22.78) * mm});
            skLineSegment(sketch, "E13197", {"start": v(-49.64, 22.78) * mm, "end": v(-49.34, 23.36) * mm});
            skLineSegment(sketch, "E13198", {"start": v(-49.34, 23.36) * mm, "end": v(-49.05, 23.96) * mm});
            skLineSegment(sketch, "E13199", {"start": v(-49.05, 23.96) * mm, "end": v(-48.77, 24.58) * mm});
            skLineSegment(sketch, "E13200", {"start": v(-48.77, 24.58) * mm, "end": v(-48.51, 25.22) * mm});
            skLineSegment(sketch, "E13201", {"start": v(-48.51, 25.22) * mm, "end": v(-48.27, 25.86) * mm});
            skLineSegment(sketch, "E13202", {"start": v(-48.27, 25.86) * mm, "end": v(-48.05, 26.5) * mm});
            skLineSegment(sketch, "E13203", {"start": v(-48.05, 26.5) * mm, "end": v(-47.85, 27.13) * mm});
            skLineSegment(sketch, "E13204", {"start": v(-47.85, 27.13) * mm, "end": v(-47.68, 27.74) * mm});
            skLineSegment(sketch, "E13205", {"start": v(-47.68, 27.74) * mm, "end": v(-47.54, 28.32) * mm});
            skLineSegment(sketch, "E13206", {"start": v(-47.54, 28.32) * mm, "end": v(-47.44, 28.88) * mm});
            skLineSegment(sketch, "E13207", {"start": v(-47.44, 28.88) * mm, "end": v(-47.4, 29.14) * mm});
            skLineSegment(sketch, "E13208", {"start": v(-47.4, 29.14) * mm, "end": v(-47.37, 29.39) * mm});
            skLineSegment(sketch, "E13209", {"start": v(-47.37, 29.39) * mm, "end": v(-47.35, 29.62) * mm});
            skLineSegment(sketch, "E13210", {"start": v(-47.35, 29.62) * mm, "end": v(-47.34, 29.85) * mm});
            skLineSegment(sketch, "E13211", {"start": v(-47.34, 29.85) * mm, "end": v(-47.33, 30.67) * mm});
            skLineSegment(sketch, "E13212", {"start": v(-47.33, 30.67) * mm, "end": v(-45.26, 32.36) * mm});
            skLineSegment(sketch, "E13213", {"start": v(-45.26, 32.36) * mm, "end": v(-44.63, 32.88) * mm});
            skLineSegment(sketch, "E13214", {"start": v(-44.63, 32.88) * mm, "end": v(-44.02, 33.43) * mm});
            skLineSegment(sketch, "E13215", {"start": v(-44.02, 33.43) * mm, "end": v(-43.43, 34) * mm});
            skLineSegment(sketch, "E13216", {"start": v(-43.43, 34) * mm, "end": v(-42.86, 34.6) * mm});
            skLineSegment(sketch, "E13217", {"start": v(-42.86, 34.6) * mm, "end": v(-42.3, 35.2) * mm});
            skLineSegment(sketch, "E13218", {"start": v(-42.3, 35.2) * mm, "end": v(-41.77, 35.83) * mm});
            skLineSegment(sketch, "E13219", {"start": v(-41.77, 35.83) * mm, "end": v(-41.25, 36.48) * mm});
            skLineSegment(sketch, "E13220", {"start": v(-41.25, 36.48) * mm, "end": v(-40.76, 37.14) * mm});
            skLineSegment(sketch, "E13221", {"start": v(-40.76, 37.14) * mm, "end": v(-40.3, 37.81) * mm});
            skLineSegment(sketch, "E13222", {"start": v(-40.3, 37.81) * mm, "end": v(-39.84, 38.5) * mm});
            skLineSegment(sketch, "E13223", {"start": v(-39.84, 38.5) * mm, "end": v(-39.42, 39.2) * mm});
            skLineSegment(sketch, "E13224", {"start": v(-39.42, 39.2) * mm, "end": v(-39.03, 39.9) * mm});
            skLineSegment(sketch, "E13225", {"start": v(-39.03, 39.9) * mm, "end": v(-38.66, 40.62) * mm});
            skLineSegment(sketch, "E13226", {"start": v(-38.66, 40.62) * mm, "end": v(-38.32, 41.34) * mm});
            skLineSegment(sketch, "E13227", {"start": v(-38.32, 41.34) * mm, "end": v(-38, 42.07) * mm});
            skLineSegment(sketch, "E13228", {"start": v(-38, 42.07) * mm, "end": v(-37.72, 42.8) * mm});
            skLineSegment(sketch, "E13229", {"start": v(-37.72, 42.8) * mm, "end": v(-37.03, 44.7) * mm});
            skLineSegment(sketch, "E13230", {"start": v(-37.03, 44.7) * mm, "end": v(-36.47, 44.7) * mm});
            skLineSegment(sketch, "E13231", {"start": v(-36.47, 44.7) * mm, "end": v(-36.33, 44.7) * mm});
            skLineSegment(sketch, "E13232", {"start": v(-36.33, 44.7) * mm, "end": v(-36.13, 44.74) * mm});
            skLineSegment(sketch, "E13233", {"start": v(-36.13, 44.74) * mm, "end": v(-35.9, 44.79) * mm});
            skLineSegment(sketch, "E13234", {"start": v(-35.9, 44.79) * mm, "end": v(-35.63, 44.85) * mm});
            skLineSegment(sketch, "E13235", {"start": v(-35.63, 44.85) * mm, "end": v(-35.02, 45.02) * mm});
            skLineSegment(sketch, "E13236", {"start": v(-35.02, 45.02) * mm, "end": v(-34.37, 45.22) * mm});
            skLineSegment(sketch, "E13237", {"start": v(-34.37, 45.22) * mm, "end": v(-34, 45.34) * mm});
            skLineSegment(sketch, "E13238", {"start": v(-34, 45.34) * mm, "end": v(-33.59, 45.45) * mm});
            skLineSegment(sketch, "E13239", {"start": v(-33.59, 45.45) * mm, "end": v(-33.38, 45.51) * mm});
            skLineSegment(sketch, "E13240", {"start": v(-33.38, 45.51) * mm, "end": v(-33.19, 45.58) * mm});
            skLineSegment(sketch, "E13241", {"start": v(-33.19, 45.58) * mm, "end": v(-33, 45.66) * mm});
            skLineSegment(sketch, "E13242", {"start": v(-33, 45.66) * mm, "end": v(-32.83, 45.75) * mm});
            skLineSegment(sketch, "E13243", {"start": v(-32.83, 45.75) * mm, "end": v(-32.4, 46.02) * mm});
            skLineSegment(sketch, "E13244", {"start": v(-32.4, 46.02) * mm, "end": v(-31.96, 46.33) * mm});
            skLineSegment(sketch, "E13245", {"start": v(-31.96, 46.33) * mm, "end": v(-31.52, 46.67) * mm});
            skLineSegment(sketch, "E13246", {"start": v(-31.52, 46.67) * mm, "end": v(-31.09, 47.04) * mm});
            skLineSegment(sketch, "E13247", {"start": v(-31.09, 47.04) * mm, "end": v(-30.67, 47.43) * mm});
            skLineSegment(sketch, "E13248", {"start": v(-30.67, 47.43) * mm, "end": v(-30.28, 47.83) * mm});
            skLineSegment(sketch, "E13249", {"start": v(-30.28, 47.83) * mm, "end": v(-30.1, 48.03) * mm});
            skLineSegment(sketch, "E13250", {"start": v(-30.1, 48.03) * mm, "end": v(-29.92, 48.24) * mm});
            skLineSegment(sketch, "E13251", {"start": v(-29.92, 48.24) * mm, "end": v(-29.76, 48.44) * mm});
            skLineSegment(sketch, "E13252", {"start": v(-29.76, 48.44) * mm, "end": v(-29.62, 48.64) * mm});
            skLineSegment(sketch, "E13253", {"start": v(-29.62, 48.64) * mm, "end": v(-29.48, 48.85) * mm});
            skLineSegment(sketch, "E13254", {"start": v(-29.48, 48.85) * mm, "end": v(-29.36, 49.1) * mm});
            skLineSegment(sketch, "E13255", {"start": v(-29.36, 49.1) * mm, "end": v(-29.25, 49.35) * mm});
            skLineSegment(sketch, "E13256", {"start": v(-29.25, 49.35) * mm, "end": v(-29.15, 49.61) * mm});
            skLineSegment(sketch, "E13257", {"start": v(-29.15, 49.61) * mm, "end": v(-28.97, 50.15) * mm});
            skLineSegment(sketch, "E13258", {"start": v(-28.97, 50.15) * mm, "end": v(-28.88, 50.4) * mm});
            skLineSegment(sketch, "E13259", {"start": v(-28.88, 50.4) * mm, "end": v(-28.79, 50.64) * mm});
            skLineSegment(sketch, "E13260", {"start": v(-28.79, 50.64) * mm, "end": v(-28.2, 50.64) * mm});
            skLineSegment(sketch, "E13261", {"start": v(-28.2, 50.64) * mm, "end": v(-28.06, 50.65) * mm});
            skLineSegment(sketch, "E13262", {"start": v(-28.06, 50.65) * mm, "end": v(-27.85, 50.68) * mm});
            skLineSegment(sketch, "E13263", {"start": v(-27.85, 50.68) * mm, "end": v(-27.6, 50.73) * mm});
            skLineSegment(sketch, "E13264", {"start": v(-27.6, 50.73) * mm, "end": v(-27.3, 50.8) * mm});
            skLineSegment(sketch, "E13265", {"start": v(-27.3, 50.8) * mm, "end": v(-26.64, 50.97) * mm});
            skLineSegment(sketch, "E13266", {"start": v(-26.64, 50.97) * mm, "end": v(-25.94, 51.18) * mm});
            skLineSegment(sketch, "E13267", {"start": v(-25.94, 51.18) * mm, "end": v(-25.53, 51.3) * mm});
            skLineSegment(sketch, "E13268", {"start": v(-25.53, 51.3) * mm, "end": v(-25.08, 51.42) * mm});
            skLineSegment(sketch, "E13269", {"start": v(-25.08, 51.42) * mm, "end": v(-24.86, 51.48) * mm});
            skLineSegment(sketch, "E13270", {"start": v(-24.86, 51.48) * mm, "end": v(-24.64, 51.55) * mm});
            skLineSegment(sketch, "E13271", {"start": v(-24.64, 51.55) * mm, "end": v(-24.44, 51.63) * mm});
            skLineSegment(sketch, "E13272", {"start": v(-24.44, 51.63) * mm, "end": v(-24.25, 51.73) * mm});
            skLineSegment(sketch, "E13273", {"start": v(-24.25, 51.73) * mm, "end": v(-24.08, 51.84) * mm});
            skLineSegment(sketch, "E13274", {"start": v(-24.08, 51.84) * mm, "end": v(-23.9, 51.97) * mm});
            skLineSegment(sketch, "E13275", {"start": v(-23.9, 51.97) * mm, "end": v(-23.56, 52.27) * mm});
            skLineSegment(sketch, "E13276", {"start": v(-23.56, 52.27) * mm, "end": v(-23.22, 52.59) * mm});
            skLineSegment(sketch, "E13277", {"start": v(-23.22, 52.59) * mm, "end": v(-22.9, 52.88) * mm});
            skLineSegment(sketch, "E13278", {"start": v(-22.9, 52.88) * mm, "end": v(-22.62, 53.14) * mm});
            skLineSegment(sketch, "E13279", {"start": v(-22.62, 53.14) * mm, "end": v(-22.31, 53.43) * mm});
            skLineSegment(sketch, "E13280", {"start": v(-22.31, 53.43) * mm, "end": v(-22, 53.75) * mm});
            skLineSegment(sketch, "E13281", {"start": v(-22, 53.75) * mm, "end": v(-21.7, 54.1) * mm});
            skLineSegment(sketch, "E13282", {"start": v(-21.7, 54.1) * mm, "end": v(-21.4, 54.43) * mm});
            skLineSegment(sketch, "E13283", {"start": v(-21.4, 54.43) * mm, "end": v(-21.14, 54.77) * mm});
            skLineSegment(sketch, "E13284", {"start": v(-21.14, 54.77) * mm, "end": v(-20.9, 55.1) * mm});
            skLineSegment(sketch, "E13285", {"start": v(-20.9, 55.1) * mm, "end": v(-20.7, 55.39) * mm});
            skLineSegment(sketch, "E13286", {"start": v(-20.7, 55.39) * mm, "end": v(-20.5, 55.69) * mm});
            skLineSegment(sketch, "E13287", {"start": v(-20.5, 55.69) * mm, "end": v(-20.25, 56.02) * mm});
            skLineSegment(sketch, "E13288", {"start": v(-20.25, 56.02) * mm, "end": v(-19.96, 56.38) * mm});
            skLineSegment(sketch, "E13289", {"start": v(-19.96, 56.38) * mm, "end": v(-19.64, 56.76) * mm});
            skLineSegment(sketch, "E13290", {"start": v(-19.64, 56.76) * mm, "end": v(-19.3, 57.13) * mm});
            skLineSegment(sketch, "E13291", {"start": v(-19.3, 57.13) * mm, "end": v(-18.96, 57.5) * mm});
            skLineSegment(sketch, "E13292", {"start": v(-18.96, 57.5) * mm, "end": v(-18.61, 57.84) * mm});
            skLineSegment(sketch, "E13293", {"start": v(-18.61, 57.84) * mm, "end": v(-18.28, 58.15) * mm});
            skLineSegment(sketch, "E13294", {"start": v(-18.28, 58.15) * mm, "end": v(-17.99, 58.43) * mm});
            skLineSegment(sketch, "E13295", {"start": v(-17.99, 58.43) * mm, "end": v(-17.7, 58.73) * mm});
            skLineSegment(sketch, "E13296", {"start": v(-17.7, 58.73) * mm, "end": v(-17.4, 59.05) * mm});
            skLineSegment(sketch, "E13297", {"start": v(-17.4, 59.05) * mm, "end": v(-17.1, 59.4) * mm});
            skLineSegment(sketch, "E13298", {"start": v(-17.1, 59.4) * mm, "end": v(-16.82, 59.75) * mm});
            skLineSegment(sketch, "E13299", {"start": v(-16.82, 59.75) * mm, "end": v(-16.55, 60.1) * mm});
            skLineSegment(sketch, "E13300", {"start": v(-16.55, 60.1) * mm, "end": v(-16.02, 60.82) * mm});
            skLineSegment(sketch, "E13301", {"start": v(-16.02, 60.82) * mm, "end": v(-15.55, 61.5) * mm});
            skLineSegment(sketch, "E13302", {"start": v(-15.55, 61.5) * mm, "end": v(-15.15, 62.1) * mm});
            skLineSegment(sketch, "E13303", {"start": v(-15.15, 62.1) * mm, "end": v(-14.64, 62.93) * mm});
            skLineSegment(sketch, "E13304", {"start": v(-14.64, 62.93) * mm, "end": v(-14.53, 63.04) * mm});
            skLineSegment(sketch, "E13305", {"start": v(-14.53, 63.04) * mm, "end": v(-14.47, 63.1) * mm});
            skLineSegment(sketch, "E13306", {"start": v(-14.47, 63.1) * mm, "end": v(-14.43, 63.16) * mm});
            skLineSegment(sketch, "E13307", {"start": v(-7.52, 5.48) * mm, "end": v(-7.24, 5.34) * mm});
            skLineSegment(sketch, "E13308", {"start": v(-7.24, 5.34) * mm, "end": v(-6.97, 5.21) * mm});
            skLineSegment(sketch, "E13309", {"start": v(-6.97, 5.21) * mm, "end": v(-6.84, 5.17) * mm});
            skLineSegment(sketch, "E13310", {"start": v(-6.84, 5.17) * mm, "end": v(-6.7, 5.13) * mm});
            skLineSegment(sketch, "E13311", {"start": v(-6.7, 5.13) * mm, "end": v(-6.58, 5.11) * mm});
            skLineSegment(sketch, "E13312", {"start": v(-6.58, 5.11) * mm, "end": v(-6.45, 5.1) * mm});
            skLineSegment(sketch, "E13313", {"start": v(-6.45, 5.1) * mm, "end": v(-5.97, 5.1) * mm});
            skLineSegment(sketch, "E13314", {"start": v(-5.97, 5.1) * mm, "end": v(-5.7, 5.12) * mm});
            skLineSegment(sketch, "E13315", {"start": v(-5.7, 5.12) * mm, "end": v(-5.59, 5.13) * mm});
            skLineSegment(sketch, "E13316", {"start": v(-5.59, 5.13) * mm, "end": v(-5.5, 5.15) * mm});
            skLineSegment(sketch, "E13317", {"start": v(-5.5, 5.15) * mm, "end": v(-5.41, 5.2) * mm});
            skLineSegment(sketch, "E13318", {"start": v(-5.41, 5.2) * mm, "end": v(-5.32, 5.24) * mm});
            skLineSegment(sketch, "E13319", {"start": v(-5.32, 5.24) * mm, "end": v(-5.14, 5.36) * mm});
            skLineSegment(sketch, "E13320", {"start": v(-5.14, 5.36) * mm, "end": v(-4.97, 5.5) * mm});
            skLineSegment(sketch, "E13321", {"start": v(-4.97, 5.5) * mm, "end": v(-4.8, 5.64) * mm});
            skLineSegment(sketch, "E13322", {"start": v(-4.8, 5.64) * mm, "end": v(-4.48, 5.96) * mm});
            skLineSegment(sketch, "E13323", {"start": v(-4.48, 5.96) * mm, "end": v(-4.33, 6.12) * mm});
            skLineSegment(sketch, "E13324", {"start": v(-4.33, 6.12) * mm, "end": v(-4.17, 6.25) * mm});
            skLineSegment(sketch, "E13325", {"start": v(-4.17, 6.25) * mm, "end": v(-4.53, 8.44) * mm});
            skLineSegment(sketch, "E13326", {"start": v(-4.53, 8.44) * mm, "end": v(-5.07, 8.2) * mm});
            skLineSegment(sketch, "E13327", {"start": v(-5.07, 8.2) * mm, "end": v(-5.2, 8.15) * mm});
            skLineSegment(sketch, "E13328", {"start": v(-5.2, 8.15) * mm, "end": v(-5.37, 8.1) * mm});
            skLineSegment(sketch, "E13329", {"start": v(-5.37, 8.1) * mm, "end": v(-5.81, 7.99) * mm});
            skLineSegment(sketch, "E13330", {"start": v(-5.81, 7.99) * mm, "end": v(-6.32, 7.9) * mm});
            skLineSegment(sketch, "E13331", {"start": v(-6.32, 7.9) * mm, "end": v(-6.84, 7.82) * mm});
            skLineSegment(sketch, "E13332", {"start": v(-6.84, 7.82) * mm, "end": v(-8.08, 7.67) * mm});
            skLineSegment(sketch, "E13333", {"start": v(-8.08, 7.67) * mm, "end": v(-8.16, 6.25) * mm});
            skLineSegment(sketch, "E13334", {"start": v(-8.16, 6.25) * mm, "end": v(-8.12, 6.15) * mm});
            skLineSegment(sketch, "E13335", {"start": v(-8.12, 6.15) * mm, "end": v(-8.07, 6.04) * mm});
            skLineSegment(sketch, "E13336", {"start": v(-8.07, 6.04) * mm, "end": v(-8, 5.93) * mm});
            skLineSegment(sketch, "E13337", {"start": v(-8, 5.93) * mm, "end": v(-7.92, 5.83) * mm});
            skLineSegment(sketch, "E13338", {"start": v(-7.92, 5.83) * mm, "end": v(-7.83, 5.72) * mm});
            skLineSegment(sketch, "E13339", {"start": v(-7.83, 5.72) * mm, "end": v(-7.74, 5.63) * mm});
            skLineSegment(sketch, "E13340", {"start": v(-7.74, 5.63) * mm, "end": v(-7.63, 5.55) * mm});
            skLineSegment(sketch, "E13341", {"start": v(-7.63, 5.55) * mm, "end": v(-7.52, 5.48) * mm});
            skLineSegment(sketch, "E13342", {"start": v(-12.5, 10.68) * mm, "end": v(-12.55, 11.1) * mm});
            skLineSegment(sketch, "E13343", {"start": v(-12.55, 11.1) * mm, "end": v(-12.57, 11.45) * mm});
            skLineSegment(sketch, "E13344", {"start": v(-12.57, 11.45) * mm, "end": v(-12.55, 11.76) * mm});
            skLineSegment(sketch, "E13345", {"start": v(-12.55, 11.76) * mm, "end": v(-12.51, 12.05) * mm});
            skLineSegment(sketch, "E13346", {"start": v(-12.51, 12.05) * mm, "end": v(-12.45, 12.34) * mm});
            skLineSegment(sketch, "E13347", {"start": v(-12.45, 12.34) * mm, "end": v(-12.37, 12.65) * mm});
            skLineSegment(sketch, "E13348", {"start": v(-12.37, 12.65) * mm, "end": v(-12.17, 13.37) * mm});
            skLineSegment(sketch, "E13349", {"start": v(-12.17, 13.37) * mm, "end": v(-12.63, 13.2) * mm});
            skLineSegment(sketch, "E13350", {"start": v(-12.63, 13.2) * mm, "end": v(-12.88, 13.1) * mm});
            skLineSegment(sketch, "E13351", {"start": v(-12.88, 13.1) * mm, "end": v(-13.21, 13) * mm});
            skLineSegment(sketch, "E13352", {"start": v(-13.21, 13) * mm, "end": v(-13.6, 12.9) * mm});
            skLineSegment(sketch, "E13353", {"start": v(-13.6, 12.9) * mm, "end": v(-13.97, 12.8) * mm});
            skLineSegment(sketch, "E13354", {"start": v(-13.97, 12.8) * mm, "end": v(-14.15, 12.75) * mm});
            skLineSegment(sketch, "E13355", {"start": v(-14.15, 12.75) * mm, "end": v(-14.32, 12.7) * mm});
            skLineSegment(sketch, "E13356", {"start": v(-14.32, 12.7) * mm, "end": v(-14.47, 12.64) * mm});
            skLineSegment(sketch, "E13357", {"start": v(-14.47, 12.64) * mm, "end": v(-14.61, 12.58) * mm});
            skLineSegment(sketch, "E13358", {"start": v(-14.61, 12.58) * mm, "end": v(-14.74, 12.5) * mm});
            skLineSegment(sketch, "E13359", {"start": v(-14.74, 12.5) * mm, "end": v(-14.85, 12.43) * mm});
            skLineSegment(sketch, "E13360", {"start": v(-14.85, 12.43) * mm, "end": v(-14.95, 12.35) * mm});
            skLineSegment(sketch, "E13361", {"start": v(-14.95, 12.35) * mm, "end": v(-15.03, 12.25) * mm});
            skLineSegment(sketch, "E13362", {"start": v(-15.03, 12.25) * mm, "end": v(-15.1, 12.15) * mm});
            skLineSegment(sketch, "E13363", {"start": v(-15.1, 12.15) * mm, "end": v(-15.17, 12.04) * mm});
            skLineSegment(sketch, "E13364", {"start": v(-15.17, 12.04) * mm, "end": v(-15.22, 11.92) * mm});
            skLineSegment(sketch, "E13365", {"start": v(-15.22, 11.92) * mm, "end": v(-15.26, 11.79) * mm});
            skLineSegment(sketch, "E13366", {"start": v(-15.26, 11.79) * mm, "end": v(-15.3, 11.65) * mm});
            skLineSegment(sketch, "E13367", {"start": v(-15.3, 11.65) * mm, "end": v(-15.32, 11.5) * mm});
            skLineSegment(sketch, "E13368", {"start": v(-15.32, 11.5) * mm, "end": v(-15.33, 11.33) * mm});
            skLineSegment(sketch, "E13369", {"start": v(-15.33, 11.33) * mm, "end": v(-15.33, 11.15) * mm});
            skLineSegment(sketch, "E13370", {"start": v(-15.33, 11.15) * mm, "end": v(-15.33, 10.97) * mm});
            skLineSegment(sketch, "E13371", {"start": v(-15.33, 10.97) * mm, "end": v(-15.3, 10.77) * mm});
            skLineSegment(sketch, "E13372", {"start": v(-15.3, 10.77) * mm, "end": v(-15.27, 10.58) * mm});
            skLineSegment(sketch, "E13373", {"start": v(-15.27, 10.58) * mm, "end": v(-15.22, 10.41) * mm});
            skLineSegment(sketch, "E13374", {"start": v(-15.22, 10.41) * mm, "end": v(-15.13, 10.19) * mm});
            skLineSegment(sketch, "E13375", {"start": v(-15.13, 10.19) * mm, "end": v(-15.1, 10.13) * mm});
            skLineSegment(sketch, "E13376", {"start": v(-15.1, 10.13) * mm, "end": v(-15.06, 10.08) * mm});
            skLineSegment(sketch, "E13377", {"start": v(-15.06, 10.08) * mm, "end": v(-14.97, 10) * mm});
            skLineSegment(sketch, "E13378", {"start": v(-14.97, 10) * mm, "end": v(-14.78, 9.83) * mm});
            skLineSegment(sketch, "E13379", {"start": v(-14.78, 9.83) * mm, "end": v(-14.74, 9.8) * mm});
            skLineSegment(sketch, "E13380", {"start": v(-14.74, 9.8) * mm, "end": v(-14.69, 9.76) * mm});
            skLineSegment(sketch, "E13381", {"start": v(-14.69, 9.76) * mm, "end": v(-14.63, 9.73) * mm});
            skLineSegment(sketch, "E13382", {"start": v(-14.63, 9.73) * mm, "end": v(-14.56, 9.71) * mm});
            skLineSegment(sketch, "E13383", {"start": v(-14.56, 9.71) * mm, "end": v(-14.4, 9.7) * mm});
            skLineSegment(sketch, "E13384", {"start": v(-14.4, 9.7) * mm, "end": v(-14.23, 9.7) * mm});
            skLineSegment(sketch, "E13385", {"start": v(-14.23, 9.7) * mm, "end": v(-14.05, 9.71) * mm});
            skLineSegment(sketch, "E13386", {"start": v(-14.05, 9.71) * mm, "end": v(-13.85, 9.75) * mm});
            skLineSegment(sketch, "E13387", {"start": v(-13.85, 9.75) * mm, "end": v(-13.65, 9.8) * mm});
            skLineSegment(sketch, "E13388", {"start": v(-13.65, 9.8) * mm, "end": v(-13.45, 9.86) * mm});
            skLineSegment(sketch, "E13389", {"start": v(-13.45, 9.86) * mm, "end": v(-13.26, 9.94) * mm});
            skLineSegment(sketch, "E13390", {"start": v(-13.26, 9.94) * mm, "end": v(-13.07, 10.03) * mm});
            skLineSegment(sketch, "E13391", {"start": v(-13.07, 10.03) * mm, "end": v(-12.9, 10.12) * mm});
            skLineSegment(sketch, "E13392", {"start": v(-12.9, 10.12) * mm, "end": v(-12.76, 10.23) * mm});
            skLineSegment(sketch, "E13393", {"start": v(-12.76, 10.23) * mm, "end": v(-12.65, 10.34) * mm});
            skLineSegment(sketch, "E13394", {"start": v(-12.65, 10.34) * mm, "end": v(-12.56, 10.45) * mm});
            skLineSegment(sketch, "E13395", {"start": v(-12.56, 10.45) * mm, "end": v(-12.53, 10.5) * mm});
            skLineSegment(sketch, "E13396", {"start": v(-12.53, 10.5) * mm, "end": v(-12.51, 10.57) * mm});
            skLineSegment(sketch, "E13397", {"start": v(-12.51, 10.57) * mm, "end": v(-12.5, 10.62) * mm});
            skLineSegment(sketch, "E13398", {"start": v(-12.5, 10.62) * mm, "end": v(-12.5, 10.68) * mm});
            skLineSegment(sketch, "E13399", {"start": v(0.01, 7.2) * mm, "end": v(-0.29, 7.09) * mm});
            skLineSegment(sketch, "E13400", {"start": v(-0.29, 7.09) * mm, "end": v(-0.63, 6.94) * mm});
            skLineSegment(sketch, "E13401", {"start": v(-0.63, 6.94) * mm, "end": v(-1, 6.76) * mm});
            skLineSegment(sketch, "E13402", {"start": v(-1, 6.76) * mm, "end": v(-1.43, 6.55) * mm});
            skLineSegment(sketch, "E13403", {"start": v(-1.43, 6.55) * mm, "end": v(-2.97, 5.77) * mm});
            skLineSegment(sketch, "E13404", {"start": v(-2.97, 5.77) * mm, "end": v(-2.86, 5.4) * mm});
            skLineSegment(sketch, "E13405", {"start": v(-2.86, 5.4) * mm, "end": v(-2.8, 5.2) * mm});
            skLineSegment(sketch, "E13406", {"start": v(-2.8, 5.2) * mm, "end": v(-2.74, 5.02) * mm});
            skLineSegment(sketch, "E13407", {"start": v(-2.74, 5.02) * mm, "end": v(-2.62, 4.72) * mm});
            skLineSegment(sketch, "E13408", {"start": v(-2.62, 4.72) * mm, "end": v(-2.54, 4.57) * mm});
            skLineSegment(sketch, "E13409", {"start": v(-2.54, 4.57) * mm, "end": v(-2.46, 4.43) * mm});
            skLineSegment(sketch, "E13410", {"start": v(-2.46, 4.43) * mm, "end": v(-2.37, 4.3) * mm});
            skLineSegment(sketch, "E13411", {"start": v(-2.37, 4.3) * mm, "end": v(-2.27, 4.17) * mm});
            skLineSegment(sketch, "E13412", {"start": v(-2.27, 4.17) * mm, "end": v(-2.17, 4.07) * mm});
            skLineSegment(sketch, "E13413", {"start": v(-2.17, 4.07) * mm, "end": v(-2.07, 4) * mm});
            skLineSegment(sketch, "E13414", {"start": v(-2.07, 4) * mm, "end": v(-1.95, 3.9) * mm});
            skLineSegment(sketch, "E13415", {"start": v(-1.95, 3.9) * mm, "end": v(-1.83, 3.8) * mm});
            skLineSegment(sketch, "E13416", {"start": v(-1.83, 3.8) * mm, "end": v(-1.7, 3.72) * mm});
            skLineSegment(sketch, "E13417", {"start": v(-1.7, 3.72) * mm, "end": v(-1.64, 3.69) * mm});
            skLineSegment(sketch, "E13418", {"start": v(-1.64, 3.69) * mm, "end": v(-1.57, 3.67) * mm});
            skLineSegment(sketch, "E13419", {"start": v(-1.57, 3.67) * mm, "end": v(-1.44, 3.67) * mm});
            skLineSegment(sketch, "E13420", {"start": v(-1.44, 3.67) * mm, "end": v(-1.3, 3.7) * mm});
            skLineSegment(sketch, "E13421", {"start": v(-1.3, 3.7) * mm, "end": v(-1.16, 3.73) * mm});
            skLineSegment(sketch, "E13422", {"start": v(-1.16, 3.73) * mm, "end": v(-1.02, 3.78) * mm});
            skLineSegment(sketch, "E13423", {"start": v(-1.02, 3.78) * mm, "end": v(-0.88, 3.84) * mm});
            skLineSegment(sketch, "E13424", {"start": v(-0.88, 3.84) * mm, "end": v(-0.75, 3.91) * mm});
            skLineSegment(sketch, "E13425", {"start": v(-0.75, 3.91) * mm, "end": v(-0.63, 4) * mm});
            skLineSegment(sketch, "E13426", {"start": v(-0.63, 4) * mm, "end": v(-0.52, 4.08) * mm});
            skLineSegment(sketch, "E13427", {"start": v(-0.52, 4.08) * mm, "end": v(-0.42, 4.18) * mm});
            skLineSegment(sketch, "E13428", {"start": v(-0.42, 4.18) * mm, "end": v(-0.32, 4.28) * mm});
            skLineSegment(sketch, "E13429", {"start": v(-0.32, 4.28) * mm, "end": v(-0.24, 4.38) * mm});
            skLineSegment(sketch, "E13430", {"start": v(-0.24, 4.38) * mm, "end": v(-0.18, 4.48) * mm});
            skLineSegment(sketch, "E13431", {"start": v(-0.18, 4.48) * mm, "end": v(-0.07, 4.68) * mm});
            skLineSegment(sketch, "E13432", {"start": v(-0.07, 4.68) * mm, "end": v(0.02, 4.9) * mm});
            skLineSegment(sketch, "E13433", {"start": v(0.02, 4.9) * mm, "end": v(0.1, 5.1) * mm});
            skLineSegment(sketch, "E13434", {"start": v(0.1, 5.1) * mm, "end": v(0.17, 5.34) * mm});
            skLineSegment(sketch, "E13435", {"start": v(0.17, 5.34) * mm, "end": v(0.26, 5.58) * mm});
            skLineSegment(sketch, "E13436", {"start": v(0.26, 5.58) * mm, "end": v(0.38, 5.84) * mm});
            skLineSegment(sketch, "E13437", {"start": v(0.38, 5.84) * mm, "end": v(0.4, 5.9) * mm});
            skLineSegment(sketch, "E13438", {"start": v(0.4, 5.9) * mm, "end": v(0.42, 6) * mm});
            skLineSegment(sketch, "E13439", {"start": v(0.42, 6) * mm, "end": v(0.43, 6.2) * mm});
            skLineSegment(sketch, "E13440", {"start": v(0.43, 6.2) * mm, "end": v(0.42, 6.43) * mm});
            skLineSegment(sketch, "E13441", {"start": v(0.42, 6.43) * mm, "end": v(0.37, 6.67) * mm});
            skLineSegment(sketch, "E13442", {"start": v(0.37, 6.67) * mm, "end": v(0.3, 6.9) * mm});
            skLineSegment(sketch, "E13443", {"start": v(0.3, 6.9) * mm, "end": v(0.27, 7) * mm});
            skLineSegment(sketch, "E13444", {"start": v(0.27, 7) * mm, "end": v(0.22, 7.08) * mm});
            skLineSegment(sketch, "E13445", {"start": v(0.22, 7.08) * mm, "end": v(0.18, 7.14) * mm});
            skLineSegment(sketch, "E13446", {"start": v(0.18, 7.14) * mm, "end": v(0.13, 7.19) * mm});
            skLineSegment(sketch, "E13447", {"start": v(0.13, 7.19) * mm, "end": v(0.07, 7.2) * mm});
            skLineSegment(sketch, "E13448", {"start": v(0.07, 7.2) * mm, "end": v(0.01, 7.2) * mm});
            skLineSegment(sketch, "E13449", {"start": v(1.78, 4.1) * mm, "end": v(1.88, 4.01) * mm});
            skLineSegment(sketch, "E13450", {"start": v(1.88, 4.01) * mm, "end": v(1.99, 3.93) * mm});
            skLineSegment(sketch, "E13451", {"start": v(1.99, 3.93) * mm, "end": v(2.11, 3.86) * mm});
            skLineSegment(sketch, "E13452", {"start": v(2.11, 3.86) * mm, "end": v(2.25, 3.8) * mm});
            skLineSegment(sketch, "E13453", {"start": v(2.25, 3.8) * mm, "end": v(2.38, 3.75) * mm});
            skLineSegment(sketch, "E13454", {"start": v(2.38, 3.75) * mm, "end": v(2.52, 3.72) * mm});
            skLineSegment(sketch, "E13455", {"start": v(2.52, 3.72) * mm, "end": v(2.66, 3.7) * mm});
            skLineSegment(sketch, "E13456", {"start": v(2.66, 3.7) * mm, "end": v(2.78, 3.72) * mm});
            skLineSegment(sketch, "E13457", {"start": v(2.78, 3.72) * mm, "end": v(2.84, 3.74) * mm});
            skLineSegment(sketch, "E13458", {"start": v(2.84, 3.74) * mm, "end": v(2.9, 3.77) * mm});
            skLineSegment(sketch, "E13459", {"start": v(2.9, 3.77) * mm, "end": v(3.02, 3.85) * mm});
            skLineSegment(sketch, "E13460", {"start": v(3.02, 3.85) * mm, "end": v(3.13, 3.95) * mm});
            skLineSegment(sketch, "E13461", {"start": v(3.13, 3.95) * mm, "end": v(3.24, 4.07) * mm});
            skLineSegment(sketch, "E13462", {"start": v(3.24, 4.07) * mm, "end": v(3.43, 4.33) * mm});
            skLineSegment(sketch, "E13463", {"start": v(3.43, 4.33) * mm, "end": v(3.53, 4.45) * mm});
            skLineSegment(sketch, "E13464", {"start": v(3.53, 4.45) * mm, "end": v(3.62, 4.56) * mm});
            skLineSegment(sketch, "E13465", {"start": v(3.62, 4.56) * mm, "end": v(3.79, 4.74) * mm});
            skLineSegment(sketch, "E13466", {"start": v(3.79, 4.74) * mm, "end": v(3.95, 4.91) * mm});
            skLineSegment(sketch, "E13467", {"start": v(3.95, 4.91) * mm, "end": v(4.09, 5.09) * mm});
            skLineSegment(sketch, "E13468", {"start": v(4.09, 5.09) * mm, "end": v(4.21, 5.25) * mm});
            skLineSegment(sketch, "E13469", {"start": v(4.21, 5.25) * mm, "end": v(4.32, 5.4) * mm});
            skLineSegment(sketch, "E13470", {"start": v(4.32, 5.4) * mm, "end": v(4.4, 5.54) * mm});
            skLineSegment(sketch, "E13471", {"start": v(4.4, 5.54) * mm, "end": v(4.44, 5.66) * mm});
            skLineSegment(sketch, "E13472", {"start": v(4.44, 5.66) * mm, "end": v(4.46, 5.74) * mm});
            skLineSegment(sketch, "E13473", {"start": v(4.46, 5.74) * mm, "end": v(4.46, 6.09) * mm});
            skLineSegment(sketch, "E13474", {"start": v(4.46, 6.09) * mm, "end": v(3.88, 6.1) * mm});
            skLineSegment(sketch, "E13475", {"start": v(3.88, 6.1) * mm, "end": v(3.75, 6.1) * mm});
            skLineSegment(sketch, "E13476", {"start": v(3.75, 6.1) * mm, "end": v(3.58, 6.14) * mm});
            skLineSegment(sketch, "E13477", {"start": v(3.58, 6.14) * mm, "end": v(3.39, 6.2) * mm});
            skLineSegment(sketch, "E13478", {"start": v(3.39, 6.2) * mm, "end": v(3.18, 6.29) * mm});
            skLineSegment(sketch, "E13479", {"start": v(3.18, 6.29) * mm, "end": v(2.97, 6.38) * mm});
            skLineSegment(sketch, "E13480", {"start": v(2.97, 6.38) * mm, "end": v(2.74, 6.5) * mm});
            skLineSegment(sketch, "E13481", {"start": v(2.74, 6.5) * mm, "end": v(2.52, 6.62) * mm});
            skLineSegment(sketch, "E13482", {"start": v(2.52, 6.62) * mm, "end": v(2.31, 6.75) * mm});
            skLineSegment(sketch, "E13483", {"start": v(2.31, 6.75) * mm, "end": v(2.1, 6.9) * mm});
            skLineSegment(sketch, "E13484", {"start": v(2.1, 6.9) * mm, "end": v(1.9, 7.05) * mm});
            skLineSegment(sketch, "E13485", {"start": v(1.9, 7.05) * mm, "end": v(1.8, 7.12) * mm});
            skLineSegment(sketch, "E13486", {"start": v(1.8, 7.12) * mm, "end": v(1.7, 7.16) * mm});
            skLineSegment(sketch, "E13487", {"start": v(1.7, 7.16) * mm, "end": v(1.6, 7.2) * mm});
            skLineSegment(sketch, "E13488", {"start": v(1.6, 7.2) * mm, "end": v(1.5, 7.2) * mm});
            skLineSegment(sketch, "E13489", {"start": v(1.5, 7.2) * mm, "end": v(1.48, 7.2) * mm});
            skLineSegment(sketch, "E13490", {"start": v(1.48, 7.2) * mm, "end": v(1.46, 7.18) * mm});
            skLineSegment(sketch, "E13491", {"start": v(1.46, 7.18) * mm, "end": v(1.44, 7.09) * mm});
            skLineSegment(sketch, "E13492", {"start": v(1.44, 7.09) * mm, "end": v(1.42, 6.95) * mm});
            skLineSegment(sketch, "E13493", {"start": v(1.42, 6.95) * mm, "end": v(1.41, 6.76) * mm});
            skLineSegment(sketch, "E13494", {"start": v(1.41, 6.76) * mm, "end": v(1.42, 6.3) * mm});
            skLineSegment(sketch, "E13495", {"start": v(1.42, 6.3) * mm, "end": v(1.46, 5.76) * mm});
            skLineSegment(sketch, "E13496", {"start": v(1.46, 5.76) * mm, "end": v(1.52, 5.21) * mm});
            skLineSegment(sketch, "E13497", {"start": v(1.52, 5.21) * mm, "end": v(1.6, 4.7) * mm});
            skLineSegment(sketch, "E13498", {"start": v(1.6, 4.7) * mm, "end": v(1.64, 4.5) * mm});
            skLineSegment(sketch, "E13499", {"start": v(1.64, 4.5) * mm, "end": v(1.69, 4.32) * mm});
            skLineSegment(sketch, "E13500", {"start": v(1.69, 4.32) * mm, "end": v(1.74, 4.18) * mm});
            skLineSegment(sketch, "E13501", {"start": v(1.74, 4.18) * mm, "end": v(1.78, 4.1) * mm});
            skLineSegment(sketch, "E13502", {"start": v(13.37, 9.74) * mm, "end": v(13.34, 9.77) * mm});
            skLineSegment(sketch, "E13503", {"start": v(13.34, 9.77) * mm, "end": v(13.3, 9.8) * mm});
            skLineSegment(sketch, "E13504", {"start": v(13.3, 9.8) * mm, "end": v(13.18, 9.83) * mm});
            skLineSegment(sketch, "E13505", {"start": v(13.18, 9.83) * mm, "end": v(13.06, 9.85) * mm});
            skLineSegment(sketch, "E13506", {"start": v(13.06, 9.85) * mm, "end": v(12.96, 9.87) * mm});
            skLineSegment(sketch, "E13507", {"start": v(12.96, 9.87) * mm, "end": v(12.71, 9.93) * mm});
            skLineSegment(sketch, "E13508", {"start": v(12.71, 9.93) * mm, "end": v(12.35, 10) * mm});
            skLineSegment(sketch, "E13509", {"start": v(12.35, 10) * mm, "end": v(11.92, 10.1) * mm});
            skLineSegment(sketch, "E13510", {"start": v(11.92, 10.1) * mm, "end": v(11.47, 10.18) * mm});
            skLineSegment(sketch, "E13511", {"start": v(11.47, 10.18) * mm, "end": v(10.4, 10.36) * mm});
            skLineSegment(sketch, "E13512", {"start": v(10.4, 10.36) * mm, "end": v(10.4, 9.69) * mm});
            skLineSegment(sketch, "E13513", {"start": v(10.4, 9.69) * mm, "end": v(10.4, 9.54) * mm});
            skLineSegment(sketch, "E13514", {"start": v(10.4, 9.54) * mm, "end": v(10.37, 9.38) * mm});
            skLineSegment(sketch, "E13515", {"start": v(10.37, 9.38) * mm, "end": v(10.34, 9.2) * mm});
            skLineSegment(sketch, "E13516", {"start": v(10.34, 9.2) * mm, "end": v(10.3, 9.03) * mm});
            skLineSegment(sketch, "E13517", {"start": v(10.3, 9.03) * mm, "end": v(10.25, 8.86) * mm});
            skLineSegment(sketch, "E13518", {"start": v(10.25, 8.86) * mm, "end": v(10.2, 8.69) * mm});
            skLineSegment(sketch, "E13519", {"start": v(10.2, 8.69) * mm, "end": v(10.13, 8.53) * mm});
            skLineSegment(sketch, "E13520", {"start": v(10.13, 8.53) * mm, "end": v(10.07, 8.4) * mm});
            skLineSegment(sketch, "E13521", {"start": v(10.07, 8.4) * mm, "end": v(9.73, 7.77) * mm});
            skLineSegment(sketch, "E13522", {"start": v(9.73, 7.77) * mm, "end": v(10.97, 7.43) * mm});
            skLineSegment(sketch, "E13523", {"start": v(10.97, 7.43) * mm, "end": v(11.54, 7.27) * mm});
            skLineSegment(sketch, "E13524", {"start": v(11.54, 7.27) * mm, "end": v(12, 7.17) * mm});
            skLineSegment(sketch, "E13525", {"start": v(12, 7.17) * mm, "end": v(12.2, 7.14) * mm});
            skLineSegment(sketch, "E13526", {"start": v(12.2, 7.14) * mm, "end": v(12.37, 7.11) * mm});
            skLineSegment(sketch, "E13527", {"start": v(12.37, 7.11) * mm, "end": v(12.52, 7.1) * mm});
            skLineSegment(sketch, "E13528", {"start": v(12.52, 7.1) * mm, "end": v(12.65, 7.11) * mm});
            skLineSegment(sketch, "E13529", {"start": v(12.65, 7.11) * mm, "end": v(12.77, 7.13) * mm});
            skLineSegment(sketch, "E13530", {"start": v(12.77, 7.13) * mm, "end": v(12.88, 7.16) * mm});
            skLineSegment(sketch, "E13531", {"start": v(12.88, 7.16) * mm, "end": v(12.97, 7.2) * mm});
            skLineSegment(sketch, "E13532", {"start": v(12.97, 7.2) * mm, "end": v(13.06, 7.27) * mm});
            skLineSegment(sketch, "E13533", {"start": v(13.06, 7.27) * mm, "end": v(13.14, 7.34) * mm});
            skLineSegment(sketch, "E13534", {"start": v(13.14, 7.34) * mm, "end": v(13.22, 7.43) * mm});
            skLineSegment(sketch, "E13535", {"start": v(13.22, 7.43) * mm, "end": v(13.3, 7.54) * mm});
            skLineSegment(sketch, "E13536", {"start": v(13.3, 7.54) * mm, "end": v(13.36, 7.66) * mm});
            skLineSegment(sketch, "E13537", {"start": v(13.36, 7.66) * mm, "end": v(13.4, 7.75) * mm});
            skLineSegment(sketch, "E13538", {"start": v(13.4, 7.75) * mm, "end": v(13.44, 7.85) * mm});
            skLineSegment(sketch, "E13539", {"start": v(13.44, 7.85) * mm, "end": v(13.46, 7.98) * mm});
            skLineSegment(sketch, "E13540", {"start": v(13.46, 7.98) * mm, "end": v(13.48, 8.13) * mm});
            skLineSegment(sketch, "E13541", {"start": v(13.48, 8.13) * mm, "end": v(13.5, 8.44) * mm});
            skLineSegment(sketch, "E13542", {"start": v(13.5, 8.44) * mm, "end": v(13.5, 8.77) * mm});
            skLineSegment(sketch, "E13543", {"start": v(13.5, 8.77) * mm, "end": v(13.49, 9.1) * mm});
            skLineSegment(sketch, "E13544", {"start": v(13.49, 9.1) * mm, "end": v(13.46, 9.39) * mm});
            skLineSegment(sketch, "E13545", {"start": v(13.46, 9.39) * mm, "end": v(13.42, 9.6) * mm});
            skLineSegment(sketch, "E13546", {"start": v(13.42, 9.6) * mm, "end": v(13.4, 9.69) * mm});
            skLineSegment(sketch, "E13547", {"start": v(13.4, 9.69) * mm, "end": v(13.37, 9.74) * mm});
            skLineSegment(sketch, "E13548", {"start": v(16.24, 12.46) * mm, "end": v(15.64, 12.54) * mm});
            skLineSegment(sketch, "E13549", {"start": v(15.64, 12.54) * mm, "end": v(15.01, 12.6) * mm});
            skLineSegment(sketch, "E13550", {"start": v(15.01, 12.6) * mm, "end": v(14.4, 12.65) * mm});
            skLineSegment(sketch, "E13551", {"start": v(14.4, 12.65) * mm, "end": v(13.83, 12.67) * mm});
            skLineSegment(sketch, "E13552", {"start": v(13.83, 12.67) * mm, "end": v(13.86, 10.05) * mm});
            skLineSegment(sketch, "E13553", {"start": v(13.86, 10.05) * mm, "end": v(14.12, 9.95) * mm});
            skLineSegment(sketch, "E13554", {"start": v(14.12, 9.95) * mm, "end": v(14.38, 9.84) * mm});
            skLineSegment(sketch, "E13555", {"start": v(14.38, 9.84) * mm, "end": v(14.65, 9.72) * mm});
            skLineSegment(sketch, "E13556", {"start": v(14.65, 9.72) * mm, "end": v(14.93, 9.6) * mm});
            skLineSegment(sketch, "E13557", {"start": v(14.93, 9.6) * mm, "end": v(15.21, 9.5) * mm});
            skLineSegment(sketch, "E13558", {"start": v(15.21, 9.5) * mm, "end": v(15.35, 9.46) * mm});
            skLineSegment(sketch, "E13559", {"start": v(15.35, 9.46) * mm, "end": v(15.49, 9.43) * mm});
            skLineSegment(sketch, "E13560", {"start": v(15.49, 9.43) * mm, "end": v(15.62, 9.4) * mm});
            skLineSegment(sketch, "E13561", {"start": v(15.62, 9.4) * mm, "end": v(15.76, 9.4) * mm});
            skLineSegment(sketch, "E13562", {"start": v(15.76, 9.4) * mm, "end": v(15.89, 9.4) * mm});
            skLineSegment(sketch, "E13563", {"start": v(15.89, 9.4) * mm, "end": v(16.02, 9.42) * mm});
            skLineSegment(sketch, "E13564", {"start": v(16.02, 9.42) * mm, "end": v(16.14, 9.44) * mm});
            skLineSegment(sketch, "E13565", {"start": v(16.14, 9.44) * mm, "end": v(16.24, 9.48) * mm});
            skLineSegment(sketch, "E13566", {"start": v(16.24, 9.48) * mm, "end": v(16.32, 9.52) * mm});
            skLineSegment(sketch, "E13567", {"start": v(16.32, 9.52) * mm, "end": v(16.39, 9.57) * mm});
            skLineSegment(sketch, "E13568", {"start": v(16.39, 9.57) * mm, "end": v(16.53, 9.69) * mm});
            skLineSegment(sketch, "E13569", {"start": v(16.53, 9.69) * mm, "end": v(16.7, 9.84) * mm});
            skLineSegment(sketch, "E13570", {"start": v(16.7, 9.84) * mm, "end": v(16.74, 9.87) * mm});
            skLineSegment(sketch, "E13571", {"start": v(16.74, 9.87) * mm, "end": v(16.77, 9.91) * mm});
            skLineSegment(sketch, "E13572", {"start": v(16.77, 9.91) * mm, "end": v(16.82, 10.03) * mm});
            skLineSegment(sketch, "E13573", {"start": v(16.82, 10.03) * mm, "end": v(16.84, 10.18) * mm});
            skLineSegment(sketch, "E13574", {"start": v(16.84, 10.18) * mm, "end": v(16.85, 10.36) * mm});
            skLineSegment(sketch, "E13575", {"start": v(16.85, 10.36) * mm, "end": v(16.85, 10.56) * mm});
            skLineSegment(sketch, "E13576", {"start": v(16.85, 10.56) * mm, "end": v(16.83, 10.78) * mm});
            skLineSegment(sketch, "E13577", {"start": v(16.83, 10.78) * mm, "end": v(16.8, 11) * mm});
            skLineSegment(sketch, "E13578", {"start": v(16.8, 11) * mm, "end": v(16.75, 11.24) * mm});
            skLineSegment(sketch, "E13579", {"start": v(16.75, 11.24) * mm, "end": v(16.7, 11.46) * mm});
            skLineSegment(sketch, "E13580", {"start": v(16.7, 11.46) * mm, "end": v(16.65, 11.68) * mm});
            skLineSegment(sketch, "E13581", {"start": v(16.65, 11.68) * mm, "end": v(16.58, 11.89) * mm});
            skLineSegment(sketch, "E13582", {"start": v(16.58, 11.89) * mm, "end": v(16.52, 12.07) * mm});
            skLineSegment(sketch, "E13583", {"start": v(16.52, 12.07) * mm, "end": v(16.45, 12.22) * mm});
            skLineSegment(sketch, "E13584", {"start": v(16.45, 12.22) * mm, "end": v(16.38, 12.34) * mm});
            skLineSegment(sketch, "E13585", {"start": v(16.38, 12.34) * mm, "end": v(16.31, 12.42) * mm});
            skLineSegment(sketch, "E13586", {"start": v(16.31, 12.42) * mm, "end": v(16.28, 12.45) * mm});
            skLineSegment(sketch, "E13587", {"start": v(16.28, 12.45) * mm, "end": v(16.24, 12.46) * mm});
            skLineSegment(sketch, "E13588", {"start": v(16.85, 9.4) * mm, "end": v(16.79, 9.33) * mm});
            skLineSegment(sketch, "E13589", {"start": v(16.79, 9.33) * mm, "end": v(16.73, 9.28) * mm});
            skLineSegment(sketch, "E13590", {"start": v(16.73, 9.28) * mm, "end": v(16.65, 9.23) * mm});
            skLineSegment(sketch, "E13591", {"start": v(16.65, 9.23) * mm, "end": v(16.58, 9.18) * mm});
            skLineSegment(sketch, "E13592", {"start": v(16.58, 9.18) * mm, "end": v(16.41, 9.11) * mm});
            skLineSegment(sketch, "E13593", {"start": v(16.41, 9.11) * mm, "end": v(16.23, 9.06) * mm});
            skLineSegment(sketch, "E13594", {"start": v(16.23, 9.06) * mm, "end": v(16.05, 9.03) * mm});
            skLineSegment(sketch, "E13595", {"start": v(16.05, 9.03) * mm, "end": v(15.86, 9.02) * mm});
            skLineSegment(sketch, "E13596", {"start": v(15.86, 9.02) * mm, "end": v(15.67, 9.02) * mm});
            skLineSegment(sketch, "E13597", {"start": v(15.67, 9.02) * mm, "end": v(15.49, 9.02) * mm});
            skLineSegment(sketch, "E13598", {"start": v(15.49, 9.02) * mm, "end": v(15.38, 9.03) * mm});
            skLineSegment(sketch, "E13599", {"start": v(15.38, 9.03) * mm, "end": v(15.27, 9.06) * mm});
            skLineSegment(sketch, "E13600", {"start": v(15.27, 9.06) * mm, "end": v(15.03, 9.12) * mm});
            skLineSegment(sketch, "E13601", {"start": v(15.03, 9.12) * mm, "end": v(14.54, 9.29) * mm});
            skLineSegment(sketch, "E13602", {"start": v(14.54, 9.29) * mm, "end": v(14.31, 9.37) * mm});
            skLineSegment(sketch, "E13603", {"start": v(14.31, 9.37) * mm, "end": v(14.11, 9.42) * mm});
            skLineSegment(sketch, "E13604", {"start": v(14.11, 9.42) * mm, "end": v(14.02, 9.44) * mm});
            skLineSegment(sketch, "E13605", {"start": v(14.02, 9.44) * mm, "end": v(13.94, 9.44) * mm});
            skLineSegment(sketch, "E13606", {"start": v(13.94, 9.44) * mm, "end": v(13.87, 9.44) * mm});
            skLineSegment(sketch, "E13607", {"start": v(13.87, 9.44) * mm, "end": v(13.82, 9.42) * mm});
            skLineSegment(sketch, "E13608", {"start": v(13.82, 9.42) * mm, "end": v(13.78, 9.39) * mm});
            skLineSegment(sketch, "E13609", {"start": v(13.78, 9.39) * mm, "end": v(13.76, 9.35) * mm});
            skLineSegment(sketch, "E13610", {"start": v(13.76, 9.35) * mm, "end": v(13.75, 9.3) * mm});
            skLineSegment(sketch, "E13611", {"start": v(13.75, 9.3) * mm, "end": v(13.75, 9.25) * mm});
            skLineSegment(sketch, "E13612", {"start": v(13.75, 9.25) * mm, "end": v(13.77, 9.11) * mm});
            skLineSegment(sketch, "E13613", {"start": v(13.77, 9.11) * mm, "end": v(13.8, 8.96) * mm});
            skLineSegment(sketch, "E13614", {"start": v(13.8, 8.96) * mm, "end": v(13.92, 8.6) * mm});
            skLineSegment(sketch, "E13615", {"start": v(13.92, 8.6) * mm, "end": v(13.96, 8.4) * mm});
            skLineSegment(sketch, "E13616", {"start": v(13.96, 8.4) * mm, "end": v(14, 8.21) * mm});
            skLineSegment(sketch, "E13617", {"start": v(14, 8.21) * mm, "end": v(14, 8.05) * mm});
            skLineSegment(sketch, "E13618", {"start": v(14, 8.05) * mm, "end": v(13.99, 7.88) * mm});
            skLineSegment(sketch, "E13619", {"start": v(13.99, 7.88) * mm, "end": v(13.95, 7.72) * mm});
            skLineSegment(sketch, "E13620", {"start": v(13.95, 7.72) * mm, "end": v(13.9, 7.56) * mm});
            skLineSegment(sketch, "E13621", {"start": v(13.9, 7.56) * mm, "end": v(13.83, 7.4) * mm});
            skLineSegment(sketch, "E13622", {"start": v(13.83, 7.4) * mm, "end": v(13.74, 7.23) * mm});
            skLineSegment(sketch, "E13623", {"start": v(13.74, 7.23) * mm, "end": v(13.63, 7.07) * mm});
            skLineSegment(sketch, "E13624", {"start": v(13.63, 7.07) * mm, "end": v(13.5, 6.91) * mm});
            skLineSegment(sketch, "E13625", {"start": v(13.5, 6.91) * mm, "end": v(13.3, 6.88) * mm});
            skLineSegment(sketch, "E13626", {"start": v(13.3, 6.88) * mm, "end": v(13.1, 6.85) * mm});
            skLineSegment(sketch, "E13627", {"start": v(13.1, 6.85) * mm, "end": v(12.89, 6.83) * mm});
            skLineSegment(sketch, "E13628", {"start": v(12.89, 6.83) * mm, "end": v(12.68, 6.82) * mm});
            skLineSegment(sketch, "E13629", {"start": v(12.68, 6.82) * mm, "end": v(12.25, 6.83) * mm});
            skLineSegment(sketch, "E13630", {"start": v(12.25, 6.83) * mm, "end": v(11.81, 6.86) * mm});
            skLineSegment(sketch, "E13631", {"start": v(11.81, 6.86) * mm, "end": v(10.96, 6.95) * mm});
            skLineSegment(sketch, "E13632", {"start": v(10.96, 6.95) * mm, "end": v(10.15, 7.05) * mm});
            skLineSegment(sketch, "E13633", {"start": v(10.15, 7.05) * mm, "end": v(10.05, 6.57) * mm});
            skLineSegment(sketch, "E13634", {"start": v(10.05, 6.57) * mm, "end": v(10, 6.3) * mm});
            skLineSegment(sketch, "E13635", {"start": v(10, 6.3) * mm, "end": v(9.93, 6.04) * mm});
            skLineSegment(sketch, "E13636", {"start": v(9.93, 6.04) * mm, "end": v(9.85, 5.78) * mm});
            skLineSegment(sketch, "E13637", {"start": v(9.85, 5.78) * mm, "end": v(9.75, 5.54) * mm});
            skLineSegment(sketch, "E13638", {"start": v(9.75, 5.54) * mm, "end": v(9.7, 5.42) * mm});
            skLineSegment(sketch, "E13639", {"start": v(9.7, 5.42) * mm, "end": v(9.64, 5.32) * mm});
            skLineSegment(sketch, "E13640", {"start": v(9.64, 5.32) * mm, "end": v(9.58, 5.22) * mm});
            skLineSegment(sketch, "E13641", {"start": v(9.58, 5.22) * mm, "end": v(9.5, 5.13) * mm});
            skLineSegment(sketch, "E13642", {"start": v(9.5, 5.13) * mm, "end": v(9.44, 5.05) * mm});
            skLineSegment(sketch, "E13643", {"start": v(9.44, 5.05) * mm, "end": v(9.36, 4.98) * mm});
            skLineSegment(sketch, "E13644", {"start": v(9.36, 4.98) * mm, "end": v(9.27, 4.92) * mm});
            skLineSegment(sketch, "E13645", {"start": v(9.27, 4.92) * mm, "end": v(9.18, 4.87) * mm});
            skLineSegment(sketch, "E13646", {"start": v(9.18, 4.87) * mm, "end": v(8.98, 4.78) * mm});
            skLineSegment(sketch, "E13647", {"start": v(8.98, 4.78) * mm, "end": v(8.77, 4.72) * mm});
            skLineSegment(sketch, "E13648", {"start": v(8.77, 4.72) * mm, "end": v(8.55, 4.67) * mm});
            skLineSegment(sketch, "E13649", {"start": v(8.55, 4.67) * mm, "end": v(8.32, 4.65) * mm});
            skLineSegment(sketch, "E13650", {"start": v(8.32, 4.65) * mm, "end": v(8.1, 4.63) * mm});
            skLineSegment(sketch, "E13651", {"start": v(8.1, 4.63) * mm, "end": v(7.89, 4.63) * mm});
            skLineSegment(sketch, "E13652", {"start": v(7.89, 4.63) * mm, "end": v(7.71, 4.65) * mm});
            skLineSegment(sketch, "E13653", {"start": v(7.71, 4.65) * mm, "end": v(7.54, 4.67) * mm});
            skLineSegment(sketch, "E13654", {"start": v(7.54, 4.67) * mm, "end": v(7.36, 4.7) * mm});
            skLineSegment(sketch, "E13655", {"start": v(7.36, 4.7) * mm, "end": v(7.18, 4.75) * mm});
            skLineSegment(sketch, "E13656", {"start": v(7.18, 4.75) * mm, "end": v(6.82, 4.87) * mm});
            skLineSegment(sketch, "E13657", {"start": v(6.82, 4.87) * mm, "end": v(6.47, 5.01) * mm});
            skLineSegment(sketch, "E13658", {"start": v(6.47, 5.01) * mm, "end": v(6.13, 5.17) * mm});
            skLineSegment(sketch, "E13659", {"start": v(6.13, 5.17) * mm, "end": v(5.8, 5.35) * mm});
            skLineSegment(sketch, "E13660", {"start": v(5.8, 5.35) * mm, "end": v(5.22, 5.68) * mm});
            skLineSegment(sketch, "E13661", {"start": v(5.22, 5.68) * mm, "end": v(5.02, 5.4) * mm});
            skLineSegment(sketch, "E13662", {"start": v(5.02, 5.4) * mm, "end": v(4.82, 5.1) * mm});
            skLineSegment(sketch, "E13663", {"start": v(4.82, 5.1) * mm, "end": v(4.63, 4.78) * mm});
            skLineSegment(sketch, "E13664", {"start": v(4.63, 4.78) * mm, "end": v(4.42, 4.45) * mm});
            skLineSegment(sketch, "E13665", {"start": v(4.42, 4.45) * mm, "end": v(4.2, 4.14) * mm});
            skLineSegment(sketch, "E13666", {"start": v(4.2, 4.14) * mm, "end": v(4.09, 4) * mm});
            skLineSegment(sketch, "E13667", {"start": v(4.09, 4) * mm, "end": v(3.97, 3.86) * mm});
            skLineSegment(sketch, "E13668", {"start": v(3.97, 3.86) * mm, "end": v(3.85, 3.74) * mm});
            skLineSegment(sketch, "E13669", {"start": v(3.85, 3.74) * mm, "end": v(3.72, 3.62) * mm});
            skLineSegment(sketch, "E13670", {"start": v(3.72, 3.62) * mm, "end": v(3.58, 3.53) * mm});
            skLineSegment(sketch, "E13671", {"start": v(3.58, 3.53) * mm, "end": v(3.44, 3.45) * mm});
            skLineSegment(sketch, "E13672", {"start": v(3.44, 3.45) * mm, "end": v(3.37, 3.43) * mm});
            skLineSegment(sketch, "E13673", {"start": v(3.37, 3.43) * mm, "end": v(3.3, 3.42) * mm});
            skLineSegment(sketch, "E13674", {"start": v(3.3, 3.42) * mm, "end": v(3.13, 3.42) * mm});
            skLineSegment(sketch, "E13675", {"start": v(3.13, 3.42) * mm, "end": v(2.97, 3.44) * mm});
            skLineSegment(sketch, "E13676", {"start": v(2.97, 3.44) * mm, "end": v(2.81, 3.45) * mm});
            skLineSegment(sketch, "E13677", {"start": v(2.81, 3.45) * mm, "end": v(2.67, 3.46) * mm});
            skLineSegment(sketch, "E13678", {"start": v(2.67, 3.46) * mm, "end": v(2.5, 3.49) * mm});
            skLineSegment(sketch, "E13679", {"start": v(2.5, 3.49) * mm, "end": v(2.32, 3.53) * mm});
            skLineSegment(sketch, "E13680", {"start": v(2.32, 3.53) * mm, "end": v(2.13, 3.58) * mm});
            skLineSegment(sketch, "E13681", {"start": v(2.13, 3.58) * mm, "end": v(1.96, 3.65) * mm});
            skLineSegment(sketch, "E13682", {"start": v(1.96, 3.65) * mm, "end": v(1.8, 3.72) * mm});
            skLineSegment(sketch, "E13683", {"start": v(1.8, 3.72) * mm, "end": v(1.7, 3.79) * mm});
            skLineSegment(sketch, "E13684", {"start": v(1.7, 3.79) * mm, "end": v(1.65, 3.82) * mm});
            skLineSegment(sketch, "E13685", {"start": v(1.65, 3.82) * mm, "end": v(1.63, 3.85) * mm});
            skLineSegment(sketch, "E13686", {"start": v(1.63, 3.85) * mm, "end": v(1.56, 3.98) * mm});
            skLineSegment(sketch, "E13687", {"start": v(1.56, 3.98) * mm, "end": v(1.5, 4.11) * mm});
            skLineSegment(sketch, "E13688", {"start": v(1.5, 4.11) * mm, "end": v(1.4, 4.4) * mm});
            skLineSegment(sketch, "E13689", {"start": v(1.4, 4.4) * mm, "end": v(1.32, 4.71) * mm});
            skLineSegment(sketch, "E13690", {"start": v(1.32, 4.71) * mm, "end": v(1.25, 5.01) * mm});
            skLineSegment(sketch, "E13691", {"start": v(1.25, 5.01) * mm, "end": v(1.2, 5.29) * mm});
            skLineSegment(sketch, "E13692", {"start": v(1.2, 5.29) * mm, "end": v(1.14, 5.51) * mm});
            skLineSegment(sketch, "E13693", {"start": v(1.14, 5.51) * mm, "end": v(1.11, 5.6) * mm});
            skLineSegment(sketch, "E13694", {"start": v(1.11, 5.6) * mm, "end": v(1.08, 5.67) * mm});
            skLineSegment(sketch, "E13695", {"start": v(1.08, 5.67) * mm, "end": v(1.05, 5.72) * mm});
            skLineSegment(sketch, "E13696", {"start": v(1.05, 5.72) * mm, "end": v(1, 5.75) * mm});
            skLineSegment(sketch, "E13697", {"start": v(1, 5.75) * mm, "end": v(0.94, 5.75) * mm});
            skLineSegment(sketch, "E13698", {"start": v(0.94, 5.75) * mm, "end": v(0.88, 5.74) * mm});
            skLineSegment(sketch, "E13699", {"start": v(0.88, 5.74) * mm, "end": v(0.83, 5.72) * mm});
            skLineSegment(sketch, "E13700", {"start": v(0.83, 5.72) * mm, "end": v(0.78, 5.68) * mm});
            skLineSegment(sketch, "E13701", {"start": v(0.78, 5.68) * mm, "end": v(0.73, 5.62) * mm});
            skLineSegment(sketch, "E13702", {"start": v(0.73, 5.62) * mm, "end": v(0.68, 5.56) * mm});
            skLineSegment(sketch, "E13703", {"start": v(0.68, 5.56) * mm, "end": v(0.6, 5.41) * mm});
            skLineSegment(sketch, "E13704", {"start": v(0.6, 5.41) * mm, "end": v(0.45, 5.07) * mm});
            skLineSegment(sketch, "E13705", {"start": v(0.45, 5.07) * mm, "end": v(0.38, 4.9) * mm});
            skLineSegment(sketch, "E13706", {"start": v(0.38, 4.9) * mm, "end": v(0.32, 4.77) * mm});
            skLineSegment(sketch, "E13707", {"start": v(0.32, 4.77) * mm, "end": v(0.05, 4.32) * mm});
            skLineSegment(sketch, "E13708", {"start": v(0.05, 4.32) * mm, "end": v(-0.08, 4.1) * mm});
            skLineSegment(sketch, "E13709", {"start": v(-0.08, 4.1) * mm, "end": v(-0.21, 3.9) * mm});
            skLineSegment(sketch, "E13710", {"start": v(-0.21, 3.9) * mm, "end": v(-0.34, 3.72) * mm});
            skLineSegment(sketch, "E13711", {"start": v(-0.34, 3.72) * mm, "end": v(-0.47, 3.57) * mm});
            skLineSegment(sketch, "E13712", {"start": v(-0.47, 3.57) * mm, "end": v(-0.6, 3.45) * mm});
            skLineSegment(sketch, "E13713", {"start": v(-0.6, 3.45) * mm, "end": v(-0.67, 3.4) * mm});
            skLineSegment(sketch, "E13714", {"start": v(-0.67, 3.4) * mm, "end": v(-0.74, 3.36) * mm});
            skLineSegment(sketch, "E13715", {"start": v(-0.74, 3.36) * mm, "end": v(-0.9, 3.28) * mm});
            skLineSegment(sketch, "E13716", {"start": v(-0.9, 3.28) * mm, "end": v(-1.1, 3.22) * mm});
            skLineSegment(sketch, "E13717", {"start": v(-1.1, 3.22) * mm, "end": v(-1.3, 3.18) * mm});
            skLineSegment(sketch, "E13718", {"start": v(-1.3, 3.18) * mm, "end": v(-1.5, 3.16) * mm});
            skLineSegment(sketch, "E13719", {"start": v(-1.5, 3.16) * mm, "end": v(-1.57, 3.17) * mm});
            skLineSegment(sketch, "E13720", {"start": v(-1.57, 3.17) * mm, "end": v(-1.65, 3.18) * mm});
            skLineSegment(sketch, "E13721", {"start": v(-1.65, 3.18) * mm, "end": v(-1.8, 3.23) * mm});
            skLineSegment(sketch, "E13722", {"start": v(-1.8, 3.23) * mm, "end": v(-1.95, 3.3) * mm});
            skLineSegment(sketch, "E13723", {"start": v(-1.95, 3.3) * mm, "end": v(-2.09, 3.4) * mm});
            skLineSegment(sketch, "E13724", {"start": v(-2.09, 3.4) * mm, "end": v(-2.22, 3.5) * mm});
            skLineSegment(sketch, "E13725", {"start": v(-2.22, 3.5) * mm, "end": v(-2.34, 3.62) * mm});
            skLineSegment(sketch, "E13726", {"start": v(-2.34, 3.62) * mm, "end": v(-2.57, 3.86) * mm});
            skLineSegment(sketch, "E13727", {"start": v(-2.57, 3.86) * mm, "end": v(-2.72, 4.06) * mm});
            skLineSegment(sketch, "E13728", {"start": v(-2.72, 4.06) * mm, "end": v(-2.85, 4.29) * mm});
            skLineSegment(sketch, "E13729", {"start": v(-2.85, 4.29) * mm, "end": v(-2.97, 4.53) * mm});
            skLineSegment(sketch, "E13730", {"start": v(-2.97, 4.53) * mm, "end": v(-3.08, 4.78) * mm});
            skLineSegment(sketch, "E13731", {"start": v(-3.08, 4.78) * mm, "end": v(-3.27, 5.3) * mm});
            skLineSegment(sketch, "E13732", {"start": v(-3.27, 5.3) * mm, "end": v(-3.44, 5.79) * mm});
            skLineSegment(sketch, "E13733", {"start": v(-3.44, 5.79) * mm, "end": v(-3.9, 5.52) * mm});
            skLineSegment(sketch, "E13734", {"start": v(-3.9, 5.52) * mm, "end": v(-4.4, 5.22) * mm});
            skLineSegment(sketch, "E13735", {"start": v(-4.4, 5.22) * mm, "end": v(-4.66, 5.08) * mm});
            skLineSegment(sketch, "E13736", {"start": v(-4.66, 5.08) * mm, "end": v(-4.9, 4.95) * mm});
            skLineSegment(sketch, "E13737", {"start": v(-4.9, 4.95) * mm, "end": v(-5.16, 4.85) * mm});
            skLineSegment(sketch, "E13738", {"start": v(-5.16, 4.85) * mm, "end": v(-5.29, 4.8) * mm});
            skLineSegment(sketch, "E13739", {"start": v(-5.29, 4.8) * mm, "end": v(-5.4, 4.77) * mm});
            skLineSegment(sketch, "E13740", {"start": v(-5.4, 4.77) * mm, "end": v(-5.63, 4.72) * mm});
            skLineSegment(sketch, "E13741", {"start": v(-5.63, 4.72) * mm, "end": v(-5.87, 4.69) * mm});
            skLineSegment(sketch, "E13742", {"start": v(-5.87, 4.69) * mm, "end": v(-6.11, 4.66) * mm});
            skLineSegment(sketch, "E13743", {"start": v(-6.11, 4.66) * mm, "end": v(-6.36, 4.66) * mm});
            skLineSegment(sketch, "E13744", {"start": v(-6.36, 4.66) * mm, "end": v(-6.61, 4.67) * mm});
            skLineSegment(sketch, "E13745", {"start": v(-6.61, 4.67) * mm, "end": v(-6.85, 4.7) * mm});
            skLineSegment(sketch, "E13746", {"start": v(-6.85, 4.7) * mm, "end": v(-7.08, 4.75) * mm});
            skLineSegment(sketch, "E13747", {"start": v(-7.08, 4.75) * mm, "end": v(-7.19, 4.8) * mm});
            skLineSegment(sketch, "E13748", {"start": v(-7.19, 4.8) * mm, "end": v(-7.3, 4.83) * mm});
            skLineSegment(sketch, "E13749", {"start": v(-7.3, 4.83) * mm, "end": v(-7.44, 4.9) * mm});
            skLineSegment(sketch, "E13750", {"start": v(-7.44, 4.9) * mm, "end": v(-7.6, 5) * mm});
            skLineSegment(sketch, "E13751", {"start": v(-7.6, 5) * mm, "end": v(-7.75, 5.1) * mm});
            skLineSegment(sketch, "E13752", {"start": v(-7.75, 5.1) * mm, "end": v(-7.9, 5.22) * mm});
            skLineSegment(sketch, "E13753", {"start": v(-7.9, 5.22) * mm, "end": v(-8.04, 5.34) * mm});
            skLineSegment(sketch, "E13754", {"start": v(-8.04, 5.34) * mm, "end": v(-8.17, 5.47) * mm});
            skLineSegment(sketch, "E13755", {"start": v(-8.17, 5.47) * mm, "end": v(-8.28, 5.6) * mm});
            skLineSegment(sketch, "E13756", {"start": v(-8.28, 5.6) * mm, "end": v(-8.37, 5.75) * mm});
            skLineSegment(sketch, "E13757", {"start": v(-8.37, 5.75) * mm, "end": v(-8.42, 5.84) * mm});
            skLineSegment(sketch, "E13758", {"start": v(-8.42, 5.84) * mm, "end": v(-8.45, 5.96) * mm});
            skLineSegment(sketch, "E13759", {"start": v(-8.45, 5.96) * mm, "end": v(-8.5, 6.21) * mm});
            skLineSegment(sketch, "E13760", {"start": v(-8.5, 6.21) * mm, "end": v(-8.53, 6.5) * mm});
            skLineSegment(sketch, "E13761", {"start": v(-8.53, 6.5) * mm, "end": v(-8.56, 6.77) * mm});
            skLineSegment(sketch, "E13762", {"start": v(-8.56, 6.77) * mm, "end": v(-8.6, 7.01) * mm});
            skLineSegment(sketch, "E13763", {"start": v(-8.6, 7.01) * mm, "end": v(-8.62, 7.12) * mm});
            skLineSegment(sketch, "E13764", {"start": v(-8.62, 7.12) * mm, "end": v(-8.66, 7.2) * mm});
            skLineSegment(sketch, "E13765", {"start": v(-8.66, 7.2) * mm, "end": v(-8.7, 7.26) * mm});
            skLineSegment(sketch, "E13766", {"start": v(-8.7, 7.26) * mm, "end": v(-8.76, 7.3) * mm});
            skLineSegment(sketch, "E13767", {"start": v(-8.76, 7.3) * mm, "end": v(-8.8, 7.31) * mm});
            skLineSegment(sketch, "E13768", {"start": v(-8.8, 7.31) * mm, "end": v(-8.83, 7.31) * mm});
            skLineSegment(sketch, "E13769", {"start": v(-8.83, 7.31) * mm, "end": v(-8.92, 7.3) * mm});
            skLineSegment(sketch, "E13770", {"start": v(-8.92, 7.3) * mm, "end": v(-9.15, 7.23) * mm});
            skLineSegment(sketch, "E13771", {"start": v(-9.15, 7.23) * mm, "end": v(-9.28, 7.2) * mm});
            skLineSegment(sketch, "E13772", {"start": v(-9.28, 7.2) * mm, "end": v(-9.39, 7.16) * mm});
            skLineSegment(sketch, "E13773", {"start": v(-9.39, 7.16) * mm, "end": v(-9.58, 7.1) * mm});
            skLineSegment(sketch, "E13774", {"start": v(-9.58, 7.1) * mm, "end": v(-9.8, 7.04) * mm});
            skLineSegment(sketch, "E13775", {"start": v(-9.8, 7.04) * mm, "end": v(-10.5, 6.9) * mm});
            skLineSegment(sketch, "E13776", {"start": v(-10.5, 6.9) * mm, "end": v(-10.8, 6.86) * mm});
            skLineSegment(sketch, "E13777", {"start": v(-10.8, 6.86) * mm, "end": v(-10.96, 6.84) * mm});
            skLineSegment(sketch, "E13778", {"start": v(-10.96, 6.84) * mm, "end": v(-11.12, 6.84) * mm});
            skLineSegment(sketch, "E13779", {"start": v(-11.12, 6.84) * mm, "end": v(-11.29, 6.84) * mm});
            skLineSegment(sketch, "E13780", {"start": v(-11.29, 6.84) * mm, "end": v(-11.45, 6.85) * mm});
            skLineSegment(sketch, "E13781", {"start": v(-11.45, 6.85) * mm, "end": v(-11.6, 6.87) * mm});
            skLineSegment(sketch, "E13782", {"start": v(-11.6, 6.87) * mm, "end": v(-11.73, 6.9) * mm});
            skLineSegment(sketch, "E13783", {"start": v(-11.73, 6.9) * mm, "end": v(-11.82, 6.95) * mm});
            skLineSegment(sketch, "E13784", {"start": v(-11.82, 6.95) * mm, "end": v(-11.9, 7) * mm});
            skLineSegment(sketch, "E13785", {"start": v(-11.9, 7) * mm, "end": v(-11.97, 7.05) * mm});
            skLineSegment(sketch, "E13786", {"start": v(-11.97, 7.05) * mm, "end": v(-12.03, 7.1) * mm});
            skLineSegment(sketch, "E13787", {"start": v(-12.03, 7.1) * mm, "end": v(-12.09, 7.18) * mm});
            skLineSegment(sketch, "E13788", {"start": v(-12.09, 7.18) * mm, "end": v(-12.14, 7.25) * mm});
            skLineSegment(sketch, "E13789", {"start": v(-12.14, 7.25) * mm, "end": v(-12.23, 7.41) * mm});
            skLineSegment(sketch, "E13790", {"start": v(-12.23, 7.41) * mm, "end": v(-12.3, 7.6) * mm});
            skLineSegment(sketch, "E13791", {"start": v(-12.3, 7.6) * mm, "end": v(-12.36, 7.78) * mm});
            skLineSegment(sketch, "E13792", {"start": v(-12.36, 7.78) * mm, "end": v(-12.44, 8.15) * mm});
            skLineSegment(sketch, "E13793", {"start": v(-12.44, 8.15) * mm, "end": v(-12.45, 8.27) * mm});
            skLineSegment(sketch, "E13794", {"start": v(-12.45, 8.27) * mm, "end": v(-12.45, 8.4) * mm});
            skLineSegment(sketch, "E13795", {"start": v(-12.45, 8.4) * mm, "end": v(-12.44, 8.51) * mm});
            skLineSegment(sketch, "E13796", {"start": v(-12.44, 8.51) * mm, "end": v(-12.42, 8.64) * mm});
            skLineSegment(sketch, "E13797", {"start": v(-12.42, 8.64) * mm, "end": v(-12.36, 8.89) * mm});
            skLineSegment(sketch, "E13798", {"start": v(-12.36, 8.89) * mm, "end": v(-12.28, 9.12) * mm});
            skLineSegment(sketch, "E13799", {"start": v(-12.28, 9.12) * mm, "end": v(-12.2, 9.34) * mm});
            skLineSegment(sketch, "E13800", {"start": v(-12.2, 9.34) * mm, "end": v(-12.15, 9.53) * mm});
            skLineSegment(sketch, "E13801", {"start": v(-12.15, 9.53) * mm, "end": v(-12.13, 9.6) * mm});
            skLineSegment(sketch, "E13802", {"start": v(-12.13, 9.6) * mm, "end": v(-12.12, 9.68) * mm});
            skLineSegment(sketch, "E13803", {"start": v(-12.12, 9.68) * mm, "end": v(-12.12, 9.74) * mm});
            skLineSegment(sketch, "E13804", {"start": v(-12.12, 9.74) * mm, "end": v(-12.14, 9.78) * mm});
            skLineSegment(sketch, "E13805", {"start": v(-12.14, 9.78) * mm, "end": v(-12.15, 9.79) * mm});
            skLineSegment(sketch, "E13806", {"start": v(-12.15, 9.79) * mm, "end": v(-12.19, 9.78) * mm});
            skLineSegment(sketch, "E13807", {"start": v(-12.19, 9.78) * mm, "end": v(-12.3, 9.75) * mm});
            skLineSegment(sketch, "E13808", {"start": v(-12.3, 9.75) * mm, "end": v(-12.7, 9.61) * mm});
            skLineSegment(sketch, "E13809", {"start": v(-12.7, 9.61) * mm, "end": v(-13.22, 9.43) * mm});
            skLineSegment(sketch, "E13810", {"start": v(-13.22, 9.43) * mm, "end": v(-13.52, 9.34) * mm});
            skLineSegment(sketch, "E13811", {"start": v(-13.52, 9.34) * mm, "end": v(-13.83, 9.25) * mm});
            skLineSegment(sketch, "E13812", {"start": v(-13.83, 9.25) * mm, "end": v(-14.13, 9.18) * mm});
            skLineSegment(sketch, "E13813", {"start": v(-14.13, 9.18) * mm, "end": v(-14.43, 9.12) * mm});
            skLineSegment(sketch, "E13814", {"start": v(-14.43, 9.12) * mm, "end": v(-14.7, 9.1) * mm});
            skLineSegment(sketch, "E13815", {"start": v(-14.7, 9.1) * mm, "end": v(-14.84, 9.1) * mm});
            skLineSegment(sketch, "E13816", {"start": v(-14.84, 9.1) * mm, "end": v(-14.96, 9.1) * mm});
            skLineSegment(sketch, "E13817", {"start": v(-14.96, 9.1) * mm, "end": v(-15.07, 9.12) * mm});
            skLineSegment(sketch, "E13818", {"start": v(-15.07, 9.12) * mm, "end": v(-15.17, 9.14) * mm});
            skLineSegment(sketch, "E13819", {"start": v(-15.17, 9.14) * mm, "end": v(-15.26, 9.18) * mm});
            skLineSegment(sketch, "E13820", {"start": v(-15.26, 9.18) * mm, "end": v(-15.34, 9.23) * mm});
            skLineSegment(sketch, "E13821", {"start": v(-15.34, 9.23) * mm, "end": v(-15.4, 9.3) * mm});
            skLineSegment(sketch, "E13822", {"start": v(-15.4, 9.3) * mm, "end": v(-15.46, 9.37) * mm});
            skLineSegment(sketch, "E13823", {"start": v(-15.46, 9.37) * mm, "end": v(-15.49, 9.46) * mm});
            skLineSegment(sketch, "E13824", {"start": v(-15.49, 9.46) * mm, "end": v(-15.5, 9.56) * mm});
            skLineSegment(sketch, "E13825", {"start": v(-15.5, 9.56) * mm, "end": v(-15.53, 9.88) * mm});
            skLineSegment(sketch, "E13826", {"start": v(-15.53, 9.88) * mm, "end": v(-15.57, 10.21) * mm});
            skLineSegment(sketch, "E13827", {"start": v(-15.57, 10.21) * mm, "end": v(-15.68, 10.9) * mm});
            skLineSegment(sketch, "E13828", {"start": v(-15.68, 10.9) * mm, "end": v(-15.8, 11.62) * mm});
            skLineSegment(sketch, "E13829", {"start": v(-15.8, 11.62) * mm, "end": v(-15.93, 12.34) * mm});
            skLineSegment(sketch, "E13830", {"start": v(-15.93, 12.34) * mm, "end": v(-15.99, 12.7) * mm});
            skLineSegment(sketch, "E13831", {"start": v(-15.99, 12.7) * mm, "end": v(-16.04, 13.07) * mm});
            skLineSegment(sketch, "E13832", {"start": v(-16.04, 13.07) * mm, "end": v(-16.07, 13.43) * mm});
            skLineSegment(sketch, "E13833", {"start": v(-16.07, 13.43) * mm, "end": v(-16.1, 13.78) * mm});
            skLineSegment(sketch, "E13834", {"start": v(-16.1, 13.78) * mm, "end": v(-16.1, 14.12) * mm});
            skLineSegment(sketch, "E13835", {"start": v(-16.1, 14.12) * mm, "end": v(-16.1, 14.46) * mm});
            skLineSegment(sketch, "E13836", {"start": v(-16.1, 14.46) * mm, "end": v(-16.06, 14.79) * mm});
            skLineSegment(sketch, "E13837", {"start": v(-16.06, 14.79) * mm, "end": v(-16, 15.1) * mm});
            skLineSegment(sketch, "E13838", {"start": v(-16, 15.1) * mm, "end": v(-15.97, 15.24) * mm});
            skLineSegment(sketch, "E13839", {"start": v(-15.97, 15.24) * mm, "end": v(-15.92, 15.39) * mm});
            skLineSegment(sketch, "E13840", {"start": v(-15.92, 15.39) * mm, "end": v(-15.85, 15.53) * mm});
            skLineSegment(sketch, "E13841", {"start": v(-15.85, 15.53) * mm, "end": v(-15.78, 15.68) * mm});
            skLineSegment(sketch, "E13842", {"start": v(-15.78, 15.68) * mm, "end": v(-15.62, 15.97) * mm});
            skLineSegment(sketch, "E13843", {"start": v(-15.62, 15.97) * mm, "end": v(-15.43, 16.26) * mm});
            skLineSegment(sketch, "E13844", {"start": v(-15.43, 16.26) * mm, "end": v(-15.03, 16.82) * mm});
            skLineSegment(sketch, "E13845", {"start": v(-15.03, 16.82) * mm, "end": v(-14.84, 17.09) * mm});
            skLineSegment(sketch, "E13846", {"start": v(-14.84, 17.09) * mm, "end": v(-14.68, 17.35) * mm});
            skLineSegment(sketch, "E13847", {"start": v(-14.68, 17.35) * mm, "end": v(-14.7, 17.68) * mm});
            skLineSegment(sketch, "E13848", {"start": v(-14.7, 17.68) * mm, "end": v(-14.72, 18.04) * mm});
            skLineSegment(sketch, "E13849", {"start": v(-14.72, 18.04) * mm, "end": v(-14.73, 18.22) * mm});
            skLineSegment(sketch, "E13850", {"start": v(-14.73, 18.22) * mm, "end": v(-14.73, 18.4) * mm});
            skLineSegment(sketch, "E13851", {"start": v(-14.73, 18.4) * mm, "end": v(-14.71, 18.56) * mm});
            skLineSegment(sketch, "E13852", {"start": v(-14.71, 18.56) * mm, "end": v(-14.68, 18.72) * mm});
            skLineSegment(sketch, "E13853", {"start": v(-14.68, 18.72) * mm, "end": v(-14.63, 18.86) * mm});
            skLineSegment(sketch, "E13854", {"start": v(-14.63, 18.86) * mm, "end": v(-14.56, 19) * mm});
            skLineSegment(sketch, "E13855", {"start": v(-14.56, 19) * mm, "end": v(-14.37, 19.29) * mm});
            skLineSegment(sketch, "E13856", {"start": v(-14.37, 19.29) * mm, "end": v(-14.17, 19.56) * mm});
            skLineSegment(sketch, "E13857", {"start": v(-14.17, 19.56) * mm, "end": v(-14, 19.82) * mm});
            skLineSegment(sketch, "E13858", {"start": v(-14, 19.82) * mm, "end": v(-13.84, 20.05) * mm});
            skLineSegment(sketch, "E13859", {"start": v(-13.84, 20.05) * mm, "end": v(-13.68, 20.28) * mm});
            skLineSegment(sketch, "E13860", {"start": v(-13.68, 20.28) * mm, "end": v(-13.52, 20.5) * mm});
            skLineSegment(sketch, "E13861", {"start": v(-13.52, 20.5) * mm, "end": v(-13.35, 20.7) * mm});
            skLineSegment(sketch, "E13862", {"start": v(-13.35, 20.7) * mm, "end": v(-13.18, 20.89) * mm});
            skLineSegment(sketch, "E13863", {"start": v(-13.18, 20.89) * mm, "end": v(-13.02, 21.04) * mm});
            skLineSegment(sketch, "E13864", {"start": v(-13.02, 21.04) * mm, "end": v(-12.88, 21.17) * mm});
            skLineSegment(sketch, "E13865", {"start": v(-12.88, 21.17) * mm, "end": v(-12.76, 21.26) * mm});
            skLineSegment(sketch, "E13866", {"start": v(-12.76, 21.26) * mm, "end": v(-12.2, 21.58) * mm});
            skLineSegment(sketch, "E13867", {"start": v(-12.2, 21.58) * mm, "end": v(-12.9, 21.59) * mm});
            skLineSegment(sketch, "E13868", {"start": v(-12.9, 21.59) * mm, "end": v(-13.08, 21.6) * mm});
            skLineSegment(sketch, "E13869", {"start": v(-13.08, 21.6) * mm, "end": v(-13.31, 21.63) * mm});
            skLineSegment(sketch, "E13870", {"start": v(-13.31, 21.63) * mm, "end": v(-13.59, 21.69) * mm});
            skLineSegment(sketch, "E13871", {"start": v(-13.59, 21.69) * mm, "end": v(-13.9, 21.75) * mm});
            skLineSegment(sketch, "E13872", {"start": v(-13.9, 21.75) * mm, "end": v(-14.58, 21.93) * mm});
            skLineSegment(sketch, "E13873", {"start": v(-14.58, 21.93) * mm, "end": v(-14.93, 22.03) * mm});
            skLineSegment(sketch, "E13874", {"start": v(-14.93, 22.03) * mm, "end": v(-15.28, 22.14) * mm});
            skLineSegment(sketch, "E13875", {"start": v(-15.28, 22.14) * mm, "end": v(-15.68, 22.25) * mm});
            skLineSegment(sketch, "E13876", {"start": v(-15.68, 22.25) * mm, "end": v(-16.12, 22.37) * mm});
            skLineSegment(sketch, "E13877", {"start": v(-16.12, 22.37) * mm, "end": v(-16.35, 22.43) * mm});
            skLineSegment(sketch, "E13878", {"start": v(-16.35, 22.43) * mm, "end": v(-16.56, 22.5) * mm});
            skLineSegment(sketch, "E13879", {"start": v(-16.56, 22.5) * mm, "end": v(-16.76, 22.58) * mm});
            skLineSegment(sketch, "E13880", {"start": v(-16.76, 22.58) * mm, "end": v(-16.94, 22.67) * mm});
            skLineSegment(sketch, "E13881", {"start": v(-16.94, 22.67) * mm, "end": v(-17.25, 22.85) * mm});
            skLineSegment(sketch, "E13882", {"start": v(-17.25, 22.85) * mm, "end": v(-17.56, 23.05) * mm});
            skLineSegment(sketch, "E13883", {"start": v(-17.56, 23.05) * mm, "end": v(-17.88, 23.27) * mm});
            skLineSegment(sketch, "E13884", {"start": v(-17.88, 23.27) * mm, "end": v(-18.2, 23.51) * mm});
            skLineSegment(sketch, "E13885", {"start": v(-18.2, 23.51) * mm, "end": v(-18.5, 23.77) * mm});
            skLineSegment(sketch, "E13886", {"start": v(-18.5, 23.77) * mm, "end": v(-18.79, 24.03) * mm});
            skLineSegment(sketch, "E13887", {"start": v(-18.79, 24.03) * mm, "end": v(-19.04, 24.3) * mm});
            skLineSegment(sketch, "E13888", {"start": v(-19.04, 24.3) * mm, "end": v(-19.15, 24.44) * mm});
            skLineSegment(sketch, "E13889", {"start": v(-19.15, 24.44) * mm, "end": v(-19.26, 24.58) * mm});
            skLineSegment(sketch, "E13890", {"start": v(-19.26, 24.58) * mm, "end": v(-19.37, 24.76) * mm});
            skLineSegment(sketch, "E13891", {"start": v(-19.37, 24.76) * mm, "end": v(-19.49, 24.95) * mm});
            skLineSegment(sketch, "E13892", {"start": v(-19.49, 24.95) * mm, "end": v(-19.6, 25.14) * mm});
            skLineSegment(sketch, "E13893", {"start": v(-19.6, 25.14) * mm, "end": v(-19.7, 25.35) * mm});
            skLineSegment(sketch, "E13894", {"start": v(-19.7, 25.35) * mm, "end": v(-19.88, 25.8) * mm});
            skLineSegment(sketch, "E13895", {"start": v(-19.88, 25.8) * mm, "end": v(-20.05, 26.25) * mm});
            skLineSegment(sketch, "E13896", {"start": v(-20.05, 26.25) * mm, "end": v(-20.2, 26.72) * mm});
            skLineSegment(sketch, "E13897", {"start": v(-20.2, 26.72) * mm, "end": v(-20.33, 27.18) * mm});
            skLineSegment(sketch, "E13898", {"start": v(-20.33, 27.18) * mm, "end": v(-20.55, 28.05) * mm});
            skLineSegment(sketch, "E13899", {"start": v(-20.55, 28.05) * mm, "end": v(-20.66, 28.5) * mm});
            skLineSegment(sketch, "E13900", {"start": v(-20.66, 28.5) * mm, "end": v(-20.76, 28.98) * mm});
            skLineSegment(sketch, "E13901", {"start": v(-20.76, 28.98) * mm, "end": v(-20.86, 29.48) * mm});
            skLineSegment(sketch, "E13902", {"start": v(-20.86, 29.48) * mm, "end": v(-20.95, 29.98) * mm});
            skLineSegment(sketch, "E13903", {"start": v(-20.95, 29.98) * mm, "end": v(-21.1, 31.02) * mm});
            skLineSegment(sketch, "E13904", {"start": v(-21.1, 31.02) * mm, "end": v(-21.24, 32.09) * mm});
            skLineSegment(sketch, "E13905", {"start": v(-21.24, 32.09) * mm, "end": v(-21.36, 33.16) * mm});
            skLineSegment(sketch, "E13906", {"start": v(-21.36, 33.16) * mm, "end": v(-21.46, 34.2) * mm});
            skLineSegment(sketch, "E13907", {"start": v(-21.46, 34.2) * mm, "end": v(-21.54, 35.22) * mm});
            skLineSegment(sketch, "E13908", {"start": v(-21.54, 35.22) * mm, "end": v(-21.6, 36.18) * mm});
            skLineSegment(sketch, "E13909", {"start": v(-21.6, 36.18) * mm, "end": v(-21.61, 36.4) * mm});
            skLineSegment(sketch, "E13910", {"start": v(-21.61, 36.4) * mm, "end": v(-21.6, 36.66) * mm});
            skLineSegment(sketch, "E13911", {"start": v(-21.6, 36.66) * mm, "end": v(-21.56, 37.18) * mm});
            skLineSegment(sketch, "E13912", {"start": v(-21.56, 37.18) * mm, "end": v(-21.55, 37.44) * mm});
            skLineSegment(sketch, "E13913", {"start": v(-21.55, 37.44) * mm, "end": v(-21.55, 37.7) * mm});
            skLineSegment(sketch, "E13914", {"start": v(-21.55, 37.7) * mm, "end": v(-21.57, 37.93) * mm});
            skLineSegment(sketch, "E13915", {"start": v(-21.57, 37.93) * mm, "end": v(-21.58, 38.05) * mm});
            skLineSegment(sketch, "E13916", {"start": v(-21.58, 38.05) * mm, "end": v(-21.6, 38.16) * mm});
            skLineSegment(sketch, "E13917", {"start": v(-21.6, 38.16) * mm, "end": v(-21.68, 38.4) * mm});
            skLineSegment(sketch, "E13918", {"start": v(-21.68, 38.4) * mm, "end": v(-21.78, 38.63) * mm});
            skLineSegment(sketch, "E13919", {"start": v(-21.78, 38.63) * mm, "end": v(-21.9, 38.87) * mm});
            skLineSegment(sketch, "E13920", {"start": v(-21.9, 38.87) * mm, "end": v(-22.04, 39.11) * mm});
            skLineSegment(sketch, "E13921", {"start": v(-22.04, 39.11) * mm, "end": v(-22.18, 39.35) * mm});
            skLineSegment(sketch, "E13922", {"start": v(-22.18, 39.35) * mm, "end": v(-22.34, 39.57) * mm});
            skLineSegment(sketch, "E13923", {"start": v(-22.34, 39.57) * mm, "end": v(-22.5, 39.77) * mm});
            skLineSegment(sketch, "E13924", {"start": v(-22.5, 39.77) * mm, "end": v(-22.67, 39.95) * mm});
            skLineSegment(sketch, "E13925", {"start": v(-22.67, 39.95) * mm, "end": v(-22.8, 40.08) * mm});
            skLineSegment(sketch, "E13926", {"start": v(-22.8, 40.08) * mm, "end": v(-22.97, 40.2) * mm});
            skLineSegment(sketch, "E13927", {"start": v(-22.97, 40.2) * mm, "end": v(-23.15, 40.32) * mm});
            skLineSegment(sketch, "E13928", {"start": v(-23.15, 40.32) * mm, "end": v(-23.34, 40.43) * mm});
            skLineSegment(sketch, "E13929", {"start": v(-23.34, 40.43) * mm, "end": v(-23.72, 40.64) * mm});
            skLineSegment(sketch, "E13930", {"start": v(-23.72, 40.64) * mm, "end": v(-23.9, 40.74) * mm});
            skLineSegment(sketch, "E13931", {"start": v(-23.9, 40.74) * mm, "end": v(-24.07, 40.84) * mm});
            skLineSegment(sketch, "E13932", {"start": v(-24.07, 40.84) * mm, "end": v(-24.43, 41.05) * mm});
            skLineSegment(sketch, "E13933", {"start": v(-24.43, 41.05) * mm, "end": v(-24.93, 41.3) * mm});
            skLineSegment(sketch, "E13934", {"start": v(-24.93, 41.3) * mm, "end": v(-25.54, 41.6) * mm});
            skLineSegment(sketch, "E13935", {"start": v(-25.54, 41.6) * mm, "end": v(-26.24, 41.94) * mm});
            skLineSegment(sketch, "E13936", {"start": v(-26.24, 41.94) * mm, "end": v(-27.01, 42.28) * mm});
            skLineSegment(sketch, "E13937", {"start": v(-27.01, 42.28) * mm, "end": v(-27.83, 42.63) * mm});
            skLineSegment(sketch, "E13938", {"start": v(-27.83, 42.63) * mm, "end": v(-28.66, 42.99) * mm});
            skLineSegment(sketch, "E13939", {"start": v(-28.66, 42.99) * mm, "end": v(-29.5, 43.33) * mm});
            skLineSegment(sketch, "E13940", {"start": v(-29.5, 43.33) * mm, "end": v(-33.13, 44.77) * mm});
            skLineSegment(sketch, "E13941", {"start": v(-33.13, 44.77) * mm, "end": v(-33.36, 44.7) * mm});
            skLineSegment(sketch, "E13942", {"start": v(-33.36, 44.7) * mm, "end": v(-33.78, 44.58) * mm});
            skLineSegment(sketch, "E13943", {"start": v(-33.78, 44.58) * mm, "end": v(-34.14, 44.47) * mm});
            skLineSegment(sketch, "E13944", {"start": v(-34.14, 44.47) * mm, "end": v(-34.8, 44.26) * mm});
            skLineSegment(sketch, "E13945", {"start": v(-34.8, 44.26) * mm, "end": v(-35.44, 44.08) * mm});
            skLineSegment(sketch, "E13946", {"start": v(-35.44, 44.08) * mm, "end": v(-35.99, 43.96) * mm});
            skLineSegment(sketch, "E13947", {"start": v(-35.99, 43.96) * mm, "end": v(-36.24, 43.92) * mm});
            skLineSegment(sketch, "E13948", {"start": v(-36.24, 43.92) * mm, "end": v(-36.44, 43.9) * mm});
            skLineSegment(sketch, "E13949", {"start": v(-36.44, 43.9) * mm, "end": v(-36.48, 43.9) * mm});
            skLineSegment(sketch, "E13950", {"start": v(-36.48, 43.9) * mm, "end": v(-36.98, 42.52) * mm});
            skLineSegment(sketch, "E13951", {"start": v(-36.98, 42.52) * mm, "end": v(-37.27, 41.77) * mm});
            skLineSegment(sketch, "E13952", {"start": v(-37.27, 41.77) * mm, "end": v(-37.6, 41.02) * mm});
            skLineSegment(sketch, "E13953", {"start": v(-37.6, 41.02) * mm, "end": v(-37.95, 40.27) * mm});
            skLineSegment(sketch, "E13954", {"start": v(-37.95, 40.27) * mm, "end": v(-38.1, 39.97) * mm});
            skLineSegment(sketch, "E13955", {"start": v(-38.1, 39.97) * mm, "end": v(-38.1, 39.86) * mm});
            skLineSegment(sketch, "E13956", {"start": v(-38.1, 39.86) * mm, "end": v(-38.06, 39.76) * mm});
            skLineSegment(sketch, "E13957", {"start": v(-38.06, 39.76) * mm, "end": v(-38.01, 39.67) * mm});
            skLineSegment(sketch, "E13958", {"start": v(-38.01, 39.67) * mm, "end": v(-37.95, 39.58) * mm});
            skLineSegment(sketch, "E13959", {"start": v(-37.95, 39.58) * mm, "end": v(-37.87, 39.49) * mm});
            skLineSegment(sketch, "E13960", {"start": v(-37.87, 39.49) * mm, "end": v(-37.78, 39.4) * mm});
            skLineSegment(sketch, "E13961", {"start": v(-37.78, 39.4) * mm, "end": v(-37.58, 39.24) * mm});
            skLineSegment(sketch, "E13962", {"start": v(-37.58, 39.24) * mm, "end": v(-37.12, 38.95) * mm});
            skLineSegment(sketch, "E13963", {"start": v(-37.12, 38.95) * mm, "end": v(-36.9, 38.8) * mm});
            skLineSegment(sketch, "E13964", {"start": v(-36.9, 38.8) * mm, "end": v(-36.72, 38.67) * mm});
            skLineSegment(sketch, "E13965", {"start": v(-36.72, 38.67) * mm, "end": v(-36.62, 38.65) * mm});
            skLineSegment(sketch, "E13966", {"start": v(-36.62, 38.65) * mm, "end": v(-36.52, 38.61) * mm});
            skLineSegment(sketch, "E13967", {"start": v(-36.52, 38.61) * mm, "end": v(-36.43, 38.55) * mm});
            skLineSegment(sketch, "E13968", {"start": v(-36.43, 38.55) * mm, "end": v(-36.36, 38.48) * mm});
            skLineSegment(sketch, "E13969", {"start": v(-36.36, 38.48) * mm, "end": v(-36.3, 38.4) * mm});
            skLineSegment(sketch, "E13970", {"start": v(-36.3, 38.4) * mm, "end": v(-36.25, 38.3) * mm});
            skLineSegment(sketch, "E13971", {"start": v(-36.25, 38.3) * mm, "end": v(-36.22, 38.2) * mm});
            skLineSegment(sketch, "E13972", {"start": v(-36.22, 38.2) * mm, "end": v(-36.22, 38.1) * mm});
            skLineSegment(sketch, "E13973", {"start": v(-36.22, 38.1) * mm, "end": v(-36.24, 37.33) * mm});
            skLineSegment(sketch, "E13974", {"start": v(-36.24, 37.33) * mm, "end": v(-36.05, 36.6) * mm});
            skLineSegment(sketch, "E13975", {"start": v(-36.05, 36.6) * mm, "end": v(-36, 36.44) * mm});
            skLineSegment(sketch, "E13976", {"start": v(-36, 36.44) * mm, "end": v(-35.95, 36.27) * mm});
            skLineSegment(sketch, "E13977", {"start": v(-35.95, 36.27) * mm, "end": v(-35.78, 35.87) * mm});
            skLineSegment(sketch, "E13978", {"start": v(-35.78, 35.87) * mm, "end": v(-35.57, 35.47) * mm});
            skLineSegment(sketch, "E13979", {"start": v(-35.57, 35.47) * mm, "end": v(-35.46, 35.3) * mm});
            skLineSegment(sketch, "E13980", {"start": v(-35.46, 35.3) * mm, "end": v(-35.35, 35.13) * mm});
            skLineSegment(sketch, "E13981", {"start": v(-35.35, 35.13) * mm, "end": v(-34.95, 34.56) * mm});
            skLineSegment(sketch, "E13982", {"start": v(-34.95, 34.56) * mm, "end": v(-34.75, 34.46) * mm});
            skLineSegment(sketch, "E13983", {"start": v(-34.75, 34.46) * mm, "end": v(-34.54, 34.37) * mm});
            skLineSegment(sketch, "E13984", {"start": v(-34.54, 34.37) * mm, "end": v(-34.1, 34.2) * mm});
            skLineSegment(sketch, "E13985", {"start": v(-34.1, 34.2) * mm, "end": v(-33.68, 34.05) * mm});
            skLineSegment(sketch, "E13986", {"start": v(-33.68, 34.05) * mm, "end": v(-33.48, 33.97) * mm});
            skLineSegment(sketch, "E13987", {"start": v(-33.48, 33.97) * mm, "end": v(-33.3, 33.88) * mm});
            skLineSegment(sketch, "E13988", {"start": v(-33.3, 33.88) * mm, "end": v(-32.08, 29.75) * mm});
            skLineSegment(sketch, "E13989", {"start": v(-32.08, 29.75) * mm, "end": v(-31.8, 28.81) * mm});
            skLineSegment(sketch, "E13990", {"start": v(-31.8, 28.81) * mm, "end": v(-31.46, 27.73) * mm});
            skLineSegment(sketch, "E13991", {"start": v(-31.46, 27.73) * mm, "end": v(-30.68, 25.3) * mm});
            skLineSegment(sketch, "E13992", {"start": v(-30.68, 25.3) * mm, "end": v(-29.83, 22.75) * mm});
            skLineSegment(sketch, "E13993", {"start": v(-29.83, 22.75) * mm, "end": v(-29.41, 21.53) * mm});
            skLineSegment(sketch, "E13994", {"start": v(-29.41, 21.53) * mm, "end": v(-29.01, 20.4) * mm});
            skLineSegment(sketch, "E13995", {"start": v(-29.01, 20.4) * mm, "end": v(-28.58, 19.13) * mm});
            skLineSegment(sketch, "E13996", {"start": v(-28.58, 19.13) * mm, "end": v(-28.12, 17.77) * mm});
            skLineSegment(sketch, "E13997", {"start": v(-28.12, 17.77) * mm, "end": v(-27.88, 17.08) * mm});
            skLineSegment(sketch, "E13998", {"start": v(-27.88, 17.08) * mm, "end": v(-27.64, 16.4) * mm});
            skLineSegment(sketch, "E13999", {"start": v(-27.64, 16.4) * mm, "end": v(-27.4, 15.77) * mm});
            skLineSegment(sketch, "E14000", {"start": v(-27.4, 15.77) * mm, "end": v(-27.16, 15.16) * mm});
            skLineSegment(sketch, "E14001", {"start": v(-27.16, 15.16) * mm, "end": v(-26.76, 14.22) * mm});
            skLineSegment(sketch, "E14002", {"start": v(-26.76, 14.22) * mm, "end": v(-26.3, 13.24) * mm});
            skLineSegment(sketch, "E14003", {"start": v(-26.3, 13.24) * mm, "end": v(-25.83, 12.22) * mm});
            skLineSegment(sketch, "E14004", {"start": v(-25.83, 12.22) * mm, "end": v(-25.33, 11.18) * mm});
            skLineSegment(sketch, "E14005", {"start": v(-25.33, 11.18) * mm, "end": v(-24.32, 9.14) * mm});
            skLineSegment(sketch, "E14006", {"start": v(-24.32, 9.14) * mm, "end": v(-23.85, 8.17) * mm});
            skLineSegment(sketch, "E14007", {"start": v(-23.85, 8.17) * mm, "end": v(-23.4, 7.24) * mm});
            skLineSegment(sketch, "E14008", {"start": v(-23.4, 7.24) * mm, "end": v(-23.26, 6.95) * mm});
            skLineSegment(sketch, "E14009", {"start": v(-23.26, 6.95) * mm, "end": v(-23.1, 6.66) * mm});
            skLineSegment(sketch, "E14010", {"start": v(-23.1, 6.66) * mm, "end": v(-22.93, 6.37) * mm});
            skLineSegment(sketch, "E14011", {"start": v(-22.93, 6.37) * mm, "end": v(-22.76, 6.09) * mm});
            skLineSegment(sketch, "E14012", {"start": v(-22.76, 6.09) * mm, "end": v(-22.58, 5.81) * mm});
            skLineSegment(sketch, "E14013", {"start": v(-22.58, 5.81) * mm, "end": v(-22.4, 5.54) * mm});
            skLineSegment(sketch, "E14014", {"start": v(-22.4, 5.54) * mm, "end": v(-22, 5) * mm});
            skLineSegment(sketch, "E14015", {"start": v(-22, 5) * mm, "end": v(-20.8, 3.42) * mm});
            skLineSegment(sketch, "E14016", {"start": v(-20.8, 3.42) * mm, "end": v(-20.5, 3.06) * mm});
            skLineSegment(sketch, "E14017", {"start": v(-20.5, 3.06) * mm, "end": v(-20.16, 2.65) * mm});
            skLineSegment(sketch, "E14018", {"start": v(-20.16, 2.65) * mm, "end": v(-19.76, 2.2) * mm});
            skLineSegment(sketch, "E14019", {"start": v(-19.76, 2.2) * mm, "end": v(-19.32, 1.72) * mm});
            skLineSegment(sketch, "E14020", {"start": v(-19.32, 1.72) * mm, "end": v(-18.86, 1.23) * mm});
            skLineSegment(sketch, "E14021", {"start": v(-18.86, 1.23) * mm, "end": v(-18.4, 0.75) * mm});
            skLineSegment(sketch, "E14022", {"start": v(-18.4, 0.75) * mm, "end": v(-17.93, 0.3) * mm});
            skLineSegment(sketch, "E14023", {"start": v(-17.93, 0.3) * mm, "end": v(-17.48, -0.14) * mm});
            skLineSegment(sketch, "E14024", {"start": v(-17.48, -0.14) * mm, "end": v(-17.24, -0.37) * mm});
            skLineSegment(sketch, "E14025", {"start": v(-17.24, -0.37) * mm, "end": v(-16.99, -0.63) * mm});
            skLineSegment(sketch, "E14026", {"start": v(-16.99, -0.63) * mm, "end": v(-16.47, -1.18) * mm});
            skLineSegment(sketch, "E14027", {"start": v(-16.47, -1.18) * mm, "end": v(-16.2, -1.45) * mm});
            skLineSegment(sketch, "E14028", {"start": v(-16.2, -1.45) * mm, "end": v(-15.93, -1.7) * mm});
            skLineSegment(sketch, "E14029", {"start": v(-15.93, -1.7) * mm, "end": v(-15.65, -1.92) * mm});
            skLineSegment(sketch, "E14030", {"start": v(-15.65, -1.92) * mm, "end": v(-15.51, -2.02) * mm});
            skLineSegment(sketch, "E14031", {"start": v(-15.51, -2.02) * mm, "end": v(-15.37, -2.1) * mm});
            skLineSegment(sketch, "E14032", {"start": v(-15.37, -2.1) * mm, "end": v(-15.23, -2.18) * mm});
            skLineSegment(sketch, "E14033", {"start": v(-15.23, -2.18) * mm, "end": v(-15.08, -2.24) * mm});
            skLineSegment(sketch, "E14034", {"start": v(-15.08, -2.24) * mm, "end": v(-14.74, -2.34) * mm});
            skLineSegment(sketch, "E14035", {"start": v(-14.74, -2.34) * mm, "end": v(-14.4, -2.43) * mm});
            skLineSegment(sketch, "E14036", {"start": v(-14.4, -2.43) * mm, "end": v(-14.08, -2.51) * mm});
            skLineSegment(sketch, "E14037", {"start": v(-14.08, -2.51) * mm, "end": v(-13.5, -2.1) * mm});
            skLineSegment(sketch, "E14038", {"start": v(-13.5, -2.1) * mm, "end": v(-12.87, -1.63) * mm});
            skLineSegment(sketch, "E14039", {"start": v(-12.87, -1.63) * mm, "end": v(-12.54, -1.4) * mm});
            skLineSegment(sketch, "E14040", {"start": v(-12.54, -1.4) * mm, "end": v(-12.22, -1.18) * mm});
            skLineSegment(sketch, "E14041", {"start": v(-12.22, -1.18) * mm, "end": v(-11.9, -0.99) * mm});
            skLineSegment(sketch, "E14042", {"start": v(-11.9, -0.99) * mm, "end": v(-11.6, -0.83) * mm});
            skLineSegment(sketch, "E14043", {"start": v(-11.6, -0.83) * mm, "end": v(-11.19, -0.64) * mm});
            skLineSegment(sketch, "E14044", {"start": v(-11.19, -0.64) * mm, "end": v(-10.74, -0.46) * mm});
            skLineSegment(sketch, "E14045", {"start": v(-10.74, -0.46) * mm, "end": v(-10.27, -0.3) * mm});
            skLineSegment(sketch, "E14046", {"start": v(-10.27, -0.3) * mm, "end": v(-9.8, -0.14) * mm});
            skLineSegment(sketch, "E14047", {"start": v(-9.8, -0.14) * mm, "end": v(-9.3, 0) * mm});
            skLineSegment(sketch, "E14048", {"start": v(-9.3, 0) * mm, "end": v(-8.83, 0.12) * mm});
            skLineSegment(sketch, "E14049", {"start": v(-8.83, 0.12) * mm, "end": v(-8.36, 0.22) * mm});
            skLineSegment(sketch, "E14050", {"start": v(-8.36, 0.22) * mm, "end": v(-7.92, 0.3) * mm});
            skLineSegment(sketch, "E14051", {"start": v(-7.92, 0.3) * mm, "end": v(-7.34, 0.37) * mm});
            skLineSegment(sketch, "E14052", {"start": v(-7.34, 0.37) * mm, "end": v(-6.73, 0.44) * mm});
            skLineSegment(sketch, "E14053", {"start": v(-6.73, 0.44) * mm, "end": v(-6.09, 0.48) * mm});
            skLineSegment(sketch, "E14054", {"start": v(-6.09, 0.48) * mm, "end": v(-5.43, 0.5) * mm});
            skLineSegment(sketch, "E14055", {"start": v(-5.43, 0.5) * mm, "end": v(-4.78, 0.5) * mm});
            skLineSegment(sketch, "E14056", {"start": v(-4.78, 0.5) * mm, "end": v(-4.46, 0.5) * mm});
            skLineSegment(sketch, "E14057", {"start": v(-4.46, 0.5) * mm, "end": v(-4.14, 0.48) * mm});
            skLineSegment(sketch, "E14058", {"start": v(-4.14, 0.48) * mm, "end": v(-3.83, 0.45) * mm});
            skLineSegment(sketch, "E14059", {"start": v(-3.83, 0.45) * mm, "end": v(-3.53, 0.4) * mm});
            skLineSegment(sketch, "E14060", {"start": v(-3.53, 0.4) * mm, "end": v(-3.24, 0.36) * mm});
            skLineSegment(sketch, "E14061", {"start": v(-3.24, 0.36) * mm, "end": v(-2.97, 0.3) * mm});
            skLineSegment(sketch, "E14062", {"start": v(-2.97, 0.3) * mm, "end": v(-2.81, 0.26) * mm});
            skLineSegment(sketch, "E14063", {"start": v(-2.81, 0.26) * mm, "end": v(-2.65, 0.2) * mm});
            skLineSegment(sketch, "E14064", {"start": v(-2.65, 0.2) * mm, "end": v(-2.33, 0.03) * mm});
            skLineSegment(sketch, "E14065", {"start": v(-2.33, 0.03) * mm, "end": v(-2.02, -0.15) * mm});
            skLineSegment(sketch, "E14066", {"start": v(-2.02, -0.15) * mm, "end": v(-1.73, -0.3) * mm});
            skLineSegment(sketch, "E14067", {"start": v(-1.73, -0.3) * mm, "end": v(-1.48, -0.44) * mm});
            skLineSegment(sketch, "E14068", {"start": v(-1.48, -0.44) * mm, "end": v(-1.26, -0.57) * mm});
            skLineSegment(sketch, "E14069", {"start": v(-1.26, -0.57) * mm, "end": v(-1.07, -0.7) * mm});
            skLineSegment(sketch, "E14070", {"start": v(-1.07, -0.7) * mm, "end": v(-0.9, -0.84) * mm});
            skLineSegment(sketch, "E14071", {"start": v(-0.9, -0.84) * mm, "end": v(-0.63, -1.07) * mm});
            skLineSegment(sketch, "E14072", {"start": v(-0.63, -1.07) * mm, "end": v(-0.5, -1.22) * mm});
            skLineSegment(sketch, "E14073", {"start": v(-0.5, -1.22) * mm, "end": v(-0.25, -1.5) * mm});
            skLineSegment(sketch, "E14074", {"start": v(-0.25, -1.5) * mm, "end": v(-0.14, -1.64) * mm});
            skLineSegment(sketch, "E14075", {"start": v(-0.14, -1.64) * mm, "end": v(-0.04, -1.78) * mm});
            skLineSegment(sketch, "E14076", {"start": v(-0.04, -1.78) * mm, "end": v(0.07, -1.94) * mm});
            skLineSegment(sketch, "E14077", {"start": v(0.07, -1.94) * mm, "end": v(0.18, -2.13) * mm});
            skLineSegment(sketch, "E14078", {"start": v(0.18, -2.13) * mm, "end": v(0.28, -2.32) * mm});
            skLineSegment(sketch, "E14079", {"start": v(0.28, -2.32) * mm, "end": v(0.36, -2.5) * mm});
            skLineSegment(sketch, "E14080", {"start": v(0.36, -2.5) * mm, "end": v(0.43, -2.68) * mm});
            skLineSegment(sketch, "E14081", {"start": v(0.43, -2.68) * mm, "end": v(0.49, -2.89) * mm});
            skLineSegment(sketch, "E14082", {"start": v(0.49, -2.89) * mm, "end": v(0.6, -3.28) * mm});
            skLineSegment(sketch, "E14083", {"start": v(0.6, -3.28) * mm, "end": v(2.77, -3.28) * mm});
            skLineSegment(sketch, "E14084", {"start": v(2.77, -3.28) * mm, "end": v(3.26, -2.73) * mm});
            skLineSegment(sketch, "E14085", {"start": v(3.26, -2.73) * mm, "end": v(3.75, -2.17) * mm});
            skLineSegment(sketch, "E14086", {"start": v(3.75, -2.17) * mm, "end": v(4.25, -1.6) * mm});
            skLineSegment(sketch, "E14087", {"start": v(4.25, -1.6) * mm, "end": v(4.5, -1.33) * mm});
            skLineSegment(sketch, "E14088", {"start": v(4.5, -1.33) * mm, "end": v(4.72, -1.09) * mm});
            skLineSegment(sketch, "E14089", {"start": v(4.72, -1.09) * mm, "end": v(4.95, -0.86) * mm});
            skLineSegment(sketch, "E14090", {"start": v(4.95, -0.86) * mm, "end": v(5.18, -0.66) * mm});
            skLineSegment(sketch, "E14091", {"start": v(5.18, -0.66) * mm, "end": v(5.4, -0.47) * mm});
            skLineSegment(sketch, "E14092", {"start": v(5.4, -0.47) * mm, "end": v(5.63, -0.3) * mm});
            skLineSegment(sketch, "E14093", {"start": v(5.63, -0.3) * mm, "end": v(5.86, -0.14) * mm});
            skLineSegment(sketch, "E14094", {"start": v(5.86, -0.14) * mm, "end": v(6.1, 0) * mm});
            skLineSegment(sketch, "E14095", {"start": v(6.1, 0) * mm, "end": v(6.34, 0.13) * mm});
            skLineSegment(sketch, "E14096", {"start": v(6.34, 0.13) * mm, "end": v(6.59, 0.24) * mm});
            skLineSegment(sketch, "E14097", {"start": v(6.59, 0.24) * mm, "end": v(6.85, 0.34) * mm});
            skLineSegment(sketch, "E14098", {"start": v(6.85, 0.34) * mm, "end": v(7.12, 0.43) * mm});
            skLineSegment(sketch, "E14099", {"start": v(7.12, 0.43) * mm, "end": v(7.4, 0.5) * mm});
            skLineSegment(sketch, "E14100", {"start": v(7.4, 0.5) * mm, "end": v(7.71, 0.57) * mm});
            skLineSegment(sketch, "E14101", {"start": v(7.71, 0.57) * mm, "end": v(8.04, 0.62) * mm});
            skLineSegment(sketch, "E14102", {"start": v(8.04, 0.62) * mm, "end": v(8.4, 0.67) * mm});
            skLineSegment(sketch, "E14103", {"start": v(8.4, 0.67) * mm, "end": v(8.75, 0.7) * mm});
            skLineSegment(sketch, "E14104", {"start": v(8.75, 0.7) * mm, "end": v(9.08, 0.72) * mm});
            skLineSegment(sketch, "E14105", {"start": v(9.08, 0.72) * mm, "end": v(9.4, 0.7) * mm});
            skLineSegment(sketch, "E14106", {"start": v(9.4, 0.7) * mm, "end": v(9.77, 0.65) * mm});
            skLineSegment(sketch, "E14107", {"start": v(9.77, 0.65) * mm, "end": v(10.45, 0.53) * mm});
            skLineSegment(sketch, "E14108", {"start": v(10.45, 0.53) * mm, "end": v(10.84, 0.45) * mm});
            skLineSegment(sketch, "E14109", {"start": v(10.84, 0.45) * mm, "end": v(11.34, 0.32) * mm});
            skLineSegment(sketch, "E14110", {"start": v(11.34, 0.32) * mm, "end": v(11.63, 0.24) * mm});
            skLineSegment(sketch, "E14111", {"start": v(11.63, 0.24) * mm, "end": v(11.94, 0.15) * mm});
            skLineSegment(sketch, "E14112", {"start": v(11.94, 0.15) * mm, "end": v(12.26, 0.04) * mm});
            skLineSegment(sketch, "E14113", {"start": v(12.26, 0.04) * mm, "end": v(12.6, -0.09) * mm});
            skLineSegment(sketch, "E14114", {"start": v(12.6, -0.09) * mm, "end": v(13, -0.26) * mm});
            skLineSegment(sketch, "E14115", {"start": v(13, -0.26) * mm, "end": v(13.4, -0.46) * mm});
            skLineSegment(sketch, "E14116", {"start": v(13.4, -0.46) * mm, "end": v(13.81, -0.66) * mm});
            skLineSegment(sketch, "E14117", {"start": v(13.81, -0.66) * mm, "end": v(14.2, -0.85) * mm});
            skLineSegment(sketch, "E14118", {"start": v(14.2, -0.85) * mm, "end": v(14.5, -1) * mm});
            skLineSegment(sketch, "E14119", {"start": v(14.5, -1) * mm, "end": v(14.8, -1.15) * mm});
            skLineSegment(sketch, "E14120", {"start": v(14.8, -1.15) * mm, "end": v(15.41, -1.49) * mm});
            skLineSegment(sketch, "E14121", {"start": v(15.41, -1.49) * mm, "end": v(16.03, -1.83) * mm});
            skLineSegment(sketch, "E14122", {"start": v(16.03, -1.83) * mm, "end": v(16.33, -1.98) * mm});
            skLineSegment(sketch, "E14123", {"start": v(16.33, -1.98) * mm, "end": v(16.62, -2.12) * mm});
            skLineSegment(sketch, "E14124", {"start": v(16.62, -2.12) * mm, "end": v(17.35, -1.6) * mm});
            skLineSegment(sketch, "E14125", {"start": v(17.35, -1.6) * mm, "end": v(18.14, -1.03) * mm});
            skLineSegment(sketch, "E14126", {"start": v(18.14, -1.03) * mm, "end": v(18.54, -0.74) * mm});
            skLineSegment(sketch, "E14127", {"start": v(18.54, -0.74) * mm, "end": v(18.92, -0.45) * mm});
            skLineSegment(sketch, "E14128", {"start": v(18.92, -0.45) * mm, "end": v(19.27, -0.16) * mm});
            skLineSegment(sketch, "E14129", {"start": v(19.27, -0.16) * mm, "end": v(19.59, 0.14) * mm});
            skLineSegment(sketch, "E14130", {"start": v(19.59, 0.14) * mm, "end": v(19.88, 0.44) * mm});
            skLineSegment(sketch, "E14131", {"start": v(19.88, 0.44) * mm, "end": v(20.17, 0.76) * mm});
            skLineSegment(sketch, "E14132", {"start": v(20.17, 0.76) * mm, "end": v(20.47, 1.09) * mm});
            skLineSegment(sketch, "E14133", {"start": v(20.47, 1.09) * mm, "end": v(20.76, 1.44) * mm});
            skLineSegment(sketch, "E14134", {"start": v(20.76, 1.44) * mm, "end": v(21.35, 2.16) * mm});
            skLineSegment(sketch, "E14135", {"start": v(21.35, 2.16) * mm, "end": v(21.93, 2.92) * mm});
            skLineSegment(sketch, "E14136", {"start": v(21.93, 2.92) * mm, "end": v(22.49, 3.69) * mm});
            skLineSegment(sketch, "E14137", {"start": v(22.49, 3.69) * mm, "end": v(23.02, 4.46) * mm});
            skLineSegment(sketch, "E14138", {"start": v(23.02, 4.46) * mm, "end": v(23.52, 5.2) * mm});
            skLineSegment(sketch, "E14139", {"start": v(23.52, 5.2) * mm, "end": v(23.97, 5.92) * mm});
            skLineSegment(sketch, "E14140", {"start": v(23.97, 5.92) * mm, "end": v(24.23, 6.37) * mm});
            skLineSegment(sketch, "E14141", {"start": v(24.23, 6.37) * mm, "end": v(24.49, 6.86) * mm});
            skLineSegment(sketch, "E14142", {"start": v(24.49, 6.86) * mm, "end": v(24.74, 7.37) * mm});
            skLineSegment(sketch, "E14143", {"start": v(24.74, 7.37) * mm, "end": v(24.99, 7.9) * mm});
            skLineSegment(sketch, "E14144", {"start": v(24.99, 7.9) * mm, "end": v(25.46, 8.94) * mm});
            skLineSegment(sketch, "E14145", {"start": v(25.46, 8.94) * mm, "end": v(25.7, 9.44) * mm});
            skLineSegment(sketch, "E14146", {"start": v(25.7, 9.44) * mm, "end": v(25.92, 9.91) * mm});
            skLineSegment(sketch, "E14147", {"start": v(25.92, 9.91) * mm, "end": v(26.36, 10.83) * mm});
            skLineSegment(sketch, "E14148", {"start": v(26.36, 10.83) * mm, "end": v(26.8, 11.76) * mm});
            skLineSegment(sketch, "E14149", {"start": v(26.8, 11.76) * mm, "end": v(27.22, 12.7) * mm});
            skLineSegment(sketch, "E14150", {"start": v(27.22, 12.7) * mm, "end": v(27.63, 13.66) * mm});
            skLineSegment(sketch, "E14151", {"start": v(27.63, 13.66) * mm, "end": v(28.05, 14.64) * mm});
            skLineSegment(sketch, "E14152", {"start": v(28.05, 14.64) * mm, "end": v(28.45, 15.63) * mm});
            skLineSegment(sketch, "E14153", {"start": v(28.45, 15.63) * mm, "end": v(28.86, 16.66) * mm});
            skLineSegment(sketch, "E14154", {"start": v(28.86, 16.66) * mm, "end": v(29.26, 17.71) * mm});
            skLineSegment(sketch, "E14155", {"start": v(29.26, 17.71) * mm, "end": v(29.66, 18.8) * mm});
            skLineSegment(sketch, "E14156", {"start": v(29.66, 18.8) * mm, "end": v(30.06, 19.91) * mm});
            skLineSegment(sketch, "E14157", {"start": v(30.06, 19.91) * mm, "end": v(30.47, 21.06) * mm});
            skLineSegment(sketch, "E14158", {"start": v(30.47, 21.06) * mm, "end": v(30.87, 22.26) * mm});
            skLineSegment(sketch, "E14159", {"start": v(30.87, 22.26) * mm, "end": v(31.28, 23.5) * mm});
            skLineSegment(sketch, "E14160", {"start": v(31.28, 23.5) * mm, "end": v(31.7, 24.78) * mm});
            skLineSegment(sketch, "E14161", {"start": v(31.7, 24.78) * mm, "end": v(32.11, 26.11) * mm});
            skLineSegment(sketch, "E14162", {"start": v(32.11, 26.11) * mm, "end": v(32.54, 27.5) * mm});
            skLineSegment(sketch, "E14163", {"start": v(32.54, 27.5) * mm, "end": v(32.63, 27.83) * mm});
            skLineSegment(sketch, "E14164", {"start": v(32.63, 27.83) * mm, "end": v(32.71, 28.18) * mm});
            skLineSegment(sketch, "E14165", {"start": v(32.71, 28.18) * mm, "end": v(32.86, 28.93) * mm});
            skLineSegment(sketch, "E14166", {"start": v(32.86, 28.93) * mm, "end": v(33, 29.72) * mm});
            skLineSegment(sketch, "E14167", {"start": v(33, 29.72) * mm, "end": v(33.15, 30.51) * mm});
            skLineSegment(sketch, "E14168", {"start": v(33.15, 30.51) * mm, "end": v(33.24, 30.9) * mm});
            skLineSegment(sketch, "E14169", {"start": v(33.24, 30.9) * mm, "end": v(33.34, 31.29) * mm});
            skLineSegment(sketch, "E14170", {"start": v(33.34, 31.29) * mm, "end": v(33.45, 31.66) * mm});
            skLineSegment(sketch, "E14171", {"start": v(33.45, 31.66) * mm, "end": v(33.57, 32.02) * mm});
            skLineSegment(sketch, "E14172", {"start": v(33.57, 32.02) * mm, "end": v(33.72, 32.36) * mm});
            skLineSegment(sketch, "E14173", {"start": v(33.72, 32.36) * mm, "end": v(33.8, 32.52) * mm});
            skLineSegment(sketch, "E14174", {"start": v(33.8, 32.52) * mm, "end": v(33.88, 32.67) * mm});
            skLineSegment(sketch, "E14175", {"start": v(33.88, 32.67) * mm, "end": v(33.97, 32.82) * mm});
            skLineSegment(sketch, "E14176", {"start": v(33.97, 32.82) * mm, "end": v(34.07, 32.97) * mm});
            skLineSegment(sketch, "E14177", {"start": v(34.07, 32.97) * mm, "end": v(34.17, 33.1) * mm});
            skLineSegment(sketch, "E14178", {"start": v(34.17, 33.1) * mm, "end": v(34.28, 33.23) * mm});
            skLineSegment(sketch, "E14179", {"start": v(34.28, 33.23) * mm, "end": v(34.38, 33.33) * mm});
            skLineSegment(sketch, "E14180", {"start": v(34.38, 33.33) * mm, "end": v(34.48, 33.41) * mm});
            skLineSegment(sketch, "E14181", {"start": v(34.48, 33.41) * mm, "end": v(34.6, 33.49) * mm});
            skLineSegment(sketch, "E14182", {"start": v(34.6, 33.49) * mm, "end": v(34.73, 33.56) * mm});
            skLineSegment(sketch, "E14183", {"start": v(34.73, 33.56) * mm, "end": v(35, 33.68) * mm});
            skLineSegment(sketch, "E14184", {"start": v(35, 33.68) * mm, "end": v(35.3, 33.78) * mm});
            skLineSegment(sketch, "E14185", {"start": v(35.3, 33.78) * mm, "end": v(35.9, 33.95) * mm});
            skLineSegment(sketch, "E14186", {"start": v(35.9, 33.95) * mm, "end": v(36.18, 34.04) * mm});
            skLineSegment(sketch, "E14187", {"start": v(36.18, 34.04) * mm, "end": v(36.44, 34.14) * mm});
            skLineSegment(sketch, "E14188", {"start": v(36.44, 34.14) * mm, "end": v(36.85, 34.88) * mm});
            skLineSegment(sketch, "E14189", {"start": v(36.85, 34.88) * mm, "end": v(36.93, 35.05) * mm});
            skLineSegment(sketch, "E14190", {"start": v(36.93, 35.05) * mm, "end": v(37.02, 35.26) * mm});
            skLineSegment(sketch, "E14191", {"start": v(37.02, 35.26) * mm, "end": v(37.1, 35.5) * mm});
            skLineSegment(sketch, "E14192", {"start": v(37.1, 35.5) * mm, "end": v(37.19, 35.74) * mm});
            skLineSegment(sketch, "E14193", {"start": v(37.19, 35.74) * mm, "end": v(37.26, 36) * mm});
            skLineSegment(sketch, "E14194", {"start": v(37.26, 36) * mm, "end": v(37.33, 36.27) * mm});
            skLineSegment(sketch, "E14195", {"start": v(37.33, 36.27) * mm, "end": v(37.4, 36.53) * mm});
            skLineSegment(sketch, "E14196", {"start": v(37.4, 36.53) * mm, "end": v(37.44, 36.78) * mm});
            skLineSegment(sketch, "E14197", {"start": v(37.44, 36.78) * mm, "end": v(37.63, 37.93) * mm});
            skLineSegment(sketch, "E14198", {"start": v(37.63, 37.93) * mm, "end": v(38.34, 40.02) * mm});
            skLineSegment(sketch, "E14199", {"start": v(38.34, 40.02) * mm, "end": v(38.24, 40.23) * mm});
            skLineSegment(sketch, "E14200", {"start": v(38.24, 40.23) * mm, "end": v(37.67, 41.48) * mm});
            skLineSegment(sketch, "E14201", {"start": v(37.67, 41.48) * mm, "end": v(37.4, 42.06) * mm});
            skLineSegment(sketch, "E14202", {"start": v(37.4, 42.06) * mm, "end": v(37.12, 42.57) * mm});
            skLineSegment(sketch, "E14203", {"start": v(37.12, 42.57) * mm, "end": v(36.53, 43.52) * mm});
            skLineSegment(sketch, "E14204", {"start": v(36.53, 43.52) * mm, "end": v(36.2, 44.02) * mm});
            skLineSegment(sketch, "E14205", {"start": v(36.2, 44.02) * mm, "end": v(35.88, 44.55) * mm});
            skLineSegment(sketch, "E14206", {"start": v(35.88, 44.55) * mm, "end": v(35.68, 44.54) * mm});
            skLineSegment(sketch, "E14207", {"start": v(35.68, 44.54) * mm, "end": v(35.59, 44.53) * mm});
            skLineSegment(sketch, "E14208", {"start": v(35.59, 44.53) * mm, "end": v(33.8, 43.94) * mm});
            skLineSegment(sketch, "E14209", {"start": v(33.8, 43.94) * mm, "end": v(31.94, 43.32) * mm});
            skLineSegment(sketch, "E14210", {"start": v(31.94, 43.32) * mm, "end": v(31, 43) * mm});
            skLineSegment(sketch, "E14211", {"start": v(31, 43) * mm, "end": v(30.1, 42.67) * mm});
            skLineSegment(sketch, "E14212", {"start": v(30.1, 42.67) * mm, "end": v(29.21, 42.34) * mm});
            skLineSegment(sketch, "E14213", {"start": v(29.21, 42.34) * mm, "end": v(28.8, 42.16) * mm});
            skLineSegment(sketch, "E14214", {"start": v(28.8, 42.16) * mm, "end": v(28.38, 42) * mm});
            skLineSegment(sketch, "E14215", {"start": v(28.38, 42) * mm, "end": v(27.42, 41.57) * mm});
            skLineSegment(sketch, "E14216", {"start": v(27.42, 41.57) * mm, "end": v(26.91, 41.34) * mm});
            skLineSegment(sketch, "E14217", {"start": v(26.91, 41.34) * mm, "end": v(26.4, 41.09) * mm});
            skLineSegment(sketch, "E14218", {"start": v(26.4, 41.09) * mm, "end": v(25.9, 40.83) * mm});
            skLineSegment(sketch, "E14219", {"start": v(25.9, 40.83) * mm, "end": v(25.41, 40.55) * mm});
            skLineSegment(sketch, "E14220", {"start": v(25.41, 40.55) * mm, "end": v(25.18, 40.41) * mm});
            skLineSegment(sketch, "E14221", {"start": v(25.18, 40.41) * mm, "end": v(24.96, 40.27) * mm});
            skLineSegment(sketch, "E14222", {"start": v(24.96, 40.27) * mm, "end": v(24.75, 40.12) * mm});
            skLineSegment(sketch, "E14223", {"start": v(24.75, 40.12) * mm, "end": v(24.55, 39.97) * mm});
            skLineSegment(sketch, "E14224", {"start": v(24.55, 39.97) * mm, "end": v(24.34, 39.79) * mm});
            skLineSegment(sketch, "E14225", {"start": v(24.34, 39.79) * mm, "end": v(24.12, 39.59) * mm});
            skLineSegment(sketch, "E14226", {"start": v(24.12, 39.59) * mm, "end": v(23.9, 39.37) * mm});
            skLineSegment(sketch, "E14227", {"start": v(23.9, 39.37) * mm, "end": v(23.68, 39.14) * mm});
            skLineSegment(sketch, "E14228", {"start": v(23.68, 39.14) * mm, "end": v(23.48, 38.9) * mm});
            skLineSegment(sketch, "E14229", {"start": v(23.48, 38.9) * mm, "end": v(23.3, 38.64) * mm});
            skLineSegment(sketch, "E14230", {"start": v(23.3, 38.64) * mm, "end": v(23.14, 38.4) * mm});
            skLineSegment(sketch, "E14231", {"start": v(23.14, 38.4) * mm, "end": v(23.08, 38.27) * mm});
            skLineSegment(sketch, "E14232", {"start": v(23.08, 38.27) * mm, "end": v(23.02, 38.14) * mm});
            skLineSegment(sketch, "E14233", {"start": v(23.02, 38.14) * mm, "end": v(22.96, 37.99) * mm});
            skLineSegment(sketch, "E14234", {"start": v(22.96, 37.99) * mm, "end": v(22.92, 37.82) * mm});
            skLineSegment(sketch, "E14235", {"start": v(22.92, 37.82) * mm, "end": v(22.88, 37.65) * mm});
            skLineSegment(sketch, "E14236", {"start": v(22.88, 37.65) * mm, "end": v(22.85, 37.47) * mm});
            skLineSegment(sketch, "E14237", {"start": v(22.85, 37.47) * mm, "end": v(22.82, 37.1) * mm});
            skLineSegment(sketch, "E14238", {"start": v(22.82, 37.1) * mm, "end": v(22.81, 36.71) * mm});
            skLineSegment(sketch, "E14239", {"start": v(22.81, 36.71) * mm, "end": v(22.82, 35.94) * mm});
            skLineSegment(sketch, "E14240", {"start": v(22.82, 35.94) * mm, "end": v(22.81, 35.58) * mm});
            skLineSegment(sketch, "E14241", {"start": v(22.81, 35.58) * mm, "end": v(22.8, 35.23) * mm});
            skLineSegment(sketch, "E14242", {"start": v(22.8, 35.23) * mm, "end": v(22.67, 33.72) * mm});
            skLineSegment(sketch, "E14243", {"start": v(22.67, 33.72) * mm, "end": v(22.53, 32.29) * mm});
            skLineSegment(sketch, "E14244", {"start": v(22.53, 32.29) * mm, "end": v(22.37, 30.94) * mm});
            skLineSegment(sketch, "E14245", {"start": v(22.37, 30.94) * mm, "end": v(22.2, 29.71) * mm});
            skLineSegment(sketch, "E14246", {"start": v(22.2, 29.71) * mm, "end": v(22.1, 29.14) * mm});
            skLineSegment(sketch, "E14247", {"start": v(22.1, 29.14) * mm, "end": v(22.01, 28.6) * mm});
            skLineSegment(sketch, "E14248", {"start": v(22.01, 28.6) * mm, "end": v(21.92, 28.09) * mm});
            skLineSegment(sketch, "E14249", {"start": v(21.92, 28.09) * mm, "end": v(21.82, 27.61) * mm});
            skLineSegment(sketch, "E14250", {"start": v(21.82, 27.61) * mm, "end": v(21.72, 27.18) * mm});
            skLineSegment(sketch, "E14251", {"start": v(21.72, 27.18) * mm, "end": v(21.62, 26.78) * mm});
            skLineSegment(sketch, "E14252", {"start": v(21.62, 26.78) * mm, "end": v(21.52, 26.42) * mm});
            skLineSegment(sketch, "E14253", {"start": v(21.52, 26.42) * mm, "end": v(21.41, 26.1) * mm});
            skLineSegment(sketch, "E14254", {"start": v(21.41, 26.1) * mm, "end": v(21.3, 25.77) * mm});
            skLineSegment(sketch, "E14255", {"start": v(21.3, 25.77) * mm, "end": v(21.2, 25.4) * mm});
            skLineSegment(sketch, "E14256", {"start": v(21.2, 25.4) * mm, "end": v(21.14, 25.23) * mm});
            skLineSegment(sketch, "E14257", {"start": v(21.14, 25.23) * mm, "end": v(21.08, 25.05) * mm});
            skLineSegment(sketch, "E14258", {"start": v(21.08, 25.05) * mm, "end": v(21.01, 24.89) * mm});
            skLineSegment(sketch, "E14259", {"start": v(21.01, 24.89) * mm, "end": v(20.93, 24.74) * mm});
            skLineSegment(sketch, "E14260", {"start": v(20.93, 24.74) * mm, "end": v(20.85, 24.62) * mm});
            skLineSegment(sketch, "E14261", {"start": v(20.85, 24.62) * mm, "end": v(20.74, 24.5) * mm});
            skLineSegment(sketch, "E14262", {"start": v(20.74, 24.5) * mm, "end": v(20.5, 24.25) * mm});
            skLineSegment(sketch, "E14263", {"start": v(20.5, 24.25) * mm, "end": v(20.26, 24.02) * mm});
            skLineSegment(sketch, "E14264", {"start": v(20.26, 24.02) * mm, "end": v(20.04, 23.8) * mm});
            skLineSegment(sketch, "E14265", {"start": v(20.04, 23.8) * mm, "end": v(19.82, 23.58) * mm});
            skLineSegment(sketch, "E14266", {"start": v(19.82, 23.58) * mm, "end": v(19.6, 23.38) * mm});
            skLineSegment(sketch, "E14267", {"start": v(19.6, 23.38) * mm, "end": v(19.39, 23.18) * mm});
            skLineSegment(sketch, "E14268", {"start": v(19.39, 23.18) * mm, "end": v(19.16, 23) * mm});
            skLineSegment(sketch, "E14269", {"start": v(19.16, 23) * mm, "end": v(18.94, 22.84) * mm});
            skLineSegment(sketch, "E14270", {"start": v(18.94, 22.84) * mm, "end": v(18.7, 22.68) * mm});
            skLineSegment(sketch, "E14271", {"start": v(18.7, 22.68) * mm, "end": v(18.46, 22.53) * mm});
            skLineSegment(sketch, "E14272", {"start": v(18.46, 22.53) * mm, "end": v(18.21, 22.4) * mm});
            skLineSegment(sketch, "E14273", {"start": v(18.21, 22.4) * mm, "end": v(17.95, 22.27) * mm});
            skLineSegment(sketch, "E14274", {"start": v(17.95, 22.27) * mm, "end": v(17.67, 22.15) * mm});
            skLineSegment(sketch, "E14275", {"start": v(17.67, 22.15) * mm, "end": v(17.39, 22.04) * mm});
            skLineSegment(sketch, "E14276", {"start": v(17.39, 22.04) * mm, "end": v(17.08, 21.94) * mm});
            skLineSegment(sketch, "E14277", {"start": v(17.08, 21.94) * mm, "end": v(16.76, 21.84) * mm});
            skLineSegment(sketch, "E14278", {"start": v(16.76, 21.84) * mm, "end": v(16.42, 21.74) * mm});
            skLineSegment(sketch, "E14279", {"start": v(16.42, 21.74) * mm, "end": v(16.07, 21.65) * mm});
            skLineSegment(sketch, "E14280", {"start": v(16.07, 21.65) * mm, "end": v(15.69, 21.57) * mm});
            skLineSegment(sketch, "E14281", {"start": v(15.69, 21.57) * mm, "end": v(14.01, 21.2) * mm});
            skLineSegment(sketch, "E14282", {"start": v(14.01, 21.2) * mm, "end": v(16, 18.94) * mm});
            skLineSegment(sketch, "E14283", {"start": v(16, 18.94) * mm, "end": v(16, 17.28) * mm});
            skLineSegment(sketch, "E14284", {"start": v(16, 17.28) * mm, "end": v(17.46, 15.32) * mm});
            skLineSegment(sketch, "E14285", {"start": v(17.46, 15.32) * mm, "end": v(17.46, 14.18) * mm});
            skLineSegment(sketch, "E14286", {"start": v(17.46, 14.18) * mm, "end": v(17.45, 13.73) * mm});
            skLineSegment(sketch, "E14287", {"start": v(17.45, 13.73) * mm, "end": v(17.42, 13.33) * mm});
            skLineSegment(sketch, "E14288", {"start": v(17.42, 13.33) * mm, "end": v(17.4, 13) * mm});
            skLineSegment(sketch, "E14289", {"start": v(17.4, 13) * mm, "end": v(17.39, 12.78) * mm});
            skLineSegment(sketch, "E14290", {"start": v(17.39, 12.78) * mm, "end": v(17.4, 12.34) * mm});
            skLineSegment(sketch, "E14291", {"start": v(17.4, 12.34) * mm, "end": v(17.4, 11.9) * mm});
            skLineSegment(sketch, "E14292", {"start": v(17.4, 11.9) * mm, "end": v(17.4, 11.44) * mm});
            skLineSegment(sketch, "E14293", {"start": v(17.4, 11.44) * mm, "end": v(17.38, 11) * mm});
            skLineSegment(sketch, "E14294", {"start": v(17.38, 11) * mm, "end": v(17.36, 10.78) * mm});
            skLineSegment(sketch, "E14295", {"start": v(17.36, 10.78) * mm, "end": v(17.33, 10.56) * mm});
            skLineSegment(sketch, "E14296", {"start": v(17.33, 10.56) * mm, "end": v(17.28, 10.35) * mm});
            skLineSegment(sketch, "E14297", {"start": v(17.28, 10.35) * mm, "end": v(17.23, 10.15) * mm});
            skLineSegment(sketch, "E14298", {"start": v(17.23, 10.15) * mm, "end": v(17.16, 9.95) * mm});
            skLineSegment(sketch, "E14299", {"start": v(17.16, 9.95) * mm, "end": v(17.07, 9.76) * mm});
            skLineSegment(sketch, "E14300", {"start": v(17.07, 9.76) * mm, "end": v(16.97, 9.57) * mm});
            skLineSegment(sketch, "E14301", {"start": v(16.97, 9.57) * mm, "end": v(16.85, 9.4) * mm});
            skLineSegment(sketch, "E14302", {"start": v(12.62, 17.45) * mm, "end": v(12.87, 17.34) * mm});
            skLineSegment(sketch, "E14303", {"start": v(12.87, 17.34) * mm, "end": v(13.13, 17.25) * mm});
            skLineSegment(sketch, "E14304", {"start": v(13.13, 17.25) * mm, "end": v(13.4, 17.17) * mm});
            skLineSegment(sketch, "E14305", {"start": v(13.4, 17.17) * mm, "end": v(13.64, 17.1) * mm});
            skLineSegment(sketch, "E14306", {"start": v(13.64, 17.1) * mm, "end": v(13.88, 17.06) * mm});
            skLineSegment(sketch, "E14307", {"start": v(13.88, 17.06) * mm, "end": v(14.09, 17.02) * mm});
            skLineSegment(sketch, "E14308", {"start": v(14.09, 17.02) * mm, "end": v(14.27, 17) * mm});
            skLineSegment(sketch, "E14309", {"start": v(14.27, 17) * mm, "end": v(14.4, 17) * mm});
            skLineSegment(sketch, "E14310", {"start": v(14.4, 17) * mm, "end": v(14.53, 17) * mm});
            skLineSegment(sketch, "E14311", {"start": v(14.53, 17) * mm, "end": v(14.67, 17) * mm});
            skLineSegment(sketch, "E14312", {"start": v(14.67, 17) * mm, "end": v(14.8, 17.01) * mm});
            skLineSegment(sketch, "E14313", {"start": v(14.8, 17.01) * mm, "end": v(14.93, 17.05) * mm});
            skLineSegment(sketch, "E14314", {"start": v(14.93, 17.05) * mm, "end": v(15.06, 17.12) * mm});
            skLineSegment(sketch, "E14315", {"start": v(15.06, 17.12) * mm, "end": v(15.19, 17.2) * mm});
            skLineSegment(sketch, "E14316", {"start": v(15.19, 17.2) * mm, "end": v(15.32, 17.3) * mm});
            skLineSegment(sketch, "E14317", {"start": v(15.32, 17.3) * mm, "end": v(15.44, 17.4) * mm});
            skLineSegment(sketch, "E14318", {"start": v(15.44, 17.4) * mm, "end": v(15.54, 17.53) * mm});
            skLineSegment(sketch, "E14319", {"start": v(15.54, 17.53) * mm, "end": v(15.63, 17.65) * mm});
            skLineSegment(sketch, "E14320", {"start": v(15.63, 17.65) * mm, "end": v(15.69, 17.79) * mm});
            skLineSegment(sketch, "E14321", {"start": v(15.69, 17.79) * mm, "end": v(15.7, 17.85) * mm});
            skLineSegment(sketch, "E14322", {"start": v(15.7, 17.85) * mm, "end": v(15.72, 17.92) * mm});
            skLineSegment(sketch, "E14323", {"start": v(15.72, 17.92) * mm, "end": v(15.72, 18.05) * mm});
            skLineSegment(sketch, "E14324", {"start": v(15.72, 18.05) * mm, "end": v(15.71, 18.18) * mm});
            skLineSegment(sketch, "E14325", {"start": v(15.71, 18.18) * mm, "end": v(15.69, 18.3) * mm});
            skLineSegment(sketch, "E14326", {"start": v(15.69, 18.3) * mm, "end": v(15.65, 18.44) * mm});
            skLineSegment(sketch, "E14327", {"start": v(15.65, 18.44) * mm, "end": v(15.6, 18.57) * mm});
            skLineSegment(sketch, "E14328", {"start": v(15.6, 18.57) * mm, "end": v(15.54, 18.7) * mm});
            skLineSegment(sketch, "E14329", {"start": v(15.54, 18.7) * mm, "end": v(15.4, 18.97) * mm});
            skLineSegment(sketch, "E14330", {"start": v(15.4, 18.97) * mm, "end": v(15.23, 19.22) * mm});
            skLineSegment(sketch, "E14331", {"start": v(15.23, 19.22) * mm, "end": v(15.05, 19.47) * mm});
            skLineSegment(sketch, "E14332", {"start": v(15.05, 19.47) * mm, "end": v(14.7, 19.9) * mm});
            skLineSegment(sketch, "E14333", {"start": v(14.7, 19.9) * mm, "end": v(14.5, 20.09) * mm});
            skLineSegment(sketch, "E14334", {"start": v(14.5, 20.09) * mm, "end": v(14.29, 20.27) * mm});
            skLineSegment(sketch, "E14335", {"start": v(14.29, 20.27) * mm, "end": v(14.05, 20.45) * mm});
            skLineSegment(sketch, "E14336", {"start": v(14.05, 20.45) * mm, "end": v(13.8, 20.62) * mm});
            skLineSegment(sketch, "E14337", {"start": v(13.8, 20.62) * mm, "end": v(13.27, 20.94) * mm});
            skLineSegment(sketch, "E14338", {"start": v(13.27, 20.94) * mm, "end": v(13.03, 21.1) * mm});
            skLineSegment(sketch, "E14339", {"start": v(13.03, 21.1) * mm, "end": v(12.8, 21.25) * mm});
            skLineSegment(sketch, "E14340", {"start": v(12.8, 21.25) * mm, "end": v(12.59, 21.04) * mm});
            skLineSegment(sketch, "E14341", {"start": v(12.59, 21.04) * mm, "end": v(12.55, 20.98) * mm});
            skLineSegment(sketch, "E14342", {"start": v(12.55, 20.98) * mm, "end": v(12.5, 20.89) * mm});
            skLineSegment(sketch, "E14343", {"start": v(12.5, 20.89) * mm, "end": v(12.47, 20.78) * mm});
            skLineSegment(sketch, "E14344", {"start": v(12.47, 20.78) * mm, "end": v(12.44, 20.64) * mm});
            skLineSegment(sketch, "E14345", {"start": v(12.44, 20.64) * mm, "end": v(12.41, 20.49) * mm});
            skLineSegment(sketch, "E14346", {"start": v(12.41, 20.49) * mm, "end": v(12.4, 20.32) * mm});
            skLineSegment(sketch, "E14347", {"start": v(12.4, 20.32) * mm, "end": v(12.38, 20.15) * mm});
            skLineSegment(sketch, "E14348", {"start": v(12.38, 20.15) * mm, "end": v(12.37, 19.98) * mm});
            skLineSegment(sketch, "E14349", {"start": v(12.37, 19.98) * mm, "end": v(12.36, 19.8) * mm});
            skLineSegment(sketch, "E14350", {"start": v(12.36, 19.8) * mm, "end": v(12.34, 19.62) * mm});
            skLineSegment(sketch, "E14351", {"start": v(12.34, 19.62) * mm, "end": v(12.3, 19.44) * mm});
            skLineSegment(sketch, "E14352", {"start": v(12.3, 19.44) * mm, "end": v(12.27, 19.27) * mm});
            skLineSegment(sketch, "E14353", {"start": v(12.27, 19.27) * mm, "end": v(12.18, 18.94) * mm});
            skLineSegment(sketch, "E14354", {"start": v(12.18, 18.94) * mm, "end": v(12.09, 18.68) * mm});
            skLineSegment(sketch, "E14355", {"start": v(12.09, 18.68) * mm, "end": v(12.07, 18.62) * mm});
            skLineSegment(sketch, "E14356", {"start": v(12.07, 18.62) * mm, "end": v(12.07, 18.54) * mm});
            skLineSegment(sketch, "E14357", {"start": v(12.07, 18.54) * mm, "end": v(12.08, 18.46) * mm});
            skLineSegment(sketch, "E14358", {"start": v(12.08, 18.46) * mm, "end": v(12.1, 18.37) * mm});
            skLineSegment(sketch, "E14359", {"start": v(12.1, 18.37) * mm, "end": v(12.16, 18.18) * mm});
            skLineSegment(sketch, "E14360", {"start": v(12.16, 18.18) * mm, "end": v(12.25, 17.99) * mm});
            skLineSegment(sketch, "E14361", {"start": v(12.25, 17.99) * mm, "end": v(12.34, 17.8) * mm});
            skLineSegment(sketch, "E14362", {"start": v(12.34, 17.8) * mm, "end": v(12.45, 17.64) * mm});
            skLineSegment(sketch, "E14363", {"start": v(12.45, 17.64) * mm, "end": v(12.54, 17.52) * mm});
            skLineSegment(sketch, "E14364", {"start": v(12.54, 17.52) * mm, "end": v(12.58, 17.48) * mm});
            skLineSegment(sketch, "E14365", {"start": v(12.58, 17.48) * mm, "end": v(12.62, 17.45) * mm});
            skLineSegment(sketch, "E14366", {"start": v(10.77, 18.77) * mm, "end": v(10.57, 18.88) * mm});
            skLineSegment(sketch, "E14367", {"start": v(10.57, 18.88) * mm, "end": v(10.38, 18.98) * mm});
            skLineSegment(sketch, "E14368", {"start": v(10.38, 18.98) * mm, "end": v(10.05, 19.12) * mm});
            skLineSegment(sketch, "E14369", {"start": v(10.05, 19.12) * mm, "end": v(9.92, 19.16) * mm});
            skLineSegment(sketch, "E14370", {"start": v(9.92, 19.16) * mm, "end": v(9.82, 19.19) * mm});
            skLineSegment(sketch, "E14371", {"start": v(9.82, 19.19) * mm, "end": v(9.76, 19.2) * mm});
            skLineSegment(sketch, "E14372", {"start": v(9.76, 19.2) * mm, "end": v(9.74, 19.19) * mm});
            skLineSegment(sketch, "E14373", {"start": v(9.74, 19.19) * mm, "end": v(9.74, 19.18) * mm});
            skLineSegment(sketch, "E14374", {"start": v(9.74, 19.18) * mm, "end": v(9.74, 18.96) * mm});
            skLineSegment(sketch, "E14375", {"start": v(9.74, 18.96) * mm, "end": v(9.74, 18.72) * mm});
            skLineSegment(sketch, "E14376", {"start": v(9.74, 18.72) * mm, "end": v(9.71, 18.46) * mm});
            skLineSegment(sketch, "E14377", {"start": v(9.71, 18.46) * mm, "end": v(9.68, 18.18) * mm});
            skLineSegment(sketch, "E14378", {"start": v(9.68, 18.18) * mm, "end": v(9.57, 17.59) * mm});
            skLineSegment(sketch, "E14379", {"start": v(9.57, 17.59) * mm, "end": v(9.44, 16.99) * mm});
            skLineSegment(sketch, "E14380", {"start": v(9.44, 16.99) * mm, "end": v(9.3, 16.41) * mm});
            skLineSegment(sketch, "E14381", {"start": v(9.3, 16.41) * mm, "end": v(9.15, 15.9) * mm});
            skLineSegment(sketch, "E14382", {"start": v(9.15, 15.9) * mm, "end": v(9.02, 15.51) * mm});
            skLineSegment(sketch, "E14383", {"start": v(9.02, 15.51) * mm, "end": v(8.96, 15.37) * mm});
            skLineSegment(sketch, "E14384", {"start": v(8.96, 15.37) * mm, "end": v(8.9, 15.26) * mm});
            skLineSegment(sketch, "E14385", {"start": v(8.9, 15.26) * mm, "end": v(8.84, 15.13) * mm});
            skLineSegment(sketch, "E14386", {"start": v(8.84, 15.13) * mm, "end": v(8.79, 14.99) * mm});
            skLineSegment(sketch, "E14387", {"start": v(8.79, 14.99) * mm, "end": v(8.7, 14.7) * mm});
            skLineSegment(sketch, "E14388", {"start": v(8.7, 14.7) * mm, "end": v(9.8, 14.39) * mm});
            skLineSegment(sketch, "E14389", {"start": v(9.8, 14.39) * mm, "end": v(10.03, 14.32) * mm});
            skLineSegment(sketch, "E14390", {"start": v(10.03, 14.32) * mm, "end": v(10.3, 14.26) * mm});
            skLineSegment(sketch, "E14391", {"start": v(10.3, 14.26) * mm, "end": v(10.88, 14.15) * mm});
            skLineSegment(sketch, "E14392", {"start": v(10.88, 14.15) * mm, "end": v(11.45, 14.08) * mm});
            skLineSegment(sketch, "E14393", {"start": v(11.45, 14.08) * mm, "end": v(11.71, 14.05) * mm});
            skLineSegment(sketch, "E14394", {"start": v(11.71, 14.05) * mm, "end": v(11.95, 14.04) * mm});
            skLineSegment(sketch, "E14395", {"start": v(11.95, 14.04) * mm, "end": v(13, 14) * mm});
            skLineSegment(sketch, "E14396", {"start": v(13, 14) * mm, "end": v(13.1, 14.17) * mm});
            skLineSegment(sketch, "E14397", {"start": v(13.1, 14.17) * mm, "end": v(13.22, 14.33) * mm});
            skLineSegment(sketch, "E14398", {"start": v(13.22, 14.33) * mm, "end": v(13.27, 14.42) * mm});
            skLineSegment(sketch, "E14399", {"start": v(13.27, 14.42) * mm, "end": v(13.31, 14.5) * mm});
            skLineSegment(sketch, "E14400", {"start": v(13.31, 14.5) * mm, "end": v(13.34, 14.6) * mm});
            skLineSegment(sketch, "E14401", {"start": v(13.34, 14.6) * mm, "end": v(13.35, 14.69) * mm});
            skLineSegment(sketch, "E14402", {"start": v(13.35, 14.69) * mm, "end": v(13.33, 14.79) * mm});
            skLineSegment(sketch, "E14403", {"start": v(13.33, 14.79) * mm, "end": v(13.3, 14.91) * mm});
            skLineSegment(sketch, "E14404", {"start": v(13.3, 14.91) * mm, "end": v(13.24, 15.06) * mm});
            skLineSegment(sketch, "E14405", {"start": v(13.24, 15.06) * mm, "end": v(13.16, 15.22) * mm});
            skLineSegment(sketch, "E14406", {"start": v(13.16, 15.22) * mm, "end": v(12.95, 15.57) * mm});
            skLineSegment(sketch, "E14407", {"start": v(12.95, 15.57) * mm, "end": v(12.7, 15.95) * mm});
            skLineSegment(sketch, "E14408", {"start": v(12.7, 15.95) * mm, "end": v(12.16, 16.7) * mm});
            skLineSegment(sketch, "E14409", {"start": v(12.16, 16.7) * mm, "end": v(11.7, 17.3) * mm});
            skLineSegment(sketch, "E14410", {"start": v(11.7, 17.3) * mm, "end": v(11.6, 17.47) * mm});
            skLineSegment(sketch, "E14411", {"start": v(11.6, 17.47) * mm, "end": v(11.48, 17.67) * mm});
            skLineSegment(sketch, "E14412", {"start": v(11.48, 17.67) * mm, "end": v(11.22, 18.13) * mm});
            skLineSegment(sketch, "E14413", {"start": v(11.22, 18.13) * mm, "end": v(11.09, 18.35) * mm});
            skLineSegment(sketch, "E14414", {"start": v(11.09, 18.35) * mm, "end": v(10.97, 18.54) * mm});
            skLineSegment(sketch, "E14415", {"start": v(10.97, 18.54) * mm, "end": v(10.86, 18.69) * mm});
            skLineSegment(sketch, "E14416", {"start": v(10.86, 18.69) * mm, "end": v(10.81, 18.74) * mm});
            skLineSegment(sketch, "E14417", {"start": v(10.81, 18.74) * mm, "end": v(10.77, 18.77) * mm});
            skLineSegment(sketch, "E14418", {"start": v(-9.19, 11.22) * mm, "end": v(-9.25, 11.15) * mm});
            skLineSegment(sketch, "E14419", {"start": v(-9.25, 11.15) * mm, "end": v(-9.33, 11.09) * mm});
            skLineSegment(sketch, "E14420", {"start": v(-9.33, 11.09) * mm, "end": v(-9.42, 11.03) * mm});
            skLineSegment(sketch, "E14421", {"start": v(-9.42, 11.03) * mm, "end": v(-9.53, 10.98) * mm});
            skLineSegment(sketch, "E14422", {"start": v(-9.53, 10.98) * mm, "end": v(-9.74, 10.91) * mm});
            skLineSegment(sketch, "E14423", {"start": v(-9.74, 10.91) * mm, "end": v(-9.91, 10.88) * mm});
            skLineSegment(sketch, "E14424", {"start": v(-9.91, 10.88) * mm, "end": v(-11.25, 10.65) * mm});
            skLineSegment(sketch, "E14425", {"start": v(-11.25, 10.65) * mm, "end": v(-11.47, 10.87) * mm});
            skLineSegment(sketch, "E14426", {"start": v(-11.47, 10.87) * mm, "end": v(-11.72, 11.11) * mm});
            skLineSegment(sketch, "E14427", {"start": v(-11.72, 11.11) * mm, "end": v(-11.84, 11.24) * mm});
            skLineSegment(sketch, "E14428", {"start": v(-11.84, 11.24) * mm, "end": v(-11.94, 11.37) * mm});
            skLineSegment(sketch, "E14429", {"start": v(-11.94, 11.37) * mm, "end": v(-12.02, 11.5) * mm});
            skLineSegment(sketch, "E14430", {"start": v(-12.02, 11.5) * mm, "end": v(-12.05, 11.57) * mm});
            skLineSegment(sketch, "E14431", {"start": v(-12.05, 11.57) * mm, "end": v(-12.07, 11.64) * mm});
            skLineSegment(sketch, "E14432", {"start": v(-12.07, 11.64) * mm, "end": v(-12.1, 11.77) * mm});
            skLineSegment(sketch, "E14433", {"start": v(-12.1, 11.77) * mm, "end": v(-12.1, 11.9) * mm});
            skLineSegment(sketch, "E14434", {"start": v(-12.1, 11.9) * mm, "end": v(-12.1, 12.02) * mm});
            skLineSegment(sketch, "E14435", {"start": v(-12.1, 12.02) * mm, "end": v(-12.07, 12.16) * mm});
            skLineSegment(sketch, "E14436", {"start": v(-12.07, 12.16) * mm, "end": v(-12, 12.43) * mm});
            skLineSegment(sketch, "E14437", {"start": v(-12, 12.43) * mm, "end": v(-11.91, 12.71) * mm});
            skLineSegment(sketch, "E14438", {"start": v(-11.91, 12.71) * mm, "end": v(-11.7, 13.27) * mm});
            skLineSegment(sketch, "E14439", {"start": v(-11.7, 13.27) * mm, "end": v(-11.6, 13.53) * mm});
            skLineSegment(sketch, "E14440", {"start": v(-11.6, 13.53) * mm, "end": v(-11.52, 13.78) * mm});
            skLineSegment(sketch, "E14441", {"start": v(-11.52, 13.78) * mm, "end": v(-10.05, 14.22) * mm});
            skLineSegment(sketch, "E14442", {"start": v(-10.05, 14.22) * mm, "end": v(-9.46, 14.39) * mm});
            skLineSegment(sketch, "E14443", {"start": v(-9.46, 14.39) * mm, "end": v(-8.94, 14.53) * mm});
            skLineSegment(sketch, "E14444", {"start": v(-8.94, 14.53) * mm, "end": v(-8.54, 14.63) * mm});
            skLineSegment(sketch, "E14445", {"start": v(-8.54, 14.63) * mm, "end": v(-8.34, 14.66) * mm});
            skLineSegment(sketch, "E14446", {"start": v(-8.34, 14.66) * mm, "end": v(-8.1, 14.67) * mm});
            skLineSegment(sketch, "E14447", {"start": v(-8.1, 14.67) * mm, "end": v(-8.42, 13.82) * mm});
            skLineSegment(sketch, "E14448", {"start": v(-8.42, 13.82) * mm, "end": v(-8.48, 13.64) * mm});
            skLineSegment(sketch, "E14449", {"start": v(-8.48, 13.64) * mm, "end": v(-8.54, 13.44) * mm});
            skLineSegment(sketch, "E14450", {"start": v(-8.54, 13.44) * mm, "end": v(-8.63, 13.04) * mm});
            skLineSegment(sketch, "E14451", {"start": v(-8.63, 13.04) * mm, "end": v(-8.7, 12.64) * mm});
            skLineSegment(sketch, "E14452", {"start": v(-8.7, 12.64) * mm, "end": v(-8.76, 12.3) * mm});
            skLineSegment(sketch, "E14453", {"start": v(-8.76, 12.3) * mm, "end": v(-8.79, 12.16) * mm});
            skLineSegment(sketch, "E14454", {"start": v(-8.79, 12.16) * mm, "end": v(-8.83, 12.02) * mm});
            skLineSegment(sketch, "E14455", {"start": v(-8.83, 12.02) * mm, "end": v(-8.92, 11.75) * mm});
            skLineSegment(sketch, "E14456", {"start": v(-8.92, 11.75) * mm, "end": v(-9.05, 11.48) * mm});
            skLineSegment(sketch, "E14457", {"start": v(-9.05, 11.48) * mm, "end": v(-9.19, 11.22) * mm});
            skLineSegment(sketch, "E14458", {"start": v(-11.4, 17.9) * mm, "end": v(-11.42, 17.85) * mm});
            skLineSegment(sketch, "E14459", {"start": v(-11.42, 17.85) * mm, "end": v(-11.46, 17.8) * mm});
            skLineSegment(sketch, "E14460", {"start": v(-11.46, 17.8) * mm, "end": v(-11.57, 17.72) * mm});
            skLineSegment(sketch, "E14461", {"start": v(-11.57, 17.72) * mm, "end": v(-11.81, 17.58) * mm});
            skLineSegment(sketch, "E14462", {"start": v(-11.81, 17.58) * mm, "end": v(-11.94, 17.51) * mm});
            skLineSegment(sketch, "E14463", {"start": v(-11.94, 17.51) * mm, "end": v(-12.06, 17.46) * mm});
            skLineSegment(sketch, "E14464", {"start": v(-12.06, 17.46) * mm, "end": v(-12.2, 17.4) * mm});
            skLineSegment(sketch, "E14465", {"start": v(-12.2, 17.4) * mm, "end": v(-12.32, 17.37) * mm});
            skLineSegment(sketch, "E14466", {"start": v(-12.32, 17.37) * mm, "end": v(-12.44, 17.34) * mm});
            skLineSegment(sketch, "E14467", {"start": v(-12.44, 17.34) * mm, "end": v(-12.57, 17.32) * mm});
            skLineSegment(sketch, "E14468", {"start": v(-12.57, 17.32) * mm, "end": v(-12.69, 17.3) * mm});
            skLineSegment(sketch, "E14469", {"start": v(-12.69, 17.3) * mm, "end": v(-12.8, 17.3) * mm});
            skLineSegment(sketch, "E14470", {"start": v(-12.8, 17.3) * mm, "end": v(-12.96, 17.3) * mm});
            skLineSegment(sketch, "E14471", {"start": v(-12.96, 17.3) * mm, "end": v(-13.13, 17.31) * mm});
            skLineSegment(sketch, "E14472", {"start": v(-13.13, 17.31) * mm, "end": v(-13.3, 17.34) * mm});
            skLineSegment(sketch, "E14473", {"start": v(-13.3, 17.34) * mm, "end": v(-13.47, 17.37) * mm});
            skLineSegment(sketch, "E14474", {"start": v(-13.47, 17.37) * mm, "end": v(-13.64, 17.42) * mm});
            skLineSegment(sketch, "E14475", {"start": v(-13.64, 17.42) * mm, "end": v(-13.79, 17.5) * mm});
            skLineSegment(sketch, "E14476", {"start": v(-13.79, 17.5) * mm, "end": v(-13.92, 17.58) * mm});
            skLineSegment(sketch, "E14477", {"start": v(-13.92, 17.58) * mm, "end": v(-13.97, 17.63) * mm});
            skLineSegment(sketch, "E14478", {"start": v(-13.97, 17.63) * mm, "end": v(-14.02, 17.68) * mm});
            skLineSegment(sketch, "E14479", {"start": v(-14.02, 17.68) * mm, "end": v(-14.08, 17.78) * mm});
            skLineSegment(sketch, "E14480", {"start": v(-14.08, 17.78) * mm, "end": v(-14.11, 17.9) * mm});
            skLineSegment(sketch, "E14481", {"start": v(-14.11, 17.9) * mm, "end": v(-14.14, 18.02) * mm});
            skLineSegment(sketch, "E14482", {"start": v(-14.14, 18.02) * mm, "end": v(-14.15, 18.15) * mm});
            skLineSegment(sketch, "E14483", {"start": v(-14.15, 18.15) * mm, "end": v(-14.14, 18.29) * mm});
            skLineSegment(sketch, "E14484", {"start": v(-14.14, 18.29) * mm, "end": v(-14.13, 18.43) * mm});
            skLineSegment(sketch, "E14485", {"start": v(-14.13, 18.43) * mm, "end": v(-14.1, 18.56) * mm});
            skLineSegment(sketch, "E14486", {"start": v(-14.1, 18.56) * mm, "end": v(-14.08, 18.68) * mm});
            skLineSegment(sketch, "E14487", {"start": v(-14.08, 18.68) * mm, "end": v(-14.06, 18.72) * mm});
            skLineSegment(sketch, "E14488", {"start": v(-14.06, 18.72) * mm, "end": v(-13.9, 18.97) * mm});
            skLineSegment(sketch, "E14489", {"start": v(-13.9, 18.97) * mm, "end": v(-13.52, 19.5) * mm});
            skLineSegment(sketch, "E14490", {"start": v(-13.52, 19.5) * mm, "end": v(-13.22, 19.92) * mm});
            skLineSegment(sketch, "E14491", {"start": v(-13.22, 19.92) * mm, "end": v(-12.91, 20.33) * mm});
            skLineSegment(sketch, "E14492", {"start": v(-12.91, 20.33) * mm, "end": v(-12.77, 20.5) * mm});
            skLineSegment(sketch, "E14493", {"start": v(-12.77, 20.5) * mm, "end": v(-12.53, 20.72) * mm});
            skLineSegment(sketch, "E14494", {"start": v(-12.53, 20.72) * mm, "end": v(-12.45, 20.77) * mm});
            skLineSegment(sketch, "E14495", {"start": v(-12.45, 20.77) * mm, "end": v(-12.21, 20.96) * mm});
            skLineSegment(sketch, "E14496", {"start": v(-12.21, 20.96) * mm, "end": v(-12.1, 21.06) * mm});
            skLineSegment(sketch, "E14497", {"start": v(-12.1, 21.06) * mm, "end": v(-11.98, 21.14) * mm});
            skLineSegment(sketch, "E14498", {"start": v(-11.98, 21.14) * mm, "end": v(-11.83, 21.23) * mm});
            skLineSegment(sketch, "E14499", {"start": v(-11.83, 21.23) * mm, "end": v(-11.7, 21.3) * mm});
            skLineSegment(sketch, "E14500", {"start": v(-11.7, 21.3) * mm, "end": v(-11.67, 21.2) * mm});
            skLineSegment(sketch, "E14501", {"start": v(-11.67, 21.2) * mm, "end": v(-11.62, 21.1) * mm});
            skLineSegment(sketch, "E14502", {"start": v(-11.62, 21.1) * mm, "end": v(-11.49, 20.88) * mm});
            skLineSegment(sketch, "E14503", {"start": v(-11.49, 20.88) * mm, "end": v(-11.34, 20.66) * mm});
            skLineSegment(sketch, "E14504", {"start": v(-11.34, 20.66) * mm, "end": v(-11.28, 20.54) * mm});
            skLineSegment(sketch, "E14505", {"start": v(-11.28, 20.54) * mm, "end": v(-11.22, 20.42) * mm});
            skLineSegment(sketch, "E14506", {"start": v(-11.22, 20.42) * mm, "end": v(-11.15, 20.25) * mm});
            skLineSegment(sketch, "E14507", {"start": v(-11.15, 20.25) * mm, "end": v(-11.1, 20.08) * mm});
            skLineSegment(sketch, "E14508", {"start": v(-11.1, 20.08) * mm, "end": v(-11.06, 19.91) * mm});
            skLineSegment(sketch, "E14509", {"start": v(-11.06, 19.91) * mm, "end": v(-11.04, 19.74) * mm});
            skLineSegment(sketch, "E14510", {"start": v(-11.04, 19.74) * mm, "end": v(-11.03, 19.57) * mm});
            skLineSegment(sketch, "E14511", {"start": v(-11.03, 19.57) * mm, "end": v(-11.03, 19.4) * mm});
            skLineSegment(sketch, "E14512", {"start": v(-11.03, 19.4) * mm, "end": v(-11.05, 19.23) * mm});
            skLineSegment(sketch, "E14513", {"start": v(-11.05, 19.23) * mm, "end": v(-11.07, 19.07) * mm});
            skLineSegment(sketch, "E14514", {"start": v(-11.07, 19.07) * mm, "end": v(-11.13, 18.75) * mm});
            skLineSegment(sketch, "E14515", {"start": v(-11.13, 18.75) * mm, "end": v(-11.21, 18.44) * mm});
            skLineSegment(sketch, "E14516", {"start": v(-11.21, 18.44) * mm, "end": v(-11.4, 17.9) * mm});
            skLineSegment(sketch, "E14517", {"start": v(-10.44, 19.8) * mm, "end": v(-10.2, 19.87) * mm});
            skLineSegment(sketch, "E14518", {"start": v(-10.2, 19.87) * mm, "end": v(-9.97, 19.95) * mm});
            skLineSegment(sketch, "E14519", {"start": v(-9.97, 19.95) * mm, "end": v(-9.5, 20.12) * mm});
            skLineSegment(sketch, "E14520", {"start": v(-9.5, 20.12) * mm, "end": v(-9.06, 20.32) * mm});
            skLineSegment(sketch, "E14521", {"start": v(-9.06, 20.32) * mm, "end": v(-8.62, 20.54) * mm});
            skLineSegment(sketch, "E14522", {"start": v(-8.62, 20.54) * mm, "end": v(-8.2, 20.78) * mm});
            skLineSegment(sketch, "E14523", {"start": v(-8.2, 20.78) * mm, "end": v(-7.8, 21.03) * mm});
            skLineSegment(sketch, "E14524", {"start": v(-7.8, 21.03) * mm, "end": v(-7.42, 21.28) * mm});
            skLineSegment(sketch, "E14525", {"start": v(-7.42, 21.28) * mm, "end": v(-7.06, 21.54) * mm});
            skLineSegment(sketch, "E14526", {"start": v(-7.06, 21.54) * mm, "end": v(-7.63, 21.9) * mm});
            skLineSegment(sketch, "E14527", {"start": v(-7.63, 21.9) * mm, "end": v(-8.69, 21.25) * mm});
            skLineSegment(sketch, "E14528", {"start": v(-8.69, 21.25) * mm, "end": v(-8.91, 21.12) * mm});
            skLineSegment(sketch, "E14529", {"start": v(-8.91, 21.12) * mm, "end": v(-9.14, 21) * mm});
            skLineSegment(sketch, "E14530", {"start": v(-9.14, 21) * mm, "end": v(-9.36, 20.9) * mm});
            skLineSegment(sketch, "E14531", {"start": v(-9.36, 20.9) * mm, "end": v(-9.58, 20.8) * mm});
            skLineSegment(sketch, "E14532", {"start": v(-9.58, 20.8) * mm, "end": v(-9.78, 20.72) * mm});
            skLineSegment(sketch, "E14533", {"start": v(-9.78, 20.72) * mm, "end": v(-9.96, 20.66) * mm});
            skLineSegment(sketch, "E14534", {"start": v(-9.96, 20.66) * mm, "end": v(-10.1, 20.62) * mm});
            skLineSegment(sketch, "E14535", {"start": v(-10.1, 20.62) * mm, "end": v(-10.23, 20.6) * mm});
            skLineSegment(sketch, "E14536", {"start": v(-10.23, 20.6) * mm, "end": v(-10.7, 20.6) * mm});
            skLineSegment(sketch, "E14537", {"start": v(-10.7, 20.6) * mm, "end": v(-10.83, 21.04) * mm});
            skLineSegment(sketch, "E14538", {"start": v(-10.83, 21.04) * mm, "end": v(-10.98, 21.5) * mm});
            skLineSegment(sketch, "E14539", {"start": v(-10.98, 21.5) * mm, "end": v(-11.04, 21.74) * mm});
            skLineSegment(sketch, "E14540", {"start": v(-11.04, 21.74) * mm, "end": v(-11.1, 21.97) * mm});
            skLineSegment(sketch, "E14541", {"start": v(-11.1, 21.97) * mm, "end": v(-11.14, 22.2) * mm});
            skLineSegment(sketch, "E14542", {"start": v(-11.14, 22.2) * mm, "end": v(-11.16, 22.4) * mm});
            skLineSegment(sketch, "E14543", {"start": v(-11.16, 22.4) * mm, "end": v(-11.16, 22.65) * mm});
            skLineSegment(sketch, "E14544", {"start": v(-11.16, 22.65) * mm, "end": v(-11.16, 22.9) * mm});
            skLineSegment(sketch, "E14545", {"start": v(-11.16, 22.9) * mm, "end": v(-11.12, 23.43) * mm});
            skLineSegment(sketch, "E14546", {"start": v(-11.12, 23.43) * mm, "end": v(-11.05, 23.98) * mm});
            skLineSegment(sketch, "E14547", {"start": v(-11.05, 23.98) * mm, "end": v(-10.96, 24.54) * mm});
            skLineSegment(sketch, "E14548", {"start": v(-10.96, 24.54) * mm, "end": v(-10.85, 25.09) * mm});
            skLineSegment(sketch, "E14549", {"start": v(-10.85, 25.09) * mm, "end": v(-10.72, 25.63) * mm});
            skLineSegment(sketch, "E14550", {"start": v(-10.72, 25.63) * mm, "end": v(-10.58, 26.14) * mm});
            skLineSegment(sketch, "E14551", {"start": v(-10.58, 26.14) * mm, "end": v(-10.44, 26.62) * mm});
            skLineSegment(sketch, "E14552", {"start": v(-10.44, 26.62) * mm, "end": v(-10.33, 26.95) * mm});
            skLineSegment(sketch, "E14553", {"start": v(-10.33, 26.95) * mm, "end": v(-10.2, 27.28) * mm});
            skLineSegment(sketch, "E14554", {"start": v(-10.2, 27.28) * mm, "end": v(-9.93, 27.97) * mm});
            skLineSegment(sketch, "E14555", {"start": v(-9.93, 27.97) * mm, "end": v(-9.62, 28.67) * mm});
            skLineSegment(sketch, "E14556", {"start": v(-9.62, 28.67) * mm, "end": v(-9.29, 29.37) * mm});
            skLineSegment(sketch, "E14557", {"start": v(-9.29, 29.37) * mm, "end": v(-8.93, 30.07) * mm});
            skLineSegment(sketch, "E14558", {"start": v(-8.93, 30.07) * mm, "end": v(-8.57, 30.75) * mm});
            skLineSegment(sketch, "E14559", {"start": v(-8.57, 30.75) * mm, "end": v(-8.2, 31.4) * mm});
            skLineSegment(sketch, "E14560", {"start": v(-8.2, 31.4) * mm, "end": v(-7.85, 32) * mm});
            skLineSegment(sketch, "E14561", {"start": v(-7.85, 32) * mm, "end": v(-7.61, 32.36) * mm});
            skLineSegment(sketch, "E14562", {"start": v(-7.61, 32.36) * mm, "end": v(-7.35, 32.73) * mm});
            skLineSegment(sketch, "E14563", {"start": v(-7.35, 32.73) * mm, "end": v(-7.06, 33.12) * mm});
            skLineSegment(sketch, "E14564", {"start": v(-7.06, 33.12) * mm, "end": v(-6.76, 33.5) * mm});
            skLineSegment(sketch, "E14565", {"start": v(-6.76, 33.5) * mm, "end": v(-6.16, 34.26) * mm});
            skLineSegment(sketch, "E14566", {"start": v(-6.16, 34.26) * mm, "end": v(-5.6, 34.96) * mm});
            skLineSegment(sketch, "E14567", {"start": v(-5.6, 34.96) * mm, "end": v(-5.15, 35.59) * mm});
            skLineSegment(sketch, "E14568", {"start": v(-5.15, 35.59) * mm, "end": v(-4.69, 36.22) * mm});
            skLineSegment(sketch, "E14569", {"start": v(-4.69, 36.22) * mm, "end": v(-4.24, 36.85) * mm});
            skLineSegment(sketch, "E14570", {"start": v(-4.24, 36.85) * mm, "end": v(-3.83, 37.46) * mm});
            skLineSegment(sketch, "E14571", {"start": v(-3.83, 37.46) * mm, "end": v(-3.46, 38.02) * mm});
            skLineSegment(sketch, "E14572", {"start": v(-3.46, 38.02) * mm, "end": v(-3.14, 38.54) * mm});
            skLineSegment(sketch, "E14573", {"start": v(-3.14, 38.54) * mm, "end": v(-2.88, 38.97) * mm});
            skLineSegment(sketch, "E14574", {"start": v(-2.88, 38.97) * mm, "end": v(-2.78, 39.16) * mm});
            skLineSegment(sketch, "E14575", {"start": v(-2.78, 39.16) * mm, "end": v(-2.7, 39.32) * mm});
            skLineSegment(sketch, "E14576", {"start": v(-2.7, 39.32) * mm, "end": v(-2.53, 39.67) * mm});
            skLineSegment(sketch, "E14577", {"start": v(-2.53, 39.67) * mm, "end": v(-2.34, 40.05) * mm});
            skLineSegment(sketch, "E14578", {"start": v(-2.34, 40.05) * mm, "end": v(-2.25, 40.24) * mm});
            skLineSegment(sketch, "E14579", {"start": v(-2.25, 40.24) * mm, "end": v(-2.17, 40.44) * mm});
            skLineSegment(sketch, "E14580", {"start": v(-2.17, 40.44) * mm, "end": v(-2.11, 40.62) * mm});
            skLineSegment(sketch, "E14581", {"start": v(-2.11, 40.62) * mm, "end": v(-2.08, 40.8) * mm});
            skLineSegment(sketch, "E14582", {"start": v(-2.08, 40.8) * mm, "end": v(-2.06, 41.08) * mm});
            skLineSegment(sketch, "E14583", {"start": v(-2.06, 41.08) * mm, "end": v(-2.07, 41.38) * mm});
            skLineSegment(sketch, "E14584", {"start": v(-2.07, 41.38) * mm, "end": v(-2.1, 41.7) * mm});
            skLineSegment(sketch, "E14585", {"start": v(-2.1, 41.7) * mm, "end": v(-2.14, 42) * mm});
            skLineSegment(sketch, "E14586", {"start": v(-2.14, 42) * mm, "end": v(-2.21, 42.31) * mm});
            skLineSegment(sketch, "E14587", {"start": v(-2.21, 42.31) * mm, "end": v(-2.3, 42.61) * mm});
            skLineSegment(sketch, "E14588", {"start": v(-2.3, 42.61) * mm, "end": v(-2.4, 42.9) * mm});
            skLineSegment(sketch, "E14589", {"start": v(-2.4, 42.9) * mm, "end": v(-2.52, 43.15) * mm});
            skLineSegment(sketch, "E14590", {"start": v(-2.52, 43.15) * mm, "end": v(-2.6, 43.29) * mm});
            skLineSegment(sketch, "E14591", {"start": v(-2.6, 43.29) * mm, "end": v(-2.7, 43.42) * mm});
            skLineSegment(sketch, "E14592", {"start": v(-2.7, 43.42) * mm, "end": v(-2.8, 43.56) * mm});
            skLineSegment(sketch, "E14593", {"start": v(-2.8, 43.56) * mm, "end": v(-2.91, 43.69) * mm});
            skLineSegment(sketch, "E14594", {"start": v(-2.91, 43.69) * mm, "end": v(-3.17, 43.95) * mm});
            skLineSegment(sketch, "E14595", {"start": v(-3.17, 43.95) * mm, "end": v(-3.44, 44.2) * mm});
            skLineSegment(sketch, "E14596", {"start": v(-3.44, 44.2) * mm, "end": v(-4, 44.68) * mm});
            skLineSegment(sketch, "E14597", {"start": v(-4, 44.68) * mm, "end": v(-4.27, 44.91) * mm});
            skLineSegment(sketch, "E14598", {"start": v(-4.27, 44.91) * mm, "end": v(-4.51, 45.14) * mm});
            skLineSegment(sketch, "E14599", {"start": v(-4.51, 45.14) * mm, "end": v(-3.74, 45.74) * mm});
            skLineSegment(sketch, "E14600", {"start": v(-3.74, 45.74) * mm, "end": v(-3.56, 45.86) * mm});
            skLineSegment(sketch, "E14601", {"start": v(-3.56, 45.86) * mm, "end": v(-3.35, 46) * mm});
            skLineSegment(sketch, "E14602", {"start": v(-3.35, 46) * mm, "end": v(-3.1, 46.14) * mm});
            skLineSegment(sketch, "E14603", {"start": v(-3.1, 46.14) * mm, "end": v(-2.85, 46.28) * mm});
            skLineSegment(sketch, "E14604", {"start": v(-2.85, 46.28) * mm, "end": v(-2.59, 46.41) * mm});
            skLineSegment(sketch, "E14605", {"start": v(-2.59, 46.41) * mm, "end": v(-2.32, 46.54) * mm});
            skLineSegment(sketch, "E14606", {"start": v(-2.32, 46.54) * mm, "end": v(-2.06, 46.65) * mm});
            skLineSegment(sketch, "E14607", {"start": v(-2.06, 46.65) * mm, "end": v(-1.81, 46.75) * mm});
            skLineSegment(sketch, "E14608", {"start": v(-1.81, 46.75) * mm, "end": v(-1.53, 46.86) * mm});
            skLineSegment(sketch, "E14609", {"start": v(-1.53, 46.86) * mm, "end": v(-1.24, 46.98) * mm});
            skLineSegment(sketch, "E14610", {"start": v(-1.24, 46.98) * mm, "end": v(-0.94, 47.1) * mm});
            skLineSegment(sketch, "E14611", {"start": v(-0.94, 47.1) * mm, "end": v(-0.8, 47.14) * mm});
            skLineSegment(sketch, "E14612", {"start": v(-0.8, 47.14) * mm, "end": v(-0.66, 47.17) * mm});
            skLineSegment(sketch, "E14613", {"start": v(-0.66, 47.17) * mm, "end": v(-0.03, 47.26) * mm});
            skLineSegment(sketch, "E14614", {"start": v(-0.03, 47.26) * mm, "end": v(0.63, 47.33) * mm});
            skLineSegment(sketch, "E14615", {"start": v(0.63, 47.33) * mm, "end": v(1.32, 47.38) * mm});
            skLineSegment(sketch, "E14616", {"start": v(1.32, 47.38) * mm, "end": v(1.68, 47.4) * mm});
            skLineSegment(sketch, "E14617", {"start": v(1.68, 47.4) * mm, "end": v(2.03, 47.4) * mm});
            skLineSegment(sketch, "E14618", {"start": v(2.03, 47.4) * mm, "end": v(2.39, 47.4) * mm});
            skLineSegment(sketch, "E14619", {"start": v(2.39, 47.4) * mm, "end": v(2.74, 47.4) * mm});
            skLineSegment(sketch, "E14620", {"start": v(2.74, 47.4) * mm, "end": v(3.09, 47.38) * mm});
            skLineSegment(sketch, "E14621", {"start": v(3.09, 47.38) * mm, "end": v(3.43, 47.35) * mm});
            skLineSegment(sketch, "E14622", {"start": v(3.43, 47.35) * mm, "end": v(3.76, 47.3) * mm});
            skLineSegment(sketch, "E14623", {"start": v(3.76, 47.3) * mm, "end": v(4.09, 47.26) * mm});
            skLineSegment(sketch, "E14624", {"start": v(4.09, 47.26) * mm, "end": v(4.4, 47.2) * mm});
            skLineSegment(sketch, "E14625", {"start": v(4.4, 47.2) * mm, "end": v(4.7, 47.12) * mm});
            skLineSegment(sketch, "E14626", {"start": v(4.7, 47.12) * mm, "end": v(4.89, 47.07) * mm});
            skLineSegment(sketch, "E14627", {"start": v(4.89, 47.07) * mm, "end": v(5.09, 47) * mm});
            skLineSegment(sketch, "E14628", {"start": v(5.09, 47) * mm, "end": v(5.29, 46.92) * mm});
            skLineSegment(sketch, "E14629", {"start": v(5.29, 46.92) * mm, "end": v(5.49, 46.83) * mm});
            skLineSegment(sketch, "E14630", {"start": v(5.49, 46.83) * mm, "end": v(5.9, 46.62) * mm});
            skLineSegment(sketch, "E14631", {"start": v(5.9, 46.62) * mm, "end": v(6.3, 46.4) * mm});
            skLineSegment(sketch, "E14632", {"start": v(6.3, 46.4) * mm, "end": v(6.7, 46.14) * mm});
            skLineSegment(sketch, "E14633", {"start": v(6.7, 46.14) * mm, "end": v(7.07, 45.88) * mm});
            skLineSegment(sketch, "E14634", {"start": v(7.07, 45.88) * mm, "end": v(7.42, 45.6) * mm});
            skLineSegment(sketch, "E14635", {"start": v(7.42, 45.6) * mm, "end": v(7.74, 45.34) * mm});
            skLineSegment(sketch, "E14636", {"start": v(7.74, 45.34) * mm, "end": v(7.85, 45.23) * mm});
            skLineSegment(sketch, "E14637", {"start": v(7.85, 45.23) * mm, "end": v(7.96, 45.1) * mm});
            skLineSegment(sketch, "E14638", {"start": v(7.96, 45.1) * mm, "end": v(8.17, 44.82) * mm});
            skLineSegment(sketch, "E14639", {"start": v(8.17, 44.82) * mm, "end": v(8.37, 44.52) * mm});
            skLineSegment(sketch, "E14640", {"start": v(8.37, 44.52) * mm, "end": v(8.57, 44.25) * mm});
            skLineSegment(sketch, "E14641", {"start": v(8.57, 44.25) * mm, "end": v(8.74, 44) * mm});
            skLineSegment(sketch, "E14642", {"start": v(8.74, 44) * mm, "end": v(8.93, 43.72) * mm});
            skLineSegment(sketch, "E14643", {"start": v(8.93, 43.72) * mm, "end": v(9.12, 43.4) * mm});
            skLineSegment(sketch, "E14644", {"start": v(9.12, 43.4) * mm, "end": v(9.3, 43.06) * mm});
            skLineSegment(sketch, "E14645", {"start": v(9.3, 43.06) * mm, "end": v(9.48, 42.72) * mm});
            skLineSegment(sketch, "E14646", {"start": v(9.48, 42.72) * mm, "end": v(9.64, 42.37) * mm});
            skLineSegment(sketch, "E14647", {"start": v(9.64, 42.37) * mm, "end": v(9.78, 42.04) * mm});
            skLineSegment(sketch, "E14648", {"start": v(9.78, 42.04) * mm, "end": v(9.9, 41.73) * mm});
            skLineSegment(sketch, "E14649", {"start": v(9.9, 41.73) * mm, "end": v(10.03, 41.39) * mm});
            skLineSegment(sketch, "E14650", {"start": v(10.03, 41.39) * mm, "end": v(10.17, 41.02) * mm});
            skLineSegment(sketch, "E14651", {"start": v(10.17, 41.02) * mm, "end": v(10.3, 40.65) * mm});
            skLineSegment(sketch, "E14652", {"start": v(10.3, 40.65) * mm, "end": v(10.36, 40.47) * mm});
            skLineSegment(sketch, "E14653", {"start": v(10.36, 40.47) * mm, "end": v(10.4, 40.3) * mm});
            skLineSegment(sketch, "E14654", {"start": v(10.4, 40.3) * mm, "end": v(10.44, 40.07) * mm});
            skLineSegment(sketch, "E14655", {"start": v(10.44, 40.07) * mm, "end": v(10.46, 39.82) * mm});
            skLineSegment(sketch, "E14656", {"start": v(10.46, 39.82) * mm, "end": v(10.48, 39.58) * mm});
            skLineSegment(sketch, "E14657", {"start": v(10.48, 39.58) * mm, "end": v(10.52, 39.35) * mm});
            skLineSegment(sketch, "E14658", {"start": v(10.52, 39.35) * mm, "end": v(10.56, 39.2) * mm});
            skLineSegment(sketch, "E14659", {"start": v(10.56, 39.2) * mm, "end": v(10.63, 39.03) * mm});
            skLineSegment(sketch, "E14660", {"start": v(10.63, 39.03) * mm, "end": v(10.69, 38.87) * mm});
            skLineSegment(sketch, "E14661", {"start": v(10.69, 38.87) * mm, "end": v(10.73, 38.72) * mm});
            skLineSegment(sketch, "E14662", {"start": v(10.73, 38.72) * mm, "end": v(10.77, 38.43) * mm});
            skLineSegment(sketch, "E14663", {"start": v(10.77, 38.43) * mm, "end": v(10.8, 38.13) * mm});
            skLineSegment(sketch, "E14664", {"start": v(10.8, 38.13) * mm, "end": v(10.81, 37.82) * mm});
            skLineSegment(sketch, "E14665", {"start": v(10.81, 37.82) * mm, "end": v(10.82, 37.5) * mm});
            skLineSegment(sketch, "E14666", {"start": v(10.82, 37.5) * mm, "end": v(10.82, 36.85) * mm});
            skLineSegment(sketch, "E14667", {"start": v(10.82, 36.85) * mm, "end": v(10.8, 36.19) * mm});
            skLineSegment(sketch, "E14668", {"start": v(10.8, 36.19) * mm, "end": v(10.73, 34.87) * mm});
            skLineSegment(sketch, "E14669", {"start": v(10.73, 34.87) * mm, "end": v(10.72, 34.24) * mm});
            skLineSegment(sketch, "E14670", {"start": v(10.72, 34.24) * mm, "end": v(10.72, 33.93) * mm});
            skLineSegment(sketch, "E14671", {"start": v(10.72, 33.93) * mm, "end": v(10.73, 33.64) * mm});
            skLineSegment(sketch, "E14672", {"start": v(10.73, 33.64) * mm, "end": v(10.77, 33.13) * mm});
            skLineSegment(sketch, "E14673", {"start": v(10.77, 33.13) * mm, "end": v(10.82, 32.6) * mm});
            skLineSegment(sketch, "E14674", {"start": v(10.82, 32.6) * mm, "end": v(10.95, 31.46) * mm});
            skLineSegment(sketch, "E14675", {"start": v(10.95, 31.46) * mm, "end": v(11.1, 30.33) * mm});
            skLineSegment(sketch, "E14676", {"start": v(11.1, 30.33) * mm, "end": v(11.22, 29.28) * mm});
            skLineSegment(sketch, "E14677", {"start": v(11.22, 29.28) * mm, "end": v(11.44, 27.48) * mm});
            skLineSegment(sketch, "E14678", {"start": v(11.44, 27.48) * mm, "end": v(11.66, 25.8) * mm});
            skLineSegment(sketch, "E14679", {"start": v(11.66, 25.8) * mm, "end": v(11.86, 24.42) * mm});
            skLineSegment(sketch, "E14680", {"start": v(11.86, 24.42) * mm, "end": v(11.95, 23.9) * mm});
            skLineSegment(sketch, "E14681", {"start": v(11.95, 23.9) * mm, "end": v(12.02, 23.53) * mm});
            skLineSegment(sketch, "E14682", {"start": v(12.02, 23.53) * mm, "end": v(12.34, 22.13) * mm});
            skLineSegment(sketch, "E14683", {"start": v(12.34, 22.13) * mm, "end": v(12.24, 21.66) * mm});
            skLineSegment(sketch, "E14684", {"start": v(12.24, 21.66) * mm, "end": v(12.19, 21.41) * mm});
            skLineSegment(sketch, "E14685", {"start": v(12.19, 21.41) * mm, "end": v(12.14, 21.18) * mm});
            skLineSegment(sketch, "E14686", {"start": v(12.14, 21.18) * mm, "end": v(12, 20.21) * mm});
            skLineSegment(sketch, "E14687", {"start": v(12, 20.21) * mm, "end": v(11.92, 19.74) * mm});
            skLineSegment(sketch, "E14688", {"start": v(11.92, 19.74) * mm, "end": v(11.85, 19.35) * mm});
            skLineSegment(sketch, "E14689", {"start": v(11.85, 19.35) * mm, "end": v(11.7, 18.59) * mm});
            skLineSegment(sketch, "E14690", {"start": v(11.7, 18.59) * mm, "end": v(10.6, 19.27) * mm});
            skLineSegment(sketch, "E14691", {"start": v(10.6, 19.27) * mm, "end": v(10.16, 19.53) * mm});
            skLineSegment(sketch, "E14692", {"start": v(10.16, 19.53) * mm, "end": v(9.77, 19.75) * mm});
            skLineSegment(sketch, "E14693", {"start": v(9.77, 19.75) * mm, "end": v(9.48, 19.9) * mm});
            skLineSegment(sketch, "E14694", {"start": v(9.48, 19.9) * mm, "end": v(9.39, 19.93) * mm});
            skLineSegment(sketch, "E14695", {"start": v(9.39, 19.93) * mm, "end": v(9.33, 19.95) * mm});
            skLineSegment(sketch, "E14696", {"start": v(9.33, 19.95) * mm, "end": v(9.32, 19.94) * mm});
            skLineSegment(sketch, "E14697", {"start": v(9.32, 19.94) * mm, "end": v(9.3, 19.91) * mm});
            skLineSegment(sketch, "E14698", {"start": v(9.3, 19.91) * mm, "end": v(9.26, 19.8) * mm});
            skLineSegment(sketch, "E14699", {"start": v(9.26, 19.8) * mm, "end": v(9.21, 19.64) * mm});
            skLineSegment(sketch, "E14700", {"start": v(9.21, 19.64) * mm, "end": v(9.16, 19.43) * mm});
            skLineSegment(sketch, "E14701", {"start": v(9.16, 19.43) * mm, "end": v(9.07, 18.86) * mm});
            skLineSegment(sketch, "E14702", {"start": v(9.07, 18.86) * mm, "end": v(8.99, 18.17) * mm});
            skLineSegment(sketch, "E14703", {"start": v(8.99, 18.17) * mm, "end": v(8.95, 17.75) * mm});
            skLineSegment(sketch, "E14704", {"start": v(8.95, 17.75) * mm, "end": v(8.9, 17.3) * mm});
            skLineSegment(sketch, "E14705", {"start": v(8.9, 17.3) * mm, "end": v(8.84, 16.85) * mm});
            skLineSegment(sketch, "E14706", {"start": v(8.84, 16.85) * mm, "end": v(8.8, 16.64) * mm});
            skLineSegment(sketch, "E14707", {"start": v(8.8, 16.64) * mm, "end": v(8.74, 16.44) * mm});
            skLineSegment(sketch, "E14708", {"start": v(8.74, 16.44) * mm, "end": v(8.58, 15.87) * mm});
            skLineSegment(sketch, "E14709", {"start": v(8.58, 15.87) * mm, "end": v(8.49, 15.56) * mm});
            skLineSegment(sketch, "E14710", {"start": v(8.49, 15.56) * mm, "end": v(8.38, 15.26) * mm});
            skLineSegment(sketch, "E14711", {"start": v(8.38, 15.26) * mm, "end": v(8.32, 15.11) * mm});
            skLineSegment(sketch, "E14712", {"start": v(8.32, 15.11) * mm, "end": v(8.25, 14.98) * mm});
            skLineSegment(sketch, "E14713", {"start": v(8.25, 14.98) * mm, "end": v(8.18, 14.85) * mm});
            skLineSegment(sketch, "E14714", {"start": v(8.18, 14.85) * mm, "end": v(8.1, 14.73) * mm});
            skLineSegment(sketch, "E14715", {"start": v(8.1, 14.73) * mm, "end": v(8, 14.62) * mm});
            skLineSegment(sketch, "E14716", {"start": v(8, 14.62) * mm, "end": v(7.9, 14.53) * mm});
            skLineSegment(sketch, "E14717", {"start": v(7.9, 14.53) * mm, "end": v(7.8, 14.45) * mm});
            skLineSegment(sketch, "E14718", {"start": v(7.8, 14.45) * mm, "end": v(7.68, 14.38) * mm});
            skLineSegment(sketch, "E14719", {"start": v(7.68, 14.38) * mm, "end": v(7.54, 14.34) * mm});
            skLineSegment(sketch, "E14720", {"start": v(7.54, 14.34) * mm, "end": v(7.37, 14.32) * mm});
            skLineSegment(sketch, "E14721", {"start": v(7.37, 14.32) * mm, "end": v(7.2, 14.31) * mm});
            skLineSegment(sketch, "E14722", {"start": v(7.2, 14.31) * mm, "end": v(7.11, 14.32) * mm});
            skLineSegment(sketch, "E14723", {"start": v(7.11, 14.32) * mm, "end": v(7.04, 14.34) * mm});
            skLineSegment(sketch, "E14724", {"start": v(7.04, 14.34) * mm, "end": v(6.92, 14.38) * mm});
            skLineSegment(sketch, "E14725", {"start": v(6.92, 14.38) * mm, "end": v(6.8, 14.43) * mm});
            skLineSegment(sketch, "E14726", {"start": v(6.8, 14.43) * mm, "end": v(6.52, 14.57) * mm});
            skLineSegment(sketch, "E14727", {"start": v(6.52, 14.57) * mm, "end": v(6.23, 14.71) * mm});
            skLineSegment(sketch, "E14728", {"start": v(6.23, 14.71) * mm, "end": v(6.08, 14.78) * mm});
            skLineSegment(sketch, "E14729", {"start": v(6.08, 14.78) * mm, "end": v(5.94, 14.84) * mm});
            skLineSegment(sketch, "E14730", {"start": v(5.94, 14.84) * mm, "end": v(5.28, 15.08) * mm});
            skLineSegment(sketch, "E14731", {"start": v(5.28, 15.08) * mm, "end": v(5.46, 14.94) * mm});
            skLineSegment(sketch, "E14732", {"start": v(5.46, 14.94) * mm, "end": v(5.64, 14.78) * mm});
            skLineSegment(sketch, "E14733", {"start": v(5.64, 14.78) * mm, "end": v(6.01, 14.43) * mm});
            skLineSegment(sketch, "E14734", {"start": v(6.01, 14.43) * mm, "end": v(6.2, 14.27) * mm});
            skLineSegment(sketch, "E14735", {"start": v(6.2, 14.27) * mm, "end": v(6.4, 14.12) * mm});
            skLineSegment(sketch, "E14736", {"start": v(6.4, 14.12) * mm, "end": v(6.5, 14.06) * mm});
            skLineSegment(sketch, "E14737", {"start": v(6.5, 14.06) * mm, "end": v(6.6, 14.01) * mm});
            skLineSegment(sketch, "E14738", {"start": v(6.6, 14.01) * mm, "end": v(6.7, 13.97) * mm});
            skLineSegment(sketch, "E14739", {"start": v(6.7, 13.97) * mm, "end": v(6.81, 13.94) * mm});
            skLineSegment(sketch, "E14740", {"start": v(6.81, 13.94) * mm, "end": v(6.9, 13.92) * mm});
            skLineSegment(sketch, "E14741", {"start": v(6.9, 13.92) * mm, "end": v(7, 13.92) * mm});
            skLineSegment(sketch, "E14742", {"start": v(7, 13.92) * mm, "end": v(7.2, 13.93) * mm});
            skLineSegment(sketch, "E14743", {"start": v(7.2, 13.93) * mm, "end": v(7.4, 13.96) * mm});
            skLineSegment(sketch, "E14744", {"start": v(7.4, 13.96) * mm, "end": v(7.6, 14.02) * mm});
            skLineSegment(sketch, "E14745", {"start": v(7.6, 14.02) * mm, "end": v(8.01, 14.14) * mm});
            skLineSegment(sketch, "E14746", {"start": v(8.01, 14.14) * mm, "end": v(8.2, 14.2) * mm});
            skLineSegment(sketch, "E14747", {"start": v(8.2, 14.2) * mm, "end": v(8.4, 14.24) * mm});
            skLineSegment(sketch, "E14748", {"start": v(8.4, 14.24) * mm, "end": v(9.04, 13.55) * mm});
            skLineSegment(sketch, "E14749", {"start": v(9.04, 13.55) * mm, "end": v(9.17, 13.4) * mm});
            skLineSegment(sketch, "E14750", {"start": v(9.17, 13.4) * mm, "end": v(9.3, 13.23) * mm});
            skLineSegment(sketch, "E14751", {"start": v(9.3, 13.23) * mm, "end": v(9.42, 13.06) * mm});
            skLineSegment(sketch, "E14752", {"start": v(9.42, 13.06) * mm, "end": v(9.52, 12.88) * mm});
            skLineSegment(sketch, "E14753", {"start": v(9.52, 12.88) * mm, "end": v(9.62, 12.7) * mm});
            skLineSegment(sketch, "E14754", {"start": v(9.62, 12.7) * mm, "end": v(9.7, 12.53) * mm});
            skLineSegment(sketch, "E14755", {"start": v(9.7, 12.53) * mm, "end": v(9.76, 12.38) * mm});
            skLineSegment(sketch, "E14756", {"start": v(9.76, 12.38) * mm, "end": v(9.8, 12.24) * mm});
            skLineSegment(sketch, "E14757", {"start": v(9.8, 12.24) * mm, "end": v(9.84, 12.09) * mm});
            skLineSegment(sketch, "E14758", {"start": v(9.84, 12.09) * mm, "end": v(9.9, 11.92) * mm});
            skLineSegment(sketch, "E14759", {"start": v(9.9, 11.92) * mm, "end": v(9.91, 11.84) * mm});
            skLineSegment(sketch, "E14760", {"start": v(9.91, 11.84) * mm, "end": v(9.92, 11.76) * mm});
            skLineSegment(sketch, "E14761", {"start": v(9.92, 11.76) * mm, "end": v(9.92, 11.69) * mm});
            skLineSegment(sketch, "E14762", {"start": v(9.92, 11.69) * mm, "end": v(9.9, 11.62) * mm});
            skLineSegment(sketch, "E14763", {"start": v(9.9, 11.62) * mm, "end": v(9.84, 11.5) * mm});
            skLineSegment(sketch, "E14764", {"start": v(9.84, 11.5) * mm, "end": v(9.77, 11.37) * mm});
            skLineSegment(sketch, "E14765", {"start": v(9.77, 11.37) * mm, "end": v(9.7, 11.27) * mm});
            skLineSegment(sketch, "E14766", {"start": v(9.7, 11.27) * mm, "end": v(9.59, 11.17) * mm});
            skLineSegment(sketch, "E14767", {"start": v(9.59, 11.17) * mm, "end": v(9.52, 11.13) * mm});
            skLineSegment(sketch, "E14768", {"start": v(9.52, 11.13) * mm, "end": v(9.45, 11.1) * mm});
            skLineSegment(sketch, "E14769", {"start": v(9.45, 11.1) * mm, "end": v(9.37, 11.06) * mm});
            skLineSegment(sketch, "E14770", {"start": v(9.37, 11.06) * mm, "end": v(9.28, 11.03) * mm});
            skLineSegment(sketch, "E14771", {"start": v(9.28, 11.03) * mm, "end": v(9.17, 11.01) * mm});
            skLineSegment(sketch, "E14772", {"start": v(9.17, 11.01) * mm, "end": v(9.06, 11) * mm});
            skLineSegment(sketch, "E14773", {"start": v(9.06, 11) * mm, "end": v(8.78, 10.98) * mm});
            skLineSegment(sketch, "E14774", {"start": v(8.78, 10.98) * mm, "end": v(8.62, 11) * mm});
            skLineSegment(sketch, "E14775", {"start": v(8.62, 11) * mm, "end": v(8.44, 11.02) * mm});
            skLineSegment(sketch, "E14776", {"start": v(8.44, 11.02) * mm, "end": v(8.25, 11.07) * mm});
            skLineSegment(sketch, "E14777", {"start": v(8.25, 11.07) * mm, "end": v(8.05, 11.13) * mm});
            skLineSegment(sketch, "E14778", {"start": v(8.05, 11.13) * mm, "end": v(7.61, 11.3) * mm});
            skLineSegment(sketch, "E14779", {"start": v(7.61, 11.3) * mm, "end": v(7.16, 11.5) * mm});
            skLineSegment(sketch, "E14780", {"start": v(7.16, 11.5) * mm, "end": v(6.23, 11.94) * mm});
            skLineSegment(sketch, "E14781", {"start": v(6.23, 11.94) * mm, "end": v(5.8, 12.15) * mm});
            skLineSegment(sketch, "E14782", {"start": v(5.8, 12.15) * mm, "end": v(5.4, 12.33) * mm});
            skLineSegment(sketch, "E14783", {"start": v(5.4, 12.33) * mm, "end": v(5.59, 11.82) * mm});
            skLineSegment(sketch, "E14784", {"start": v(5.59, 11.82) * mm, "end": v(5.68, 11.56) * mm});
            skLineSegment(sketch, "E14785", {"start": v(5.68, 11.56) * mm, "end": v(5.78, 11.22) * mm});
            skLineSegment(sketch, "E14786", {"start": v(5.78, 11.22) * mm, "end": v(5.89, 10.86) * mm});
            skLineSegment(sketch, "E14787", {"start": v(5.89, 10.86) * mm, "end": v(5.98, 10.5) * mm});
            skLineSegment(sketch, "E14788", {"start": v(5.98, 10.5) * mm, "end": v(6.18, 9.71) * mm});
            skLineSegment(sketch, "E14789", {"start": v(6.18, 9.71) * mm, "end": v(5.78, 9.22) * mm});
            skLineSegment(sketch, "E14790", {"start": v(5.78, 9.22) * mm, "end": v(5.68, 9.12) * mm});
            skLineSegment(sketch, "E14791", {"start": v(5.68, 9.12) * mm, "end": v(5.58, 9.03) * mm});
            skLineSegment(sketch, "E14792", {"start": v(5.58, 9.03) * mm, "end": v(5.47, 8.95) * mm});
            skLineSegment(sketch, "E14793", {"start": v(5.47, 8.95) * mm, "end": v(5.36, 8.87) * mm});
            skLineSegment(sketch, "E14794", {"start": v(5.36, 8.87) * mm, "end": v(5.25, 8.81) * mm});
            skLineSegment(sketch, "E14795", {"start": v(5.25, 8.81) * mm, "end": v(5.14, 8.77) * mm});
            skLineSegment(sketch, "E14796", {"start": v(5.14, 8.77) * mm, "end": v(5.03, 8.74) * mm});
            skLineSegment(sketch, "E14797", {"start": v(5.03, 8.74) * mm, "end": v(4.94, 8.73) * mm});
            skLineSegment(sketch, "E14798", {"start": v(4.94, 8.73) * mm, "end": v(4.83, 8.73) * mm});
            skLineSegment(sketch, "E14799", {"start": v(4.83, 8.73) * mm, "end": v(4.71, 8.74) * mm});
            skLineSegment(sketch, "E14800", {"start": v(4.71, 8.74) * mm, "end": v(4.6, 8.77) * mm});
            skLineSegment(sketch, "E14801", {"start": v(4.6, 8.77) * mm, "end": v(4.5, 8.8) * mm});
            skLineSegment(sketch, "E14802", {"start": v(4.5, 8.8) * mm, "end": v(4.39, 8.87) * mm});
            skLineSegment(sketch, "E14803", {"start": v(4.39, 8.87) * mm, "end": v(4.3, 8.95) * mm});
            skLineSegment(sketch, "E14804", {"start": v(4.3, 8.95) * mm, "end": v(4.2, 9.04) * mm});
            skLineSegment(sketch, "E14805", {"start": v(4.2, 9.04) * mm, "end": v(4.13, 9.15) * mm});
            skLineSegment(sketch, "E14806", {"start": v(4.13, 9.15) * mm, "end": v(3.98, 9.37) * mm});
            skLineSegment(sketch, "E14807", {"start": v(3.98, 9.37) * mm, "end": v(3.84, 9.58) * mm});
            skLineSegment(sketch, "E14808", {"start": v(3.84, 9.58) * mm, "end": v(3.7, 9.77) * mm});
            skLineSegment(sketch, "E14809", {"start": v(3.7, 9.77) * mm, "end": v(3.56, 9.96) * mm});
            skLineSegment(sketch, "E14810", {"start": v(3.56, 9.96) * mm, "end": v(3.3, 10.36) * mm});
            skLineSegment(sketch, "E14811", {"start": v(3.3, 10.36) * mm, "end": v(3.2, 10.56) * mm});
            skLineSegment(sketch, "E14812", {"start": v(3.2, 10.56) * mm, "end": v(3.1, 10.74) * mm});
            skLineSegment(sketch, "E14813", {"start": v(3.1, 10.74) * mm, "end": v(3.03, 10.9) * mm});
            skLineSegment(sketch, "E14814", {"start": v(3.03, 10.9) * mm, "end": v(2.97, 11.04) * mm});
            skLineSegment(sketch, "E14815", {"start": v(2.97, 11.04) * mm, "end": v(2.78, 11.65) * mm});
            skLineSegment(sketch, "E14816", {"start": v(2.78, 11.65) * mm, "end": v(4.85, 15.33) * mm});
            skLineSegment(sketch, "E14817", {"start": v(4.85, 15.33) * mm, "end": v(5.58, 15.33) * mm});
            skLineSegment(sketch, "E14818", {"start": v(5.58, 15.33) * mm, "end": v(4.7, 16.15) * mm});
            skLineSegment(sketch, "E14819", {"start": v(4.7, 16.15) * mm, "end": v(4.64, 15.99) * mm});
            skLineSegment(sketch, "E14820", {"start": v(4.64, 15.99) * mm, "end": v(4.58, 15.82) * mm});
            skLineSegment(sketch, "E14821", {"start": v(4.58, 15.82) * mm, "end": v(4.4, 15.47) * mm});
            skLineSegment(sketch, "E14822", {"start": v(4.4, 15.47) * mm, "end": v(4.18, 15.11) * mm});
            skLineSegment(sketch, "E14823", {"start": v(4.18, 15.11) * mm, "end": v(3.72, 14.36) * mm});
            skLineSegment(sketch, "E14824", {"start": v(3.72, 14.36) * mm, "end": v(3.25, 13.62) * mm});
            skLineSegment(sketch, "E14825", {"start": v(3.25, 13.62) * mm, "end": v(2.8, 12.94) * mm});
            skLineSegment(sketch, "E14826", {"start": v(2.8, 12.94) * mm, "end": v(2.48, 12.42) * mm});
            skLineSegment(sketch, "E14827", {"start": v(2.48, 12.42) * mm, "end": v(2.15, 11.94) * mm});
            skLineSegment(sketch, "E14828", {"start": v(2.15, 11.94) * mm, "end": v(1.85, 11.5) * mm});
            skLineSegment(sketch, "E14829", {"start": v(1.85, 11.5) * mm, "end": v(1.57, 11.13) * mm});
            skLineSegment(sketch, "E14830", {"start": v(1.57, 11.13) * mm, "end": v(1.32, 10.82) * mm});
            skLineSegment(sketch, "E14831", {"start": v(1.32, 10.82) * mm, "end": v(1.12, 10.58) * mm});
            skLineSegment(sketch, "E14832", {"start": v(1.12, 10.58) * mm, "end": v(0.97, 10.43) * mm});
            skLineSegment(sketch, "E14833", {"start": v(0.97, 10.43) * mm, "end": v(0.92, 10.4) * mm});
            skLineSegment(sketch, "E14834", {"start": v(0.92, 10.4) * mm, "end": v(0.88, 10.38) * mm});
            skLineSegment(sketch, "E14835", {"start": v(0.88, 10.38) * mm, "end": v(0.59, 10.38) * mm});
            skLineSegment(sketch, "E14836", {"start": v(0.59, 10.38) * mm, "end": v(-0.49, 12.85) * mm});
            skLineSegment(sketch, "E14837", {"start": v(-0.49, 12.85) * mm, "end": v(-0.71, 13.35) * mm});
            skLineSegment(sketch, "E14838", {"start": v(-0.71, 13.35) * mm, "end": v(-0.94, 13.83) * mm});
            skLineSegment(sketch, "E14839", {"start": v(-0.94, 13.83) * mm, "end": v(-1.16, 14.28) * mm});
            skLineSegment(sketch, "E14840", {"start": v(-1.16, 14.28) * mm, "end": v(-1.37, 14.7) * mm});
            skLineSegment(sketch, "E14841", {"start": v(-1.37, 14.7) * mm, "end": v(-1.56, 15.04) * mm});
            skLineSegment(sketch, "E14842", {"start": v(-1.56, 15.04) * mm, "end": v(-1.73, 15.33) * mm});
            skLineSegment(sketch, "E14843", {"start": v(-1.73, 15.33) * mm, "end": v(-1.87, 15.54) * mm});
            skLineSegment(sketch, "E14844", {"start": v(-1.87, 15.54) * mm, "end": v(-1.92, 15.6) * mm});
            skLineSegment(sketch, "E14845", {"start": v(-1.92, 15.6) * mm, "end": v(-1.97, 15.66) * mm});
            skLineSegment(sketch, "E14846", {"start": v(-1.97, 15.66) * mm, "end": v(-2.06, 15.73) * mm});
            skLineSegment(sketch, "E14847", {"start": v(-2.06, 15.73) * mm, "end": v(-2.14, 15.8) * mm});
            skLineSegment(sketch, "E14848", {"start": v(-2.14, 15.8) * mm, "end": v(-2.18, 15.84) * mm});
            skLineSegment(sketch, "E14849", {"start": v(-2.18, 15.84) * mm, "end": v(-2.22, 15.86) * mm});
            skLineSegment(sketch, "E14850", {"start": v(-2.22, 15.86) * mm, "end": v(-2.27, 15.88) * mm});
            skLineSegment(sketch, "E14851", {"start": v(-2.27, 15.88) * mm, "end": v(-2.33, 15.88) * mm});
            skLineSegment(sketch, "E14852", {"start": v(-2.33, 15.88) * mm, "end": v(-2.4, 15.87) * mm});
            skLineSegment(sketch, "E14853", {"start": v(-2.4, 15.87) * mm, "end": v(-2.48, 15.83) * mm});
            skLineSegment(sketch, "E14854", {"start": v(-2.48, 15.83) * mm, "end": v(-2.56, 15.77) * mm});
            skLineSegment(sketch, "E14855", {"start": v(-2.56, 15.77) * mm, "end": v(-2.66, 15.7) * mm});
            skLineSegment(sketch, "E14856", {"start": v(-2.66, 15.7) * mm, "end": v(-2.88, 15.5) * mm});
            skLineSegment(sketch, "E14857", {"start": v(-2.88, 15.5) * mm, "end": v(-3.12, 15.26) * mm});
            skLineSegment(sketch, "E14858", {"start": v(-3.12, 15.26) * mm, "end": v(-3.38, 15.03) * mm});
            skLineSegment(sketch, "E14859", {"start": v(-3.38, 15.03) * mm, "end": v(-3.51, 14.92) * mm});
            skLineSegment(sketch, "E14860", {"start": v(-3.51, 14.92) * mm, "end": v(-3.64, 14.82) * mm});
            skLineSegment(sketch, "E14861", {"start": v(-3.64, 14.82) * mm, "end": v(-3.78, 14.73) * mm});
            skLineSegment(sketch, "E14862", {"start": v(-3.78, 14.73) * mm, "end": v(-3.91, 14.66) * mm});
            skLineSegment(sketch, "E14863", {"start": v(-3.91, 14.66) * mm, "end": v(-4.04, 14.6) * mm});
            skLineSegment(sketch, "E14864", {"start": v(-4.04, 14.6) * mm, "end": v(-4.17, 14.58) * mm});
            skLineSegment(sketch, "E14865", {"start": v(-4.17, 14.58) * mm, "end": v(-4.25, 14.57) * mm});
            skLineSegment(sketch, "E14866", {"start": v(-4.25, 14.57) * mm, "end": v(-4.34, 14.58) * mm});
            skLineSegment(sketch, "E14867", {"start": v(-4.34, 14.58) * mm, "end": v(-4.42, 14.6) * mm});
            skLineSegment(sketch, "E14868", {"start": v(-4.42, 14.6) * mm, "end": v(-4.5, 14.62) * mm});
            skLineSegment(sketch, "E14869", {"start": v(-4.5, 14.62) * mm, "end": v(-4.67, 14.7) * mm});
            skLineSegment(sketch, "E14870", {"start": v(-4.67, 14.7) * mm, "end": v(-4.84, 14.79) * mm});
            skLineSegment(sketch, "E14871", {"start": v(-4.84, 14.79) * mm, "end": v(-5.17, 15) * mm});
            skLineSegment(sketch, "E14872", {"start": v(-5.17, 15) * mm, "end": v(-5.33, 15.09) * mm});
            skLineSegment(sketch, "E14873", {"start": v(-5.33, 15.09) * mm, "end": v(-5.48, 15.16) * mm});
            skLineSegment(sketch, "E14874", {"start": v(-5.48, 15.16) * mm, "end": v(-4.4, 14.01) * mm});
            skLineSegment(sketch, "E14875", {"start": v(-4.4, 14.01) * mm, "end": v(-3.79, 14.34) * mm});
            skLineSegment(sketch, "E14876", {"start": v(-3.79, 14.34) * mm, "end": v(-3.53, 14.5) * mm});
            skLineSegment(sketch, "E14877", {"start": v(-3.53, 14.5) * mm, "end": v(-3.29, 14.67) * mm});
            skLineSegment(sketch, "E14878", {"start": v(-3.29, 14.67) * mm, "end": v(-3.1, 14.85) * mm});
            skLineSegment(sketch, "E14879", {"start": v(-3.1, 14.85) * mm, "end": v(-3.02, 14.93) * mm});
            skLineSegment(sketch, "E14880", {"start": v(-3.02, 14.93) * mm, "end": v(-2.96, 15) * mm});
            skLineSegment(sketch, "E14881", {"start": v(-2.96, 15) * mm, "end": v(-2.91, 15.07) * mm});
            skLineSegment(sketch, "E14882", {"start": v(-2.91, 15.07) * mm, "end": v(-2.85, 15.13) * mm});
            skLineSegment(sketch, "E14883", {"start": v(-2.85, 15.13) * mm, "end": v(-2.77, 15.19) * mm});
            skLineSegment(sketch, "E14884", {"start": v(-2.77, 15.19) * mm, "end": v(-2.7, 15.24) * mm});
            skLineSegment(sketch, "E14885", {"start": v(-2.7, 15.24) * mm, "end": v(-2.6, 15.28) * mm});
            skLineSegment(sketch, "E14886", {"start": v(-2.6, 15.28) * mm, "end": v(-2.5, 15.31) * mm});
            skLineSegment(sketch, "E14887", {"start": v(-2.5, 15.31) * mm, "end": v(-2.42, 15.33) * mm});
            skLineSegment(sketch, "E14888", {"start": v(-2.42, 15.33) * mm, "end": v(-2.33, 15.33) * mm});
            skLineSegment(sketch, "E14889", {"start": v(-2.33, 15.33) * mm, "end": v(-2.22, 15.31) * mm});
            skLineSegment(sketch, "E14890", {"start": v(-2.22, 15.31) * mm, "end": v(-2.11, 15.29) * mm});
            skLineSegment(sketch, "E14891", {"start": v(-2.11, 15.29) * mm, "end": v(-2, 15.24) * mm});
            skLineSegment(sketch, "E14892", {"start": v(-2, 15.24) * mm, "end": v(-1.96, 15.21) * mm});
            skLineSegment(sketch, "E14893", {"start": v(-1.96, 15.21) * mm, "end": v(-1.93, 15.18) * mm});
            skLineSegment(sketch, "E14894", {"start": v(-1.93, 15.18) * mm, "end": v(-1.86, 15.1) * mm});
            skLineSegment(sketch, "E14895", {"start": v(-1.86, 15.1) * mm, "end": v(-1.78, 14.98) * mm});
            skLineSegment(sketch, "E14896", {"start": v(-1.78, 14.98) * mm, "end": v(-1.6, 14.67) * mm});
            skLineSegment(sketch, "E14897", {"start": v(-1.6, 14.67) * mm, "end": v(-1.42, 14.26) * mm});
            skLineSegment(sketch, "E14898", {"start": v(-1.42, 14.26) * mm, "end": v(-1.22, 13.8) * mm});
            skLineSegment(sketch, "E14899", {"start": v(-1.22, 13.8) * mm, "end": v(-0.8, 12.8) * mm});
            skLineSegment(sketch, "E14900", {"start": v(-0.8, 12.8) * mm, "end": v(-0.61, 12.34) * mm});
            skLineSegment(sketch, "E14901", {"start": v(-0.61, 12.34) * mm, "end": v(-0.43, 11.94) * mm});
            skLineSegment(sketch, "E14902", {"start": v(-0.43, 11.94) * mm, "end": v(-0.71, 11.74) * mm});
            skLineSegment(sketch, "E14903", {"start": v(-0.71, 11.74) * mm, "end": v(-0.79, 11.67) * mm});
            skLineSegment(sketch, "E14904", {"start": v(-0.79, 11.67) * mm, "end": v(-0.9, 11.56) * mm});
            skLineSegment(sketch, "E14905", {"start": v(-0.9, 11.56) * mm, "end": v(-1.18, 11.23) * mm});
            skLineSegment(sketch, "E14906", {"start": v(-1.18, 11.23) * mm, "end": v(-1.53, 10.8) * mm});
            skLineSegment(sketch, "E14907", {"start": v(-1.53, 10.8) * mm, "end": v(-1.91, 10.3) * mm});
            skLineSegment(sketch, "E14908", {"start": v(-1.91, 10.3) * mm, "end": v(-2.83, 9.06) * mm});
            skLineSegment(sketch, "E14909", {"start": v(-2.83, 9.06) * mm, "end": v(-4.54, 9.06) * mm});
            skLineSegment(sketch, "E14910", {"start": v(-4.54, 9.06) * mm, "end": v(-4.15, 12.36) * mm});
            skLineSegment(sketch, "E14911", {"start": v(-4.15, 12.36) * mm, "end": v(-4.65, 12.1) * mm});
            skLineSegment(sketch, "E14912", {"start": v(-4.65, 12.1) * mm, "end": v(-5.17, 11.8) * mm});
            skLineSegment(sketch, "E14913", {"start": v(-5.17, 11.8) * mm, "end": v(-5.44, 11.67) * mm});
            skLineSegment(sketch, "E14914", {"start": v(-5.44, 11.67) * mm, "end": v(-5.7, 11.55) * mm});
            skLineSegment(sketch, "E14915", {"start": v(-5.7, 11.55) * mm, "end": v(-5.97, 11.44) * mm});
            skLineSegment(sketch, "E14916", {"start": v(-5.97, 11.44) * mm, "end": v(-6.23, 11.35) * mm});
            skLineSegment(sketch, "E14917", {"start": v(-6.23, 11.35) * mm, "end": v(-6.5, 11.3) * mm});
            skLineSegment(sketch, "E14918", {"start": v(-6.5, 11.3) * mm, "end": v(-6.82, 11.25) * mm});
            skLineSegment(sketch, "E14919", {"start": v(-6.82, 11.25) * mm, "end": v(-7.41, 11.2) * mm});
            skLineSegment(sketch, "E14920", {"start": v(-7.41, 11.2) * mm, "end": v(-7.78, 11.16) * mm});
            skLineSegment(sketch, "E14921", {"start": v(-7.78, 11.16) * mm, "end": v(-7.87, 11.16) * mm});
            skLineSegment(sketch, "E14922", {"start": v(-7.87, 11.16) * mm, "end": v(-7.95, 11.18) * mm});
            skLineSegment(sketch, "E14923", {"start": v(-7.95, 11.18) * mm, "end": v(-8.03, 11.22) * mm});
            skLineSegment(sketch, "E14924", {"start": v(-8.03, 11.22) * mm, "end": v(-8.1, 11.28) * mm});
            skLineSegment(sketch, "E14925", {"start": v(-8.1, 11.28) * mm, "end": v(-8.16, 11.34) * mm});
            skLineSegment(sketch, "E14926", {"start": v(-8.16, 11.34) * mm, "end": v(-8.22, 11.42) * mm});
            skLineSegment(sketch, "E14927", {"start": v(-8.22, 11.42) * mm, "end": v(-8.28, 11.51) * mm});
            skLineSegment(sketch, "E14928", {"start": v(-8.28, 11.51) * mm, "end": v(-8.32, 11.61) * mm});
            skLineSegment(sketch, "E14929", {"start": v(-8.32, 11.61) * mm, "end": v(-8.36, 11.71) * mm});
            skLineSegment(sketch, "E14930", {"start": v(-8.36, 11.71) * mm, "end": v(-8.4, 11.82) * mm});
            skLineSegment(sketch, "E14931", {"start": v(-8.4, 11.82) * mm, "end": v(-8.42, 11.93) * mm});
            skLineSegment(sketch, "E14932", {"start": v(-8.42, 11.93) * mm, "end": v(-8.44, 12.04) * mm});
            skLineSegment(sketch, "E14933", {"start": v(-8.44, 12.04) * mm, "end": v(-8.44, 12.15) * mm});
            skLineSegment(sketch, "E14934", {"start": v(-8.44, 12.15) * mm, "end": v(-8.44, 12.25) * mm});
            skLineSegment(sketch, "E14935", {"start": v(-8.44, 12.25) * mm, "end": v(-8.43, 12.35) * mm});
            skLineSegment(sketch, "E14936", {"start": v(-8.43, 12.35) * mm, "end": v(-8.41, 12.44) * mm});
            skLineSegment(sketch, "E14937", {"start": v(-8.41, 12.44) * mm, "end": v(-8.34, 12.64) * mm});
            skLineSegment(sketch, "E14938", {"start": v(-8.34, 12.64) * mm, "end": v(-8.25, 12.88) * mm});
            skLineSegment(sketch, "E14939", {"start": v(-8.25, 12.88) * mm, "end": v(-8.14, 13.14) * mm});
            skLineSegment(sketch, "E14940", {"start": v(-8.14, 13.14) * mm, "end": v(-8, 13.42) * mm});
            skLineSegment(sketch, "E14941", {"start": v(-8, 13.42) * mm, "end": v(-7.72, 13.98) * mm});
            skLineSegment(sketch, "E14942", {"start": v(-7.72, 13.98) * mm, "end": v(-7.57, 14.25) * mm});
            skLineSegment(sketch, "E14943", {"start": v(-7.57, 14.25) * mm, "end": v(-7.42, 14.5) * mm});
            skLineSegment(sketch, "E14944", {"start": v(-7.42, 14.5) * mm, "end": v(-6.7, 15.66) * mm});
            skLineSegment(sketch, "E14945", {"start": v(-6.7, 15.66) * mm, "end": v(-6.98, 15.66) * mm});
            skLineSegment(sketch, "E14946", {"start": v(-6.98, 15.66) * mm, "end": v(-7.08, 15.65) * mm});
            skLineSegment(sketch, "E14947", {"start": v(-7.08, 15.65) * mm, "end": v(-7.26, 15.62) * mm});
            skLineSegment(sketch, "E14948", {"start": v(-7.26, 15.62) * mm, "end": v(-7.8, 15.5) * mm});
            skLineSegment(sketch, "E14949", {"start": v(-7.8, 15.5) * mm, "end": v(-8.14, 15.41) * mm});
            skLineSegment(sketch, "E14950", {"start": v(-8.14, 15.41) * mm, "end": v(-8.52, 15.3) * mm});
            skLineSegment(sketch, "E14951", {"start": v(-8.52, 15.3) * mm, "end": v(-8.93, 15.18) * mm});
            skLineSegment(sketch, "E14952", {"start": v(-8.93, 15.18) * mm, "end": v(-9.35, 15.04) * mm});
            skLineSegment(sketch, "E14953", {"start": v(-9.35, 15.04) * mm, "end": v(-9.83, 14.85) * mm});
            skLineSegment(sketch, "E14954", {"start": v(-9.83, 14.85) * mm, "end": v(-10.34, 14.62) * mm});
            skLineSegment(sketch, "E14955", {"start": v(-10.34, 14.62) * mm, "end": v(-10.86, 14.39) * mm});
            skLineSegment(sketch, "E14956", {"start": v(-10.86, 14.39) * mm, "end": v(-11.1, 14.28) * mm});
            skLineSegment(sketch, "E14957", {"start": v(-11.1, 14.28) * mm, "end": v(-11.34, 14.2) * mm});
            skLineSegment(sketch, "E14958", {"start": v(-11.34, 14.2) * mm, "end": v(-11.7, 14.64) * mm});
            skLineSegment(sketch, "E14959", {"start": v(-11.7, 14.64) * mm, "end": v(-11.68, 14.82) * mm});
            skLineSegment(sketch, "E14960", {"start": v(-11.68, 14.82) * mm, "end": v(-11.64, 15) * mm});
            skLineSegment(sketch, "E14961", {"start": v(-11.64, 15) * mm, "end": v(-11.55, 15.33) * mm});
            skLineSegment(sketch, "E14962", {"start": v(-11.55, 15.33) * mm, "end": v(-11.48, 15.5) * mm});
            skLineSegment(sketch, "E14963", {"start": v(-11.48, 15.5) * mm, "end": v(-11.38, 15.69) * mm});
            skLineSegment(sketch, "E14964", {"start": v(-11.38, 15.69) * mm, "end": v(-11.25, 15.91) * mm});
            skLineSegment(sketch, "E14965", {"start": v(-11.25, 15.91) * mm, "end": v(-11.1, 16.16) * mm});
            skLineSegment(sketch, "E14966", {"start": v(-11.1, 16.16) * mm, "end": v(-10.92, 16.41) * mm});
            skLineSegment(sketch, "E14967", {"start": v(-10.92, 16.41) * mm, "end": v(-10.73, 16.67) * mm});
            skLineSegment(sketch, "E14968", {"start": v(-10.73, 16.67) * mm, "end": v(-10.53, 16.92) * mm});
            skLineSegment(sketch, "E14969", {"start": v(-10.53, 16.92) * mm, "end": v(-10.33, 17.17) * mm});
            skLineSegment(sketch, "E14970", {"start": v(-10.33, 17.17) * mm, "end": v(-9.33, 18.3) * mm});
            skLineSegment(sketch, "E14971", {"start": v(-9.33, 18.3) * mm, "end": v(-9.65, 18.3) * mm});
            skLineSegment(sketch, "E14972", {"start": v(-9.65, 18.3) * mm, "end": v(-9.76, 18.31) * mm});
            skLineSegment(sketch, "E14973", {"start": v(-9.76, 18.31) * mm, "end": v(-9.87, 18.36) * mm});
            skLineSegment(sketch, "E14974", {"start": v(-9.87, 18.36) * mm, "end": v(-9.98, 18.42) * mm});
            skLineSegment(sketch, "E14975", {"start": v(-9.98, 18.42) * mm, "end": v(-10.1, 18.51) * mm});
            skLineSegment(sketch, "E14976", {"start": v(-10.1, 18.51) * mm, "end": v(-10.2, 18.62) * mm});
            skLineSegment(sketch, "E14977", {"start": v(-10.2, 18.62) * mm, "end": v(-10.3, 18.74) * mm});
            skLineSegment(sketch, "E14978", {"start": v(-10.3, 18.74) * mm, "end": v(-10.39, 18.86) * mm});
            skLineSegment(sketch, "E14979", {"start": v(-10.39, 18.86) * mm, "end": v(-10.47, 19) * mm});
            skLineSegment(sketch, "E14980", {"start": v(-10.47, 19) * mm, "end": v(-10.53, 19.13) * mm});
            skLineSegment(sketch, "E14981", {"start": v(-10.53, 19.13) * mm, "end": v(-10.58, 19.26) * mm});
            skLineSegment(sketch, "E14982", {"start": v(-10.58, 19.26) * mm, "end": v(-10.62, 19.39) * mm});
            skLineSegment(sketch, "E14983", {"start": v(-10.62, 19.39) * mm, "end": v(-10.63, 19.5) * mm});
            skLineSegment(sketch, "E14984", {"start": v(-10.63, 19.5) * mm, "end": v(-10.62, 19.6) * mm});
            skLineSegment(sketch, "E14985", {"start": v(-10.62, 19.6) * mm, "end": v(-10.6, 19.66) * mm});
            skLineSegment(sketch, "E14986", {"start": v(-10.6, 19.66) * mm, "end": v(-10.59, 19.7) * mm});
            skLineSegment(sketch, "E14987", {"start": v(-10.59, 19.7) * mm, "end": v(-10.56, 19.73) * mm});
            skLineSegment(sketch, "E14988", {"start": v(-10.56, 19.73) * mm, "end": v(-10.53, 19.76) * mm});
            skLineSegment(sketch, "E14989", {"start": v(-10.53, 19.76) * mm, "end": v(-10.49, 19.79) * mm});
            skLineSegment(sketch, "E14990", {"start": v(-10.49, 19.79) * mm, "end": v(-10.44, 19.8) * mm});
            skLineSegment(sketch, "E14991.bottom", {"start": v(-105.05, 79.47) * mm, "end": v(105.05, 79.47) * mm});
            skLineSegment(sketch, "E14991.top", {"start": v(-105.05, -79.47) * mm, "end": v(105.05, -79.47) * mm});
            skLineSegment(sketch, "E14991.left", {"start": v(-105.05, 79.47) * mm, "end": v(-105.05, -79.47) * mm});
            skLineSegment(sketch, "E14991.right", {"start": v(105.05, 79.47) * mm, "end": v(105.05, -79.47) * mm});
            skPoint(sketch, "E14991.middle", {"position": v(0, 0) * mm});
            skSolve(sketch);
        }
        {
            var Q0;
            Q0=makeQuery(id+"F0.imprint","IMPRINT",FACE,{"disambiguationData":[TD([[makeQuery(id+"F0.imprint","IMPRINT",EDGE,{"derivedFrom":sQuery(id+"F0.wireOp",EDGE,"E0")}),-1.0]])]});
            var Q1;
            Q1=makeQuery(id+"F0.imprint","IMPRINT",FACE,{"disambiguationData":[TD([[makeQuery(id+"F0.imprint","IMPRINT",EDGE,{"derivedFrom":sQuery(id+"F0.wireOp",EDGE,"E138")}),-1.0]])]});
            var Q2;
            Q2=makeQuery(id+"F0.imprint","IMPRINT",FACE,{"disambiguationData":[TD([[makeQuery(id+"F0.imprint","IMPRINT",EDGE,{"derivedFrom":sQuery(id+"F0.wireOp",EDGE,"E276")}),1.0]])]});
            var Q3;
            Q3=makeQuery(id+"F0.imprint","IMPRINT",FACE,{"disambiguationData":[TD([[makeQuery(id+"F0.imprint","IMPRINT",EDGE,{"derivedFrom":sQuery(id+"F0.wireOp",EDGE,"E500")}),1.0]])]});
            extrude(context, id + "F1", {"entities" : qUnion([Q0, Q1, Q2, Q3]), "depth" : 25.4 * mm});
        }
        {
            var Q0;
            Q0=makeQuery(id+"F0.imprint","IMPRINT",FACE,{"disambiguationData":[TD([[makeQuery(id+"F0.imprint","IMPRINT",EDGE,{"derivedFrom":sQuery(id+"F0.wireOp",EDGE,"E5680")}),-1.0]])]});
            var Q1;
            Q1=makeQuery(id+"F0.imprint","IMPRINT",FACE,{"disambiguationData":[TD([[makeQuery(id+"F0.imprint","IMPRINT",EDGE,{"derivedFrom":sQuery(id+"F0.wireOp",EDGE,"E4484")}),1.0]])]});
            var Q2;
            Q2=makeQuery(id+"F0.imprint","IMPRINT",FACE,{"disambiguationData":[TD([[makeQuery(id+"F0.imprint","IMPRINT",EDGE,{"derivedFrom":sQuery(id+"F0.wireOp",EDGE,"E4031")}),1.0]])]});
            var Q3;
            Q3=makeQuery(id+"F0.imprint","IMPRINT",FACE,{"disambiguationData":[TD([[makeQuery(id+"F0.imprint","IMPRINT",EDGE,{"derivedFrom":sQuery(id+"F0.wireOp",EDGE,"E3684")}),1.0]])]});
            var Q4;
            Q4=makeQuery(id+"F0.imprint","IMPRINT",FACE,{"disambiguationData":[TD([[makeQuery(id+"F0.imprint","IMPRINT",EDGE,{"derivedFrom":sQuery(id+"F0.wireOp",EDGE,"E3106")}),1.0]])]});
            var Q5;
            Q5=makeQuery(id+"F0.imprint","IMPRINT",FACE,{"disambiguationData":[TD([[makeQuery(id+"F0.imprint","IMPRINT",EDGE,{"derivedFrom":sQuery(id+"F0.wireOp",EDGE,"E2790")}),1.0]])]});
            var Q6;
            Q6=makeQuery(id+"F0.imprint","IMPRINT",FACE,{"disambiguationData":[TD([[makeQuery(id+"F0.imprint","IMPRINT",EDGE,{"derivedFrom":sQuery(id+"F0.wireOp",EDGE,"E1761")}),1.0]])]});
            var Q7;
            Q7=makeQuery(id+"F0.imprint","IMPRINT",FACE,{"disambiguationData":[TD([[makeQuery(id+"F0.imprint","IMPRINT",EDGE,{"derivedFrom":sQuery(id+"F0.wireOp",EDGE,"E4674")}),1.0]])]});
            var Q8;
            Q8=makeQuery(id+"F0.imprint","IMPRINT",FACE,{"disambiguationData":[TD([[makeQuery(id+"F0.imprint","IMPRINT",EDGE,{"derivedFrom":sQuery(id+"F0.wireOp",EDGE,"E570")}),1.0]])]});
            var Q9;
            Q9=makeQuery(id+"F0.imprint","IMPRINT",FACE,{"disambiguationData":[TD([[makeQuery(id+"F0.imprint","IMPRINT",EDGE,{"derivedFrom":sQuery(id+"F0.wireOp",EDGE,"E0")}),1.0]])]});
            var Q10;
            Q10=makeQuery(id+"F0.imprint","IMPRINT",FACE,{"disambiguationData":[TD([[makeQuery(id+"F0.imprint","IMPRINT",EDGE,{"derivedFrom":sQuery(id+"F0.wireOp",EDGE,"E858")}),1.0]])]});
            var Q11;
            Q11=makeQuery(id+"F0.imprint","IMPRINT",FACE,{"disambiguationData":[TD([[makeQuery(id+"F0.imprint","IMPRINT",EDGE,{"derivedFrom":sQuery(id+"F0.wireOp",EDGE,"E1271")}),1.0]])]});
            var Q12;
            Q12=makeQuery(id+"F0.imprint","IMPRINT",FACE,{"disambiguationData":[TD([[makeQuery(id+"F0.imprint","IMPRINT",EDGE,{"derivedFrom":sQuery(id+"F0.wireOp",EDGE,"E1904")}),1.0]])]});
            var Q13;
            Q13=makeQuery(id+"F0.imprint","IMPRINT",FACE,{"disambiguationData":[TD([[makeQuery(id+"F0.imprint","IMPRINT",EDGE,{"derivedFrom":sQuery(id+"F0.wireOp",EDGE,"E2663")}),1.0]])]});
            var Q14;
            Q14=makeQuery(id+"F0.imprint","IMPRINT",FACE,{"disambiguationData":[TD([[makeQuery(id+"F0.imprint","IMPRINT",EDGE,{"derivedFrom":sQuery(id+"F0.wireOp",EDGE,"E3327")}),1.0]])]});
            var Q15;
            Q15=makeQuery(id+"F0.imprint","IMPRINT",FACE,{"disambiguationData":[TD([[makeQuery(id+"F0.imprint","IMPRINT",EDGE,{"derivedFrom":sQuery(id+"F0.wireOp",EDGE,"E3933")}),1.0]])]});
            var Q16;
            Q16=makeQuery(id+"F0.imprint","IMPRINT",FACE,{"disambiguationData":[TD([[makeQuery(id+"F0.imprint","IMPRINT",EDGE,{"derivedFrom":sQuery(id+"F0.wireOp",EDGE,"E4301")}),1.0]])]});
            extrude(context, id + "F2", {"entities" : qUnion([Q0, Q1, Q2, Q3, Q4, Q5, Q6, Q7, Q8, Q9, Q10, Q11, Q12, Q13, Q14, Q15, Q16]), "operationType" : NewBodyOperationType.ADD, "oppositeDirection" : true, "depth" : 31.75 * mm});
        }
        {
            var Q0;
            Q0=makeQuery(id+"F0.imprint","IMPRINT",FACE,{"disambiguationData":[TD([[makeQuery(id+"F0.imprint","IMPRINT",EDGE,{"derivedFrom":sQuery(id+"F0.wireOp",EDGE,"E8051")}),1.0]])]});
            var Q1;
            Q1=makeQuery(id+"F0.imprint","IMPRINT",FACE,{"disambiguationData":[TD([[makeQuery(id+"F0.imprint","IMPRINT",EDGE,{"derivedFrom":sQuery(id+"F0.wireOp",EDGE,"E7931")}),1.0]])]});
            var Q2;
            Q2=makeQuery(id+"F0.imprint","IMPRINT",FACE,{"disambiguationData":[TD([[makeQuery(id+"F0.imprint","IMPRINT",EDGE,{"derivedFrom":sQuery(id+"F0.wireOp",EDGE,"E7786")}),-1.0]])]});
            var Q3;
            Q3=makeQuery(id+"F0.imprint","IMPRINT",FACE,{"disambiguationData":[TD([[makeQuery(id+"F0.imprint","IMPRINT",EDGE,{"derivedFrom":sQuery(id+"F0.wireOp",EDGE,"E7667")}),-1.0]])]});
            var Q4;
            {var subQ0=sQuery(id+"F0.wireOp",EDGE,"E10079");Q4=makeQuery(id+"F0.imprint","IMPRINT",FACE,{"disambiguationData":[TD([[makeQuery(id+"F0.imprint","IMPRINT",EDGE,{"derivedFrom":subQ0}),1.0]])]});}
            var Q5;
            Q5=makeQuery(id+"F0.imprint","IMPRINT",FACE,{"disambiguationData":[TD([[makeQuery(id+"F0.imprint","IMPRINT",EDGE,{"derivedFrom":sQuery(id+"F0.wireOp",EDGE,"E7583")}),1.0]])]});
            var Q6;
            Q6=makeQuery(id+"F0.imprint","IMPRINT",FACE,{"disambiguationData":[TD([[makeQuery(id+"F0.imprint","IMPRINT",EDGE,{"derivedFrom":sQuery(id+"F0.wireOp",EDGE,"E4904")}),1.0]])]});
            extrude(context, id + "F3", {"entities" : qUnion([Q0, Q1, Q2, Q3, Q4, Q5, Q6]), "operationType" : NewBodyOperationType.ADD, "oppositeDirection" : true, "depth" : 19.05 * mm});
        }
    });
